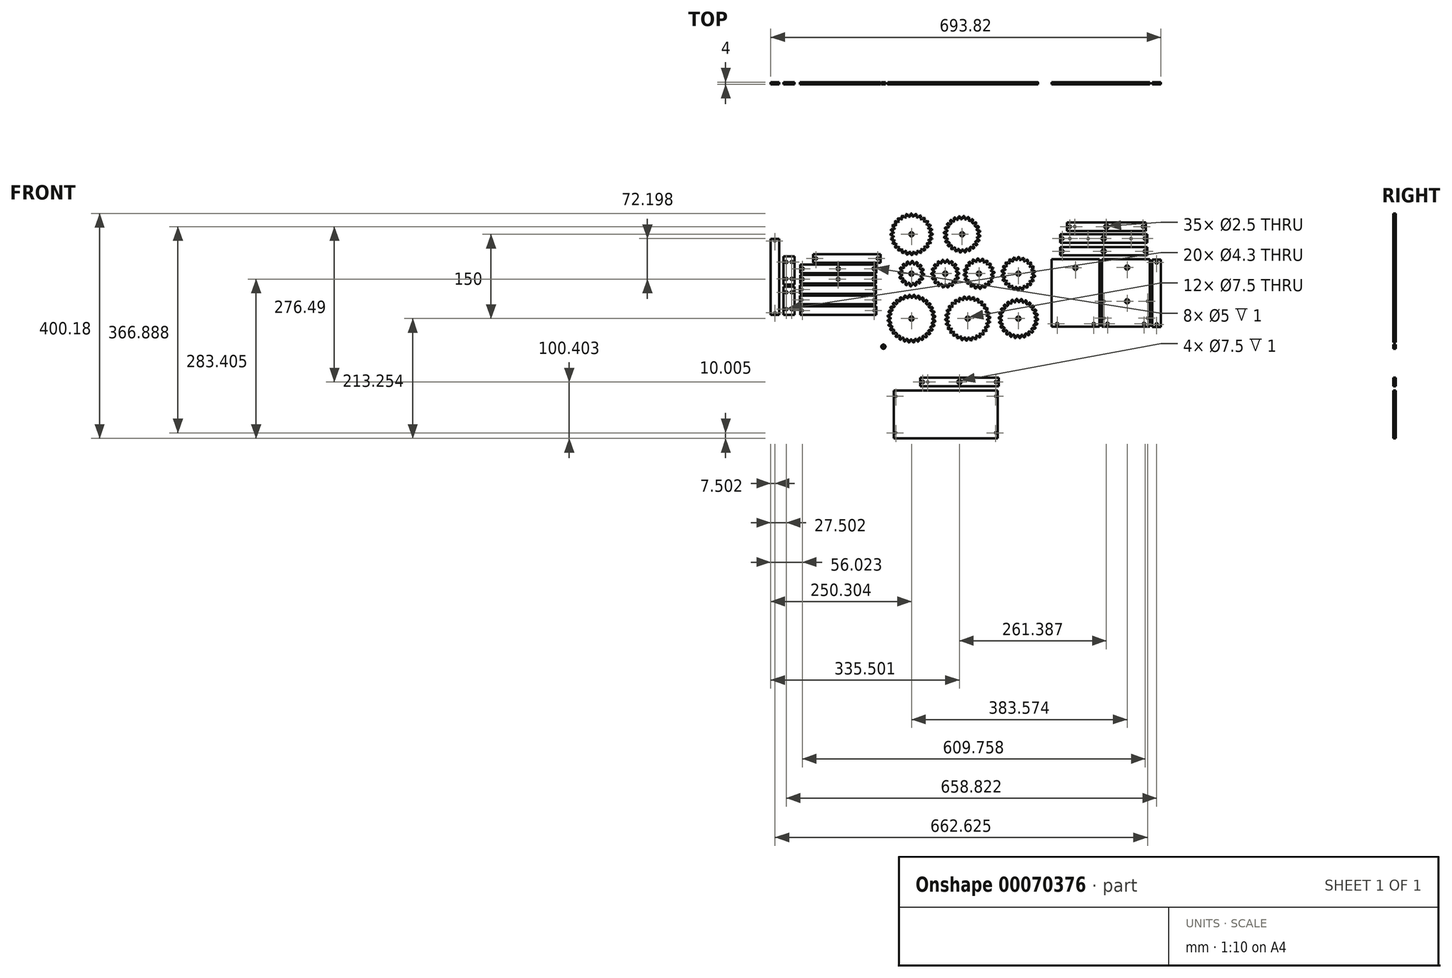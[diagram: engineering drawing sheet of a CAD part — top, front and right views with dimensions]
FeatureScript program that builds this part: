
annotation { "Feature Type Name" : "Feature", "Feature Type Description" : "" }
export const myFeature = defineFeature(function(context is Context, id is Id, definition is map)
    precondition{}
    {
        {
            var Q0;
            Q0=qCreatedBy(makeId("Front.planeOp"),FACE);
            var sketch = newSketch(context, id + "F0", { "sketchPlane" : qUnion([Q0])});
            skLineSegment(sketch, "E0", {"start": v(-125.86, -279.84) * mm, "end": v(59.14, -279.84) * mm});
            skLineSegment(sketch, "E1", {"start": v(59.14, -279.84) * mm, "end": v(59.14, -194.84) * mm});
            skLineSegment(sketch, "E2", {"start": v(59.14, -194.84) * mm, "end": v(-125.86, -194.84) * mm});
            skLineSegment(sketch, "E3", {"start": v(-125.86, -194.84) * mm, "end": v(-125.86, -279.84) * mm});
            skLineSegment(sketch, "E4", {"start": v(-79, -171.94) * mm, "end": v(-79, -186.94) * mm});
            skLineSegment(sketch, "E5", {"start": v(-79, -186.94) * mm, "end": v(61, -186.94) * mm});
            skLineSegment(sketch, "E6", {"start": v(61, -186.94) * mm, "end": v(61, -171.94) * mm});
            skLineSegment(sketch, "E7", {"start": v(61, -171.94) * mm, "end": v(-79, -171.94) * mm});
            skLineSegment(sketch, "E8", {"start": v(-122.1, -204.84) * mm, "end": v(-122.1, -269.84) * mm, "construction": true});
            skLineSegment(sketch, "E9", {"start": v(-122.1, -204.84) * mm, "end": v(55.4, -204.84) * mm, "construction": true});
            skLineSegment(sketch, "E10", {"start": v(55.4, -204.84) * mm, "end": v(55.4, -269.84) * mm, "construction": true});
            skLineSegment(sketch, "E11", {"start": v(55.4, -269.84) * mm, "end": v(-122.1, -269.84) * mm, "construction": true});
            skCircle(sketch, "E12", {"center": v(-122.1, -204.84) * mm, "radius": 1.25 * mm});
            skCircle(sketch, "E13", {"center": v(55.4, -204.84) * mm, "radius": 1.25 * mm});
            skCircle(sketch, "E14", {"center": v(-122.1, -269.84) * mm, "radius": 1.25 * mm});
            skCircle(sketch, "E15", {"center": v(55.4, -269.84) * mm, "radius": 1.25 * mm});
            skLineSegment(sketch, "E16", {"start": v(-74, -179.44) * mm, "end": v(-65.25, -179.44) * mm, "construction": true});
            skCircle(sketch, "E17", {"center": v(-74, -179.44) * mm, "radius": 2.15 * mm});
            skCircle(sketch, "E18", {"center": v(-65.25, -179.44) * mm, "radius": 1.25 * mm});
            skCircle(sketch, "E19", {"center": v(-9, -179.44) * mm, "radius": 1.25 * mm});
            skCircle(sketch, "E20", {"center": v(-9, -179.44) * mm, "radius": 3.75 * mm});
            skCircle(sketch, "E21", {"center": v(56, -179.44) * mm, "radius": 2.15 * mm});
            skLineSegment(sketch, "E22", {"start": v(-74, -179.44) * mm, "end": v(56, -179.44) * mm, "construction": true});
            skSolve(sketch);
        }
        {
            var Q0;
            Q0=makeQuery(id+"F0.imprint","IMPRINT",FACE,{"disambiguationData":[TD([[makeQuery(id+"F0.imprint","IMPRINT",EDGE,{"derivedFrom":sQuery(id+"F0.wireOp",EDGE,"E0")}),1.0]])]});
            var Q1;
            Q1=makeQuery(id+"F0.imprint","IMPRINT",FACE,{"disambiguationData":[TD([[makeQuery(id+"F0.imprint","IMPRINT",EDGE,{"derivedFrom":sQuery(id+"F0.wireOp",EDGE,"E4")}),1.0]])]});
            extrude(context, id + "F1", {"entities" : qUnion([Q0, Q1]), "depth" : 4 * mm});
        }
        {
            var Q0;
            Q0=makeQuery(id+"F0.imprint","IMPRINT",FACE,{"disambiguationData":[TD([[makeQuery(id+"F0.imprint","IMPRINT",EDGE,{"derivedFrom":sQuery(id+"F0.wireOp",EDGE,"E19")}),-1.0]])]});
            extrude(context, id + "F2", {"entities" : qUnion([Q0]), "operationType" : NewBodyOperationType.ADD, "depth" : 3 * mm});
        }
        {
            var Q0;
            Q0=qCreatedBy(makeId("Front.planeOp"),FACE);
            var sketch = newSketch(context, id + "F3", { "sketchPlane" : qUnion([Q0])});
            skLineSegment(sketch, "E23", {"start": v(-50.97, 12.48) * mm, "end": v(-50.97, 12.61) * mm});
            skLineSegment(sketch, "E24", {"start": v(-50.97, 12.61) * mm, "end": v(-50.98, 12.74) * mm});
            skLineSegment(sketch, "E25", {"start": v(-50.98, 12.74) * mm, "end": v(-50.99, 12.87) * mm});
            skLineSegment(sketch, "E26", {"start": v(-50.99, 12.87) * mm, "end": v(-51, 13) * mm});
            skLineSegment(sketch, "E27", {"start": v(-51, 13) * mm, "end": v(-51.02, 13.13) * mm});
            skLineSegment(sketch, "E28", {"start": v(-51.02, 13.13) * mm, "end": v(-51.05, 13.26) * mm});
            skLineSegment(sketch, "E29", {"start": v(-51.05, 13.26) * mm, "end": v(-51.08, 13.38) * mm});
            skLineSegment(sketch, "E30", {"start": v(-51.08, 13.38) * mm, "end": v(-51.1, 13.51) * mm});
            skLineSegment(sketch, "E31", {"start": v(-51.1, 13.51) * mm, "end": v(-51.15, 13.63) * mm});
            skLineSegment(sketch, "E32", {"start": v(-51.15, 13.63) * mm, "end": v(-51.19, 13.76) * mm});
            skLineSegment(sketch, "E33", {"start": v(-51.24, 13.88) * mm, "end": v(-51.29, 14) * mm});
            skLineSegment(sketch, "E34", {"start": v(-51.29, 14) * mm, "end": v(-51.34, 14.12) * mm});
            skLineSegment(sketch, "E35", {"start": v(-51.34, 14.12) * mm, "end": v(-51.4, 14.23) * mm});
            skLineSegment(sketch, "E36", {"start": v(-51.4, 14.23) * mm, "end": v(-51.46, 14.35) * mm});
            skLineSegment(sketch, "E37", {"start": v(-51.46, 14.35) * mm, "end": v(-51.53, 14.46) * mm});
            skLineSegment(sketch, "E38", {"start": v(-51.53, 14.46) * mm, "end": v(-51.6, 14.57) * mm});
            skLineSegment(sketch, "E39", {"start": v(-51.67, 14.68) * mm, "end": v(-51.75, 14.78) * mm});
            skLineSegment(sketch, "E40", {"start": v(-51.75, 14.78) * mm, "end": v(-51.83, 14.88) * mm});
            skLineSegment(sketch, "E41", {"start": v(-51.83, 14.88) * mm, "end": v(-51.92, 14.98) * mm});
            skLineSegment(sketch, "E42", {"start": v(-51.92, 14.98) * mm, "end": v(-52, 15.08) * mm});
            skLineSegment(sketch, "E43", {"start": v(-52, 15.08) * mm, "end": v(-52.1, 15.17) * mm});
            skLineSegment(sketch, "E44", {"start": v(-52.1, 15.17) * mm, "end": v(-52.2, 15.26) * mm});
            skLineSegment(sketch, "E45", {"start": v(-52.2, 15.26) * mm, "end": v(-52.3, 15.34) * mm});
            skLineSegment(sketch, "E46", {"start": v(-52.3, 15.34) * mm, "end": v(-52.4, 15.43) * mm});
            skLineSegment(sketch, "E47", {"start": v(-52.4, 15.43) * mm, "end": v(-52.5, 15.5) * mm});
            skLineSegment(sketch, "E48", {"start": v(-52.71, 15.65) * mm, "end": v(-52.82, 15.72) * mm});
            skLineSegment(sketch, "E49", {"start": v(-52.82, 15.72) * mm, "end": v(-52.94, 15.78) * mm});
            skLineSegment(sketch, "E50", {"start": v(-52.94, 15.78) * mm, "end": v(-53.05, 15.84) * mm});
            skLineSegment(sketch, "E51", {"start": v(-53.05, 15.84) * mm, "end": v(-53.17, 15.9) * mm});
            skLineSegment(sketch, "E52", {"start": v(-53.17, 15.9) * mm, "end": v(-53.29, 15.95) * mm});
            skLineSegment(sketch, "E53", {"start": v(-53.4, 16) * mm, "end": v(-53.53, 16.04) * mm});
            skLineSegment(sketch, "E54", {"start": v(-53.53, 16.04) * mm, "end": v(-53.66, 16.08) * mm});
            skLineSegment(sketch, "E55", {"start": v(-54.04, 16.17) * mm, "end": v(-54.16, 16.2) * mm});
            skLineSegment(sketch, "E56", {"start": v(-54.42, 16.22) * mm, "end": v(-54.55, 16.23) * mm});
            skLineSegment(sketch, "E57", {"start": v(-54.55, 16.23) * mm, "end": v(-54.68, 16.23) * mm});
            skLineSegment(sketch, "E58", {"start": v(-54.68, 16.23) * mm, "end": v(-54.81, 16.23) * mm});
            skLineSegment(sketch, "E59", {"start": v(-54.81, 16.23) * mm, "end": v(-54.94, 16.23) * mm});
            skLineSegment(sketch, "E60", {"start": v(-54.94, 16.23) * mm, "end": v(-55.07, 16.22) * mm});
            skLineSegment(sketch, "E61", {"start": v(-55.07, 16.22) * mm, "end": v(-55.2, 16.2) * mm});
            skLineSegment(sketch, "E62", {"start": v(-55.2, 16.2) * mm, "end": v(-55.33, 16.18) * mm});
            skLineSegment(sketch, "E63", {"start": v(-55.33, 16.18) * mm, "end": v(-55.46, 16.16) * mm});
            skLineSegment(sketch, "E64", {"start": v(-55.46, 16.16) * mm, "end": v(-55.59, 16.13) * mm});
            skLineSegment(sketch, "E65", {"start": v(-55.59, 16.13) * mm, "end": v(-55.71, 16.1) * mm});
            skLineSegment(sketch, "E66", {"start": v(-55.71, 16.1) * mm, "end": v(-55.84, 16.06) * mm});
            skLineSegment(sketch, "E67", {"start": v(-55.84, 16.06) * mm, "end": v(-55.96, 16.02) * mm});
            skLineSegment(sketch, "E68", {"start": v(-55.96, 16.02) * mm, "end": v(-56.08, 15.97) * mm});
            skLineSegment(sketch, "E69", {"start": v(-56.2, 15.92) * mm, "end": v(-56.32, 15.87) * mm});
            skLineSegment(sketch, "E70", {"start": v(-56.44, 15.81) * mm, "end": v(-56.55, 15.75) * mm});
            skLineSegment(sketch, "E71", {"start": v(-56.55, 15.75) * mm, "end": v(-56.67, 15.69) * mm});
            skLineSegment(sketch, "E72", {"start": v(-56.78, 15.62) * mm, "end": v(-56.88, 15.54) * mm});
            skLineSegment(sketch, "E73", {"start": v(-56.88, 15.54) * mm, "end": v(-56.99, 15.47) * mm});
            skLineSegment(sketch, "E74", {"start": v(-56.99, 15.47) * mm, "end": v(-57.1, 15.39) * mm});
            skLineSegment(sketch, "E75", {"start": v(-57.1, 15.39) * mm, "end": v(-57.19, 15.3) * mm});
            skLineSegment(sketch, "E76", {"start": v(-57.38, 15.12) * mm, "end": v(-57.47, 15.03) * mm});
            skLineSegment(sketch, "E77", {"start": v(-57.47, 15.03) * mm, "end": v(-57.56, 14.93) * mm});
            skLineSegment(sketch, "E78", {"start": v(-57.72, 14.73) * mm, "end": v(-57.8, 14.62) * mm});
            skLineSegment(sketch, "E79", {"start": v(-57.8, 14.62) * mm, "end": v(-57.87, 14.51) * mm});
            skLineSegment(sketch, "E80", {"start": v(-57.94, 14.4) * mm, "end": v(-58, 14.3) * mm});
            skLineSegment(sketch, "E81", {"start": v(-58, 14.3) * mm, "end": v(-58.06, 14.18) * mm});
            skLineSegment(sketch, "E82", {"start": v(-58.12, 14.06) * mm, "end": v(-58.17, 13.94) * mm});
            skLineSegment(sketch, "E83", {"start": v(-58.17, 13.94) * mm, "end": v(-58.22, 13.82) * mm});
            skLineSegment(sketch, "E84", {"start": v(-58.26, 13.7) * mm, "end": v(-58.3, 13.57) * mm});
            skLineSegment(sketch, "E85", {"start": v(-58.3, 13.57) * mm, "end": v(-58.34, 13.45) * mm});
            skLineSegment(sketch, "E86", {"start": v(-58.34, 13.45) * mm, "end": v(-58.37, 13.32) * mm});
            skLineSegment(sketch, "E87", {"start": v(-58.37, 13.32) * mm, "end": v(-58.4, 13.2) * mm});
            skLineSegment(sketch, "E88", {"start": v(-58.4, 13.2) * mm, "end": v(-58.42, 13.07) * mm});
            skLineSegment(sketch, "E89", {"start": v(-58.42, 13.07) * mm, "end": v(-58.44, 12.94) * mm});
            skLineSegment(sketch, "E90", {"start": v(-58.44, 12.94) * mm, "end": v(-58.45, 12.8) * mm});
            skLineSegment(sketch, "E91", {"start": v(-58.45, 12.8) * mm, "end": v(-58.46, 12.68) * mm});
            skLineSegment(sketch, "E92", {"start": v(-58.44, 12.03) * mm, "end": v(-58.42, 11.9) * mm});
            skLineSegment(sketch, "E93", {"start": v(-58.37, 11.64) * mm, "end": v(-58.34, 11.52) * mm});
            skLineSegment(sketch, "E94", {"start": v(-58.34, 11.52) * mm, "end": v(-58.3, 11.4) * mm});
            skLineSegment(sketch, "E95", {"start": v(-58.3, 11.4) * mm, "end": v(-58.26, 11.27) * mm});
            skLineSegment(sketch, "E96", {"start": v(-58.26, 11.27) * mm, "end": v(-58.22, 11.15) * mm});
            skLineSegment(sketch, "E97", {"start": v(-58.17, 11.02) * mm, "end": v(-58.12, 10.9) * mm});
            skLineSegment(sketch, "E98", {"start": v(-58.12, 10.9) * mm, "end": v(-58.06, 10.79) * mm});
            skLineSegment(sketch, "E99", {"start": v(-58.06, 10.79) * mm, "end": v(-58, 10.67) * mm});
            skLineSegment(sketch, "E100", {"start": v(-58, 10.67) * mm, "end": v(-57.94, 10.56) * mm});
            skLineSegment(sketch, "E101", {"start": v(-57.8, 10.34) * mm, "end": v(-57.72, 10.24) * mm});
            skLineSegment(sketch, "E102", {"start": v(-57.72, 10.24) * mm, "end": v(-57.64, 10.13) * mm});
            skLineSegment(sketch, "E103", {"start": v(-57.64, 10.13) * mm, "end": v(-57.56, 10.03) * mm});
            skLineSegment(sketch, "E104", {"start": v(-57.56, 10.03) * mm, "end": v(-57.47, 9.94) * mm});
            skLineSegment(sketch, "E105", {"start": v(-57.47, 9.94) * mm, "end": v(-57.38, 9.84) * mm});
            skLineSegment(sketch, "E106", {"start": v(-57.38, 9.84) * mm, "end": v(-57.29, 9.75) * mm});
            skLineSegment(sketch, "E107", {"start": v(-57.29, 9.75) * mm, "end": v(-57.19, 9.66) * mm});
            skLineSegment(sketch, "E108", {"start": v(-57.19, 9.66) * mm, "end": v(-57.1, 9.58) * mm});
            skLineSegment(sketch, "E109", {"start": v(-57.1, 9.58) * mm, "end": v(-56.99, 9.5) * mm});
            skLineSegment(sketch, "E110", {"start": v(-56.99, 9.5) * mm, "end": v(-56.88, 9.42) * mm});
            skLineSegment(sketch, "E111", {"start": v(-56.55, 9.21) * mm, "end": v(-56.44, 9.15) * mm});
            skLineSegment(sketch, "E112", {"start": v(-56.44, 9.15) * mm, "end": v(-56.32, 9.1) * mm});
            skLineSegment(sketch, "E113", {"start": v(-56.32, 9.1) * mm, "end": v(-56.2, 9.04) * mm});
            skLineSegment(sketch, "E114", {"start": v(-56.2, 9.04) * mm, "end": v(-56.08, 9) * mm});
            skLineSegment(sketch, "E115", {"start": v(-55.96, 8.95) * mm, "end": v(-55.84, 8.9) * mm});
            skLineSegment(sketch, "E116", {"start": v(-55.71, 8.87) * mm, "end": v(-55.59, 8.83) * mm});
            skLineSegment(sketch, "E117", {"start": v(-55.59, 8.83) * mm, "end": v(-55.46, 8.8) * mm});
            skLineSegment(sketch, "E118", {"start": v(-55.46, 8.8) * mm, "end": v(-55.33, 8.78) * mm});
            skLineSegment(sketch, "E119", {"start": v(-55.33, 8.78) * mm, "end": v(-55.2, 8.76) * mm});
            skLineSegment(sketch, "E120", {"start": v(-55.2, 8.76) * mm, "end": v(-55.07, 8.75) * mm});
            skLineSegment(sketch, "E121", {"start": v(-55.07, 8.75) * mm, "end": v(-54.94, 8.74) * mm});
            skLineSegment(sketch, "E122", {"start": v(-54.94, 8.74) * mm, "end": v(-54.81, 8.73) * mm});
            skLineSegment(sketch, "E123", {"start": v(-54.81, 8.73) * mm, "end": v(-54.68, 8.73) * mm});
            skLineSegment(sketch, "E124", {"start": v(-54.68, 8.73) * mm, "end": v(-54.55, 8.74) * mm});
            skLineSegment(sketch, "E125", {"start": v(-54.55, 8.74) * mm, "end": v(-54.42, 8.74) * mm});
            skLineSegment(sketch, "E126", {"start": v(-54.16, 8.77) * mm, "end": v(-54.04, 8.8) * mm});
            skLineSegment(sketch, "E127", {"start": v(-53.9, 8.82) * mm, "end": v(-53.78, 8.85) * mm});
            skLineSegment(sketch, "E128", {"start": v(-53.78, 8.85) * mm, "end": v(-53.66, 8.89) * mm});
            skLineSegment(sketch, "E129", {"start": v(-53.66, 8.89) * mm, "end": v(-53.53, 8.92) * mm});
            skLineSegment(sketch, "E130", {"start": v(-52.82, 9.25) * mm, "end": v(-52.71, 9.31) * mm});
            skLineSegment(sketch, "E131", {"start": v(-52.71, 9.31) * mm, "end": v(-52.6, 9.38) * mm});
            skLineSegment(sketch, "E132", {"start": v(-52.6, 9.38) * mm, "end": v(-52.5, 9.46) * mm});
            skLineSegment(sketch, "E133", {"start": v(-52.5, 9.46) * mm, "end": v(-52.4, 9.54) * mm});
            skLineSegment(sketch, "E134", {"start": v(-52.4, 9.54) * mm, "end": v(-52.3, 9.62) * mm});
            skLineSegment(sketch, "E135", {"start": v(-52.2, 9.7) * mm, "end": v(-52.1, 9.8) * mm});
            skLineSegment(sketch, "E136", {"start": v(-52.1, 9.8) * mm, "end": v(-52, 9.89) * mm});
            skLineSegment(sketch, "E137", {"start": v(-51.92, 9.98) * mm, "end": v(-51.83, 10.08) * mm});
            skLineSegment(sketch, "E138", {"start": v(-51.83, 10.08) * mm, "end": v(-51.75, 10.18) * mm});
            skLineSegment(sketch, "E139", {"start": v(-51.67, 10.29) * mm, "end": v(-51.6, 10.4) * mm});
            skLineSegment(sketch, "E140", {"start": v(-51.6, 10.4) * mm, "end": v(-51.53, 10.5) * mm});
            skLineSegment(sketch, "E141", {"start": v(-51.53, 10.5) * mm, "end": v(-51.46, 10.62) * mm});
            skLineSegment(sketch, "E142", {"start": v(-51.46, 10.62) * mm, "end": v(-51.4, 10.73) * mm});
            skLineSegment(sketch, "E143", {"start": v(-51.4, 10.73) * mm, "end": v(-51.34, 10.85) * mm});
            skLineSegment(sketch, "E144", {"start": v(-51.34, 10.85) * mm, "end": v(-51.29, 10.97) * mm});
            skLineSegment(sketch, "E145", {"start": v(-51.29, 10.97) * mm, "end": v(-51.24, 11.08) * mm});
            skLineSegment(sketch, "E146", {"start": v(-51.24, 11.08) * mm, "end": v(-51.19, 11.2) * mm});
            skLineSegment(sketch, "E147", {"start": v(-51.19, 11.2) * mm, "end": v(-51.15, 11.33) * mm});
            skLineSegment(sketch, "E148", {"start": v(-51.15, 11.33) * mm, "end": v(-51.1, 11.45) * mm});
            skLineSegment(sketch, "E149", {"start": v(-51.05, 11.7) * mm, "end": v(-51.02, 11.83) * mm});
            skLineSegment(sketch, "E150", {"start": v(-51.02, 11.83) * mm, "end": v(-51, 11.96) * mm});
            skLineSegment(sketch, "E151", {"start": v(-50.99, 12.1) * mm, "end": v(-50.98, 12.22) * mm});
            skLineSegment(sketch, "E152", {"start": v(-50.98, 12.22) * mm, "end": v(-50.97, 12.35) * mm});
            skLineSegment(sketch, "E153", {"start": v(-20.07, -87.52) * mm, "end": v(-20.07, -87.44) * mm});
            skLineSegment(sketch, "E154", {"start": v(-20.07, -87.44) * mm, "end": v(-20.07, -87.37) * mm});
            skLineSegment(sketch, "E155", {"start": v(-20.07, -87.37) * mm, "end": v(-20.08, -87.3) * mm});
            skLineSegment(sketch, "E156", {"start": v(-20.08, -87.3) * mm, "end": v(-20.09, -87.22) * mm});
            skLineSegment(sketch, "E157", {"start": v(-20.09, -87.22) * mm, "end": v(-20.1, -87.15) * mm});
            skLineSegment(sketch, "E158", {"start": v(-20.1, -87.15) * mm, "end": v(-20.11, -87.07) * mm});
            skLineSegment(sketch, "E159", {"start": v(-20.11, -87.07) * mm, "end": v(-20.13, -87) * mm});
            skLineSegment(sketch, "E160", {"start": v(-20.13, -87) * mm, "end": v(-20.15, -86.93) * mm});
            skLineSegment(sketch, "E161", {"start": v(-20.15, -86.93) * mm, "end": v(-20.17, -86.86) * mm});
            skLineSegment(sketch, "E162", {"start": v(-20.2, -86.79) * mm, "end": v(-20.22, -86.72) * mm});
            skLineSegment(sketch, "E163", {"start": v(-20.22, -86.72) * mm, "end": v(-20.25, -86.65) * mm});
            skLineSegment(sketch, "E164", {"start": v(-20.28, -86.58) * mm, "end": v(-20.32, -86.51) * mm});
            skLineSegment(sketch, "E165", {"start": v(-20.32, -86.51) * mm, "end": v(-20.35, -86.45) * mm});
            skLineSegment(sketch, "E166", {"start": v(-20.35, -86.45) * mm, "end": v(-20.39, -86.38) * mm});
            skLineSegment(sketch, "E167", {"start": v(-20.39, -86.38) * mm, "end": v(-20.43, -86.32) * mm});
            skLineSegment(sketch, "E168", {"start": v(-20.43, -86.32) * mm, "end": v(-20.47, -86.26) * mm});
            skLineSegment(sketch, "E169", {"start": v(-20.52, -86.2) * mm, "end": v(-20.56, -86.14) * mm});
            skLineSegment(sketch, "E170", {"start": v(-20.56, -86.14) * mm, "end": v(-20.61, -86.09) * mm});
            skLineSegment(sketch, "E171", {"start": v(-20.61, -86.09) * mm, "end": v(-20.66, -86.03) * mm});
            skLineSegment(sketch, "E172", {"start": v(-20.66, -86.03) * mm, "end": v(-20.72, -85.98) * mm});
            skLineSegment(sketch, "E173", {"start": v(-20.72, -85.98) * mm, "end": v(-20.77, -85.93) * mm});
            skLineSegment(sketch, "E174", {"start": v(-20.83, -85.88) * mm, "end": v(-20.88, -85.83) * mm});
            skLineSegment(sketch, "E175", {"start": v(-20.88, -85.83) * mm, "end": v(-20.94, -85.78) * mm});
            skLineSegment(sketch, "E176", {"start": v(-20.94, -85.78) * mm, "end": v(-21, -85.74) * mm});
            skLineSegment(sketch, "E177", {"start": v(-21, -85.74) * mm, "end": v(-21.07, -85.7) * mm});
            skLineSegment(sketch, "E178", {"start": v(-21.07, -85.7) * mm, "end": v(-21.13, -85.66) * mm});
            skLineSegment(sketch, "E179", {"start": v(-21.13, -85.66) * mm, "end": v(-21.2, -85.63) * mm});
            skLineSegment(sketch, "E180", {"start": v(-21.2, -85.63) * mm, "end": v(-21.26, -85.6) * mm});
            skLineSegment(sketch, "E181", {"start": v(-21.26, -85.6) * mm, "end": v(-21.33, -85.56) * mm});
            skLineSegment(sketch, "E182", {"start": v(-21.4, -85.53) * mm, "end": v(-21.47, -85.5) * mm});
            skLineSegment(sketch, "E183", {"start": v(-21.47, -85.5) * mm, "end": v(-21.54, -85.48) * mm});
            skLineSegment(sketch, "E184", {"start": v(-21.54, -85.48) * mm, "end": v(-21.6, -85.46) * mm});
            skLineSegment(sketch, "E185", {"start": v(-21.6, -85.46) * mm, "end": v(-21.68, -85.44) * mm});
            skLineSegment(sketch, "E186", {"start": v(-21.68, -85.44) * mm, "end": v(-21.75, -85.42) * mm});
            skLineSegment(sketch, "E187", {"start": v(-21.75, -85.42) * mm, "end": v(-21.83, -85.4) * mm});
            skLineSegment(sketch, "E188", {"start": v(-21.83, -85.4) * mm, "end": v(-21.9, -85.4) * mm});
            skLineSegment(sketch, "E189", {"start": v(-21.9, -85.4) * mm, "end": v(-21.97, -85.38) * mm});
            skLineSegment(sketch, "E190", {"start": v(-21.97, -85.38) * mm, "end": v(-22.05, -85.37) * mm});
            skLineSegment(sketch, "E191", {"start": v(-22.05, -85.37) * mm, "end": v(-22.12, -85.37) * mm});
            skLineSegment(sketch, "E192", {"start": v(-22.12, -85.37) * mm, "end": v(-22.2, -85.37) * mm});
            skLineSegment(sketch, "E193", {"start": v(-22.2, -85.37) * mm, "end": v(-22.27, -85.37) * mm});
            skLineSegment(sketch, "E194", {"start": v(-22.27, -85.37) * mm, "end": v(-22.35, -85.37) * mm});
            skLineSegment(sketch, "E195", {"start": v(-22.35, -85.37) * mm, "end": v(-22.42, -85.38) * mm});
            skLineSegment(sketch, "E196", {"start": v(-22.42, -85.38) * mm, "end": v(-22.5, -85.39) * mm});
            skLineSegment(sketch, "E197", {"start": v(-22.5, -85.39) * mm, "end": v(-22.57, -85.4) * mm});
            skLineSegment(sketch, "E198", {"start": v(-22.64, -85.41) * mm, "end": v(-22.72, -85.43) * mm});
            skLineSegment(sketch, "E199", {"start": v(-22.72, -85.43) * mm, "end": v(-22.79, -85.44) * mm});
            skLineSegment(sketch, "E200", {"start": v(-22.79, -85.44) * mm, "end": v(-22.86, -85.47) * mm});
            skLineSegment(sketch, "E201", {"start": v(-23, -85.52) * mm, "end": v(-23.07, -85.54) * mm});
            skLineSegment(sketch, "E202", {"start": v(-23.2, -85.6) * mm, "end": v(-23.27, -85.64) * mm});
            skLineSegment(sketch, "E203", {"start": v(-23.27, -85.64) * mm, "end": v(-23.33, -85.68) * mm});
            skLineSegment(sketch, "E204", {"start": v(-23.33, -85.68) * mm, "end": v(-23.4, -85.72) * mm});
            skLineSegment(sketch, "E205", {"start": v(-23.4, -85.72) * mm, "end": v(-23.46, -85.76) * mm});
            skLineSegment(sketch, "E206", {"start": v(-23.46, -85.76) * mm, "end": v(-23.52, -85.8) * mm});
            skLineSegment(sketch, "E207", {"start": v(-23.52, -85.8) * mm, "end": v(-23.58, -85.85) * mm});
            skLineSegment(sketch, "E208", {"start": v(-23.58, -85.85) * mm, "end": v(-23.63, -85.9) * mm});
            skLineSegment(sketch, "E209", {"start": v(-23.63, -85.9) * mm, "end": v(-23.69, -85.95) * mm});
            skLineSegment(sketch, "E210", {"start": v(-23.69, -85.95) * mm, "end": v(-23.74, -86) * mm});
            skLineSegment(sketch, "E211", {"start": v(-23.74, -86) * mm, "end": v(-23.8, -86.06) * mm});
            skLineSegment(sketch, "E212", {"start": v(-23.8, -86.06) * mm, "end": v(-23.84, -86.11) * mm});
            skLineSegment(sketch, "E213", {"start": v(-23.84, -86.11) * mm, "end": v(-23.9, -86.17) * mm});
            skLineSegment(sketch, "E214", {"start": v(-23.9, -86.17) * mm, "end": v(-23.94, -86.23) * mm});
            skLineSegment(sketch, "E215", {"start": v(-23.94, -86.23) * mm, "end": v(-23.98, -86.3) * mm});
            skLineSegment(sketch, "E216", {"start": v(-23.98, -86.3) * mm, "end": v(-24.02, -86.35) * mm});
            skLineSegment(sketch, "E217", {"start": v(-24.02, -86.35) * mm, "end": v(-24.06, -86.42) * mm});
            skLineSegment(sketch, "E218", {"start": v(-24.1, -86.48) * mm, "end": v(-24.13, -86.55) * mm});
            skLineSegment(sketch, "E219", {"start": v(-24.17, -86.61) * mm, "end": v(-24.2, -86.68) * mm});
            skLineSegment(sketch, "E220", {"start": v(-24.2, -86.68) * mm, "end": v(-24.22, -86.75) * mm});
            skLineSegment(sketch, "E221", {"start": v(-24.22, -86.75) * mm, "end": v(-24.25, -86.82) * mm});
            skLineSegment(sketch, "E222", {"start": v(-24.25, -86.82) * mm, "end": v(-24.27, -86.9) * mm});
            skLineSegment(sketch, "E223", {"start": v(-24.27, -86.9) * mm, "end": v(-24.3, -86.96) * mm});
            skLineSegment(sketch, "E224", {"start": v(-24.3, -86.96) * mm, "end": v(-24.31, -87.04) * mm});
            skLineSegment(sketch, "E225", {"start": v(-24.31, -87.04) * mm, "end": v(-24.33, -87.1) * mm});
            skLineSegment(sketch, "E226", {"start": v(-24.33, -87.1) * mm, "end": v(-24.34, -87.18) * mm});
            skLineSegment(sketch, "E227", {"start": v(-24.34, -87.18) * mm, "end": v(-24.35, -87.26) * mm});
            skLineSegment(sketch, "E228", {"start": v(-24.35, -87.26) * mm, "end": v(-24.36, -87.33) * mm});
            skLineSegment(sketch, "E229", {"start": v(-24.36, -87.33) * mm, "end": v(-24.36, -87.4) * mm});
            skLineSegment(sketch, "E230", {"start": v(-24.36, -87.4) * mm, "end": v(-24.37, -87.48) * mm});
            skLineSegment(sketch, "E231", {"start": v(-24.37, -87.48) * mm, "end": v(-24.37, -87.55) * mm});
            skLineSegment(sketch, "E232", {"start": v(-24.37, -87.55) * mm, "end": v(-24.36, -87.63) * mm});
            skLineSegment(sketch, "E233", {"start": v(-24.36, -87.63) * mm, "end": v(-24.36, -87.7) * mm});
            skLineSegment(sketch, "E234", {"start": v(-24.36, -87.7) * mm, "end": v(-24.35, -87.78) * mm});
            skLineSegment(sketch, "E235", {"start": v(-24.22, -88.28) * mm, "end": v(-24.2, -88.35) * mm});
            skLineSegment(sketch, "E236", {"start": v(-24.2, -88.35) * mm, "end": v(-24.17, -88.42) * mm});
            skLineSegment(sketch, "E237", {"start": v(-24.17, -88.42) * mm, "end": v(-24.13, -88.49) * mm});
            skLineSegment(sketch, "E238", {"start": v(-24.13, -88.49) * mm, "end": v(-24.1, -88.55) * mm});
            skLineSegment(sketch, "E239", {"start": v(-24.1, -88.55) * mm, "end": v(-24.06, -88.62) * mm});
            skLineSegment(sketch, "E240", {"start": v(-24.06, -88.62) * mm, "end": v(-24.02, -88.68) * mm});
            skLineSegment(sketch, "E241", {"start": v(-23.94, -88.8) * mm, "end": v(-23.9, -88.86) * mm});
            skLineSegment(sketch, "E242", {"start": v(-23.9, -88.86) * mm, "end": v(-23.84, -88.92) * mm});
            skLineSegment(sketch, "E243", {"start": v(-23.84, -88.92) * mm, "end": v(-23.8, -88.98) * mm});
            skLineSegment(sketch, "E244", {"start": v(-23.8, -88.98) * mm, "end": v(-23.74, -89.03) * mm});
            skLineSegment(sketch, "E245", {"start": v(-23.74, -89.03) * mm, "end": v(-23.69, -89.08) * mm});
            skLineSegment(sketch, "E246", {"start": v(-23.69, -89.08) * mm, "end": v(-23.63, -89.13) * mm});
            skLineSegment(sketch, "E247", {"start": v(-23.58, -89.18) * mm, "end": v(-23.52, -89.23) * mm});
            skLineSegment(sketch, "E248", {"start": v(-23.52, -89.23) * mm, "end": v(-23.46, -89.27) * mm});
            skLineSegment(sketch, "E249", {"start": v(-23.46, -89.27) * mm, "end": v(-23.4, -89.31) * mm});
            skLineSegment(sketch, "E250", {"start": v(-23.4, -89.31) * mm, "end": v(-23.33, -89.35) * mm});
            skLineSegment(sketch, "E251", {"start": v(-23.33, -89.35) * mm, "end": v(-23.27, -89.4) * mm});
            skLineSegment(sketch, "E252", {"start": v(-23.14, -89.46) * mm, "end": v(-23.07, -89.5) * mm});
            skLineSegment(sketch, "E253", {"start": v(-23.07, -89.5) * mm, "end": v(-23, -89.52) * mm});
            skLineSegment(sketch, "E254", {"start": v(-23, -89.52) * mm, "end": v(-22.93, -89.55) * mm});
            skLineSegment(sketch, "E255", {"start": v(-22.93, -89.55) * mm, "end": v(-22.86, -89.57) * mm});
            skLineSegment(sketch, "E256", {"start": v(-22.86, -89.57) * mm, "end": v(-22.79, -89.6) * mm});
            skLineSegment(sketch, "E257", {"start": v(-22.72, -89.6) * mm, "end": v(-22.64, -89.62) * mm});
            skLineSegment(sketch, "E258", {"start": v(-22.64, -89.62) * mm, "end": v(-22.57, -89.64) * mm});
            skLineSegment(sketch, "E259", {"start": v(-22.5, -89.65) * mm, "end": v(-22.42, -89.66) * mm});
            skLineSegment(sketch, "E260", {"start": v(-22.42, -89.66) * mm, "end": v(-22.35, -89.66) * mm});
            skLineSegment(sketch, "E261", {"start": v(-22.35, -89.66) * mm, "end": v(-22.27, -89.67) * mm});
            skLineSegment(sketch, "E262", {"start": v(-22.27, -89.67) * mm, "end": v(-22.2, -89.67) * mm});
            skLineSegment(sketch, "E263", {"start": v(-22.2, -89.67) * mm, "end": v(-22.12, -89.67) * mm});
            skLineSegment(sketch, "E264", {"start": v(-22.12, -89.67) * mm, "end": v(-22.05, -89.66) * mm});
            skLineSegment(sketch, "E265", {"start": v(-22.05, -89.66) * mm, "end": v(-21.97, -89.65) * mm});
            skLineSegment(sketch, "E266", {"start": v(-21.97, -89.65) * mm, "end": v(-21.9, -89.64) * mm});
            skLineSegment(sketch, "E267", {"start": v(-21.9, -89.64) * mm, "end": v(-21.83, -89.63) * mm});
            skLineSegment(sketch, "E268", {"start": v(-21.83, -89.63) * mm, "end": v(-21.75, -89.62) * mm});
            skLineSegment(sketch, "E269", {"start": v(-21.75, -89.62) * mm, "end": v(-21.68, -89.6) * mm});
            skLineSegment(sketch, "E270", {"start": v(-21.68, -89.6) * mm, "end": v(-21.6, -89.58) * mm});
            skLineSegment(sketch, "E271", {"start": v(-21.54, -89.56) * mm, "end": v(-21.47, -89.53) * mm});
            skLineSegment(sketch, "E272", {"start": v(-21.47, -89.53) * mm, "end": v(-21.4, -89.5) * mm});
            skLineSegment(sketch, "E273", {"start": v(-21.4, -89.5) * mm, "end": v(-21.33, -89.48) * mm});
            skLineSegment(sketch, "E274", {"start": v(-21.33, -89.48) * mm, "end": v(-21.26, -89.44) * mm});
            skLineSegment(sketch, "E275", {"start": v(-21.26, -89.44) * mm, "end": v(-21.2, -89.4) * mm});
            skLineSegment(sketch, "E276", {"start": v(-21.13, -89.37) * mm, "end": v(-21.07, -89.33) * mm});
            skLineSegment(sketch, "E277", {"start": v(-21.07, -89.33) * mm, "end": v(-21, -89.3) * mm});
            skLineSegment(sketch, "E278", {"start": v(-21, -89.3) * mm, "end": v(-20.94, -89.25) * mm});
            skLineSegment(sketch, "E279", {"start": v(-20.94, -89.25) * mm, "end": v(-20.88, -89.2) * mm});
            skLineSegment(sketch, "E280", {"start": v(-20.88, -89.2) * mm, "end": v(-20.83, -89.16) * mm});
            skLineSegment(sketch, "E281", {"start": v(-20.83, -89.16) * mm, "end": v(-20.77, -89.1) * mm});
            skLineSegment(sketch, "E282", {"start": v(-20.77, -89.1) * mm, "end": v(-20.72, -89.06) * mm});
            skLineSegment(sketch, "E283", {"start": v(-20.72, -89.06) * mm, "end": v(-20.66, -89) * mm});
            skLineSegment(sketch, "E284", {"start": v(-20.66, -89) * mm, "end": v(-20.61, -88.95) * mm});
            skLineSegment(sketch, "E285", {"start": v(-20.61, -88.95) * mm, "end": v(-20.56, -88.9) * mm});
            skLineSegment(sketch, "E286", {"start": v(-20.56, -88.9) * mm, "end": v(-20.52, -88.84) * mm});
            skLineSegment(sketch, "E287", {"start": v(-20.52, -88.84) * mm, "end": v(-20.47, -88.78) * mm});
            skLineSegment(sketch, "E288", {"start": v(-20.47, -88.78) * mm, "end": v(-20.43, -88.71) * mm});
            skLineSegment(sketch, "E289", {"start": v(-20.43, -88.71) * mm, "end": v(-20.39, -88.65) * mm});
            skLineSegment(sketch, "E290", {"start": v(-20.17, -88.18) * mm, "end": v(-20.15, -88.1) * mm});
            skLineSegment(sketch, "E291", {"start": v(-20.15, -88.1) * mm, "end": v(-20.13, -88.03) * mm});
            skLineSegment(sketch, "E292", {"start": v(-20.11, -87.96) * mm, "end": v(-20.1, -87.89) * mm});
            skLineSegment(sketch, "E293", {"start": v(-20.1, -87.89) * mm, "end": v(-20.09, -87.82) * mm});
            skLineSegment(sketch, "E294", {"start": v(-20.08, -87.74) * mm, "end": v(-20.07, -87.67) * mm});
            skLineSegment(sketch, "E295", {"start": v(-20.07, -87.67) * mm, "end": v(-20.07, -87.6) * mm});
            skLineSegment(sketch, "E296", {"start": v(-20.07, -87.6) * mm, "end": v(-20.07, -87.52) * mm});
            skLineSegment(sketch, "E297", {"start": v(-85.07, -87.52) * mm, "end": v(-85.07, -87.44) * mm});
            skLineSegment(sketch, "E298", {"start": v(-85.07, -87.44) * mm, "end": v(-85.07, -87.37) * mm});
            skLineSegment(sketch, "E299", {"start": v(-85.07, -87.37) * mm, "end": v(-85.08, -87.3) * mm});
            skLineSegment(sketch, "E300", {"start": v(-85.08, -87.3) * mm, "end": v(-85.09, -87.22) * mm});
            skLineSegment(sketch, "E301", {"start": v(-85.09, -87.22) * mm, "end": v(-85.1, -87.15) * mm});
            skLineSegment(sketch, "E302", {"start": v(-85.1, -87.15) * mm, "end": v(-85.11, -87.07) * mm});
            skLineSegment(sketch, "E303", {"start": v(-85.11, -87.07) * mm, "end": v(-85.13, -87) * mm});
            skLineSegment(sketch, "E304", {"start": v(-85.13, -87) * mm, "end": v(-85.15, -86.93) * mm});
            skLineSegment(sketch, "E305", {"start": v(-85.15, -86.93) * mm, "end": v(-85.17, -86.86) * mm});
            skLineSegment(sketch, "E306", {"start": v(-85.17, -86.86) * mm, "end": v(-85.2, -86.79) * mm});
            skLineSegment(sketch, "E307", {"start": v(-85.2, -86.79) * mm, "end": v(-85.22, -86.72) * mm});
            skLineSegment(sketch, "E308", {"start": v(-85.22, -86.72) * mm, "end": v(-85.25, -86.65) * mm});
            skLineSegment(sketch, "E309", {"start": v(-85.25, -86.65) * mm, "end": v(-85.28, -86.58) * mm});
            skLineSegment(sketch, "E310", {"start": v(-85.28, -86.58) * mm, "end": v(-85.32, -86.51) * mm});
            skLineSegment(sketch, "E311", {"start": v(-85.32, -86.51) * mm, "end": v(-85.35, -86.45) * mm});
            skLineSegment(sketch, "E312", {"start": v(-85.35, -86.45) * mm, "end": v(-85.39, -86.38) * mm});
            skLineSegment(sketch, "E313", {"start": v(-85.39, -86.38) * mm, "end": v(-85.43, -86.32) * mm});
            skLineSegment(sketch, "E314", {"start": v(-85.43, -86.32) * mm, "end": v(-85.47, -86.26) * mm});
            skLineSegment(sketch, "E315", {"start": v(-85.47, -86.26) * mm, "end": v(-85.52, -86.2) * mm});
            skLineSegment(sketch, "E316", {"start": v(-85.52, -86.2) * mm, "end": v(-85.56, -86.14) * mm});
            skLineSegment(sketch, "E317", {"start": v(-85.61, -86.09) * mm, "end": v(-85.66, -86.03) * mm});
            skLineSegment(sketch, "E318", {"start": v(-85.72, -85.98) * mm, "end": v(-85.77, -85.93) * mm});
            skLineSegment(sketch, "E319", {"start": v(-85.77, -85.93) * mm, "end": v(-85.83, -85.88) * mm});
            skLineSegment(sketch, "E320", {"start": v(-85.83, -85.88) * mm, "end": v(-85.88, -85.83) * mm});
            skLineSegment(sketch, "E321", {"start": v(-85.88, -85.83) * mm, "end": v(-85.94, -85.78) * mm});
            skLineSegment(sketch, "E322", {"start": v(-85.94, -85.78) * mm, "end": v(-86, -85.74) * mm});
            skLineSegment(sketch, "E323", {"start": v(-86, -85.74) * mm, "end": v(-86.07, -85.7) * mm});
            skLineSegment(sketch, "E324", {"start": v(-86.13, -85.66) * mm, "end": v(-86.2, -85.63) * mm});
            skLineSegment(sketch, "E325", {"start": v(-86.2, -85.63) * mm, "end": v(-86.26, -85.6) * mm});
            skLineSegment(sketch, "E326", {"start": v(-86.26, -85.6) * mm, "end": v(-86.33, -85.56) * mm});
            skLineSegment(sketch, "E327", {"start": v(-86.33, -85.56) * mm, "end": v(-86.4, -85.53) * mm});
            skLineSegment(sketch, "E328", {"start": v(-86.4, -85.53) * mm, "end": v(-86.47, -85.5) * mm});
            skLineSegment(sketch, "E329", {"start": v(-86.47, -85.5) * mm, "end": v(-86.54, -85.48) * mm});
            skLineSegment(sketch, "E330", {"start": v(-86.54, -85.48) * mm, "end": v(-86.6, -85.46) * mm});
            skLineSegment(sketch, "E331", {"start": v(-86.6, -85.46) * mm, "end": v(-86.68, -85.44) * mm});
            skLineSegment(sketch, "E332", {"start": v(-86.9, -85.4) * mm, "end": v(-86.97, -85.38) * mm});
            skLineSegment(sketch, "E333", {"start": v(-86.97, -85.38) * mm, "end": v(-87.05, -85.37) * mm});
            skLineSegment(sketch, "E334", {"start": v(-87.05, -85.37) * mm, "end": v(-87.12, -85.37) * mm});
            skLineSegment(sketch, "E335", {"start": v(-87.12, -85.37) * mm, "end": v(-87.2, -85.37) * mm});
            skLineSegment(sketch, "E336", {"start": v(-87.2, -85.37) * mm, "end": v(-87.27, -85.37) * mm});
            skLineSegment(sketch, "E337", {"start": v(-87.42, -85.38) * mm, "end": v(-87.5, -85.39) * mm});
            skLineSegment(sketch, "E338", {"start": v(-87.5, -85.39) * mm, "end": v(-87.57, -85.4) * mm});
            skLineSegment(sketch, "E339", {"start": v(-87.57, -85.4) * mm, "end": v(-87.64, -85.41) * mm});
            skLineSegment(sketch, "E340", {"start": v(-87.64, -85.41) * mm, "end": v(-87.72, -85.43) * mm});
            skLineSegment(sketch, "E341", {"start": v(-87.72, -85.43) * mm, "end": v(-87.79, -85.44) * mm});
            skLineSegment(sketch, "E342", {"start": v(-87.86, -85.47) * mm, "end": v(-87.93, -85.49) * mm});
            skLineSegment(sketch, "E343", {"start": v(-87.93, -85.49) * mm, "end": v(-88, -85.52) * mm});
            skLineSegment(sketch, "E344", {"start": v(-88, -85.52) * mm, "end": v(-88.07, -85.54) * mm});
            skLineSegment(sketch, "E345", {"start": v(-88.07, -85.54) * mm, "end": v(-88.14, -85.57) * mm});
            skLineSegment(sketch, "E346", {"start": v(-88.14, -85.57) * mm, "end": v(-88.2, -85.6) * mm});
            skLineSegment(sketch, "E347", {"start": v(-88.2, -85.6) * mm, "end": v(-88.27, -85.64) * mm});
            skLineSegment(sketch, "E348", {"start": v(-88.27, -85.64) * mm, "end": v(-88.33, -85.68) * mm});
            skLineSegment(sketch, "E349", {"start": v(-88.33, -85.68) * mm, "end": v(-88.4, -85.72) * mm});
            skLineSegment(sketch, "E350", {"start": v(-88.4, -85.72) * mm, "end": v(-88.46, -85.76) * mm});
            skLineSegment(sketch, "E351", {"start": v(-88.46, -85.76) * mm, "end": v(-88.52, -85.8) * mm});
            skLineSegment(sketch, "E352", {"start": v(-88.52, -85.8) * mm, "end": v(-88.58, -85.85) * mm});
            skLineSegment(sketch, "E353", {"start": v(-88.58, -85.85) * mm, "end": v(-88.63, -85.9) * mm});
            skLineSegment(sketch, "E354", {"start": v(-88.63, -85.9) * mm, "end": v(-88.69, -85.95) * mm});
            skLineSegment(sketch, "E355", {"start": v(-88.69, -85.95) * mm, "end": v(-88.74, -86) * mm});
            skLineSegment(sketch, "E356", {"start": v(-88.74, -86) * mm, "end": v(-88.8, -86.06) * mm});
            skLineSegment(sketch, "E357", {"start": v(-88.8, -86.06) * mm, "end": v(-88.84, -86.11) * mm});
            skLineSegment(sketch, "E358", {"start": v(-88.84, -86.11) * mm, "end": v(-88.9, -86.17) * mm});
            skLineSegment(sketch, "E359", {"start": v(-88.9, -86.17) * mm, "end": v(-88.94, -86.23) * mm});
            skLineSegment(sketch, "E360", {"start": v(-88.94, -86.23) * mm, "end": v(-88.98, -86.3) * mm});
            skLineSegment(sketch, "E361", {"start": v(-88.98, -86.3) * mm, "end": v(-89.02, -86.35) * mm});
            skLineSegment(sketch, "E362", {"start": v(-89.1, -86.48) * mm, "end": v(-89.13, -86.55) * mm});
            skLineSegment(sketch, "E363", {"start": v(-89.13, -86.55) * mm, "end": v(-89.17, -86.61) * mm});
            skLineSegment(sketch, "E364", {"start": v(-89.17, -86.61) * mm, "end": v(-89.2, -86.68) * mm});
            skLineSegment(sketch, "E365", {"start": v(-89.2, -86.68) * mm, "end": v(-89.22, -86.75) * mm});
            skLineSegment(sketch, "E366", {"start": v(-89.22, -86.75) * mm, "end": v(-89.25, -86.82) * mm});
            skLineSegment(sketch, "E367", {"start": v(-89.25, -86.82) * mm, "end": v(-89.27, -86.9) * mm});
            skLineSegment(sketch, "E368", {"start": v(-89.27, -86.9) * mm, "end": v(-89.3, -86.96) * mm});
            skLineSegment(sketch, "E369", {"start": v(-89.3, -86.96) * mm, "end": v(-89.31, -87.04) * mm});
            skLineSegment(sketch, "E370", {"start": v(-89.31, -87.04) * mm, "end": v(-89.33, -87.1) * mm});
            skLineSegment(sketch, "E371", {"start": v(-89.33, -87.1) * mm, "end": v(-89.34, -87.18) * mm});
            skLineSegment(sketch, "E372", {"start": v(-89.34, -87.18) * mm, "end": v(-89.35, -87.26) * mm});
            skLineSegment(sketch, "E373", {"start": v(-89.35, -87.26) * mm, "end": v(-89.36, -87.33) * mm});
            skLineSegment(sketch, "E374", {"start": v(-89.36, -87.33) * mm, "end": v(-89.36, -87.4) * mm});
            skLineSegment(sketch, "E375", {"start": v(-89.36, -87.4) * mm, "end": v(-89.37, -87.48) * mm});
            skLineSegment(sketch, "E376", {"start": v(-89.37, -87.48) * mm, "end": v(-89.37, -87.55) * mm});
            skLineSegment(sketch, "E377", {"start": v(-89.37, -87.55) * mm, "end": v(-89.36, -87.63) * mm});
            skLineSegment(sketch, "E378", {"start": v(-89.36, -87.63) * mm, "end": v(-89.36, -87.7) * mm});
            skLineSegment(sketch, "E379", {"start": v(-89.36, -87.7) * mm, "end": v(-89.35, -87.78) * mm});
            skLineSegment(sketch, "E380", {"start": v(-89.35, -87.78) * mm, "end": v(-89.34, -87.85) * mm});
            skLineSegment(sketch, "E381", {"start": v(-89.34, -87.85) * mm, "end": v(-89.33, -87.93) * mm});
            skLineSegment(sketch, "E382", {"start": v(-89.33, -87.93) * mm, "end": v(-89.31, -88) * mm});
            skLineSegment(sketch, "E383", {"start": v(-89.31, -88) * mm, "end": v(-89.3, -88.07) * mm});
            skLineSegment(sketch, "E384", {"start": v(-89.3, -88.07) * mm, "end": v(-89.27, -88.14) * mm});
            skLineSegment(sketch, "E385", {"start": v(-89.27, -88.14) * mm, "end": v(-89.25, -88.21) * mm});
            skLineSegment(sketch, "E386", {"start": v(-89.25, -88.21) * mm, "end": v(-89.22, -88.28) * mm});
            skLineSegment(sketch, "E387", {"start": v(-89.2, -88.35) * mm, "end": v(-89.17, -88.42) * mm});
            skLineSegment(sketch, "E388", {"start": v(-89.17, -88.42) * mm, "end": v(-89.13, -88.49) * mm});
            skLineSegment(sketch, "E389", {"start": v(-89.13, -88.49) * mm, "end": v(-89.1, -88.55) * mm});
            skLineSegment(sketch, "E390", {"start": v(-89.1, -88.55) * mm, "end": v(-89.06, -88.62) * mm});
            skLineSegment(sketch, "E391", {"start": v(-89.06, -88.62) * mm, "end": v(-89.02, -88.68) * mm});
            skLineSegment(sketch, "E392", {"start": v(-89.02, -88.68) * mm, "end": v(-88.98, -88.74) * mm});
            skLineSegment(sketch, "E393", {"start": v(-88.98, -88.74) * mm, "end": v(-88.94, -88.8) * mm});
            skLineSegment(sketch, "E394", {"start": v(-88.94, -88.8) * mm, "end": v(-88.9, -88.86) * mm});
            skLineSegment(sketch, "E395", {"start": v(-88.9, -88.86) * mm, "end": v(-88.84, -88.92) * mm});
            skLineSegment(sketch, "E396", {"start": v(-88.84, -88.92) * mm, "end": v(-88.8, -88.98) * mm});
            skLineSegment(sketch, "E397", {"start": v(-88.63, -89.13) * mm, "end": v(-88.58, -89.18) * mm});
            skLineSegment(sketch, "E398", {"start": v(-88.58, -89.18) * mm, "end": v(-88.52, -89.23) * mm});
            skLineSegment(sketch, "E399", {"start": v(-88.46, -89.27) * mm, "end": v(-88.4, -89.31) * mm});
            skLineSegment(sketch, "E400", {"start": v(-88.4, -89.31) * mm, "end": v(-88.33, -89.35) * mm});
            skLineSegment(sketch, "E401", {"start": v(-88.33, -89.35) * mm, "end": v(-88.27, -89.4) * mm});
            skLineSegment(sketch, "E402", {"start": v(-88.27, -89.4) * mm, "end": v(-88.2, -89.43) * mm});
            skLineSegment(sketch, "E403", {"start": v(-88.2, -89.43) * mm, "end": v(-88.14, -89.46) * mm});
            skLineSegment(sketch, "E404", {"start": v(-88.14, -89.46) * mm, "end": v(-88.07, -89.5) * mm});
            skLineSegment(sketch, "E405", {"start": v(-88.07, -89.5) * mm, "end": v(-88, -89.52) * mm});
            skLineSegment(sketch, "E406", {"start": v(-88, -89.52) * mm, "end": v(-87.93, -89.55) * mm});
            skLineSegment(sketch, "E407", {"start": v(-87.93, -89.55) * mm, "end": v(-87.86, -89.57) * mm});
            skLineSegment(sketch, "E408", {"start": v(-87.86, -89.57) * mm, "end": v(-87.79, -89.6) * mm});
            skLineSegment(sketch, "E409", {"start": v(-87.35, -89.66) * mm, "end": v(-87.27, -89.67) * mm});
            skLineSegment(sketch, "E410", {"start": v(-87.27, -89.67) * mm, "end": v(-87.2, -89.67) * mm});
            skLineSegment(sketch, "E411", {"start": v(-87.2, -89.67) * mm, "end": v(-87.12, -89.67) * mm});
            skLineSegment(sketch, "E412", {"start": v(-87.12, -89.67) * mm, "end": v(-87.05, -89.66) * mm});
            skLineSegment(sketch, "E413", {"start": v(-87.05, -89.66) * mm, "end": v(-86.97, -89.65) * mm});
            skLineSegment(sketch, "E414", {"start": v(-86.97, -89.65) * mm, "end": v(-86.9, -89.64) * mm});
            skLineSegment(sketch, "E415", {"start": v(-86.9, -89.64) * mm, "end": v(-86.83, -89.63) * mm});
            skLineSegment(sketch, "E416", {"start": v(-86.83, -89.63) * mm, "end": v(-86.75, -89.62) * mm});
            skLineSegment(sketch, "E417", {"start": v(-86.75, -89.62) * mm, "end": v(-86.68, -89.6) * mm});
            skLineSegment(sketch, "E418", {"start": v(-86.68, -89.6) * mm, "end": v(-86.6, -89.58) * mm});
            skLineSegment(sketch, "E419", {"start": v(-86.6, -89.58) * mm, "end": v(-86.54, -89.56) * mm});
            skLineSegment(sketch, "E420", {"start": v(-86.54, -89.56) * mm, "end": v(-86.47, -89.53) * mm});
            skLineSegment(sketch, "E421", {"start": v(-86.47, -89.53) * mm, "end": v(-86.4, -89.5) * mm});
            skLineSegment(sketch, "E422", {"start": v(-86.4, -89.5) * mm, "end": v(-86.33, -89.48) * mm});
            skLineSegment(sketch, "E423", {"start": v(-86.33, -89.48) * mm, "end": v(-86.26, -89.44) * mm});
            skLineSegment(sketch, "E424", {"start": v(-86.26, -89.44) * mm, "end": v(-86.2, -89.4) * mm});
            skLineSegment(sketch, "E425", {"start": v(-86.2, -89.4) * mm, "end": v(-86.13, -89.37) * mm});
            skLineSegment(sketch, "E426", {"start": v(-86.13, -89.37) * mm, "end": v(-86.07, -89.33) * mm});
            skLineSegment(sketch, "E427", {"start": v(-86.07, -89.33) * mm, "end": v(-86, -89.3) * mm});
            skLineSegment(sketch, "E428", {"start": v(-86, -89.3) * mm, "end": v(-85.94, -89.25) * mm});
            skLineSegment(sketch, "E429", {"start": v(-85.94, -89.25) * mm, "end": v(-85.88, -89.2) * mm});
            skLineSegment(sketch, "E430", {"start": v(-85.88, -89.2) * mm, "end": v(-85.83, -89.16) * mm});
            skLineSegment(sketch, "E431", {"start": v(-85.83, -89.16) * mm, "end": v(-85.77, -89.1) * mm});
            skLineSegment(sketch, "E432", {"start": v(-85.77, -89.1) * mm, "end": v(-85.72, -89.06) * mm});
            skLineSegment(sketch, "E433", {"start": v(-85.72, -89.06) * mm, "end": v(-85.66, -89) * mm});
            skLineSegment(sketch, "E434", {"start": v(-85.66, -89) * mm, "end": v(-85.61, -88.95) * mm});
            skLineSegment(sketch, "E435", {"start": v(-85.61, -88.95) * mm, "end": v(-85.56, -88.9) * mm});
            skLineSegment(sketch, "E436", {"start": v(-85.56, -88.9) * mm, "end": v(-85.52, -88.84) * mm});
            skLineSegment(sketch, "E437", {"start": v(-85.52, -88.84) * mm, "end": v(-85.47, -88.78) * mm});
            skLineSegment(sketch, "E438", {"start": v(-85.47, -88.78) * mm, "end": v(-85.43, -88.71) * mm});
            skLineSegment(sketch, "E439", {"start": v(-85.43, -88.71) * mm, "end": v(-85.39, -88.65) * mm});
            skLineSegment(sketch, "E440", {"start": v(-85.39, -88.65) * mm, "end": v(-85.35, -88.59) * mm});
            skLineSegment(sketch, "E441", {"start": v(-85.35, -88.59) * mm, "end": v(-85.32, -88.52) * mm});
            skLineSegment(sketch, "E442", {"start": v(-85.32, -88.52) * mm, "end": v(-85.28, -88.46) * mm});
            skLineSegment(sketch, "E443", {"start": v(-85.28, -88.46) * mm, "end": v(-85.25, -88.39) * mm});
            skLineSegment(sketch, "E444", {"start": v(-85.22, -88.32) * mm, "end": v(-85.2, -88.25) * mm});
            skLineSegment(sketch, "E445", {"start": v(-85.2, -88.25) * mm, "end": v(-85.17, -88.18) * mm});
            skLineSegment(sketch, "E446", {"start": v(-85.15, -88.1) * mm, "end": v(-85.13, -88.03) * mm});
            skLineSegment(sketch, "E447", {"start": v(-85.13, -88.03) * mm, "end": v(-85.11, -87.96) * mm});
            skLineSegment(sketch, "E448", {"start": v(-85.11, -87.96) * mm, "end": v(-85.1, -87.89) * mm});
            skLineSegment(sketch, "E449", {"start": v(-85.09, -87.82) * mm, "end": v(-85.08, -87.74) * mm});
            skLineSegment(sketch, "E450", {"start": v(-85.08, -87.74) * mm, "end": v(-85.07, -87.67) * mm});
            skLineSegment(sketch, "E451", {"start": v(-85.07, -87.67) * mm, "end": v(-85.07, -87.6) * mm});
            skLineSegment(sketch, "E452", {"start": v(-85.07, -87.6) * mm, "end": v(-85.07, -87.52) * mm});
            skLineSegment(sketch, "E453", {"start": v(154.9, -81.16) * mm, "end": v(239.9, -81.16) * mm});
            skLineSegment(sketch, "E454", {"start": v(239.9, -81.16) * mm, "end": v(239.9, 38.84) * mm});
            skLineSegment(sketch, "E455", {"start": v(239.9, 38.84) * mm, "end": v(154.9, 38.84) * mm});
            skLineSegment(sketch, "E456", {"start": v(154.9, 38.84) * mm, "end": v(154.9, -81.16) * mm});
            skLineSegment(sketch, "E457", {"start": v(74.77, -47.12) * mm, "end": v(74.77, -47.08) * mm});
            skLineSegment(sketch, "E458", {"start": v(74.77, -47.08) * mm, "end": v(74.77, -47.04) * mm});
            skLineSegment(sketch, "E459", {"start": v(74.77, -47.04) * mm, "end": v(74.76, -47) * mm});
            skLineSegment(sketch, "E460", {"start": v(74.76, -47) * mm, "end": v(74.76, -46.95) * mm});
            skLineSegment(sketch, "E461", {"start": v(74.76, -46.95) * mm, "end": v(74.75, -46.9) * mm});
            skLineSegment(sketch, "E462", {"start": v(74.75, -46.9) * mm, "end": v(74.74, -46.86) * mm});
            skLineSegment(sketch, "E463", {"start": v(74.74, -46.86) * mm, "end": v(74.73, -46.82) * mm});
            skLineSegment(sketch, "E464", {"start": v(74.73, -46.82) * mm, "end": v(74.72, -46.78) * mm});
            skLineSegment(sketch, "E465", {"start": v(74.72, -46.78) * mm, "end": v(74.7, -46.74) * mm});
            skLineSegment(sketch, "E466", {"start": v(74.7, -46.74) * mm, "end": v(74.7, -46.7) * mm});
            skLineSegment(sketch, "E467", {"start": v(74.7, -46.7) * mm, "end": v(74.68, -46.66) * mm});
            skLineSegment(sketch, "E468", {"start": v(74.68, -46.66) * mm, "end": v(74.66, -46.62) * mm});
            skLineSegment(sketch, "E469", {"start": v(74.66, -46.62) * mm, "end": v(74.64, -46.58) * mm});
            skLineSegment(sketch, "E470", {"start": v(74.64, -46.58) * mm, "end": v(74.62, -46.54) * mm});
            skLineSegment(sketch, "E471", {"start": v(74.62, -46.54) * mm, "end": v(74.6, -46.5) * mm});
            skLineSegment(sketch, "E472", {"start": v(74.6, -46.5) * mm, "end": v(74.58, -46.46) * mm});
            skLineSegment(sketch, "E473", {"start": v(74.53, -46.4) * mm, "end": v(74.5, -46.36) * mm});
            skLineSegment(sketch, "E474", {"start": v(74.5, -46.36) * mm, "end": v(74.48, -46.32) * mm});
            skLineSegment(sketch, "E475", {"start": v(74.42, -46.26) * mm, "end": v(74.4, -46.23) * mm});
            skLineSegment(sketch, "E476", {"start": v(74.4, -46.23) * mm, "end": v(74.36, -46.2) * mm});
            skLineSegment(sketch, "E477", {"start": v(74.36, -46.2) * mm, "end": v(74.33, -46.17) * mm});
            skLineSegment(sketch, "E478", {"start": v(74.33, -46.17) * mm, "end": v(74.3, -46.14) * mm});
            skLineSegment(sketch, "E479", {"start": v(74.3, -46.14) * mm, "end": v(74.26, -46.11) * mm});
            skLineSegment(sketch, "E480", {"start": v(74.26, -46.11) * mm, "end": v(74.22, -46.09) * mm});
            skLineSegment(sketch, "E481", {"start": v(74.22, -46.09) * mm, "end": v(74.19, -46.07) * mm});
            skLineSegment(sketch, "E482", {"start": v(74.19, -46.07) * mm, "end": v(74.15, -46.04) * mm});
            skLineSegment(sketch, "E483", {"start": v(74.15, -46.04) * mm, "end": v(74.11, -46.02) * mm});
            skLineSegment(sketch, "E484", {"start": v(74.11, -46.02) * mm, "end": v(74.07, -46) * mm});
            skLineSegment(sketch, "E485", {"start": v(74.07, -46) * mm, "end": v(74.03, -45.98) * mm});
            skLineSegment(sketch, "E486", {"start": v(74.03, -45.98) * mm, "end": v(74, -45.97) * mm});
            skLineSegment(sketch, "E487", {"start": v(74, -45.97) * mm, "end": v(73.95, -45.95) * mm});
            skLineSegment(sketch, "E488", {"start": v(73.95, -45.95) * mm, "end": v(73.91, -45.94) * mm});
            skLineSegment(sketch, "E489", {"start": v(73.91, -45.94) * mm, "end": v(73.87, -45.92) * mm});
            skLineSegment(sketch, "E490", {"start": v(73.87, -45.92) * mm, "end": v(73.83, -45.91) * mm});
            skLineSegment(sketch, "E491", {"start": v(73.83, -45.91) * mm, "end": v(73.79, -45.9) * mm});
            skLineSegment(sketch, "E492", {"start": v(73.79, -45.9) * mm, "end": v(73.75, -45.9) * mm});
            skLineSegment(sketch, "E493", {"start": v(73.75, -45.9) * mm, "end": v(73.7, -45.89) * mm});
            skLineSegment(sketch, "E494", {"start": v(73.7, -45.89) * mm, "end": v(73.66, -45.88) * mm});
            skLineSegment(sketch, "E495", {"start": v(73.66, -45.88) * mm, "end": v(73.62, -45.88) * mm});
            skLineSegment(sketch, "E496", {"start": v(73.62, -45.88) * mm, "end": v(73.57, -45.87) * mm});
            skLineSegment(sketch, "E497", {"start": v(73.57, -45.87) * mm, "end": v(73.53, -45.87) * mm});
            skLineSegment(sketch, "E498", {"start": v(73.53, -45.87) * mm, "end": v(73.49, -45.87) * mm});
            skLineSegment(sketch, "E499", {"start": v(73.49, -45.87) * mm, "end": v(73.44, -45.87) * mm});
            skLineSegment(sketch, "E500", {"start": v(73.44, -45.87) * mm, "end": v(73.4, -45.88) * mm});
            skLineSegment(sketch, "E501", {"start": v(73.4, -45.88) * mm, "end": v(73.36, -45.88) * mm});
            skLineSegment(sketch, "E502", {"start": v(73.36, -45.88) * mm, "end": v(73.31, -45.89) * mm});
            skLineSegment(sketch, "E503", {"start": v(73.31, -45.89) * mm, "end": v(73.27, -45.9) * mm});
            skLineSegment(sketch, "E504", {"start": v(73.27, -45.9) * mm, "end": v(73.23, -45.9) * mm});
            skLineSegment(sketch, "E505", {"start": v(73.23, -45.9) * mm, "end": v(73.19, -45.92) * mm});
            skLineSegment(sketch, "E506", {"start": v(73.15, -45.93) * mm, "end": v(73.1, -45.94) * mm});
            skLineSegment(sketch, "E507", {"start": v(73.1, -45.94) * mm, "end": v(73.06, -45.96) * mm});
            skLineSegment(sketch, "E508", {"start": v(73.06, -45.96) * mm, "end": v(73.02, -45.97) * mm});
            skLineSegment(sketch, "E509", {"start": v(73.02, -45.97) * mm, "end": v(72.98, -46) * mm});
            skLineSegment(sketch, "E510", {"start": v(72.98, -46) * mm, "end": v(72.94, -46.01) * mm});
            skLineSegment(sketch, "E511", {"start": v(72.94, -46.01) * mm, "end": v(72.9, -46.03) * mm});
            skLineSegment(sketch, "E512", {"start": v(72.9, -46.03) * mm, "end": v(72.87, -46.05) * mm});
            skLineSegment(sketch, "E513", {"start": v(72.87, -46.05) * mm, "end": v(72.83, -46.08) * mm});
            skLineSegment(sketch, "E514", {"start": v(72.83, -46.08) * mm, "end": v(72.8, -46.1) * mm});
            skLineSegment(sketch, "E515", {"start": v(72.8, -46.1) * mm, "end": v(72.76, -46.13) * mm});
            skLineSegment(sketch, "E516", {"start": v(72.76, -46.13) * mm, "end": v(72.73, -46.15) * mm});
            skLineSegment(sketch, "E517", {"start": v(72.73, -46.15) * mm, "end": v(72.7, -46.18) * mm});
            skLineSegment(sketch, "E518", {"start": v(72.7, -46.18) * mm, "end": v(72.66, -46.21) * mm});
            skLineSegment(sketch, "E519", {"start": v(72.66, -46.21) * mm, "end": v(72.63, -46.24) * mm});
            skLineSegment(sketch, "E520", {"start": v(72.63, -46.24) * mm, "end": v(72.6, -46.27) * mm});
            skLineSegment(sketch, "E521", {"start": v(72.6, -46.27) * mm, "end": v(72.57, -46.3) * mm});
            skLineSegment(sketch, "E522", {"start": v(72.57, -46.3) * mm, "end": v(72.54, -46.34) * mm});
            skLineSegment(sketch, "E523", {"start": v(72.54, -46.34) * mm, "end": v(72.52, -46.37) * mm});
            skLineSegment(sketch, "E524", {"start": v(72.52, -46.37) * mm, "end": v(72.5, -46.4) * mm});
            skLineSegment(sketch, "E525", {"start": v(72.5, -46.4) * mm, "end": v(72.47, -46.44) * mm});
            skLineSegment(sketch, "E526", {"start": v(72.47, -46.44) * mm, "end": v(72.45, -46.48) * mm});
            skLineSegment(sketch, "E527", {"start": v(72.45, -46.48) * mm, "end": v(72.42, -46.52) * mm});
            skLineSegment(sketch, "E528", {"start": v(72.42, -46.52) * mm, "end": v(72.4, -46.56) * mm});
            skLineSegment(sketch, "E529", {"start": v(72.4, -46.56) * mm, "end": v(72.38, -46.6) * mm});
            skLineSegment(sketch, "E530", {"start": v(72.38, -46.6) * mm, "end": v(72.37, -46.64) * mm});
            skLineSegment(sketch, "E531", {"start": v(72.37, -46.64) * mm, "end": v(72.35, -46.68) * mm});
            skLineSegment(sketch, "E532", {"start": v(72.35, -46.68) * mm, "end": v(72.34, -46.72) * mm});
            skLineSegment(sketch, "E533", {"start": v(72.34, -46.72) * mm, "end": v(72.32, -46.76) * mm});
            skLineSegment(sketch, "E534", {"start": v(72.32, -46.76) * mm, "end": v(72.31, -46.8) * mm});
            skLineSegment(sketch, "E535", {"start": v(72.31, -46.8) * mm, "end": v(72.3, -46.84) * mm});
            skLineSegment(sketch, "E536", {"start": v(72.3, -46.84) * mm, "end": v(72.3, -46.88) * mm});
            skLineSegment(sketch, "E537", {"start": v(72.3, -46.88) * mm, "end": v(72.28, -46.93) * mm});
            skLineSegment(sketch, "E538", {"start": v(72.28, -46.93) * mm, "end": v(72.28, -46.97) * mm});
            skLineSegment(sketch, "E539", {"start": v(72.28, -46.97) * mm, "end": v(72.27, -47.01) * mm});
            skLineSegment(sketch, "E540", {"start": v(72.27, -47.01) * mm, "end": v(72.27, -47.06) * mm});
            skLineSegment(sketch, "E541", {"start": v(72.27, -47.06) * mm, "end": v(72.27, -47.1) * mm});
            skLineSegment(sketch, "E542", {"start": v(72.27, -47.1) * mm, "end": v(72.27, -47.14) * mm});
            skLineSegment(sketch, "E543", {"start": v(72.27, -47.14) * mm, "end": v(72.27, -47.19) * mm});
            skLineSegment(sketch, "E544", {"start": v(72.27, -47.19) * mm, "end": v(72.27, -47.23) * mm});
            skLineSegment(sketch, "E545", {"start": v(72.27, -47.23) * mm, "end": v(72.28, -47.27) * mm});
            skLineSegment(sketch, "E546", {"start": v(72.3, -47.36) * mm, "end": v(72.3, -47.4) * mm});
            skLineSegment(sketch, "E547", {"start": v(72.3, -47.4) * mm, "end": v(72.31, -47.44) * mm});
            skLineSegment(sketch, "E548", {"start": v(72.31, -47.44) * mm, "end": v(72.32, -47.49) * mm});
            skLineSegment(sketch, "E549", {"start": v(72.32, -47.49) * mm, "end": v(72.34, -47.53) * mm});
            skLineSegment(sketch, "E550", {"start": v(72.34, -47.53) * mm, "end": v(72.35, -47.57) * mm});
            skLineSegment(sketch, "E551", {"start": v(72.35, -47.57) * mm, "end": v(72.37, -47.6) * mm});
            skLineSegment(sketch, "E552", {"start": v(72.37, -47.6) * mm, "end": v(72.38, -47.65) * mm});
            skLineSegment(sketch, "E553", {"start": v(72.38, -47.65) * mm, "end": v(72.4, -47.69) * mm});
            skLineSegment(sketch, "E554", {"start": v(72.4, -47.69) * mm, "end": v(72.42, -47.72) * mm});
            skLineSegment(sketch, "E555", {"start": v(72.42, -47.72) * mm, "end": v(72.45, -47.76) * mm});
            skLineSegment(sketch, "E556", {"start": v(72.45, -47.76) * mm, "end": v(72.47, -47.8) * mm});
            skLineSegment(sketch, "E557", {"start": v(72.5, -47.84) * mm, "end": v(72.52, -47.87) * mm});
            skLineSegment(sketch, "E558", {"start": v(72.52, -47.87) * mm, "end": v(72.54, -47.9) * mm});
            skLineSegment(sketch, "E559", {"start": v(72.54, -47.9) * mm, "end": v(72.57, -47.94) * mm});
            skLineSegment(sketch, "E560", {"start": v(72.63, -48) * mm, "end": v(72.66, -48.03) * mm});
            skLineSegment(sketch, "E561", {"start": v(72.66, -48.03) * mm, "end": v(72.7, -48.06) * mm});
            skLineSegment(sketch, "E562", {"start": v(72.7, -48.06) * mm, "end": v(72.73, -48.09) * mm});
            skLineSegment(sketch, "E563", {"start": v(72.73, -48.09) * mm, "end": v(72.76, -48.12) * mm});
            skLineSegment(sketch, "E564", {"start": v(72.76, -48.12) * mm, "end": v(72.8, -48.14) * mm});
            skLineSegment(sketch, "E565", {"start": v(72.8, -48.14) * mm, "end": v(72.83, -48.17) * mm});
            skLineSegment(sketch, "E566", {"start": v(72.83, -48.17) * mm, "end": v(72.87, -48.19) * mm});
            skLineSegment(sketch, "E567", {"start": v(72.87, -48.19) * mm, "end": v(72.9, -48.21) * mm});
            skLineSegment(sketch, "E568", {"start": v(72.9, -48.21) * mm, "end": v(72.94, -48.23) * mm});
            skLineSegment(sketch, "E569", {"start": v(72.94, -48.23) * mm, "end": v(72.98, -48.25) * mm});
            skLineSegment(sketch, "E570", {"start": v(72.98, -48.25) * mm, "end": v(73.02, -48.27) * mm});
            skLineSegment(sketch, "E571", {"start": v(73.02, -48.27) * mm, "end": v(73.06, -48.29) * mm});
            skLineSegment(sketch, "E572", {"start": v(73.06, -48.29) * mm, "end": v(73.1, -48.3) * mm});
            skLineSegment(sketch, "E573", {"start": v(73.1, -48.3) * mm, "end": v(73.15, -48.31) * mm});
            skLineSegment(sketch, "E574", {"start": v(73.15, -48.31) * mm, "end": v(73.19, -48.33) * mm});
            skLineSegment(sketch, "E575", {"start": v(73.19, -48.33) * mm, "end": v(73.23, -48.34) * mm});
            skLineSegment(sketch, "E576", {"start": v(73.27, -48.35) * mm, "end": v(73.31, -48.35) * mm});
            skLineSegment(sketch, "E577", {"start": v(73.31, -48.35) * mm, "end": v(73.36, -48.36) * mm});
            skLineSegment(sketch, "E578", {"start": v(73.36, -48.36) * mm, "end": v(73.4, -48.37) * mm});
            skLineSegment(sketch, "E579", {"start": v(73.4, -48.37) * mm, "end": v(73.44, -48.37) * mm});
            skLineSegment(sketch, "E580", {"start": v(73.44, -48.37) * mm, "end": v(73.49, -48.37) * mm});
            skLineSegment(sketch, "E581", {"start": v(73.49, -48.37) * mm, "end": v(73.53, -48.37) * mm});
            skLineSegment(sketch, "E582", {"start": v(73.53, -48.37) * mm, "end": v(73.57, -48.37) * mm});
            skLineSegment(sketch, "E583", {"start": v(73.57, -48.37) * mm, "end": v(73.62, -48.37) * mm});
            skLineSegment(sketch, "E584", {"start": v(73.62, -48.37) * mm, "end": v(73.66, -48.36) * mm});
            skLineSegment(sketch, "E585", {"start": v(73.66, -48.36) * mm, "end": v(73.7, -48.36) * mm});
            skLineSegment(sketch, "E586", {"start": v(73.7, -48.36) * mm, "end": v(73.75, -48.35) * mm});
            skLineSegment(sketch, "E587", {"start": v(73.75, -48.35) * mm, "end": v(73.79, -48.34) * mm});
            skLineSegment(sketch, "E588", {"start": v(73.79, -48.34) * mm, "end": v(73.83, -48.33) * mm});
            skLineSegment(sketch, "E589", {"start": v(73.83, -48.33) * mm, "end": v(73.87, -48.32) * mm});
            skLineSegment(sketch, "E590", {"start": v(73.87, -48.32) * mm, "end": v(73.91, -48.3) * mm});
            skLineSegment(sketch, "E591", {"start": v(73.91, -48.3) * mm, "end": v(73.95, -48.3) * mm});
            skLineSegment(sketch, "E592", {"start": v(73.95, -48.3) * mm, "end": v(74, -48.28) * mm});
            skLineSegment(sketch, "E593", {"start": v(74, -48.28) * mm, "end": v(74.03, -48.26) * mm});
            skLineSegment(sketch, "E594", {"start": v(74.03, -48.26) * mm, "end": v(74.07, -48.24) * mm});
            skLineSegment(sketch, "E595", {"start": v(74.07, -48.24) * mm, "end": v(74.11, -48.22) * mm});
            skLineSegment(sketch, "E596", {"start": v(74.11, -48.22) * mm, "end": v(74.15, -48.2) * mm});
            skLineSegment(sketch, "E597", {"start": v(74.15, -48.2) * mm, "end": v(74.19, -48.18) * mm});
            skLineSegment(sketch, "E598", {"start": v(74.19, -48.18) * mm, "end": v(74.22, -48.15) * mm});
            skLineSegment(sketch, "E599", {"start": v(74.22, -48.15) * mm, "end": v(74.26, -48.13) * mm});
            skLineSegment(sketch, "E600", {"start": v(74.26, -48.13) * mm, "end": v(74.3, -48.1) * mm});
            skLineSegment(sketch, "E601", {"start": v(74.3, -48.1) * mm, "end": v(74.33, -48.08) * mm});
            skLineSegment(sketch, "E602", {"start": v(74.33, -48.08) * mm, "end": v(74.36, -48.05) * mm});
            skLineSegment(sketch, "E603", {"start": v(74.36, -48.05) * mm, "end": v(74.4, -48.02) * mm});
            skLineSegment(sketch, "E604", {"start": v(74.4, -48.02) * mm, "end": v(74.42, -47.99) * mm});
            skLineSegment(sketch, "E605", {"start": v(74.42, -47.99) * mm, "end": v(74.45, -47.95) * mm});
            skLineSegment(sketch, "E606", {"start": v(74.45, -47.95) * mm, "end": v(74.48, -47.92) * mm});
            skLineSegment(sketch, "E607", {"start": v(74.48, -47.92) * mm, "end": v(74.5, -47.89) * mm});
            skLineSegment(sketch, "E608", {"start": v(74.53, -47.85) * mm, "end": v(74.56, -47.82) * mm});
            skLineSegment(sketch, "E609", {"start": v(74.56, -47.82) * mm, "end": v(74.58, -47.78) * mm});
            skLineSegment(sketch, "E610", {"start": v(74.58, -47.78) * mm, "end": v(74.6, -47.74) * mm});
            skLineSegment(sketch, "E611", {"start": v(74.6, -47.74) * mm, "end": v(74.62, -47.7) * mm});
            skLineSegment(sketch, "E612", {"start": v(74.62, -47.7) * mm, "end": v(74.64, -47.67) * mm});
            skLineSegment(sketch, "E613", {"start": v(74.64, -47.67) * mm, "end": v(74.66, -47.63) * mm});
            skLineSegment(sketch, "E614", {"start": v(74.66, -47.63) * mm, "end": v(74.68, -47.59) * mm});
            skLineSegment(sketch, "E615", {"start": v(74.68, -47.59) * mm, "end": v(74.7, -47.55) * mm});
            skLineSegment(sketch, "E616", {"start": v(74.7, -47.55) * mm, "end": v(74.7, -47.5) * mm});
            skLineSegment(sketch, "E617", {"start": v(74.7, -47.5) * mm, "end": v(74.72, -47.46) * mm});
            skLineSegment(sketch, "E618", {"start": v(74.72, -47.46) * mm, "end": v(74.73, -47.42) * mm});
            skLineSegment(sketch, "E619", {"start": v(74.74, -47.38) * mm, "end": v(74.75, -47.34) * mm});
            skLineSegment(sketch, "E620", {"start": v(74.75, -47.34) * mm, "end": v(74.76, -47.3) * mm});
            skLineSegment(sketch, "E621", {"start": v(74.76, -47.3) * mm, "end": v(74.76, -47.25) * mm});
            skLineSegment(sketch, "E622", {"start": v(74.76, -47.25) * mm, "end": v(74.77, -47.2) * mm});
            skLineSegment(sketch, "E623", {"start": v(74.77, -47.2) * mm, "end": v(74.77, -47.17) * mm});
            skLineSegment(sketch, "E624", {"start": v(74.77, -47.17) * mm, "end": v(74.77, -47.12) * mm});
            skLineSegment(sketch, "E625", {"start": v(74.77, -77.12) * mm, "end": v(74.77, -77.08) * mm});
            skLineSegment(sketch, "E626", {"start": v(74.77, -77.08) * mm, "end": v(74.77, -77.04) * mm});
            skLineSegment(sketch, "E627", {"start": v(74.77, -77.04) * mm, "end": v(74.76, -77) * mm});
            skLineSegment(sketch, "E628", {"start": v(74.76, -77) * mm, "end": v(74.76, -76.95) * mm});
            skLineSegment(sketch, "E629", {"start": v(74.76, -76.95) * mm, "end": v(74.75, -76.9) * mm});
            skLineSegment(sketch, "E630", {"start": v(74.75, -76.9) * mm, "end": v(74.74, -76.86) * mm});
            skLineSegment(sketch, "E631", {"start": v(74.74, -76.86) * mm, "end": v(74.73, -76.82) * mm});
            skLineSegment(sketch, "E632", {"start": v(74.73, -76.82) * mm, "end": v(74.72, -76.78) * mm});
            skLineSegment(sketch, "E633", {"start": v(74.72, -76.78) * mm, "end": v(74.7, -76.74) * mm});
            skLineSegment(sketch, "E634", {"start": v(74.7, -76.7) * mm, "end": v(74.68, -76.66) * mm});
            skLineSegment(sketch, "E635", {"start": v(74.68, -76.66) * mm, "end": v(74.66, -76.62) * mm});
            skLineSegment(sketch, "E636", {"start": v(74.66, -76.62) * mm, "end": v(74.64, -76.58) * mm});
            skLineSegment(sketch, "E637", {"start": v(74.64, -76.58) * mm, "end": v(74.62, -76.54) * mm});
            skLineSegment(sketch, "E638", {"start": v(74.6, -76.5) * mm, "end": v(74.58, -76.46) * mm});
            skLineSegment(sketch, "E639", {"start": v(74.58, -76.46) * mm, "end": v(74.56, -76.43) * mm});
            skLineSegment(sketch, "E640", {"start": v(74.56, -76.43) * mm, "end": v(74.53, -76.4) * mm});
            skLineSegment(sketch, "E641", {"start": v(74.53, -76.4) * mm, "end": v(74.5, -76.36) * mm});
            skLineSegment(sketch, "E642", {"start": v(74.5, -76.36) * mm, "end": v(74.48, -76.32) * mm});
            skLineSegment(sketch, "E643", {"start": v(74.48, -76.32) * mm, "end": v(74.45, -76.29) * mm});
            skLineSegment(sketch, "E644", {"start": v(74.45, -76.29) * mm, "end": v(74.42, -76.26) * mm});
            skLineSegment(sketch, "E645", {"start": v(74.42, -76.26) * mm, "end": v(74.4, -76.23) * mm});
            skLineSegment(sketch, "E646", {"start": v(74.4, -76.23) * mm, "end": v(74.36, -76.2) * mm});
            skLineSegment(sketch, "E647", {"start": v(74.36, -76.2) * mm, "end": v(74.33, -76.17) * mm});
            skLineSegment(sketch, "E648", {"start": v(74.33, -76.17) * mm, "end": v(74.3, -76.14) * mm});
            skLineSegment(sketch, "E649", {"start": v(74.3, -76.14) * mm, "end": v(74.26, -76.11) * mm});
            skLineSegment(sketch, "E650", {"start": v(74.26, -76.11) * mm, "end": v(74.22, -76.09) * mm});
            skLineSegment(sketch, "E651", {"start": v(74.22, -76.09) * mm, "end": v(74.19, -76.07) * mm});
            skLineSegment(sketch, "E652", {"start": v(74.15, -76.04) * mm, "end": v(74.11, -76.02) * mm});
            skLineSegment(sketch, "E653", {"start": v(74.11, -76.02) * mm, "end": v(74.07, -76) * mm});
            skLineSegment(sketch, "E654", {"start": v(74.07, -76) * mm, "end": v(74.03, -75.98) * mm});
            skLineSegment(sketch, "E655", {"start": v(74.03, -75.98) * mm, "end": v(74, -75.97) * mm});
            skLineSegment(sketch, "E656", {"start": v(74, -75.97) * mm, "end": v(73.95, -75.95) * mm});
            skLineSegment(sketch, "E657", {"start": v(73.95, -75.95) * mm, "end": v(73.91, -75.94) * mm});
            skLineSegment(sketch, "E658", {"start": v(73.91, -75.94) * mm, "end": v(73.87, -75.92) * mm});
            skLineSegment(sketch, "E659", {"start": v(73.87, -75.92) * mm, "end": v(73.83, -75.91) * mm});
            skLineSegment(sketch, "E660", {"start": v(73.83, -75.91) * mm, "end": v(73.79, -75.9) * mm});
            skLineSegment(sketch, "E661", {"start": v(73.79, -75.9) * mm, "end": v(73.75, -75.9) * mm});
            skLineSegment(sketch, "E662", {"start": v(73.75, -75.9) * mm, "end": v(73.7, -75.89) * mm});
            skLineSegment(sketch, "E663", {"start": v(73.7, -75.89) * mm, "end": v(73.66, -75.88) * mm});
            skLineSegment(sketch, "E664", {"start": v(73.66, -75.88) * mm, "end": v(73.62, -75.88) * mm});
            skLineSegment(sketch, "E665", {"start": v(73.62, -75.88) * mm, "end": v(73.57, -75.87) * mm});
            skLineSegment(sketch, "E666", {"start": v(73.57, -75.87) * mm, "end": v(73.53, -75.87) * mm});
            skLineSegment(sketch, "E667", {"start": v(73.53, -75.87) * mm, "end": v(73.49, -75.87) * mm});
            skLineSegment(sketch, "E668", {"start": v(73.49, -75.87) * mm, "end": v(73.44, -75.87) * mm});
            skLineSegment(sketch, "E669", {"start": v(73.44, -75.87) * mm, "end": v(73.4, -75.88) * mm});
            skLineSegment(sketch, "E670", {"start": v(73.4, -75.88) * mm, "end": v(73.36, -75.88) * mm});
            skLineSegment(sketch, "E671", {"start": v(73.36, -75.88) * mm, "end": v(73.31, -75.89) * mm});
            skLineSegment(sketch, "E672", {"start": v(73.27, -75.9) * mm, "end": v(73.23, -75.9) * mm});
            skLineSegment(sketch, "E673", {"start": v(73.23, -75.9) * mm, "end": v(73.19, -75.92) * mm});
            skLineSegment(sketch, "E674", {"start": v(73.19, -75.92) * mm, "end": v(73.15, -75.93) * mm});
            skLineSegment(sketch, "E675", {"start": v(73.15, -75.93) * mm, "end": v(73.1, -75.94) * mm});
            skLineSegment(sketch, "E676", {"start": v(73.1, -75.94) * mm, "end": v(73.06, -75.96) * mm});
            skLineSegment(sketch, "E677", {"start": v(73.06, -75.96) * mm, "end": v(73.02, -75.97) * mm});
            skLineSegment(sketch, "E678", {"start": v(73.02, -75.97) * mm, "end": v(72.98, -76) * mm});
            skLineSegment(sketch, "E679", {"start": v(72.66, -76.21) * mm, "end": v(72.63, -76.24) * mm});
            skLineSegment(sketch, "E680", {"start": v(72.63, -76.24) * mm, "end": v(72.6, -76.27) * mm});
            skLineSegment(sketch, "E681", {"start": v(72.6, -76.27) * mm, "end": v(72.57, -76.3) * mm});
            skLineSegment(sketch, "E682", {"start": v(72.57, -76.3) * mm, "end": v(72.54, -76.34) * mm});
            skLineSegment(sketch, "E683", {"start": v(72.54, -76.34) * mm, "end": v(72.52, -76.37) * mm});
            skLineSegment(sketch, "E684", {"start": v(72.52, -76.37) * mm, "end": v(72.5, -76.4) * mm});
            skLineSegment(sketch, "E685", {"start": v(72.5, -76.4) * mm, "end": v(72.47, -76.44) * mm});
            skLineSegment(sketch, "E686", {"start": v(72.45, -76.48) * mm, "end": v(72.42, -76.52) * mm});
            skLineSegment(sketch, "E687", {"start": v(72.42, -76.52) * mm, "end": v(72.4, -76.56) * mm});
            skLineSegment(sketch, "E688", {"start": v(72.4, -76.56) * mm, "end": v(72.38, -76.6) * mm});
            skLineSegment(sketch, "E689", {"start": v(72.38, -76.6) * mm, "end": v(72.37, -76.64) * mm});
            skLineSegment(sketch, "E690", {"start": v(72.37, -76.64) * mm, "end": v(72.35, -76.68) * mm});
            skLineSegment(sketch, "E691", {"start": v(72.35, -76.68) * mm, "end": v(72.34, -76.72) * mm});
            skLineSegment(sketch, "E692", {"start": v(72.32, -76.76) * mm, "end": v(72.31, -76.8) * mm});
            skLineSegment(sketch, "E693", {"start": v(72.31, -76.8) * mm, "end": v(72.3, -76.84) * mm});
            skLineSegment(sketch, "E694", {"start": v(72.3, -76.88) * mm, "end": v(72.28, -76.93) * mm});
            skLineSegment(sketch, "E695", {"start": v(72.28, -76.93) * mm, "end": v(72.28, -76.97) * mm});
            skLineSegment(sketch, "E696", {"start": v(72.28, -76.97) * mm, "end": v(72.27, -77.01) * mm});
            skLineSegment(sketch, "E697", {"start": v(72.27, -77.01) * mm, "end": v(72.27, -77.06) * mm});
            skLineSegment(sketch, "E698", {"start": v(72.27, -77.06) * mm, "end": v(72.27, -77.1) * mm});
            skLineSegment(sketch, "E699", {"start": v(72.27, -77.1) * mm, "end": v(72.27, -77.14) * mm});
            skLineSegment(sketch, "E700", {"start": v(72.27, -77.14) * mm, "end": v(72.27, -77.19) * mm});
            skLineSegment(sketch, "E701", {"start": v(72.27, -77.19) * mm, "end": v(72.27, -77.23) * mm});
            skLineSegment(sketch, "E702", {"start": v(72.27, -77.23) * mm, "end": v(72.28, -77.27) * mm});
            skLineSegment(sketch, "E703", {"start": v(72.28, -77.27) * mm, "end": v(72.28, -77.32) * mm});
            skLineSegment(sketch, "E704", {"start": v(72.28, -77.32) * mm, "end": v(72.3, -77.36) * mm});
            skLineSegment(sketch, "E705", {"start": v(72.3, -77.36) * mm, "end": v(72.3, -77.4) * mm});
            skLineSegment(sketch, "E706", {"start": v(72.3, -77.4) * mm, "end": v(72.31, -77.44) * mm});
            skLineSegment(sketch, "E707", {"start": v(72.31, -77.44) * mm, "end": v(72.32, -77.49) * mm});
            skLineSegment(sketch, "E708", {"start": v(72.32, -77.49) * mm, "end": v(72.34, -77.53) * mm});
            skLineSegment(sketch, "E709", {"start": v(72.34, -77.53) * mm, "end": v(72.35, -77.57) * mm});
            skLineSegment(sketch, "E710", {"start": v(72.35, -77.57) * mm, "end": v(72.37, -77.6) * mm});
            skLineSegment(sketch, "E711", {"start": v(72.37, -77.6) * mm, "end": v(72.38, -77.65) * mm});
            skLineSegment(sketch, "E712", {"start": v(72.38, -77.65) * mm, "end": v(72.4, -77.69) * mm});
            skLineSegment(sketch, "E713", {"start": v(72.4, -77.69) * mm, "end": v(72.42, -77.72) * mm});
            skLineSegment(sketch, "E714", {"start": v(72.45, -77.76) * mm, "end": v(72.47, -77.8) * mm});
            skLineSegment(sketch, "E715", {"start": v(72.47, -77.8) * mm, "end": v(72.5, -77.84) * mm});
            skLineSegment(sketch, "E716", {"start": v(72.5, -77.84) * mm, "end": v(72.52, -77.87) * mm});
            skLineSegment(sketch, "E717", {"start": v(72.52, -77.87) * mm, "end": v(72.54, -77.9) * mm});
            skLineSegment(sketch, "E718", {"start": v(72.54, -77.9) * mm, "end": v(72.57, -77.94) * mm});
            skLineSegment(sketch, "E719", {"start": v(72.57, -77.94) * mm, "end": v(72.6, -77.97) * mm});
            skLineSegment(sketch, "E720", {"start": v(72.6, -77.97) * mm, "end": v(72.63, -78) * mm});
            skLineSegment(sketch, "E721", {"start": v(72.63, -78) * mm, "end": v(72.66, -78.03) * mm});
            skLineSegment(sketch, "E722", {"start": v(72.66, -78.03) * mm, "end": v(72.7, -78.06) * mm});
            skLineSegment(sketch, "E723", {"start": v(72.7, -78.06) * mm, "end": v(72.73, -78.09) * mm});
            skLineSegment(sketch, "E724", {"start": v(72.73, -78.09) * mm, "end": v(72.76, -78.12) * mm});
            skLineSegment(sketch, "E725", {"start": v(72.76, -78.12) * mm, "end": v(72.8, -78.14) * mm});
            skLineSegment(sketch, "E726", {"start": v(72.8, -78.14) * mm, "end": v(72.83, -78.17) * mm});
            skLineSegment(sketch, "E727", {"start": v(72.83, -78.17) * mm, "end": v(72.87, -78.19) * mm});
            skLineSegment(sketch, "E728", {"start": v(72.87, -78.19) * mm, "end": v(72.9, -78.21) * mm});
            skLineSegment(sketch, "E729", {"start": v(72.9, -78.21) * mm, "end": v(72.94, -78.23) * mm});
            skLineSegment(sketch, "E730", {"start": v(72.94, -78.23) * mm, "end": v(72.98, -78.25) * mm});
            skLineSegment(sketch, "E731", {"start": v(73.02, -78.27) * mm, "end": v(73.06, -78.29) * mm});
            skLineSegment(sketch, "E732", {"start": v(73.06, -78.29) * mm, "end": v(73.1, -78.3) * mm});
            skLineSegment(sketch, "E733", {"start": v(73.15, -78.31) * mm, "end": v(73.19, -78.33) * mm});
            skLineSegment(sketch, "E734", {"start": v(73.19, -78.33) * mm, "end": v(73.23, -78.34) * mm});
            skLineSegment(sketch, "E735", {"start": v(73.23, -78.34) * mm, "end": v(73.27, -78.35) * mm});
            skLineSegment(sketch, "E736", {"start": v(73.27, -78.35) * mm, "end": v(73.31, -78.35) * mm});
            skLineSegment(sketch, "E737", {"start": v(73.31, -78.35) * mm, "end": v(73.36, -78.36) * mm});
            skLineSegment(sketch, "E738", {"start": v(73.36, -78.36) * mm, "end": v(73.4, -78.37) * mm});
            skLineSegment(sketch, "E739", {"start": v(73.4, -78.37) * mm, "end": v(73.44, -78.37) * mm});
            skLineSegment(sketch, "E740", {"start": v(73.44, -78.37) * mm, "end": v(73.49, -78.37) * mm});
            skLineSegment(sketch, "E741", {"start": v(73.49, -78.37) * mm, "end": v(73.53, -78.37) * mm});
            skLineSegment(sketch, "E742", {"start": v(73.53, -78.37) * mm, "end": v(73.57, -78.37) * mm});
            skLineSegment(sketch, "E743", {"start": v(73.57, -78.37) * mm, "end": v(73.62, -78.37) * mm});
            skLineSegment(sketch, "E744", {"start": v(73.62, -78.37) * mm, "end": v(73.66, -78.36) * mm});
            skLineSegment(sketch, "E745", {"start": v(73.66, -78.36) * mm, "end": v(73.7, -78.36) * mm});
            skLineSegment(sketch, "E746", {"start": v(73.7, -78.36) * mm, "end": v(73.75, -78.35) * mm});
            skLineSegment(sketch, "E747", {"start": v(73.75, -78.35) * mm, "end": v(73.79, -78.34) * mm});
            skLineSegment(sketch, "E748", {"start": v(73.79, -78.34) * mm, "end": v(73.83, -78.33) * mm});
            skLineSegment(sketch, "E749", {"start": v(73.83, -78.33) * mm, "end": v(73.87, -78.32) * mm});
            skLineSegment(sketch, "E750", {"start": v(73.87, -78.32) * mm, "end": v(73.91, -78.3) * mm});
            skLineSegment(sketch, "E751", {"start": v(73.91, -78.3) * mm, "end": v(73.95, -78.3) * mm});
            skLineSegment(sketch, "E752", {"start": v(73.95, -78.3) * mm, "end": v(74, -78.28) * mm});
            skLineSegment(sketch, "E753", {"start": v(74, -78.28) * mm, "end": v(74.03, -78.26) * mm});
            skLineSegment(sketch, "E754", {"start": v(74.03, -78.26) * mm, "end": v(74.07, -78.24) * mm});
            skLineSegment(sketch, "E755", {"start": v(74.07, -78.24) * mm, "end": v(74.11, -78.22) * mm});
            skLineSegment(sketch, "E756", {"start": v(74.11, -78.22) * mm, "end": v(74.15, -78.2) * mm});
            skLineSegment(sketch, "E757", {"start": v(74.15, -78.2) * mm, "end": v(74.19, -78.18) * mm});
            skLineSegment(sketch, "E758", {"start": v(74.19, -78.18) * mm, "end": v(74.22, -78.15) * mm});
            skLineSegment(sketch, "E759", {"start": v(74.22, -78.15) * mm, "end": v(74.26, -78.13) * mm});
            skLineSegment(sketch, "E760", {"start": v(74.26, -78.13) * mm, "end": v(74.3, -78.1) * mm});
            skLineSegment(sketch, "E761", {"start": v(74.3, -78.1) * mm, "end": v(74.33, -78.08) * mm});
            skLineSegment(sketch, "E762", {"start": v(74.36, -78.05) * mm, "end": v(74.4, -78.02) * mm});
            skLineSegment(sketch, "E763", {"start": v(74.4, -78.02) * mm, "end": v(74.42, -77.99) * mm});
            skLineSegment(sketch, "E764", {"start": v(74.42, -77.99) * mm, "end": v(74.45, -77.95) * mm});
            skLineSegment(sketch, "E765", {"start": v(74.45, -77.95) * mm, "end": v(74.48, -77.92) * mm});
            skLineSegment(sketch, "E766", {"start": v(74.5, -77.89) * mm, "end": v(74.53, -77.85) * mm});
            skLineSegment(sketch, "E767", {"start": v(74.53, -77.85) * mm, "end": v(74.56, -77.82) * mm});
            skLineSegment(sketch, "E768", {"start": v(74.58, -77.78) * mm, "end": v(74.6, -77.74) * mm});
            skLineSegment(sketch, "E769", {"start": v(74.6, -77.74) * mm, "end": v(74.62, -77.7) * mm});
            skLineSegment(sketch, "E770", {"start": v(74.62, -77.7) * mm, "end": v(74.64, -77.67) * mm});
            skLineSegment(sketch, "E771", {"start": v(74.64, -77.67) * mm, "end": v(74.66, -77.63) * mm});
            skLineSegment(sketch, "E772", {"start": v(74.66, -77.63) * mm, "end": v(74.68, -77.59) * mm});
            skLineSegment(sketch, "E773", {"start": v(74.68, -77.59) * mm, "end": v(74.7, -77.55) * mm});
            skLineSegment(sketch, "E774", {"start": v(74.7, -77.55) * mm, "end": v(74.7, -77.5) * mm});
            skLineSegment(sketch, "E775", {"start": v(74.7, -77.5) * mm, "end": v(74.72, -77.46) * mm});
            skLineSegment(sketch, "E776", {"start": v(74.72, -77.46) * mm, "end": v(74.73, -77.42) * mm});
            skLineSegment(sketch, "E777", {"start": v(74.73, -77.42) * mm, "end": v(74.74, -77.38) * mm});
            skLineSegment(sketch, "E778", {"start": v(74.74, -77.38) * mm, "end": v(74.75, -77.34) * mm});
            skLineSegment(sketch, "E779", {"start": v(74.75, -77.34) * mm, "end": v(74.76, -77.3) * mm});
            skLineSegment(sketch, "E780", {"start": v(74.76, -77.3) * mm, "end": v(74.76, -77.25) * mm});
            skLineSegment(sketch, "E781", {"start": v(74.76, -77.25) * mm, "end": v(74.77, -77.2) * mm});
            skLineSegment(sketch, "E782", {"start": v(74.77, -77.2) * mm, "end": v(74.77, -77.17) * mm});
            skLineSegment(sketch, "E783", {"start": v(74.77, -77.17) * mm, "end": v(74.77, -77.12) * mm});
            skLineSegment(sketch, "E784", {"start": v(-2.73, -77.12) * mm, "end": v(-2.73, -77.08) * mm});
            skLineSegment(sketch, "E785", {"start": v(-2.73, -77.08) * mm, "end": v(-2.73, -77.04) * mm});
            skLineSegment(sketch, "E786", {"start": v(-2.73, -77.04) * mm, "end": v(-2.74, -77) * mm});
            skLineSegment(sketch, "E787", {"start": v(-2.74, -77) * mm, "end": v(-2.74, -76.95) * mm});
            skLineSegment(sketch, "E788", {"start": v(-2.74, -76.95) * mm, "end": v(-2.75, -76.9) * mm});
            skLineSegment(sketch, "E789", {"start": v(-2.75, -76.9) * mm, "end": v(-2.76, -76.86) * mm});
            skLineSegment(sketch, "E790", {"start": v(-2.77, -76.82) * mm, "end": v(-2.78, -76.78) * mm});
            skLineSegment(sketch, "E791", {"start": v(-2.78, -76.78) * mm, "end": v(-2.8, -76.74) * mm});
            skLineSegment(sketch, "E792", {"start": v(-2.8, -76.74) * mm, "end": v(-2.8, -76.7) * mm});
            skLineSegment(sketch, "E793", {"start": v(-2.82, -76.66) * mm, "end": v(-2.84, -76.62) * mm});
            skLineSegment(sketch, "E794", {"start": v(-2.84, -76.62) * mm, "end": v(-2.86, -76.58) * mm});
            skLineSegment(sketch, "E795", {"start": v(-2.86, -76.58) * mm, "end": v(-2.88, -76.54) * mm});
            skLineSegment(sketch, "E796", {"start": v(-2.88, -76.54) * mm, "end": v(-2.9, -76.5) * mm});
            skLineSegment(sketch, "E797", {"start": v(-2.9, -76.5) * mm, "end": v(-2.92, -76.46) * mm});
            skLineSegment(sketch, "E798", {"start": v(-2.92, -76.46) * mm, "end": v(-2.94, -76.43) * mm});
            skLineSegment(sketch, "E799", {"start": v(-2.94, -76.43) * mm, "end": v(-2.97, -76.4) * mm});
            skLineSegment(sketch, "E800", {"start": v(-2.97, -76.4) * mm, "end": v(-3, -76.36) * mm});
            skLineSegment(sketch, "E801", {"start": v(-3, -76.36) * mm, "end": v(-3.02, -76.32) * mm});
            skLineSegment(sketch, "E802", {"start": v(-3.02, -76.32) * mm, "end": v(-3.05, -76.29) * mm});
            skLineSegment(sketch, "E803", {"start": v(-3.05, -76.29) * mm, "end": v(-3.08, -76.26) * mm});
            skLineSegment(sketch, "E804", {"start": v(-3.08, -76.26) * mm, "end": v(-3.1, -76.23) * mm});
            skLineSegment(sketch, "E805", {"start": v(-3.1, -76.23) * mm, "end": v(-3.14, -76.2) * mm});
            skLineSegment(sketch, "E806", {"start": v(-3.14, -76.2) * mm, "end": v(-3.17, -76.17) * mm});
            skLineSegment(sketch, "E807", {"start": v(-3.17, -76.17) * mm, "end": v(-3.2, -76.14) * mm});
            skLineSegment(sketch, "E808", {"start": v(-3.2, -76.14) * mm, "end": v(-3.24, -76.11) * mm});
            skLineSegment(sketch, "E809", {"start": v(-3.24, -76.11) * mm, "end": v(-3.28, -76.09) * mm});
            skLineSegment(sketch, "E810", {"start": v(-3.28, -76.09) * mm, "end": v(-3.31, -76.07) * mm});
            skLineSegment(sketch, "E811", {"start": v(-3.35, -76.04) * mm, "end": v(-3.39, -76.02) * mm});
            skLineSegment(sketch, "E812", {"start": v(-3.39, -76.02) * mm, "end": v(-3.43, -76) * mm});
            skLineSegment(sketch, "E813", {"start": v(-3.47, -75.98) * mm, "end": v(-3.5, -75.97) * mm});
            skLineSegment(sketch, "E814", {"start": v(-3.5, -75.97) * mm, "end": v(-3.55, -75.95) * mm});
            skLineSegment(sketch, "E815", {"start": v(-3.55, -75.95) * mm, "end": v(-3.59, -75.94) * mm});
            skLineSegment(sketch, "E816", {"start": v(-3.59, -75.94) * mm, "end": v(-3.63, -75.92) * mm});
            skLineSegment(sketch, "E817", {"start": v(-3.63, -75.92) * mm, "end": v(-3.67, -75.91) * mm});
            skLineSegment(sketch, "E818", {"start": v(-3.67, -75.91) * mm, "end": v(-3.71, -75.9) * mm});
            skLineSegment(sketch, "E819", {"start": v(-3.71, -75.9) * mm, "end": v(-3.75, -75.9) * mm});
            skLineSegment(sketch, "E820", {"start": v(-3.84, -75.88) * mm, "end": v(-3.88, -75.88) * mm});
            skLineSegment(sketch, "E821", {"start": v(-3.88, -75.88) * mm, "end": v(-3.93, -75.87) * mm});
            skLineSegment(sketch, "E822", {"start": v(-3.93, -75.87) * mm, "end": v(-3.97, -75.87) * mm});
            skLineSegment(sketch, "E823", {"start": v(-3.97, -75.87) * mm, "end": v(-4.01, -75.87) * mm});
            skLineSegment(sketch, "E824", {"start": v(-4.01, -75.87) * mm, "end": v(-4.06, -75.87) * mm});
            skLineSegment(sketch, "E825", {"start": v(-4.06, -75.87) * mm, "end": v(-4.1, -75.88) * mm});
            skLineSegment(sketch, "E826", {"start": v(-4.1, -75.88) * mm, "end": v(-4.14, -75.88) * mm});
            skLineSegment(sketch, "E827", {"start": v(-4.14, -75.88) * mm, "end": v(-4.19, -75.89) * mm});
            skLineSegment(sketch, "E828", {"start": v(-4.19, -75.89) * mm, "end": v(-4.23, -75.9) * mm});
            skLineSegment(sketch, "E829", {"start": v(-4.23, -75.9) * mm, "end": v(-4.27, -75.9) * mm});
            skLineSegment(sketch, "E830", {"start": v(-4.27, -75.9) * mm, "end": v(-4.31, -75.92) * mm});
            skLineSegment(sketch, "E831", {"start": v(-4.31, -75.92) * mm, "end": v(-4.35, -75.93) * mm});
            skLineSegment(sketch, "E832", {"start": v(-4.35, -75.93) * mm, "end": v(-4.4, -75.94) * mm});
            skLineSegment(sketch, "E833", {"start": v(-4.4, -75.94) * mm, "end": v(-4.44, -75.96) * mm});
            skLineSegment(sketch, "E834", {"start": v(-4.44, -75.96) * mm, "end": v(-4.48, -75.97) * mm});
            skLineSegment(sketch, "E835", {"start": v(-4.48, -75.97) * mm, "end": v(-4.52, -76) * mm});
            skLineSegment(sketch, "E836", {"start": v(-4.52, -76) * mm, "end": v(-4.56, -76.01) * mm});
            skLineSegment(sketch, "E837", {"start": v(-4.56, -76.01) * mm, "end": v(-4.6, -76.03) * mm});
            skLineSegment(sketch, "E838", {"start": v(-4.6, -76.03) * mm, "end": v(-4.63, -76.05) * mm});
            skLineSegment(sketch, "E839", {"start": v(-4.63, -76.05) * mm, "end": v(-4.67, -76.08) * mm});
            skLineSegment(sketch, "E840", {"start": v(-4.67, -76.08) * mm, "end": v(-4.7, -76.1) * mm});
            skLineSegment(sketch, "E841", {"start": v(-4.7, -76.1) * mm, "end": v(-4.74, -76.13) * mm});
            skLineSegment(sketch, "E842", {"start": v(-4.74, -76.13) * mm, "end": v(-4.77, -76.15) * mm});
            skLineSegment(sketch, "E843", {"start": v(-4.77, -76.15) * mm, "end": v(-4.8, -76.18) * mm});
            skLineSegment(sketch, "E844", {"start": v(-4.8, -76.18) * mm, "end": v(-4.84, -76.21) * mm});
            skLineSegment(sketch, "E845", {"start": v(-4.84, -76.21) * mm, "end": v(-4.87, -76.24) * mm});
            skLineSegment(sketch, "E846", {"start": v(-4.87, -76.24) * mm, "end": v(-4.9, -76.27) * mm});
            skLineSegment(sketch, "E847", {"start": v(-4.9, -76.27) * mm, "end": v(-4.93, -76.3) * mm});
            skLineSegment(sketch, "E848", {"start": v(-4.93, -76.3) * mm, "end": v(-4.96, -76.34) * mm});
            skLineSegment(sketch, "E849", {"start": v(-4.96, -76.34) * mm, "end": v(-4.98, -76.37) * mm});
            skLineSegment(sketch, "E850", {"start": v(-4.98, -76.37) * mm, "end": v(-5, -76.4) * mm});
            skLineSegment(sketch, "E851", {"start": v(-5, -76.4) * mm, "end": v(-5.03, -76.44) * mm});
            skLineSegment(sketch, "E852", {"start": v(-5.03, -76.44) * mm, "end": v(-5.05, -76.48) * mm});
            skLineSegment(sketch, "E853", {"start": v(-5.05, -76.48) * mm, "end": v(-5.08, -76.52) * mm});
            skLineSegment(sketch, "E854", {"start": v(-5.08, -76.52) * mm, "end": v(-5.1, -76.56) * mm});
            skLineSegment(sketch, "E855", {"start": v(-5.1, -76.56) * mm, "end": v(-5.12, -76.6) * mm});
            skLineSegment(sketch, "E856", {"start": v(-5.12, -76.6) * mm, "end": v(-5.13, -76.64) * mm});
            skLineSegment(sketch, "E857", {"start": v(-5.13, -76.64) * mm, "end": v(-5.15, -76.68) * mm});
            skLineSegment(sketch, "E858", {"start": v(-5.15, -76.68) * mm, "end": v(-5.16, -76.72) * mm});
            skLineSegment(sketch, "E859", {"start": v(-5.18, -76.76) * mm, "end": v(-5.19, -76.8) * mm});
            skLineSegment(sketch, "E860", {"start": v(-5.19, -76.8) * mm, "end": v(-5.2, -76.84) * mm});
            skLineSegment(sketch, "E861", {"start": v(-5.2, -76.84) * mm, "end": v(-5.2, -76.88) * mm});
            skLineSegment(sketch, "E862", {"start": v(-5.2, -76.88) * mm, "end": v(-5.22, -76.93) * mm});
            skLineSegment(sketch, "E863", {"start": v(-5.22, -76.93) * mm, "end": v(-5.22, -76.97) * mm});
            skLineSegment(sketch, "E864", {"start": v(-5.22, -76.97) * mm, "end": v(-5.23, -77.01) * mm});
            skLineSegment(sketch, "E865", {"start": v(-5.23, -77.01) * mm, "end": v(-5.23, -77.06) * mm});
            skLineSegment(sketch, "E866", {"start": v(-5.23, -77.06) * mm, "end": v(-5.23, -77.1) * mm});
            skLineSegment(sketch, "E867", {"start": v(-5.23, -77.1) * mm, "end": v(-5.23, -77.14) * mm});
            skLineSegment(sketch, "E868", {"start": v(-5.23, -77.14) * mm, "end": v(-5.23, -77.19) * mm});
            skLineSegment(sketch, "E869", {"start": v(-5.23, -77.19) * mm, "end": v(-5.23, -77.23) * mm});
            skLineSegment(sketch, "E870", {"start": v(-5.23, -77.23) * mm, "end": v(-5.22, -77.27) * mm});
            skLineSegment(sketch, "E871", {"start": v(-5.22, -77.27) * mm, "end": v(-5.22, -77.32) * mm});
            skLineSegment(sketch, "E872", {"start": v(-5.22, -77.32) * mm, "end": v(-5.2, -77.36) * mm});
            skLineSegment(sketch, "E873", {"start": v(-5.2, -77.36) * mm, "end": v(-5.2, -77.4) * mm});
            skLineSegment(sketch, "E874", {"start": v(-5.2, -77.4) * mm, "end": v(-5.19, -77.44) * mm});
            skLineSegment(sketch, "E875", {"start": v(-5.19, -77.44) * mm, "end": v(-5.18, -77.49) * mm});
            skLineSegment(sketch, "E876", {"start": v(-5.18, -77.49) * mm, "end": v(-5.16, -77.53) * mm});
            skLineSegment(sketch, "E877", {"start": v(-5.16, -77.53) * mm, "end": v(-5.15, -77.57) * mm});
            skLineSegment(sketch, "E878", {"start": v(-5.15, -77.57) * mm, "end": v(-5.13, -77.6) * mm});
            skLineSegment(sketch, "E879", {"start": v(-5.13, -77.6) * mm, "end": v(-5.12, -77.65) * mm});
            skLineSegment(sketch, "E880", {"start": v(-5.12, -77.65) * mm, "end": v(-5.1, -77.69) * mm});
            skLineSegment(sketch, "E881", {"start": v(-5.1, -77.69) * mm, "end": v(-5.08, -77.72) * mm});
            skLineSegment(sketch, "E882", {"start": v(-5.08, -77.72) * mm, "end": v(-5.05, -77.76) * mm});
            skLineSegment(sketch, "E883", {"start": v(-5.05, -77.76) * mm, "end": v(-5.03, -77.8) * mm});
            skLineSegment(sketch, "E884", {"start": v(-5.03, -77.8) * mm, "end": v(-5, -77.84) * mm});
            skLineSegment(sketch, "E885", {"start": v(-5, -77.84) * mm, "end": v(-4.98, -77.87) * mm});
            skLineSegment(sketch, "E886", {"start": v(-4.98, -77.87) * mm, "end": v(-4.96, -77.9) * mm});
            skLineSegment(sketch, "E887", {"start": v(-4.96, -77.9) * mm, "end": v(-4.93, -77.94) * mm});
            skLineSegment(sketch, "E888", {"start": v(-4.93, -77.94) * mm, "end": v(-4.9, -77.97) * mm});
            skLineSegment(sketch, "E889", {"start": v(-4.9, -77.97) * mm, "end": v(-4.87, -78) * mm});
            skLineSegment(sketch, "E890", {"start": v(-4.87, -78) * mm, "end": v(-4.84, -78.03) * mm});
            skLineSegment(sketch, "E891", {"start": v(-4.84, -78.03) * mm, "end": v(-4.8, -78.06) * mm});
            skLineSegment(sketch, "E892", {"start": v(-4.8, -78.06) * mm, "end": v(-4.77, -78.09) * mm});
            skLineSegment(sketch, "E893", {"start": v(-4.77, -78.09) * mm, "end": v(-4.74, -78.12) * mm});
            skLineSegment(sketch, "E894", {"start": v(-4.74, -78.12) * mm, "end": v(-4.7, -78.14) * mm});
            skLineSegment(sketch, "E895", {"start": v(-4.35, -78.31) * mm, "end": v(-4.31, -78.33) * mm});
            skLineSegment(sketch, "E896", {"start": v(-4.31, -78.33) * mm, "end": v(-4.27, -78.34) * mm});
            skLineSegment(sketch, "E897", {"start": v(-4.27, -78.34) * mm, "end": v(-4.23, -78.35) * mm});
            skLineSegment(sketch, "E898", {"start": v(-4.23, -78.35) * mm, "end": v(-4.19, -78.35) * mm});
            skLineSegment(sketch, "E899", {"start": v(-4.1, -78.37) * mm, "end": v(-4.06, -78.37) * mm});
            skLineSegment(sketch, "E900", {"start": v(-4.06, -78.37) * mm, "end": v(-4.01, -78.37) * mm});
            skLineSegment(sketch, "E901", {"start": v(-4.01, -78.37) * mm, "end": v(-3.97, -78.37) * mm});
            skLineSegment(sketch, "E902", {"start": v(-3.97, -78.37) * mm, "end": v(-3.93, -78.37) * mm});
            skLineSegment(sketch, "E903", {"start": v(-3.93, -78.37) * mm, "end": v(-3.88, -78.37) * mm});
            skLineSegment(sketch, "E904", {"start": v(-3.84, -78.36) * mm, "end": v(-3.8, -78.36) * mm});
            skLineSegment(sketch, "E905", {"start": v(-3.8, -78.36) * mm, "end": v(-3.75, -78.35) * mm});
            skLineSegment(sketch, "E906", {"start": v(-3.75, -78.35) * mm, "end": v(-3.71, -78.34) * mm});
            skLineSegment(sketch, "E907", {"start": v(-3.71, -78.34) * mm, "end": v(-3.67, -78.33) * mm});
            skLineSegment(sketch, "E908", {"start": v(-3.67, -78.33) * mm, "end": v(-3.63, -78.32) * mm});
            skLineSegment(sketch, "E909", {"start": v(-3.63, -78.32) * mm, "end": v(-3.59, -78.3) * mm});
            skLineSegment(sketch, "E910", {"start": v(-3.59, -78.3) * mm, "end": v(-3.55, -78.3) * mm});
            skLineSegment(sketch, "E911", {"start": v(-3.55, -78.3) * mm, "end": v(-3.5, -78.28) * mm});
            skLineSegment(sketch, "E912", {"start": v(-3.5, -78.28) * mm, "end": v(-3.47, -78.26) * mm});
            skLineSegment(sketch, "E913", {"start": v(-3.47, -78.26) * mm, "end": v(-3.43, -78.24) * mm});
            skLineSegment(sketch, "E914", {"start": v(-3.43, -78.24) * mm, "end": v(-3.39, -78.22) * mm});
            skLineSegment(sketch, "E915", {"start": v(-3.39, -78.22) * mm, "end": v(-3.35, -78.2) * mm});
            skLineSegment(sketch, "E916", {"start": v(-3.35, -78.2) * mm, "end": v(-3.31, -78.18) * mm});
            skLineSegment(sketch, "E917", {"start": v(-3.31, -78.18) * mm, "end": v(-3.28, -78.15) * mm});
            skLineSegment(sketch, "E918", {"start": v(-3.28, -78.15) * mm, "end": v(-3.24, -78.13) * mm});
            skLineSegment(sketch, "E919", {"start": v(-3.24, -78.13) * mm, "end": v(-3.2, -78.1) * mm});
            skLineSegment(sketch, "E920", {"start": v(-3.2, -78.1) * mm, "end": v(-3.17, -78.08) * mm});
            skLineSegment(sketch, "E921", {"start": v(-3.17, -78.08) * mm, "end": v(-3.14, -78.05) * mm});
            skLineSegment(sketch, "E922", {"start": v(-3.14, -78.05) * mm, "end": v(-3.1, -78.02) * mm});
            skLineSegment(sketch, "E923", {"start": v(-3.1, -78.02) * mm, "end": v(-3.08, -77.99) * mm});
            skLineSegment(sketch, "E924", {"start": v(-3.08, -77.99) * mm, "end": v(-3.05, -77.95) * mm});
            skLineSegment(sketch, "E925", {"start": v(-3.05, -77.95) * mm, "end": v(-3.02, -77.92) * mm});
            skLineSegment(sketch, "E926", {"start": v(-3.02, -77.92) * mm, "end": v(-3, -77.89) * mm});
            skLineSegment(sketch, "E927", {"start": v(-3, -77.89) * mm, "end": v(-2.97, -77.85) * mm});
            skLineSegment(sketch, "E928", {"start": v(-2.97, -77.85) * mm, "end": v(-2.94, -77.82) * mm});
            skLineSegment(sketch, "E929", {"start": v(-2.94, -77.82) * mm, "end": v(-2.92, -77.78) * mm});
            skLineSegment(sketch, "E930", {"start": v(-2.92, -77.78) * mm, "end": v(-2.9, -77.74) * mm});
            skLineSegment(sketch, "E931", {"start": v(-2.9, -77.74) * mm, "end": v(-2.88, -77.7) * mm});
            skLineSegment(sketch, "E932", {"start": v(-2.88, -77.7) * mm, "end": v(-2.86, -77.67) * mm});
            skLineSegment(sketch, "E933", {"start": v(-2.86, -77.67) * mm, "end": v(-2.84, -77.63) * mm});
            skLineSegment(sketch, "E934", {"start": v(-2.84, -77.63) * mm, "end": v(-2.82, -77.59) * mm});
            skLineSegment(sketch, "E935", {"start": v(-2.82, -77.59) * mm, "end": v(-2.8, -77.55) * mm});
            skLineSegment(sketch, "E936", {"start": v(-2.8, -77.5) * mm, "end": v(-2.78, -77.46) * mm});
            skLineSegment(sketch, "E937", {"start": v(-2.78, -77.46) * mm, "end": v(-2.77, -77.42) * mm});
            skLineSegment(sketch, "E938", {"start": v(-2.77, -77.42) * mm, "end": v(-2.76, -77.38) * mm});
            skLineSegment(sketch, "E939", {"start": v(-2.76, -77.38) * mm, "end": v(-2.75, -77.34) * mm});
            skLineSegment(sketch, "E940", {"start": v(-2.75, -77.34) * mm, "end": v(-2.74, -77.3) * mm});
            skLineSegment(sketch, "E941", {"start": v(-2.74, -77.3) * mm, "end": v(-2.74, -77.25) * mm});
            skLineSegment(sketch, "E942", {"start": v(-2.74, -77.25) * mm, "end": v(-2.73, -77.2) * mm});
            skLineSegment(sketch, "E943", {"start": v(-2.73, -77.2) * mm, "end": v(-2.73, -77.17) * mm});
            skLineSegment(sketch, "E944", {"start": v(-2.73, -77.17) * mm, "end": v(-2.73, -77.12) * mm});
            skLineSegment(sketch, "E945", {"start": v(-2.73, -47.12) * mm, "end": v(-2.73, -47.08) * mm});
            skLineSegment(sketch, "E946", {"start": v(-2.73, -47.08) * mm, "end": v(-2.73, -47.04) * mm});
            skLineSegment(sketch, "E947", {"start": v(-2.73, -47.04) * mm, "end": v(-2.74, -47) * mm});
            skLineSegment(sketch, "E948", {"start": v(-2.74, -47) * mm, "end": v(-2.74, -46.95) * mm});
            skLineSegment(sketch, "E949", {"start": v(-2.74, -46.95) * mm, "end": v(-2.75, -46.9) * mm});
            skLineSegment(sketch, "E950", {"start": v(-2.75, -46.9) * mm, "end": v(-2.76, -46.86) * mm});
            skLineSegment(sketch, "E951", {"start": v(-2.76, -46.86) * mm, "end": v(-2.77, -46.82) * mm});
            skLineSegment(sketch, "E952", {"start": v(-2.77, -46.82) * mm, "end": v(-2.78, -46.78) * mm});
            skLineSegment(sketch, "E953", {"start": v(-2.78, -46.78) * mm, "end": v(-2.8, -46.74) * mm});
            skLineSegment(sketch, "E954", {"start": v(-2.8, -46.74) * mm, "end": v(-2.8, -46.7) * mm});
            skLineSegment(sketch, "E955", {"start": v(-2.8, -46.7) * mm, "end": v(-2.82, -46.66) * mm});
            skLineSegment(sketch, "E956", {"start": v(-2.82, -46.66) * mm, "end": v(-2.84, -46.62) * mm});
            skLineSegment(sketch, "E957", {"start": v(-2.84, -46.62) * mm, "end": v(-2.86, -46.58) * mm});
            skLineSegment(sketch, "E958", {"start": v(-2.86, -46.58) * mm, "end": v(-2.88, -46.54) * mm});
            skLineSegment(sketch, "E959", {"start": v(-2.88, -46.54) * mm, "end": v(-2.9, -46.5) * mm});
            skLineSegment(sketch, "E960", {"start": v(-2.9, -46.5) * mm, "end": v(-2.92, -46.46) * mm});
            skLineSegment(sketch, "E961", {"start": v(-2.92, -46.46) * mm, "end": v(-2.94, -46.43) * mm});
            skLineSegment(sketch, "E962", {"start": v(-2.94, -46.43) * mm, "end": v(-2.97, -46.4) * mm});
            skLineSegment(sketch, "E963", {"start": v(-2.97, -46.4) * mm, "end": v(-3, -46.36) * mm});
            skLineSegment(sketch, "E964", {"start": v(-3, -46.36) * mm, "end": v(-3.02, -46.32) * mm});
            skLineSegment(sketch, "E965", {"start": v(-3.02, -46.32) * mm, "end": v(-3.05, -46.29) * mm});
            skLineSegment(sketch, "E966", {"start": v(-3.05, -46.29) * mm, "end": v(-3.08, -46.26) * mm});
            skLineSegment(sketch, "E967", {"start": v(-3.08, -46.26) * mm, "end": v(-3.1, -46.23) * mm});
            skLineSegment(sketch, "E968", {"start": v(-3.1, -46.23) * mm, "end": v(-3.14, -46.2) * mm});
            skLineSegment(sketch, "E969", {"start": v(-3.14, -46.2) * mm, "end": v(-3.17, -46.17) * mm});
            skLineSegment(sketch, "E970", {"start": v(-3.17, -46.17) * mm, "end": v(-3.2, -46.14) * mm});
            skLineSegment(sketch, "E971", {"start": v(-3.2, -46.14) * mm, "end": v(-3.24, -46.11) * mm});
            skLineSegment(sketch, "E972", {"start": v(-3.24, -46.11) * mm, "end": v(-3.28, -46.09) * mm});
            skLineSegment(sketch, "E973", {"start": v(-3.28, -46.09) * mm, "end": v(-3.31, -46.07) * mm});
            skLineSegment(sketch, "E974", {"start": v(-3.31, -46.07) * mm, "end": v(-3.35, -46.04) * mm});
            skLineSegment(sketch, "E975", {"start": v(-3.35, -46.04) * mm, "end": v(-3.39, -46.02) * mm});
            skLineSegment(sketch, "E976", {"start": v(-3.39, -46.02) * mm, "end": v(-3.43, -46) * mm});
            skLineSegment(sketch, "E977", {"start": v(-3.43, -46) * mm, "end": v(-3.47, -45.98) * mm});
            skLineSegment(sketch, "E978", {"start": v(-3.5, -45.97) * mm, "end": v(-3.55, -45.95) * mm});
            skLineSegment(sketch, "E979", {"start": v(-3.55, -45.95) * mm, "end": v(-3.59, -45.94) * mm});
            skLineSegment(sketch, "E980", {"start": v(-3.59, -45.94) * mm, "end": v(-3.63, -45.92) * mm});
            skLineSegment(sketch, "E981", {"start": v(-3.63, -45.92) * mm, "end": v(-3.67, -45.91) * mm});
            skLineSegment(sketch, "E982", {"start": v(-3.67, -45.91) * mm, "end": v(-3.71, -45.9) * mm});
            skLineSegment(sketch, "E983", {"start": v(-3.75, -45.9) * mm, "end": v(-3.8, -45.89) * mm});
            skLineSegment(sketch, "E984", {"start": v(-3.8, -45.89) * mm, "end": v(-3.84, -45.88) * mm});
            skLineSegment(sketch, "E985", {"start": v(-3.84, -45.88) * mm, "end": v(-3.88, -45.88) * mm});
            skLineSegment(sketch, "E986", {"start": v(-3.88, -45.88) * mm, "end": v(-3.93, -45.87) * mm});
            skLineSegment(sketch, "E987", {"start": v(-3.93, -45.87) * mm, "end": v(-3.97, -45.87) * mm});
            skLineSegment(sketch, "E988", {"start": v(-3.97, -45.87) * mm, "end": v(-4.01, -45.87) * mm});
            skLineSegment(sketch, "E989", {"start": v(-4.01, -45.87) * mm, "end": v(-4.06, -45.87) * mm});
            skLineSegment(sketch, "E990", {"start": v(-4.06, -45.87) * mm, "end": v(-4.1, -45.88) * mm});
            skLineSegment(sketch, "E991", {"start": v(-4.1, -45.88) * mm, "end": v(-4.14, -45.88) * mm});
            skLineSegment(sketch, "E992", {"start": v(-4.14, -45.88) * mm, "end": v(-4.19, -45.89) * mm});
            skLineSegment(sketch, "E993", {"start": v(-4.19, -45.89) * mm, "end": v(-4.23, -45.9) * mm});
            skLineSegment(sketch, "E994", {"start": v(-4.27, -45.9) * mm, "end": v(-4.31, -45.92) * mm});
            skLineSegment(sketch, "E995", {"start": v(-4.44, -45.96) * mm, "end": v(-4.48, -45.97) * mm});
            skLineSegment(sketch, "E996", {"start": v(-4.48, -45.97) * mm, "end": v(-4.52, -46) * mm});
            skLineSegment(sketch, "E997", {"start": v(-4.52, -46) * mm, "end": v(-4.56, -46.01) * mm});
            skLineSegment(sketch, "E998", {"start": v(-4.56, -46.01) * mm, "end": v(-4.6, -46.03) * mm});
            skLineSegment(sketch, "E999", {"start": v(-4.6, -46.03) * mm, "end": v(-4.63, -46.05) * mm});
            skLineSegment(sketch, "E1000", {"start": v(-4.63, -46.05) * mm, "end": v(-4.67, -46.08) * mm});
            skLineSegment(sketch, "E1001", {"start": v(-4.67, -46.08) * mm, "end": v(-4.7, -46.1) * mm});
            skLineSegment(sketch, "E1002", {"start": v(-4.7, -46.1) * mm, "end": v(-4.74, -46.13) * mm});
            skLineSegment(sketch, "E1003", {"start": v(-4.8, -46.18) * mm, "end": v(-4.84, -46.21) * mm});
            skLineSegment(sketch, "E1004", {"start": v(-4.84, -46.21) * mm, "end": v(-4.87, -46.24) * mm});
            skLineSegment(sketch, "E1005", {"start": v(-4.87, -46.24) * mm, "end": v(-4.9, -46.27) * mm});
            skLineSegment(sketch, "E1006", {"start": v(-4.9, -46.27) * mm, "end": v(-4.93, -46.3) * mm});
            skLineSegment(sketch, "E1007", {"start": v(-4.93, -46.3) * mm, "end": v(-4.96, -46.34) * mm});
            skLineSegment(sketch, "E1008", {"start": v(-4.96, -46.34) * mm, "end": v(-4.98, -46.37) * mm});
            skLineSegment(sketch, "E1009", {"start": v(-4.98, -46.37) * mm, "end": v(-5, -46.4) * mm});
            skLineSegment(sketch, "E1010", {"start": v(-5, -46.4) * mm, "end": v(-5.03, -46.44) * mm});
            skLineSegment(sketch, "E1011", {"start": v(-5.03, -46.44) * mm, "end": v(-5.05, -46.48) * mm});
            skLineSegment(sketch, "E1012", {"start": v(-5.08, -46.52) * mm, "end": v(-5.1, -46.56) * mm});
            skLineSegment(sketch, "E1013", {"start": v(-5.1, -46.56) * mm, "end": v(-5.12, -46.6) * mm});
            skLineSegment(sketch, "E1014", {"start": v(-5.12, -46.6) * mm, "end": v(-5.13, -46.64) * mm});
            skLineSegment(sketch, "E1015", {"start": v(-5.13, -46.64) * mm, "end": v(-5.15, -46.68) * mm});
            skLineSegment(sketch, "E1016", {"start": v(-5.15, -46.68) * mm, "end": v(-5.16, -46.72) * mm});
            skLineSegment(sketch, "E1017", {"start": v(-5.16, -46.72) * mm, "end": v(-5.18, -46.76) * mm});
            skLineSegment(sketch, "E1018", {"start": v(-5.18, -46.76) * mm, "end": v(-5.19, -46.8) * mm});
            skLineSegment(sketch, "E1019", {"start": v(-5.19, -46.8) * mm, "end": v(-5.2, -46.84) * mm});
            skLineSegment(sketch, "E1020", {"start": v(-5.2, -46.84) * mm, "end": v(-5.2, -46.88) * mm});
            skLineSegment(sketch, "E1021", {"start": v(-5.2, -46.88) * mm, "end": v(-5.22, -46.93) * mm});
            skLineSegment(sketch, "E1022", {"start": v(-5.22, -46.93) * mm, "end": v(-5.22, -46.97) * mm});
            skLineSegment(sketch, "E1023", {"start": v(-5.22, -46.97) * mm, "end": v(-5.23, -47.01) * mm});
            skLineSegment(sketch, "E1024", {"start": v(-5.23, -47.01) * mm, "end": v(-5.23, -47.06) * mm});
            skLineSegment(sketch, "E1025", {"start": v(-5.23, -47.06) * mm, "end": v(-5.23, -47.1) * mm});
            skLineSegment(sketch, "E1026", {"start": v(-5.23, -47.1) * mm, "end": v(-5.23, -47.14) * mm});
            skLineSegment(sketch, "E1027", {"start": v(-5.23, -47.14) * mm, "end": v(-5.23, -47.19) * mm});
            skLineSegment(sketch, "E1028", {"start": v(-5.23, -47.19) * mm, "end": v(-5.23, -47.23) * mm});
            skLineSegment(sketch, "E1029", {"start": v(-5.23, -47.23) * mm, "end": v(-5.22, -47.27) * mm});
            skLineSegment(sketch, "E1030", {"start": v(-5.22, -47.27) * mm, "end": v(-5.22, -47.32) * mm});
            skLineSegment(sketch, "E1031", {"start": v(-5.2, -47.36) * mm, "end": v(-5.2, -47.4) * mm});
            skLineSegment(sketch, "E1032", {"start": v(-5.19, -47.44) * mm, "end": v(-5.18, -47.49) * mm});
            skLineSegment(sketch, "E1033", {"start": v(-5.18, -47.49) * mm, "end": v(-5.16, -47.53) * mm});
            skLineSegment(sketch, "E1034", {"start": v(-5.16, -47.53) * mm, "end": v(-5.15, -47.57) * mm});
            skLineSegment(sketch, "E1035", {"start": v(-5.15, -47.57) * mm, "end": v(-5.13, -47.6) * mm});
            skLineSegment(sketch, "E1036", {"start": v(-5.13, -47.6) * mm, "end": v(-5.12, -47.65) * mm});
            skLineSegment(sketch, "E1037", {"start": v(-5.12, -47.65) * mm, "end": v(-5.1, -47.69) * mm});
            skLineSegment(sketch, "E1038", {"start": v(-5.1, -47.69) * mm, "end": v(-5.08, -47.72) * mm});
            skLineSegment(sketch, "E1039", {"start": v(-5.08, -47.72) * mm, "end": v(-5.05, -47.76) * mm});
            skLineSegment(sketch, "E1040", {"start": v(-5.05, -47.76) * mm, "end": v(-5.03, -47.8) * mm});
            skLineSegment(sketch, "E1041", {"start": v(-5.03, -47.8) * mm, "end": v(-5, -47.84) * mm});
            skLineSegment(sketch, "E1042", {"start": v(-5, -47.84) * mm, "end": v(-4.98, -47.87) * mm});
            skLineSegment(sketch, "E1043", {"start": v(-4.98, -47.87) * mm, "end": v(-4.96, -47.9) * mm});
            skLineSegment(sketch, "E1044", {"start": v(-4.96, -47.9) * mm, "end": v(-4.93, -47.94) * mm});
            skLineSegment(sketch, "E1045", {"start": v(-4.93, -47.94) * mm, "end": v(-4.9, -47.97) * mm});
            skLineSegment(sketch, "E1046", {"start": v(-4.9, -47.97) * mm, "end": v(-4.87, -48) * mm});
            skLineSegment(sketch, "E1047", {"start": v(-4.87, -48) * mm, "end": v(-4.84, -48.03) * mm});
            skLineSegment(sketch, "E1048", {"start": v(-4.84, -48.03) * mm, "end": v(-4.8, -48.06) * mm});
            skLineSegment(sketch, "E1049", {"start": v(-4.8, -48.06) * mm, "end": v(-4.77, -48.09) * mm});
            skLineSegment(sketch, "E1050", {"start": v(-4.77, -48.09) * mm, "end": v(-4.74, -48.12) * mm});
            skLineSegment(sketch, "E1051", {"start": v(-4.74, -48.12) * mm, "end": v(-4.7, -48.14) * mm});
            skLineSegment(sketch, "E1052", {"start": v(-4.23, -48.35) * mm, "end": v(-4.19, -48.35) * mm});
            skLineSegment(sketch, "E1053", {"start": v(-4.19, -48.35) * mm, "end": v(-4.14, -48.36) * mm});
            skLineSegment(sketch, "E1054", {"start": v(-4.14, -48.36) * mm, "end": v(-4.1, -48.37) * mm});
            skLineSegment(sketch, "E1055", {"start": v(-4.1, -48.37) * mm, "end": v(-4.06, -48.37) * mm});
            skLineSegment(sketch, "E1056", {"start": v(-4.06, -48.37) * mm, "end": v(-4.01, -48.37) * mm});
            skLineSegment(sketch, "E1057", {"start": v(-4.01, -48.37) * mm, "end": v(-3.97, -48.37) * mm});
            skLineSegment(sketch, "E1058", {"start": v(-3.97, -48.37) * mm, "end": v(-3.93, -48.37) * mm});
            skLineSegment(sketch, "E1059", {"start": v(-3.93, -48.37) * mm, "end": v(-3.88, -48.37) * mm});
            skLineSegment(sketch, "E1060", {"start": v(-3.88, -48.37) * mm, "end": v(-3.84, -48.36) * mm});
            skLineSegment(sketch, "E1061", {"start": v(-3.8, -48.36) * mm, "end": v(-3.75, -48.35) * mm});
            skLineSegment(sketch, "E1062", {"start": v(-3.75, -48.35) * mm, "end": v(-3.71, -48.34) * mm});
            skLineSegment(sketch, "E1063", {"start": v(-3.71, -48.34) * mm, "end": v(-3.67, -48.33) * mm});
            skLineSegment(sketch, "E1064", {"start": v(-3.67, -48.33) * mm, "end": v(-3.63, -48.32) * mm});
            skLineSegment(sketch, "E1065", {"start": v(-3.5, -48.28) * mm, "end": v(-3.47, -48.26) * mm});
            skLineSegment(sketch, "E1066", {"start": v(-3.47, -48.26) * mm, "end": v(-3.43, -48.24) * mm});
            skLineSegment(sketch, "E1067", {"start": v(-3.43, -48.24) * mm, "end": v(-3.39, -48.22) * mm});
            skLineSegment(sketch, "E1068", {"start": v(-3.39, -48.22) * mm, "end": v(-3.35, -48.2) * mm});
            skLineSegment(sketch, "E1069", {"start": v(-3.35, -48.2) * mm, "end": v(-3.31, -48.18) * mm});
            skLineSegment(sketch, "E1070", {"start": v(-3.31, -48.18) * mm, "end": v(-3.28, -48.15) * mm});
            skLineSegment(sketch, "E1071", {"start": v(-3.28, -48.15) * mm, "end": v(-3.24, -48.13) * mm});
            skLineSegment(sketch, "E1072", {"start": v(-3.2, -48.1) * mm, "end": v(-3.17, -48.08) * mm});
            skLineSegment(sketch, "E1073", {"start": v(-3.17, -48.08) * mm, "end": v(-3.14, -48.05) * mm});
            skLineSegment(sketch, "E1074", {"start": v(-3.14, -48.05) * mm, "end": v(-3.1, -48.02) * mm});
            skLineSegment(sketch, "E1075", {"start": v(-3.1, -48.02) * mm, "end": v(-3.08, -47.99) * mm});
            skLineSegment(sketch, "E1076", {"start": v(-3.08, -47.99) * mm, "end": v(-3.05, -47.95) * mm});
            skLineSegment(sketch, "E1077", {"start": v(-3.05, -47.95) * mm, "end": v(-3.02, -47.92) * mm});
            skLineSegment(sketch, "E1078", {"start": v(-3.02, -47.92) * mm, "end": v(-3, -47.89) * mm});
            skLineSegment(sketch, "E1079", {"start": v(-3, -47.89) * mm, "end": v(-2.97, -47.85) * mm});
            skLineSegment(sketch, "E1080", {"start": v(-2.97, -47.85) * mm, "end": v(-2.94, -47.82) * mm});
            skLineSegment(sketch, "E1081", {"start": v(-2.94, -47.82) * mm, "end": v(-2.92, -47.78) * mm});
            skLineSegment(sketch, "E1082", {"start": v(-2.92, -47.78) * mm, "end": v(-2.9, -47.74) * mm});
            skLineSegment(sketch, "E1083", {"start": v(-2.9, -47.74) * mm, "end": v(-2.88, -47.7) * mm});
            skLineSegment(sketch, "E1084", {"start": v(-2.88, -47.7) * mm, "end": v(-2.86, -47.67) * mm});
            skLineSegment(sketch, "E1085", {"start": v(-2.86, -47.67) * mm, "end": v(-2.84, -47.63) * mm});
            skLineSegment(sketch, "E1086", {"start": v(-2.84, -47.63) * mm, "end": v(-2.82, -47.59) * mm});
            skLineSegment(sketch, "E1087", {"start": v(-2.82, -47.59) * mm, "end": v(-2.8, -47.55) * mm});
            skLineSegment(sketch, "E1088", {"start": v(-2.8, -47.55) * mm, "end": v(-2.8, -47.5) * mm});
            skLineSegment(sketch, "E1089", {"start": v(-2.8, -47.5) * mm, "end": v(-2.78, -47.46) * mm});
            skLineSegment(sketch, "E1090", {"start": v(-2.78, -47.46) * mm, "end": v(-2.77, -47.42) * mm});
            skLineSegment(sketch, "E1091", {"start": v(-2.77, -47.42) * mm, "end": v(-2.76, -47.38) * mm});
            skLineSegment(sketch, "E1092", {"start": v(-2.76, -47.38) * mm, "end": v(-2.75, -47.34) * mm});
            skLineSegment(sketch, "E1093", {"start": v(-2.74, -47.3) * mm, "end": v(-2.74, -47.25) * mm});
            skLineSegment(sketch, "E1094", {"start": v(-2.74, -47.25) * mm, "end": v(-2.73, -47.2) * mm});
            skLineSegment(sketch, "E1095", {"start": v(-2.73, -47.2) * mm, "end": v(-2.73, -47.17) * mm});
            skLineSegment(sketch, "E1096", {"start": v(-2.73, -47.17) * mm, "end": v(-2.73, -47.12) * mm});
            skLineSegment(sketch, "E1097", {"start": v(41.02, -47.12) * mm, "end": v(41.02, -47) * mm});
            skLineSegment(sketch, "E1098", {"start": v(41.02, -47) * mm, "end": v(41.01, -46.86) * mm});
            skLineSegment(sketch, "E1099", {"start": v(41.01, -46.86) * mm, "end": v(41, -46.73) * mm});
            skLineSegment(sketch, "E1100", {"start": v(41, -46.73) * mm, "end": v(40.98, -46.6) * mm});
            skLineSegment(sketch, "E1101", {"start": v(40.98, -46.6) * mm, "end": v(40.96, -46.47) * mm});
            skLineSegment(sketch, "E1102", {"start": v(40.96, -46.47) * mm, "end": v(40.94, -46.35) * mm});
            skLineSegment(sketch, "E1103", {"start": v(40.94, -46.35) * mm, "end": v(40.9, -46.22) * mm});
            skLineSegment(sketch, "E1104", {"start": v(40.9, -46.22) * mm, "end": v(40.88, -46.1) * mm});
            skLineSegment(sketch, "E1105", {"start": v(40.88, -46.1) * mm, "end": v(40.84, -45.97) * mm});
            skLineSegment(sketch, "E1106", {"start": v(40.84, -45.97) * mm, "end": v(40.8, -45.85) * mm});
            skLineSegment(sketch, "E1107", {"start": v(40.8, -45.85) * mm, "end": v(40.75, -45.72) * mm});
            skLineSegment(sketch, "E1108", {"start": v(40.64, -45.49) * mm, "end": v(40.58, -45.37) * mm});
            skLineSegment(sketch, "E1109", {"start": v(40.58, -45.37) * mm, "end": v(40.52, -45.26) * mm});
            skLineSegment(sketch, "E1110", {"start": v(40.52, -45.26) * mm, "end": v(40.46, -45.14) * mm});
            skLineSegment(sketch, "E1111", {"start": v(40.46, -45.14) * mm, "end": v(40.38, -45.04) * mm});
            skLineSegment(sketch, "E1112", {"start": v(40.38, -45.04) * mm, "end": v(40.31, -44.93) * mm});
            skLineSegment(sketch, "E1113", {"start": v(40.31, -44.93) * mm, "end": v(40.23, -44.82) * mm});
            skLineSegment(sketch, "E1114", {"start": v(40.23, -44.82) * mm, "end": v(40.15, -44.72) * mm});
            skLineSegment(sketch, "E1115", {"start": v(39.89, -44.44) * mm, "end": v(39.8, -44.35) * mm});
            skLineSegment(sketch, "E1116", {"start": v(39.8, -44.35) * mm, "end": v(39.7, -44.26) * mm});
            skLineSegment(sketch, "E1117", {"start": v(39.7, -44.26) * mm, "end": v(39.6, -44.18) * mm});
            skLineSegment(sketch, "E1118", {"start": v(39.6, -44.18) * mm, "end": v(39.49, -44.1) * mm});
            skLineSegment(sketch, "E1119", {"start": v(39.49, -44.1) * mm, "end": v(39.38, -44.02) * mm});
            skLineSegment(sketch, "E1120", {"start": v(39.16, -43.89) * mm, "end": v(39.05, -43.82) * mm});
            skLineSegment(sketch, "E1121", {"start": v(38.82, -43.7) * mm, "end": v(38.7, -43.65) * mm});
            skLineSegment(sketch, "E1122", {"start": v(38.7, -43.65) * mm, "end": v(38.58, -43.6) * mm});
            skLineSegment(sketch, "E1123", {"start": v(38.58, -43.6) * mm, "end": v(38.45, -43.56) * mm});
            skLineSegment(sketch, "E1124", {"start": v(38.45, -43.56) * mm, "end": v(38.33, -43.52) * mm});
            skLineSegment(sketch, "E1125", {"start": v(38.33, -43.52) * mm, "end": v(38.2, -43.49) * mm});
            skLineSegment(sketch, "E1126", {"start": v(38.08, -43.46) * mm, "end": v(37.95, -43.43) * mm});
            skLineSegment(sketch, "E1127", {"start": v(37.95, -43.43) * mm, "end": v(37.82, -43.41) * mm});
            skLineSegment(sketch, "E1128", {"start": v(37.82, -43.41) * mm, "end": v(37.7, -43.4) * mm});
            skLineSegment(sketch, "E1129", {"start": v(37.7, -43.4) * mm, "end": v(37.56, -43.38) * mm});
            skLineSegment(sketch, "E1130", {"start": v(37.56, -43.38) * mm, "end": v(37.43, -43.38) * mm});
            skLineSegment(sketch, "E1131", {"start": v(37.43, -43.38) * mm, "end": v(37.3, -43.37) * mm});
            skLineSegment(sketch, "E1132", {"start": v(37.3, -43.37) * mm, "end": v(37.17, -43.37) * mm});
            skLineSegment(sketch, "E1133", {"start": v(36.53, -43.45) * mm, "end": v(36.4, -43.47) * mm});
            skLineSegment(sketch, "E1134", {"start": v(36.4, -43.47) * mm, "end": v(36.27, -43.5) * mm});
            skLineSegment(sketch, "E1135", {"start": v(36.27, -43.5) * mm, "end": v(36.15, -43.54) * mm});
            skLineSegment(sketch, "E1136", {"start": v(36.15, -43.54) * mm, "end": v(36.02, -43.58) * mm});
            skLineSegment(sketch, "E1137", {"start": v(36.02, -43.58) * mm, "end": v(35.9, -43.63) * mm});
            skLineSegment(sketch, "E1138", {"start": v(35.9, -43.63) * mm, "end": v(35.78, -43.68) * mm});
            skLineSegment(sketch, "E1139", {"start": v(35.78, -43.68) * mm, "end": v(35.66, -43.73) * mm});
            skLineSegment(sketch, "E1140", {"start": v(35.66, -43.73) * mm, "end": v(35.55, -43.8) * mm});
            skLineSegment(sketch, "E1141", {"start": v(35.55, -43.8) * mm, "end": v(35.43, -43.85) * mm});
            skLineSegment(sketch, "E1142", {"start": v(35.43, -43.85) * mm, "end": v(35.32, -43.92) * mm});
            skLineSegment(sketch, "E1143", {"start": v(35.2, -43.99) * mm, "end": v(35.1, -44.06) * mm});
            skLineSegment(sketch, "E1144", {"start": v(35.1, -44.06) * mm, "end": v(35, -44.14) * mm});
            skLineSegment(sketch, "E1145", {"start": v(35, -44.14) * mm, "end": v(34.9, -44.22) * mm});
            skLineSegment(sketch, "E1146", {"start": v(34.9, -44.22) * mm, "end": v(34.8, -44.3) * mm});
            skLineSegment(sketch, "E1147", {"start": v(34.7, -44.4) * mm, "end": v(34.6, -44.48) * mm});
            skLineSegment(sketch, "E1148", {"start": v(34.6, -44.48) * mm, "end": v(34.52, -44.58) * mm});
            skLineSegment(sketch, "E1149", {"start": v(34.52, -44.58) * mm, "end": v(34.43, -44.67) * mm});
            skLineSegment(sketch, "E1150", {"start": v(34.43, -44.67) * mm, "end": v(34.35, -44.77) * mm});
            skLineSegment(sketch, "E1151", {"start": v(34.35, -44.77) * mm, "end": v(34.27, -44.88) * mm});
            skLineSegment(sketch, "E1152", {"start": v(34.19, -44.98) * mm, "end": v(34.12, -45.09) * mm});
            skLineSegment(sketch, "E1153", {"start": v(34.12, -45.09) * mm, "end": v(34.05, -45.2) * mm});
            skLineSegment(sketch, "E1154", {"start": v(34.05, -45.2) * mm, "end": v(33.98, -45.31) * mm});
            skLineSegment(sketch, "E1155", {"start": v(33.98, -45.31) * mm, "end": v(33.92, -45.43) * mm});
            skLineSegment(sketch, "E1156", {"start": v(33.92, -45.43) * mm, "end": v(33.87, -45.55) * mm});
            skLineSegment(sketch, "E1157", {"start": v(33.87, -45.55) * mm, "end": v(33.81, -45.66) * mm});
            skLineSegment(sketch, "E1158", {"start": v(33.77, -45.79) * mm, "end": v(33.72, -45.9) * mm});
            skLineSegment(sketch, "E1159", {"start": v(33.72, -45.9) * mm, "end": v(33.68, -46.03) * mm});
            skLineSegment(sketch, "E1160", {"start": v(33.68, -46.03) * mm, "end": v(33.65, -46.16) * mm});
            skLineSegment(sketch, "E1161", {"start": v(33.65, -46.16) * mm, "end": v(33.61, -46.28) * mm});
            skLineSegment(sketch, "E1162", {"start": v(33.61, -46.28) * mm, "end": v(33.59, -46.41) * mm});
            skLineSegment(sketch, "E1163", {"start": v(33.59, -46.41) * mm, "end": v(33.56, -46.54) * mm});
            skLineSegment(sketch, "E1164", {"start": v(33.56, -46.54) * mm, "end": v(33.55, -46.67) * mm});
            skLineSegment(sketch, "E1165", {"start": v(33.55, -46.67) * mm, "end": v(33.53, -46.8) * mm});
            skLineSegment(sketch, "E1166", {"start": v(33.53, -46.8) * mm, "end": v(33.52, -46.93) * mm});
            skLineSegment(sketch, "E1167", {"start": v(33.52, -46.93) * mm, "end": v(33.52, -47.06) * mm});
            skLineSegment(sketch, "E1168", {"start": v(33.52, -47.06) * mm, "end": v(33.52, -47.19) * mm});
            skLineSegment(sketch, "E1169", {"start": v(33.52, -47.19) * mm, "end": v(33.52, -47.32) * mm});
            skLineSegment(sketch, "E1170", {"start": v(33.61, -47.96) * mm, "end": v(33.65, -48.09) * mm});
            skLineSegment(sketch, "E1171", {"start": v(33.65, -48.09) * mm, "end": v(33.68, -48.21) * mm});
            skLineSegment(sketch, "E1172", {"start": v(33.68, -48.21) * mm, "end": v(33.72, -48.34) * mm});
            skLineSegment(sketch, "E1173", {"start": v(33.72, -48.34) * mm, "end": v(33.77, -48.46) * mm});
            skLineSegment(sketch, "E1174", {"start": v(33.77, -48.46) * mm, "end": v(33.81, -48.58) * mm});
            skLineSegment(sketch, "E1175", {"start": v(33.81, -48.58) * mm, "end": v(33.87, -48.7) * mm});
            skLineSegment(sketch, "E1176", {"start": v(33.87, -48.7) * mm, "end": v(33.92, -48.82) * mm});
            skLineSegment(sketch, "E1177", {"start": v(33.92, -48.82) * mm, "end": v(33.98, -48.93) * mm});
            skLineSegment(sketch, "E1178", {"start": v(34.12, -49.15) * mm, "end": v(34.19, -49.26) * mm});
            skLineSegment(sketch, "E1179", {"start": v(34.19, -49.26) * mm, "end": v(34.27, -49.37) * mm});
            skLineSegment(sketch, "E1180", {"start": v(34.27, -49.37) * mm, "end": v(34.35, -49.47) * mm});
            skLineSegment(sketch, "E1181", {"start": v(34.35, -49.47) * mm, "end": v(34.43, -49.57) * mm});
            skLineSegment(sketch, "E1182", {"start": v(34.43, -49.57) * mm, "end": v(34.52, -49.67) * mm});
            skLineSegment(sketch, "E1183", {"start": v(34.52, -49.67) * mm, "end": v(34.6, -49.76) * mm});
            skLineSegment(sketch, "E1184", {"start": v(34.9, -50.02) * mm, "end": v(35, -50.1) * mm});
            skLineSegment(sketch, "E1185", {"start": v(35, -50.1) * mm, "end": v(35.1, -50.18) * mm});
            skLineSegment(sketch, "E1186", {"start": v(35.1, -50.18) * mm, "end": v(35.2, -50.26) * mm});
            skLineSegment(sketch, "E1187", {"start": v(35.2, -50.26) * mm, "end": v(35.32, -50.33) * mm});
            skLineSegment(sketch, "E1188", {"start": v(35.32, -50.33) * mm, "end": v(35.43, -50.4) * mm});
            skLineSegment(sketch, "E1189", {"start": v(35.78, -50.56) * mm, "end": v(35.9, -50.61) * mm});
            skLineSegment(sketch, "E1190", {"start": v(35.9, -50.61) * mm, "end": v(36.02, -50.66) * mm});
            skLineSegment(sketch, "E1191", {"start": v(36.02, -50.66) * mm, "end": v(36.15, -50.7) * mm});
            skLineSegment(sketch, "E1192", {"start": v(36.15, -50.7) * mm, "end": v(36.27, -50.74) * mm});
            skLineSegment(sketch, "E1193", {"start": v(36.27, -50.74) * mm, "end": v(36.4, -50.77) * mm});
            skLineSegment(sketch, "E1194", {"start": v(36.4, -50.77) * mm, "end": v(36.53, -50.8) * mm});
            skLineSegment(sketch, "E1195", {"start": v(36.53, -50.8) * mm, "end": v(36.65, -50.82) * mm});
            skLineSegment(sketch, "E1196", {"start": v(36.65, -50.82) * mm, "end": v(36.78, -50.84) * mm});
            skLineSegment(sketch, "E1197", {"start": v(37.17, -50.87) * mm, "end": v(37.3, -50.87) * mm});
            skLineSegment(sketch, "E1198", {"start": v(37.3, -50.87) * mm, "end": v(37.43, -50.87) * mm});
            skLineSegment(sketch, "E1199", {"start": v(37.43, -50.87) * mm, "end": v(37.56, -50.86) * mm});
            skLineSegment(sketch, "E1200", {"start": v(37.56, -50.86) * mm, "end": v(37.7, -50.85) * mm});
            skLineSegment(sketch, "E1201", {"start": v(37.7, -50.85) * mm, "end": v(37.82, -50.83) * mm});
            skLineSegment(sketch, "E1202", {"start": v(37.82, -50.83) * mm, "end": v(37.95, -50.8) * mm});
            skLineSegment(sketch, "E1203", {"start": v(37.95, -50.8) * mm, "end": v(38.08, -50.78) * mm});
            skLineSegment(sketch, "E1204", {"start": v(38.08, -50.78) * mm, "end": v(38.2, -50.75) * mm});
            skLineSegment(sketch, "E1205", {"start": v(38.2, -50.75) * mm, "end": v(38.33, -50.72) * mm});
            skLineSegment(sketch, "E1206", {"start": v(38.45, -50.68) * mm, "end": v(38.58, -50.64) * mm});
            skLineSegment(sketch, "E1207", {"start": v(38.7, -50.59) * mm, "end": v(38.82, -50.54) * mm});
            skLineSegment(sketch, "E1208", {"start": v(38.82, -50.54) * mm, "end": v(38.93, -50.48) * mm});
            skLineSegment(sketch, "E1209", {"start": v(38.93, -50.48) * mm, "end": v(39.05, -50.42) * mm});
            skLineSegment(sketch, "E1210", {"start": v(39.05, -50.42) * mm, "end": v(39.16, -50.36) * mm});
            skLineSegment(sketch, "E1211", {"start": v(39.16, -50.36) * mm, "end": v(39.27, -50.3) * mm});
            skLineSegment(sketch, "E1212", {"start": v(39.27, -50.3) * mm, "end": v(39.38, -50.22) * mm});
            skLineSegment(sketch, "E1213", {"start": v(39.7, -49.98) * mm, "end": v(39.8, -49.9) * mm});
            skLineSegment(sketch, "E1214", {"start": v(39.8, -49.9) * mm, "end": v(39.89, -49.8) * mm});
            skLineSegment(sketch, "E1215", {"start": v(39.89, -49.8) * mm, "end": v(39.98, -49.72) * mm});
            skLineSegment(sketch, "E1216", {"start": v(39.98, -49.72) * mm, "end": v(40.07, -49.62) * mm});
            skLineSegment(sketch, "E1217", {"start": v(40.23, -49.42) * mm, "end": v(40.31, -49.32) * mm});
            skLineSegment(sketch, "E1218", {"start": v(40.31, -49.32) * mm, "end": v(40.38, -49.2) * mm});
            skLineSegment(sketch, "E1219", {"start": v(40.46, -49.1) * mm, "end": v(40.52, -48.99) * mm});
            skLineSegment(sketch, "E1220", {"start": v(40.52, -48.99) * mm, "end": v(40.58, -48.87) * mm});
            skLineSegment(sketch, "E1221", {"start": v(40.58, -48.87) * mm, "end": v(40.64, -48.76) * mm});
            skLineSegment(sketch, "E1222", {"start": v(40.64, -48.76) * mm, "end": v(40.7, -48.64) * mm});
            skLineSegment(sketch, "E1223", {"start": v(40.7, -48.64) * mm, "end": v(40.75, -48.52) * mm});
            skLineSegment(sketch, "E1224", {"start": v(40.75, -48.52) * mm, "end": v(40.8, -48.4) * mm});
            skLineSegment(sketch, "E1225", {"start": v(40.8, -48.4) * mm, "end": v(40.84, -48.27) * mm});
            skLineSegment(sketch, "E1226", {"start": v(40.84, -48.27) * mm, "end": v(40.88, -48.15) * mm});
            skLineSegment(sketch, "E1227", {"start": v(40.96, -47.77) * mm, "end": v(40.98, -47.64) * mm});
            skLineSegment(sketch, "E1228", {"start": v(41.01, -47.38) * mm, "end": v(41.02, -47.25) * mm});
            skLineSegment(sketch, "E1229", {"start": v(41.02, -47.25) * mm, "end": v(41.02, -47.12) * mm});
            skLineSegment(sketch, "E1230", {"start": v(41.02, 12.88) * mm, "end": v(41.02, 13) * mm});
            skLineSegment(sketch, "E1231", {"start": v(41.02, 13) * mm, "end": v(41.01, 13.14) * mm});
            skLineSegment(sketch, "E1232", {"start": v(41.01, 13.14) * mm, "end": v(41, 13.27) * mm});
            skLineSegment(sketch, "E1233", {"start": v(41, 13.27) * mm, "end": v(40.98, 13.4) * mm});
            skLineSegment(sketch, "E1234", {"start": v(40.98, 13.4) * mm, "end": v(40.96, 13.53) * mm});
            skLineSegment(sketch, "E1235", {"start": v(40.96, 13.53) * mm, "end": v(40.94, 13.65) * mm});
            skLineSegment(sketch, "E1236", {"start": v(40.94, 13.65) * mm, "end": v(40.9, 13.78) * mm});
            skLineSegment(sketch, "E1237", {"start": v(40.9, 13.78) * mm, "end": v(40.88, 13.9) * mm});
            skLineSegment(sketch, "E1238", {"start": v(40.88, 13.9) * mm, "end": v(40.84, 14.03) * mm});
            skLineSegment(sketch, "E1239", {"start": v(40.84, 14.03) * mm, "end": v(40.8, 14.15) * mm});
            skLineSegment(sketch, "E1240", {"start": v(40.7, 14.4) * mm, "end": v(40.64, 14.51) * mm});
            skLineSegment(sketch, "E1241", {"start": v(40.64, 14.51) * mm, "end": v(40.58, 14.63) * mm});
            skLineSegment(sketch, "E1242", {"start": v(40.58, 14.63) * mm, "end": v(40.52, 14.74) * mm});
            skLineSegment(sketch, "E1243", {"start": v(40.52, 14.74) * mm, "end": v(40.46, 14.86) * mm});
            skLineSegment(sketch, "E1244", {"start": v(40.46, 14.86) * mm, "end": v(40.38, 14.96) * mm});
            skLineSegment(sketch, "E1245", {"start": v(40.38, 14.96) * mm, "end": v(40.31, 15.07) * mm});
            skLineSegment(sketch, "E1246", {"start": v(39.98, 15.47) * mm, "end": v(39.89, 15.56) * mm});
            skLineSegment(sketch, "E1247", {"start": v(39.89, 15.56) * mm, "end": v(39.8, 15.65) * mm});
            skLineSegment(sketch, "E1248", {"start": v(39.8, 15.65) * mm, "end": v(39.7, 15.74) * mm});
            skLineSegment(sketch, "E1249", {"start": v(39.7, 15.74) * mm, "end": v(39.6, 15.82) * mm});
            skLineSegment(sketch, "E1250", {"start": v(39.38, 15.98) * mm, "end": v(39.27, 16.05) * mm});
            skLineSegment(sketch, "E1251", {"start": v(39.27, 16.05) * mm, "end": v(39.16, 16.11) * mm});
            skLineSegment(sketch, "E1252", {"start": v(39.16, 16.11) * mm, "end": v(39.05, 16.18) * mm});
            skLineSegment(sketch, "E1253", {"start": v(38.93, 16.24) * mm, "end": v(38.82, 16.3) * mm});
            skLineSegment(sketch, "E1254", {"start": v(38.82, 16.3) * mm, "end": v(38.7, 16.35) * mm});
            skLineSegment(sketch, "E1255", {"start": v(38.7, 16.35) * mm, "end": v(38.58, 16.4) * mm});
            skLineSegment(sketch, "E1256", {"start": v(38.58, 16.4) * mm, "end": v(38.45, 16.44) * mm});
            skLineSegment(sketch, "E1257", {"start": v(38.45, 16.44) * mm, "end": v(38.33, 16.48) * mm});
            skLineSegment(sketch, "E1258", {"start": v(38.2, 16.51) * mm, "end": v(38.08, 16.54) * mm});
            skLineSegment(sketch, "E1259", {"start": v(38.08, 16.54) * mm, "end": v(37.95, 16.57) * mm});
            skLineSegment(sketch, "E1260", {"start": v(37.95, 16.57) * mm, "end": v(37.82, 16.59) * mm});
            skLineSegment(sketch, "E1261", {"start": v(37.82, 16.59) * mm, "end": v(37.7, 16.6) * mm});
            skLineSegment(sketch, "E1262", {"start": v(37.7, 16.6) * mm, "end": v(37.56, 16.62) * mm});
            skLineSegment(sketch, "E1263", {"start": v(37.56, 16.62) * mm, "end": v(37.43, 16.62) * mm});
            skLineSegment(sketch, "E1264", {"start": v(37.43, 16.62) * mm, "end": v(37.3, 16.63) * mm});
            skLineSegment(sketch, "E1265", {"start": v(37.3, 16.63) * mm, "end": v(37.17, 16.63) * mm});
            skLineSegment(sketch, "E1266", {"start": v(36.78, 16.6) * mm, "end": v(36.65, 16.58) * mm});
            skLineSegment(sketch, "E1267", {"start": v(36.27, 16.5) * mm, "end": v(36.15, 16.46) * mm});
            skLineSegment(sketch, "E1268", {"start": v(36.15, 16.46) * mm, "end": v(36.02, 16.42) * mm});
            skLineSegment(sketch, "E1269", {"start": v(35.9, 16.37) * mm, "end": v(35.78, 16.32) * mm});
            skLineSegment(sketch, "E1270", {"start": v(35.78, 16.32) * mm, "end": v(35.66, 16.27) * mm});
            skLineSegment(sketch, "E1271", {"start": v(35.66, 16.27) * mm, "end": v(35.55, 16.2) * mm});
            skLineSegment(sketch, "E1272", {"start": v(35.55, 16.2) * mm, "end": v(35.43, 16.15) * mm});
            skLineSegment(sketch, "E1273", {"start": v(35.32, 16.08) * mm, "end": v(35.2, 16.01) * mm});
            skLineSegment(sketch, "E1274", {"start": v(35.1, 15.94) * mm, "end": v(35, 15.86) * mm});
            skLineSegment(sketch, "E1275", {"start": v(35, 15.86) * mm, "end": v(34.9, 15.78) * mm});
            skLineSegment(sketch, "E1276", {"start": v(34.9, 15.78) * mm, "end": v(34.8, 15.7) * mm});
            skLineSegment(sketch, "E1277", {"start": v(34.8, 15.7) * mm, "end": v(34.7, 15.6) * mm});
            skLineSegment(sketch, "E1278", {"start": v(34.7, 15.6) * mm, "end": v(34.6, 15.52) * mm});
            skLineSegment(sketch, "E1279", {"start": v(34.43, 15.33) * mm, "end": v(34.35, 15.23) * mm});
            skLineSegment(sketch, "E1280", {"start": v(34.27, 15.12) * mm, "end": v(34.19, 15.02) * mm});
            skLineSegment(sketch, "E1281", {"start": v(34.19, 15.02) * mm, "end": v(34.12, 14.91) * mm});
            skLineSegment(sketch, "E1282", {"start": v(34.12, 14.91) * mm, "end": v(34.05, 14.8) * mm});
            skLineSegment(sketch, "E1283", {"start": v(33.98, 14.69) * mm, "end": v(33.92, 14.57) * mm});
            skLineSegment(sketch, "E1284", {"start": v(33.92, 14.57) * mm, "end": v(33.87, 14.45) * mm});
            skLineSegment(sketch, "E1285", {"start": v(33.87, 14.45) * mm, "end": v(33.81, 14.34) * mm});
            skLineSegment(sketch, "E1286", {"start": v(33.77, 14.21) * mm, "end": v(33.72, 14.1) * mm});
            skLineSegment(sketch, "E1287", {"start": v(33.68, 13.97) * mm, "end": v(33.65, 13.84) * mm});
            skLineSegment(sketch, "E1288", {"start": v(33.65, 13.84) * mm, "end": v(33.61, 13.72) * mm});
            skLineSegment(sketch, "E1289", {"start": v(33.61, 13.72) * mm, "end": v(33.59, 13.59) * mm});
            skLineSegment(sketch, "E1290", {"start": v(33.59, 13.59) * mm, "end": v(33.56, 13.46) * mm});
            skLineSegment(sketch, "E1291", {"start": v(33.56, 13.46) * mm, "end": v(33.55, 13.33) * mm});
            skLineSegment(sketch, "E1292", {"start": v(33.55, 13.33) * mm, "end": v(33.53, 13.2) * mm});
            skLineSegment(sketch, "E1293", {"start": v(33.53, 13.2) * mm, "end": v(33.52, 13.07) * mm});
            skLineSegment(sketch, "E1294", {"start": v(33.52, 13.07) * mm, "end": v(33.52, 12.94) * mm});
            skLineSegment(sketch, "E1295", {"start": v(33.52, 12.94) * mm, "end": v(33.52, 12.81) * mm});
            skLineSegment(sketch, "E1296", {"start": v(33.52, 12.81) * mm, "end": v(33.52, 12.68) * mm});
            skLineSegment(sketch, "E1297", {"start": v(33.52, 12.68) * mm, "end": v(33.53, 12.55) * mm});
            skLineSegment(sketch, "E1298", {"start": v(33.53, 12.55) * mm, "end": v(33.55, 12.42) * mm});
            skLineSegment(sketch, "E1299", {"start": v(33.55, 12.42) * mm, "end": v(33.56, 12.3) * mm});
            skLineSegment(sketch, "E1300", {"start": v(33.59, 12.17) * mm, "end": v(33.61, 12.04) * mm});
            skLineSegment(sketch, "E1301", {"start": v(33.61, 12.04) * mm, "end": v(33.65, 11.91) * mm});
            skLineSegment(sketch, "E1302", {"start": v(33.68, 11.79) * mm, "end": v(33.72, 11.66) * mm});
            skLineSegment(sketch, "E1303", {"start": v(33.72, 11.66) * mm, "end": v(33.77, 11.54) * mm});
            skLineSegment(sketch, "E1304", {"start": v(33.77, 11.54) * mm, "end": v(33.81, 11.42) * mm});
            skLineSegment(sketch, "E1305", {"start": v(33.81, 11.42) * mm, "end": v(33.87, 11.3) * mm});
            skLineSegment(sketch, "E1306", {"start": v(33.87, 11.3) * mm, "end": v(33.92, 11.18) * mm});
            skLineSegment(sketch, "E1307", {"start": v(33.92, 11.18) * mm, "end": v(33.98, 11.07) * mm});
            skLineSegment(sketch, "E1308", {"start": v(34.12, 10.85) * mm, "end": v(34.19, 10.74) * mm});
            skLineSegment(sketch, "E1309", {"start": v(34.19, 10.74) * mm, "end": v(34.27, 10.63) * mm});
            skLineSegment(sketch, "E1310", {"start": v(34.35, 10.53) * mm, "end": v(34.43, 10.43) * mm});
            skLineSegment(sketch, "E1311", {"start": v(34.43, 10.43) * mm, "end": v(34.52, 10.33) * mm});
            skLineSegment(sketch, "E1312", {"start": v(34.52, 10.33) * mm, "end": v(34.6, 10.24) * mm});
            skLineSegment(sketch, "E1313", {"start": v(34.9, 9.98) * mm, "end": v(35, 9.9) * mm});
            skLineSegment(sketch, "E1314", {"start": v(35, 9.9) * mm, "end": v(35.1, 9.82) * mm});
            skLineSegment(sketch, "E1315", {"start": v(35.1, 9.82) * mm, "end": v(35.2, 9.74) * mm});
            skLineSegment(sketch, "E1316", {"start": v(35.2, 9.74) * mm, "end": v(35.32, 9.67) * mm});
            skLineSegment(sketch, "E1317", {"start": v(35.32, 9.67) * mm, "end": v(35.43, 9.6) * mm});
            skLineSegment(sketch, "E1318", {"start": v(35.43, 9.6) * mm, "end": v(35.55, 9.55) * mm});
            skLineSegment(sketch, "E1319", {"start": v(35.66, 9.49) * mm, "end": v(35.78, 9.44) * mm});
            skLineSegment(sketch, "E1320", {"start": v(35.9, 9.39) * mm, "end": v(36.02, 9.34) * mm});
            skLineSegment(sketch, "E1321", {"start": v(36.02, 9.34) * mm, "end": v(36.15, 9.3) * mm});
            skLineSegment(sketch, "E1322", {"start": v(36.15, 9.3) * mm, "end": v(36.27, 9.26) * mm});
            skLineSegment(sketch, "E1323", {"start": v(36.27, 9.26) * mm, "end": v(36.4, 9.23) * mm});
            skLineSegment(sketch, "E1324", {"start": v(36.4, 9.23) * mm, "end": v(36.53, 9.2) * mm});
            skLineSegment(sketch, "E1325", {"start": v(36.53, 9.2) * mm, "end": v(36.65, 9.18) * mm});
            skLineSegment(sketch, "E1326", {"start": v(36.65, 9.18) * mm, "end": v(36.78, 9.16) * mm});
            skLineSegment(sketch, "E1327", {"start": v(37.17, 9.13) * mm, "end": v(37.3, 9.13) * mm});
            skLineSegment(sketch, "E1328", {"start": v(37.3, 9.13) * mm, "end": v(37.43, 9.13) * mm});
            skLineSegment(sketch, "E1329", {"start": v(37.43, 9.13) * mm, "end": v(37.56, 9.14) * mm});
            skLineSegment(sketch, "E1330", {"start": v(37.56, 9.14) * mm, "end": v(37.7, 9.15) * mm});
            skLineSegment(sketch, "E1331", {"start": v(37.7, 9.15) * mm, "end": v(37.82, 9.17) * mm});
            skLineSegment(sketch, "E1332", {"start": v(37.82, 9.17) * mm, "end": v(37.95, 9.2) * mm});
            skLineSegment(sketch, "E1333", {"start": v(37.95, 9.2) * mm, "end": v(38.08, 9.22) * mm});
            skLineSegment(sketch, "E1334", {"start": v(38.08, 9.22) * mm, "end": v(38.2, 9.25) * mm});
            skLineSegment(sketch, "E1335", {"start": v(38.33, 9.28) * mm, "end": v(38.45, 9.32) * mm});
            skLineSegment(sketch, "E1336", {"start": v(38.45, 9.32) * mm, "end": v(38.58, 9.36) * mm});
            skLineSegment(sketch, "E1337", {"start": v(38.58, 9.36) * mm, "end": v(38.7, 9.41) * mm});
            skLineSegment(sketch, "E1338", {"start": v(38.82, 9.46) * mm, "end": v(38.93, 9.52) * mm});
            skLineSegment(sketch, "E1339", {"start": v(38.93, 9.52) * mm, "end": v(39.05, 9.58) * mm});
            skLineSegment(sketch, "E1340", {"start": v(39.05, 9.58) * mm, "end": v(39.16, 9.64) * mm});
            skLineSegment(sketch, "E1341", {"start": v(39.89, 10.2) * mm, "end": v(39.98, 10.28) * mm});
            skLineSegment(sketch, "E1342", {"start": v(39.98, 10.28) * mm, "end": v(40.07, 10.38) * mm});
            skLineSegment(sketch, "E1343", {"start": v(40.07, 10.38) * mm, "end": v(40.15, 10.48) * mm});
            skLineSegment(sketch, "E1344", {"start": v(40.15, 10.48) * mm, "end": v(40.23, 10.58) * mm});
            skLineSegment(sketch, "E1345", {"start": v(40.23, 10.58) * mm, "end": v(40.31, 10.68) * mm});
            skLineSegment(sketch, "E1346", {"start": v(40.31, 10.68) * mm, "end": v(40.38, 10.8) * mm});
            skLineSegment(sketch, "E1347", {"start": v(40.38, 10.8) * mm, "end": v(40.46, 10.9) * mm});
            skLineSegment(sketch, "E1348", {"start": v(40.46, 10.9) * mm, "end": v(40.52, 11.01) * mm});
            skLineSegment(sketch, "E1349", {"start": v(40.52, 11.01) * mm, "end": v(40.58, 11.13) * mm});
            skLineSegment(sketch, "E1350", {"start": v(40.58, 11.13) * mm, "end": v(40.64, 11.24) * mm});
            skLineSegment(sketch, "E1351", {"start": v(40.64, 11.24) * mm, "end": v(40.7, 11.36) * mm});
            skLineSegment(sketch, "E1352", {"start": v(40.7, 11.36) * mm, "end": v(40.75, 11.48) * mm});
            skLineSegment(sketch, "E1353", {"start": v(40.8, 11.6) * mm, "end": v(40.84, 11.73) * mm});
            skLineSegment(sketch, "E1354", {"start": v(40.84, 11.73) * mm, "end": v(40.88, 11.85) * mm});
            skLineSegment(sketch, "E1355", {"start": v(40.88, 11.85) * mm, "end": v(40.9, 11.98) * mm});
            skLineSegment(sketch, "E1356", {"start": v(40.96, 12.23) * mm, "end": v(40.98, 12.36) * mm});
            skLineSegment(sketch, "E1357", {"start": v(40.98, 12.36) * mm, "end": v(41, 12.49) * mm});
            skLineSegment(sketch, "E1358", {"start": v(41.01, 12.62) * mm, "end": v(41.02, 12.75) * mm});
            skLineSegment(sketch, "E1359", {"start": v(41.02, 12.75) * mm, "end": v(41.02, 12.88) * mm});
            skLineSegment(sketch, "E1360", {"start": v(69.42, -87.12) * mm, "end": v(69.42, -87.05) * mm});
            skLineSegment(sketch, "E1361", {"start": v(69.42, -87.05) * mm, "end": v(69.41, -86.97) * mm});
            skLineSegment(sketch, "E1362", {"start": v(69.41, -86.97) * mm, "end": v(69.4, -86.9) * mm});
            skLineSegment(sketch, "E1363", {"start": v(69.4, -86.9) * mm, "end": v(69.4, -86.82) * mm});
            skLineSegment(sketch, "E1364", {"start": v(69.4, -86.82) * mm, "end": v(69.39, -86.75) * mm});
            skLineSegment(sketch, "E1365", {"start": v(69.39, -86.75) * mm, "end": v(69.37, -86.68) * mm});
            skLineSegment(sketch, "E1366", {"start": v(69.37, -86.68) * mm, "end": v(69.36, -86.6) * mm});
            skLineSegment(sketch, "E1367", {"start": v(69.36, -86.6) * mm, "end": v(69.34, -86.53) * mm});
            skLineSegment(sketch, "E1368", {"start": v(69.31, -86.46) * mm, "end": v(69.3, -86.4) * mm});
            skLineSegment(sketch, "E1369", {"start": v(69.3, -86.4) * mm, "end": v(69.26, -86.32) * mm});
            skLineSegment(sketch, "E1370", {"start": v(69.26, -86.32) * mm, "end": v(69.24, -86.25) * mm});
            skLineSegment(sketch, "E1371", {"start": v(69.24, -86.25) * mm, "end": v(69.2, -86.18) * mm});
            skLineSegment(sketch, "E1372", {"start": v(69.2, -86.18) * mm, "end": v(69.17, -86.12) * mm});
            skLineSegment(sketch, "E1373", {"start": v(69.17, -86.12) * mm, "end": v(69.13, -86.05) * mm});
            skLineSegment(sketch, "E1374", {"start": v(69.13, -86.05) * mm, "end": v(69.1, -85.99) * mm});
            skLineSegment(sketch, "E1375", {"start": v(69.1, -85.99) * mm, "end": v(69.06, -85.93) * mm});
            skLineSegment(sketch, "E1376", {"start": v(69.06, -85.93) * mm, "end": v(69.01, -85.86) * mm});
            skLineSegment(sketch, "E1377", {"start": v(69.01, -85.86) * mm, "end": v(68.97, -85.8) * mm});
            skLineSegment(sketch, "E1378", {"start": v(68.97, -85.8) * mm, "end": v(68.92, -85.75) * mm});
            skLineSegment(sketch, "E1379", {"start": v(68.92, -85.75) * mm, "end": v(68.87, -85.69) * mm});
            skLineSegment(sketch, "E1380", {"start": v(68.87, -85.69) * mm, "end": v(68.82, -85.63) * mm});
            skLineSegment(sketch, "E1381", {"start": v(68.82, -85.63) * mm, "end": v(68.77, -85.58) * mm});
            skLineSegment(sketch, "E1382", {"start": v(68.77, -85.58) * mm, "end": v(68.72, -85.53) * mm});
            skLineSegment(sketch, "E1383", {"start": v(68.6, -85.43) * mm, "end": v(68.54, -85.39) * mm});
            skLineSegment(sketch, "E1384", {"start": v(68.54, -85.39) * mm, "end": v(68.48, -85.35) * mm});
            skLineSegment(sketch, "E1385", {"start": v(68.48, -85.35) * mm, "end": v(68.42, -85.3) * mm});
            skLineSegment(sketch, "E1386", {"start": v(68.29, -85.23) * mm, "end": v(68.22, -85.2) * mm});
            skLineSegment(sketch, "E1387", {"start": v(68.22, -85.2) * mm, "end": v(68.16, -85.16) * mm});
            skLineSegment(sketch, "E1388", {"start": v(68.16, -85.16) * mm, "end": v(68.09, -85.13) * mm});
            skLineSegment(sketch, "E1389", {"start": v(68.09, -85.13) * mm, "end": v(68.02, -85.1) * mm});
            skLineSegment(sketch, "E1390", {"start": v(68.02, -85.1) * mm, "end": v(67.95, -85.08) * mm});
            skLineSegment(sketch, "E1391", {"start": v(67.95, -85.08) * mm, "end": v(67.88, -85.06) * mm});
            skLineSegment(sketch, "E1392", {"start": v(67.88, -85.06) * mm, "end": v(67.8, -85.04) * mm});
            skLineSegment(sketch, "E1393", {"start": v(67.8, -85.04) * mm, "end": v(67.73, -85.02) * mm});
            skLineSegment(sketch, "E1394", {"start": v(67.73, -85.02) * mm, "end": v(67.66, -85) * mm});
            skLineSegment(sketch, "E1395", {"start": v(67.66, -85) * mm, "end": v(67.59, -85) * mm});
            skLineSegment(sketch, "E1396", {"start": v(67.59, -85) * mm, "end": v(67.51, -84.99) * mm});
            skLineSegment(sketch, "E1397", {"start": v(67.51, -84.99) * mm, "end": v(67.44, -84.98) * mm});
            skLineSegment(sketch, "E1398", {"start": v(67.44, -84.98) * mm, "end": v(67.36, -84.97) * mm});
            skLineSegment(sketch, "E1399", {"start": v(67.36, -84.97) * mm, "end": v(67.29, -84.97) * mm});
            skLineSegment(sketch, "E1400", {"start": v(67.29, -84.97) * mm, "end": v(67.21, -84.97) * mm});
            skLineSegment(sketch, "E1401", {"start": v(67.21, -84.97) * mm, "end": v(67.14, -84.98) * mm});
            skLineSegment(sketch, "E1402", {"start": v(67.14, -84.98) * mm, "end": v(67.06, -84.98) * mm});
            skLineSegment(sketch, "E1403", {"start": v(67.06, -84.98) * mm, "end": v(66.99, -85) * mm});
            skLineSegment(sketch, "E1404", {"start": v(66.99, -85) * mm, "end": v(66.92, -85) * mm});
            skLineSegment(sketch, "E1405", {"start": v(66.92, -85) * mm, "end": v(66.84, -85.01) * mm});
            skLineSegment(sketch, "E1406", {"start": v(66.84, -85.01) * mm, "end": v(66.77, -85.03) * mm});
            skLineSegment(sketch, "E1407", {"start": v(66.77, -85.03) * mm, "end": v(66.7, -85.05) * mm});
            skLineSegment(sketch, "E1408", {"start": v(66.7, -85.05) * mm, "end": v(66.63, -85.07) * mm});
            skLineSegment(sketch, "E1409", {"start": v(66.63, -85.07) * mm, "end": v(66.56, -85.1) * mm});
            skLineSegment(sketch, "E1410", {"start": v(66.56, -85.1) * mm, "end": v(66.49, -85.12) * mm});
            skLineSegment(sketch, "E1411", {"start": v(66.42, -85.15) * mm, "end": v(66.35, -85.18) * mm});
            skLineSegment(sketch, "E1412", {"start": v(66.35, -85.18) * mm, "end": v(66.28, -85.21) * mm});
            skLineSegment(sketch, "E1413", {"start": v(66.28, -85.21) * mm, "end": v(66.22, -85.25) * mm});
            skLineSegment(sketch, "E1414", {"start": v(66.22, -85.25) * mm, "end": v(66.15, -85.29) * mm});
            skLineSegment(sketch, "E1415", {"start": v(66.15, -85.29) * mm, "end": v(66.09, -85.33) * mm});
            skLineSegment(sketch, "E1416", {"start": v(66.09, -85.33) * mm, "end": v(66.03, -85.37) * mm});
            skLineSegment(sketch, "E1417", {"start": v(66.03, -85.37) * mm, "end": v(65.97, -85.41) * mm});
            skLineSegment(sketch, "E1418", {"start": v(65.97, -85.41) * mm, "end": v(65.9, -85.46) * mm});
            skLineSegment(sketch, "E1419", {"start": v(65.9, -85.46) * mm, "end": v(65.85, -85.5) * mm});
            skLineSegment(sketch, "E1420", {"start": v(65.46, -85.96) * mm, "end": v(65.42, -86.02) * mm});
            skLineSegment(sketch, "E1421", {"start": v(65.42, -86.02) * mm, "end": v(65.39, -86.08) * mm});
            skLineSegment(sketch, "E1422", {"start": v(65.39, -86.08) * mm, "end": v(65.35, -86.15) * mm});
            skLineSegment(sketch, "E1423", {"start": v(65.35, -86.15) * mm, "end": v(65.32, -86.22) * mm});
            skLineSegment(sketch, "E1424", {"start": v(65.32, -86.22) * mm, "end": v(65.29, -86.29) * mm});
            skLineSegment(sketch, "E1425", {"start": v(65.29, -86.29) * mm, "end": v(65.26, -86.36) * mm});
            skLineSegment(sketch, "E1426", {"start": v(65.23, -86.43) * mm, "end": v(65.21, -86.5) * mm});
            skLineSegment(sketch, "E1427", {"start": v(65.21, -86.5) * mm, "end": v(65.2, -86.57) * mm});
            skLineSegment(sketch, "E1428", {"start": v(65.2, -86.57) * mm, "end": v(65.17, -86.64) * mm});
            skLineSegment(sketch, "E1429", {"start": v(65.17, -86.64) * mm, "end": v(65.16, -86.71) * mm});
            skLineSegment(sketch, "E1430", {"start": v(65.16, -86.71) * mm, "end": v(65.15, -86.79) * mm});
            skLineSegment(sketch, "E1431", {"start": v(65.15, -86.79) * mm, "end": v(65.13, -86.86) * mm});
            skLineSegment(sketch, "E1432", {"start": v(65.13, -86.86) * mm, "end": v(65.13, -86.94) * mm});
            skLineSegment(sketch, "E1433", {"start": v(65.13, -86.94) * mm, "end": v(65.12, -87) * mm});
            skLineSegment(sketch, "E1434", {"start": v(65.12, -87) * mm, "end": v(65.12, -87.08) * mm});
            skLineSegment(sketch, "E1435", {"start": v(65.12, -87.08) * mm, "end": v(65.12, -87.16) * mm});
            skLineSegment(sketch, "E1436", {"start": v(65.12, -87.16) * mm, "end": v(65.12, -87.23) * mm});
            skLineSegment(sketch, "E1437", {"start": v(65.12, -87.23) * mm, "end": v(65.13, -87.3) * mm});
            skLineSegment(sketch, "E1438", {"start": v(65.13, -87.3) * mm, "end": v(65.13, -87.38) * mm});
            skLineSegment(sketch, "E1439", {"start": v(65.13, -87.38) * mm, "end": v(65.15, -87.46) * mm});
            skLineSegment(sketch, "E1440", {"start": v(65.15, -87.46) * mm, "end": v(65.16, -87.53) * mm});
            skLineSegment(sketch, "E1441", {"start": v(65.16, -87.53) * mm, "end": v(65.17, -87.6) * mm});
            skLineSegment(sketch, "E1442", {"start": v(65.2, -87.68) * mm, "end": v(65.21, -87.75) * mm});
            skLineSegment(sketch, "E1443", {"start": v(65.21, -87.75) * mm, "end": v(65.23, -87.82) * mm});
            skLineSegment(sketch, "E1444", {"start": v(65.35, -88.1) * mm, "end": v(65.39, -88.16) * mm});
            skLineSegment(sketch, "E1445", {"start": v(65.39, -88.16) * mm, "end": v(65.42, -88.22) * mm});
            skLineSegment(sketch, "E1446", {"start": v(65.46, -88.29) * mm, "end": v(65.5, -88.35) * mm});
            skLineSegment(sketch, "E1447", {"start": v(65.5, -88.35) * mm, "end": v(65.55, -88.4) * mm});
            skLineSegment(sketch, "E1448", {"start": v(65.55, -88.4) * mm, "end": v(65.6, -88.47) * mm});
            skLineSegment(sketch, "E1449", {"start": v(65.74, -88.64) * mm, "end": v(65.8, -88.69) * mm});
            skLineSegment(sketch, "E1450", {"start": v(65.8, -88.69) * mm, "end": v(65.85, -88.74) * mm});
            skLineSegment(sketch, "E1451", {"start": v(65.85, -88.74) * mm, "end": v(65.9, -88.79) * mm});
            skLineSegment(sketch, "E1452", {"start": v(65.9, -88.79) * mm, "end": v(65.97, -88.83) * mm});
            skLineSegment(sketch, "E1453", {"start": v(65.97, -88.83) * mm, "end": v(66.03, -88.88) * mm});
            skLineSegment(sketch, "E1454", {"start": v(66.03, -88.88) * mm, "end": v(66.09, -88.92) * mm});
            skLineSegment(sketch, "E1455", {"start": v(66.09, -88.92) * mm, "end": v(66.15, -88.96) * mm});
            skLineSegment(sketch, "E1456", {"start": v(66.15, -88.96) * mm, "end": v(66.22, -89) * mm});
            skLineSegment(sketch, "E1457", {"start": v(66.22, -89) * mm, "end": v(66.28, -89.03) * mm});
            skLineSegment(sketch, "E1458", {"start": v(66.35, -89.06) * mm, "end": v(66.42, -89.1) * mm});
            skLineSegment(sketch, "E1459", {"start": v(66.42, -89.1) * mm, "end": v(66.49, -89.12) * mm});
            skLineSegment(sketch, "E1460", {"start": v(66.49, -89.12) * mm, "end": v(66.56, -89.15) * mm});
            skLineSegment(sketch, "E1461", {"start": v(66.56, -89.15) * mm, "end": v(66.63, -89.17) * mm});
            skLineSegment(sketch, "E1462", {"start": v(66.63, -89.17) * mm, "end": v(66.7, -89.2) * mm});
            skLineSegment(sketch, "E1463", {"start": v(66.7, -89.2) * mm, "end": v(66.77, -89.21) * mm});
            skLineSegment(sketch, "E1464", {"start": v(66.77, -89.21) * mm, "end": v(66.84, -89.23) * mm});
            skLineSegment(sketch, "E1465", {"start": v(66.84, -89.23) * mm, "end": v(66.92, -89.24) * mm});
            skLineSegment(sketch, "E1466", {"start": v(66.92, -89.24) * mm, "end": v(66.99, -89.25) * mm});
            skLineSegment(sketch, "E1467", {"start": v(66.99, -89.25) * mm, "end": v(67.06, -89.26) * mm});
            skLineSegment(sketch, "E1468", {"start": v(67.06, -89.26) * mm, "end": v(67.14, -89.27) * mm});
            skLineSegment(sketch, "E1469", {"start": v(67.14, -89.27) * mm, "end": v(67.21, -89.27) * mm});
            skLineSegment(sketch, "E1470", {"start": v(67.21, -89.27) * mm, "end": v(67.29, -89.27) * mm});
            skLineSegment(sketch, "E1471", {"start": v(67.29, -89.27) * mm, "end": v(67.36, -89.27) * mm});
            skLineSegment(sketch, "E1472", {"start": v(67.36, -89.27) * mm, "end": v(67.44, -89.27) * mm});
            skLineSegment(sketch, "E1473", {"start": v(67.44, -89.27) * mm, "end": v(67.51, -89.26) * mm});
            skLineSegment(sketch, "E1474", {"start": v(67.51, -89.26) * mm, "end": v(67.59, -89.25) * mm});
            skLineSegment(sketch, "E1475", {"start": v(67.59, -89.25) * mm, "end": v(67.66, -89.24) * mm});
            skLineSegment(sketch, "E1476", {"start": v(67.66, -89.24) * mm, "end": v(67.73, -89.22) * mm});
            skLineSegment(sketch, "E1477", {"start": v(67.88, -89.18) * mm, "end": v(67.95, -89.16) * mm});
            skLineSegment(sketch, "E1478", {"start": v(67.95, -89.16) * mm, "end": v(68.02, -89.14) * mm});
            skLineSegment(sketch, "E1479", {"start": v(68.02, -89.14) * mm, "end": v(68.09, -89.1) * mm});
            skLineSegment(sketch, "E1480", {"start": v(68.09, -89.1) * mm, "end": v(68.16, -89.08) * mm});
            skLineSegment(sketch, "E1481", {"start": v(68.16, -89.08) * mm, "end": v(68.22, -89.05) * mm});
            skLineSegment(sketch, "E1482", {"start": v(68.22, -89.05) * mm, "end": v(68.29, -89.01) * mm});
            skLineSegment(sketch, "E1483", {"start": v(68.29, -89.01) * mm, "end": v(68.35, -88.98) * mm});
            skLineSegment(sketch, "E1484", {"start": v(68.35, -88.98) * mm, "end": v(68.42, -88.94) * mm});
            skLineSegment(sketch, "E1485", {"start": v(68.48, -88.9) * mm, "end": v(68.54, -88.85) * mm});
            skLineSegment(sketch, "E1486", {"start": v(68.54, -88.85) * mm, "end": v(68.6, -88.8) * mm});
            skLineSegment(sketch, "E1487", {"start": v(68.72, -88.71) * mm, "end": v(68.77, -88.66) * mm});
            skLineSegment(sketch, "E1488", {"start": v(68.77, -88.66) * mm, "end": v(68.82, -88.6) * mm});
            skLineSegment(sketch, "E1489", {"start": v(68.82, -88.6) * mm, "end": v(68.87, -88.55) * mm});
            skLineSegment(sketch, "E1490", {"start": v(68.87, -88.55) * mm, "end": v(68.92, -88.5) * mm});
            skLineSegment(sketch, "E1491", {"start": v(68.97, -88.44) * mm, "end": v(69.01, -88.38) * mm});
            skLineSegment(sketch, "E1492", {"start": v(69.01, -88.38) * mm, "end": v(69.06, -88.32) * mm});
            skLineSegment(sketch, "E1493", {"start": v(69.06, -88.32) * mm, "end": v(69.1, -88.26) * mm});
            skLineSegment(sketch, "E1494", {"start": v(69.1, -88.26) * mm, "end": v(69.13, -88.2) * mm});
            skLineSegment(sketch, "E1495", {"start": v(69.13, -88.2) * mm, "end": v(69.17, -88.13) * mm});
            skLineSegment(sketch, "E1496", {"start": v(69.17, -88.13) * mm, "end": v(69.2, -88.06) * mm});
            skLineSegment(sketch, "E1497", {"start": v(69.2, -88.06) * mm, "end": v(69.24, -88) * mm});
            skLineSegment(sketch, "E1498", {"start": v(69.26, -87.92) * mm, "end": v(69.3, -87.85) * mm});
            skLineSegment(sketch, "E1499", {"start": v(69.3, -87.85) * mm, "end": v(69.31, -87.78) * mm});
            skLineSegment(sketch, "E1500", {"start": v(69.34, -87.71) * mm, "end": v(69.36, -87.64) * mm});
            skLineSegment(sketch, "E1501", {"start": v(69.36, -87.64) * mm, "end": v(69.37, -87.57) * mm});
            skLineSegment(sketch, "E1502", {"start": v(69.37, -87.57) * mm, "end": v(69.39, -87.5) * mm});
            skLineSegment(sketch, "E1503", {"start": v(69.39, -87.5) * mm, "end": v(69.4, -87.42) * mm});
            skLineSegment(sketch, "E1504", {"start": v(69.4, -87.42) * mm, "end": v(69.4, -87.35) * mm});
            skLineSegment(sketch, "E1505", {"start": v(69.4, -87.35) * mm, "end": v(69.41, -87.27) * mm});
            skLineSegment(sketch, "E1506", {"start": v(69.41, -87.27) * mm, "end": v(69.42, -87.2) * mm});
            skLineSegment(sketch, "E1507", {"start": v(69.42, -87.2) * mm, "end": v(69.42, -87.12) * mm});
            skLineSegment(sketch, "E1508", {"start": v(4.42, -87.12) * mm, "end": v(4.42, -87.05) * mm});
            skLineSegment(sketch, "E1509", {"start": v(4.42, -87.05) * mm, "end": v(4.41, -86.97) * mm});
            skLineSegment(sketch, "E1510", {"start": v(4.41, -86.97) * mm, "end": v(4.4, -86.9) * mm});
            skLineSegment(sketch, "E1511", {"start": v(4.4, -86.9) * mm, "end": v(4.4, -86.82) * mm});
            skLineSegment(sketch, "E1512", {"start": v(4.4, -86.82) * mm, "end": v(4.39, -86.75) * mm});
            skLineSegment(sketch, "E1513", {"start": v(4.39, -86.75) * mm, "end": v(4.37, -86.68) * mm});
            skLineSegment(sketch, "E1514", {"start": v(4.37, -86.68) * mm, "end": v(4.36, -86.6) * mm});
            skLineSegment(sketch, "E1515", {"start": v(4.36, -86.6) * mm, "end": v(4.34, -86.53) * mm});
            skLineSegment(sketch, "E1516", {"start": v(4.34, -86.53) * mm, "end": v(4.31, -86.46) * mm});
            skLineSegment(sketch, "E1517", {"start": v(4.31, -86.46) * mm, "end": v(4.3, -86.4) * mm});
            skLineSegment(sketch, "E1518", {"start": v(4.3, -86.4) * mm, "end": v(4.26, -86.32) * mm});
            skLineSegment(sketch, "E1519", {"start": v(4.26, -86.32) * mm, "end": v(4.24, -86.25) * mm});
            skLineSegment(sketch, "E1520", {"start": v(4.24, -86.25) * mm, "end": v(4.2, -86.18) * mm});
            skLineSegment(sketch, "E1521", {"start": v(4.2, -86.18) * mm, "end": v(4.17, -86.12) * mm});
            skLineSegment(sketch, "E1522", {"start": v(4.17, -86.12) * mm, "end": v(4.13, -86.05) * mm});
            skLineSegment(sketch, "E1523", {"start": v(4.13, -86.05) * mm, "end": v(4.1, -85.99) * mm});
            skLineSegment(sketch, "E1524", {"start": v(4.1, -85.99) * mm, "end": v(4.06, -85.93) * mm});
            skLineSegment(sketch, "E1525", {"start": v(4.06, -85.93) * mm, "end": v(4.01, -85.86) * mm});
            skLineSegment(sketch, "E1526", {"start": v(3.92, -85.75) * mm, "end": v(3.87, -85.69) * mm});
            skLineSegment(sketch, "E1527", {"start": v(3.87, -85.69) * mm, "end": v(3.82, -85.63) * mm});
            skLineSegment(sketch, "E1528", {"start": v(3.82, -85.63) * mm, "end": v(3.77, -85.58) * mm});
            skLineSegment(sketch, "E1529", {"start": v(3.77, -85.58) * mm, "end": v(3.72, -85.53) * mm});
            skLineSegment(sketch, "E1530", {"start": v(3.72, -85.53) * mm, "end": v(3.66, -85.48) * mm});
            skLineSegment(sketch, "E1531", {"start": v(3.66, -85.48) * mm, "end": v(3.6, -85.43) * mm});
            skLineSegment(sketch, "E1532", {"start": v(3.54, -85.39) * mm, "end": v(3.48, -85.35) * mm});
            skLineSegment(sketch, "E1533", {"start": v(3.48, -85.35) * mm, "end": v(3.42, -85.3) * mm});
            skLineSegment(sketch, "E1534", {"start": v(3.42, -85.3) * mm, "end": v(3.35, -85.27) * mm});
            skLineSegment(sketch, "E1535", {"start": v(3.35, -85.27) * mm, "end": v(3.29, -85.23) * mm});
            skLineSegment(sketch, "E1536", {"start": v(3.29, -85.23) * mm, "end": v(3.22, -85.2) * mm});
            skLineSegment(sketch, "E1537", {"start": v(3.22, -85.2) * mm, "end": v(3.16, -85.16) * mm});
            skLineSegment(sketch, "E1538", {"start": v(3.16, -85.16) * mm, "end": v(3.09, -85.13) * mm});
            skLineSegment(sketch, "E1539", {"start": v(3.02, -85.1) * mm, "end": v(2.95, -85.08) * mm});
            skLineSegment(sketch, "E1540", {"start": v(2.95, -85.08) * mm, "end": v(2.88, -85.06) * mm});
            skLineSegment(sketch, "E1541", {"start": v(2.8, -85.04) * mm, "end": v(2.73, -85.02) * mm});
            skLineSegment(sketch, "E1542", {"start": v(2.73, -85.02) * mm, "end": v(2.66, -85) * mm});
            skLineSegment(sketch, "E1543", {"start": v(2.66, -85) * mm, "end": v(2.59, -85) * mm});
            skLineSegment(sketch, "E1544", {"start": v(2.44, -84.98) * mm, "end": v(2.36, -84.97) * mm});
            skLineSegment(sketch, "E1545", {"start": v(2.36, -84.97) * mm, "end": v(2.29, -84.97) * mm});
            skLineSegment(sketch, "E1546", {"start": v(2.29, -84.97) * mm, "end": v(2.21, -84.97) * mm});
            skLineSegment(sketch, "E1547", {"start": v(2.14, -84.98) * mm, "end": v(2.06, -84.98) * mm});
            skLineSegment(sketch, "E1548", {"start": v(2.06, -84.98) * mm, "end": v(1.99, -85) * mm});
            skLineSegment(sketch, "E1549", {"start": v(1.99, -85) * mm, "end": v(1.92, -85) * mm});
            skLineSegment(sketch, "E1550", {"start": v(1.92, -85) * mm, "end": v(1.84, -85.01) * mm});
            skLineSegment(sketch, "E1551", {"start": v(1.84, -85.01) * mm, "end": v(1.77, -85.03) * mm});
            skLineSegment(sketch, "E1552", {"start": v(1.77, -85.03) * mm, "end": v(1.7, -85.05) * mm});
            skLineSegment(sketch, "E1553", {"start": v(1.7, -85.05) * mm, "end": v(1.63, -85.07) * mm});
            skLineSegment(sketch, "E1554", {"start": v(1.56, -85.1) * mm, "end": v(1.49, -85.12) * mm});
            skLineSegment(sketch, "E1555", {"start": v(1.49, -85.12) * mm, "end": v(1.42, -85.15) * mm});
            skLineSegment(sketch, "E1556", {"start": v(1.42, -85.15) * mm, "end": v(1.35, -85.18) * mm});
            skLineSegment(sketch, "E1557", {"start": v(1.35, -85.18) * mm, "end": v(1.28, -85.21) * mm});
            skLineSegment(sketch, "E1558", {"start": v(1.28, -85.21) * mm, "end": v(1.22, -85.25) * mm});
            skLineSegment(sketch, "E1559", {"start": v(1.22, -85.25) * mm, "end": v(1.15, -85.29) * mm});
            skLineSegment(sketch, "E1560", {"start": v(1.15, -85.29) * mm, "end": v(1.09, -85.33) * mm});
            skLineSegment(sketch, "E1561", {"start": v(1.09, -85.33) * mm, "end": v(1.03, -85.37) * mm});
            skLineSegment(sketch, "E1562", {"start": v(1.03, -85.37) * mm, "end": v(0.97, -85.41) * mm});
            skLineSegment(sketch, "E1563", {"start": v(0.97, -85.41) * mm, "end": v(0.9, -85.46) * mm});
            skLineSegment(sketch, "E1564", {"start": v(0.9, -85.46) * mm, "end": v(0.85, -85.5) * mm});
            skLineSegment(sketch, "E1565", {"start": v(0.8, -85.56) * mm, "end": v(0.74, -85.6) * mm});
            skLineSegment(sketch, "E1566", {"start": v(0.7, -85.66) * mm, "end": v(0.64, -85.72) * mm});
            skLineSegment(sketch, "E1567", {"start": v(0.64, -85.72) * mm, "end": v(0.6, -85.78) * mm});
            skLineSegment(sketch, "E1568", {"start": v(0.6, -85.78) * mm, "end": v(0.55, -85.83) * mm});
            skLineSegment(sketch, "E1569", {"start": v(0.55, -85.83) * mm, "end": v(0.5, -85.9) * mm});
            skLineSegment(sketch, "E1570", {"start": v(0.5, -85.9) * mm, "end": v(0.46, -85.96) * mm});
            skLineSegment(sketch, "E1571", {"start": v(0.46, -85.96) * mm, "end": v(0.42, -86.02) * mm});
            skLineSegment(sketch, "E1572", {"start": v(0.42, -86.02) * mm, "end": v(0.39, -86.08) * mm});
            skLineSegment(sketch, "E1573", {"start": v(0.39, -86.08) * mm, "end": v(0.35, -86.15) * mm});
            skLineSegment(sketch, "E1574", {"start": v(0.35, -86.15) * mm, "end": v(0.32, -86.22) * mm});
            skLineSegment(sketch, "E1575", {"start": v(0.32, -86.22) * mm, "end": v(0.29, -86.29) * mm});
            skLineSegment(sketch, "E1576", {"start": v(0.29, -86.29) * mm, "end": v(0.26, -86.36) * mm});
            skLineSegment(sketch, "E1577", {"start": v(0.26, -86.36) * mm, "end": v(0.23, -86.43) * mm});
            skLineSegment(sketch, "E1578", {"start": v(0.23, -86.43) * mm, "end": v(0.21, -86.5) * mm});
            skLineSegment(sketch, "E1579", {"start": v(0.21, -86.5) * mm, "end": v(0.2, -86.57) * mm});
            skLineSegment(sketch, "E1580", {"start": v(0.2, -86.57) * mm, "end": v(0.17, -86.64) * mm});
            skLineSegment(sketch, "E1581", {"start": v(0.17, -86.64) * mm, "end": v(0.16, -86.71) * mm});
            skLineSegment(sketch, "E1582", {"start": v(0.16, -86.71) * mm, "end": v(0.15, -86.79) * mm});
            skLineSegment(sketch, "E1583", {"start": v(0.15, -86.79) * mm, "end": v(0.13, -86.86) * mm});
            skLineSegment(sketch, "E1584", {"start": v(0.13, -86.86) * mm, "end": v(0.13, -86.94) * mm});
            skLineSegment(sketch, "E1585", {"start": v(0.13, -86.94) * mm, "end": v(0.12, -87) * mm});
            skLineSegment(sketch, "E1586", {"start": v(0.12, -87) * mm, "end": v(0.12, -87.08) * mm});
            skLineSegment(sketch, "E1587", {"start": v(0.12, -87.08) * mm, "end": v(0.12, -87.16) * mm});
            skLineSegment(sketch, "E1588", {"start": v(0.12, -87.16) * mm, "end": v(0.12, -87.23) * mm});
            skLineSegment(sketch, "E1589", {"start": v(0.12, -87.23) * mm, "end": v(0.13, -87.3) * mm});
            skLineSegment(sketch, "E1590", {"start": v(0.13, -87.3) * mm, "end": v(0.13, -87.38) * mm});
            skLineSegment(sketch, "E1591", {"start": v(0.13, -87.38) * mm, "end": v(0.15, -87.46) * mm});
            skLineSegment(sketch, "E1592", {"start": v(0.15, -87.46) * mm, "end": v(0.16, -87.53) * mm});
            skLineSegment(sketch, "E1593", {"start": v(0.16, -87.53) * mm, "end": v(0.17, -87.6) * mm});
            skLineSegment(sketch, "E1594", {"start": v(0.17, -87.6) * mm, "end": v(0.2, -87.68) * mm});
            skLineSegment(sketch, "E1595", {"start": v(0.2, -87.68) * mm, "end": v(0.21, -87.75) * mm});
            skLineSegment(sketch, "E1596", {"start": v(0.21, -87.75) * mm, "end": v(0.23, -87.82) * mm});
            skLineSegment(sketch, "E1597", {"start": v(0.23, -87.82) * mm, "end": v(0.26, -87.89) * mm});
            skLineSegment(sketch, "E1598", {"start": v(0.29, -87.96) * mm, "end": v(0.32, -88.03) * mm});
            skLineSegment(sketch, "E1599", {"start": v(0.32, -88.03) * mm, "end": v(0.35, -88.1) * mm});
            skLineSegment(sketch, "E1600", {"start": v(0.35, -88.1) * mm, "end": v(0.39, -88.16) * mm});
            skLineSegment(sketch, "E1601", {"start": v(0.39, -88.16) * mm, "end": v(0.42, -88.22) * mm});
            skLineSegment(sketch, "E1602", {"start": v(0.42, -88.22) * mm, "end": v(0.46, -88.29) * mm});
            skLineSegment(sketch, "E1603", {"start": v(0.46, -88.29) * mm, "end": v(0.5, -88.35) * mm});
            skLineSegment(sketch, "E1604", {"start": v(0.55, -88.4) * mm, "end": v(0.6, -88.47) * mm});
            skLineSegment(sketch, "E1605", {"start": v(0.6, -88.47) * mm, "end": v(0.64, -88.53) * mm});
            skLineSegment(sketch, "E1606", {"start": v(0.64, -88.53) * mm, "end": v(0.7, -88.58) * mm});
            skLineSegment(sketch, "E1607", {"start": v(0.7, -88.58) * mm, "end": v(0.74, -88.64) * mm});
            skLineSegment(sketch, "E1608", {"start": v(0.74, -88.64) * mm, "end": v(0.8, -88.69) * mm});
            skLineSegment(sketch, "E1609", {"start": v(0.8, -88.69) * mm, "end": v(0.85, -88.74) * mm});
            skLineSegment(sketch, "E1610", {"start": v(0.85, -88.74) * mm, "end": v(0.9, -88.79) * mm});
            skLineSegment(sketch, "E1611", {"start": v(0.97, -88.83) * mm, "end": v(1.03, -88.88) * mm});
            skLineSegment(sketch, "E1612", {"start": v(1.03, -88.88) * mm, "end": v(1.09, -88.92) * mm});
            skLineSegment(sketch, "E1613", {"start": v(1.09, -88.92) * mm, "end": v(1.15, -88.96) * mm});
            skLineSegment(sketch, "E1614", {"start": v(1.15, -88.96) * mm, "end": v(1.22, -89) * mm});
            skLineSegment(sketch, "E1615", {"start": v(1.22, -89) * mm, "end": v(1.28, -89.03) * mm});
            skLineSegment(sketch, "E1616", {"start": v(1.28, -89.03) * mm, "end": v(1.35, -89.06) * mm});
            skLineSegment(sketch, "E1617", {"start": v(1.35, -89.06) * mm, "end": v(1.42, -89.1) * mm});
            skLineSegment(sketch, "E1618", {"start": v(1.42, -89.1) * mm, "end": v(1.49, -89.12) * mm});
            skLineSegment(sketch, "E1619", {"start": v(1.49, -89.12) * mm, "end": v(1.56, -89.15) * mm});
            skLineSegment(sketch, "E1620", {"start": v(1.56, -89.15) * mm, "end": v(1.63, -89.17) * mm});
            skLineSegment(sketch, "E1621", {"start": v(1.7, -89.2) * mm, "end": v(1.77, -89.21) * mm});
            skLineSegment(sketch, "E1622", {"start": v(1.77, -89.21) * mm, "end": v(1.84, -89.23) * mm});
            skLineSegment(sketch, "E1623", {"start": v(1.84, -89.23) * mm, "end": v(1.92, -89.24) * mm});
            skLineSegment(sketch, "E1624", {"start": v(2.14, -89.27) * mm, "end": v(2.21, -89.27) * mm});
            skLineSegment(sketch, "E1625", {"start": v(2.21, -89.27) * mm, "end": v(2.29, -89.27) * mm});
            skLineSegment(sketch, "E1626", {"start": v(2.29, -89.27) * mm, "end": v(2.36, -89.27) * mm});
            skLineSegment(sketch, "E1627", {"start": v(2.36, -89.27) * mm, "end": v(2.44, -89.27) * mm});
            skLineSegment(sketch, "E1628", {"start": v(2.44, -89.27) * mm, "end": v(2.51, -89.26) * mm});
            skLineSegment(sketch, "E1629", {"start": v(2.51, -89.26) * mm, "end": v(2.59, -89.25) * mm});
            skLineSegment(sketch, "E1630", {"start": v(2.59, -89.25) * mm, "end": v(2.66, -89.24) * mm});
            skLineSegment(sketch, "E1631", {"start": v(2.66, -89.24) * mm, "end": v(2.73, -89.22) * mm});
            skLineSegment(sketch, "E1632", {"start": v(2.73, -89.22) * mm, "end": v(2.8, -89.2) * mm});
            skLineSegment(sketch, "E1633", {"start": v(2.8, -89.2) * mm, "end": v(2.88, -89.18) * mm});
            skLineSegment(sketch, "E1634", {"start": v(3.02, -89.14) * mm, "end": v(3.09, -89.1) * mm});
            skLineSegment(sketch, "E1635", {"start": v(3.09, -89.1) * mm, "end": v(3.16, -89.08) * mm});
            skLineSegment(sketch, "E1636", {"start": v(3.16, -89.08) * mm, "end": v(3.22, -89.05) * mm});
            skLineSegment(sketch, "E1637", {"start": v(3.22, -89.05) * mm, "end": v(3.29, -89.01) * mm});
            skLineSegment(sketch, "E1638", {"start": v(3.29, -89.01) * mm, "end": v(3.35, -88.98) * mm});
            skLineSegment(sketch, "E1639", {"start": v(3.35, -88.98) * mm, "end": v(3.42, -88.94) * mm});
            skLineSegment(sketch, "E1640", {"start": v(3.42, -88.94) * mm, "end": v(3.48, -88.9) * mm});
            skLineSegment(sketch, "E1641", {"start": v(3.48, -88.9) * mm, "end": v(3.54, -88.85) * mm});
            skLineSegment(sketch, "E1642", {"start": v(3.6, -88.8) * mm, "end": v(3.66, -88.76) * mm});
            skLineSegment(sketch, "E1643", {"start": v(3.66, -88.76) * mm, "end": v(3.72, -88.71) * mm});
            skLineSegment(sketch, "E1644", {"start": v(3.77, -88.66) * mm, "end": v(3.82, -88.6) * mm});
            skLineSegment(sketch, "E1645", {"start": v(3.92, -88.5) * mm, "end": v(3.97, -88.44) * mm});
            skLineSegment(sketch, "E1646", {"start": v(3.97, -88.44) * mm, "end": v(4.01, -88.38) * mm});
            skLineSegment(sketch, "E1647", {"start": v(4.01, -88.38) * mm, "end": v(4.06, -88.32) * mm});
            skLineSegment(sketch, "E1648", {"start": v(4.06, -88.32) * mm, "end": v(4.1, -88.26) * mm});
            skLineSegment(sketch, "E1649", {"start": v(4.1, -88.26) * mm, "end": v(4.13, -88.2) * mm});
            skLineSegment(sketch, "E1650", {"start": v(4.13, -88.2) * mm, "end": v(4.17, -88.13) * mm});
            skLineSegment(sketch, "E1651", {"start": v(4.17, -88.13) * mm, "end": v(4.2, -88.06) * mm});
            skLineSegment(sketch, "E1652", {"start": v(4.2, -88.06) * mm, "end": v(4.24, -88) * mm});
            skLineSegment(sketch, "E1653", {"start": v(4.24, -88) * mm, "end": v(4.26, -87.92) * mm});
            skLineSegment(sketch, "E1654", {"start": v(4.26, -87.92) * mm, "end": v(4.3, -87.85) * mm});
            skLineSegment(sketch, "E1655", {"start": v(4.3, -87.85) * mm, "end": v(4.31, -87.78) * mm});
            skLineSegment(sketch, "E1656", {"start": v(4.31, -87.78) * mm, "end": v(4.34, -87.71) * mm});
            skLineSegment(sketch, "E1657", {"start": v(4.34, -87.71) * mm, "end": v(4.36, -87.64) * mm});
            skLineSegment(sketch, "E1658", {"start": v(4.36, -87.64) * mm, "end": v(4.37, -87.57) * mm});
            skLineSegment(sketch, "E1659", {"start": v(4.37, -87.57) * mm, "end": v(4.39, -87.5) * mm});
            skLineSegment(sketch, "E1660", {"start": v(4.39, -87.5) * mm, "end": v(4.4, -87.42) * mm});
            skLineSegment(sketch, "E1661", {"start": v(4.4, -87.42) * mm, "end": v(4.4, -87.35) * mm});
            skLineSegment(sketch, "E1662", {"start": v(4.4, -87.35) * mm, "end": v(4.41, -87.27) * mm});
            skLineSegment(sketch, "E1663", {"start": v(4.41, -87.27) * mm, "end": v(4.42, -87.2) * mm});
            skLineSegment(sketch, "E1664", {"start": v(4.42, -87.2) * mm, "end": v(4.42, -87.12) * mm});
            skLineSegment(sketch, "E1665", {"start": v(244.38, -80.76) * mm, "end": v(329.38, -80.76) * mm});
            skLineSegment(sketch, "E1666", {"start": v(329.38, -80.76) * mm, "end": v(329.38, 39.24) * mm});
            skLineSegment(sketch, "E1667", {"start": v(329.38, 39.24) * mm, "end": v(244.38, 39.24) * mm});
            skLineSegment(sketch, "E1668", {"start": v(244.38, 39.24) * mm, "end": v(244.38, -80.76) * mm});
            skLineSegment(sketch, "E1669", {"start": v(91.87, -88.2) * mm, "end": v(91.86, -88.12) * mm});
            skLineSegment(sketch, "E1670", {"start": v(91.83, -87.82) * mm, "end": v(91.82, -87.75) * mm});
            skLineSegment(sketch, "E1671", {"start": v(91.82, -87.75) * mm, "end": v(91.8, -87.68) * mm});
            skLineSegment(sketch, "E1672", {"start": v(91.8, -87.68) * mm, "end": v(91.78, -87.6) * mm});
            skLineSegment(sketch, "E1673", {"start": v(91.78, -87.6) * mm, "end": v(91.76, -87.53) * mm});
            skLineSegment(sketch, "E1674", {"start": v(91.76, -87.53) * mm, "end": v(91.74, -87.46) * mm});
            skLineSegment(sketch, "E1675", {"start": v(91.74, -87.46) * mm, "end": v(91.71, -87.4) * mm});
            skLineSegment(sketch, "E1676", {"start": v(91.71, -87.4) * mm, "end": v(91.68, -87.32) * mm});
            skLineSegment(sketch, "E1677", {"start": v(91.68, -87.32) * mm, "end": v(91.65, -87.25) * mm});
            skLineSegment(sketch, "E1678", {"start": v(91.65, -87.25) * mm, "end": v(91.62, -87.19) * mm});
            skLineSegment(sketch, "E1679", {"start": v(91.62, -87.19) * mm, "end": v(91.58, -87.12) * mm});
            skLineSegment(sketch, "E1680", {"start": v(91.58, -87.12) * mm, "end": v(91.54, -87.06) * mm});
            skLineSegment(sketch, "E1681", {"start": v(91.54, -87.06) * mm, "end": v(91.5, -87) * mm});
            skLineSegment(sketch, "E1682", {"start": v(91.5, -87) * mm, "end": v(91.46, -86.93) * mm});
            skLineSegment(sketch, "E1683", {"start": v(91.46, -86.93) * mm, "end": v(91.42, -86.88) * mm});
            skLineSegment(sketch, "E1684", {"start": v(91.42, -86.88) * mm, "end": v(91.37, -86.82) * mm});
            skLineSegment(sketch, "E1685", {"start": v(91.37, -86.82) * mm, "end": v(91.32, -86.76) * mm});
            skLineSegment(sketch, "E1686", {"start": v(91.32, -86.76) * mm, "end": v(91.27, -86.7) * mm});
            skLineSegment(sketch, "E1687", {"start": v(91.27, -86.7) * mm, "end": v(91.22, -86.65) * mm});
            skLineSegment(sketch, "E1688", {"start": v(91.16, -86.6) * mm, "end": v(91.1, -86.55) * mm});
            skLineSegment(sketch, "E1689", {"start": v(91.1, -86.55) * mm, "end": v(91.05, -86.5) * mm});
            skLineSegment(sketch, "E1690", {"start": v(91.05, -86.5) * mm, "end": v(90.99, -86.46) * mm});
            skLineSegment(sketch, "E1691", {"start": v(90.99, -86.46) * mm, "end": v(90.93, -86.42) * mm});
            skLineSegment(sketch, "E1692", {"start": v(90.93, -86.42) * mm, "end": v(90.87, -86.38) * mm});
            skLineSegment(sketch, "E1693", {"start": v(90.87, -86.38) * mm, "end": v(90.8, -86.34) * mm});
            skLineSegment(sketch, "E1694", {"start": v(90.74, -86.3) * mm, "end": v(90.67, -86.27) * mm});
            skLineSegment(sketch, "E1695", {"start": v(90.67, -86.27) * mm, "end": v(90.6, -86.23) * mm});
            skLineSegment(sketch, "E1696", {"start": v(90.6, -86.23) * mm, "end": v(90.53, -86.2) * mm});
            skLineSegment(sketch, "E1697", {"start": v(90.53, -86.2) * mm, "end": v(90.47, -86.18) * mm});
            skLineSegment(sketch, "E1698", {"start": v(90.47, -86.18) * mm, "end": v(90.4, -86.15) * mm});
            skLineSegment(sketch, "E1699", {"start": v(90.4, -86.15) * mm, "end": v(90.32, -86.13) * mm});
            skLineSegment(sketch, "E1700", {"start": v(90.32, -86.13) * mm, "end": v(90.25, -86.11) * mm});
            skLineSegment(sketch, "E1701", {"start": v(90.25, -86.11) * mm, "end": v(90.18, -86.1) * mm});
            skLineSegment(sketch, "E1702", {"start": v(90.18, -86.1) * mm, "end": v(90.1, -86.08) * mm});
            skLineSegment(sketch, "E1703", {"start": v(90.1, -86.08) * mm, "end": v(90.03, -86.07) * mm});
            skLineSegment(sketch, "E1704", {"start": v(90.03, -86.07) * mm, "end": v(89.96, -86.06) * mm});
            skLineSegment(sketch, "E1705", {"start": v(89.96, -86.06) * mm, "end": v(89.88, -86.05) * mm});
            skLineSegment(sketch, "E1706", {"start": v(88.04, -86.85) * mm, "end": v(88, -86.9) * mm});
            skLineSegment(sketch, "E1707", {"start": v(88, -86.9) * mm, "end": v(87.95, -86.97) * mm});
            skLineSegment(sketch, "E1708", {"start": v(87.95, -86.97) * mm, "end": v(87.9, -87.03) * mm});
            skLineSegment(sketch, "E1709", {"start": v(87.9, -87.03) * mm, "end": v(87.87, -87.1) * mm});
            skLineSegment(sketch, "E1710", {"start": v(87.87, -87.1) * mm, "end": v(87.83, -87.16) * mm});
            skLineSegment(sketch, "E1711", {"start": v(87.83, -87.16) * mm, "end": v(87.8, -87.22) * mm});
            skLineSegment(sketch, "E1712", {"start": v(87.8, -87.22) * mm, "end": v(87.77, -87.29) * mm});
            skLineSegment(sketch, "E1713", {"start": v(87.77, -87.29) * mm, "end": v(87.74, -87.36) * mm});
            skLineSegment(sketch, "E1714", {"start": v(87.74, -87.36) * mm, "end": v(87.7, -87.43) * mm});
            skLineSegment(sketch, "E1715", {"start": v(87.7, -87.43) * mm, "end": v(87.68, -87.5) * mm});
            skLineSegment(sketch, "E1716", {"start": v(87.68, -87.5) * mm, "end": v(87.66, -87.57) * mm});
            skLineSegment(sketch, "E1717", {"start": v(87.66, -87.57) * mm, "end": v(87.64, -87.64) * mm});
            skLineSegment(sketch, "E1718", {"start": v(87.64, -87.64) * mm, "end": v(87.62, -87.71) * mm});
            skLineSegment(sketch, "E1719", {"start": v(87.62, -87.71) * mm, "end": v(87.6, -87.78) * mm});
            skLineSegment(sketch, "E1720", {"start": v(87.6, -87.78) * mm, "end": v(87.6, -87.86) * mm});
            skLineSegment(sketch, "E1721", {"start": v(87.6, -87.86) * mm, "end": v(87.58, -87.93) * mm});
            skLineSegment(sketch, "E1722", {"start": v(87.57, -88) * mm, "end": v(87.57, -88.08) * mm});
            skLineSegment(sketch, "E1723", {"start": v(87.57, -88.16) * mm, "end": v(87.57, -88.23) * mm});
            skLineSegment(sketch, "E1724", {"start": v(87.57, -88.23) * mm, "end": v(87.57, -88.3) * mm});
            skLineSegment(sketch, "E1725", {"start": v(87.57, -88.3) * mm, "end": v(87.57, -88.38) * mm});
            skLineSegment(sketch, "E1726", {"start": v(87.57, -88.38) * mm, "end": v(87.58, -88.45) * mm});
            skLineSegment(sketch, "E1727", {"start": v(87.58, -88.45) * mm, "end": v(87.6, -88.53) * mm});
            skLineSegment(sketch, "E1728", {"start": v(87.6, -88.53) * mm, "end": v(87.6, -88.6) * mm});
            skLineSegment(sketch, "E1729", {"start": v(87.6, -88.6) * mm, "end": v(87.62, -88.67) * mm});
            skLineSegment(sketch, "E1730", {"start": v(87.62, -88.67) * mm, "end": v(87.64, -88.75) * mm});
            skLineSegment(sketch, "E1731", {"start": v(87.64, -88.75) * mm, "end": v(87.66, -88.82) * mm});
            skLineSegment(sketch, "E1732", {"start": v(87.66, -88.82) * mm, "end": v(87.68, -88.89) * mm});
            skLineSegment(sketch, "E1733", {"start": v(87.68, -88.89) * mm, "end": v(87.7, -88.96) * mm});
            skLineSegment(sketch, "E1734", {"start": v(87.7, -88.96) * mm, "end": v(87.74, -89.03) * mm});
            skLineSegment(sketch, "E1735", {"start": v(87.74, -89.03) * mm, "end": v(87.77, -89.1) * mm});
            skLineSegment(sketch, "E1736", {"start": v(87.77, -89.1) * mm, "end": v(87.8, -89.16) * mm});
            skLineSegment(sketch, "E1737", {"start": v(87.8, -89.16) * mm, "end": v(87.83, -89.23) * mm});
            skLineSegment(sketch, "E1738", {"start": v(87.83, -89.23) * mm, "end": v(87.87, -89.3) * mm});
            skLineSegment(sketch, "E1739", {"start": v(87.87, -89.3) * mm, "end": v(87.9, -89.36) * mm});
            skLineSegment(sketch, "E1740", {"start": v(87.9, -89.36) * mm, "end": v(87.95, -89.42) * mm});
            skLineSegment(sketch, "E1741", {"start": v(87.95, -89.42) * mm, "end": v(88, -89.48) * mm});
            skLineSegment(sketch, "E1742", {"start": v(88, -89.48) * mm, "end": v(88.04, -89.54) * mm});
            skLineSegment(sketch, "E1743", {"start": v(88.04, -89.54) * mm, "end": v(88.09, -89.6) * mm});
            skLineSegment(sketch, "E1744", {"start": v(88.09, -89.6) * mm, "end": v(88.14, -89.65) * mm});
            skLineSegment(sketch, "E1745", {"start": v(88.19, -89.7) * mm, "end": v(88.24, -89.76) * mm});
            skLineSegment(sketch, "E1746", {"start": v(88.3, -89.8) * mm, "end": v(88.35, -89.86) * mm});
            skLineSegment(sketch, "E1747", {"start": v(88.35, -89.86) * mm, "end": v(88.41, -89.9) * mm});
            skLineSegment(sketch, "E1748", {"start": v(88.41, -89.9) * mm, "end": v(88.47, -89.95) * mm});
            skLineSegment(sketch, "E1749", {"start": v(88.47, -89.95) * mm, "end": v(88.54, -89.99) * mm});
            skLineSegment(sketch, "E1750", {"start": v(88.54, -89.99) * mm, "end": v(88.6, -90.03) * mm});
            skLineSegment(sketch, "E1751", {"start": v(88.6, -90.03) * mm, "end": v(88.66, -90.07) * mm});
            skLineSegment(sketch, "E1752", {"start": v(88.66, -90.07) * mm, "end": v(88.73, -90.1) * mm});
            skLineSegment(sketch, "E1753", {"start": v(88.73, -90.1) * mm, "end": v(88.8, -90.14) * mm});
            skLineSegment(sketch, "E1754", {"start": v(88.8, -90.14) * mm, "end": v(88.86, -90.17) * mm});
            skLineSegment(sketch, "E1755", {"start": v(88.86, -90.17) * mm, "end": v(88.93, -90.2) * mm});
            skLineSegment(sketch, "E1756", {"start": v(88.93, -90.2) * mm, "end": v(89, -90.22) * mm});
            skLineSegment(sketch, "E1757", {"start": v(89, -90.22) * mm, "end": v(89.07, -90.24) * mm});
            skLineSegment(sketch, "E1758", {"start": v(89.07, -90.24) * mm, "end": v(89.14, -90.27) * mm});
            skLineSegment(sketch, "E1759", {"start": v(89.14, -90.27) * mm, "end": v(89.22, -90.28) * mm});
            skLineSegment(sketch, "E1760", {"start": v(89.22, -90.28) * mm, "end": v(89.29, -90.3) * mm});
            skLineSegment(sketch, "E1761", {"start": v(90.99, -89.93) * mm, "end": v(91.05, -89.88) * mm});
            skLineSegment(sketch, "E1762", {"start": v(91.05, -89.88) * mm, "end": v(91.1, -89.83) * mm});
            skLineSegment(sketch, "E1763", {"start": v(91.16, -89.78) * mm, "end": v(91.22, -89.73) * mm});
            skLineSegment(sketch, "E1764", {"start": v(91.27, -89.68) * mm, "end": v(91.32, -89.62) * mm});
            skLineSegment(sketch, "E1765", {"start": v(91.32, -89.62) * mm, "end": v(91.37, -89.57) * mm});
            skLineSegment(sketch, "E1766", {"start": v(91.37, -89.57) * mm, "end": v(91.42, -89.5) * mm});
            skLineSegment(sketch, "E1767", {"start": v(91.42, -89.5) * mm, "end": v(91.46, -89.45) * mm});
            skLineSegment(sketch, "E1768", {"start": v(91.46, -89.45) * mm, "end": v(91.5, -89.39) * mm});
            skLineSegment(sketch, "E1769", {"start": v(91.5, -89.39) * mm, "end": v(91.54, -89.33) * mm});
            skLineSegment(sketch, "E1770", {"start": v(91.54, -89.33) * mm, "end": v(91.58, -89.26) * mm});
            skLineSegment(sketch, "E1771", {"start": v(91.58, -89.26) * mm, "end": v(91.62, -89.2) * mm});
            skLineSegment(sketch, "E1772", {"start": v(91.62, -89.2) * mm, "end": v(91.65, -89.13) * mm});
            skLineSegment(sketch, "E1773", {"start": v(91.65, -89.13) * mm, "end": v(91.68, -89.06) * mm});
            skLineSegment(sketch, "E1774", {"start": v(91.68, -89.06) * mm, "end": v(91.71, -89) * mm});
            skLineSegment(sketch, "E1775", {"start": v(91.71, -89) * mm, "end": v(91.74, -88.92) * mm});
            skLineSegment(sketch, "E1776", {"start": v(91.74, -88.92) * mm, "end": v(91.76, -88.85) * mm});
            skLineSegment(sketch, "E1777", {"start": v(91.76, -88.85) * mm, "end": v(91.78, -88.78) * mm});
            skLineSegment(sketch, "E1778", {"start": v(91.78, -88.78) * mm, "end": v(91.8, -88.7) * mm});
            skLineSegment(sketch, "E1779", {"start": v(91.8, -88.7) * mm, "end": v(91.82, -88.64) * mm});
            skLineSegment(sketch, "E1780", {"start": v(91.82, -88.64) * mm, "end": v(91.83, -88.56) * mm});
            skLineSegment(sketch, "E1781", {"start": v(91.83, -88.56) * mm, "end": v(91.85, -88.5) * mm});
            skLineSegment(sketch, "E1782", {"start": v(91.85, -88.42) * mm, "end": v(91.86, -88.34) * mm});
            skLineSegment(sketch, "E1783", {"start": v(91.86, -88.34) * mm, "end": v(91.86, -88.27) * mm});
            skLineSegment(sketch, "E1784", {"start": v(91.86, -88.27) * mm, "end": v(91.87, -88.2) * mm});
            skLineSegment(sketch, "E1785", {"start": v(91.87, 21.8) * mm, "end": v(91.86, 21.88) * mm});
            skLineSegment(sketch, "E1786", {"start": v(91.86, 21.88) * mm, "end": v(91.86, 21.96) * mm});
            skLineSegment(sketch, "E1787", {"start": v(91.85, 22.03) * mm, "end": v(91.85, 22.1) * mm});
            skLineSegment(sketch, "E1788", {"start": v(91.85, 22.1) * mm, "end": v(91.83, 22.18) * mm});
            skLineSegment(sketch, "E1789", {"start": v(91.83, 22.18) * mm, "end": v(91.82, 22.25) * mm});
            skLineSegment(sketch, "E1790", {"start": v(91.82, 22.25) * mm, "end": v(91.8, 22.32) * mm});
            skLineSegment(sketch, "E1791", {"start": v(91.8, 22.32) * mm, "end": v(91.78, 22.4) * mm});
            skLineSegment(sketch, "E1792", {"start": v(91.78, 22.4) * mm, "end": v(91.76, 22.47) * mm});
            skLineSegment(sketch, "E1793", {"start": v(91.76, 22.47) * mm, "end": v(91.74, 22.54) * mm});
            skLineSegment(sketch, "E1794", {"start": v(91.74, 22.54) * mm, "end": v(91.71, 22.6) * mm});
            skLineSegment(sketch, "E1795", {"start": v(91.71, 22.6) * mm, "end": v(91.68, 22.68) * mm});
            skLineSegment(sketch, "E1796", {"start": v(91.68, 22.68) * mm, "end": v(91.65, 22.75) * mm});
            skLineSegment(sketch, "E1797", {"start": v(91.65, 22.75) * mm, "end": v(91.62, 22.81) * mm});
            skLineSegment(sketch, "E1798", {"start": v(91.62, 22.81) * mm, "end": v(91.58, 22.88) * mm});
            skLineSegment(sketch, "E1799", {"start": v(91.58, 22.88) * mm, "end": v(91.54, 22.94) * mm});
            skLineSegment(sketch, "E1800", {"start": v(91.54, 22.94) * mm, "end": v(91.5, 23) * mm});
            skLineSegment(sketch, "E1801", {"start": v(91.5, 23) * mm, "end": v(91.46, 23.07) * mm});
            skLineSegment(sketch, "E1802", {"start": v(91.46, 23.07) * mm, "end": v(91.42, 23.12) * mm});
            skLineSegment(sketch, "E1803", {"start": v(91.42, 23.12) * mm, "end": v(91.37, 23.18) * mm});
            skLineSegment(sketch, "E1804", {"start": v(91.37, 23.18) * mm, "end": v(91.32, 23.24) * mm});
            skLineSegment(sketch, "E1805", {"start": v(91.27, 23.3) * mm, "end": v(91.22, 23.35) * mm});
            skLineSegment(sketch, "E1806", {"start": v(91.22, 23.35) * mm, "end": v(91.16, 23.4) * mm});
            skLineSegment(sketch, "E1807", {"start": v(91.16, 23.4) * mm, "end": v(91.1, 23.45) * mm});
            skLineSegment(sketch, "E1808", {"start": v(91.1, 23.45) * mm, "end": v(91.05, 23.5) * mm});
            skLineSegment(sketch, "E1809", {"start": v(91.05, 23.5) * mm, "end": v(90.99, 23.54) * mm});
            skLineSegment(sketch, "E1810", {"start": v(90.99, 23.54) * mm, "end": v(90.93, 23.58) * mm});
            skLineSegment(sketch, "E1811", {"start": v(90.93, 23.58) * mm, "end": v(90.87, 23.62) * mm});
            skLineSegment(sketch, "E1812", {"start": v(90.87, 23.62) * mm, "end": v(90.8, 23.66) * mm});
            skLineSegment(sketch, "E1813", {"start": v(90.8, 23.66) * mm, "end": v(90.74, 23.7) * mm});
            skLineSegment(sketch, "E1814", {"start": v(90.74, 23.7) * mm, "end": v(90.67, 23.73) * mm});
            skLineSegment(sketch, "E1815", {"start": v(90.67, 23.73) * mm, "end": v(90.6, 23.77) * mm});
            skLineSegment(sketch, "E1816", {"start": v(90.6, 23.77) * mm, "end": v(90.53, 23.8) * mm});
            skLineSegment(sketch, "E1817", {"start": v(89.22, 23.9) * mm, "end": v(89.14, 23.88) * mm});
            skLineSegment(sketch, "E1818", {"start": v(89.14, 23.88) * mm, "end": v(89.07, 23.86) * mm});
            skLineSegment(sketch, "E1819", {"start": v(89.07, 23.86) * mm, "end": v(89, 23.84) * mm});
            skLineSegment(sketch, "E1820", {"start": v(89, 23.84) * mm, "end": v(88.93, 23.8) * mm});
            skLineSegment(sketch, "E1821", {"start": v(88.93, 23.8) * mm, "end": v(88.86, 23.78) * mm});
            skLineSegment(sketch, "E1822", {"start": v(88.86, 23.78) * mm, "end": v(88.8, 23.75) * mm});
            skLineSegment(sketch, "E1823", {"start": v(88.73, 23.72) * mm, "end": v(88.66, 23.68) * mm});
            skLineSegment(sketch, "E1824", {"start": v(88.66, 23.68) * mm, "end": v(88.6, 23.64) * mm});
            skLineSegment(sketch, "E1825", {"start": v(88.6, 23.64) * mm, "end": v(88.54, 23.6) * mm});
            skLineSegment(sketch, "E1826", {"start": v(88.54, 23.6) * mm, "end": v(88.47, 23.56) * mm});
            skLineSegment(sketch, "E1827", {"start": v(88.47, 23.56) * mm, "end": v(88.41, 23.52) * mm});
            skLineSegment(sketch, "E1828", {"start": v(88.41, 23.52) * mm, "end": v(88.35, 23.47) * mm});
            skLineSegment(sketch, "E1829", {"start": v(88.35, 23.47) * mm, "end": v(88.3, 23.42) * mm});
            skLineSegment(sketch, "E1830", {"start": v(88.24, 23.37) * mm, "end": v(88.19, 23.32) * mm});
            skLineSegment(sketch, "E1831", {"start": v(88.19, 23.32) * mm, "end": v(88.14, 23.27) * mm});
            skLineSegment(sketch, "E1832", {"start": v(88.09, 23.21) * mm, "end": v(88.04, 23.15) * mm});
            skLineSegment(sketch, "E1833", {"start": v(88.04, 23.15) * mm, "end": v(88, 23.1) * mm});
            skLineSegment(sketch, "E1834", {"start": v(88, 23.1) * mm, "end": v(87.95, 23.03) * mm});
            skLineSegment(sketch, "E1835", {"start": v(87.95, 23.03) * mm, "end": v(87.9, 22.97) * mm});
            skLineSegment(sketch, "E1836", {"start": v(87.9, 22.97) * mm, "end": v(87.87, 22.9) * mm});
            skLineSegment(sketch, "E1837", {"start": v(87.87, 22.9) * mm, "end": v(87.83, 22.84) * mm});
            skLineSegment(sketch, "E1838", {"start": v(87.83, 22.84) * mm, "end": v(87.8, 22.78) * mm});
            skLineSegment(sketch, "E1839", {"start": v(87.8, 22.78) * mm, "end": v(87.77, 22.71) * mm});
            skLineSegment(sketch, "E1840", {"start": v(87.77, 22.71) * mm, "end": v(87.74, 22.64) * mm});
            skLineSegment(sketch, "E1841", {"start": v(87.74, 22.64) * mm, "end": v(87.7, 22.57) * mm});
            skLineSegment(sketch, "E1842", {"start": v(87.7, 22.57) * mm, "end": v(87.68, 22.5) * mm});
            skLineSegment(sketch, "E1843", {"start": v(87.68, 22.5) * mm, "end": v(87.66, 22.43) * mm});
            skLineSegment(sketch, "E1844", {"start": v(87.66, 22.43) * mm, "end": v(87.64, 22.36) * mm});
            skLineSegment(sketch, "E1845", {"start": v(87.64, 22.36) * mm, "end": v(87.62, 22.29) * mm});
            skLineSegment(sketch, "E1846", {"start": v(87.62, 22.29) * mm, "end": v(87.6, 22.22) * mm});
            skLineSegment(sketch, "E1847", {"start": v(87.6, 22.22) * mm, "end": v(87.6, 22.14) * mm});
            skLineSegment(sketch, "E1848", {"start": v(87.6, 22.14) * mm, "end": v(87.58, 22.07) * mm});
            skLineSegment(sketch, "E1849", {"start": v(87.57, 22) * mm, "end": v(87.57, 21.92) * mm});
            skLineSegment(sketch, "E1850", {"start": v(87.57, 21.92) * mm, "end": v(87.57, 21.84) * mm});
            skLineSegment(sketch, "E1851", {"start": v(87.57, 21.84) * mm, "end": v(87.57, 21.77) * mm});
            skLineSegment(sketch, "E1852", {"start": v(87.57, 21.77) * mm, "end": v(87.57, 21.7) * mm});
            skLineSegment(sketch, "E1853", {"start": v(87.58, 21.55) * mm, "end": v(87.6, 21.47) * mm});
            skLineSegment(sketch, "E1854", {"start": v(87.6, 21.47) * mm, "end": v(87.6, 21.4) * mm});
            skLineSegment(sketch, "E1855", {"start": v(87.6, 21.4) * mm, "end": v(87.62, 21.33) * mm});
            skLineSegment(sketch, "E1856", {"start": v(87.62, 21.33) * mm, "end": v(87.64, 21.25) * mm});
            skLineSegment(sketch, "E1857", {"start": v(87.64, 21.25) * mm, "end": v(87.66, 21.18) * mm});
            skLineSegment(sketch, "E1858", {"start": v(87.7, 21.04) * mm, "end": v(87.74, 20.97) * mm});
            skLineSegment(sketch, "E1859", {"start": v(87.74, 20.97) * mm, "end": v(87.77, 20.9) * mm});
            skLineSegment(sketch, "E1860", {"start": v(87.77, 20.9) * mm, "end": v(87.8, 20.84) * mm});
            skLineSegment(sketch, "E1861", {"start": v(87.8, 20.84) * mm, "end": v(87.83, 20.77) * mm});
            skLineSegment(sketch, "E1862", {"start": v(87.83, 20.77) * mm, "end": v(87.87, 20.7) * mm});
            skLineSegment(sketch, "E1863", {"start": v(87.87, 20.7) * mm, "end": v(87.9, 20.64) * mm});
            skLineSegment(sketch, "E1864", {"start": v(87.9, 20.64) * mm, "end": v(87.95, 20.58) * mm});
            skLineSegment(sketch, "E1865", {"start": v(87.95, 20.58) * mm, "end": v(88, 20.52) * mm});
            skLineSegment(sketch, "E1866", {"start": v(88, 20.52) * mm, "end": v(88.04, 20.46) * mm});
            skLineSegment(sketch, "E1867", {"start": v(88.04, 20.46) * mm, "end": v(88.09, 20.4) * mm});
            skLineSegment(sketch, "E1868", {"start": v(88.14, 20.35) * mm, "end": v(88.19, 20.3) * mm});
            skLineSegment(sketch, "E1869", {"start": v(88.19, 20.3) * mm, "end": v(88.24, 20.24) * mm});
            skLineSegment(sketch, "E1870", {"start": v(88.24, 20.24) * mm, "end": v(88.3, 20.2) * mm});
            skLineSegment(sketch, "E1871", {"start": v(88.3, 20.2) * mm, "end": v(88.35, 20.14) * mm});
            skLineSegment(sketch, "E1872", {"start": v(88.35, 20.14) * mm, "end": v(88.41, 20.1) * mm});
            skLineSegment(sketch, "E1873", {"start": v(88.41, 20.1) * mm, "end": v(88.47, 20.05) * mm});
            skLineSegment(sketch, "E1874", {"start": v(88.47, 20.05) * mm, "end": v(88.54, 20.01) * mm});
            skLineSegment(sketch, "E1875", {"start": v(88.54, 20.01) * mm, "end": v(88.6, 19.97) * mm});
            skLineSegment(sketch, "E1876", {"start": v(88.6, 19.97) * mm, "end": v(88.66, 19.93) * mm});
            skLineSegment(sketch, "E1877", {"start": v(90.32, 19.75) * mm, "end": v(90.4, 19.77) * mm});
            skLineSegment(sketch, "E1878", {"start": v(90.4, 19.77) * mm, "end": v(90.47, 19.8) * mm});
            skLineSegment(sketch, "E1879", {"start": v(90.47, 19.8) * mm, "end": v(90.53, 19.82) * mm});
            skLineSegment(sketch, "E1880", {"start": v(90.53, 19.82) * mm, "end": v(90.6, 19.85) * mm});
            skLineSegment(sketch, "E1881", {"start": v(90.6, 19.85) * mm, "end": v(90.67, 19.88) * mm});
            skLineSegment(sketch, "E1882", {"start": v(90.74, 19.92) * mm, "end": v(90.8, 19.95) * mm});
            skLineSegment(sketch, "E1883", {"start": v(90.8, 19.95) * mm, "end": v(90.87, 20) * mm});
            skLineSegment(sketch, "E1884", {"start": v(90.87, 20) * mm, "end": v(90.93, 20.03) * mm});
            skLineSegment(sketch, "E1885", {"start": v(90.93, 20.03) * mm, "end": v(90.99, 20.07) * mm});
            skLineSegment(sketch, "E1886", {"start": v(90.99, 20.07) * mm, "end": v(91.05, 20.12) * mm});
            skLineSegment(sketch, "E1887", {"start": v(91.05, 20.12) * mm, "end": v(91.1, 20.17) * mm});
            skLineSegment(sketch, "E1888", {"start": v(91.1, 20.17) * mm, "end": v(91.16, 20.22) * mm});
            skLineSegment(sketch, "E1889", {"start": v(91.16, 20.22) * mm, "end": v(91.22, 20.27) * mm});
            skLineSegment(sketch, "E1890", {"start": v(91.22, 20.27) * mm, "end": v(91.27, 20.32) * mm});
            skLineSegment(sketch, "E1891", {"start": v(91.32, 20.38) * mm, "end": v(91.37, 20.43) * mm});
            skLineSegment(sketch, "E1892", {"start": v(91.37, 20.43) * mm, "end": v(91.42, 20.5) * mm});
            skLineSegment(sketch, "E1893", {"start": v(91.42, 20.5) * mm, "end": v(91.46, 20.55) * mm});
            skLineSegment(sketch, "E1894", {"start": v(91.46, 20.55) * mm, "end": v(91.5, 20.61) * mm});
            skLineSegment(sketch, "E1895", {"start": v(91.5, 20.61) * mm, "end": v(91.54, 20.67) * mm});
            skLineSegment(sketch, "E1896", {"start": v(91.54, 20.67) * mm, "end": v(91.58, 20.74) * mm});
            skLineSegment(sketch, "E1897", {"start": v(91.58, 20.74) * mm, "end": v(91.62, 20.8) * mm});
            skLineSegment(sketch, "E1898", {"start": v(91.62, 20.8) * mm, "end": v(91.65, 20.87) * mm});
            skLineSegment(sketch, "E1899", {"start": v(91.65, 20.87) * mm, "end": v(91.68, 20.94) * mm});
            skLineSegment(sketch, "E1900", {"start": v(91.68, 20.94) * mm, "end": v(91.71, 21) * mm});
            skLineSegment(sketch, "E1901", {"start": v(91.71, 21) * mm, "end": v(91.74, 21.08) * mm});
            skLineSegment(sketch, "E1902", {"start": v(91.86, 21.66) * mm, "end": v(91.86, 21.73) * mm});
            skLineSegment(sketch, "E1903", {"start": v(91.86, 21.73) * mm, "end": v(91.87, 21.8) * mm});
            skLineSegment(sketch, "E1904", {"start": v(334.32, -81.83) * mm, "end": v(349.32, -81.83) * mm});
            skLineSegment(sketch, "E1905", {"start": v(349.32, -81.83) * mm, "end": v(349.32, 38.17) * mm});
            skLineSegment(sketch, "E1906", {"start": v(349.32, 38.17) * mm, "end": v(334.32, 38.17) * mm});
            skLineSegment(sketch, "E1907", {"start": v(334.32, 38.17) * mm, "end": v(334.32, -81.83) * mm});
            skLineSegment(sketch, "E1908", {"start": v(170.03, 60.76) * mm, "end": v(170.03, 45.76) * mm});
            skLineSegment(sketch, "E1909", {"start": v(170.03, 45.76) * mm, "end": v(325.03, 45.76) * mm});
            skLineSegment(sketch, "E1910", {"start": v(325.03, 45.76) * mm, "end": v(325.03, 60.76) * mm});
            skLineSegment(sketch, "E1911", {"start": v(325.03, 60.76) * mm, "end": v(170.03, 60.76) * mm});
            skLineSegment(sketch, "E1912", {"start": v(182.39, 104.55) * mm, "end": v(182.39, 89.55) * mm});
            skLineSegment(sketch, "E1913", {"start": v(182.39, 89.55) * mm, "end": v(322.39, 89.55) * mm});
            skLineSegment(sketch, "E1914", {"start": v(322.39, 89.55) * mm, "end": v(322.39, 104.55) * mm});
            skLineSegment(sketch, "E1915", {"start": v(322.39, 104.55) * mm, "end": v(182.39, 104.55) * mm});
            skLineSegment(sketch, "E1916", {"start": v(-64.72, 83.54) * mm, "end": v(-64.65, 83.54) * mm});
            skLineSegment(sketch, "E1917", {"start": v(-64.2, 83.6) * mm, "end": v(-64.13, 83.62) * mm});
            skLineSegment(sketch, "E1918", {"start": v(-63.4, 84) * mm, "end": v(-63.34, 84.04) * mm});
            skLineSegment(sketch, "E1919", {"start": v(-63.29, 84.09) * mm, "end": v(-63.23, 84.14) * mm});
            skLineSegment(sketch, "E1920", {"start": v(-62.62, 85.23) * mm, "end": v(-62.6, 85.3) * mm});
            skLineSegment(sketch, "E1921", {"start": v(-62.58, 85.45) * mm, "end": v(-62.58, 85.52) * mm});
            skLineSegment(sketch, "E1922", {"start": v(-62.57, 85.6) * mm, "end": v(-62.57, 85.67) * mm});
            skLineSegment(sketch, "E1923", {"start": v(-62.57, 85.75) * mm, "end": v(-62.57, 85.82) * mm});
            skLineSegment(sketch, "E1924", {"start": v(-62.65, 86.26) * mm, "end": v(-62.67, 86.34) * mm});
            skLineSegment(sketch, "E1925", {"start": v(-63.82, 87.64) * mm, "end": v(-63.88, 87.67) * mm});
            skLineSegment(sketch, "E1926", {"start": v(-64.46, 87.83) * mm, "end": v(-64.53, 87.83) * mm});
            skLineSegment(sketch, "E1927", {"start": v(-64.6, 87.84) * mm, "end": v(-64.68, 87.84) * mm});
            skLineSegment(sketch, "E1928", {"start": v(-64.68, 87.84) * mm, "end": v(-64.76, 87.84) * mm});
            skLineSegment(sketch, "E1929", {"start": v(-64.98, 87.83) * mm, "end": v(-65.05, 87.82) * mm});
            skLineSegment(sketch, "E1930", {"start": v(-65.35, 87.75) * mm, "end": v(-65.42, 87.73) * mm});
            skLineSegment(sketch, "E1931", {"start": v(-66, 87.41) * mm, "end": v(-66.07, 87.37) * mm});
            skLineSegment(sketch, "E1932", {"start": v(-66.18, 87.27) * mm, "end": v(-66.23, 87.22) * mm});
            skLineSegment(sketch, "E1933", {"start": v(-66.34, 87.11) * mm, "end": v(-66.38, 87.05) * mm});
            skLineSegment(sketch, "E1934", {"start": v(-66.85, 85.97) * mm, "end": v(-66.86, 85.9) * mm});
            skLineSegment(sketch, "E1935", {"start": v(-66.87, 85.82) * mm, "end": v(-66.87, 85.75) * mm});
            skLineSegment(sketch, "E1936", {"start": v(-66.87, 85.67) * mm, "end": v(-66.87, 85.6) * mm});
            skLineSegment(sketch, "E1937", {"start": v(-66.86, 85.52) * mm, "end": v(-66.86, 85.45) * mm});
            skLineSegment(sketch, "E1938", {"start": v(-66.4, 84.36) * mm, "end": v(-66.36, 84.3) * mm});
            skLineSegment(sketch, "E1939", {"start": v(-66.26, 84.2) * mm, "end": v(-66.2, 84.14) * mm});
            skLineSegment(sketch, "E1940", {"start": v(-65.52, 83.7) * mm, "end": v(-65.45, 83.67) * mm});
            skLineSegment(sketch, "E1941", {"start": v(-65.1, 83.57) * mm, "end": v(-65.02, 83.56) * mm});
            skLineSegment(sketch, "E1942", {"start": v(-64.87, 83.55) * mm, "end": v(-64.8, 83.54) * mm});
            skLineSegment(sketch, "E1943", {"start": v(65.28, 83.54) * mm, "end": v(65.35, 83.54) * mm});
            skLineSegment(sketch, "E1944", {"start": v(65.35, 83.54) * mm, "end": v(65.43, 83.55) * mm});
            skLineSegment(sketch, "E1945", {"start": v(65.94, 83.65) * mm, "end": v(66.01, 83.67) * mm});
            skLineSegment(sketch, "E1946", {"start": v(66.01, 83.67) * mm, "end": v(66.08, 83.7) * mm});
            skLineSegment(sketch, "E1947", {"start": v(66.15, 83.73) * mm, "end": v(66.22, 83.76) * mm});
            skLineSegment(sketch, "E1948", {"start": v(66.22, 83.76) * mm, "end": v(66.28, 83.8) * mm});
            skLineSegment(sketch, "E1949", {"start": v(66.28, 83.8) * mm, "end": v(66.35, 83.83) * mm});
            skLineSegment(sketch, "E1950", {"start": v(66.41, 83.87) * mm, "end": v(66.48, 83.9) * mm});
            skLineSegment(sketch, "E1951", {"start": v(66.48, 83.9) * mm, "end": v(66.54, 83.95) * mm});
            skLineSegment(sketch, "E1952", {"start": v(66.54, 83.95) * mm, "end": v(66.6, 84) * mm});
            skLineSegment(sketch, "E1953", {"start": v(66.6, 84) * mm, "end": v(66.66, 84.04) * mm});
            skLineSegment(sketch, "E1954", {"start": v(66.66, 84.04) * mm, "end": v(66.71, 84.09) * mm});
            skLineSegment(sketch, "E1955", {"start": v(66.71, 84.09) * mm, "end": v(66.77, 84.14) * mm});
            skLineSegment(sketch, "E1956", {"start": v(66.87, 84.25) * mm, "end": v(66.92, 84.3) * mm});
            skLineSegment(sketch, "E1957", {"start": v(66.92, 84.3) * mm, "end": v(66.97, 84.36) * mm});
            skLineSegment(sketch, "E1958", {"start": v(66.97, 84.36) * mm, "end": v(67.01, 84.42) * mm});
            skLineSegment(sketch, "E1959", {"start": v(67.01, 84.42) * mm, "end": v(67.06, 84.48) * mm});
            skLineSegment(sketch, "E1960", {"start": v(67.06, 84.48) * mm, "end": v(67.1, 84.54) * mm});
            skLineSegment(sketch, "E1961", {"start": v(67.1, 84.54) * mm, "end": v(67.14, 84.6) * mm});
            skLineSegment(sketch, "E1962", {"start": v(67.17, 84.67) * mm, "end": v(67.2, 84.74) * mm});
            skLineSegment(sketch, "E1963", {"start": v(67.2, 84.74) * mm, "end": v(67.24, 84.8) * mm});
            skLineSegment(sketch, "E1964", {"start": v(67.3, 84.94) * mm, "end": v(67.32, 85.01) * mm});
            skLineSegment(sketch, "E1965", {"start": v(67.32, 85.01) * mm, "end": v(67.34, 85.09) * mm});
            skLineSegment(sketch, "E1966", {"start": v(67.36, 85.16) * mm, "end": v(67.38, 85.23) * mm});
            skLineSegment(sketch, "E1967", {"start": v(67.38, 85.23) * mm, "end": v(67.4, 85.3) * mm});
            skLineSegment(sketch, "E1968", {"start": v(67.4, 85.38) * mm, "end": v(67.42, 85.45) * mm});
            skLineSegment(sketch, "E1969", {"start": v(67.42, 85.45) * mm, "end": v(67.42, 85.52) * mm});
            skLineSegment(sketch, "E1970", {"start": v(67.42, 85.52) * mm, "end": v(67.43, 85.6) * mm});
            skLineSegment(sketch, "E1971", {"start": v(67.43, 85.6) * mm, "end": v(67.43, 85.67) * mm});
            skLineSegment(sketch, "E1972", {"start": v(67.43, 85.67) * mm, "end": v(67.43, 85.75) * mm});
            skLineSegment(sketch, "E1973", {"start": v(67.43, 85.75) * mm, "end": v(67.43, 85.82) * mm});
            skLineSegment(sketch, "E1974", {"start": v(67.43, 85.82) * mm, "end": v(67.42, 85.9) * mm});
            skLineSegment(sketch, "E1975", {"start": v(67.41, 85.97) * mm, "end": v(67.4, 86.05) * mm});
            skLineSegment(sketch, "E1976", {"start": v(67.4, 86.05) * mm, "end": v(67.39, 86.12) * mm});
            skLineSegment(sketch, "E1977", {"start": v(67.39, 86.12) * mm, "end": v(67.37, 86.2) * mm});
            skLineSegment(sketch, "E1978", {"start": v(67.35, 86.26) * mm, "end": v(67.33, 86.34) * mm});
            skLineSegment(sketch, "E1979", {"start": v(67.33, 86.34) * mm, "end": v(67.3, 86.4) * mm});
            skLineSegment(sketch, "E1980", {"start": v(67.3, 86.4) * mm, "end": v(67.28, 86.48) * mm});
            skLineSegment(sketch, "E1981", {"start": v(67.25, 86.55) * mm, "end": v(67.22, 86.61) * mm});
            skLineSegment(sketch, "E1982", {"start": v(67.22, 86.61) * mm, "end": v(67.19, 86.68) * mm});
            skLineSegment(sketch, "E1983", {"start": v(67.19, 86.68) * mm, "end": v(67.15, 86.75) * mm});
            skLineSegment(sketch, "E1984", {"start": v(67.15, 86.75) * mm, "end": v(67.12, 86.81) * mm});
            skLineSegment(sketch, "E1985", {"start": v(67.12, 86.81) * mm, "end": v(67.08, 86.87) * mm});
            skLineSegment(sketch, "E1986", {"start": v(67.08, 86.87) * mm, "end": v(67.03, 86.93) * mm});
            skLineSegment(sketch, "E1987", {"start": v(66.8, 87.22) * mm, "end": v(66.74, 87.27) * mm});
            skLineSegment(sketch, "E1988", {"start": v(66.68, 87.32) * mm, "end": v(66.63, 87.37) * mm});
            skLineSegment(sketch, "E1989", {"start": v(66.63, 87.37) * mm, "end": v(66.57, 87.41) * mm});
            skLineSegment(sketch, "E1990", {"start": v(66.57, 87.41) * mm, "end": v(66.5, 87.46) * mm});
            skLineSegment(sketch, "E1991", {"start": v(66.5, 87.46) * mm, "end": v(66.45, 87.5) * mm});
            skLineSegment(sketch, "E1992", {"start": v(66.45, 87.5) * mm, "end": v(66.38, 87.54) * mm});
            skLineSegment(sketch, "E1993", {"start": v(66.38, 87.54) * mm, "end": v(66.32, 87.58) * mm});
            skLineSegment(sketch, "E1994", {"start": v(66.32, 87.58) * mm, "end": v(66.25, 87.61) * mm});
            skLineSegment(sketch, "E1995", {"start": v(66.25, 87.61) * mm, "end": v(66.18, 87.64) * mm});
            skLineSegment(sketch, "E1996", {"start": v(66.18, 87.64) * mm, "end": v(66.12, 87.67) * mm});
            skLineSegment(sketch, "E1997", {"start": v(66.05, 87.7) * mm, "end": v(65.98, 87.73) * mm});
            skLineSegment(sketch, "E1998", {"start": v(65.98, 87.73) * mm, "end": v(65.9, 87.75) * mm});
            skLineSegment(sketch, "E1999", {"start": v(65.76, 87.79) * mm, "end": v(65.69, 87.8) * mm});
            skLineSegment(sketch, "E2000", {"start": v(65.69, 87.8) * mm, "end": v(65.61, 87.82) * mm});
            skLineSegment(sketch, "E2001", {"start": v(65.54, 87.83) * mm, "end": v(65.47, 87.83) * mm});
            skLineSegment(sketch, "E2002", {"start": v(65.47, 87.83) * mm, "end": v(65.4, 87.84) * mm});
            skLineSegment(sketch, "E2003", {"start": v(65.4, 87.84) * mm, "end": v(65.32, 87.84) * mm});
            skLineSegment(sketch, "E2004", {"start": v(65.32, 87.84) * mm, "end": v(65.24, 87.84) * mm});
            skLineSegment(sketch, "E2005", {"start": v(65.24, 87.84) * mm, "end": v(65.17, 87.84) * mm});
            skLineSegment(sketch, "E2006", {"start": v(65.1, 87.83) * mm, "end": v(65.02, 87.83) * mm});
            skLineSegment(sketch, "E2007", {"start": v(64.87, 87.8) * mm, "end": v(64.8, 87.79) * mm});
            skLineSegment(sketch, "E2008", {"start": v(64.73, 87.77) * mm, "end": v(64.65, 87.75) * mm});
            skLineSegment(sketch, "E2009", {"start": v(64.65, 87.75) * mm, "end": v(64.58, 87.73) * mm});
            skLineSegment(sketch, "E2010", {"start": v(64.44, 87.67) * mm, "end": v(64.38, 87.64) * mm});
            skLineSegment(sketch, "E2011", {"start": v(64.38, 87.64) * mm, "end": v(64.3, 87.61) * mm});
            skLineSegment(sketch, "E2012", {"start": v(64.24, 87.58) * mm, "end": v(64.18, 87.54) * mm});
            skLineSegment(sketch, "E2013", {"start": v(64.11, 87.5) * mm, "end": v(64.05, 87.46) * mm});
            skLineSegment(sketch, "E2014", {"start": v(64, 87.41) * mm, "end": v(63.93, 87.37) * mm});
            skLineSegment(sketch, "E2015", {"start": v(63.93, 87.37) * mm, "end": v(63.88, 87.32) * mm});
            skLineSegment(sketch, "E2016", {"start": v(63.88, 87.32) * mm, "end": v(63.82, 87.27) * mm});
            skLineSegment(sketch, "E2017", {"start": v(63.71, 87.17) * mm, "end": v(63.66, 87.11) * mm});
            skLineSegment(sketch, "E2018", {"start": v(63.66, 87.11) * mm, "end": v(63.62, 87.05) * mm});
            skLineSegment(sketch, "E2019", {"start": v(63.62, 87.05) * mm, "end": v(63.57, 87) * mm});
            skLineSegment(sketch, "E2020", {"start": v(63.4, 86.75) * mm, "end": v(63.37, 86.68) * mm});
            skLineSegment(sketch, "E2021", {"start": v(63.37, 86.68) * mm, "end": v(63.34, 86.61) * mm});
            skLineSegment(sketch, "E2022", {"start": v(63.34, 86.61) * mm, "end": v(63.3, 86.55) * mm});
            skLineSegment(sketch, "E2023", {"start": v(63.3, 86.55) * mm, "end": v(63.28, 86.48) * mm});
            skLineSegment(sketch, "E2024", {"start": v(63.25, 86.4) * mm, "end": v(63.23, 86.34) * mm});
            skLineSegment(sketch, "E2025", {"start": v(63.13, 85.82) * mm, "end": v(63.13, 85.75) * mm});
            skLineSegment(sketch, "E2026", {"start": v(63.13, 85.75) * mm, "end": v(63.13, 85.67) * mm});
            skLineSegment(sketch, "E2027", {"start": v(63.13, 85.67) * mm, "end": v(63.13, 85.6) * mm});
            skLineSegment(sketch, "E2028", {"start": v(63.13, 85.6) * mm, "end": v(63.14, 85.52) * mm});
            skLineSegment(sketch, "E2029", {"start": v(63.14, 85.52) * mm, "end": v(63.14, 85.45) * mm});
            skLineSegment(sketch, "E2030", {"start": v(63.14, 85.45) * mm, "end": v(63.15, 85.38) * mm});
            skLineSegment(sketch, "E2031", {"start": v(63.17, 85.3) * mm, "end": v(63.18, 85.23) * mm});
            skLineSegment(sketch, "E2032", {"start": v(63.22, 85.09) * mm, "end": v(63.24, 85.01) * mm});
            skLineSegment(sketch, "E2033", {"start": v(63.24, 85.01) * mm, "end": v(63.26, 84.94) * mm});
            skLineSegment(sketch, "E2034", {"start": v(63.26, 84.94) * mm, "end": v(63.3, 84.87) * mm});
            skLineSegment(sketch, "E2035", {"start": v(63.3, 84.87) * mm, "end": v(63.32, 84.8) * mm});
            skLineSegment(sketch, "E2036", {"start": v(63.32, 84.8) * mm, "end": v(63.35, 84.74) * mm});
            skLineSegment(sketch, "E2037", {"start": v(63.55, 84.42) * mm, "end": v(63.6, 84.36) * mm});
            skLineSegment(sketch, "E2038", {"start": v(63.6, 84.36) * mm, "end": v(63.64, 84.3) * mm});
            skLineSegment(sketch, "E2039", {"start": v(63.69, 84.25) * mm, "end": v(63.74, 84.2) * mm});
            skLineSegment(sketch, "E2040", {"start": v(63.8, 84.14) * mm, "end": v(63.85, 84.09) * mm});
            skLineSegment(sketch, "E2041", {"start": v(63.85, 84.09) * mm, "end": v(63.9, 84.04) * mm});
            skLineSegment(sketch, "E2042", {"start": v(63.9, 84.04) * mm, "end": v(63.96, 84) * mm});
            skLineSegment(sketch, "E2043", {"start": v(63.96, 84) * mm, "end": v(64.02, 83.95) * mm});
            skLineSegment(sketch, "E2044", {"start": v(64.02, 83.95) * mm, "end": v(64.08, 83.9) * mm});
            skLineSegment(sketch, "E2045", {"start": v(64.08, 83.9) * mm, "end": v(64.15, 83.87) * mm});
            skLineSegment(sketch, "E2046", {"start": v(64.15, 83.87) * mm, "end": v(64.21, 83.83) * mm});
            skLineSegment(sketch, "E2047", {"start": v(64.21, 83.83) * mm, "end": v(64.28, 83.8) * mm});
            skLineSegment(sketch, "E2048", {"start": v(64.28, 83.8) * mm, "end": v(64.34, 83.76) * mm});
            skLineSegment(sketch, "E2049", {"start": v(64.48, 83.7) * mm, "end": v(64.55, 83.67) * mm});
            skLineSegment(sketch, "E2050", {"start": v(64.55, 83.67) * mm, "end": v(64.62, 83.65) * mm});
            skLineSegment(sketch, "E2051", {"start": v(64.62, 83.65) * mm, "end": v(64.7, 83.62) * mm});
            skLineSegment(sketch, "E2052", {"start": v(64.76, 83.6) * mm, "end": v(64.84, 83.59) * mm});
            skLineSegment(sketch, "E2053", {"start": v(64.84, 83.59) * mm, "end": v(64.9, 83.57) * mm});
            skLineSegment(sketch, "E2054", {"start": v(64.9, 83.57) * mm, "end": v(64.98, 83.56) * mm});
            skLineSegment(sketch, "E2055", {"start": v(65.13, 83.55) * mm, "end": v(65.2, 83.54) * mm});
            skLineSegment(sketch, "E2056", {"start": v(65.2, 83.54) * mm, "end": v(65.28, 83.54) * mm});
            skLineSegment(sketch, "E2057", {"start": v(0.28, 81.94) * mm, "end": v(0.4, 81.94) * mm});
            skLineSegment(sketch, "E2058", {"start": v(0.4, 81.94) * mm, "end": v(0.54, 81.95) * mm});
            skLineSegment(sketch, "E2059", {"start": v(0.54, 81.95) * mm, "end": v(0.67, 81.96) * mm});
            skLineSegment(sketch, "E2060", {"start": v(1.56, 82.17) * mm, "end": v(1.68, 82.21) * mm});
            skLineSegment(sketch, "E2061", {"start": v(1.68, 82.21) * mm, "end": v(1.8, 82.26) * mm});
            skLineSegment(sketch, "E2062", {"start": v(1.92, 82.32) * mm, "end": v(2.03, 82.38) * mm});
            skLineSegment(sketch, "E2063", {"start": v(2.03, 82.38) * mm, "end": v(2.15, 82.44) * mm});
            skLineSegment(sketch, "E2064", {"start": v(2.15, 82.44) * mm, "end": v(2.26, 82.5) * mm});
            skLineSegment(sketch, "E2065", {"start": v(2.26, 82.5) * mm, "end": v(2.37, 82.58) * mm});
            skLineSegment(sketch, "E2066", {"start": v(2.68, 82.81) * mm, "end": v(2.78, 82.9) * mm});
            skLineSegment(sketch, "E2067", {"start": v(2.87, 82.98) * mm, "end": v(2.97, 83.08) * mm});
            skLineSegment(sketch, "E2068", {"start": v(3.05, 83.17) * mm, "end": v(3.14, 83.27) * mm});
            skLineSegment(sketch, "E2069", {"start": v(3.14, 83.27) * mm, "end": v(3.22, 83.37) * mm});
            skLineSegment(sketch, "E2070", {"start": v(3.52, 83.8) * mm, "end": v(3.58, 83.91) * mm});
            skLineSegment(sketch, "E2071", {"start": v(3.58, 83.91) * mm, "end": v(3.64, 84.03) * mm});
            skLineSegment(sketch, "E2072", {"start": v(3.64, 84.03) * mm, "end": v(3.7, 84.15) * mm});
            skLineSegment(sketch, "E2073", {"start": v(3.7, 84.15) * mm, "end": v(3.75, 84.26) * mm});
            skLineSegment(sketch, "E2074", {"start": v(3.91, 84.76) * mm, "end": v(3.94, 84.89) * mm});
            skLineSegment(sketch, "E2075", {"start": v(3.97, 85.01) * mm, "end": v(3.99, 85.14) * mm});
            skLineSegment(sketch, "E2076", {"start": v(4.02, 85.4) * mm, "end": v(4.03, 85.53) * mm});
            skLineSegment(sketch, "E2077", {"start": v(4.03, 85.53) * mm, "end": v(4.03, 85.66) * mm});
            skLineSegment(sketch, "E2078", {"start": v(4.03, 85.66) * mm, "end": v(4.03, 85.8) * mm});
            skLineSegment(sketch, "E2079", {"start": v(4.03, 85.8) * mm, "end": v(4.02, 85.92) * mm});
            skLineSegment(sketch, "E2080", {"start": v(4.02, 85.92) * mm, "end": v(4.01, 86.05) * mm});
            skLineSegment(sketch, "E2081", {"start": v(3.93, 86.56) * mm, "end": v(3.9, 86.69) * mm});
            skLineSegment(sketch, "E2082", {"start": v(3.9, 86.69) * mm, "end": v(3.86, 86.81) * mm});
            skLineSegment(sketch, "E2083", {"start": v(3.86, 86.81) * mm, "end": v(3.82, 86.94) * mm});
            skLineSegment(sketch, "E2084", {"start": v(3.77, 87.06) * mm, "end": v(3.72, 87.18) * mm});
            skLineSegment(sketch, "E2085", {"start": v(3.61, 87.42) * mm, "end": v(3.55, 87.53) * mm});
            skLineSegment(sketch, "E2086", {"start": v(3.55, 87.53) * mm, "end": v(3.48, 87.64) * mm});
            skLineSegment(sketch, "E2087", {"start": v(3.48, 87.64) * mm, "end": v(3.41, 87.75) * mm});
            skLineSegment(sketch, "E2088", {"start": v(3.41, 87.75) * mm, "end": v(3.34, 87.86) * mm});
            skLineSegment(sketch, "E2089", {"start": v(3.26, 87.96) * mm, "end": v(3.18, 88.07) * mm});
            skLineSegment(sketch, "E2090", {"start": v(3.18, 88.07) * mm, "end": v(3.1, 88.17) * mm});
            skLineSegment(sketch, "E2091", {"start": v(2.73, 88.53) * mm, "end": v(2.63, 88.62) * mm});
            skLineSegment(sketch, "E2092", {"start": v(2.31, 88.84) * mm, "end": v(2.2, 88.91) * mm});
            skLineSegment(sketch, "E2093", {"start": v(2.2, 88.91) * mm, "end": v(2.09, 88.98) * mm});
            skLineSegment(sketch, "E2094", {"start": v(2.09, 88.98) * mm, "end": v(1.97, 89.04) * mm});
            skLineSegment(sketch, "E2095", {"start": v(1.97, 89.04) * mm, "end": v(1.86, 89.1) * mm});
            skLineSegment(sketch, "E2096", {"start": v(1, 89.37) * mm, "end": v(0.86, 89.4) * mm});
            skLineSegment(sketch, "E2097", {"start": v(0.6, 89.43) * mm, "end": v(0.47, 89.44) * mm});
            skLineSegment(sketch, "E2098", {"start": v(0.47, 89.44) * mm, "end": v(0.34, 89.44) * mm});
            skLineSegment(sketch, "E2099", {"start": v(0.34, 89.44) * mm, "end": v(0.21, 89.44) * mm});
            skLineSegment(sketch, "E2100", {"start": v(0.21, 89.44) * mm, "end": v(0.08, 89.44) * mm});
            skLineSegment(sketch, "E2101", {"start": v(0.08, 89.44) * mm, "end": v(-0.05, 89.43) * mm});
            skLineSegment(sketch, "E2102", {"start": v(-0.3, 89.4) * mm, "end": v(-0.43, 89.37) * mm});
            skLineSegment(sketch, "E2103", {"start": v(-0.43, 89.37) * mm, "end": v(-0.56, 89.35) * mm});
            skLineSegment(sketch, "E2104", {"start": v(-0.56, 89.35) * mm, "end": v(-0.69, 89.32) * mm});
            skLineSegment(sketch, "E2105", {"start": v(-1.3, 89.1) * mm, "end": v(-1.41, 89.04) * mm});
            skLineSegment(sketch, "E2106", {"start": v(-1.41, 89.04) * mm, "end": v(-1.53, 88.98) * mm});
            skLineSegment(sketch, "E2107", {"start": v(-1.53, 88.98) * mm, "end": v(-1.64, 88.91) * mm});
            skLineSegment(sketch, "E2108", {"start": v(-1.75, 88.84) * mm, "end": v(-1.86, 88.77) * mm});
            skLineSegment(sketch, "E2109", {"start": v(-2.07, 88.62) * mm, "end": v(-2.17, 88.53) * mm});
            skLineSegment(sketch, "E2110", {"start": v(-2.17, 88.53) * mm, "end": v(-2.27, 88.45) * mm});
            skLineSegment(sketch, "E2111", {"start": v(-2.45, 88.26) * mm, "end": v(-2.54, 88.17) * mm});
            skLineSegment(sketch, "E2112", {"start": v(-2.62, 88.07) * mm, "end": v(-2.7, 87.96) * mm});
            skLineSegment(sketch, "E2113", {"start": v(-2.85, 87.75) * mm, "end": v(-2.92, 87.64) * mm});
            skLineSegment(sketch, "E2114", {"start": v(-2.92, 87.64) * mm, "end": v(-2.99, 87.53) * mm});
            skLineSegment(sketch, "E2115", {"start": v(-2.99, 87.53) * mm, "end": v(-3.05, 87.42) * mm});
            skLineSegment(sketch, "E2116", {"start": v(-3.05, 87.42) * mm, "end": v(-3.1, 87.3) * mm});
            skLineSegment(sketch, "E2117", {"start": v(-3.21, 87.06) * mm, "end": v(-3.26, 86.94) * mm});
            skLineSegment(sketch, "E2118", {"start": v(-3.3, 86.81) * mm, "end": v(-3.34, 86.69) * mm});
            skLineSegment(sketch, "E2119", {"start": v(-3.34, 86.69) * mm, "end": v(-3.37, 86.56) * mm});
            skLineSegment(sketch, "E2120", {"start": v(-3.44, 86.18) * mm, "end": v(-3.45, 86.05) * mm});
            skLineSegment(sketch, "E2121", {"start": v(-3.46, 85.92) * mm, "end": v(-3.47, 85.8) * mm});
            skLineSegment(sketch, "E2122", {"start": v(-3.47, 85.8) * mm, "end": v(-3.47, 85.66) * mm});
            skLineSegment(sketch, "E2123", {"start": v(-3.47, 85.66) * mm, "end": v(-3.47, 85.53) * mm});
            skLineSegment(sketch, "E2124", {"start": v(-3.47, 85.53) * mm, "end": v(-3.46, 85.4) * mm});
            skLineSegment(sketch, "E2125", {"start": v(-3.43, 85.14) * mm, "end": v(-3.4, 85.01) * mm});
            skLineSegment(sketch, "E2126", {"start": v(-3.4, 85.01) * mm, "end": v(-3.38, 84.89) * mm});
            skLineSegment(sketch, "E2127", {"start": v(-3.38, 84.89) * mm, "end": v(-3.35, 84.76) * mm});
            skLineSegment(sketch, "E2128", {"start": v(-3.35, 84.76) * mm, "end": v(-3.32, 84.63) * mm});
            skLineSegment(sketch, "E2129", {"start": v(-3.28, 84.5) * mm, "end": v(-3.24, 84.39) * mm});
            skLineSegment(sketch, "E2130", {"start": v(-3.19, 84.26) * mm, "end": v(-3.14, 84.15) * mm});
            skLineSegment(sketch, "E2131", {"start": v(-3.14, 84.15) * mm, "end": v(-3.08, 84.03) * mm});
            skLineSegment(sketch, "E2132", {"start": v(-3.08, 84.03) * mm, "end": v(-3.02, 83.91) * mm});
            skLineSegment(sketch, "E2133", {"start": v(-3.02, 83.91) * mm, "end": v(-2.96, 83.8) * mm});
            skLineSegment(sketch, "E2134", {"start": v(-2.96, 83.8) * mm, "end": v(-2.89, 83.69) * mm});
            skLineSegment(sketch, "E2135", {"start": v(-2.82, 83.58) * mm, "end": v(-2.74, 83.47) * mm});
            skLineSegment(sketch, "E2136", {"start": v(-2.58, 83.27) * mm, "end": v(-2.5, 83.17) * mm});
            skLineSegment(sketch, "E2137", {"start": v(-2.12, 82.81) * mm, "end": v(-2.02, 82.73) * mm});
            skLineSegment(sketch, "E2138", {"start": v(-1.91, 82.65) * mm, "end": v(-1.8, 82.58) * mm});
            skLineSegment(sketch, "E2139", {"start": v(-1.8, 82.58) * mm, "end": v(-1.7, 82.5) * mm});
            skLineSegment(sketch, "E2140", {"start": v(-1.7, 82.5) * mm, "end": v(-1.59, 82.44) * mm});
            skLineSegment(sketch, "E2141", {"start": v(-1.59, 82.44) * mm, "end": v(-1.47, 82.38) * mm});
            skLineSegment(sketch, "E2142", {"start": v(-1.47, 82.38) * mm, "end": v(-1.36, 82.32) * mm});
            skLineSegment(sketch, "E2143", {"start": v(-0.75, 82.09) * mm, "end": v(-0.62, 82.05) * mm});
            skLineSegment(sketch, "E2144", {"start": v(-0.62, 82.05) * mm, "end": v(-0.5, 82.02) * mm});
            skLineSegment(sketch, "E2145", {"start": v(-0.5, 82.02) * mm, "end": v(-0.37, 82) * mm});
            skLineSegment(sketch, "E2146", {"start": v(-0.11, 81.96) * mm, "end": v(0.02, 81.95) * mm});
            skLineSegment(sketch, "E2147", {"start": v(0.02, 81.95) * mm, "end": v(0.15, 81.94) * mm});
            skLineSegment(sketch, "E2148", {"start": v(0.15, 81.94) * mm, "end": v(0.28, 81.94) * mm});
            skLineSegment(sketch, "E2149", {"start": v(0.28, 84.44) * mm, "end": v(0.32, 84.44) * mm});
            skLineSegment(sketch, "E2150", {"start": v(0.32, 84.44) * mm, "end": v(0.37, 84.45) * mm});
            skLineSegment(sketch, "E2151", {"start": v(0.37, 84.45) * mm, "end": v(0.4, 84.45) * mm});
            skLineSegment(sketch, "E2152", {"start": v(0.4, 84.45) * mm, "end": v(0.45, 84.45) * mm});
            skLineSegment(sketch, "E2153", {"start": v(0.45, 84.45) * mm, "end": v(0.5, 84.46) * mm});
            skLineSegment(sketch, "E2154", {"start": v(0.5, 84.46) * mm, "end": v(0.54, 84.47) * mm});
            skLineSegment(sketch, "E2155", {"start": v(0.54, 84.47) * mm, "end": v(0.58, 84.48) * mm});
            skLineSegment(sketch, "E2156", {"start": v(0.58, 84.48) * mm, "end": v(0.62, 84.5) * mm});
            skLineSegment(sketch, "E2157", {"start": v(0.62, 84.5) * mm, "end": v(0.66, 84.5) * mm});
            skLineSegment(sketch, "E2158", {"start": v(0.7, 84.52) * mm, "end": v(0.75, 84.53) * mm});
            skLineSegment(sketch, "E2159", {"start": v(0.75, 84.53) * mm, "end": v(0.79, 84.55) * mm});
            skLineSegment(sketch, "E2160", {"start": v(0.79, 84.55) * mm, "end": v(0.82, 84.57) * mm});
            skLineSegment(sketch, "E2161", {"start": v(0.82, 84.57) * mm, "end": v(0.86, 84.59) * mm});
            skLineSegment(sketch, "E2162", {"start": v(0.86, 84.59) * mm, "end": v(0.9, 84.6) * mm});
            skLineSegment(sketch, "E2163", {"start": v(0.9, 84.6) * mm, "end": v(0.94, 84.63) * mm});
            skLineSegment(sketch, "E2164", {"start": v(0.94, 84.63) * mm, "end": v(0.98, 84.65) * mm});
            skLineSegment(sketch, "E2165", {"start": v(0.98, 84.65) * mm, "end": v(1.01, 84.68) * mm});
            skLineSegment(sketch, "E2166", {"start": v(1.01, 84.68) * mm, "end": v(1.05, 84.7) * mm});
            skLineSegment(sketch, "E2167", {"start": v(1.08, 84.73) * mm, "end": v(1.11, 84.76) * mm});
            skLineSegment(sketch, "E2168", {"start": v(1.11, 84.76) * mm, "end": v(1.14, 84.79) * mm});
            skLineSegment(sketch, "E2169", {"start": v(1.14, 84.79) * mm, "end": v(1.18, 84.82) * mm});
            skLineSegment(sketch, "E2170", {"start": v(1.2, 84.85) * mm, "end": v(1.23, 84.88) * mm});
            skLineSegment(sketch, "E2171", {"start": v(1.29, 84.95) * mm, "end": v(1.31, 84.99) * mm});
            skLineSegment(sketch, "E2172", {"start": v(1.31, 84.99) * mm, "end": v(1.34, 85.02) * mm});
            skLineSegment(sketch, "E2173", {"start": v(1.34, 85.02) * mm, "end": v(1.36, 85.06) * mm});
            skLineSegment(sketch, "E2174", {"start": v(1.36, 85.06) * mm, "end": v(1.38, 85.1) * mm});
            skLineSegment(sketch, "E2175", {"start": v(1.38, 85.1) * mm, "end": v(1.4, 85.14) * mm});
            skLineSegment(sketch, "E2176", {"start": v(1.4, 85.14) * mm, "end": v(1.42, 85.18) * mm});
            skLineSegment(sketch, "E2177", {"start": v(1.42, 85.18) * mm, "end": v(1.44, 85.22) * mm});
            skLineSegment(sketch, "E2178", {"start": v(1.44, 85.22) * mm, "end": v(1.45, 85.26) * mm});
            skLineSegment(sketch, "E2179", {"start": v(1.47, 85.3) * mm, "end": v(1.48, 85.34) * mm});
            skLineSegment(sketch, "E2180", {"start": v(1.5, 85.38) * mm, "end": v(1.5, 85.42) * mm});
            skLineSegment(sketch, "E2181", {"start": v(1.5, 85.42) * mm, "end": v(1.5, 85.47) * mm});
            skLineSegment(sketch, "E2182", {"start": v(1.5, 85.47) * mm, "end": v(1.52, 85.5) * mm});
            skLineSegment(sketch, "E2183", {"start": v(1.52, 85.5) * mm, "end": v(1.52, 85.55) * mm});
            skLineSegment(sketch, "E2184", {"start": v(1.52, 85.55) * mm, "end": v(1.53, 85.6) * mm});
            skLineSegment(sketch, "E2185", {"start": v(1.53, 85.6) * mm, "end": v(1.53, 85.64) * mm});
            skLineSegment(sketch, "E2186", {"start": v(1.53, 85.64) * mm, "end": v(1.53, 85.68) * mm});
            skLineSegment(sketch, "E2187", {"start": v(1.53, 85.68) * mm, "end": v(1.53, 85.72) * mm});
            skLineSegment(sketch, "E2188", {"start": v(1.53, 85.72) * mm, "end": v(1.53, 85.77) * mm});
            skLineSegment(sketch, "E2189", {"start": v(1.53, 85.77) * mm, "end": v(1.52, 85.81) * mm});
            skLineSegment(sketch, "E2190", {"start": v(1.52, 85.85) * mm, "end": v(1.51, 85.9) * mm});
            skLineSegment(sketch, "E2191", {"start": v(1.51, 85.9) * mm, "end": v(1.5, 85.94) * mm});
            skLineSegment(sketch, "E2192", {"start": v(1.5, 85.94) * mm, "end": v(1.5, 85.98) * mm});
            skLineSegment(sketch, "E2193", {"start": v(1.5, 85.98) * mm, "end": v(1.48, 86.02) * mm});
            skLineSegment(sketch, "E2194", {"start": v(1.48, 86.02) * mm, "end": v(1.47, 86.07) * mm});
            skLineSegment(sketch, "E2195", {"start": v(1.47, 86.07) * mm, "end": v(1.46, 86.1) * mm});
            skLineSegment(sketch, "E2196", {"start": v(1.44, 86.15) * mm, "end": v(1.43, 86.19) * mm});
            skLineSegment(sketch, "E2197", {"start": v(1.43, 86.19) * mm, "end": v(1.4, 86.23) * mm});
            skLineSegment(sketch, "E2198", {"start": v(1.37, 86.3) * mm, "end": v(1.35, 86.34) * mm});
            skLineSegment(sketch, "E2199", {"start": v(1.35, 86.34) * mm, "end": v(1.32, 86.38) * mm});
            skLineSegment(sketch, "E2200", {"start": v(1.32, 86.38) * mm, "end": v(1.3, 86.41) * mm});
            skLineSegment(sketch, "E2201", {"start": v(1.3, 86.41) * mm, "end": v(1.27, 86.45) * mm});
            skLineSegment(sketch, "E2202", {"start": v(1.27, 86.45) * mm, "end": v(1.25, 86.48) * mm});
            skLineSegment(sketch, "E2203", {"start": v(1.25, 86.48) * mm, "end": v(1.22, 86.52) * mm});
            skLineSegment(sketch, "E2204", {"start": v(1.22, 86.52) * mm, "end": v(1.2, 86.55) * mm});
            skLineSegment(sketch, "E2205", {"start": v(1.06, 86.67) * mm, "end": v(1.03, 86.7) * mm});
            skLineSegment(sketch, "E2206", {"start": v(1, 86.72) * mm, "end": v(0.96, 86.74) * mm});
            skLineSegment(sketch, "E2207", {"start": v(0.96, 86.74) * mm, "end": v(0.92, 86.77) * mm});
            skLineSegment(sketch, "E2208", {"start": v(0.92, 86.77) * mm, "end": v(0.88, 86.79) * mm});
            skLineSegment(sketch, "E2209", {"start": v(0.88, 86.79) * mm, "end": v(0.84, 86.8) * mm});
            skLineSegment(sketch, "E2210", {"start": v(0.84, 86.8) * mm, "end": v(0.8, 86.83) * mm});
            skLineSegment(sketch, "E2211", {"start": v(0.8, 86.83) * mm, "end": v(0.77, 86.84) * mm});
            skLineSegment(sketch, "E2212", {"start": v(0.77, 86.84) * mm, "end": v(0.73, 86.86) * mm});
            skLineSegment(sketch, "E2213", {"start": v(0.73, 86.86) * mm, "end": v(0.68, 86.88) * mm});
            skLineSegment(sketch, "E2214", {"start": v(0.64, 86.89) * mm, "end": v(0.6, 86.9) * mm});
            skLineSegment(sketch, "E2215", {"start": v(0.56, 86.91) * mm, "end": v(0.52, 86.92) * mm});
            skLineSegment(sketch, "E2216", {"start": v(0.52, 86.92) * mm, "end": v(0.47, 86.93) * mm});
            skLineSegment(sketch, "E2217", {"start": v(0.47, 86.93) * mm, "end": v(0.43, 86.93) * mm});
            skLineSegment(sketch, "E2218", {"start": v(0.43, 86.93) * mm, "end": v(0.39, 86.94) * mm});
            skLineSegment(sketch, "E2219", {"start": v(0.39, 86.94) * mm, "end": v(0.34, 86.94) * mm});
            skLineSegment(sketch, "E2220", {"start": v(0.34, 86.94) * mm, "end": v(0.3, 86.94) * mm});
            skLineSegment(sketch, "E2221", {"start": v(0.3, 86.94) * mm, "end": v(0.26, 86.94) * mm});
            skLineSegment(sketch, "E2222", {"start": v(0.26, 86.94) * mm, "end": v(0.21, 86.94) * mm});
            skLineSegment(sketch, "E2223", {"start": v(0.21, 86.94) * mm, "end": v(0.17, 86.94) * mm});
            skLineSegment(sketch, "E2224", {"start": v(0.17, 86.94) * mm, "end": v(0.13, 86.93) * mm});
            skLineSegment(sketch, "E2225", {"start": v(0.13, 86.93) * mm, "end": v(0.09, 86.93) * mm});
            skLineSegment(sketch, "E2226", {"start": v(0.09, 86.93) * mm, "end": v(0.04, 86.92) * mm});
            skLineSegment(sketch, "E2227", {"start": v(0.04, 86.92) * mm, "end": v(0, 86.91) * mm});
            skLineSegment(sketch, "E2228", {"start": v(0, 86.91) * mm, "end": v(-0.04, 86.9) * mm});
            skLineSegment(sketch, "E2229", {"start": v(-0.04, 86.9) * mm, "end": v(-0.08, 86.89) * mm});
            skLineSegment(sketch, "E2230", {"start": v(-0.12, 86.88) * mm, "end": v(-0.17, 86.86) * mm});
            skLineSegment(sketch, "E2231", {"start": v(-0.17, 86.86) * mm, "end": v(-0.2, 86.84) * mm});
            skLineSegment(sketch, "E2232", {"start": v(-0.2, 86.84) * mm, "end": v(-0.25, 86.83) * mm});
            skLineSegment(sketch, "E2233", {"start": v(-0.25, 86.83) * mm, "end": v(-0.28, 86.8) * mm});
            skLineSegment(sketch, "E2234", {"start": v(-0.28, 86.8) * mm, "end": v(-0.32, 86.79) * mm});
            skLineSegment(sketch, "E2235", {"start": v(-0.32, 86.79) * mm, "end": v(-0.36, 86.77) * mm});
            skLineSegment(sketch, "E2236", {"start": v(-0.4, 86.74) * mm, "end": v(-0.43, 86.72) * mm});
            skLineSegment(sketch, "E2237", {"start": v(-0.43, 86.72) * mm, "end": v(-0.47, 86.7) * mm});
            skLineSegment(sketch, "E2238", {"start": v(-0.47, 86.7) * mm, "end": v(-0.5, 86.67) * mm});
            skLineSegment(sketch, "E2239", {"start": v(-0.5, 86.67) * mm, "end": v(-0.54, 86.64) * mm});
            skLineSegment(sketch, "E2240", {"start": v(-0.6, 86.58) * mm, "end": v(-0.63, 86.55) * mm});
            skLineSegment(sketch, "E2241", {"start": v(-0.63, 86.55) * mm, "end": v(-0.66, 86.52) * mm});
            skLineSegment(sketch, "E2242", {"start": v(-0.69, 86.48) * mm, "end": v(-0.71, 86.45) * mm});
            skLineSegment(sketch, "E2243", {"start": v(-0.71, 86.45) * mm, "end": v(-0.74, 86.41) * mm});
            skLineSegment(sketch, "E2244", {"start": v(-0.74, 86.41) * mm, "end": v(-0.76, 86.38) * mm});
            skLineSegment(sketch, "E2245", {"start": v(-0.76, 86.38) * mm, "end": v(-0.79, 86.34) * mm});
            skLineSegment(sketch, "E2246", {"start": v(-0.79, 86.34) * mm, "end": v(-0.8, 86.3) * mm});
            skLineSegment(sketch, "E2247", {"start": v(-0.8, 86.3) * mm, "end": v(-0.83, 86.27) * mm});
            skLineSegment(sketch, "E2248", {"start": v(-0.83, 86.27) * mm, "end": v(-0.85, 86.23) * mm});
            skLineSegment(sketch, "E2249", {"start": v(-0.85, 86.23) * mm, "end": v(-0.87, 86.19) * mm});
            skLineSegment(sketch, "E2250", {"start": v(-0.87, 86.19) * mm, "end": v(-0.88, 86.15) * mm});
            skLineSegment(sketch, "E2251", {"start": v(-0.9, 86.1) * mm, "end": v(-0.91, 86.07) * mm});
            skLineSegment(sketch, "E2252", {"start": v(-0.91, 86.07) * mm, "end": v(-0.93, 86.02) * mm});
            skLineSegment(sketch, "E2253", {"start": v(-0.93, 86.02) * mm, "end": v(-0.94, 85.98) * mm});
            skLineSegment(sketch, "E2254", {"start": v(-0.94, 85.98) * mm, "end": v(-0.95, 85.94) * mm});
            skLineSegment(sketch, "E2255", {"start": v(-0.95, 85.94) * mm, "end": v(-0.95, 85.9) * mm});
            skLineSegment(sketch, "E2256", {"start": v(-0.95, 85.9) * mm, "end": v(-0.96, 85.85) * mm});
            skLineSegment(sketch, "E2257", {"start": v(-0.96, 85.85) * mm, "end": v(-0.96, 85.81) * mm});
            skLineSegment(sketch, "E2258", {"start": v(-0.96, 85.81) * mm, "end": v(-0.97, 85.77) * mm});
            skLineSegment(sketch, "E2259", {"start": v(-0.97, 85.77) * mm, "end": v(-0.97, 85.72) * mm});
            skLineSegment(sketch, "E2260", {"start": v(-0.97, 85.72) * mm, "end": v(-0.97, 85.68) * mm});
            skLineSegment(sketch, "E2261", {"start": v(-0.97, 85.68) * mm, "end": v(-0.97, 85.64) * mm});
            skLineSegment(sketch, "E2262", {"start": v(-0.97, 85.64) * mm, "end": v(-0.97, 85.6) * mm});
            skLineSegment(sketch, "E2263", {"start": v(-0.97, 85.6) * mm, "end": v(-0.96, 85.55) * mm});
            skLineSegment(sketch, "E2264", {"start": v(-0.96, 85.55) * mm, "end": v(-0.96, 85.5) * mm});
            skLineSegment(sketch, "E2265", {"start": v(-0.96, 85.5) * mm, "end": v(-0.95, 85.47) * mm});
            skLineSegment(sketch, "E2266", {"start": v(-0.95, 85.47) * mm, "end": v(-0.94, 85.42) * mm});
            skLineSegment(sketch, "E2267", {"start": v(-0.94, 85.42) * mm, "end": v(-0.93, 85.38) * mm});
            skLineSegment(sketch, "E2268", {"start": v(-0.92, 85.34) * mm, "end": v(-0.9, 85.3) * mm});
            skLineSegment(sketch, "E2269", {"start": v(-0.9, 85.3) * mm, "end": v(-0.9, 85.26) * mm});
            skLineSegment(sketch, "E2270", {"start": v(-0.9, 85.26) * mm, "end": v(-0.88, 85.22) * mm});
            skLineSegment(sketch, "E2271", {"start": v(-0.88, 85.22) * mm, "end": v(-0.86, 85.18) * mm});
            skLineSegment(sketch, "E2272", {"start": v(-0.86, 85.18) * mm, "end": v(-0.84, 85.14) * mm});
            skLineSegment(sketch, "E2273", {"start": v(-0.8, 85.06) * mm, "end": v(-0.78, 85.02) * mm});
            skLineSegment(sketch, "E2274", {"start": v(-0.78, 85.02) * mm, "end": v(-0.75, 84.99) * mm});
            skLineSegment(sketch, "E2275", {"start": v(-0.7, 84.92) * mm, "end": v(-0.67, 84.88) * mm});
            skLineSegment(sketch, "E2276", {"start": v(-0.67, 84.88) * mm, "end": v(-0.65, 84.85) * mm});
            skLineSegment(sketch, "E2277", {"start": v(-0.62, 84.82) * mm, "end": v(-0.58, 84.79) * mm});
            skLineSegment(sketch, "E2278", {"start": v(-0.58, 84.79) * mm, "end": v(-0.55, 84.76) * mm});
            skLineSegment(sketch, "E2279", {"start": v(-0.55, 84.76) * mm, "end": v(-0.52, 84.73) * mm});
            skLineSegment(sketch, "E2280", {"start": v(-0.52, 84.73) * mm, "end": v(-0.49, 84.7) * mm});
            skLineSegment(sketch, "E2281", {"start": v(-0.49, 84.7) * mm, "end": v(-0.45, 84.68) * mm});
            skLineSegment(sketch, "E2282", {"start": v(-0.45, 84.68) * mm, "end": v(-0.42, 84.65) * mm});
            skLineSegment(sketch, "E2283", {"start": v(-0.42, 84.65) * mm, "end": v(-0.38, 84.63) * mm});
            skLineSegment(sketch, "E2284", {"start": v(-0.38, 84.63) * mm, "end": v(-0.34, 84.6) * mm});
            skLineSegment(sketch, "E2285", {"start": v(-0.34, 84.6) * mm, "end": v(-0.3, 84.59) * mm});
            skLineSegment(sketch, "E2286", {"start": v(-0.3, 84.59) * mm, "end": v(-0.27, 84.57) * mm});
            skLineSegment(sketch, "E2287", {"start": v(-0.27, 84.57) * mm, "end": v(-0.23, 84.55) * mm});
            skLineSegment(sketch, "E2288", {"start": v(-0.23, 84.55) * mm, "end": v(-0.19, 84.53) * mm});
            skLineSegment(sketch, "E2289", {"start": v(-0.15, 84.52) * mm, "end": v(-0.1, 84.5) * mm});
            skLineSegment(sketch, "E2290", {"start": v(-0.1, 84.5) * mm, "end": v(-0.06, 84.5) * mm});
            skLineSegment(sketch, "E2291", {"start": v(-0.06, 84.5) * mm, "end": v(-0.02, 84.48) * mm});
            skLineSegment(sketch, "E2292", {"start": v(-0.02, 84.48) * mm, "end": v(0.02, 84.47) * mm});
            skLineSegment(sketch, "E2293", {"start": v(0.02, 84.47) * mm, "end": v(0.06, 84.46) * mm});
            skLineSegment(sketch, "E2294", {"start": v(0.06, 84.46) * mm, "end": v(0.1, 84.45) * mm});
            skLineSegment(sketch, "E2295", {"start": v(0.1, 84.45) * mm, "end": v(0.15, 84.45) * mm});
            skLineSegment(sketch, "E2296", {"start": v(0.15, 84.45) * mm, "end": v(0.2, 84.45) * mm});
            skLineSegment(sketch, "E2297", {"start": v(0.2, 84.45) * mm, "end": v(0.24, 84.44) * mm});
            skLineSegment(sketch, "E2298", {"start": v(0.24, 84.44) * mm, "end": v(0.28, 84.44) * mm});
            skLineSegment(sketch, "E2299", {"start": v(-55.97, 84.44) * mm, "end": v(-55.93, 84.44) * mm});
            skLineSegment(sketch, "E2300", {"start": v(-55.93, 84.44) * mm, "end": v(-55.88, 84.45) * mm});
            skLineSegment(sketch, "E2301", {"start": v(-55.8, 84.45) * mm, "end": v(-55.75, 84.46) * mm});
            skLineSegment(sketch, "E2302", {"start": v(-55.71, 84.47) * mm, "end": v(-55.67, 84.48) * mm});
            skLineSegment(sketch, "E2303", {"start": v(-55.67, 84.48) * mm, "end": v(-55.63, 84.5) * mm});
            skLineSegment(sketch, "E2304", {"start": v(-55.63, 84.5) * mm, "end": v(-55.59, 84.5) * mm});
            skLineSegment(sketch, "E2305", {"start": v(-55.54, 84.52) * mm, "end": v(-55.5, 84.53) * mm});
            skLineSegment(sketch, "E2306", {"start": v(-55.5, 84.53) * mm, "end": v(-55.46, 84.55) * mm});
            skLineSegment(sketch, "E2307", {"start": v(-55.43, 84.57) * mm, "end": v(-55.39, 84.59) * mm});
            skLineSegment(sketch, "E2308", {"start": v(-55.39, 84.59) * mm, "end": v(-55.35, 84.6) * mm});
            skLineSegment(sketch, "E2309", {"start": v(-55.1, 84.79) * mm, "end": v(-55.07, 84.82) * mm});
            skLineSegment(sketch, "E2310", {"start": v(-55.07, 84.82) * mm, "end": v(-55.05, 84.85) * mm});
            skLineSegment(sketch, "E2311", {"start": v(-54.99, 84.92) * mm, "end": v(-54.96, 84.95) * mm});
            skLineSegment(sketch, "E2312", {"start": v(-54.96, 84.95) * mm, "end": v(-54.94, 84.99) * mm});
            skLineSegment(sketch, "E2313", {"start": v(-54.94, 84.99) * mm, "end": v(-54.91, 85.02) * mm});
            skLineSegment(sketch, "E2314", {"start": v(-54.87, 85.1) * mm, "end": v(-54.85, 85.14) * mm});
            skLineSegment(sketch, "E2315", {"start": v(-54.85, 85.14) * mm, "end": v(-54.83, 85.18) * mm});
            skLineSegment(sketch, "E2316", {"start": v(-54.83, 85.18) * mm, "end": v(-54.81, 85.22) * mm});
            skLineSegment(sketch, "E2317", {"start": v(-54.81, 85.22) * mm, "end": v(-54.8, 85.26) * mm});
            skLineSegment(sketch, "E2318", {"start": v(-54.75, 85.42) * mm, "end": v(-54.74, 85.47) * mm});
            skLineSegment(sketch, "E2319", {"start": v(-54.74, 85.47) * mm, "end": v(-54.73, 85.5) * mm});
            skLineSegment(sketch, "E2320", {"start": v(-54.73, 85.5) * mm, "end": v(-54.73, 85.55) * mm});
            skLineSegment(sketch, "E2321", {"start": v(-54.73, 85.55) * mm, "end": v(-54.72, 85.6) * mm});
            skLineSegment(sketch, "E2322", {"start": v(-54.72, 85.6) * mm, "end": v(-54.72, 85.64) * mm});
            skLineSegment(sketch, "E2323", {"start": v(-54.72, 85.64) * mm, "end": v(-54.72, 85.68) * mm});
            skLineSegment(sketch, "E2324", {"start": v(-54.72, 85.72) * mm, "end": v(-54.72, 85.77) * mm});
            skLineSegment(sketch, "E2325", {"start": v(-54.72, 85.77) * mm, "end": v(-54.73, 85.81) * mm});
            skLineSegment(sketch, "E2326", {"start": v(-54.73, 85.81) * mm, "end": v(-54.73, 85.85) * mm});
            skLineSegment(sketch, "E2327", {"start": v(-54.73, 85.85) * mm, "end": v(-54.74, 85.9) * mm});
            skLineSegment(sketch, "E2328", {"start": v(-54.74, 85.9) * mm, "end": v(-54.75, 85.94) * mm});
            skLineSegment(sketch, "E2329", {"start": v(-54.75, 85.98) * mm, "end": v(-54.77, 86.02) * mm});
            skLineSegment(sketch, "E2330", {"start": v(-54.78, 86.07) * mm, "end": v(-54.8, 86.1) * mm});
            skLineSegment(sketch, "E2331", {"start": v(-54.8, 86.1) * mm, "end": v(-54.8, 86.15) * mm});
            skLineSegment(sketch, "E2332", {"start": v(-54.84, 86.23) * mm, "end": v(-54.86, 86.27) * mm});
            skLineSegment(sketch, "E2333", {"start": v(-54.86, 86.27) * mm, "end": v(-54.88, 86.3) * mm});
            skLineSegment(sketch, "E2334", {"start": v(-54.9, 86.34) * mm, "end": v(-54.93, 86.38) * mm});
            skLineSegment(sketch, "E2335", {"start": v(-54.93, 86.38) * mm, "end": v(-54.95, 86.41) * mm});
            skLineSegment(sketch, "E2336", {"start": v(-54.95, 86.41) * mm, "end": v(-54.98, 86.45) * mm});
            skLineSegment(sketch, "E2337", {"start": v(-54.98, 86.45) * mm, "end": v(-55, 86.48) * mm});
            skLineSegment(sketch, "E2338", {"start": v(-55.06, 86.55) * mm, "end": v(-55.1, 86.58) * mm});
            skLineSegment(sketch, "E2339", {"start": v(-55.1, 86.58) * mm, "end": v(-55.12, 86.61) * mm});
            skLineSegment(sketch, "E2340", {"start": v(-55.12, 86.61) * mm, "end": v(-55.15, 86.64) * mm});
            skLineSegment(sketch, "E2341", {"start": v(-55.26, 86.72) * mm, "end": v(-55.3, 86.74) * mm});
            skLineSegment(sketch, "E2342", {"start": v(-55.3, 86.74) * mm, "end": v(-55.33, 86.77) * mm});
            skLineSegment(sketch, "E2343", {"start": v(-55.37, 86.79) * mm, "end": v(-55.4, 86.8) * mm});
            skLineSegment(sketch, "E2344", {"start": v(-55.48, 86.84) * mm, "end": v(-55.52, 86.86) * mm});
            skLineSegment(sketch, "E2345", {"start": v(-55.52, 86.86) * mm, "end": v(-55.57, 86.88) * mm});
            skLineSegment(sketch, "E2346", {"start": v(-55.57, 86.88) * mm, "end": v(-55.6, 86.89) * mm});
            skLineSegment(sketch, "E2347", {"start": v(-55.6, 86.89) * mm, "end": v(-55.65, 86.9) * mm});
            skLineSegment(sketch, "E2348", {"start": v(-55.65, 86.9) * mm, "end": v(-55.7, 86.91) * mm});
            skLineSegment(sketch, "E2349", {"start": v(-55.7, 86.91) * mm, "end": v(-55.73, 86.92) * mm});
            skLineSegment(sketch, "E2350", {"start": v(-55.86, 86.94) * mm, "end": v(-55.9, 86.94) * mm});
            skLineSegment(sketch, "E2351", {"start": v(-55.9, 86.94) * mm, "end": v(-55.95, 86.94) * mm});
            skLineSegment(sketch, "E2352", {"start": v(-55.95, 86.94) * mm, "end": v(-56, 86.94) * mm});
            skLineSegment(sketch, "E2353", {"start": v(-56, 86.94) * mm, "end": v(-56.04, 86.94) * mm});
            skLineSegment(sketch, "E2354", {"start": v(-56.37, 86.88) * mm, "end": v(-56.42, 86.86) * mm});
            skLineSegment(sketch, "E2355", {"start": v(-56.46, 86.84) * mm, "end": v(-56.5, 86.83) * mm});
            skLineSegment(sketch, "E2356", {"start": v(-56.5, 86.83) * mm, "end": v(-56.53, 86.8) * mm});
            skLineSegment(sketch, "E2357", {"start": v(-56.57, 86.79) * mm, "end": v(-56.61, 86.77) * mm});
            skLineSegment(sketch, "E2358", {"start": v(-56.61, 86.77) * mm, "end": v(-56.65, 86.74) * mm});
            skLineSegment(sketch, "E2359", {"start": v(-56.65, 86.74) * mm, "end": v(-56.68, 86.72) * mm});
            skLineSegment(sketch, "E2360", {"start": v(-56.68, 86.72) * mm, "end": v(-56.72, 86.7) * mm});
            skLineSegment(sketch, "E2361", {"start": v(-56.72, 86.7) * mm, "end": v(-56.75, 86.67) * mm});
            skLineSegment(sketch, "E2362", {"start": v(-56.75, 86.67) * mm, "end": v(-56.79, 86.64) * mm});
            skLineSegment(sketch, "E2363", {"start": v(-56.79, 86.64) * mm, "end": v(-56.82, 86.61) * mm});
            skLineSegment(sketch, "E2364", {"start": v(-56.82, 86.61) * mm, "end": v(-56.85, 86.58) * mm});
            skLineSegment(sketch, "E2365", {"start": v(-56.85, 86.58) * mm, "end": v(-56.88, 86.55) * mm});
            skLineSegment(sketch, "E2366", {"start": v(-56.88, 86.55) * mm, "end": v(-56.9, 86.52) * mm});
            skLineSegment(sketch, "E2367", {"start": v(-56.96, 86.45) * mm, "end": v(-57, 86.41) * mm});
            skLineSegment(sketch, "E2368", {"start": v(-57, 86.41) * mm, "end": v(-57.01, 86.38) * mm});
            skLineSegment(sketch, "E2369", {"start": v(-57.01, 86.38) * mm, "end": v(-57.04, 86.34) * mm});
            skLineSegment(sketch, "E2370", {"start": v(-57.08, 86.27) * mm, "end": v(-57.1, 86.23) * mm});
            skLineSegment(sketch, "E2371", {"start": v(-57.1, 86.23) * mm, "end": v(-57.12, 86.19) * mm});
            skLineSegment(sketch, "E2372", {"start": v(-57.12, 86.19) * mm, "end": v(-57.13, 86.15) * mm});
            skLineSegment(sketch, "E2373", {"start": v(-57.13, 86.15) * mm, "end": v(-57.15, 86.1) * mm});
            skLineSegment(sketch, "E2374", {"start": v(-57.18, 86.02) * mm, "end": v(-57.19, 85.98) * mm});
            skLineSegment(sketch, "E2375", {"start": v(-57.2, 85.94) * mm, "end": v(-57.2, 85.9) * mm});
            skLineSegment(sketch, "E2376", {"start": v(-57.2, 85.9) * mm, "end": v(-57.2, 85.85) * mm});
            skLineSegment(sketch, "E2377", {"start": v(-57.21, 85.81) * mm, "end": v(-57.22, 85.77) * mm});
            skLineSegment(sketch, "E2378", {"start": v(-57.22, 85.77) * mm, "end": v(-57.22, 85.72) * mm});
            skLineSegment(sketch, "E2379", {"start": v(-57.22, 85.68) * mm, "end": v(-57.22, 85.64) * mm});
            skLineSegment(sketch, "E2380", {"start": v(-57.22, 85.64) * mm, "end": v(-57.22, 85.6) * mm});
            skLineSegment(sketch, "E2381", {"start": v(-57.22, 85.6) * mm, "end": v(-57.21, 85.55) * mm});
            skLineSegment(sketch, "E2382", {"start": v(-57.21, 85.55) * mm, "end": v(-57.2, 85.5) * mm});
            skLineSegment(sketch, "E2383", {"start": v(-57.2, 85.5) * mm, "end": v(-57.2, 85.47) * mm});
            skLineSegment(sketch, "E2384", {"start": v(-57.17, 85.34) * mm, "end": v(-57.16, 85.3) * mm});
            skLineSegment(sketch, "E2385", {"start": v(-57.16, 85.3) * mm, "end": v(-57.14, 85.26) * mm});
            skLineSegment(sketch, "E2386", {"start": v(-57.14, 85.26) * mm, "end": v(-57.13, 85.22) * mm});
            skLineSegment(sketch, "E2387", {"start": v(-57.1, 85.18) * mm, "end": v(-57.1, 85.14) * mm});
            skLineSegment(sketch, "E2388", {"start": v(-57.05, 85.06) * mm, "end": v(-57.03, 85.02) * mm});
            skLineSegment(sketch, "E2389", {"start": v(-57.03, 85.02) * mm, "end": v(-57, 84.99) * mm});
            skLineSegment(sketch, "E2390", {"start": v(-57, 84.99) * mm, "end": v(-56.98, 84.95) * mm});
            skLineSegment(sketch, "E2391", {"start": v(-56.92, 84.88) * mm, "end": v(-56.9, 84.85) * mm});
            skLineSegment(sketch, "E2392", {"start": v(-56.9, 84.85) * mm, "end": v(-56.87, 84.82) * mm});
            skLineSegment(sketch, "E2393", {"start": v(-56.87, 84.82) * mm, "end": v(-56.83, 84.79) * mm});
            skLineSegment(sketch, "E2394", {"start": v(-56.83, 84.79) * mm, "end": v(-56.8, 84.76) * mm});
            skLineSegment(sketch, "E2395", {"start": v(-56.77, 84.73) * mm, "end": v(-56.74, 84.7) * mm});
            skLineSegment(sketch, "E2396", {"start": v(-56.74, 84.7) * mm, "end": v(-56.7, 84.68) * mm});
            skLineSegment(sketch, "E2397", {"start": v(-56.7, 84.68) * mm, "end": v(-56.67, 84.65) * mm});
            skLineSegment(sketch, "E2398", {"start": v(-56.63, 84.63) * mm, "end": v(-56.6, 84.6) * mm});
            skLineSegment(sketch, "E2399", {"start": v(-56.55, 84.59) * mm, "end": v(-56.52, 84.57) * mm});
            skLineSegment(sketch, "E2400", {"start": v(-56.52, 84.57) * mm, "end": v(-56.48, 84.55) * mm});
            skLineSegment(sketch, "E2401", {"start": v(-56.44, 84.53) * mm, "end": v(-56.4, 84.52) * mm});
            skLineSegment(sketch, "E2402", {"start": v(-56.06, 84.45) * mm, "end": v(-56.01, 84.44) * mm});
            skLineSegment(sketch, "E2403", {"start": v(-56.01, 84.44) * mm, "end": v(-55.97, 84.44) * mm});
            skLineSegment(sketch, "E2404", {"start": v(69.17, 63.15) * mm, "end": v(69.22, 63.15) * mm});
            skLineSegment(sketch, "E2405", {"start": v(69.22, 63.15) * mm, "end": v(69.26, 63.16) * mm});
            skLineSegment(sketch, "E2406", {"start": v(69.26, 63.16) * mm, "end": v(69.3, 63.16) * mm});
            skLineSegment(sketch, "E2407", {"start": v(69.3, 63.16) * mm, "end": v(69.35, 63.16) * mm});
            skLineSegment(sketch, "E2408", {"start": v(69.35, 63.16) * mm, "end": v(69.39, 63.17) * mm});
            skLineSegment(sketch, "E2409", {"start": v(69.39, 63.17) * mm, "end": v(69.43, 63.18) * mm});
            skLineSegment(sketch, "E2410", {"start": v(69.43, 63.18) * mm, "end": v(69.47, 63.19) * mm});
            skLineSegment(sketch, "E2411", {"start": v(69.47, 63.19) * mm, "end": v(69.52, 63.2) * mm});
            skLineSegment(sketch, "E2412", {"start": v(69.52, 63.2) * mm, "end": v(69.56, 63.21) * mm});
            skLineSegment(sketch, "E2413", {"start": v(69.56, 63.21) * mm, "end": v(69.6, 63.23) * mm});
            skLineSegment(sketch, "E2414", {"start": v(69.6, 63.23) * mm, "end": v(69.64, 63.24) * mm});
            skLineSegment(sketch, "E2415", {"start": v(69.64, 63.24) * mm, "end": v(69.68, 63.26) * mm});
            skLineSegment(sketch, "E2416", {"start": v(69.68, 63.26) * mm, "end": v(69.72, 63.28) * mm});
            skLineSegment(sketch, "E2417", {"start": v(69.72, 63.28) * mm, "end": v(69.76, 63.3) * mm});
            skLineSegment(sketch, "E2418", {"start": v(69.76, 63.3) * mm, "end": v(69.8, 63.32) * mm});
            skLineSegment(sketch, "E2419", {"start": v(69.83, 63.34) * mm, "end": v(69.87, 63.36) * mm});
            skLineSegment(sketch, "E2420", {"start": v(69.87, 63.36) * mm, "end": v(69.9, 63.39) * mm});
            skLineSegment(sketch, "E2421", {"start": v(69.9, 63.39) * mm, "end": v(69.94, 63.41) * mm});
            skLineSegment(sketch, "E2422", {"start": v(69.94, 63.41) * mm, "end": v(69.97, 63.44) * mm});
            skLineSegment(sketch, "E2423", {"start": v(69.97, 63.44) * mm, "end": v(70, 63.47) * mm});
            skLineSegment(sketch, "E2424", {"start": v(70.04, 63.5) * mm, "end": v(70.07, 63.53) * mm});
            skLineSegment(sketch, "E2425", {"start": v(70.07, 63.53) * mm, "end": v(70.1, 63.56) * mm});
            skLineSegment(sketch, "E2426", {"start": v(70.1, 63.56) * mm, "end": v(70.13, 63.6) * mm});
            skLineSegment(sketch, "E2427", {"start": v(70.13, 63.6) * mm, "end": v(70.15, 63.63) * mm});
            skLineSegment(sketch, "E2428", {"start": v(70.15, 63.63) * mm, "end": v(70.18, 63.66) * mm});
            skLineSegment(sketch, "E2429", {"start": v(70.18, 63.66) * mm, "end": v(70.2, 63.7) * mm});
            skLineSegment(sketch, "E2430", {"start": v(70.2, 63.7) * mm, "end": v(70.23, 63.73) * mm});
            skLineSegment(sketch, "E2431", {"start": v(70.23, 63.73) * mm, "end": v(70.25, 63.77) * mm});
            skLineSegment(sketch, "E2432", {"start": v(70.25, 63.77) * mm, "end": v(70.27, 63.8) * mm});
            skLineSegment(sketch, "E2433", {"start": v(70.27, 63.8) * mm, "end": v(70.3, 63.85) * mm});
            skLineSegment(sketch, "E2434", {"start": v(70.3, 63.85) * mm, "end": v(70.31, 63.89) * mm});
            skLineSegment(sketch, "E2435", {"start": v(70.31, 63.89) * mm, "end": v(70.33, 63.93) * mm});
            skLineSegment(sketch, "E2436", {"start": v(70.33, 63.93) * mm, "end": v(70.34, 63.97) * mm});
            skLineSegment(sketch, "E2437", {"start": v(70.34, 63.97) * mm, "end": v(70.36, 64) * mm});
            skLineSegment(sketch, "E2438", {"start": v(70.36, 64) * mm, "end": v(70.37, 64.05) * mm});
            skLineSegment(sketch, "E2439", {"start": v(70.37, 64.05) * mm, "end": v(70.38, 64.1) * mm});
            skLineSegment(sketch, "E2440", {"start": v(70.38, 64.1) * mm, "end": v(70.4, 64.13) * mm});
            skLineSegment(sketch, "E2441", {"start": v(70.4, 64.13) * mm, "end": v(70.4, 64.18) * mm});
            skLineSegment(sketch, "E2442", {"start": v(70.4, 64.22) * mm, "end": v(70.41, 64.26) * mm});
            skLineSegment(sketch, "E2443", {"start": v(70.41, 64.26) * mm, "end": v(70.42, 64.3) * mm});
            skLineSegment(sketch, "E2444", {"start": v(70.42, 64.3) * mm, "end": v(70.42, 64.35) * mm});
            skLineSegment(sketch, "E2445", {"start": v(70.38, 64.73) * mm, "end": v(70.37, 64.78) * mm});
            skLineSegment(sketch, "E2446", {"start": v(70.37, 64.78) * mm, "end": v(70.35, 64.82) * mm});
            skLineSegment(sketch, "E2447", {"start": v(70.35, 64.82) * mm, "end": v(70.34, 64.86) * mm});
            skLineSegment(sketch, "E2448", {"start": v(70.34, 64.86) * mm, "end": v(70.32, 64.9) * mm});
            skLineSegment(sketch, "E2449", {"start": v(70.32, 64.9) * mm, "end": v(70.3, 64.94) * mm});
            skLineSegment(sketch, "E2450", {"start": v(70.3, 64.94) * mm, "end": v(70.28, 64.98) * mm});
            skLineSegment(sketch, "E2451", {"start": v(70.28, 64.98) * mm, "end": v(70.26, 65.02) * mm});
            skLineSegment(sketch, "E2452", {"start": v(70.26, 65.02) * mm, "end": v(70.24, 65.05) * mm});
            skLineSegment(sketch, "E2453", {"start": v(70.22, 65.09) * mm, "end": v(70.2, 65.13) * mm});
            skLineSegment(sketch, "E2454", {"start": v(70.2, 65.13) * mm, "end": v(70.17, 65.16) * mm});
            skLineSegment(sketch, "E2455", {"start": v(70.17, 65.16) * mm, "end": v(70.14, 65.2) * mm});
            skLineSegment(sketch, "E2456", {"start": v(70.14, 65.2) * mm, "end": v(70.11, 65.23) * mm});
            skLineSegment(sketch, "E2457", {"start": v(70.11, 65.23) * mm, "end": v(70.08, 65.26) * mm});
            skLineSegment(sketch, "E2458", {"start": v(70.08, 65.26) * mm, "end": v(70.05, 65.3) * mm});
            skLineSegment(sketch, "E2459", {"start": v(70.05, 65.3) * mm, "end": v(70.02, 65.32) * mm});
            skLineSegment(sketch, "E2460", {"start": v(70.02, 65.32) * mm, "end": v(69.99, 65.35) * mm});
            skLineSegment(sketch, "E2461", {"start": v(69.99, 65.35) * mm, "end": v(69.96, 65.38) * mm});
            skLineSegment(sketch, "E2462", {"start": v(69.92, 65.4) * mm, "end": v(69.89, 65.43) * mm});
            skLineSegment(sketch, "E2463", {"start": v(69.89, 65.43) * mm, "end": v(69.85, 65.45) * mm});
            skLineSegment(sketch, "E2464", {"start": v(69.85, 65.45) * mm, "end": v(69.81, 65.48) * mm});
            skLineSegment(sketch, "E2465", {"start": v(69.81, 65.48) * mm, "end": v(69.78, 65.5) * mm});
            skLineSegment(sketch, "E2466", {"start": v(69.78, 65.5) * mm, "end": v(69.74, 65.52) * mm});
            skLineSegment(sketch, "E2467", {"start": v(69.74, 65.52) * mm, "end": v(69.7, 65.54) * mm});
            skLineSegment(sketch, "E2468", {"start": v(69.7, 65.54) * mm, "end": v(69.66, 65.55) * mm});
            skLineSegment(sketch, "E2469", {"start": v(69.66, 65.55) * mm, "end": v(69.62, 65.57) * mm});
            skLineSegment(sketch, "E2470", {"start": v(69.62, 65.57) * mm, "end": v(69.58, 65.59) * mm});
            skLineSegment(sketch, "E2471", {"start": v(69.58, 65.59) * mm, "end": v(69.54, 65.6) * mm});
            skLineSegment(sketch, "E2472", {"start": v(69.54, 65.6) * mm, "end": v(69.5, 65.61) * mm});
            skLineSegment(sketch, "E2473", {"start": v(69.5, 65.61) * mm, "end": v(69.45, 65.62) * mm});
            skLineSegment(sketch, "E2474", {"start": v(69.45, 65.62) * mm, "end": v(69.4, 65.63) * mm});
            skLineSegment(sketch, "E2475", {"start": v(69.4, 65.63) * mm, "end": v(69.37, 65.64) * mm});
            skLineSegment(sketch, "E2476", {"start": v(69.37, 65.64) * mm, "end": v(69.32, 65.64) * mm});
            skLineSegment(sketch, "E2477", {"start": v(69.32, 65.64) * mm, "end": v(69.28, 65.65) * mm});
            skLineSegment(sketch, "E2478", {"start": v(69.28, 65.65) * mm, "end": v(69.24, 65.65) * mm});
            skLineSegment(sketch, "E2479", {"start": v(69.24, 65.65) * mm, "end": v(69.2, 65.65) * mm});
            skLineSegment(sketch, "E2480", {"start": v(69.2, 65.65) * mm, "end": v(69.15, 65.65) * mm});
            skLineSegment(sketch, "E2481", {"start": v(69.15, 65.65) * mm, "end": v(69.1, 65.65) * mm});
            skLineSegment(sketch, "E2482", {"start": v(69.1, 65.65) * mm, "end": v(69.06, 65.65) * mm});
            skLineSegment(sketch, "E2483", {"start": v(69.06, 65.65) * mm, "end": v(69.02, 65.64) * mm});
            skLineSegment(sketch, "E2484", {"start": v(69.02, 65.64) * mm, "end": v(68.98, 65.64) * mm});
            skLineSegment(sketch, "E2485", {"start": v(68.98, 65.64) * mm, "end": v(68.94, 65.63) * mm});
            skLineSegment(sketch, "E2486", {"start": v(68.9, 65.62) * mm, "end": v(68.85, 65.61) * mm});
            skLineSegment(sketch, "E2487", {"start": v(68.85, 65.61) * mm, "end": v(68.8, 65.6) * mm});
            skLineSegment(sketch, "E2488", {"start": v(68.8, 65.6) * mm, "end": v(68.77, 65.59) * mm});
            skLineSegment(sketch, "E2489", {"start": v(68.77, 65.59) * mm, "end": v(68.73, 65.57) * mm});
            skLineSegment(sketch, "E2490", {"start": v(68.73, 65.57) * mm, "end": v(68.69, 65.55) * mm});
            skLineSegment(sketch, "E2491", {"start": v(68.69, 65.55) * mm, "end": v(68.65, 65.54) * mm});
            skLineSegment(sketch, "E2492", {"start": v(68.65, 65.54) * mm, "end": v(68.6, 65.52) * mm});
            skLineSegment(sketch, "E2493", {"start": v(68.6, 65.52) * mm, "end": v(68.57, 65.5) * mm});
            skLineSegment(sketch, "E2494", {"start": v(68.57, 65.5) * mm, "end": v(68.53, 65.48) * mm});
            skLineSegment(sketch, "E2495", {"start": v(68.53, 65.48) * mm, "end": v(68.5, 65.45) * mm});
            skLineSegment(sketch, "E2496", {"start": v(68.5, 65.45) * mm, "end": v(68.46, 65.43) * mm});
            skLineSegment(sketch, "E2497", {"start": v(68.46, 65.43) * mm, "end": v(68.42, 65.4) * mm});
            skLineSegment(sketch, "E2498", {"start": v(68.42, 65.4) * mm, "end": v(68.39, 65.38) * mm});
            skLineSegment(sketch, "E2499", {"start": v(68.39, 65.38) * mm, "end": v(68.36, 65.35) * mm});
            skLineSegment(sketch, "E2500", {"start": v(68.36, 65.35) * mm, "end": v(68.32, 65.32) * mm});
            skLineSegment(sketch, "E2501", {"start": v(68.18, 65.16) * mm, "end": v(68.15, 65.13) * mm});
            skLineSegment(sketch, "E2502", {"start": v(68.15, 65.13) * mm, "end": v(68.13, 65.09) * mm});
            skLineSegment(sketch, "E2503", {"start": v(68.13, 65.09) * mm, "end": v(68.1, 65.05) * mm});
            skLineSegment(sketch, "E2504", {"start": v(68.1, 65.05) * mm, "end": v(68.08, 65.02) * mm});
            skLineSegment(sketch, "E2505", {"start": v(68.08, 65.02) * mm, "end": v(68.06, 64.98) * mm});
            skLineSegment(sketch, "E2506", {"start": v(68.06, 64.98) * mm, "end": v(68.04, 64.94) * mm});
            skLineSegment(sketch, "E2507", {"start": v(68.04, 64.94) * mm, "end": v(68.03, 64.9) * mm});
            skLineSegment(sketch, "E2508", {"start": v(68.03, 64.9) * mm, "end": v(68, 64.86) * mm});
            skLineSegment(sketch, "E2509", {"start": v(68, 64.86) * mm, "end": v(68, 64.82) * mm});
            skLineSegment(sketch, "E2510", {"start": v(68, 64.82) * mm, "end": v(67.98, 64.78) * mm});
            skLineSegment(sketch, "E2511", {"start": v(67.98, 64.78) * mm, "end": v(67.97, 64.73) * mm});
            skLineSegment(sketch, "E2512", {"start": v(67.93, 64.56) * mm, "end": v(67.93, 64.52) * mm});
            skLineSegment(sketch, "E2513", {"start": v(67.93, 64.52) * mm, "end": v(67.92, 64.48) * mm});
            skLineSegment(sketch, "E2514", {"start": v(67.92, 64.4) * mm, "end": v(67.92, 64.35) * mm});
            skLineSegment(sketch, "E2515", {"start": v(67.92, 64.35) * mm, "end": v(67.93, 64.3) * mm});
            skLineSegment(sketch, "E2516", {"start": v(67.93, 64.3) * mm, "end": v(67.93, 64.26) * mm});
            skLineSegment(sketch, "E2517", {"start": v(67.93, 64.26) * mm, "end": v(67.94, 64.22) * mm});
            skLineSegment(sketch, "E2518", {"start": v(67.94, 64.22) * mm, "end": v(67.94, 64.18) * mm});
            skLineSegment(sketch, "E2519", {"start": v(67.94, 64.18) * mm, "end": v(67.95, 64.13) * mm});
            skLineSegment(sketch, "E2520", {"start": v(67.95, 64.13) * mm, "end": v(67.96, 64.1) * mm});
            skLineSegment(sketch, "E2521", {"start": v(67.96, 64.1) * mm, "end": v(67.97, 64.05) * mm});
            skLineSegment(sketch, "E2522", {"start": v(67.97, 64.05) * mm, "end": v(67.99, 64) * mm});
            skLineSegment(sketch, "E2523", {"start": v(67.99, 64) * mm, "end": v(68, 63.97) * mm});
            skLineSegment(sketch, "E2524", {"start": v(68, 63.97) * mm, "end": v(68.02, 63.93) * mm});
            skLineSegment(sketch, "E2525", {"start": v(68.02, 63.93) * mm, "end": v(68.03, 63.89) * mm});
            skLineSegment(sketch, "E2526", {"start": v(68.03, 63.89) * mm, "end": v(68.05, 63.85) * mm});
            skLineSegment(sketch, "E2527", {"start": v(68.05, 63.85) * mm, "end": v(68.07, 63.8) * mm});
            skLineSegment(sketch, "E2528", {"start": v(68.07, 63.8) * mm, "end": v(68.1, 63.77) * mm});
            skLineSegment(sketch, "E2529", {"start": v(68.1, 63.77) * mm, "end": v(68.12, 63.73) * mm});
            skLineSegment(sketch, "E2530", {"start": v(68.12, 63.73) * mm, "end": v(68.14, 63.7) * mm});
            skLineSegment(sketch, "E2531", {"start": v(68.14, 63.7) * mm, "end": v(68.17, 63.66) * mm});
            skLineSegment(sketch, "E2532", {"start": v(68.17, 63.66) * mm, "end": v(68.2, 63.63) * mm});
            skLineSegment(sketch, "E2533", {"start": v(68.2, 63.63) * mm, "end": v(68.22, 63.6) * mm});
            skLineSegment(sketch, "E2534", {"start": v(68.22, 63.6) * mm, "end": v(68.25, 63.56) * mm});
            skLineSegment(sketch, "E2535", {"start": v(68.25, 63.56) * mm, "end": v(68.28, 63.53) * mm});
            skLineSegment(sketch, "E2536", {"start": v(68.28, 63.53) * mm, "end": v(68.3, 63.5) * mm});
            skLineSegment(sketch, "E2537", {"start": v(68.3, 63.5) * mm, "end": v(68.34, 63.47) * mm});
            skLineSegment(sketch, "E2538", {"start": v(68.34, 63.47) * mm, "end": v(68.37, 63.44) * mm});
            skLineSegment(sketch, "E2539", {"start": v(68.37, 63.44) * mm, "end": v(68.4, 63.41) * mm});
            skLineSegment(sketch, "E2540", {"start": v(68.4, 63.41) * mm, "end": v(68.44, 63.39) * mm});
            skLineSegment(sketch, "E2541", {"start": v(68.44, 63.39) * mm, "end": v(68.48, 63.36) * mm});
            skLineSegment(sketch, "E2542", {"start": v(68.48, 63.36) * mm, "end": v(68.51, 63.34) * mm});
            skLineSegment(sketch, "E2543", {"start": v(68.51, 63.34) * mm, "end": v(68.55, 63.32) * mm});
            skLineSegment(sketch, "E2544", {"start": v(68.55, 63.32) * mm, "end": v(68.59, 63.3) * mm});
            skLineSegment(sketch, "E2545", {"start": v(68.59, 63.3) * mm, "end": v(68.63, 63.28) * mm});
            skLineSegment(sketch, "E2546", {"start": v(68.63, 63.28) * mm, "end": v(68.67, 63.26) * mm});
            skLineSegment(sketch, "E2547", {"start": v(68.67, 63.26) * mm, "end": v(68.7, 63.24) * mm});
            skLineSegment(sketch, "E2548", {"start": v(68.7, 63.24) * mm, "end": v(68.75, 63.23) * mm});
            skLineSegment(sketch, "E2549", {"start": v(68.75, 63.23) * mm, "end": v(68.79, 63.21) * mm});
            skLineSegment(sketch, "E2550", {"start": v(68.79, 63.21) * mm, "end": v(68.83, 63.2) * mm});
            skLineSegment(sketch, "E2551", {"start": v(68.83, 63.2) * mm, "end": v(68.87, 63.19) * mm});
            skLineSegment(sketch, "E2552", {"start": v(68.87, 63.19) * mm, "end": v(68.91, 63.18) * mm});
            skLineSegment(sketch, "E2553", {"start": v(68.91, 63.18) * mm, "end": v(68.96, 63.17) * mm});
            skLineSegment(sketch, "E2554", {"start": v(68.96, 63.17) * mm, "end": v(69, 63.16) * mm});
            skLineSegment(sketch, "E2555", {"start": v(69, 63.16) * mm, "end": v(69.04, 63.16) * mm});
            skLineSegment(sketch, "E2556", {"start": v(69.04, 63.16) * mm, "end": v(69.09, 63.16) * mm});
            skLineSegment(sketch, "E2557", {"start": v(69.09, 63.16) * mm, "end": v(69.13, 63.15) * mm});
            skLineSegment(sketch, "E2558", {"start": v(69.13, 63.15) * mm, "end": v(69.17, 63.15) * mm});
            skLineSegment(sketch, "E2559", {"start": v(69.17, 40.65) * mm, "end": v(69.22, 40.65) * mm});
            skLineSegment(sketch, "E2560", {"start": v(69.22, 40.65) * mm, "end": v(69.26, 40.66) * mm});
            skLineSegment(sketch, "E2561", {"start": v(69.26, 40.66) * mm, "end": v(69.3, 40.66) * mm});
            skLineSegment(sketch, "E2562", {"start": v(69.3, 40.66) * mm, "end": v(69.35, 40.66) * mm});
            skLineSegment(sketch, "E2563", {"start": v(69.35, 40.66) * mm, "end": v(69.39, 40.67) * mm});
            skLineSegment(sketch, "E2564", {"start": v(69.39, 40.67) * mm, "end": v(69.43, 40.68) * mm});
            skLineSegment(sketch, "E2565", {"start": v(69.43, 40.68) * mm, "end": v(69.47, 40.69) * mm});
            skLineSegment(sketch, "E2566", {"start": v(69.47, 40.69) * mm, "end": v(69.52, 40.7) * mm});
            skLineSegment(sketch, "E2567", {"start": v(69.52, 40.7) * mm, "end": v(69.56, 40.71) * mm});
            skLineSegment(sketch, "E2568", {"start": v(69.56, 40.71) * mm, "end": v(69.6, 40.73) * mm});
            skLineSegment(sketch, "E2569", {"start": v(69.6, 40.73) * mm, "end": v(69.64, 40.74) * mm});
            skLineSegment(sketch, "E2570", {"start": v(69.64, 40.74) * mm, "end": v(69.68, 40.76) * mm});
            skLineSegment(sketch, "E2571", {"start": v(69.72, 40.78) * mm, "end": v(69.76, 40.8) * mm});
            skLineSegment(sketch, "E2572", {"start": v(69.76, 40.8) * mm, "end": v(69.8, 40.82) * mm});
            skLineSegment(sketch, "E2573", {"start": v(69.8, 40.82) * mm, "end": v(69.83, 40.84) * mm});
            skLineSegment(sketch, "E2574", {"start": v(69.83, 40.84) * mm, "end": v(69.87, 40.86) * mm});
            skLineSegment(sketch, "E2575", {"start": v(69.87, 40.86) * mm, "end": v(69.9, 40.89) * mm});
            skLineSegment(sketch, "E2576", {"start": v(69.9, 40.89) * mm, "end": v(69.94, 40.91) * mm});
            skLineSegment(sketch, "E2577", {"start": v(69.94, 40.91) * mm, "end": v(69.97, 40.94) * mm});
            skLineSegment(sketch, "E2578", {"start": v(69.97, 40.94) * mm, "end": v(70, 40.97) * mm});
            skLineSegment(sketch, "E2579", {"start": v(70, 40.97) * mm, "end": v(70.04, 41) * mm});
            skLineSegment(sketch, "E2580", {"start": v(70.04, 41) * mm, "end": v(70.07, 41.03) * mm});
            skLineSegment(sketch, "E2581", {"start": v(70.07, 41.03) * mm, "end": v(70.1, 41.06) * mm});
            skLineSegment(sketch, "E2582", {"start": v(70.13, 41.1) * mm, "end": v(70.15, 41.13) * mm});
            skLineSegment(sketch, "E2583", {"start": v(70.15, 41.13) * mm, "end": v(70.18, 41.16) * mm});
            skLineSegment(sketch, "E2584", {"start": v(70.18, 41.16) * mm, "end": v(70.2, 41.2) * mm});
            skLineSegment(sketch, "E2585", {"start": v(70.2, 41.2) * mm, "end": v(70.23, 41.23) * mm});
            skLineSegment(sketch, "E2586", {"start": v(70.23, 41.23) * mm, "end": v(70.25, 41.27) * mm});
            skLineSegment(sketch, "E2587", {"start": v(70.25, 41.27) * mm, "end": v(70.27, 41.3) * mm});
            skLineSegment(sketch, "E2588", {"start": v(70.27, 41.3) * mm, "end": v(70.3, 41.35) * mm});
            skLineSegment(sketch, "E2589", {"start": v(70.3, 41.35) * mm, "end": v(70.31, 41.39) * mm});
            skLineSegment(sketch, "E2590", {"start": v(70.31, 41.39) * mm, "end": v(70.33, 41.43) * mm});
            skLineSegment(sketch, "E2591", {"start": v(70.33, 41.43) * mm, "end": v(70.34, 41.47) * mm});
            skLineSegment(sketch, "E2592", {"start": v(70.34, 41.47) * mm, "end": v(70.36, 41.5) * mm});
            skLineSegment(sketch, "E2593", {"start": v(70.36, 41.5) * mm, "end": v(70.37, 41.55) * mm});
            skLineSegment(sketch, "E2594", {"start": v(70.38, 41.6) * mm, "end": v(70.4, 41.63) * mm});
            skLineSegment(sketch, "E2595", {"start": v(70.4, 41.63) * mm, "end": v(70.4, 41.68) * mm});
            skLineSegment(sketch, "E2596", {"start": v(70.4, 41.68) * mm, "end": v(70.4, 41.72) * mm});
            skLineSegment(sketch, "E2597", {"start": v(70.4, 41.72) * mm, "end": v(70.41, 41.76) * mm});
            skLineSegment(sketch, "E2598", {"start": v(70.41, 41.76) * mm, "end": v(70.42, 41.8) * mm});
            skLineSegment(sketch, "E2599", {"start": v(70.42, 41.8) * mm, "end": v(70.42, 41.85) * mm});
            skLineSegment(sketch, "E2600", {"start": v(70.42, 41.85) * mm, "end": v(70.42, 41.9) * mm});
            skLineSegment(sketch, "E2601", {"start": v(70.42, 41.9) * mm, "end": v(70.42, 41.94) * mm});
            skLineSegment(sketch, "E2602", {"start": v(70.42, 41.94) * mm, "end": v(70.42, 41.98) * mm});
            skLineSegment(sketch, "E2603", {"start": v(70.42, 41.98) * mm, "end": v(70.42, 42.02) * mm});
            skLineSegment(sketch, "E2604", {"start": v(70.42, 42.02) * mm, "end": v(70.41, 42.06) * mm});
            skLineSegment(sketch, "E2605", {"start": v(70.41, 42.06) * mm, "end": v(70.4, 42.1) * mm});
            skLineSegment(sketch, "E2606", {"start": v(70.4, 42.1) * mm, "end": v(70.4, 42.15) * mm});
            skLineSegment(sketch, "E2607", {"start": v(70.4, 42.15) * mm, "end": v(70.39, 42.2) * mm});
            skLineSegment(sketch, "E2608", {"start": v(70.39, 42.2) * mm, "end": v(70.38, 42.23) * mm});
            skLineSegment(sketch, "E2609", {"start": v(70.38, 42.23) * mm, "end": v(70.37, 42.28) * mm});
            skLineSegment(sketch, "E2610", {"start": v(70.37, 42.28) * mm, "end": v(70.35, 42.32) * mm});
            skLineSegment(sketch, "E2611", {"start": v(70.35, 42.32) * mm, "end": v(70.34, 42.36) * mm});
            skLineSegment(sketch, "E2612", {"start": v(70.34, 42.36) * mm, "end": v(70.32, 42.4) * mm});
            skLineSegment(sketch, "E2613", {"start": v(70.32, 42.4) * mm, "end": v(70.3, 42.44) * mm});
            skLineSegment(sketch, "E2614", {"start": v(70.3, 42.44) * mm, "end": v(70.28, 42.48) * mm});
            skLineSegment(sketch, "E2615", {"start": v(70.28, 42.48) * mm, "end": v(70.26, 42.52) * mm});
            skLineSegment(sketch, "E2616", {"start": v(70.26, 42.52) * mm, "end": v(70.24, 42.55) * mm});
            skLineSegment(sketch, "E2617", {"start": v(70.24, 42.55) * mm, "end": v(70.22, 42.59) * mm});
            skLineSegment(sketch, "E2618", {"start": v(70.22, 42.59) * mm, "end": v(70.2, 42.63) * mm});
            skLineSegment(sketch, "E2619", {"start": v(70.2, 42.63) * mm, "end": v(70.17, 42.66) * mm});
            skLineSegment(sketch, "E2620", {"start": v(70.17, 42.66) * mm, "end": v(70.14, 42.7) * mm});
            skLineSegment(sketch, "E2621", {"start": v(70.14, 42.7) * mm, "end": v(70.11, 42.73) * mm});
            skLineSegment(sketch, "E2622", {"start": v(70.05, 42.8) * mm, "end": v(70.02, 42.82) * mm});
            skLineSegment(sketch, "E2623", {"start": v(70.02, 42.82) * mm, "end": v(69.99, 42.85) * mm});
            skLineSegment(sketch, "E2624", {"start": v(69.99, 42.85) * mm, "end": v(69.96, 42.88) * mm});
            skLineSegment(sketch, "E2625", {"start": v(69.92, 42.9) * mm, "end": v(69.89, 42.93) * mm});
            skLineSegment(sketch, "E2626", {"start": v(69.89, 42.93) * mm, "end": v(69.85, 42.95) * mm});
            skLineSegment(sketch, "E2627", {"start": v(69.85, 42.95) * mm, "end": v(69.81, 42.98) * mm});
            skLineSegment(sketch, "E2628", {"start": v(69.81, 42.98) * mm, "end": v(69.78, 43) * mm});
            skLineSegment(sketch, "E2629", {"start": v(69.78, 43) * mm, "end": v(69.74, 43.02) * mm});
            skLineSegment(sketch, "E2630", {"start": v(69.74, 43.02) * mm, "end": v(69.7, 43.04) * mm});
            skLineSegment(sketch, "E2631", {"start": v(69.7, 43.04) * mm, "end": v(69.66, 43.05) * mm});
            skLineSegment(sketch, "E2632", {"start": v(69.66, 43.05) * mm, "end": v(69.62, 43.07) * mm});
            skLineSegment(sketch, "E2633", {"start": v(69.62, 43.07) * mm, "end": v(69.58, 43.09) * mm});
            skLineSegment(sketch, "E2634", {"start": v(69.58, 43.09) * mm, "end": v(69.54, 43.1) * mm});
            skLineSegment(sketch, "E2635", {"start": v(69.54, 43.1) * mm, "end": v(69.5, 43.11) * mm});
            skLineSegment(sketch, "E2636", {"start": v(69.5, 43.11) * mm, "end": v(69.45, 43.12) * mm});
            skLineSegment(sketch, "E2637", {"start": v(69.45, 43.12) * mm, "end": v(69.4, 43.13) * mm});
            skLineSegment(sketch, "E2638", {"start": v(69.4, 43.13) * mm, "end": v(69.37, 43.14) * mm});
            skLineSegment(sketch, "E2639", {"start": v(69.37, 43.14) * mm, "end": v(69.32, 43.14) * mm});
            skLineSegment(sketch, "E2640", {"start": v(69.32, 43.14) * mm, "end": v(69.28, 43.15) * mm});
            skLineSegment(sketch, "E2641", {"start": v(69.28, 43.15) * mm, "end": v(69.24, 43.15) * mm});
            skLineSegment(sketch, "E2642", {"start": v(69.24, 43.15) * mm, "end": v(69.2, 43.15) * mm});
            skLineSegment(sketch, "E2643", {"start": v(69.2, 43.15) * mm, "end": v(69.15, 43.15) * mm});
            skLineSegment(sketch, "E2644", {"start": v(69.15, 43.15) * mm, "end": v(69.1, 43.15) * mm});
            skLineSegment(sketch, "E2645", {"start": v(69.1, 43.15) * mm, "end": v(69.06, 43.15) * mm});
            skLineSegment(sketch, "E2646", {"start": v(69.06, 43.15) * mm, "end": v(69.02, 43.14) * mm});
            skLineSegment(sketch, "E2647", {"start": v(69.02, 43.14) * mm, "end": v(68.98, 43.14) * mm});
            skLineSegment(sketch, "E2648", {"start": v(68.98, 43.14) * mm, "end": v(68.94, 43.13) * mm});
            skLineSegment(sketch, "E2649", {"start": v(68.94, 43.13) * mm, "end": v(68.9, 43.12) * mm});
            skLineSegment(sketch, "E2650", {"start": v(68.9, 43.12) * mm, "end": v(68.85, 43.11) * mm});
            skLineSegment(sketch, "E2651", {"start": v(68.85, 43.11) * mm, "end": v(68.8, 43.1) * mm});
            skLineSegment(sketch, "E2652", {"start": v(68.8, 43.1) * mm, "end": v(68.77, 43.09) * mm});
            skLineSegment(sketch, "E2653", {"start": v(68.77, 43.09) * mm, "end": v(68.73, 43.07) * mm});
            skLineSegment(sketch, "E2654", {"start": v(68.73, 43.07) * mm, "end": v(68.69, 43.05) * mm});
            skLineSegment(sketch, "E2655", {"start": v(68.69, 43.05) * mm, "end": v(68.65, 43.04) * mm});
            skLineSegment(sketch, "E2656", {"start": v(68.65, 43.04) * mm, "end": v(68.6, 43.02) * mm});
            skLineSegment(sketch, "E2657", {"start": v(68.6, 43.02) * mm, "end": v(68.57, 43) * mm});
            skLineSegment(sketch, "E2658", {"start": v(68.53, 42.98) * mm, "end": v(68.5, 42.95) * mm});
            skLineSegment(sketch, "E2659", {"start": v(68.5, 42.95) * mm, "end": v(68.46, 42.93) * mm});
            skLineSegment(sketch, "E2660", {"start": v(68.46, 42.93) * mm, "end": v(68.42, 42.9) * mm});
            skLineSegment(sketch, "E2661", {"start": v(68.42, 42.9) * mm, "end": v(68.39, 42.88) * mm});
            skLineSegment(sketch, "E2662", {"start": v(68.39, 42.88) * mm, "end": v(68.36, 42.85) * mm});
            skLineSegment(sketch, "E2663", {"start": v(68.32, 42.82) * mm, "end": v(68.3, 42.8) * mm});
            skLineSegment(sketch, "E2664", {"start": v(68.3, 42.8) * mm, "end": v(68.26, 42.76) * mm});
            skLineSegment(sketch, "E2665", {"start": v(68.26, 42.76) * mm, "end": v(68.23, 42.73) * mm});
            skLineSegment(sketch, "E2666", {"start": v(68.23, 42.73) * mm, "end": v(68.2, 42.7) * mm});
            skLineSegment(sketch, "E2667", {"start": v(68.2, 42.7) * mm, "end": v(68.18, 42.66) * mm});
            skLineSegment(sketch, "E2668", {"start": v(68.18, 42.66) * mm, "end": v(68.15, 42.63) * mm});
            skLineSegment(sketch, "E2669", {"start": v(68.15, 42.63) * mm, "end": v(68.13, 42.59) * mm});
            skLineSegment(sketch, "E2670", {"start": v(68.13, 42.59) * mm, "end": v(68.1, 42.55) * mm});
            skLineSegment(sketch, "E2671", {"start": v(68.1, 42.55) * mm, "end": v(68.08, 42.52) * mm});
            skLineSegment(sketch, "E2672", {"start": v(68.08, 42.52) * mm, "end": v(68.06, 42.48) * mm});
            skLineSegment(sketch, "E2673", {"start": v(68.06, 42.48) * mm, "end": v(68.04, 42.44) * mm});
            skLineSegment(sketch, "E2674", {"start": v(68.04, 42.44) * mm, "end": v(68.03, 42.4) * mm});
            skLineSegment(sketch, "E2675", {"start": v(68.03, 42.4) * mm, "end": v(68, 42.36) * mm});
            skLineSegment(sketch, "E2676", {"start": v(68, 42.36) * mm, "end": v(68, 42.32) * mm});
            skLineSegment(sketch, "E2677", {"start": v(68, 42.32) * mm, "end": v(67.98, 42.28) * mm});
            skLineSegment(sketch, "E2678", {"start": v(67.98, 42.28) * mm, "end": v(67.97, 42.23) * mm});
            skLineSegment(sketch, "E2679", {"start": v(67.97, 42.23) * mm, "end": v(67.96, 42.2) * mm});
            skLineSegment(sketch, "E2680", {"start": v(67.96, 42.2) * mm, "end": v(67.95, 42.15) * mm});
            skLineSegment(sketch, "E2681", {"start": v(67.95, 42.15) * mm, "end": v(67.94, 42.1) * mm});
            skLineSegment(sketch, "E2682", {"start": v(67.94, 42.1) * mm, "end": v(67.93, 42.06) * mm});
            skLineSegment(sketch, "E2683", {"start": v(67.93, 42.06) * mm, "end": v(67.93, 42.02) * mm});
            skLineSegment(sketch, "E2684", {"start": v(67.93, 42.02) * mm, "end": v(67.92, 41.98) * mm});
            skLineSegment(sketch, "E2685", {"start": v(67.92, 41.98) * mm, "end": v(67.92, 41.94) * mm});
            skLineSegment(sketch, "E2686", {"start": v(67.92, 41.94) * mm, "end": v(67.92, 41.9) * mm});
            skLineSegment(sketch, "E2687", {"start": v(67.92, 41.9) * mm, "end": v(67.92, 41.85) * mm});
            skLineSegment(sketch, "E2688", {"start": v(67.92, 41.85) * mm, "end": v(67.93, 41.8) * mm});
            skLineSegment(sketch, "E2689", {"start": v(67.93, 41.8) * mm, "end": v(67.93, 41.76) * mm});
            skLineSegment(sketch, "E2690", {"start": v(67.93, 41.76) * mm, "end": v(67.94, 41.72) * mm});
            skLineSegment(sketch, "E2691", {"start": v(67.94, 41.68) * mm, "end": v(67.95, 41.63) * mm});
            skLineSegment(sketch, "E2692", {"start": v(67.95, 41.63) * mm, "end": v(67.96, 41.6) * mm});
            skLineSegment(sketch, "E2693", {"start": v(67.96, 41.6) * mm, "end": v(67.97, 41.55) * mm});
            skLineSegment(sketch, "E2694", {"start": v(67.97, 41.55) * mm, "end": v(67.99, 41.5) * mm});
            skLineSegment(sketch, "E2695", {"start": v(67.99, 41.5) * mm, "end": v(68, 41.47) * mm});
            skLineSegment(sketch, "E2696", {"start": v(68.2, 41.13) * mm, "end": v(68.22, 41.1) * mm});
            skLineSegment(sketch, "E2697", {"start": v(68.34, 40.97) * mm, "end": v(68.37, 40.94) * mm});
            skLineSegment(sketch, "E2698", {"start": v(68.37, 40.94) * mm, "end": v(68.4, 40.91) * mm});
            skLineSegment(sketch, "E2699", {"start": v(68.4, 40.91) * mm, "end": v(68.44, 40.89) * mm});
            skLineSegment(sketch, "E2700", {"start": v(68.44, 40.89) * mm, "end": v(68.48, 40.86) * mm});
            skLineSegment(sketch, "E2701", {"start": v(68.48, 40.86) * mm, "end": v(68.51, 40.84) * mm});
            skLineSegment(sketch, "E2702", {"start": v(68.51, 40.84) * mm, "end": v(68.55, 40.82) * mm});
            skLineSegment(sketch, "E2703", {"start": v(68.55, 40.82) * mm, "end": v(68.59, 40.8) * mm});
            skLineSegment(sketch, "E2704", {"start": v(68.59, 40.8) * mm, "end": v(68.63, 40.78) * mm});
            skLineSegment(sketch, "E2705", {"start": v(68.63, 40.78) * mm, "end": v(68.67, 40.76) * mm});
            skLineSegment(sketch, "E2706", {"start": v(68.67, 40.76) * mm, "end": v(68.7, 40.74) * mm});
            skLineSegment(sketch, "E2707", {"start": v(68.7, 40.74) * mm, "end": v(68.75, 40.73) * mm});
            skLineSegment(sketch, "E2708", {"start": v(68.75, 40.73) * mm, "end": v(68.79, 40.71) * mm});
            skLineSegment(sketch, "E2709", {"start": v(68.79, 40.71) * mm, "end": v(68.83, 40.7) * mm});
            skLineSegment(sketch, "E2710", {"start": v(68.83, 40.7) * mm, "end": v(68.87, 40.69) * mm});
            skLineSegment(sketch, "E2711", {"start": v(68.87, 40.69) * mm, "end": v(68.91, 40.68) * mm});
            skLineSegment(sketch, "E2712", {"start": v(68.91, 40.68) * mm, "end": v(68.96, 40.67) * mm});
            skLineSegment(sketch, "E2713", {"start": v(68.96, 40.67) * mm, "end": v(69, 40.66) * mm});
            skLineSegment(sketch, "E2714", {"start": v(69, 40.66) * mm, "end": v(69.04, 40.66) * mm});
            skLineSegment(sketch, "E2715", {"start": v(69.04, 40.66) * mm, "end": v(69.09, 40.66) * mm});
            skLineSegment(sketch, "E2716", {"start": v(69.09, 40.66) * mm, "end": v(69.13, 40.65) * mm});
            skLineSegment(sketch, "E2717", {"start": v(69.13, 40.65) * mm, "end": v(69.17, 40.65) * mm});
            skLineSegment(sketch, "E2718", {"start": v(-77.98, 40.7) * mm, "end": v(-77.94, 40.71) * mm});
            skLineSegment(sketch, "E2719", {"start": v(-77.94, 40.71) * mm, "end": v(-77.9, 40.73) * mm});
            skLineSegment(sketch, "E2720", {"start": v(-77.9, 40.73) * mm, "end": v(-77.86, 40.74) * mm});
            skLineSegment(sketch, "E2721", {"start": v(-77.86, 40.74) * mm, "end": v(-77.82, 40.76) * mm});
            skLineSegment(sketch, "E2722", {"start": v(-77.82, 40.76) * mm, "end": v(-77.78, 40.78) * mm});
            skLineSegment(sketch, "E2723", {"start": v(-77.78, 40.78) * mm, "end": v(-77.74, 40.8) * mm});
            skLineSegment(sketch, "E2724", {"start": v(-77.74, 40.8) * mm, "end": v(-77.7, 40.82) * mm});
            skLineSegment(sketch, "E2725", {"start": v(-77.7, 40.82) * mm, "end": v(-77.67, 40.84) * mm});
            skLineSegment(sketch, "E2726", {"start": v(-77.67, 40.84) * mm, "end": v(-77.63, 40.86) * mm});
            skLineSegment(sketch, "E2727", {"start": v(-77.63, 40.86) * mm, "end": v(-77.6, 40.89) * mm});
            skLineSegment(sketch, "E2728", {"start": v(-77.6, 40.89) * mm, "end": v(-77.56, 40.91) * mm});
            skLineSegment(sketch, "E2729", {"start": v(-77.56, 40.91) * mm, "end": v(-77.53, 40.94) * mm});
            skLineSegment(sketch, "E2730", {"start": v(-77.53, 40.94) * mm, "end": v(-77.5, 40.97) * mm});
            skLineSegment(sketch, "E2731", {"start": v(-77.17, 41.43) * mm, "end": v(-77.16, 41.47) * mm});
            skLineSegment(sketch, "E2732", {"start": v(-77.16, 41.47) * mm, "end": v(-77.14, 41.5) * mm});
            skLineSegment(sketch, "E2733", {"start": v(-77.14, 41.5) * mm, "end": v(-77.13, 41.55) * mm});
            skLineSegment(sketch, "E2734", {"start": v(-77.13, 41.55) * mm, "end": v(-77.12, 41.6) * mm});
            skLineSegment(sketch, "E2735", {"start": v(-77.12, 41.6) * mm, "end": v(-77.1, 41.63) * mm});
            skLineSegment(sketch, "E2736", {"start": v(-77.1, 41.72) * mm, "end": v(-77.09, 41.76) * mm});
            skLineSegment(sketch, "E2737", {"start": v(-77.09, 41.76) * mm, "end": v(-77.08, 41.8) * mm});
            skLineSegment(sketch, "E2738", {"start": v(-77.08, 41.8) * mm, "end": v(-77.08, 41.85) * mm});
            skLineSegment(sketch, "E2739", {"start": v(-77.08, 41.85) * mm, "end": v(-77.08, 41.9) * mm});
            skLineSegment(sketch, "E2740", {"start": v(-77.08, 41.9) * mm, "end": v(-77.08, 41.94) * mm});
            skLineSegment(sketch, "E2741", {"start": v(-77.08, 41.94) * mm, "end": v(-77.08, 41.98) * mm});
            skLineSegment(sketch, "E2742", {"start": v(-77.08, 41.98) * mm, "end": v(-77.08, 42.02) * mm});
            skLineSegment(sketch, "E2743", {"start": v(-77.08, 42.02) * mm, "end": v(-77.09, 42.06) * mm});
            skLineSegment(sketch, "E2744", {"start": v(-77.09, 42.06) * mm, "end": v(-77.1, 42.1) * mm});
            skLineSegment(sketch, "E2745", {"start": v(-77.1, 42.1) * mm, "end": v(-77.1, 42.15) * mm});
            skLineSegment(sketch, "E2746", {"start": v(-77.1, 42.15) * mm, "end": v(-77.11, 42.2) * mm});
            skLineSegment(sketch, "E2747", {"start": v(-77.11, 42.2) * mm, "end": v(-77.12, 42.23) * mm});
            skLineSegment(sketch, "E2748", {"start": v(-77.12, 42.23) * mm, "end": v(-77.13, 42.28) * mm});
            skLineSegment(sketch, "E2749", {"start": v(-77.13, 42.28) * mm, "end": v(-77.15, 42.32) * mm});
            skLineSegment(sketch, "E2750", {"start": v(-77.15, 42.32) * mm, "end": v(-77.16, 42.36) * mm});
            skLineSegment(sketch, "E2751", {"start": v(-77.16, 42.36) * mm, "end": v(-77.18, 42.4) * mm});
            skLineSegment(sketch, "E2752", {"start": v(-77.18, 42.4) * mm, "end": v(-77.2, 42.44) * mm});
            skLineSegment(sketch, "E2753", {"start": v(-77.2, 42.44) * mm, "end": v(-77.22, 42.48) * mm});
            skLineSegment(sketch, "E2754", {"start": v(-77.22, 42.48) * mm, "end": v(-77.24, 42.52) * mm});
            skLineSegment(sketch, "E2755", {"start": v(-77.26, 42.55) * mm, "end": v(-77.28, 42.59) * mm});
            skLineSegment(sketch, "E2756", {"start": v(-77.28, 42.59) * mm, "end": v(-77.3, 42.63) * mm});
            skLineSegment(sketch, "E2757", {"start": v(-77.3, 42.63) * mm, "end": v(-77.33, 42.66) * mm});
            skLineSegment(sketch, "E2758", {"start": v(-77.33, 42.66) * mm, "end": v(-77.36, 42.7) * mm});
            skLineSegment(sketch, "E2759", {"start": v(-77.36, 42.7) * mm, "end": v(-77.39, 42.73) * mm});
            skLineSegment(sketch, "E2760", {"start": v(-77.39, 42.73) * mm, "end": v(-77.42, 42.76) * mm});
            skLineSegment(sketch, "E2761", {"start": v(-77.42, 42.76) * mm, "end": v(-77.45, 42.8) * mm});
            skLineSegment(sketch, "E2762", {"start": v(-77.45, 42.8) * mm, "end": v(-77.48, 42.82) * mm});
            skLineSegment(sketch, "E2763", {"start": v(-77.48, 42.82) * mm, "end": v(-77.51, 42.85) * mm});
            skLineSegment(sketch, "E2764", {"start": v(-77.51, 42.85) * mm, "end": v(-77.54, 42.88) * mm});
            skLineSegment(sketch, "E2765", {"start": v(-77.54, 42.88) * mm, "end": v(-77.58, 42.9) * mm});
            skLineSegment(sketch, "E2766", {"start": v(-77.58, 42.9) * mm, "end": v(-77.61, 42.93) * mm});
            skLineSegment(sketch, "E2767", {"start": v(-77.61, 42.93) * mm, "end": v(-77.65, 42.95) * mm});
            skLineSegment(sketch, "E2768", {"start": v(-77.65, 42.95) * mm, "end": v(-77.69, 42.98) * mm});
            skLineSegment(sketch, "E2769", {"start": v(-77.69, 42.98) * mm, "end": v(-77.72, 43) * mm});
            skLineSegment(sketch, "E2770", {"start": v(-77.72, 43) * mm, "end": v(-77.76, 43.02) * mm});
            skLineSegment(sketch, "E2771", {"start": v(-77.76, 43.02) * mm, "end": v(-77.8, 43.04) * mm});
            skLineSegment(sketch, "E2772", {"start": v(-77.8, 43.04) * mm, "end": v(-77.84, 43.05) * mm});
            skLineSegment(sketch, "E2773", {"start": v(-77.84, 43.05) * mm, "end": v(-77.88, 43.07) * mm});
            skLineSegment(sketch, "E2774", {"start": v(-77.92, 43.09) * mm, "end": v(-77.96, 43.1) * mm});
            skLineSegment(sketch, "E2775", {"start": v(-77.96, 43.1) * mm, "end": v(-78, 43.11) * mm});
            skLineSegment(sketch, "E2776", {"start": v(-78.35, 43.15) * mm, "end": v(-78.4, 43.15) * mm});
            skLineSegment(sketch, "E2777", {"start": v(-78.4, 43.15) * mm, "end": v(-78.44, 43.15) * mm});
            skLineSegment(sketch, "E2778", {"start": v(-78.44, 43.15) * mm, "end": v(-78.48, 43.14) * mm});
            skLineSegment(sketch, "E2779", {"start": v(-78.48, 43.14) * mm, "end": v(-78.52, 43.14) * mm});
            skLineSegment(sketch, "E2780", {"start": v(-78.52, 43.14) * mm, "end": v(-78.56, 43.13) * mm});
            skLineSegment(sketch, "E2781", {"start": v(-78.56, 43.13) * mm, "end": v(-78.6, 43.12) * mm});
            skLineSegment(sketch, "E2782", {"start": v(-78.6, 43.12) * mm, "end": v(-78.65, 43.11) * mm});
            skLineSegment(sketch, "E2783", {"start": v(-78.65, 43.11) * mm, "end": v(-78.7, 43.1) * mm});
            skLineSegment(sketch, "E2784", {"start": v(-78.7, 43.1) * mm, "end": v(-78.73, 43.09) * mm});
            skLineSegment(sketch, "E2785", {"start": v(-78.73, 43.09) * mm, "end": v(-78.77, 43.07) * mm});
            skLineSegment(sketch, "E2786", {"start": v(-78.77, 43.07) * mm, "end": v(-78.81, 43.05) * mm});
            skLineSegment(sketch, "E2787", {"start": v(-78.81, 43.05) * mm, "end": v(-78.85, 43.04) * mm});
            skLineSegment(sketch, "E2788", {"start": v(-78.85, 43.04) * mm, "end": v(-78.9, 43.02) * mm});
            skLineSegment(sketch, "E2789", {"start": v(-78.9, 43.02) * mm, "end": v(-78.93, 43) * mm});
            skLineSegment(sketch, "E2790", {"start": v(-78.93, 43) * mm, "end": v(-78.97, 42.98) * mm});
            skLineSegment(sketch, "E2791", {"start": v(-78.97, 42.98) * mm, "end": v(-79, 42.95) * mm});
            skLineSegment(sketch, "E2792", {"start": v(-79, 42.95) * mm, "end": v(-79.04, 42.93) * mm});
            skLineSegment(sketch, "E2793", {"start": v(-79.04, 42.93) * mm, "end": v(-79.08, 42.9) * mm});
            skLineSegment(sketch, "E2794", {"start": v(-79.08, 42.9) * mm, "end": v(-79.11, 42.88) * mm});
            skLineSegment(sketch, "E2795", {"start": v(-79.11, 42.88) * mm, "end": v(-79.14, 42.85) * mm});
            skLineSegment(sketch, "E2796", {"start": v(-79.24, 42.76) * mm, "end": v(-79.27, 42.73) * mm});
            skLineSegment(sketch, "E2797", {"start": v(-79.27, 42.73) * mm, "end": v(-79.3, 42.7) * mm});
            skLineSegment(sketch, "E2798", {"start": v(-79.3, 42.7) * mm, "end": v(-79.32, 42.66) * mm});
            skLineSegment(sketch, "E2799", {"start": v(-79.35, 42.63) * mm, "end": v(-79.37, 42.59) * mm});
            skLineSegment(sketch, "E2800", {"start": v(-79.37, 42.59) * mm, "end": v(-79.4, 42.55) * mm});
            skLineSegment(sketch, "E2801", {"start": v(-79.4, 42.55) * mm, "end": v(-79.42, 42.52) * mm});
            skLineSegment(sketch, "E2802", {"start": v(-79.44, 42.48) * mm, "end": v(-79.46, 42.44) * mm});
            skLineSegment(sketch, "E2803", {"start": v(-79.46, 42.44) * mm, "end": v(-79.47, 42.4) * mm});
            skLineSegment(sketch, "E2804", {"start": v(-79.47, 42.4) * mm, "end": v(-79.5, 42.36) * mm});
            skLineSegment(sketch, "E2805", {"start": v(-79.5, 42.36) * mm, "end": v(-79.5, 42.32) * mm});
            skLineSegment(sketch, "E2806", {"start": v(-79.5, 42.32) * mm, "end": v(-79.52, 42.28) * mm});
            skLineSegment(sketch, "E2807", {"start": v(-79.52, 42.28) * mm, "end": v(-79.53, 42.23) * mm});
            skLineSegment(sketch, "E2808", {"start": v(-79.53, 42.23) * mm, "end": v(-79.54, 42.2) * mm});
            skLineSegment(sketch, "E2809", {"start": v(-79.54, 42.2) * mm, "end": v(-79.55, 42.15) * mm});
            skLineSegment(sketch, "E2810", {"start": v(-79.55, 42.15) * mm, "end": v(-79.56, 42.1) * mm});
            skLineSegment(sketch, "E2811", {"start": v(-79.56, 42.1) * mm, "end": v(-79.57, 42.06) * mm});
            skLineSegment(sketch, "E2812", {"start": v(-79.57, 42.06) * mm, "end": v(-79.57, 42.02) * mm});
            skLineSegment(sketch, "E2813", {"start": v(-79.57, 42.02) * mm, "end": v(-79.58, 41.98) * mm});
            skLineSegment(sketch, "E2814", {"start": v(-79.58, 41.98) * mm, "end": v(-79.58, 41.94) * mm});
            skLineSegment(sketch, "E2815", {"start": v(-79.58, 41.94) * mm, "end": v(-79.58, 41.9) * mm});
            skLineSegment(sketch, "E2816", {"start": v(-79.58, 41.9) * mm, "end": v(-79.58, 41.85) * mm});
            skLineSegment(sketch, "E2817", {"start": v(-79.58, 41.85) * mm, "end": v(-79.57, 41.8) * mm});
            skLineSegment(sketch, "E2818", {"start": v(-79.57, 41.8) * mm, "end": v(-79.57, 41.76) * mm});
            skLineSegment(sketch, "E2819", {"start": v(-79.57, 41.76) * mm, "end": v(-79.56, 41.72) * mm});
            skLineSegment(sketch, "E2820", {"start": v(-79.56, 41.72) * mm, "end": v(-79.56, 41.68) * mm});
            skLineSegment(sketch, "E2821", {"start": v(-79.56, 41.68) * mm, "end": v(-79.55, 41.63) * mm});
            skLineSegment(sketch, "E2822", {"start": v(-79.55, 41.63) * mm, "end": v(-79.54, 41.6) * mm});
            skLineSegment(sketch, "E2823", {"start": v(-79.54, 41.6) * mm, "end": v(-79.53, 41.55) * mm});
            skLineSegment(sketch, "E2824", {"start": v(-79.53, 41.55) * mm, "end": v(-79.51, 41.5) * mm});
            skLineSegment(sketch, "E2825", {"start": v(-79.5, 41.47) * mm, "end": v(-79.48, 41.43) * mm});
            skLineSegment(sketch, "E2826", {"start": v(-79.48, 41.43) * mm, "end": v(-79.47, 41.39) * mm});
            skLineSegment(sketch, "E2827", {"start": v(-79.47, 41.39) * mm, "end": v(-79.45, 41.35) * mm});
            skLineSegment(sketch, "E2828", {"start": v(-79.45, 41.35) * mm, "end": v(-79.43, 41.3) * mm});
            skLineSegment(sketch, "E2829", {"start": v(-79.43, 41.3) * mm, "end": v(-79.4, 41.27) * mm});
            skLineSegment(sketch, "E2830", {"start": v(-79.4, 41.27) * mm, "end": v(-79.38, 41.23) * mm});
            skLineSegment(sketch, "E2831", {"start": v(-79.38, 41.23) * mm, "end": v(-79.36, 41.2) * mm});
            skLineSegment(sketch, "E2832", {"start": v(-79.36, 41.2) * mm, "end": v(-79.33, 41.16) * mm});
            skLineSegment(sketch, "E2833", {"start": v(-79.33, 41.16) * mm, "end": v(-79.3, 41.13) * mm});
            skLineSegment(sketch, "E2834", {"start": v(-79.3, 41.13) * mm, "end": v(-79.28, 41.1) * mm});
            skLineSegment(sketch, "E2835", {"start": v(-79.28, 41.1) * mm, "end": v(-79.25, 41.06) * mm});
            skLineSegment(sketch, "E2836", {"start": v(-79.25, 41.06) * mm, "end": v(-79.22, 41.03) * mm});
            skLineSegment(sketch, "E2837", {"start": v(-79.22, 41.03) * mm, "end": v(-79.2, 41) * mm});
            skLineSegment(sketch, "E2838", {"start": v(-79.2, 41) * mm, "end": v(-79.16, 40.97) * mm});
            skLineSegment(sketch, "E2839", {"start": v(-79.16, 40.97) * mm, "end": v(-79.13, 40.94) * mm});
            skLineSegment(sketch, "E2840", {"start": v(-79.13, 40.94) * mm, "end": v(-79.1, 40.91) * mm});
            skLineSegment(sketch, "E2841", {"start": v(-79.1, 40.91) * mm, "end": v(-79.06, 40.89) * mm});
            skLineSegment(sketch, "E2842", {"start": v(-79.06, 40.89) * mm, "end": v(-79.02, 40.86) * mm});
            skLineSegment(sketch, "E2843", {"start": v(-79.02, 40.86) * mm, "end": v(-78.99, 40.84) * mm});
            skLineSegment(sketch, "E2844", {"start": v(-78.95, 40.82) * mm, "end": v(-78.91, 40.8) * mm});
            skLineSegment(sketch, "E2845", {"start": v(-78.91, 40.8) * mm, "end": v(-78.87, 40.78) * mm});
            skLineSegment(sketch, "E2846", {"start": v(-78.87, 40.78) * mm, "end": v(-78.83, 40.76) * mm});
            skLineSegment(sketch, "E2847", {"start": v(-78.83, 40.76) * mm, "end": v(-78.8, 40.74) * mm});
            skLineSegment(sketch, "E2848", {"start": v(-78.8, 40.74) * mm, "end": v(-78.75, 40.73) * mm});
            skLineSegment(sketch, "E2849", {"start": v(-78.75, 40.73) * mm, "end": v(-78.71, 40.71) * mm});
            skLineSegment(sketch, "E2850", {"start": v(-78.71, 40.71) * mm, "end": v(-78.67, 40.7) * mm});
            skLineSegment(sketch, "E2851", {"start": v(-78.67, 40.7) * mm, "end": v(-78.63, 40.69) * mm});
            skLineSegment(sketch, "E2852", {"start": v(-78.63, 40.69) * mm, "end": v(-78.59, 40.68) * mm});
            skLineSegment(sketch, "E2853", {"start": v(-78.59, 40.68) * mm, "end": v(-78.54, 40.67) * mm});
            skLineSegment(sketch, "E2854", {"start": v(-78.54, 40.67) * mm, "end": v(-78.5, 40.66) * mm});
            skLineSegment(sketch, "E2855", {"start": v(-78.5, 40.66) * mm, "end": v(-78.46, 40.66) * mm});
            skLineSegment(sketch, "E2856", {"start": v(-78.46, 40.66) * mm, "end": v(-78.41, 40.66) * mm});
            skLineSegment(sketch, "E2857", {"start": v(-78.41, 40.66) * mm, "end": v(-78.37, 40.65) * mm});
            skLineSegment(sketch, "E2858", {"start": v(-78.37, 40.65) * mm, "end": v(-78.33, 40.65) * mm});
            skLineSegment(sketch, "E2859", {"start": v(-78.33, 63.15) * mm, "end": v(-78.28, 63.15) * mm});
            skLineSegment(sketch, "E2860", {"start": v(-78.28, 63.15) * mm, "end": v(-78.24, 63.16) * mm});
            skLineSegment(sketch, "E2861", {"start": v(-78.24, 63.16) * mm, "end": v(-78.2, 63.16) * mm});
            skLineSegment(sketch, "E2862", {"start": v(-78.2, 63.16) * mm, "end": v(-78.15, 63.16) * mm});
            skLineSegment(sketch, "E2863", {"start": v(-78.15, 63.16) * mm, "end": v(-78.11, 63.17) * mm});
            skLineSegment(sketch, "E2864", {"start": v(-78.11, 63.17) * mm, "end": v(-78.07, 63.18) * mm});
            skLineSegment(sketch, "E2865", {"start": v(-78.07, 63.18) * mm, "end": v(-78.03, 63.19) * mm});
            skLineSegment(sketch, "E2866", {"start": v(-78.03, 63.19) * mm, "end": v(-77.98, 63.2) * mm});
            skLineSegment(sketch, "E2867", {"start": v(-77.98, 63.2) * mm, "end": v(-77.94, 63.21) * mm});
            skLineSegment(sketch, "E2868", {"start": v(-77.94, 63.21) * mm, "end": v(-77.9, 63.23) * mm});
            skLineSegment(sketch, "E2869", {"start": v(-77.9, 63.23) * mm, "end": v(-77.86, 63.24) * mm});
            skLineSegment(sketch, "E2870", {"start": v(-77.86, 63.24) * mm, "end": v(-77.82, 63.26) * mm});
            skLineSegment(sketch, "E2871", {"start": v(-77.82, 63.26) * mm, "end": v(-77.78, 63.28) * mm});
            skLineSegment(sketch, "E2872", {"start": v(-77.78, 63.28) * mm, "end": v(-77.74, 63.3) * mm});
            skLineSegment(sketch, "E2873", {"start": v(-77.74, 63.3) * mm, "end": v(-77.7, 63.32) * mm});
            skLineSegment(sketch, "E2874", {"start": v(-77.7, 63.32) * mm, "end": v(-77.67, 63.34) * mm});
            skLineSegment(sketch, "E2875", {"start": v(-77.67, 63.34) * mm, "end": v(-77.63, 63.36) * mm});
            skLineSegment(sketch, "E2876", {"start": v(-77.63, 63.36) * mm, "end": v(-77.6, 63.39) * mm});
            skLineSegment(sketch, "E2877", {"start": v(-77.6, 63.39) * mm, "end": v(-77.56, 63.41) * mm});
            skLineSegment(sketch, "E2878", {"start": v(-77.56, 63.41) * mm, "end": v(-77.53, 63.44) * mm});
            skLineSegment(sketch, "E2879", {"start": v(-77.53, 63.44) * mm, "end": v(-77.5, 63.47) * mm});
            skLineSegment(sketch, "E2880", {"start": v(-77.5, 63.47) * mm, "end": v(-77.46, 63.5) * mm});
            skLineSegment(sketch, "E2881", {"start": v(-77.46, 63.5) * mm, "end": v(-77.43, 63.53) * mm});
            skLineSegment(sketch, "E2882", {"start": v(-77.43, 63.53) * mm, "end": v(-77.4, 63.56) * mm});
            skLineSegment(sketch, "E2883", {"start": v(-77.37, 63.6) * mm, "end": v(-77.35, 63.63) * mm});
            skLineSegment(sketch, "E2884", {"start": v(-77.35, 63.63) * mm, "end": v(-77.32, 63.66) * mm});
            skLineSegment(sketch, "E2885", {"start": v(-77.32, 63.66) * mm, "end": v(-77.3, 63.7) * mm});
            skLineSegment(sketch, "E2886", {"start": v(-77.3, 63.7) * mm, "end": v(-77.27, 63.73) * mm});
            skLineSegment(sketch, "E2887", {"start": v(-77.27, 63.73) * mm, "end": v(-77.25, 63.77) * mm});
            skLineSegment(sketch, "E2888", {"start": v(-77.25, 63.77) * mm, "end": v(-77.23, 63.8) * mm});
            skLineSegment(sketch, "E2889", {"start": v(-77.23, 63.8) * mm, "end": v(-77.2, 63.85) * mm});
            skLineSegment(sketch, "E2890", {"start": v(-77.2, 63.85) * mm, "end": v(-77.19, 63.89) * mm});
            skLineSegment(sketch, "E2891", {"start": v(-77.19, 63.89) * mm, "end": v(-77.17, 63.93) * mm});
            skLineSegment(sketch, "E2892", {"start": v(-77.17, 63.93) * mm, "end": v(-77.16, 63.97) * mm});
            skLineSegment(sketch, "E2893", {"start": v(-77.16, 63.97) * mm, "end": v(-77.14, 64) * mm});
            skLineSegment(sketch, "E2894", {"start": v(-77.14, 64) * mm, "end": v(-77.13, 64.05) * mm});
            skLineSegment(sketch, "E2895", {"start": v(-77.13, 64.05) * mm, "end": v(-77.12, 64.1) * mm});
            skLineSegment(sketch, "E2896", {"start": v(-77.12, 64.1) * mm, "end": v(-77.1, 64.13) * mm});
            skLineSegment(sketch, "E2897", {"start": v(-77.1, 64.13) * mm, "end": v(-77.1, 64.18) * mm});
            skLineSegment(sketch, "E2898", {"start": v(-77.1, 64.18) * mm, "end": v(-77.1, 64.22) * mm});
            skLineSegment(sketch, "E2899", {"start": v(-77.1, 64.22) * mm, "end": v(-77.09, 64.26) * mm});
            skLineSegment(sketch, "E2900", {"start": v(-77.09, 64.26) * mm, "end": v(-77.08, 64.3) * mm});
            skLineSegment(sketch, "E2901", {"start": v(-77.08, 64.3) * mm, "end": v(-77.08, 64.35) * mm});
            skLineSegment(sketch, "E2902", {"start": v(-77.08, 64.35) * mm, "end": v(-77.08, 64.4) * mm});
            skLineSegment(sketch, "E2903", {"start": v(-77.08, 64.44) * mm, "end": v(-77.08, 64.48) * mm});
            skLineSegment(sketch, "E2904", {"start": v(-77.08, 64.48) * mm, "end": v(-77.08, 64.52) * mm});
            skLineSegment(sketch, "E2905", {"start": v(-77.08, 64.52) * mm, "end": v(-77.09, 64.56) * mm});
            skLineSegment(sketch, "E2906", {"start": v(-77.09, 64.56) * mm, "end": v(-77.1, 64.6) * mm});
            skLineSegment(sketch, "E2907", {"start": v(-77.1, 64.6) * mm, "end": v(-77.1, 64.65) * mm});
            skLineSegment(sketch, "E2908", {"start": v(-77.1, 64.65) * mm, "end": v(-77.11, 64.7) * mm});
            skLineSegment(sketch, "E2909", {"start": v(-77.11, 64.7) * mm, "end": v(-77.12, 64.73) * mm});
            skLineSegment(sketch, "E2910", {"start": v(-77.13, 64.78) * mm, "end": v(-77.15, 64.82) * mm});
            skLineSegment(sketch, "E2911", {"start": v(-77.15, 64.82) * mm, "end": v(-77.16, 64.86) * mm});
            skLineSegment(sketch, "E2912", {"start": v(-77.16, 64.86) * mm, "end": v(-77.18, 64.9) * mm});
            skLineSegment(sketch, "E2913", {"start": v(-77.18, 64.9) * mm, "end": v(-77.2, 64.94) * mm});
            skLineSegment(sketch, "E2914", {"start": v(-77.2, 64.94) * mm, "end": v(-77.22, 64.98) * mm});
            skLineSegment(sketch, "E2915", {"start": v(-77.22, 64.98) * mm, "end": v(-77.24, 65.02) * mm});
            skLineSegment(sketch, "E2916", {"start": v(-77.24, 65.02) * mm, "end": v(-77.26, 65.05) * mm});
            skLineSegment(sketch, "E2917", {"start": v(-77.26, 65.05) * mm, "end": v(-77.28, 65.09) * mm});
            skLineSegment(sketch, "E2918", {"start": v(-77.28, 65.09) * mm, "end": v(-77.3, 65.13) * mm});
            skLineSegment(sketch, "E2919", {"start": v(-77.3, 65.13) * mm, "end": v(-77.33, 65.16) * mm});
            skLineSegment(sketch, "E2920", {"start": v(-77.33, 65.16) * mm, "end": v(-77.36, 65.2) * mm});
            skLineSegment(sketch, "E2921", {"start": v(-77.51, 65.35) * mm, "end": v(-77.54, 65.38) * mm});
            skLineSegment(sketch, "E2922", {"start": v(-77.54, 65.38) * mm, "end": v(-77.58, 65.4) * mm});
            skLineSegment(sketch, "E2923", {"start": v(-77.69, 65.48) * mm, "end": v(-77.72, 65.5) * mm});
            skLineSegment(sketch, "E2924", {"start": v(-77.72, 65.5) * mm, "end": v(-77.76, 65.52) * mm});
            skLineSegment(sketch, "E2925", {"start": v(-77.76, 65.52) * mm, "end": v(-77.8, 65.54) * mm});
            skLineSegment(sketch, "E2926", {"start": v(-77.8, 65.54) * mm, "end": v(-77.84, 65.55) * mm});
            skLineSegment(sketch, "E2927", {"start": v(-77.84, 65.55) * mm, "end": v(-77.88, 65.57) * mm});
            skLineSegment(sketch, "E2928", {"start": v(-77.88, 65.57) * mm, "end": v(-77.92, 65.59) * mm});
            skLineSegment(sketch, "E2929", {"start": v(-77.92, 65.59) * mm, "end": v(-77.96, 65.6) * mm});
            skLineSegment(sketch, "E2930", {"start": v(-78, 65.61) * mm, "end": v(-78.05, 65.62) * mm});
            skLineSegment(sketch, "E2931", {"start": v(-78.05, 65.62) * mm, "end": v(-78.1, 65.63) * mm});
            skLineSegment(sketch, "E2932", {"start": v(-78.1, 65.63) * mm, "end": v(-78.13, 65.64) * mm});
            skLineSegment(sketch, "E2933", {"start": v(-78.13, 65.64) * mm, "end": v(-78.18, 65.64) * mm});
            skLineSegment(sketch, "E2934", {"start": v(-78.18, 65.64) * mm, "end": v(-78.22, 65.65) * mm});
            skLineSegment(sketch, "E2935", {"start": v(-78.26, 65.65) * mm, "end": v(-78.3, 65.65) * mm});
            skLineSegment(sketch, "E2936", {"start": v(-78.3, 65.65) * mm, "end": v(-78.35, 65.65) * mm});
            skLineSegment(sketch, "E2937", {"start": v(-78.35, 65.65) * mm, "end": v(-78.4, 65.65) * mm});
            skLineSegment(sketch, "E2938", {"start": v(-78.4, 65.65) * mm, "end": v(-78.44, 65.65) * mm});
            skLineSegment(sketch, "E2939", {"start": v(-78.44, 65.65) * mm, "end": v(-78.48, 65.64) * mm});
            skLineSegment(sketch, "E2940", {"start": v(-78.48, 65.64) * mm, "end": v(-78.52, 65.64) * mm});
            skLineSegment(sketch, "E2941", {"start": v(-78.52, 65.64) * mm, "end": v(-78.56, 65.63) * mm});
            skLineSegment(sketch, "E2942", {"start": v(-78.56, 65.63) * mm, "end": v(-78.6, 65.62) * mm});
            skLineSegment(sketch, "E2943", {"start": v(-78.6, 65.62) * mm, "end": v(-78.65, 65.61) * mm});
            skLineSegment(sketch, "E2944", {"start": v(-78.65, 65.61) * mm, "end": v(-78.7, 65.6) * mm});
            skLineSegment(sketch, "E2945", {"start": v(-78.7, 65.6) * mm, "end": v(-78.73, 65.59) * mm});
            skLineSegment(sketch, "E2946", {"start": v(-78.73, 65.59) * mm, "end": v(-78.77, 65.57) * mm});
            skLineSegment(sketch, "E2947", {"start": v(-78.77, 65.57) * mm, "end": v(-78.81, 65.55) * mm});
            skLineSegment(sketch, "E2948", {"start": v(-78.81, 65.55) * mm, "end": v(-78.85, 65.54) * mm});
            skLineSegment(sketch, "E2949", {"start": v(-78.85, 65.54) * mm, "end": v(-78.9, 65.52) * mm});
            skLineSegment(sketch, "E2950", {"start": v(-78.9, 65.52) * mm, "end": v(-78.93, 65.5) * mm});
            skLineSegment(sketch, "E2951", {"start": v(-78.93, 65.5) * mm, "end": v(-78.97, 65.48) * mm});
            skLineSegment(sketch, "E2952", {"start": v(-78.97, 65.48) * mm, "end": v(-79, 65.45) * mm});
            skLineSegment(sketch, "E2953", {"start": v(-79, 65.45) * mm, "end": v(-79.04, 65.43) * mm});
            skLineSegment(sketch, "E2954", {"start": v(-79.04, 65.43) * mm, "end": v(-79.08, 65.4) * mm});
            skLineSegment(sketch, "E2955", {"start": v(-79.08, 65.4) * mm, "end": v(-79.11, 65.38) * mm});
            skLineSegment(sketch, "E2956", {"start": v(-79.11, 65.38) * mm, "end": v(-79.14, 65.35) * mm});
            skLineSegment(sketch, "E2957", {"start": v(-79.14, 65.35) * mm, "end": v(-79.18, 65.32) * mm});
            skLineSegment(sketch, "E2958", {"start": v(-79.18, 65.32) * mm, "end": v(-79.2, 65.3) * mm});
            skLineSegment(sketch, "E2959", {"start": v(-79.2, 65.3) * mm, "end": v(-79.24, 65.26) * mm});
            skLineSegment(sketch, "E2960", {"start": v(-79.24, 65.26) * mm, "end": v(-79.27, 65.23) * mm});
            skLineSegment(sketch, "E2961", {"start": v(-79.27, 65.23) * mm, "end": v(-79.3, 65.2) * mm});
            skLineSegment(sketch, "E2962", {"start": v(-79.3, 65.2) * mm, "end": v(-79.32, 65.16) * mm});
            skLineSegment(sketch, "E2963", {"start": v(-79.32, 65.16) * mm, "end": v(-79.35, 65.13) * mm});
            skLineSegment(sketch, "E2964", {"start": v(-79.35, 65.13) * mm, "end": v(-79.37, 65.09) * mm});
            skLineSegment(sketch, "E2965", {"start": v(-79.37, 65.09) * mm, "end": v(-79.4, 65.05) * mm});
            skLineSegment(sketch, "E2966", {"start": v(-79.4, 65.05) * mm, "end": v(-79.42, 65.02) * mm});
            skLineSegment(sketch, "E2967", {"start": v(-79.42, 65.02) * mm, "end": v(-79.44, 64.98) * mm});
            skLineSegment(sketch, "E2968", {"start": v(-79.46, 64.94) * mm, "end": v(-79.47, 64.9) * mm});
            skLineSegment(sketch, "E2969", {"start": v(-79.47, 64.9) * mm, "end": v(-79.5, 64.86) * mm});
            skLineSegment(sketch, "E2970", {"start": v(-79.5, 64.86) * mm, "end": v(-79.5, 64.82) * mm});
            skLineSegment(sketch, "E2971", {"start": v(-79.5, 64.82) * mm, "end": v(-79.52, 64.78) * mm});
            skLineSegment(sketch, "E2972", {"start": v(-79.52, 64.78) * mm, "end": v(-79.53, 64.73) * mm});
            skLineSegment(sketch, "E2973", {"start": v(-79.53, 64.73) * mm, "end": v(-79.54, 64.7) * mm});
            skLineSegment(sketch, "E2974", {"start": v(-79.54, 64.7) * mm, "end": v(-79.55, 64.65) * mm});
            skLineSegment(sketch, "E2975", {"start": v(-79.55, 64.65) * mm, "end": v(-79.56, 64.6) * mm});
            skLineSegment(sketch, "E2976", {"start": v(-79.56, 64.6) * mm, "end": v(-79.57, 64.56) * mm});
            skLineSegment(sketch, "E2977", {"start": v(-79.57, 64.56) * mm, "end": v(-79.57, 64.52) * mm});
            skLineSegment(sketch, "E2978", {"start": v(-79.58, 64.48) * mm, "end": v(-79.58, 64.44) * mm});
            skLineSegment(sketch, "E2979", {"start": v(-79.58, 64.35) * mm, "end": v(-79.57, 64.3) * mm});
            skLineSegment(sketch, "E2980", {"start": v(-79.57, 64.3) * mm, "end": v(-79.57, 64.26) * mm});
            skLineSegment(sketch, "E2981", {"start": v(-79.57, 64.26) * mm, "end": v(-79.56, 64.22) * mm});
            skLineSegment(sketch, "E2982", {"start": v(-79.56, 64.22) * mm, "end": v(-79.56, 64.18) * mm});
            skLineSegment(sketch, "E2983", {"start": v(-79.56, 64.18) * mm, "end": v(-79.55, 64.13) * mm});
            skLineSegment(sketch, "E2984", {"start": v(-79.55, 64.13) * mm, "end": v(-79.54, 64.1) * mm});
            skLineSegment(sketch, "E2985", {"start": v(-79.54, 64.1) * mm, "end": v(-79.53, 64.05) * mm});
            skLineSegment(sketch, "E2986", {"start": v(-79.53, 64.05) * mm, "end": v(-79.51, 64) * mm});
            skLineSegment(sketch, "E2987", {"start": v(-79.51, 64) * mm, "end": v(-79.5, 63.97) * mm});
            skLineSegment(sketch, "E2988", {"start": v(-79.5, 63.97) * mm, "end": v(-79.48, 63.93) * mm});
            skLineSegment(sketch, "E2989", {"start": v(-79.48, 63.93) * mm, "end": v(-79.47, 63.89) * mm});
            skLineSegment(sketch, "E2990", {"start": v(-79.47, 63.89) * mm, "end": v(-79.45, 63.85) * mm});
            skLineSegment(sketch, "E2991", {"start": v(-79.45, 63.85) * mm, "end": v(-79.43, 63.8) * mm});
            skLineSegment(sketch, "E2992", {"start": v(-79.43, 63.8) * mm, "end": v(-79.4, 63.77) * mm});
            skLineSegment(sketch, "E2993", {"start": v(-79.4, 63.77) * mm, "end": v(-79.38, 63.73) * mm});
            skLineSegment(sketch, "E2994", {"start": v(-79.38, 63.73) * mm, "end": v(-79.36, 63.7) * mm});
            skLineSegment(sketch, "E2995", {"start": v(-79.36, 63.7) * mm, "end": v(-79.33, 63.66) * mm});
            skLineSegment(sketch, "E2996", {"start": v(-79.33, 63.66) * mm, "end": v(-79.3, 63.63) * mm});
            skLineSegment(sketch, "E2997", {"start": v(-79.28, 63.6) * mm, "end": v(-79.25, 63.56) * mm});
            skLineSegment(sketch, "E2998", {"start": v(-78.99, 63.34) * mm, "end": v(-78.95, 63.32) * mm});
            skLineSegment(sketch, "E2999", {"start": v(-78.95, 63.32) * mm, "end": v(-78.91, 63.3) * mm});
            skLineSegment(sketch, "E3000", {"start": v(-78.91, 63.3) * mm, "end": v(-78.87, 63.28) * mm});
            skLineSegment(sketch, "E3001", {"start": v(-78.87, 63.28) * mm, "end": v(-78.83, 63.26) * mm});
            skLineSegment(sketch, "E3002", {"start": v(-78.83, 63.26) * mm, "end": v(-78.8, 63.24) * mm});
            skLineSegment(sketch, "E3003", {"start": v(-78.8, 63.24) * mm, "end": v(-78.75, 63.23) * mm});
            skLineSegment(sketch, "E3004", {"start": v(-78.75, 63.23) * mm, "end": v(-78.71, 63.21) * mm});
            skLineSegment(sketch, "E3005", {"start": v(-78.71, 63.21) * mm, "end": v(-78.67, 63.2) * mm});
            skLineSegment(sketch, "E3006", {"start": v(-78.67, 63.2) * mm, "end": v(-78.63, 63.19) * mm});
            skLineSegment(sketch, "E3007", {"start": v(-78.63, 63.19) * mm, "end": v(-78.59, 63.18) * mm});
            skLineSegment(sketch, "E3008", {"start": v(-78.59, 63.18) * mm, "end": v(-78.54, 63.17) * mm});
            skLineSegment(sketch, "E3009", {"start": v(-78.54, 63.17) * mm, "end": v(-78.5, 63.16) * mm});
            skLineSegment(sketch, "E3010", {"start": v(-78.5, 63.16) * mm, "end": v(-78.46, 63.16) * mm});
            skLineSegment(sketch, "E3011", {"start": v(-78.46, 63.16) * mm, "end": v(-78.41, 63.16) * mm});
            skLineSegment(sketch, "E3012", {"start": v(-78.41, 63.16) * mm, "end": v(-78.37, 63.15) * mm});
            skLineSegment(sketch, "E3013", {"start": v(-78.37, 63.15) * mm, "end": v(-78.33, 63.15) * mm});
            skLineSegment(sketch, "E3014", {"start": v(44.17, 63.15) * mm, "end": v(44.22, 63.15) * mm});
            skLineSegment(sketch, "E3015", {"start": v(44.26, 63.16) * mm, "end": v(44.3, 63.16) * mm});
            skLineSegment(sketch, "E3016", {"start": v(44.3, 63.16) * mm, "end": v(44.35, 63.16) * mm});
            skLineSegment(sketch, "E3017", {"start": v(44.35, 63.16) * mm, "end": v(44.39, 63.17) * mm});
            skLineSegment(sketch, "E3018", {"start": v(44.68, 63.26) * mm, "end": v(44.72, 63.28) * mm});
            skLineSegment(sketch, "E3019", {"start": v(44.72, 63.28) * mm, "end": v(44.76, 63.3) * mm});
            skLineSegment(sketch, "E3020", {"start": v(44.76, 63.3) * mm, "end": v(44.8, 63.32) * mm});
            skLineSegment(sketch, "E3021", {"start": v(44.8, 63.32) * mm, "end": v(44.83, 63.34) * mm});
            skLineSegment(sketch, "E3022", {"start": v(44.83, 63.34) * mm, "end": v(44.87, 63.36) * mm});
            skLineSegment(sketch, "E3023", {"start": v(44.87, 63.36) * mm, "end": v(44.9, 63.39) * mm});
            skLineSegment(sketch, "E3024", {"start": v(44.9, 63.39) * mm, "end": v(44.94, 63.41) * mm});
            skLineSegment(sketch, "E3025", {"start": v(44.94, 63.41) * mm, "end": v(44.97, 63.44) * mm});
            skLineSegment(sketch, "E3026", {"start": v(44.97, 63.44) * mm, "end": v(45, 63.47) * mm});
            skLineSegment(sketch, "E3027", {"start": v(45, 63.47) * mm, "end": v(45.04, 63.5) * mm});
            skLineSegment(sketch, "E3028", {"start": v(45.04, 63.5) * mm, "end": v(45.07, 63.53) * mm});
            skLineSegment(sketch, "E3029", {"start": v(45.1, 63.56) * mm, "end": v(45.13, 63.6) * mm});
            skLineSegment(sketch, "E3030", {"start": v(45.13, 63.6) * mm, "end": v(45.15, 63.63) * mm});
            skLineSegment(sketch, "E3031", {"start": v(45.15, 63.63) * mm, "end": v(45.18, 63.66) * mm});
            skLineSegment(sketch, "E3032", {"start": v(45.18, 63.66) * mm, "end": v(45.2, 63.7) * mm});
            skLineSegment(sketch, "E3033", {"start": v(45.2, 63.7) * mm, "end": v(45.23, 63.73) * mm});
            skLineSegment(sketch, "E3034", {"start": v(45.25, 63.77) * mm, "end": v(45.27, 63.8) * mm});
            skLineSegment(sketch, "E3035", {"start": v(45.27, 63.8) * mm, "end": v(45.3, 63.85) * mm});
            skLineSegment(sketch, "E3036", {"start": v(45.3, 63.85) * mm, "end": v(45.31, 63.89) * mm});
            skLineSegment(sketch, "E3037", {"start": v(45.31, 63.89) * mm, "end": v(45.33, 63.93) * mm});
            skLineSegment(sketch, "E3038", {"start": v(45.33, 63.93) * mm, "end": v(45.34, 63.97) * mm});
            skLineSegment(sketch, "E3039", {"start": v(45.34, 63.97) * mm, "end": v(45.36, 64) * mm});
            skLineSegment(sketch, "E3040", {"start": v(45.36, 64) * mm, "end": v(45.37, 64.05) * mm});
            skLineSegment(sketch, "E3041", {"start": v(45.37, 64.05) * mm, "end": v(45.38, 64.1) * mm});
            skLineSegment(sketch, "E3042", {"start": v(45.38, 64.1) * mm, "end": v(45.4, 64.13) * mm});
            skLineSegment(sketch, "E3043", {"start": v(45.4, 64.13) * mm, "end": v(45.4, 64.18) * mm});
            skLineSegment(sketch, "E3044", {"start": v(45.4, 64.65) * mm, "end": v(45.39, 64.7) * mm});
            skLineSegment(sketch, "E3045", {"start": v(45.39, 64.7) * mm, "end": v(45.38, 64.73) * mm});
            skLineSegment(sketch, "E3046", {"start": v(45.38, 64.73) * mm, "end": v(45.37, 64.78) * mm});
            skLineSegment(sketch, "E3047", {"start": v(45.37, 64.78) * mm, "end": v(45.35, 64.82) * mm});
            skLineSegment(sketch, "E3048", {"start": v(45.34, 64.86) * mm, "end": v(45.32, 64.9) * mm});
            skLineSegment(sketch, "E3049", {"start": v(45.32, 64.9) * mm, "end": v(45.3, 64.94) * mm});
            skLineSegment(sketch, "E3050", {"start": v(45.3, 64.94) * mm, "end": v(45.28, 64.98) * mm});
            skLineSegment(sketch, "E3051", {"start": v(45.28, 64.98) * mm, "end": v(45.26, 65.02) * mm});
            skLineSegment(sketch, "E3052", {"start": v(45.26, 65.02) * mm, "end": v(45.24, 65.05) * mm});
            skLineSegment(sketch, "E3053", {"start": v(45.24, 65.05) * mm, "end": v(45.22, 65.09) * mm});
            skLineSegment(sketch, "E3054", {"start": v(45.22, 65.09) * mm, "end": v(45.2, 65.13) * mm});
            skLineSegment(sketch, "E3055", {"start": v(45.2, 65.13) * mm, "end": v(45.17, 65.16) * mm});
            skLineSegment(sketch, "E3056", {"start": v(45.17, 65.16) * mm, "end": v(45.14, 65.2) * mm});
            skLineSegment(sketch, "E3057", {"start": v(45.14, 65.2) * mm, "end": v(45.11, 65.23) * mm});
            skLineSegment(sketch, "E3058", {"start": v(45.11, 65.23) * mm, "end": v(45.08, 65.26) * mm});
            skLineSegment(sketch, "E3059", {"start": v(45.08, 65.26) * mm, "end": v(45.05, 65.3) * mm});
            skLineSegment(sketch, "E3060", {"start": v(45.05, 65.3) * mm, "end": v(45.02, 65.32) * mm});
            skLineSegment(sketch, "E3061", {"start": v(45.02, 65.32) * mm, "end": v(44.99, 65.35) * mm});
            skLineSegment(sketch, "E3062", {"start": v(44.99, 65.35) * mm, "end": v(44.96, 65.38) * mm});
            skLineSegment(sketch, "E3063", {"start": v(44.96, 65.38) * mm, "end": v(44.92, 65.4) * mm});
            skLineSegment(sketch, "E3064", {"start": v(44.92, 65.4) * mm, "end": v(44.89, 65.43) * mm});
            skLineSegment(sketch, "E3065", {"start": v(44.89, 65.43) * mm, "end": v(44.85, 65.45) * mm});
            skLineSegment(sketch, "E3066", {"start": v(44.85, 65.45) * mm, "end": v(44.81, 65.48) * mm});
            skLineSegment(sketch, "E3067", {"start": v(44.81, 65.48) * mm, "end": v(44.78, 65.5) * mm});
            skLineSegment(sketch, "E3068", {"start": v(44.78, 65.5) * mm, "end": v(44.74, 65.52) * mm});
            skLineSegment(sketch, "E3069", {"start": v(44.74, 65.52) * mm, "end": v(44.7, 65.54) * mm});
            skLineSegment(sketch, "E3070", {"start": v(44.7, 65.54) * mm, "end": v(44.66, 65.55) * mm});
            skLineSegment(sketch, "E3071", {"start": v(44.66, 65.55) * mm, "end": v(44.62, 65.57) * mm});
            skLineSegment(sketch, "E3072", {"start": v(44.62, 65.57) * mm, "end": v(44.58, 65.59) * mm});
            skLineSegment(sketch, "E3073", {"start": v(44.54, 65.6) * mm, "end": v(44.5, 65.61) * mm});
            skLineSegment(sketch, "E3074", {"start": v(44.5, 65.61) * mm, "end": v(44.45, 65.62) * mm});
            skLineSegment(sketch, "E3075", {"start": v(44.45, 65.62) * mm, "end": v(44.4, 65.63) * mm});
            skLineSegment(sketch, "E3076", {"start": v(44.4, 65.63) * mm, "end": v(44.37, 65.64) * mm});
            skLineSegment(sketch, "E3077", {"start": v(44.37, 65.64) * mm, "end": v(44.32, 65.64) * mm});
            skLineSegment(sketch, "E3078", {"start": v(44.24, 65.65) * mm, "end": v(44.2, 65.65) * mm});
            skLineSegment(sketch, "E3079", {"start": v(44.2, 65.65) * mm, "end": v(44.15, 65.65) * mm});
            skLineSegment(sketch, "E3080", {"start": v(44.15, 65.65) * mm, "end": v(44.1, 65.65) * mm});
            skLineSegment(sketch, "E3081", {"start": v(44.1, 65.65) * mm, "end": v(44.06, 65.65) * mm});
            skLineSegment(sketch, "E3082", {"start": v(44.06, 65.65) * mm, "end": v(44.02, 65.64) * mm});
            skLineSegment(sketch, "E3083", {"start": v(44.02, 65.64) * mm, "end": v(43.98, 65.64) * mm});
            skLineSegment(sketch, "E3084", {"start": v(43.98, 65.64) * mm, "end": v(43.94, 65.63) * mm});
            skLineSegment(sketch, "E3085", {"start": v(43.6, 65.52) * mm, "end": v(43.57, 65.5) * mm});
            skLineSegment(sketch, "E3086", {"start": v(43.57, 65.5) * mm, "end": v(43.53, 65.48) * mm});
            skLineSegment(sketch, "E3087", {"start": v(43.53, 65.48) * mm, "end": v(43.5, 65.45) * mm});
            skLineSegment(sketch, "E3088", {"start": v(43.46, 65.43) * mm, "end": v(43.42, 65.4) * mm});
            skLineSegment(sketch, "E3089", {"start": v(43.42, 65.4) * mm, "end": v(43.39, 65.38) * mm});
            skLineSegment(sketch, "E3090", {"start": v(43.39, 65.38) * mm, "end": v(43.36, 65.35) * mm});
            skLineSegment(sketch, "E3091", {"start": v(43.36, 65.35) * mm, "end": v(43.32, 65.32) * mm});
            skLineSegment(sketch, "E3092", {"start": v(43.3, 65.3) * mm, "end": v(43.26, 65.26) * mm});
            skLineSegment(sketch, "E3093", {"start": v(43.26, 65.26) * mm, "end": v(43.23, 65.23) * mm});
            skLineSegment(sketch, "E3094", {"start": v(43.23, 65.23) * mm, "end": v(43.2, 65.2) * mm});
            skLineSegment(sketch, "E3095", {"start": v(43.2, 65.2) * mm, "end": v(43.18, 65.16) * mm});
            skLineSegment(sketch, "E3096", {"start": v(43.18, 65.16) * mm, "end": v(43.15, 65.13) * mm});
            skLineSegment(sketch, "E3097", {"start": v(43.15, 65.13) * mm, "end": v(43.13, 65.09) * mm});
            skLineSegment(sketch, "E3098", {"start": v(43.13, 65.09) * mm, "end": v(43.1, 65.05) * mm});
            skLineSegment(sketch, "E3099", {"start": v(43.1, 65.05) * mm, "end": v(43.08, 65.02) * mm});
            skLineSegment(sketch, "E3100", {"start": v(43.08, 65.02) * mm, "end": v(43.06, 64.98) * mm});
            skLineSegment(sketch, "E3101", {"start": v(43.06, 64.98) * mm, "end": v(43.04, 64.94) * mm});
            skLineSegment(sketch, "E3102", {"start": v(43.04, 64.94) * mm, "end": v(43.03, 64.9) * mm});
            skLineSegment(sketch, "E3103", {"start": v(43.03, 64.9) * mm, "end": v(43, 64.86) * mm});
            skLineSegment(sketch, "E3104", {"start": v(43, 64.86) * mm, "end": v(43, 64.82) * mm});
            skLineSegment(sketch, "E3105", {"start": v(43, 64.82) * mm, "end": v(42.98, 64.78) * mm});
            skLineSegment(sketch, "E3106", {"start": v(42.98, 64.78) * mm, "end": v(42.97, 64.73) * mm});
            skLineSegment(sketch, "E3107", {"start": v(42.97, 64.73) * mm, "end": v(42.96, 64.7) * mm});
            skLineSegment(sketch, "E3108", {"start": v(42.96, 64.7) * mm, "end": v(42.95, 64.65) * mm});
            skLineSegment(sketch, "E3109", {"start": v(42.95, 64.65) * mm, "end": v(42.94, 64.6) * mm});
            skLineSegment(sketch, "E3110", {"start": v(42.94, 64.6) * mm, "end": v(42.93, 64.56) * mm});
            skLineSegment(sketch, "E3111", {"start": v(42.93, 64.56) * mm, "end": v(42.93, 64.52) * mm});
            skLineSegment(sketch, "E3112", {"start": v(42.93, 64.52) * mm, "end": v(42.92, 64.48) * mm});
            skLineSegment(sketch, "E3113", {"start": v(42.92, 64.48) * mm, "end": v(42.92, 64.44) * mm});
            skLineSegment(sketch, "E3114", {"start": v(42.92, 64.4) * mm, "end": v(42.92, 64.35) * mm});
            skLineSegment(sketch, "E3115", {"start": v(42.92, 64.35) * mm, "end": v(42.93, 64.3) * mm});
            skLineSegment(sketch, "E3116", {"start": v(42.93, 64.3) * mm, "end": v(42.93, 64.26) * mm});
            skLineSegment(sketch, "E3117", {"start": v(42.93, 64.26) * mm, "end": v(42.94, 64.22) * mm});
            skLineSegment(sketch, "E3118", {"start": v(42.94, 64.22) * mm, "end": v(42.94, 64.18) * mm});
            skLineSegment(sketch, "E3119", {"start": v(42.94, 64.18) * mm, "end": v(42.95, 64.13) * mm});
            skLineSegment(sketch, "E3120", {"start": v(42.95, 64.13) * mm, "end": v(42.96, 64.1) * mm});
            skLineSegment(sketch, "E3121", {"start": v(42.96, 64.1) * mm, "end": v(42.97, 64.05) * mm});
            skLineSegment(sketch, "E3122", {"start": v(42.97, 64.05) * mm, "end": v(42.99, 64) * mm});
            skLineSegment(sketch, "E3123", {"start": v(42.99, 64) * mm, "end": v(43, 63.97) * mm});
            skLineSegment(sketch, "E3124", {"start": v(43, 63.97) * mm, "end": v(43.02, 63.93) * mm});
            skLineSegment(sketch, "E3125", {"start": v(43.02, 63.93) * mm, "end": v(43.03, 63.89) * mm});
            skLineSegment(sketch, "E3126", {"start": v(43.03, 63.89) * mm, "end": v(43.05, 63.85) * mm});
            skLineSegment(sketch, "E3127", {"start": v(43.05, 63.85) * mm, "end": v(43.07, 63.8) * mm});
            skLineSegment(sketch, "E3128", {"start": v(43.07, 63.8) * mm, "end": v(43.1, 63.77) * mm});
            skLineSegment(sketch, "E3129", {"start": v(43.1, 63.77) * mm, "end": v(43.12, 63.73) * mm});
            skLineSegment(sketch, "E3130", {"start": v(43.12, 63.73) * mm, "end": v(43.14, 63.7) * mm});
            skLineSegment(sketch, "E3131", {"start": v(43.14, 63.7) * mm, "end": v(43.17, 63.66) * mm});
            skLineSegment(sketch, "E3132", {"start": v(43.17, 63.66) * mm, "end": v(43.2, 63.63) * mm});
            skLineSegment(sketch, "E3133", {"start": v(43.2, 63.63) * mm, "end": v(43.22, 63.6) * mm});
            skLineSegment(sketch, "E3134", {"start": v(43.22, 63.6) * mm, "end": v(43.25, 63.56) * mm});
            skLineSegment(sketch, "E3135", {"start": v(43.25, 63.56) * mm, "end": v(43.28, 63.53) * mm});
            skLineSegment(sketch, "E3136", {"start": v(43.28, 63.53) * mm, "end": v(43.3, 63.5) * mm});
            skLineSegment(sketch, "E3137", {"start": v(43.3, 63.5) * mm, "end": v(43.34, 63.47) * mm});
            skLineSegment(sketch, "E3138", {"start": v(43.34, 63.47) * mm, "end": v(43.37, 63.44) * mm});
            skLineSegment(sketch, "E3139", {"start": v(43.37, 63.44) * mm, "end": v(43.4, 63.41) * mm});
            skLineSegment(sketch, "E3140", {"start": v(43.4, 63.41) * mm, "end": v(43.44, 63.39) * mm});
            skLineSegment(sketch, "E3141", {"start": v(43.44, 63.39) * mm, "end": v(43.48, 63.36) * mm});
            skLineSegment(sketch, "E3142", {"start": v(43.48, 63.36) * mm, "end": v(43.51, 63.34) * mm});
            skLineSegment(sketch, "E3143", {"start": v(43.51, 63.34) * mm, "end": v(43.55, 63.32) * mm});
            skLineSegment(sketch, "E3144", {"start": v(43.55, 63.32) * mm, "end": v(43.59, 63.3) * mm});
            skLineSegment(sketch, "E3145", {"start": v(43.59, 63.3) * mm, "end": v(43.63, 63.28) * mm});
            skLineSegment(sketch, "E3146", {"start": v(43.63, 63.28) * mm, "end": v(43.67, 63.26) * mm});
            skLineSegment(sketch, "E3147", {"start": v(43.67, 63.26) * mm, "end": v(43.7, 63.24) * mm});
            skLineSegment(sketch, "E3148", {"start": v(43.7, 63.24) * mm, "end": v(43.75, 63.23) * mm});
            skLineSegment(sketch, "E3149", {"start": v(43.75, 63.23) * mm, "end": v(43.79, 63.21) * mm});
            skLineSegment(sketch, "E3150", {"start": v(43.79, 63.21) * mm, "end": v(43.83, 63.2) * mm});
            skLineSegment(sketch, "E3151", {"start": v(43.83, 63.2) * mm, "end": v(43.87, 63.19) * mm});
            skLineSegment(sketch, "E3152", {"start": v(43.87, 63.19) * mm, "end": v(43.91, 63.18) * mm});
            skLineSegment(sketch, "E3153", {"start": v(43.91, 63.18) * mm, "end": v(43.96, 63.17) * mm});
            skLineSegment(sketch, "E3154", {"start": v(43.96, 63.17) * mm, "end": v(44, 63.16) * mm});
            skLineSegment(sketch, "E3155", {"start": v(44, 63.16) * mm, "end": v(44.04, 63.16) * mm});
            skLineSegment(sketch, "E3156", {"start": v(44.09, 63.16) * mm, "end": v(44.13, 63.15) * mm});
            skLineSegment(sketch, "E3157", {"start": v(-4.58, 40.65) * mm, "end": v(-4.53, 40.65) * mm});
            skLineSegment(sketch, "E3158", {"start": v(-4.53, 40.65) * mm, "end": v(-4.5, 40.66) * mm});
            skLineSegment(sketch, "E3159", {"start": v(-4.5, 40.66) * mm, "end": v(-4.45, 40.66) * mm});
            skLineSegment(sketch, "E3160", {"start": v(-4.45, 40.66) * mm, "end": v(-4.4, 40.66) * mm});
            skLineSegment(sketch, "E3161", {"start": v(-4.32, 40.68) * mm, "end": v(-4.28, 40.69) * mm});
            skLineSegment(sketch, "E3162", {"start": v(-4.28, 40.69) * mm, "end": v(-4.23, 40.7) * mm});
            skLineSegment(sketch, "E3163", {"start": v(-4.23, 40.7) * mm, "end": v(-4.2, 40.71) * mm});
            skLineSegment(sketch, "E3164", {"start": v(-4.2, 40.71) * mm, "end": v(-4.15, 40.73) * mm});
            skLineSegment(sketch, "E3165", {"start": v(-4.15, 40.73) * mm, "end": v(-4.11, 40.74) * mm});
            skLineSegment(sketch, "E3166", {"start": v(-4.11, 40.74) * mm, "end": v(-4.07, 40.76) * mm});
            skLineSegment(sketch, "E3167", {"start": v(-4.07, 40.76) * mm, "end": v(-4.03, 40.78) * mm});
            skLineSegment(sketch, "E3168", {"start": v(-4.03, 40.78) * mm, "end": v(-4, 40.8) * mm});
            skLineSegment(sketch, "E3169", {"start": v(-3.85, 40.89) * mm, "end": v(-3.81, 40.91) * mm});
            skLineSegment(sketch, "E3170", {"start": v(-3.81, 40.91) * mm, "end": v(-3.78, 40.94) * mm});
            skLineSegment(sketch, "E3171", {"start": v(-3.78, 40.94) * mm, "end": v(-3.74, 40.97) * mm});
            skLineSegment(sketch, "E3172", {"start": v(-3.74, 40.97) * mm, "end": v(-3.71, 41) * mm});
            skLineSegment(sketch, "E3173", {"start": v(-3.71, 41) * mm, "end": v(-3.68, 41.03) * mm});
            skLineSegment(sketch, "E3174", {"start": v(-3.68, 41.03) * mm, "end": v(-3.65, 41.06) * mm});
            skLineSegment(sketch, "E3175", {"start": v(-3.65, 41.06) * mm, "end": v(-3.62, 41.1) * mm});
            skLineSegment(sketch, "E3176", {"start": v(-3.62, 41.1) * mm, "end": v(-3.6, 41.13) * mm});
            skLineSegment(sketch, "E3177", {"start": v(-3.44, 41.39) * mm, "end": v(-3.42, 41.43) * mm});
            skLineSegment(sketch, "E3178", {"start": v(-3.42, 41.43) * mm, "end": v(-3.4, 41.47) * mm});
            skLineSegment(sketch, "E3179", {"start": v(-3.4, 41.47) * mm, "end": v(-3.4, 41.5) * mm});
            skLineSegment(sketch, "E3180", {"start": v(-3.4, 41.5) * mm, "end": v(-3.38, 41.55) * mm});
            skLineSegment(sketch, "E3181", {"start": v(-3.38, 41.55) * mm, "end": v(-3.37, 41.6) * mm});
            skLineSegment(sketch, "E3182", {"start": v(-3.37, 41.6) * mm, "end": v(-3.36, 41.63) * mm});
            skLineSegment(sketch, "E3183", {"start": v(-3.35, 41.68) * mm, "end": v(-3.34, 41.72) * mm});
            skLineSegment(sketch, "E3184", {"start": v(-3.34, 41.72) * mm, "end": v(-3.34, 41.76) * mm});
            skLineSegment(sketch, "E3185", {"start": v(-3.34, 41.76) * mm, "end": v(-3.33, 41.8) * mm});
            skLineSegment(sketch, "E3186", {"start": v(-3.33, 41.8) * mm, "end": v(-3.33, 41.85) * mm});
            skLineSegment(sketch, "E3187", {"start": v(-3.33, 41.85) * mm, "end": v(-3.33, 41.9) * mm});
            skLineSegment(sketch, "E3188", {"start": v(-3.33, 41.9) * mm, "end": v(-3.33, 41.94) * mm});
            skLineSegment(sketch, "E3189", {"start": v(-3.33, 41.94) * mm, "end": v(-3.33, 41.98) * mm});
            skLineSegment(sketch, "E3190", {"start": v(-3.33, 41.98) * mm, "end": v(-3.33, 42.02) * mm});
            skLineSegment(sketch, "E3191", {"start": v(-3.33, 42.02) * mm, "end": v(-3.34, 42.06) * mm});
            skLineSegment(sketch, "E3192", {"start": v(-3.34, 42.06) * mm, "end": v(-3.34, 42.1) * mm});
            skLineSegment(sketch, "E3193", {"start": v(-3.34, 42.1) * mm, "end": v(-3.35, 42.15) * mm});
            skLineSegment(sketch, "E3194", {"start": v(-3.35, 42.15) * mm, "end": v(-3.36, 42.2) * mm});
            skLineSegment(sketch, "E3195", {"start": v(-3.36, 42.2) * mm, "end": v(-3.37, 42.23) * mm});
            skLineSegment(sketch, "E3196", {"start": v(-3.37, 42.23) * mm, "end": v(-3.38, 42.28) * mm});
            skLineSegment(sketch, "E3197", {"start": v(-3.38, 42.28) * mm, "end": v(-3.4, 42.32) * mm});
            skLineSegment(sketch, "E3198", {"start": v(-3.4, 42.32) * mm, "end": v(-3.41, 42.36) * mm});
            skLineSegment(sketch, "E3199", {"start": v(-3.41, 42.36) * mm, "end": v(-3.43, 42.4) * mm});
            skLineSegment(sketch, "E3200", {"start": v(-3.43, 42.4) * mm, "end": v(-3.45, 42.44) * mm});
            skLineSegment(sketch, "E3201", {"start": v(-3.45, 42.44) * mm, "end": v(-3.47, 42.48) * mm});
            skLineSegment(sketch, "E3202", {"start": v(-3.47, 42.48) * mm, "end": v(-3.49, 42.52) * mm});
            skLineSegment(sketch, "E3203", {"start": v(-3.49, 42.52) * mm, "end": v(-3.5, 42.55) * mm});
            skLineSegment(sketch, "E3204", {"start": v(-3.5, 42.55) * mm, "end": v(-3.53, 42.59) * mm});
            skLineSegment(sketch, "E3205", {"start": v(-3.53, 42.59) * mm, "end": v(-3.56, 42.63) * mm});
            skLineSegment(sketch, "E3206", {"start": v(-3.56, 42.63) * mm, "end": v(-3.58, 42.66) * mm});
            skLineSegment(sketch, "E3207", {"start": v(-3.58, 42.66) * mm, "end": v(-3.6, 42.7) * mm});
            skLineSegment(sketch, "E3208", {"start": v(-3.6, 42.7) * mm, "end": v(-3.64, 42.73) * mm});
            skLineSegment(sketch, "E3209", {"start": v(-3.64, 42.73) * mm, "end": v(-3.67, 42.76) * mm});
            skLineSegment(sketch, "E3210", {"start": v(-3.67, 42.76) * mm, "end": v(-3.7, 42.8) * mm});
            skLineSegment(sketch, "E3211", {"start": v(-3.7, 42.8) * mm, "end": v(-3.73, 42.82) * mm});
            skLineSegment(sketch, "E3212", {"start": v(-3.73, 42.82) * mm, "end": v(-3.76, 42.85) * mm});
            skLineSegment(sketch, "E3213", {"start": v(-3.76, 42.85) * mm, "end": v(-3.8, 42.88) * mm});
            skLineSegment(sketch, "E3214", {"start": v(-3.8, 42.88) * mm, "end": v(-3.83, 42.9) * mm});
            skLineSegment(sketch, "E3215", {"start": v(-3.83, 42.9) * mm, "end": v(-3.86, 42.93) * mm});
            skLineSegment(sketch, "E3216", {"start": v(-3.86, 42.93) * mm, "end": v(-3.9, 42.95) * mm});
            skLineSegment(sketch, "E3217", {"start": v(-4.01, 43.02) * mm, "end": v(-4.05, 43.04) * mm});
            skLineSegment(sketch, "E3218", {"start": v(-4.05, 43.04) * mm, "end": v(-4.1, 43.05) * mm});
            skLineSegment(sketch, "E3219", {"start": v(-4.1, 43.05) * mm, "end": v(-4.13, 43.07) * mm});
            skLineSegment(sketch, "E3220", {"start": v(-4.13, 43.07) * mm, "end": v(-4.17, 43.09) * mm});
            skLineSegment(sketch, "E3221", {"start": v(-4.17, 43.09) * mm, "end": v(-4.21, 43.1) * mm});
            skLineSegment(sketch, "E3222", {"start": v(-4.21, 43.1) * mm, "end": v(-4.26, 43.11) * mm});
            skLineSegment(sketch, "E3223", {"start": v(-4.26, 43.11) * mm, "end": v(-4.3, 43.12) * mm});
            skLineSegment(sketch, "E3224", {"start": v(-4.3, 43.12) * mm, "end": v(-4.34, 43.13) * mm});
            skLineSegment(sketch, "E3225", {"start": v(-4.34, 43.13) * mm, "end": v(-4.38, 43.14) * mm});
            skLineSegment(sketch, "E3226", {"start": v(-4.38, 43.14) * mm, "end": v(-4.43, 43.14) * mm});
            skLineSegment(sketch, "E3227", {"start": v(-4.43, 43.14) * mm, "end": v(-4.47, 43.15) * mm});
            skLineSegment(sketch, "E3228", {"start": v(-4.47, 43.15) * mm, "end": v(-4.51, 43.15) * mm});
            skLineSegment(sketch, "E3229", {"start": v(-4.51, 43.15) * mm, "end": v(-4.56, 43.15) * mm});
            skLineSegment(sketch, "E3230", {"start": v(-4.56, 43.15) * mm, "end": v(-4.6, 43.15) * mm});
            skLineSegment(sketch, "E3231", {"start": v(-4.6, 43.15) * mm, "end": v(-4.64, 43.15) * mm});
            skLineSegment(sketch, "E3232", {"start": v(-4.64, 43.15) * mm, "end": v(-4.69, 43.15) * mm});
            skLineSegment(sketch, "E3233", {"start": v(-4.69, 43.15) * mm, "end": v(-4.73, 43.14) * mm});
            skLineSegment(sketch, "E3234", {"start": v(-4.81, 43.13) * mm, "end": v(-4.86, 43.12) * mm});
            skLineSegment(sketch, "E3235", {"start": v(-4.86, 43.12) * mm, "end": v(-4.9, 43.11) * mm});
            skLineSegment(sketch, "E3236", {"start": v(-4.9, 43.11) * mm, "end": v(-4.94, 43.1) * mm});
            skLineSegment(sketch, "E3237", {"start": v(-4.94, 43.1) * mm, "end": v(-4.98, 43.09) * mm});
            skLineSegment(sketch, "E3238", {"start": v(-4.98, 43.09) * mm, "end": v(-5.02, 43.07) * mm});
            skLineSegment(sketch, "E3239", {"start": v(-5.02, 43.07) * mm, "end": v(-5.06, 43.05) * mm});
            skLineSegment(sketch, "E3240", {"start": v(-5.06, 43.05) * mm, "end": v(-5.1, 43.04) * mm});
            skLineSegment(sketch, "E3241", {"start": v(-5.1, 43.04) * mm, "end": v(-5.14, 43.02) * mm});
            skLineSegment(sketch, "E3242", {"start": v(-5.14, 43.02) * mm, "end": v(-5.18, 43) * mm});
            skLineSegment(sketch, "E3243", {"start": v(-5.18, 43) * mm, "end": v(-5.22, 42.98) * mm});
            skLineSegment(sketch, "E3244", {"start": v(-5.22, 42.98) * mm, "end": v(-5.25, 42.95) * mm});
            skLineSegment(sketch, "E3245", {"start": v(-5.25, 42.95) * mm, "end": v(-5.3, 42.93) * mm});
            skLineSegment(sketch, "E3246", {"start": v(-5.3, 42.93) * mm, "end": v(-5.33, 42.9) * mm});
            skLineSegment(sketch, "E3247", {"start": v(-5.33, 42.9) * mm, "end": v(-5.36, 42.88) * mm});
            skLineSegment(sketch, "E3248", {"start": v(-5.36, 42.88) * mm, "end": v(-5.4, 42.85) * mm});
            skLineSegment(sketch, "E3249", {"start": v(-5.4, 42.85) * mm, "end": v(-5.43, 42.82) * mm});
            skLineSegment(sketch, "E3250", {"start": v(-5.43, 42.82) * mm, "end": v(-5.46, 42.8) * mm});
            skLineSegment(sketch, "E3251", {"start": v(-5.46, 42.8) * mm, "end": v(-5.49, 42.76) * mm});
            skLineSegment(sketch, "E3252", {"start": v(-5.49, 42.76) * mm, "end": v(-5.52, 42.73) * mm});
            skLineSegment(sketch, "E3253", {"start": v(-5.52, 42.73) * mm, "end": v(-5.54, 42.7) * mm});
            skLineSegment(sketch, "E3254", {"start": v(-5.54, 42.7) * mm, "end": v(-5.57, 42.66) * mm});
            skLineSegment(sketch, "E3255", {"start": v(-5.6, 42.63) * mm, "end": v(-5.62, 42.59) * mm});
            skLineSegment(sketch, "E3256", {"start": v(-5.62, 42.59) * mm, "end": v(-5.65, 42.55) * mm});
            skLineSegment(sketch, "E3257", {"start": v(-5.65, 42.55) * mm, "end": v(-5.67, 42.52) * mm});
            skLineSegment(sketch, "E3258", {"start": v(-5.67, 42.52) * mm, "end": v(-5.69, 42.48) * mm});
            skLineSegment(sketch, "E3259", {"start": v(-5.69, 42.48) * mm, "end": v(-5.7, 42.44) * mm});
            skLineSegment(sketch, "E3260", {"start": v(-5.7, 42.44) * mm, "end": v(-5.72, 42.4) * mm});
            skLineSegment(sketch, "E3261", {"start": v(-5.72, 42.4) * mm, "end": v(-5.74, 42.36) * mm});
            skLineSegment(sketch, "E3262", {"start": v(-5.74, 42.36) * mm, "end": v(-5.76, 42.32) * mm});
            skLineSegment(sketch, "E3263", {"start": v(-5.76, 42.32) * mm, "end": v(-5.77, 42.28) * mm});
            skLineSegment(sketch, "E3264", {"start": v(-5.77, 42.28) * mm, "end": v(-5.78, 42.23) * mm});
            skLineSegment(sketch, "E3265", {"start": v(-5.78, 42.23) * mm, "end": v(-5.8, 42.2) * mm});
            skLineSegment(sketch, "E3266", {"start": v(-5.8, 42.2) * mm, "end": v(-5.8, 42.15) * mm});
            skLineSegment(sketch, "E3267", {"start": v(-5.8, 42.15) * mm, "end": v(-5.81, 42.1) * mm});
            skLineSegment(sketch, "E3268", {"start": v(-5.81, 42.1) * mm, "end": v(-5.82, 42.06) * mm});
            skLineSegment(sketch, "E3269", {"start": v(-5.82, 42.06) * mm, "end": v(-5.82, 42.02) * mm});
            skLineSegment(sketch, "E3270", {"start": v(-5.82, 42.02) * mm, "end": v(-5.83, 41.98) * mm});
            skLineSegment(sketch, "E3271", {"start": v(-5.83, 41.98) * mm, "end": v(-5.83, 41.94) * mm});
            skLineSegment(sketch, "E3272", {"start": v(-5.83, 41.94) * mm, "end": v(-5.83, 41.9) * mm});
            skLineSegment(sketch, "E3273", {"start": v(-5.83, 41.9) * mm, "end": v(-5.83, 41.85) * mm});
            skLineSegment(sketch, "E3274", {"start": v(-5.83, 41.85) * mm, "end": v(-5.82, 41.8) * mm});
            skLineSegment(sketch, "E3275", {"start": v(-5.82, 41.8) * mm, "end": v(-5.82, 41.76) * mm});
            skLineSegment(sketch, "E3276", {"start": v(-5.82, 41.76) * mm, "end": v(-5.81, 41.72) * mm});
            skLineSegment(sketch, "E3277", {"start": v(-5.81, 41.72) * mm, "end": v(-5.8, 41.68) * mm});
            skLineSegment(sketch, "E3278", {"start": v(-5.8, 41.68) * mm, "end": v(-5.8, 41.63) * mm});
            skLineSegment(sketch, "E3279", {"start": v(-5.8, 41.63) * mm, "end": v(-5.79, 41.6) * mm});
            skLineSegment(sketch, "E3280", {"start": v(-5.79, 41.6) * mm, "end": v(-5.78, 41.55) * mm});
            skLineSegment(sketch, "E3281", {"start": v(-5.78, 41.55) * mm, "end": v(-5.76, 41.5) * mm});
            skLineSegment(sketch, "E3282", {"start": v(-5.76, 41.5) * mm, "end": v(-5.75, 41.47) * mm});
            skLineSegment(sketch, "E3283", {"start": v(-5.75, 41.47) * mm, "end": v(-5.73, 41.43) * mm});
            skLineSegment(sketch, "E3284", {"start": v(-5.72, 41.39) * mm, "end": v(-5.7, 41.35) * mm});
            skLineSegment(sketch, "E3285", {"start": v(-5.7, 41.35) * mm, "end": v(-5.68, 41.3) * mm});
            skLineSegment(sketch, "E3286", {"start": v(-5.68, 41.3) * mm, "end": v(-5.66, 41.27) * mm});
            skLineSegment(sketch, "E3287", {"start": v(-5.66, 41.27) * mm, "end": v(-5.63, 41.23) * mm});
            skLineSegment(sketch, "E3288", {"start": v(-5.63, 41.23) * mm, "end": v(-5.6, 41.2) * mm});
            skLineSegment(sketch, "E3289", {"start": v(-5.58, 41.16) * mm, "end": v(-5.56, 41.13) * mm});
            skLineSegment(sketch, "E3290", {"start": v(-5.56, 41.13) * mm, "end": v(-5.53, 41.1) * mm});
            skLineSegment(sketch, "E3291", {"start": v(-5.53, 41.1) * mm, "end": v(-5.5, 41.06) * mm});
            skLineSegment(sketch, "E3292", {"start": v(-5.5, 41.06) * mm, "end": v(-5.47, 41.03) * mm});
            skLineSegment(sketch, "E3293", {"start": v(-5.47, 41.03) * mm, "end": v(-5.44, 41) * mm});
            skLineSegment(sketch, "E3294", {"start": v(-5.44, 41) * mm, "end": v(-5.41, 40.97) * mm});
            skLineSegment(sketch, "E3295", {"start": v(-5.41, 40.97) * mm, "end": v(-5.38, 40.94) * mm});
            skLineSegment(sketch, "E3296", {"start": v(-5.38, 40.94) * mm, "end": v(-5.34, 40.91) * mm});
            skLineSegment(sketch, "E3297", {"start": v(-5.34, 40.91) * mm, "end": v(-5.3, 40.89) * mm});
            skLineSegment(sketch, "E3298", {"start": v(-5.3, 40.89) * mm, "end": v(-5.27, 40.86) * mm});
            skLineSegment(sketch, "E3299", {"start": v(-5.27, 40.86) * mm, "end": v(-5.24, 40.84) * mm});
            skLineSegment(sketch, "E3300", {"start": v(-5.24, 40.84) * mm, "end": v(-5.2, 40.82) * mm});
            skLineSegment(sketch, "E3301", {"start": v(-5.2, 40.82) * mm, "end": v(-5.16, 40.8) * mm});
            skLineSegment(sketch, "E3302", {"start": v(-5.16, 40.8) * mm, "end": v(-5.12, 40.78) * mm});
            skLineSegment(sketch, "E3303", {"start": v(-5.08, 40.76) * mm, "end": v(-5.04, 40.74) * mm});
            skLineSegment(sketch, "E3304", {"start": v(-5.04, 40.74) * mm, "end": v(-5, 40.73) * mm});
            skLineSegment(sketch, "E3305", {"start": v(-5, 40.73) * mm, "end": v(-4.96, 40.71) * mm});
            skLineSegment(sketch, "E3306", {"start": v(-4.96, 40.71) * mm, "end": v(-4.92, 40.7) * mm});
            skLineSegment(sketch, "E3307", {"start": v(-4.92, 40.7) * mm, "end": v(-4.88, 40.69) * mm});
            skLineSegment(sketch, "E3308", {"start": v(-4.88, 40.69) * mm, "end": v(-4.84, 40.68) * mm});
            skLineSegment(sketch, "E3309", {"start": v(-4.84, 40.68) * mm, "end": v(-4.8, 40.67) * mm});
            skLineSegment(sketch, "E3310", {"start": v(-4.8, 40.67) * mm, "end": v(-4.75, 40.66) * mm});
            skLineSegment(sketch, "E3311", {"start": v(-4.75, 40.66) * mm, "end": v(-4.7, 40.66) * mm});
            skLineSegment(sketch, "E3312", {"start": v(-4.7, 40.66) * mm, "end": v(-4.66, 40.66) * mm});
            skLineSegment(sketch, "E3313", {"start": v(-4.66, 40.66) * mm, "end": v(-4.62, 40.65) * mm});
            skLineSegment(sketch, "E3314", {"start": v(-4.62, 40.65) * mm, "end": v(-4.58, 40.65) * mm});
            skLineSegment(sketch, "E3315", {"start": v(-4.58, 63.15) * mm, "end": v(-4.53, 63.15) * mm});
            skLineSegment(sketch, "E3316", {"start": v(-4.53, 63.15) * mm, "end": v(-4.5, 63.16) * mm});
            skLineSegment(sketch, "E3317", {"start": v(-4.5, 63.16) * mm, "end": v(-4.45, 63.16) * mm});
            skLineSegment(sketch, "E3318", {"start": v(-4.45, 63.16) * mm, "end": v(-4.4, 63.16) * mm});
            skLineSegment(sketch, "E3319", {"start": v(-4.4, 63.16) * mm, "end": v(-4.36, 63.17) * mm});
            skLineSegment(sketch, "E3320", {"start": v(-4.36, 63.17) * mm, "end": v(-4.32, 63.18) * mm});
            skLineSegment(sketch, "E3321", {"start": v(-4.32, 63.18) * mm, "end": v(-4.28, 63.19) * mm});
            skLineSegment(sketch, "E3322", {"start": v(-4.28, 63.19) * mm, "end": v(-4.23, 63.2) * mm});
            skLineSegment(sketch, "E3323", {"start": v(-4.23, 63.2) * mm, "end": v(-4.2, 63.21) * mm});
            skLineSegment(sketch, "E3324", {"start": v(-4.15, 63.23) * mm, "end": v(-4.11, 63.24) * mm});
            skLineSegment(sketch, "E3325", {"start": v(-4.11, 63.24) * mm, "end": v(-4.07, 63.26) * mm});
            skLineSegment(sketch, "E3326", {"start": v(-4.07, 63.26) * mm, "end": v(-4.03, 63.28) * mm});
            skLineSegment(sketch, "E3327", {"start": v(-4.03, 63.28) * mm, "end": v(-4, 63.3) * mm});
            skLineSegment(sketch, "E3328", {"start": v(-4, 63.3) * mm, "end": v(-3.96, 63.32) * mm});
            skLineSegment(sketch, "E3329", {"start": v(-3.96, 63.32) * mm, "end": v(-3.92, 63.34) * mm});
            skLineSegment(sketch, "E3330", {"start": v(-3.92, 63.34) * mm, "end": v(-3.88, 63.36) * mm});
            skLineSegment(sketch, "E3331", {"start": v(-3.88, 63.36) * mm, "end": v(-3.85, 63.39) * mm});
            skLineSegment(sketch, "E3332", {"start": v(-3.85, 63.39) * mm, "end": v(-3.81, 63.41) * mm});
            skLineSegment(sketch, "E3333", {"start": v(-3.81, 63.41) * mm, "end": v(-3.78, 63.44) * mm});
            skLineSegment(sketch, "E3334", {"start": v(-3.78, 63.44) * mm, "end": v(-3.74, 63.47) * mm});
            skLineSegment(sketch, "E3335", {"start": v(-3.74, 63.47) * mm, "end": v(-3.71, 63.5) * mm});
            skLineSegment(sketch, "E3336", {"start": v(-3.71, 63.5) * mm, "end": v(-3.68, 63.53) * mm});
            skLineSegment(sketch, "E3337", {"start": v(-3.68, 63.53) * mm, "end": v(-3.65, 63.56) * mm});
            skLineSegment(sketch, "E3338", {"start": v(-3.65, 63.56) * mm, "end": v(-3.62, 63.6) * mm});
            skLineSegment(sketch, "E3339", {"start": v(-3.62, 63.6) * mm, "end": v(-3.6, 63.63) * mm});
            skLineSegment(sketch, "E3340", {"start": v(-3.6, 63.63) * mm, "end": v(-3.57, 63.66) * mm});
            skLineSegment(sketch, "E3341", {"start": v(-3.57, 63.66) * mm, "end": v(-3.54, 63.7) * mm});
            skLineSegment(sketch, "E3342", {"start": v(-3.54, 63.7) * mm, "end": v(-3.52, 63.73) * mm});
            skLineSegment(sketch, "E3343", {"start": v(-3.52, 63.73) * mm, "end": v(-3.5, 63.77) * mm});
            skLineSegment(sketch, "E3344", {"start": v(-3.5, 63.77) * mm, "end": v(-3.48, 63.8) * mm});
            skLineSegment(sketch, "E3345", {"start": v(-3.48, 63.8) * mm, "end": v(-3.46, 63.85) * mm});
            skLineSegment(sketch, "E3346", {"start": v(-3.46, 63.85) * mm, "end": v(-3.44, 63.89) * mm});
            skLineSegment(sketch, "E3347", {"start": v(-3.44, 63.89) * mm, "end": v(-3.42, 63.93) * mm});
            skLineSegment(sketch, "E3348", {"start": v(-3.42, 63.93) * mm, "end": v(-3.4, 63.97) * mm});
            skLineSegment(sketch, "E3349", {"start": v(-3.4, 63.97) * mm, "end": v(-3.4, 64) * mm});
            skLineSegment(sketch, "E3350", {"start": v(-3.4, 64) * mm, "end": v(-3.38, 64.05) * mm});
            skLineSegment(sketch, "E3351", {"start": v(-3.38, 64.05) * mm, "end": v(-3.37, 64.1) * mm});
            skLineSegment(sketch, "E3352", {"start": v(-3.37, 64.1) * mm, "end": v(-3.36, 64.13) * mm});
            skLineSegment(sketch, "E3353", {"start": v(-3.36, 64.13) * mm, "end": v(-3.35, 64.18) * mm});
            skLineSegment(sketch, "E3354", {"start": v(-3.35, 64.18) * mm, "end": v(-3.34, 64.22) * mm});
            skLineSegment(sketch, "E3355", {"start": v(-3.34, 64.22) * mm, "end": v(-3.34, 64.26) * mm});
            skLineSegment(sketch, "E3356", {"start": v(-3.37, 64.73) * mm, "end": v(-3.38, 64.78) * mm});
            skLineSegment(sketch, "E3357", {"start": v(-3.38, 64.78) * mm, "end": v(-3.4, 64.82) * mm});
            skLineSegment(sketch, "E3358", {"start": v(-3.4, 64.82) * mm, "end": v(-3.41, 64.86) * mm});
            skLineSegment(sketch, "E3359", {"start": v(-3.41, 64.86) * mm, "end": v(-3.43, 64.9) * mm});
            skLineSegment(sketch, "E3360", {"start": v(-3.43, 64.9) * mm, "end": v(-3.45, 64.94) * mm});
            skLineSegment(sketch, "E3361", {"start": v(-3.45, 64.94) * mm, "end": v(-3.47, 64.98) * mm});
            skLineSegment(sketch, "E3362", {"start": v(-3.47, 64.98) * mm, "end": v(-3.49, 65.02) * mm});
            skLineSegment(sketch, "E3363", {"start": v(-3.49, 65.02) * mm, "end": v(-3.5, 65.05) * mm});
            skLineSegment(sketch, "E3364", {"start": v(-3.5, 65.05) * mm, "end": v(-3.53, 65.09) * mm});
            skLineSegment(sketch, "E3365", {"start": v(-3.53, 65.09) * mm, "end": v(-3.56, 65.13) * mm});
            skLineSegment(sketch, "E3366", {"start": v(-3.56, 65.13) * mm, "end": v(-3.58, 65.16) * mm});
            skLineSegment(sketch, "E3367", {"start": v(-3.76, 65.35) * mm, "end": v(-3.8, 65.38) * mm});
            skLineSegment(sketch, "E3368", {"start": v(-3.8, 65.38) * mm, "end": v(-3.83, 65.4) * mm});
            skLineSegment(sketch, "E3369", {"start": v(-3.83, 65.4) * mm, "end": v(-3.86, 65.43) * mm});
            skLineSegment(sketch, "E3370", {"start": v(-3.86, 65.43) * mm, "end": v(-3.9, 65.45) * mm});
            skLineSegment(sketch, "E3371", {"start": v(-3.9, 65.45) * mm, "end": v(-3.94, 65.48) * mm});
            skLineSegment(sketch, "E3372", {"start": v(-3.94, 65.48) * mm, "end": v(-3.97, 65.5) * mm});
            skLineSegment(sketch, "E3373", {"start": v(-3.97, 65.5) * mm, "end": v(-4.01, 65.52) * mm});
            skLineSegment(sketch, "E3374", {"start": v(-4.01, 65.52) * mm, "end": v(-4.05, 65.54) * mm});
            skLineSegment(sketch, "E3375", {"start": v(-4.05, 65.54) * mm, "end": v(-4.1, 65.55) * mm});
            skLineSegment(sketch, "E3376", {"start": v(-4.1, 65.55) * mm, "end": v(-4.13, 65.57) * mm});
            skLineSegment(sketch, "E3377", {"start": v(-4.13, 65.57) * mm, "end": v(-4.17, 65.59) * mm});
            skLineSegment(sketch, "E3378", {"start": v(-4.17, 65.59) * mm, "end": v(-4.21, 65.6) * mm});
            skLineSegment(sketch, "E3379", {"start": v(-4.26, 65.61) * mm, "end": v(-4.3, 65.62) * mm});
            skLineSegment(sketch, "E3380", {"start": v(-4.3, 65.62) * mm, "end": v(-4.34, 65.63) * mm});
            skLineSegment(sketch, "E3381", {"start": v(-4.34, 65.63) * mm, "end": v(-4.38, 65.64) * mm});
            skLineSegment(sketch, "E3382", {"start": v(-4.38, 65.64) * mm, "end": v(-4.43, 65.64) * mm});
            skLineSegment(sketch, "E3383", {"start": v(-4.43, 65.64) * mm, "end": v(-4.47, 65.65) * mm});
            skLineSegment(sketch, "E3384", {"start": v(-4.47, 65.65) * mm, "end": v(-4.51, 65.65) * mm});
            skLineSegment(sketch, "E3385", {"start": v(-4.56, 65.65) * mm, "end": v(-4.6, 65.65) * mm});
            skLineSegment(sketch, "E3386", {"start": v(-4.6, 65.65) * mm, "end": v(-4.64, 65.65) * mm});
            skLineSegment(sketch, "E3387", {"start": v(-4.64, 65.65) * mm, "end": v(-4.69, 65.65) * mm});
            skLineSegment(sketch, "E3388", {"start": v(-4.69, 65.65) * mm, "end": v(-4.73, 65.64) * mm});
            skLineSegment(sketch, "E3389", {"start": v(-4.73, 65.64) * mm, "end": v(-4.77, 65.64) * mm});
            skLineSegment(sketch, "E3390", {"start": v(-4.77, 65.64) * mm, "end": v(-4.81, 65.63) * mm});
            skLineSegment(sketch, "E3391", {"start": v(-4.81, 65.63) * mm, "end": v(-4.86, 65.62) * mm});
            skLineSegment(sketch, "E3392", {"start": v(-4.86, 65.62) * mm, "end": v(-4.9, 65.61) * mm});
            skLineSegment(sketch, "E3393", {"start": v(-4.9, 65.61) * mm, "end": v(-4.94, 65.6) * mm});
            skLineSegment(sketch, "E3394", {"start": v(-4.94, 65.6) * mm, "end": v(-4.98, 65.59) * mm});
            skLineSegment(sketch, "E3395", {"start": v(-4.98, 65.59) * mm, "end": v(-5.02, 65.57) * mm});
            skLineSegment(sketch, "E3396", {"start": v(-5.02, 65.57) * mm, "end": v(-5.06, 65.55) * mm});
            skLineSegment(sketch, "E3397", {"start": v(-5.06, 65.55) * mm, "end": v(-5.1, 65.54) * mm});
            skLineSegment(sketch, "E3398", {"start": v(-5.1, 65.54) * mm, "end": v(-5.14, 65.52) * mm});
            skLineSegment(sketch, "E3399", {"start": v(-5.14, 65.52) * mm, "end": v(-5.18, 65.5) * mm});
            skLineSegment(sketch, "E3400", {"start": v(-5.18, 65.5) * mm, "end": v(-5.22, 65.48) * mm});
            skLineSegment(sketch, "E3401", {"start": v(-5.22, 65.48) * mm, "end": v(-5.25, 65.45) * mm});
            skLineSegment(sketch, "E3402", {"start": v(-5.25, 65.45) * mm, "end": v(-5.3, 65.43) * mm});
            skLineSegment(sketch, "E3403", {"start": v(-5.3, 65.43) * mm, "end": v(-5.33, 65.4) * mm});
            skLineSegment(sketch, "E3404", {"start": v(-5.33, 65.4) * mm, "end": v(-5.36, 65.38) * mm});
            skLineSegment(sketch, "E3405", {"start": v(-5.36, 65.38) * mm, "end": v(-5.4, 65.35) * mm});
            skLineSegment(sketch, "E3406", {"start": v(-5.4, 65.35) * mm, "end": v(-5.43, 65.32) * mm});
            skLineSegment(sketch, "E3407", {"start": v(-5.43, 65.32) * mm, "end": v(-5.46, 65.3) * mm});
            skLineSegment(sketch, "E3408", {"start": v(-5.46, 65.3) * mm, "end": v(-5.49, 65.26) * mm});
            skLineSegment(sketch, "E3409", {"start": v(-5.49, 65.26) * mm, "end": v(-5.52, 65.23) * mm});
            skLineSegment(sketch, "E3410", {"start": v(-5.52, 65.23) * mm, "end": v(-5.54, 65.2) * mm});
            skLineSegment(sketch, "E3411", {"start": v(-5.54, 65.2) * mm, "end": v(-5.57, 65.16) * mm});
            skLineSegment(sketch, "E3412", {"start": v(-5.57, 65.16) * mm, "end": v(-5.6, 65.13) * mm});
            skLineSegment(sketch, "E3413", {"start": v(-5.6, 65.13) * mm, "end": v(-5.62, 65.09) * mm});
            skLineSegment(sketch, "E3414", {"start": v(-5.65, 65.05) * mm, "end": v(-5.67, 65.02) * mm});
            skLineSegment(sketch, "E3415", {"start": v(-5.67, 65.02) * mm, "end": v(-5.69, 64.98) * mm});
            skLineSegment(sketch, "E3416", {"start": v(-5.69, 64.98) * mm, "end": v(-5.7, 64.94) * mm});
            skLineSegment(sketch, "E3417", {"start": v(-5.7, 64.94) * mm, "end": v(-5.72, 64.9) * mm});
            skLineSegment(sketch, "E3418", {"start": v(-5.72, 64.9) * mm, "end": v(-5.74, 64.86) * mm});
            skLineSegment(sketch, "E3419", {"start": v(-5.74, 64.86) * mm, "end": v(-5.76, 64.82) * mm});
            skLineSegment(sketch, "E3420", {"start": v(-5.76, 64.82) * mm, "end": v(-5.77, 64.78) * mm});
            skLineSegment(sketch, "E3421", {"start": v(-5.77, 64.78) * mm, "end": v(-5.78, 64.73) * mm});
            skLineSegment(sketch, "E3422", {"start": v(-5.78, 64.73) * mm, "end": v(-5.8, 64.7) * mm});
            skLineSegment(sketch, "E3423", {"start": v(-5.8, 64.7) * mm, "end": v(-5.8, 64.65) * mm});
            skLineSegment(sketch, "E3424", {"start": v(-5.8, 64.65) * mm, "end": v(-5.81, 64.6) * mm});
            skLineSegment(sketch, "E3425", {"start": v(-5.79, 64.1) * mm, "end": v(-5.78, 64.05) * mm});
            skLineSegment(sketch, "E3426", {"start": v(-5.78, 64.05) * mm, "end": v(-5.76, 64) * mm});
            skLineSegment(sketch, "E3427", {"start": v(-5.76, 64) * mm, "end": v(-5.75, 63.97) * mm});
            skLineSegment(sketch, "E3428", {"start": v(-5.75, 63.97) * mm, "end": v(-5.73, 63.93) * mm});
            skLineSegment(sketch, "E3429", {"start": v(-5.73, 63.93) * mm, "end": v(-5.72, 63.89) * mm});
            skLineSegment(sketch, "E3430", {"start": v(-5.72, 63.89) * mm, "end": v(-5.7, 63.85) * mm});
            skLineSegment(sketch, "E3431", {"start": v(-5.7, 63.85) * mm, "end": v(-5.68, 63.8) * mm});
            skLineSegment(sketch, "E3432", {"start": v(-5.68, 63.8) * mm, "end": v(-5.66, 63.77) * mm});
            skLineSegment(sketch, "E3433", {"start": v(-5.66, 63.77) * mm, "end": v(-5.63, 63.73) * mm});
            skLineSegment(sketch, "E3434", {"start": v(-5.63, 63.73) * mm, "end": v(-5.6, 63.7) * mm});
            skLineSegment(sketch, "E3435", {"start": v(-5.6, 63.7) * mm, "end": v(-5.58, 63.66) * mm});
            skLineSegment(sketch, "E3436", {"start": v(-5.58, 63.66) * mm, "end": v(-5.56, 63.63) * mm});
            skLineSegment(sketch, "E3437", {"start": v(-5.56, 63.63) * mm, "end": v(-5.53, 63.6) * mm});
            skLineSegment(sketch, "E3438", {"start": v(-5.53, 63.6) * mm, "end": v(-5.5, 63.56) * mm});
            skLineSegment(sketch, "E3439", {"start": v(-5.5, 63.56) * mm, "end": v(-5.47, 63.53) * mm});
            skLineSegment(sketch, "E3440", {"start": v(-5.47, 63.53) * mm, "end": v(-5.44, 63.5) * mm});
            skLineSegment(sketch, "E3441", {"start": v(-5.41, 63.47) * mm, "end": v(-5.38, 63.44) * mm});
            skLineSegment(sketch, "E3442", {"start": v(-5.38, 63.44) * mm, "end": v(-5.34, 63.41) * mm});
            skLineSegment(sketch, "E3443", {"start": v(-5.3, 63.39) * mm, "end": v(-5.27, 63.36) * mm});
            skLineSegment(sketch, "E3444", {"start": v(-5.27, 63.36) * mm, "end": v(-5.24, 63.34) * mm});
            skLineSegment(sketch, "E3445", {"start": v(-5.24, 63.34) * mm, "end": v(-5.2, 63.32) * mm});
            skLineSegment(sketch, "E3446", {"start": v(-5.2, 63.32) * mm, "end": v(-5.16, 63.3) * mm});
            skLineSegment(sketch, "E3447", {"start": v(-5.16, 63.3) * mm, "end": v(-5.12, 63.28) * mm});
            skLineSegment(sketch, "E3448", {"start": v(-5.12, 63.28) * mm, "end": v(-5.08, 63.26) * mm});
            skLineSegment(sketch, "E3449", {"start": v(-5.08, 63.26) * mm, "end": v(-5.04, 63.24) * mm});
            skLineSegment(sketch, "E3450", {"start": v(-5.04, 63.24) * mm, "end": v(-5, 63.23) * mm});
            skLineSegment(sketch, "E3451", {"start": v(-5, 63.23) * mm, "end": v(-4.96, 63.21) * mm});
            skLineSegment(sketch, "E3452", {"start": v(-4.96, 63.21) * mm, "end": v(-4.92, 63.2) * mm});
            skLineSegment(sketch, "E3453", {"start": v(-4.92, 63.2) * mm, "end": v(-4.88, 63.19) * mm});
            skLineSegment(sketch, "E3454", {"start": v(-4.88, 63.19) * mm, "end": v(-4.84, 63.18) * mm});
            skLineSegment(sketch, "E3455", {"start": v(-4.84, 63.18) * mm, "end": v(-4.8, 63.17) * mm});
            skLineSegment(sketch, "E3456", {"start": v(-4.8, 63.17) * mm, "end": v(-4.75, 63.16) * mm});
            skLineSegment(sketch, "E3457", {"start": v(-4.75, 63.16) * mm, "end": v(-4.7, 63.16) * mm});
            skLineSegment(sketch, "E3458", {"start": v(-4.7, 63.16) * mm, "end": v(-4.66, 63.16) * mm});
            skLineSegment(sketch, "E3459", {"start": v(-4.66, 63.16) * mm, "end": v(-4.62, 63.15) * mm});
            skLineSegment(sketch, "E3460", {"start": v(-4.62, 63.15) * mm, "end": v(-4.58, 63.15) * mm});
            skLineSegment(sketch, "E3461", {"start": v(-78.33, 61.9) * mm, "end": v(-78.24, 61.9) * mm});
            skLineSegment(sketch, "E3462", {"start": v(-78.24, 61.9) * mm, "end": v(-78.15, 61.9) * mm});
            skLineSegment(sketch, "E3463", {"start": v(-78.07, 61.92) * mm, "end": v(-77.98, 61.93) * mm});
            skLineSegment(sketch, "E3464", {"start": v(-77.9, 61.94) * mm, "end": v(-77.81, 61.96) * mm});
            skLineSegment(sketch, "E3465", {"start": v(-77.81, 61.96) * mm, "end": v(-77.73, 61.98) * mm});
            skLineSegment(sketch, "E3466", {"start": v(-77.73, 61.98) * mm, "end": v(-77.64, 62) * mm});
            skLineSegment(sketch, "E3467", {"start": v(-77.64, 62) * mm, "end": v(-77.56, 62.02) * mm});
            skLineSegment(sketch, "E3468", {"start": v(-77.56, 62.02) * mm, "end": v(-77.48, 62.05) * mm});
            skLineSegment(sketch, "E3469", {"start": v(-77.32, 62.12) * mm, "end": v(-77.24, 62.15) * mm});
            skLineSegment(sketch, "E3470", {"start": v(-77.24, 62.15) * mm, "end": v(-77.16, 62.2) * mm});
            skLineSegment(sketch, "E3471", {"start": v(-77.16, 62.2) * mm, "end": v(-77.08, 62.23) * mm});
            skLineSegment(sketch, "E3472", {"start": v(-77.08, 62.23) * mm, "end": v(-77, 62.28) * mm});
            skLineSegment(sketch, "E3473", {"start": v(-77, 62.28) * mm, "end": v(-76.94, 62.33) * mm});
            skLineSegment(sketch, "E3474", {"start": v(-76.94, 62.33) * mm, "end": v(-76.86, 62.37) * mm});
            skLineSegment(sketch, "E3475", {"start": v(-76.86, 62.37) * mm, "end": v(-76.8, 62.43) * mm});
            skLineSegment(sketch, "E3476", {"start": v(-76.8, 62.43) * mm, "end": v(-76.73, 62.48) * mm});
            skLineSegment(sketch, "E3477", {"start": v(-76.73, 62.48) * mm, "end": v(-76.66, 62.54) * mm});
            skLineSegment(sketch, "E3478", {"start": v(-76.66, 62.54) * mm, "end": v(-76.6, 62.6) * mm});
            skLineSegment(sketch, "E3479", {"start": v(-76.6, 62.6) * mm, "end": v(-76.54, 62.66) * mm});
            skLineSegment(sketch, "E3480", {"start": v(-76.54, 62.66) * mm, "end": v(-76.48, 62.72) * mm});
            skLineSegment(sketch, "E3481", {"start": v(-76.42, 62.79) * mm, "end": v(-76.37, 62.85) * mm});
            skLineSegment(sketch, "E3482", {"start": v(-76.37, 62.85) * mm, "end": v(-76.31, 62.92) * mm});
            skLineSegment(sketch, "E3483", {"start": v(-76.31, 62.92) * mm, "end": v(-76.26, 63) * mm});
            skLineSegment(sketch, "E3484", {"start": v(-76.26, 63) * mm, "end": v(-76.21, 63.07) * mm});
            skLineSegment(sketch, "E3485", {"start": v(-76.21, 63.07) * mm, "end": v(-76.17, 63.14) * mm});
            skLineSegment(sketch, "E3486", {"start": v(-76.17, 63.14) * mm, "end": v(-76.13, 63.22) * mm});
            skLineSegment(sketch, "E3487", {"start": v(-76.13, 63.22) * mm, "end": v(-76.09, 63.3) * mm});
            skLineSegment(sketch, "E3488", {"start": v(-76.09, 63.3) * mm, "end": v(-76.05, 63.37) * mm});
            skLineSegment(sketch, "E3489", {"start": v(-76.05, 63.37) * mm, "end": v(-76.02, 63.45) * mm});
            skLineSegment(sketch, "E3490", {"start": v(-76.02, 63.45) * mm, "end": v(-75.98, 63.53) * mm});
            skLineSegment(sketch, "E3491", {"start": v(-75.98, 63.53) * mm, "end": v(-75.96, 63.61) * mm});
            skLineSegment(sketch, "E3492", {"start": v(-75.96, 63.61) * mm, "end": v(-75.93, 63.7) * mm});
            skLineSegment(sketch, "E3493", {"start": v(-75.93, 63.7) * mm, "end": v(-75.9, 63.78) * mm});
            skLineSegment(sketch, "E3494", {"start": v(-75.9, 63.78) * mm, "end": v(-75.89, 63.86) * mm});
            skLineSegment(sketch, "E3495", {"start": v(-75.89, 63.86) * mm, "end": v(-75.87, 63.95) * mm});
            skLineSegment(sketch, "E3496", {"start": v(-75.87, 63.95) * mm, "end": v(-75.85, 64.04) * mm});
            skLineSegment(sketch, "E3497", {"start": v(-75.85, 64.04) * mm, "end": v(-75.84, 64.12) * mm});
            skLineSegment(sketch, "E3498", {"start": v(-75.84, 64.12) * mm, "end": v(-75.84, 64.2) * mm});
            skLineSegment(sketch, "E3499", {"start": v(-75.84, 64.2) * mm, "end": v(-75.83, 64.3) * mm});
            skLineSegment(sketch, "E3500", {"start": v(-75.85, 64.73) * mm, "end": v(-75.86, 64.81) * mm});
            skLineSegment(sketch, "E3501", {"start": v(-75.86, 64.81) * mm, "end": v(-75.88, 64.9) * mm});
            skLineSegment(sketch, "E3502", {"start": v(-75.88, 64.9) * mm, "end": v(-75.9, 64.98) * mm});
            skLineSegment(sketch, "E3503", {"start": v(-75.9, 64.98) * mm, "end": v(-75.92, 65.07) * mm});
            skLineSegment(sketch, "E3504", {"start": v(-75.94, 65.15) * mm, "end": v(-75.97, 65.23) * mm});
            skLineSegment(sketch, "E3505", {"start": v(-75.97, 65.23) * mm, "end": v(-76, 65.31) * mm});
            skLineSegment(sketch, "E3506", {"start": v(-76, 65.31) * mm, "end": v(-76.03, 65.4) * mm});
            skLineSegment(sketch, "E3507", {"start": v(-76.03, 65.4) * mm, "end": v(-76.07, 65.47) * mm});
            skLineSegment(sketch, "E3508", {"start": v(-76.07, 65.47) * mm, "end": v(-76.1, 65.55) * mm});
            skLineSegment(sketch, "E3509", {"start": v(-76.1, 65.55) * mm, "end": v(-76.15, 65.63) * mm});
            skLineSegment(sketch, "E3510", {"start": v(-76.15, 65.63) * mm, "end": v(-76.2, 65.7) * mm});
            skLineSegment(sketch, "E3511", {"start": v(-76.2, 65.7) * mm, "end": v(-76.24, 65.78) * mm});
            skLineSegment(sketch, "E3512", {"start": v(-76.83, 66.4) * mm, "end": v(-76.9, 66.46) * mm});
            skLineSegment(sketch, "E3513", {"start": v(-77.05, 66.55) * mm, "end": v(-77.12, 66.6) * mm});
            skLineSegment(sketch, "E3514", {"start": v(-77.12, 66.6) * mm, "end": v(-77.2, 66.63) * mm});
            skLineSegment(sketch, "E3515", {"start": v(-77.2, 66.63) * mm, "end": v(-77.28, 66.67) * mm});
            skLineSegment(sketch, "E3516", {"start": v(-77.28, 66.67) * mm, "end": v(-77.36, 66.7) * mm});
            skLineSegment(sketch, "E3517", {"start": v(-77.36, 66.7) * mm, "end": v(-77.44, 66.74) * mm});
            skLineSegment(sketch, "E3518", {"start": v(-77.44, 66.74) * mm, "end": v(-77.52, 66.77) * mm});
            skLineSegment(sketch, "E3519", {"start": v(-77.52, 66.77) * mm, "end": v(-77.6, 66.8) * mm});
            skLineSegment(sketch, "E3520", {"start": v(-77.68, 66.82) * mm, "end": v(-77.77, 66.84) * mm});
            skLineSegment(sketch, "E3521", {"start": v(-77.77, 66.84) * mm, "end": v(-77.85, 66.86) * mm});
            skLineSegment(sketch, "E3522", {"start": v(-78.37, 66.9) * mm, "end": v(-78.46, 66.9) * mm});
            skLineSegment(sketch, "E3523", {"start": v(-78.46, 66.9) * mm, "end": v(-78.54, 66.9) * mm});
            skLineSegment(sketch, "E3524", {"start": v(-78.54, 66.9) * mm, "end": v(-78.63, 66.88) * mm});
            skLineSegment(sketch, "E3525", {"start": v(-78.63, 66.88) * mm, "end": v(-78.72, 66.87) * mm});
            skLineSegment(sketch, "E3526", {"start": v(-78.72, 66.87) * mm, "end": v(-78.8, 66.86) * mm});
            skLineSegment(sketch, "E3527", {"start": v(-78.8, 66.86) * mm, "end": v(-78.89, 66.84) * mm});
            skLineSegment(sketch, "E3528", {"start": v(-78.89, 66.84) * mm, "end": v(-78.97, 66.82) * mm});
            skLineSegment(sketch, "E3529", {"start": v(-78.97, 66.82) * mm, "end": v(-79.05, 66.8) * mm});
            skLineSegment(sketch, "E3530", {"start": v(-79.05, 66.8) * mm, "end": v(-79.14, 66.77) * mm});
            skLineSegment(sketch, "E3531", {"start": v(-79.14, 66.77) * mm, "end": v(-79.22, 66.74) * mm});
            skLineSegment(sketch, "E3532", {"start": v(-79.22, 66.74) * mm, "end": v(-79.3, 66.7) * mm});
            skLineSegment(sketch, "E3533", {"start": v(-79.3, 66.7) * mm, "end": v(-79.38, 66.67) * mm});
            skLineSegment(sketch, "E3534", {"start": v(-79.38, 66.67) * mm, "end": v(-79.46, 66.63) * mm});
            skLineSegment(sketch, "E3535", {"start": v(-79.46, 66.63) * mm, "end": v(-79.53, 66.6) * mm});
            skLineSegment(sketch, "E3536", {"start": v(-79.53, 66.6) * mm, "end": v(-79.6, 66.55) * mm});
            skLineSegment(sketch, "E3537", {"start": v(-79.6, 66.55) * mm, "end": v(-79.68, 66.5) * mm});
            skLineSegment(sketch, "E3538", {"start": v(-79.68, 66.5) * mm, "end": v(-79.75, 66.46) * mm});
            skLineSegment(sketch, "E3539", {"start": v(-79.82, 66.4) * mm, "end": v(-79.9, 66.35) * mm});
            skLineSegment(sketch, "E3540", {"start": v(-79.9, 66.35) * mm, "end": v(-79.96, 66.3) * mm});
            skLineSegment(sketch, "E3541", {"start": v(-79.96, 66.3) * mm, "end": v(-80.02, 66.24) * mm});
            skLineSegment(sketch, "E3542", {"start": v(-80.02, 66.24) * mm, "end": v(-80.09, 66.18) * mm});
            skLineSegment(sketch, "E3543", {"start": v(-80.09, 66.18) * mm, "end": v(-80.15, 66.12) * mm});
            skLineSegment(sketch, "E3544", {"start": v(-80.15, 66.12) * mm, "end": v(-80.2, 66.05) * mm});
            skLineSegment(sketch, "E3545", {"start": v(-80.2, 66.05) * mm, "end": v(-80.26, 65.99) * mm});
            skLineSegment(sketch, "E3546", {"start": v(-80.26, 65.99) * mm, "end": v(-80.32, 65.92) * mm});
            skLineSegment(sketch, "E3547", {"start": v(-80.32, 65.92) * mm, "end": v(-80.37, 65.85) * mm});
            skLineSegment(sketch, "E3548", {"start": v(-80.37, 65.85) * mm, "end": v(-80.42, 65.78) * mm});
            skLineSegment(sketch, "E3549", {"start": v(-80.42, 65.78) * mm, "end": v(-80.46, 65.7) * mm});
            skLineSegment(sketch, "E3550", {"start": v(-80.46, 65.7) * mm, "end": v(-80.5, 65.63) * mm});
            skLineSegment(sketch, "E3551", {"start": v(-80.5, 65.63) * mm, "end": v(-80.55, 65.55) * mm});
            skLineSegment(sketch, "E3552", {"start": v(-80.59, 65.47) * mm, "end": v(-80.62, 65.4) * mm});
            skLineSegment(sketch, "E3553", {"start": v(-80.62, 65.4) * mm, "end": v(-80.66, 65.31) * mm});
            skLineSegment(sketch, "E3554", {"start": v(-80.66, 65.31) * mm, "end": v(-80.69, 65.23) * mm});
            skLineSegment(sketch, "E3555", {"start": v(-80.69, 65.23) * mm, "end": v(-80.71, 65.15) * mm});
            skLineSegment(sketch, "E3556", {"start": v(-80.71, 65.15) * mm, "end": v(-80.74, 65.07) * mm});
            skLineSegment(sketch, "E3557", {"start": v(-80.74, 65.07) * mm, "end": v(-80.76, 64.98) * mm});
            skLineSegment(sketch, "E3558", {"start": v(-80.78, 64.9) * mm, "end": v(-80.8, 64.81) * mm});
            skLineSegment(sketch, "E3559", {"start": v(-80.8, 64.81) * mm, "end": v(-80.8, 64.73) * mm});
            skLineSegment(sketch, "E3560", {"start": v(-80.8, 64.73) * mm, "end": v(-80.82, 64.64) * mm});
            skLineSegment(sketch, "E3561", {"start": v(-80.82, 64.2) * mm, "end": v(-80.81, 64.12) * mm});
            skLineSegment(sketch, "E3562", {"start": v(-80.81, 64.12) * mm, "end": v(-80.8, 64.04) * mm});
            skLineSegment(sketch, "E3563", {"start": v(-80.8, 64.04) * mm, "end": v(-80.79, 63.95) * mm});
            skLineSegment(sketch, "E3564", {"start": v(-80.79, 63.95) * mm, "end": v(-80.77, 63.86) * mm});
            skLineSegment(sketch, "E3565", {"start": v(-80.77, 63.86) * mm, "end": v(-80.75, 63.78) * mm});
            skLineSegment(sketch, "E3566", {"start": v(-80.75, 63.78) * mm, "end": v(-80.73, 63.7) * mm});
            skLineSegment(sketch, "E3567", {"start": v(-80.73, 63.7) * mm, "end": v(-80.7, 63.61) * mm});
            skLineSegment(sketch, "E3568", {"start": v(-80.67, 63.53) * mm, "end": v(-80.64, 63.45) * mm});
            skLineSegment(sketch, "E3569", {"start": v(-80.64, 63.45) * mm, "end": v(-80.6, 63.37) * mm});
            skLineSegment(sketch, "E3570", {"start": v(-80.6, 63.37) * mm, "end": v(-80.57, 63.3) * mm});
            skLineSegment(sketch, "E3571", {"start": v(-80.57, 63.3) * mm, "end": v(-80.53, 63.22) * mm});
            skLineSegment(sketch, "E3572", {"start": v(-80.53, 63.22) * mm, "end": v(-80.49, 63.14) * mm});
            skLineSegment(sketch, "E3573", {"start": v(-80.49, 63.14) * mm, "end": v(-80.44, 63.07) * mm});
            skLineSegment(sketch, "E3574", {"start": v(-80.44, 63.07) * mm, "end": v(-80.4, 63) * mm});
            skLineSegment(sketch, "E3575", {"start": v(-80.4, 63) * mm, "end": v(-80.34, 62.92) * mm});
            skLineSegment(sketch, "E3576", {"start": v(-80.34, 62.92) * mm, "end": v(-80.29, 62.85) * mm});
            skLineSegment(sketch, "E3577", {"start": v(-80.18, 62.72) * mm, "end": v(-80.12, 62.66) * mm});
            skLineSegment(sketch, "E3578", {"start": v(-80.06, 62.6) * mm, "end": v(-80, 62.54) * mm});
            skLineSegment(sketch, "E3579", {"start": v(-80, 62.54) * mm, "end": v(-79.93, 62.48) * mm});
            skLineSegment(sketch, "E3580", {"start": v(-79.93, 62.48) * mm, "end": v(-79.86, 62.43) * mm});
            skLineSegment(sketch, "E3581", {"start": v(-79.86, 62.43) * mm, "end": v(-79.79, 62.37) * mm});
            skLineSegment(sketch, "E3582", {"start": v(-79.79, 62.37) * mm, "end": v(-79.72, 62.33) * mm});
            skLineSegment(sketch, "E3583", {"start": v(-79.72, 62.33) * mm, "end": v(-79.65, 62.28) * mm});
            skLineSegment(sketch, "E3584", {"start": v(-79.65, 62.28) * mm, "end": v(-79.57, 62.23) * mm});
            skLineSegment(sketch, "E3585", {"start": v(-79.57, 62.23) * mm, "end": v(-79.5, 62.2) * mm});
            skLineSegment(sketch, "E3586", {"start": v(-79.5, 62.2) * mm, "end": v(-79.42, 62.15) * mm});
            skLineSegment(sketch, "E3587", {"start": v(-79.34, 62.12) * mm, "end": v(-79.26, 62.08) * mm});
            skLineSegment(sketch, "E3588", {"start": v(-79.26, 62.08) * mm, "end": v(-79.18, 62.05) * mm});
            skLineSegment(sketch, "E3589", {"start": v(-79.18, 62.05) * mm, "end": v(-79.1, 62.02) * mm});
            skLineSegment(sketch, "E3590", {"start": v(-79.1, 62.02) * mm, "end": v(-79.01, 62) * mm});
            skLineSegment(sketch, "E3591", {"start": v(-79.01, 62) * mm, "end": v(-78.93, 61.98) * mm});
            skLineSegment(sketch, "E3592", {"start": v(-78.93, 61.98) * mm, "end": v(-78.84, 61.96) * mm});
            skLineSegment(sketch, "E3593", {"start": v(-78.84, 61.96) * mm, "end": v(-78.76, 61.94) * mm});
            skLineSegment(sketch, "E3594", {"start": v(-78.76, 61.94) * mm, "end": v(-78.67, 61.93) * mm});
            skLineSegment(sketch, "E3595", {"start": v(-78.67, 61.93) * mm, "end": v(-78.59, 61.92) * mm});
            skLineSegment(sketch, "E3596", {"start": v(-78.59, 61.92) * mm, "end": v(-78.5, 61.9) * mm});
            skLineSegment(sketch, "E3597", {"start": v(-78.5, 61.9) * mm, "end": v(-78.41, 61.9) * mm});
            skLineSegment(sketch, "E3598", {"start": v(-78.41, 61.9) * mm, "end": v(-78.33, 61.9) * mm});
            skLineSegment(sketch, "E3599", {"start": v(69.17, 61.9) * mm, "end": v(69.26, 61.9) * mm});
            skLineSegment(sketch, "E3600", {"start": v(69.26, 61.9) * mm, "end": v(69.35, 61.9) * mm});
            skLineSegment(sketch, "E3601", {"start": v(69.35, 61.9) * mm, "end": v(69.43, 61.92) * mm});
            skLineSegment(sketch, "E3602", {"start": v(69.43, 61.92) * mm, "end": v(69.52, 61.93) * mm});
            skLineSegment(sketch, "E3603", {"start": v(69.52, 61.93) * mm, "end": v(69.6, 61.94) * mm});
            skLineSegment(sketch, "E3604", {"start": v(69.6, 61.94) * mm, "end": v(69.69, 61.96) * mm});
            skLineSegment(sketch, "E3605", {"start": v(69.69, 61.96) * mm, "end": v(69.77, 61.98) * mm});
            skLineSegment(sketch, "E3606", {"start": v(69.77, 61.98) * mm, "end": v(69.86, 62) * mm});
            skLineSegment(sketch, "E3607", {"start": v(69.86, 62) * mm, "end": v(69.94, 62.02) * mm});
            skLineSegment(sketch, "E3608", {"start": v(69.94, 62.02) * mm, "end": v(70.02, 62.05) * mm});
            skLineSegment(sketch, "E3609", {"start": v(70.02, 62.05) * mm, "end": v(70.1, 62.08) * mm});
            skLineSegment(sketch, "E3610", {"start": v(70.1, 62.08) * mm, "end": v(70.18, 62.12) * mm});
            skLineSegment(sketch, "E3611", {"start": v(70.18, 62.12) * mm, "end": v(70.26, 62.15) * mm});
            skLineSegment(sketch, "E3612", {"start": v(70.64, 62.37) * mm, "end": v(70.7, 62.43) * mm});
            skLineSegment(sketch, "E3613", {"start": v(70.77, 62.48) * mm, "end": v(70.84, 62.54) * mm});
            skLineSegment(sketch, "E3614", {"start": v(70.9, 62.6) * mm, "end": v(70.96, 62.66) * mm});
            skLineSegment(sketch, "E3615", {"start": v(70.96, 62.66) * mm, "end": v(71.02, 62.72) * mm});
            skLineSegment(sketch, "E3616", {"start": v(71.02, 62.72) * mm, "end": v(71.08, 62.79) * mm});
            skLineSegment(sketch, "E3617", {"start": v(71.08, 62.79) * mm, "end": v(71.13, 62.85) * mm});
            skLineSegment(sketch, "E3618", {"start": v(71.13, 62.85) * mm, "end": v(71.19, 62.92) * mm});
            skLineSegment(sketch, "E3619", {"start": v(71.19, 62.92) * mm, "end": v(71.24, 63) * mm});
            skLineSegment(sketch, "E3620", {"start": v(71.24, 63) * mm, "end": v(71.29, 63.07) * mm});
            skLineSegment(sketch, "E3621", {"start": v(71.33, 63.14) * mm, "end": v(71.37, 63.22) * mm});
            skLineSegment(sketch, "E3622", {"start": v(71.37, 63.22) * mm, "end": v(71.41, 63.3) * mm});
            skLineSegment(sketch, "E3623", {"start": v(71.41, 63.3) * mm, "end": v(71.45, 63.37) * mm});
            skLineSegment(sketch, "E3624", {"start": v(71.45, 63.37) * mm, "end": v(71.48, 63.45) * mm});
            skLineSegment(sketch, "E3625", {"start": v(71.52, 63.53) * mm, "end": v(71.54, 63.61) * mm});
            skLineSegment(sketch, "E3626", {"start": v(71.54, 63.61) * mm, "end": v(71.57, 63.7) * mm});
            skLineSegment(sketch, "E3627", {"start": v(71.57, 63.7) * mm, "end": v(71.6, 63.78) * mm});
            skLineSegment(sketch, "E3628", {"start": v(71.6, 63.78) * mm, "end": v(71.61, 63.86) * mm});
            skLineSegment(sketch, "E3629", {"start": v(71.61, 63.86) * mm, "end": v(71.63, 63.95) * mm});
            skLineSegment(sketch, "E3630", {"start": v(71.63, 63.95) * mm, "end": v(71.65, 64.04) * mm});
            skLineSegment(sketch, "E3631", {"start": v(71.65, 64.04) * mm, "end": v(71.66, 64.12) * mm});
            skLineSegment(sketch, "E3632", {"start": v(71.66, 64.12) * mm, "end": v(71.66, 64.2) * mm});
            skLineSegment(sketch, "E3633", {"start": v(71.64, 64.81) * mm, "end": v(71.62, 64.9) * mm});
            skLineSegment(sketch, "E3634", {"start": v(71.62, 64.9) * mm, "end": v(71.6, 64.98) * mm});
            skLineSegment(sketch, "E3635", {"start": v(71.6, 64.98) * mm, "end": v(71.58, 65.07) * mm});
            skLineSegment(sketch, "E3636", {"start": v(71.58, 65.07) * mm, "end": v(71.56, 65.15) * mm});
            skLineSegment(sketch, "E3637", {"start": v(71.56, 65.15) * mm, "end": v(71.53, 65.23) * mm});
            skLineSegment(sketch, "E3638", {"start": v(71.53, 65.23) * mm, "end": v(71.5, 65.31) * mm});
            skLineSegment(sketch, "E3639", {"start": v(71.5, 65.31) * mm, "end": v(71.47, 65.4) * mm});
            skLineSegment(sketch, "E3640", {"start": v(71.47, 65.4) * mm, "end": v(71.43, 65.47) * mm});
            skLineSegment(sketch, "E3641", {"start": v(71.43, 65.47) * mm, "end": v(71.4, 65.55) * mm});
            skLineSegment(sketch, "E3642", {"start": v(71.4, 65.55) * mm, "end": v(71.35, 65.63) * mm});
            skLineSegment(sketch, "E3643", {"start": v(71.35, 65.63) * mm, "end": v(71.3, 65.7) * mm});
            skLineSegment(sketch, "E3644", {"start": v(71.21, 65.85) * mm, "end": v(71.16, 65.92) * mm});
            skLineSegment(sketch, "E3645", {"start": v(71.16, 65.92) * mm, "end": v(71.1, 65.99) * mm});
            skLineSegment(sketch, "E3646", {"start": v(71.1, 65.99) * mm, "end": v(71.05, 66.05) * mm});
            skLineSegment(sketch, "E3647", {"start": v(71.05, 66.05) * mm, "end": v(71, 66.12) * mm});
            skLineSegment(sketch, "E3648", {"start": v(71, 66.12) * mm, "end": v(70.93, 66.18) * mm});
            skLineSegment(sketch, "E3649", {"start": v(70.93, 66.18) * mm, "end": v(70.87, 66.24) * mm});
            skLineSegment(sketch, "E3650", {"start": v(70.87, 66.24) * mm, "end": v(70.8, 66.3) * mm});
            skLineSegment(sketch, "E3651", {"start": v(70.8, 66.3) * mm, "end": v(70.74, 66.35) * mm});
            skLineSegment(sketch, "E3652", {"start": v(70.67, 66.4) * mm, "end": v(70.6, 66.46) * mm});
            skLineSegment(sketch, "E3653", {"start": v(70.6, 66.46) * mm, "end": v(70.53, 66.5) * mm});
            skLineSegment(sketch, "E3654", {"start": v(70.53, 66.5) * mm, "end": v(70.45, 66.55) * mm});
            skLineSegment(sketch, "E3655", {"start": v(70.45, 66.55) * mm, "end": v(70.38, 66.6) * mm});
            skLineSegment(sketch, "E3656", {"start": v(70.3, 66.63) * mm, "end": v(70.22, 66.67) * mm});
            skLineSegment(sketch, "E3657", {"start": v(70.22, 66.67) * mm, "end": v(70.14, 66.7) * mm});
            skLineSegment(sketch, "E3658", {"start": v(70.14, 66.7) * mm, "end": v(70.06, 66.74) * mm});
            skLineSegment(sketch, "E3659", {"start": v(70.06, 66.74) * mm, "end": v(69.98, 66.77) * mm});
            skLineSegment(sketch, "E3660", {"start": v(69.98, 66.77) * mm, "end": v(69.9, 66.8) * mm});
            skLineSegment(sketch, "E3661", {"start": v(69.9, 66.8) * mm, "end": v(69.82, 66.82) * mm});
            skLineSegment(sketch, "E3662", {"start": v(69.82, 66.82) * mm, "end": v(69.73, 66.84) * mm});
            skLineSegment(sketch, "E3663", {"start": v(69.73, 66.84) * mm, "end": v(69.65, 66.86) * mm});
            skLineSegment(sketch, "E3664", {"start": v(69.65, 66.86) * mm, "end": v(69.56, 66.87) * mm});
            skLineSegment(sketch, "E3665", {"start": v(69.56, 66.87) * mm, "end": v(69.48, 66.88) * mm});
            skLineSegment(sketch, "E3666", {"start": v(69.48, 66.88) * mm, "end": v(69.39, 66.9) * mm});
            skLineSegment(sketch, "E3667", {"start": v(69.39, 66.9) * mm, "end": v(69.3, 66.9) * mm});
            skLineSegment(sketch, "E3668", {"start": v(69.3, 66.9) * mm, "end": v(69.22, 66.9) * mm});
            skLineSegment(sketch, "E3669", {"start": v(69.22, 66.9) * mm, "end": v(69.13, 66.9) * mm});
            skLineSegment(sketch, "E3670", {"start": v(69.13, 66.9) * mm, "end": v(69.04, 66.9) * mm});
            skLineSegment(sketch, "E3671", {"start": v(69.04, 66.9) * mm, "end": v(68.96, 66.9) * mm});
            skLineSegment(sketch, "E3672", {"start": v(68.96, 66.9) * mm, "end": v(68.87, 66.88) * mm});
            skLineSegment(sketch, "E3673", {"start": v(68.87, 66.88) * mm, "end": v(68.78, 66.87) * mm});
            skLineSegment(sketch, "E3674", {"start": v(68.78, 66.87) * mm, "end": v(68.7, 66.86) * mm});
            skLineSegment(sketch, "E3675", {"start": v(68.61, 66.84) * mm, "end": v(68.53, 66.82) * mm});
            skLineSegment(sketch, "E3676", {"start": v(68.53, 66.82) * mm, "end": v(68.45, 66.8) * mm});
            skLineSegment(sketch, "E3677", {"start": v(68.45, 66.8) * mm, "end": v(68.36, 66.77) * mm});
            skLineSegment(sketch, "E3678", {"start": v(68.36, 66.77) * mm, "end": v(68.28, 66.74) * mm});
            skLineSegment(sketch, "E3679", {"start": v(68.2, 66.7) * mm, "end": v(68.12, 66.67) * mm});
            skLineSegment(sketch, "E3680", {"start": v(68.12, 66.67) * mm, "end": v(68.04, 66.63) * mm});
            skLineSegment(sketch, "E3681", {"start": v(68.04, 66.63) * mm, "end": v(67.97, 66.6) * mm});
            skLineSegment(sketch, "E3682", {"start": v(67.97, 66.6) * mm, "end": v(67.9, 66.55) * mm});
            skLineSegment(sketch, "E3683", {"start": v(67.9, 66.55) * mm, "end": v(67.82, 66.5) * mm});
            skLineSegment(sketch, "E3684", {"start": v(67.82, 66.5) * mm, "end": v(67.75, 66.46) * mm});
            skLineSegment(sketch, "E3685", {"start": v(67.75, 66.46) * mm, "end": v(67.68, 66.4) * mm});
            skLineSegment(sketch, "E3686", {"start": v(67.68, 66.4) * mm, "end": v(67.6, 66.35) * mm});
            skLineSegment(sketch, "E3687", {"start": v(67.6, 66.35) * mm, "end": v(67.54, 66.3) * mm});
            skLineSegment(sketch, "E3688", {"start": v(67.54, 66.3) * mm, "end": v(67.48, 66.24) * mm});
            skLineSegment(sketch, "E3689", {"start": v(67.48, 66.24) * mm, "end": v(67.41, 66.18) * mm});
            skLineSegment(sketch, "E3690", {"start": v(67.3, 66.05) * mm, "end": v(67.24, 65.99) * mm});
            skLineSegment(sketch, "E3691", {"start": v(67.24, 65.99) * mm, "end": v(67.18, 65.92) * mm});
            skLineSegment(sketch, "E3692", {"start": v(67.13, 65.85) * mm, "end": v(67.08, 65.78) * mm});
            skLineSegment(sketch, "E3693", {"start": v(67.08, 65.78) * mm, "end": v(67.04, 65.7) * mm});
            skLineSegment(sketch, "E3694", {"start": v(67.04, 65.7) * mm, "end": v(67, 65.63) * mm});
            skLineSegment(sketch, "E3695", {"start": v(67, 65.63) * mm, "end": v(66.95, 65.55) * mm});
            skLineSegment(sketch, "E3696", {"start": v(66.95, 65.55) * mm, "end": v(66.91, 65.47) * mm});
            skLineSegment(sketch, "E3697", {"start": v(66.91, 65.47) * mm, "end": v(66.88, 65.4) * mm});
            skLineSegment(sketch, "E3698", {"start": v(66.88, 65.4) * mm, "end": v(66.84, 65.31) * mm});
            skLineSegment(sketch, "E3699", {"start": v(66.84, 65.31) * mm, "end": v(66.81, 65.23) * mm});
            skLineSegment(sketch, "E3700", {"start": v(66.81, 65.23) * mm, "end": v(66.79, 65.15) * mm});
            skLineSegment(sketch, "E3701", {"start": v(66.79, 65.15) * mm, "end": v(66.76, 65.07) * mm});
            skLineSegment(sketch, "E3702", {"start": v(66.74, 64.98) * mm, "end": v(66.72, 64.9) * mm});
            skLineSegment(sketch, "E3703", {"start": v(66.7, 64.73) * mm, "end": v(66.68, 64.64) * mm});
            skLineSegment(sketch, "E3704", {"start": v(66.68, 64.64) * mm, "end": v(66.68, 64.55) * mm});
            skLineSegment(sketch, "E3705", {"start": v(66.67, 64.3) * mm, "end": v(66.68, 64.2) * mm});
            skLineSegment(sketch, "E3706", {"start": v(66.68, 64.2) * mm, "end": v(66.69, 64.12) * mm});
            skLineSegment(sketch, "E3707", {"start": v(66.69, 64.12) * mm, "end": v(66.7, 64.04) * mm});
            skLineSegment(sketch, "E3708", {"start": v(66.7, 64.04) * mm, "end": v(66.71, 63.95) * mm});
            skLineSegment(sketch, "E3709", {"start": v(66.71, 63.95) * mm, "end": v(66.73, 63.86) * mm});
            skLineSegment(sketch, "E3710", {"start": v(66.73, 63.86) * mm, "end": v(66.75, 63.78) * mm});
            skLineSegment(sketch, "E3711", {"start": v(66.75, 63.78) * mm, "end": v(66.77, 63.7) * mm});
            skLineSegment(sketch, "E3712", {"start": v(66.77, 63.7) * mm, "end": v(66.8, 63.61) * mm});
            skLineSegment(sketch, "E3713", {"start": v(66.8, 63.61) * mm, "end": v(66.83, 63.53) * mm});
            skLineSegment(sketch, "E3714", {"start": v(66.83, 63.53) * mm, "end": v(66.86, 63.45) * mm});
            skLineSegment(sketch, "E3715", {"start": v(66.9, 63.37) * mm, "end": v(66.93, 63.3) * mm});
            skLineSegment(sketch, "E3716", {"start": v(66.93, 63.3) * mm, "end": v(66.97, 63.22) * mm});
            skLineSegment(sketch, "E3717", {"start": v(66.97, 63.22) * mm, "end": v(67.01, 63.14) * mm});
            skLineSegment(sketch, "E3718", {"start": v(67.01, 63.14) * mm, "end": v(67.06, 63.07) * mm});
            skLineSegment(sketch, "E3719", {"start": v(67.06, 63.07) * mm, "end": v(67.1, 63) * mm});
            skLineSegment(sketch, "E3720", {"start": v(67.1, 63) * mm, "end": v(67.16, 62.92) * mm});
            skLineSegment(sketch, "E3721", {"start": v(67.16, 62.92) * mm, "end": v(67.21, 62.85) * mm});
            skLineSegment(sketch, "E3722", {"start": v(67.27, 62.79) * mm, "end": v(67.32, 62.72) * mm});
            skLineSegment(sketch, "E3723", {"start": v(67.32, 62.72) * mm, "end": v(67.38, 62.66) * mm});
            skLineSegment(sketch, "E3724", {"start": v(67.38, 62.66) * mm, "end": v(67.44, 62.6) * mm});
            skLineSegment(sketch, "E3725", {"start": v(67.44, 62.6) * mm, "end": v(67.5, 62.54) * mm});
            skLineSegment(sketch, "E3726", {"start": v(67.5, 62.54) * mm, "end": v(67.57, 62.48) * mm});
            skLineSegment(sketch, "E3727", {"start": v(67.57, 62.48) * mm, "end": v(67.64, 62.43) * mm});
            skLineSegment(sketch, "E3728", {"start": v(67.64, 62.43) * mm, "end": v(67.71, 62.37) * mm});
            skLineSegment(sketch, "E3729", {"start": v(67.85, 62.28) * mm, "end": v(67.93, 62.23) * mm});
            skLineSegment(sketch, "E3730", {"start": v(68.24, 62.08) * mm, "end": v(68.32, 62.05) * mm});
            skLineSegment(sketch, "E3731", {"start": v(68.32, 62.05) * mm, "end": v(68.4, 62.02) * mm});
            skLineSegment(sketch, "E3732", {"start": v(68.4, 62.02) * mm, "end": v(68.49, 62) * mm});
            skLineSegment(sketch, "E3733", {"start": v(68.66, 61.96) * mm, "end": v(68.74, 61.94) * mm});
            skLineSegment(sketch, "E3734", {"start": v(68.74, 61.94) * mm, "end": v(68.83, 61.93) * mm});
            skLineSegment(sketch, "E3735", {"start": v(68.83, 61.93) * mm, "end": v(68.91, 61.92) * mm});
            skLineSegment(sketch, "E3736", {"start": v(68.91, 61.92) * mm, "end": v(69, 61.9) * mm});
            skLineSegment(sketch, "E3737", {"start": v(69, 61.9) * mm, "end": v(69.09, 61.9) * mm});
            skLineSegment(sketch, "E3738", {"start": v(69.09, 61.9) * mm, "end": v(69.17, 61.9) * mm});
            skLineSegment(sketch, "E3739", {"start": v(-4.32, 60.66) * mm, "end": v(-4.19, 60.67) * mm});
            skLineSegment(sketch, "E3740", {"start": v(-4.19, 60.67) * mm, "end": v(-4.06, 60.69) * mm});
            skLineSegment(sketch, "E3741", {"start": v(-3.93, 60.7) * mm, "end": v(-3.8, 60.73) * mm});
            skLineSegment(sketch, "E3742", {"start": v(-3.8, 60.73) * mm, "end": v(-3.68, 60.76) * mm});
            skLineSegment(sketch, "E3743", {"start": v(-3.55, 60.8) * mm, "end": v(-3.42, 60.83) * mm});
            skLineSegment(sketch, "E3744", {"start": v(-3.3, 60.88) * mm, "end": v(-3.18, 60.92) * mm});
            skLineSegment(sketch, "E3745", {"start": v(-3.18, 60.92) * mm, "end": v(-3.06, 60.97) * mm});
            skLineSegment(sketch, "E3746", {"start": v(-3.06, 60.97) * mm, "end": v(-2.94, 61.03) * mm});
            skLineSegment(sketch, "E3747", {"start": v(-2.94, 61.03) * mm, "end": v(-2.83, 61.09) * mm});
            skLineSegment(sketch, "E3748", {"start": v(-2.83, 61.09) * mm, "end": v(-2.71, 61.15) * mm});
            skLineSegment(sketch, "E3749", {"start": v(-2.71, 61.15) * mm, "end": v(-2.6, 61.22) * mm});
            skLineSegment(sketch, "E3750", {"start": v(-2.38, 61.36) * mm, "end": v(-2.28, 61.44) * mm});
            skLineSegment(sketch, "E3751", {"start": v(-2.28, 61.44) * mm, "end": v(-2.18, 61.52) * mm});
            skLineSegment(sketch, "E3752", {"start": v(-2.08, 61.6) * mm, "end": v(-1.98, 61.7) * mm});
            skLineSegment(sketch, "E3753", {"start": v(-1.98, 61.7) * mm, "end": v(-1.9, 61.79) * mm});
            skLineSegment(sketch, "E3754", {"start": v(-1.8, 61.88) * mm, "end": v(-1.72, 61.98) * mm});
            skLineSegment(sketch, "E3755", {"start": v(-1.72, 61.98) * mm, "end": v(-1.63, 62.08) * mm});
            skLineSegment(sketch, "E3756", {"start": v(-1.4, 62.4) * mm, "end": v(-1.34, 62.5) * mm});
            skLineSegment(sketch, "E3757", {"start": v(-1.34, 62.5) * mm, "end": v(-1.28, 62.62) * mm});
            skLineSegment(sketch, "E3758", {"start": v(-1.28, 62.62) * mm, "end": v(-1.22, 62.74) * mm});
            skLineSegment(sketch, "E3759", {"start": v(-1.06, 63.1) * mm, "end": v(-1.02, 63.22) * mm});
            skLineSegment(sketch, "E3760", {"start": v(-1.02, 63.22) * mm, "end": v(-0.98, 63.34) * mm});
            skLineSegment(sketch, "E3761", {"start": v(-0.98, 63.34) * mm, "end": v(-0.95, 63.47) * mm});
            skLineSegment(sketch, "E3762", {"start": v(-0.95, 63.47) * mm, "end": v(-0.92, 63.6) * mm});
            skLineSegment(sketch, "E3763", {"start": v(-0.92, 63.6) * mm, "end": v(-0.89, 63.72) * mm});
            skLineSegment(sketch, "E3764", {"start": v(-0.89, 63.72) * mm, "end": v(-0.87, 63.85) * mm});
            skLineSegment(sketch, "E3765", {"start": v(-0.87, 63.85) * mm, "end": v(-0.85, 63.98) * mm});
            skLineSegment(sketch, "E3766", {"start": v(-0.85, 63.98) * mm, "end": v(-0.84, 64.11) * mm});
            skLineSegment(sketch, "E3767", {"start": v(-0.84, 64.11) * mm, "end": v(-0.83, 64.24) * mm});
            skLineSegment(sketch, "E3768", {"start": v(-0.83, 64.24) * mm, "end": v(-0.83, 64.37) * mm});
            skLineSegment(sketch, "E3769", {"start": v(-0.83, 64.63) * mm, "end": v(-0.84, 64.76) * mm});
            skLineSegment(sketch, "E3770", {"start": v(-0.84, 64.76) * mm, "end": v(-0.86, 64.89) * mm});
            skLineSegment(sketch, "E3771", {"start": v(-0.88, 65.02) * mm, "end": v(-0.9, 65.15) * mm});
            skLineSegment(sketch, "E3772", {"start": v(-0.9, 65.15) * mm, "end": v(-0.93, 65.27) * mm});
            skLineSegment(sketch, "E3773", {"start": v(-0.96, 65.4) * mm, "end": v(-1, 65.52) * mm});
            skLineSegment(sketch, "E3774", {"start": v(-1, 65.52) * mm, "end": v(-1.04, 65.65) * mm});
            skLineSegment(sketch, "E3775", {"start": v(-1.04, 65.65) * mm, "end": v(-1.09, 65.77) * mm});
            skLineSegment(sketch, "E3776", {"start": v(-1.09, 65.77) * mm, "end": v(-1.14, 65.9) * mm});
            skLineSegment(sketch, "E3777", {"start": v(-1.19, 66) * mm, "end": v(-1.25, 66.13) * mm});
            skLineSegment(sketch, "E3778", {"start": v(-1.25, 66.13) * mm, "end": v(-1.3, 66.24) * mm});
            skLineSegment(sketch, "E3779", {"start": v(-1.3, 66.24) * mm, "end": v(-1.37, 66.35) * mm});
            skLineSegment(sketch, "E3780", {"start": v(-1.37, 66.35) * mm, "end": v(-1.44, 66.46) * mm});
            skLineSegment(sketch, "E3781", {"start": v(-1.44, 66.46) * mm, "end": v(-1.52, 66.57) * mm});
            skLineSegment(sketch, "E3782", {"start": v(-1.52, 66.57) * mm, "end": v(-1.6, 66.67) * mm});
            skLineSegment(sketch, "E3783", {"start": v(-1.67, 66.78) * mm, "end": v(-1.76, 66.88) * mm});
            skLineSegment(sketch, "E3784", {"start": v(-1.76, 66.88) * mm, "end": v(-1.85, 66.97) * mm});
            skLineSegment(sketch, "E3785", {"start": v(-1.94, 67.07) * mm, "end": v(-2.03, 67.16) * mm});
            skLineSegment(sketch, "E3786", {"start": v(-2.03, 67.16) * mm, "end": v(-2.13, 67.24) * mm});
            skLineSegment(sketch, "E3787", {"start": v(-2.13, 67.24) * mm, "end": v(-2.23, 67.33) * mm});
            skLineSegment(sketch, "E3788", {"start": v(-2.23, 67.33) * mm, "end": v(-2.33, 67.4) * mm});
            skLineSegment(sketch, "E3789", {"start": v(-2.33, 67.4) * mm, "end": v(-2.44, 67.48) * mm});
            skLineSegment(sketch, "E3790", {"start": v(-2.44, 67.48) * mm, "end": v(-2.55, 67.55) * mm});
            skLineSegment(sketch, "E3791", {"start": v(-2.66, 67.62) * mm, "end": v(-2.77, 67.69) * mm});
            skLineSegment(sketch, "E3792", {"start": v(-2.77, 67.69) * mm, "end": v(-2.88, 67.75) * mm});
            skLineSegment(sketch, "E3793", {"start": v(-2.88, 67.75) * mm, "end": v(-3, 67.8) * mm});
            skLineSegment(sketch, "E3794", {"start": v(-3, 67.8) * mm, "end": v(-3.12, 67.86) * mm});
            skLineSegment(sketch, "E3795", {"start": v(-3.12, 67.86) * mm, "end": v(-3.24, 67.9) * mm});
            skLineSegment(sketch, "E3796", {"start": v(-3.24, 67.9) * mm, "end": v(-3.36, 67.95) * mm});
            skLineSegment(sketch, "E3797", {"start": v(-3.36, 67.95) * mm, "end": v(-3.49, 68) * mm});
            skLineSegment(sketch, "E3798", {"start": v(-3.61, 68.03) * mm, "end": v(-3.74, 68.06) * mm});
            skLineSegment(sketch, "E3799", {"start": v(-3.74, 68.06) * mm, "end": v(-3.87, 68.08) * mm});
            skLineSegment(sketch, "E3800", {"start": v(-4.12, 68.12) * mm, "end": v(-4.25, 68.14) * mm});
            skLineSegment(sketch, "E3801", {"start": v(-4.25, 68.14) * mm, "end": v(-4.38, 68.15) * mm});
            skLineSegment(sketch, "E3802", {"start": v(-4.51, 68.15) * mm, "end": v(-4.64, 68.15) * mm});
            skLineSegment(sketch, "E3803", {"start": v(-4.64, 68.15) * mm, "end": v(-4.77, 68.15) * mm});
            skLineSegment(sketch, "E3804", {"start": v(-4.77, 68.15) * mm, "end": v(-4.9, 68.14) * mm});
            skLineSegment(sketch, "E3805", {"start": v(-4.9, 68.14) * mm, "end": v(-5.03, 68.12) * mm});
            skLineSegment(sketch, "E3806", {"start": v(-5.03, 68.12) * mm, "end": v(-5.16, 68.1) * mm});
            skLineSegment(sketch, "E3807", {"start": v(-5.16, 68.1) * mm, "end": v(-5.29, 68.08) * mm});
            skLineSegment(sketch, "E3808", {"start": v(-5.29, 68.08) * mm, "end": v(-5.42, 68.06) * mm});
            skLineSegment(sketch, "E3809", {"start": v(-5.54, 68.03) * mm, "end": v(-5.67, 68) * mm});
            skLineSegment(sketch, "E3810", {"start": v(-5.8, 67.95) * mm, "end": v(-5.91, 67.9) * mm});
            skLineSegment(sketch, "E3811", {"start": v(-6.15, 67.8) * mm, "end": v(-6.27, 67.75) * mm});
            skLineSegment(sketch, "E3812", {"start": v(-6.27, 67.75) * mm, "end": v(-6.39, 67.69) * mm});
            skLineSegment(sketch, "E3813", {"start": v(-6.39, 67.69) * mm, "end": v(-6.5, 67.62) * mm});
            skLineSegment(sketch, "E3814", {"start": v(-6.72, 67.48) * mm, "end": v(-6.82, 67.4) * mm});
            skLineSegment(sketch, "E3815", {"start": v(-6.82, 67.4) * mm, "end": v(-6.93, 67.33) * mm});
            skLineSegment(sketch, "E3816", {"start": v(-6.93, 67.33) * mm, "end": v(-7.03, 67.24) * mm});
            skLineSegment(sketch, "E3817", {"start": v(-7.03, 67.24) * mm, "end": v(-7.12, 67.16) * mm});
            skLineSegment(sketch, "E3818", {"start": v(-7.22, 67.07) * mm, "end": v(-7.3, 66.97) * mm});
            skLineSegment(sketch, "E3819", {"start": v(-7.3, 66.97) * mm, "end": v(-7.4, 66.88) * mm});
            skLineSegment(sketch, "E3820", {"start": v(-7.4, 66.88) * mm, "end": v(-7.48, 66.78) * mm});
            skLineSegment(sketch, "E3821", {"start": v(-7.48, 66.78) * mm, "end": v(-7.56, 66.67) * mm});
            skLineSegment(sketch, "E3822", {"start": v(-7.56, 66.67) * mm, "end": v(-7.64, 66.57) * mm});
            skLineSegment(sketch, "E3823", {"start": v(-7.78, 66.35) * mm, "end": v(-7.85, 66.24) * mm});
            skLineSegment(sketch, "E3824", {"start": v(-7.85, 66.24) * mm, "end": v(-7.9, 66.13) * mm});
            skLineSegment(sketch, "E3825", {"start": v(-7.9, 66.13) * mm, "end": v(-7.97, 66) * mm});
            skLineSegment(sketch, "E3826", {"start": v(-7.97, 66) * mm, "end": v(-8.02, 65.9) * mm});
            skLineSegment(sketch, "E3827", {"start": v(-8.02, 65.9) * mm, "end": v(-8.07, 65.77) * mm});
            skLineSegment(sketch, "E3828", {"start": v(-8.07, 65.77) * mm, "end": v(-8.11, 65.65) * mm});
            skLineSegment(sketch, "E3829", {"start": v(-8.11, 65.65) * mm, "end": v(-8.16, 65.52) * mm});
            skLineSegment(sketch, "E3830", {"start": v(-8.16, 65.52) * mm, "end": v(-8.2, 65.4) * mm});
            skLineSegment(sketch, "E3831", {"start": v(-8.25, 65.15) * mm, "end": v(-8.28, 65.02) * mm});
            skLineSegment(sketch, "E3832", {"start": v(-8.28, 65.02) * mm, "end": v(-8.3, 64.89) * mm});
            skLineSegment(sketch, "E3833", {"start": v(-8.33, 64.37) * mm, "end": v(-8.32, 64.24) * mm});
            skLineSegment(sketch, "E3834", {"start": v(-8.32, 64.24) * mm, "end": v(-8.32, 64.11) * mm});
            skLineSegment(sketch, "E3835", {"start": v(-8.32, 64.11) * mm, "end": v(-8.3, 63.98) * mm});
            skLineSegment(sketch, "E3836", {"start": v(-8.3, 63.98) * mm, "end": v(-8.29, 63.85) * mm});
            skLineSegment(sketch, "E3837", {"start": v(-8.29, 63.85) * mm, "end": v(-8.27, 63.72) * mm});
            skLineSegment(sketch, "E3838", {"start": v(-8.27, 63.72) * mm, "end": v(-8.24, 63.6) * mm});
            skLineSegment(sketch, "E3839", {"start": v(-8.24, 63.6) * mm, "end": v(-8.2, 63.47) * mm});
            skLineSegment(sketch, "E3840", {"start": v(-8.2, 63.47) * mm, "end": v(-8.17, 63.34) * mm});
            skLineSegment(sketch, "E3841", {"start": v(-8.17, 63.34) * mm, "end": v(-8.14, 63.22) * mm});
            skLineSegment(sketch, "E3842", {"start": v(-8.14, 63.22) * mm, "end": v(-8.1, 63.1) * mm});
            skLineSegment(sketch, "E3843", {"start": v(-8.05, 62.98) * mm, "end": v(-8, 62.86) * mm});
            skLineSegment(sketch, "E3844", {"start": v(-8, 62.86) * mm, "end": v(-7.94, 62.74) * mm});
            skLineSegment(sketch, "E3845", {"start": v(-7.94, 62.74) * mm, "end": v(-7.88, 62.62) * mm});
            skLineSegment(sketch, "E3846", {"start": v(-7.81, 62.5) * mm, "end": v(-7.75, 62.4) * mm});
            skLineSegment(sketch, "E3847", {"start": v(-7.75, 62.4) * mm, "end": v(-7.67, 62.29) * mm});
            skLineSegment(sketch, "E3848", {"start": v(-7.67, 62.29) * mm, "end": v(-7.6, 62.18) * mm});
            skLineSegment(sketch, "E3849", {"start": v(-7.6, 62.18) * mm, "end": v(-7.52, 62.08) * mm});
            skLineSegment(sketch, "E3850", {"start": v(-7.52, 62.08) * mm, "end": v(-7.44, 61.98) * mm});
            skLineSegment(sketch, "E3851", {"start": v(-7.44, 61.98) * mm, "end": v(-7.35, 61.88) * mm});
            skLineSegment(sketch, "E3852", {"start": v(-7.35, 61.88) * mm, "end": v(-7.26, 61.79) * mm});
            skLineSegment(sketch, "E3853", {"start": v(-6.98, 61.52) * mm, "end": v(-6.88, 61.44) * mm});
            skLineSegment(sketch, "E3854", {"start": v(-6.77, 61.36) * mm, "end": v(-6.66, 61.29) * mm});
            skLineSegment(sketch, "E3855", {"start": v(-6.66, 61.29) * mm, "end": v(-6.55, 61.22) * mm});
            skLineSegment(sketch, "E3856", {"start": v(-6.55, 61.22) * mm, "end": v(-6.44, 61.15) * mm});
            skLineSegment(sketch, "E3857", {"start": v(-6.44, 61.15) * mm, "end": v(-6.33, 61.09) * mm});
            skLineSegment(sketch, "E3858", {"start": v(-6.33, 61.09) * mm, "end": v(-6.21, 61.03) * mm});
            skLineSegment(sketch, "E3859", {"start": v(-6.21, 61.03) * mm, "end": v(-6.1, 60.97) * mm});
            skLineSegment(sketch, "E3860", {"start": v(-6.1, 60.97) * mm, "end": v(-5.97, 60.92) * mm});
            skLineSegment(sketch, "E3861", {"start": v(-5.97, 60.92) * mm, "end": v(-5.85, 60.88) * mm});
            skLineSegment(sketch, "E3862", {"start": v(-5.73, 60.83) * mm, "end": v(-5.6, 60.8) * mm});
            skLineSegment(sketch, "E3863", {"start": v(-5.6, 60.8) * mm, "end": v(-5.48, 60.76) * mm});
            skLineSegment(sketch, "E3864", {"start": v(-5.48, 60.76) * mm, "end": v(-5.35, 60.73) * mm});
            skLineSegment(sketch, "E3865", {"start": v(-5.35, 60.73) * mm, "end": v(-5.23, 60.7) * mm});
            skLineSegment(sketch, "E3866", {"start": v(-5.23, 60.7) * mm, "end": v(-5.1, 60.69) * mm});
            skLineSegment(sketch, "E3867", {"start": v(-5.1, 60.69) * mm, "end": v(-4.97, 60.67) * mm});
            skLineSegment(sketch, "E3868", {"start": v(-4.97, 60.67) * mm, "end": v(-4.84, 60.66) * mm});
            skLineSegment(sketch, "E3869", {"start": v(-4.84, 60.66) * mm, "end": v(-4.7, 60.65) * mm});
            skLineSegment(sketch, "E3870", {"start": v(-4.7, 60.65) * mm, "end": v(-4.58, 60.65) * mm});
            skLineSegment(sketch, "E3871", {"start": v(-64.58, 63.15) * mm, "end": v(-64.53, 63.15) * mm});
            skLineSegment(sketch, "E3872", {"start": v(-64.53, 63.15) * mm, "end": v(-64.5, 63.16) * mm});
            skLineSegment(sketch, "E3873", {"start": v(-64.5, 63.16) * mm, "end": v(-64.45, 63.16) * mm});
            skLineSegment(sketch, "E3874", {"start": v(-64.45, 63.16) * mm, "end": v(-64.4, 63.16) * mm});
            skLineSegment(sketch, "E3875", {"start": v(-64.4, 63.16) * mm, "end": v(-64.36, 63.17) * mm});
            skLineSegment(sketch, "E3876", {"start": v(-64.36, 63.17) * mm, "end": v(-64.32, 63.18) * mm});
            skLineSegment(sketch, "E3877", {"start": v(-64.32, 63.18) * mm, "end": v(-64.28, 63.19) * mm});
            skLineSegment(sketch, "E3878", {"start": v(-64.28, 63.19) * mm, "end": v(-64.23, 63.2) * mm});
            skLineSegment(sketch, "E3879", {"start": v(-64.23, 63.2) * mm, "end": v(-64.2, 63.21) * mm});
            skLineSegment(sketch, "E3880", {"start": v(-64.2, 63.21) * mm, "end": v(-64.15, 63.23) * mm});
            skLineSegment(sketch, "E3881", {"start": v(-64.15, 63.23) * mm, "end": v(-64.11, 63.24) * mm});
            skLineSegment(sketch, "E3882", {"start": v(-64.11, 63.24) * mm, "end": v(-64.07, 63.26) * mm});
            skLineSegment(sketch, "E3883", {"start": v(-64.07, 63.26) * mm, "end": v(-64.03, 63.28) * mm});
            skLineSegment(sketch, "E3884", {"start": v(-64.03, 63.28) * mm, "end": v(-64, 63.3) * mm});
            skLineSegment(sketch, "E3885", {"start": v(-64, 63.3) * mm, "end": v(-63.96, 63.32) * mm});
            skLineSegment(sketch, "E3886", {"start": v(-63.96, 63.32) * mm, "end": v(-63.92, 63.34) * mm});
            skLineSegment(sketch, "E3887", {"start": v(-63.92, 63.34) * mm, "end": v(-63.88, 63.36) * mm});
            skLineSegment(sketch, "E3888", {"start": v(-63.88, 63.36) * mm, "end": v(-63.85, 63.39) * mm});
            skLineSegment(sketch, "E3889", {"start": v(-63.85, 63.39) * mm, "end": v(-63.81, 63.41) * mm});
            skLineSegment(sketch, "E3890", {"start": v(-63.78, 63.44) * mm, "end": v(-63.74, 63.47) * mm});
            skLineSegment(sketch, "E3891", {"start": v(-63.74, 63.47) * mm, "end": v(-63.71, 63.5) * mm});
            skLineSegment(sketch, "E3892", {"start": v(-63.71, 63.5) * mm, "end": v(-63.68, 63.53) * mm});
            skLineSegment(sketch, "E3893", {"start": v(-63.68, 63.53) * mm, "end": v(-63.65, 63.56) * mm});
            skLineSegment(sketch, "E3894", {"start": v(-63.65, 63.56) * mm, "end": v(-63.62, 63.6) * mm});
            skLineSegment(sketch, "E3895", {"start": v(-63.62, 63.6) * mm, "end": v(-63.6, 63.63) * mm});
            skLineSegment(sketch, "E3896", {"start": v(-63.6, 63.63) * mm, "end": v(-63.57, 63.66) * mm});
            skLineSegment(sketch, "E3897", {"start": v(-63.57, 63.66) * mm, "end": v(-63.54, 63.7) * mm});
            skLineSegment(sketch, "E3898", {"start": v(-63.54, 63.7) * mm, "end": v(-63.52, 63.73) * mm});
            skLineSegment(sketch, "E3899", {"start": v(-63.52, 63.73) * mm, "end": v(-63.5, 63.77) * mm});
            skLineSegment(sketch, "E3900", {"start": v(-63.5, 63.77) * mm, "end": v(-63.48, 63.8) * mm});
            skLineSegment(sketch, "E3901", {"start": v(-63.48, 63.8) * mm, "end": v(-63.46, 63.85) * mm});
            skLineSegment(sketch, "E3902", {"start": v(-63.46, 63.85) * mm, "end": v(-63.44, 63.89) * mm});
            skLineSegment(sketch, "E3903", {"start": v(-63.44, 63.89) * mm, "end": v(-63.42, 63.93) * mm});
            skLineSegment(sketch, "E3904", {"start": v(-63.42, 63.93) * mm, "end": v(-63.4, 63.97) * mm});
            skLineSegment(sketch, "E3905", {"start": v(-63.4, 63.97) * mm, "end": v(-63.4, 64) * mm});
            skLineSegment(sketch, "E3906", {"start": v(-63.4, 64) * mm, "end": v(-63.38, 64.05) * mm});
            skLineSegment(sketch, "E3907", {"start": v(-63.38, 64.05) * mm, "end": v(-63.37, 64.1) * mm});
            skLineSegment(sketch, "E3908", {"start": v(-63.37, 64.1) * mm, "end": v(-63.36, 64.13) * mm});
            skLineSegment(sketch, "E3909", {"start": v(-63.36, 64.13) * mm, "end": v(-63.35, 64.18) * mm});
            skLineSegment(sketch, "E3910", {"start": v(-63.35, 64.18) * mm, "end": v(-63.34, 64.22) * mm});
            skLineSegment(sketch, "E3911", {"start": v(-63.34, 64.22) * mm, "end": v(-63.34, 64.26) * mm});
            skLineSegment(sketch, "E3912", {"start": v(-63.34, 64.26) * mm, "end": v(-63.33, 64.3) * mm});
            skLineSegment(sketch, "E3913", {"start": v(-63.33, 64.3) * mm, "end": v(-63.33, 64.35) * mm});
            skLineSegment(sketch, "E3914", {"start": v(-63.33, 64.48) * mm, "end": v(-63.33, 64.52) * mm});
            skLineSegment(sketch, "E3915", {"start": v(-63.33, 64.52) * mm, "end": v(-63.34, 64.56) * mm});
            skLineSegment(sketch, "E3916", {"start": v(-63.34, 64.56) * mm, "end": v(-63.34, 64.6) * mm});
            skLineSegment(sketch, "E3917", {"start": v(-63.34, 64.6) * mm, "end": v(-63.35, 64.65) * mm});
            skLineSegment(sketch, "E3918", {"start": v(-63.36, 64.7) * mm, "end": v(-63.37, 64.73) * mm});
            skLineSegment(sketch, "E3919", {"start": v(-63.37, 64.73) * mm, "end": v(-63.38, 64.78) * mm});
            skLineSegment(sketch, "E3920", {"start": v(-63.38, 64.78) * mm, "end": v(-63.4, 64.82) * mm});
            skLineSegment(sketch, "E3921", {"start": v(-63.4, 64.82) * mm, "end": v(-63.41, 64.86) * mm});
            skLineSegment(sketch, "E3922", {"start": v(-63.41, 64.86) * mm, "end": v(-63.43, 64.9) * mm});
            skLineSegment(sketch, "E3923", {"start": v(-63.43, 64.9) * mm, "end": v(-63.45, 64.94) * mm});
            skLineSegment(sketch, "E3924", {"start": v(-63.45, 64.94) * mm, "end": v(-63.47, 64.98) * mm});
            skLineSegment(sketch, "E3925", {"start": v(-63.47, 64.98) * mm, "end": v(-63.49, 65.02) * mm});
            skLineSegment(sketch, "E3926", {"start": v(-63.49, 65.02) * mm, "end": v(-63.5, 65.05) * mm});
            skLineSegment(sketch, "E3927", {"start": v(-63.5, 65.05) * mm, "end": v(-63.53, 65.09) * mm});
            skLineSegment(sketch, "E3928", {"start": v(-63.53, 65.09) * mm, "end": v(-63.56, 65.13) * mm});
            skLineSegment(sketch, "E3929", {"start": v(-63.58, 65.16) * mm, "end": v(-63.6, 65.2) * mm});
            skLineSegment(sketch, "E3930", {"start": v(-63.6, 65.2) * mm, "end": v(-63.64, 65.23) * mm});
            skLineSegment(sketch, "E3931", {"start": v(-63.64, 65.23) * mm, "end": v(-63.67, 65.26) * mm});
            skLineSegment(sketch, "E3932", {"start": v(-63.67, 65.26) * mm, "end": v(-63.7, 65.3) * mm});
            skLineSegment(sketch, "E3933", {"start": v(-63.7, 65.3) * mm, "end": v(-63.73, 65.32) * mm});
            skLineSegment(sketch, "E3934", {"start": v(-63.73, 65.32) * mm, "end": v(-63.76, 65.35) * mm});
            skLineSegment(sketch, "E3935", {"start": v(-63.76, 65.35) * mm, "end": v(-63.8, 65.38) * mm});
            skLineSegment(sketch, "E3936", {"start": v(-63.8, 65.38) * mm, "end": v(-63.83, 65.4) * mm});
            skLineSegment(sketch, "E3937", {"start": v(-63.83, 65.4) * mm, "end": v(-63.86, 65.43) * mm});
            skLineSegment(sketch, "E3938", {"start": v(-63.86, 65.43) * mm, "end": v(-63.9, 65.45) * mm});
            skLineSegment(sketch, "E3939", {"start": v(-63.9, 65.45) * mm, "end": v(-63.94, 65.48) * mm});
            skLineSegment(sketch, "E3940", {"start": v(-63.94, 65.48) * mm, "end": v(-63.97, 65.5) * mm});
            skLineSegment(sketch, "E3941", {"start": v(-63.97, 65.5) * mm, "end": v(-64.01, 65.52) * mm});
            skLineSegment(sketch, "E3942", {"start": v(-64.01, 65.52) * mm, "end": v(-64.05, 65.54) * mm});
            skLineSegment(sketch, "E3943", {"start": v(-64.05, 65.54) * mm, "end": v(-64.1, 65.55) * mm});
            skLineSegment(sketch, "E3944", {"start": v(-64.1, 65.55) * mm, "end": v(-64.13, 65.57) * mm});
            skLineSegment(sketch, "E3945", {"start": v(-64.17, 65.59) * mm, "end": v(-64.21, 65.6) * mm});
            skLineSegment(sketch, "E3946", {"start": v(-64.21, 65.6) * mm, "end": v(-64.26, 65.61) * mm});
            skLineSegment(sketch, "E3947", {"start": v(-64.26, 65.61) * mm, "end": v(-64.3, 65.62) * mm});
            skLineSegment(sketch, "E3948", {"start": v(-64.3, 65.62) * mm, "end": v(-64.34, 65.63) * mm});
            skLineSegment(sketch, "E3949", {"start": v(-64.34, 65.63) * mm, "end": v(-64.38, 65.64) * mm});
            skLineSegment(sketch, "E3950", {"start": v(-64.43, 65.64) * mm, "end": v(-64.47, 65.65) * mm});
            skLineSegment(sketch, "E3951", {"start": v(-64.47, 65.65) * mm, "end": v(-64.51, 65.65) * mm});
            skLineSegment(sketch, "E3952", {"start": v(-64.51, 65.65) * mm, "end": v(-64.56, 65.65) * mm});
            skLineSegment(sketch, "E3953", {"start": v(-64.56, 65.65) * mm, "end": v(-64.6, 65.65) * mm});
            skLineSegment(sketch, "E3954", {"start": v(-64.6, 65.65) * mm, "end": v(-64.64, 65.65) * mm});
            skLineSegment(sketch, "E3955", {"start": v(-64.64, 65.65) * mm, "end": v(-64.69, 65.65) * mm});
            skLineSegment(sketch, "E3956", {"start": v(-64.69, 65.65) * mm, "end": v(-64.73, 65.64) * mm});
            skLineSegment(sketch, "E3957", {"start": v(-64.73, 65.64) * mm, "end": v(-64.77, 65.64) * mm});
            skLineSegment(sketch, "E3958", {"start": v(-64.77, 65.64) * mm, "end": v(-64.81, 65.63) * mm});
            skLineSegment(sketch, "E3959", {"start": v(-64.81, 65.63) * mm, "end": v(-64.86, 65.62) * mm});
            skLineSegment(sketch, "E3960", {"start": v(-64.86, 65.62) * mm, "end": v(-64.9, 65.61) * mm});
            skLineSegment(sketch, "E3961", {"start": v(-64.9, 65.61) * mm, "end": v(-64.94, 65.6) * mm});
            skLineSegment(sketch, "E3962", {"start": v(-64.94, 65.6) * mm, "end": v(-64.98, 65.59) * mm});
            skLineSegment(sketch, "E3963", {"start": v(-65.02, 65.57) * mm, "end": v(-65.06, 65.55) * mm});
            skLineSegment(sketch, "E3964", {"start": v(-65.06, 65.55) * mm, "end": v(-65.1, 65.54) * mm});
            skLineSegment(sketch, "E3965", {"start": v(-65.1, 65.54) * mm, "end": v(-65.14, 65.52) * mm});
            skLineSegment(sketch, "E3966", {"start": v(-65.14, 65.52) * mm, "end": v(-65.18, 65.5) * mm});
            skLineSegment(sketch, "E3967", {"start": v(-65.18, 65.5) * mm, "end": v(-65.22, 65.48) * mm});
            skLineSegment(sketch, "E3968", {"start": v(-65.25, 65.45) * mm, "end": v(-65.3, 65.43) * mm});
            skLineSegment(sketch, "E3969", {"start": v(-65.3, 65.43) * mm, "end": v(-65.33, 65.4) * mm});
            skLineSegment(sketch, "E3970", {"start": v(-65.33, 65.4) * mm, "end": v(-65.36, 65.38) * mm});
            skLineSegment(sketch, "E3971", {"start": v(-65.36, 65.38) * mm, "end": v(-65.4, 65.35) * mm});
            skLineSegment(sketch, "E3972", {"start": v(-65.4, 65.35) * mm, "end": v(-65.43, 65.32) * mm});
            skLineSegment(sketch, "E3973", {"start": v(-65.43, 65.32) * mm, "end": v(-65.46, 65.3) * mm});
            skLineSegment(sketch, "E3974", {"start": v(-65.46, 65.3) * mm, "end": v(-65.49, 65.26) * mm});
            skLineSegment(sketch, "E3975", {"start": v(-65.49, 65.26) * mm, "end": v(-65.52, 65.23) * mm});
            skLineSegment(sketch, "E3976", {"start": v(-65.52, 65.23) * mm, "end": v(-65.54, 65.2) * mm});
            skLineSegment(sketch, "E3977", {"start": v(-65.54, 65.2) * mm, "end": v(-65.57, 65.16) * mm});
            skLineSegment(sketch, "E3978", {"start": v(-65.57, 65.16) * mm, "end": v(-65.6, 65.13) * mm});
            skLineSegment(sketch, "E3979", {"start": v(-65.6, 65.13) * mm, "end": v(-65.62, 65.09) * mm});
            skLineSegment(sketch, "E3980", {"start": v(-65.62, 65.09) * mm, "end": v(-65.65, 65.05) * mm});
            skLineSegment(sketch, "E3981", {"start": v(-65.65, 65.05) * mm, "end": v(-65.67, 65.02) * mm});
            skLineSegment(sketch, "E3982", {"start": v(-65.67, 65.02) * mm, "end": v(-65.69, 64.98) * mm});
            skLineSegment(sketch, "E3983", {"start": v(-65.69, 64.98) * mm, "end": v(-65.7, 64.94) * mm});
            skLineSegment(sketch, "E3984", {"start": v(-65.7, 64.94) * mm, "end": v(-65.72, 64.9) * mm});
            skLineSegment(sketch, "E3985", {"start": v(-65.72, 64.9) * mm, "end": v(-65.74, 64.86) * mm});
            skLineSegment(sketch, "E3986", {"start": v(-65.74, 64.86) * mm, "end": v(-65.76, 64.82) * mm});
            skLineSegment(sketch, "E3987", {"start": v(-65.76, 64.82) * mm, "end": v(-65.77, 64.78) * mm});
            skLineSegment(sketch, "E3988", {"start": v(-65.77, 64.78) * mm, "end": v(-65.78, 64.73) * mm});
            skLineSegment(sketch, "E3989", {"start": v(-65.78, 64.73) * mm, "end": v(-65.8, 64.7) * mm});
            skLineSegment(sketch, "E3990", {"start": v(-65.8, 64.7) * mm, "end": v(-65.8, 64.65) * mm});
            skLineSegment(sketch, "E3991", {"start": v(-65.8, 64.65) * mm, "end": v(-65.81, 64.6) * mm});
            skLineSegment(sketch, "E3992", {"start": v(-65.81, 64.6) * mm, "end": v(-65.82, 64.56) * mm});
            skLineSegment(sketch, "E3993", {"start": v(-65.82, 64.52) * mm, "end": v(-65.83, 64.48) * mm});
            skLineSegment(sketch, "E3994", {"start": v(-65.83, 64.48) * mm, "end": v(-65.83, 64.44) * mm});
            skLineSegment(sketch, "E3995", {"start": v(-65.83, 64.35) * mm, "end": v(-65.82, 64.3) * mm});
            skLineSegment(sketch, "E3996", {"start": v(-65.82, 64.3) * mm, "end": v(-65.82, 64.26) * mm});
            skLineSegment(sketch, "E3997", {"start": v(-65.82, 64.26) * mm, "end": v(-65.81, 64.22) * mm});
            skLineSegment(sketch, "E3998", {"start": v(-65.81, 64.22) * mm, "end": v(-65.8, 64.18) * mm});
            skLineSegment(sketch, "E3999", {"start": v(-65.79, 64.1) * mm, "end": v(-65.78, 64.05) * mm});
            skLineSegment(sketch, "E4000", {"start": v(-65.78, 64.05) * mm, "end": v(-65.76, 64) * mm});
            skLineSegment(sketch, "E4001", {"start": v(-65.76, 64) * mm, "end": v(-65.75, 63.97) * mm});
            skLineSegment(sketch, "E4002", {"start": v(-65.75, 63.97) * mm, "end": v(-65.73, 63.93) * mm});
            skLineSegment(sketch, "E4003", {"start": v(-65.73, 63.93) * mm, "end": v(-65.72, 63.89) * mm});
            skLineSegment(sketch, "E4004", {"start": v(-65.72, 63.89) * mm, "end": v(-65.7, 63.85) * mm});
            skLineSegment(sketch, "E4005", {"start": v(-65.7, 63.85) * mm, "end": v(-65.68, 63.8) * mm});
            skLineSegment(sketch, "E4006", {"start": v(-65.68, 63.8) * mm, "end": v(-65.66, 63.77) * mm});
            skLineSegment(sketch, "E4007", {"start": v(-65.66, 63.77) * mm, "end": v(-65.63, 63.73) * mm});
            skLineSegment(sketch, "E4008", {"start": v(-65.63, 63.73) * mm, "end": v(-65.6, 63.7) * mm});
            skLineSegment(sketch, "E4009", {"start": v(-65.6, 63.7) * mm, "end": v(-65.58, 63.66) * mm});
            skLineSegment(sketch, "E4010", {"start": v(-65.58, 63.66) * mm, "end": v(-65.56, 63.63) * mm});
            skLineSegment(sketch, "E4011", {"start": v(-65.56, 63.63) * mm, "end": v(-65.53, 63.6) * mm});
            skLineSegment(sketch, "E4012", {"start": v(-65.53, 63.6) * mm, "end": v(-65.5, 63.56) * mm});
            skLineSegment(sketch, "E4013", {"start": v(-65.5, 63.56) * mm, "end": v(-65.47, 63.53) * mm});
            skLineSegment(sketch, "E4014", {"start": v(-65.47, 63.53) * mm, "end": v(-65.44, 63.5) * mm});
            skLineSegment(sketch, "E4015", {"start": v(-65.44, 63.5) * mm, "end": v(-65.41, 63.47) * mm});
            skLineSegment(sketch, "E4016", {"start": v(-65.34, 63.41) * mm, "end": v(-65.3, 63.39) * mm});
            skLineSegment(sketch, "E4017", {"start": v(-65.3, 63.39) * mm, "end": v(-65.27, 63.36) * mm});
            skLineSegment(sketch, "E4018", {"start": v(-65.27, 63.36) * mm, "end": v(-65.24, 63.34) * mm});
            skLineSegment(sketch, "E4019", {"start": v(-65.24, 63.34) * mm, "end": v(-65.2, 63.32) * mm});
            skLineSegment(sketch, "E4020", {"start": v(-65.2, 63.32) * mm, "end": v(-65.16, 63.3) * mm});
            skLineSegment(sketch, "E4021", {"start": v(-65.16, 63.3) * mm, "end": v(-65.12, 63.28) * mm});
            skLineSegment(sketch, "E4022", {"start": v(-65.12, 63.28) * mm, "end": v(-65.08, 63.26) * mm});
            skLineSegment(sketch, "E4023", {"start": v(-65.08, 63.26) * mm, "end": v(-65.04, 63.24) * mm});
            skLineSegment(sketch, "E4024", {"start": v(-65.04, 63.24) * mm, "end": v(-65, 63.23) * mm});
            skLineSegment(sketch, "E4025", {"start": v(-65, 63.23) * mm, "end": v(-64.96, 63.21) * mm});
            skLineSegment(sketch, "E4026", {"start": v(-64.96, 63.21) * mm, "end": v(-64.92, 63.2) * mm});
            skLineSegment(sketch, "E4027", {"start": v(-64.92, 63.2) * mm, "end": v(-64.88, 63.19) * mm});
            skLineSegment(sketch, "E4028", {"start": v(-64.88, 63.19) * mm, "end": v(-64.84, 63.18) * mm});
            skLineSegment(sketch, "E4029", {"start": v(-64.84, 63.18) * mm, "end": v(-64.8, 63.17) * mm});
            skLineSegment(sketch, "E4030", {"start": v(-64.8, 63.17) * mm, "end": v(-64.75, 63.16) * mm});
            skLineSegment(sketch, "E4031", {"start": v(-64.75, 63.16) * mm, "end": v(-64.7, 63.16) * mm});
            skLineSegment(sketch, "E4032", {"start": v(-64.7, 63.16) * mm, "end": v(-64.66, 63.16) * mm});
            skLineSegment(sketch, "E4033", {"start": v(-64.66, 63.16) * mm, "end": v(-64.62, 63.15) * mm});
            skLineSegment(sketch, "E4034", {"start": v(-64.62, 63.15) * mm, "end": v(-64.58, 63.15) * mm});
            skLineSegment(sketch, "E4035", {"start": v(-32.08, 63.15) * mm, "end": v(-32.03, 63.15) * mm});
            skLineSegment(sketch, "E4036", {"start": v(-32.03, 63.15) * mm, "end": v(-32, 63.16) * mm});
            skLineSegment(sketch, "E4037", {"start": v(-32, 63.16) * mm, "end": v(-31.95, 63.16) * mm});
            skLineSegment(sketch, "E4038", {"start": v(-31.95, 63.16) * mm, "end": v(-31.9, 63.16) * mm});
            skLineSegment(sketch, "E4039", {"start": v(-31.9, 63.16) * mm, "end": v(-31.86, 63.17) * mm});
            skLineSegment(sketch, "E4040", {"start": v(-31.86, 63.17) * mm, "end": v(-31.82, 63.18) * mm});
            skLineSegment(sketch, "E4041", {"start": v(-31.78, 63.19) * mm, "end": v(-31.73, 63.2) * mm});
            skLineSegment(sketch, "E4042", {"start": v(-31.73, 63.2) * mm, "end": v(-31.7, 63.21) * mm});
            skLineSegment(sketch, "E4043", {"start": v(-31.7, 63.21) * mm, "end": v(-31.65, 63.23) * mm});
            skLineSegment(sketch, "E4044", {"start": v(-31.65, 63.23) * mm, "end": v(-31.61, 63.24) * mm});
            skLineSegment(sketch, "E4045", {"start": v(-31.61, 63.24) * mm, "end": v(-31.57, 63.26) * mm});
            skLineSegment(sketch, "E4046", {"start": v(-31.57, 63.26) * mm, "end": v(-31.53, 63.28) * mm});
            skLineSegment(sketch, "E4047", {"start": v(-31.53, 63.28) * mm, "end": v(-31.5, 63.3) * mm});
            skLineSegment(sketch, "E4048", {"start": v(-31.5, 63.3) * mm, "end": v(-31.46, 63.32) * mm});
            skLineSegment(sketch, "E4049", {"start": v(-31.46, 63.32) * mm, "end": v(-31.42, 63.34) * mm});
            skLineSegment(sketch, "E4050", {"start": v(-31.42, 63.34) * mm, "end": v(-31.38, 63.36) * mm});
            skLineSegment(sketch, "E4051", {"start": v(-31.38, 63.36) * mm, "end": v(-31.35, 63.39) * mm});
            skLineSegment(sketch, "E4052", {"start": v(-31.35, 63.39) * mm, "end": v(-31.31, 63.41) * mm});
            skLineSegment(sketch, "E4053", {"start": v(-31.31, 63.41) * mm, "end": v(-31.28, 63.44) * mm});
            skLineSegment(sketch, "E4054", {"start": v(-31.28, 63.44) * mm, "end": v(-31.24, 63.47) * mm});
            skLineSegment(sketch, "E4055", {"start": v(-31.24, 63.47) * mm, "end": v(-31.21, 63.5) * mm});
            skLineSegment(sketch, "E4056", {"start": v(-31.21, 63.5) * mm, "end": v(-31.18, 63.53) * mm});
            skLineSegment(sketch, "E4057", {"start": v(-31.18, 63.53) * mm, "end": v(-31.15, 63.56) * mm});
            skLineSegment(sketch, "E4058", {"start": v(-31.15, 63.56) * mm, "end": v(-31.12, 63.6) * mm});
            skLineSegment(sketch, "E4059", {"start": v(-31.12, 63.6) * mm, "end": v(-31.1, 63.63) * mm});
            skLineSegment(sketch, "E4060", {"start": v(-31.1, 63.63) * mm, "end": v(-31.07, 63.66) * mm});
            skLineSegment(sketch, "E4061", {"start": v(-31.07, 63.66) * mm, "end": v(-31.04, 63.7) * mm});
            skLineSegment(sketch, "E4062", {"start": v(-31.04, 63.7) * mm, "end": v(-31.02, 63.73) * mm});
            skLineSegment(sketch, "E4063", {"start": v(-31.02, 63.73) * mm, "end": v(-31, 63.77) * mm});
            skLineSegment(sketch, "E4064", {"start": v(-31, 63.77) * mm, "end": v(-30.98, 63.8) * mm});
            skLineSegment(sketch, "E4065", {"start": v(-30.98, 63.8) * mm, "end": v(-30.96, 63.85) * mm});
            skLineSegment(sketch, "E4066", {"start": v(-30.96, 63.85) * mm, "end": v(-30.94, 63.89) * mm});
            skLineSegment(sketch, "E4067", {"start": v(-30.94, 63.89) * mm, "end": v(-30.92, 63.93) * mm});
            skLineSegment(sketch, "E4068", {"start": v(-30.92, 63.93) * mm, "end": v(-30.9, 63.97) * mm});
            skLineSegment(sketch, "E4069", {"start": v(-30.88, 64.05) * mm, "end": v(-30.87, 64.1) * mm});
            skLineSegment(sketch, "E4070", {"start": v(-30.87, 64.1) * mm, "end": v(-30.86, 64.13) * mm});
            skLineSegment(sketch, "E4071", {"start": v(-30.86, 64.13) * mm, "end": v(-30.85, 64.18) * mm});
            skLineSegment(sketch, "E4072", {"start": v(-30.85, 64.65) * mm, "end": v(-30.86, 64.7) * mm});
            skLineSegment(sketch, "E4073", {"start": v(-30.86, 64.7) * mm, "end": v(-30.87, 64.73) * mm});
            skLineSegment(sketch, "E4074", {"start": v(-30.87, 64.73) * mm, "end": v(-30.88, 64.78) * mm});
            skLineSegment(sketch, "E4075", {"start": v(-30.88, 64.78) * mm, "end": v(-30.9, 64.82) * mm});
            skLineSegment(sketch, "E4076", {"start": v(-30.9, 64.82) * mm, "end": v(-30.91, 64.86) * mm});
            skLineSegment(sketch, "E4077", {"start": v(-30.93, 64.9) * mm, "end": v(-30.95, 64.94) * mm});
            skLineSegment(sketch, "E4078", {"start": v(-30.95, 64.94) * mm, "end": v(-30.97, 64.98) * mm});
            skLineSegment(sketch, "E4079", {"start": v(-30.97, 64.98) * mm, "end": v(-30.99, 65.02) * mm});
            skLineSegment(sketch, "E4080", {"start": v(-30.99, 65.02) * mm, "end": v(-31, 65.05) * mm});
            skLineSegment(sketch, "E4081", {"start": v(-31, 65.05) * mm, "end": v(-31.03, 65.09) * mm});
            skLineSegment(sketch, "E4082", {"start": v(-31.03, 65.09) * mm, "end": v(-31.06, 65.13) * mm});
            skLineSegment(sketch, "E4083", {"start": v(-31.06, 65.13) * mm, "end": v(-31.08, 65.16) * mm});
            skLineSegment(sketch, "E4084", {"start": v(-31.08, 65.16) * mm, "end": v(-31.1, 65.2) * mm});
            skLineSegment(sketch, "E4085", {"start": v(-31.1, 65.2) * mm, "end": v(-31.14, 65.23) * mm});
            skLineSegment(sketch, "E4086", {"start": v(-31.14, 65.23) * mm, "end": v(-31.17, 65.26) * mm});
            skLineSegment(sketch, "E4087", {"start": v(-31.17, 65.26) * mm, "end": v(-31.2, 65.3) * mm});
            skLineSegment(sketch, "E4088", {"start": v(-31.2, 65.3) * mm, "end": v(-31.23, 65.32) * mm});
            skLineSegment(sketch, "E4089", {"start": v(-31.23, 65.32) * mm, "end": v(-31.26, 65.35) * mm});
            skLineSegment(sketch, "E4090", {"start": v(-31.26, 65.35) * mm, "end": v(-31.3, 65.38) * mm});
            skLineSegment(sketch, "E4091", {"start": v(-31.3, 65.38) * mm, "end": v(-31.33, 65.4) * mm});
            skLineSegment(sketch, "E4092", {"start": v(-31.36, 65.43) * mm, "end": v(-31.4, 65.45) * mm});
            skLineSegment(sketch, "E4093", {"start": v(-31.4, 65.45) * mm, "end": v(-31.44, 65.48) * mm});
            skLineSegment(sketch, "E4094", {"start": v(-31.44, 65.48) * mm, "end": v(-31.47, 65.5) * mm});
            skLineSegment(sketch, "E4095", {"start": v(-31.47, 65.5) * mm, "end": v(-31.51, 65.52) * mm});
            skLineSegment(sketch, "E4096", {"start": v(-31.51, 65.52) * mm, "end": v(-31.55, 65.54) * mm});
            skLineSegment(sketch, "E4097", {"start": v(-31.55, 65.54) * mm, "end": v(-31.6, 65.55) * mm});
            skLineSegment(sketch, "E4098", {"start": v(-31.6, 65.55) * mm, "end": v(-31.63, 65.57) * mm});
            skLineSegment(sketch, "E4099", {"start": v(-31.63, 65.57) * mm, "end": v(-31.67, 65.59) * mm});
            skLineSegment(sketch, "E4100", {"start": v(-31.67, 65.59) * mm, "end": v(-31.71, 65.6) * mm});
            skLineSegment(sketch, "E4101", {"start": v(-31.71, 65.6) * mm, "end": v(-31.76, 65.61) * mm});
            skLineSegment(sketch, "E4102", {"start": v(-31.76, 65.61) * mm, "end": v(-31.8, 65.62) * mm});
            skLineSegment(sketch, "E4103", {"start": v(-31.8, 65.62) * mm, "end": v(-31.84, 65.63) * mm});
            skLineSegment(sketch, "E4104", {"start": v(-31.84, 65.63) * mm, "end": v(-31.88, 65.64) * mm});
            skLineSegment(sketch, "E4105", {"start": v(-31.88, 65.64) * mm, "end": v(-31.93, 65.64) * mm});
            skLineSegment(sketch, "E4106", {"start": v(-31.93, 65.64) * mm, "end": v(-31.97, 65.65) * mm});
            skLineSegment(sketch, "E4107", {"start": v(-31.97, 65.65) * mm, "end": v(-32.01, 65.65) * mm});
            skLineSegment(sketch, "E4108", {"start": v(-32.01, 65.65) * mm, "end": v(-32.06, 65.65) * mm});
            skLineSegment(sketch, "E4109", {"start": v(-32.06, 65.65) * mm, "end": v(-32.1, 65.65) * mm});
            skLineSegment(sketch, "E4110", {"start": v(-32.1, 65.65) * mm, "end": v(-32.14, 65.65) * mm});
            skLineSegment(sketch, "E4111", {"start": v(-32.19, 65.65) * mm, "end": v(-32.23, 65.64) * mm});
            skLineSegment(sketch, "E4112", {"start": v(-32.23, 65.64) * mm, "end": v(-32.27, 65.64) * mm});
            skLineSegment(sketch, "E4113", {"start": v(-32.27, 65.64) * mm, "end": v(-32.31, 65.63) * mm});
            skLineSegment(sketch, "E4114", {"start": v(-32.4, 65.61) * mm, "end": v(-32.44, 65.6) * mm});
            skLineSegment(sketch, "E4115", {"start": v(-32.44, 65.6) * mm, "end": v(-32.48, 65.59) * mm});
            skLineSegment(sketch, "E4116", {"start": v(-32.48, 65.59) * mm, "end": v(-32.52, 65.57) * mm});
            skLineSegment(sketch, "E4117", {"start": v(-32.52, 65.57) * mm, "end": v(-32.56, 65.55) * mm});
            skLineSegment(sketch, "E4118", {"start": v(-32.56, 65.55) * mm, "end": v(-32.6, 65.54) * mm});
            skLineSegment(sketch, "E4119", {"start": v(-32.6, 65.54) * mm, "end": v(-32.64, 65.52) * mm});
            skLineSegment(sketch, "E4120", {"start": v(-32.64, 65.52) * mm, "end": v(-32.68, 65.5) * mm});
            skLineSegment(sketch, "E4121", {"start": v(-32.68, 65.5) * mm, "end": v(-32.72, 65.48) * mm});
            skLineSegment(sketch, "E4122", {"start": v(-32.72, 65.48) * mm, "end": v(-32.75, 65.45) * mm});
            skLineSegment(sketch, "E4123", {"start": v(-32.8, 65.43) * mm, "end": v(-32.83, 65.4) * mm});
            skLineSegment(sketch, "E4124", {"start": v(-32.83, 65.4) * mm, "end": v(-32.86, 65.38) * mm});
            skLineSegment(sketch, "E4125", {"start": v(-32.86, 65.38) * mm, "end": v(-32.9, 65.35) * mm});
            skLineSegment(sketch, "E4126", {"start": v(-32.9, 65.35) * mm, "end": v(-32.93, 65.32) * mm});
            skLineSegment(sketch, "E4127", {"start": v(-32.93, 65.32) * mm, "end": v(-32.96, 65.3) * mm});
            skLineSegment(sketch, "E4128", {"start": v(-32.96, 65.3) * mm, "end": v(-32.99, 65.26) * mm});
            skLineSegment(sketch, "E4129", {"start": v(-32.99, 65.26) * mm, "end": v(-33.02, 65.23) * mm});
            skLineSegment(sketch, "E4130", {"start": v(-33.02, 65.23) * mm, "end": v(-33.04, 65.2) * mm});
            skLineSegment(sketch, "E4131", {"start": v(-33.04, 65.2) * mm, "end": v(-33.07, 65.16) * mm});
            skLineSegment(sketch, "E4132", {"start": v(-33.07, 65.16) * mm, "end": v(-33.1, 65.13) * mm});
            skLineSegment(sketch, "E4133", {"start": v(-33.1, 65.13) * mm, "end": v(-33.12, 65.09) * mm});
            skLineSegment(sketch, "E4134", {"start": v(-33.12, 65.09) * mm, "end": v(-33.15, 65.05) * mm});
            skLineSegment(sketch, "E4135", {"start": v(-33.15, 65.05) * mm, "end": v(-33.17, 65.02) * mm});
            skLineSegment(sketch, "E4136", {"start": v(-33.17, 65.02) * mm, "end": v(-33.19, 64.98) * mm});
            skLineSegment(sketch, "E4137", {"start": v(-33.19, 64.98) * mm, "end": v(-33.2, 64.94) * mm});
            skLineSegment(sketch, "E4138", {"start": v(-33.2, 64.94) * mm, "end": v(-33.22, 64.9) * mm});
            skLineSegment(sketch, "E4139", {"start": v(-33.22, 64.9) * mm, "end": v(-33.24, 64.86) * mm});
            skLineSegment(sketch, "E4140", {"start": v(-33.24, 64.86) * mm, "end": v(-33.26, 64.82) * mm});
            skLineSegment(sketch, "E4141", {"start": v(-33.28, 64.73) * mm, "end": v(-33.3, 64.7) * mm});
            skLineSegment(sketch, "E4142", {"start": v(-33.3, 64.7) * mm, "end": v(-33.3, 64.65) * mm});
            skLineSegment(sketch, "E4143", {"start": v(-33.3, 64.65) * mm, "end": v(-33.31, 64.6) * mm});
            skLineSegment(sketch, "E4144", {"start": v(-33.31, 64.6) * mm, "end": v(-33.32, 64.56) * mm});
            skLineSegment(sketch, "E4145", {"start": v(-33.32, 64.56) * mm, "end": v(-33.32, 64.52) * mm});
            skLineSegment(sketch, "E4146", {"start": v(-33.32, 64.52) * mm, "end": v(-33.33, 64.48) * mm});
            skLineSegment(sketch, "E4147", {"start": v(-33.33, 64.48) * mm, "end": v(-33.33, 64.44) * mm});
            skLineSegment(sketch, "E4148", {"start": v(-33.33, 64.4) * mm, "end": v(-33.33, 64.35) * mm});
            skLineSegment(sketch, "E4149", {"start": v(-33.33, 64.35) * mm, "end": v(-33.32, 64.3) * mm});
            skLineSegment(sketch, "E4150", {"start": v(-33.32, 64.3) * mm, "end": v(-33.32, 64.26) * mm});
            skLineSegment(sketch, "E4151", {"start": v(-33.32, 64.26) * mm, "end": v(-33.31, 64.22) * mm});
            skLineSegment(sketch, "E4152", {"start": v(-33.31, 64.22) * mm, "end": v(-33.3, 64.18) * mm});
            skLineSegment(sketch, "E4153", {"start": v(-33.3, 64.18) * mm, "end": v(-33.3, 64.13) * mm});
            skLineSegment(sketch, "E4154", {"start": v(-33.3, 64.13) * mm, "end": v(-33.29, 64.1) * mm});
            skLineSegment(sketch, "E4155", {"start": v(-33.29, 64.1) * mm, "end": v(-33.28, 64.05) * mm});
            skLineSegment(sketch, "E4156", {"start": v(-33.28, 64.05) * mm, "end": v(-33.26, 64) * mm});
            skLineSegment(sketch, "E4157", {"start": v(-33.26, 64) * mm, "end": v(-33.25, 63.97) * mm});
            skLineSegment(sketch, "E4158", {"start": v(-33.25, 63.97) * mm, "end": v(-33.23, 63.93) * mm});
            skLineSegment(sketch, "E4159", {"start": v(-33.23, 63.93) * mm, "end": v(-33.22, 63.89) * mm});
            skLineSegment(sketch, "E4160", {"start": v(-33.22, 63.89) * mm, "end": v(-33.2, 63.85) * mm});
            skLineSegment(sketch, "E4161", {"start": v(-33.2, 63.85) * mm, "end": v(-33.18, 63.8) * mm});
            skLineSegment(sketch, "E4162", {"start": v(-33.18, 63.8) * mm, "end": v(-33.16, 63.77) * mm});
            skLineSegment(sketch, "E4163", {"start": v(-33.16, 63.77) * mm, "end": v(-33.13, 63.73) * mm});
            skLineSegment(sketch, "E4164", {"start": v(-33.13, 63.73) * mm, "end": v(-33.1, 63.7) * mm});
            skLineSegment(sketch, "E4165", {"start": v(-33.1, 63.7) * mm, "end": v(-33.08, 63.66) * mm});
            skLineSegment(sketch, "E4166", {"start": v(-33.08, 63.66) * mm, "end": v(-33.06, 63.63) * mm});
            skLineSegment(sketch, "E4167", {"start": v(-33.06, 63.63) * mm, "end": v(-33.03, 63.6) * mm});
            skLineSegment(sketch, "E4168", {"start": v(-33.03, 63.6) * mm, "end": v(-33, 63.56) * mm});
            skLineSegment(sketch, "E4169", {"start": v(-33, 63.56) * mm, "end": v(-32.97, 63.53) * mm});
            skLineSegment(sketch, "E4170", {"start": v(-32.97, 63.53) * mm, "end": v(-32.94, 63.5) * mm});
            skLineSegment(sketch, "E4171", {"start": v(-32.94, 63.5) * mm, "end": v(-32.91, 63.47) * mm});
            skLineSegment(sketch, "E4172", {"start": v(-32.91, 63.47) * mm, "end": v(-32.88, 63.44) * mm});
            skLineSegment(sketch, "E4173", {"start": v(-32.88, 63.44) * mm, "end": v(-32.84, 63.41) * mm});
            skLineSegment(sketch, "E4174", {"start": v(-32.84, 63.41) * mm, "end": v(-32.8, 63.39) * mm});
            skLineSegment(sketch, "E4175", {"start": v(-32.8, 63.39) * mm, "end": v(-32.77, 63.36) * mm});
            skLineSegment(sketch, "E4176", {"start": v(-32.77, 63.36) * mm, "end": v(-32.74, 63.34) * mm});
            skLineSegment(sketch, "E4177", {"start": v(-32.74, 63.34) * mm, "end": v(-32.7, 63.32) * mm});
            skLineSegment(sketch, "E4178", {"start": v(-32.7, 63.32) * mm, "end": v(-32.66, 63.3) * mm});
            skLineSegment(sketch, "E4179", {"start": v(-32.66, 63.3) * mm, "end": v(-32.62, 63.28) * mm});
            skLineSegment(sketch, "E4180", {"start": v(-32.62, 63.28) * mm, "end": v(-32.58, 63.26) * mm});
            skLineSegment(sketch, "E4181", {"start": v(-32.58, 63.26) * mm, "end": v(-32.54, 63.24) * mm});
            skLineSegment(sketch, "E4182", {"start": v(-32.54, 63.24) * mm, "end": v(-32.5, 63.23) * mm});
            skLineSegment(sketch, "E4183", {"start": v(-32.5, 63.23) * mm, "end": v(-32.46, 63.21) * mm});
            skLineSegment(sketch, "E4184", {"start": v(-32.46, 63.21) * mm, "end": v(-32.42, 63.2) * mm});
            skLineSegment(sketch, "E4185", {"start": v(-32.42, 63.2) * mm, "end": v(-32.38, 63.19) * mm});
            skLineSegment(sketch, "E4186", {"start": v(-32.34, 63.18) * mm, "end": v(-32.3, 63.17) * mm});
            skLineSegment(sketch, "E4187", {"start": v(-32.3, 63.17) * mm, "end": v(-32.25, 63.16) * mm});
            skLineSegment(sketch, "E4188", {"start": v(-32.25, 63.16) * mm, "end": v(-32.2, 63.16) * mm});
            skLineSegment(sketch, "E4189", {"start": v(-32.2, 63.16) * mm, "end": v(-32.16, 63.16) * mm});
            skLineSegment(sketch, "E4190", {"start": v(-32.16, 63.16) * mm, "end": v(-32.12, 63.15) * mm});
            skLineSegment(sketch, "E4191", {"start": v(-32.12, 63.15) * mm, "end": v(-32.08, 63.15) * mm});
            skLineSegment(sketch, "E4192", {"start": v(-4.45, 38.15) * mm, "end": v(-4.32, 38.16) * mm});
            skLineSegment(sketch, "E4193", {"start": v(-3.68, 38.26) * mm, "end": v(-3.55, 38.3) * mm});
            skLineSegment(sketch, "E4194", {"start": v(-3.55, 38.3) * mm, "end": v(-3.42, 38.33) * mm});
            skLineSegment(sketch, "E4195", {"start": v(-3.3, 38.38) * mm, "end": v(-3.18, 38.42) * mm});
            skLineSegment(sketch, "E4196", {"start": v(-3.18, 38.42) * mm, "end": v(-3.06, 38.47) * mm});
            skLineSegment(sketch, "E4197", {"start": v(-3.06, 38.47) * mm, "end": v(-2.94, 38.53) * mm});
            skLineSegment(sketch, "E4198", {"start": v(-2.94, 38.53) * mm, "end": v(-2.83, 38.59) * mm});
            skLineSegment(sketch, "E4199", {"start": v(-2.83, 38.59) * mm, "end": v(-2.71, 38.65) * mm});
            skLineSegment(sketch, "E4200", {"start": v(-2.38, 38.86) * mm, "end": v(-2.28, 38.94) * mm});
            skLineSegment(sketch, "E4201", {"start": v(-2.28, 38.94) * mm, "end": v(-2.18, 39.02) * mm});
            skLineSegment(sketch, "E4202", {"start": v(-2.08, 39.1) * mm, "end": v(-1.98, 39.2) * mm});
            skLineSegment(sketch, "E4203", {"start": v(-1.98, 39.2) * mm, "end": v(-1.9, 39.29) * mm});
            skLineSegment(sketch, "E4204", {"start": v(-1.9, 39.29) * mm, "end": v(-1.8, 39.38) * mm});
            skLineSegment(sketch, "E4205", {"start": v(-1.72, 39.48) * mm, "end": v(-1.63, 39.58) * mm});
            skLineSegment(sketch, "E4206", {"start": v(-1.63, 39.58) * mm, "end": v(-1.56, 39.68) * mm});
            skLineSegment(sketch, "E4207", {"start": v(-1.56, 39.68) * mm, "end": v(-1.48, 39.79) * mm});
            skLineSegment(sketch, "E4208", {"start": v(-1.48, 39.79) * mm, "end": v(-1.4, 39.9) * mm});
            skLineSegment(sketch, "E4209", {"start": v(-1.4, 39.9) * mm, "end": v(-1.34, 40) * mm});
            skLineSegment(sketch, "E4210", {"start": v(-1.34, 40) * mm, "end": v(-1.28, 40.12) * mm});
            skLineSegment(sketch, "E4211", {"start": v(-1.28, 40.12) * mm, "end": v(-1.22, 40.24) * mm});
            skLineSegment(sketch, "E4212", {"start": v(-1.22, 40.24) * mm, "end": v(-1.16, 40.36) * mm});
            skLineSegment(sketch, "E4213", {"start": v(-1.16, 40.36) * mm, "end": v(-1.1, 40.48) * mm});
            skLineSegment(sketch, "E4214", {"start": v(-1.06, 40.6) * mm, "end": v(-1.02, 40.72) * mm});
            skLineSegment(sketch, "E4215", {"start": v(-1.02, 40.72) * mm, "end": v(-0.98, 40.84) * mm});
            skLineSegment(sketch, "E4216", {"start": v(-0.98, 40.84) * mm, "end": v(-0.95, 40.97) * mm});
            skLineSegment(sketch, "E4217", {"start": v(-0.95, 40.97) * mm, "end": v(-0.92, 41.1) * mm});
            skLineSegment(sketch, "E4218", {"start": v(-0.87, 41.35) * mm, "end": v(-0.85, 41.48) * mm});
            skLineSegment(sketch, "E4219", {"start": v(-0.84, 41.61) * mm, "end": v(-0.83, 41.74) * mm});
            skLineSegment(sketch, "E4220", {"start": v(-0.83, 41.74) * mm, "end": v(-0.83, 41.87) * mm});
            skLineSegment(sketch, "E4221", {"start": v(-0.83, 41.87) * mm, "end": v(-0.83, 42) * mm});
            skLineSegment(sketch, "E4222", {"start": v(-0.83, 42) * mm, "end": v(-0.83, 42.13) * mm});
            skLineSegment(sketch, "E4223", {"start": v(-0.83, 42.13) * mm, "end": v(-0.84, 42.26) * mm});
            skLineSegment(sketch, "E4224", {"start": v(-0.84, 42.26) * mm, "end": v(-0.86, 42.39) * mm});
            skLineSegment(sketch, "E4225", {"start": v(-0.86, 42.39) * mm, "end": v(-0.88, 42.52) * mm});
            skLineSegment(sketch, "E4226", {"start": v(-0.88, 42.52) * mm, "end": v(-0.9, 42.65) * mm});
            skLineSegment(sketch, "E4227", {"start": v(-0.93, 42.77) * mm, "end": v(-0.96, 42.9) * mm});
            skLineSegment(sketch, "E4228", {"start": v(-1, 43.02) * mm, "end": v(-1.04, 43.15) * mm});
            skLineSegment(sketch, "E4229", {"start": v(-1.09, 43.27) * mm, "end": v(-1.14, 43.4) * mm});
            skLineSegment(sketch, "E4230", {"start": v(-1.14, 43.4) * mm, "end": v(-1.19, 43.5) * mm});
            skLineSegment(sketch, "E4231", {"start": v(-1.37, 43.85) * mm, "end": v(-1.44, 43.96) * mm});
            skLineSegment(sketch, "E4232", {"start": v(-1.44, 43.96) * mm, "end": v(-1.52, 44.07) * mm});
            skLineSegment(sketch, "E4233", {"start": v(-1.52, 44.07) * mm, "end": v(-1.6, 44.17) * mm});
            skLineSegment(sketch, "E4234", {"start": v(-1.6, 44.17) * mm, "end": v(-1.67, 44.28) * mm});
            skLineSegment(sketch, "E4235", {"start": v(-1.67, 44.28) * mm, "end": v(-1.76, 44.38) * mm});
            skLineSegment(sketch, "E4236", {"start": v(-1.76, 44.38) * mm, "end": v(-1.85, 44.47) * mm});
            skLineSegment(sketch, "E4237", {"start": v(-1.85, 44.47) * mm, "end": v(-1.94, 44.57) * mm});
            skLineSegment(sketch, "E4238", {"start": v(-1.94, 44.57) * mm, "end": v(-2.03, 44.66) * mm});
            skLineSegment(sketch, "E4239", {"start": v(-2.13, 44.74) * mm, "end": v(-2.23, 44.83) * mm});
            skLineSegment(sketch, "E4240", {"start": v(-2.23, 44.83) * mm, "end": v(-2.33, 44.9) * mm});
            skLineSegment(sketch, "E4241", {"start": v(-2.33, 44.9) * mm, "end": v(-2.44, 44.98) * mm});
            skLineSegment(sketch, "E4242", {"start": v(-2.88, 45.25) * mm, "end": v(-3, 45.3) * mm});
            skLineSegment(sketch, "E4243", {"start": v(-3, 45.3) * mm, "end": v(-3.12, 45.36) * mm});
            skLineSegment(sketch, "E4244", {"start": v(-3.12, 45.36) * mm, "end": v(-3.24, 45.4) * mm});
            skLineSegment(sketch, "E4245", {"start": v(-3.24, 45.4) * mm, "end": v(-3.36, 45.45) * mm});
            skLineSegment(sketch, "E4246", {"start": v(-3.36, 45.45) * mm, "end": v(-3.49, 45.5) * mm});
            skLineSegment(sketch, "E4247", {"start": v(-3.49, 45.5) * mm, "end": v(-3.61, 45.53) * mm});
            skLineSegment(sketch, "E4248", {"start": v(-4, 45.6) * mm, "end": v(-4.12, 45.62) * mm});
            skLineSegment(sketch, "E4249", {"start": v(-4.12, 45.62) * mm, "end": v(-4.25, 45.64) * mm});
            skLineSegment(sketch, "E4250", {"start": v(-4.51, 45.65) * mm, "end": v(-4.64, 45.65) * mm});
            skLineSegment(sketch, "E4251", {"start": v(-4.64, 45.65) * mm, "end": v(-4.77, 45.65) * mm});
            skLineSegment(sketch, "E4252", {"start": v(-4.77, 45.65) * mm, "end": v(-4.9, 45.64) * mm});
            skLineSegment(sketch, "E4253", {"start": v(-4.9, 45.64) * mm, "end": v(-5.03, 45.62) * mm});
            skLineSegment(sketch, "E4254", {"start": v(-5.03, 45.62) * mm, "end": v(-5.16, 45.6) * mm});
            skLineSegment(sketch, "E4255", {"start": v(-5.16, 45.6) * mm, "end": v(-5.29, 45.58) * mm});
            skLineSegment(sketch, "E4256", {"start": v(-5.29, 45.58) * mm, "end": v(-5.42, 45.56) * mm});
            skLineSegment(sketch, "E4257", {"start": v(-5.42, 45.56) * mm, "end": v(-5.54, 45.53) * mm});
            skLineSegment(sketch, "E4258", {"start": v(-5.54, 45.53) * mm, "end": v(-5.67, 45.5) * mm});
            skLineSegment(sketch, "E4259", {"start": v(-5.8, 45.45) * mm, "end": v(-5.91, 45.4) * mm});
            skLineSegment(sketch, "E4260", {"start": v(-5.91, 45.4) * mm, "end": v(-6.04, 45.36) * mm});
            skLineSegment(sketch, "E4261", {"start": v(-6.15, 45.3) * mm, "end": v(-6.27, 45.25) * mm});
            skLineSegment(sketch, "E4262", {"start": v(-6.39, 45.19) * mm, "end": v(-6.5, 45.12) * mm});
            skLineSegment(sketch, "E4263", {"start": v(-6.5, 45.12) * mm, "end": v(-6.6, 45.05) * mm});
            skLineSegment(sketch, "E4264", {"start": v(-6.6, 45.05) * mm, "end": v(-6.72, 44.98) * mm});
            skLineSegment(sketch, "E4265", {"start": v(-6.72, 44.98) * mm, "end": v(-6.82, 44.9) * mm});
            skLineSegment(sketch, "E4266", {"start": v(-6.93, 44.83) * mm, "end": v(-7.03, 44.74) * mm});
            skLineSegment(sketch, "E4267", {"start": v(-7.12, 44.66) * mm, "end": v(-7.22, 44.57) * mm});
            skLineSegment(sketch, "E4268", {"start": v(-7.22, 44.57) * mm, "end": v(-7.3, 44.47) * mm});
            skLineSegment(sketch, "E4269", {"start": v(-7.4, 44.38) * mm, "end": v(-7.48, 44.28) * mm});
            skLineSegment(sketch, "E4270", {"start": v(-7.48, 44.28) * mm, "end": v(-7.56, 44.17) * mm});
            skLineSegment(sketch, "E4271", {"start": v(-7.71, 43.96) * mm, "end": v(-7.78, 43.85) * mm});
            skLineSegment(sketch, "E4272", {"start": v(-7.78, 43.85) * mm, "end": v(-7.85, 43.74) * mm});
            skLineSegment(sketch, "E4273", {"start": v(-7.85, 43.74) * mm, "end": v(-7.9, 43.63) * mm});
            skLineSegment(sketch, "E4274", {"start": v(-7.9, 43.63) * mm, "end": v(-7.97, 43.5) * mm});
            skLineSegment(sketch, "E4275", {"start": v(-8.07, 43.27) * mm, "end": v(-8.11, 43.15) * mm});
            skLineSegment(sketch, "E4276", {"start": v(-8.11, 43.15) * mm, "end": v(-8.16, 43.02) * mm});
            skLineSegment(sketch, "E4277", {"start": v(-8.2, 42.9) * mm, "end": v(-8.22, 42.77) * mm});
            skLineSegment(sketch, "E4278", {"start": v(-8.22, 42.77) * mm, "end": v(-8.25, 42.65) * mm});
            skLineSegment(sketch, "E4279", {"start": v(-8.25, 42.65) * mm, "end": v(-8.28, 42.52) * mm});
            skLineSegment(sketch, "E4280", {"start": v(-8.28, 42.52) * mm, "end": v(-8.3, 42.39) * mm});
            skLineSegment(sketch, "E4281", {"start": v(-8.3, 42.39) * mm, "end": v(-8.31, 42.26) * mm});
            skLineSegment(sketch, "E4282", {"start": v(-8.31, 42.26) * mm, "end": v(-8.32, 42.13) * mm});
            skLineSegment(sketch, "E4283", {"start": v(-8.32, 42.13) * mm, "end": v(-8.33, 42) * mm});
            skLineSegment(sketch, "E4284", {"start": v(-8.33, 42) * mm, "end": v(-8.33, 41.87) * mm});
            skLineSegment(sketch, "E4285", {"start": v(-8.33, 41.87) * mm, "end": v(-8.32, 41.74) * mm});
            skLineSegment(sketch, "E4286", {"start": v(-8.32, 41.74) * mm, "end": v(-8.32, 41.61) * mm});
            skLineSegment(sketch, "E4287", {"start": v(-8.32, 41.61) * mm, "end": v(-8.3, 41.48) * mm});
            skLineSegment(sketch, "E4288", {"start": v(-8.2, 40.97) * mm, "end": v(-8.17, 40.84) * mm});
            skLineSegment(sketch, "E4289", {"start": v(-8.17, 40.84) * mm, "end": v(-8.14, 40.72) * mm});
            skLineSegment(sketch, "E4290", {"start": v(-8.14, 40.72) * mm, "end": v(-8.1, 40.6) * mm});
            skLineSegment(sketch, "E4291", {"start": v(-8.1, 40.6) * mm, "end": v(-8.05, 40.48) * mm});
            skLineSegment(sketch, "E4292", {"start": v(-7.94, 40.24) * mm, "end": v(-7.88, 40.12) * mm});
            skLineSegment(sketch, "E4293", {"start": v(-7.88, 40.12) * mm, "end": v(-7.81, 40) * mm});
            skLineSegment(sketch, "E4294", {"start": v(-7.81, 40) * mm, "end": v(-7.75, 39.9) * mm});
            skLineSegment(sketch, "E4295", {"start": v(-7.75, 39.9) * mm, "end": v(-7.67, 39.79) * mm});
            skLineSegment(sketch, "E4296", {"start": v(-7.6, 39.68) * mm, "end": v(-7.52, 39.58) * mm});
            skLineSegment(sketch, "E4297", {"start": v(-7.35, 39.38) * mm, "end": v(-7.26, 39.29) * mm});
            skLineSegment(sketch, "E4298", {"start": v(-7.26, 39.29) * mm, "end": v(-7.17, 39.2) * mm});
            skLineSegment(sketch, "E4299", {"start": v(-7.17, 39.2) * mm, "end": v(-7.08, 39.1) * mm});
            skLineSegment(sketch, "E4300", {"start": v(-7.08, 39.1) * mm, "end": v(-6.98, 39.02) * mm});
            skLineSegment(sketch, "E4301", {"start": v(-6.88, 38.94) * mm, "end": v(-6.77, 38.86) * mm});
            skLineSegment(sketch, "E4302", {"start": v(-6.77, 38.86) * mm, "end": v(-6.66, 38.79) * mm});
            skLineSegment(sketch, "E4303", {"start": v(-6.66, 38.79) * mm, "end": v(-6.55, 38.72) * mm});
            skLineSegment(sketch, "E4304", {"start": v(-6.55, 38.72) * mm, "end": v(-6.44, 38.65) * mm});
            skLineSegment(sketch, "E4305", {"start": v(-6.44, 38.65) * mm, "end": v(-6.33, 38.59) * mm});
            skLineSegment(sketch, "E4306", {"start": v(-6.33, 38.59) * mm, "end": v(-6.21, 38.53) * mm});
            skLineSegment(sketch, "E4307", {"start": v(-5.97, 38.42) * mm, "end": v(-5.85, 38.38) * mm});
            skLineSegment(sketch, "E4308", {"start": v(-5.85, 38.38) * mm, "end": v(-5.73, 38.33) * mm});
            skLineSegment(sketch, "E4309", {"start": v(-5.73, 38.33) * mm, "end": v(-5.6, 38.3) * mm});
            skLineSegment(sketch, "E4310", {"start": v(-5.48, 38.26) * mm, "end": v(-5.35, 38.23) * mm});
            skLineSegment(sketch, "E4311", {"start": v(-5.35, 38.23) * mm, "end": v(-5.23, 38.2) * mm});
            skLineSegment(sketch, "E4312", {"start": v(-5.23, 38.2) * mm, "end": v(-5.1, 38.19) * mm});
            skLineSegment(sketch, "E4313", {"start": v(-5.1, 38.19) * mm, "end": v(-4.97, 38.17) * mm});
            skLineSegment(sketch, "E4314", {"start": v(-4.97, 38.17) * mm, "end": v(-4.84, 38.16) * mm});
            skLineSegment(sketch, "E4315", {"start": v(-4.84, 38.16) * mm, "end": v(-4.7, 38.15) * mm});
            skLineSegment(sketch, "E4316", {"start": v(-4.7, 38.15) * mm, "end": v(-4.58, 38.15) * mm});
            skLineSegment(sketch, "E4317", {"start": v(69.17, 39.4) * mm, "end": v(69.26, 39.4) * mm});
            skLineSegment(sketch, "E4318", {"start": v(69.26, 39.4) * mm, "end": v(69.35, 39.4) * mm});
            skLineSegment(sketch, "E4319", {"start": v(69.35, 39.4) * mm, "end": v(69.43, 39.42) * mm});
            skLineSegment(sketch, "E4320", {"start": v(69.43, 39.42) * mm, "end": v(69.52, 39.43) * mm});
            skLineSegment(sketch, "E4321", {"start": v(69.52, 39.43) * mm, "end": v(69.6, 39.44) * mm});
            skLineSegment(sketch, "E4322", {"start": v(69.6, 39.44) * mm, "end": v(69.69, 39.46) * mm});
            skLineSegment(sketch, "E4323", {"start": v(69.69, 39.46) * mm, "end": v(69.77, 39.48) * mm});
            skLineSegment(sketch, "E4324", {"start": v(69.77, 39.48) * mm, "end": v(69.86, 39.5) * mm});
            skLineSegment(sketch, "E4325", {"start": v(69.86, 39.5) * mm, "end": v(69.94, 39.52) * mm});
            skLineSegment(sketch, "E4326", {"start": v(69.94, 39.52) * mm, "end": v(70.02, 39.55) * mm});
            skLineSegment(sketch, "E4327", {"start": v(70.02, 39.55) * mm, "end": v(70.1, 39.58) * mm});
            skLineSegment(sketch, "E4328", {"start": v(70.1, 39.58) * mm, "end": v(70.18, 39.62) * mm});
            skLineSegment(sketch, "E4329", {"start": v(70.26, 39.65) * mm, "end": v(70.34, 39.7) * mm});
            skLineSegment(sketch, "E4330", {"start": v(70.34, 39.7) * mm, "end": v(70.42, 39.73) * mm});
            skLineSegment(sketch, "E4331", {"start": v(70.42, 39.73) * mm, "end": v(70.5, 39.78) * mm});
            skLineSegment(sketch, "E4332", {"start": v(70.56, 39.83) * mm, "end": v(70.64, 39.87) * mm});
            skLineSegment(sketch, "E4333", {"start": v(70.64, 39.87) * mm, "end": v(70.7, 39.93) * mm});
            skLineSegment(sketch, "E4334", {"start": v(70.7, 39.93) * mm, "end": v(70.77, 39.98) * mm});
            skLineSegment(sketch, "E4335", {"start": v(70.77, 39.98) * mm, "end": v(70.84, 40.04) * mm});
            skLineSegment(sketch, "E4336", {"start": v(70.84, 40.04) * mm, "end": v(70.9, 40.1) * mm});
            skLineSegment(sketch, "E4337", {"start": v(70.9, 40.1) * mm, "end": v(70.96, 40.16) * mm});
            skLineSegment(sketch, "E4338", {"start": v(70.96, 40.16) * mm, "end": v(71.02, 40.22) * mm});
            skLineSegment(sketch, "E4339", {"start": v(71.08, 40.29) * mm, "end": v(71.13, 40.35) * mm});
            skLineSegment(sketch, "E4340", {"start": v(71.13, 40.35) * mm, "end": v(71.19, 40.42) * mm});
            skLineSegment(sketch, "E4341", {"start": v(71.19, 40.42) * mm, "end": v(71.24, 40.5) * mm});
            skLineSegment(sketch, "E4342", {"start": v(71.24, 40.5) * mm, "end": v(71.29, 40.57) * mm});
            skLineSegment(sketch, "E4343", {"start": v(71.29, 40.57) * mm, "end": v(71.33, 40.64) * mm});
            skLineSegment(sketch, "E4344", {"start": v(71.33, 40.64) * mm, "end": v(71.37, 40.72) * mm});
            skLineSegment(sketch, "E4345", {"start": v(71.37, 40.72) * mm, "end": v(71.41, 40.8) * mm});
            skLineSegment(sketch, "E4346", {"start": v(71.48, 40.95) * mm, "end": v(71.52, 41.03) * mm});
            skLineSegment(sketch, "E4347", {"start": v(71.52, 41.03) * mm, "end": v(71.54, 41.11) * mm});
            skLineSegment(sketch, "E4348", {"start": v(71.65, 41.54) * mm, "end": v(71.66, 41.62) * mm});
            skLineSegment(sketch, "E4349", {"start": v(71.66, 41.62) * mm, "end": v(71.66, 41.7) * mm});
            skLineSegment(sketch, "E4350", {"start": v(71.66, 41.7) * mm, "end": v(71.67, 41.8) * mm});
            skLineSegment(sketch, "E4351", {"start": v(71.67, 41.8) * mm, "end": v(71.67, 41.88) * mm});
            skLineSegment(sketch, "E4352", {"start": v(71.67, 41.88) * mm, "end": v(71.67, 41.97) * mm});
            skLineSegment(sketch, "E4353", {"start": v(71.67, 41.97) * mm, "end": v(71.67, 42.05) * mm});
            skLineSegment(sketch, "E4354", {"start": v(71.67, 42.05) * mm, "end": v(71.66, 42.14) * mm});
            skLineSegment(sketch, "E4355", {"start": v(71.66, 42.14) * mm, "end": v(71.65, 42.23) * mm});
            skLineSegment(sketch, "E4356", {"start": v(71.65, 42.23) * mm, "end": v(71.64, 42.31) * mm});
            skLineSegment(sketch, "E4357", {"start": v(71.64, 42.31) * mm, "end": v(71.62, 42.4) * mm});
            skLineSegment(sketch, "E4358", {"start": v(71.62, 42.4) * mm, "end": v(71.6, 42.48) * mm});
            skLineSegment(sketch, "E4359", {"start": v(71.6, 42.48) * mm, "end": v(71.58, 42.57) * mm});
            skLineSegment(sketch, "E4360", {"start": v(71.58, 42.57) * mm, "end": v(71.56, 42.65) * mm});
            skLineSegment(sketch, "E4361", {"start": v(71.53, 42.73) * mm, "end": v(71.5, 42.81) * mm});
            skLineSegment(sketch, "E4362", {"start": v(71.5, 42.81) * mm, "end": v(71.47, 42.9) * mm});
            skLineSegment(sketch, "E4363", {"start": v(71.47, 42.9) * mm, "end": v(71.43, 42.97) * mm});
            skLineSegment(sketch, "E4364", {"start": v(71.43, 42.97) * mm, "end": v(71.4, 43.05) * mm});
            skLineSegment(sketch, "E4365", {"start": v(71.4, 43.05) * mm, "end": v(71.35, 43.13) * mm});
            skLineSegment(sketch, "E4366", {"start": v(71.35, 43.13) * mm, "end": v(71.3, 43.2) * mm});
            skLineSegment(sketch, "E4367", {"start": v(71.3, 43.2) * mm, "end": v(71.26, 43.28) * mm});
            skLineSegment(sketch, "E4368", {"start": v(71.26, 43.28) * mm, "end": v(71.21, 43.35) * mm});
            skLineSegment(sketch, "E4369", {"start": v(71.21, 43.35) * mm, "end": v(71.16, 43.42) * mm});
            skLineSegment(sketch, "E4370", {"start": v(71.16, 43.42) * mm, "end": v(71.1, 43.49) * mm});
            skLineSegment(sketch, "E4371", {"start": v(71.1, 43.49) * mm, "end": v(71.05, 43.55) * mm});
            skLineSegment(sketch, "E4372", {"start": v(71, 43.62) * mm, "end": v(70.93, 43.68) * mm});
            skLineSegment(sketch, "E4373", {"start": v(70.93, 43.68) * mm, "end": v(70.87, 43.74) * mm});
            skLineSegment(sketch, "E4374", {"start": v(70.87, 43.74) * mm, "end": v(70.8, 43.8) * mm});
            skLineSegment(sketch, "E4375", {"start": v(70.8, 43.8) * mm, "end": v(70.74, 43.85) * mm});
            skLineSegment(sketch, "E4376", {"start": v(70.67, 43.9) * mm, "end": v(70.6, 43.96) * mm});
            skLineSegment(sketch, "E4377", {"start": v(70.6, 43.96) * mm, "end": v(70.53, 44) * mm});
            skLineSegment(sketch, "E4378", {"start": v(70.53, 44) * mm, "end": v(70.45, 44.05) * mm});
            skLineSegment(sketch, "E4379", {"start": v(70.45, 44.05) * mm, "end": v(70.38, 44.1) * mm});
            skLineSegment(sketch, "E4380", {"start": v(70.38, 44.1) * mm, "end": v(70.3, 44.13) * mm});
            skLineSegment(sketch, "E4381", {"start": v(70.3, 44.13) * mm, "end": v(70.22, 44.17) * mm});
            skLineSegment(sketch, "E4382", {"start": v(70.22, 44.17) * mm, "end": v(70.14, 44.2) * mm});
            skLineSegment(sketch, "E4383", {"start": v(70.14, 44.2) * mm, "end": v(70.06, 44.24) * mm});
            skLineSegment(sketch, "E4384", {"start": v(69.9, 44.3) * mm, "end": v(69.82, 44.32) * mm});
            skLineSegment(sketch, "E4385", {"start": v(69.82, 44.32) * mm, "end": v(69.73, 44.34) * mm});
            skLineSegment(sketch, "E4386", {"start": v(69.73, 44.34) * mm, "end": v(69.65, 44.36) * mm});
            skLineSegment(sketch, "E4387", {"start": v(69.65, 44.36) * mm, "end": v(69.56, 44.37) * mm});
            skLineSegment(sketch, "E4388", {"start": v(69.56, 44.37) * mm, "end": v(69.48, 44.38) * mm});
            skLineSegment(sketch, "E4389", {"start": v(69.48, 44.38) * mm, "end": v(69.39, 44.4) * mm});
            skLineSegment(sketch, "E4390", {"start": v(69.39, 44.4) * mm, "end": v(69.3, 44.4) * mm});
            skLineSegment(sketch, "E4391", {"start": v(69.3, 44.4) * mm, "end": v(69.22, 44.4) * mm});
            skLineSegment(sketch, "E4392", {"start": v(69.22, 44.4) * mm, "end": v(69.13, 44.4) * mm});
            skLineSegment(sketch, "E4393", {"start": v(69.13, 44.4) * mm, "end": v(69.04, 44.4) * mm});
            skLineSegment(sketch, "E4394", {"start": v(69.04, 44.4) * mm, "end": v(68.96, 44.4) * mm});
            skLineSegment(sketch, "E4395", {"start": v(68.96, 44.4) * mm, "end": v(68.87, 44.38) * mm});
            skLineSegment(sketch, "E4396", {"start": v(68.87, 44.38) * mm, "end": v(68.78, 44.37) * mm});
            skLineSegment(sketch, "E4397", {"start": v(68.78, 44.37) * mm, "end": v(68.7, 44.36) * mm});
            skLineSegment(sketch, "E4398", {"start": v(68.45, 44.3) * mm, "end": v(68.36, 44.27) * mm});
            skLineSegment(sketch, "E4399", {"start": v(68.36, 44.27) * mm, "end": v(68.28, 44.24) * mm});
            skLineSegment(sketch, "E4400", {"start": v(68.28, 44.24) * mm, "end": v(68.2, 44.2) * mm});
            skLineSegment(sketch, "E4401", {"start": v(68.2, 44.2) * mm, "end": v(68.12, 44.17) * mm});
            skLineSegment(sketch, "E4402", {"start": v(68.12, 44.17) * mm, "end": v(68.04, 44.13) * mm});
            skLineSegment(sketch, "E4403", {"start": v(68.04, 44.13) * mm, "end": v(67.97, 44.1) * mm});
            skLineSegment(sketch, "E4404", {"start": v(67.9, 44.05) * mm, "end": v(67.82, 44) * mm});
            skLineSegment(sketch, "E4405", {"start": v(67.82, 44) * mm, "end": v(67.75, 43.96) * mm});
            skLineSegment(sketch, "E4406", {"start": v(67.75, 43.96) * mm, "end": v(67.68, 43.9) * mm});
            skLineSegment(sketch, "E4407", {"start": v(67.68, 43.9) * mm, "end": v(67.6, 43.85) * mm});
            skLineSegment(sketch, "E4408", {"start": v(67.6, 43.85) * mm, "end": v(67.54, 43.8) * mm});
            skLineSegment(sketch, "E4409", {"start": v(67.48, 43.74) * mm, "end": v(67.41, 43.68) * mm});
            skLineSegment(sketch, "E4410", {"start": v(67.41, 43.68) * mm, "end": v(67.35, 43.62) * mm});
            skLineSegment(sketch, "E4411", {"start": v(67.35, 43.62) * mm, "end": v(67.3, 43.55) * mm});
            skLineSegment(sketch, "E4412", {"start": v(67.3, 43.55) * mm, "end": v(67.24, 43.49) * mm});
            skLineSegment(sketch, "E4413", {"start": v(67.24, 43.49) * mm, "end": v(67.18, 43.42) * mm});
            skLineSegment(sketch, "E4414", {"start": v(67.18, 43.42) * mm, "end": v(67.13, 43.35) * mm});
            skLineSegment(sketch, "E4415", {"start": v(67.13, 43.35) * mm, "end": v(67.08, 43.28) * mm});
            skLineSegment(sketch, "E4416", {"start": v(67.08, 43.28) * mm, "end": v(67.04, 43.2) * mm});
            skLineSegment(sketch, "E4417", {"start": v(67.04, 43.2) * mm, "end": v(67, 43.13) * mm});
            skLineSegment(sketch, "E4418", {"start": v(67, 43.13) * mm, "end": v(66.95, 43.05) * mm});
            skLineSegment(sketch, "E4419", {"start": v(66.95, 43.05) * mm, "end": v(66.91, 42.97) * mm});
            skLineSegment(sketch, "E4420", {"start": v(66.91, 42.97) * mm, "end": v(66.88, 42.9) * mm});
            skLineSegment(sketch, "E4421", {"start": v(66.88, 42.9) * mm, "end": v(66.84, 42.81) * mm});
            skLineSegment(sketch, "E4422", {"start": v(66.84, 42.81) * mm, "end": v(66.81, 42.73) * mm});
            skLineSegment(sketch, "E4423", {"start": v(66.81, 42.73) * mm, "end": v(66.79, 42.65) * mm});
            skLineSegment(sketch, "E4424", {"start": v(66.79, 42.65) * mm, "end": v(66.76, 42.57) * mm});
            skLineSegment(sketch, "E4425", {"start": v(66.76, 42.57) * mm, "end": v(66.74, 42.48) * mm});
            skLineSegment(sketch, "E4426", {"start": v(66.74, 42.48) * mm, "end": v(66.72, 42.4) * mm});
            skLineSegment(sketch, "E4427", {"start": v(66.72, 42.4) * mm, "end": v(66.7, 42.31) * mm});
            skLineSegment(sketch, "E4428", {"start": v(66.7, 42.31) * mm, "end": v(66.7, 42.23) * mm});
            skLineSegment(sketch, "E4429", {"start": v(66.7, 42.23) * mm, "end": v(66.68, 42.14) * mm});
            skLineSegment(sketch, "E4430", {"start": v(66.68, 42.14) * mm, "end": v(66.68, 42.05) * mm});
            skLineSegment(sketch, "E4431", {"start": v(66.68, 42.05) * mm, "end": v(66.67, 41.97) * mm});
            skLineSegment(sketch, "E4432", {"start": v(66.67, 41.97) * mm, "end": v(66.67, 41.88) * mm});
            skLineSegment(sketch, "E4433", {"start": v(66.67, 41.88) * mm, "end": v(66.67, 41.8) * mm});
            skLineSegment(sketch, "E4434", {"start": v(66.67, 41.8) * mm, "end": v(66.68, 41.7) * mm});
            skLineSegment(sketch, "E4435", {"start": v(66.68, 41.7) * mm, "end": v(66.69, 41.62) * mm});
            skLineSegment(sketch, "E4436", {"start": v(66.69, 41.62) * mm, "end": v(66.7, 41.54) * mm});
            skLineSegment(sketch, "E4437", {"start": v(66.71, 41.45) * mm, "end": v(66.73, 41.36) * mm});
            skLineSegment(sketch, "E4438", {"start": v(66.73, 41.36) * mm, "end": v(66.75, 41.28) * mm});
            skLineSegment(sketch, "E4439", {"start": v(66.75, 41.28) * mm, "end": v(66.77, 41.2) * mm});
            skLineSegment(sketch, "E4440", {"start": v(66.77, 41.2) * mm, "end": v(66.8, 41.11) * mm});
            skLineSegment(sketch, "E4441", {"start": v(66.83, 41.03) * mm, "end": v(66.86, 40.95) * mm});
            skLineSegment(sketch, "E4442", {"start": v(66.86, 40.95) * mm, "end": v(66.9, 40.87) * mm});
            skLineSegment(sketch, "E4443", {"start": v(66.9, 40.87) * mm, "end": v(66.93, 40.8) * mm});
            skLineSegment(sketch, "E4444", {"start": v(66.93, 40.8) * mm, "end": v(66.97, 40.72) * mm});
            skLineSegment(sketch, "E4445", {"start": v(66.97, 40.72) * mm, "end": v(67.01, 40.64) * mm});
            skLineSegment(sketch, "E4446", {"start": v(67.1, 40.5) * mm, "end": v(67.16, 40.42) * mm});
            skLineSegment(sketch, "E4447", {"start": v(67.16, 40.42) * mm, "end": v(67.21, 40.35) * mm});
            skLineSegment(sketch, "E4448", {"start": v(67.21, 40.35) * mm, "end": v(67.27, 40.29) * mm});
            skLineSegment(sketch, "E4449", {"start": v(67.5, 40.04) * mm, "end": v(67.57, 39.98) * mm});
            skLineSegment(sketch, "E4450", {"start": v(67.57, 39.98) * mm, "end": v(67.64, 39.93) * mm});
            skLineSegment(sketch, "E4451", {"start": v(67.64, 39.93) * mm, "end": v(67.71, 39.87) * mm});
            skLineSegment(sketch, "E4452", {"start": v(67.71, 39.87) * mm, "end": v(67.78, 39.83) * mm});
            skLineSegment(sketch, "E4453", {"start": v(67.78, 39.83) * mm, "end": v(67.85, 39.78) * mm});
            skLineSegment(sketch, "E4454", {"start": v(67.85, 39.78) * mm, "end": v(67.93, 39.73) * mm});
            skLineSegment(sketch, "E4455", {"start": v(67.93, 39.73) * mm, "end": v(68, 39.7) * mm});
            skLineSegment(sketch, "E4456", {"start": v(68, 39.7) * mm, "end": v(68.08, 39.65) * mm});
            skLineSegment(sketch, "E4457", {"start": v(68.08, 39.65) * mm, "end": v(68.16, 39.62) * mm});
            skLineSegment(sketch, "E4458", {"start": v(68.16, 39.62) * mm, "end": v(68.24, 39.58) * mm});
            skLineSegment(sketch, "E4459", {"start": v(68.24, 39.58) * mm, "end": v(68.32, 39.55) * mm});
            skLineSegment(sketch, "E4460", {"start": v(68.49, 39.5) * mm, "end": v(68.57, 39.48) * mm});
            skLineSegment(sketch, "E4461", {"start": v(68.57, 39.48) * mm, "end": v(68.66, 39.46) * mm});
            skLineSegment(sketch, "E4462", {"start": v(68.66, 39.46) * mm, "end": v(68.74, 39.44) * mm});
            skLineSegment(sketch, "E4463", {"start": v(68.74, 39.44) * mm, "end": v(68.83, 39.43) * mm});
            skLineSegment(sketch, "E4464", {"start": v(68.83, 39.43) * mm, "end": v(68.91, 39.42) * mm});
            skLineSegment(sketch, "E4465", {"start": v(68.91, 39.42) * mm, "end": v(69, 39.4) * mm});
            skLineSegment(sketch, "E4466", {"start": v(69, 39.4) * mm, "end": v(69.09, 39.4) * mm});
            skLineSegment(sketch, "E4467", {"start": v(69.09, 39.4) * mm, "end": v(69.17, 39.4) * mm});
            skLineSegment(sketch, "E4468", {"start": v(-78.33, 39.4) * mm, "end": v(-78.24, 39.4) * mm});
            skLineSegment(sketch, "E4469", {"start": v(-78.15, 39.4) * mm, "end": v(-78.07, 39.42) * mm});
            skLineSegment(sketch, "E4470", {"start": v(-77.73, 39.48) * mm, "end": v(-77.64, 39.5) * mm});
            skLineSegment(sketch, "E4471", {"start": v(-77.64, 39.5) * mm, "end": v(-77.56, 39.52) * mm});
            skLineSegment(sketch, "E4472", {"start": v(-77.56, 39.52) * mm, "end": v(-77.48, 39.55) * mm});
            skLineSegment(sketch, "E4473", {"start": v(-77.48, 39.55) * mm, "end": v(-77.4, 39.58) * mm});
            skLineSegment(sketch, "E4474", {"start": v(-77.4, 39.58) * mm, "end": v(-77.32, 39.62) * mm});
            skLineSegment(sketch, "E4475", {"start": v(-77.32, 39.62) * mm, "end": v(-77.24, 39.65) * mm});
            skLineSegment(sketch, "E4476", {"start": v(-77.24, 39.65) * mm, "end": v(-77.16, 39.7) * mm});
            skLineSegment(sketch, "E4477", {"start": v(-77.16, 39.7) * mm, "end": v(-77.08, 39.73) * mm});
            skLineSegment(sketch, "E4478", {"start": v(-77.08, 39.73) * mm, "end": v(-77, 39.78) * mm});
            skLineSegment(sketch, "E4479", {"start": v(-77, 39.78) * mm, "end": v(-76.94, 39.83) * mm});
            skLineSegment(sketch, "E4480", {"start": v(-76.94, 39.83) * mm, "end": v(-76.86, 39.87) * mm});
            skLineSegment(sketch, "E4481", {"start": v(-76.86, 39.87) * mm, "end": v(-76.8, 39.93) * mm});
            skLineSegment(sketch, "E4482", {"start": v(-76.8, 39.93) * mm, "end": v(-76.73, 39.98) * mm});
            skLineSegment(sketch, "E4483", {"start": v(-76.54, 40.16) * mm, "end": v(-76.48, 40.22) * mm});
            skLineSegment(sketch, "E4484", {"start": v(-76.48, 40.22) * mm, "end": v(-76.42, 40.29) * mm});
            skLineSegment(sketch, "E4485", {"start": v(-76.42, 40.29) * mm, "end": v(-76.37, 40.35) * mm});
            skLineSegment(sketch, "E4486", {"start": v(-76.26, 40.5) * mm, "end": v(-76.21, 40.57) * mm});
            skLineSegment(sketch, "E4487", {"start": v(-76.21, 40.57) * mm, "end": v(-76.17, 40.64) * mm});
            skLineSegment(sketch, "E4488", {"start": v(-76.17, 40.64) * mm, "end": v(-76.13, 40.72) * mm});
            skLineSegment(sketch, "E4489", {"start": v(-76.13, 40.72) * mm, "end": v(-76.09, 40.8) * mm});
            skLineSegment(sketch, "E4490", {"start": v(-76.05, 40.87) * mm, "end": v(-76.02, 40.95) * mm});
            skLineSegment(sketch, "E4491", {"start": v(-76.02, 40.95) * mm, "end": v(-75.98, 41.03) * mm});
            skLineSegment(sketch, "E4492", {"start": v(-75.98, 41.03) * mm, "end": v(-75.96, 41.11) * mm});
            skLineSegment(sketch, "E4493", {"start": v(-75.96, 41.11) * mm, "end": v(-75.93, 41.2) * mm});
            skLineSegment(sketch, "E4494", {"start": v(-75.93, 41.2) * mm, "end": v(-75.9, 41.28) * mm});
            skLineSegment(sketch, "E4495", {"start": v(-75.9, 41.28) * mm, "end": v(-75.89, 41.36) * mm});
            skLineSegment(sketch, "E4496", {"start": v(-75.85, 41.54) * mm, "end": v(-75.84, 41.62) * mm});
            skLineSegment(sketch, "E4497", {"start": v(-75.84, 41.62) * mm, "end": v(-75.84, 41.7) * mm});
            skLineSegment(sketch, "E4498", {"start": v(-75.84, 41.7) * mm, "end": v(-75.83, 41.8) * mm});
            skLineSegment(sketch, "E4499", {"start": v(-75.83, 41.8) * mm, "end": v(-75.83, 41.88) * mm});
            skLineSegment(sketch, "E4500", {"start": v(-75.83, 41.88) * mm, "end": v(-75.83, 41.97) * mm});
            skLineSegment(sketch, "E4501", {"start": v(-75.83, 41.97) * mm, "end": v(-75.83, 42.05) * mm});
            skLineSegment(sketch, "E4502", {"start": v(-75.83, 42.05) * mm, "end": v(-75.84, 42.14) * mm});
            skLineSegment(sketch, "E4503", {"start": v(-75.84, 42.14) * mm, "end": v(-75.85, 42.23) * mm});
            skLineSegment(sketch, "E4504", {"start": v(-75.85, 42.23) * mm, "end": v(-75.86, 42.31) * mm});
            skLineSegment(sketch, "E4505", {"start": v(-75.86, 42.31) * mm, "end": v(-75.88, 42.4) * mm});
            skLineSegment(sketch, "E4506", {"start": v(-75.88, 42.4) * mm, "end": v(-75.9, 42.48) * mm});
            skLineSegment(sketch, "E4507", {"start": v(-75.9, 42.48) * mm, "end": v(-75.92, 42.57) * mm});
            skLineSegment(sketch, "E4508", {"start": v(-75.92, 42.57) * mm, "end": v(-75.94, 42.65) * mm});
            skLineSegment(sketch, "E4509", {"start": v(-75.94, 42.65) * mm, "end": v(-75.97, 42.73) * mm});
            skLineSegment(sketch, "E4510", {"start": v(-75.97, 42.73) * mm, "end": v(-76, 42.81) * mm});
            skLineSegment(sketch, "E4511", {"start": v(-76, 42.81) * mm, "end": v(-76.03, 42.9) * mm});
            skLineSegment(sketch, "E4512", {"start": v(-76.07, 42.97) * mm, "end": v(-76.1, 43.05) * mm});
            skLineSegment(sketch, "E4513", {"start": v(-76.1, 43.05) * mm, "end": v(-76.15, 43.13) * mm});
            skLineSegment(sketch, "E4514", {"start": v(-76.2, 43.2) * mm, "end": v(-76.24, 43.28) * mm});
            skLineSegment(sketch, "E4515", {"start": v(-76.24, 43.28) * mm, "end": v(-76.29, 43.35) * mm});
            skLineSegment(sketch, "E4516", {"start": v(-76.29, 43.35) * mm, "end": v(-76.34, 43.42) * mm});
            skLineSegment(sketch, "E4517", {"start": v(-76.34, 43.42) * mm, "end": v(-76.4, 43.49) * mm});
            skLineSegment(sketch, "E4518", {"start": v(-76.4, 43.49) * mm, "end": v(-76.45, 43.55) * mm});
            skLineSegment(sketch, "E4519", {"start": v(-76.45, 43.55) * mm, "end": v(-76.5, 43.62) * mm});
            skLineSegment(sketch, "E4520", {"start": v(-76.5, 43.62) * mm, "end": v(-76.57, 43.68) * mm});
            skLineSegment(sketch, "E4521", {"start": v(-76.57, 43.68) * mm, "end": v(-76.63, 43.74) * mm});
            skLineSegment(sketch, "E4522", {"start": v(-76.63, 43.74) * mm, "end": v(-76.7, 43.8) * mm});
            skLineSegment(sketch, "E4523", {"start": v(-76.7, 43.8) * mm, "end": v(-76.76, 43.85) * mm});
            skLineSegment(sketch, "E4524", {"start": v(-76.76, 43.85) * mm, "end": v(-76.83, 43.9) * mm});
            skLineSegment(sketch, "E4525", {"start": v(-76.9, 43.96) * mm, "end": v(-76.97, 44) * mm});
            skLineSegment(sketch, "E4526", {"start": v(-76.97, 44) * mm, "end": v(-77.05, 44.05) * mm});
            skLineSegment(sketch, "E4527", {"start": v(-77.05, 44.05) * mm, "end": v(-77.12, 44.1) * mm});
            skLineSegment(sketch, "E4528", {"start": v(-77.12, 44.1) * mm, "end": v(-77.2, 44.13) * mm});
            skLineSegment(sketch, "E4529", {"start": v(-77.2, 44.13) * mm, "end": v(-77.28, 44.17) * mm});
            skLineSegment(sketch, "E4530", {"start": v(-77.28, 44.17) * mm, "end": v(-77.36, 44.2) * mm});
            skLineSegment(sketch, "E4531", {"start": v(-77.36, 44.2) * mm, "end": v(-77.44, 44.24) * mm});
            skLineSegment(sketch, "E4532", {"start": v(-77.6, 44.3) * mm, "end": v(-77.68, 44.32) * mm});
            skLineSegment(sketch, "E4533", {"start": v(-77.68, 44.32) * mm, "end": v(-77.77, 44.34) * mm});
            skLineSegment(sketch, "E4534", {"start": v(-77.77, 44.34) * mm, "end": v(-77.85, 44.36) * mm});
            skLineSegment(sketch, "E4535", {"start": v(-78.11, 44.4) * mm, "end": v(-78.2, 44.4) * mm});
            skLineSegment(sketch, "E4536", {"start": v(-78.28, 44.4) * mm, "end": v(-78.37, 44.4) * mm});
            skLineSegment(sketch, "E4537", {"start": v(-78.37, 44.4) * mm, "end": v(-78.46, 44.4) * mm});
            skLineSegment(sketch, "E4538", {"start": v(-78.46, 44.4) * mm, "end": v(-78.54, 44.4) * mm});
            skLineSegment(sketch, "E4539", {"start": v(-78.54, 44.4) * mm, "end": v(-78.63, 44.38) * mm});
            skLineSegment(sketch, "E4540", {"start": v(-78.63, 44.38) * mm, "end": v(-78.72, 44.37) * mm});
            skLineSegment(sketch, "E4541", {"start": v(-78.72, 44.37) * mm, "end": v(-78.8, 44.36) * mm});
            skLineSegment(sketch, "E4542", {"start": v(-78.8, 44.36) * mm, "end": v(-78.89, 44.34) * mm});
            skLineSegment(sketch, "E4543", {"start": v(-78.89, 44.34) * mm, "end": v(-78.97, 44.32) * mm});
            skLineSegment(sketch, "E4544", {"start": v(-78.97, 44.32) * mm, "end": v(-79.05, 44.3) * mm});
            skLineSegment(sketch, "E4545", {"start": v(-79.05, 44.3) * mm, "end": v(-79.14, 44.27) * mm});
            skLineSegment(sketch, "E4546", {"start": v(-79.14, 44.27) * mm, "end": v(-79.22, 44.24) * mm});
            skLineSegment(sketch, "E4547", {"start": v(-79.22, 44.24) * mm, "end": v(-79.3, 44.2) * mm});
            skLineSegment(sketch, "E4548", {"start": v(-79.3, 44.2) * mm, "end": v(-79.38, 44.17) * mm});
            skLineSegment(sketch, "E4549", {"start": v(-79.38, 44.17) * mm, "end": v(-79.46, 44.13) * mm});
            skLineSegment(sketch, "E4550", {"start": v(-79.46, 44.13) * mm, "end": v(-79.53, 44.1) * mm});
            skLineSegment(sketch, "E4551", {"start": v(-79.53, 44.1) * mm, "end": v(-79.6, 44.05) * mm});
            skLineSegment(sketch, "E4552", {"start": v(-79.68, 44) * mm, "end": v(-79.75, 43.96) * mm});
            skLineSegment(sketch, "E4553", {"start": v(-79.75, 43.96) * mm, "end": v(-79.82, 43.9) * mm});
            skLineSegment(sketch, "E4554", {"start": v(-79.82, 43.9) * mm, "end": v(-79.9, 43.85) * mm});
            skLineSegment(sketch, "E4555", {"start": v(-79.9, 43.85) * mm, "end": v(-79.96, 43.8) * mm});
            skLineSegment(sketch, "E4556", {"start": v(-80.26, 43.49) * mm, "end": v(-80.32, 43.42) * mm});
            skLineSegment(sketch, "E4557", {"start": v(-80.32, 43.42) * mm, "end": v(-80.37, 43.35) * mm});
            skLineSegment(sketch, "E4558", {"start": v(-80.37, 43.35) * mm, "end": v(-80.42, 43.28) * mm});
            skLineSegment(sketch, "E4559", {"start": v(-80.62, 42.9) * mm, "end": v(-80.66, 42.81) * mm});
            skLineSegment(sketch, "E4560", {"start": v(-80.66, 42.81) * mm, "end": v(-80.69, 42.73) * mm});
            skLineSegment(sketch, "E4561", {"start": v(-80.69, 42.73) * mm, "end": v(-80.71, 42.65) * mm});
            skLineSegment(sketch, "E4562", {"start": v(-80.71, 42.65) * mm, "end": v(-80.74, 42.57) * mm});
            skLineSegment(sketch, "E4563", {"start": v(-80.76, 42.48) * mm, "end": v(-80.78, 42.4) * mm});
            skLineSegment(sketch, "E4564", {"start": v(-80.78, 42.4) * mm, "end": v(-80.8, 42.31) * mm});
            skLineSegment(sketch, "E4565", {"start": v(-80.8, 42.31) * mm, "end": v(-80.8, 42.23) * mm});
            skLineSegment(sketch, "E4566", {"start": v(-80.8, 42.23) * mm, "end": v(-80.82, 42.14) * mm});
            skLineSegment(sketch, "E4567", {"start": v(-80.82, 42.14) * mm, "end": v(-80.82, 42.05) * mm});
            skLineSegment(sketch, "E4568", {"start": v(-80.82, 42.05) * mm, "end": v(-80.83, 41.97) * mm});
            skLineSegment(sketch, "E4569", {"start": v(-80.83, 41.97) * mm, "end": v(-80.83, 41.88) * mm});
            skLineSegment(sketch, "E4570", {"start": v(-80.83, 41.88) * mm, "end": v(-80.83, 41.8) * mm});
            skLineSegment(sketch, "E4571", {"start": v(-80.83, 41.8) * mm, "end": v(-80.82, 41.7) * mm});
            skLineSegment(sketch, "E4572", {"start": v(-80.82, 41.7) * mm, "end": v(-80.81, 41.62) * mm});
            skLineSegment(sketch, "E4573", {"start": v(-80.81, 41.62) * mm, "end": v(-80.8, 41.54) * mm});
            skLineSegment(sketch, "E4574", {"start": v(-80.8, 41.54) * mm, "end": v(-80.79, 41.45) * mm});
            skLineSegment(sketch, "E4575", {"start": v(-80.44, 40.57) * mm, "end": v(-80.4, 40.5) * mm});
            skLineSegment(sketch, "E4576", {"start": v(-80.4, 40.5) * mm, "end": v(-80.34, 40.42) * mm});
            skLineSegment(sketch, "E4577", {"start": v(-80.34, 40.42) * mm, "end": v(-80.29, 40.35) * mm});
            skLineSegment(sketch, "E4578", {"start": v(-80.29, 40.35) * mm, "end": v(-80.23, 40.29) * mm});
            skLineSegment(sketch, "E4579", {"start": v(-80.23, 40.29) * mm, "end": v(-80.18, 40.22) * mm});
            skLineSegment(sketch, "E4580", {"start": v(-80.18, 40.22) * mm, "end": v(-80.12, 40.16) * mm});
            skLineSegment(sketch, "E4581", {"start": v(-80.12, 40.16) * mm, "end": v(-80.06, 40.1) * mm});
            skLineSegment(sketch, "E4582", {"start": v(-80.06, 40.1) * mm, "end": v(-80, 40.04) * mm});
            skLineSegment(sketch, "E4583", {"start": v(-80, 40.04) * mm, "end": v(-79.93, 39.98) * mm});
            skLineSegment(sketch, "E4584", {"start": v(-79.93, 39.98) * mm, "end": v(-79.86, 39.93) * mm});
            skLineSegment(sketch, "E4585", {"start": v(-79.86, 39.93) * mm, "end": v(-79.79, 39.87) * mm});
            skLineSegment(sketch, "E4586", {"start": v(-79.79, 39.87) * mm, "end": v(-79.72, 39.83) * mm});
            skLineSegment(sketch, "E4587", {"start": v(-79.72, 39.83) * mm, "end": v(-79.65, 39.78) * mm});
            skLineSegment(sketch, "E4588", {"start": v(-79.57, 39.73) * mm, "end": v(-79.5, 39.7) * mm});
            skLineSegment(sketch, "E4589", {"start": v(-79.5, 39.7) * mm, "end": v(-79.42, 39.65) * mm});
            skLineSegment(sketch, "E4590", {"start": v(-79.42, 39.65) * mm, "end": v(-79.34, 39.62) * mm});
            skLineSegment(sketch, "E4591", {"start": v(-79.34, 39.62) * mm, "end": v(-79.26, 39.58) * mm});
            skLineSegment(sketch, "E4592", {"start": v(-79.26, 39.58) * mm, "end": v(-79.18, 39.55) * mm});
            skLineSegment(sketch, "E4593", {"start": v(-79.18, 39.55) * mm, "end": v(-79.1, 39.52) * mm});
            skLineSegment(sketch, "E4594", {"start": v(-79.1, 39.52) * mm, "end": v(-79.01, 39.5) * mm});
            skLineSegment(sketch, "E4595", {"start": v(-79.01, 39.5) * mm, "end": v(-78.93, 39.48) * mm});
            skLineSegment(sketch, "E4596", {"start": v(-78.93, 39.48) * mm, "end": v(-78.84, 39.46) * mm});
            skLineSegment(sketch, "E4597", {"start": v(-78.84, 39.46) * mm, "end": v(-78.76, 39.44) * mm});
            skLineSegment(sketch, "E4598", {"start": v(-78.76, 39.44) * mm, "end": v(-78.67, 39.43) * mm});
            skLineSegment(sketch, "E4599", {"start": v(-78.67, 39.43) * mm, "end": v(-78.59, 39.42) * mm});
            skLineSegment(sketch, "E4600", {"start": v(-78.59, 39.42) * mm, "end": v(-78.5, 39.4) * mm});
            skLineSegment(sketch, "E4601", {"start": v(-78.5, 39.4) * mm, "end": v(-78.41, 39.4) * mm});
            skLineSegment(sketch, "E4602", {"start": v(-78.41, 39.4) * mm, "end": v(-78.33, 39.4) * mm});
            skLineSegment(sketch, "E4603", {"start": v(170.03, 83.26) * mm, "end": v(170.03, 68.26) * mm});
            skLineSegment(sketch, "E4604", {"start": v(170.03, 68.26) * mm, "end": v(325.03, 68.26) * mm});
            skLineSegment(sketch, "E4605", {"start": v(325.03, 68.26) * mm, "end": v(325.03, 83.26) * mm});
            skLineSegment(sketch, "E4606", {"start": v(325.03, 83.26) * mm, "end": v(170.03, 83.26) * mm});
            skCircle(sketch, "E4607", {"center": v(187.39, 97.05) * mm, "radius": 2.15 * mm});
            skCircle(sketch, "E4608", {"center": v(196.14, 97.05) * mm, "radius": 1.25 * mm});
            skCircle(sketch, "E4609", {"center": v(252.39, 97.05) * mm, "radius": 3.75 * mm});
            skCircle(sketch, "E4610", {"center": v(252.39, 97.05) * mm, "radius": 1.25 * mm});
            skCircle(sketch, "E4611", {"center": v(317.39, 97.05) * mm, "radius": 2.15 * mm});
            skCircle(sketch, "E4612", {"center": v(173.78, 75.76) * mm, "radius": 2.5 * mm});
            skCircle(sketch, "E4613", {"center": v(173.78, 75.76) * mm, "radius": 1.25 * mm});
            skCircle(sketch, "E4614", {"center": v(187.53, 75.76) * mm, "radius": 1.25 * mm});
            skCircle(sketch, "E4615", {"center": v(220.03, 75.76) * mm, "radius": 1.25 * mm});
            skCircle(sketch, "E4616", {"center": v(247.53, 75.76) * mm, "radius": 1.25 * mm});
            skCircle(sketch, "E4617", {"center": v(247.53, 75.76) * mm, "radius": 3.75 * mm});
            skCircle(sketch, "E4618", {"center": v(296.28, 75.76) * mm, "radius": 1.25 * mm});
            skCircle(sketch, "E4619", {"center": v(321.28, 75.76) * mm, "radius": 1.25 * mm});
            skCircle(sketch, "E4620", {"center": v(321.28, 75.76) * mm, "radius": 2.5 * mm});
            skCircle(sketch, "E4621", {"center": v(173.78, 53.26) * mm, "radius": 2.5 * mm});
            skCircle(sketch, "E4622", {"center": v(173.78, 53.26) * mm, "radius": 1.25 * mm});
            skCircle(sketch, "E4623", {"center": v(247.53, 53.26) * mm, "radius": 3.75 * mm});
            skCircle(sketch, "E4624", {"center": v(247.53, 53.26) * mm, "radius": 1.25 * mm});
            skCircle(sketch, "E4625", {"center": v(321.28, 53.26) * mm, "radius": 2.5 * mm});
            skCircle(sketch, "E4626", {"center": v(321.28, 53.26) * mm, "radius": 1.25 * mm});
            skCircle(sketch, "E4627", {"center": v(197.4, 23.84) * mm, "radius": 3.75 * mm});
            skCircle(sketch, "E4628", {"center": v(164.9, -76.16) * mm, "radius": 2.15 * mm});
            skCircle(sketch, "E4629", {"center": v(229.9, -76.16) * mm, "radius": 2.15 * mm});
            skCircle(sketch, "E4630", {"center": v(248.13, -65.76) * mm, "radius": 1.25 * mm});
            skCircle(sketch, "E4631", {"center": v(254.38, -75.76) * mm, "radius": 2.15 * mm});
            skCircle(sketch, "E4632", {"center": v(319.38, -75.76) * mm, "radius": 2.15 * mm});
            skCircle(sketch, "E4633", {"center": v(325.63, -65.76) * mm, "radius": 1.25 * mm});
            skCircle(sketch, "E4634", {"center": v(248.13, -35.76) * mm, "radius": 1.25 * mm});
            skCircle(sketch, "E4635", {"center": v(289.38, -35.76) * mm, "radius": 3.75 * mm});
            skCircle(sketch, "E4636", {"center": v(325.63, -35.76) * mm, "radius": 1.25 * mm});
            skCircle(sketch, "E4637", {"center": v(289.38, 24.24) * mm, "radius": 3.75 * mm});
            skCircle(sketch, "E4638", {"center": v(341.82, 33.17) * mm, "radius": 2.15 * mm});
            skCircle(sketch, "E4639", {"center": v(341.82, -76.83) * mm, "radius": 2.15 * mm});
            skSolve(sketch);
        }
        {
            var Q0;
            Q0=makeQuery(id+"F3.imprint","IMPRINT",FACE,{"disambiguationData":[TD([[makeQuery(id+"F3.imprint","IMPRINT",EDGE,{"derivedFrom":sQuery(id+"F3.wireOp",EDGE,"E453")}),1.0]])]});
            var Q1;
            Q1=makeQuery(id+"F3.imprint","IMPRINT",FACE,{"disambiguationData":[TD([[makeQuery(id+"F3.imprint","IMPRINT",EDGE,{"derivedFrom":sQuery(id+"F3.wireOp",EDGE,"E1665")}),1.0]])]});
            var Q2;
            Q2=makeQuery(id+"F3.imprint","IMPRINT",FACE,{"disambiguationData":[TD([[makeQuery(id+"F3.imprint","IMPRINT",EDGE,{"derivedFrom":sQuery(id+"F3.wireOp",EDGE,"E1904")}),1.0]])]});
            var Q3;
            Q3=makeQuery(id+"F3.imprint","IMPRINT",FACE,{"disambiguationData":[TD([[makeQuery(id+"F3.imprint","IMPRINT",EDGE,{"derivedFrom":sQuery(id+"F3.wireOp",EDGE,"E1908")}),1.0]])]});
            var Q4;
            Q4=makeQuery(id+"F3.imprint","IMPRINT",FACE,{"disambiguationData":[TD([[makeQuery(id+"F3.imprint","IMPRINT",EDGE,{"derivedFrom":sQuery(id+"F3.wireOp",EDGE,"E4603")}),1.0]])]});
            var Q5;
            Q5=makeQuery(id+"F3.imprint","IMPRINT",FACE,{"disambiguationData":[TD([[makeQuery(id+"F3.imprint","IMPRINT",EDGE,{"derivedFrom":sQuery(id+"F3.wireOp",EDGE,"E1912")}),1.0]])]});
            extrude(context, id + "F4", {"entities" : qUnion([Q0, Q1, Q2, Q3, Q4, Q5]), "depth" : 4 * mm});
        }
        {
            var Q0;
            Q0=makeQuery(id+"F3.imprint","IMPRINT",FACE,{"disambiguationData":[TD([[makeQuery(id+"F3.imprint","IMPRINT",EDGE,{"derivedFrom":sQuery(id+"F3.wireOp",EDGE,"E4616")}),-1.0]])]});
            var Q1;
            Q1=makeQuery(id+"F3.imprint","IMPRINT",FACE,{"disambiguationData":[TD([[makeQuery(id+"F3.imprint","IMPRINT",EDGE,{"derivedFrom":sQuery(id+"F3.wireOp",EDGE,"E4609")}),1.0]])]});
            var Q2;
            Q2=makeQuery(id+"F3.imprint","IMPRINT",FACE,{"disambiguationData":[TD([[makeQuery(id+"F3.imprint","IMPRINT",EDGE,{"derivedFrom":sQuery(id+"F3.wireOp",EDGE,"E4623")}),1.0]])]});
            var Q3;
            Q3=makeQuery(id+"F3.imprint","IMPRINT",FACE,{"disambiguationData":[TD([[makeQuery(id+"F3.imprint","IMPRINT",EDGE,{"derivedFrom":sQuery(id+"F3.wireOp",EDGE,"E4612")}),1.0]])]});
            var Q4;
            Q4=makeQuery(id+"F3.imprint","IMPRINT",FACE,{"disambiguationData":[TD([[makeQuery(id+"F3.imprint","IMPRINT",EDGE,{"derivedFrom":sQuery(id+"F3.wireOp",EDGE,"E4621")}),1.0]])]});
            var Q5;
            Q5=makeQuery(id+"F3.imprint","IMPRINT",FACE,{"disambiguationData":[TD([[makeQuery(id+"F3.imprint","IMPRINT",EDGE,{"derivedFrom":sQuery(id+"F3.wireOp",EDGE,"E4619")}),-1.0]])]});
            var Q6;
            Q6=makeQuery(id+"F3.imprint","IMPRINT",FACE,{"disambiguationData":[TD([[makeQuery(id+"F3.imprint","IMPRINT",EDGE,{"derivedFrom":sQuery(id+"F3.wireOp",EDGE,"E4625")}),1.0]])]});
            extrude(context, id + "F5", {"entities" : qUnion([Q0, Q1, Q2, Q3, Q4, Q5, Q6]), "operationType" : NewBodyOperationType.ADD, "depth" : 3 * mm});
        }
        {
            var Q0;
            Q0=qCreatedBy(makeId("Front.planeOp"),FACE);
            var sketch = newSketch(context, id + "F6", { "sketchPlane" : qUnion([Q0])});
            skLineSegment(sketch, "E4640", {"start": v(-344.5, -59.75) * mm, "end": v(-329.5, -59.75) * mm});
            skLineSegment(sketch, "E4641", {"start": v(-329.5, -59.75) * mm, "end": v(-329.5, 75.25) * mm});
            skLineSegment(sketch, "E4642", {"start": v(-329.5, 75.25) * mm, "end": v(-344.5, 75.25) * mm});
            skLineSegment(sketch, "E4643", {"start": v(-344.5, 75.25) * mm, "end": v(-344.5, -59.75) * mm});
            skLineSegment(sketch, "E4644", {"start": v(-88.9, 63.8) * mm, "end": v(-88.9, 63.85) * mm});
            skLineSegment(sketch, "E4645", {"start": v(-88.9, 63.85) * mm, "end": v(-88.9, 63.9) * mm});
            skLineSegment(sketch, "E4646", {"start": v(-88.9, 63.9) * mm, "end": v(-88.91, 63.93) * mm});
            skLineSegment(sketch, "E4647", {"start": v(-88.91, 63.93) * mm, "end": v(-88.92, 63.98) * mm});
            skLineSegment(sketch, "E4648", {"start": v(-88.92, 63.98) * mm, "end": v(-88.92, 64.02) * mm});
            skLineSegment(sketch, "E4649", {"start": v(-88.92, 64.02) * mm, "end": v(-88.93, 64.06) * mm});
            skLineSegment(sketch, "E4650", {"start": v(-88.93, 64.06) * mm, "end": v(-88.94, 64.1) * mm});
            skLineSegment(sketch, "E4651", {"start": v(-88.94, 64.1) * mm, "end": v(-88.95, 64.15) * mm});
            skLineSegment(sketch, "E4652", {"start": v(-88.97, 64.19) * mm, "end": v(-88.98, 64.23) * mm});
            skLineSegment(sketch, "E4653", {"start": v(-88.98, 64.23) * mm, "end": v(-89, 64.27) * mm});
            skLineSegment(sketch, "E4654", {"start": v(-89, 64.27) * mm, "end": v(-89.01, 64.3) * mm});
            skLineSegment(sketch, "E4655", {"start": v(-89.01, 64.3) * mm, "end": v(-89.03, 64.35) * mm});
            skLineSegment(sketch, "E4656", {"start": v(-89.03, 64.35) * mm, "end": v(-89.05, 64.39) * mm});
            skLineSegment(sketch, "E4657", {"start": v(-89.05, 64.39) * mm, "end": v(-89.07, 64.43) * mm});
            skLineSegment(sketch, "E4658", {"start": v(-89.07, 64.43) * mm, "end": v(-89.1, 64.46) * mm});
            skLineSegment(sketch, "E4659", {"start": v(-89.1, 64.46) * mm, "end": v(-89.12, 64.5) * mm});
            skLineSegment(sketch, "E4660", {"start": v(-89.12, 64.5) * mm, "end": v(-89.14, 64.53) * mm});
            skLineSegment(sketch, "E4661", {"start": v(-89.14, 64.53) * mm, "end": v(-89.17, 64.57) * mm});
            skLineSegment(sketch, "E4662", {"start": v(-89.17, 64.57) * mm, "end": v(-89.2, 64.6) * mm});
            skLineSegment(sketch, "E4663", {"start": v(-89.2, 64.6) * mm, "end": v(-89.22, 64.64) * mm});
            skLineSegment(sketch, "E4664", {"start": v(-89.22, 64.64) * mm, "end": v(-89.25, 64.67) * mm});
            skLineSegment(sketch, "E4665", {"start": v(-89.25, 64.67) * mm, "end": v(-89.28, 64.7) * mm});
            skLineSegment(sketch, "E4666", {"start": v(-89.28, 64.7) * mm, "end": v(-89.31, 64.73) * mm});
            skLineSegment(sketch, "E4667", {"start": v(-89.31, 64.73) * mm, "end": v(-89.35, 64.76) * mm});
            skLineSegment(sketch, "E4668", {"start": v(-89.35, 64.76) * mm, "end": v(-89.38, 64.78) * mm});
            skLineSegment(sketch, "E4669", {"start": v(-89.38, 64.78) * mm, "end": v(-89.42, 64.81) * mm});
            skLineSegment(sketch, "E4670", {"start": v(-89.42, 64.81) * mm, "end": v(-89.45, 64.84) * mm});
            skLineSegment(sketch, "E4671", {"start": v(-89.45, 64.84) * mm, "end": v(-89.49, 64.86) * mm});
            skLineSegment(sketch, "E4672", {"start": v(-89.49, 64.86) * mm, "end": v(-89.52, 64.88) * mm});
            skLineSegment(sketch, "E4673", {"start": v(-89.56, 64.9) * mm, "end": v(-89.6, 64.92) * mm});
            skLineSegment(sketch, "E4674", {"start": v(-89.6, 64.92) * mm, "end": v(-89.64, 64.94) * mm});
            skLineSegment(sketch, "E4675", {"start": v(-89.64, 64.94) * mm, "end": v(-89.68, 64.96) * mm});
            skLineSegment(sketch, "E4676", {"start": v(-89.68, 64.96) * mm, "end": v(-89.72, 64.98) * mm});
            skLineSegment(sketch, "E4677", {"start": v(-89.72, 64.98) * mm, "end": v(-89.76, 64.99) * mm});
            skLineSegment(sketch, "E4678", {"start": v(-89.76, 64.99) * mm, "end": v(-89.8, 65) * mm});
            skLineSegment(sketch, "E4679", {"start": v(-89.8, 65) * mm, "end": v(-89.84, 65.01) * mm});
            skLineSegment(sketch, "E4680", {"start": v(-89.84, 65.01) * mm, "end": v(-89.89, 65.02) * mm});
            skLineSegment(sketch, "E4681", {"start": v(-89.89, 65.02) * mm, "end": v(-89.93, 65.03) * mm});
            skLineSegment(sketch, "E4682", {"start": v(-89.93, 65.03) * mm, "end": v(-89.97, 65.04) * mm});
            skLineSegment(sketch, "E4683", {"start": v(-89.97, 65.04) * mm, "end": v(-90.01, 65.05) * mm});
            skLineSegment(sketch, "E4684", {"start": v(-90.01, 65.05) * mm, "end": v(-90.06, 65.05) * mm});
            skLineSegment(sketch, "E4685", {"start": v(-90.06, 65.05) * mm, "end": v(-90.1, 65.05) * mm});
            skLineSegment(sketch, "E4686", {"start": v(-90.1, 65.05) * mm, "end": v(-90.14, 65.05) * mm});
            skLineSegment(sketch, "E4687", {"start": v(-90.14, 65.05) * mm, "end": v(-90.19, 65.05) * mm});
            skLineSegment(sketch, "E4688", {"start": v(-90.19, 65.05) * mm, "end": v(-90.23, 65.05) * mm});
            skLineSegment(sketch, "E4689", {"start": v(-90.23, 65.05) * mm, "end": v(-90.27, 65.05) * mm});
            skLineSegment(sketch, "E4690", {"start": v(-90.27, 65.05) * mm, "end": v(-90.32, 65.04) * mm});
            skLineSegment(sketch, "E4691", {"start": v(-90.32, 65.04) * mm, "end": v(-90.36, 65.04) * mm});
            skLineSegment(sketch, "E4692", {"start": v(-90.36, 65.04) * mm, "end": v(-90.4, 65.03) * mm});
            skLineSegment(sketch, "E4693", {"start": v(-90.4, 65.03) * mm, "end": v(-90.45, 65.02) * mm});
            skLineSegment(sketch, "E4694", {"start": v(-90.45, 65.02) * mm, "end": v(-90.49, 65) * mm});
            skLineSegment(sketch, "E4695", {"start": v(-90.49, 65) * mm, "end": v(-90.53, 65) * mm});
            skLineSegment(sketch, "E4696", {"start": v(-90.53, 65) * mm, "end": v(-90.57, 64.98) * mm});
            skLineSegment(sketch, "E4697", {"start": v(-90.57, 64.98) * mm, "end": v(-90.61, 64.97) * mm});
            skLineSegment(sketch, "E4698", {"start": v(-90.61, 64.97) * mm, "end": v(-90.65, 64.95) * mm});
            skLineSegment(sketch, "E4699", {"start": v(-90.65, 64.95) * mm, "end": v(-90.7, 64.93) * mm});
            skLineSegment(sketch, "E4700", {"start": v(-90.7, 64.93) * mm, "end": v(-90.73, 64.91) * mm});
            skLineSegment(sketch, "E4701", {"start": v(-90.73, 64.91) * mm, "end": v(-90.77, 64.9) * mm});
            skLineSegment(sketch, "E4702", {"start": v(-90.77, 64.9) * mm, "end": v(-90.8, 64.87) * mm});
            skLineSegment(sketch, "E4703", {"start": v(-90.8, 64.87) * mm, "end": v(-90.84, 64.85) * mm});
            skLineSegment(sketch, "E4704", {"start": v(-90.84, 64.85) * mm, "end": v(-90.88, 64.82) * mm});
            skLineSegment(sketch, "E4705", {"start": v(-90.88, 64.82) * mm, "end": v(-90.91, 64.8) * mm});
            skLineSegment(sketch, "E4706", {"start": v(-90.91, 64.8) * mm, "end": v(-90.95, 64.77) * mm});
            skLineSegment(sketch, "E4707", {"start": v(-90.95, 64.77) * mm, "end": v(-90.98, 64.74) * mm});
            skLineSegment(sketch, "E4708", {"start": v(-90.98, 64.74) * mm, "end": v(-91.01, 64.71) * mm});
            skLineSegment(sketch, "E4709", {"start": v(-91.01, 64.71) * mm, "end": v(-91.04, 64.68) * mm});
            skLineSegment(sketch, "E4710", {"start": v(-91.04, 64.68) * mm, "end": v(-91.07, 64.65) * mm});
            skLineSegment(sketch, "E4711", {"start": v(-91.07, 64.65) * mm, "end": v(-91.1, 64.62) * mm});
            skLineSegment(sketch, "E4712", {"start": v(-91.1, 64.62) * mm, "end": v(-91.13, 64.59) * mm});
            skLineSegment(sketch, "E4713", {"start": v(-91.13, 64.59) * mm, "end": v(-91.16, 64.55) * mm});
            skLineSegment(sketch, "E4714", {"start": v(-91.16, 64.55) * mm, "end": v(-91.18, 64.52) * mm});
            skLineSegment(sketch, "E4715", {"start": v(-91.18, 64.52) * mm, "end": v(-91.2, 64.48) * mm});
            skLineSegment(sketch, "E4716", {"start": v(-91.2, 64.48) * mm, "end": v(-91.23, 64.44) * mm});
            skLineSegment(sketch, "E4717", {"start": v(-91.23, 64.44) * mm, "end": v(-91.25, 64.4) * mm});
            skLineSegment(sketch, "E4718", {"start": v(-91.25, 64.4) * mm, "end": v(-91.27, 64.37) * mm});
            skLineSegment(sketch, "E4719", {"start": v(-91.29, 64.33) * mm, "end": v(-91.3, 64.29) * mm});
            skLineSegment(sketch, "E4720", {"start": v(-91.3, 64.29) * mm, "end": v(-91.32, 64.25) * mm});
            skLineSegment(sketch, "E4721", {"start": v(-91.32, 64.25) * mm, "end": v(-91.34, 64.2) * mm});
            skLineSegment(sketch, "E4722", {"start": v(-91.34, 64.2) * mm, "end": v(-91.35, 64.17) * mm});
            skLineSegment(sketch, "E4723", {"start": v(-91.35, 64.17) * mm, "end": v(-91.36, 64.13) * mm});
            skLineSegment(sketch, "E4724", {"start": v(-91.36, 64.13) * mm, "end": v(-91.37, 64.08) * mm});
            skLineSegment(sketch, "E4725", {"start": v(-91.37, 64.08) * mm, "end": v(-91.38, 64.04) * mm});
            skLineSegment(sketch, "E4726", {"start": v(-91.38, 64.04) * mm, "end": v(-91.4, 64) * mm});
            skLineSegment(sketch, "E4727", {"start": v(-91.4, 64) * mm, "end": v(-91.4, 63.96) * mm});
            skLineSegment(sketch, "E4728", {"start": v(-91.4, 63.96) * mm, "end": v(-91.4, 63.91) * mm});
            skLineSegment(sketch, "E4729", {"start": v(-91.4, 63.91) * mm, "end": v(-91.4, 63.87) * mm});
            skLineSegment(sketch, "E4730", {"start": v(-91.4, 63.87) * mm, "end": v(-91.4, 63.83) * mm});
            skLineSegment(sketch, "E4731", {"start": v(-91.4, 63.83) * mm, "end": v(-91.4, 63.78) * mm});
            skLineSegment(sketch, "E4732", {"start": v(-91.4, 63.78) * mm, "end": v(-91.4, 63.74) * mm});
            skLineSegment(sketch, "E4733", {"start": v(-91.4, 63.74) * mm, "end": v(-91.4, 63.7) * mm});
            skLineSegment(sketch, "E4734", {"start": v(-91.4, 63.7) * mm, "end": v(-91.4, 63.65) * mm});
            skLineSegment(sketch, "E4735", {"start": v(-91.4, 63.65) * mm, "end": v(-91.4, 63.6) * mm});
            skLineSegment(sketch, "E4736", {"start": v(-91.4, 63.6) * mm, "end": v(-91.38, 63.57) * mm});
            skLineSegment(sketch, "E4737", {"start": v(-91.38, 63.57) * mm, "end": v(-91.37, 63.52) * mm});
            skLineSegment(sketch, "E4738", {"start": v(-91.37, 63.52) * mm, "end": v(-91.36, 63.48) * mm});
            skLineSegment(sketch, "E4739", {"start": v(-91.36, 63.48) * mm, "end": v(-91.35, 63.44) * mm});
            skLineSegment(sketch, "E4740", {"start": v(-91.35, 63.44) * mm, "end": v(-91.34, 63.4) * mm});
            skLineSegment(sketch, "E4741", {"start": v(-91.34, 63.4) * mm, "end": v(-91.32, 63.36) * mm});
            skLineSegment(sketch, "E4742", {"start": v(-91.32, 63.36) * mm, "end": v(-91.3, 63.32) * mm});
            skLineSegment(sketch, "E4743", {"start": v(-91.3, 63.32) * mm, "end": v(-91.29, 63.28) * mm});
            skLineSegment(sketch, "E4744", {"start": v(-91.29, 63.28) * mm, "end": v(-91.27, 63.24) * mm});
            skLineSegment(sketch, "E4745", {"start": v(-91.27, 63.24) * mm, "end": v(-91.25, 63.2) * mm});
            skLineSegment(sketch, "E4746", {"start": v(-91.25, 63.2) * mm, "end": v(-91.23, 63.16) * mm});
            skLineSegment(sketch, "E4747", {"start": v(-91.23, 63.16) * mm, "end": v(-91.2, 63.13) * mm});
            skLineSegment(sketch, "E4748", {"start": v(-91.2, 63.13) * mm, "end": v(-91.18, 63.1) * mm});
            skLineSegment(sketch, "E4749", {"start": v(-91.18, 63.1) * mm, "end": v(-91.16, 63.06) * mm});
            skLineSegment(sketch, "E4750", {"start": v(-91.16, 63.06) * mm, "end": v(-91.13, 63.02) * mm});
            skLineSegment(sketch, "E4751", {"start": v(-91.13, 63.02) * mm, "end": v(-91.1, 62.99) * mm});
            skLineSegment(sketch, "E4752", {"start": v(-91.1, 62.99) * mm, "end": v(-91.07, 62.96) * mm});
            skLineSegment(sketch, "E4753", {"start": v(-91.07, 62.96) * mm, "end": v(-91.04, 62.92) * mm});
            skLineSegment(sketch, "E4754", {"start": v(-91.04, 62.92) * mm, "end": v(-91.01, 62.9) * mm});
            skLineSegment(sketch, "E4755", {"start": v(-91.01, 62.9) * mm, "end": v(-90.98, 62.86) * mm});
            skLineSegment(sketch, "E4756", {"start": v(-90.98, 62.86) * mm, "end": v(-90.95, 62.84) * mm});
            skLineSegment(sketch, "E4757", {"start": v(-90.95, 62.84) * mm, "end": v(-90.91, 62.8) * mm});
            skLineSegment(sketch, "E4758", {"start": v(-90.91, 62.8) * mm, "end": v(-90.88, 62.78) * mm});
            skLineSegment(sketch, "E4759", {"start": v(-90.88, 62.78) * mm, "end": v(-90.84, 62.76) * mm});
            skLineSegment(sketch, "E4760", {"start": v(-90.84, 62.76) * mm, "end": v(-90.8, 62.74) * mm});
            skLineSegment(sketch, "E4761", {"start": v(-90.8, 62.74) * mm, "end": v(-90.77, 62.71) * mm});
            skLineSegment(sketch, "E4762", {"start": v(-90.77, 62.71) * mm, "end": v(-90.73, 62.7) * mm});
            skLineSegment(sketch, "E4763", {"start": v(-90.73, 62.7) * mm, "end": v(-90.7, 62.67) * mm});
            skLineSegment(sketch, "E4764", {"start": v(-90.7, 62.67) * mm, "end": v(-90.65, 62.66) * mm});
            skLineSegment(sketch, "E4765", {"start": v(-90.65, 62.66) * mm, "end": v(-90.61, 62.64) * mm});
            skLineSegment(sketch, "E4766", {"start": v(-90.61, 62.64) * mm, "end": v(-90.57, 62.62) * mm});
            skLineSegment(sketch, "E4767", {"start": v(-90.57, 62.62) * mm, "end": v(-90.53, 62.61) * mm});
            skLineSegment(sketch, "E4768", {"start": v(-90.53, 62.61) * mm, "end": v(-90.49, 62.6) * mm});
            skLineSegment(sketch, "E4769", {"start": v(-90.49, 62.6) * mm, "end": v(-90.45, 62.59) * mm});
            skLineSegment(sketch, "E4770", {"start": v(-90.45, 62.59) * mm, "end": v(-90.4, 62.58) * mm});
            skLineSegment(sketch, "E4771", {"start": v(-90.4, 62.58) * mm, "end": v(-90.36, 62.57) * mm});
            skLineSegment(sketch, "E4772", {"start": v(-90.36, 62.57) * mm, "end": v(-90.32, 62.56) * mm});
            skLineSegment(sketch, "E4773", {"start": v(-90.32, 62.56) * mm, "end": v(-90.27, 62.56) * mm});
            skLineSegment(sketch, "E4774", {"start": v(-90.27, 62.56) * mm, "end": v(-90.23, 62.56) * mm});
            skLineSegment(sketch, "E4775", {"start": v(-90.23, 62.56) * mm, "end": v(-90.19, 62.55) * mm});
            skLineSegment(sketch, "E4776", {"start": v(-90.19, 62.55) * mm, "end": v(-90.14, 62.55) * mm});
            skLineSegment(sketch, "E4777", {"start": v(-90.14, 62.55) * mm, "end": v(-90.1, 62.55) * mm});
            skLineSegment(sketch, "E4778", {"start": v(-90.1, 62.55) * mm, "end": v(-90.06, 62.56) * mm});
            skLineSegment(sketch, "E4779", {"start": v(-90.06, 62.56) * mm, "end": v(-90.01, 62.56) * mm});
            skLineSegment(sketch, "E4780", {"start": v(-90.01, 62.56) * mm, "end": v(-89.97, 62.57) * mm});
            skLineSegment(sketch, "E4781", {"start": v(-89.97, 62.57) * mm, "end": v(-89.93, 62.57) * mm});
            skLineSegment(sketch, "E4782", {"start": v(-89.93, 62.57) * mm, "end": v(-89.89, 62.58) * mm});
            skLineSegment(sketch, "E4783", {"start": v(-89.64, 62.67) * mm, "end": v(-89.6, 62.68) * mm});
            skLineSegment(sketch, "E4784", {"start": v(-89.6, 62.68) * mm, "end": v(-89.56, 62.7) * mm});
            skLineSegment(sketch, "E4785", {"start": v(-89.56, 62.7) * mm, "end": v(-89.52, 62.72) * mm});
            skLineSegment(sketch, "E4786", {"start": v(-89.52, 62.72) * mm, "end": v(-89.49, 62.75) * mm});
            skLineSegment(sketch, "E4787", {"start": v(-89.49, 62.75) * mm, "end": v(-89.45, 62.77) * mm});
            skLineSegment(sketch, "E4788", {"start": v(-89.45, 62.77) * mm, "end": v(-89.42, 62.8) * mm});
            skLineSegment(sketch, "E4789", {"start": v(-89.42, 62.8) * mm, "end": v(-89.38, 62.82) * mm});
            skLineSegment(sketch, "E4790", {"start": v(-89.38, 62.82) * mm, "end": v(-89.35, 62.85) * mm});
            skLineSegment(sketch, "E4791", {"start": v(-89.35, 62.85) * mm, "end": v(-89.31, 62.88) * mm});
            skLineSegment(sketch, "E4792", {"start": v(-89.31, 62.88) * mm, "end": v(-89.28, 62.9) * mm});
            skLineSegment(sketch, "E4793", {"start": v(-89.28, 62.9) * mm, "end": v(-89.25, 62.94) * mm});
            skLineSegment(sketch, "E4794", {"start": v(-89.25, 62.94) * mm, "end": v(-89.22, 62.97) * mm});
            skLineSegment(sketch, "E4795", {"start": v(-89.22, 62.97) * mm, "end": v(-89.2, 63) * mm});
            skLineSegment(sketch, "E4796", {"start": v(-89.2, 63) * mm, "end": v(-89.17, 63.04) * mm});
            skLineSegment(sketch, "E4797", {"start": v(-89.17, 63.04) * mm, "end": v(-89.14, 63.07) * mm});
            skLineSegment(sketch, "E4798", {"start": v(-89.14, 63.07) * mm, "end": v(-89.12, 63.1) * mm});
            skLineSegment(sketch, "E4799", {"start": v(-89.12, 63.1) * mm, "end": v(-89.1, 63.14) * mm});
            skLineSegment(sketch, "E4800", {"start": v(-89.1, 63.14) * mm, "end": v(-89.07, 63.18) * mm});
            skLineSegment(sketch, "E4801", {"start": v(-89.07, 63.18) * mm, "end": v(-89.05, 63.22) * mm});
            skLineSegment(sketch, "E4802", {"start": v(-89.05, 63.22) * mm, "end": v(-89.03, 63.26) * mm});
            skLineSegment(sketch, "E4803", {"start": v(-89.03, 63.26) * mm, "end": v(-89.01, 63.3) * mm});
            skLineSegment(sketch, "E4804", {"start": v(-89.01, 63.3) * mm, "end": v(-89, 63.34) * mm});
            skLineSegment(sketch, "E4805", {"start": v(-89, 63.34) * mm, "end": v(-88.98, 63.38) * mm});
            skLineSegment(sketch, "E4806", {"start": v(-88.98, 63.38) * mm, "end": v(-88.97, 63.42) * mm});
            skLineSegment(sketch, "E4807", {"start": v(-88.97, 63.42) * mm, "end": v(-88.95, 63.46) * mm});
            skLineSegment(sketch, "E4808", {"start": v(-88.95, 63.46) * mm, "end": v(-88.94, 63.5) * mm});
            skLineSegment(sketch, "E4809", {"start": v(-88.94, 63.5) * mm, "end": v(-88.93, 63.55) * mm});
            skLineSegment(sketch, "E4810", {"start": v(-88.93, 63.55) * mm, "end": v(-88.92, 63.59) * mm});
            skLineSegment(sketch, "E4811", {"start": v(-88.92, 63.59) * mm, "end": v(-88.92, 63.63) * mm});
            skLineSegment(sketch, "E4812", {"start": v(-88.92, 63.63) * mm, "end": v(-88.91, 63.67) * mm});
            skLineSegment(sketch, "E4813", {"start": v(-88.91, 63.67) * mm, "end": v(-88.9, 63.72) * mm});
            skLineSegment(sketch, "E4814", {"start": v(-88.9, 63.72) * mm, "end": v(-88.9, 63.76) * mm});
            skLineSegment(sketch, "E4815", {"start": v(-88.9, 63.76) * mm, "end": v(-88.9, 63.8) * mm});
            skLineSegment(sketch, "E4816", {"start": v(-88.9, -63.7) * mm, "end": v(-88.9, -63.65) * mm});
            skLineSegment(sketch, "E4817", {"start": v(-88.9, -63.65) * mm, "end": v(-88.9, -63.6) * mm});
            skLineSegment(sketch, "E4818", {"start": v(-88.9, -63.6) * mm, "end": v(-88.91, -63.57) * mm});
            skLineSegment(sketch, "E4819", {"start": v(-88.91, -63.57) * mm, "end": v(-88.92, -63.52) * mm});
            skLineSegment(sketch, "E4820", {"start": v(-88.92, -63.52) * mm, "end": v(-88.92, -63.48) * mm});
            skLineSegment(sketch, "E4821", {"start": v(-88.92, -63.48) * mm, "end": v(-88.93, -63.44) * mm});
            skLineSegment(sketch, "E4822", {"start": v(-88.93, -63.44) * mm, "end": v(-88.94, -63.4) * mm});
            skLineSegment(sketch, "E4823", {"start": v(-88.94, -63.4) * mm, "end": v(-88.95, -63.35) * mm});
            skLineSegment(sketch, "E4824", {"start": v(-88.95, -63.35) * mm, "end": v(-88.97, -63.31) * mm});
            skLineSegment(sketch, "E4825", {"start": v(-88.97, -63.31) * mm, "end": v(-88.98, -63.27) * mm});
            skLineSegment(sketch, "E4826", {"start": v(-88.98, -63.27) * mm, "end": v(-89, -63.23) * mm});
            skLineSegment(sketch, "E4827", {"start": v(-89, -63.23) * mm, "end": v(-89.01, -63.2) * mm});
            skLineSegment(sketch, "E4828", {"start": v(-89.01, -63.2) * mm, "end": v(-89.03, -63.15) * mm});
            skLineSegment(sketch, "E4829", {"start": v(-89.03, -63.15) * mm, "end": v(-89.05, -63.11) * mm});
            skLineSegment(sketch, "E4830", {"start": v(-89.05, -63.11) * mm, "end": v(-89.07, -63.07) * mm});
            skLineSegment(sketch, "E4831", {"start": v(-89.07, -63.07) * mm, "end": v(-89.1, -63.04) * mm});
            skLineSegment(sketch, "E4832", {"start": v(-89.1, -63.04) * mm, "end": v(-89.12, -63) * mm});
            skLineSegment(sketch, "E4833", {"start": v(-89.12, -63) * mm, "end": v(-89.14, -62.97) * mm});
            skLineSegment(sketch, "E4834", {"start": v(-89.14, -62.97) * mm, "end": v(-89.17, -62.93) * mm});
            skLineSegment(sketch, "E4835", {"start": v(-89.17, -62.93) * mm, "end": v(-89.2, -62.9) * mm});
            skLineSegment(sketch, "E4836", {"start": v(-89.2, -62.9) * mm, "end": v(-89.22, -62.86) * mm});
            skLineSegment(sketch, "E4837", {"start": v(-89.22, -62.86) * mm, "end": v(-89.25, -62.83) * mm});
            skLineSegment(sketch, "E4838", {"start": v(-89.25, -62.83) * mm, "end": v(-89.28, -62.8) * mm});
            skLineSegment(sketch, "E4839", {"start": v(-89.28, -62.8) * mm, "end": v(-89.31, -62.77) * mm});
            skLineSegment(sketch, "E4840", {"start": v(-89.31, -62.77) * mm, "end": v(-89.35, -62.74) * mm});
            skLineSegment(sketch, "E4841", {"start": v(-89.35, -62.74) * mm, "end": v(-89.38, -62.72) * mm});
            skLineSegment(sketch, "E4842", {"start": v(-89.38, -62.72) * mm, "end": v(-89.42, -62.69) * mm});
            skLineSegment(sketch, "E4843", {"start": v(-89.42, -62.69) * mm, "end": v(-89.45, -62.66) * mm});
            skLineSegment(sketch, "E4844", {"start": v(-89.45, -62.66) * mm, "end": v(-89.49, -62.64) * mm});
            skLineSegment(sketch, "E4845", {"start": v(-89.49, -62.64) * mm, "end": v(-89.52, -62.62) * mm});
            skLineSegment(sketch, "E4846", {"start": v(-89.52, -62.62) * mm, "end": v(-89.56, -62.6) * mm});
            skLineSegment(sketch, "E4847", {"start": v(-89.56, -62.6) * mm, "end": v(-89.6, -62.58) * mm});
            skLineSegment(sketch, "E4848", {"start": v(-89.6, -62.58) * mm, "end": v(-89.64, -62.56) * mm});
            skLineSegment(sketch, "E4849", {"start": v(-89.64, -62.56) * mm, "end": v(-89.68, -62.54) * mm});
            skLineSegment(sketch, "E4850", {"start": v(-89.68, -62.54) * mm, "end": v(-89.72, -62.52) * mm});
            skLineSegment(sketch, "E4851", {"start": v(-89.72, -62.52) * mm, "end": v(-89.76, -62.51) * mm});
            skLineSegment(sketch, "E4852", {"start": v(-89.8, -62.5) * mm, "end": v(-89.84, -62.49) * mm});
            skLineSegment(sketch, "E4853", {"start": v(-89.84, -62.49) * mm, "end": v(-89.89, -62.48) * mm});
            skLineSegment(sketch, "E4854", {"start": v(-89.89, -62.48) * mm, "end": v(-89.93, -62.47) * mm});
            skLineSegment(sketch, "E4855", {"start": v(-89.93, -62.47) * mm, "end": v(-89.97, -62.46) * mm});
            skLineSegment(sketch, "E4856", {"start": v(-89.97, -62.46) * mm, "end": v(-90.01, -62.45) * mm});
            skLineSegment(sketch, "E4857", {"start": v(-90.01, -62.45) * mm, "end": v(-90.06, -62.45) * mm});
            skLineSegment(sketch, "E4858", {"start": v(-90.06, -62.45) * mm, "end": v(-90.1, -62.45) * mm});
            skLineSegment(sketch, "E4859", {"start": v(-90.1, -62.45) * mm, "end": v(-90.14, -62.45) * mm});
            skLineSegment(sketch, "E4860", {"start": v(-90.14, -62.45) * mm, "end": v(-90.19, -62.45) * mm});
            skLineSegment(sketch, "E4861", {"start": v(-90.19, -62.45) * mm, "end": v(-90.23, -62.45) * mm});
            skLineSegment(sketch, "E4862", {"start": v(-90.23, -62.45) * mm, "end": v(-90.27, -62.45) * mm});
            skLineSegment(sketch, "E4863", {"start": v(-90.27, -62.45) * mm, "end": v(-90.32, -62.46) * mm});
            skLineSegment(sketch, "E4864", {"start": v(-90.32, -62.46) * mm, "end": v(-90.36, -62.46) * mm});
            skLineSegment(sketch, "E4865", {"start": v(-90.36, -62.46) * mm, "end": v(-90.4, -62.47) * mm});
            skLineSegment(sketch, "E4866", {"start": v(-90.4, -62.47) * mm, "end": v(-90.45, -62.48) * mm});
            skLineSegment(sketch, "E4867", {"start": v(-90.45, -62.48) * mm, "end": v(-90.49, -62.5) * mm});
            skLineSegment(sketch, "E4868", {"start": v(-90.49, -62.5) * mm, "end": v(-90.53, -62.5) * mm});
            skLineSegment(sketch, "E4869", {"start": v(-90.53, -62.5) * mm, "end": v(-90.57, -62.52) * mm});
            skLineSegment(sketch, "E4870", {"start": v(-90.57, -62.52) * mm, "end": v(-90.61, -62.53) * mm});
            skLineSegment(sketch, "E4871", {"start": v(-90.61, -62.53) * mm, "end": v(-90.65, -62.55) * mm});
            skLineSegment(sketch, "E4872", {"start": v(-90.65, -62.55) * mm, "end": v(-90.7, -62.57) * mm});
            skLineSegment(sketch, "E4873", {"start": v(-90.7, -62.57) * mm, "end": v(-90.73, -62.59) * mm});
            skLineSegment(sketch, "E4874", {"start": v(-90.73, -62.59) * mm, "end": v(-90.77, -62.6) * mm});
            skLineSegment(sketch, "E4875", {"start": v(-90.77, -62.6) * mm, "end": v(-90.8, -62.63) * mm});
            skLineSegment(sketch, "E4876", {"start": v(-90.8, -62.63) * mm, "end": v(-90.84, -62.65) * mm});
            skLineSegment(sketch, "E4877", {"start": v(-90.84, -62.65) * mm, "end": v(-90.88, -62.68) * mm});
            skLineSegment(sketch, "E4878", {"start": v(-90.88, -62.68) * mm, "end": v(-90.91, -62.7) * mm});
            skLineSegment(sketch, "E4879", {"start": v(-90.91, -62.7) * mm, "end": v(-90.95, -62.73) * mm});
            skLineSegment(sketch, "E4880", {"start": v(-90.95, -62.73) * mm, "end": v(-90.98, -62.76) * mm});
            skLineSegment(sketch, "E4881", {"start": v(-90.98, -62.76) * mm, "end": v(-91.01, -62.79) * mm});
            skLineSegment(sketch, "E4882", {"start": v(-91.01, -62.79) * mm, "end": v(-91.04, -62.82) * mm});
            skLineSegment(sketch, "E4883", {"start": v(-91.04, -62.82) * mm, "end": v(-91.07, -62.85) * mm});
            skLineSegment(sketch, "E4884", {"start": v(-91.07, -62.85) * mm, "end": v(-91.1, -62.88) * mm});
            skLineSegment(sketch, "E4885", {"start": v(-91.13, -62.91) * mm, "end": v(-91.16, -62.95) * mm});
            skLineSegment(sketch, "E4886", {"start": v(-91.16, -62.95) * mm, "end": v(-91.18, -62.98) * mm});
            skLineSegment(sketch, "E4887", {"start": v(-91.18, -62.98) * mm, "end": v(-91.2, -63.02) * mm});
            skLineSegment(sketch, "E4888", {"start": v(-91.2, -63.02) * mm, "end": v(-91.23, -63.06) * mm});
            skLineSegment(sketch, "E4889", {"start": v(-91.23, -63.06) * mm, "end": v(-91.25, -63.1) * mm});
            skLineSegment(sketch, "E4890", {"start": v(-91.25, -63.1) * mm, "end": v(-91.27, -63.13) * mm});
            skLineSegment(sketch, "E4891", {"start": v(-91.27, -63.13) * mm, "end": v(-91.29, -63.17) * mm});
            skLineSegment(sketch, "E4892", {"start": v(-91.29, -63.17) * mm, "end": v(-91.3, -63.21) * mm});
            skLineSegment(sketch, "E4893", {"start": v(-91.3, -63.21) * mm, "end": v(-91.32, -63.25) * mm});
            skLineSegment(sketch, "E4894", {"start": v(-91.32, -63.25) * mm, "end": v(-91.34, -63.3) * mm});
            skLineSegment(sketch, "E4895", {"start": v(-91.34, -63.3) * mm, "end": v(-91.35, -63.33) * mm});
            skLineSegment(sketch, "E4896", {"start": v(-91.35, -63.33) * mm, "end": v(-91.36, -63.37) * mm});
            skLineSegment(sketch, "E4897", {"start": v(-91.36, -63.37) * mm, "end": v(-91.37, -63.42) * mm});
            skLineSegment(sketch, "E4898", {"start": v(-91.37, -63.42) * mm, "end": v(-91.38, -63.46) * mm});
            skLineSegment(sketch, "E4899", {"start": v(-91.38, -63.46) * mm, "end": v(-91.4, -63.5) * mm});
            skLineSegment(sketch, "E4900", {"start": v(-91.4, -63.5) * mm, "end": v(-91.4, -63.54) * mm});
            skLineSegment(sketch, "E4901", {"start": v(-91.4, -63.54) * mm, "end": v(-91.4, -63.59) * mm});
            skLineSegment(sketch, "E4902", {"start": v(-91.4, -63.59) * mm, "end": v(-91.4, -63.63) * mm});
            skLineSegment(sketch, "E4903", {"start": v(-91.4, -63.63) * mm, "end": v(-91.4, -63.67) * mm});
            skLineSegment(sketch, "E4904", {"start": v(-91.4, -63.67) * mm, "end": v(-91.4, -63.72) * mm});
            skLineSegment(sketch, "E4905", {"start": v(-91.4, -63.72) * mm, "end": v(-91.4, -63.76) * mm});
            skLineSegment(sketch, "E4906", {"start": v(-91.4, -63.76) * mm, "end": v(-91.4, -63.8) * mm});
            skLineSegment(sketch, "E4907", {"start": v(-91.4, -63.8) * mm, "end": v(-91.4, -63.85) * mm});
            skLineSegment(sketch, "E4908", {"start": v(-91.4, -63.85) * mm, "end": v(-91.4, -63.9) * mm});
            skLineSegment(sketch, "E4909", {"start": v(-91.4, -63.9) * mm, "end": v(-91.38, -63.93) * mm});
            skLineSegment(sketch, "E4910", {"start": v(-91.38, -63.93) * mm, "end": v(-91.37, -63.98) * mm});
            skLineSegment(sketch, "E4911", {"start": v(-91.37, -63.98) * mm, "end": v(-91.36, -64.02) * mm});
            skLineSegment(sketch, "E4912", {"start": v(-91.36, -64.02) * mm, "end": v(-91.35, -64.06) * mm});
            skLineSegment(sketch, "E4913", {"start": v(-91.35, -64.06) * mm, "end": v(-91.34, -64.1) * mm});
            skLineSegment(sketch, "E4914", {"start": v(-91.34, -64.1) * mm, "end": v(-91.32, -64.14) * mm});
            skLineSegment(sketch, "E4915", {"start": v(-91.32, -64.14) * mm, "end": v(-91.3, -64.18) * mm});
            skLineSegment(sketch, "E4916", {"start": v(-91.29, -64.22) * mm, "end": v(-91.27, -64.26) * mm});
            skLineSegment(sketch, "E4917", {"start": v(-91.27, -64.26) * mm, "end": v(-91.25, -64.3) * mm});
            skLineSegment(sketch, "E4918", {"start": v(-91.25, -64.3) * mm, "end": v(-91.23, -64.34) * mm});
            skLineSegment(sketch, "E4919", {"start": v(-91.23, -64.34) * mm, "end": v(-91.2, -64.37) * mm});
            skLineSegment(sketch, "E4920", {"start": v(-91.2, -64.37) * mm, "end": v(-91.18, -64.4) * mm});
            skLineSegment(sketch, "E4921", {"start": v(-91.18, -64.4) * mm, "end": v(-91.16, -64.44) * mm});
            skLineSegment(sketch, "E4922", {"start": v(-91.16, -64.44) * mm, "end": v(-91.13, -64.48) * mm});
            skLineSegment(sketch, "E4923", {"start": v(-91.13, -64.48) * mm, "end": v(-91.1, -64.51) * mm});
            skLineSegment(sketch, "E4924", {"start": v(-91.1, -64.51) * mm, "end": v(-91.07, -64.54) * mm});
            skLineSegment(sketch, "E4925", {"start": v(-91.07, -64.54) * mm, "end": v(-91.04, -64.58) * mm});
            skLineSegment(sketch, "E4926", {"start": v(-91.04, -64.58) * mm, "end": v(-91.01, -64.6) * mm});
            skLineSegment(sketch, "E4927", {"start": v(-91.01, -64.6) * mm, "end": v(-90.98, -64.64) * mm});
            skLineSegment(sketch, "E4928", {"start": v(-90.98, -64.64) * mm, "end": v(-90.95, -64.66) * mm});
            skLineSegment(sketch, "E4929", {"start": v(-90.95, -64.66) * mm, "end": v(-90.91, -64.7) * mm});
            skLineSegment(sketch, "E4930", {"start": v(-90.91, -64.7) * mm, "end": v(-90.88, -64.72) * mm});
            skLineSegment(sketch, "E4931", {"start": v(-90.88, -64.72) * mm, "end": v(-90.84, -64.74) * mm});
            skLineSegment(sketch, "E4932", {"start": v(-90.84, -64.74) * mm, "end": v(-90.8, -64.76) * mm});
            skLineSegment(sketch, "E4933", {"start": v(-90.77, -64.79) * mm, "end": v(-90.73, -64.8) * mm});
            skLineSegment(sketch, "E4934", {"start": v(-90.73, -64.8) * mm, "end": v(-90.7, -64.83) * mm});
            skLineSegment(sketch, "E4935", {"start": v(-90.7, -64.83) * mm, "end": v(-90.65, -64.84) * mm});
            skLineSegment(sketch, "E4936", {"start": v(-90.65, -64.84) * mm, "end": v(-90.61, -64.86) * mm});
            skLineSegment(sketch, "E4937", {"start": v(-90.61, -64.86) * mm, "end": v(-90.57, -64.88) * mm});
            skLineSegment(sketch, "E4938", {"start": v(-90.57, -64.88) * mm, "end": v(-90.53, -64.89) * mm});
            skLineSegment(sketch, "E4939", {"start": v(-90.53, -64.89) * mm, "end": v(-90.49, -64.9) * mm});
            skLineSegment(sketch, "E4940", {"start": v(-90.49, -64.9) * mm, "end": v(-90.45, -64.91) * mm});
            skLineSegment(sketch, "E4941", {"start": v(-90.45, -64.91) * mm, "end": v(-90.4, -64.92) * mm});
            skLineSegment(sketch, "E4942", {"start": v(-90.4, -64.92) * mm, "end": v(-90.36, -64.93) * mm});
            skLineSegment(sketch, "E4943", {"start": v(-90.36, -64.93) * mm, "end": v(-90.32, -64.94) * mm});
            skLineSegment(sketch, "E4944", {"start": v(-90.32, -64.94) * mm, "end": v(-90.27, -64.94) * mm});
            skLineSegment(sketch, "E4945", {"start": v(-90.27, -64.94) * mm, "end": v(-90.23, -64.94) * mm});
            skLineSegment(sketch, "E4946", {"start": v(-90.23, -64.94) * mm, "end": v(-90.19, -64.95) * mm});
            skLineSegment(sketch, "E4947", {"start": v(-90.19, -64.95) * mm, "end": v(-90.14, -64.95) * mm});
            skLineSegment(sketch, "E4948", {"start": v(-90.14, -64.95) * mm, "end": v(-90.1, -64.95) * mm});
            skLineSegment(sketch, "E4949", {"start": v(-90.1, -64.95) * mm, "end": v(-90.06, -64.94) * mm});
            skLineSegment(sketch, "E4950", {"start": v(-90.06, -64.94) * mm, "end": v(-90.01, -64.94) * mm});
            skLineSegment(sketch, "E4951", {"start": v(-90.01, -64.94) * mm, "end": v(-89.97, -64.93) * mm});
            skLineSegment(sketch, "E4952", {"start": v(-89.93, -64.93) * mm, "end": v(-89.89, -64.92) * mm});
            skLineSegment(sketch, "E4953", {"start": v(-89.89, -64.92) * mm, "end": v(-89.84, -64.9) * mm});
            skLineSegment(sketch, "E4954", {"start": v(-89.84, -64.9) * mm, "end": v(-89.8, -64.9) * mm});
            skLineSegment(sketch, "E4955", {"start": v(-89.8, -64.9) * mm, "end": v(-89.76, -64.88) * mm});
            skLineSegment(sketch, "E4956", {"start": v(-89.76, -64.88) * mm, "end": v(-89.72, -64.87) * mm});
            skLineSegment(sketch, "E4957", {"start": v(-89.72, -64.87) * mm, "end": v(-89.68, -64.85) * mm});
            skLineSegment(sketch, "E4958", {"start": v(-89.68, -64.85) * mm, "end": v(-89.64, -64.83) * mm});
            skLineSegment(sketch, "E4959", {"start": v(-89.64, -64.83) * mm, "end": v(-89.6, -64.82) * mm});
            skLineSegment(sketch, "E4960", {"start": v(-89.6, -64.82) * mm, "end": v(-89.56, -64.8) * mm});
            skLineSegment(sketch, "E4961", {"start": v(-89.56, -64.8) * mm, "end": v(-89.52, -64.78) * mm});
            skLineSegment(sketch, "E4962", {"start": v(-89.49, -64.75) * mm, "end": v(-89.45, -64.73) * mm});
            skLineSegment(sketch, "E4963", {"start": v(-89.45, -64.73) * mm, "end": v(-89.42, -64.7) * mm});
            skLineSegment(sketch, "E4964", {"start": v(-89.42, -64.7) * mm, "end": v(-89.38, -64.68) * mm});
            skLineSegment(sketch, "E4965", {"start": v(-89.38, -64.68) * mm, "end": v(-89.35, -64.65) * mm});
            skLineSegment(sketch, "E4966", {"start": v(-89.35, -64.65) * mm, "end": v(-89.31, -64.62) * mm});
            skLineSegment(sketch, "E4967", {"start": v(-89.31, -64.62) * mm, "end": v(-89.28, -64.6) * mm});
            skLineSegment(sketch, "E4968", {"start": v(-89.28, -64.6) * mm, "end": v(-89.25, -64.56) * mm});
            skLineSegment(sketch, "E4969", {"start": v(-89.25, -64.56) * mm, "end": v(-89.22, -64.53) * mm});
            skLineSegment(sketch, "E4970", {"start": v(-89.22, -64.53) * mm, "end": v(-89.2, -64.5) * mm});
            skLineSegment(sketch, "E4971", {"start": v(-89.2, -64.5) * mm, "end": v(-89.17, -64.46) * mm});
            skLineSegment(sketch, "E4972", {"start": v(-89.17, -64.46) * mm, "end": v(-89.14, -64.43) * mm});
            skLineSegment(sketch, "E4973", {"start": v(-89.14, -64.43) * mm, "end": v(-89.12, -64.4) * mm});
            skLineSegment(sketch, "E4974", {"start": v(-89.12, -64.4) * mm, "end": v(-89.1, -64.36) * mm});
            skLineSegment(sketch, "E4975", {"start": v(-89.1, -64.36) * mm, "end": v(-89.07, -64.32) * mm});
            skLineSegment(sketch, "E4976", {"start": v(-89.07, -64.32) * mm, "end": v(-89.05, -64.28) * mm});
            skLineSegment(sketch, "E4977", {"start": v(-89.05, -64.28) * mm, "end": v(-89.03, -64.24) * mm});
            skLineSegment(sketch, "E4978", {"start": v(-89.03, -64.24) * mm, "end": v(-89.01, -64.2) * mm});
            skLineSegment(sketch, "E4979", {"start": v(-89.01, -64.2) * mm, "end": v(-89, -64.16) * mm});
            skLineSegment(sketch, "E4980", {"start": v(-89, -64.16) * mm, "end": v(-88.98, -64.12) * mm});
            skLineSegment(sketch, "E4981", {"start": v(-88.98, -64.12) * mm, "end": v(-88.97, -64.08) * mm});
            skLineSegment(sketch, "E4982", {"start": v(-88.97, -64.08) * mm, "end": v(-88.95, -64.04) * mm});
            skLineSegment(sketch, "E4983", {"start": v(-88.95, -64.04) * mm, "end": v(-88.94, -64) * mm});
            skLineSegment(sketch, "E4984", {"start": v(-88.94, -64) * mm, "end": v(-88.93, -63.95) * mm});
            skLineSegment(sketch, "E4985", {"start": v(-88.93, -63.95) * mm, "end": v(-88.92, -63.91) * mm});
            skLineSegment(sketch, "E4986", {"start": v(-88.92, -63.91) * mm, "end": v(-88.92, -63.87) * mm});
            skLineSegment(sketch, "E4987", {"start": v(-88.92, -63.87) * mm, "end": v(-88.91, -63.83) * mm});
            skLineSegment(sketch, "E4988", {"start": v(-88.91, -63.83) * mm, "end": v(-88.9, -63.78) * mm});
            skLineSegment(sketch, "E4989", {"start": v(-88.9, -63.78) * mm, "end": v(-88.9, -63.74) * mm});
            skLineSegment(sketch, "E4990", {"start": v(-88.9, -63.74) * mm, "end": v(-88.9, -63.7) * mm});
            skLineSegment(sketch, "E4991", {"start": v(-322, -59.75) * mm, "end": v(-302, -59.75) * mm});
            skLineSegment(sketch, "E4992", {"start": v(-302, -59.75) * mm, "end": v(-302, -9.75) * mm});
            skLineSegment(sketch, "E4993", {"start": v(-302, -9.75) * mm, "end": v(-322, -9.75) * mm});
            skLineSegment(sketch, "E4994", {"start": v(-322, -9.75) * mm, "end": v(-322, -59.75) * mm});
            skLineSegment(sketch, "E4995", {"start": v(-68, -57.45) * mm, "end": v(-68, -57.37) * mm});
            skLineSegment(sketch, "E4996", {"start": v(-68, -57.37) * mm, "end": v(-68.01, -57.3) * mm});
            skLineSegment(sketch, "E4997", {"start": v(-68.01, -57.3) * mm, "end": v(-68.02, -57.22) * mm});
            skLineSegment(sketch, "E4998", {"start": v(-68.02, -57.22) * mm, "end": v(-68.03, -57.15) * mm});
            skLineSegment(sketch, "E4999", {"start": v(-68.03, -57.15) * mm, "end": v(-68.04, -57.07) * mm});
            skLineSegment(sketch, "E5000", {"start": v(-68.04, -57.07) * mm, "end": v(-68.05, -57) * mm});
            skLineSegment(sketch, "E5001", {"start": v(-68.05, -57) * mm, "end": v(-68.07, -56.93) * mm});
            skLineSegment(sketch, "E5002", {"start": v(-68.07, -56.93) * mm, "end": v(-68.09, -56.86) * mm});
            skLineSegment(sketch, "E5003", {"start": v(-68.09, -56.86) * mm, "end": v(-68.1, -56.79) * mm});
            skLineSegment(sketch, "E5004", {"start": v(-68.1, -56.79) * mm, "end": v(-68.13, -56.71) * mm});
            skLineSegment(sketch, "E5005", {"start": v(-68.13, -56.71) * mm, "end": v(-68.16, -56.65) * mm});
            skLineSegment(sketch, "E5006", {"start": v(-68.16, -56.65) * mm, "end": v(-68.19, -56.58) * mm});
            skLineSegment(sketch, "E5007", {"start": v(-68.19, -56.58) * mm, "end": v(-68.22, -56.5) * mm});
            skLineSegment(sketch, "E5008", {"start": v(-68.22, -56.5) * mm, "end": v(-68.25, -56.44) * mm});
            skLineSegment(sketch, "E5009", {"start": v(-68.25, -56.44) * mm, "end": v(-68.3, -56.38) * mm});
            skLineSegment(sketch, "E5010", {"start": v(-68.3, -56.38) * mm, "end": v(-68.33, -56.31) * mm});
            skLineSegment(sketch, "E5011", {"start": v(-68.33, -56.31) * mm, "end": v(-68.37, -56.25) * mm});
            skLineSegment(sketch, "E5012", {"start": v(-68.37, -56.25) * mm, "end": v(-68.41, -56.19) * mm});
            skLineSegment(sketch, "E5013", {"start": v(-68.41, -56.19) * mm, "end": v(-68.46, -56.13) * mm});
            skLineSegment(sketch, "E5014", {"start": v(-68.46, -56.13) * mm, "end": v(-68.5, -56.07) * mm});
            skLineSegment(sketch, "E5015", {"start": v(-68.5, -56.07) * mm, "end": v(-68.55, -56.01) * mm});
            skLineSegment(sketch, "E5016", {"start": v(-68.55, -56.01) * mm, "end": v(-68.6, -55.96) * mm});
            skLineSegment(sketch, "E5017", {"start": v(-68.6, -55.96) * mm, "end": v(-68.66, -55.9) * mm});
            skLineSegment(sketch, "E5018", {"start": v(-68.66, -55.9) * mm, "end": v(-68.7, -55.86) * mm});
            skLineSegment(sketch, "E5019", {"start": v(-68.7, -55.86) * mm, "end": v(-68.77, -55.8) * mm});
            skLineSegment(sketch, "E5020", {"start": v(-68.88, -55.71) * mm, "end": v(-68.94, -55.67) * mm});
            skLineSegment(sketch, "E5021", {"start": v(-68.94, -55.67) * mm, "end": v(-69, -55.63) * mm});
            skLineSegment(sketch, "E5022", {"start": v(-69, -55.63) * mm, "end": v(-69.07, -55.6) * mm});
            skLineSegment(sketch, "E5023", {"start": v(-69.07, -55.6) * mm, "end": v(-69.13, -55.55) * mm});
            skLineSegment(sketch, "E5024", {"start": v(-69.13, -55.55) * mm, "end": v(-69.2, -55.52) * mm});
            skLineSegment(sketch, "E5025", {"start": v(-69.2, -55.52) * mm, "end": v(-69.27, -55.49) * mm});
            skLineSegment(sketch, "E5026", {"start": v(-69.27, -55.49) * mm, "end": v(-69.34, -55.46) * mm});
            skLineSegment(sketch, "E5027", {"start": v(-69.34, -55.46) * mm, "end": v(-69.4, -55.43) * mm});
            skLineSegment(sketch, "E5028", {"start": v(-69.4, -55.43) * mm, "end": v(-69.48, -55.4) * mm});
            skLineSegment(sketch, "E5029", {"start": v(-69.48, -55.4) * mm, "end": v(-69.55, -55.38) * mm});
            skLineSegment(sketch, "E5030", {"start": v(-69.55, -55.38) * mm, "end": v(-69.62, -55.36) * mm});
            skLineSegment(sketch, "E5031", {"start": v(-69.62, -55.36) * mm, "end": v(-69.7, -55.35) * mm});
            skLineSegment(sketch, "E5032", {"start": v(-69.7, -55.35) * mm, "end": v(-69.77, -55.33) * mm});
            skLineSegment(sketch, "E5033", {"start": v(-69.77, -55.33) * mm, "end": v(-69.84, -55.32) * mm});
            skLineSegment(sketch, "E5034", {"start": v(-69.84, -55.32) * mm, "end": v(-69.91, -55.3) * mm});
            skLineSegment(sketch, "E5035", {"start": v(-69.91, -55.3) * mm, "end": v(-69.99, -55.3) * mm});
            skLineSegment(sketch, "E5036", {"start": v(-69.99, -55.3) * mm, "end": v(-70.06, -55.3) * mm});
            skLineSegment(sketch, "E5037", {"start": v(-70.06, -55.3) * mm, "end": v(-70.14, -55.3) * mm});
            skLineSegment(sketch, "E5038", {"start": v(-70.14, -55.3) * mm, "end": v(-70.21, -55.3) * mm});
            skLineSegment(sketch, "E5039", {"start": v(-70.21, -55.3) * mm, "end": v(-70.29, -55.3) * mm});
            skLineSegment(sketch, "E5040", {"start": v(-70.29, -55.3) * mm, "end": v(-70.36, -55.3) * mm});
            skLineSegment(sketch, "E5041", {"start": v(-70.36, -55.3) * mm, "end": v(-70.43, -55.31) * mm});
            skLineSegment(sketch, "E5042", {"start": v(-70.43, -55.31) * mm, "end": v(-70.5, -55.33) * mm});
            skLineSegment(sketch, "E5043", {"start": v(-70.5, -55.33) * mm, "end": v(-70.58, -55.34) * mm});
            skLineSegment(sketch, "E5044", {"start": v(-70.58, -55.34) * mm, "end": v(-70.65, -55.36) * mm});
            skLineSegment(sketch, "E5045", {"start": v(-70.65, -55.36) * mm, "end": v(-70.73, -55.37) * mm});
            skLineSegment(sketch, "E5046", {"start": v(-70.73, -55.37) * mm, "end": v(-70.8, -55.4) * mm});
            skLineSegment(sketch, "E5047", {"start": v(-70.87, -55.42) * mm, "end": v(-70.94, -55.44) * mm});
            skLineSegment(sketch, "E5048", {"start": v(-70.94, -55.44) * mm, "end": v(-71, -55.47) * mm});
            skLineSegment(sketch, "E5049", {"start": v(-71, -55.47) * mm, "end": v(-71.08, -55.5) * mm});
            skLineSegment(sketch, "E5050", {"start": v(-71.08, -55.5) * mm, "end": v(-71.14, -55.54) * mm});
            skLineSegment(sketch, "E5051", {"start": v(-71.14, -55.54) * mm, "end": v(-71.2, -55.57) * mm});
            skLineSegment(sketch, "E5052", {"start": v(-71.2, -55.57) * mm, "end": v(-71.27, -55.6) * mm});
            skLineSegment(sketch, "E5053", {"start": v(-71.27, -55.6) * mm, "end": v(-71.34, -55.65) * mm});
            skLineSegment(sketch, "E5054", {"start": v(-71.34, -55.65) * mm, "end": v(-71.4, -55.7) * mm});
            skLineSegment(sketch, "E5055", {"start": v(-71.4, -55.7) * mm, "end": v(-71.46, -55.74) * mm});
            skLineSegment(sketch, "E5056", {"start": v(-71.46, -55.74) * mm, "end": v(-71.52, -55.78) * mm});
            skLineSegment(sketch, "E5057", {"start": v(-71.52, -55.78) * mm, "end": v(-71.57, -55.83) * mm});
            skLineSegment(sketch, "E5058", {"start": v(-71.63, -55.88) * mm, "end": v(-71.68, -55.93) * mm});
            skLineSegment(sketch, "E5059", {"start": v(-71.68, -55.93) * mm, "end": v(-71.73, -55.99) * mm});
            skLineSegment(sketch, "E5060", {"start": v(-71.73, -55.99) * mm, "end": v(-71.78, -56.04) * mm});
            skLineSegment(sketch, "E5061", {"start": v(-71.78, -56.04) * mm, "end": v(-71.83, -56.1) * mm});
            skLineSegment(sketch, "E5062", {"start": v(-71.83, -56.1) * mm, "end": v(-71.88, -56.16) * mm});
            skLineSegment(sketch, "E5063", {"start": v(-71.88, -56.16) * mm, "end": v(-71.92, -56.22) * mm});
            skLineSegment(sketch, "E5064", {"start": v(-71.92, -56.22) * mm, "end": v(-71.96, -56.28) * mm});
            skLineSegment(sketch, "E5065", {"start": v(-71.96, -56.28) * mm, "end": v(-72, -56.34) * mm});
            skLineSegment(sketch, "E5066", {"start": v(-72, -56.34) * mm, "end": v(-72.04, -56.4) * mm});
            skLineSegment(sketch, "E5067", {"start": v(-72.04, -56.4) * mm, "end": v(-72.07, -56.48) * mm});
            skLineSegment(sketch, "E5068", {"start": v(-72.07, -56.48) * mm, "end": v(-72.1, -56.54) * mm});
            skLineSegment(sketch, "E5069", {"start": v(-72.1, -56.54) * mm, "end": v(-72.14, -56.61) * mm});
            skLineSegment(sketch, "E5070", {"start": v(-72.16, -56.68) * mm, "end": v(-72.19, -56.75) * mm});
            skLineSegment(sketch, "E5071", {"start": v(-72.19, -56.75) * mm, "end": v(-72.21, -56.82) * mm});
            skLineSegment(sketch, "E5072", {"start": v(-72.21, -56.82) * mm, "end": v(-72.23, -56.9) * mm});
            skLineSegment(sketch, "E5073", {"start": v(-72.23, -56.9) * mm, "end": v(-72.25, -56.97) * mm});
            skLineSegment(sketch, "E5074", {"start": v(-72.25, -56.97) * mm, "end": v(-72.27, -57.04) * mm});
            skLineSegment(sketch, "E5075", {"start": v(-72.27, -57.04) * mm, "end": v(-72.28, -57.11) * mm});
            skLineSegment(sketch, "E5076", {"start": v(-72.28, -57.11) * mm, "end": v(-72.29, -57.19) * mm});
            skLineSegment(sketch, "E5077", {"start": v(-72.29, -57.19) * mm, "end": v(-72.3, -57.26) * mm});
            skLineSegment(sketch, "E5078", {"start": v(-72.3, -57.26) * mm, "end": v(-72.3, -57.33) * mm});
            skLineSegment(sketch, "E5079", {"start": v(-72.3, -57.33) * mm, "end": v(-72.3, -57.4) * mm});
            skLineSegment(sketch, "E5080", {"start": v(-72.3, -57.4) * mm, "end": v(-72.3, -57.48) * mm});
            skLineSegment(sketch, "E5081", {"start": v(-72.3, -57.48) * mm, "end": v(-72.3, -57.56) * mm});
            skLineSegment(sketch, "E5082", {"start": v(-72.3, -57.56) * mm, "end": v(-72.3, -57.63) * mm});
            skLineSegment(sketch, "E5083", {"start": v(-72.3, -57.63) * mm, "end": v(-72.29, -57.7) * mm});
            skLineSegment(sketch, "E5084", {"start": v(-72.29, -57.7) * mm, "end": v(-72.28, -57.78) * mm});
            skLineSegment(sketch, "E5085", {"start": v(-72.28, -57.78) * mm, "end": v(-72.27, -57.85) * mm});
            skLineSegment(sketch, "E5086", {"start": v(-72.27, -57.85) * mm, "end": v(-72.25, -57.93) * mm});
            skLineSegment(sketch, "E5087", {"start": v(-72.25, -57.93) * mm, "end": v(-72.23, -58) * mm});
            skLineSegment(sketch, "E5088", {"start": v(-72.23, -58) * mm, "end": v(-72.21, -58.07) * mm});
            skLineSegment(sketch, "E5089", {"start": v(-72.21, -58.07) * mm, "end": v(-72.19, -58.14) * mm});
            skLineSegment(sketch, "E5090", {"start": v(-72.19, -58.14) * mm, "end": v(-72.16, -58.21) * mm});
            skLineSegment(sketch, "E5091", {"start": v(-72.16, -58.21) * mm, "end": v(-72.14, -58.28) * mm});
            skLineSegment(sketch, "E5092", {"start": v(-72.14, -58.28) * mm, "end": v(-72.1, -58.35) * mm});
            skLineSegment(sketch, "E5093", {"start": v(-72.1, -58.35) * mm, "end": v(-72.07, -58.42) * mm});
            skLineSegment(sketch, "E5094", {"start": v(-72.07, -58.42) * mm, "end": v(-72.04, -58.48) * mm});
            skLineSegment(sketch, "E5095", {"start": v(-72.04, -58.48) * mm, "end": v(-72, -58.55) * mm});
            skLineSegment(sketch, "E5096", {"start": v(-72, -58.55) * mm, "end": v(-71.96, -58.61) * mm});
            skLineSegment(sketch, "E5097", {"start": v(-71.96, -58.61) * mm, "end": v(-71.92, -58.67) * mm});
            skLineSegment(sketch, "E5098", {"start": v(-71.83, -58.8) * mm, "end": v(-71.78, -58.85) * mm});
            skLineSegment(sketch, "E5099", {"start": v(-71.78, -58.85) * mm, "end": v(-71.73, -58.9) * mm});
            skLineSegment(sketch, "E5100", {"start": v(-71.73, -58.9) * mm, "end": v(-71.68, -58.96) * mm});
            skLineSegment(sketch, "E5101", {"start": v(-71.68, -58.96) * mm, "end": v(-71.63, -59.01) * mm});
            skLineSegment(sketch, "E5102", {"start": v(-71.63, -59.01) * mm, "end": v(-71.57, -59.06) * mm});
            skLineSegment(sketch, "E5103", {"start": v(-71.57, -59.06) * mm, "end": v(-71.52, -59.11) * mm});
            skLineSegment(sketch, "E5104", {"start": v(-71.52, -59.11) * mm, "end": v(-71.46, -59.16) * mm});
            skLineSegment(sketch, "E5105", {"start": v(-71.46, -59.16) * mm, "end": v(-71.4, -59.2) * mm});
            skLineSegment(sketch, "E5106", {"start": v(-71.4, -59.2) * mm, "end": v(-71.34, -59.24) * mm});
            skLineSegment(sketch, "E5107", {"start": v(-71.34, -59.24) * mm, "end": v(-71.27, -59.28) * mm});
            skLineSegment(sketch, "E5108", {"start": v(-71.27, -59.28) * mm, "end": v(-71.2, -59.32) * mm});
            skLineSegment(sketch, "E5109", {"start": v(-71.2, -59.32) * mm, "end": v(-71.14, -59.36) * mm});
            skLineSegment(sketch, "E5110", {"start": v(-71.14, -59.36) * mm, "end": v(-71.08, -59.39) * mm});
            skLineSegment(sketch, "E5111", {"start": v(-71.08, -59.39) * mm, "end": v(-71, -59.42) * mm});
            skLineSegment(sketch, "E5112", {"start": v(-71, -59.42) * mm, "end": v(-70.94, -59.45) * mm});
            skLineSegment(sketch, "E5113", {"start": v(-70.87, -59.47) * mm, "end": v(-70.8, -59.5) * mm});
            skLineSegment(sketch, "E5114", {"start": v(-70.8, -59.5) * mm, "end": v(-70.73, -59.52) * mm});
            skLineSegment(sketch, "E5115", {"start": v(-70.73, -59.52) * mm, "end": v(-70.65, -59.54) * mm});
            skLineSegment(sketch, "E5116", {"start": v(-70.65, -59.54) * mm, "end": v(-70.58, -59.55) * mm});
            skLineSegment(sketch, "E5117", {"start": v(-70.58, -59.55) * mm, "end": v(-70.5, -59.57) * mm});
            skLineSegment(sketch, "E5118", {"start": v(-70.5, -59.57) * mm, "end": v(-70.43, -59.58) * mm});
            skLineSegment(sketch, "E5119", {"start": v(-70.43, -59.58) * mm, "end": v(-70.36, -59.59) * mm});
            skLineSegment(sketch, "E5120", {"start": v(-70.36, -59.59) * mm, "end": v(-70.29, -59.6) * mm});
            skLineSegment(sketch, "E5121", {"start": v(-70.29, -59.6) * mm, "end": v(-70.21, -59.6) * mm});
            skLineSegment(sketch, "E5122", {"start": v(-70.21, -59.6) * mm, "end": v(-70.14, -59.6) * mm});
            skLineSegment(sketch, "E5123", {"start": v(-70.14, -59.6) * mm, "end": v(-70.06, -59.6) * mm});
            skLineSegment(sketch, "E5124", {"start": v(-70.06, -59.6) * mm, "end": v(-69.99, -59.59) * mm});
            skLineSegment(sketch, "E5125", {"start": v(-69.99, -59.59) * mm, "end": v(-69.91, -59.58) * mm});
            skLineSegment(sketch, "E5126", {"start": v(-69.91, -59.58) * mm, "end": v(-69.84, -59.57) * mm});
            skLineSegment(sketch, "E5127", {"start": v(-69.84, -59.57) * mm, "end": v(-69.77, -59.56) * mm});
            skLineSegment(sketch, "E5128", {"start": v(-69.77, -59.56) * mm, "end": v(-69.7, -59.55) * mm});
            skLineSegment(sketch, "E5129", {"start": v(-69.7, -59.55) * mm, "end": v(-69.62, -59.53) * mm});
            skLineSegment(sketch, "E5130", {"start": v(-69.62, -59.53) * mm, "end": v(-69.55, -59.5) * mm});
            skLineSegment(sketch, "E5131", {"start": v(-69.55, -59.5) * mm, "end": v(-69.48, -59.49) * mm});
            skLineSegment(sketch, "E5132", {"start": v(-69.48, -59.49) * mm, "end": v(-69.4, -59.46) * mm});
            skLineSegment(sketch, "E5133", {"start": v(-69.4, -59.46) * mm, "end": v(-69.34, -59.43) * mm});
            skLineSegment(sketch, "E5134", {"start": v(-69.34, -59.43) * mm, "end": v(-69.27, -59.4) * mm});
            skLineSegment(sketch, "E5135", {"start": v(-69.27, -59.4) * mm, "end": v(-69.2, -59.37) * mm});
            skLineSegment(sketch, "E5136", {"start": v(-69.2, -59.37) * mm, "end": v(-69.13, -59.34) * mm});
            skLineSegment(sketch, "E5137", {"start": v(-69.13, -59.34) * mm, "end": v(-69.07, -59.3) * mm});
            skLineSegment(sketch, "E5138", {"start": v(-69.07, -59.3) * mm, "end": v(-69, -59.26) * mm});
            skLineSegment(sketch, "E5139", {"start": v(-69, -59.26) * mm, "end": v(-68.94, -59.22) * mm});
            skLineSegment(sketch, "E5140", {"start": v(-68.94, -59.22) * mm, "end": v(-68.88, -59.18) * mm});
            skLineSegment(sketch, "E5141", {"start": v(-68.88, -59.18) * mm, "end": v(-68.82, -59.13) * mm});
            skLineSegment(sketch, "E5142", {"start": v(-68.82, -59.13) * mm, "end": v(-68.77, -59.09) * mm});
            skLineSegment(sketch, "E5143", {"start": v(-68.77, -59.09) * mm, "end": v(-68.7, -59.04) * mm});
            skLineSegment(sketch, "E5144", {"start": v(-68.7, -59.04) * mm, "end": v(-68.66, -58.99) * mm});
            skLineSegment(sketch, "E5145", {"start": v(-68.66, -58.99) * mm, "end": v(-68.6, -58.93) * mm});
            skLineSegment(sketch, "E5146", {"start": v(-68.6, -58.93) * mm, "end": v(-68.55, -58.88) * mm});
            skLineSegment(sketch, "E5147", {"start": v(-68.5, -58.82) * mm, "end": v(-68.46, -58.76) * mm});
            skLineSegment(sketch, "E5148", {"start": v(-68.46, -58.76) * mm, "end": v(-68.41, -58.7) * mm});
            skLineSegment(sketch, "E5149", {"start": v(-68.41, -58.7) * mm, "end": v(-68.37, -58.64) * mm});
            skLineSegment(sketch, "E5150", {"start": v(-68.37, -58.64) * mm, "end": v(-68.33, -58.58) * mm});
            skLineSegment(sketch, "E5151", {"start": v(-68.33, -58.58) * mm, "end": v(-68.3, -58.52) * mm});
            skLineSegment(sketch, "E5152", {"start": v(-68.3, -58.52) * mm, "end": v(-68.25, -58.45) * mm});
            skLineSegment(sketch, "E5153", {"start": v(-68.25, -58.45) * mm, "end": v(-68.22, -58.38) * mm});
            skLineSegment(sketch, "E5154", {"start": v(-68.22, -58.38) * mm, "end": v(-68.19, -58.32) * mm});
            skLineSegment(sketch, "E5155", {"start": v(-68.19, -58.32) * mm, "end": v(-68.16, -58.25) * mm});
            skLineSegment(sketch, "E5156", {"start": v(-68.16, -58.25) * mm, "end": v(-68.13, -58.18) * mm});
            skLineSegment(sketch, "E5157", {"start": v(-68.13, -58.18) * mm, "end": v(-68.1, -58.1) * mm});
            skLineSegment(sketch, "E5158", {"start": v(-68.1, -58.1) * mm, "end": v(-68.09, -58.04) * mm});
            skLineSegment(sketch, "E5159", {"start": v(-68.07, -57.96) * mm, "end": v(-68.05, -57.9) * mm});
            skLineSegment(sketch, "E5160", {"start": v(-68.05, -57.9) * mm, "end": v(-68.04, -57.82) * mm});
            skLineSegment(sketch, "E5161", {"start": v(-68.04, -57.82) * mm, "end": v(-68.03, -57.74) * mm});
            skLineSegment(sketch, "E5162", {"start": v(-68.03, -57.74) * mm, "end": v(-68.02, -57.67) * mm});
            skLineSegment(sketch, "E5163", {"start": v(-68.02, -57.67) * mm, "end": v(-68.01, -57.6) * mm});
            skLineSegment(sketch, "E5164", {"start": v(-68.01, -57.6) * mm, "end": v(-68, -57.52) * mm});
            skLineSegment(sketch, "E5165", {"start": v(-68, -57.52) * mm, "end": v(-68, -57.45) * mm});
            skLineSegment(sketch, "E5166", {"start": v(-58, -57.45) * mm, "end": v(-58, -57.37) * mm});
            skLineSegment(sketch, "E5167", {"start": v(-58, -57.37) * mm, "end": v(-58.01, -57.3) * mm});
            skLineSegment(sketch, "E5168", {"start": v(-58.01, -57.3) * mm, "end": v(-58.02, -57.22) * mm});
            skLineSegment(sketch, "E5169", {"start": v(-58.02, -57.22) * mm, "end": v(-58.03, -57.15) * mm});
            skLineSegment(sketch, "E5170", {"start": v(-58.03, -57.15) * mm, "end": v(-58.04, -57.07) * mm});
            skLineSegment(sketch, "E5171", {"start": v(-58.04, -57.07) * mm, "end": v(-58.05, -57) * mm});
            skLineSegment(sketch, "E5172", {"start": v(-58.05, -57) * mm, "end": v(-58.07, -56.93) * mm});
            skLineSegment(sketch, "E5173", {"start": v(-58.07, -56.93) * mm, "end": v(-58.09, -56.86) * mm});
            skLineSegment(sketch, "E5174", {"start": v(-58.09, -56.86) * mm, "end": v(-58.1, -56.79) * mm});
            skLineSegment(sketch, "E5175", {"start": v(-58.1, -56.79) * mm, "end": v(-58.13, -56.71) * mm});
            skLineSegment(sketch, "E5176", {"start": v(-58.16, -56.65) * mm, "end": v(-58.19, -56.58) * mm});
            skLineSegment(sketch, "E5177", {"start": v(-58.19, -56.58) * mm, "end": v(-58.22, -56.5) * mm});
            skLineSegment(sketch, "E5178", {"start": v(-58.22, -56.5) * mm, "end": v(-58.25, -56.44) * mm});
            skLineSegment(sketch, "E5179", {"start": v(-58.25, -56.44) * mm, "end": v(-58.3, -56.38) * mm});
            skLineSegment(sketch, "E5180", {"start": v(-58.3, -56.38) * mm, "end": v(-58.33, -56.31) * mm});
            skLineSegment(sketch, "E5181", {"start": v(-58.33, -56.31) * mm, "end": v(-58.37, -56.25) * mm});
            skLineSegment(sketch, "E5182", {"start": v(-58.37, -56.25) * mm, "end": v(-58.41, -56.19) * mm});
            skLineSegment(sketch, "E5183", {"start": v(-58.41, -56.19) * mm, "end": v(-58.46, -56.13) * mm});
            skLineSegment(sketch, "E5184", {"start": v(-58.46, -56.13) * mm, "end": v(-58.5, -56.07) * mm});
            skLineSegment(sketch, "E5185", {"start": v(-58.5, -56.07) * mm, "end": v(-58.55, -56.01) * mm});
            skLineSegment(sketch, "E5186", {"start": v(-58.55, -56.01) * mm, "end": v(-58.6, -55.96) * mm});
            skLineSegment(sketch, "E5187", {"start": v(-58.66, -55.9) * mm, "end": v(-58.7, -55.86) * mm});
            skLineSegment(sketch, "E5188", {"start": v(-58.7, -55.86) * mm, "end": v(-58.77, -55.8) * mm});
            skLineSegment(sketch, "E5189", {"start": v(-58.77, -55.8) * mm, "end": v(-58.82, -55.76) * mm});
            skLineSegment(sketch, "E5190", {"start": v(-58.82, -55.76) * mm, "end": v(-58.88, -55.71) * mm});
            skLineSegment(sketch, "E5191", {"start": v(-58.88, -55.71) * mm, "end": v(-58.94, -55.67) * mm});
            skLineSegment(sketch, "E5192", {"start": v(-58.94, -55.67) * mm, "end": v(-59, -55.63) * mm});
            skLineSegment(sketch, "E5193", {"start": v(-59, -55.63) * mm, "end": v(-59.07, -55.6) * mm});
            skLineSegment(sketch, "E5194", {"start": v(-59.07, -55.6) * mm, "end": v(-59.13, -55.55) * mm});
            skLineSegment(sketch, "E5195", {"start": v(-59.13, -55.55) * mm, "end": v(-59.2, -55.52) * mm});
            skLineSegment(sketch, "E5196", {"start": v(-59.2, -55.52) * mm, "end": v(-59.27, -55.49) * mm});
            skLineSegment(sketch, "E5197", {"start": v(-59.27, -55.49) * mm, "end": v(-59.34, -55.46) * mm});
            skLineSegment(sketch, "E5198", {"start": v(-59.34, -55.46) * mm, "end": v(-59.4, -55.43) * mm});
            skLineSegment(sketch, "E5199", {"start": v(-59.4, -55.43) * mm, "end": v(-59.48, -55.4) * mm});
            skLineSegment(sketch, "E5200", {"start": v(-59.48, -55.4) * mm, "end": v(-59.55, -55.38) * mm});
            skLineSegment(sketch, "E5201", {"start": v(-59.55, -55.38) * mm, "end": v(-59.62, -55.36) * mm});
            skLineSegment(sketch, "E5202", {"start": v(-59.62, -55.36) * mm, "end": v(-59.7, -55.35) * mm});
            skLineSegment(sketch, "E5203", {"start": v(-59.7, -55.35) * mm, "end": v(-59.77, -55.33) * mm});
            skLineSegment(sketch, "E5204", {"start": v(-59.77, -55.33) * mm, "end": v(-59.84, -55.32) * mm});
            skLineSegment(sketch, "E5205", {"start": v(-59.84, -55.32) * mm, "end": v(-59.91, -55.3) * mm});
            skLineSegment(sketch, "E5206", {"start": v(-59.91, -55.3) * mm, "end": v(-59.99, -55.3) * mm});
            skLineSegment(sketch, "E5207", {"start": v(-59.99, -55.3) * mm, "end": v(-60.06, -55.3) * mm});
            skLineSegment(sketch, "E5208", {"start": v(-60.06, -55.3) * mm, "end": v(-60.14, -55.3) * mm});
            skLineSegment(sketch, "E5209", {"start": v(-60.14, -55.3) * mm, "end": v(-60.21, -55.3) * mm});
            skLineSegment(sketch, "E5210", {"start": v(-60.21, -55.3) * mm, "end": v(-60.29, -55.3) * mm});
            skLineSegment(sketch, "E5211", {"start": v(-60.29, -55.3) * mm, "end": v(-60.36, -55.3) * mm});
            skLineSegment(sketch, "E5212", {"start": v(-60.36, -55.3) * mm, "end": v(-60.43, -55.31) * mm});
            skLineSegment(sketch, "E5213", {"start": v(-60.43, -55.31) * mm, "end": v(-60.5, -55.33) * mm});
            skLineSegment(sketch, "E5214", {"start": v(-60.5, -55.33) * mm, "end": v(-60.58, -55.34) * mm});
            skLineSegment(sketch, "E5215", {"start": v(-60.58, -55.34) * mm, "end": v(-60.65, -55.36) * mm});
            skLineSegment(sketch, "E5216", {"start": v(-60.73, -55.37) * mm, "end": v(-60.8, -55.4) * mm});
            skLineSegment(sketch, "E5217", {"start": v(-60.8, -55.4) * mm, "end": v(-60.87, -55.42) * mm});
            skLineSegment(sketch, "E5218", {"start": v(-60.87, -55.42) * mm, "end": v(-60.94, -55.44) * mm});
            skLineSegment(sketch, "E5219", {"start": v(-60.94, -55.44) * mm, "end": v(-61, -55.47) * mm});
            skLineSegment(sketch, "E5220", {"start": v(-61, -55.47) * mm, "end": v(-61.08, -55.5) * mm});
            skLineSegment(sketch, "E5221", {"start": v(-61.08, -55.5) * mm, "end": v(-61.14, -55.54) * mm});
            skLineSegment(sketch, "E5222", {"start": v(-61.14, -55.54) * mm, "end": v(-61.2, -55.57) * mm});
            skLineSegment(sketch, "E5223", {"start": v(-61.2, -55.57) * mm, "end": v(-61.27, -55.6) * mm});
            skLineSegment(sketch, "E5224", {"start": v(-61.27, -55.6) * mm, "end": v(-61.34, -55.65) * mm});
            skLineSegment(sketch, "E5225", {"start": v(-61.4, -55.7) * mm, "end": v(-61.46, -55.74) * mm});
            skLineSegment(sketch, "E5226", {"start": v(-61.46, -55.74) * mm, "end": v(-61.52, -55.78) * mm});
            skLineSegment(sketch, "E5227", {"start": v(-61.52, -55.78) * mm, "end": v(-61.57, -55.83) * mm});
            skLineSegment(sketch, "E5228", {"start": v(-61.57, -55.83) * mm, "end": v(-61.63, -55.88) * mm});
            skLineSegment(sketch, "E5229", {"start": v(-61.63, -55.88) * mm, "end": v(-61.68, -55.93) * mm});
            skLineSegment(sketch, "E5230", {"start": v(-61.68, -55.93) * mm, "end": v(-61.73, -55.99) * mm});
            skLineSegment(sketch, "E5231", {"start": v(-61.73, -55.99) * mm, "end": v(-61.78, -56.04) * mm});
            skLineSegment(sketch, "E5232", {"start": v(-61.78, -56.04) * mm, "end": v(-61.83, -56.1) * mm});
            skLineSegment(sketch, "E5233", {"start": v(-61.83, -56.1) * mm, "end": v(-61.88, -56.16) * mm});
            skLineSegment(sketch, "E5234", {"start": v(-61.88, -56.16) * mm, "end": v(-61.92, -56.22) * mm});
            skLineSegment(sketch, "E5235", {"start": v(-61.92, -56.22) * mm, "end": v(-61.96, -56.28) * mm});
            skLineSegment(sketch, "E5236", {"start": v(-61.96, -56.28) * mm, "end": v(-62, -56.34) * mm});
            skLineSegment(sketch, "E5237", {"start": v(-62, -56.34) * mm, "end": v(-62.04, -56.4) * mm});
            skLineSegment(sketch, "E5238", {"start": v(-62.04, -56.4) * mm, "end": v(-62.07, -56.48) * mm});
            skLineSegment(sketch, "E5239", {"start": v(-62.07, -56.48) * mm, "end": v(-62.1, -56.54) * mm});
            skLineSegment(sketch, "E5240", {"start": v(-62.1, -56.54) * mm, "end": v(-62.14, -56.61) * mm});
            skLineSegment(sketch, "E5241", {"start": v(-62.14, -56.61) * mm, "end": v(-62.16, -56.68) * mm});
            skLineSegment(sketch, "E5242", {"start": v(-62.16, -56.68) * mm, "end": v(-62.19, -56.75) * mm});
            skLineSegment(sketch, "E5243", {"start": v(-62.19, -56.75) * mm, "end": v(-62.21, -56.82) * mm});
            skLineSegment(sketch, "E5244", {"start": v(-62.21, -56.82) * mm, "end": v(-62.23, -56.9) * mm});
            skLineSegment(sketch, "E5245", {"start": v(-62.23, -56.9) * mm, "end": v(-62.25, -56.97) * mm});
            skLineSegment(sketch, "E5246", {"start": v(-62.25, -56.97) * mm, "end": v(-62.27, -57.04) * mm});
            skLineSegment(sketch, "E5247", {"start": v(-62.27, -57.04) * mm, "end": v(-62.28, -57.11) * mm});
            skLineSegment(sketch, "E5248", {"start": v(-62.28, -57.11) * mm, "end": v(-62.29, -57.19) * mm});
            skLineSegment(sketch, "E5249", {"start": v(-62.29, -57.19) * mm, "end": v(-62.3, -57.26) * mm});
            skLineSegment(sketch, "E5250", {"start": v(-62.3, -57.26) * mm, "end": v(-62.3, -57.33) * mm});
            skLineSegment(sketch, "E5251", {"start": v(-62.3, -57.33) * mm, "end": v(-62.3, -57.4) * mm});
            skLineSegment(sketch, "E5252", {"start": v(-62.3, -57.4) * mm, "end": v(-62.3, -57.48) * mm});
            skLineSegment(sketch, "E5253", {"start": v(-62.3, -57.48) * mm, "end": v(-62.3, -57.56) * mm});
            skLineSegment(sketch, "E5254", {"start": v(-62.3, -57.56) * mm, "end": v(-62.3, -57.63) * mm});
            skLineSegment(sketch, "E5255", {"start": v(-62.3, -57.63) * mm, "end": v(-62.29, -57.7) * mm});
            skLineSegment(sketch, "E5256", {"start": v(-62.29, -57.7) * mm, "end": v(-62.28, -57.78) * mm});
            skLineSegment(sketch, "E5257", {"start": v(-62.28, -57.78) * mm, "end": v(-62.27, -57.85) * mm});
            skLineSegment(sketch, "E5258", {"start": v(-62.27, -57.85) * mm, "end": v(-62.25, -57.93) * mm});
            skLineSegment(sketch, "E5259", {"start": v(-62.25, -57.93) * mm, "end": v(-62.23, -58) * mm});
            skLineSegment(sketch, "E5260", {"start": v(-62.21, -58.07) * mm, "end": v(-62.19, -58.14) * mm});
            skLineSegment(sketch, "E5261", {"start": v(-62.19, -58.14) * mm, "end": v(-62.16, -58.21) * mm});
            skLineSegment(sketch, "E5262", {"start": v(-62.16, -58.21) * mm, "end": v(-62.14, -58.28) * mm});
            skLineSegment(sketch, "E5263", {"start": v(-62.14, -58.28) * mm, "end": v(-62.1, -58.35) * mm});
            skLineSegment(sketch, "E5264", {"start": v(-62.1, -58.35) * mm, "end": v(-62.07, -58.42) * mm});
            skLineSegment(sketch, "E5265", {"start": v(-62.07, -58.42) * mm, "end": v(-62.04, -58.48) * mm});
            skLineSegment(sketch, "E5266", {"start": v(-62.04, -58.48) * mm, "end": v(-62, -58.55) * mm});
            skLineSegment(sketch, "E5267", {"start": v(-62, -58.55) * mm, "end": v(-61.96, -58.61) * mm});
            skLineSegment(sketch, "E5268", {"start": v(-61.96, -58.61) * mm, "end": v(-61.92, -58.67) * mm});
            skLineSegment(sketch, "E5269", {"start": v(-61.92, -58.67) * mm, "end": v(-61.88, -58.73) * mm});
            skLineSegment(sketch, "E5270", {"start": v(-61.88, -58.73) * mm, "end": v(-61.83, -58.8) * mm});
            skLineSegment(sketch, "E5271", {"start": v(-61.83, -58.8) * mm, "end": v(-61.78, -58.85) * mm});
            skLineSegment(sketch, "E5272", {"start": v(-61.78, -58.85) * mm, "end": v(-61.73, -58.9) * mm});
            skLineSegment(sketch, "E5273", {"start": v(-61.63, -59.01) * mm, "end": v(-61.57, -59.06) * mm});
            skLineSegment(sketch, "E5274", {"start": v(-61.57, -59.06) * mm, "end": v(-61.52, -59.11) * mm});
            skLineSegment(sketch, "E5275", {"start": v(-61.52, -59.11) * mm, "end": v(-61.46, -59.16) * mm});
            skLineSegment(sketch, "E5276", {"start": v(-61.46, -59.16) * mm, "end": v(-61.4, -59.2) * mm});
            skLineSegment(sketch, "E5277", {"start": v(-61.4, -59.2) * mm, "end": v(-61.34, -59.24) * mm});
            skLineSegment(sketch, "E5278", {"start": v(-61.34, -59.24) * mm, "end": v(-61.27, -59.28) * mm});
            skLineSegment(sketch, "E5279", {"start": v(-61.27, -59.28) * mm, "end": v(-61.2, -59.32) * mm});
            skLineSegment(sketch, "E5280", {"start": v(-61.2, -59.32) * mm, "end": v(-61.14, -59.36) * mm});
            skLineSegment(sketch, "E5281", {"start": v(-61.14, -59.36) * mm, "end": v(-61.08, -59.39) * mm});
            skLineSegment(sketch, "E5282", {"start": v(-61.08, -59.39) * mm, "end": v(-61, -59.42) * mm});
            skLineSegment(sketch, "E5283", {"start": v(-61, -59.42) * mm, "end": v(-60.94, -59.45) * mm});
            skLineSegment(sketch, "E5284", {"start": v(-60.94, -59.45) * mm, "end": v(-60.87, -59.47) * mm});
            skLineSegment(sketch, "E5285", {"start": v(-60.87, -59.47) * mm, "end": v(-60.8, -59.5) * mm});
            skLineSegment(sketch, "E5286", {"start": v(-60.73, -59.52) * mm, "end": v(-60.65, -59.54) * mm});
            skLineSegment(sketch, "E5287", {"start": v(-60.65, -59.54) * mm, "end": v(-60.58, -59.55) * mm});
            skLineSegment(sketch, "E5288", {"start": v(-60.58, -59.55) * mm, "end": v(-60.5, -59.57) * mm});
            skLineSegment(sketch, "E5289", {"start": v(-60.5, -59.57) * mm, "end": v(-60.43, -59.58) * mm});
            skLineSegment(sketch, "E5290", {"start": v(-60.43, -59.58) * mm, "end": v(-60.36, -59.59) * mm});
            skLineSegment(sketch, "E5291", {"start": v(-60.36, -59.59) * mm, "end": v(-60.29, -59.6) * mm});
            skLineSegment(sketch, "E5292", {"start": v(-60.29, -59.6) * mm, "end": v(-60.21, -59.6) * mm});
            skLineSegment(sketch, "E5293", {"start": v(-60.21, -59.6) * mm, "end": v(-60.14, -59.6) * mm});
            skLineSegment(sketch, "E5294", {"start": v(-60.14, -59.6) * mm, "end": v(-60.06, -59.6) * mm});
            skLineSegment(sketch, "E5295", {"start": v(-60.06, -59.6) * mm, "end": v(-59.99, -59.59) * mm});
            skLineSegment(sketch, "E5296", {"start": v(-59.99, -59.59) * mm, "end": v(-59.91, -59.58) * mm});
            skLineSegment(sketch, "E5297", {"start": v(-59.91, -59.58) * mm, "end": v(-59.84, -59.57) * mm});
            skLineSegment(sketch, "E5298", {"start": v(-59.84, -59.57) * mm, "end": v(-59.77, -59.56) * mm});
            skLineSegment(sketch, "E5299", {"start": v(-59.77, -59.56) * mm, "end": v(-59.7, -59.55) * mm});
            skLineSegment(sketch, "E5300", {"start": v(-59.7, -59.55) * mm, "end": v(-59.62, -59.53) * mm});
            skLineSegment(sketch, "E5301", {"start": v(-59.62, -59.53) * mm, "end": v(-59.55, -59.5) * mm});
            skLineSegment(sketch, "E5302", {"start": v(-59.55, -59.5) * mm, "end": v(-59.48, -59.49) * mm});
            skLineSegment(sketch, "E5303", {"start": v(-59.48, -59.49) * mm, "end": v(-59.4, -59.46) * mm});
            skLineSegment(sketch, "E5304", {"start": v(-59.4, -59.46) * mm, "end": v(-59.34, -59.43) * mm});
            skLineSegment(sketch, "E5305", {"start": v(-59.27, -59.4) * mm, "end": v(-59.2, -59.37) * mm});
            skLineSegment(sketch, "E5306", {"start": v(-59.2, -59.37) * mm, "end": v(-59.13, -59.34) * mm});
            skLineSegment(sketch, "E5307", {"start": v(-59.13, -59.34) * mm, "end": v(-59.07, -59.3) * mm});
            skLineSegment(sketch, "E5308", {"start": v(-59.07, -59.3) * mm, "end": v(-59, -59.26) * mm});
            skLineSegment(sketch, "E5309", {"start": v(-59, -59.26) * mm, "end": v(-58.94, -59.22) * mm});
            skLineSegment(sketch, "E5310", {"start": v(-58.94, -59.22) * mm, "end": v(-58.88, -59.18) * mm});
            skLineSegment(sketch, "E5311", {"start": v(-58.88, -59.18) * mm, "end": v(-58.82, -59.13) * mm});
            skLineSegment(sketch, "E5312", {"start": v(-58.82, -59.13) * mm, "end": v(-58.77, -59.09) * mm});
            skLineSegment(sketch, "E5313", {"start": v(-58.77, -59.09) * mm, "end": v(-58.7, -59.04) * mm});
            skLineSegment(sketch, "E5314", {"start": v(-58.7, -59.04) * mm, "end": v(-58.66, -58.99) * mm});
            skLineSegment(sketch, "E5315", {"start": v(-58.66, -58.99) * mm, "end": v(-58.6, -58.93) * mm});
            skLineSegment(sketch, "E5316", {"start": v(-58.6, -58.93) * mm, "end": v(-58.55, -58.88) * mm});
            skLineSegment(sketch, "E5317", {"start": v(-58.55, -58.88) * mm, "end": v(-58.5, -58.82) * mm});
            skLineSegment(sketch, "E5318", {"start": v(-58.5, -58.82) * mm, "end": v(-58.46, -58.76) * mm});
            skLineSegment(sketch, "E5319", {"start": v(-58.46, -58.76) * mm, "end": v(-58.41, -58.7) * mm});
            skLineSegment(sketch, "E5320", {"start": v(-58.33, -58.58) * mm, "end": v(-58.3, -58.52) * mm});
            skLineSegment(sketch, "E5321", {"start": v(-58.3, -58.52) * mm, "end": v(-58.25, -58.45) * mm});
            skLineSegment(sketch, "E5322", {"start": v(-58.25, -58.45) * mm, "end": v(-58.22, -58.38) * mm});
            skLineSegment(sketch, "E5323", {"start": v(-58.22, -58.38) * mm, "end": v(-58.19, -58.32) * mm});
            skLineSegment(sketch, "E5324", {"start": v(-58.19, -58.32) * mm, "end": v(-58.16, -58.25) * mm});
            skLineSegment(sketch, "E5325", {"start": v(-58.16, -58.25) * mm, "end": v(-58.13, -58.18) * mm});
            skLineSegment(sketch, "E5326", {"start": v(-58.13, -58.18) * mm, "end": v(-58.1, -58.1) * mm});
            skLineSegment(sketch, "E5327", {"start": v(-58.1, -58.1) * mm, "end": v(-58.09, -58.04) * mm});
            skLineSegment(sketch, "E5328", {"start": v(-58.09, -58.04) * mm, "end": v(-58.07, -57.96) * mm});
            skLineSegment(sketch, "E5329", {"start": v(-58.07, -57.96) * mm, "end": v(-58.05, -57.9) * mm});
            skLineSegment(sketch, "E5330", {"start": v(-58.05, -57.9) * mm, "end": v(-58.04, -57.82) * mm});
            skLineSegment(sketch, "E5331", {"start": v(-58.04, -57.82) * mm, "end": v(-58.03, -57.74) * mm});
            skLineSegment(sketch, "E5332", {"start": v(-58.03, -57.74) * mm, "end": v(-58.02, -57.67) * mm});
            skLineSegment(sketch, "E5333", {"start": v(-58.02, -57.67) * mm, "end": v(-58.01, -57.6) * mm});
            skLineSegment(sketch, "E5334", {"start": v(-58.01, -57.6) * mm, "end": v(-58, -57.52) * mm});
            skLineSegment(sketch, "E5335", {"start": v(-58, -57.52) * mm, "end": v(-58, -57.45) * mm});
            skLineSegment(sketch, "E5336", {"start": v(-58, -27.45) * mm, "end": v(-58, -27.37) * mm});
            skLineSegment(sketch, "E5337", {"start": v(-58, -27.37) * mm, "end": v(-58.01, -27.3) * mm});
            skLineSegment(sketch, "E5338", {"start": v(-58.01, -27.3) * mm, "end": v(-58.02, -27.22) * mm});
            skLineSegment(sketch, "E5339", {"start": v(-58.02, -27.22) * mm, "end": v(-58.03, -27.15) * mm});
            skLineSegment(sketch, "E5340", {"start": v(-58.03, -27.15) * mm, "end": v(-58.04, -27.07) * mm});
            skLineSegment(sketch, "E5341", {"start": v(-58.04, -27.07) * mm, "end": v(-58.05, -27) * mm});
            skLineSegment(sketch, "E5342", {"start": v(-58.05, -27) * mm, "end": v(-58.07, -26.93) * mm});
            skLineSegment(sketch, "E5343", {"start": v(-58.07, -26.93) * mm, "end": v(-58.09, -26.86) * mm});
            skLineSegment(sketch, "E5344", {"start": v(-58.09, -26.86) * mm, "end": v(-58.1, -26.79) * mm});
            skLineSegment(sketch, "E5345", {"start": v(-58.1, -26.79) * mm, "end": v(-58.13, -26.71) * mm});
            skLineSegment(sketch, "E5346", {"start": v(-58.13, -26.71) * mm, "end": v(-58.16, -26.65) * mm});
            skLineSegment(sketch, "E5347", {"start": v(-58.16, -26.65) * mm, "end": v(-58.19, -26.58) * mm});
            skLineSegment(sketch, "E5348", {"start": v(-58.19, -26.58) * mm, "end": v(-58.22, -26.5) * mm});
            skLineSegment(sketch, "E5349", {"start": v(-58.22, -26.5) * mm, "end": v(-58.25, -26.44) * mm});
            skLineSegment(sketch, "E5350", {"start": v(-58.25, -26.44) * mm, "end": v(-58.3, -26.38) * mm});
            skLineSegment(sketch, "E5351", {"start": v(-58.33, -26.31) * mm, "end": v(-58.37, -26.25) * mm});
            skLineSegment(sketch, "E5352", {"start": v(-58.37, -26.25) * mm, "end": v(-58.41, -26.19) * mm});
            skLineSegment(sketch, "E5353", {"start": v(-58.41, -26.19) * mm, "end": v(-58.46, -26.13) * mm});
            skLineSegment(sketch, "E5354", {"start": v(-58.46, -26.13) * mm, "end": v(-58.5, -26.07) * mm});
            skLineSegment(sketch, "E5355", {"start": v(-58.5, -26.07) * mm, "end": v(-58.55, -26.01) * mm});
            skLineSegment(sketch, "E5356", {"start": v(-58.55, -26.01) * mm, "end": v(-58.6, -25.96) * mm});
            skLineSegment(sketch, "E5357", {"start": v(-58.6, -25.96) * mm, "end": v(-58.66, -25.9) * mm});
            skLineSegment(sketch, "E5358", {"start": v(-58.66, -25.9) * mm, "end": v(-58.7, -25.86) * mm});
            skLineSegment(sketch, "E5359", {"start": v(-58.7, -25.86) * mm, "end": v(-58.77, -25.8) * mm});
            skLineSegment(sketch, "E5360", {"start": v(-58.77, -25.8) * mm, "end": v(-58.82, -25.76) * mm});
            skLineSegment(sketch, "E5361", {"start": v(-58.82, -25.76) * mm, "end": v(-58.88, -25.71) * mm});
            skLineSegment(sketch, "E5362", {"start": v(-58.88, -25.71) * mm, "end": v(-58.94, -25.67) * mm});
            skLineSegment(sketch, "E5363", {"start": v(-59.07, -25.6) * mm, "end": v(-59.13, -25.55) * mm});
            skLineSegment(sketch, "E5364", {"start": v(-59.13, -25.55) * mm, "end": v(-59.2, -25.52) * mm});
            skLineSegment(sketch, "E5365", {"start": v(-59.2, -25.52) * mm, "end": v(-59.27, -25.49) * mm});
            skLineSegment(sketch, "E5366", {"start": v(-59.27, -25.49) * mm, "end": v(-59.34, -25.46) * mm});
            skLineSegment(sketch, "E5367", {"start": v(-59.34, -25.46) * mm, "end": v(-59.4, -25.43) * mm});
            skLineSegment(sketch, "E5368", {"start": v(-59.4, -25.43) * mm, "end": v(-59.48, -25.4) * mm});
            skLineSegment(sketch, "E5369", {"start": v(-59.55, -25.38) * mm, "end": v(-59.62, -25.36) * mm});
            skLineSegment(sketch, "E5370", {"start": v(-59.62, -25.36) * mm, "end": v(-59.7, -25.35) * mm});
            skLineSegment(sketch, "E5371", {"start": v(-59.7, -25.35) * mm, "end": v(-59.77, -25.33) * mm});
            skLineSegment(sketch, "E5372", {"start": v(-59.77, -25.33) * mm, "end": v(-59.84, -25.32) * mm});
            skLineSegment(sketch, "E5373", {"start": v(-59.84, -25.32) * mm, "end": v(-59.91, -25.3) * mm});
            skLineSegment(sketch, "E5374", {"start": v(-59.91, -25.3) * mm, "end": v(-59.99, -25.3) * mm});
            skLineSegment(sketch, "E5375", {"start": v(-59.99, -25.3) * mm, "end": v(-60.06, -25.3) * mm});
            skLineSegment(sketch, "E5376", {"start": v(-60.06, -25.3) * mm, "end": v(-60.14, -25.3) * mm});
            skLineSegment(sketch, "E5377", {"start": v(-60.14, -25.3) * mm, "end": v(-60.21, -25.3) * mm});
            skLineSegment(sketch, "E5378", {"start": v(-60.21, -25.3) * mm, "end": v(-60.29, -25.3) * mm});
            skLineSegment(sketch, "E5379", {"start": v(-60.29, -25.3) * mm, "end": v(-60.36, -25.3) * mm});
            skLineSegment(sketch, "E5380", {"start": v(-60.36, -25.3) * mm, "end": v(-60.43, -25.31) * mm});
            skLineSegment(sketch, "E5381", {"start": v(-60.43, -25.31) * mm, "end": v(-60.5, -25.33) * mm});
            skLineSegment(sketch, "E5382", {"start": v(-60.5, -25.33) * mm, "end": v(-60.58, -25.34) * mm});
            skLineSegment(sketch, "E5383", {"start": v(-60.58, -25.34) * mm, "end": v(-60.65, -25.36) * mm});
            skLineSegment(sketch, "E5384", {"start": v(-60.65, -25.36) * mm, "end": v(-60.73, -25.37) * mm});
            skLineSegment(sketch, "E5385", {"start": v(-60.73, -25.37) * mm, "end": v(-60.8, -25.4) * mm});
            skLineSegment(sketch, "E5386", {"start": v(-61.14, -25.54) * mm, "end": v(-61.2, -25.57) * mm});
            skLineSegment(sketch, "E5387", {"start": v(-61.2, -25.57) * mm, "end": v(-61.27, -25.6) * mm});
            skLineSegment(sketch, "E5388", {"start": v(-61.27, -25.6) * mm, "end": v(-61.34, -25.65) * mm});
            skLineSegment(sketch, "E5389", {"start": v(-61.34, -25.65) * mm, "end": v(-61.4, -25.7) * mm});
            skLineSegment(sketch, "E5390", {"start": v(-61.4, -25.7) * mm, "end": v(-61.46, -25.74) * mm});
            skLineSegment(sketch, "E5391", {"start": v(-61.46, -25.74) * mm, "end": v(-61.52, -25.78) * mm});
            skLineSegment(sketch, "E5392", {"start": v(-61.52, -25.78) * mm, "end": v(-61.57, -25.83) * mm});
            skLineSegment(sketch, "E5393", {"start": v(-61.57, -25.83) * mm, "end": v(-61.63, -25.88) * mm});
            skLineSegment(sketch, "E5394", {"start": v(-61.63, -25.88) * mm, "end": v(-61.68, -25.93) * mm});
            skLineSegment(sketch, "E5395", {"start": v(-61.68, -25.93) * mm, "end": v(-61.73, -25.99) * mm});
            skLineSegment(sketch, "E5396", {"start": v(-61.73, -25.99) * mm, "end": v(-61.78, -26.04) * mm});
            skLineSegment(sketch, "E5397", {"start": v(-61.78, -26.04) * mm, "end": v(-61.83, -26.1) * mm});
            skLineSegment(sketch, "E5398", {"start": v(-61.83, -26.1) * mm, "end": v(-61.88, -26.16) * mm});
            skLineSegment(sketch, "E5399", {"start": v(-61.88, -26.16) * mm, "end": v(-61.92, -26.22) * mm});
            skLineSegment(sketch, "E5400", {"start": v(-61.96, -26.28) * mm, "end": v(-62, -26.34) * mm});
            skLineSegment(sketch, "E5401", {"start": v(-62, -26.34) * mm, "end": v(-62.04, -26.4) * mm});
            skLineSegment(sketch, "E5402", {"start": v(-62.04, -26.4) * mm, "end": v(-62.07, -26.48) * mm});
            skLineSegment(sketch, "E5403", {"start": v(-62.07, -26.48) * mm, "end": v(-62.1, -26.54) * mm});
            skLineSegment(sketch, "E5404", {"start": v(-62.1, -26.54) * mm, "end": v(-62.14, -26.61) * mm});
            skLineSegment(sketch, "E5405", {"start": v(-62.14, -26.61) * mm, "end": v(-62.16, -26.68) * mm});
            skLineSegment(sketch, "E5406", {"start": v(-62.16, -26.68) * mm, "end": v(-62.19, -26.75) * mm});
            skLineSegment(sketch, "E5407", {"start": v(-62.19, -26.75) * mm, "end": v(-62.21, -26.82) * mm});
            skLineSegment(sketch, "E5408", {"start": v(-62.21, -26.82) * mm, "end": v(-62.23, -26.9) * mm});
            skLineSegment(sketch, "E5409", {"start": v(-62.23, -26.9) * mm, "end": v(-62.25, -26.97) * mm});
            skLineSegment(sketch, "E5410", {"start": v(-62.25, -26.97) * mm, "end": v(-62.27, -27.04) * mm});
            skLineSegment(sketch, "E5411", {"start": v(-62.27, -27.04) * mm, "end": v(-62.28, -27.11) * mm});
            skLineSegment(sketch, "E5412", {"start": v(-62.28, -27.11) * mm, "end": v(-62.29, -27.19) * mm});
            skLineSegment(sketch, "E5413", {"start": v(-62.29, -27.19) * mm, "end": v(-62.3, -27.26) * mm});
            skLineSegment(sketch, "E5414", {"start": v(-62.3, -27.26) * mm, "end": v(-62.3, -27.33) * mm});
            skLineSegment(sketch, "E5415", {"start": v(-62.3, -27.33) * mm, "end": v(-62.3, -27.4) * mm});
            skLineSegment(sketch, "E5416", {"start": v(-62.3, -27.4) * mm, "end": v(-62.3, -27.48) * mm});
            skLineSegment(sketch, "E5417", {"start": v(-62.3, -27.56) * mm, "end": v(-62.3, -27.63) * mm});
            skLineSegment(sketch, "E5418", {"start": v(-62.27, -27.85) * mm, "end": v(-62.25, -27.93) * mm});
            skLineSegment(sketch, "E5419", {"start": v(-62.25, -27.93) * mm, "end": v(-62.23, -28) * mm});
            skLineSegment(sketch, "E5420", {"start": v(-62.23, -28) * mm, "end": v(-62.21, -28.07) * mm});
            skLineSegment(sketch, "E5421", {"start": v(-62.21, -28.07) * mm, "end": v(-62.19, -28.14) * mm});
            skLineSegment(sketch, "E5422", {"start": v(-62.19, -28.14) * mm, "end": v(-62.16, -28.21) * mm});
            skLineSegment(sketch, "E5423", {"start": v(-62.16, -28.21) * mm, "end": v(-62.14, -28.28) * mm});
            skLineSegment(sketch, "E5424", {"start": v(-62.14, -28.28) * mm, "end": v(-62.1, -28.35) * mm});
            skLineSegment(sketch, "E5425", {"start": v(-62.1, -28.35) * mm, "end": v(-62.07, -28.42) * mm});
            skLineSegment(sketch, "E5426", {"start": v(-62.07, -28.42) * mm, "end": v(-62.04, -28.48) * mm});
            skLineSegment(sketch, "E5427", {"start": v(-62.04, -28.48) * mm, "end": v(-62, -28.55) * mm});
            skLineSegment(sketch, "E5428", {"start": v(-62, -28.55) * mm, "end": v(-61.96, -28.61) * mm});
            skLineSegment(sketch, "E5429", {"start": v(-61.96, -28.61) * mm, "end": v(-61.92, -28.67) * mm});
            skLineSegment(sketch, "E5430", {"start": v(-61.92, -28.67) * mm, "end": v(-61.88, -28.73) * mm});
            skLineSegment(sketch, "E5431", {"start": v(-61.88, -28.73) * mm, "end": v(-61.83, -28.8) * mm});
            skLineSegment(sketch, "E5432", {"start": v(-61.83, -28.8) * mm, "end": v(-61.78, -28.85) * mm});
            skLineSegment(sketch, "E5433", {"start": v(-61.78, -28.85) * mm, "end": v(-61.73, -28.9) * mm});
            skLineSegment(sketch, "E5434", {"start": v(-61.73, -28.9) * mm, "end": v(-61.68, -28.96) * mm});
            skLineSegment(sketch, "E5435", {"start": v(-61.68, -28.96) * mm, "end": v(-61.63, -29.01) * mm});
            skLineSegment(sketch, "E5436", {"start": v(-61.63, -29.01) * mm, "end": v(-61.57, -29.06) * mm});
            skLineSegment(sketch, "E5437", {"start": v(-61.57, -29.06) * mm, "end": v(-61.52, -29.11) * mm});
            skLineSegment(sketch, "E5438", {"start": v(-61.52, -29.11) * mm, "end": v(-61.46, -29.16) * mm});
            skLineSegment(sketch, "E5439", {"start": v(-61.46, -29.16) * mm, "end": v(-61.4, -29.2) * mm});
            skLineSegment(sketch, "E5440", {"start": v(-61.4, -29.2) * mm, "end": v(-61.34, -29.24) * mm});
            skLineSegment(sketch, "E5441", {"start": v(-61.34, -29.24) * mm, "end": v(-61.27, -29.28) * mm});
            skLineSegment(sketch, "E5442", {"start": v(-61.27, -29.28) * mm, "end": v(-61.2, -29.32) * mm});
            skLineSegment(sketch, "E5443", {"start": v(-61.2, -29.32) * mm, "end": v(-61.14, -29.36) * mm});
            skLineSegment(sketch, "E5444", {"start": v(-61.14, -29.36) * mm, "end": v(-61.08, -29.39) * mm});
            skLineSegment(sketch, "E5445", {"start": v(-61.08, -29.39) * mm, "end": v(-61, -29.42) * mm});
            skLineSegment(sketch, "E5446", {"start": v(-61, -29.42) * mm, "end": v(-60.94, -29.45) * mm});
            skLineSegment(sketch, "E5447", {"start": v(-60.8, -29.5) * mm, "end": v(-60.73, -29.52) * mm});
            skLineSegment(sketch, "E5448", {"start": v(-60.73, -29.52) * mm, "end": v(-60.65, -29.54) * mm});
            skLineSegment(sketch, "E5449", {"start": v(-60.65, -29.54) * mm, "end": v(-60.58, -29.55) * mm});
            skLineSegment(sketch, "E5450", {"start": v(-60.58, -29.55) * mm, "end": v(-60.5, -29.57) * mm});
            skLineSegment(sketch, "E5451", {"start": v(-60.5, -29.57) * mm, "end": v(-60.43, -29.58) * mm});
            skLineSegment(sketch, "E5452", {"start": v(-60.43, -29.58) * mm, "end": v(-60.36, -29.59) * mm});
            skLineSegment(sketch, "E5453", {"start": v(-60.36, -29.59) * mm, "end": v(-60.29, -29.6) * mm});
            skLineSegment(sketch, "E5454", {"start": v(-60.29, -29.6) * mm, "end": v(-60.21, -29.6) * mm});
            skLineSegment(sketch, "E5455", {"start": v(-60.21, -29.6) * mm, "end": v(-60.14, -29.6) * mm});
            skLineSegment(sketch, "E5456", {"start": v(-60.14, -29.6) * mm, "end": v(-60.06, -29.6) * mm});
            skLineSegment(sketch, "E5457", {"start": v(-60.06, -29.6) * mm, "end": v(-59.99, -29.59) * mm});
            skLineSegment(sketch, "E5458", {"start": v(-59.99, -29.59) * mm, "end": v(-59.91, -29.58) * mm});
            skLineSegment(sketch, "E5459", {"start": v(-59.91, -29.58) * mm, "end": v(-59.84, -29.57) * mm});
            skLineSegment(sketch, "E5460", {"start": v(-59.84, -29.57) * mm, "end": v(-59.77, -29.56) * mm});
            skLineSegment(sketch, "E5461", {"start": v(-59.77, -29.56) * mm, "end": v(-59.7, -29.55) * mm});
            skLineSegment(sketch, "E5462", {"start": v(-59.7, -29.55) * mm, "end": v(-59.62, -29.53) * mm});
            skLineSegment(sketch, "E5463", {"start": v(-59.62, -29.53) * mm, "end": v(-59.55, -29.5) * mm});
            skLineSegment(sketch, "E5464", {"start": v(-59.55, -29.5) * mm, "end": v(-59.48, -29.49) * mm});
            skLineSegment(sketch, "E5465", {"start": v(-59.48, -29.49) * mm, "end": v(-59.4, -29.46) * mm});
            skLineSegment(sketch, "E5466", {"start": v(-59.4, -29.46) * mm, "end": v(-59.34, -29.43) * mm});
            skLineSegment(sketch, "E5467", {"start": v(-59.34, -29.43) * mm, "end": v(-59.27, -29.4) * mm});
            skLineSegment(sketch, "E5468", {"start": v(-59.27, -29.4) * mm, "end": v(-59.2, -29.37) * mm});
            skLineSegment(sketch, "E5469", {"start": v(-59.2, -29.37) * mm, "end": v(-59.13, -29.34) * mm});
            skLineSegment(sketch, "E5470", {"start": v(-59.07, -29.3) * mm, "end": v(-59, -29.26) * mm});
            skLineSegment(sketch, "E5471", {"start": v(-59, -29.26) * mm, "end": v(-58.94, -29.22) * mm});
            skLineSegment(sketch, "E5472", {"start": v(-58.94, -29.22) * mm, "end": v(-58.88, -29.18) * mm});
            skLineSegment(sketch, "E5473", {"start": v(-58.88, -29.18) * mm, "end": v(-58.82, -29.13) * mm});
            skLineSegment(sketch, "E5474", {"start": v(-58.82, -29.13) * mm, "end": v(-58.77, -29.09) * mm});
            skLineSegment(sketch, "E5475", {"start": v(-58.77, -29.09) * mm, "end": v(-58.7, -29.04) * mm});
            skLineSegment(sketch, "E5476", {"start": v(-58.7, -29.04) * mm, "end": v(-58.66, -28.99) * mm});
            skLineSegment(sketch, "E5477", {"start": v(-58.66, -28.99) * mm, "end": v(-58.6, -28.93) * mm});
            skLineSegment(sketch, "E5478", {"start": v(-58.6, -28.93) * mm, "end": v(-58.55, -28.88) * mm});
            skLineSegment(sketch, "E5479", {"start": v(-58.55, -28.88) * mm, "end": v(-58.5, -28.82) * mm});
            skLineSegment(sketch, "E5480", {"start": v(-58.5, -28.82) * mm, "end": v(-58.46, -28.76) * mm});
            skLineSegment(sketch, "E5481", {"start": v(-58.46, -28.76) * mm, "end": v(-58.41, -28.7) * mm});
            skLineSegment(sketch, "E5482", {"start": v(-58.41, -28.7) * mm, "end": v(-58.37, -28.64) * mm});
            skLineSegment(sketch, "E5483", {"start": v(-58.37, -28.64) * mm, "end": v(-58.33, -28.58) * mm});
            skLineSegment(sketch, "E5484", {"start": v(-58.33, -28.58) * mm, "end": v(-58.3, -28.52) * mm});
            skLineSegment(sketch, "E5485", {"start": v(-58.3, -28.52) * mm, "end": v(-58.25, -28.45) * mm});
            skLineSegment(sketch, "E5486", {"start": v(-58.25, -28.45) * mm, "end": v(-58.22, -28.38) * mm});
            skLineSegment(sketch, "E5487", {"start": v(-58.22, -28.38) * mm, "end": v(-58.19, -28.32) * mm});
            skLineSegment(sketch, "E5488", {"start": v(-58.19, -28.32) * mm, "end": v(-58.16, -28.25) * mm});
            skLineSegment(sketch, "E5489", {"start": v(-58.16, -28.25) * mm, "end": v(-58.13, -28.18) * mm});
            skLineSegment(sketch, "E5490", {"start": v(-58.13, -28.18) * mm, "end": v(-58.1, -28.1) * mm});
            skLineSegment(sketch, "E5491", {"start": v(-58.1, -28.1) * mm, "end": v(-58.09, -28.04) * mm});
            skLineSegment(sketch, "E5492", {"start": v(-58.09, -28.04) * mm, "end": v(-58.07, -27.96) * mm});
            skLineSegment(sketch, "E5493", {"start": v(-58.07, -27.96) * mm, "end": v(-58.05, -27.9) * mm});
            skLineSegment(sketch, "E5494", {"start": v(-58.05, -27.9) * mm, "end": v(-58.04, -27.82) * mm});
            skLineSegment(sketch, "E5495", {"start": v(-58.04, -27.82) * mm, "end": v(-58.03, -27.74) * mm});
            skLineSegment(sketch, "E5496", {"start": v(-58.01, -27.6) * mm, "end": v(-58, -27.52) * mm});
            skLineSegment(sketch, "E5497", {"start": v(-58, -27.52) * mm, "end": v(-58, -27.45) * mm});
            skLineSegment(sketch, "E5498", {"start": v(-68, -27.45) * mm, "end": v(-68, -27.37) * mm});
            skLineSegment(sketch, "E5499", {"start": v(-68, -27.37) * mm, "end": v(-68.01, -27.3) * mm});
            skLineSegment(sketch, "E5500", {"start": v(-68.01, -27.3) * mm, "end": v(-68.02, -27.22) * mm});
            skLineSegment(sketch, "E5501", {"start": v(-68.02, -27.22) * mm, "end": v(-68.03, -27.15) * mm});
            skLineSegment(sketch, "E5502", {"start": v(-68.03, -27.15) * mm, "end": v(-68.04, -27.07) * mm});
            skLineSegment(sketch, "E5503", {"start": v(-68.04, -27.07) * mm, "end": v(-68.05, -27) * mm});
            skLineSegment(sketch, "E5504", {"start": v(-68.05, -27) * mm, "end": v(-68.07, -26.93) * mm});
            skLineSegment(sketch, "E5505", {"start": v(-68.07, -26.93) * mm, "end": v(-68.09, -26.86) * mm});
            skLineSegment(sketch, "E5506", {"start": v(-68.09, -26.86) * mm, "end": v(-68.1, -26.79) * mm});
            skLineSegment(sketch, "E5507", {"start": v(-68.1, -26.79) * mm, "end": v(-68.13, -26.71) * mm});
            skLineSegment(sketch, "E5508", {"start": v(-68.13, -26.71) * mm, "end": v(-68.16, -26.65) * mm});
            skLineSegment(sketch, "E5509", {"start": v(-68.16, -26.65) * mm, "end": v(-68.19, -26.58) * mm});
            skLineSegment(sketch, "E5510", {"start": v(-68.19, -26.58) * mm, "end": v(-68.22, -26.5) * mm});
            skLineSegment(sketch, "E5511", {"start": v(-68.22, -26.5) * mm, "end": v(-68.25, -26.44) * mm});
            skLineSegment(sketch, "E5512", {"start": v(-68.25, -26.44) * mm, "end": v(-68.3, -26.38) * mm});
            skLineSegment(sketch, "E5513", {"start": v(-68.3, -26.38) * mm, "end": v(-68.33, -26.31) * mm});
            skLineSegment(sketch, "E5514", {"start": v(-68.37, -26.25) * mm, "end": v(-68.41, -26.19) * mm});
            skLineSegment(sketch, "E5515", {"start": v(-68.41, -26.19) * mm, "end": v(-68.46, -26.13) * mm});
            skLineSegment(sketch, "E5516", {"start": v(-68.46, -26.13) * mm, "end": v(-68.5, -26.07) * mm});
            skLineSegment(sketch, "E5517", {"start": v(-68.5, -26.07) * mm, "end": v(-68.55, -26.01) * mm});
            skLineSegment(sketch, "E5518", {"start": v(-68.55, -26.01) * mm, "end": v(-68.6, -25.96) * mm});
            skLineSegment(sketch, "E5519", {"start": v(-68.6, -25.96) * mm, "end": v(-68.66, -25.9) * mm});
            skLineSegment(sketch, "E5520", {"start": v(-68.66, -25.9) * mm, "end": v(-68.7, -25.86) * mm});
            skLineSegment(sketch, "E5521", {"start": v(-68.7, -25.86) * mm, "end": v(-68.77, -25.8) * mm});
            skLineSegment(sketch, "E5522", {"start": v(-68.77, -25.8) * mm, "end": v(-68.82, -25.76) * mm});
            skLineSegment(sketch, "E5523", {"start": v(-68.82, -25.76) * mm, "end": v(-68.88, -25.71) * mm});
            skLineSegment(sketch, "E5524", {"start": v(-68.88, -25.71) * mm, "end": v(-68.94, -25.67) * mm});
            skLineSegment(sketch, "E5525", {"start": v(-68.94, -25.67) * mm, "end": v(-69, -25.63) * mm});
            skLineSegment(sketch, "E5526", {"start": v(-69, -25.63) * mm, "end": v(-69.07, -25.6) * mm});
            skLineSegment(sketch, "E5527", {"start": v(-69.34, -25.46) * mm, "end": v(-69.4, -25.43) * mm});
            skLineSegment(sketch, "E5528", {"start": v(-69.4, -25.43) * mm, "end": v(-69.48, -25.4) * mm});
            skLineSegment(sketch, "E5529", {"start": v(-69.48, -25.4) * mm, "end": v(-69.55, -25.38) * mm});
            skLineSegment(sketch, "E5530", {"start": v(-69.55, -25.38) * mm, "end": v(-69.62, -25.36) * mm});
            skLineSegment(sketch, "E5531", {"start": v(-69.7, -25.35) * mm, "end": v(-69.77, -25.33) * mm});
            skLineSegment(sketch, "E5532", {"start": v(-69.77, -25.33) * mm, "end": v(-69.84, -25.32) * mm});
            skLineSegment(sketch, "E5533", {"start": v(-69.84, -25.32) * mm, "end": v(-69.91, -25.3) * mm});
            skLineSegment(sketch, "E5534", {"start": v(-69.91, -25.3) * mm, "end": v(-69.99, -25.3) * mm});
            skLineSegment(sketch, "E5535", {"start": v(-69.99, -25.3) * mm, "end": v(-70.06, -25.3) * mm});
            skLineSegment(sketch, "E5536", {"start": v(-70.06, -25.3) * mm, "end": v(-70.14, -25.3) * mm});
            skLineSegment(sketch, "E5537", {"start": v(-70.14, -25.3) * mm, "end": v(-70.21, -25.3) * mm});
            skLineSegment(sketch, "E5538", {"start": v(-70.21, -25.3) * mm, "end": v(-70.29, -25.3) * mm});
            skLineSegment(sketch, "E5539", {"start": v(-70.29, -25.3) * mm, "end": v(-70.36, -25.3) * mm});
            skLineSegment(sketch, "E5540", {"start": v(-70.36, -25.3) * mm, "end": v(-70.43, -25.31) * mm});
            skLineSegment(sketch, "E5541", {"start": v(-70.43, -25.31) * mm, "end": v(-70.5, -25.33) * mm});
            skLineSegment(sketch, "E5542", {"start": v(-70.5, -25.33) * mm, "end": v(-70.58, -25.34) * mm});
            skLineSegment(sketch, "E5543", {"start": v(-70.58, -25.34) * mm, "end": v(-70.65, -25.36) * mm});
            skLineSegment(sketch, "E5544", {"start": v(-70.65, -25.36) * mm, "end": v(-70.73, -25.37) * mm});
            skLineSegment(sketch, "E5545", {"start": v(-70.73, -25.37) * mm, "end": v(-70.8, -25.4) * mm});
            skLineSegment(sketch, "E5546", {"start": v(-70.8, -25.4) * mm, "end": v(-70.87, -25.42) * mm});
            skLineSegment(sketch, "E5547", {"start": v(-70.87, -25.42) * mm, "end": v(-70.94, -25.44) * mm});
            skLineSegment(sketch, "E5548", {"start": v(-70.94, -25.44) * mm, "end": v(-71, -25.47) * mm});
            skLineSegment(sketch, "E5549", {"start": v(-71, -25.47) * mm, "end": v(-71.08, -25.5) * mm});
            skLineSegment(sketch, "E5550", {"start": v(-71.34, -25.65) * mm, "end": v(-71.4, -25.7) * mm});
            skLineSegment(sketch, "E5551", {"start": v(-71.4, -25.7) * mm, "end": v(-71.46, -25.74) * mm});
            skLineSegment(sketch, "E5552", {"start": v(-71.46, -25.74) * mm, "end": v(-71.52, -25.78) * mm});
            skLineSegment(sketch, "E5553", {"start": v(-71.52, -25.78) * mm, "end": v(-71.57, -25.83) * mm});
            skLineSegment(sketch, "E5554", {"start": v(-71.57, -25.83) * mm, "end": v(-71.63, -25.88) * mm});
            skLineSegment(sketch, "E5555", {"start": v(-71.63, -25.88) * mm, "end": v(-71.68, -25.93) * mm});
            skLineSegment(sketch, "E5556", {"start": v(-71.68, -25.93) * mm, "end": v(-71.73, -25.99) * mm});
            skLineSegment(sketch, "E5557", {"start": v(-71.73, -25.99) * mm, "end": v(-71.78, -26.04) * mm});
            skLineSegment(sketch, "E5558", {"start": v(-71.78, -26.04) * mm, "end": v(-71.83, -26.1) * mm});
            skLineSegment(sketch, "E5559", {"start": v(-71.83, -26.1) * mm, "end": v(-71.88, -26.16) * mm});
            skLineSegment(sketch, "E5560", {"start": v(-71.88, -26.16) * mm, "end": v(-71.92, -26.22) * mm});
            skLineSegment(sketch, "E5561", {"start": v(-71.92, -26.22) * mm, "end": v(-71.96, -26.28) * mm});
            skLineSegment(sketch, "E5562", {"start": v(-72, -26.34) * mm, "end": v(-72.04, -26.4) * mm});
            skLineSegment(sketch, "E5563", {"start": v(-72.04, -26.4) * mm, "end": v(-72.07, -26.48) * mm});
            skLineSegment(sketch, "E5564", {"start": v(-72.07, -26.48) * mm, "end": v(-72.1, -26.54) * mm});
            skLineSegment(sketch, "E5565", {"start": v(-72.1, -26.54) * mm, "end": v(-72.14, -26.61) * mm});
            skLineSegment(sketch, "E5566", {"start": v(-72.14, -26.61) * mm, "end": v(-72.16, -26.68) * mm});
            skLineSegment(sketch, "E5567", {"start": v(-72.16, -26.68) * mm, "end": v(-72.19, -26.75) * mm});
            skLineSegment(sketch, "E5568", {"start": v(-72.19, -26.75) * mm, "end": v(-72.21, -26.82) * mm});
            skLineSegment(sketch, "E5569", {"start": v(-72.21, -26.82) * mm, "end": v(-72.23, -26.9) * mm});
            skLineSegment(sketch, "E5570", {"start": v(-72.23, -26.9) * mm, "end": v(-72.25, -26.97) * mm});
            skLineSegment(sketch, "E5571", {"start": v(-72.25, -26.97) * mm, "end": v(-72.27, -27.04) * mm});
            skLineSegment(sketch, "E5572", {"start": v(-72.27, -27.04) * mm, "end": v(-72.28, -27.11) * mm});
            skLineSegment(sketch, "E5573", {"start": v(-72.28, -27.11) * mm, "end": v(-72.29, -27.19) * mm});
            skLineSegment(sketch, "E5574", {"start": v(-72.29, -27.19) * mm, "end": v(-72.3, -27.26) * mm});
            skLineSegment(sketch, "E5575", {"start": v(-72.3, -27.26) * mm, "end": v(-72.3, -27.33) * mm});
            skLineSegment(sketch, "E5576", {"start": v(-72.3, -27.33) * mm, "end": v(-72.3, -27.4) * mm});
            skLineSegment(sketch, "E5577", {"start": v(-72.3, -27.4) * mm, "end": v(-72.3, -27.48) * mm});
            skLineSegment(sketch, "E5578", {"start": v(-72.29, -27.7) * mm, "end": v(-72.28, -27.78) * mm});
            skLineSegment(sketch, "E5579", {"start": v(-72.28, -27.78) * mm, "end": v(-72.27, -27.85) * mm});
            skLineSegment(sketch, "E5580", {"start": v(-72.27, -27.85) * mm, "end": v(-72.25, -27.93) * mm});
            skLineSegment(sketch, "E5581", {"start": v(-72.25, -27.93) * mm, "end": v(-72.23, -28) * mm});
            skLineSegment(sketch, "E5582", {"start": v(-72.23, -28) * mm, "end": v(-72.21, -28.07) * mm});
            skLineSegment(sketch, "E5583", {"start": v(-72.21, -28.07) * mm, "end": v(-72.19, -28.14) * mm});
            skLineSegment(sketch, "E5584", {"start": v(-72.19, -28.14) * mm, "end": v(-72.16, -28.21) * mm});
            skLineSegment(sketch, "E5585", {"start": v(-72.16, -28.21) * mm, "end": v(-72.14, -28.28) * mm});
            skLineSegment(sketch, "E5586", {"start": v(-72.14, -28.28) * mm, "end": v(-72.1, -28.35) * mm});
            skLineSegment(sketch, "E5587", {"start": v(-72.1, -28.35) * mm, "end": v(-72.07, -28.42) * mm});
            skLineSegment(sketch, "E5588", {"start": v(-72.07, -28.42) * mm, "end": v(-72.04, -28.48) * mm});
            skLineSegment(sketch, "E5589", {"start": v(-72.04, -28.48) * mm, "end": v(-72, -28.55) * mm});
            skLineSegment(sketch, "E5590", {"start": v(-72, -28.55) * mm, "end": v(-71.96, -28.61) * mm});
            skLineSegment(sketch, "E5591", {"start": v(-71.96, -28.61) * mm, "end": v(-71.92, -28.67) * mm});
            skLineSegment(sketch, "E5592", {"start": v(-71.92, -28.67) * mm, "end": v(-71.88, -28.73) * mm});
            skLineSegment(sketch, "E5593", {"start": v(-71.88, -28.73) * mm, "end": v(-71.83, -28.8) * mm});
            skLineSegment(sketch, "E5594", {"start": v(-71.83, -28.8) * mm, "end": v(-71.78, -28.85) * mm});
            skLineSegment(sketch, "E5595", {"start": v(-71.78, -28.85) * mm, "end": v(-71.73, -28.9) * mm});
            skLineSegment(sketch, "E5596", {"start": v(-71.73, -28.9) * mm, "end": v(-71.68, -28.96) * mm});
            skLineSegment(sketch, "E5597", {"start": v(-71.68, -28.96) * mm, "end": v(-71.63, -29.01) * mm});
            skLineSegment(sketch, "E5598", {"start": v(-71.63, -29.01) * mm, "end": v(-71.57, -29.06) * mm});
            skLineSegment(sketch, "E5599", {"start": v(-71.57, -29.06) * mm, "end": v(-71.52, -29.11) * mm});
            skLineSegment(sketch, "E5600", {"start": v(-71.52, -29.11) * mm, "end": v(-71.46, -29.16) * mm});
            skLineSegment(sketch, "E5601", {"start": v(-71.46, -29.16) * mm, "end": v(-71.4, -29.2) * mm});
            skLineSegment(sketch, "E5602", {"start": v(-71.4, -29.2) * mm, "end": v(-71.34, -29.24) * mm});
            skLineSegment(sketch, "E5603", {"start": v(-71.34, -29.24) * mm, "end": v(-71.27, -29.28) * mm});
            skLineSegment(sketch, "E5604", {"start": v(-71.27, -29.28) * mm, "end": v(-71.2, -29.32) * mm});
            skLineSegment(sketch, "E5605", {"start": v(-71.2, -29.32) * mm, "end": v(-71.14, -29.36) * mm});
            skLineSegment(sketch, "E5606", {"start": v(-71.08, -29.39) * mm, "end": v(-71, -29.42) * mm});
            skLineSegment(sketch, "E5607", {"start": v(-71, -29.42) * mm, "end": v(-70.94, -29.45) * mm});
            skLineSegment(sketch, "E5608", {"start": v(-70.94, -29.45) * mm, "end": v(-70.87, -29.47) * mm});
            skLineSegment(sketch, "E5609", {"start": v(-70.87, -29.47) * mm, "end": v(-70.8, -29.5) * mm});
            skLineSegment(sketch, "E5610", {"start": v(-70.8, -29.5) * mm, "end": v(-70.73, -29.52) * mm});
            skLineSegment(sketch, "E5611", {"start": v(-70.73, -29.52) * mm, "end": v(-70.65, -29.54) * mm});
            skLineSegment(sketch, "E5612", {"start": v(-70.65, -29.54) * mm, "end": v(-70.58, -29.55) * mm});
            skLineSegment(sketch, "E5613", {"start": v(-70.58, -29.55) * mm, "end": v(-70.5, -29.57) * mm});
            skLineSegment(sketch, "E5614", {"start": v(-70.5, -29.57) * mm, "end": v(-70.43, -29.58) * mm});
            skLineSegment(sketch, "E5615", {"start": v(-70.43, -29.58) * mm, "end": v(-70.36, -29.59) * mm});
            skLineSegment(sketch, "E5616", {"start": v(-70.36, -29.59) * mm, "end": v(-70.29, -29.6) * mm});
            skLineSegment(sketch, "E5617", {"start": v(-70.29, -29.6) * mm, "end": v(-70.21, -29.6) * mm});
            skLineSegment(sketch, "E5618", {"start": v(-70.21, -29.6) * mm, "end": v(-70.14, -29.6) * mm});
            skLineSegment(sketch, "E5619", {"start": v(-70.14, -29.6) * mm, "end": v(-70.06, -29.6) * mm});
            skLineSegment(sketch, "E5620", {"start": v(-70.06, -29.6) * mm, "end": v(-69.99, -29.59) * mm});
            skLineSegment(sketch, "E5621", {"start": v(-69.99, -29.59) * mm, "end": v(-69.91, -29.58) * mm});
            skLineSegment(sketch, "E5622", {"start": v(-69.91, -29.58) * mm, "end": v(-69.84, -29.57) * mm});
            skLineSegment(sketch, "E5623", {"start": v(-69.84, -29.57) * mm, "end": v(-69.77, -29.56) * mm});
            skLineSegment(sketch, "E5624", {"start": v(-69.77, -29.56) * mm, "end": v(-69.7, -29.55) * mm});
            skLineSegment(sketch, "E5625", {"start": v(-69.7, -29.55) * mm, "end": v(-69.62, -29.53) * mm});
            skLineSegment(sketch, "E5626", {"start": v(-69.62, -29.53) * mm, "end": v(-69.55, -29.5) * mm});
            skLineSegment(sketch, "E5627", {"start": v(-69.55, -29.5) * mm, "end": v(-69.48, -29.49) * mm});
            skLineSegment(sketch, "E5628", {"start": v(-69.48, -29.49) * mm, "end": v(-69.4, -29.46) * mm});
            skLineSegment(sketch, "E5629", {"start": v(-69.4, -29.46) * mm, "end": v(-69.34, -29.43) * mm});
            skLineSegment(sketch, "E5630", {"start": v(-69.27, -29.4) * mm, "end": v(-69.2, -29.37) * mm});
            skLineSegment(sketch, "E5631", {"start": v(-69.2, -29.37) * mm, "end": v(-69.13, -29.34) * mm});
            skLineSegment(sketch, "E5632", {"start": v(-69.13, -29.34) * mm, "end": v(-69.07, -29.3) * mm});
            skLineSegment(sketch, "E5633", {"start": v(-69.07, -29.3) * mm, "end": v(-69, -29.26) * mm});
            skLineSegment(sketch, "E5634", {"start": v(-69, -29.26) * mm, "end": v(-68.94, -29.22) * mm});
            skLineSegment(sketch, "E5635", {"start": v(-68.94, -29.22) * mm, "end": v(-68.88, -29.18) * mm});
            skLineSegment(sketch, "E5636", {"start": v(-68.88, -29.18) * mm, "end": v(-68.82, -29.13) * mm});
            skLineSegment(sketch, "E5637", {"start": v(-68.82, -29.13) * mm, "end": v(-68.77, -29.09) * mm});
            skLineSegment(sketch, "E5638", {"start": v(-68.77, -29.09) * mm, "end": v(-68.7, -29.04) * mm});
            skLineSegment(sketch, "E5639", {"start": v(-68.7, -29.04) * mm, "end": v(-68.66, -28.99) * mm});
            skLineSegment(sketch, "E5640", {"start": v(-68.66, -28.99) * mm, "end": v(-68.6, -28.93) * mm});
            skLineSegment(sketch, "E5641", {"start": v(-68.6, -28.93) * mm, "end": v(-68.55, -28.88) * mm});
            skLineSegment(sketch, "E5642", {"start": v(-68.55, -28.88) * mm, "end": v(-68.5, -28.82) * mm});
            skLineSegment(sketch, "E5643", {"start": v(-68.5, -28.82) * mm, "end": v(-68.46, -28.76) * mm});
            skLineSegment(sketch, "E5644", {"start": v(-68.46, -28.76) * mm, "end": v(-68.41, -28.7) * mm});
            skLineSegment(sketch, "E5645", {"start": v(-68.41, -28.7) * mm, "end": v(-68.37, -28.64) * mm});
            skLineSegment(sketch, "E5646", {"start": v(-68.37, -28.64) * mm, "end": v(-68.33, -28.58) * mm});
            skLineSegment(sketch, "E5647", {"start": v(-68.33, -28.58) * mm, "end": v(-68.3, -28.52) * mm});
            skLineSegment(sketch, "E5648", {"start": v(-68.3, -28.52) * mm, "end": v(-68.25, -28.45) * mm});
            skLineSegment(sketch, "E5649", {"start": v(-68.25, -28.45) * mm, "end": v(-68.22, -28.38) * mm});
            skLineSegment(sketch, "E5650", {"start": v(-68.22, -28.38) * mm, "end": v(-68.19, -28.32) * mm});
            skLineSegment(sketch, "E5651", {"start": v(-68.19, -28.32) * mm, "end": v(-68.16, -28.25) * mm});
            skLineSegment(sketch, "E5652", {"start": v(-68.16, -28.25) * mm, "end": v(-68.13, -28.18) * mm});
            skLineSegment(sketch, "E5653", {"start": v(-68.13, -28.18) * mm, "end": v(-68.1, -28.1) * mm});
            skLineSegment(sketch, "E5654", {"start": v(-68.1, -28.1) * mm, "end": v(-68.09, -28.04) * mm});
            skLineSegment(sketch, "E5655", {"start": v(-68.09, -28.04) * mm, "end": v(-68.07, -27.96) * mm});
            skLineSegment(sketch, "E5656", {"start": v(-68.07, -27.96) * mm, "end": v(-68.05, -27.9) * mm});
            skLineSegment(sketch, "E5657", {"start": v(-68.05, -27.9) * mm, "end": v(-68.04, -27.82) * mm});
            skLineSegment(sketch, "E5658", {"start": v(-68.04, -27.82) * mm, "end": v(-68.03, -27.74) * mm});
            skLineSegment(sketch, "E5659", {"start": v(-68.01, -27.6) * mm, "end": v(-68, -27.52) * mm});
            skLineSegment(sketch, "E5660", {"start": v(-68, -27.52) * mm, "end": v(-68, -27.45) * mm});
            skLineSegment(sketch, "E5661", {"start": v(87.24, -60.05) * mm, "end": v(87.24, -60.01) * mm});
            skLineSegment(sketch, "E5662", {"start": v(87.24, -60.01) * mm, "end": v(87.24, -59.97) * mm});
            skLineSegment(sketch, "E5663", {"start": v(87.24, -59.97) * mm, "end": v(87.23, -59.92) * mm});
            skLineSegment(sketch, "E5664", {"start": v(87.23, -59.92) * mm, "end": v(87.23, -59.88) * mm});
            skLineSegment(sketch, "E5665", {"start": v(87.23, -59.88) * mm, "end": v(87.22, -59.84) * mm});
            skLineSegment(sketch, "E5666", {"start": v(87.22, -59.84) * mm, "end": v(87.21, -59.8) * mm});
            skLineSegment(sketch, "E5667", {"start": v(87.21, -59.8) * mm, "end": v(87.2, -59.75) * mm});
            skLineSegment(sketch, "E5668", {"start": v(87.2, -59.75) * mm, "end": v(87.2, -59.71) * mm});
            skLineSegment(sketch, "E5669", {"start": v(87.2, -59.71) * mm, "end": v(87.18, -59.67) * mm});
            skLineSegment(sketch, "E5670", {"start": v(87.18, -59.67) * mm, "end": v(87.17, -59.63) * mm});
            skLineSegment(sketch, "E5671", {"start": v(87.17, -59.63) * mm, "end": v(87.15, -59.59) * mm});
            skLineSegment(sketch, "E5672", {"start": v(87.15, -59.59) * mm, "end": v(87.13, -59.55) * mm});
            skLineSegment(sketch, "E5673", {"start": v(87.13, -59.55) * mm, "end": v(87.12, -59.5) * mm});
            skLineSegment(sketch, "E5674", {"start": v(87.12, -59.5) * mm, "end": v(87.1, -59.47) * mm});
            skLineSegment(sketch, "E5675", {"start": v(87.1, -59.47) * mm, "end": v(87.08, -59.43) * mm});
            skLineSegment(sketch, "E5676", {"start": v(87.08, -59.43) * mm, "end": v(87.05, -59.4) * mm});
            skLineSegment(sketch, "E5677", {"start": v(87.05, -59.4) * mm, "end": v(87.03, -59.36) * mm});
            skLineSegment(sketch, "E5678", {"start": v(87.03, -59.36) * mm, "end": v(87, -59.32) * mm});
            skLineSegment(sketch, "E5679", {"start": v(87, -59.32) * mm, "end": v(86.98, -59.29) * mm});
            skLineSegment(sketch, "E5680", {"start": v(86.98, -59.29) * mm, "end": v(86.95, -59.25) * mm});
            skLineSegment(sketch, "E5681", {"start": v(86.95, -59.25) * mm, "end": v(86.92, -59.22) * mm});
            skLineSegment(sketch, "E5682", {"start": v(86.92, -59.22) * mm, "end": v(86.9, -59.19) * mm});
            skLineSegment(sketch, "E5683", {"start": v(86.9, -59.19) * mm, "end": v(86.86, -59.16) * mm});
            skLineSegment(sketch, "E5684", {"start": v(86.86, -59.16) * mm, "end": v(86.83, -59.13) * mm});
            skLineSegment(sketch, "E5685", {"start": v(86.83, -59.13) * mm, "end": v(86.8, -59.1) * mm});
            skLineSegment(sketch, "E5686", {"start": v(86.8, -59.1) * mm, "end": v(86.77, -59.07) * mm});
            skLineSegment(sketch, "E5687", {"start": v(86.77, -59.07) * mm, "end": v(86.73, -59.05) * mm});
            skLineSegment(sketch, "E5688", {"start": v(86.73, -59.05) * mm, "end": v(86.7, -59.02) * mm});
            skLineSegment(sketch, "E5689", {"start": v(86.7, -59.02) * mm, "end": v(86.66, -59) * mm});
            skLineSegment(sketch, "E5690", {"start": v(86.66, -59) * mm, "end": v(86.62, -58.97) * mm});
            skLineSegment(sketch, "E5691", {"start": v(86.62, -58.97) * mm, "end": v(86.58, -58.95) * mm});
            skLineSegment(sketch, "E5692", {"start": v(86.58, -58.95) * mm, "end": v(86.55, -58.93) * mm});
            skLineSegment(sketch, "E5693", {"start": v(86.55, -58.93) * mm, "end": v(86.5, -58.92) * mm});
            skLineSegment(sketch, "E5694", {"start": v(86.47, -58.9) * mm, "end": v(86.43, -58.88) * mm});
            skLineSegment(sketch, "E5695", {"start": v(86.43, -58.88) * mm, "end": v(86.39, -58.87) * mm});
            skLineSegment(sketch, "E5696", {"start": v(86.39, -58.87) * mm, "end": v(86.34, -58.85) * mm});
            skLineSegment(sketch, "E5697", {"start": v(86.34, -58.85) * mm, "end": v(86.3, -58.84) * mm});
            skLineSegment(sketch, "E5698", {"start": v(86.3, -58.84) * mm, "end": v(86.26, -58.83) * mm});
            skLineSegment(sketch, "E5699", {"start": v(86.26, -58.83) * mm, "end": v(86.22, -58.82) * mm});
            skLineSegment(sketch, "E5700", {"start": v(86.22, -58.82) * mm, "end": v(86.17, -58.82) * mm});
            skLineSegment(sketch, "E5701", {"start": v(86.17, -58.82) * mm, "end": v(86.13, -58.81) * mm});
            skLineSegment(sketch, "E5702", {"start": v(86.13, -58.81) * mm, "end": v(86.09, -58.8) * mm});
            skLineSegment(sketch, "E5703", {"start": v(86.09, -58.8) * mm, "end": v(86.05, -58.8) * mm});
            skLineSegment(sketch, "E5704", {"start": v(86.05, -58.8) * mm, "end": v(86, -58.8) * mm});
            skLineSegment(sketch, "E5705", {"start": v(86, -58.8) * mm, "end": v(85.96, -58.8) * mm});
            skLineSegment(sketch, "E5706", {"start": v(85.96, -58.8) * mm, "end": v(85.92, -58.8) * mm});
            skLineSegment(sketch, "E5707", {"start": v(85.92, -58.8) * mm, "end": v(85.87, -58.8) * mm});
            skLineSegment(sketch, "E5708", {"start": v(85.87, -58.8) * mm, "end": v(85.83, -58.81) * mm});
            skLineSegment(sketch, "E5709", {"start": v(85.83, -58.81) * mm, "end": v(85.79, -58.82) * mm});
            skLineSegment(sketch, "E5710", {"start": v(85.79, -58.82) * mm, "end": v(85.74, -58.83) * mm});
            skLineSegment(sketch, "E5711", {"start": v(85.74, -58.83) * mm, "end": v(85.7, -58.84) * mm});
            skLineSegment(sketch, "E5712", {"start": v(85.7, -58.84) * mm, "end": v(85.66, -58.85) * mm});
            skLineSegment(sketch, "E5713", {"start": v(85.66, -58.85) * mm, "end": v(85.62, -58.86) * mm});
            skLineSegment(sketch, "E5714", {"start": v(85.62, -58.86) * mm, "end": v(85.58, -58.87) * mm});
            skLineSegment(sketch, "E5715", {"start": v(85.58, -58.87) * mm, "end": v(85.54, -58.89) * mm});
            skLineSegment(sketch, "E5716", {"start": v(85.54, -58.89) * mm, "end": v(85.5, -58.9) * mm});
            skLineSegment(sketch, "E5717", {"start": v(85.5, -58.9) * mm, "end": v(85.46, -58.92) * mm});
            skLineSegment(sketch, "E5718", {"start": v(85.46, -58.92) * mm, "end": v(85.42, -58.94) * mm});
            skLineSegment(sketch, "E5719", {"start": v(85.42, -58.94) * mm, "end": v(85.38, -58.96) * mm});
            skLineSegment(sketch, "E5720", {"start": v(85.38, -58.96) * mm, "end": v(85.34, -58.99) * mm});
            skLineSegment(sketch, "E5721", {"start": v(85.34, -58.99) * mm, "end": v(85.3, -59) * mm});
            skLineSegment(sketch, "E5722", {"start": v(85.3, -59) * mm, "end": v(85.27, -59.03) * mm});
            skLineSegment(sketch, "E5723", {"start": v(85.27, -59.03) * mm, "end": v(85.23, -59.06) * mm});
            skLineSegment(sketch, "E5724", {"start": v(85.23, -59.06) * mm, "end": v(85.2, -59.09) * mm});
            skLineSegment(sketch, "E5725", {"start": v(85.2, -59.09) * mm, "end": v(85.17, -59.11) * mm});
            skLineSegment(sketch, "E5726", {"start": v(85.17, -59.11) * mm, "end": v(85.13, -59.14) * mm});
            skLineSegment(sketch, "E5727", {"start": v(85.13, -59.14) * mm, "end": v(85.1, -59.17) * mm});
            skLineSegment(sketch, "E5728", {"start": v(85.1, -59.17) * mm, "end": v(85.07, -59.2) * mm});
            skLineSegment(sketch, "E5729", {"start": v(85.07, -59.2) * mm, "end": v(85.04, -59.24) * mm});
            skLineSegment(sketch, "E5730", {"start": v(85.04, -59.24) * mm, "end": v(85.02, -59.27) * mm});
            skLineSegment(sketch, "E5731", {"start": v(85.02, -59.27) * mm, "end": v(84.99, -59.3) * mm});
            skLineSegment(sketch, "E5732", {"start": v(84.99, -59.3) * mm, "end": v(84.96, -59.34) * mm});
            skLineSegment(sketch, "E5733", {"start": v(84.96, -59.34) * mm, "end": v(84.94, -59.38) * mm});
            skLineSegment(sketch, "E5734", {"start": v(84.94, -59.38) * mm, "end": v(84.92, -59.41) * mm});
            skLineSegment(sketch, "E5735", {"start": v(84.92, -59.41) * mm, "end": v(84.9, -59.45) * mm});
            skLineSegment(sketch, "E5736", {"start": v(84.9, -59.45) * mm, "end": v(84.88, -59.49) * mm});
            skLineSegment(sketch, "E5737", {"start": v(84.88, -59.49) * mm, "end": v(84.86, -59.53) * mm});
            skLineSegment(sketch, "E5738", {"start": v(84.86, -59.53) * mm, "end": v(84.84, -59.57) * mm});
            skLineSegment(sketch, "E5739", {"start": v(84.84, -59.57) * mm, "end": v(84.82, -59.6) * mm});
            skLineSegment(sketch, "E5740", {"start": v(84.82, -59.6) * mm, "end": v(84.8, -59.65) * mm});
            skLineSegment(sketch, "E5741", {"start": v(84.8, -59.65) * mm, "end": v(84.8, -59.7) * mm});
            skLineSegment(sketch, "E5742", {"start": v(84.8, -59.7) * mm, "end": v(84.78, -59.73) * mm});
            skLineSegment(sketch, "E5743", {"start": v(84.78, -59.73) * mm, "end": v(84.77, -59.77) * mm});
            skLineSegment(sketch, "E5744", {"start": v(84.77, -59.77) * mm, "end": v(84.76, -59.82) * mm});
            skLineSegment(sketch, "E5745", {"start": v(84.76, -59.82) * mm, "end": v(84.76, -59.86) * mm});
            skLineSegment(sketch, "E5746", {"start": v(84.76, -59.86) * mm, "end": v(84.75, -59.9) * mm});
            skLineSegment(sketch, "E5747", {"start": v(84.75, -59.9) * mm, "end": v(84.75, -59.95) * mm});
            skLineSegment(sketch, "E5748", {"start": v(84.75, -59.95) * mm, "end": v(84.74, -59.99) * mm});
            skLineSegment(sketch, "E5749", {"start": v(84.74, -59.99) * mm, "end": v(84.74, -60.03) * mm});
            skLineSegment(sketch, "E5750", {"start": v(84.74, -60.03) * mm, "end": v(84.74, -60.08) * mm});
            skLineSegment(sketch, "E5751", {"start": v(84.74, -60.08) * mm, "end": v(84.74, -60.12) * mm});
            skLineSegment(sketch, "E5752", {"start": v(84.74, -60.12) * mm, "end": v(84.75, -60.16) * mm});
            skLineSegment(sketch, "E5753", {"start": v(84.8, -60.46) * mm, "end": v(84.82, -60.5) * mm});
            skLineSegment(sketch, "E5754", {"start": v(84.82, -60.5) * mm, "end": v(84.84, -60.54) * mm});
            skLineSegment(sketch, "E5755", {"start": v(84.84, -60.54) * mm, "end": v(84.86, -60.58) * mm});
            skLineSegment(sketch, "E5756", {"start": v(84.86, -60.58) * mm, "end": v(84.88, -60.62) * mm});
            skLineSegment(sketch, "E5757", {"start": v(84.88, -60.62) * mm, "end": v(84.9, -60.66) * mm});
            skLineSegment(sketch, "E5758", {"start": v(84.9, -60.66) * mm, "end": v(84.92, -60.7) * mm});
            skLineSegment(sketch, "E5759", {"start": v(84.92, -60.7) * mm, "end": v(84.94, -60.73) * mm});
            skLineSegment(sketch, "E5760", {"start": v(84.94, -60.73) * mm, "end": v(84.96, -60.77) * mm});
            skLineSegment(sketch, "E5761", {"start": v(84.96, -60.77) * mm, "end": v(84.99, -60.8) * mm});
            skLineSegment(sketch, "E5762", {"start": v(84.99, -60.8) * mm, "end": v(85.02, -60.84) * mm});
            skLineSegment(sketch, "E5763", {"start": v(85.02, -60.84) * mm, "end": v(85.04, -60.87) * mm});
            skLineSegment(sketch, "E5764", {"start": v(85.04, -60.87) * mm, "end": v(85.07, -60.9) * mm});
            skLineSegment(sketch, "E5765", {"start": v(85.07, -60.9) * mm, "end": v(85.1, -60.93) * mm});
            skLineSegment(sketch, "E5766", {"start": v(85.1, -60.93) * mm, "end": v(85.13, -60.96) * mm});
            skLineSegment(sketch, "E5767", {"start": v(85.13, -60.96) * mm, "end": v(85.17, -61) * mm});
            skLineSegment(sketch, "E5768", {"start": v(85.17, -61) * mm, "end": v(85.2, -61.02) * mm});
            skLineSegment(sketch, "E5769", {"start": v(85.2, -61.02) * mm, "end": v(85.23, -61.05) * mm});
            skLineSegment(sketch, "E5770", {"start": v(85.23, -61.05) * mm, "end": v(85.27, -61.07) * mm});
            skLineSegment(sketch, "E5771", {"start": v(85.27, -61.07) * mm, "end": v(85.3, -61.1) * mm});
            skLineSegment(sketch, "E5772", {"start": v(85.3, -61.1) * mm, "end": v(85.34, -61.12) * mm});
            skLineSegment(sketch, "E5773", {"start": v(85.34, -61.12) * mm, "end": v(85.38, -61.14) * mm});
            skLineSegment(sketch, "E5774", {"start": v(85.38, -61.14) * mm, "end": v(85.42, -61.16) * mm});
            skLineSegment(sketch, "E5775", {"start": v(85.42, -61.16) * mm, "end": v(85.46, -61.18) * mm});
            skLineSegment(sketch, "E5776", {"start": v(85.46, -61.18) * mm, "end": v(85.5, -61.2) * mm});
            skLineSegment(sketch, "E5777", {"start": v(85.5, -61.2) * mm, "end": v(85.54, -61.22) * mm});
            skLineSegment(sketch, "E5778", {"start": v(85.54, -61.22) * mm, "end": v(85.58, -61.23) * mm});
            skLineSegment(sketch, "E5779", {"start": v(85.58, -61.23) * mm, "end": v(85.62, -61.25) * mm});
            skLineSegment(sketch, "E5780", {"start": v(85.62, -61.25) * mm, "end": v(85.66, -61.26) * mm});
            skLineSegment(sketch, "E5781", {"start": v(85.66, -61.26) * mm, "end": v(85.7, -61.27) * mm});
            skLineSegment(sketch, "E5782", {"start": v(85.7, -61.27) * mm, "end": v(85.74, -61.28) * mm});
            skLineSegment(sketch, "E5783", {"start": v(85.74, -61.28) * mm, "end": v(85.79, -61.29) * mm});
            skLineSegment(sketch, "E5784", {"start": v(85.79, -61.29) * mm, "end": v(85.83, -61.3) * mm});
            skLineSegment(sketch, "E5785", {"start": v(85.83, -61.3) * mm, "end": v(85.87, -61.3) * mm});
            skLineSegment(sketch, "E5786", {"start": v(85.87, -61.3) * mm, "end": v(85.92, -61.3) * mm});
            skLineSegment(sketch, "E5787", {"start": v(85.92, -61.3) * mm, "end": v(85.96, -61.3) * mm});
            skLineSegment(sketch, "E5788", {"start": v(85.96, -61.3) * mm, "end": v(86, -61.3) * mm});
            skLineSegment(sketch, "E5789", {"start": v(86, -61.3) * mm, "end": v(86.05, -61.3) * mm});
            skLineSegment(sketch, "E5790", {"start": v(86.05, -61.3) * mm, "end": v(86.09, -61.3) * mm});
            skLineSegment(sketch, "E5791", {"start": v(86.09, -61.3) * mm, "end": v(86.13, -61.3) * mm});
            skLineSegment(sketch, "E5792", {"start": v(86.13, -61.3) * mm, "end": v(86.17, -61.3) * mm});
            skLineSegment(sketch, "E5793", {"start": v(86.17, -61.3) * mm, "end": v(86.22, -61.28) * mm});
            skLineSegment(sketch, "E5794", {"start": v(86.22, -61.28) * mm, "end": v(86.26, -61.27) * mm});
            skLineSegment(sketch, "E5795", {"start": v(86.26, -61.27) * mm, "end": v(86.3, -61.26) * mm});
            skLineSegment(sketch, "E5796", {"start": v(86.3, -61.26) * mm, "end": v(86.34, -61.25) * mm});
            skLineSegment(sketch, "E5797", {"start": v(86.34, -61.25) * mm, "end": v(86.39, -61.24) * mm});
            skLineSegment(sketch, "E5798", {"start": v(86.39, -61.24) * mm, "end": v(86.43, -61.23) * mm});
            skLineSegment(sketch, "E5799", {"start": v(86.43, -61.23) * mm, "end": v(86.47, -61.2) * mm});
            skLineSegment(sketch, "E5800", {"start": v(86.47, -61.2) * mm, "end": v(86.5, -61.2) * mm});
            skLineSegment(sketch, "E5801", {"start": v(86.5, -61.2) * mm, "end": v(86.55, -61.17) * mm});
            skLineSegment(sketch, "E5802", {"start": v(86.55, -61.17) * mm, "end": v(86.58, -61.15) * mm});
            skLineSegment(sketch, "E5803", {"start": v(86.58, -61.15) * mm, "end": v(86.62, -61.13) * mm});
            skLineSegment(sketch, "E5804", {"start": v(86.62, -61.13) * mm, "end": v(86.66, -61.11) * mm});
            skLineSegment(sketch, "E5805", {"start": v(86.66, -61.11) * mm, "end": v(86.7, -61.09) * mm});
            skLineSegment(sketch, "E5806", {"start": v(86.7, -61.09) * mm, "end": v(86.73, -61.06) * mm});
            skLineSegment(sketch, "E5807", {"start": v(86.73, -61.06) * mm, "end": v(86.77, -61.03) * mm});
            skLineSegment(sketch, "E5808", {"start": v(86.77, -61.03) * mm, "end": v(86.8, -61) * mm});
            skLineSegment(sketch, "E5809", {"start": v(86.8, -61) * mm, "end": v(86.83, -60.98) * mm});
            skLineSegment(sketch, "E5810", {"start": v(86.83, -60.98) * mm, "end": v(86.86, -60.95) * mm});
            skLineSegment(sketch, "E5811", {"start": v(86.86, -60.95) * mm, "end": v(86.9, -60.92) * mm});
            skLineSegment(sketch, "E5812", {"start": v(86.9, -60.92) * mm, "end": v(86.92, -60.89) * mm});
            skLineSegment(sketch, "E5813", {"start": v(86.92, -60.89) * mm, "end": v(86.95, -60.85) * mm});
            skLineSegment(sketch, "E5814", {"start": v(86.95, -60.85) * mm, "end": v(86.98, -60.82) * mm});
            skLineSegment(sketch, "E5815", {"start": v(86.98, -60.82) * mm, "end": v(87, -60.78) * mm});
            skLineSegment(sketch, "E5816", {"start": v(87, -60.78) * mm, "end": v(87.03, -60.75) * mm});
            skLineSegment(sketch, "E5817", {"start": v(87.03, -60.75) * mm, "end": v(87.05, -60.71) * mm});
            skLineSegment(sketch, "E5818", {"start": v(87.05, -60.71) * mm, "end": v(87.08, -60.68) * mm});
            skLineSegment(sketch, "E5819", {"start": v(87.08, -60.68) * mm, "end": v(87.1, -60.64) * mm});
            skLineSegment(sketch, "E5820", {"start": v(87.1, -60.64) * mm, "end": v(87.12, -60.6) * mm});
            skLineSegment(sketch, "E5821", {"start": v(87.12, -60.6) * mm, "end": v(87.13, -60.56) * mm});
            skLineSegment(sketch, "E5822", {"start": v(87.13, -60.56) * mm, "end": v(87.15, -60.52) * mm});
            skLineSegment(sketch, "E5823", {"start": v(87.15, -60.52) * mm, "end": v(87.17, -60.48) * mm});
            skLineSegment(sketch, "E5824", {"start": v(87.18, -60.44) * mm, "end": v(87.2, -60.4) * mm});
            skLineSegment(sketch, "E5825", {"start": v(87.2, -60.4) * mm, "end": v(87.2, -60.35) * mm});
            skLineSegment(sketch, "E5826", {"start": v(87.2, -60.35) * mm, "end": v(87.21, -60.31) * mm});
            skLineSegment(sketch, "E5827", {"start": v(87.21, -60.31) * mm, "end": v(87.22, -60.27) * mm});
            skLineSegment(sketch, "E5828", {"start": v(87.22, -60.27) * mm, "end": v(87.23, -60.23) * mm});
            skLineSegment(sketch, "E5829", {"start": v(87.23, -60.23) * mm, "end": v(87.23, -60.18) * mm});
            skLineSegment(sketch, "E5830", {"start": v(87.24, -60.14) * mm, "end": v(87.24, -60.1) * mm});
            skLineSegment(sketch, "E5831", {"start": v(87.24, -60.1) * mm, "end": v(87.24, -60.05) * mm});
            skLineSegment(sketch, "E5832", {"start": v(-40.26, -60.05) * mm, "end": v(-40.26, -60.01) * mm});
            skLineSegment(sketch, "E5833", {"start": v(-40.26, -60.01) * mm, "end": v(-40.26, -59.97) * mm});
            skLineSegment(sketch, "E5834", {"start": v(-40.26, -59.97) * mm, "end": v(-40.27, -59.92) * mm});
            skLineSegment(sketch, "E5835", {"start": v(-40.27, -59.92) * mm, "end": v(-40.27, -59.88) * mm});
            skLineSegment(sketch, "E5836", {"start": v(-40.27, -59.88) * mm, "end": v(-40.28, -59.84) * mm});
            skLineSegment(sketch, "E5837", {"start": v(-40.28, -59.84) * mm, "end": v(-40.29, -59.8) * mm});
            skLineSegment(sketch, "E5838", {"start": v(-40.29, -59.8) * mm, "end": v(-40.3, -59.75) * mm});
            skLineSegment(sketch, "E5839", {"start": v(-40.3, -59.75) * mm, "end": v(-40.3, -59.71) * mm});
            skLineSegment(sketch, "E5840", {"start": v(-40.3, -59.71) * mm, "end": v(-40.32, -59.67) * mm});
            skLineSegment(sketch, "E5841", {"start": v(-40.32, -59.67) * mm, "end": v(-40.33, -59.63) * mm});
            skLineSegment(sketch, "E5842", {"start": v(-40.33, -59.63) * mm, "end": v(-40.35, -59.59) * mm});
            skLineSegment(sketch, "E5843", {"start": v(-40.35, -59.59) * mm, "end": v(-40.37, -59.55) * mm});
            skLineSegment(sketch, "E5844", {"start": v(-40.37, -59.55) * mm, "end": v(-40.38, -59.5) * mm});
            skLineSegment(sketch, "E5845", {"start": v(-40.38, -59.5) * mm, "end": v(-40.4, -59.47) * mm});
            skLineSegment(sketch, "E5846", {"start": v(-40.4, -59.47) * mm, "end": v(-40.42, -59.43) * mm});
            skLineSegment(sketch, "E5847", {"start": v(-40.42, -59.43) * mm, "end": v(-40.45, -59.4) * mm});
            skLineSegment(sketch, "E5848", {"start": v(-40.45, -59.4) * mm, "end": v(-40.47, -59.36) * mm});
            skLineSegment(sketch, "E5849", {"start": v(-40.47, -59.36) * mm, "end": v(-40.5, -59.32) * mm});
            skLineSegment(sketch, "E5850", {"start": v(-40.5, -59.32) * mm, "end": v(-40.52, -59.29) * mm});
            skLineSegment(sketch, "E5851", {"start": v(-40.52, -59.29) * mm, "end": v(-40.55, -59.25) * mm});
            skLineSegment(sketch, "E5852", {"start": v(-40.55, -59.25) * mm, "end": v(-40.58, -59.22) * mm});
            skLineSegment(sketch, "E5853", {"start": v(-40.58, -59.22) * mm, "end": v(-40.6, -59.19) * mm});
            skLineSegment(sketch, "E5854", {"start": v(-40.6, -59.19) * mm, "end": v(-40.64, -59.16) * mm});
            skLineSegment(sketch, "E5855", {"start": v(-40.64, -59.16) * mm, "end": v(-40.67, -59.13) * mm});
            skLineSegment(sketch, "E5856", {"start": v(-40.67, -59.13) * mm, "end": v(-40.7, -59.1) * mm});
            skLineSegment(sketch, "E5857", {"start": v(-40.7, -59.1) * mm, "end": v(-40.73, -59.07) * mm});
            skLineSegment(sketch, "E5858", {"start": v(-40.73, -59.07) * mm, "end": v(-40.77, -59.05) * mm});
            skLineSegment(sketch, "E5859", {"start": v(-40.77, -59.05) * mm, "end": v(-40.8, -59.02) * mm});
            skLineSegment(sketch, "E5860", {"start": v(-40.8, -59.02) * mm, "end": v(-40.84, -59) * mm});
            skLineSegment(sketch, "E5861", {"start": v(-40.84, -59) * mm, "end": v(-40.88, -58.97) * mm});
            skLineSegment(sketch, "E5862", {"start": v(-40.88, -58.97) * mm, "end": v(-40.92, -58.95) * mm});
            skLineSegment(sketch, "E5863", {"start": v(-40.92, -58.95) * mm, "end": v(-40.95, -58.93) * mm});
            skLineSegment(sketch, "E5864", {"start": v(-40.95, -58.93) * mm, "end": v(-41, -58.92) * mm});
            skLineSegment(sketch, "E5865", {"start": v(-41, -58.92) * mm, "end": v(-41.03, -58.9) * mm});
            skLineSegment(sketch, "E5866", {"start": v(-41.03, -58.9) * mm, "end": v(-41.07, -58.88) * mm});
            skLineSegment(sketch, "E5867", {"start": v(-41.07, -58.88) * mm, "end": v(-41.11, -58.87) * mm});
            skLineSegment(sketch, "E5868", {"start": v(-41.11, -58.87) * mm, "end": v(-41.16, -58.85) * mm});
            skLineSegment(sketch, "E5869", {"start": v(-41.16, -58.85) * mm, "end": v(-41.2, -58.84) * mm});
            skLineSegment(sketch, "E5870", {"start": v(-41.2, -58.84) * mm, "end": v(-41.24, -58.83) * mm});
            skLineSegment(sketch, "E5871", {"start": v(-41.24, -58.83) * mm, "end": v(-41.28, -58.82) * mm});
            skLineSegment(sketch, "E5872", {"start": v(-41.28, -58.82) * mm, "end": v(-41.33, -58.82) * mm});
            skLineSegment(sketch, "E5873", {"start": v(-41.33, -58.82) * mm, "end": v(-41.37, -58.81) * mm});
            skLineSegment(sketch, "E5874", {"start": v(-41.37, -58.81) * mm, "end": v(-41.41, -58.8) * mm});
            skLineSegment(sketch, "E5875", {"start": v(-41.41, -58.8) * mm, "end": v(-41.45, -58.8) * mm});
            skLineSegment(sketch, "E5876", {"start": v(-41.45, -58.8) * mm, "end": v(-41.5, -58.8) * mm});
            skLineSegment(sketch, "E5877", {"start": v(-41.5, -58.8) * mm, "end": v(-41.54, -58.8) * mm});
            skLineSegment(sketch, "E5878", {"start": v(-41.54, -58.8) * mm, "end": v(-41.58, -58.8) * mm});
            skLineSegment(sketch, "E5879", {"start": v(-41.58, -58.8) * mm, "end": v(-41.63, -58.8) * mm});
            skLineSegment(sketch, "E5880", {"start": v(-41.63, -58.8) * mm, "end": v(-41.67, -58.81) * mm});
            skLineSegment(sketch, "E5881", {"start": v(-41.67, -58.81) * mm, "end": v(-41.71, -58.82) * mm});
            skLineSegment(sketch, "E5882", {"start": v(-41.71, -58.82) * mm, "end": v(-41.76, -58.83) * mm});
            skLineSegment(sketch, "E5883", {"start": v(-41.76, -58.83) * mm, "end": v(-41.8, -58.84) * mm});
            skLineSegment(sketch, "E5884", {"start": v(-41.8, -58.84) * mm, "end": v(-41.84, -58.85) * mm});
            skLineSegment(sketch, "E5885", {"start": v(-41.84, -58.85) * mm, "end": v(-41.88, -58.86) * mm});
            skLineSegment(sketch, "E5886", {"start": v(-41.88, -58.86) * mm, "end": v(-41.92, -58.87) * mm});
            skLineSegment(sketch, "E5887", {"start": v(-41.92, -58.87) * mm, "end": v(-41.96, -58.89) * mm});
            skLineSegment(sketch, "E5888", {"start": v(-41.96, -58.89) * mm, "end": v(-42, -58.9) * mm});
            skLineSegment(sketch, "E5889", {"start": v(-42, -58.9) * mm, "end": v(-42.04, -58.92) * mm});
            skLineSegment(sketch, "E5890", {"start": v(-42.04, -58.92) * mm, "end": v(-42.08, -58.94) * mm});
            skLineSegment(sketch, "E5891", {"start": v(-42.08, -58.94) * mm, "end": v(-42.12, -58.96) * mm});
            skLineSegment(sketch, "E5892", {"start": v(-42.12, -58.96) * mm, "end": v(-42.16, -58.99) * mm});
            skLineSegment(sketch, "E5893", {"start": v(-42.16, -58.99) * mm, "end": v(-42.2, -59) * mm});
            skLineSegment(sketch, "E5894", {"start": v(-42.2, -59) * mm, "end": v(-42.23, -59.03) * mm});
            skLineSegment(sketch, "E5895", {"start": v(-42.23, -59.03) * mm, "end": v(-42.27, -59.06) * mm});
            skLineSegment(sketch, "E5896", {"start": v(-42.27, -59.06) * mm, "end": v(-42.3, -59.09) * mm});
            skLineSegment(sketch, "E5897", {"start": v(-42.3, -59.09) * mm, "end": v(-42.33, -59.11) * mm});
            skLineSegment(sketch, "E5898", {"start": v(-42.33, -59.11) * mm, "end": v(-42.37, -59.14) * mm});
            skLineSegment(sketch, "E5899", {"start": v(-42.37, -59.14) * mm, "end": v(-42.4, -59.17) * mm});
            skLineSegment(sketch, "E5900", {"start": v(-42.4, -59.17) * mm, "end": v(-42.43, -59.2) * mm});
            skLineSegment(sketch, "E5901", {"start": v(-42.43, -59.2) * mm, "end": v(-42.46, -59.24) * mm});
            skLineSegment(sketch, "E5902", {"start": v(-42.46, -59.24) * mm, "end": v(-42.48, -59.27) * mm});
            skLineSegment(sketch, "E5903", {"start": v(-42.48, -59.27) * mm, "end": v(-42.51, -59.3) * mm});
            skLineSegment(sketch, "E5904", {"start": v(-42.51, -59.3) * mm, "end": v(-42.54, -59.34) * mm});
            skLineSegment(sketch, "E5905", {"start": v(-42.54, -59.34) * mm, "end": v(-42.56, -59.38) * mm});
            skLineSegment(sketch, "E5906", {"start": v(-42.56, -59.38) * mm, "end": v(-42.58, -59.41) * mm});
            skLineSegment(sketch, "E5907", {"start": v(-42.58, -59.41) * mm, "end": v(-42.6, -59.45) * mm});
            skLineSegment(sketch, "E5908", {"start": v(-42.6, -59.45) * mm, "end": v(-42.62, -59.49) * mm});
            skLineSegment(sketch, "E5909", {"start": v(-42.62, -59.49) * mm, "end": v(-42.64, -59.53) * mm});
            skLineSegment(sketch, "E5910", {"start": v(-42.64, -59.53) * mm, "end": v(-42.66, -59.57) * mm});
            skLineSegment(sketch, "E5911", {"start": v(-42.66, -59.57) * mm, "end": v(-42.68, -59.6) * mm});
            skLineSegment(sketch, "E5912", {"start": v(-42.68, -59.6) * mm, "end": v(-42.7, -59.65) * mm});
            skLineSegment(sketch, "E5913", {"start": v(-42.7, -59.65) * mm, "end": v(-42.7, -59.7) * mm});
            skLineSegment(sketch, "E5914", {"start": v(-42.7, -59.7) * mm, "end": v(-42.72, -59.73) * mm});
            skLineSegment(sketch, "E5915", {"start": v(-42.72, -59.73) * mm, "end": v(-42.73, -59.77) * mm});
            skLineSegment(sketch, "E5916", {"start": v(-42.73, -59.77) * mm, "end": v(-42.74, -59.82) * mm});
            skLineSegment(sketch, "E5917", {"start": v(-42.74, -59.82) * mm, "end": v(-42.74, -59.86) * mm});
            skLineSegment(sketch, "E5918", {"start": v(-42.74, -59.86) * mm, "end": v(-42.75, -59.9) * mm});
            skLineSegment(sketch, "E5919", {"start": v(-42.75, -59.9) * mm, "end": v(-42.75, -59.95) * mm});
            skLineSegment(sketch, "E5920", {"start": v(-42.75, -59.95) * mm, "end": v(-42.76, -59.99) * mm});
            skLineSegment(sketch, "E5921", {"start": v(-42.76, -59.99) * mm, "end": v(-42.76, -60.03) * mm});
            skLineSegment(sketch, "E5922", {"start": v(-42.76, -60.03) * mm, "end": v(-42.76, -60.08) * mm});
            skLineSegment(sketch, "E5923", {"start": v(-42.76, -60.08) * mm, "end": v(-42.76, -60.12) * mm});
            skLineSegment(sketch, "E5924", {"start": v(-42.76, -60.12) * mm, "end": v(-42.75, -60.16) * mm});
            skLineSegment(sketch, "E5925", {"start": v(-42.75, -60.16) * mm, "end": v(-42.75, -60.2) * mm});
            skLineSegment(sketch, "E5926", {"start": v(-42.75, -60.2) * mm, "end": v(-42.74, -60.25) * mm});
            skLineSegment(sketch, "E5927", {"start": v(-42.74, -60.25) * mm, "end": v(-42.74, -60.3) * mm});
            skLineSegment(sketch, "E5928", {"start": v(-42.74, -60.3) * mm, "end": v(-42.73, -60.33) * mm});
            skLineSegment(sketch, "E5929", {"start": v(-42.72, -60.38) * mm, "end": v(-42.7, -60.42) * mm});
            skLineSegment(sketch, "E5930", {"start": v(-42.7, -60.42) * mm, "end": v(-42.7, -60.46) * mm});
            skLineSegment(sketch, "E5931", {"start": v(-42.7, -60.46) * mm, "end": v(-42.68, -60.5) * mm});
            skLineSegment(sketch, "E5932", {"start": v(-42.68, -60.5) * mm, "end": v(-42.66, -60.54) * mm});
            skLineSegment(sketch, "E5933", {"start": v(-42.66, -60.54) * mm, "end": v(-42.64, -60.58) * mm});
            skLineSegment(sketch, "E5934", {"start": v(-42.64, -60.58) * mm, "end": v(-42.62, -60.62) * mm});
            skLineSegment(sketch, "E5935", {"start": v(-42.62, -60.62) * mm, "end": v(-42.6, -60.66) * mm});
            skLineSegment(sketch, "E5936", {"start": v(-42.6, -60.66) * mm, "end": v(-42.58, -60.7) * mm});
            skLineSegment(sketch, "E5937", {"start": v(-42.58, -60.7) * mm, "end": v(-42.56, -60.73) * mm});
            skLineSegment(sketch, "E5938", {"start": v(-42.56, -60.73) * mm, "end": v(-42.54, -60.77) * mm});
            skLineSegment(sketch, "E5939", {"start": v(-42.54, -60.77) * mm, "end": v(-42.51, -60.8) * mm});
            skLineSegment(sketch, "E5940", {"start": v(-42.51, -60.8) * mm, "end": v(-42.48, -60.84) * mm});
            skLineSegment(sketch, "E5941", {"start": v(-42.48, -60.84) * mm, "end": v(-42.46, -60.87) * mm});
            skLineSegment(sketch, "E5942", {"start": v(-42.46, -60.87) * mm, "end": v(-42.43, -60.9) * mm});
            skLineSegment(sketch, "E5943", {"start": v(-42.43, -60.9) * mm, "end": v(-42.4, -60.93) * mm});
            skLineSegment(sketch, "E5944", {"start": v(-42.4, -60.93) * mm, "end": v(-42.37, -60.96) * mm});
            skLineSegment(sketch, "E5945", {"start": v(-42.37, -60.96) * mm, "end": v(-42.33, -61) * mm});
            skLineSegment(sketch, "E5946", {"start": v(-42.33, -61) * mm, "end": v(-42.3, -61.02) * mm});
            skLineSegment(sketch, "E5947", {"start": v(-42.3, -61.02) * mm, "end": v(-42.27, -61.05) * mm});
            skLineSegment(sketch, "E5948", {"start": v(-42.27, -61.05) * mm, "end": v(-42.23, -61.07) * mm});
            skLineSegment(sketch, "E5949", {"start": v(-42.23, -61.07) * mm, "end": v(-42.2, -61.1) * mm});
            skLineSegment(sketch, "E5950", {"start": v(-42.2, -61.1) * mm, "end": v(-42.16, -61.12) * mm});
            skLineSegment(sketch, "E5951", {"start": v(-42.16, -61.12) * mm, "end": v(-42.12, -61.14) * mm});
            skLineSegment(sketch, "E5952", {"start": v(-42.12, -61.14) * mm, "end": v(-42.08, -61.16) * mm});
            skLineSegment(sketch, "E5953", {"start": v(-42.08, -61.16) * mm, "end": v(-42.04, -61.18) * mm});
            skLineSegment(sketch, "E5954", {"start": v(-42.04, -61.18) * mm, "end": v(-42, -61.2) * mm});
            skLineSegment(sketch, "E5955", {"start": v(-42, -61.2) * mm, "end": v(-41.96, -61.22) * mm});
            skLineSegment(sketch, "E5956", {"start": v(-41.96, -61.22) * mm, "end": v(-41.92, -61.23) * mm});
            skLineSegment(sketch, "E5957", {"start": v(-41.92, -61.23) * mm, "end": v(-41.88, -61.25) * mm});
            skLineSegment(sketch, "E5958", {"start": v(-41.88, -61.25) * mm, "end": v(-41.84, -61.26) * mm});
            skLineSegment(sketch, "E5959", {"start": v(-41.84, -61.26) * mm, "end": v(-41.8, -61.27) * mm});
            skLineSegment(sketch, "E5960", {"start": v(-41.8, -61.27) * mm, "end": v(-41.76, -61.28) * mm});
            skLineSegment(sketch, "E5961", {"start": v(-41.76, -61.28) * mm, "end": v(-41.71, -61.29) * mm});
            skLineSegment(sketch, "E5962", {"start": v(-41.71, -61.29) * mm, "end": v(-41.67, -61.3) * mm});
            skLineSegment(sketch, "E5963", {"start": v(-41.67, -61.3) * mm, "end": v(-41.63, -61.3) * mm});
            skLineSegment(sketch, "E5964", {"start": v(-41.63, -61.3) * mm, "end": v(-41.58, -61.3) * mm});
            skLineSegment(sketch, "E5965", {"start": v(-41.58, -61.3) * mm, "end": v(-41.54, -61.3) * mm});
            skLineSegment(sketch, "E5966", {"start": v(-41.54, -61.3) * mm, "end": v(-41.5, -61.3) * mm});
            skLineSegment(sketch, "E5967", {"start": v(-41.5, -61.3) * mm, "end": v(-41.45, -61.3) * mm});
            skLineSegment(sketch, "E5968", {"start": v(-41.45, -61.3) * mm, "end": v(-41.41, -61.3) * mm});
            skLineSegment(sketch, "E5969", {"start": v(-41.41, -61.3) * mm, "end": v(-41.37, -61.3) * mm});
            skLineSegment(sketch, "E5970", {"start": v(-41.37, -61.3) * mm, "end": v(-41.33, -61.3) * mm});
            skLineSegment(sketch, "E5971", {"start": v(-41.33, -61.3) * mm, "end": v(-41.28, -61.28) * mm});
            skLineSegment(sketch, "E5972", {"start": v(-41.28, -61.28) * mm, "end": v(-41.24, -61.27) * mm});
            skLineSegment(sketch, "E5973", {"start": v(-41.24, -61.27) * mm, "end": v(-41.2, -61.26) * mm});
            skLineSegment(sketch, "E5974", {"start": v(-41.2, -61.26) * mm, "end": v(-41.16, -61.25) * mm});
            skLineSegment(sketch, "E5975", {"start": v(-41.16, -61.25) * mm, "end": v(-41.11, -61.24) * mm});
            skLineSegment(sketch, "E5976", {"start": v(-41.11, -61.24) * mm, "end": v(-41.07, -61.23) * mm});
            skLineSegment(sketch, "E5977", {"start": v(-41.07, -61.23) * mm, "end": v(-41.03, -61.2) * mm});
            skLineSegment(sketch, "E5978", {"start": v(-41.03, -61.2) * mm, "end": v(-41, -61.2) * mm});
            skLineSegment(sketch, "E5979", {"start": v(-41, -61.2) * mm, "end": v(-40.95, -61.17) * mm});
            skLineSegment(sketch, "E5980", {"start": v(-40.95, -61.17) * mm, "end": v(-40.92, -61.15) * mm});
            skLineSegment(sketch, "E5981", {"start": v(-40.92, -61.15) * mm, "end": v(-40.88, -61.13) * mm});
            skLineSegment(sketch, "E5982", {"start": v(-40.88, -61.13) * mm, "end": v(-40.84, -61.11) * mm});
            skLineSegment(sketch, "E5983", {"start": v(-40.84, -61.11) * mm, "end": v(-40.8, -61.09) * mm});
            skLineSegment(sketch, "E5984", {"start": v(-40.8, -61.09) * mm, "end": v(-40.77, -61.06) * mm});
            skLineSegment(sketch, "E5985", {"start": v(-40.77, -61.06) * mm, "end": v(-40.73, -61.03) * mm});
            skLineSegment(sketch, "E5986", {"start": v(-40.73, -61.03) * mm, "end": v(-40.7, -61) * mm});
            skLineSegment(sketch, "E5987", {"start": v(-40.7, -61) * mm, "end": v(-40.67, -60.98) * mm});
            skLineSegment(sketch, "E5988", {"start": v(-40.67, -60.98) * mm, "end": v(-40.64, -60.95) * mm});
            skLineSegment(sketch, "E5989", {"start": v(-40.64, -60.95) * mm, "end": v(-40.6, -60.92) * mm});
            skLineSegment(sketch, "E5990", {"start": v(-40.6, -60.92) * mm, "end": v(-40.58, -60.89) * mm});
            skLineSegment(sketch, "E5991", {"start": v(-40.58, -60.89) * mm, "end": v(-40.55, -60.85) * mm});
            skLineSegment(sketch, "E5992", {"start": v(-40.55, -60.85) * mm, "end": v(-40.52, -60.82) * mm});
            skLineSegment(sketch, "E5993", {"start": v(-40.52, -60.82) * mm, "end": v(-40.5, -60.78) * mm});
            skLineSegment(sketch, "E5994", {"start": v(-40.5, -60.78) * mm, "end": v(-40.47, -60.75) * mm});
            skLineSegment(sketch, "E5995", {"start": v(-40.47, -60.75) * mm, "end": v(-40.45, -60.71) * mm});
            skLineSegment(sketch, "E5996", {"start": v(-40.45, -60.71) * mm, "end": v(-40.42, -60.68) * mm});
            skLineSegment(sketch, "E5997", {"start": v(-40.42, -60.68) * mm, "end": v(-40.4, -60.64) * mm});
            skLineSegment(sketch, "E5998", {"start": v(-40.4, -60.64) * mm, "end": v(-40.38, -60.6) * mm});
            skLineSegment(sketch, "E5999", {"start": v(-40.38, -60.6) * mm, "end": v(-40.37, -60.56) * mm});
            skLineSegment(sketch, "E6000", {"start": v(-40.37, -60.56) * mm, "end": v(-40.35, -60.52) * mm});
            skLineSegment(sketch, "E6001", {"start": v(-40.35, -60.52) * mm, "end": v(-40.33, -60.48) * mm});
            skLineSegment(sketch, "E6002", {"start": v(-40.33, -60.48) * mm, "end": v(-40.32, -60.44) * mm});
            skLineSegment(sketch, "E6003", {"start": v(-40.32, -60.44) * mm, "end": v(-40.3, -60.4) * mm});
            skLineSegment(sketch, "E6004", {"start": v(-40.29, -60.31) * mm, "end": v(-40.28, -60.27) * mm});
            skLineSegment(sketch, "E6005", {"start": v(-40.28, -60.27) * mm, "end": v(-40.27, -60.23) * mm});
            skLineSegment(sketch, "E6006", {"start": v(-40.27, -60.23) * mm, "end": v(-40.27, -60.18) * mm});
            skLineSegment(sketch, "E6007", {"start": v(-40.26, -60.14) * mm, "end": v(-40.26, -60.1) * mm});
            skLineSegment(sketch, "E6008", {"start": v(-40.26, -60.1) * mm, "end": v(-40.26, -60.05) * mm});
            skLineSegment(sketch, "E6009", {"start": v(-292.1, -59.86) * mm, "end": v(-157.1, -59.86) * mm});
            skLineSegment(sketch, "E6010", {"start": v(-157.1, -59.86) * mm, "end": v(-157.1, -44.86) * mm});
            skLineSegment(sketch, "E6011", {"start": v(-157.1, -44.86) * mm, "end": v(-292.1, -44.86) * mm});
            skLineSegment(sketch, "E6012", {"start": v(-292.1, -44.86) * mm, "end": v(-292.1, -59.86) * mm});
            skLineSegment(sketch, "E6013", {"start": v(-292.7, -40.98) * mm, "end": v(-157.7, -40.98) * mm});
            skLineSegment(sketch, "E6014", {"start": v(-157.7, -40.98) * mm, "end": v(-157.7, -25.98) * mm});
            skLineSegment(sketch, "E6015", {"start": v(-157.7, -25.98) * mm, "end": v(-292.7, -25.98) * mm});
            skLineSegment(sketch, "E6016", {"start": v(-292.7, -25.98) * mm, "end": v(-292.7, -40.98) * mm});
            skLineSegment(sketch, "E6017", {"start": v(-40.86, -41.18) * mm, "end": v(-40.86, -41.13) * mm});
            skLineSegment(sketch, "E6018", {"start": v(-40.86, -41.13) * mm, "end": v(-40.87, -41.09) * mm});
            skLineSegment(sketch, "E6019", {"start": v(-40.87, -41.09) * mm, "end": v(-40.87, -41.05) * mm});
            skLineSegment(sketch, "E6020", {"start": v(-40.87, -41.05) * mm, "end": v(-40.87, -41) * mm});
            skLineSegment(sketch, "E6021", {"start": v(-40.87, -41) * mm, "end": v(-40.88, -40.96) * mm});
            skLineSegment(sketch, "E6022", {"start": v(-40.88, -40.96) * mm, "end": v(-40.89, -40.92) * mm});
            skLineSegment(sketch, "E6023", {"start": v(-40.89, -40.92) * mm, "end": v(-40.9, -40.88) * mm});
            skLineSegment(sketch, "E6024", {"start": v(-40.9, -40.88) * mm, "end": v(-40.91, -40.83) * mm});
            skLineSegment(sketch, "E6025", {"start": v(-40.91, -40.83) * mm, "end": v(-40.92, -40.8) * mm});
            skLineSegment(sketch, "E6026", {"start": v(-40.92, -40.8) * mm, "end": v(-40.94, -40.75) * mm});
            skLineSegment(sketch, "E6027", {"start": v(-40.94, -40.75) * mm, "end": v(-40.95, -40.71) * mm});
            skLineSegment(sketch, "E6028", {"start": v(-40.95, -40.71) * mm, "end": v(-40.97, -40.67) * mm});
            skLineSegment(sketch, "E6029", {"start": v(-40.97, -40.67) * mm, "end": v(-40.99, -40.63) * mm});
            skLineSegment(sketch, "E6030", {"start": v(-40.99, -40.63) * mm, "end": v(-41, -40.6) * mm});
            skLineSegment(sketch, "E6031", {"start": v(-41, -40.6) * mm, "end": v(-41.03, -40.55) * mm});
            skLineSegment(sketch, "E6032", {"start": v(-41.03, -40.55) * mm, "end": v(-41.05, -40.52) * mm});
            skLineSegment(sketch, "E6033", {"start": v(-41.05, -40.52) * mm, "end": v(-41.07, -40.48) * mm});
            skLineSegment(sketch, "E6034", {"start": v(-41.07, -40.48) * mm, "end": v(-41.1, -40.45) * mm});
            skLineSegment(sketch, "E6035", {"start": v(-41.1, -40.45) * mm, "end": v(-41.13, -40.41) * mm});
            skLineSegment(sketch, "E6036", {"start": v(-41.15, -40.38) * mm, "end": v(-41.18, -40.34) * mm});
            skLineSegment(sketch, "E6037", {"start": v(-41.18, -40.34) * mm, "end": v(-41.21, -40.31) * mm});
            skLineSegment(sketch, "E6038", {"start": v(-41.21, -40.31) * mm, "end": v(-41.24, -40.28) * mm});
            skLineSegment(sketch, "E6039", {"start": v(-41.24, -40.28) * mm, "end": v(-41.27, -40.25) * mm});
            skLineSegment(sketch, "E6040", {"start": v(-41.27, -40.25) * mm, "end": v(-41.3, -40.22) * mm});
            skLineSegment(sketch, "E6041", {"start": v(-41.3, -40.22) * mm, "end": v(-41.34, -40.2) * mm});
            skLineSegment(sketch, "E6042", {"start": v(-41.34, -40.2) * mm, "end": v(-41.37, -40.17) * mm});
            skLineSegment(sketch, "E6043", {"start": v(-41.37, -40.17) * mm, "end": v(-41.4, -40.14) * mm});
            skLineSegment(sketch, "E6044", {"start": v(-41.4, -40.14) * mm, "end": v(-41.44, -40.12) * mm});
            skLineSegment(sketch, "E6045", {"start": v(-41.44, -40.12) * mm, "end": v(-41.48, -40.1) * mm});
            skLineSegment(sketch, "E6046", {"start": v(-41.48, -40.1) * mm, "end": v(-41.52, -40.08) * mm});
            skLineSegment(sketch, "E6047", {"start": v(-41.52, -40.08) * mm, "end": v(-41.56, -40.06) * mm});
            skLineSegment(sketch, "E6048", {"start": v(-41.56, -40.06) * mm, "end": v(-41.6, -40.04) * mm});
            skLineSegment(sketch, "E6049", {"start": v(-41.6, -40.04) * mm, "end": v(-41.64, -40.02) * mm});
            skLineSegment(sketch, "E6050", {"start": v(-41.64, -40.02) * mm, "end": v(-41.68, -40) * mm});
            skLineSegment(sketch, "E6051", {"start": v(-41.68, -40) * mm, "end": v(-41.72, -40) * mm});
            skLineSegment(sketch, "E6052", {"start": v(-41.72, -40) * mm, "end": v(-41.76, -39.98) * mm});
            skLineSegment(sketch, "E6053", {"start": v(-41.76, -39.98) * mm, "end": v(-41.8, -39.97) * mm});
            skLineSegment(sketch, "E6054", {"start": v(-41.8, -39.97) * mm, "end": v(-41.84, -39.96) * mm});
            skLineSegment(sketch, "E6055", {"start": v(-41.84, -39.96) * mm, "end": v(-41.89, -39.95) * mm});
            skLineSegment(sketch, "E6056", {"start": v(-41.89, -39.95) * mm, "end": v(-41.93, -39.94) * mm});
            skLineSegment(sketch, "E6057", {"start": v(-41.93, -39.94) * mm, "end": v(-41.97, -39.93) * mm});
            skLineSegment(sketch, "E6058", {"start": v(-41.97, -39.93) * mm, "end": v(-42.02, -39.93) * mm});
            skLineSegment(sketch, "E6059", {"start": v(-42.02, -39.93) * mm, "end": v(-42.06, -39.93) * mm});
            skLineSegment(sketch, "E6060", {"start": v(-42.06, -39.93) * mm, "end": v(-42.1, -39.93) * mm});
            skLineSegment(sketch, "E6061", {"start": v(-42.1, -39.93) * mm, "end": v(-42.15, -39.93) * mm});
            skLineSegment(sketch, "E6062", {"start": v(-42.15, -39.93) * mm, "end": v(-42.19, -39.93) * mm});
            skLineSegment(sketch, "E6063", {"start": v(-42.19, -39.93) * mm, "end": v(-42.23, -39.93) * mm});
            skLineSegment(sketch, "E6064", {"start": v(-42.23, -39.93) * mm, "end": v(-42.28, -39.94) * mm});
            skLineSegment(sketch, "E6065", {"start": v(-42.28, -39.94) * mm, "end": v(-42.32, -39.94) * mm});
            skLineSegment(sketch, "E6066", {"start": v(-42.32, -39.94) * mm, "end": v(-42.36, -39.95) * mm});
            skLineSegment(sketch, "E6067", {"start": v(-42.49, -39.98) * mm, "end": v(-42.53, -40) * mm});
            skLineSegment(sketch, "E6068", {"start": v(-42.53, -40) * mm, "end": v(-42.57, -40.01) * mm});
            skLineSegment(sketch, "E6069", {"start": v(-42.57, -40.01) * mm, "end": v(-42.6, -40.03) * mm});
            skLineSegment(sketch, "E6070", {"start": v(-42.6, -40.03) * mm, "end": v(-42.65, -40.05) * mm});
            skLineSegment(sketch, "E6071", {"start": v(-42.65, -40.05) * mm, "end": v(-42.69, -40.07) * mm});
            skLineSegment(sketch, "E6072", {"start": v(-42.69, -40.07) * mm, "end": v(-42.73, -40.09) * mm});
            skLineSegment(sketch, "E6073", {"start": v(-42.73, -40.09) * mm, "end": v(-42.76, -40.1) * mm});
            skLineSegment(sketch, "E6074", {"start": v(-42.76, -40.1) * mm, "end": v(-42.8, -40.13) * mm});
            skLineSegment(sketch, "E6075", {"start": v(-42.8, -40.13) * mm, "end": v(-42.84, -40.16) * mm});
            skLineSegment(sketch, "E6076", {"start": v(-42.84, -40.16) * mm, "end": v(-42.87, -40.18) * mm});
            skLineSegment(sketch, "E6077", {"start": v(-42.87, -40.18) * mm, "end": v(-42.9, -40.2) * mm});
            skLineSegment(sketch, "E6078", {"start": v(-42.9, -40.2) * mm, "end": v(-42.94, -40.24) * mm});
            skLineSegment(sketch, "E6079", {"start": v(-42.94, -40.24) * mm, "end": v(-42.97, -40.27) * mm});
            skLineSegment(sketch, "E6080", {"start": v(-42.97, -40.27) * mm, "end": v(-43, -40.3) * mm});
            skLineSegment(sketch, "E6081", {"start": v(-43, -40.3) * mm, "end": v(-43.03, -40.33) * mm});
            skLineSegment(sketch, "E6082", {"start": v(-43.03, -40.33) * mm, "end": v(-43.06, -40.36) * mm});
            skLineSegment(sketch, "E6083", {"start": v(-43.06, -40.36) * mm, "end": v(-43.09, -40.4) * mm});
            skLineSegment(sketch, "E6084", {"start": v(-43.09, -40.4) * mm, "end": v(-43.11, -40.43) * mm});
            skLineSegment(sketch, "E6085", {"start": v(-43.11, -40.43) * mm, "end": v(-43.14, -40.46) * mm});
            skLineSegment(sketch, "E6086", {"start": v(-43.14, -40.46) * mm, "end": v(-43.16, -40.5) * mm});
            skLineSegment(sketch, "E6087", {"start": v(-43.16, -40.5) * mm, "end": v(-43.19, -40.54) * mm});
            skLineSegment(sketch, "E6088", {"start": v(-43.19, -40.54) * mm, "end": v(-43.2, -40.57) * mm});
            skLineSegment(sketch, "E6089", {"start": v(-43.2, -40.57) * mm, "end": v(-43.23, -40.61) * mm});
            skLineSegment(sketch, "E6090", {"start": v(-43.23, -40.61) * mm, "end": v(-43.25, -40.65) * mm});
            skLineSegment(sketch, "E6091", {"start": v(-43.25, -40.65) * mm, "end": v(-43.26, -40.7) * mm});
            skLineSegment(sketch, "E6092", {"start": v(-43.26, -40.7) * mm, "end": v(-43.28, -40.73) * mm});
            skLineSegment(sketch, "E6093", {"start": v(-43.28, -40.73) * mm, "end": v(-43.3, -40.77) * mm});
            skLineSegment(sketch, "E6094", {"start": v(-43.3, -40.77) * mm, "end": v(-43.3, -40.81) * mm});
            skLineSegment(sketch, "E6095", {"start": v(-43.3, -40.81) * mm, "end": v(-43.32, -40.85) * mm});
            skLineSegment(sketch, "E6096", {"start": v(-43.32, -40.85) * mm, "end": v(-43.33, -40.9) * mm});
            skLineSegment(sketch, "E6097", {"start": v(-43.33, -40.9) * mm, "end": v(-43.34, -40.94) * mm});
            skLineSegment(sketch, "E6098", {"start": v(-43.34, -40.94) * mm, "end": v(-43.35, -40.98) * mm});
            skLineSegment(sketch, "E6099", {"start": v(-43.35, -40.98) * mm, "end": v(-43.35, -41.03) * mm});
            skLineSegment(sketch, "E6100", {"start": v(-43.35, -41.03) * mm, "end": v(-43.36, -41.07) * mm});
            skLineSegment(sketch, "E6101", {"start": v(-43.36, -41.07) * mm, "end": v(-43.36, -41.11) * mm});
            skLineSegment(sketch, "E6102", {"start": v(-43.36, -41.11) * mm, "end": v(-43.36, -41.15) * mm});
            skLineSegment(sketch, "E6103", {"start": v(-43.36, -41.15) * mm, "end": v(-43.36, -41.2) * mm});
            skLineSegment(sketch, "E6104", {"start": v(-43.36, -41.2) * mm, "end": v(-43.36, -41.24) * mm});
            skLineSegment(sketch, "E6105", {"start": v(-43.36, -41.24) * mm, "end": v(-43.36, -41.29) * mm});
            skLineSegment(sketch, "E6106", {"start": v(-43.36, -41.29) * mm, "end": v(-43.35, -41.33) * mm});
            skLineSegment(sketch, "E6107", {"start": v(-43.35, -41.33) * mm, "end": v(-43.35, -41.37) * mm});
            skLineSegment(sketch, "E6108", {"start": v(-43.35, -41.37) * mm, "end": v(-43.34, -41.41) * mm});
            skLineSegment(sketch, "E6109", {"start": v(-43.34, -41.41) * mm, "end": v(-43.33, -41.46) * mm});
            skLineSegment(sketch, "E6110", {"start": v(-43.33, -41.46) * mm, "end": v(-43.32, -41.5) * mm});
            skLineSegment(sketch, "E6111", {"start": v(-43.3, -41.54) * mm, "end": v(-43.3, -41.58) * mm});
            skLineSegment(sketch, "E6112", {"start": v(-43.3, -41.58) * mm, "end": v(-43.28, -41.62) * mm});
            skLineSegment(sketch, "E6113", {"start": v(-43.28, -41.62) * mm, "end": v(-43.26, -41.66) * mm});
            skLineSegment(sketch, "E6114", {"start": v(-43.26, -41.66) * mm, "end": v(-43.25, -41.7) * mm});
            skLineSegment(sketch, "E6115", {"start": v(-43.25, -41.7) * mm, "end": v(-43.23, -41.74) * mm});
            skLineSegment(sketch, "E6116", {"start": v(-43.23, -41.74) * mm, "end": v(-43.2, -41.78) * mm});
            skLineSegment(sketch, "E6117", {"start": v(-43.2, -41.78) * mm, "end": v(-43.19, -41.82) * mm});
            skLineSegment(sketch, "E6118", {"start": v(-43.19, -41.82) * mm, "end": v(-43.16, -41.85) * mm});
            skLineSegment(sketch, "E6119", {"start": v(-43.16, -41.85) * mm, "end": v(-43.14, -41.9) * mm});
            skLineSegment(sketch, "E6120", {"start": v(-43.14, -41.9) * mm, "end": v(-43.11, -41.93) * mm});
            skLineSegment(sketch, "E6121", {"start": v(-43.11, -41.93) * mm, "end": v(-43.09, -41.96) * mm});
            skLineSegment(sketch, "E6122", {"start": v(-43.09, -41.96) * mm, "end": v(-43.06, -42) * mm});
            skLineSegment(sketch, "E6123", {"start": v(-43.06, -42) * mm, "end": v(-43.03, -42.03) * mm});
            skLineSegment(sketch, "E6124", {"start": v(-43.03, -42.03) * mm, "end": v(-43, -42.06) * mm});
            skLineSegment(sketch, "E6125", {"start": v(-43, -42.06) * mm, "end": v(-42.97, -42.09) * mm});
            skLineSegment(sketch, "E6126", {"start": v(-42.97, -42.09) * mm, "end": v(-42.94, -42.12) * mm});
            skLineSegment(sketch, "E6127", {"start": v(-42.94, -42.12) * mm, "end": v(-42.9, -42.14) * mm});
            skLineSegment(sketch, "E6128", {"start": v(-42.9, -42.14) * mm, "end": v(-42.87, -42.17) * mm});
            skLineSegment(sketch, "E6129", {"start": v(-42.87, -42.17) * mm, "end": v(-42.84, -42.2) * mm});
            skLineSegment(sketch, "E6130", {"start": v(-42.84, -42.2) * mm, "end": v(-42.8, -42.22) * mm});
            skLineSegment(sketch, "E6131", {"start": v(-42.8, -42.22) * mm, "end": v(-42.76, -42.24) * mm});
            skLineSegment(sketch, "E6132", {"start": v(-42.69, -42.29) * mm, "end": v(-42.65, -42.3) * mm});
            skLineSegment(sketch, "E6133", {"start": v(-42.65, -42.3) * mm, "end": v(-42.6, -42.32) * mm});
            skLineSegment(sketch, "E6134", {"start": v(-42.6, -42.32) * mm, "end": v(-42.57, -42.34) * mm});
            skLineSegment(sketch, "E6135", {"start": v(-42.57, -42.34) * mm, "end": v(-42.53, -42.36) * mm});
            skLineSegment(sketch, "E6136", {"start": v(-42.53, -42.36) * mm, "end": v(-42.49, -42.37) * mm});
            skLineSegment(sketch, "E6137", {"start": v(-42.49, -42.37) * mm, "end": v(-42.45, -42.38) * mm});
            skLineSegment(sketch, "E6138", {"start": v(-42.45, -42.38) * mm, "end": v(-42.4, -42.4) * mm});
            skLineSegment(sketch, "E6139", {"start": v(-42.4, -42.4) * mm, "end": v(-42.36, -42.4) * mm});
            skLineSegment(sketch, "E6140", {"start": v(-42.36, -42.4) * mm, "end": v(-42.32, -42.4) * mm});
            skLineSegment(sketch, "E6141", {"start": v(-42.28, -42.42) * mm, "end": v(-42.23, -42.42) * mm});
            skLineSegment(sketch, "E6142", {"start": v(-42.23, -42.42) * mm, "end": v(-42.19, -42.42) * mm});
            skLineSegment(sketch, "E6143", {"start": v(-42.19, -42.42) * mm, "end": v(-42.15, -42.43) * mm});
            skLineSegment(sketch, "E6144", {"start": v(-42.15, -42.43) * mm, "end": v(-42.1, -42.43) * mm});
            skLineSegment(sketch, "E6145", {"start": v(-42.1, -42.43) * mm, "end": v(-42.06, -42.43) * mm});
            skLineSegment(sketch, "E6146", {"start": v(-42.06, -42.43) * mm, "end": v(-42.02, -42.42) * mm});
            skLineSegment(sketch, "E6147", {"start": v(-42.02, -42.42) * mm, "end": v(-41.97, -42.42) * mm});
            skLineSegment(sketch, "E6148", {"start": v(-41.97, -42.42) * mm, "end": v(-41.93, -42.41) * mm});
            skLineSegment(sketch, "E6149", {"start": v(-41.93, -42.41) * mm, "end": v(-41.89, -42.4) * mm});
            skLineSegment(sketch, "E6150", {"start": v(-41.89, -42.4) * mm, "end": v(-41.84, -42.4) * mm});
            skLineSegment(sketch, "E6151", {"start": v(-41.84, -42.4) * mm, "end": v(-41.8, -42.39) * mm});
            skLineSegment(sketch, "E6152", {"start": v(-41.8, -42.39) * mm, "end": v(-41.76, -42.38) * mm});
            skLineSegment(sketch, "E6153", {"start": v(-41.76, -42.38) * mm, "end": v(-41.72, -42.36) * mm});
            skLineSegment(sketch, "E6154", {"start": v(-41.72, -42.36) * mm, "end": v(-41.68, -42.35) * mm});
            skLineSegment(sketch, "E6155", {"start": v(-41.68, -42.35) * mm, "end": v(-41.64, -42.33) * mm});
            skLineSegment(sketch, "E6156", {"start": v(-41.64, -42.33) * mm, "end": v(-41.6, -42.32) * mm});
            skLineSegment(sketch, "E6157", {"start": v(-41.6, -42.32) * mm, "end": v(-41.56, -42.3) * mm});
            skLineSegment(sketch, "E6158", {"start": v(-41.56, -42.3) * mm, "end": v(-41.52, -42.28) * mm});
            skLineSegment(sketch, "E6159", {"start": v(-41.52, -42.28) * mm, "end": v(-41.48, -42.26) * mm});
            skLineSegment(sketch, "E6160", {"start": v(-41.48, -42.26) * mm, "end": v(-41.44, -42.23) * mm});
            skLineSegment(sketch, "E6161", {"start": v(-41.44, -42.23) * mm, "end": v(-41.4, -42.2) * mm});
            skLineSegment(sketch, "E6162", {"start": v(-41.4, -42.2) * mm, "end": v(-41.37, -42.18) * mm});
            skLineSegment(sketch, "E6163", {"start": v(-41.37, -42.18) * mm, "end": v(-41.34, -42.16) * mm});
            skLineSegment(sketch, "E6164", {"start": v(-41.34, -42.16) * mm, "end": v(-41.3, -42.13) * mm});
            skLineSegment(sketch, "E6165", {"start": v(-41.3, -42.13) * mm, "end": v(-41.27, -42.1) * mm});
            skLineSegment(sketch, "E6166", {"start": v(-41.27, -42.1) * mm, "end": v(-41.24, -42.07) * mm});
            skLineSegment(sketch, "E6167", {"start": v(-41.24, -42.07) * mm, "end": v(-41.21, -42.04) * mm});
            skLineSegment(sketch, "E6168", {"start": v(-41.21, -42.04) * mm, "end": v(-41.18, -42) * mm});
            skLineSegment(sketch, "E6169", {"start": v(-41.18, -42) * mm, "end": v(-41.15, -41.98) * mm});
            skLineSegment(sketch, "E6170", {"start": v(-41.15, -41.98) * mm, "end": v(-41.13, -41.94) * mm});
            skLineSegment(sketch, "E6171", {"start": v(-41.13, -41.94) * mm, "end": v(-41.1, -41.9) * mm});
            skLineSegment(sketch, "E6172", {"start": v(-41.1, -41.9) * mm, "end": v(-41.07, -41.87) * mm});
            skLineSegment(sketch, "E6173", {"start": v(-41.07, -41.87) * mm, "end": v(-41.05, -41.84) * mm});
            skLineSegment(sketch, "E6174", {"start": v(-41.05, -41.84) * mm, "end": v(-41.03, -41.8) * mm});
            skLineSegment(sketch, "E6175", {"start": v(-41.03, -41.8) * mm, "end": v(-41, -41.76) * mm});
            skLineSegment(sketch, "E6176", {"start": v(-41, -41.76) * mm, "end": v(-40.99, -41.72) * mm});
            skLineSegment(sketch, "E6177", {"start": v(-40.99, -41.72) * mm, "end": v(-40.97, -41.68) * mm});
            skLineSegment(sketch, "E6178", {"start": v(-40.95, -41.64) * mm, "end": v(-40.94, -41.6) * mm});
            skLineSegment(sketch, "E6179", {"start": v(-40.94, -41.6) * mm, "end": v(-40.92, -41.56) * mm});
            skLineSegment(sketch, "E6180", {"start": v(-40.92, -41.56) * mm, "end": v(-40.91, -41.52) * mm});
            skLineSegment(sketch, "E6181", {"start": v(-40.91, -41.52) * mm, "end": v(-40.9, -41.48) * mm});
            skLineSegment(sketch, "E6182", {"start": v(-40.9, -41.48) * mm, "end": v(-40.89, -41.44) * mm});
            skLineSegment(sketch, "E6183", {"start": v(-40.89, -41.44) * mm, "end": v(-40.88, -41.4) * mm});
            skLineSegment(sketch, "E6184", {"start": v(-40.88, -41.4) * mm, "end": v(-40.87, -41.35) * mm});
            skLineSegment(sketch, "E6185", {"start": v(-40.87, -41.35) * mm, "end": v(-40.87, -41.3) * mm});
            skLineSegment(sketch, "E6186", {"start": v(-40.87, -41.3) * mm, "end": v(-40.87, -41.26) * mm});
            skLineSegment(sketch, "E6187", {"start": v(-40.87, -41.26) * mm, "end": v(-40.86, -41.22) * mm});
            skLineSegment(sketch, "E6188", {"start": v(-40.86, -41.22) * mm, "end": v(-40.86, -41.18) * mm});
            skLineSegment(sketch, "E6189", {"start": v(86.64, -41.18) * mm, "end": v(86.64, -41.13) * mm});
            skLineSegment(sketch, "E6190", {"start": v(86.64, -41.13) * mm, "end": v(86.63, -41.09) * mm});
            skLineSegment(sketch, "E6191", {"start": v(86.63, -41.09) * mm, "end": v(86.63, -41.05) * mm});
            skLineSegment(sketch, "E6192", {"start": v(86.63, -41.05) * mm, "end": v(86.63, -41) * mm});
            skLineSegment(sketch, "E6193", {"start": v(86.63, -41) * mm, "end": v(86.62, -40.96) * mm});
            skLineSegment(sketch, "E6194", {"start": v(86.62, -40.96) * mm, "end": v(86.61, -40.92) * mm});
            skLineSegment(sketch, "E6195", {"start": v(86.61, -40.92) * mm, "end": v(86.6, -40.88) * mm});
            skLineSegment(sketch, "E6196", {"start": v(86.6, -40.88) * mm, "end": v(86.59, -40.83) * mm});
            skLineSegment(sketch, "E6197", {"start": v(86.59, -40.83) * mm, "end": v(86.58, -40.8) * mm});
            skLineSegment(sketch, "E6198", {"start": v(86.58, -40.8) * mm, "end": v(86.56, -40.75) * mm});
            skLineSegment(sketch, "E6199", {"start": v(86.56, -40.75) * mm, "end": v(86.55, -40.71) * mm});
            skLineSegment(sketch, "E6200", {"start": v(86.55, -40.71) * mm, "end": v(86.53, -40.67) * mm});
            skLineSegment(sketch, "E6201", {"start": v(86.53, -40.67) * mm, "end": v(86.51, -40.63) * mm});
            skLineSegment(sketch, "E6202", {"start": v(86.51, -40.63) * mm, "end": v(86.5, -40.6) * mm});
            skLineSegment(sketch, "E6203", {"start": v(86.5, -40.6) * mm, "end": v(86.47, -40.55) * mm});
            skLineSegment(sketch, "E6204", {"start": v(86.47, -40.55) * mm, "end": v(86.45, -40.52) * mm});
            skLineSegment(sketch, "E6205", {"start": v(86.45, -40.52) * mm, "end": v(86.43, -40.48) * mm});
            skLineSegment(sketch, "E6206", {"start": v(86.43, -40.48) * mm, "end": v(86.4, -40.45) * mm});
            skLineSegment(sketch, "E6207", {"start": v(86.4, -40.45) * mm, "end": v(86.37, -40.41) * mm});
            skLineSegment(sketch, "E6208", {"start": v(86.37, -40.41) * mm, "end": v(86.35, -40.38) * mm});
            skLineSegment(sketch, "E6209", {"start": v(86.35, -40.38) * mm, "end": v(86.32, -40.34) * mm});
            skLineSegment(sketch, "E6210", {"start": v(86.32, -40.34) * mm, "end": v(86.29, -40.31) * mm});
            skLineSegment(sketch, "E6211", {"start": v(86.26, -40.28) * mm, "end": v(86.23, -40.25) * mm});
            skLineSegment(sketch, "E6212", {"start": v(86.23, -40.25) * mm, "end": v(86.2, -40.22) * mm});
            skLineSegment(sketch, "E6213", {"start": v(86.2, -40.22) * mm, "end": v(86.16, -40.2) * mm});
            skLineSegment(sketch, "E6214", {"start": v(86.16, -40.2) * mm, "end": v(86.13, -40.17) * mm});
            skLineSegment(sketch, "E6215", {"start": v(86.13, -40.17) * mm, "end": v(86.1, -40.14) * mm});
            skLineSegment(sketch, "E6216", {"start": v(86.1, -40.14) * mm, "end": v(86.06, -40.12) * mm});
            skLineSegment(sketch, "E6217", {"start": v(86.06, -40.12) * mm, "end": v(86.02, -40.1) * mm});
            skLineSegment(sketch, "E6218", {"start": v(86.02, -40.1) * mm, "end": v(85.98, -40.08) * mm});
            skLineSegment(sketch, "E6219", {"start": v(85.98, -40.08) * mm, "end": v(85.94, -40.06) * mm});
            skLineSegment(sketch, "E6220", {"start": v(85.94, -40.06) * mm, "end": v(85.9, -40.04) * mm});
            skLineSegment(sketch, "E6221", {"start": v(85.9, -40.04) * mm, "end": v(85.86, -40.02) * mm});
            skLineSegment(sketch, "E6222", {"start": v(85.86, -40.02) * mm, "end": v(85.82, -40) * mm});
            skLineSegment(sketch, "E6223", {"start": v(85.82, -40) * mm, "end": v(85.78, -40) * mm});
            skLineSegment(sketch, "E6224", {"start": v(85.78, -40) * mm, "end": v(85.74, -39.98) * mm});
            skLineSegment(sketch, "E6225", {"start": v(85.74, -39.98) * mm, "end": v(85.7, -39.97) * mm});
            skLineSegment(sketch, "E6226", {"start": v(85.7, -39.97) * mm, "end": v(85.66, -39.96) * mm});
            skLineSegment(sketch, "E6227", {"start": v(85.66, -39.96) * mm, "end": v(85.61, -39.95) * mm});
            skLineSegment(sketch, "E6228", {"start": v(85.61, -39.95) * mm, "end": v(85.57, -39.94) * mm});
            skLineSegment(sketch, "E6229", {"start": v(85.57, -39.94) * mm, "end": v(85.53, -39.93) * mm});
            skLineSegment(sketch, "E6230", {"start": v(85.53, -39.93) * mm, "end": v(85.48, -39.93) * mm});
            skLineSegment(sketch, "E6231", {"start": v(85.48, -39.93) * mm, "end": v(85.44, -39.93) * mm});
            skLineSegment(sketch, "E6232", {"start": v(85.44, -39.93) * mm, "end": v(85.4, -39.93) * mm});
            skLineSegment(sketch, "E6233", {"start": v(85.4, -39.93) * mm, "end": v(85.35, -39.93) * mm});
            skLineSegment(sketch, "E6234", {"start": v(85.35, -39.93) * mm, "end": v(85.31, -39.93) * mm});
            skLineSegment(sketch, "E6235", {"start": v(85.31, -39.93) * mm, "end": v(85.27, -39.93) * mm});
            skLineSegment(sketch, "E6236", {"start": v(85.27, -39.93) * mm, "end": v(85.22, -39.94) * mm});
            skLineSegment(sketch, "E6237", {"start": v(85.22, -39.94) * mm, "end": v(85.18, -39.94) * mm});
            skLineSegment(sketch, "E6238", {"start": v(85.18, -39.94) * mm, "end": v(85.14, -39.95) * mm});
            skLineSegment(sketch, "E6239", {"start": v(85.14, -39.95) * mm, "end": v(85.1, -39.96) * mm});
            skLineSegment(sketch, "E6240", {"start": v(85.1, -39.96) * mm, "end": v(85.05, -39.97) * mm});
            skLineSegment(sketch, "E6241", {"start": v(85.05, -39.97) * mm, "end": v(85.01, -39.98) * mm});
            skLineSegment(sketch, "E6242", {"start": v(85.01, -39.98) * mm, "end": v(84.97, -40) * mm});
            skLineSegment(sketch, "E6243", {"start": v(84.97, -40) * mm, "end": v(84.93, -40.01) * mm});
            skLineSegment(sketch, "E6244", {"start": v(84.93, -40.01) * mm, "end": v(84.9, -40.03) * mm});
            skLineSegment(sketch, "E6245", {"start": v(84.9, -40.03) * mm, "end": v(84.85, -40.05) * mm});
            skLineSegment(sketch, "E6246", {"start": v(84.81, -40.07) * mm, "end": v(84.77, -40.09) * mm});
            skLineSegment(sketch, "E6247", {"start": v(84.77, -40.09) * mm, "end": v(84.74, -40.1) * mm});
            skLineSegment(sketch, "E6248", {"start": v(84.74, -40.1) * mm, "end": v(84.7, -40.13) * mm});
            skLineSegment(sketch, "E6249", {"start": v(84.7, -40.13) * mm, "end": v(84.66, -40.16) * mm});
            skLineSegment(sketch, "E6250", {"start": v(84.66, -40.16) * mm, "end": v(84.63, -40.18) * mm});
            skLineSegment(sketch, "E6251", {"start": v(84.63, -40.18) * mm, "end": v(84.6, -40.2) * mm});
            skLineSegment(sketch, "E6252", {"start": v(84.6, -40.2) * mm, "end": v(84.56, -40.24) * mm});
            skLineSegment(sketch, "E6253", {"start": v(84.56, -40.24) * mm, "end": v(84.53, -40.27) * mm});
            skLineSegment(sketch, "E6254", {"start": v(84.53, -40.27) * mm, "end": v(84.5, -40.3) * mm});
            skLineSegment(sketch, "E6255", {"start": v(84.5, -40.3) * mm, "end": v(84.47, -40.33) * mm});
            skLineSegment(sketch, "E6256", {"start": v(84.47, -40.33) * mm, "end": v(84.44, -40.36) * mm});
            skLineSegment(sketch, "E6257", {"start": v(84.44, -40.36) * mm, "end": v(84.41, -40.4) * mm});
            skLineSegment(sketch, "E6258", {"start": v(84.41, -40.4) * mm, "end": v(84.39, -40.43) * mm});
            skLineSegment(sketch, "E6259", {"start": v(84.39, -40.43) * mm, "end": v(84.36, -40.46) * mm});
            skLineSegment(sketch, "E6260", {"start": v(84.36, -40.46) * mm, "end": v(84.34, -40.5) * mm});
            skLineSegment(sketch, "E6261", {"start": v(84.34, -40.5) * mm, "end": v(84.31, -40.54) * mm});
            skLineSegment(sketch, "E6262", {"start": v(84.31, -40.54) * mm, "end": v(84.3, -40.57) * mm});
            skLineSegment(sketch, "E6263", {"start": v(84.3, -40.57) * mm, "end": v(84.27, -40.61) * mm});
            skLineSegment(sketch, "E6264", {"start": v(84.25, -40.65) * mm, "end": v(84.24, -40.7) * mm});
            skLineSegment(sketch, "E6265", {"start": v(84.24, -40.7) * mm, "end": v(84.22, -40.73) * mm});
            skLineSegment(sketch, "E6266", {"start": v(84.22, -40.73) * mm, "end": v(84.2, -40.77) * mm});
            skLineSegment(sketch, "E6267", {"start": v(84.2, -40.77) * mm, "end": v(84.2, -40.81) * mm});
            skLineSegment(sketch, "E6268", {"start": v(84.2, -40.81) * mm, "end": v(84.18, -40.85) * mm});
            skLineSegment(sketch, "E6269", {"start": v(84.18, -40.85) * mm, "end": v(84.17, -40.9) * mm});
            skLineSegment(sketch, "E6270", {"start": v(84.17, -40.9) * mm, "end": v(84.16, -40.94) * mm});
            skLineSegment(sketch, "E6271", {"start": v(84.16, -40.94) * mm, "end": v(84.15, -40.98) * mm});
            skLineSegment(sketch, "E6272", {"start": v(84.15, -40.98) * mm, "end": v(84.15, -41.03) * mm});
            skLineSegment(sketch, "E6273", {"start": v(84.15, -41.03) * mm, "end": v(84.14, -41.07) * mm});
            skLineSegment(sketch, "E6274", {"start": v(84.14, -41.07) * mm, "end": v(84.14, -41.11) * mm});
            skLineSegment(sketch, "E6275", {"start": v(84.14, -41.11) * mm, "end": v(84.14, -41.15) * mm});
            skLineSegment(sketch, "E6276", {"start": v(84.14, -41.15) * mm, "end": v(84.14, -41.2) * mm});
            skLineSegment(sketch, "E6277", {"start": v(84.14, -41.2) * mm, "end": v(84.14, -41.24) * mm});
            skLineSegment(sketch, "E6278", {"start": v(84.14, -41.24) * mm, "end": v(84.14, -41.29) * mm});
            skLineSegment(sketch, "E6279", {"start": v(84.14, -41.29) * mm, "end": v(84.15, -41.33) * mm});
            skLineSegment(sketch, "E6280", {"start": v(84.15, -41.33) * mm, "end": v(84.15, -41.37) * mm});
            skLineSegment(sketch, "E6281", {"start": v(84.15, -41.37) * mm, "end": v(84.16, -41.41) * mm});
            skLineSegment(sketch, "E6282", {"start": v(84.16, -41.41) * mm, "end": v(84.17, -41.46) * mm});
            skLineSegment(sketch, "E6283", {"start": v(84.17, -41.46) * mm, "end": v(84.18, -41.5) * mm});
            skLineSegment(sketch, "E6284", {"start": v(84.18, -41.5) * mm, "end": v(84.2, -41.54) * mm});
            skLineSegment(sketch, "E6285", {"start": v(84.2, -41.54) * mm, "end": v(84.2, -41.58) * mm});
            skLineSegment(sketch, "E6286", {"start": v(84.2, -41.58) * mm, "end": v(84.22, -41.62) * mm});
            skLineSegment(sketch, "E6287", {"start": v(84.22, -41.62) * mm, "end": v(84.24, -41.66) * mm});
            skLineSegment(sketch, "E6288", {"start": v(84.24, -41.66) * mm, "end": v(84.25, -41.7) * mm});
            skLineSegment(sketch, "E6289", {"start": v(84.25, -41.7) * mm, "end": v(84.27, -41.74) * mm});
            skLineSegment(sketch, "E6290", {"start": v(84.27, -41.74) * mm, "end": v(84.3, -41.78) * mm});
            skLineSegment(sketch, "E6291", {"start": v(84.3, -41.78) * mm, "end": v(84.31, -41.82) * mm});
            skLineSegment(sketch, "E6292", {"start": v(84.31, -41.82) * mm, "end": v(84.34, -41.85) * mm});
            skLineSegment(sketch, "E6293", {"start": v(84.34, -41.85) * mm, "end": v(84.36, -41.9) * mm});
            skLineSegment(sketch, "E6294", {"start": v(84.36, -41.9) * mm, "end": v(84.39, -41.93) * mm});
            skLineSegment(sketch, "E6295", {"start": v(84.39, -41.93) * mm, "end": v(84.41, -41.96) * mm});
            skLineSegment(sketch, "E6296", {"start": v(84.41, -41.96) * mm, "end": v(84.44, -42) * mm});
            skLineSegment(sketch, "E6297", {"start": v(84.44, -42) * mm, "end": v(84.47, -42.03) * mm});
            skLineSegment(sketch, "E6298", {"start": v(84.47, -42.03) * mm, "end": v(84.5, -42.06) * mm});
            skLineSegment(sketch, "E6299", {"start": v(84.53, -42.09) * mm, "end": v(84.56, -42.12) * mm});
            skLineSegment(sketch, "E6300", {"start": v(84.56, -42.12) * mm, "end": v(84.6, -42.14) * mm});
            skLineSegment(sketch, "E6301", {"start": v(84.6, -42.14) * mm, "end": v(84.63, -42.17) * mm});
            skLineSegment(sketch, "E6302", {"start": v(84.63, -42.17) * mm, "end": v(84.66, -42.2) * mm});
            skLineSegment(sketch, "E6303", {"start": v(84.66, -42.2) * mm, "end": v(84.7, -42.22) * mm});
            skLineSegment(sketch, "E6304", {"start": v(84.7, -42.22) * mm, "end": v(84.74, -42.24) * mm});
            skLineSegment(sketch, "E6305", {"start": v(84.74, -42.24) * mm, "end": v(84.77, -42.27) * mm});
            skLineSegment(sketch, "E6306", {"start": v(84.77, -42.27) * mm, "end": v(84.81, -42.29) * mm});
            skLineSegment(sketch, "E6307", {"start": v(84.81, -42.29) * mm, "end": v(84.85, -42.3) * mm});
            skLineSegment(sketch, "E6308", {"start": v(84.85, -42.3) * mm, "end": v(84.9, -42.32) * mm});
            skLineSegment(sketch, "E6309", {"start": v(84.9, -42.32) * mm, "end": v(84.93, -42.34) * mm});
            skLineSegment(sketch, "E6310", {"start": v(84.93, -42.34) * mm, "end": v(84.97, -42.36) * mm});
            skLineSegment(sketch, "E6311", {"start": v(84.97, -42.36) * mm, "end": v(85.01, -42.37) * mm});
            skLineSegment(sketch, "E6312", {"start": v(85.01, -42.37) * mm, "end": v(85.05, -42.38) * mm});
            skLineSegment(sketch, "E6313", {"start": v(85.05, -42.38) * mm, "end": v(85.1, -42.4) * mm});
            skLineSegment(sketch, "E6314", {"start": v(85.1, -42.4) * mm, "end": v(85.14, -42.4) * mm});
            skLineSegment(sketch, "E6315", {"start": v(85.14, -42.4) * mm, "end": v(85.18, -42.4) * mm});
            skLineSegment(sketch, "E6316", {"start": v(85.18, -42.4) * mm, "end": v(85.22, -42.42) * mm});
            skLineSegment(sketch, "E6317", {"start": v(85.22, -42.42) * mm, "end": v(85.27, -42.42) * mm});
            skLineSegment(sketch, "E6318", {"start": v(85.27, -42.42) * mm, "end": v(85.31, -42.42) * mm});
            skLineSegment(sketch, "E6319", {"start": v(85.31, -42.42) * mm, "end": v(85.35, -42.43) * mm});
            skLineSegment(sketch, "E6320", {"start": v(85.35, -42.43) * mm, "end": v(85.4, -42.43) * mm});
            skLineSegment(sketch, "E6321", {"start": v(85.4, -42.43) * mm, "end": v(85.44, -42.43) * mm});
            skLineSegment(sketch, "E6322", {"start": v(85.44, -42.43) * mm, "end": v(85.48, -42.42) * mm});
            skLineSegment(sketch, "E6323", {"start": v(85.48, -42.42) * mm, "end": v(85.53, -42.42) * mm});
            skLineSegment(sketch, "E6324", {"start": v(85.53, -42.42) * mm, "end": v(85.57, -42.41) * mm});
            skLineSegment(sketch, "E6325", {"start": v(85.57, -42.41) * mm, "end": v(85.61, -42.4) * mm});
            skLineSegment(sketch, "E6326", {"start": v(85.61, -42.4) * mm, "end": v(85.66, -42.4) * mm});
            skLineSegment(sketch, "E6327", {"start": v(85.66, -42.4) * mm, "end": v(85.7, -42.39) * mm});
            skLineSegment(sketch, "E6328", {"start": v(85.7, -42.39) * mm, "end": v(85.74, -42.38) * mm});
            skLineSegment(sketch, "E6329", {"start": v(85.74, -42.38) * mm, "end": v(85.78, -42.36) * mm});
            skLineSegment(sketch, "E6330", {"start": v(85.78, -42.36) * mm, "end": v(85.82, -42.35) * mm});
            skLineSegment(sketch, "E6331", {"start": v(85.82, -42.35) * mm, "end": v(85.86, -42.33) * mm});
            skLineSegment(sketch, "E6332", {"start": v(85.86, -42.33) * mm, "end": v(85.9, -42.32) * mm});
            skLineSegment(sketch, "E6333", {"start": v(85.9, -42.32) * mm, "end": v(85.94, -42.3) * mm});
            skLineSegment(sketch, "E6334", {"start": v(85.94, -42.3) * mm, "end": v(85.98, -42.28) * mm});
            skLineSegment(sketch, "E6335", {"start": v(85.98, -42.28) * mm, "end": v(86.02, -42.26) * mm});
            skLineSegment(sketch, "E6336", {"start": v(86.02, -42.26) * mm, "end": v(86.06, -42.23) * mm});
            skLineSegment(sketch, "E6337", {"start": v(86.06, -42.23) * mm, "end": v(86.1, -42.2) * mm});
            skLineSegment(sketch, "E6338", {"start": v(86.1, -42.2) * mm, "end": v(86.13, -42.18) * mm});
            skLineSegment(sketch, "E6339", {"start": v(86.13, -42.18) * mm, "end": v(86.16, -42.16) * mm});
            skLineSegment(sketch, "E6340", {"start": v(86.16, -42.16) * mm, "end": v(86.2, -42.13) * mm});
            skLineSegment(sketch, "E6341", {"start": v(86.2, -42.13) * mm, "end": v(86.23, -42.1) * mm});
            skLineSegment(sketch, "E6342", {"start": v(86.23, -42.1) * mm, "end": v(86.26, -42.07) * mm});
            skLineSegment(sketch, "E6343", {"start": v(86.26, -42.07) * mm, "end": v(86.29, -42.04) * mm});
            skLineSegment(sketch, "E6344", {"start": v(86.29, -42.04) * mm, "end": v(86.32, -42) * mm});
            skLineSegment(sketch, "E6345", {"start": v(86.32, -42) * mm, "end": v(86.35, -41.98) * mm});
            skLineSegment(sketch, "E6346", {"start": v(86.35, -41.98) * mm, "end": v(86.37, -41.94) * mm});
            skLineSegment(sketch, "E6347", {"start": v(86.37, -41.94) * mm, "end": v(86.4, -41.9) * mm});
            skLineSegment(sketch, "E6348", {"start": v(86.4, -41.9) * mm, "end": v(86.43, -41.87) * mm});
            skLineSegment(sketch, "E6349", {"start": v(86.43, -41.87) * mm, "end": v(86.45, -41.84) * mm});
            skLineSegment(sketch, "E6350", {"start": v(86.45, -41.84) * mm, "end": v(86.47, -41.8) * mm});
            skLineSegment(sketch, "E6351", {"start": v(86.47, -41.8) * mm, "end": v(86.5, -41.76) * mm});
            skLineSegment(sketch, "E6352", {"start": v(86.51, -41.72) * mm, "end": v(86.53, -41.68) * mm});
            skLineSegment(sketch, "E6353", {"start": v(86.53, -41.68) * mm, "end": v(86.55, -41.64) * mm});
            skLineSegment(sketch, "E6354", {"start": v(86.55, -41.64) * mm, "end": v(86.56, -41.6) * mm});
            skLineSegment(sketch, "E6355", {"start": v(86.56, -41.6) * mm, "end": v(86.58, -41.56) * mm});
            skLineSegment(sketch, "E6356", {"start": v(86.58, -41.56) * mm, "end": v(86.59, -41.52) * mm});
            skLineSegment(sketch, "E6357", {"start": v(86.59, -41.52) * mm, "end": v(86.6, -41.48) * mm});
            skLineSegment(sketch, "E6358", {"start": v(86.6, -41.48) * mm, "end": v(86.61, -41.44) * mm});
            skLineSegment(sketch, "E6359", {"start": v(86.61, -41.44) * mm, "end": v(86.62, -41.4) * mm});
            skLineSegment(sketch, "E6360", {"start": v(86.62, -41.4) * mm, "end": v(86.63, -41.35) * mm});
            skLineSegment(sketch, "E6361", {"start": v(86.63, -41.35) * mm, "end": v(86.63, -41.3) * mm});
            skLineSegment(sketch, "E6362", {"start": v(86.63, -41.3) * mm, "end": v(86.63, -41.26) * mm});
            skLineSegment(sketch, "E6363", {"start": v(86.63, -41.26) * mm, "end": v(86.64, -41.22) * mm});
            skLineSegment(sketch, "E6364", {"start": v(86.64, -41.22) * mm, "end": v(86.64, -41.18) * mm});
            skLineSegment(sketch, "E6365", {"start": v(-68, 26.42) * mm, "end": v(-68, 26.5) * mm});
            skLineSegment(sketch, "E6366", {"start": v(-68, 26.5) * mm, "end": v(-68.01, 26.57) * mm});
            skLineSegment(sketch, "E6367", {"start": v(-68.01, 26.57) * mm, "end": v(-68.02, 26.64) * mm});
            skLineSegment(sketch, "E6368", {"start": v(-68.02, 26.64) * mm, "end": v(-68.03, 26.72) * mm});
            skLineSegment(sketch, "E6369", {"start": v(-68.03, 26.72) * mm, "end": v(-68.04, 26.8) * mm});
            skLineSegment(sketch, "E6370", {"start": v(-68.04, 26.8) * mm, "end": v(-68.05, 26.86) * mm});
            skLineSegment(sketch, "E6371", {"start": v(-68.05, 26.86) * mm, "end": v(-68.07, 26.94) * mm});
            skLineSegment(sketch, "E6372", {"start": v(-68.07, 26.94) * mm, "end": v(-68.09, 27) * mm});
            skLineSegment(sketch, "E6373", {"start": v(-68.09, 27) * mm, "end": v(-68.1, 27.08) * mm});
            skLineSegment(sketch, "E6374", {"start": v(-68.1, 27.08) * mm, "end": v(-68.13, 27.15) * mm});
            skLineSegment(sketch, "E6375", {"start": v(-68.13, 27.15) * mm, "end": v(-68.16, 27.22) * mm});
            skLineSegment(sketch, "E6376", {"start": v(-68.19, 27.29) * mm, "end": v(-68.22, 27.36) * mm});
            skLineSegment(sketch, "E6377", {"start": v(-68.22, 27.36) * mm, "end": v(-68.25, 27.42) * mm});
            skLineSegment(sketch, "E6378", {"start": v(-68.25, 27.42) * mm, "end": v(-68.3, 27.49) * mm});
            skLineSegment(sketch, "E6379", {"start": v(-68.3, 27.49) * mm, "end": v(-68.33, 27.55) * mm});
            skLineSegment(sketch, "E6380", {"start": v(-68.33, 27.55) * mm, "end": v(-68.37, 27.62) * mm});
            skLineSegment(sketch, "E6381", {"start": v(-68.37, 27.62) * mm, "end": v(-68.41, 27.68) * mm});
            skLineSegment(sketch, "E6382", {"start": v(-68.41, 27.68) * mm, "end": v(-68.46, 27.74) * mm});
            skLineSegment(sketch, "E6383", {"start": v(-68.46, 27.74) * mm, "end": v(-68.5, 27.8) * mm});
            skLineSegment(sketch, "E6384", {"start": v(-68.5, 27.8) * mm, "end": v(-68.55, 27.85) * mm});
            skLineSegment(sketch, "E6385", {"start": v(-68.55, 27.85) * mm, "end": v(-68.6, 27.9) * mm});
            skLineSegment(sketch, "E6386", {"start": v(-68.6, 27.9) * mm, "end": v(-68.66, 27.96) * mm});
            skLineSegment(sketch, "E6387", {"start": v(-68.66, 27.96) * mm, "end": v(-68.7, 28.01) * mm});
            skLineSegment(sketch, "E6388", {"start": v(-68.7, 28.01) * mm, "end": v(-68.77, 28.06) * mm});
            skLineSegment(sketch, "E6389", {"start": v(-68.77, 28.06) * mm, "end": v(-68.82, 28.1) * mm});
            skLineSegment(sketch, "E6390", {"start": v(-68.94, 28.2) * mm, "end": v(-69, 28.24) * mm});
            skLineSegment(sketch, "E6391", {"start": v(-69, 28.24) * mm, "end": v(-69.07, 28.28) * mm});
            skLineSegment(sketch, "E6392", {"start": v(-69.07, 28.28) * mm, "end": v(-69.13, 28.31) * mm});
            skLineSegment(sketch, "E6393", {"start": v(-69.13, 28.31) * mm, "end": v(-69.2, 28.35) * mm});
            skLineSegment(sketch, "E6394", {"start": v(-69.2, 28.35) * mm, "end": v(-69.27, 28.38) * mm});
            skLineSegment(sketch, "E6395", {"start": v(-69.27, 28.38) * mm, "end": v(-69.34, 28.4) * mm});
            skLineSegment(sketch, "E6396", {"start": v(-69.34, 28.4) * mm, "end": v(-69.4, 28.44) * mm});
            skLineSegment(sketch, "E6397", {"start": v(-69.4, 28.44) * mm, "end": v(-69.48, 28.46) * mm});
            skLineSegment(sketch, "E6398", {"start": v(-69.48, 28.46) * mm, "end": v(-69.55, 28.48) * mm});
            skLineSegment(sketch, "E6399", {"start": v(-69.62, 28.5) * mm, "end": v(-69.7, 28.52) * mm});
            skLineSegment(sketch, "E6400", {"start": v(-69.7, 28.52) * mm, "end": v(-69.77, 28.53) * mm});
            skLineSegment(sketch, "E6401", {"start": v(-69.77, 28.53) * mm, "end": v(-69.84, 28.55) * mm});
            skLineSegment(sketch, "E6402", {"start": v(-69.84, 28.55) * mm, "end": v(-69.91, 28.56) * mm});
            skLineSegment(sketch, "E6403", {"start": v(-69.91, 28.56) * mm, "end": v(-69.99, 28.56) * mm});
            skLineSegment(sketch, "E6404", {"start": v(-69.99, 28.56) * mm, "end": v(-70.06, 28.57) * mm});
            skLineSegment(sketch, "E6405", {"start": v(-70.06, 28.57) * mm, "end": v(-70.14, 28.57) * mm});
            skLineSegment(sketch, "E6406", {"start": v(-70.14, 28.57) * mm, "end": v(-70.21, 28.57) * mm});
            skLineSegment(sketch, "E6407", {"start": v(-70.21, 28.57) * mm, "end": v(-70.29, 28.57) * mm});
            skLineSegment(sketch, "E6408", {"start": v(-70.29, 28.57) * mm, "end": v(-70.36, 28.56) * mm});
            skLineSegment(sketch, "E6409", {"start": v(-70.36, 28.56) * mm, "end": v(-70.43, 28.55) * mm});
            skLineSegment(sketch, "E6410", {"start": v(-70.43, 28.55) * mm, "end": v(-70.5, 28.54) * mm});
            skLineSegment(sketch, "E6411", {"start": v(-70.5, 28.54) * mm, "end": v(-70.58, 28.53) * mm});
            skLineSegment(sketch, "E6412", {"start": v(-70.58, 28.53) * mm, "end": v(-70.65, 28.51) * mm});
            skLineSegment(sketch, "E6413", {"start": v(-70.65, 28.51) * mm, "end": v(-70.73, 28.5) * mm});
            skLineSegment(sketch, "E6414", {"start": v(-70.73, 28.5) * mm, "end": v(-70.8, 28.47) * mm});
            skLineSegment(sketch, "E6415", {"start": v(-70.87, 28.45) * mm, "end": v(-70.94, 28.42) * mm});
            skLineSegment(sketch, "E6416", {"start": v(-70.94, 28.42) * mm, "end": v(-71, 28.4) * mm});
            skLineSegment(sketch, "E6417", {"start": v(-71, 28.4) * mm, "end": v(-71.08, 28.36) * mm});
            skLineSegment(sketch, "E6418", {"start": v(-71.08, 28.36) * mm, "end": v(-71.14, 28.33) * mm});
            skLineSegment(sketch, "E6419", {"start": v(-71.14, 28.33) * mm, "end": v(-71.2, 28.3) * mm});
            skLineSegment(sketch, "E6420", {"start": v(-71.2, 28.3) * mm, "end": v(-71.27, 28.26) * mm});
            skLineSegment(sketch, "E6421", {"start": v(-71.27, 28.26) * mm, "end": v(-71.34, 28.22) * mm});
            skLineSegment(sketch, "E6422", {"start": v(-71.34, 28.22) * mm, "end": v(-71.4, 28.17) * mm});
            skLineSegment(sketch, "E6423", {"start": v(-71.4, 28.17) * mm, "end": v(-71.46, 28.13) * mm});
            skLineSegment(sketch, "E6424", {"start": v(-71.46, 28.13) * mm, "end": v(-71.52, 28.08) * mm});
            skLineSegment(sketch, "E6425", {"start": v(-71.57, 28.04) * mm, "end": v(-71.63, 27.99) * mm});
            skLineSegment(sketch, "E6426", {"start": v(-71.63, 27.99) * mm, "end": v(-71.68, 27.93) * mm});
            skLineSegment(sketch, "E6427", {"start": v(-71.68, 27.93) * mm, "end": v(-71.73, 27.88) * mm});
            skLineSegment(sketch, "E6428", {"start": v(-71.73, 27.88) * mm, "end": v(-71.78, 27.82) * mm});
            skLineSegment(sketch, "E6429", {"start": v(-71.78, 27.82) * mm, "end": v(-71.83, 27.77) * mm});
            skLineSegment(sketch, "E6430", {"start": v(-71.83, 27.77) * mm, "end": v(-71.88, 27.7) * mm});
            skLineSegment(sketch, "E6431", {"start": v(-71.88, 27.7) * mm, "end": v(-71.92, 27.65) * mm});
            skLineSegment(sketch, "E6432", {"start": v(-71.92, 27.65) * mm, "end": v(-71.96, 27.59) * mm});
            skLineSegment(sketch, "E6433", {"start": v(-71.96, 27.59) * mm, "end": v(-72, 27.52) * mm});
            skLineSegment(sketch, "E6434", {"start": v(-72, 27.52) * mm, "end": v(-72.04, 27.46) * mm});
            skLineSegment(sketch, "E6435", {"start": v(-72.04, 27.46) * mm, "end": v(-72.07, 27.4) * mm});
            skLineSegment(sketch, "E6436", {"start": v(-72.07, 27.4) * mm, "end": v(-72.1, 27.32) * mm});
            skLineSegment(sketch, "E6437", {"start": v(-72.1, 27.32) * mm, "end": v(-72.14, 27.26) * mm});
            skLineSegment(sketch, "E6438", {"start": v(-72.16, 27.19) * mm, "end": v(-72.19, 27.12) * mm});
            skLineSegment(sketch, "E6439", {"start": v(-72.19, 27.12) * mm, "end": v(-72.21, 27.05) * mm});
            skLineSegment(sketch, "E6440", {"start": v(-72.21, 27.05) * mm, "end": v(-72.23, 26.97) * mm});
            skLineSegment(sketch, "E6441", {"start": v(-72.23, 26.97) * mm, "end": v(-72.25, 26.9) * mm});
            skLineSegment(sketch, "E6442", {"start": v(-72.25, 26.9) * mm, "end": v(-72.27, 26.83) * mm});
            skLineSegment(sketch, "E6443", {"start": v(-72.27, 26.83) * mm, "end": v(-72.28, 26.75) * mm});
            skLineSegment(sketch, "E6444", {"start": v(-72.28, 26.75) * mm, "end": v(-72.29, 26.68) * mm});
            skLineSegment(sketch, "E6445", {"start": v(-72.29, 26.68) * mm, "end": v(-72.3, 26.6) * mm});
            skLineSegment(sketch, "E6446", {"start": v(-72.3, 26.6) * mm, "end": v(-72.3, 26.53) * mm});
            skLineSegment(sketch, "E6447", {"start": v(-72.3, 26.53) * mm, "end": v(-72.3, 26.46) * mm});
            skLineSegment(sketch, "E6448", {"start": v(-72.3, 26.46) * mm, "end": v(-72.3, 26.38) * mm});
            skLineSegment(sketch, "E6449", {"start": v(-72.3, 26.38) * mm, "end": v(-72.3, 26.3) * mm});
            skLineSegment(sketch, "E6450", {"start": v(-72.3, 26.3) * mm, "end": v(-72.3, 26.23) * mm});
            skLineSegment(sketch, "E6451", {"start": v(-72.3, 26.23) * mm, "end": v(-72.29, 26.16) * mm});
            skLineSegment(sketch, "E6452", {"start": v(-72.29, 26.16) * mm, "end": v(-72.28, 26.09) * mm});
            skLineSegment(sketch, "E6453", {"start": v(-72.28, 26.09) * mm, "end": v(-72.27, 26.01) * mm});
            skLineSegment(sketch, "E6454", {"start": v(-72.27, 26.01) * mm, "end": v(-72.25, 25.94) * mm});
            skLineSegment(sketch, "E6455", {"start": v(-72.23, 25.87) * mm, "end": v(-72.21, 25.8) * mm});
            skLineSegment(sketch, "E6456", {"start": v(-72.21, 25.8) * mm, "end": v(-72.19, 25.72) * mm});
            skLineSegment(sketch, "E6457", {"start": v(-72.19, 25.72) * mm, "end": v(-72.16, 25.65) * mm});
            skLineSegment(sketch, "E6458", {"start": v(-72.16, 25.65) * mm, "end": v(-72.14, 25.58) * mm});
            skLineSegment(sketch, "E6459", {"start": v(-72.14, 25.58) * mm, "end": v(-72.1, 25.52) * mm});
            skLineSegment(sketch, "E6460", {"start": v(-72.1, 25.52) * mm, "end": v(-72.07, 25.45) * mm});
            skLineSegment(sketch, "E6461", {"start": v(-72.07, 25.45) * mm, "end": v(-72.04, 25.38) * mm});
            skLineSegment(sketch, "E6462", {"start": v(-72.04, 25.38) * mm, "end": v(-72, 25.32) * mm});
            skLineSegment(sketch, "E6463", {"start": v(-72, 25.32) * mm, "end": v(-71.96, 25.25) * mm});
            skLineSegment(sketch, "E6464", {"start": v(-71.88, 25.13) * mm, "end": v(-71.83, 25.07) * mm});
            skLineSegment(sketch, "E6465", {"start": v(-71.83, 25.07) * mm, "end": v(-71.78, 25.02) * mm});
            skLineSegment(sketch, "E6466", {"start": v(-71.78, 25.02) * mm, "end": v(-71.73, 24.96) * mm});
            skLineSegment(sketch, "E6467", {"start": v(-71.73, 24.96) * mm, "end": v(-71.68, 24.9) * mm});
            skLineSegment(sketch, "E6468", {"start": v(-71.68, 24.9) * mm, "end": v(-71.63, 24.85) * mm});
            skLineSegment(sketch, "E6469", {"start": v(-71.63, 24.85) * mm, "end": v(-71.57, 24.8) * mm});
            skLineSegment(sketch, "E6470", {"start": v(-71.57, 24.8) * mm, "end": v(-71.52, 24.76) * mm});
            skLineSegment(sketch, "E6471", {"start": v(-71.52, 24.76) * mm, "end": v(-71.46, 24.7) * mm});
            skLineSegment(sketch, "E6472", {"start": v(-71.46, 24.7) * mm, "end": v(-71.4, 24.67) * mm});
            skLineSegment(sketch, "E6473", {"start": v(-71.4, 24.67) * mm, "end": v(-71.34, 24.62) * mm});
            skLineSegment(sketch, "E6474", {"start": v(-71.34, 24.62) * mm, "end": v(-71.27, 24.58) * mm});
            skLineSegment(sketch, "E6475", {"start": v(-71.27, 24.58) * mm, "end": v(-71.2, 24.55) * mm});
            skLineSegment(sketch, "E6476", {"start": v(-71.2, 24.55) * mm, "end": v(-71.14, 24.51) * mm});
            skLineSegment(sketch, "E6477", {"start": v(-71.14, 24.51) * mm, "end": v(-71.08, 24.48) * mm});
            skLineSegment(sketch, "E6478", {"start": v(-71.08, 24.48) * mm, "end": v(-71, 24.45) * mm});
            skLineSegment(sketch, "E6479", {"start": v(-71, 24.45) * mm, "end": v(-70.94, 24.42) * mm});
            skLineSegment(sketch, "E6480", {"start": v(-70.94, 24.42) * mm, "end": v(-70.87, 24.4) * mm});
            skLineSegment(sketch, "E6481", {"start": v(-70.87, 24.4) * mm, "end": v(-70.8, 24.37) * mm});
            skLineSegment(sketch, "E6482", {"start": v(-70.8, 24.37) * mm, "end": v(-70.73, 24.35) * mm});
            skLineSegment(sketch, "E6483", {"start": v(-70.73, 24.35) * mm, "end": v(-70.65, 24.33) * mm});
            skLineSegment(sketch, "E6484", {"start": v(-70.65, 24.33) * mm, "end": v(-70.58, 24.31) * mm});
            skLineSegment(sketch, "E6485", {"start": v(-70.58, 24.31) * mm, "end": v(-70.5, 24.3) * mm});
            skLineSegment(sketch, "E6486", {"start": v(-70.5, 24.3) * mm, "end": v(-70.43, 24.29) * mm});
            skLineSegment(sketch, "E6487", {"start": v(-70.43, 24.29) * mm, "end": v(-70.36, 24.28) * mm});
            skLineSegment(sketch, "E6488", {"start": v(-70.36, 24.28) * mm, "end": v(-70.29, 24.27) * mm});
            skLineSegment(sketch, "E6489", {"start": v(-70.29, 24.27) * mm, "end": v(-70.21, 24.27) * mm});
            skLineSegment(sketch, "E6490", {"start": v(-70.21, 24.27) * mm, "end": v(-70.14, 24.27) * mm});
            skLineSegment(sketch, "E6491", {"start": v(-70.14, 24.27) * mm, "end": v(-70.06, 24.27) * mm});
            skLineSegment(sketch, "E6492", {"start": v(-70.06, 24.27) * mm, "end": v(-69.99, 24.28) * mm});
            skLineSegment(sketch, "E6493", {"start": v(-69.99, 24.28) * mm, "end": v(-69.91, 24.28) * mm});
            skLineSegment(sketch, "E6494", {"start": v(-69.91, 24.28) * mm, "end": v(-69.84, 24.3) * mm});
            skLineSegment(sketch, "E6495", {"start": v(-69.84, 24.3) * mm, "end": v(-69.77, 24.3) * mm});
            skLineSegment(sketch, "E6496", {"start": v(-69.77, 24.3) * mm, "end": v(-69.7, 24.32) * mm});
            skLineSegment(sketch, "E6497", {"start": v(-69.7, 24.32) * mm, "end": v(-69.62, 24.34) * mm});
            skLineSegment(sketch, "E6498", {"start": v(-69.62, 24.34) * mm, "end": v(-69.55, 24.36) * mm});
            skLineSegment(sketch, "E6499", {"start": v(-69.55, 24.36) * mm, "end": v(-69.48, 24.38) * mm});
            skLineSegment(sketch, "E6500", {"start": v(-69.4, 24.4) * mm, "end": v(-69.34, 24.43) * mm});
            skLineSegment(sketch, "E6501", {"start": v(-69.34, 24.43) * mm, "end": v(-69.27, 24.46) * mm});
            skLineSegment(sketch, "E6502", {"start": v(-69.27, 24.46) * mm, "end": v(-69.2, 24.5) * mm});
            skLineSegment(sketch, "E6503", {"start": v(-69.2, 24.5) * mm, "end": v(-69.13, 24.53) * mm});
            skLineSegment(sketch, "E6504", {"start": v(-69.13, 24.53) * mm, "end": v(-69.07, 24.56) * mm});
            skLineSegment(sketch, "E6505", {"start": v(-69.07, 24.56) * mm, "end": v(-69, 24.6) * mm});
            skLineSegment(sketch, "E6506", {"start": v(-69, 24.6) * mm, "end": v(-68.94, 24.64) * mm});
            skLineSegment(sketch, "E6507", {"start": v(-68.94, 24.64) * mm, "end": v(-68.88, 24.69) * mm});
            skLineSegment(sketch, "E6508", {"start": v(-68.88, 24.69) * mm, "end": v(-68.82, 24.73) * mm});
            skLineSegment(sketch, "E6509", {"start": v(-68.82, 24.73) * mm, "end": v(-68.77, 24.78) * mm});
            skLineSegment(sketch, "E6510", {"start": v(-68.77, 24.78) * mm, "end": v(-68.7, 24.83) * mm});
            skLineSegment(sketch, "E6511", {"start": v(-68.7, 24.83) * mm, "end": v(-68.66, 24.88) * mm});
            skLineSegment(sketch, "E6512", {"start": v(-68.66, 24.88) * mm, "end": v(-68.6, 24.93) * mm});
            skLineSegment(sketch, "E6513", {"start": v(-68.55, 24.99) * mm, "end": v(-68.5, 25.04) * mm});
            skLineSegment(sketch, "E6514", {"start": v(-68.41, 25.16) * mm, "end": v(-68.37, 25.22) * mm});
            skLineSegment(sketch, "E6515", {"start": v(-68.37, 25.22) * mm, "end": v(-68.33, 25.29) * mm});
            skLineSegment(sketch, "E6516", {"start": v(-68.33, 25.29) * mm, "end": v(-68.3, 25.35) * mm});
            skLineSegment(sketch, "E6517", {"start": v(-68.3, 25.35) * mm, "end": v(-68.25, 25.42) * mm});
            skLineSegment(sketch, "E6518", {"start": v(-68.25, 25.42) * mm, "end": v(-68.22, 25.48) * mm});
            skLineSegment(sketch, "E6519", {"start": v(-68.22, 25.48) * mm, "end": v(-68.19, 25.55) * mm});
            skLineSegment(sketch, "E6520", {"start": v(-68.19, 25.55) * mm, "end": v(-68.16, 25.62) * mm});
            skLineSegment(sketch, "E6521", {"start": v(-68.16, 25.62) * mm, "end": v(-68.13, 25.69) * mm});
            skLineSegment(sketch, "E6522", {"start": v(-68.13, 25.69) * mm, "end": v(-68.1, 25.76) * mm});
            skLineSegment(sketch, "E6523", {"start": v(-68.1, 25.76) * mm, "end": v(-68.09, 25.83) * mm});
            skLineSegment(sketch, "E6524", {"start": v(-68.09, 25.83) * mm, "end": v(-68.07, 25.9) * mm});
            skLineSegment(sketch, "E6525", {"start": v(-68.07, 25.9) * mm, "end": v(-68.05, 25.98) * mm});
            skLineSegment(sketch, "E6526", {"start": v(-68.05, 25.98) * mm, "end": v(-68.04, 26.05) * mm});
            skLineSegment(sketch, "E6527", {"start": v(-68.04, 26.05) * mm, "end": v(-68.03, 26.12) * mm});
            skLineSegment(sketch, "E6528", {"start": v(-68.03, 26.12) * mm, "end": v(-68.02, 26.2) * mm});
            skLineSegment(sketch, "E6529", {"start": v(-68.02, 26.2) * mm, "end": v(-68.01, 26.27) * mm});
            skLineSegment(sketch, "E6530", {"start": v(-68.01, 26.27) * mm, "end": v(-68, 26.35) * mm});
            skLineSegment(sketch, "E6531", {"start": v(-68, 26.35) * mm, "end": v(-68, 26.42) * mm});
            skLineSegment(sketch, "E6532", {"start": v(-58, 26.42) * mm, "end": v(-58, 26.5) * mm});
            skLineSegment(sketch, "E6533", {"start": v(-58, 26.5) * mm, "end": v(-58.01, 26.57) * mm});
            skLineSegment(sketch, "E6534", {"start": v(-58.01, 26.57) * mm, "end": v(-58.02, 26.64) * mm});
            skLineSegment(sketch, "E6535", {"start": v(-58.02, 26.64) * mm, "end": v(-58.03, 26.72) * mm});
            skLineSegment(sketch, "E6536", {"start": v(-58.03, 26.72) * mm, "end": v(-58.04, 26.8) * mm});
            skLineSegment(sketch, "E6537", {"start": v(-58.04, 26.8) * mm, "end": v(-58.05, 26.86) * mm});
            skLineSegment(sketch, "E6538", {"start": v(-58.05, 26.86) * mm, "end": v(-58.07, 26.94) * mm});
            skLineSegment(sketch, "E6539", {"start": v(-58.07, 26.94) * mm, "end": v(-58.09, 27) * mm});
            skLineSegment(sketch, "E6540", {"start": v(-58.09, 27) * mm, "end": v(-58.1, 27.08) * mm});
            skLineSegment(sketch, "E6541", {"start": v(-58.1, 27.08) * mm, "end": v(-58.13, 27.15) * mm});
            skLineSegment(sketch, "E6542", {"start": v(-58.13, 27.15) * mm, "end": v(-58.16, 27.22) * mm});
            skLineSegment(sketch, "E6543", {"start": v(-58.16, 27.22) * mm, "end": v(-58.19, 27.29) * mm});
            skLineSegment(sketch, "E6544", {"start": v(-58.19, 27.29) * mm, "end": v(-58.22, 27.36) * mm});
            skLineSegment(sketch, "E6545", {"start": v(-58.22, 27.36) * mm, "end": v(-58.25, 27.42) * mm});
            skLineSegment(sketch, "E6546", {"start": v(-58.25, 27.42) * mm, "end": v(-58.3, 27.49) * mm});
            skLineSegment(sketch, "E6547", {"start": v(-58.3, 27.49) * mm, "end": v(-58.33, 27.55) * mm});
            skLineSegment(sketch, "E6548", {"start": v(-58.33, 27.55) * mm, "end": v(-58.37, 27.62) * mm});
            skLineSegment(sketch, "E6549", {"start": v(-58.37, 27.62) * mm, "end": v(-58.41, 27.68) * mm});
            skLineSegment(sketch, "E6550", {"start": v(-58.41, 27.68) * mm, "end": v(-58.46, 27.74) * mm});
            skLineSegment(sketch, "E6551", {"start": v(-58.46, 27.74) * mm, "end": v(-58.5, 27.8) * mm});
            skLineSegment(sketch, "E6552", {"start": v(-58.5, 27.8) * mm, "end": v(-58.55, 27.85) * mm});
            skLineSegment(sketch, "E6553", {"start": v(-58.55, 27.85) * mm, "end": v(-58.6, 27.9) * mm});
            skLineSegment(sketch, "E6554", {"start": v(-58.6, 27.9) * mm, "end": v(-58.66, 27.96) * mm});
            skLineSegment(sketch, "E6555", {"start": v(-58.7, 28.01) * mm, "end": v(-58.77, 28.06) * mm});
            skLineSegment(sketch, "E6556", {"start": v(-58.77, 28.06) * mm, "end": v(-58.82, 28.1) * mm});
            skLineSegment(sketch, "E6557", {"start": v(-58.82, 28.1) * mm, "end": v(-58.88, 28.15) * mm});
            skLineSegment(sketch, "E6558", {"start": v(-58.88, 28.15) * mm, "end": v(-58.94, 28.2) * mm});
            skLineSegment(sketch, "E6559", {"start": v(-58.94, 28.2) * mm, "end": v(-59, 28.24) * mm});
            skLineSegment(sketch, "E6560", {"start": v(-59, 28.24) * mm, "end": v(-59.07, 28.28) * mm});
            skLineSegment(sketch, "E6561", {"start": v(-59.07, 28.28) * mm, "end": v(-59.13, 28.31) * mm});
            skLineSegment(sketch, "E6562", {"start": v(-59.13, 28.31) * mm, "end": v(-59.2, 28.35) * mm});
            skLineSegment(sketch, "E6563", {"start": v(-59.2, 28.35) * mm, "end": v(-59.27, 28.38) * mm});
            skLineSegment(sketch, "E6564", {"start": v(-59.27, 28.38) * mm, "end": v(-59.34, 28.4) * mm});
            skLineSegment(sketch, "E6565", {"start": v(-59.34, 28.4) * mm, "end": v(-59.4, 28.44) * mm});
            skLineSegment(sketch, "E6566", {"start": v(-59.48, 28.46) * mm, "end": v(-59.55, 28.48) * mm});
            skLineSegment(sketch, "E6567", {"start": v(-59.55, 28.48) * mm, "end": v(-59.62, 28.5) * mm});
            skLineSegment(sketch, "E6568", {"start": v(-59.62, 28.5) * mm, "end": v(-59.7, 28.52) * mm});
            skLineSegment(sketch, "E6569", {"start": v(-59.7, 28.52) * mm, "end": v(-59.77, 28.53) * mm});
            skLineSegment(sketch, "E6570", {"start": v(-59.77, 28.53) * mm, "end": v(-59.84, 28.55) * mm});
            skLineSegment(sketch, "E6571", {"start": v(-59.84, 28.55) * mm, "end": v(-59.91, 28.56) * mm});
            skLineSegment(sketch, "E6572", {"start": v(-59.91, 28.56) * mm, "end": v(-59.99, 28.56) * mm});
            skLineSegment(sketch, "E6573", {"start": v(-59.99, 28.56) * mm, "end": v(-60.06, 28.57) * mm});
            skLineSegment(sketch, "E6574", {"start": v(-60.06, 28.57) * mm, "end": v(-60.14, 28.57) * mm});
            skLineSegment(sketch, "E6575", {"start": v(-60.14, 28.57) * mm, "end": v(-60.21, 28.57) * mm});
            skLineSegment(sketch, "E6576", {"start": v(-60.21, 28.57) * mm, "end": v(-60.29, 28.57) * mm});
            skLineSegment(sketch, "E6577", {"start": v(-60.29, 28.57) * mm, "end": v(-60.36, 28.56) * mm});
            skLineSegment(sketch, "E6578", {"start": v(-60.36, 28.56) * mm, "end": v(-60.43, 28.55) * mm});
            skLineSegment(sketch, "E6579", {"start": v(-60.43, 28.55) * mm, "end": v(-60.5, 28.54) * mm});
            skLineSegment(sketch, "E6580", {"start": v(-60.5, 28.54) * mm, "end": v(-60.58, 28.53) * mm});
            skLineSegment(sketch, "E6581", {"start": v(-60.58, 28.53) * mm, "end": v(-60.65, 28.51) * mm});
            skLineSegment(sketch, "E6582", {"start": v(-60.73, 28.5) * mm, "end": v(-60.8, 28.47) * mm});
            skLineSegment(sketch, "E6583", {"start": v(-60.8, 28.47) * mm, "end": v(-60.87, 28.45) * mm});
            skLineSegment(sketch, "E6584", {"start": v(-60.87, 28.45) * mm, "end": v(-60.94, 28.42) * mm});
            skLineSegment(sketch, "E6585", {"start": v(-60.94, 28.42) * mm, "end": v(-61, 28.4) * mm});
            skLineSegment(sketch, "E6586", {"start": v(-61, 28.4) * mm, "end": v(-61.08, 28.36) * mm});
            skLineSegment(sketch, "E6587", {"start": v(-61.08, 28.36) * mm, "end": v(-61.14, 28.33) * mm});
            skLineSegment(sketch, "E6588", {"start": v(-61.14, 28.33) * mm, "end": v(-61.2, 28.3) * mm});
            skLineSegment(sketch, "E6589", {"start": v(-61.2, 28.3) * mm, "end": v(-61.27, 28.26) * mm});
            skLineSegment(sketch, "E6590", {"start": v(-61.34, 28.22) * mm, "end": v(-61.4, 28.17) * mm});
            skLineSegment(sketch, "E6591", {"start": v(-61.4, 28.17) * mm, "end": v(-61.46, 28.13) * mm});
            skLineSegment(sketch, "E6592", {"start": v(-61.46, 28.13) * mm, "end": v(-61.52, 28.08) * mm});
            skLineSegment(sketch, "E6593", {"start": v(-61.52, 28.08) * mm, "end": v(-61.57, 28.04) * mm});
            skLineSegment(sketch, "E6594", {"start": v(-61.57, 28.04) * mm, "end": v(-61.63, 27.99) * mm});
            skLineSegment(sketch, "E6595", {"start": v(-61.63, 27.99) * mm, "end": v(-61.68, 27.93) * mm});
            skLineSegment(sketch, "E6596", {"start": v(-61.68, 27.93) * mm, "end": v(-61.73, 27.88) * mm});
            skLineSegment(sketch, "E6597", {"start": v(-61.73, 27.88) * mm, "end": v(-61.78, 27.82) * mm});
            skLineSegment(sketch, "E6598", {"start": v(-61.78, 27.82) * mm, "end": v(-61.83, 27.77) * mm});
            skLineSegment(sketch, "E6599", {"start": v(-61.83, 27.77) * mm, "end": v(-61.88, 27.7) * mm});
            skLineSegment(sketch, "E6600", {"start": v(-61.88, 27.7) * mm, "end": v(-61.92, 27.65) * mm});
            skLineSegment(sketch, "E6601", {"start": v(-61.92, 27.65) * mm, "end": v(-61.96, 27.59) * mm});
            skLineSegment(sketch, "E6602", {"start": v(-61.96, 27.59) * mm, "end": v(-62, 27.52) * mm});
            skLineSegment(sketch, "E6603", {"start": v(-62, 27.52) * mm, "end": v(-62.04, 27.46) * mm});
            skLineSegment(sketch, "E6604", {"start": v(-62.04, 27.46) * mm, "end": v(-62.07, 27.4) * mm});
            skLineSegment(sketch, "E6605", {"start": v(-62.07, 27.4) * mm, "end": v(-62.1, 27.32) * mm});
            skLineSegment(sketch, "E6606", {"start": v(-62.14, 27.26) * mm, "end": v(-62.16, 27.19) * mm});
            skLineSegment(sketch, "E6607", {"start": v(-62.16, 27.19) * mm, "end": v(-62.19, 27.12) * mm});
            skLineSegment(sketch, "E6608", {"start": v(-62.19, 27.12) * mm, "end": v(-62.21, 27.05) * mm});
            skLineSegment(sketch, "E6609", {"start": v(-62.21, 27.05) * mm, "end": v(-62.23, 26.97) * mm});
            skLineSegment(sketch, "E6610", {"start": v(-62.23, 26.97) * mm, "end": v(-62.25, 26.9) * mm});
            skLineSegment(sketch, "E6611", {"start": v(-62.25, 26.9) * mm, "end": v(-62.27, 26.83) * mm});
            skLineSegment(sketch, "E6612", {"start": v(-62.27, 26.83) * mm, "end": v(-62.28, 26.75) * mm});
            skLineSegment(sketch, "E6613", {"start": v(-62.28, 26.75) * mm, "end": v(-62.29, 26.68) * mm});
            skLineSegment(sketch, "E6614", {"start": v(-62.29, 26.68) * mm, "end": v(-62.3, 26.6) * mm});
            skLineSegment(sketch, "E6615", {"start": v(-62.3, 26.6) * mm, "end": v(-62.3, 26.53) * mm});
            skLineSegment(sketch, "E6616", {"start": v(-62.3, 26.53) * mm, "end": v(-62.3, 26.46) * mm});
            skLineSegment(sketch, "E6617", {"start": v(-62.3, 26.46) * mm, "end": v(-62.3, 26.38) * mm});
            skLineSegment(sketch, "E6618", {"start": v(-62.3, 26.38) * mm, "end": v(-62.3, 26.3) * mm});
            skLineSegment(sketch, "E6619", {"start": v(-62.3, 26.3) * mm, "end": v(-62.3, 26.23) * mm});
            skLineSegment(sketch, "E6620", {"start": v(-62.3, 26.23) * mm, "end": v(-62.29, 26.16) * mm});
            skLineSegment(sketch, "E6621", {"start": v(-62.29, 26.16) * mm, "end": v(-62.28, 26.09) * mm});
            skLineSegment(sketch, "E6622", {"start": v(-62.28, 26.09) * mm, "end": v(-62.27, 26.01) * mm});
            skLineSegment(sketch, "E6623", {"start": v(-62.27, 26.01) * mm, "end": v(-62.25, 25.94) * mm});
            skLineSegment(sketch, "E6624", {"start": v(-62.23, 25.87) * mm, "end": v(-62.21, 25.8) * mm});
            skLineSegment(sketch, "E6625", {"start": v(-62.21, 25.8) * mm, "end": v(-62.19, 25.72) * mm});
            skLineSegment(sketch, "E6626", {"start": v(-62.19, 25.72) * mm, "end": v(-62.16, 25.65) * mm});
            skLineSegment(sketch, "E6627", {"start": v(-62.16, 25.65) * mm, "end": v(-62.14, 25.58) * mm});
            skLineSegment(sketch, "E6628", {"start": v(-62.14, 25.58) * mm, "end": v(-62.1, 25.52) * mm});
            skLineSegment(sketch, "E6629", {"start": v(-62.1, 25.52) * mm, "end": v(-62.07, 25.45) * mm});
            skLineSegment(sketch, "E6630", {"start": v(-62.07, 25.45) * mm, "end": v(-62.04, 25.38) * mm});
            skLineSegment(sketch, "E6631", {"start": v(-62.04, 25.38) * mm, "end": v(-62, 25.32) * mm});
            skLineSegment(sketch, "E6632", {"start": v(-62, 25.32) * mm, "end": v(-61.96, 25.25) * mm});
            skLineSegment(sketch, "E6633", {"start": v(-61.96, 25.25) * mm, "end": v(-61.92, 25.2) * mm});
            skLineSegment(sketch, "E6634", {"start": v(-61.92, 25.2) * mm, "end": v(-61.88, 25.13) * mm});
            skLineSegment(sketch, "E6635", {"start": v(-61.88, 25.13) * mm, "end": v(-61.83, 25.07) * mm});
            skLineSegment(sketch, "E6636", {"start": v(-61.83, 25.07) * mm, "end": v(-61.78, 25.02) * mm});
            skLineSegment(sketch, "E6637", {"start": v(-61.68, 24.9) * mm, "end": v(-61.63, 24.85) * mm});
            skLineSegment(sketch, "E6638", {"start": v(-61.63, 24.85) * mm, "end": v(-61.57, 24.8) * mm});
            skLineSegment(sketch, "E6639", {"start": v(-61.57, 24.8) * mm, "end": v(-61.52, 24.76) * mm});
            skLineSegment(sketch, "E6640", {"start": v(-61.52, 24.76) * mm, "end": v(-61.46, 24.7) * mm});
            skLineSegment(sketch, "E6641", {"start": v(-61.46, 24.7) * mm, "end": v(-61.4, 24.67) * mm});
            skLineSegment(sketch, "E6642", {"start": v(-61.4, 24.67) * mm, "end": v(-61.34, 24.62) * mm});
            skLineSegment(sketch, "E6643", {"start": v(-61.34, 24.62) * mm, "end": v(-61.27, 24.58) * mm});
            skLineSegment(sketch, "E6644", {"start": v(-61.27, 24.58) * mm, "end": v(-61.2, 24.55) * mm});
            skLineSegment(sketch, "E6645", {"start": v(-61.2, 24.55) * mm, "end": v(-61.14, 24.51) * mm});
            skLineSegment(sketch, "E6646", {"start": v(-61.14, 24.51) * mm, "end": v(-61.08, 24.48) * mm});
            skLineSegment(sketch, "E6647", {"start": v(-61.08, 24.48) * mm, "end": v(-61, 24.45) * mm});
            skLineSegment(sketch, "E6648", {"start": v(-61, 24.45) * mm, "end": v(-60.94, 24.42) * mm});
            skLineSegment(sketch, "E6649", {"start": v(-60.94, 24.42) * mm, "end": v(-60.87, 24.4) * mm});
            skLineSegment(sketch, "E6650", {"start": v(-60.87, 24.4) * mm, "end": v(-60.8, 24.37) * mm});
            skLineSegment(sketch, "E6651", {"start": v(-60.73, 24.35) * mm, "end": v(-60.65, 24.33) * mm});
            skLineSegment(sketch, "E6652", {"start": v(-60.65, 24.33) * mm, "end": v(-60.58, 24.31) * mm});
            skLineSegment(sketch, "E6653", {"start": v(-60.58, 24.31) * mm, "end": v(-60.5, 24.3) * mm});
            skLineSegment(sketch, "E6654", {"start": v(-60.5, 24.3) * mm, "end": v(-60.43, 24.29) * mm});
            skLineSegment(sketch, "E6655", {"start": v(-60.43, 24.29) * mm, "end": v(-60.36, 24.28) * mm});
            skLineSegment(sketch, "E6656", {"start": v(-60.36, 24.28) * mm, "end": v(-60.29, 24.27) * mm});
            skLineSegment(sketch, "E6657", {"start": v(-60.29, 24.27) * mm, "end": v(-60.21, 24.27) * mm});
            skLineSegment(sketch, "E6658", {"start": v(-60.21, 24.27) * mm, "end": v(-60.14, 24.27) * mm});
            skLineSegment(sketch, "E6659", {"start": v(-60.14, 24.27) * mm, "end": v(-60.06, 24.27) * mm});
            skLineSegment(sketch, "E6660", {"start": v(-60.06, 24.27) * mm, "end": v(-59.99, 24.28) * mm});
            skLineSegment(sketch, "E6661", {"start": v(-59.99, 24.28) * mm, "end": v(-59.91, 24.28) * mm});
            skLineSegment(sketch, "E6662", {"start": v(-59.91, 24.28) * mm, "end": v(-59.84, 24.3) * mm});
            skLineSegment(sketch, "E6663", {"start": v(-59.84, 24.3) * mm, "end": v(-59.77, 24.3) * mm});
            skLineSegment(sketch, "E6664", {"start": v(-59.77, 24.3) * mm, "end": v(-59.7, 24.32) * mm});
            skLineSegment(sketch, "E6665", {"start": v(-59.7, 24.32) * mm, "end": v(-59.62, 24.34) * mm});
            skLineSegment(sketch, "E6666", {"start": v(-59.62, 24.34) * mm, "end": v(-59.55, 24.36) * mm});
            skLineSegment(sketch, "E6667", {"start": v(-59.55, 24.36) * mm, "end": v(-59.48, 24.38) * mm});
            skLineSegment(sketch, "E6668", {"start": v(-59.48, 24.38) * mm, "end": v(-59.4, 24.4) * mm});
            skLineSegment(sketch, "E6669", {"start": v(-59.4, 24.4) * mm, "end": v(-59.34, 24.43) * mm});
            skLineSegment(sketch, "E6670", {"start": v(-59.27, 24.46) * mm, "end": v(-59.2, 24.5) * mm});
            skLineSegment(sketch, "E6671", {"start": v(-59.2, 24.5) * mm, "end": v(-59.13, 24.53) * mm});
            skLineSegment(sketch, "E6672", {"start": v(-59.13, 24.53) * mm, "end": v(-59.07, 24.56) * mm});
            skLineSegment(sketch, "E6673", {"start": v(-59.07, 24.56) * mm, "end": v(-59, 24.6) * mm});
            skLineSegment(sketch, "E6674", {"start": v(-59, 24.6) * mm, "end": v(-58.94, 24.64) * mm});
            skLineSegment(sketch, "E6675", {"start": v(-58.94, 24.64) * mm, "end": v(-58.88, 24.69) * mm});
            skLineSegment(sketch, "E6676", {"start": v(-58.88, 24.69) * mm, "end": v(-58.82, 24.73) * mm});
            skLineSegment(sketch, "E6677", {"start": v(-58.82, 24.73) * mm, "end": v(-58.77, 24.78) * mm});
            skLineSegment(sketch, "E6678", {"start": v(-58.77, 24.78) * mm, "end": v(-58.7, 24.83) * mm});
            skLineSegment(sketch, "E6679", {"start": v(-58.7, 24.83) * mm, "end": v(-58.66, 24.88) * mm});
            skLineSegment(sketch, "E6680", {"start": v(-58.66, 24.88) * mm, "end": v(-58.6, 24.93) * mm});
            skLineSegment(sketch, "E6681", {"start": v(-58.6, 24.93) * mm, "end": v(-58.55, 24.99) * mm});
            skLineSegment(sketch, "E6682", {"start": v(-58.55, 24.99) * mm, "end": v(-58.5, 25.04) * mm});
            skLineSegment(sketch, "E6683", {"start": v(-58.5, 25.04) * mm, "end": v(-58.46, 25.1) * mm});
            skLineSegment(sketch, "E6684", {"start": v(-58.46, 25.1) * mm, "end": v(-58.41, 25.16) * mm});
            skLineSegment(sketch, "E6685", {"start": v(-58.41, 25.16) * mm, "end": v(-58.37, 25.22) * mm});
            skLineSegment(sketch, "E6686", {"start": v(-58.3, 25.35) * mm, "end": v(-58.25, 25.42) * mm});
            skLineSegment(sketch, "E6687", {"start": v(-58.25, 25.42) * mm, "end": v(-58.22, 25.48) * mm});
            skLineSegment(sketch, "E6688", {"start": v(-58.22, 25.48) * mm, "end": v(-58.19, 25.55) * mm});
            skLineSegment(sketch, "E6689", {"start": v(-58.19, 25.55) * mm, "end": v(-58.16, 25.62) * mm});
            skLineSegment(sketch, "E6690", {"start": v(-58.16, 25.62) * mm, "end": v(-58.13, 25.69) * mm});
            skLineSegment(sketch, "E6691", {"start": v(-58.13, 25.69) * mm, "end": v(-58.1, 25.76) * mm});
            skLineSegment(sketch, "E6692", {"start": v(-58.1, 25.76) * mm, "end": v(-58.09, 25.83) * mm});
            skLineSegment(sketch, "E6693", {"start": v(-58.09, 25.83) * mm, "end": v(-58.07, 25.9) * mm});
            skLineSegment(sketch, "E6694", {"start": v(-58.05, 25.98) * mm, "end": v(-58.04, 26.05) * mm});
            skLineSegment(sketch, "E6695", {"start": v(-58.04, 26.05) * mm, "end": v(-58.03, 26.12) * mm});
            skLineSegment(sketch, "E6696", {"start": v(-58.03, 26.12) * mm, "end": v(-58.02, 26.2) * mm});
            skLineSegment(sketch, "E6697", {"start": v(-58.02, 26.2) * mm, "end": v(-58.01, 26.27) * mm});
            skLineSegment(sketch, "E6698", {"start": v(-58.01, 26.27) * mm, "end": v(-58, 26.35) * mm});
            skLineSegment(sketch, "E6699", {"start": v(-58, 26.35) * mm, "end": v(-58, 26.42) * mm});
            skLineSegment(sketch, "E6700", {"start": v(-58, -3.58) * mm, "end": v(-58, -3.5) * mm});
            skLineSegment(sketch, "E6701", {"start": v(-58, -3.5) * mm, "end": v(-58.01, -3.43) * mm});
            skLineSegment(sketch, "E6702", {"start": v(-58.01, -3.43) * mm, "end": v(-58.02, -3.36) * mm});
            skLineSegment(sketch, "E6703", {"start": v(-58.02, -3.36) * mm, "end": v(-58.03, -3.28) * mm});
            skLineSegment(sketch, "E6704", {"start": v(-58.03, -3.28) * mm, "end": v(-58.04, -3.2) * mm});
            skLineSegment(sketch, "E6705", {"start": v(-58.04, -3.2) * mm, "end": v(-58.05, -3.14) * mm});
            skLineSegment(sketch, "E6706", {"start": v(-58.05, -3.14) * mm, "end": v(-58.07, -3.06) * mm});
            skLineSegment(sketch, "E6707", {"start": v(-58.07, -3.06) * mm, "end": v(-58.09, -3) * mm});
            skLineSegment(sketch, "E6708", {"start": v(-58.09, -3) * mm, "end": v(-58.1, -2.92) * mm});
            skLineSegment(sketch, "E6709", {"start": v(-58.1, -2.92) * mm, "end": v(-58.13, -2.85) * mm});
            skLineSegment(sketch, "E6710", {"start": v(-58.13, -2.85) * mm, "end": v(-58.16, -2.78) * mm});
            skLineSegment(sketch, "E6711", {"start": v(-58.16, -2.78) * mm, "end": v(-58.19, -2.71) * mm});
            skLineSegment(sketch, "E6712", {"start": v(-58.25, -2.58) * mm, "end": v(-58.3, -2.51) * mm});
            skLineSegment(sketch, "E6713", {"start": v(-58.3, -2.51) * mm, "end": v(-58.33, -2.45) * mm});
            skLineSegment(sketch, "E6714", {"start": v(-58.33, -2.45) * mm, "end": v(-58.37, -2.38) * mm});
            skLineSegment(sketch, "E6715", {"start": v(-58.37, -2.38) * mm, "end": v(-58.41, -2.32) * mm});
            skLineSegment(sketch, "E6716", {"start": v(-58.41, -2.32) * mm, "end": v(-58.46, -2.26) * mm});
            skLineSegment(sketch, "E6717", {"start": v(-58.46, -2.26) * mm, "end": v(-58.5, -2.2) * mm});
            skLineSegment(sketch, "E6718", {"start": v(-58.5, -2.2) * mm, "end": v(-58.55, -2.15) * mm});
            skLineSegment(sketch, "E6719", {"start": v(-58.55, -2.15) * mm, "end": v(-58.6, -2.1) * mm});
            skLineSegment(sketch, "E6720", {"start": v(-58.6, -2.1) * mm, "end": v(-58.66, -2.04) * mm});
            skLineSegment(sketch, "E6721", {"start": v(-58.66, -2.04) * mm, "end": v(-58.7, -1.99) * mm});
            skLineSegment(sketch, "E6722", {"start": v(-58.7, -1.99) * mm, "end": v(-58.77, -1.94) * mm});
            skLineSegment(sketch, "E6723", {"start": v(-58.77, -1.94) * mm, "end": v(-58.82, -1.9) * mm});
            skLineSegment(sketch, "E6724", {"start": v(-58.82, -1.9) * mm, "end": v(-58.88, -1.85) * mm});
            skLineSegment(sketch, "E6725", {"start": v(-58.88, -1.85) * mm, "end": v(-58.94, -1.8) * mm});
            skLineSegment(sketch, "E6726", {"start": v(-58.94, -1.8) * mm, "end": v(-59, -1.76) * mm});
            skLineSegment(sketch, "E6727", {"start": v(-59, -1.76) * mm, "end": v(-59.07, -1.72) * mm});
            skLineSegment(sketch, "E6728", {"start": v(-59.07, -1.72) * mm, "end": v(-59.13, -1.69) * mm});
            skLineSegment(sketch, "E6729", {"start": v(-59.13, -1.69) * mm, "end": v(-59.2, -1.65) * mm});
            skLineSegment(sketch, "E6730", {"start": v(-59.27, -1.62) * mm, "end": v(-59.34, -1.6) * mm});
            skLineSegment(sketch, "E6731", {"start": v(-59.34, -1.6) * mm, "end": v(-59.4, -1.56) * mm});
            skLineSegment(sketch, "E6732", {"start": v(-59.4, -1.56) * mm, "end": v(-59.48, -1.54) * mm});
            skLineSegment(sketch, "E6733", {"start": v(-59.48, -1.54) * mm, "end": v(-59.55, -1.52) * mm});
            skLineSegment(sketch, "E6734", {"start": v(-59.55, -1.52) * mm, "end": v(-59.62, -1.5) * mm});
            skLineSegment(sketch, "E6735", {"start": v(-59.62, -1.5) * mm, "end": v(-59.7, -1.48) * mm});
            skLineSegment(sketch, "E6736", {"start": v(-59.7, -1.48) * mm, "end": v(-59.77, -1.47) * mm});
            skLineSegment(sketch, "E6737", {"start": v(-59.77, -1.47) * mm, "end": v(-59.84, -1.45) * mm});
            skLineSegment(sketch, "E6738", {"start": v(-59.84, -1.45) * mm, "end": v(-59.91, -1.44) * mm});
            skLineSegment(sketch, "E6739", {"start": v(-59.91, -1.44) * mm, "end": v(-59.99, -1.44) * mm});
            skLineSegment(sketch, "E6740", {"start": v(-59.99, -1.44) * mm, "end": v(-60.06, -1.43) * mm});
            skLineSegment(sketch, "E6741", {"start": v(-60.06, -1.43) * mm, "end": v(-60.14, -1.43) * mm});
            skLineSegment(sketch, "E6742", {"start": v(-60.14, -1.43) * mm, "end": v(-60.21, -1.43) * mm});
            skLineSegment(sketch, "E6743", {"start": v(-60.21, -1.43) * mm, "end": v(-60.29, -1.43) * mm});
            skLineSegment(sketch, "E6744", {"start": v(-60.29, -1.43) * mm, "end": v(-60.36, -1.44) * mm});
            skLineSegment(sketch, "E6745", {"start": v(-60.36, -1.44) * mm, "end": v(-60.43, -1.45) * mm});
            skLineSegment(sketch, "E6746", {"start": v(-60.43, -1.45) * mm, "end": v(-60.5, -1.46) * mm});
            skLineSegment(sketch, "E6747", {"start": v(-60.5, -1.46) * mm, "end": v(-60.58, -1.47) * mm});
            skLineSegment(sketch, "E6748", {"start": v(-60.58, -1.47) * mm, "end": v(-60.65, -1.49) * mm});
            skLineSegment(sketch, "E6749", {"start": v(-60.65, -1.49) * mm, "end": v(-60.73, -1.5) * mm});
            skLineSegment(sketch, "E6750", {"start": v(-60.73, -1.5) * mm, "end": v(-60.8, -1.53) * mm});
            skLineSegment(sketch, "E6751", {"start": v(-60.8, -1.53) * mm, "end": v(-60.87, -1.55) * mm});
            skLineSegment(sketch, "E6752", {"start": v(-60.87, -1.55) * mm, "end": v(-60.94, -1.58) * mm});
            skLineSegment(sketch, "E6753", {"start": v(-60.94, -1.58) * mm, "end": v(-61, -1.6) * mm});
            skLineSegment(sketch, "E6754", {"start": v(-61, -1.6) * mm, "end": v(-61.08, -1.64) * mm});
            skLineSegment(sketch, "E6755", {"start": v(-61.08, -1.64) * mm, "end": v(-61.14, -1.67) * mm});
            skLineSegment(sketch, "E6756", {"start": v(-61.14, -1.67) * mm, "end": v(-61.2, -1.7) * mm});
            skLineSegment(sketch, "E6757", {"start": v(-61.2, -1.7) * mm, "end": v(-61.27, -1.74) * mm});
            skLineSegment(sketch, "E6758", {"start": v(-61.27, -1.74) * mm, "end": v(-61.34, -1.78) * mm});
            skLineSegment(sketch, "E6759", {"start": v(-61.34, -1.78) * mm, "end": v(-61.4, -1.83) * mm});
            skLineSegment(sketch, "E6760", {"start": v(-61.4, -1.83) * mm, "end": v(-61.46, -1.87) * mm});
            skLineSegment(sketch, "E6761", {"start": v(-61.46, -1.87) * mm, "end": v(-61.52, -1.92) * mm});
            skLineSegment(sketch, "E6762", {"start": v(-61.52, -1.92) * mm, "end": v(-61.57, -1.96) * mm});
            skLineSegment(sketch, "E6763", {"start": v(-61.57, -1.96) * mm, "end": v(-61.63, -2.01) * mm});
            skLineSegment(sketch, "E6764", {"start": v(-61.63, -2.01) * mm, "end": v(-61.68, -2.07) * mm});
            skLineSegment(sketch, "E6765", {"start": v(-61.68, -2.07) * mm, "end": v(-61.73, -2.12) * mm});
            skLineSegment(sketch, "E6766", {"start": v(-61.73, -2.12) * mm, "end": v(-61.78, -2.18) * mm});
            skLineSegment(sketch, "E6767", {"start": v(-61.78, -2.18) * mm, "end": v(-61.83, -2.23) * mm});
            skLineSegment(sketch, "E6768", {"start": v(-61.83, -2.23) * mm, "end": v(-61.88, -2.3) * mm});
            skLineSegment(sketch, "E6769", {"start": v(-61.96, -2.41) * mm, "end": v(-62, -2.48) * mm});
            skLineSegment(sketch, "E6770", {"start": v(-62, -2.48) * mm, "end": v(-62.04, -2.54) * mm});
            skLineSegment(sketch, "E6771", {"start": v(-62.04, -2.54) * mm, "end": v(-62.07, -2.6) * mm});
            skLineSegment(sketch, "E6772", {"start": v(-62.07, -2.6) * mm, "end": v(-62.1, -2.68) * mm});
            skLineSegment(sketch, "E6773", {"start": v(-62.1, -2.68) * mm, "end": v(-62.14, -2.74) * mm});
            skLineSegment(sketch, "E6774", {"start": v(-62.14, -2.74) * mm, "end": v(-62.16, -2.81) * mm});
            skLineSegment(sketch, "E6775", {"start": v(-62.16, -2.81) * mm, "end": v(-62.19, -2.88) * mm});
            skLineSegment(sketch, "E6776", {"start": v(-62.19, -2.88) * mm, "end": v(-62.21, -2.95) * mm});
            skLineSegment(sketch, "E6777", {"start": v(-62.21, -2.95) * mm, "end": v(-62.23, -3.03) * mm});
            skLineSegment(sketch, "E6778", {"start": v(-62.23, -3.03) * mm, "end": v(-62.25, -3.1) * mm});
            skLineSegment(sketch, "E6779", {"start": v(-62.27, -3.17) * mm, "end": v(-62.28, -3.25) * mm});
            skLineSegment(sketch, "E6780", {"start": v(-62.28, -3.25) * mm, "end": v(-62.29, -3.32) * mm});
            skLineSegment(sketch, "E6781", {"start": v(-62.29, -3.32) * mm, "end": v(-62.3, -3.4) * mm});
            skLineSegment(sketch, "E6782", {"start": v(-62.3, -3.4) * mm, "end": v(-62.3, -3.47) * mm});
            skLineSegment(sketch, "E6783", {"start": v(-62.3, -3.47) * mm, "end": v(-62.3, -3.54) * mm});
            skLineSegment(sketch, "E6784", {"start": v(-62.3, -3.54) * mm, "end": v(-62.3, -3.62) * mm});
            skLineSegment(sketch, "E6785", {"start": v(-62.3, -3.62) * mm, "end": v(-62.3, -3.7) * mm});
            skLineSegment(sketch, "E6786", {"start": v(-62.3, -3.7) * mm, "end": v(-62.3, -3.77) * mm});
            skLineSegment(sketch, "E6787", {"start": v(-62.3, -3.77) * mm, "end": v(-62.29, -3.84) * mm});
            skLineSegment(sketch, "E6788", {"start": v(-62.29, -3.84) * mm, "end": v(-62.28, -3.91) * mm});
            skLineSegment(sketch, "E6789", {"start": v(-62.28, -3.91) * mm, "end": v(-62.27, -3.99) * mm});
            skLineSegment(sketch, "E6790", {"start": v(-62.27, -3.99) * mm, "end": v(-62.25, -4.06) * mm});
            skLineSegment(sketch, "E6791", {"start": v(-62.25, -4.06) * mm, "end": v(-62.23, -4.13) * mm});
            skLineSegment(sketch, "E6792", {"start": v(-62.23, -4.13) * mm, "end": v(-62.21, -4.2) * mm});
            skLineSegment(sketch, "E6793", {"start": v(-62.21, -4.2) * mm, "end": v(-62.19, -4.28) * mm});
            skLineSegment(sketch, "E6794", {"start": v(-62.19, -4.28) * mm, "end": v(-62.16, -4.35) * mm});
            skLineSegment(sketch, "E6795", {"start": v(-62.16, -4.35) * mm, "end": v(-62.14, -4.42) * mm});
            skLineSegment(sketch, "E6796", {"start": v(-62.14, -4.42) * mm, "end": v(-62.1, -4.48) * mm});
            skLineSegment(sketch, "E6797", {"start": v(-62.1, -4.48) * mm, "end": v(-62.07, -4.55) * mm});
            skLineSegment(sketch, "E6798", {"start": v(-62.07, -4.55) * mm, "end": v(-62.04, -4.62) * mm});
            skLineSegment(sketch, "E6799", {"start": v(-62.04, -4.62) * mm, "end": v(-62, -4.68) * mm});
            skLineSegment(sketch, "E6800", {"start": v(-62, -4.68) * mm, "end": v(-61.96, -4.75) * mm});
            skLineSegment(sketch, "E6801", {"start": v(-61.96, -4.75) * mm, "end": v(-61.92, -4.8) * mm});
            skLineSegment(sketch, "E6802", {"start": v(-61.92, -4.8) * mm, "end": v(-61.88, -4.87) * mm});
            skLineSegment(sketch, "E6803", {"start": v(-61.88, -4.87) * mm, "end": v(-61.83, -4.93) * mm});
            skLineSegment(sketch, "E6804", {"start": v(-61.83, -4.93) * mm, "end": v(-61.78, -4.98) * mm});
            skLineSegment(sketch, "E6805", {"start": v(-61.78, -4.98) * mm, "end": v(-61.73, -5.04) * mm});
            skLineSegment(sketch, "E6806", {"start": v(-61.73, -5.04) * mm, "end": v(-61.68, -5.1) * mm});
            skLineSegment(sketch, "E6807", {"start": v(-61.68, -5.1) * mm, "end": v(-61.63, -5.15) * mm});
            skLineSegment(sketch, "E6808", {"start": v(-61.63, -5.15) * mm, "end": v(-61.57, -5.2) * mm});
            skLineSegment(sketch, "E6809", {"start": v(-61.57, -5.2) * mm, "end": v(-61.52, -5.24) * mm});
            skLineSegment(sketch, "E6810", {"start": v(-61.52, -5.24) * mm, "end": v(-61.46, -5.3) * mm});
            skLineSegment(sketch, "E6811", {"start": v(-61.46, -5.3) * mm, "end": v(-61.4, -5.33) * mm});
            skLineSegment(sketch, "E6812", {"start": v(-61.4, -5.33) * mm, "end": v(-61.34, -5.38) * mm});
            skLineSegment(sketch, "E6813", {"start": v(-61.34, -5.38) * mm, "end": v(-61.27, -5.42) * mm});
            skLineSegment(sketch, "E6814", {"start": v(-61.2, -5.45) * mm, "end": v(-61.14, -5.49) * mm});
            skLineSegment(sketch, "E6815", {"start": v(-61.14, -5.49) * mm, "end": v(-61.08, -5.52) * mm});
            skLineSegment(sketch, "E6816", {"start": v(-61.08, -5.52) * mm, "end": v(-61, -5.55) * mm});
            skLineSegment(sketch, "E6817", {"start": v(-61, -5.55) * mm, "end": v(-60.94, -5.58) * mm});
            skLineSegment(sketch, "E6818", {"start": v(-60.94, -5.58) * mm, "end": v(-60.87, -5.6) * mm});
            skLineSegment(sketch, "E6819", {"start": v(-60.87, -5.6) * mm, "end": v(-60.8, -5.63) * mm});
            skLineSegment(sketch, "E6820", {"start": v(-60.8, -5.63) * mm, "end": v(-60.73, -5.65) * mm});
            skLineSegment(sketch, "E6821", {"start": v(-60.73, -5.65) * mm, "end": v(-60.65, -5.67) * mm});
            skLineSegment(sketch, "E6822", {"start": v(-60.65, -5.67) * mm, "end": v(-60.58, -5.69) * mm});
            skLineSegment(sketch, "E6823", {"start": v(-60.58, -5.69) * mm, "end": v(-60.5, -5.7) * mm});
            skLineSegment(sketch, "E6824", {"start": v(-60.5, -5.7) * mm, "end": v(-60.43, -5.71) * mm});
            skLineSegment(sketch, "E6825", {"start": v(-60.43, -5.71) * mm, "end": v(-60.36, -5.72) * mm});
            skLineSegment(sketch, "E6826", {"start": v(-60.36, -5.72) * mm, "end": v(-60.29, -5.73) * mm});
            skLineSegment(sketch, "E6827", {"start": v(-60.29, -5.73) * mm, "end": v(-60.21, -5.73) * mm});
            skLineSegment(sketch, "E6828", {"start": v(-60.21, -5.73) * mm, "end": v(-60.14, -5.73) * mm});
            skLineSegment(sketch, "E6829", {"start": v(-60.14, -5.73) * mm, "end": v(-60.06, -5.73) * mm});
            skLineSegment(sketch, "E6830", {"start": v(-60.06, -5.73) * mm, "end": v(-59.99, -5.72) * mm});
            skLineSegment(sketch, "E6831", {"start": v(-59.99, -5.72) * mm, "end": v(-59.91, -5.72) * mm});
            skLineSegment(sketch, "E6832", {"start": v(-59.91, -5.72) * mm, "end": v(-59.84, -5.7) * mm});
            skLineSegment(sketch, "E6833", {"start": v(-59.84, -5.7) * mm, "end": v(-59.77, -5.7) * mm});
            skLineSegment(sketch, "E6834", {"start": v(-59.77, -5.7) * mm, "end": v(-59.7, -5.68) * mm});
            skLineSegment(sketch, "E6835", {"start": v(-59.7, -5.68) * mm, "end": v(-59.62, -5.66) * mm});
            skLineSegment(sketch, "E6836", {"start": v(-59.62, -5.66) * mm, "end": v(-59.55, -5.64) * mm});
            skLineSegment(sketch, "E6837", {"start": v(-59.55, -5.64) * mm, "end": v(-59.48, -5.62) * mm});
            skLineSegment(sketch, "E6838", {"start": v(-59.4, -5.6) * mm, "end": v(-59.34, -5.57) * mm});
            skLineSegment(sketch, "E6839", {"start": v(-59.34, -5.57) * mm, "end": v(-59.27, -5.54) * mm});
            skLineSegment(sketch, "E6840", {"start": v(-59.27, -5.54) * mm, "end": v(-59.2, -5.5) * mm});
            skLineSegment(sketch, "E6841", {"start": v(-59.2, -5.5) * mm, "end": v(-59.13, -5.47) * mm});
            skLineSegment(sketch, "E6842", {"start": v(-59.13, -5.47) * mm, "end": v(-59.07, -5.44) * mm});
            skLineSegment(sketch, "E6843", {"start": v(-59.07, -5.44) * mm, "end": v(-59, -5.4) * mm});
            skLineSegment(sketch, "E6844", {"start": v(-59, -5.4) * mm, "end": v(-58.94, -5.36) * mm});
            skLineSegment(sketch, "E6845", {"start": v(-58.94, -5.36) * mm, "end": v(-58.88, -5.31) * mm});
            skLineSegment(sketch, "E6846", {"start": v(-58.88, -5.31) * mm, "end": v(-58.82, -5.27) * mm});
            skLineSegment(sketch, "E6847", {"start": v(-58.77, -5.22) * mm, "end": v(-58.7, -5.17) * mm});
            skLineSegment(sketch, "E6848", {"start": v(-58.7, -5.17) * mm, "end": v(-58.66, -5.12) * mm});
            skLineSegment(sketch, "E6849", {"start": v(-58.66, -5.12) * mm, "end": v(-58.6, -5.07) * mm});
            skLineSegment(sketch, "E6850", {"start": v(-58.6, -5.07) * mm, "end": v(-58.55, -5.01) * mm});
            skLineSegment(sketch, "E6851", {"start": v(-58.55, -5.01) * mm, "end": v(-58.5, -4.96) * mm});
            skLineSegment(sketch, "E6852", {"start": v(-58.5, -4.96) * mm, "end": v(-58.46, -4.9) * mm});
            skLineSegment(sketch, "E6853", {"start": v(-58.46, -4.9) * mm, "end": v(-58.41, -4.84) * mm});
            skLineSegment(sketch, "E6854", {"start": v(-58.41, -4.84) * mm, "end": v(-58.37, -4.78) * mm});
            skLineSegment(sketch, "E6855", {"start": v(-58.37, -4.78) * mm, "end": v(-58.33, -4.71) * mm});
            skLineSegment(sketch, "E6856", {"start": v(-58.33, -4.71) * mm, "end": v(-58.3, -4.65) * mm});
            skLineSegment(sketch, "E6857", {"start": v(-58.3, -4.65) * mm, "end": v(-58.25, -4.58) * mm});
            skLineSegment(sketch, "E6858", {"start": v(-58.25, -4.58) * mm, "end": v(-58.22, -4.52) * mm});
            skLineSegment(sketch, "E6859", {"start": v(-58.22, -4.52) * mm, "end": v(-58.19, -4.45) * mm});
            skLineSegment(sketch, "E6860", {"start": v(-58.19, -4.45) * mm, "end": v(-58.16, -4.38) * mm});
            skLineSegment(sketch, "E6861", {"start": v(-58.16, -4.38) * mm, "end": v(-58.13, -4.31) * mm});
            skLineSegment(sketch, "E6862", {"start": v(-58.13, -4.31) * mm, "end": v(-58.1, -4.24) * mm});
            skLineSegment(sketch, "E6863", {"start": v(-58.1, -4.24) * mm, "end": v(-58.09, -4.17) * mm});
            skLineSegment(sketch, "E6864", {"start": v(-58.09, -4.17) * mm, "end": v(-58.07, -4.1) * mm});
            skLineSegment(sketch, "E6865", {"start": v(-58.07, -4.1) * mm, "end": v(-58.05, -4.02) * mm});
            skLineSegment(sketch, "E6866", {"start": v(-58.05, -4.02) * mm, "end": v(-58.04, -3.95) * mm});
            skLineSegment(sketch, "E6867", {"start": v(-58.04, -3.95) * mm, "end": v(-58.03, -3.88) * mm});
            skLineSegment(sketch, "E6868", {"start": v(-58.03, -3.88) * mm, "end": v(-58.02, -3.8) * mm});
            skLineSegment(sketch, "E6869", {"start": v(-58.02, -3.8) * mm, "end": v(-58.01, -3.73) * mm});
            skLineSegment(sketch, "E6870", {"start": v(-58.01, -3.73) * mm, "end": v(-58, -3.65) * mm});
            skLineSegment(sketch, "E6871", {"start": v(-58, -3.65) * mm, "end": v(-58, -3.58) * mm});
            skLineSegment(sketch, "E6872", {"start": v(-68, -3.58) * mm, "end": v(-68, -3.5) * mm});
            skLineSegment(sketch, "E6873", {"start": v(-68, -3.5) * mm, "end": v(-68.01, -3.43) * mm});
            skLineSegment(sketch, "E6874", {"start": v(-68.01, -3.43) * mm, "end": v(-68.02, -3.36) * mm});
            skLineSegment(sketch, "E6875", {"start": v(-68.02, -3.36) * mm, "end": v(-68.03, -3.28) * mm});
            skLineSegment(sketch, "E6876", {"start": v(-68.03, -3.28) * mm, "end": v(-68.04, -3.2) * mm});
            skLineSegment(sketch, "E6877", {"start": v(-68.05, -3.14) * mm, "end": v(-68.07, -3.06) * mm});
            skLineSegment(sketch, "E6878", {"start": v(-68.07, -3.06) * mm, "end": v(-68.09, -3) * mm});
            skLineSegment(sketch, "E6879", {"start": v(-68.09, -3) * mm, "end": v(-68.1, -2.92) * mm});
            skLineSegment(sketch, "E6880", {"start": v(-68.1, -2.92) * mm, "end": v(-68.13, -2.85) * mm});
            skLineSegment(sketch, "E6881", {"start": v(-68.13, -2.85) * mm, "end": v(-68.16, -2.78) * mm});
            skLineSegment(sketch, "E6882", {"start": v(-68.16, -2.78) * mm, "end": v(-68.19, -2.71) * mm});
            skLineSegment(sketch, "E6883", {"start": v(-68.19, -2.71) * mm, "end": v(-68.22, -2.64) * mm});
            skLineSegment(sketch, "E6884", {"start": v(-68.22, -2.64) * mm, "end": v(-68.25, -2.58) * mm});
            skLineSegment(sketch, "E6885", {"start": v(-68.25, -2.58) * mm, "end": v(-68.3, -2.51) * mm});
            skLineSegment(sketch, "E6886", {"start": v(-68.37, -2.38) * mm, "end": v(-68.41, -2.32) * mm});
            skLineSegment(sketch, "E6887", {"start": v(-68.41, -2.32) * mm, "end": v(-68.46, -2.26) * mm});
            skLineSegment(sketch, "E6888", {"start": v(-68.46, -2.26) * mm, "end": v(-68.5, -2.2) * mm});
            skLineSegment(sketch, "E6889", {"start": v(-68.5, -2.2) * mm, "end": v(-68.55, -2.15) * mm});
            skLineSegment(sketch, "E6890", {"start": v(-68.55, -2.15) * mm, "end": v(-68.6, -2.1) * mm});
            skLineSegment(sketch, "E6891", {"start": v(-68.6, -2.1) * mm, "end": v(-68.66, -2.04) * mm});
            skLineSegment(sketch, "E6892", {"start": v(-68.66, -2.04) * mm, "end": v(-68.7, -1.99) * mm});
            skLineSegment(sketch, "E6893", {"start": v(-68.7, -1.99) * mm, "end": v(-68.77, -1.94) * mm});
            skLineSegment(sketch, "E6894", {"start": v(-68.77, -1.94) * mm, "end": v(-68.82, -1.9) * mm});
            skLineSegment(sketch, "E6895", {"start": v(-68.82, -1.9) * mm, "end": v(-68.88, -1.85) * mm});
            skLineSegment(sketch, "E6896", {"start": v(-68.88, -1.85) * mm, "end": v(-68.94, -1.8) * mm});
            skLineSegment(sketch, "E6897", {"start": v(-68.94, -1.8) * mm, "end": v(-69, -1.76) * mm});
            skLineSegment(sketch, "E6898", {"start": v(-69, -1.76) * mm, "end": v(-69.07, -1.72) * mm});
            skLineSegment(sketch, "E6899", {"start": v(-69.07, -1.72) * mm, "end": v(-69.13, -1.69) * mm});
            skLineSegment(sketch, "E6900", {"start": v(-69.13, -1.69) * mm, "end": v(-69.2, -1.65) * mm});
            skLineSegment(sketch, "E6901", {"start": v(-69.2, -1.65) * mm, "end": v(-69.27, -1.62) * mm});
            skLineSegment(sketch, "E6902", {"start": v(-69.27, -1.62) * mm, "end": v(-69.34, -1.6) * mm});
            skLineSegment(sketch, "E6903", {"start": v(-69.34, -1.6) * mm, "end": v(-69.4, -1.56) * mm});
            skLineSegment(sketch, "E6904", {"start": v(-69.48, -1.54) * mm, "end": v(-69.55, -1.52) * mm});
            skLineSegment(sketch, "E6905", {"start": v(-69.55, -1.52) * mm, "end": v(-69.62, -1.5) * mm});
            skLineSegment(sketch, "E6906", {"start": v(-69.62, -1.5) * mm, "end": v(-69.7, -1.48) * mm});
            skLineSegment(sketch, "E6907", {"start": v(-69.7, -1.48) * mm, "end": v(-69.77, -1.47) * mm});
            skLineSegment(sketch, "E6908", {"start": v(-69.77, -1.47) * mm, "end": v(-69.84, -1.45) * mm});
            skLineSegment(sketch, "E6909", {"start": v(-69.84, -1.45) * mm, "end": v(-69.91, -1.44) * mm});
            skLineSegment(sketch, "E6910", {"start": v(-69.91, -1.44) * mm, "end": v(-69.99, -1.44) * mm});
            skLineSegment(sketch, "E6911", {"start": v(-69.99, -1.44) * mm, "end": v(-70.06, -1.43) * mm});
            skLineSegment(sketch, "E6912", {"start": v(-70.06, -1.43) * mm, "end": v(-70.14, -1.43) * mm});
            skLineSegment(sketch, "E6913", {"start": v(-70.14, -1.43) * mm, "end": v(-70.21, -1.43) * mm});
            skLineSegment(sketch, "E6914", {"start": v(-70.21, -1.43) * mm, "end": v(-70.29, -1.43) * mm});
            skLineSegment(sketch, "E6915", {"start": v(-70.29, -1.43) * mm, "end": v(-70.36, -1.44) * mm});
            skLineSegment(sketch, "E6916", {"start": v(-70.36, -1.44) * mm, "end": v(-70.43, -1.45) * mm});
            skLineSegment(sketch, "E6917", {"start": v(-70.43, -1.45) * mm, "end": v(-70.5, -1.46) * mm});
            skLineSegment(sketch, "E6918", {"start": v(-70.5, -1.46) * mm, "end": v(-70.58, -1.47) * mm});
            skLineSegment(sketch, "E6919", {"start": v(-70.58, -1.47) * mm, "end": v(-70.65, -1.49) * mm});
            skLineSegment(sketch, "E6920", {"start": v(-70.65, -1.49) * mm, "end": v(-70.73, -1.5) * mm});
            skLineSegment(sketch, "E6921", {"start": v(-70.73, -1.5) * mm, "end": v(-70.8, -1.53) * mm});
            skLineSegment(sketch, "E6922", {"start": v(-70.8, -1.53) * mm, "end": v(-70.87, -1.55) * mm});
            skLineSegment(sketch, "E6923", {"start": v(-70.87, -1.55) * mm, "end": v(-70.94, -1.58) * mm});
            skLineSegment(sketch, "E6924", {"start": v(-71, -1.6) * mm, "end": v(-71.08, -1.64) * mm});
            skLineSegment(sketch, "E6925", {"start": v(-71.08, -1.64) * mm, "end": v(-71.14, -1.67) * mm});
            skLineSegment(sketch, "E6926", {"start": v(-71.14, -1.67) * mm, "end": v(-71.2, -1.7) * mm});
            skLineSegment(sketch, "E6927", {"start": v(-71.2, -1.7) * mm, "end": v(-71.27, -1.74) * mm});
            skLineSegment(sketch, "E6928", {"start": v(-71.27, -1.74) * mm, "end": v(-71.34, -1.78) * mm});
            skLineSegment(sketch, "E6929", {"start": v(-71.34, -1.78) * mm, "end": v(-71.4, -1.83) * mm});
            skLineSegment(sketch, "E6930", {"start": v(-71.4, -1.83) * mm, "end": v(-71.46, -1.87) * mm});
            skLineSegment(sketch, "E6931", {"start": v(-71.46, -1.87) * mm, "end": v(-71.52, -1.92) * mm});
            skLineSegment(sketch, "E6932", {"start": v(-71.52, -1.92) * mm, "end": v(-71.57, -1.96) * mm});
            skLineSegment(sketch, "E6933", {"start": v(-71.57, -1.96) * mm, "end": v(-71.63, -2.01) * mm});
            skLineSegment(sketch, "E6934", {"start": v(-71.63, -2.01) * mm, "end": v(-71.68, -2.07) * mm});
            skLineSegment(sketch, "E6935", {"start": v(-71.68, -2.07) * mm, "end": v(-71.73, -2.12) * mm});
            skLineSegment(sketch, "E6936", {"start": v(-71.73, -2.12) * mm, "end": v(-71.78, -2.18) * mm});
            skLineSegment(sketch, "E6937", {"start": v(-71.83, -2.23) * mm, "end": v(-71.88, -2.3) * mm});
            skLineSegment(sketch, "E6938", {"start": v(-71.88, -2.3) * mm, "end": v(-71.92, -2.35) * mm});
            skLineSegment(sketch, "E6939", {"start": v(-71.92, -2.35) * mm, "end": v(-71.96, -2.41) * mm});
            skLineSegment(sketch, "E6940", {"start": v(-71.96, -2.41) * mm, "end": v(-72, -2.48) * mm});
            skLineSegment(sketch, "E6941", {"start": v(-72.07, -2.6) * mm, "end": v(-72.1, -2.68) * mm});
            skLineSegment(sketch, "E6942", {"start": v(-72.1, -2.68) * mm, "end": v(-72.14, -2.74) * mm});
            skLineSegment(sketch, "E6943", {"start": v(-72.14, -2.74) * mm, "end": v(-72.16, -2.81) * mm});
            skLineSegment(sketch, "E6944", {"start": v(-72.16, -2.81) * mm, "end": v(-72.19, -2.88) * mm});
            skLineSegment(sketch, "E6945", {"start": v(-72.19, -2.88) * mm, "end": v(-72.21, -2.95) * mm});
            skLineSegment(sketch, "E6946", {"start": v(-72.21, -2.95) * mm, "end": v(-72.23, -3.03) * mm});
            skLineSegment(sketch, "E6947", {"start": v(-72.23, -3.03) * mm, "end": v(-72.25, -3.1) * mm});
            skLineSegment(sketch, "E6948", {"start": v(-72.25, -3.1) * mm, "end": v(-72.27, -3.17) * mm});
            skLineSegment(sketch, "E6949", {"start": v(-72.27, -3.17) * mm, "end": v(-72.28, -3.25) * mm});
            skLineSegment(sketch, "E6950", {"start": v(-72.28, -3.25) * mm, "end": v(-72.29, -3.32) * mm});
            skLineSegment(sketch, "E6951", {"start": v(-72.29, -3.32) * mm, "end": v(-72.3, -3.4) * mm});
            skLineSegment(sketch, "E6952", {"start": v(-72.3, -3.4) * mm, "end": v(-72.3, -3.47) * mm});
            skLineSegment(sketch, "E6953", {"start": v(-72.3, -3.47) * mm, "end": v(-72.3, -3.54) * mm});
            skLineSegment(sketch, "E6954", {"start": v(-72.3, -3.54) * mm, "end": v(-72.3, -3.62) * mm});
            skLineSegment(sketch, "E6955", {"start": v(-72.3, -3.62) * mm, "end": v(-72.3, -3.7) * mm});
            skLineSegment(sketch, "E6956", {"start": v(-72.3, -3.7) * mm, "end": v(-72.3, -3.77) * mm});
            skLineSegment(sketch, "E6957", {"start": v(-72.3, -3.77) * mm, "end": v(-72.29, -3.84) * mm});
            skLineSegment(sketch, "E6958", {"start": v(-72.29, -3.84) * mm, "end": v(-72.28, -3.91) * mm});
            skLineSegment(sketch, "E6959", {"start": v(-72.28, -3.91) * mm, "end": v(-72.27, -3.99) * mm});
            skLineSegment(sketch, "E6960", {"start": v(-72.27, -3.99) * mm, "end": v(-72.25, -4.06) * mm});
            skLineSegment(sketch, "E6961", {"start": v(-72.25, -4.06) * mm, "end": v(-72.23, -4.13) * mm});
            skLineSegment(sketch, "E6962", {"start": v(-72.23, -4.13) * mm, "end": v(-72.21, -4.2) * mm});
            skLineSegment(sketch, "E6963", {"start": v(-72.21, -4.2) * mm, "end": v(-72.19, -4.28) * mm});
            skLineSegment(sketch, "E6964", {"start": v(-72.19, -4.28) * mm, "end": v(-72.16, -4.35) * mm});
            skLineSegment(sketch, "E6965", {"start": v(-72.16, -4.35) * mm, "end": v(-72.14, -4.42) * mm});
            skLineSegment(sketch, "E6966", {"start": v(-72.14, -4.42) * mm, "end": v(-72.1, -4.48) * mm});
            skLineSegment(sketch, "E6967", {"start": v(-72.1, -4.48) * mm, "end": v(-72.07, -4.55) * mm});
            skLineSegment(sketch, "E6968", {"start": v(-72.07, -4.55) * mm, "end": v(-72.04, -4.62) * mm});
            skLineSegment(sketch, "E6969", {"start": v(-72.04, -4.62) * mm, "end": v(-72, -4.68) * mm});
            skLineSegment(sketch, "E6970", {"start": v(-72, -4.68) * mm, "end": v(-71.96, -4.75) * mm});
            skLineSegment(sketch, "E6971", {"start": v(-71.96, -4.75) * mm, "end": v(-71.92, -4.8) * mm});
            skLineSegment(sketch, "E6972", {"start": v(-71.92, -4.8) * mm, "end": v(-71.88, -4.87) * mm});
            skLineSegment(sketch, "E6973", {"start": v(-71.88, -4.87) * mm, "end": v(-71.83, -4.93) * mm});
            skLineSegment(sketch, "E6974", {"start": v(-71.83, -4.93) * mm, "end": v(-71.78, -4.98) * mm});
            skLineSegment(sketch, "E6975", {"start": v(-71.78, -4.98) * mm, "end": v(-71.73, -5.04) * mm});
            skLineSegment(sketch, "E6976", {"start": v(-71.73, -5.04) * mm, "end": v(-71.68, -5.1) * mm});
            skLineSegment(sketch, "E6977", {"start": v(-71.68, -5.1) * mm, "end": v(-71.63, -5.15) * mm});
            skLineSegment(sketch, "E6978", {"start": v(-71.63, -5.15) * mm, "end": v(-71.57, -5.2) * mm});
            skLineSegment(sketch, "E6979", {"start": v(-71.57, -5.2) * mm, "end": v(-71.52, -5.24) * mm});
            skLineSegment(sketch, "E6980", {"start": v(-71.52, -5.24) * mm, "end": v(-71.46, -5.3) * mm});
            skLineSegment(sketch, "E6981", {"start": v(-71.4, -5.33) * mm, "end": v(-71.34, -5.38) * mm});
            skLineSegment(sketch, "E6982", {"start": v(-71.34, -5.38) * mm, "end": v(-71.27, -5.42) * mm});
            skLineSegment(sketch, "E6983", {"start": v(-71.27, -5.42) * mm, "end": v(-71.2, -5.45) * mm});
            skLineSegment(sketch, "E6984", {"start": v(-71.2, -5.45) * mm, "end": v(-71.14, -5.49) * mm});
            skLineSegment(sketch, "E6985", {"start": v(-71.14, -5.49) * mm, "end": v(-71.08, -5.52) * mm});
            skLineSegment(sketch, "E6986", {"start": v(-71.08, -5.52) * mm, "end": v(-71, -5.55) * mm});
            skLineSegment(sketch, "E6987", {"start": v(-71, -5.55) * mm, "end": v(-70.94, -5.58) * mm});
            skLineSegment(sketch, "E6988", {"start": v(-70.94, -5.58) * mm, "end": v(-70.87, -5.6) * mm});
            skLineSegment(sketch, "E6989", {"start": v(-70.87, -5.6) * mm, "end": v(-70.8, -5.63) * mm});
            skLineSegment(sketch, "E6990", {"start": v(-70.8, -5.63) * mm, "end": v(-70.73, -5.65) * mm});
            skLineSegment(sketch, "E6991", {"start": v(-70.73, -5.65) * mm, "end": v(-70.65, -5.67) * mm});
            skLineSegment(sketch, "E6992", {"start": v(-70.65, -5.67) * mm, "end": v(-70.58, -5.69) * mm});
            skLineSegment(sketch, "E6993", {"start": v(-70.58, -5.69) * mm, "end": v(-70.5, -5.7) * mm});
            skLineSegment(sketch, "E6994", {"start": v(-70.5, -5.7) * mm, "end": v(-70.43, -5.71) * mm});
            skLineSegment(sketch, "E6995", {"start": v(-70.43, -5.71) * mm, "end": v(-70.36, -5.72) * mm});
            skLineSegment(sketch, "E6996", {"start": v(-70.36, -5.72) * mm, "end": v(-70.29, -5.73) * mm});
            skLineSegment(sketch, "E6997", {"start": v(-70.29, -5.73) * mm, "end": v(-70.21, -5.73) * mm});
            skLineSegment(sketch, "E6998", {"start": v(-70.21, -5.73) * mm, "end": v(-70.14, -5.73) * mm});
            skLineSegment(sketch, "E6999", {"start": v(-70.14, -5.73) * mm, "end": v(-70.06, -5.73) * mm});
            skLineSegment(sketch, "E7000", {"start": v(-70.06, -5.73) * mm, "end": v(-69.99, -5.72) * mm});
            skLineSegment(sketch, "E7001", {"start": v(-69.99, -5.72) * mm, "end": v(-69.91, -5.72) * mm});
            skLineSegment(sketch, "E7002", {"start": v(-69.91, -5.72) * mm, "end": v(-69.84, -5.7) * mm});
            skLineSegment(sketch, "E7003", {"start": v(-69.84, -5.7) * mm, "end": v(-69.77, -5.7) * mm});
            skLineSegment(sketch, "E7004", {"start": v(-69.77, -5.7) * mm, "end": v(-69.7, -5.68) * mm});
            skLineSegment(sketch, "E7005", {"start": v(-69.7, -5.68) * mm, "end": v(-69.62, -5.66) * mm});
            skLineSegment(sketch, "E7006", {"start": v(-69.55, -5.64) * mm, "end": v(-69.48, -5.62) * mm});
            skLineSegment(sketch, "E7007", {"start": v(-69.48, -5.62) * mm, "end": v(-69.4, -5.6) * mm});
            skLineSegment(sketch, "E7008", {"start": v(-69.4, -5.6) * mm, "end": v(-69.34, -5.57) * mm});
            skLineSegment(sketch, "E7009", {"start": v(-69.34, -5.57) * mm, "end": v(-69.27, -5.54) * mm});
            skLineSegment(sketch, "E7010", {"start": v(-69.27, -5.54) * mm, "end": v(-69.2, -5.5) * mm});
            skLineSegment(sketch, "E7011", {"start": v(-69.2, -5.5) * mm, "end": v(-69.13, -5.47) * mm});
            skLineSegment(sketch, "E7012", {"start": v(-69.13, -5.47) * mm, "end": v(-69.07, -5.44) * mm});
            skLineSegment(sketch, "E7013", {"start": v(-69.07, -5.44) * mm, "end": v(-69, -5.4) * mm});
            skLineSegment(sketch, "E7014", {"start": v(-68.94, -5.36) * mm, "end": v(-68.88, -5.31) * mm});
            skLineSegment(sketch, "E7015", {"start": v(-68.88, -5.31) * mm, "end": v(-68.82, -5.27) * mm});
            skLineSegment(sketch, "E7016", {"start": v(-68.82, -5.27) * mm, "end": v(-68.77, -5.22) * mm});
            skLineSegment(sketch, "E7017", {"start": v(-68.77, -5.22) * mm, "end": v(-68.7, -5.17) * mm});
            skLineSegment(sketch, "E7018", {"start": v(-68.7, -5.17) * mm, "end": v(-68.66, -5.12) * mm});
            skLineSegment(sketch, "E7019", {"start": v(-68.66, -5.12) * mm, "end": v(-68.6, -5.07) * mm});
            skLineSegment(sketch, "E7020", {"start": v(-68.6, -5.07) * mm, "end": v(-68.55, -5.01) * mm});
            skLineSegment(sketch, "E7021", {"start": v(-68.55, -5.01) * mm, "end": v(-68.5, -4.96) * mm});
            skLineSegment(sketch, "E7022", {"start": v(-68.5, -4.96) * mm, "end": v(-68.46, -4.9) * mm});
            skLineSegment(sketch, "E7023", {"start": v(-68.46, -4.9) * mm, "end": v(-68.41, -4.84) * mm});
            skLineSegment(sketch, "E7024", {"start": v(-68.41, -4.84) * mm, "end": v(-68.37, -4.78) * mm});
            skLineSegment(sketch, "E7025", {"start": v(-68.37, -4.78) * mm, "end": v(-68.33, -4.71) * mm});
            skLineSegment(sketch, "E7026", {"start": v(-68.33, -4.71) * mm, "end": v(-68.3, -4.65) * mm});
            skLineSegment(sketch, "E7027", {"start": v(-68.3, -4.65) * mm, "end": v(-68.25, -4.58) * mm});
            skLineSegment(sketch, "E7028", {"start": v(-68.25, -4.58) * mm, "end": v(-68.22, -4.52) * mm});
            skLineSegment(sketch, "E7029", {"start": v(-68.22, -4.52) * mm, "end": v(-68.19, -4.45) * mm});
            skLineSegment(sketch, "E7030", {"start": v(-68.19, -4.45) * mm, "end": v(-68.16, -4.38) * mm});
            skLineSegment(sketch, "E7031", {"start": v(-68.16, -4.38) * mm, "end": v(-68.13, -4.31) * mm});
            skLineSegment(sketch, "E7032", {"start": v(-68.13, -4.31) * mm, "end": v(-68.1, -4.24) * mm});
            skLineSegment(sketch, "E7033", {"start": v(-68.1, -4.24) * mm, "end": v(-68.09, -4.17) * mm});
            skLineSegment(sketch, "E7034", {"start": v(-68.09, -4.17) * mm, "end": v(-68.07, -4.1) * mm});
            skLineSegment(sketch, "E7035", {"start": v(-68.07, -4.1) * mm, "end": v(-68.05, -4.02) * mm});
            skLineSegment(sketch, "E7036", {"start": v(-68.05, -4.02) * mm, "end": v(-68.04, -3.95) * mm});
            skLineSegment(sketch, "E7037", {"start": v(-68.04, -3.95) * mm, "end": v(-68.03, -3.88) * mm});
            skLineSegment(sketch, "E7038", {"start": v(-68.03, -3.88) * mm, "end": v(-68.02, -3.8) * mm});
            skLineSegment(sketch, "E7039", {"start": v(-68.02, -3.8) * mm, "end": v(-68.01, -3.73) * mm});
            skLineSegment(sketch, "E7040", {"start": v(-68.01, -3.73) * mm, "end": v(-68, -3.65) * mm});
            skLineSegment(sketch, "E7041", {"start": v(-68, -3.65) * mm, "end": v(-68, -3.58) * mm});
            skLineSegment(sketch, "E7042", {"start": v(-322, -5.88) * mm, "end": v(-302, -5.88) * mm});
            skLineSegment(sketch, "E7043", {"start": v(-302, -5.88) * mm, "end": v(-302, 44.12) * mm});
            skLineSegment(sketch, "E7044", {"start": v(-302, 44.12) * mm, "end": v(-322, 44.12) * mm});
            skLineSegment(sketch, "E7045", {"start": v(-322, 44.12) * mm, "end": v(-322, -5.88) * mm});
            skLineSegment(sketch, "E7046", {"start": v(-292.44, -22.37) * mm, "end": v(-157.44, -22.37) * mm});
            skLineSegment(sketch, "E7047", {"start": v(-157.44, -22.37) * mm, "end": v(-157.44, -7.37) * mm});
            skLineSegment(sketch, "E7048", {"start": v(-157.44, -7.37) * mm, "end": v(-292.44, -7.37) * mm});
            skLineSegment(sketch, "E7049", {"start": v(-292.44, -7.37) * mm, "end": v(-292.44, -22.37) * mm});
            skLineSegment(sketch, "E7050", {"start": v(-40.6, -22.57) * mm, "end": v(-40.6, -22.52) * mm});
            skLineSegment(sketch, "E7051", {"start": v(-40.6, -22.52) * mm, "end": v(-40.6, -22.48) * mm});
            skLineSegment(sketch, "E7052", {"start": v(-40.6, -22.48) * mm, "end": v(-40.6, -22.44) * mm});
            skLineSegment(sketch, "E7053", {"start": v(-40.6, -22.44) * mm, "end": v(-40.61, -22.4) * mm});
            skLineSegment(sketch, "E7054", {"start": v(-40.61, -22.4) * mm, "end": v(-40.62, -22.35) * mm});
            skLineSegment(sketch, "E7055", {"start": v(-40.62, -22.35) * mm, "end": v(-40.63, -22.3) * mm});
            skLineSegment(sketch, "E7056", {"start": v(-40.63, -22.3) * mm, "end": v(-40.64, -22.27) * mm});
            skLineSegment(sketch, "E7057", {"start": v(-40.64, -22.27) * mm, "end": v(-40.65, -22.23) * mm});
            skLineSegment(sketch, "E7058", {"start": v(-40.65, -22.23) * mm, "end": v(-40.66, -22.18) * mm});
            skLineSegment(sketch, "E7059", {"start": v(-40.66, -22.18) * mm, "end": v(-40.68, -22.14) * mm});
            skLineSegment(sketch, "E7060", {"start": v(-40.68, -22.14) * mm, "end": v(-40.7, -22.1) * mm});
            skLineSegment(sketch, "E7061", {"start": v(-40.7, -22.1) * mm, "end": v(-40.7, -22.06) * mm});
            skLineSegment(sketch, "E7062", {"start": v(-40.7, -22.06) * mm, "end": v(-40.73, -22.02) * mm});
            skLineSegment(sketch, "E7063", {"start": v(-40.73, -22.02) * mm, "end": v(-40.75, -21.98) * mm});
            skLineSegment(sketch, "E7064", {"start": v(-40.75, -21.98) * mm, "end": v(-40.77, -21.95) * mm});
            skLineSegment(sketch, "E7065", {"start": v(-40.77, -21.95) * mm, "end": v(-40.79, -21.9) * mm});
            skLineSegment(sketch, "E7066", {"start": v(-40.79, -21.9) * mm, "end": v(-40.81, -21.87) * mm});
            skLineSegment(sketch, "E7067", {"start": v(-40.81, -21.87) * mm, "end": v(-40.84, -21.84) * mm});
            skLineSegment(sketch, "E7068", {"start": v(-40.84, -21.84) * mm, "end": v(-40.86, -21.8) * mm});
            skLineSegment(sketch, "E7069", {"start": v(-40.86, -21.8) * mm, "end": v(-40.89, -21.77) * mm});
            skLineSegment(sketch, "E7070", {"start": v(-40.89, -21.77) * mm, "end": v(-40.92, -21.74) * mm});
            skLineSegment(sketch, "E7071", {"start": v(-40.92, -21.74) * mm, "end": v(-40.95, -21.7) * mm});
            skLineSegment(sketch, "E7072", {"start": v(-40.95, -21.7) * mm, "end": v(-40.98, -21.67) * mm});
            skLineSegment(sketch, "E7073", {"start": v(-40.98, -21.67) * mm, "end": v(-41, -21.64) * mm});
            skLineSegment(sketch, "E7074", {"start": v(-41, -21.64) * mm, "end": v(-41.04, -21.61) * mm});
            skLineSegment(sketch, "E7075", {"start": v(-41.04, -21.61) * mm, "end": v(-41.08, -21.59) * mm});
            skLineSegment(sketch, "E7076", {"start": v(-41.08, -21.59) * mm, "end": v(-41.11, -21.56) * mm});
            skLineSegment(sketch, "E7077", {"start": v(-41.11, -21.56) * mm, "end": v(-41.15, -21.54) * mm});
            skLineSegment(sketch, "E7078", {"start": v(-41.15, -21.54) * mm, "end": v(-41.18, -21.51) * mm});
            skLineSegment(sketch, "E7079", {"start": v(-41.18, -21.51) * mm, "end": v(-41.22, -21.49) * mm});
            skLineSegment(sketch, "E7080", {"start": v(-41.22, -21.49) * mm, "end": v(-41.26, -21.47) * mm});
            skLineSegment(sketch, "E7081", {"start": v(-41.26, -21.47) * mm, "end": v(-41.3, -21.45) * mm});
            skLineSegment(sketch, "E7082", {"start": v(-41.3, -21.45) * mm, "end": v(-41.33, -21.43) * mm});
            skLineSegment(sketch, "E7083", {"start": v(-41.33, -21.43) * mm, "end": v(-41.37, -21.41) * mm});
            skLineSegment(sketch, "E7084", {"start": v(-41.37, -21.41) * mm, "end": v(-41.42, -21.4) * mm});
            skLineSegment(sketch, "E7085", {"start": v(-41.42, -21.4) * mm, "end": v(-41.46, -21.38) * mm});
            skLineSegment(sketch, "E7086", {"start": v(-41.46, -21.38) * mm, "end": v(-41.5, -21.37) * mm});
            skLineSegment(sketch, "E7087", {"start": v(-41.5, -21.37) * mm, "end": v(-41.54, -21.36) * mm});
            skLineSegment(sketch, "E7088", {"start": v(-41.54, -21.36) * mm, "end": v(-41.58, -21.35) * mm});
            skLineSegment(sketch, "E7089", {"start": v(-41.58, -21.35) * mm, "end": v(-41.62, -21.34) * mm});
            skLineSegment(sketch, "E7090", {"start": v(-41.62, -21.34) * mm, "end": v(-41.67, -21.33) * mm});
            skLineSegment(sketch, "E7091", {"start": v(-41.67, -21.33) * mm, "end": v(-41.7, -21.33) * mm});
            skLineSegment(sketch, "E7092", {"start": v(-41.7, -21.33) * mm, "end": v(-41.75, -21.32) * mm});
            skLineSegment(sketch, "E7093", {"start": v(-41.75, -21.32) * mm, "end": v(-41.8, -21.32) * mm});
            skLineSegment(sketch, "E7094", {"start": v(-41.8, -21.32) * mm, "end": v(-41.84, -21.32) * mm});
            skLineSegment(sketch, "E7095", {"start": v(-41.84, -21.32) * mm, "end": v(-41.88, -21.32) * mm});
            skLineSegment(sketch, "E7096", {"start": v(-41.88, -21.32) * mm, "end": v(-41.93, -21.32) * mm});
            skLineSegment(sketch, "E7097", {"start": v(-41.93, -21.32) * mm, "end": v(-41.97, -21.32) * mm});
            skLineSegment(sketch, "E7098", {"start": v(-41.97, -21.32) * mm, "end": v(-42.01, -21.33) * mm});
            skLineSegment(sketch, "E7099", {"start": v(-42.01, -21.33) * mm, "end": v(-42.06, -21.34) * mm});
            skLineSegment(sketch, "E7100", {"start": v(-42.06, -21.34) * mm, "end": v(-42.1, -21.34) * mm});
            skLineSegment(sketch, "E7101", {"start": v(-42.1, -21.34) * mm, "end": v(-42.14, -21.35) * mm});
            skLineSegment(sketch, "E7102", {"start": v(-42.14, -21.35) * mm, "end": v(-42.18, -21.36) * mm});
            skLineSegment(sketch, "E7103", {"start": v(-42.18, -21.36) * mm, "end": v(-42.22, -21.38) * mm});
            skLineSegment(sketch, "E7104", {"start": v(-42.22, -21.38) * mm, "end": v(-42.27, -21.39) * mm});
            skLineSegment(sketch, "E7105", {"start": v(-42.27, -21.39) * mm, "end": v(-42.3, -21.4) * mm});
            skLineSegment(sketch, "E7106", {"start": v(-42.3, -21.4) * mm, "end": v(-42.35, -21.42) * mm});
            skLineSegment(sketch, "E7107", {"start": v(-42.35, -21.42) * mm, "end": v(-42.39, -21.44) * mm});
            skLineSegment(sketch, "E7108", {"start": v(-42.57, -21.55) * mm, "end": v(-42.6, -21.57) * mm});
            skLineSegment(sketch, "E7109", {"start": v(-42.6, -21.57) * mm, "end": v(-42.64, -21.6) * mm});
            skLineSegment(sketch, "E7110", {"start": v(-42.64, -21.6) * mm, "end": v(-42.68, -21.63) * mm});
            skLineSegment(sketch, "E7111", {"start": v(-42.68, -21.63) * mm, "end": v(-42.7, -21.66) * mm});
            skLineSegment(sketch, "E7112", {"start": v(-42.7, -21.66) * mm, "end": v(-42.74, -21.69) * mm});
            skLineSegment(sketch, "E7113", {"start": v(-42.74, -21.69) * mm, "end": v(-42.77, -21.72) * mm});
            skLineSegment(sketch, "E7114", {"start": v(-42.77, -21.72) * mm, "end": v(-42.8, -21.75) * mm});
            skLineSegment(sketch, "E7115", {"start": v(-42.8, -21.75) * mm, "end": v(-42.83, -21.79) * mm});
            skLineSegment(sketch, "E7116", {"start": v(-42.83, -21.79) * mm, "end": v(-42.85, -21.82) * mm});
            skLineSegment(sketch, "E7117", {"start": v(-42.85, -21.82) * mm, "end": v(-42.88, -21.85) * mm});
            skLineSegment(sketch, "E7118", {"start": v(-42.88, -21.85) * mm, "end": v(-42.9, -21.9) * mm});
            skLineSegment(sketch, "E7119", {"start": v(-42.9, -21.9) * mm, "end": v(-42.92, -21.93) * mm});
            skLineSegment(sketch, "E7120", {"start": v(-42.92, -21.93) * mm, "end": v(-42.95, -21.97) * mm});
            skLineSegment(sketch, "E7121", {"start": v(-42.95, -21.97) * mm, "end": v(-42.97, -22) * mm});
            skLineSegment(sketch, "E7122", {"start": v(-42.97, -22) * mm, "end": v(-42.98, -22.04) * mm});
            skLineSegment(sketch, "E7123", {"start": v(-42.98, -22.04) * mm, "end": v(-43, -22.08) * mm});
            skLineSegment(sketch, "E7124", {"start": v(-43, -22.08) * mm, "end": v(-43.02, -22.12) * mm});
            skLineSegment(sketch, "E7125", {"start": v(-43.02, -22.12) * mm, "end": v(-43.03, -22.16) * mm});
            skLineSegment(sketch, "E7126", {"start": v(-43.03, -22.16) * mm, "end": v(-43.05, -22.2) * mm});
            skLineSegment(sketch, "E7127", {"start": v(-43.05, -22.2) * mm, "end": v(-43.06, -22.25) * mm});
            skLineSegment(sketch, "E7128", {"start": v(-43.06, -22.25) * mm, "end": v(-43.07, -22.29) * mm});
            skLineSegment(sketch, "E7129", {"start": v(-43.07, -22.29) * mm, "end": v(-43.08, -22.33) * mm});
            skLineSegment(sketch, "E7130", {"start": v(-43.08, -22.33) * mm, "end": v(-43.09, -22.37) * mm});
            skLineSegment(sketch, "E7131", {"start": v(-43.09, -22.37) * mm, "end": v(-43.1, -22.42) * mm});
            skLineSegment(sketch, "E7132", {"start": v(-43.1, -22.42) * mm, "end": v(-43.1, -22.46) * mm});
            skLineSegment(sketch, "E7133", {"start": v(-43.1, -22.46) * mm, "end": v(-43.1, -22.5) * mm});
            skLineSegment(sketch, "E7134", {"start": v(-43.1, -22.5) * mm, "end": v(-43.1, -22.55) * mm});
            skLineSegment(sketch, "E7135", {"start": v(-43.1, -22.55) * mm, "end": v(-43.1, -22.6) * mm});
            skLineSegment(sketch, "E7136", {"start": v(-43.1, -22.6) * mm, "end": v(-43.1, -22.63) * mm});
            skLineSegment(sketch, "E7137", {"start": v(-43.1, -22.63) * mm, "end": v(-43.1, -22.68) * mm});
            skLineSegment(sketch, "E7138", {"start": v(-43.1, -22.68) * mm, "end": v(-43.1, -22.72) * mm});
            skLineSegment(sketch, "E7139", {"start": v(-43.1, -22.72) * mm, "end": v(-43.09, -22.76) * mm});
            skLineSegment(sketch, "E7140", {"start": v(-43.09, -22.76) * mm, "end": v(-43.08, -22.8) * mm});
            skLineSegment(sketch, "E7141", {"start": v(-43.08, -22.8) * mm, "end": v(-43.07, -22.85) * mm});
            skLineSegment(sketch, "E7142", {"start": v(-43.07, -22.85) * mm, "end": v(-43.06, -22.9) * mm});
            skLineSegment(sketch, "E7143", {"start": v(-43.06, -22.9) * mm, "end": v(-43.05, -22.93) * mm});
            skLineSegment(sketch, "E7144", {"start": v(-43.03, -22.97) * mm, "end": v(-43.02, -23.01) * mm});
            skLineSegment(sketch, "E7145", {"start": v(-43.02, -23.01) * mm, "end": v(-43, -23.05) * mm});
            skLineSegment(sketch, "E7146", {"start": v(-43, -23.05) * mm, "end": v(-42.98, -23.1) * mm});
            skLineSegment(sketch, "E7147", {"start": v(-42.98, -23.1) * mm, "end": v(-42.97, -23.13) * mm});
            skLineSegment(sketch, "E7148", {"start": v(-42.97, -23.13) * mm, "end": v(-42.95, -23.17) * mm});
            skLineSegment(sketch, "E7149", {"start": v(-42.95, -23.17) * mm, "end": v(-42.92, -23.2) * mm});
            skLineSegment(sketch, "E7150", {"start": v(-42.92, -23.2) * mm, "end": v(-42.9, -23.25) * mm});
            skLineSegment(sketch, "E7151", {"start": v(-42.9, -23.25) * mm, "end": v(-42.88, -23.28) * mm});
            skLineSegment(sketch, "E7152", {"start": v(-42.88, -23.28) * mm, "end": v(-42.85, -23.32) * mm});
            skLineSegment(sketch, "E7153", {"start": v(-42.85, -23.32) * mm, "end": v(-42.83, -23.35) * mm});
            skLineSegment(sketch, "E7154", {"start": v(-42.83, -23.35) * mm, "end": v(-42.8, -23.38) * mm});
            skLineSegment(sketch, "E7155", {"start": v(-42.8, -23.38) * mm, "end": v(-42.77, -23.42) * mm});
            skLineSegment(sketch, "E7156", {"start": v(-42.77, -23.42) * mm, "end": v(-42.74, -23.45) * mm});
            skLineSegment(sketch, "E7157", {"start": v(-42.74, -23.45) * mm, "end": v(-42.7, -23.48) * mm});
            skLineSegment(sketch, "E7158", {"start": v(-42.7, -23.48) * mm, "end": v(-42.68, -23.5) * mm});
            skLineSegment(sketch, "E7159", {"start": v(-42.57, -23.59) * mm, "end": v(-42.54, -23.61) * mm});
            skLineSegment(sketch, "E7160", {"start": v(-42.54, -23.61) * mm, "end": v(-42.5, -23.64) * mm});
            skLineSegment(sketch, "E7161", {"start": v(-42.5, -23.64) * mm, "end": v(-42.46, -23.66) * mm});
            skLineSegment(sketch, "E7162", {"start": v(-42.46, -23.66) * mm, "end": v(-42.42, -23.68) * mm});
            skLineSegment(sketch, "E7163", {"start": v(-42.42, -23.68) * mm, "end": v(-42.39, -23.7) * mm});
            skLineSegment(sketch, "E7164", {"start": v(-42.39, -23.7) * mm, "end": v(-42.35, -23.72) * mm});
            skLineSegment(sketch, "E7165", {"start": v(-42.35, -23.72) * mm, "end": v(-42.3, -23.73) * mm});
            skLineSegment(sketch, "E7166", {"start": v(-42.3, -23.73) * mm, "end": v(-42.27, -23.75) * mm});
            skLineSegment(sketch, "E7167", {"start": v(-42.27, -23.75) * mm, "end": v(-42.22, -23.76) * mm});
            skLineSegment(sketch, "E7168", {"start": v(-42.22, -23.76) * mm, "end": v(-42.18, -23.77) * mm});
            skLineSegment(sketch, "E7169", {"start": v(-42.18, -23.77) * mm, "end": v(-42.14, -23.78) * mm});
            skLineSegment(sketch, "E7170", {"start": v(-42.1, -23.8) * mm, "end": v(-42.06, -23.8) * mm});
            skLineSegment(sketch, "E7171", {"start": v(-42.06, -23.8) * mm, "end": v(-42.01, -23.8) * mm});
            skLineSegment(sketch, "E7172", {"start": v(-42.01, -23.8) * mm, "end": v(-41.97, -23.81) * mm});
            skLineSegment(sketch, "E7173", {"start": v(-41.97, -23.81) * mm, "end": v(-41.93, -23.82) * mm});
            skLineSegment(sketch, "E7174", {"start": v(-41.93, -23.82) * mm, "end": v(-41.88, -23.82) * mm});
            skLineSegment(sketch, "E7175", {"start": v(-41.88, -23.82) * mm, "end": v(-41.84, -23.82) * mm});
            skLineSegment(sketch, "E7176", {"start": v(-41.84, -23.82) * mm, "end": v(-41.8, -23.82) * mm});
            skLineSegment(sketch, "E7177", {"start": v(-41.8, -23.82) * mm, "end": v(-41.75, -23.81) * mm});
            skLineSegment(sketch, "E7178", {"start": v(-41.75, -23.81) * mm, "end": v(-41.7, -23.81) * mm});
            skLineSegment(sketch, "E7179", {"start": v(-41.7, -23.81) * mm, "end": v(-41.67, -23.8) * mm});
            skLineSegment(sketch, "E7180", {"start": v(-41.67, -23.8) * mm, "end": v(-41.62, -23.8) * mm});
            skLineSegment(sketch, "E7181", {"start": v(-41.62, -23.8) * mm, "end": v(-41.58, -23.79) * mm});
            skLineSegment(sketch, "E7182", {"start": v(-41.58, -23.79) * mm, "end": v(-41.54, -23.78) * mm});
            skLineSegment(sketch, "E7183", {"start": v(-41.54, -23.78) * mm, "end": v(-41.5, -23.77) * mm});
            skLineSegment(sketch, "E7184", {"start": v(-41.5, -23.77) * mm, "end": v(-41.46, -23.75) * mm});
            skLineSegment(sketch, "E7185", {"start": v(-41.46, -23.75) * mm, "end": v(-41.42, -23.74) * mm});
            skLineSegment(sketch, "E7186", {"start": v(-41.42, -23.74) * mm, "end": v(-41.37, -23.72) * mm});
            skLineSegment(sketch, "E7187", {"start": v(-41.37, -23.72) * mm, "end": v(-41.33, -23.7) * mm});
            skLineSegment(sketch, "E7188", {"start": v(-41.3, -23.69) * mm, "end": v(-41.26, -23.67) * mm});
            skLineSegment(sketch, "E7189", {"start": v(-41.26, -23.67) * mm, "end": v(-41.22, -23.65) * mm});
            skLineSegment(sketch, "E7190", {"start": v(-41.22, -23.65) * mm, "end": v(-41.18, -23.62) * mm});
            skLineSegment(sketch, "E7191", {"start": v(-41.18, -23.62) * mm, "end": v(-41.15, -23.6) * mm});
            skLineSegment(sketch, "E7192", {"start": v(-41.15, -23.6) * mm, "end": v(-41.11, -23.58) * mm});
            skLineSegment(sketch, "E7193", {"start": v(-41.11, -23.58) * mm, "end": v(-41.08, -23.55) * mm});
            skLineSegment(sketch, "E7194", {"start": v(-41.08, -23.55) * mm, "end": v(-41.04, -23.52) * mm});
            skLineSegment(sketch, "E7195", {"start": v(-41.04, -23.52) * mm, "end": v(-41, -23.5) * mm});
            skLineSegment(sketch, "E7196", {"start": v(-41, -23.5) * mm, "end": v(-40.98, -23.46) * mm});
            skLineSegment(sketch, "E7197", {"start": v(-40.98, -23.46) * mm, "end": v(-40.95, -23.43) * mm});
            skLineSegment(sketch, "E7198", {"start": v(-40.95, -23.43) * mm, "end": v(-40.92, -23.4) * mm});
            skLineSegment(sketch, "E7199", {"start": v(-40.92, -23.4) * mm, "end": v(-40.89, -23.37) * mm});
            skLineSegment(sketch, "E7200", {"start": v(-40.89, -23.37) * mm, "end": v(-40.86, -23.33) * mm});
            skLineSegment(sketch, "E7201", {"start": v(-40.86, -23.33) * mm, "end": v(-40.84, -23.3) * mm});
            skLineSegment(sketch, "E7202", {"start": v(-40.84, -23.3) * mm, "end": v(-40.81, -23.26) * mm});
            skLineSegment(sketch, "E7203", {"start": v(-40.79, -23.23) * mm, "end": v(-40.77, -23.2) * mm});
            skLineSegment(sketch, "E7204", {"start": v(-40.77, -23.2) * mm, "end": v(-40.75, -23.15) * mm});
            skLineSegment(sketch, "E7205", {"start": v(-40.75, -23.15) * mm, "end": v(-40.73, -23.11) * mm});
            skLineSegment(sketch, "E7206", {"start": v(-40.73, -23.11) * mm, "end": v(-40.7, -23.07) * mm});
            skLineSegment(sketch, "E7207", {"start": v(-40.7, -23.07) * mm, "end": v(-40.7, -23.03) * mm});
            skLineSegment(sketch, "E7208", {"start": v(-40.7, -23.03) * mm, "end": v(-40.68, -23) * mm});
            skLineSegment(sketch, "E7209", {"start": v(-40.68, -23) * mm, "end": v(-40.66, -22.95) * mm});
            skLineSegment(sketch, "E7210", {"start": v(-40.66, -22.95) * mm, "end": v(-40.65, -22.91) * mm});
            skLineSegment(sketch, "E7211", {"start": v(-40.65, -22.91) * mm, "end": v(-40.64, -22.87) * mm});
            skLineSegment(sketch, "E7212", {"start": v(-40.64, -22.87) * mm, "end": v(-40.63, -22.83) * mm});
            skLineSegment(sketch, "E7213", {"start": v(-40.63, -22.83) * mm, "end": v(-40.62, -22.78) * mm});
            skLineSegment(sketch, "E7214", {"start": v(-40.62, -22.78) * mm, "end": v(-40.61, -22.74) * mm});
            skLineSegment(sketch, "E7215", {"start": v(-40.61, -22.74) * mm, "end": v(-40.6, -22.7) * mm});
            skLineSegment(sketch, "E7216", {"start": v(-40.6, -22.7) * mm, "end": v(-40.6, -22.66) * mm});
            skLineSegment(sketch, "E7217", {"start": v(-40.6, -22.66) * mm, "end": v(-40.6, -22.61) * mm});
            skLineSegment(sketch, "E7218", {"start": v(-40.6, -22.61) * mm, "end": v(-40.6, -22.57) * mm});
            skLineSegment(sketch, "E7219", {"start": v(86.9, -22.57) * mm, "end": v(86.9, -22.52) * mm});
            skLineSegment(sketch, "E7220", {"start": v(86.9, -22.52) * mm, "end": v(86.9, -22.48) * mm});
            skLineSegment(sketch, "E7221", {"start": v(86.9, -22.48) * mm, "end": v(86.9, -22.44) * mm});
            skLineSegment(sketch, "E7222", {"start": v(86.9, -22.44) * mm, "end": v(86.89, -22.4) * mm});
            skLineSegment(sketch, "E7223", {"start": v(86.89, -22.4) * mm, "end": v(86.88, -22.35) * mm});
            skLineSegment(sketch, "E7224", {"start": v(86.88, -22.35) * mm, "end": v(86.87, -22.3) * mm});
            skLineSegment(sketch, "E7225", {"start": v(86.87, -22.3) * mm, "end": v(86.86, -22.27) * mm});
            skLineSegment(sketch, "E7226", {"start": v(86.86, -22.27) * mm, "end": v(86.85, -22.23) * mm});
            skLineSegment(sketch, "E7227", {"start": v(86.85, -22.23) * mm, "end": v(86.84, -22.18) * mm});
            skLineSegment(sketch, "E7228", {"start": v(86.84, -22.18) * mm, "end": v(86.82, -22.14) * mm});
            skLineSegment(sketch, "E7229", {"start": v(86.82, -22.14) * mm, "end": v(86.8, -22.1) * mm});
            skLineSegment(sketch, "E7230", {"start": v(86.8, -22.1) * mm, "end": v(86.8, -22.06) * mm});
            skLineSegment(sketch, "E7231", {"start": v(86.8, -22.06) * mm, "end": v(86.77, -22.02) * mm});
            skLineSegment(sketch, "E7232", {"start": v(86.77, -22.02) * mm, "end": v(86.75, -21.98) * mm});
            skLineSegment(sketch, "E7233", {"start": v(86.75, -21.98) * mm, "end": v(86.73, -21.95) * mm});
            skLineSegment(sketch, "E7234", {"start": v(86.73, -21.95) * mm, "end": v(86.71, -21.9) * mm});
            skLineSegment(sketch, "E7235", {"start": v(86.71, -21.9) * mm, "end": v(86.69, -21.87) * mm});
            skLineSegment(sketch, "E7236", {"start": v(86.69, -21.87) * mm, "end": v(86.66, -21.84) * mm});
            skLineSegment(sketch, "E7237", {"start": v(86.66, -21.84) * mm, "end": v(86.64, -21.8) * mm});
            skLineSegment(sketch, "E7238", {"start": v(86.64, -21.8) * mm, "end": v(86.61, -21.77) * mm});
            skLineSegment(sketch, "E7239", {"start": v(86.61, -21.77) * mm, "end": v(86.58, -21.74) * mm});
            skLineSegment(sketch, "E7240", {"start": v(86.58, -21.74) * mm, "end": v(86.55, -21.7) * mm});
            skLineSegment(sketch, "E7241", {"start": v(86.55, -21.7) * mm, "end": v(86.52, -21.67) * mm});
            skLineSegment(sketch, "E7242", {"start": v(86.5, -21.64) * mm, "end": v(86.46, -21.61) * mm});
            skLineSegment(sketch, "E7243", {"start": v(86.46, -21.61) * mm, "end": v(86.42, -21.59) * mm});
            skLineSegment(sketch, "E7244", {"start": v(86.42, -21.59) * mm, "end": v(86.39, -21.56) * mm});
            skLineSegment(sketch, "E7245", {"start": v(86.39, -21.56) * mm, "end": v(86.35, -21.54) * mm});
            skLineSegment(sketch, "E7246", {"start": v(86.35, -21.54) * mm, "end": v(86.32, -21.51) * mm});
            skLineSegment(sketch, "E7247", {"start": v(86.32, -21.51) * mm, "end": v(86.28, -21.49) * mm});
            skLineSegment(sketch, "E7248", {"start": v(86.28, -21.49) * mm, "end": v(86.24, -21.47) * mm});
            skLineSegment(sketch, "E7249", {"start": v(86.24, -21.47) * mm, "end": v(86.2, -21.45) * mm});
            skLineSegment(sketch, "E7250", {"start": v(86.2, -21.45) * mm, "end": v(86.17, -21.43) * mm});
            skLineSegment(sketch, "E7251", {"start": v(86.17, -21.43) * mm, "end": v(86.13, -21.41) * mm});
            skLineSegment(sketch, "E7252", {"start": v(86.13, -21.41) * mm, "end": v(86.08, -21.4) * mm});
            skLineSegment(sketch, "E7253", {"start": v(86.08, -21.4) * mm, "end": v(86.04, -21.38) * mm});
            skLineSegment(sketch, "E7254", {"start": v(86.04, -21.38) * mm, "end": v(86, -21.37) * mm});
            skLineSegment(sketch, "E7255", {"start": v(86, -21.37) * mm, "end": v(85.96, -21.36) * mm});
            skLineSegment(sketch, "E7256", {"start": v(85.96, -21.36) * mm, "end": v(85.92, -21.35) * mm});
            skLineSegment(sketch, "E7257", {"start": v(85.92, -21.35) * mm, "end": v(85.88, -21.34) * mm});
            skLineSegment(sketch, "E7258", {"start": v(85.88, -21.34) * mm, "end": v(85.83, -21.33) * mm});
            skLineSegment(sketch, "E7259", {"start": v(85.83, -21.33) * mm, "end": v(85.8, -21.33) * mm});
            skLineSegment(sketch, "E7260", {"start": v(85.8, -21.33) * mm, "end": v(85.75, -21.32) * mm});
            skLineSegment(sketch, "E7261", {"start": v(85.75, -21.32) * mm, "end": v(85.7, -21.32) * mm});
            skLineSegment(sketch, "E7262", {"start": v(85.7, -21.32) * mm, "end": v(85.66, -21.32) * mm});
            skLineSegment(sketch, "E7263", {"start": v(85.66, -21.32) * mm, "end": v(85.62, -21.32) * mm});
            skLineSegment(sketch, "E7264", {"start": v(85.62, -21.32) * mm, "end": v(85.57, -21.32) * mm});
            skLineSegment(sketch, "E7265", {"start": v(85.57, -21.32) * mm, "end": v(85.53, -21.32) * mm});
            skLineSegment(sketch, "E7266", {"start": v(85.53, -21.32) * mm, "end": v(85.49, -21.33) * mm});
            skLineSegment(sketch, "E7267", {"start": v(85.49, -21.33) * mm, "end": v(85.44, -21.34) * mm});
            skLineSegment(sketch, "E7268", {"start": v(85.44, -21.34) * mm, "end": v(85.4, -21.34) * mm});
            skLineSegment(sketch, "E7269", {"start": v(85.4, -21.34) * mm, "end": v(85.36, -21.35) * mm});
            skLineSegment(sketch, "E7270", {"start": v(85.36, -21.35) * mm, "end": v(85.32, -21.36) * mm});
            skLineSegment(sketch, "E7271", {"start": v(85.32, -21.36) * mm, "end": v(85.28, -21.38) * mm});
            skLineSegment(sketch, "E7272", {"start": v(85.28, -21.38) * mm, "end": v(85.23, -21.39) * mm});
            skLineSegment(sketch, "E7273", {"start": v(85.23, -21.39) * mm, "end": v(85.2, -21.4) * mm});
            skLineSegment(sketch, "E7274", {"start": v(85.2, -21.4) * mm, "end": v(85.15, -21.42) * mm});
            skLineSegment(sketch, "E7275", {"start": v(85.15, -21.42) * mm, "end": v(85.11, -21.44) * mm});
            skLineSegment(sketch, "E7276", {"start": v(85.11, -21.44) * mm, "end": v(85.08, -21.46) * mm});
            skLineSegment(sketch, "E7277", {"start": v(85.08, -21.46) * mm, "end": v(85.04, -21.48) * mm});
            skLineSegment(sketch, "E7278", {"start": v(85.04, -21.48) * mm, "end": v(85, -21.5) * mm});
            skLineSegment(sketch, "E7279", {"start": v(85, -21.5) * mm, "end": v(84.96, -21.52) * mm});
            skLineSegment(sketch, "E7280", {"start": v(84.96, -21.52) * mm, "end": v(84.93, -21.55) * mm});
            skLineSegment(sketch, "E7281", {"start": v(84.93, -21.55) * mm, "end": v(84.9, -21.57) * mm});
            skLineSegment(sketch, "E7282", {"start": v(84.9, -21.57) * mm, "end": v(84.86, -21.6) * mm});
            skLineSegment(sketch, "E7283", {"start": v(84.86, -21.6) * mm, "end": v(84.82, -21.63) * mm});
            skLineSegment(sketch, "E7284", {"start": v(84.82, -21.63) * mm, "end": v(84.8, -21.66) * mm});
            skLineSegment(sketch, "E7285", {"start": v(84.8, -21.66) * mm, "end": v(84.76, -21.69) * mm});
            skLineSegment(sketch, "E7286", {"start": v(84.76, -21.69) * mm, "end": v(84.73, -21.72) * mm});
            skLineSegment(sketch, "E7287", {"start": v(84.73, -21.72) * mm, "end": v(84.7, -21.75) * mm});
            skLineSegment(sketch, "E7288", {"start": v(84.7, -21.75) * mm, "end": v(84.67, -21.79) * mm});
            skLineSegment(sketch, "E7289", {"start": v(84.67, -21.79) * mm, "end": v(84.65, -21.82) * mm});
            skLineSegment(sketch, "E7290", {"start": v(84.65, -21.82) * mm, "end": v(84.62, -21.85) * mm});
            skLineSegment(sketch, "E7291", {"start": v(84.62, -21.85) * mm, "end": v(84.6, -21.9) * mm});
            skLineSegment(sketch, "E7292", {"start": v(84.6, -21.9) * mm, "end": v(84.58, -21.93) * mm});
            skLineSegment(sketch, "E7293", {"start": v(84.58, -21.93) * mm, "end": v(84.55, -21.97) * mm});
            skLineSegment(sketch, "E7294", {"start": v(84.55, -21.97) * mm, "end": v(84.53, -22) * mm});
            skLineSegment(sketch, "E7295", {"start": v(84.53, -22) * mm, "end": v(84.52, -22.04) * mm});
            skLineSegment(sketch, "E7296", {"start": v(84.52, -22.04) * mm, "end": v(84.5, -22.08) * mm});
            skLineSegment(sketch, "E7297", {"start": v(84.5, -22.08) * mm, "end": v(84.48, -22.12) * mm});
            skLineSegment(sketch, "E7298", {"start": v(84.48, -22.12) * mm, "end": v(84.47, -22.16) * mm});
            skLineSegment(sketch, "E7299", {"start": v(84.47, -22.16) * mm, "end": v(84.45, -22.2) * mm});
            skLineSegment(sketch, "E7300", {"start": v(84.45, -22.2) * mm, "end": v(84.44, -22.25) * mm});
            skLineSegment(sketch, "E7301", {"start": v(84.44, -22.25) * mm, "end": v(84.43, -22.29) * mm});
            skLineSegment(sketch, "E7302", {"start": v(84.43, -22.29) * mm, "end": v(84.42, -22.33) * mm});
            skLineSegment(sketch, "E7303", {"start": v(84.42, -22.33) * mm, "end": v(84.41, -22.37) * mm});
            skLineSegment(sketch, "E7304", {"start": v(84.41, -22.37) * mm, "end": v(84.4, -22.42) * mm});
            skLineSegment(sketch, "E7305", {"start": v(84.4, -22.42) * mm, "end": v(84.4, -22.46) * mm});
            skLineSegment(sketch, "E7306", {"start": v(84.4, -22.46) * mm, "end": v(84.4, -22.5) * mm});
            skLineSegment(sketch, "E7307", {"start": v(84.4, -22.5) * mm, "end": v(84.4, -22.55) * mm});
            skLineSegment(sketch, "E7308", {"start": v(84.4, -22.55) * mm, "end": v(84.4, -22.6) * mm});
            skLineSegment(sketch, "E7309", {"start": v(84.4, -22.6) * mm, "end": v(84.4, -22.63) * mm});
            skLineSegment(sketch, "E7310", {"start": v(84.4, -22.63) * mm, "end": v(84.4, -22.68) * mm});
            skLineSegment(sketch, "E7311", {"start": v(84.4, -22.68) * mm, "end": v(84.4, -22.72) * mm});
            skLineSegment(sketch, "E7312", {"start": v(84.4, -22.72) * mm, "end": v(84.41, -22.76) * mm});
            skLineSegment(sketch, "E7313", {"start": v(84.41, -22.76) * mm, "end": v(84.42, -22.8) * mm});
            skLineSegment(sketch, "E7314", {"start": v(84.42, -22.8) * mm, "end": v(84.43, -22.85) * mm});
            skLineSegment(sketch, "E7315", {"start": v(84.43, -22.85) * mm, "end": v(84.44, -22.9) * mm});
            skLineSegment(sketch, "E7316", {"start": v(84.44, -22.9) * mm, "end": v(84.45, -22.93) * mm});
            skLineSegment(sketch, "E7317", {"start": v(84.45, -22.93) * mm, "end": v(84.47, -22.97) * mm});
            skLineSegment(sketch, "E7318", {"start": v(84.47, -22.97) * mm, "end": v(84.48, -23.01) * mm});
            skLineSegment(sketch, "E7319", {"start": v(84.48, -23.01) * mm, "end": v(84.5, -23.05) * mm});
            skLineSegment(sketch, "E7320", {"start": v(84.5, -23.05) * mm, "end": v(84.52, -23.1) * mm});
            skLineSegment(sketch, "E7321", {"start": v(84.52, -23.1) * mm, "end": v(84.53, -23.13) * mm});
            skLineSegment(sketch, "E7322", {"start": v(84.53, -23.13) * mm, "end": v(84.55, -23.17) * mm});
            skLineSegment(sketch, "E7323", {"start": v(84.55, -23.17) * mm, "end": v(84.58, -23.2) * mm});
            skLineSegment(sketch, "E7324", {"start": v(84.58, -23.2) * mm, "end": v(84.6, -23.25) * mm});
            skLineSegment(sketch, "E7325", {"start": v(84.6, -23.25) * mm, "end": v(84.62, -23.28) * mm});
            skLineSegment(sketch, "E7326", {"start": v(84.62, -23.28) * mm, "end": v(84.65, -23.32) * mm});
            skLineSegment(sketch, "E7327", {"start": v(84.86, -23.54) * mm, "end": v(84.9, -23.56) * mm});
            skLineSegment(sketch, "E7328", {"start": v(84.9, -23.56) * mm, "end": v(84.93, -23.59) * mm});
            skLineSegment(sketch, "E7329", {"start": v(84.93, -23.59) * mm, "end": v(84.96, -23.61) * mm});
            skLineSegment(sketch, "E7330", {"start": v(84.96, -23.61) * mm, "end": v(85, -23.64) * mm});
            skLineSegment(sketch, "E7331", {"start": v(85, -23.64) * mm, "end": v(85.04, -23.66) * mm});
            skLineSegment(sketch, "E7332", {"start": v(85.04, -23.66) * mm, "end": v(85.08, -23.68) * mm});
            skLineSegment(sketch, "E7333", {"start": v(85.08, -23.68) * mm, "end": v(85.11, -23.7) * mm});
            skLineSegment(sketch, "E7334", {"start": v(85.11, -23.7) * mm, "end": v(85.15, -23.72) * mm});
            skLineSegment(sketch, "E7335", {"start": v(85.15, -23.72) * mm, "end": v(85.2, -23.73) * mm});
            skLineSegment(sketch, "E7336", {"start": v(85.2, -23.73) * mm, "end": v(85.23, -23.75) * mm});
            skLineSegment(sketch, "E7337", {"start": v(85.23, -23.75) * mm, "end": v(85.28, -23.76) * mm});
            skLineSegment(sketch, "E7338", {"start": v(85.28, -23.76) * mm, "end": v(85.32, -23.77) * mm});
            skLineSegment(sketch, "E7339", {"start": v(85.32, -23.77) * mm, "end": v(85.36, -23.78) * mm});
            skLineSegment(sketch, "E7340", {"start": v(85.36, -23.78) * mm, "end": v(85.4, -23.8) * mm});
            skLineSegment(sketch, "E7341", {"start": v(85.4, -23.8) * mm, "end": v(85.44, -23.8) * mm});
            skLineSegment(sketch, "E7342", {"start": v(85.44, -23.8) * mm, "end": v(85.49, -23.8) * mm});
            skLineSegment(sketch, "E7343", {"start": v(85.49, -23.8) * mm, "end": v(85.53, -23.81) * mm});
            skLineSegment(sketch, "E7344", {"start": v(85.53, -23.81) * mm, "end": v(85.57, -23.82) * mm});
            skLineSegment(sketch, "E7345", {"start": v(85.57, -23.82) * mm, "end": v(85.62, -23.82) * mm});
            skLineSegment(sketch, "E7346", {"start": v(85.62, -23.82) * mm, "end": v(85.66, -23.82) * mm});
            skLineSegment(sketch, "E7347", {"start": v(85.66, -23.82) * mm, "end": v(85.7, -23.82) * mm});
            skLineSegment(sketch, "E7348", {"start": v(85.7, -23.82) * mm, "end": v(85.75, -23.81) * mm});
            skLineSegment(sketch, "E7349", {"start": v(85.75, -23.81) * mm, "end": v(85.8, -23.81) * mm});
            skLineSegment(sketch, "E7350", {"start": v(85.8, -23.81) * mm, "end": v(85.83, -23.8) * mm});
            skLineSegment(sketch, "E7351", {"start": v(85.83, -23.8) * mm, "end": v(85.88, -23.8) * mm});
            skLineSegment(sketch, "E7352", {"start": v(85.88, -23.8) * mm, "end": v(85.92, -23.79) * mm});
            skLineSegment(sketch, "E7353", {"start": v(85.92, -23.79) * mm, "end": v(85.96, -23.78) * mm});
            skLineSegment(sketch, "E7354", {"start": v(85.96, -23.78) * mm, "end": v(86, -23.77) * mm});
            skLineSegment(sketch, "E7355", {"start": v(86, -23.77) * mm, "end": v(86.04, -23.75) * mm});
            skLineSegment(sketch, "E7356", {"start": v(86.04, -23.75) * mm, "end": v(86.08, -23.74) * mm});
            skLineSegment(sketch, "E7357", {"start": v(86.08, -23.74) * mm, "end": v(86.13, -23.72) * mm});
            skLineSegment(sketch, "E7358", {"start": v(86.13, -23.72) * mm, "end": v(86.17, -23.7) * mm});
            skLineSegment(sketch, "E7359", {"start": v(86.17, -23.7) * mm, "end": v(86.2, -23.69) * mm});
            skLineSegment(sketch, "E7360", {"start": v(86.2, -23.69) * mm, "end": v(86.24, -23.67) * mm});
            skLineSegment(sketch, "E7361", {"start": v(86.24, -23.67) * mm, "end": v(86.28, -23.65) * mm});
            skLineSegment(sketch, "E7362", {"start": v(86.28, -23.65) * mm, "end": v(86.32, -23.62) * mm});
            skLineSegment(sketch, "E7363", {"start": v(86.32, -23.62) * mm, "end": v(86.35, -23.6) * mm});
            skLineSegment(sketch, "E7364", {"start": v(86.35, -23.6) * mm, "end": v(86.39, -23.58) * mm});
            skLineSegment(sketch, "E7365", {"start": v(86.39, -23.58) * mm, "end": v(86.42, -23.55) * mm});
            skLineSegment(sketch, "E7366", {"start": v(86.42, -23.55) * mm, "end": v(86.46, -23.52) * mm});
            skLineSegment(sketch, "E7367", {"start": v(86.46, -23.52) * mm, "end": v(86.5, -23.5) * mm});
            skLineSegment(sketch, "E7368", {"start": v(86.5, -23.5) * mm, "end": v(86.52, -23.46) * mm});
            skLineSegment(sketch, "E7369", {"start": v(86.52, -23.46) * mm, "end": v(86.55, -23.43) * mm});
            skLineSegment(sketch, "E7370", {"start": v(86.55, -23.43) * mm, "end": v(86.58, -23.4) * mm});
            skLineSegment(sketch, "E7371", {"start": v(86.58, -23.4) * mm, "end": v(86.61, -23.37) * mm});
            skLineSegment(sketch, "E7372", {"start": v(86.66, -23.3) * mm, "end": v(86.69, -23.26) * mm});
            skLineSegment(sketch, "E7373", {"start": v(86.69, -23.26) * mm, "end": v(86.71, -23.23) * mm});
            skLineSegment(sketch, "E7374", {"start": v(86.71, -23.23) * mm, "end": v(86.73, -23.2) * mm});
            skLineSegment(sketch, "E7375", {"start": v(86.73, -23.2) * mm, "end": v(86.75, -23.15) * mm});
            skLineSegment(sketch, "E7376", {"start": v(86.75, -23.15) * mm, "end": v(86.77, -23.11) * mm});
            skLineSegment(sketch, "E7377", {"start": v(86.77, -23.11) * mm, "end": v(86.8, -23.07) * mm});
            skLineSegment(sketch, "E7378", {"start": v(86.8, -23.07) * mm, "end": v(86.8, -23.03) * mm});
            skLineSegment(sketch, "E7379", {"start": v(86.8, -23.03) * mm, "end": v(86.82, -23) * mm});
            skLineSegment(sketch, "E7380", {"start": v(86.82, -23) * mm, "end": v(86.84, -22.95) * mm});
            skLineSegment(sketch, "E7381", {"start": v(86.84, -22.95) * mm, "end": v(86.85, -22.91) * mm});
            skLineSegment(sketch, "E7382", {"start": v(86.85, -22.91) * mm, "end": v(86.86, -22.87) * mm});
            skLineSegment(sketch, "E7383", {"start": v(86.86, -22.87) * mm, "end": v(86.87, -22.83) * mm});
            skLineSegment(sketch, "E7384", {"start": v(86.87, -22.83) * mm, "end": v(86.88, -22.78) * mm});
            skLineSegment(sketch, "E7385", {"start": v(86.88, -22.78) * mm, "end": v(86.89, -22.74) * mm});
            skLineSegment(sketch, "E7386", {"start": v(86.89, -22.74) * mm, "end": v(86.9, -22.7) * mm});
            skLineSegment(sketch, "E7387", {"start": v(86.9, -22.7) * mm, "end": v(86.9, -22.66) * mm});
            skLineSegment(sketch, "E7388", {"start": v(86.9, -22.66) * mm, "end": v(86.9, -22.61) * mm});
            skLineSegment(sketch, "E7389", {"start": v(86.9, -22.61) * mm, "end": v(86.9, -22.57) * mm});
            skLineSegment(sketch, "E7390", {"start": v(85.87, -1.63) * mm, "end": v(85.78, -1.63) * mm});
            skLineSegment(sketch, "E7391", {"start": v(85.78, -1.63) * mm, "end": v(85.7, -1.64) * mm});
            skLineSegment(sketch, "E7392", {"start": v(85.7, -1.64) * mm, "end": v(85.6, -1.64) * mm});
            skLineSegment(sketch, "E7393", {"start": v(85.6, -1.64) * mm, "end": v(85.52, -1.65) * mm});
            skLineSegment(sketch, "E7394", {"start": v(85.52, -1.65) * mm, "end": v(85.43, -1.67) * mm});
            skLineSegment(sketch, "E7395", {"start": v(85.43, -1.67) * mm, "end": v(85.35, -1.68) * mm});
            skLineSegment(sketch, "E7396", {"start": v(85.35, -1.68) * mm, "end": v(85.26, -1.7) * mm});
            skLineSegment(sketch, "E7397", {"start": v(85.26, -1.7) * mm, "end": v(85.18, -1.73) * mm});
            skLineSegment(sketch, "E7398", {"start": v(85.18, -1.73) * mm, "end": v(85.1, -1.75) * mm});
            skLineSegment(sketch, "E7399", {"start": v(85.1, -1.75) * mm, "end": v(85.02, -1.78) * mm});
            skLineSegment(sketch, "E7400", {"start": v(85.02, -1.78) * mm, "end": v(84.93, -1.81) * mm});
            skLineSegment(sketch, "E7401", {"start": v(84.93, -1.81) * mm, "end": v(84.85, -1.84) * mm});
            skLineSegment(sketch, "E7402", {"start": v(84.85, -1.84) * mm, "end": v(84.78, -1.88) * mm});
            skLineSegment(sketch, "E7403", {"start": v(84.78, -1.88) * mm, "end": v(84.7, -1.92) * mm});
            skLineSegment(sketch, "E7404", {"start": v(84.7, -1.92) * mm, "end": v(84.62, -1.96) * mm});
            skLineSegment(sketch, "E7405", {"start": v(84.62, -1.96) * mm, "end": v(84.55, -2) * mm});
            skLineSegment(sketch, "E7406", {"start": v(84.55, -2) * mm, "end": v(84.47, -2.05) * mm});
            skLineSegment(sketch, "E7407", {"start": v(84.47, -2.05) * mm, "end": v(84.4, -2.1) * mm});
            skLineSegment(sketch, "E7408", {"start": v(84.4, -2.1) * mm, "end": v(84.33, -2.15) * mm});
            skLineSegment(sketch, "E7409", {"start": v(84.33, -2.15) * mm, "end": v(84.27, -2.2) * mm});
            skLineSegment(sketch, "E7410", {"start": v(84.27, -2.2) * mm, "end": v(84.2, -2.27) * mm});
            skLineSegment(sketch, "E7411", {"start": v(84.2, -2.27) * mm, "end": v(84.14, -2.32) * mm});
            skLineSegment(sketch, "E7412", {"start": v(84.02, -2.45) * mm, "end": v(83.96, -2.51) * mm});
            skLineSegment(sketch, "E7413", {"start": v(83.96, -2.51) * mm, "end": v(83.9, -2.58) * mm});
            skLineSegment(sketch, "E7414", {"start": v(83.9, -2.58) * mm, "end": v(83.85, -2.65) * mm});
            skLineSegment(sketch, "E7415", {"start": v(83.85, -2.65) * mm, "end": v(83.8, -2.72) * mm});
            skLineSegment(sketch, "E7416", {"start": v(83.8, -2.72) * mm, "end": v(83.75, -2.8) * mm});
            skLineSegment(sketch, "E7417", {"start": v(83.75, -2.8) * mm, "end": v(83.7, -2.87) * mm});
            skLineSegment(sketch, "E7418", {"start": v(83.7, -2.87) * mm, "end": v(83.67, -2.94) * mm});
            skLineSegment(sketch, "E7419", {"start": v(83.67, -2.94) * mm, "end": v(83.63, -3.02) * mm});
            skLineSegment(sketch, "E7420", {"start": v(83.63, -3.02) * mm, "end": v(83.59, -3.1) * mm});
            skLineSegment(sketch, "E7421", {"start": v(83.59, -3.1) * mm, "end": v(83.55, -3.18) * mm});
            skLineSegment(sketch, "E7422", {"start": v(83.55, -3.18) * mm, "end": v(83.52, -3.26) * mm});
            skLineSegment(sketch, "E7423", {"start": v(83.5, -3.34) * mm, "end": v(83.47, -3.42) * mm});
            skLineSegment(sketch, "E7424", {"start": v(83.47, -3.42) * mm, "end": v(83.44, -3.5) * mm});
            skLineSegment(sketch, "E7425", {"start": v(83.44, -3.5) * mm, "end": v(83.42, -3.6) * mm});
            skLineSegment(sketch, "E7426", {"start": v(83.42, -3.6) * mm, "end": v(83.4, -3.68) * mm});
            skLineSegment(sketch, "E7427", {"start": v(83.4, -3.68) * mm, "end": v(83.4, -3.76) * mm});
            skLineSegment(sketch, "E7428", {"start": v(83.4, -3.76) * mm, "end": v(83.38, -3.85) * mm});
            skLineSegment(sketch, "E7429", {"start": v(83.38, -3.85) * mm, "end": v(83.37, -3.94) * mm});
            skLineSegment(sketch, "E7430", {"start": v(83.37, -3.94) * mm, "end": v(83.37, -4.02) * mm});
            skLineSegment(sketch, "E7431", {"start": v(83.37, -4.02) * mm, "end": v(83.37, -4.1) * mm});
            skLineSegment(sketch, "E7432", {"start": v(83.37, -4.1) * mm, "end": v(83.37, -4.2) * mm});
            skLineSegment(sketch, "E7433", {"start": v(83.37, -4.2) * mm, "end": v(83.37, -4.28) * mm});
            skLineSegment(sketch, "E7434", {"start": v(83.37, -4.28) * mm, "end": v(83.38, -4.37) * mm});
            skLineSegment(sketch, "E7435", {"start": v(83.38, -4.37) * mm, "end": v(83.39, -4.45) * mm});
            skLineSegment(sketch, "E7436", {"start": v(83.39, -4.45) * mm, "end": v(83.4, -4.54) * mm});
            skLineSegment(sketch, "E7437", {"start": v(83.4, -4.54) * mm, "end": v(83.42, -4.63) * mm});
            skLineSegment(sketch, "E7438", {"start": v(83.42, -4.63) * mm, "end": v(83.43, -4.71) * mm});
            skLineSegment(sketch, "E7439", {"start": v(83.43, -4.71) * mm, "end": v(83.46, -4.8) * mm});
            skLineSegment(sketch, "E7440", {"start": v(83.48, -4.88) * mm, "end": v(83.5, -4.96) * mm});
            skLineSegment(sketch, "E7441", {"start": v(83.5, -4.96) * mm, "end": v(83.54, -5.04) * mm});
            skLineSegment(sketch, "E7442", {"start": v(83.54, -5.04) * mm, "end": v(83.57, -5.12) * mm});
            skLineSegment(sketch, "E7443", {"start": v(83.57, -5.12) * mm, "end": v(83.6, -5.2) * mm});
            skLineSegment(sketch, "E7444", {"start": v(83.6, -5.2) * mm, "end": v(83.65, -5.28) * mm});
            skLineSegment(sketch, "E7445", {"start": v(83.65, -5.28) * mm, "end": v(83.69, -5.36) * mm});
            skLineSegment(sketch, "E7446", {"start": v(83.69, -5.36) * mm, "end": v(83.73, -5.43) * mm});
            skLineSegment(sketch, "E7447", {"start": v(83.73, -5.43) * mm, "end": v(83.78, -5.5) * mm});
            skLineSegment(sketch, "E7448", {"start": v(83.78, -5.5) * mm, "end": v(83.83, -5.58) * mm});
            skLineSegment(sketch, "E7449", {"start": v(83.93, -5.71) * mm, "end": v(83.99, -5.78) * mm});
            skLineSegment(sketch, "E7450", {"start": v(84.04, -5.84) * mm, "end": v(84.1, -5.9) * mm});
            skLineSegment(sketch, "E7451", {"start": v(84.1, -5.9) * mm, "end": v(84.17, -5.97) * mm});
            skLineSegment(sketch, "E7452", {"start": v(84.17, -5.97) * mm, "end": v(84.23, -6.02) * mm});
            skLineSegment(sketch, "E7453", {"start": v(84.23, -6.02) * mm, "end": v(84.3, -6.08) * mm});
            skLineSegment(sketch, "E7454", {"start": v(84.3, -6.08) * mm, "end": v(84.37, -6.13) * mm});
            skLineSegment(sketch, "E7455", {"start": v(84.37, -6.13) * mm, "end": v(84.44, -6.18) * mm});
            skLineSegment(sketch, "E7456", {"start": v(84.44, -6.18) * mm, "end": v(84.51, -6.23) * mm});
            skLineSegment(sketch, "E7457", {"start": v(84.51, -6.23) * mm, "end": v(84.58, -6.28) * mm});
            skLineSegment(sketch, "E7458", {"start": v(84.58, -6.28) * mm, "end": v(84.66, -6.32) * mm});
            skLineSegment(sketch, "E7459", {"start": v(84.66, -6.32) * mm, "end": v(84.74, -6.36) * mm});
            skLineSegment(sketch, "E7460", {"start": v(84.74, -6.36) * mm, "end": v(84.81, -6.4) * mm});
            skLineSegment(sketch, "E7461", {"start": v(84.81, -6.4) * mm, "end": v(84.9, -6.43) * mm});
            skLineSegment(sketch, "E7462", {"start": v(84.97, -6.47) * mm, "end": v(85.06, -6.5) * mm});
            skLineSegment(sketch, "E7463", {"start": v(85.06, -6.5) * mm, "end": v(85.14, -6.52) * mm});
            skLineSegment(sketch, "E7464", {"start": v(85.14, -6.52) * mm, "end": v(85.22, -6.55) * mm});
            skLineSegment(sketch, "E7465", {"start": v(85.22, -6.55) * mm, "end": v(85.3, -6.57) * mm});
            skLineSegment(sketch, "E7466", {"start": v(85.3, -6.57) * mm, "end": v(85.4, -6.58) * mm});
            skLineSegment(sketch, "E7467", {"start": v(85.4, -6.58) * mm, "end": v(85.48, -6.6) * mm});
            skLineSegment(sketch, "E7468", {"start": v(85.48, -6.6) * mm, "end": v(85.56, -6.61) * mm});
            skLineSegment(sketch, "E7469", {"start": v(85.56, -6.61) * mm, "end": v(85.65, -6.62) * mm});
            skLineSegment(sketch, "E7470", {"start": v(85.65, -6.62) * mm, "end": v(85.74, -6.63) * mm});
            skLineSegment(sketch, "E7471", {"start": v(85.74, -6.63) * mm, "end": v(85.82, -6.63) * mm});
            skLineSegment(sketch, "E7472", {"start": v(85.82, -6.63) * mm, "end": v(85.9, -6.63) * mm});
            skLineSegment(sketch, "E7473", {"start": v(85.9, -6.63) * mm, "end": v(86, -6.63) * mm});
            skLineSegment(sketch, "E7474", {"start": v(86, -6.63) * mm, "end": v(86.08, -6.62) * mm});
            skLineSegment(sketch, "E7475", {"start": v(86.08, -6.62) * mm, "end": v(86.17, -6.61) * mm});
            skLineSegment(sketch, "E7476", {"start": v(86.17, -6.61) * mm, "end": v(86.25, -6.6) * mm});
            skLineSegment(sketch, "E7477", {"start": v(86.25, -6.6) * mm, "end": v(86.34, -6.58) * mm});
            skLineSegment(sketch, "E7478", {"start": v(86.34, -6.58) * mm, "end": v(86.42, -6.57) * mm});
            skLineSegment(sketch, "E7479", {"start": v(86.42, -6.57) * mm, "end": v(86.5, -6.55) * mm});
            skLineSegment(sketch, "E7480", {"start": v(86.5, -6.55) * mm, "end": v(86.6, -6.52) * mm});
            skLineSegment(sketch, "E7481", {"start": v(86.6, -6.52) * mm, "end": v(86.68, -6.5) * mm});
            skLineSegment(sketch, "E7482", {"start": v(86.68, -6.5) * mm, "end": v(86.76, -6.47) * mm});
            skLineSegment(sketch, "E7483", {"start": v(86.76, -6.47) * mm, "end": v(86.84, -6.43) * mm});
            skLineSegment(sketch, "E7484", {"start": v(86.84, -6.43) * mm, "end": v(86.92, -6.4) * mm});
            skLineSegment(sketch, "E7485", {"start": v(86.92, -6.4) * mm, "end": v(87, -6.36) * mm});
            skLineSegment(sketch, "E7486", {"start": v(87, -6.36) * mm, "end": v(87.07, -6.32) * mm});
            skLineSegment(sketch, "E7487", {"start": v(87.07, -6.32) * mm, "end": v(87.15, -6.28) * mm});
            skLineSegment(sketch, "E7488", {"start": v(87.15, -6.28) * mm, "end": v(87.22, -6.23) * mm});
            skLineSegment(sketch, "E7489", {"start": v(87.22, -6.23) * mm, "end": v(87.3, -6.18) * mm});
            skLineSegment(sketch, "E7490", {"start": v(87.3, -6.18) * mm, "end": v(87.36, -6.13) * mm});
            skLineSegment(sketch, "E7491", {"start": v(87.36, -6.13) * mm, "end": v(87.43, -6.08) * mm});
            skLineSegment(sketch, "E7492", {"start": v(87.43, -6.08) * mm, "end": v(87.5, -6.02) * mm});
            skLineSegment(sketch, "E7493", {"start": v(87.5, -6.02) * mm, "end": v(87.56, -5.97) * mm});
            skLineSegment(sketch, "E7494", {"start": v(87.69, -5.84) * mm, "end": v(87.74, -5.78) * mm});
            skLineSegment(sketch, "E7495", {"start": v(87.74, -5.78) * mm, "end": v(87.8, -5.71) * mm});
            skLineSegment(sketch, "E7496", {"start": v(87.8, -5.71) * mm, "end": v(87.85, -5.65) * mm});
            skLineSegment(sketch, "E7497", {"start": v(87.85, -5.65) * mm, "end": v(87.9, -5.58) * mm});
            skLineSegment(sketch, "E7498", {"start": v(87.9, -5.58) * mm, "end": v(87.95, -5.5) * mm});
            skLineSegment(sketch, "E7499", {"start": v(87.95, -5.5) * mm, "end": v(88, -5.43) * mm});
            skLineSegment(sketch, "E7500", {"start": v(88, -5.43) * mm, "end": v(88.05, -5.36) * mm});
            skLineSegment(sketch, "E7501", {"start": v(88.05, -5.36) * mm, "end": v(88.09, -5.28) * mm});
            skLineSegment(sketch, "E7502", {"start": v(88.09, -5.28) * mm, "end": v(88.12, -5.2) * mm});
            skLineSegment(sketch, "E7503", {"start": v(88.12, -5.2) * mm, "end": v(88.16, -5.12) * mm});
            skLineSegment(sketch, "E7504", {"start": v(88.16, -5.12) * mm, "end": v(88.2, -5.04) * mm});
            skLineSegment(sketch, "E7505", {"start": v(88.2, -5.04) * mm, "end": v(88.22, -4.96) * mm});
            skLineSegment(sketch, "E7506", {"start": v(88.22, -4.96) * mm, "end": v(88.25, -4.88) * mm});
            skLineSegment(sketch, "E7507", {"start": v(88.28, -4.8) * mm, "end": v(88.3, -4.71) * mm});
            skLineSegment(sketch, "E7508", {"start": v(88.3, -4.71) * mm, "end": v(88.32, -4.63) * mm});
            skLineSegment(sketch, "E7509", {"start": v(88.32, -4.63) * mm, "end": v(88.33, -4.54) * mm});
            skLineSegment(sketch, "E7510", {"start": v(88.33, -4.54) * mm, "end": v(88.34, -4.45) * mm});
            skLineSegment(sketch, "E7511", {"start": v(88.34, -4.45) * mm, "end": v(88.35, -4.37) * mm});
            skLineSegment(sketch, "E7512", {"start": v(88.35, -4.37) * mm, "end": v(88.36, -4.28) * mm});
            skLineSegment(sketch, "E7513", {"start": v(88.36, -4.28) * mm, "end": v(88.36, -4.2) * mm});
            skLineSegment(sketch, "E7514", {"start": v(88.36, -4.2) * mm, "end": v(88.37, -4.1) * mm});
            skLineSegment(sketch, "E7515", {"start": v(88.37, -4.1) * mm, "end": v(88.36, -4.02) * mm});
            skLineSegment(sketch, "E7516", {"start": v(88.36, -4.02) * mm, "end": v(88.36, -3.94) * mm});
            skLineSegment(sketch, "E7517", {"start": v(88.36, -3.94) * mm, "end": v(88.35, -3.85) * mm});
            skLineSegment(sketch, "E7518", {"start": v(88.35, -3.85) * mm, "end": v(88.34, -3.76) * mm});
            skLineSegment(sketch, "E7519", {"start": v(88.34, -3.76) * mm, "end": v(88.32, -3.68) * mm});
            skLineSegment(sketch, "E7520", {"start": v(88.32, -3.68) * mm, "end": v(88.3, -3.6) * mm});
            skLineSegment(sketch, "E7521", {"start": v(88.3, -3.6) * mm, "end": v(88.29, -3.5) * mm});
            skLineSegment(sketch, "E7522", {"start": v(88.29, -3.5) * mm, "end": v(88.26, -3.42) * mm});
            skLineSegment(sketch, "E7523", {"start": v(88.26, -3.42) * mm, "end": v(88.24, -3.34) * mm});
            skLineSegment(sketch, "E7524", {"start": v(88.24, -3.34) * mm, "end": v(88.2, -3.26) * mm});
            skLineSegment(sketch, "E7525", {"start": v(88.18, -3.18) * mm, "end": v(88.14, -3.1) * mm});
            skLineSegment(sketch, "E7526", {"start": v(88.14, -3.1) * mm, "end": v(88.1, -3.02) * mm});
            skLineSegment(sketch, "E7527", {"start": v(88.1, -3.02) * mm, "end": v(88.07, -2.94) * mm});
            skLineSegment(sketch, "E7528", {"start": v(88.07, -2.94) * mm, "end": v(88.02, -2.87) * mm});
            skLineSegment(sketch, "E7529", {"start": v(88.02, -2.87) * mm, "end": v(87.98, -2.8) * mm});
            skLineSegment(sketch, "E7530", {"start": v(87.98, -2.8) * mm, "end": v(87.93, -2.72) * mm});
            skLineSegment(sketch, "E7531", {"start": v(87.93, -2.72) * mm, "end": v(87.88, -2.65) * mm});
            skLineSegment(sketch, "E7532", {"start": v(87.88, -2.65) * mm, "end": v(87.83, -2.58) * mm});
            skLineSegment(sketch, "E7533", {"start": v(87.83, -2.58) * mm, "end": v(87.77, -2.51) * mm});
            skLineSegment(sketch, "E7534", {"start": v(87.77, -2.51) * mm, "end": v(87.72, -2.45) * mm});
            skLineSegment(sketch, "E7535", {"start": v(87.72, -2.45) * mm, "end": v(87.66, -2.39) * mm});
            skLineSegment(sketch, "E7536", {"start": v(87.66, -2.39) * mm, "end": v(87.6, -2.32) * mm});
            skLineSegment(sketch, "E7537", {"start": v(87.53, -2.27) * mm, "end": v(87.47, -2.2) * mm});
            skLineSegment(sketch, "E7538", {"start": v(87.33, -2.1) * mm, "end": v(87.26, -2.05) * mm});
            skLineSegment(sketch, "E7539", {"start": v(87.26, -2.05) * mm, "end": v(87.18, -2) * mm});
            skLineSegment(sketch, "E7540", {"start": v(87.18, -2) * mm, "end": v(87.1, -1.96) * mm});
            skLineSegment(sketch, "E7541", {"start": v(87.1, -1.96) * mm, "end": v(87.03, -1.92) * mm});
            skLineSegment(sketch, "E7542", {"start": v(87.03, -1.92) * mm, "end": v(86.96, -1.88) * mm});
            skLineSegment(sketch, "E7543", {"start": v(86.96, -1.88) * mm, "end": v(86.88, -1.84) * mm});
            skLineSegment(sketch, "E7544", {"start": v(86.88, -1.84) * mm, "end": v(86.8, -1.81) * mm});
            skLineSegment(sketch, "E7545", {"start": v(86.8, -1.81) * mm, "end": v(86.72, -1.78) * mm});
            skLineSegment(sketch, "E7546", {"start": v(86.72, -1.78) * mm, "end": v(86.63, -1.75) * mm});
            skLineSegment(sketch, "E7547", {"start": v(86.63, -1.75) * mm, "end": v(86.55, -1.73) * mm});
            skLineSegment(sketch, "E7548", {"start": v(86.47, -1.7) * mm, "end": v(86.38, -1.68) * mm});
            skLineSegment(sketch, "E7549", {"start": v(86.38, -1.68) * mm, "end": v(86.3, -1.67) * mm});
            skLineSegment(sketch, "E7550", {"start": v(86.3, -1.67) * mm, "end": v(86.21, -1.65) * mm});
            skLineSegment(sketch, "E7551", {"start": v(86.21, -1.65) * mm, "end": v(86.13, -1.64) * mm});
            skLineSegment(sketch, "E7552", {"start": v(86.13, -1.64) * mm, "end": v(86.04, -1.64) * mm});
            skLineSegment(sketch, "E7553", {"start": v(86.04, -1.64) * mm, "end": v(85.95, -1.63) * mm});
            skLineSegment(sketch, "E7554", {"start": v(85.95, -1.63) * mm, "end": v(85.87, -1.63) * mm});
            skLineSegment(sketch, "E7555", {"start": v(-41.63, -1.63) * mm, "end": v(-41.72, -1.63) * mm});
            skLineSegment(sketch, "E7556", {"start": v(-41.72, -1.63) * mm, "end": v(-41.8, -1.64) * mm});
            skLineSegment(sketch, "E7557", {"start": v(-41.8, -1.64) * mm, "end": v(-41.9, -1.64) * mm});
            skLineSegment(sketch, "E7558", {"start": v(-41.9, -1.64) * mm, "end": v(-41.98, -1.65) * mm});
            skLineSegment(sketch, "E7559", {"start": v(-41.98, -1.65) * mm, "end": v(-42.07, -1.67) * mm});
            skLineSegment(sketch, "E7560", {"start": v(-42.07, -1.67) * mm, "end": v(-42.15, -1.68) * mm});
            skLineSegment(sketch, "E7561", {"start": v(-42.15, -1.68) * mm, "end": v(-42.24, -1.7) * mm});
            skLineSegment(sketch, "E7562", {"start": v(-42.32, -1.73) * mm, "end": v(-42.4, -1.75) * mm});
            skLineSegment(sketch, "E7563", {"start": v(-42.4, -1.75) * mm, "end": v(-42.48, -1.78) * mm});
            skLineSegment(sketch, "E7564", {"start": v(-42.48, -1.78) * mm, "end": v(-42.57, -1.81) * mm});
            skLineSegment(sketch, "E7565", {"start": v(-42.57, -1.81) * mm, "end": v(-42.65, -1.84) * mm});
            skLineSegment(sketch, "E7566", {"start": v(-42.65, -1.84) * mm, "end": v(-42.72, -1.88) * mm});
            skLineSegment(sketch, "E7567", {"start": v(-42.72, -1.88) * mm, "end": v(-42.8, -1.92) * mm});
            skLineSegment(sketch, "E7568", {"start": v(-42.8, -1.92) * mm, "end": v(-42.88, -1.96) * mm});
            skLineSegment(sketch, "E7569", {"start": v(-42.88, -1.96) * mm, "end": v(-42.95, -2) * mm});
            skLineSegment(sketch, "E7570", {"start": v(-42.95, -2) * mm, "end": v(-43.03, -2.05) * mm});
            skLineSegment(sketch, "E7571", {"start": v(-43.03, -2.05) * mm, "end": v(-43.1, -2.1) * mm});
            skLineSegment(sketch, "E7572", {"start": v(-43.23, -2.2) * mm, "end": v(-43.3, -2.27) * mm});
            skLineSegment(sketch, "E7573", {"start": v(-43.36, -2.32) * mm, "end": v(-43.42, -2.39) * mm});
            skLineSegment(sketch, "E7574", {"start": v(-43.42, -2.39) * mm, "end": v(-43.48, -2.45) * mm});
            skLineSegment(sketch, "E7575", {"start": v(-43.48, -2.45) * mm, "end": v(-43.54, -2.51) * mm});
            skLineSegment(sketch, "E7576", {"start": v(-43.54, -2.51) * mm, "end": v(-43.6, -2.58) * mm});
            skLineSegment(sketch, "E7577", {"start": v(-43.6, -2.58) * mm, "end": v(-43.65, -2.65) * mm});
            skLineSegment(sketch, "E7578", {"start": v(-43.65, -2.65) * mm, "end": v(-43.7, -2.72) * mm});
            skLineSegment(sketch, "E7579", {"start": v(-43.7, -2.72) * mm, "end": v(-43.75, -2.8) * mm});
            skLineSegment(sketch, "E7580", {"start": v(-43.75, -2.8) * mm, "end": v(-43.8, -2.87) * mm});
            skLineSegment(sketch, "E7581", {"start": v(-43.8, -2.87) * mm, "end": v(-43.83, -2.94) * mm});
            skLineSegment(sketch, "E7582", {"start": v(-43.83, -2.94) * mm, "end": v(-43.87, -3.02) * mm});
            skLineSegment(sketch, "E7583", {"start": v(-43.87, -3.02) * mm, "end": v(-43.91, -3.1) * mm});
            skLineSegment(sketch, "E7584", {"start": v(-43.91, -3.1) * mm, "end": v(-43.95, -3.18) * mm});
            skLineSegment(sketch, "E7585", {"start": v(-43.98, -3.26) * mm, "end": v(-44, -3.34) * mm});
            skLineSegment(sketch, "E7586", {"start": v(-44, -3.34) * mm, "end": v(-44.03, -3.42) * mm});
            skLineSegment(sketch, "E7587", {"start": v(-44.03, -3.42) * mm, "end": v(-44.06, -3.5) * mm});
            skLineSegment(sketch, "E7588", {"start": v(-44.06, -3.5) * mm, "end": v(-44.08, -3.6) * mm});
            skLineSegment(sketch, "E7589", {"start": v(-44.08, -3.6) * mm, "end": v(-44.1, -3.68) * mm});
            skLineSegment(sketch, "E7590", {"start": v(-44.1, -3.68) * mm, "end": v(-44.1, -3.76) * mm});
            skLineSegment(sketch, "E7591", {"start": v(-44.1, -3.76) * mm, "end": v(-44.12, -3.85) * mm});
            skLineSegment(sketch, "E7592", {"start": v(-44.12, -3.85) * mm, "end": v(-44.13, -3.94) * mm});
            skLineSegment(sketch, "E7593", {"start": v(-44.13, -3.94) * mm, "end": v(-44.13, -4.02) * mm});
            skLineSegment(sketch, "E7594", {"start": v(-44.13, -4.02) * mm, "end": v(-44.13, -4.1) * mm});
            skLineSegment(sketch, "E7595", {"start": v(-44.13, -4.1) * mm, "end": v(-44.13, -4.2) * mm});
            skLineSegment(sketch, "E7596", {"start": v(-44.13, -4.2) * mm, "end": v(-44.13, -4.28) * mm});
            skLineSegment(sketch, "E7597", {"start": v(-44.13, -4.28) * mm, "end": v(-44.12, -4.37) * mm});
            skLineSegment(sketch, "E7598", {"start": v(-44.12, -4.37) * mm, "end": v(-44.11, -4.45) * mm});
            skLineSegment(sketch, "E7599", {"start": v(-44.11, -4.45) * mm, "end": v(-44.1, -4.54) * mm});
            skLineSegment(sketch, "E7600", {"start": v(-44.1, -4.54) * mm, "end": v(-44.08, -4.63) * mm});
            skLineSegment(sketch, "E7601", {"start": v(-44.08, -4.63) * mm, "end": v(-44.07, -4.71) * mm});
            skLineSegment(sketch, "E7602", {"start": v(-44.07, -4.71) * mm, "end": v(-44.04, -4.8) * mm});
            skLineSegment(sketch, "E7603", {"start": v(-44.02, -4.88) * mm, "end": v(-44, -4.96) * mm});
            skLineSegment(sketch, "E7604", {"start": v(-44, -4.96) * mm, "end": v(-43.96, -5.04) * mm});
            skLineSegment(sketch, "E7605", {"start": v(-43.96, -5.04) * mm, "end": v(-43.93, -5.12) * mm});
            skLineSegment(sketch, "E7606", {"start": v(-43.93, -5.12) * mm, "end": v(-43.9, -5.2) * mm});
            skLineSegment(sketch, "E7607", {"start": v(-43.9, -5.2) * mm, "end": v(-43.85, -5.28) * mm});
            skLineSegment(sketch, "E7608", {"start": v(-43.85, -5.28) * mm, "end": v(-43.81, -5.36) * mm});
            skLineSegment(sketch, "E7609", {"start": v(-43.81, -5.36) * mm, "end": v(-43.77, -5.43) * mm});
            skLineSegment(sketch, "E7610", {"start": v(-43.77, -5.43) * mm, "end": v(-43.72, -5.5) * mm});
            skLineSegment(sketch, "E7611", {"start": v(-43.72, -5.5) * mm, "end": v(-43.67, -5.58) * mm});
            skLineSegment(sketch, "E7612", {"start": v(-43.67, -5.58) * mm, "end": v(-43.62, -5.65) * mm});
            skLineSegment(sketch, "E7613", {"start": v(-43.62, -5.65) * mm, "end": v(-43.57, -5.71) * mm});
            skLineSegment(sketch, "E7614", {"start": v(-43.57, -5.71) * mm, "end": v(-43.51, -5.78) * mm});
            skLineSegment(sketch, "E7615", {"start": v(-43.51, -5.78) * mm, "end": v(-43.46, -5.84) * mm});
            skLineSegment(sketch, "E7616", {"start": v(-43.33, -5.97) * mm, "end": v(-43.27, -6.02) * mm});
            skLineSegment(sketch, "E7617", {"start": v(-43.27, -6.02) * mm, "end": v(-43.2, -6.08) * mm});
            skLineSegment(sketch, "E7618", {"start": v(-43.2, -6.08) * mm, "end": v(-43.13, -6.13) * mm});
            skLineSegment(sketch, "E7619", {"start": v(-43.13, -6.13) * mm, "end": v(-43.06, -6.18) * mm});
            skLineSegment(sketch, "E7620", {"start": v(-43.06, -6.18) * mm, "end": v(-42.99, -6.23) * mm});
            skLineSegment(sketch, "E7621", {"start": v(-42.99, -6.23) * mm, "end": v(-42.92, -6.28) * mm});
            skLineSegment(sketch, "E7622", {"start": v(-42.92, -6.28) * mm, "end": v(-42.84, -6.32) * mm});
            skLineSegment(sketch, "E7623", {"start": v(-42.84, -6.32) * mm, "end": v(-42.76, -6.36) * mm});
            skLineSegment(sketch, "E7624", {"start": v(-42.76, -6.36) * mm, "end": v(-42.69, -6.4) * mm});
            skLineSegment(sketch, "E7625", {"start": v(-42.69, -6.4) * mm, "end": v(-42.6, -6.43) * mm});
            skLineSegment(sketch, "E7626", {"start": v(-42.6, -6.43) * mm, "end": v(-42.53, -6.47) * mm});
            skLineSegment(sketch, "E7627", {"start": v(-42.53, -6.47) * mm, "end": v(-42.44, -6.5) * mm});
            skLineSegment(sketch, "E7628", {"start": v(-42.44, -6.5) * mm, "end": v(-42.36, -6.52) * mm});
            skLineSegment(sketch, "E7629", {"start": v(-42.28, -6.55) * mm, "end": v(-42.2, -6.57) * mm});
            skLineSegment(sketch, "E7630", {"start": v(-42.2, -6.57) * mm, "end": v(-42.1, -6.58) * mm});
            skLineSegment(sketch, "E7631", {"start": v(-42.1, -6.58) * mm, "end": v(-42.02, -6.6) * mm});
            skLineSegment(sketch, "E7632", {"start": v(-42.02, -6.6) * mm, "end": v(-41.94, -6.61) * mm});
            skLineSegment(sketch, "E7633", {"start": v(-41.94, -6.61) * mm, "end": v(-41.85, -6.62) * mm});
            skLineSegment(sketch, "E7634", {"start": v(-41.85, -6.62) * mm, "end": v(-41.76, -6.63) * mm});
            skLineSegment(sketch, "E7635", {"start": v(-41.76, -6.63) * mm, "end": v(-41.68, -6.63) * mm});
            skLineSegment(sketch, "E7636", {"start": v(-41.68, -6.63) * mm, "end": v(-41.6, -6.63) * mm});
            skLineSegment(sketch, "E7637", {"start": v(-41.6, -6.63) * mm, "end": v(-41.5, -6.63) * mm});
            skLineSegment(sketch, "E7638", {"start": v(-41.5, -6.63) * mm, "end": v(-41.42, -6.62) * mm});
            skLineSegment(sketch, "E7639", {"start": v(-41.42, -6.62) * mm, "end": v(-41.33, -6.61) * mm});
            skLineSegment(sketch, "E7640", {"start": v(-41.33, -6.61) * mm, "end": v(-41.25, -6.6) * mm});
            skLineSegment(sketch, "E7641", {"start": v(-41.25, -6.6) * mm, "end": v(-41.16, -6.58) * mm});
            skLineSegment(sketch, "E7642", {"start": v(-41.16, -6.58) * mm, "end": v(-41.08, -6.57) * mm});
            skLineSegment(sketch, "E7643", {"start": v(-41.08, -6.57) * mm, "end": v(-41, -6.55) * mm});
            skLineSegment(sketch, "E7644", {"start": v(-41, -6.55) * mm, "end": v(-40.9, -6.52) * mm});
            skLineSegment(sketch, "E7645", {"start": v(-40.9, -6.52) * mm, "end": v(-40.82, -6.5) * mm});
            skLineSegment(sketch, "E7646", {"start": v(-40.82, -6.5) * mm, "end": v(-40.74, -6.47) * mm});
            skLineSegment(sketch, "E7647", {"start": v(-40.66, -6.43) * mm, "end": v(-40.58, -6.4) * mm});
            skLineSegment(sketch, "E7648", {"start": v(-40.58, -6.4) * mm, "end": v(-40.5, -6.36) * mm});
            skLineSegment(sketch, "E7649", {"start": v(-40.5, -6.36) * mm, "end": v(-40.43, -6.32) * mm});
            skLineSegment(sketch, "E7650", {"start": v(-40.43, -6.32) * mm, "end": v(-40.35, -6.28) * mm});
            skLineSegment(sketch, "E7651", {"start": v(-40.35, -6.28) * mm, "end": v(-40.28, -6.23) * mm});
            skLineSegment(sketch, "E7652", {"start": v(-40.28, -6.23) * mm, "end": v(-40.2, -6.18) * mm});
            skLineSegment(sketch, "E7653", {"start": v(-40.2, -6.18) * mm, "end": v(-40.14, -6.13) * mm});
            skLineSegment(sketch, "E7654", {"start": v(-40.14, -6.13) * mm, "end": v(-40.07, -6.08) * mm});
            skLineSegment(sketch, "E7655", {"start": v(-40.07, -6.08) * mm, "end": v(-40, -6.02) * mm});
            skLineSegment(sketch, "E7656", {"start": v(-40, -6.02) * mm, "end": v(-39.94, -5.97) * mm});
            skLineSegment(sketch, "E7657", {"start": v(-39.94, -5.97) * mm, "end": v(-39.87, -5.9) * mm});
            skLineSegment(sketch, "E7658", {"start": v(-39.87, -5.9) * mm, "end": v(-39.81, -5.84) * mm});
            skLineSegment(sketch, "E7659", {"start": v(-39.76, -5.78) * mm, "end": v(-39.7, -5.71) * mm});
            skLineSegment(sketch, "E7660", {"start": v(-39.6, -5.58) * mm, "end": v(-39.55, -5.5) * mm});
            skLineSegment(sketch, "E7661", {"start": v(-39.55, -5.5) * mm, "end": v(-39.5, -5.43) * mm});
            skLineSegment(sketch, "E7662", {"start": v(-39.5, -5.43) * mm, "end": v(-39.45, -5.36) * mm});
            skLineSegment(sketch, "E7663", {"start": v(-39.45, -5.36) * mm, "end": v(-39.41, -5.28) * mm});
            skLineSegment(sketch, "E7664", {"start": v(-39.41, -5.28) * mm, "end": v(-39.38, -5.2) * mm});
            skLineSegment(sketch, "E7665", {"start": v(-39.38, -5.2) * mm, "end": v(-39.34, -5.12) * mm});
            skLineSegment(sketch, "E7666", {"start": v(-39.34, -5.12) * mm, "end": v(-39.3, -5.04) * mm});
            skLineSegment(sketch, "E7667", {"start": v(-39.3, -5.04) * mm, "end": v(-39.28, -4.96) * mm});
            skLineSegment(sketch, "E7668", {"start": v(-39.28, -4.96) * mm, "end": v(-39.25, -4.88) * mm});
            skLineSegment(sketch, "E7669", {"start": v(-39.22, -4.8) * mm, "end": v(-39.2, -4.71) * mm});
            skLineSegment(sketch, "E7670", {"start": v(-39.2, -4.71) * mm, "end": v(-39.18, -4.63) * mm});
            skLineSegment(sketch, "E7671", {"start": v(-39.18, -4.63) * mm, "end": v(-39.17, -4.54) * mm});
            skLineSegment(sketch, "E7672", {"start": v(-39.17, -4.54) * mm, "end": v(-39.16, -4.45) * mm});
            skLineSegment(sketch, "E7673", {"start": v(-39.16, -4.45) * mm, "end": v(-39.15, -4.37) * mm});
            skLineSegment(sketch, "E7674", {"start": v(-39.15, -4.37) * mm, "end": v(-39.14, -4.28) * mm});
            skLineSegment(sketch, "E7675", {"start": v(-39.14, -4.28) * mm, "end": v(-39.14, -4.2) * mm});
            skLineSegment(sketch, "E7676", {"start": v(-39.14, -4.2) * mm, "end": v(-39.13, -4.1) * mm});
            skLineSegment(sketch, "E7677", {"start": v(-39.13, -4.1) * mm, "end": v(-39.14, -4.02) * mm});
            skLineSegment(sketch, "E7678", {"start": v(-39.14, -4.02) * mm, "end": v(-39.14, -3.94) * mm});
            skLineSegment(sketch, "E7679", {"start": v(-39.14, -3.94) * mm, "end": v(-39.15, -3.85) * mm});
            skLineSegment(sketch, "E7680", {"start": v(-39.15, -3.85) * mm, "end": v(-39.16, -3.76) * mm});
            skLineSegment(sketch, "E7681", {"start": v(-39.16, -3.76) * mm, "end": v(-39.18, -3.68) * mm});
            skLineSegment(sketch, "E7682", {"start": v(-39.18, -3.68) * mm, "end": v(-39.2, -3.6) * mm});
            skLineSegment(sketch, "E7683", {"start": v(-39.2, -3.6) * mm, "end": v(-39.21, -3.5) * mm});
            skLineSegment(sketch, "E7684", {"start": v(-39.21, -3.5) * mm, "end": v(-39.24, -3.42) * mm});
            skLineSegment(sketch, "E7685", {"start": v(-39.24, -3.42) * mm, "end": v(-39.26, -3.34) * mm});
            skLineSegment(sketch, "E7686", {"start": v(-39.3, -3.26) * mm, "end": v(-39.32, -3.18) * mm});
            skLineSegment(sketch, "E7687", {"start": v(-39.32, -3.18) * mm, "end": v(-39.36, -3.1) * mm});
            skLineSegment(sketch, "E7688", {"start": v(-39.36, -3.1) * mm, "end": v(-39.4, -3.02) * mm});
            skLineSegment(sketch, "E7689", {"start": v(-39.4, -3.02) * mm, "end": v(-39.43, -2.94) * mm});
            skLineSegment(sketch, "E7690", {"start": v(-39.43, -2.94) * mm, "end": v(-39.48, -2.87) * mm});
            skLineSegment(sketch, "E7691", {"start": v(-39.48, -2.87) * mm, "end": v(-39.52, -2.8) * mm});
            skLineSegment(sketch, "E7692", {"start": v(-39.52, -2.8) * mm, "end": v(-39.57, -2.72) * mm});
            skLineSegment(sketch, "E7693", {"start": v(-39.57, -2.72) * mm, "end": v(-39.62, -2.65) * mm});
            skLineSegment(sketch, "E7694", {"start": v(-39.62, -2.65) * mm, "end": v(-39.67, -2.58) * mm});
            skLineSegment(sketch, "E7695", {"start": v(-39.67, -2.58) * mm, "end": v(-39.73, -2.51) * mm});
            skLineSegment(sketch, "E7696", {"start": v(-39.73, -2.51) * mm, "end": v(-39.78, -2.45) * mm});
            skLineSegment(sketch, "E7697", {"start": v(-39.9, -2.32) * mm, "end": v(-39.97, -2.27) * mm});
            skLineSegment(sketch, "E7698", {"start": v(-39.97, -2.27) * mm, "end": v(-40.03, -2.2) * mm});
            skLineSegment(sketch, "E7699", {"start": v(-40.03, -2.2) * mm, "end": v(-40.1, -2.15) * mm});
            skLineSegment(sketch, "E7700", {"start": v(-40.1, -2.15) * mm, "end": v(-40.17, -2.1) * mm});
            skLineSegment(sketch, "E7701", {"start": v(-40.17, -2.1) * mm, "end": v(-40.24, -2.05) * mm});
            skLineSegment(sketch, "E7702", {"start": v(-40.24, -2.05) * mm, "end": v(-40.32, -2) * mm});
            skLineSegment(sketch, "E7703", {"start": v(-40.32, -2) * mm, "end": v(-40.4, -1.96) * mm});
            skLineSegment(sketch, "E7704", {"start": v(-40.4, -1.96) * mm, "end": v(-40.47, -1.92) * mm});
            skLineSegment(sketch, "E7705", {"start": v(-40.47, -1.92) * mm, "end": v(-40.54, -1.88) * mm});
            skLineSegment(sketch, "E7706", {"start": v(-40.54, -1.88) * mm, "end": v(-40.62, -1.84) * mm});
            skLineSegment(sketch, "E7707", {"start": v(-40.62, -1.84) * mm, "end": v(-40.7, -1.81) * mm});
            skLineSegment(sketch, "E7708", {"start": v(-40.7, -1.81) * mm, "end": v(-40.78, -1.78) * mm});
            skLineSegment(sketch, "E7709", {"start": v(-40.78, -1.78) * mm, "end": v(-40.87, -1.75) * mm});
            skLineSegment(sketch, "E7710", {"start": v(-40.87, -1.75) * mm, "end": v(-40.95, -1.73) * mm});
            skLineSegment(sketch, "E7711", {"start": v(-40.95, -1.73) * mm, "end": v(-41.03, -1.7) * mm});
            skLineSegment(sketch, "E7712", {"start": v(-41.03, -1.7) * mm, "end": v(-41.12, -1.68) * mm});
            skLineSegment(sketch, "E7713", {"start": v(-41.12, -1.68) * mm, "end": v(-41.2, -1.67) * mm});
            skLineSegment(sketch, "E7714", {"start": v(-41.2, -1.67) * mm, "end": v(-41.29, -1.65) * mm});
            skLineSegment(sketch, "E7715", {"start": v(-41.29, -1.65) * mm, "end": v(-41.37, -1.64) * mm});
            skLineSegment(sketch, "E7716", {"start": v(-41.37, -1.64) * mm, "end": v(-41.46, -1.64) * mm});
            skLineSegment(sketch, "E7717", {"start": v(-41.46, -1.64) * mm, "end": v(-41.55, -1.63) * mm});
            skLineSegment(sketch, "E7718", {"start": v(-41.55, -1.63) * mm, "end": v(-41.63, -1.63) * mm});
            skLineSegment(sketch, "E7719", {"start": v(-222.63, 0.82) * mm, "end": v(-222.63, 6.32) * mm});
            skLineSegment(sketch, "E7720", {"start": v(-222.63, 6.32) * mm, "end": v(-226.83, 6.32) * mm});
            skLineSegment(sketch, "E7721", {"start": v(-226.83, 6.32) * mm, "end": v(-226.83, 0.82) * mm});
            skLineSegment(sketch, "E7722", {"start": v(-226.83, 0.82) * mm, "end": v(-222.63, 0.82) * mm});
            skLineSegment(sketch, "E7723", {"start": v(22.12, -2.88) * mm, "end": v(22.07, -2.88) * mm});
            skLineSegment(sketch, "E7724", {"start": v(22.07, -2.88) * mm, "end": v(22.03, -2.88) * mm});
            skLineSegment(sketch, "E7725", {"start": v(22.03, -2.88) * mm, "end": v(21.99, -2.89) * mm});
            skLineSegment(sketch, "E7726", {"start": v(21.99, -2.89) * mm, "end": v(21.94, -2.9) * mm});
            skLineSegment(sketch, "E7727", {"start": v(21.94, -2.9) * mm, "end": v(21.9, -2.9) * mm});
            skLineSegment(sketch, "E7728", {"start": v(21.9, -2.9) * mm, "end": v(21.86, -2.9) * mm});
            skLineSegment(sketch, "E7729", {"start": v(21.86, -2.9) * mm, "end": v(21.81, -2.92) * mm});
            skLineSegment(sketch, "E7730", {"start": v(21.81, -2.92) * mm, "end": v(21.77, -2.93) * mm});
            skLineSegment(sketch, "E7731", {"start": v(21.77, -2.93) * mm, "end": v(21.73, -2.94) * mm});
            skLineSegment(sketch, "E7732", {"start": v(21.73, -2.94) * mm, "end": v(21.7, -2.95) * mm});
            skLineSegment(sketch, "E7733", {"start": v(21.7, -2.95) * mm, "end": v(21.65, -2.97) * mm});
            skLineSegment(sketch, "E7734", {"start": v(21.65, -2.97) * mm, "end": v(21.6, -2.99) * mm});
            skLineSegment(sketch, "E7735", {"start": v(21.6, -2.99) * mm, "end": v(21.57, -3) * mm});
            skLineSegment(sketch, "E7736", {"start": v(21.57, -3) * mm, "end": v(21.53, -3.03) * mm});
            skLineSegment(sketch, "E7737", {"start": v(21.53, -3.03) * mm, "end": v(21.5, -3.05) * mm});
            skLineSegment(sketch, "E7738", {"start": v(21.5, -3.05) * mm, "end": v(21.46, -3.07) * mm});
            skLineSegment(sketch, "E7739", {"start": v(21.46, -3.07) * mm, "end": v(21.42, -3.1) * mm});
            skLineSegment(sketch, "E7740", {"start": v(21.42, -3.1) * mm, "end": v(21.38, -3.12) * mm});
            skLineSegment(sketch, "E7741", {"start": v(21.38, -3.12) * mm, "end": v(21.35, -3.14) * mm});
            skLineSegment(sketch, "E7742", {"start": v(21.35, -3.14) * mm, "end": v(21.32, -3.17) * mm});
            skLineSegment(sketch, "E7743", {"start": v(21.32, -3.17) * mm, "end": v(21.28, -3.2) * mm});
            skLineSegment(sketch, "E7744", {"start": v(21.28, -3.2) * mm, "end": v(21.25, -3.23) * mm});
            skLineSegment(sketch, "E7745", {"start": v(21.25, -3.23) * mm, "end": v(21.22, -3.26) * mm});
            skLineSegment(sketch, "E7746", {"start": v(21.22, -3.26) * mm, "end": v(21.2, -3.29) * mm});
            skLineSegment(sketch, "E7747", {"start": v(21.2, -3.29) * mm, "end": v(21.16, -3.32) * mm});
            skLineSegment(sketch, "E7748", {"start": v(21.16, -3.32) * mm, "end": v(21.13, -3.36) * mm});
            skLineSegment(sketch, "E7749", {"start": v(21.13, -3.36) * mm, "end": v(21.1, -3.4) * mm});
            skLineSegment(sketch, "E7750", {"start": v(21.1, -3.4) * mm, "end": v(21.08, -3.43) * mm});
            skLineSegment(sketch, "E7751", {"start": v(21.08, -3.43) * mm, "end": v(21.06, -3.46) * mm});
            skLineSegment(sketch, "E7752", {"start": v(21.06, -3.46) * mm, "end": v(21.04, -3.5) * mm});
            skLineSegment(sketch, "E7753", {"start": v(21.04, -3.5) * mm, "end": v(21.02, -3.54) * mm});
            skLineSegment(sketch, "E7754", {"start": v(21.02, -3.54) * mm, "end": v(21, -3.58) * mm});
            skLineSegment(sketch, "E7755", {"start": v(21, -3.58) * mm, "end": v(20.98, -3.61) * mm});
            skLineSegment(sketch, "E7756", {"start": v(20.98, -3.61) * mm, "end": v(20.96, -3.65) * mm});
            skLineSegment(sketch, "E7757", {"start": v(20.96, -3.65) * mm, "end": v(20.94, -3.7) * mm});
            skLineSegment(sketch, "E7758", {"start": v(20.94, -3.7) * mm, "end": v(20.93, -3.74) * mm});
            skLineSegment(sketch, "E7759", {"start": v(20.93, -3.74) * mm, "end": v(20.92, -3.78) * mm});
            skLineSegment(sketch, "E7760", {"start": v(20.92, -3.78) * mm, "end": v(20.9, -3.82) * mm});
            skLineSegment(sketch, "E7761", {"start": v(20.9, -3.82) * mm, "end": v(20.9, -3.86) * mm});
            skLineSegment(sketch, "E7762", {"start": v(20.9, -3.86) * mm, "end": v(20.89, -3.9) * mm});
            skLineSegment(sketch, "E7763", {"start": v(20.89, -3.9) * mm, "end": v(20.88, -3.95) * mm});
            skLineSegment(sketch, "E7764", {"start": v(20.88, -3.95) * mm, "end": v(20.87, -3.99) * mm});
            skLineSegment(sketch, "E7765", {"start": v(20.87, -3.99) * mm, "end": v(20.87, -4.03) * mm});
            skLineSegment(sketch, "E7766", {"start": v(20.87, -4.03) * mm, "end": v(20.87, -4.08) * mm});
            skLineSegment(sketch, "E7767", {"start": v(20.87, -4.08) * mm, "end": v(20.87, -4.12) * mm});
            skLineSegment(sketch, "E7768", {"start": v(20.87, -4.12) * mm, "end": v(20.87, -4.16) * mm});
            skLineSegment(sketch, "E7769", {"start": v(20.87, -4.16) * mm, "end": v(20.87, -4.2) * mm});
            skLineSegment(sketch, "E7770", {"start": v(20.87, -4.2) * mm, "end": v(20.87, -4.25) * mm});
            skLineSegment(sketch, "E7771", {"start": v(20.87, -4.25) * mm, "end": v(20.88, -4.3) * mm});
            skLineSegment(sketch, "E7772", {"start": v(20.88, -4.3) * mm, "end": v(20.88, -4.34) * mm});
            skLineSegment(sketch, "E7773", {"start": v(20.88, -4.34) * mm, "end": v(20.9, -4.38) * mm});
            skLineSegment(sketch, "E7774", {"start": v(20.9, -4.38) * mm, "end": v(20.9, -4.42) * mm});
            skLineSegment(sketch, "E7775", {"start": v(20.9, -4.42) * mm, "end": v(20.91, -4.46) * mm});
            skLineSegment(sketch, "E7776", {"start": v(20.92, -4.5) * mm, "end": v(20.94, -4.55) * mm});
            skLineSegment(sketch, "E7777", {"start": v(20.94, -4.55) * mm, "end": v(20.95, -4.59) * mm});
            skLineSegment(sketch, "E7778", {"start": v(20.95, -4.59) * mm, "end": v(20.97, -4.63) * mm});
            skLineSegment(sketch, "E7779", {"start": v(20.97, -4.63) * mm, "end": v(20.99, -4.67) * mm});
            skLineSegment(sketch, "E7780", {"start": v(20.99, -4.67) * mm, "end": v(21, -4.7) * mm});
            skLineSegment(sketch, "E7781", {"start": v(21, -4.7) * mm, "end": v(21.03, -4.74) * mm});
            skLineSegment(sketch, "E7782", {"start": v(21.03, -4.74) * mm, "end": v(21.05, -4.78) * mm});
            skLineSegment(sketch, "E7783", {"start": v(21.05, -4.78) * mm, "end": v(21.07, -4.82) * mm});
            skLineSegment(sketch, "E7784", {"start": v(21.07, -4.82) * mm, "end": v(21.1, -4.85) * mm});
            skLineSegment(sketch, "E7785", {"start": v(21.1, -4.85) * mm, "end": v(21.12, -4.89) * mm});
            skLineSegment(sketch, "E7786", {"start": v(21.24, -5.02) * mm, "end": v(21.27, -5.05) * mm});
            skLineSegment(sketch, "E7787", {"start": v(21.27, -5.05) * mm, "end": v(21.3, -5.08) * mm});
            skLineSegment(sketch, "E7788", {"start": v(21.3, -5.08) * mm, "end": v(21.33, -5.1) * mm});
            skLineSegment(sketch, "E7789", {"start": v(21.33, -5.1) * mm, "end": v(21.37, -5.13) * mm});
            skLineSegment(sketch, "E7790", {"start": v(21.37, -5.13) * mm, "end": v(21.4, -5.16) * mm});
            skLineSegment(sketch, "E7791", {"start": v(21.4, -5.16) * mm, "end": v(21.44, -5.18) * mm});
            skLineSegment(sketch, "E7792", {"start": v(21.44, -5.18) * mm, "end": v(21.48, -5.2) * mm});
            skLineSegment(sketch, "E7793", {"start": v(21.48, -5.2) * mm, "end": v(21.51, -5.23) * mm});
            skLineSegment(sketch, "E7794", {"start": v(21.51, -5.23) * mm, "end": v(21.55, -5.25) * mm});
            skLineSegment(sketch, "E7795", {"start": v(21.55, -5.25) * mm, "end": v(21.6, -5.26) * mm});
            skLineSegment(sketch, "E7796", {"start": v(21.6, -5.26) * mm, "end": v(21.63, -5.28) * mm});
            skLineSegment(sketch, "E7797", {"start": v(21.63, -5.28) * mm, "end": v(21.67, -5.3) * mm});
            skLineSegment(sketch, "E7798", {"start": v(21.67, -5.3) * mm, "end": v(21.71, -5.31) * mm});
            skLineSegment(sketch, "E7799", {"start": v(21.71, -5.31) * mm, "end": v(21.75, -5.33) * mm});
            skLineSegment(sketch, "E7800", {"start": v(21.75, -5.33) * mm, "end": v(21.8, -5.34) * mm});
            skLineSegment(sketch, "E7801", {"start": v(21.8, -5.34) * mm, "end": v(21.84, -5.35) * mm});
            skLineSegment(sketch, "E7802", {"start": v(21.84, -5.35) * mm, "end": v(21.88, -5.36) * mm});
            skLineSegment(sketch, "E7803", {"start": v(21.88, -5.36) * mm, "end": v(21.92, -5.37) * mm});
            skLineSegment(sketch, "E7804", {"start": v(21.92, -5.37) * mm, "end": v(21.96, -5.37) * mm});
            skLineSegment(sketch, "E7805", {"start": v(21.96, -5.37) * mm, "end": v(22, -5.38) * mm});
            skLineSegment(sketch, "E7806", {"start": v(22, -5.38) * mm, "end": v(22.05, -5.38) * mm});
            skLineSegment(sketch, "E7807", {"start": v(22.05, -5.38) * mm, "end": v(22.1, -5.38) * mm});
            skLineSegment(sketch, "E7808", {"start": v(22.1, -5.38) * mm, "end": v(22.14, -5.38) * mm});
            skLineSegment(sketch, "E7809", {"start": v(22.14, -5.38) * mm, "end": v(22.18, -5.38) * mm});
            skLineSegment(sketch, "E7810", {"start": v(22.18, -5.38) * mm, "end": v(22.22, -5.38) * mm});
            skLineSegment(sketch, "E7811", {"start": v(22.22, -5.38) * mm, "end": v(22.27, -5.37) * mm});
            skLineSegment(sketch, "E7812", {"start": v(22.27, -5.37) * mm, "end": v(22.31, -5.37) * mm});
            skLineSegment(sketch, "E7813", {"start": v(22.31, -5.37) * mm, "end": v(22.35, -5.36) * mm});
            skLineSegment(sketch, "E7814", {"start": v(22.35, -5.36) * mm, "end": v(22.4, -5.35) * mm});
            skLineSegment(sketch, "E7815", {"start": v(22.4, -5.35) * mm, "end": v(22.44, -5.34) * mm});
            skLineSegment(sketch, "E7816", {"start": v(22.44, -5.34) * mm, "end": v(22.48, -5.33) * mm});
            skLineSegment(sketch, "E7817", {"start": v(22.48, -5.33) * mm, "end": v(22.52, -5.31) * mm});
            skLineSegment(sketch, "E7818", {"start": v(22.52, -5.31) * mm, "end": v(22.56, -5.3) * mm});
            skLineSegment(sketch, "E7819", {"start": v(22.56, -5.3) * mm, "end": v(22.6, -5.28) * mm});
            skLineSegment(sketch, "E7820", {"start": v(22.6, -5.28) * mm, "end": v(22.64, -5.26) * mm});
            skLineSegment(sketch, "E7821", {"start": v(22.64, -5.26) * mm, "end": v(22.68, -5.25) * mm});
            skLineSegment(sketch, "E7822", {"start": v(22.68, -5.25) * mm, "end": v(22.72, -5.23) * mm});
            skLineSegment(sketch, "E7823", {"start": v(22.72, -5.23) * mm, "end": v(22.76, -5.2) * mm});
            skLineSegment(sketch, "E7824", {"start": v(22.76, -5.2) * mm, "end": v(22.8, -5.18) * mm});
            skLineSegment(sketch, "E7825", {"start": v(22.8, -5.18) * mm, "end": v(22.83, -5.16) * mm});
            skLineSegment(sketch, "E7826", {"start": v(22.83, -5.16) * mm, "end": v(22.86, -5.13) * mm});
            skLineSegment(sketch, "E7827", {"start": v(22.86, -5.13) * mm, "end": v(22.9, -5.1) * mm});
            skLineSegment(sketch, "E7828", {"start": v(22.9, -5.1) * mm, "end": v(22.93, -5.08) * mm});
            skLineSegment(sketch, "E7829", {"start": v(22.93, -5.08) * mm, "end": v(22.96, -5.05) * mm});
            skLineSegment(sketch, "E7830", {"start": v(22.96, -5.05) * mm, "end": v(23, -5.02) * mm});
            skLineSegment(sketch, "E7831", {"start": v(23.11, -4.89) * mm, "end": v(23.14, -4.85) * mm});
            skLineSegment(sketch, "E7832", {"start": v(23.14, -4.85) * mm, "end": v(23.16, -4.82) * mm});
            skLineSegment(sketch, "E7833", {"start": v(23.16, -4.82) * mm, "end": v(23.18, -4.78) * mm});
            skLineSegment(sketch, "E7834", {"start": v(23.18, -4.78) * mm, "end": v(23.2, -4.74) * mm});
            skLineSegment(sketch, "E7835", {"start": v(23.2, -4.74) * mm, "end": v(23.23, -4.7) * mm});
            skLineSegment(sketch, "E7836", {"start": v(23.23, -4.7) * mm, "end": v(23.25, -4.67) * mm});
            skLineSegment(sketch, "E7837", {"start": v(23.25, -4.67) * mm, "end": v(23.26, -4.63) * mm});
            skLineSegment(sketch, "E7838", {"start": v(23.26, -4.63) * mm, "end": v(23.28, -4.59) * mm});
            skLineSegment(sketch, "E7839", {"start": v(23.28, -4.59) * mm, "end": v(23.3, -4.55) * mm});
            skLineSegment(sketch, "E7840", {"start": v(23.3, -4.55) * mm, "end": v(23.3, -4.5) * mm});
            skLineSegment(sketch, "E7841", {"start": v(23.32, -4.46) * mm, "end": v(23.33, -4.42) * mm});
            skLineSegment(sketch, "E7842", {"start": v(23.33, -4.42) * mm, "end": v(23.34, -4.38) * mm});
            skLineSegment(sketch, "E7843", {"start": v(23.34, -4.38) * mm, "end": v(23.35, -4.34) * mm});
            skLineSegment(sketch, "E7844", {"start": v(23.35, -4.34) * mm, "end": v(23.36, -4.3) * mm});
            skLineSegment(sketch, "E7845", {"start": v(23.36, -4.3) * mm, "end": v(23.36, -4.25) * mm});
            skLineSegment(sketch, "E7846", {"start": v(23.36, -4.25) * mm, "end": v(23.36, -4.2) * mm});
            skLineSegment(sketch, "E7847", {"start": v(23.36, -4.2) * mm, "end": v(23.37, -4.16) * mm});
            skLineSegment(sketch, "E7848", {"start": v(23.37, -4.16) * mm, "end": v(23.37, -4.12) * mm});
            skLineSegment(sketch, "E7849", {"start": v(23.37, -4.12) * mm, "end": v(23.36, -4.08) * mm});
            skLineSegment(sketch, "E7850", {"start": v(23.36, -4.08) * mm, "end": v(23.36, -4.03) * mm});
            skLineSegment(sketch, "E7851", {"start": v(23.36, -4.03) * mm, "end": v(23.36, -3.99) * mm});
            skLineSegment(sketch, "E7852", {"start": v(23.36, -3.99) * mm, "end": v(23.35, -3.95) * mm});
            skLineSegment(sketch, "E7853", {"start": v(23.35, -3.95) * mm, "end": v(23.34, -3.9) * mm});
            skLineSegment(sketch, "E7854", {"start": v(23.34, -3.9) * mm, "end": v(23.34, -3.86) * mm});
            skLineSegment(sketch, "E7855", {"start": v(23.34, -3.86) * mm, "end": v(23.33, -3.82) * mm});
            skLineSegment(sketch, "E7856", {"start": v(23.33, -3.82) * mm, "end": v(23.31, -3.78) * mm});
            skLineSegment(sketch, "E7857", {"start": v(23.31, -3.78) * mm, "end": v(23.3, -3.74) * mm});
            skLineSegment(sketch, "E7858", {"start": v(23.3, -3.74) * mm, "end": v(23.29, -3.7) * mm});
            skLineSegment(sketch, "E7859", {"start": v(23.29, -3.7) * mm, "end": v(23.27, -3.65) * mm});
            skLineSegment(sketch, "E7860", {"start": v(23.27, -3.65) * mm, "end": v(23.25, -3.61) * mm});
            skLineSegment(sketch, "E7861", {"start": v(23.25, -3.61) * mm, "end": v(23.24, -3.58) * mm});
            skLineSegment(sketch, "E7862", {"start": v(23.24, -3.58) * mm, "end": v(23.22, -3.54) * mm});
            skLineSegment(sketch, "E7863", {"start": v(23.22, -3.54) * mm, "end": v(23.2, -3.5) * mm});
            skLineSegment(sketch, "E7864", {"start": v(23.2, -3.5) * mm, "end": v(23.17, -3.46) * mm});
            skLineSegment(sketch, "E7865", {"start": v(23.17, -3.46) * mm, "end": v(23.15, -3.43) * mm});
            skLineSegment(sketch, "E7866", {"start": v(23.15, -3.43) * mm, "end": v(23.12, -3.4) * mm});
            skLineSegment(sketch, "E7867", {"start": v(23.12, -3.4) * mm, "end": v(23.1, -3.36) * mm});
            skLineSegment(sketch, "E7868", {"start": v(23.1, -3.36) * mm, "end": v(23.07, -3.32) * mm});
            skLineSegment(sketch, "E7869", {"start": v(23.07, -3.32) * mm, "end": v(23.04, -3.29) * mm});
            skLineSegment(sketch, "E7870", {"start": v(23.04, -3.29) * mm, "end": v(23.01, -3.26) * mm});
            skLineSegment(sketch, "E7871", {"start": v(23.01, -3.26) * mm, "end": v(22.98, -3.23) * mm});
            skLineSegment(sketch, "E7872", {"start": v(22.95, -3.2) * mm, "end": v(22.92, -3.17) * mm});
            skLineSegment(sketch, "E7873", {"start": v(22.92, -3.17) * mm, "end": v(22.88, -3.14) * mm});
            skLineSegment(sketch, "E7874", {"start": v(22.88, -3.14) * mm, "end": v(22.85, -3.12) * mm});
            skLineSegment(sketch, "E7875", {"start": v(22.85, -3.12) * mm, "end": v(22.81, -3.1) * mm});
            skLineSegment(sketch, "E7876", {"start": v(22.81, -3.1) * mm, "end": v(22.77, -3.07) * mm});
            skLineSegment(sketch, "E7877", {"start": v(22.77, -3.07) * mm, "end": v(22.74, -3.05) * mm});
            skLineSegment(sketch, "E7878", {"start": v(22.74, -3.05) * mm, "end": v(22.7, -3.03) * mm});
            skLineSegment(sketch, "E7879", {"start": v(22.7, -3.03) * mm, "end": v(22.66, -3) * mm});
            skLineSegment(sketch, "E7880", {"start": v(22.66, -3) * mm, "end": v(22.62, -2.99) * mm});
            skLineSegment(sketch, "E7881", {"start": v(22.62, -2.99) * mm, "end": v(22.58, -2.97) * mm});
            skLineSegment(sketch, "E7882", {"start": v(22.58, -2.97) * mm, "end": v(22.54, -2.95) * mm});
            skLineSegment(sketch, "E7883", {"start": v(22.54, -2.95) * mm, "end": v(22.5, -2.94) * mm});
            skLineSegment(sketch, "E7884", {"start": v(22.5, -2.94) * mm, "end": v(22.46, -2.93) * mm});
            skLineSegment(sketch, "E7885", {"start": v(22.46, -2.93) * mm, "end": v(22.42, -2.92) * mm});
            skLineSegment(sketch, "E7886", {"start": v(22.42, -2.92) * mm, "end": v(22.37, -2.9) * mm});
            skLineSegment(sketch, "E7887", {"start": v(22.37, -2.9) * mm, "end": v(22.33, -2.9) * mm});
            skLineSegment(sketch, "E7888", {"start": v(22.33, -2.9) * mm, "end": v(22.29, -2.9) * mm});
            skLineSegment(sketch, "E7889", {"start": v(22.29, -2.9) * mm, "end": v(22.25, -2.89) * mm});
            skLineSegment(sketch, "E7890", {"start": v(22.25, -2.89) * mm, "end": v(22.2, -2.88) * mm});
            skLineSegment(sketch, "E7891", {"start": v(22.2, -2.88) * mm, "end": v(22.16, -2.88) * mm});
            skLineSegment(sketch, "E7892", {"start": v(22.16, -2.88) * mm, "end": v(22.12, -2.88) * mm});
            skLineSegment(sketch, "E7893", {"start": v(85.87, -2.88) * mm, "end": v(85.82, -2.88) * mm});
            skLineSegment(sketch, "E7894", {"start": v(85.82, -2.88) * mm, "end": v(85.78, -2.88) * mm});
            skLineSegment(sketch, "E7895", {"start": v(85.78, -2.88) * mm, "end": v(85.74, -2.89) * mm});
            skLineSegment(sketch, "E7896", {"start": v(85.74, -2.89) * mm, "end": v(85.7, -2.9) * mm});
            skLineSegment(sketch, "E7897", {"start": v(85.7, -2.9) * mm, "end": v(85.65, -2.9) * mm});
            skLineSegment(sketch, "E7898", {"start": v(85.65, -2.9) * mm, "end": v(85.6, -2.9) * mm});
            skLineSegment(sketch, "E7899", {"start": v(85.6, -2.9) * mm, "end": v(85.56, -2.92) * mm});
            skLineSegment(sketch, "E7900", {"start": v(85.56, -2.92) * mm, "end": v(85.52, -2.93) * mm});
            skLineSegment(sketch, "E7901", {"start": v(85.52, -2.93) * mm, "end": v(85.48, -2.94) * mm});
            skLineSegment(sketch, "E7902", {"start": v(85.48, -2.94) * mm, "end": v(85.44, -2.95) * mm});
            skLineSegment(sketch, "E7903", {"start": v(85.44, -2.95) * mm, "end": v(85.4, -2.97) * mm});
            skLineSegment(sketch, "E7904", {"start": v(85.4, -2.97) * mm, "end": v(85.36, -2.99) * mm});
            skLineSegment(sketch, "E7905", {"start": v(85.36, -2.99) * mm, "end": v(85.32, -3) * mm});
            skLineSegment(sketch, "E7906", {"start": v(85.32, -3) * mm, "end": v(85.28, -3.03) * mm});
            skLineSegment(sketch, "E7907", {"start": v(85.28, -3.03) * mm, "end": v(85.24, -3.05) * mm});
            skLineSegment(sketch, "E7908", {"start": v(85.24, -3.05) * mm, "end": v(85.2, -3.07) * mm});
            skLineSegment(sketch, "E7909", {"start": v(85.2, -3.07) * mm, "end": v(85.17, -3.1) * mm});
            skLineSegment(sketch, "E7910", {"start": v(85.17, -3.1) * mm, "end": v(85.13, -3.12) * mm});
            skLineSegment(sketch, "E7911", {"start": v(85.13, -3.12) * mm, "end": v(85.1, -3.14) * mm});
            skLineSegment(sketch, "E7912", {"start": v(85.1, -3.14) * mm, "end": v(85.07, -3.17) * mm});
            skLineSegment(sketch, "E7913", {"start": v(85.07, -3.17) * mm, "end": v(85.03, -3.2) * mm});
            skLineSegment(sketch, "E7914", {"start": v(85.03, -3.2) * mm, "end": v(85, -3.23) * mm});
            skLineSegment(sketch, "E7915", {"start": v(84.97, -3.26) * mm, "end": v(84.94, -3.29) * mm});
            skLineSegment(sketch, "E7916", {"start": v(84.94, -3.29) * mm, "end": v(84.91, -3.32) * mm});
            skLineSegment(sketch, "E7917", {"start": v(84.91, -3.32) * mm, "end": v(84.88, -3.36) * mm});
            skLineSegment(sketch, "E7918", {"start": v(84.88, -3.36) * mm, "end": v(84.86, -3.4) * mm});
            skLineSegment(sketch, "E7919", {"start": v(84.86, -3.4) * mm, "end": v(84.83, -3.43) * mm});
            skLineSegment(sketch, "E7920", {"start": v(84.83, -3.43) * mm, "end": v(84.8, -3.46) * mm});
            skLineSegment(sketch, "E7921", {"start": v(84.8, -3.46) * mm, "end": v(84.79, -3.5) * mm});
            skLineSegment(sketch, "E7922", {"start": v(84.79, -3.5) * mm, "end": v(84.77, -3.54) * mm});
            skLineSegment(sketch, "E7923", {"start": v(84.77, -3.54) * mm, "end": v(84.75, -3.58) * mm});
            skLineSegment(sketch, "E7924", {"start": v(84.75, -3.58) * mm, "end": v(84.73, -3.61) * mm});
            skLineSegment(sketch, "E7925", {"start": v(84.73, -3.61) * mm, "end": v(84.7, -3.65) * mm});
            skLineSegment(sketch, "E7926", {"start": v(84.7, -3.65) * mm, "end": v(84.7, -3.7) * mm});
            skLineSegment(sketch, "E7927", {"start": v(84.7, -3.7) * mm, "end": v(84.68, -3.74) * mm});
            skLineSegment(sketch, "E7928", {"start": v(84.68, -3.74) * mm, "end": v(84.67, -3.78) * mm});
            skLineSegment(sketch, "E7929", {"start": v(84.67, -3.78) * mm, "end": v(84.66, -3.82) * mm});
            skLineSegment(sketch, "E7930", {"start": v(84.66, -3.82) * mm, "end": v(84.64, -3.86) * mm});
            skLineSegment(sketch, "E7931", {"start": v(84.64, -3.86) * mm, "end": v(84.64, -3.9) * mm});
            skLineSegment(sketch, "E7932", {"start": v(84.64, -3.9) * mm, "end": v(84.63, -3.95) * mm});
            skLineSegment(sketch, "E7933", {"start": v(84.63, -3.95) * mm, "end": v(84.62, -3.99) * mm});
            skLineSegment(sketch, "E7934", {"start": v(84.62, -3.99) * mm, "end": v(84.62, -4.03) * mm});
            skLineSegment(sketch, "E7935", {"start": v(84.62, -4.03) * mm, "end": v(84.62, -4.08) * mm});
            skLineSegment(sketch, "E7936", {"start": v(84.62, -4.08) * mm, "end": v(84.62, -4.12) * mm});
            skLineSegment(sketch, "E7937", {"start": v(84.62, -4.12) * mm, "end": v(84.62, -4.16) * mm});
            skLineSegment(sketch, "E7938", {"start": v(84.62, -4.16) * mm, "end": v(84.62, -4.2) * mm});
            skLineSegment(sketch, "E7939", {"start": v(84.62, -4.2) * mm, "end": v(84.62, -4.25) * mm});
            skLineSegment(sketch, "E7940", {"start": v(84.62, -4.25) * mm, "end": v(84.63, -4.3) * mm});
            skLineSegment(sketch, "E7941", {"start": v(84.63, -4.3) * mm, "end": v(84.63, -4.34) * mm});
            skLineSegment(sketch, "E7942", {"start": v(84.63, -4.34) * mm, "end": v(84.64, -4.38) * mm});
            skLineSegment(sketch, "E7943", {"start": v(84.64, -4.38) * mm, "end": v(84.65, -4.42) * mm});
            skLineSegment(sketch, "E7944", {"start": v(84.65, -4.42) * mm, "end": v(84.66, -4.46) * mm});
            skLineSegment(sketch, "E7945", {"start": v(84.66, -4.46) * mm, "end": v(84.67, -4.5) * mm});
            skLineSegment(sketch, "E7946", {"start": v(84.67, -4.5) * mm, "end": v(84.69, -4.55) * mm});
            skLineSegment(sketch, "E7947", {"start": v(84.69, -4.55) * mm, "end": v(84.7, -4.59) * mm});
            skLineSegment(sketch, "E7948", {"start": v(84.7, -4.59) * mm, "end": v(84.72, -4.63) * mm});
            skLineSegment(sketch, "E7949", {"start": v(84.72, -4.63) * mm, "end": v(84.74, -4.67) * mm});
            skLineSegment(sketch, "E7950", {"start": v(84.74, -4.67) * mm, "end": v(84.76, -4.7) * mm});
            skLineSegment(sketch, "E7951", {"start": v(84.76, -4.7) * mm, "end": v(84.78, -4.74) * mm});
            skLineSegment(sketch, "E7952", {"start": v(84.78, -4.74) * mm, "end": v(84.8, -4.78) * mm});
            skLineSegment(sketch, "E7953", {"start": v(84.8, -4.78) * mm, "end": v(84.82, -4.82) * mm});
            skLineSegment(sketch, "E7954", {"start": v(84.82, -4.82) * mm, "end": v(84.85, -4.85) * mm});
            skLineSegment(sketch, "E7955", {"start": v(84.85, -4.85) * mm, "end": v(84.87, -4.89) * mm});
            skLineSegment(sketch, "E7956", {"start": v(84.9, -4.92) * mm, "end": v(84.93, -4.95) * mm});
            skLineSegment(sketch, "E7957", {"start": v(84.93, -4.95) * mm, "end": v(84.96, -4.99) * mm});
            skLineSegment(sketch, "E7958", {"start": v(84.96, -4.99) * mm, "end": v(84.99, -5.02) * mm});
            skLineSegment(sketch, "E7959", {"start": v(84.99, -5.02) * mm, "end": v(85.02, -5.05) * mm});
            skLineSegment(sketch, "E7960", {"start": v(85.02, -5.05) * mm, "end": v(85.05, -5.08) * mm});
            skLineSegment(sketch, "E7961", {"start": v(85.05, -5.08) * mm, "end": v(85.08, -5.1) * mm});
            skLineSegment(sketch, "E7962", {"start": v(85.08, -5.1) * mm, "end": v(85.12, -5.13) * mm});
            skLineSegment(sketch, "E7963", {"start": v(85.12, -5.13) * mm, "end": v(85.15, -5.16) * mm});
            skLineSegment(sketch, "E7964", {"start": v(85.15, -5.16) * mm, "end": v(85.19, -5.18) * mm});
            skLineSegment(sketch, "E7965", {"start": v(85.19, -5.18) * mm, "end": v(85.23, -5.2) * mm});
            skLineSegment(sketch, "E7966", {"start": v(85.23, -5.2) * mm, "end": v(85.26, -5.23) * mm});
            skLineSegment(sketch, "E7967", {"start": v(85.26, -5.23) * mm, "end": v(85.3, -5.25) * mm});
            skLineSegment(sketch, "E7968", {"start": v(85.3, -5.25) * mm, "end": v(85.34, -5.26) * mm});
            skLineSegment(sketch, "E7969", {"start": v(85.34, -5.26) * mm, "end": v(85.38, -5.28) * mm});
            skLineSegment(sketch, "E7970", {"start": v(85.38, -5.28) * mm, "end": v(85.42, -5.3) * mm});
            skLineSegment(sketch, "E7971", {"start": v(85.42, -5.3) * mm, "end": v(85.46, -5.31) * mm});
            skLineSegment(sketch, "E7972", {"start": v(85.46, -5.31) * mm, "end": v(85.5, -5.33) * mm});
            skLineSegment(sketch, "E7973", {"start": v(85.5, -5.33) * mm, "end": v(85.54, -5.34) * mm});
            skLineSegment(sketch, "E7974", {"start": v(85.54, -5.34) * mm, "end": v(85.59, -5.35) * mm});
            skLineSegment(sketch, "E7975", {"start": v(85.59, -5.35) * mm, "end": v(85.63, -5.36) * mm});
            skLineSegment(sketch, "E7976", {"start": v(85.63, -5.36) * mm, "end": v(85.67, -5.37) * mm});
            skLineSegment(sketch, "E7977", {"start": v(85.67, -5.37) * mm, "end": v(85.71, -5.37) * mm});
            skLineSegment(sketch, "E7978", {"start": v(85.71, -5.37) * mm, "end": v(85.76, -5.38) * mm});
            skLineSegment(sketch, "E7979", {"start": v(85.76, -5.38) * mm, "end": v(85.8, -5.38) * mm});
            skLineSegment(sketch, "E7980", {"start": v(85.8, -5.38) * mm, "end": v(85.84, -5.38) * mm});
            skLineSegment(sketch, "E7981", {"start": v(85.84, -5.38) * mm, "end": v(85.89, -5.38) * mm});
            skLineSegment(sketch, "E7982", {"start": v(85.89, -5.38) * mm, "end": v(85.93, -5.38) * mm});
            skLineSegment(sketch, "E7983", {"start": v(85.93, -5.38) * mm, "end": v(85.97, -5.38) * mm});
            skLineSegment(sketch, "E7984", {"start": v(85.97, -5.38) * mm, "end": v(86.02, -5.37) * mm});
            skLineSegment(sketch, "E7985", {"start": v(86.02, -5.37) * mm, "end": v(86.06, -5.37) * mm});
            skLineSegment(sketch, "E7986", {"start": v(86.06, -5.37) * mm, "end": v(86.1, -5.36) * mm});
            skLineSegment(sketch, "E7987", {"start": v(86.1, -5.36) * mm, "end": v(86.15, -5.35) * mm});
            skLineSegment(sketch, "E7988", {"start": v(86.15, -5.35) * mm, "end": v(86.19, -5.34) * mm});
            skLineSegment(sketch, "E7989", {"start": v(86.19, -5.34) * mm, "end": v(86.23, -5.33) * mm});
            skLineSegment(sketch, "E7990", {"start": v(86.23, -5.33) * mm, "end": v(86.27, -5.31) * mm});
            skLineSegment(sketch, "E7991", {"start": v(86.27, -5.31) * mm, "end": v(86.31, -5.3) * mm});
            skLineSegment(sketch, "E7992", {"start": v(86.31, -5.3) * mm, "end": v(86.35, -5.28) * mm});
            skLineSegment(sketch, "E7993", {"start": v(86.35, -5.28) * mm, "end": v(86.4, -5.26) * mm});
            skLineSegment(sketch, "E7994", {"start": v(86.4, -5.26) * mm, "end": v(86.43, -5.25) * mm});
            skLineSegment(sketch, "E7995", {"start": v(86.43, -5.25) * mm, "end": v(86.47, -5.23) * mm});
            skLineSegment(sketch, "E7996", {"start": v(86.47, -5.23) * mm, "end": v(86.5, -5.2) * mm});
            skLineSegment(sketch, "E7997", {"start": v(86.5, -5.2) * mm, "end": v(86.54, -5.18) * mm});
            skLineSegment(sketch, "E7998", {"start": v(86.54, -5.18) * mm, "end": v(86.58, -5.16) * mm});
            skLineSegment(sketch, "E7999", {"start": v(86.58, -5.16) * mm, "end": v(86.61, -5.13) * mm});
            skLineSegment(sketch, "E8000", {"start": v(86.86, -4.89) * mm, "end": v(86.89, -4.85) * mm});
            skLineSegment(sketch, "E8001", {"start": v(86.89, -4.85) * mm, "end": v(86.91, -4.82) * mm});
            skLineSegment(sketch, "E8002", {"start": v(86.91, -4.82) * mm, "end": v(86.93, -4.78) * mm});
            skLineSegment(sketch, "E8003", {"start": v(86.93, -4.78) * mm, "end": v(86.96, -4.74) * mm});
            skLineSegment(sketch, "E8004", {"start": v(86.96, -4.74) * mm, "end": v(86.98, -4.7) * mm});
            skLineSegment(sketch, "E8005", {"start": v(86.98, -4.7) * mm, "end": v(87, -4.67) * mm});
            skLineSegment(sketch, "E8006", {"start": v(87, -4.67) * mm, "end": v(87.01, -4.63) * mm});
            skLineSegment(sketch, "E8007", {"start": v(87.01, -4.63) * mm, "end": v(87.03, -4.59) * mm});
            skLineSegment(sketch, "E8008", {"start": v(87.03, -4.59) * mm, "end": v(87.04, -4.55) * mm});
            skLineSegment(sketch, "E8009", {"start": v(87.04, -4.55) * mm, "end": v(87.06, -4.5) * mm});
            skLineSegment(sketch, "E8010", {"start": v(87.06, -4.5) * mm, "end": v(87.07, -4.46) * mm});
            skLineSegment(sketch, "E8011", {"start": v(87.07, -4.46) * mm, "end": v(87.08, -4.42) * mm});
            skLineSegment(sketch, "E8012", {"start": v(87.08, -4.42) * mm, "end": v(87.1, -4.38) * mm});
            skLineSegment(sketch, "E8013", {"start": v(87.1, -4.38) * mm, "end": v(87.1, -4.34) * mm});
            skLineSegment(sketch, "E8014", {"start": v(87.1, -4.34) * mm, "end": v(87.1, -4.3) * mm});
            skLineSegment(sketch, "E8015", {"start": v(87.1, -4.3) * mm, "end": v(87.1, -4.25) * mm});
            skLineSegment(sketch, "E8016", {"start": v(87.1, -4.25) * mm, "end": v(87.11, -4.2) * mm});
            skLineSegment(sketch, "E8017", {"start": v(87.11, -4.2) * mm, "end": v(87.12, -4.16) * mm});
            skLineSegment(sketch, "E8018", {"start": v(87.12, -4.16) * mm, "end": v(87.12, -4.12) * mm});
            skLineSegment(sketch, "E8019", {"start": v(87.12, -4.12) * mm, "end": v(87.11, -4.08) * mm});
            skLineSegment(sketch, "E8020", {"start": v(87.11, -4.08) * mm, "end": v(87.11, -4.03) * mm});
            skLineSegment(sketch, "E8021", {"start": v(87.11, -4.03) * mm, "end": v(87.1, -3.99) * mm});
            skLineSegment(sketch, "E8022", {"start": v(87.1, -3.99) * mm, "end": v(87.1, -3.95) * mm});
            skLineSegment(sketch, "E8023", {"start": v(87.1, -3.95) * mm, "end": v(87.1, -3.9) * mm});
            skLineSegment(sketch, "E8024", {"start": v(87.1, -3.9) * mm, "end": v(87.09, -3.86) * mm});
            skLineSegment(sketch, "E8025", {"start": v(87.09, -3.86) * mm, "end": v(87.08, -3.82) * mm});
            skLineSegment(sketch, "E8026", {"start": v(87.08, -3.82) * mm, "end": v(87.06, -3.78) * mm});
            skLineSegment(sketch, "E8027", {"start": v(87.06, -3.78) * mm, "end": v(87.05, -3.74) * mm});
            skLineSegment(sketch, "E8028", {"start": v(87.05, -3.74) * mm, "end": v(87.04, -3.7) * mm});
            skLineSegment(sketch, "E8029", {"start": v(87.02, -3.65) * mm, "end": v(87, -3.61) * mm});
            skLineSegment(sketch, "E8030", {"start": v(87, -3.61) * mm, "end": v(86.99, -3.58) * mm});
            skLineSegment(sketch, "E8031", {"start": v(86.99, -3.58) * mm, "end": v(86.97, -3.54) * mm});
            skLineSegment(sketch, "E8032", {"start": v(86.97, -3.54) * mm, "end": v(86.94, -3.5) * mm});
            skLineSegment(sketch, "E8033", {"start": v(86.94, -3.5) * mm, "end": v(86.92, -3.46) * mm});
            skLineSegment(sketch, "E8034", {"start": v(86.92, -3.46) * mm, "end": v(86.9, -3.43) * mm});
            skLineSegment(sketch, "E8035", {"start": v(86.9, -3.43) * mm, "end": v(86.87, -3.4) * mm});
            skLineSegment(sketch, "E8036", {"start": v(86.87, -3.4) * mm, "end": v(86.85, -3.36) * mm});
            skLineSegment(sketch, "E8037", {"start": v(86.85, -3.36) * mm, "end": v(86.82, -3.32) * mm});
            skLineSegment(sketch, "E8038", {"start": v(86.82, -3.32) * mm, "end": v(86.8, -3.29) * mm});
            skLineSegment(sketch, "E8039", {"start": v(86.8, -3.29) * mm, "end": v(86.76, -3.26) * mm});
            skLineSegment(sketch, "E8040", {"start": v(86.76, -3.26) * mm, "end": v(86.73, -3.23) * mm});
            skLineSegment(sketch, "E8041", {"start": v(86.73, -3.23) * mm, "end": v(86.7, -3.2) * mm});
            skLineSegment(sketch, "E8042", {"start": v(86.7, -3.2) * mm, "end": v(86.67, -3.17) * mm});
            skLineSegment(sketch, "E8043", {"start": v(86.63, -3.14) * mm, "end": v(86.6, -3.12) * mm});
            skLineSegment(sketch, "E8044", {"start": v(86.6, -3.12) * mm, "end": v(86.56, -3.1) * mm});
            skLineSegment(sketch, "E8045", {"start": v(86.56, -3.1) * mm, "end": v(86.52, -3.07) * mm});
            skLineSegment(sketch, "E8046", {"start": v(86.52, -3.07) * mm, "end": v(86.49, -3.05) * mm});
            skLineSegment(sketch, "E8047", {"start": v(86.49, -3.05) * mm, "end": v(86.45, -3.03) * mm});
            skLineSegment(sketch, "E8048", {"start": v(86.45, -3.03) * mm, "end": v(86.41, -3) * mm});
            skLineSegment(sketch, "E8049", {"start": v(86.41, -3) * mm, "end": v(86.37, -2.99) * mm});
            skLineSegment(sketch, "E8050", {"start": v(86.37, -2.99) * mm, "end": v(86.33, -2.97) * mm});
            skLineSegment(sketch, "E8051", {"start": v(86.33, -2.97) * mm, "end": v(86.3, -2.95) * mm});
            skLineSegment(sketch, "E8052", {"start": v(86.3, -2.95) * mm, "end": v(86.25, -2.94) * mm});
            skLineSegment(sketch, "E8053", {"start": v(86.25, -2.94) * mm, "end": v(86.2, -2.93) * mm});
            skLineSegment(sketch, "E8054", {"start": v(86.2, -2.93) * mm, "end": v(86.17, -2.92) * mm});
            skLineSegment(sketch, "E8055", {"start": v(86.17, -2.92) * mm, "end": v(86.12, -2.9) * mm});
            skLineSegment(sketch, "E8056", {"start": v(86.12, -2.9) * mm, "end": v(86.08, -2.9) * mm});
            skLineSegment(sketch, "E8057", {"start": v(86.08, -2.9) * mm, "end": v(86.04, -2.9) * mm});
            skLineSegment(sketch, "E8058", {"start": v(86.04, -2.9) * mm, "end": v(86, -2.89) * mm});
            skLineSegment(sketch, "E8059", {"start": v(86, -2.89) * mm, "end": v(85.95, -2.88) * mm});
            skLineSegment(sketch, "E8060", {"start": v(85.95, -2.88) * mm, "end": v(85.9, -2.88) * mm});
            skLineSegment(sketch, "E8061", {"start": v(85.9, -2.88) * mm, "end": v(85.87, -2.88) * mm});
            skLineSegment(sketch, "E8062", {"start": v(-41.63, -2.88) * mm, "end": v(-41.68, -2.88) * mm});
            skLineSegment(sketch, "E8063", {"start": v(-41.68, -2.88) * mm, "end": v(-41.72, -2.88) * mm});
            skLineSegment(sketch, "E8064", {"start": v(-41.72, -2.88) * mm, "end": v(-41.76, -2.89) * mm});
            skLineSegment(sketch, "E8065", {"start": v(-41.76, -2.89) * mm, "end": v(-41.8, -2.9) * mm});
            skLineSegment(sketch, "E8066", {"start": v(-41.8, -2.9) * mm, "end": v(-41.85, -2.9) * mm});
            skLineSegment(sketch, "E8067", {"start": v(-41.85, -2.9) * mm, "end": v(-41.9, -2.9) * mm});
            skLineSegment(sketch, "E8068", {"start": v(-41.9, -2.9) * mm, "end": v(-41.94, -2.92) * mm});
            skLineSegment(sketch, "E8069", {"start": v(-41.94, -2.92) * mm, "end": v(-41.98, -2.93) * mm});
            skLineSegment(sketch, "E8070", {"start": v(-41.98, -2.93) * mm, "end": v(-42.02, -2.94) * mm});
            skLineSegment(sketch, "E8071", {"start": v(-42.02, -2.94) * mm, "end": v(-42.06, -2.95) * mm});
            skLineSegment(sketch, "E8072", {"start": v(-42.06, -2.95) * mm, "end": v(-42.1, -2.97) * mm});
            skLineSegment(sketch, "E8073", {"start": v(-42.1, -2.97) * mm, "end": v(-42.14, -2.99) * mm});
            skLineSegment(sketch, "E8074", {"start": v(-42.14, -2.99) * mm, "end": v(-42.18, -3) * mm});
            skLineSegment(sketch, "E8075", {"start": v(-42.18, -3) * mm, "end": v(-42.22, -3.03) * mm});
            skLineSegment(sketch, "E8076", {"start": v(-42.22, -3.03) * mm, "end": v(-42.26, -3.05) * mm});
            skLineSegment(sketch, "E8077", {"start": v(-42.26, -3.05) * mm, "end": v(-42.3, -3.07) * mm});
            skLineSegment(sketch, "E8078", {"start": v(-42.3, -3.07) * mm, "end": v(-42.33, -3.1) * mm});
            skLineSegment(sketch, "E8079", {"start": v(-42.33, -3.1) * mm, "end": v(-42.37, -3.12) * mm});
            skLineSegment(sketch, "E8080", {"start": v(-42.37, -3.12) * mm, "end": v(-42.4, -3.14) * mm});
            skLineSegment(sketch, "E8081", {"start": v(-42.4, -3.14) * mm, "end": v(-42.43, -3.17) * mm});
            skLineSegment(sketch, "E8082", {"start": v(-42.43, -3.17) * mm, "end": v(-42.47, -3.2) * mm});
            skLineSegment(sketch, "E8083", {"start": v(-42.47, -3.2) * mm, "end": v(-42.5, -3.23) * mm});
            skLineSegment(sketch, "E8084", {"start": v(-42.5, -3.23) * mm, "end": v(-42.53, -3.26) * mm});
            skLineSegment(sketch, "E8085", {"start": v(-42.53, -3.26) * mm, "end": v(-42.56, -3.29) * mm});
            skLineSegment(sketch, "E8086", {"start": v(-42.56, -3.29) * mm, "end": v(-42.59, -3.32) * mm});
            skLineSegment(sketch, "E8087", {"start": v(-42.59, -3.32) * mm, "end": v(-42.62, -3.36) * mm});
            skLineSegment(sketch, "E8088", {"start": v(-42.62, -3.36) * mm, "end": v(-42.64, -3.4) * mm});
            skLineSegment(sketch, "E8089", {"start": v(-42.64, -3.4) * mm, "end": v(-42.67, -3.43) * mm});
            skLineSegment(sketch, "E8090", {"start": v(-42.67, -3.43) * mm, "end": v(-42.7, -3.46) * mm});
            skLineSegment(sketch, "E8091", {"start": v(-42.7, -3.46) * mm, "end": v(-42.71, -3.5) * mm});
            skLineSegment(sketch, "E8092", {"start": v(-42.71, -3.5) * mm, "end": v(-42.73, -3.54) * mm});
            skLineSegment(sketch, "E8093", {"start": v(-42.73, -3.54) * mm, "end": v(-42.75, -3.58) * mm});
            skLineSegment(sketch, "E8094", {"start": v(-42.75, -3.58) * mm, "end": v(-42.77, -3.61) * mm});
            skLineSegment(sketch, "E8095", {"start": v(-42.77, -3.61) * mm, "end": v(-42.8, -3.65) * mm});
            skLineSegment(sketch, "E8096", {"start": v(-42.8, -3.7) * mm, "end": v(-42.82, -3.74) * mm});
            skLineSegment(sketch, "E8097", {"start": v(-42.82, -3.74) * mm, "end": v(-42.83, -3.78) * mm});
            skLineSegment(sketch, "E8098", {"start": v(-42.83, -3.78) * mm, "end": v(-42.84, -3.82) * mm});
            skLineSegment(sketch, "E8099", {"start": v(-42.84, -3.82) * mm, "end": v(-42.86, -3.86) * mm});
            skLineSegment(sketch, "E8100", {"start": v(-42.86, -3.86) * mm, "end": v(-42.86, -3.9) * mm});
            skLineSegment(sketch, "E8101", {"start": v(-42.86, -3.9) * mm, "end": v(-42.87, -3.95) * mm});
            skLineSegment(sketch, "E8102", {"start": v(-42.87, -3.95) * mm, "end": v(-42.88, -3.99) * mm});
            skLineSegment(sketch, "E8103", {"start": v(-42.88, -3.99) * mm, "end": v(-42.88, -4.03) * mm});
            skLineSegment(sketch, "E8104", {"start": v(-42.88, -4.03) * mm, "end": v(-42.88, -4.08) * mm});
            skLineSegment(sketch, "E8105", {"start": v(-42.88, -4.08) * mm, "end": v(-42.88, -4.12) * mm});
            skLineSegment(sketch, "E8106", {"start": v(-42.88, -4.12) * mm, "end": v(-42.88, -4.16) * mm});
            skLineSegment(sketch, "E8107", {"start": v(-42.88, -4.16) * mm, "end": v(-42.88, -4.2) * mm});
            skLineSegment(sketch, "E8108", {"start": v(-42.88, -4.2) * mm, "end": v(-42.88, -4.25) * mm});
            skLineSegment(sketch, "E8109", {"start": v(-42.88, -4.25) * mm, "end": v(-42.87, -4.3) * mm});
            skLineSegment(sketch, "E8110", {"start": v(-42.87, -4.3) * mm, "end": v(-42.87, -4.34) * mm});
            skLineSegment(sketch, "E8111", {"start": v(-42.87, -4.34) * mm, "end": v(-42.86, -4.38) * mm});
            skLineSegment(sketch, "E8112", {"start": v(-42.86, -4.38) * mm, "end": v(-42.85, -4.42) * mm});
            skLineSegment(sketch, "E8113", {"start": v(-42.85, -4.42) * mm, "end": v(-42.84, -4.46) * mm});
            skLineSegment(sketch, "E8114", {"start": v(-42.84, -4.46) * mm, "end": v(-42.83, -4.5) * mm});
            skLineSegment(sketch, "E8115", {"start": v(-42.83, -4.5) * mm, "end": v(-42.81, -4.55) * mm});
            skLineSegment(sketch, "E8116", {"start": v(-42.81, -4.55) * mm, "end": v(-42.8, -4.59) * mm});
            skLineSegment(sketch, "E8117", {"start": v(-42.8, -4.59) * mm, "end": v(-42.78, -4.63) * mm});
            skLineSegment(sketch, "E8118", {"start": v(-42.78, -4.63) * mm, "end": v(-42.76, -4.67) * mm});
            skLineSegment(sketch, "E8119", {"start": v(-42.76, -4.67) * mm, "end": v(-42.74, -4.7) * mm});
            skLineSegment(sketch, "E8120", {"start": v(-42.74, -4.7) * mm, "end": v(-42.72, -4.74) * mm});
            skLineSegment(sketch, "E8121", {"start": v(-42.72, -4.74) * mm, "end": v(-42.7, -4.78) * mm});
            skLineSegment(sketch, "E8122", {"start": v(-42.7, -4.78) * mm, "end": v(-42.68, -4.82) * mm});
            skLineSegment(sketch, "E8123", {"start": v(-42.68, -4.82) * mm, "end": v(-42.65, -4.85) * mm});
            skLineSegment(sketch, "E8124", {"start": v(-42.65, -4.85) * mm, "end": v(-42.63, -4.89) * mm});
            skLineSegment(sketch, "E8125", {"start": v(-42.38, -5.13) * mm, "end": v(-42.35, -5.16) * mm});
            skLineSegment(sketch, "E8126", {"start": v(-42.35, -5.16) * mm, "end": v(-42.31, -5.18) * mm});
            skLineSegment(sketch, "E8127", {"start": v(-42.31, -5.18) * mm, "end": v(-42.27, -5.2) * mm});
            skLineSegment(sketch, "E8128", {"start": v(-42.27, -5.2) * mm, "end": v(-42.24, -5.23) * mm});
            skLineSegment(sketch, "E8129", {"start": v(-42.24, -5.23) * mm, "end": v(-42.2, -5.25) * mm});
            skLineSegment(sketch, "E8130", {"start": v(-42.2, -5.25) * mm, "end": v(-42.16, -5.26) * mm});
            skLineSegment(sketch, "E8131", {"start": v(-42.16, -5.26) * mm, "end": v(-42.12, -5.28) * mm});
            skLineSegment(sketch, "E8132", {"start": v(-42.12, -5.28) * mm, "end": v(-42.08, -5.3) * mm});
            skLineSegment(sketch, "E8133", {"start": v(-42.08, -5.3) * mm, "end": v(-42.04, -5.31) * mm});
            skLineSegment(sketch, "E8134", {"start": v(-42.04, -5.31) * mm, "end": v(-42, -5.33) * mm});
            skLineSegment(sketch, "E8135", {"start": v(-42, -5.33) * mm, "end": v(-41.96, -5.34) * mm});
            skLineSegment(sketch, "E8136", {"start": v(-41.96, -5.34) * mm, "end": v(-41.91, -5.35) * mm});
            skLineSegment(sketch, "E8137", {"start": v(-41.91, -5.35) * mm, "end": v(-41.87, -5.36) * mm});
            skLineSegment(sketch, "E8138", {"start": v(-41.87, -5.36) * mm, "end": v(-41.83, -5.37) * mm});
            skLineSegment(sketch, "E8139", {"start": v(-41.83, -5.37) * mm, "end": v(-41.79, -5.37) * mm});
            skLineSegment(sketch, "E8140", {"start": v(-41.79, -5.37) * mm, "end": v(-41.74, -5.38) * mm});
            skLineSegment(sketch, "E8141", {"start": v(-41.74, -5.38) * mm, "end": v(-41.7, -5.38) * mm});
            skLineSegment(sketch, "E8142", {"start": v(-41.7, -5.38) * mm, "end": v(-41.66, -5.38) * mm});
            skLineSegment(sketch, "E8143", {"start": v(-41.66, -5.38) * mm, "end": v(-41.61, -5.38) * mm});
            skLineSegment(sketch, "E8144", {"start": v(-41.61, -5.38) * mm, "end": v(-41.57, -5.38) * mm});
            skLineSegment(sketch, "E8145", {"start": v(-41.57, -5.38) * mm, "end": v(-41.53, -5.38) * mm});
            skLineSegment(sketch, "E8146", {"start": v(-41.53, -5.38) * mm, "end": v(-41.48, -5.37) * mm});
            skLineSegment(sketch, "E8147", {"start": v(-41.48, -5.37) * mm, "end": v(-41.44, -5.37) * mm});
            skLineSegment(sketch, "E8148", {"start": v(-41.44, -5.37) * mm, "end": v(-41.4, -5.36) * mm});
            skLineSegment(sketch, "E8149", {"start": v(-41.4, -5.36) * mm, "end": v(-41.35, -5.35) * mm});
            skLineSegment(sketch, "E8150", {"start": v(-41.35, -5.35) * mm, "end": v(-41.31, -5.34) * mm});
            skLineSegment(sketch, "E8151", {"start": v(-41.31, -5.34) * mm, "end": v(-41.27, -5.33) * mm});
            skLineSegment(sketch, "E8152", {"start": v(-41.27, -5.33) * mm, "end": v(-41.23, -5.31) * mm});
            skLineSegment(sketch, "E8153", {"start": v(-41.23, -5.31) * mm, "end": v(-41.19, -5.3) * mm});
            skLineSegment(sketch, "E8154", {"start": v(-41.19, -5.3) * mm, "end": v(-41.15, -5.28) * mm});
            skLineSegment(sketch, "E8155", {"start": v(-41.15, -5.28) * mm, "end": v(-41.1, -5.26) * mm});
            skLineSegment(sketch, "E8156", {"start": v(-41.1, -5.26) * mm, "end": v(-41.07, -5.25) * mm});
            skLineSegment(sketch, "E8157", {"start": v(-41.07, -5.25) * mm, "end": v(-41.03, -5.23) * mm});
            skLineSegment(sketch, "E8158", {"start": v(-41.03, -5.23) * mm, "end": v(-41, -5.2) * mm});
            skLineSegment(sketch, "E8159", {"start": v(-41, -5.2) * mm, "end": v(-40.96, -5.18) * mm});
            skLineSegment(sketch, "E8160", {"start": v(-40.96, -5.18) * mm, "end": v(-40.92, -5.16) * mm});
            skLineSegment(sketch, "E8161", {"start": v(-40.92, -5.16) * mm, "end": v(-40.89, -5.13) * mm});
            skLineSegment(sketch, "E8162", {"start": v(-40.89, -5.13) * mm, "end": v(-40.85, -5.1) * mm});
            skLineSegment(sketch, "E8163", {"start": v(-40.85, -5.1) * mm, "end": v(-40.82, -5.08) * mm});
            skLineSegment(sketch, "E8164", {"start": v(-40.82, -5.08) * mm, "end": v(-40.79, -5.05) * mm});
            skLineSegment(sketch, "E8165", {"start": v(-40.79, -5.05) * mm, "end": v(-40.75, -5.02) * mm});
            skLineSegment(sketch, "E8166", {"start": v(-40.75, -5.02) * mm, "end": v(-40.72, -4.99) * mm});
            skLineSegment(sketch, "E8167", {"start": v(-40.72, -4.99) * mm, "end": v(-40.7, -4.95) * mm});
            skLineSegment(sketch, "E8168", {"start": v(-40.7, -4.95) * mm, "end": v(-40.67, -4.92) * mm});
            skLineSegment(sketch, "E8169", {"start": v(-40.64, -4.89) * mm, "end": v(-40.61, -4.85) * mm});
            skLineSegment(sketch, "E8170", {"start": v(-40.61, -4.85) * mm, "end": v(-40.59, -4.82) * mm});
            skLineSegment(sketch, "E8171", {"start": v(-40.59, -4.82) * mm, "end": v(-40.57, -4.78) * mm});
            skLineSegment(sketch, "E8172", {"start": v(-40.57, -4.78) * mm, "end": v(-40.54, -4.74) * mm});
            skLineSegment(sketch, "E8173", {"start": v(-40.54, -4.74) * mm, "end": v(-40.52, -4.7) * mm});
            skLineSegment(sketch, "E8174", {"start": v(-40.52, -4.7) * mm, "end": v(-40.5, -4.67) * mm});
            skLineSegment(sketch, "E8175", {"start": v(-40.5, -4.67) * mm, "end": v(-40.49, -4.63) * mm});
            skLineSegment(sketch, "E8176", {"start": v(-40.49, -4.63) * mm, "end": v(-40.47, -4.59) * mm});
            skLineSegment(sketch, "E8177", {"start": v(-40.47, -4.59) * mm, "end": v(-40.46, -4.55) * mm});
            skLineSegment(sketch, "E8178", {"start": v(-40.46, -4.55) * mm, "end": v(-40.44, -4.5) * mm});
            skLineSegment(sketch, "E8179", {"start": v(-40.44, -4.5) * mm, "end": v(-40.43, -4.46) * mm});
            skLineSegment(sketch, "E8180", {"start": v(-40.43, -4.46) * mm, "end": v(-40.42, -4.42) * mm});
            skLineSegment(sketch, "E8181", {"start": v(-40.42, -4.42) * mm, "end": v(-40.4, -4.38) * mm});
            skLineSegment(sketch, "E8182", {"start": v(-40.4, -4.38) * mm, "end": v(-40.4, -4.34) * mm});
            skLineSegment(sketch, "E8183", {"start": v(-40.4, -4.34) * mm, "end": v(-40.4, -4.3) * mm});
            skLineSegment(sketch, "E8184", {"start": v(-40.4, -4.3) * mm, "end": v(-40.4, -4.25) * mm});
            skLineSegment(sketch, "E8185", {"start": v(-40.4, -4.25) * mm, "end": v(-40.39, -4.2) * mm});
            skLineSegment(sketch, "E8186", {"start": v(-40.39, -4.2) * mm, "end": v(-40.38, -4.16) * mm});
            skLineSegment(sketch, "E8187", {"start": v(-40.38, -4.16) * mm, "end": v(-40.38, -4.12) * mm});
            skLineSegment(sketch, "E8188", {"start": v(-40.38, -4.12) * mm, "end": v(-40.39, -4.08) * mm});
            skLineSegment(sketch, "E8189", {"start": v(-40.39, -4.08) * mm, "end": v(-40.39, -4.03) * mm});
            skLineSegment(sketch, "E8190", {"start": v(-40.39, -4.03) * mm, "end": v(-40.4, -3.99) * mm});
            skLineSegment(sketch, "E8191", {"start": v(-40.4, -3.99) * mm, "end": v(-40.4, -3.95) * mm});
            skLineSegment(sketch, "E8192", {"start": v(-40.4, -3.95) * mm, "end": v(-40.4, -3.9) * mm});
            skLineSegment(sketch, "E8193", {"start": v(-40.4, -3.9) * mm, "end": v(-40.41, -3.86) * mm});
            skLineSegment(sketch, "E8194", {"start": v(-40.41, -3.86) * mm, "end": v(-40.42, -3.82) * mm});
            skLineSegment(sketch, "E8195", {"start": v(-40.42, -3.82) * mm, "end": v(-40.44, -3.78) * mm});
            skLineSegment(sketch, "E8196", {"start": v(-40.44, -3.78) * mm, "end": v(-40.45, -3.74) * mm});
            skLineSegment(sketch, "E8197", {"start": v(-40.45, -3.74) * mm, "end": v(-40.46, -3.7) * mm});
            skLineSegment(sketch, "E8198", {"start": v(-40.46, -3.7) * mm, "end": v(-40.48, -3.65) * mm});
            skLineSegment(sketch, "E8199", {"start": v(-40.48, -3.65) * mm, "end": v(-40.5, -3.61) * mm});
            skLineSegment(sketch, "E8200", {"start": v(-40.5, -3.61) * mm, "end": v(-40.51, -3.58) * mm});
            skLineSegment(sketch, "E8201", {"start": v(-40.51, -3.58) * mm, "end": v(-40.53, -3.54) * mm});
            skLineSegment(sketch, "E8202", {"start": v(-40.53, -3.54) * mm, "end": v(-40.56, -3.5) * mm});
            skLineSegment(sketch, "E8203", {"start": v(-40.56, -3.5) * mm, "end": v(-40.58, -3.46) * mm});
            skLineSegment(sketch, "E8204", {"start": v(-40.58, -3.46) * mm, "end": v(-40.6, -3.43) * mm});
            skLineSegment(sketch, "E8205", {"start": v(-40.6, -3.43) * mm, "end": v(-40.63, -3.4) * mm});
            skLineSegment(sketch, "E8206", {"start": v(-40.63, -3.4) * mm, "end": v(-40.65, -3.36) * mm});
            skLineSegment(sketch, "E8207", {"start": v(-40.65, -3.36) * mm, "end": v(-40.68, -3.32) * mm});
            skLineSegment(sketch, "E8208", {"start": v(-40.68, -3.32) * mm, "end": v(-40.7, -3.29) * mm});
            skLineSegment(sketch, "E8209", {"start": v(-40.7, -3.29) * mm, "end": v(-40.74, -3.26) * mm});
            skLineSegment(sketch, "E8210", {"start": v(-40.74, -3.26) * mm, "end": v(-40.77, -3.23) * mm});
            skLineSegment(sketch, "E8211", {"start": v(-40.77, -3.23) * mm, "end": v(-40.8, -3.2) * mm});
            skLineSegment(sketch, "E8212", {"start": v(-40.8, -3.2) * mm, "end": v(-40.83, -3.17) * mm});
            skLineSegment(sketch, "E8213", {"start": v(-40.83, -3.17) * mm, "end": v(-40.87, -3.14) * mm});
            skLineSegment(sketch, "E8214", {"start": v(-40.87, -3.14) * mm, "end": v(-40.9, -3.12) * mm});
            skLineSegment(sketch, "E8215", {"start": v(-40.9, -3.12) * mm, "end": v(-40.94, -3.1) * mm});
            skLineSegment(sketch, "E8216", {"start": v(-40.94, -3.1) * mm, "end": v(-40.98, -3.07) * mm});
            skLineSegment(sketch, "E8217", {"start": v(-40.98, -3.07) * mm, "end": v(-41.01, -3.05) * mm});
            skLineSegment(sketch, "E8218", {"start": v(-41.01, -3.05) * mm, "end": v(-41.05, -3.03) * mm});
            skLineSegment(sketch, "E8219", {"start": v(-41.05, -3.03) * mm, "end": v(-41.09, -3) * mm});
            skLineSegment(sketch, "E8220", {"start": v(-41.09, -3) * mm, "end": v(-41.13, -2.99) * mm});
            skLineSegment(sketch, "E8221", {"start": v(-41.13, -2.99) * mm, "end": v(-41.17, -2.97) * mm});
            skLineSegment(sketch, "E8222", {"start": v(-41.17, -2.97) * mm, "end": v(-41.2, -2.95) * mm});
            skLineSegment(sketch, "E8223", {"start": v(-41.2, -2.95) * mm, "end": v(-41.25, -2.94) * mm});
            skLineSegment(sketch, "E8224", {"start": v(-41.25, -2.94) * mm, "end": v(-41.3, -2.93) * mm});
            skLineSegment(sketch, "E8225", {"start": v(-41.3, -2.93) * mm, "end": v(-41.33, -2.92) * mm});
            skLineSegment(sketch, "E8226", {"start": v(-41.33, -2.92) * mm, "end": v(-41.38, -2.9) * mm});
            skLineSegment(sketch, "E8227", {"start": v(-41.38, -2.9) * mm, "end": v(-41.42, -2.9) * mm});
            skLineSegment(sketch, "E8228", {"start": v(-41.42, -2.9) * mm, "end": v(-41.46, -2.9) * mm});
            skLineSegment(sketch, "E8229", {"start": v(-41.46, -2.9) * mm, "end": v(-41.5, -2.89) * mm});
            skLineSegment(sketch, "E8230", {"start": v(-41.5, -2.89) * mm, "end": v(-41.55, -2.88) * mm});
            skLineSegment(sketch, "E8231", {"start": v(-41.55, -2.88) * mm, "end": v(-41.6, -2.88) * mm});
            skLineSegment(sketch, "E8232", {"start": v(-41.6, -2.88) * mm, "end": v(-41.63, -2.88) * mm});
            skLineSegment(sketch, "E8233", {"start": v(-157.23, -3.93) * mm, "end": v(-157.23, 11.07) * mm});
            skLineSegment(sketch, "E8234", {"start": v(-157.23, 11.07) * mm, "end": v(-292.23, 11.07) * mm});
            skLineSegment(sketch, "E8235", {"start": v(-292.23, 11.07) * mm, "end": v(-292.23, -3.93) * mm});
            skLineSegment(sketch, "E8236", {"start": v(-292.23, -3.93) * mm, "end": v(-157.23, -3.93) * mm});
            skLineSegment(sketch, "E8237", {"start": v(86.04, 16.94) * mm, "end": v(85.95, 16.94) * mm});
            skLineSegment(sketch, "E8238", {"start": v(85.95, 16.94) * mm, "end": v(85.86, 16.94) * mm});
            skLineSegment(sketch, "E8239", {"start": v(85.86, 16.94) * mm, "end": v(85.78, 16.93) * mm});
            skLineSegment(sketch, "E8240", {"start": v(85.78, 16.93) * mm, "end": v(85.7, 16.92) * mm});
            skLineSegment(sketch, "E8241", {"start": v(85.7, 16.92) * mm, "end": v(85.6, 16.9) * mm});
            skLineSegment(sketch, "E8242", {"start": v(85.6, 16.9) * mm, "end": v(85.52, 16.89) * mm});
            skLineSegment(sketch, "E8243", {"start": v(85.52, 16.89) * mm, "end": v(85.43, 16.87) * mm});
            skLineSegment(sketch, "E8244", {"start": v(85.43, 16.87) * mm, "end": v(85.35, 16.85) * mm});
            skLineSegment(sketch, "E8245", {"start": v(85.35, 16.85) * mm, "end": v(85.27, 16.82) * mm});
            skLineSegment(sketch, "E8246", {"start": v(85.27, 16.82) * mm, "end": v(85.19, 16.8) * mm});
            skLineSegment(sketch, "E8247", {"start": v(85.19, 16.8) * mm, "end": v(85.1, 16.76) * mm});
            skLineSegment(sketch, "E8248", {"start": v(85.02, 16.73) * mm, "end": v(84.95, 16.7) * mm});
            skLineSegment(sketch, "E8249", {"start": v(84.95, 16.7) * mm, "end": v(84.87, 16.65) * mm});
            skLineSegment(sketch, "E8250", {"start": v(84.87, 16.65) * mm, "end": v(84.8, 16.61) * mm});
            skLineSegment(sketch, "E8251", {"start": v(84.8, 16.61) * mm, "end": v(84.72, 16.57) * mm});
            skLineSegment(sketch, "E8252", {"start": v(84.72, 16.57) * mm, "end": v(84.65, 16.52) * mm});
            skLineSegment(sketch, "E8253", {"start": v(84.65, 16.52) * mm, "end": v(84.57, 16.47) * mm});
            skLineSegment(sketch, "E8254", {"start": v(84.57, 16.47) * mm, "end": v(84.5, 16.42) * mm});
            skLineSegment(sketch, "E8255", {"start": v(84.5, 16.42) * mm, "end": v(84.44, 16.36) * mm});
            skLineSegment(sketch, "E8256", {"start": v(84.44, 16.36) * mm, "end": v(84.37, 16.3) * mm});
            skLineSegment(sketch, "E8257", {"start": v(84.37, 16.3) * mm, "end": v(84.3, 16.25) * mm});
            skLineSegment(sketch, "E8258", {"start": v(84.3, 16.25) * mm, "end": v(84.25, 16.19) * mm});
            skLineSegment(sketch, "E8259", {"start": v(84.25, 16.19) * mm, "end": v(84.19, 16.12) * mm});
            skLineSegment(sketch, "E8260", {"start": v(84.19, 16.12) * mm, "end": v(84.13, 16.06) * mm});
            skLineSegment(sketch, "E8261", {"start": v(84.13, 16.06) * mm, "end": v(84.07, 16) * mm});
            skLineSegment(sketch, "E8262", {"start": v(84.02, 15.92) * mm, "end": v(83.97, 15.85) * mm});
            skLineSegment(sketch, "E8263", {"start": v(83.97, 15.85) * mm, "end": v(83.92, 15.78) * mm});
            skLineSegment(sketch, "E8264", {"start": v(83.92, 15.78) * mm, "end": v(83.88, 15.7) * mm});
            skLineSegment(sketch, "E8265", {"start": v(83.88, 15.7) * mm, "end": v(83.84, 15.63) * mm});
            skLineSegment(sketch, "E8266", {"start": v(83.84, 15.63) * mm, "end": v(83.8, 15.55) * mm});
            skLineSegment(sketch, "E8267", {"start": v(83.8, 15.55) * mm, "end": v(83.76, 15.47) * mm});
            skLineSegment(sketch, "E8268", {"start": v(83.76, 15.47) * mm, "end": v(83.72, 15.4) * mm});
            skLineSegment(sketch, "E8269", {"start": v(83.72, 15.4) * mm, "end": v(83.7, 15.31) * mm});
            skLineSegment(sketch, "E8270", {"start": v(83.7, 15.31) * mm, "end": v(83.66, 15.23) * mm});
            skLineSegment(sketch, "E8271", {"start": v(83.66, 15.23) * mm, "end": v(83.64, 15.15) * mm});
            skLineSegment(sketch, "E8272", {"start": v(83.64, 15.15) * mm, "end": v(83.62, 15.06) * mm});
            skLineSegment(sketch, "E8273", {"start": v(83.62, 15.06) * mm, "end": v(83.6, 14.98) * mm});
            skLineSegment(sketch, "E8274", {"start": v(83.6, 14.98) * mm, "end": v(83.58, 14.9) * mm});
            skLineSegment(sketch, "E8275", {"start": v(83.58, 14.9) * mm, "end": v(83.56, 14.8) * mm});
            skLineSegment(sketch, "E8276", {"start": v(83.56, 14.8) * mm, "end": v(83.55, 14.72) * mm});
            skLineSegment(sketch, "E8277", {"start": v(83.55, 14.72) * mm, "end": v(83.54, 14.64) * mm});
            skLineSegment(sketch, "E8278", {"start": v(83.54, 14.64) * mm, "end": v(83.54, 14.55) * mm});
            skLineSegment(sketch, "E8279", {"start": v(83.54, 14.55) * mm, "end": v(83.54, 14.46) * mm});
            skLineSegment(sketch, "E8280", {"start": v(83.54, 14.46) * mm, "end": v(83.54, 14.38) * mm});
            skLineSegment(sketch, "E8281", {"start": v(83.54, 14.38) * mm, "end": v(83.54, 14.29) * mm});
            skLineSegment(sketch, "E8282", {"start": v(83.54, 14.29) * mm, "end": v(83.55, 14.2) * mm});
            skLineSegment(sketch, "E8283", {"start": v(83.55, 14.2) * mm, "end": v(83.56, 14.12) * mm});
            skLineSegment(sketch, "E8284", {"start": v(83.56, 14.12) * mm, "end": v(83.57, 14.03) * mm});
            skLineSegment(sketch, "E8285", {"start": v(83.57, 14.03) * mm, "end": v(83.59, 13.95) * mm});
            skLineSegment(sketch, "E8286", {"start": v(83.59, 13.95) * mm, "end": v(83.6, 13.86) * mm});
            skLineSegment(sketch, "E8287", {"start": v(83.6, 13.86) * mm, "end": v(83.63, 13.78) * mm});
            skLineSegment(sketch, "E8288", {"start": v(83.63, 13.78) * mm, "end": v(83.65, 13.7) * mm});
            skLineSegment(sketch, "E8289", {"start": v(83.65, 13.7) * mm, "end": v(83.68, 13.61) * mm});
            skLineSegment(sketch, "E8290", {"start": v(83.68, 13.61) * mm, "end": v(83.7, 13.53) * mm});
            skLineSegment(sketch, "E8291", {"start": v(83.7, 13.53) * mm, "end": v(83.74, 13.45) * mm});
            skLineSegment(sketch, "E8292", {"start": v(83.74, 13.45) * mm, "end": v(83.78, 13.37) * mm});
            skLineSegment(sketch, "E8293", {"start": v(83.78, 13.37) * mm, "end": v(83.82, 13.3) * mm});
            skLineSegment(sketch, "E8294", {"start": v(83.82, 13.3) * mm, "end": v(83.86, 13.22) * mm});
            skLineSegment(sketch, "E8295", {"start": v(83.86, 13.22) * mm, "end": v(83.9, 13.14) * mm});
            skLineSegment(sketch, "E8296", {"start": v(83.9, 13.14) * mm, "end": v(83.95, 13.07) * mm});
            skLineSegment(sketch, "E8297", {"start": v(83.95, 13.07) * mm, "end": v(84, 13) * mm});
            skLineSegment(sketch, "E8298", {"start": v(84, 13) * mm, "end": v(84.05, 12.93) * mm});
            skLineSegment(sketch, "E8299", {"start": v(84.1, 12.86) * mm, "end": v(84.16, 12.8) * mm});
            skLineSegment(sketch, "E8300", {"start": v(84.16, 12.8) * mm, "end": v(84.22, 12.73) * mm});
            skLineSegment(sketch, "E8301", {"start": v(84.22, 12.73) * mm, "end": v(84.28, 12.67) * mm});
            skLineSegment(sketch, "E8302", {"start": v(84.28, 12.67) * mm, "end": v(84.34, 12.6) * mm});
            skLineSegment(sketch, "E8303", {"start": v(84.34, 12.6) * mm, "end": v(84.4, 12.55) * mm});
            skLineSegment(sketch, "E8304", {"start": v(84.4, 12.55) * mm, "end": v(84.47, 12.5) * mm});
            skLineSegment(sketch, "E8305", {"start": v(84.47, 12.5) * mm, "end": v(84.54, 12.44) * mm});
            skLineSegment(sketch, "E8306", {"start": v(84.54, 12.44) * mm, "end": v(84.6, 12.39) * mm});
            skLineSegment(sketch, "E8307", {"start": v(84.6, 12.39) * mm, "end": v(84.68, 12.34) * mm});
            skLineSegment(sketch, "E8308", {"start": v(84.68, 12.34) * mm, "end": v(84.76, 12.3) * mm});
            skLineSegment(sketch, "E8309", {"start": v(84.76, 12.3) * mm, "end": v(84.83, 12.25) * mm});
            skLineSegment(sketch, "E8310", {"start": v(84.83, 12.25) * mm, "end": v(84.9, 12.21) * mm});
            skLineSegment(sketch, "E8311", {"start": v(84.9, 12.21) * mm, "end": v(84.99, 12.17) * mm});
            skLineSegment(sketch, "E8312", {"start": v(84.99, 12.17) * mm, "end": v(85.06, 12.14) * mm});
            skLineSegment(sketch, "E8313", {"start": v(85.06, 12.14) * mm, "end": v(85.15, 12.1) * mm});
            skLineSegment(sketch, "E8314", {"start": v(85.15, 12.1) * mm, "end": v(85.23, 12.08) * mm});
            skLineSegment(sketch, "E8315", {"start": v(85.23, 12.08) * mm, "end": v(85.3, 12.05) * mm});
            skLineSegment(sketch, "E8316", {"start": v(85.3, 12.05) * mm, "end": v(85.4, 12.03) * mm});
            skLineSegment(sketch, "E8317", {"start": v(85.4, 12.03) * mm, "end": v(85.48, 12) * mm});
            skLineSegment(sketch, "E8318", {"start": v(85.48, 12) * mm, "end": v(85.56, 11.99) * mm});
            skLineSegment(sketch, "E8319", {"start": v(85.56, 11.99) * mm, "end": v(85.65, 11.97) * mm});
            skLineSegment(sketch, "E8320", {"start": v(85.65, 11.97) * mm, "end": v(85.73, 11.96) * mm});
            skLineSegment(sketch, "E8321", {"start": v(85.73, 11.96) * mm, "end": v(85.82, 11.95) * mm});
            skLineSegment(sketch, "E8322", {"start": v(85.82, 11.95) * mm, "end": v(85.9, 11.95) * mm});
            skLineSegment(sketch, "E8323", {"start": v(85.9, 11.95) * mm, "end": v(86, 11.94) * mm});
            skLineSegment(sketch, "E8324", {"start": v(86, 11.94) * mm, "end": v(86.08, 11.94) * mm});
            skLineSegment(sketch, "E8325", {"start": v(86.08, 11.94) * mm, "end": v(86.17, 11.95) * mm});
            skLineSegment(sketch, "E8326", {"start": v(86.17, 11.95) * mm, "end": v(86.25, 11.95) * mm});
            skLineSegment(sketch, "E8327", {"start": v(86.25, 11.95) * mm, "end": v(86.34, 11.96) * mm});
            skLineSegment(sketch, "E8328", {"start": v(86.34, 11.96) * mm, "end": v(86.43, 11.97) * mm});
            skLineSegment(sketch, "E8329", {"start": v(86.43, 11.97) * mm, "end": v(86.51, 11.99) * mm});
            skLineSegment(sketch, "E8330", {"start": v(86.51, 11.99) * mm, "end": v(86.6, 12) * mm});
            skLineSegment(sketch, "E8331", {"start": v(86.6, 12) * mm, "end": v(86.68, 12.03) * mm});
            skLineSegment(sketch, "E8332", {"start": v(86.68, 12.03) * mm, "end": v(86.76, 12.05) * mm});
            skLineSegment(sketch, "E8333", {"start": v(86.76, 12.05) * mm, "end": v(86.85, 12.08) * mm});
            skLineSegment(sketch, "E8334", {"start": v(86.85, 12.08) * mm, "end": v(86.93, 12.1) * mm});
            skLineSegment(sketch, "E8335", {"start": v(86.93, 12.1) * mm, "end": v(87, 12.14) * mm});
            skLineSegment(sketch, "E8336", {"start": v(87, 12.14) * mm, "end": v(87.09, 12.17) * mm});
            skLineSegment(sketch, "E8337", {"start": v(87.09, 12.17) * mm, "end": v(87.17, 12.21) * mm});
            skLineSegment(sketch, "E8338", {"start": v(87.17, 12.21) * mm, "end": v(87.24, 12.25) * mm});
            skLineSegment(sketch, "E8339", {"start": v(87.24, 12.25) * mm, "end": v(87.32, 12.3) * mm});
            skLineSegment(sketch, "E8340", {"start": v(87.32, 12.3) * mm, "end": v(87.4, 12.34) * mm});
            skLineSegment(sketch, "E8341", {"start": v(87.53, 12.44) * mm, "end": v(87.6, 12.5) * mm});
            skLineSegment(sketch, "E8342", {"start": v(87.6, 12.5) * mm, "end": v(87.67, 12.55) * mm});
            skLineSegment(sketch, "E8343", {"start": v(87.73, 12.6) * mm, "end": v(87.8, 12.67) * mm});
            skLineSegment(sketch, "E8344", {"start": v(87.8, 12.67) * mm, "end": v(87.86, 12.73) * mm});
            skLineSegment(sketch, "E8345", {"start": v(87.86, 12.73) * mm, "end": v(87.92, 12.8) * mm});
            skLineSegment(sketch, "E8346", {"start": v(87.92, 12.8) * mm, "end": v(87.97, 12.86) * mm});
            skLineSegment(sketch, "E8347", {"start": v(87.97, 12.86) * mm, "end": v(88.03, 12.93) * mm});
            skLineSegment(sketch, "E8348", {"start": v(88.03, 12.93) * mm, "end": v(88.08, 13) * mm});
            skLineSegment(sketch, "E8349", {"start": v(88.08, 13) * mm, "end": v(88.13, 13.07) * mm});
            skLineSegment(sketch, "E8350", {"start": v(88.13, 13.07) * mm, "end": v(88.17, 13.14) * mm});
            skLineSegment(sketch, "E8351", {"start": v(88.17, 13.14) * mm, "end": v(88.22, 13.22) * mm});
            skLineSegment(sketch, "E8352", {"start": v(88.22, 13.22) * mm, "end": v(88.26, 13.3) * mm});
            skLineSegment(sketch, "E8353", {"start": v(88.26, 13.3) * mm, "end": v(88.3, 13.37) * mm});
            skLineSegment(sketch, "E8354", {"start": v(88.3, 13.37) * mm, "end": v(88.33, 13.45) * mm});
            skLineSegment(sketch, "E8355", {"start": v(88.33, 13.45) * mm, "end": v(88.36, 13.53) * mm});
            skLineSegment(sketch, "E8356", {"start": v(88.4, 13.61) * mm, "end": v(88.42, 13.7) * mm});
            skLineSegment(sketch, "E8357", {"start": v(88.42, 13.7) * mm, "end": v(88.45, 13.78) * mm});
            skLineSegment(sketch, "E8358", {"start": v(88.45, 13.78) * mm, "end": v(88.47, 13.86) * mm});
            skLineSegment(sketch, "E8359", {"start": v(88.47, 13.86) * mm, "end": v(88.49, 13.95) * mm});
            skLineSegment(sketch, "E8360", {"start": v(88.49, 13.95) * mm, "end": v(88.5, 14.03) * mm});
            skLineSegment(sketch, "E8361", {"start": v(88.5, 14.03) * mm, "end": v(88.52, 14.12) * mm});
            skLineSegment(sketch, "E8362", {"start": v(88.52, 14.12) * mm, "end": v(88.53, 14.2) * mm});
            skLineSegment(sketch, "E8363", {"start": v(88.53, 14.2) * mm, "end": v(88.53, 14.29) * mm});
            skLineSegment(sketch, "E8364", {"start": v(88.53, 14.29) * mm, "end": v(88.54, 14.38) * mm});
            skLineSegment(sketch, "E8365", {"start": v(88.54, 14.38) * mm, "end": v(88.54, 14.46) * mm});
            skLineSegment(sketch, "E8366", {"start": v(88.54, 14.46) * mm, "end": v(88.53, 14.55) * mm});
            skLineSegment(sketch, "E8367", {"start": v(88.53, 14.55) * mm, "end": v(88.53, 14.64) * mm});
            skLineSegment(sketch, "E8368", {"start": v(88.53, 14.64) * mm, "end": v(88.52, 14.72) * mm});
            skLineSegment(sketch, "E8369", {"start": v(88.52, 14.72) * mm, "end": v(88.5, 14.8) * mm});
            skLineSegment(sketch, "E8370", {"start": v(88.5, 14.8) * mm, "end": v(88.5, 14.9) * mm});
            skLineSegment(sketch, "E8371", {"start": v(88.5, 14.9) * mm, "end": v(88.48, 14.98) * mm});
            skLineSegment(sketch, "E8372", {"start": v(88.48, 14.98) * mm, "end": v(88.46, 15.06) * mm});
            skLineSegment(sketch, "E8373", {"start": v(88.46, 15.06) * mm, "end": v(88.43, 15.15) * mm});
            skLineSegment(sketch, "E8374", {"start": v(88.43, 15.15) * mm, "end": v(88.4, 15.23) * mm});
            skLineSegment(sketch, "E8375", {"start": v(88.38, 15.31) * mm, "end": v(88.35, 15.4) * mm});
            skLineSegment(sketch, "E8376", {"start": v(88.35, 15.4) * mm, "end": v(88.31, 15.47) * mm});
            skLineSegment(sketch, "E8377", {"start": v(88.31, 15.47) * mm, "end": v(88.28, 15.55) * mm});
            skLineSegment(sketch, "E8378", {"start": v(88.28, 15.55) * mm, "end": v(88.24, 15.63) * mm});
            skLineSegment(sketch, "E8379", {"start": v(88.24, 15.63) * mm, "end": v(88.2, 15.7) * mm});
            skLineSegment(sketch, "E8380", {"start": v(88.2, 15.7) * mm, "end": v(88.15, 15.78) * mm});
            skLineSegment(sketch, "E8381", {"start": v(88.15, 15.78) * mm, "end": v(88.1, 15.85) * mm});
            skLineSegment(sketch, "E8382", {"start": v(88.1, 15.85) * mm, "end": v(88.05, 15.92) * mm});
            skLineSegment(sketch, "E8383", {"start": v(88.05, 15.92) * mm, "end": v(88, 16) * mm});
            skLineSegment(sketch, "E8384", {"start": v(88, 16) * mm, "end": v(87.94, 16.06) * mm});
            skLineSegment(sketch, "E8385", {"start": v(87.94, 16.06) * mm, "end": v(87.89, 16.12) * mm});
            skLineSegment(sketch, "E8386", {"start": v(87.89, 16.12) * mm, "end": v(87.83, 16.19) * mm});
            skLineSegment(sketch, "E8387", {"start": v(87.83, 16.19) * mm, "end": v(87.77, 16.25) * mm});
            skLineSegment(sketch, "E8388", {"start": v(87.7, 16.3) * mm, "end": v(87.64, 16.36) * mm});
            skLineSegment(sketch, "E8389", {"start": v(87.64, 16.36) * mm, "end": v(87.57, 16.42) * mm});
            skLineSegment(sketch, "E8390", {"start": v(87.43, 16.52) * mm, "end": v(87.35, 16.57) * mm});
            skLineSegment(sketch, "E8391", {"start": v(87.35, 16.57) * mm, "end": v(87.28, 16.61) * mm});
            skLineSegment(sketch, "E8392", {"start": v(87.28, 16.61) * mm, "end": v(87.2, 16.65) * mm});
            skLineSegment(sketch, "E8393", {"start": v(87.2, 16.65) * mm, "end": v(87.13, 16.7) * mm});
            skLineSegment(sketch, "E8394", {"start": v(87.13, 16.7) * mm, "end": v(87.05, 16.73) * mm});
            skLineSegment(sketch, "E8395", {"start": v(87.05, 16.73) * mm, "end": v(86.97, 16.76) * mm});
            skLineSegment(sketch, "E8396", {"start": v(86.97, 16.76) * mm, "end": v(86.89, 16.8) * mm});
            skLineSegment(sketch, "E8397", {"start": v(86.89, 16.8) * mm, "end": v(86.8, 16.82) * mm});
            skLineSegment(sketch, "E8398", {"start": v(86.8, 16.82) * mm, "end": v(86.72, 16.85) * mm});
            skLineSegment(sketch, "E8399", {"start": v(86.72, 16.85) * mm, "end": v(86.64, 16.87) * mm});
            skLineSegment(sketch, "E8400", {"start": v(86.55, 16.89) * mm, "end": v(86.47, 16.9) * mm});
            skLineSegment(sketch, "E8401", {"start": v(86.47, 16.9) * mm, "end": v(86.38, 16.92) * mm});
            skLineSegment(sketch, "E8402", {"start": v(86.38, 16.92) * mm, "end": v(86.3, 16.93) * mm});
            skLineSegment(sketch, "E8403", {"start": v(86.3, 16.93) * mm, "end": v(86.2, 16.94) * mm});
            skLineSegment(sketch, "E8404", {"start": v(86.2, 16.94) * mm, "end": v(86.12, 16.94) * mm});
            skLineSegment(sketch, "E8405", {"start": v(86.12, 16.94) * mm, "end": v(86.04, 16.94) * mm});
            skLineSegment(sketch, "E8406", {"start": v(-41.46, 16.94) * mm, "end": v(-41.55, 16.94) * mm});
            skLineSegment(sketch, "E8407", {"start": v(-41.55, 16.94) * mm, "end": v(-41.64, 16.94) * mm});
            skLineSegment(sketch, "E8408", {"start": v(-41.64, 16.94) * mm, "end": v(-41.72, 16.93) * mm});
            skLineSegment(sketch, "E8409", {"start": v(-41.72, 16.93) * mm, "end": v(-41.8, 16.92) * mm});
            skLineSegment(sketch, "E8410", {"start": v(-41.8, 16.92) * mm, "end": v(-41.9, 16.9) * mm});
            skLineSegment(sketch, "E8411", {"start": v(-41.9, 16.9) * mm, "end": v(-41.98, 16.89) * mm});
            skLineSegment(sketch, "E8412", {"start": v(-41.98, 16.89) * mm, "end": v(-42.07, 16.87) * mm});
            skLineSegment(sketch, "E8413", {"start": v(-42.07, 16.87) * mm, "end": v(-42.15, 16.85) * mm});
            skLineSegment(sketch, "E8414", {"start": v(-42.15, 16.85) * mm, "end": v(-42.23, 16.82) * mm});
            skLineSegment(sketch, "E8415", {"start": v(-42.31, 16.8) * mm, "end": v(-42.4, 16.76) * mm});
            skLineSegment(sketch, "E8416", {"start": v(-42.4, 16.76) * mm, "end": v(-42.48, 16.73) * mm});
            skLineSegment(sketch, "E8417", {"start": v(-42.48, 16.73) * mm, "end": v(-42.55, 16.7) * mm});
            skLineSegment(sketch, "E8418", {"start": v(-42.55, 16.7) * mm, "end": v(-42.63, 16.65) * mm});
            skLineSegment(sketch, "E8419", {"start": v(-42.63, 16.65) * mm, "end": v(-42.7, 16.61) * mm});
            skLineSegment(sketch, "E8420", {"start": v(-42.7, 16.61) * mm, "end": v(-42.78, 16.57) * mm});
            skLineSegment(sketch, "E8421", {"start": v(-42.78, 16.57) * mm, "end": v(-42.85, 16.52) * mm});
            skLineSegment(sketch, "E8422", {"start": v(-42.85, 16.52) * mm, "end": v(-42.93, 16.47) * mm});
            skLineSegment(sketch, "E8423", {"start": v(-42.93, 16.47) * mm, "end": v(-43, 16.42) * mm});
            skLineSegment(sketch, "E8424", {"start": v(-43, 16.42) * mm, "end": v(-43.06, 16.36) * mm});
            skLineSegment(sketch, "E8425", {"start": v(-43.06, 16.36) * mm, "end": v(-43.13, 16.3) * mm});
            skLineSegment(sketch, "E8426", {"start": v(-43.13, 16.3) * mm, "end": v(-43.2, 16.25) * mm});
            skLineSegment(sketch, "E8427", {"start": v(-43.2, 16.25) * mm, "end": v(-43.25, 16.19) * mm});
            skLineSegment(sketch, "E8428", {"start": v(-43.31, 16.12) * mm, "end": v(-43.37, 16.06) * mm});
            skLineSegment(sketch, "E8429", {"start": v(-43.37, 16.06) * mm, "end": v(-43.43, 16) * mm});
            skLineSegment(sketch, "E8430", {"start": v(-43.43, 16) * mm, "end": v(-43.48, 15.92) * mm});
            skLineSegment(sketch, "E8431", {"start": v(-43.48, 15.92) * mm, "end": v(-43.53, 15.85) * mm});
            skLineSegment(sketch, "E8432", {"start": v(-43.53, 15.85) * mm, "end": v(-43.58, 15.78) * mm});
            skLineSegment(sketch, "E8433", {"start": v(-43.58, 15.78) * mm, "end": v(-43.62, 15.7) * mm});
            skLineSegment(sketch, "E8434", {"start": v(-43.62, 15.7) * mm, "end": v(-43.66, 15.63) * mm});
            skLineSegment(sketch, "E8435", {"start": v(-43.66, 15.63) * mm, "end": v(-43.7, 15.55) * mm});
            skLineSegment(sketch, "E8436", {"start": v(-43.7, 15.55) * mm, "end": v(-43.74, 15.47) * mm});
            skLineSegment(sketch, "E8437", {"start": v(-43.74, 15.47) * mm, "end": v(-43.78, 15.4) * mm});
            skLineSegment(sketch, "E8438", {"start": v(-43.78, 15.4) * mm, "end": v(-43.8, 15.31) * mm});
            skLineSegment(sketch, "E8439", {"start": v(-43.8, 15.31) * mm, "end": v(-43.84, 15.23) * mm});
            skLineSegment(sketch, "E8440", {"start": v(-43.86, 15.15) * mm, "end": v(-43.88, 15.06) * mm});
            skLineSegment(sketch, "E8441", {"start": v(-43.88, 15.06) * mm, "end": v(-43.9, 14.98) * mm});
            skLineSegment(sketch, "E8442", {"start": v(-43.9, 14.98) * mm, "end": v(-43.92, 14.9) * mm});
            skLineSegment(sketch, "E8443", {"start": v(-43.92, 14.9) * mm, "end": v(-43.94, 14.8) * mm});
            skLineSegment(sketch, "E8444", {"start": v(-43.94, 14.8) * mm, "end": v(-43.95, 14.72) * mm});
            skLineSegment(sketch, "E8445", {"start": v(-43.95, 14.72) * mm, "end": v(-43.96, 14.64) * mm});
            skLineSegment(sketch, "E8446", {"start": v(-43.96, 14.64) * mm, "end": v(-43.96, 14.55) * mm});
            skLineSegment(sketch, "E8447", {"start": v(-43.96, 14.55) * mm, "end": v(-43.96, 14.46) * mm});
            skLineSegment(sketch, "E8448", {"start": v(-43.96, 14.46) * mm, "end": v(-43.96, 14.38) * mm});
            skLineSegment(sketch, "E8449", {"start": v(-43.96, 14.38) * mm, "end": v(-43.96, 14.29) * mm});
            skLineSegment(sketch, "E8450", {"start": v(-43.96, 14.29) * mm, "end": v(-43.95, 14.2) * mm});
            skLineSegment(sketch, "E8451", {"start": v(-43.95, 14.2) * mm, "end": v(-43.94, 14.12) * mm});
            skLineSegment(sketch, "E8452", {"start": v(-43.94, 14.12) * mm, "end": v(-43.93, 14.03) * mm});
            skLineSegment(sketch, "E8453", {"start": v(-43.93, 14.03) * mm, "end": v(-43.91, 13.95) * mm});
            skLineSegment(sketch, "E8454", {"start": v(-43.91, 13.95) * mm, "end": v(-43.9, 13.86) * mm});
            skLineSegment(sketch, "E8455", {"start": v(-43.9, 13.86) * mm, "end": v(-43.87, 13.78) * mm});
            skLineSegment(sketch, "E8456", {"start": v(-43.87, 13.78) * mm, "end": v(-43.85, 13.7) * mm});
            skLineSegment(sketch, "E8457", {"start": v(-43.82, 13.61) * mm, "end": v(-43.8, 13.53) * mm});
            skLineSegment(sketch, "E8458", {"start": v(-43.8, 13.53) * mm, "end": v(-43.76, 13.45) * mm});
            skLineSegment(sketch, "E8459", {"start": v(-43.76, 13.45) * mm, "end": v(-43.72, 13.37) * mm});
            skLineSegment(sketch, "E8460", {"start": v(-43.72, 13.37) * mm, "end": v(-43.68, 13.3) * mm});
            skLineSegment(sketch, "E8461", {"start": v(-43.68, 13.3) * mm, "end": v(-43.64, 13.22) * mm});
            skLineSegment(sketch, "E8462", {"start": v(-43.64, 13.22) * mm, "end": v(-43.6, 13.14) * mm});
            skLineSegment(sketch, "E8463", {"start": v(-43.6, 13.14) * mm, "end": v(-43.55, 13.07) * mm});
            skLineSegment(sketch, "E8464", {"start": v(-43.55, 13.07) * mm, "end": v(-43.5, 13) * mm});
            skLineSegment(sketch, "E8465", {"start": v(-43.5, 13) * mm, "end": v(-43.45, 12.93) * mm});
            skLineSegment(sketch, "E8466", {"start": v(-43.45, 12.93) * mm, "end": v(-43.4, 12.86) * mm});
            skLineSegment(sketch, "E8467", {"start": v(-43.4, 12.86) * mm, "end": v(-43.34, 12.8) * mm});
            skLineSegment(sketch, "E8468", {"start": v(-43.34, 12.8) * mm, "end": v(-43.28, 12.73) * mm});
            skLineSegment(sketch, "E8469", {"start": v(-43.16, 12.6) * mm, "end": v(-43.1, 12.55) * mm});
            skLineSegment(sketch, "E8470", {"start": v(-43.1, 12.55) * mm, "end": v(-43.03, 12.5) * mm});
            skLineSegment(sketch, "E8471", {"start": v(-43.03, 12.5) * mm, "end": v(-42.96, 12.44) * mm});
            skLineSegment(sketch, "E8472", {"start": v(-42.96, 12.44) * mm, "end": v(-42.9, 12.39) * mm});
            skLineSegment(sketch, "E8473", {"start": v(-42.9, 12.39) * mm, "end": v(-42.82, 12.34) * mm});
            skLineSegment(sketch, "E8474", {"start": v(-42.82, 12.34) * mm, "end": v(-42.74, 12.3) * mm});
            skLineSegment(sketch, "E8475", {"start": v(-42.74, 12.3) * mm, "end": v(-42.67, 12.25) * mm});
            skLineSegment(sketch, "E8476", {"start": v(-42.67, 12.25) * mm, "end": v(-42.6, 12.21) * mm});
            skLineSegment(sketch, "E8477", {"start": v(-42.6, 12.21) * mm, "end": v(-42.51, 12.17) * mm});
            skLineSegment(sketch, "E8478", {"start": v(-42.51, 12.17) * mm, "end": v(-42.44, 12.14) * mm});
            skLineSegment(sketch, "E8479", {"start": v(-42.44, 12.14) * mm, "end": v(-42.35, 12.1) * mm});
            skLineSegment(sketch, "E8480", {"start": v(-42.35, 12.1) * mm, "end": v(-42.27, 12.08) * mm});
            skLineSegment(sketch, "E8481", {"start": v(-42.27, 12.08) * mm, "end": v(-42.2, 12.05) * mm});
            skLineSegment(sketch, "E8482", {"start": v(-42.2, 12.05) * mm, "end": v(-42.1, 12.03) * mm});
            skLineSegment(sketch, "E8483", {"start": v(-42.1, 12.03) * mm, "end": v(-42.02, 12) * mm});
            skLineSegment(sketch, "E8484", {"start": v(-42.02, 12) * mm, "end": v(-41.94, 11.99) * mm});
            skLineSegment(sketch, "E8485", {"start": v(-41.94, 11.99) * mm, "end": v(-41.85, 11.97) * mm});
            skLineSegment(sketch, "E8486", {"start": v(-41.85, 11.97) * mm, "end": v(-41.77, 11.96) * mm});
            skLineSegment(sketch, "E8487", {"start": v(-41.77, 11.96) * mm, "end": v(-41.68, 11.95) * mm});
            skLineSegment(sketch, "E8488", {"start": v(-41.68, 11.95) * mm, "end": v(-41.6, 11.95) * mm});
            skLineSegment(sketch, "E8489", {"start": v(-41.6, 11.95) * mm, "end": v(-41.5, 11.94) * mm});
            skLineSegment(sketch, "E8490", {"start": v(-41.5, 11.94) * mm, "end": v(-41.42, 11.94) * mm});
            skLineSegment(sketch, "E8491", {"start": v(-41.42, 11.94) * mm, "end": v(-41.33, 11.95) * mm});
            skLineSegment(sketch, "E8492", {"start": v(-41.33, 11.95) * mm, "end": v(-41.25, 11.95) * mm});
            skLineSegment(sketch, "E8493", {"start": v(-41.25, 11.95) * mm, "end": v(-41.16, 11.96) * mm});
            skLineSegment(sketch, "E8494", {"start": v(-41.16, 11.96) * mm, "end": v(-41.07, 11.97) * mm});
            skLineSegment(sketch, "E8495", {"start": v(-41.07, 11.97) * mm, "end": v(-40.99, 11.99) * mm});
            skLineSegment(sketch, "E8496", {"start": v(-40.99, 11.99) * mm, "end": v(-40.9, 12) * mm});
            skLineSegment(sketch, "E8497", {"start": v(-40.9, 12) * mm, "end": v(-40.82, 12.03) * mm});
            skLineSegment(sketch, "E8498", {"start": v(-40.82, 12.03) * mm, "end": v(-40.74, 12.05) * mm});
            skLineSegment(sketch, "E8499", {"start": v(-40.65, 12.08) * mm, "end": v(-40.57, 12.1) * mm});
            skLineSegment(sketch, "E8500", {"start": v(-40.57, 12.1) * mm, "end": v(-40.5, 12.14) * mm});
            skLineSegment(sketch, "E8501", {"start": v(-40.5, 12.14) * mm, "end": v(-40.41, 12.17) * mm});
            skLineSegment(sketch, "E8502", {"start": v(-40.41, 12.17) * mm, "end": v(-40.33, 12.21) * mm});
            skLineSegment(sketch, "E8503", {"start": v(-40.33, 12.21) * mm, "end": v(-40.26, 12.25) * mm});
            skLineSegment(sketch, "E8504", {"start": v(-40.26, 12.25) * mm, "end": v(-40.18, 12.3) * mm});
            skLineSegment(sketch, "E8505", {"start": v(-40.18, 12.3) * mm, "end": v(-40.1, 12.34) * mm});
            skLineSegment(sketch, "E8506", {"start": v(-40.1, 12.34) * mm, "end": v(-40.04, 12.39) * mm});
            skLineSegment(sketch, "E8507", {"start": v(-40.04, 12.39) * mm, "end": v(-39.97, 12.44) * mm});
            skLineSegment(sketch, "E8508", {"start": v(-39.97, 12.44) * mm, "end": v(-39.9, 12.5) * mm});
            skLineSegment(sketch, "E8509", {"start": v(-39.9, 12.5) * mm, "end": v(-39.83, 12.55) * mm});
            skLineSegment(sketch, "E8510", {"start": v(-39.7, 12.67) * mm, "end": v(-39.64, 12.73) * mm});
            skLineSegment(sketch, "E8511", {"start": v(-39.64, 12.73) * mm, "end": v(-39.58, 12.8) * mm});
            skLineSegment(sketch, "E8512", {"start": v(-39.58, 12.8) * mm, "end": v(-39.53, 12.86) * mm});
            skLineSegment(sketch, "E8513", {"start": v(-39.53, 12.86) * mm, "end": v(-39.47, 12.93) * mm});
            skLineSegment(sketch, "E8514", {"start": v(-39.47, 12.93) * mm, "end": v(-39.42, 13) * mm});
            skLineSegment(sketch, "E8515", {"start": v(-39.42, 13) * mm, "end": v(-39.37, 13.07) * mm});
            skLineSegment(sketch, "E8516", {"start": v(-39.37, 13.07) * mm, "end": v(-39.33, 13.14) * mm});
            skLineSegment(sketch, "E8517", {"start": v(-39.33, 13.14) * mm, "end": v(-39.28, 13.22) * mm});
            skLineSegment(sketch, "E8518", {"start": v(-39.28, 13.22) * mm, "end": v(-39.24, 13.3) * mm});
            skLineSegment(sketch, "E8519", {"start": v(-39.24, 13.3) * mm, "end": v(-39.2, 13.37) * mm});
            skLineSegment(sketch, "E8520", {"start": v(-39.2, 13.37) * mm, "end": v(-39.17, 13.45) * mm});
            skLineSegment(sketch, "E8521", {"start": v(-39.17, 13.45) * mm, "end": v(-39.14, 13.53) * mm});
            skLineSegment(sketch, "E8522", {"start": v(-39.14, 13.53) * mm, "end": v(-39.1, 13.61) * mm});
            skLineSegment(sketch, "E8523", {"start": v(-39.08, 13.7) * mm, "end": v(-39.05, 13.78) * mm});
            skLineSegment(sketch, "E8524", {"start": v(-39.05, 13.78) * mm, "end": v(-39.03, 13.86) * mm});
            skLineSegment(sketch, "E8525", {"start": v(-39.03, 13.86) * mm, "end": v(-39.01, 13.95) * mm});
            skLineSegment(sketch, "E8526", {"start": v(-39.01, 13.95) * mm, "end": v(-39, 14.03) * mm});
            skLineSegment(sketch, "E8527", {"start": v(-39, 14.03) * mm, "end": v(-38.98, 14.12) * mm});
            skLineSegment(sketch, "E8528", {"start": v(-38.98, 14.12) * mm, "end": v(-38.97, 14.2) * mm});
            skLineSegment(sketch, "E8529", {"start": v(-38.97, 14.2) * mm, "end": v(-38.97, 14.29) * mm});
            skLineSegment(sketch, "E8530", {"start": v(-38.97, 14.29) * mm, "end": v(-38.96, 14.38) * mm});
            skLineSegment(sketch, "E8531", {"start": v(-38.96, 14.38) * mm, "end": v(-38.96, 14.46) * mm});
            skLineSegment(sketch, "E8532", {"start": v(-38.96, 14.46) * mm, "end": v(-38.97, 14.55) * mm});
            skLineSegment(sketch, "E8533", {"start": v(-38.97, 14.55) * mm, "end": v(-38.97, 14.64) * mm});
            skLineSegment(sketch, "E8534", {"start": v(-38.97, 14.64) * mm, "end": v(-38.98, 14.72) * mm});
            skLineSegment(sketch, "E8535", {"start": v(-38.98, 14.72) * mm, "end": v(-39, 14.8) * mm});
            skLineSegment(sketch, "E8536", {"start": v(-39, 14.8) * mm, "end": v(-39, 14.9) * mm});
            skLineSegment(sketch, "E8537", {"start": v(-39, 14.9) * mm, "end": v(-39.02, 14.98) * mm});
            skLineSegment(sketch, "E8538", {"start": v(-39.02, 14.98) * mm, "end": v(-39.04, 15.06) * mm});
            skLineSegment(sketch, "E8539", {"start": v(-39.04, 15.06) * mm, "end": v(-39.07, 15.15) * mm});
            skLineSegment(sketch, "E8540", {"start": v(-39.1, 15.23) * mm, "end": v(-39.12, 15.31) * mm});
            skLineSegment(sketch, "E8541", {"start": v(-39.12, 15.31) * mm, "end": v(-39.15, 15.4) * mm});
            skLineSegment(sketch, "E8542", {"start": v(-39.15, 15.4) * mm, "end": v(-39.19, 15.47) * mm});
            skLineSegment(sketch, "E8543", {"start": v(-39.19, 15.47) * mm, "end": v(-39.22, 15.55) * mm});
            skLineSegment(sketch, "E8544", {"start": v(-39.22, 15.55) * mm, "end": v(-39.26, 15.63) * mm});
            skLineSegment(sketch, "E8545", {"start": v(-39.26, 15.63) * mm, "end": v(-39.3, 15.7) * mm});
            skLineSegment(sketch, "E8546", {"start": v(-39.3, 15.7) * mm, "end": v(-39.35, 15.78) * mm});
            skLineSegment(sketch, "E8547", {"start": v(-39.35, 15.78) * mm, "end": v(-39.4, 15.85) * mm});
            skLineSegment(sketch, "E8548", {"start": v(-39.4, 15.85) * mm, "end": v(-39.45, 15.92) * mm});
            skLineSegment(sketch, "E8549", {"start": v(-39.45, 15.92) * mm, "end": v(-39.5, 16) * mm});
            skLineSegment(sketch, "E8550", {"start": v(-39.5, 16) * mm, "end": v(-39.56, 16.06) * mm});
            skLineSegment(sketch, "E8551", {"start": v(-39.56, 16.06) * mm, "end": v(-39.61, 16.12) * mm});
            skLineSegment(sketch, "E8552", {"start": v(-39.73, 16.25) * mm, "end": v(-39.8, 16.3) * mm});
            skLineSegment(sketch, "E8553", {"start": v(-39.8, 16.3) * mm, "end": v(-39.86, 16.36) * mm});
            skLineSegment(sketch, "E8554", {"start": v(-39.86, 16.36) * mm, "end": v(-39.93, 16.42) * mm});
            skLineSegment(sketch, "E8555", {"start": v(-39.93, 16.42) * mm, "end": v(-40, 16.47) * mm});
            skLineSegment(sketch, "E8556", {"start": v(-40, 16.47) * mm, "end": v(-40.07, 16.52) * mm});
            skLineSegment(sketch, "E8557", {"start": v(-40.07, 16.52) * mm, "end": v(-40.15, 16.57) * mm});
            skLineSegment(sketch, "E8558", {"start": v(-40.15, 16.57) * mm, "end": v(-40.22, 16.61) * mm});
            skLineSegment(sketch, "E8559", {"start": v(-40.22, 16.61) * mm, "end": v(-40.3, 16.65) * mm});
            skLineSegment(sketch, "E8560", {"start": v(-40.3, 16.65) * mm, "end": v(-40.37, 16.7) * mm});
            skLineSegment(sketch, "E8561", {"start": v(-40.37, 16.7) * mm, "end": v(-40.45, 16.73) * mm});
            skLineSegment(sketch, "E8562", {"start": v(-40.45, 16.73) * mm, "end": v(-40.53, 16.76) * mm});
            skLineSegment(sketch, "E8563", {"start": v(-40.53, 16.76) * mm, "end": v(-40.61, 16.8) * mm});
            skLineSegment(sketch, "E8564", {"start": v(-40.61, 16.8) * mm, "end": v(-40.7, 16.82) * mm});
            skLineSegment(sketch, "E8565", {"start": v(-40.7, 16.82) * mm, "end": v(-40.78, 16.85) * mm});
            skLineSegment(sketch, "E8566", {"start": v(-40.78, 16.85) * mm, "end": v(-40.86, 16.87) * mm});
            skLineSegment(sketch, "E8567", {"start": v(-40.86, 16.87) * mm, "end": v(-40.95, 16.89) * mm});
            skLineSegment(sketch, "E8568", {"start": v(-40.95, 16.89) * mm, "end": v(-41.03, 16.9) * mm});
            skLineSegment(sketch, "E8569", {"start": v(-41.03, 16.9) * mm, "end": v(-41.12, 16.92) * mm});
            skLineSegment(sketch, "E8570", {"start": v(-41.12, 16.92) * mm, "end": v(-41.2, 16.93) * mm});
            skLineSegment(sketch, "E8571", {"start": v(-41.2, 16.93) * mm, "end": v(-41.3, 16.94) * mm});
            skLineSegment(sketch, "E8572", {"start": v(-41.3, 16.94) * mm, "end": v(-41.38, 16.94) * mm});
            skLineSegment(sketch, "E8573", {"start": v(-41.38, 16.94) * mm, "end": v(-41.46, 16.94) * mm});
            skLineSegment(sketch, "E8574", {"start": v(-222.46, 19.39) * mm, "end": v(-222.46, 24.89) * mm});
            skLineSegment(sketch, "E8575", {"start": v(-222.46, 24.89) * mm, "end": v(-226.66, 24.89) * mm});
            skLineSegment(sketch, "E8576", {"start": v(-226.66, 24.89) * mm, "end": v(-226.66, 19.39) * mm});
            skLineSegment(sketch, "E8577", {"start": v(-226.66, 19.39) * mm, "end": v(-222.46, 19.39) * mm});
            skLineSegment(sketch, "E8578", {"start": v(22.29, 15.7) * mm, "end": v(22.24, 15.7) * mm});
            skLineSegment(sketch, "E8579", {"start": v(22.24, 15.7) * mm, "end": v(22.2, 15.69) * mm});
            skLineSegment(sketch, "E8580", {"start": v(22.2, 15.69) * mm, "end": v(22.16, 15.68) * mm});
            skLineSegment(sketch, "E8581", {"start": v(22.16, 15.68) * mm, "end": v(22.11, 15.68) * mm});
            skLineSegment(sketch, "E8582", {"start": v(22.11, 15.68) * mm, "end": v(22.07, 15.67) * mm});
            skLineSegment(sketch, "E8583", {"start": v(22.07, 15.67) * mm, "end": v(22.03, 15.66) * mm});
            skLineSegment(sketch, "E8584", {"start": v(22.03, 15.66) * mm, "end": v(21.99, 15.65) * mm});
            skLineSegment(sketch, "E8585", {"start": v(21.99, 15.65) * mm, "end": v(21.94, 15.64) * mm});
            skLineSegment(sketch, "E8586", {"start": v(21.94, 15.64) * mm, "end": v(21.9, 15.63) * mm});
            skLineSegment(sketch, "E8587", {"start": v(21.9, 15.63) * mm, "end": v(21.86, 15.62) * mm});
            skLineSegment(sketch, "E8588", {"start": v(21.86, 15.62) * mm, "end": v(21.82, 15.6) * mm});
            skLineSegment(sketch, "E8589", {"start": v(21.82, 15.6) * mm, "end": v(21.78, 15.58) * mm});
            skLineSegment(sketch, "E8590", {"start": v(21.78, 15.58) * mm, "end": v(21.74, 15.57) * mm});
            skLineSegment(sketch, "E8591", {"start": v(21.74, 15.57) * mm, "end": v(21.7, 15.55) * mm});
            skLineSegment(sketch, "E8592", {"start": v(21.7, 15.55) * mm, "end": v(21.66, 15.53) * mm});
            skLineSegment(sketch, "E8593", {"start": v(21.66, 15.53) * mm, "end": v(21.63, 15.5) * mm});
            skLineSegment(sketch, "E8594", {"start": v(21.63, 15.5) * mm, "end": v(21.6, 15.48) * mm});
            skLineSegment(sketch, "E8595", {"start": v(21.6, 15.48) * mm, "end": v(21.56, 15.46) * mm});
            skLineSegment(sketch, "E8596", {"start": v(21.56, 15.46) * mm, "end": v(21.52, 15.43) * mm});
            skLineSegment(sketch, "E8597", {"start": v(21.52, 15.43) * mm, "end": v(21.49, 15.4) * mm});
            skLineSegment(sketch, "E8598", {"start": v(21.49, 15.4) * mm, "end": v(21.45, 15.37) * mm});
            skLineSegment(sketch, "E8599", {"start": v(21.45, 15.37) * mm, "end": v(21.42, 15.34) * mm});
            skLineSegment(sketch, "E8600", {"start": v(21.42, 15.34) * mm, "end": v(21.4, 15.31) * mm});
            skLineSegment(sketch, "E8601", {"start": v(21.4, 15.31) * mm, "end": v(21.36, 15.28) * mm});
            skLineSegment(sketch, "E8602", {"start": v(21.36, 15.28) * mm, "end": v(21.33, 15.25) * mm});
            skLineSegment(sketch, "E8603", {"start": v(21.3, 15.22) * mm, "end": v(21.28, 15.18) * mm});
            skLineSegment(sketch, "E8604", {"start": v(21.28, 15.18) * mm, "end": v(21.25, 15.15) * mm});
            skLineSegment(sketch, "E8605", {"start": v(21.25, 15.15) * mm, "end": v(21.23, 15.1) * mm});
            skLineSegment(sketch, "E8606", {"start": v(21.23, 15.1) * mm, "end": v(21.2, 15.07) * mm});
            skLineSegment(sketch, "E8607", {"start": v(21.2, 15.07) * mm, "end": v(21.19, 15.04) * mm});
            skLineSegment(sketch, "E8608", {"start": v(21.19, 15.04) * mm, "end": v(21.17, 15) * mm});
            skLineSegment(sketch, "E8609", {"start": v(21.17, 15) * mm, "end": v(21.15, 14.96) * mm});
            skLineSegment(sketch, "E8610", {"start": v(21.15, 14.96) * mm, "end": v(21.13, 14.92) * mm});
            skLineSegment(sketch, "E8611", {"start": v(21.13, 14.92) * mm, "end": v(21.11, 14.88) * mm});
            skLineSegment(sketch, "E8612", {"start": v(21.11, 14.88) * mm, "end": v(21.1, 14.84) * mm});
            skLineSegment(sketch, "E8613", {"start": v(21.1, 14.84) * mm, "end": v(21.09, 14.8) * mm});
            skLineSegment(sketch, "E8614", {"start": v(21.09, 14.8) * mm, "end": v(21.08, 14.75) * mm});
            skLineSegment(sketch, "E8615", {"start": v(21.08, 14.75) * mm, "end": v(21.07, 14.71) * mm});
            skLineSegment(sketch, "E8616", {"start": v(21.07, 14.71) * mm, "end": v(21.06, 14.67) * mm});
            skLineSegment(sketch, "E8617", {"start": v(21.06, 14.67) * mm, "end": v(21.05, 14.63) * mm});
            skLineSegment(sketch, "E8618", {"start": v(21.05, 14.63) * mm, "end": v(21.04, 14.58) * mm});
            skLineSegment(sketch, "E8619", {"start": v(21.04, 14.58) * mm, "end": v(21.04, 14.54) * mm});
            skLineSegment(sketch, "E8620", {"start": v(21.04, 14.54) * mm, "end": v(21.04, 14.5) * mm});
            skLineSegment(sketch, "E8621", {"start": v(21.04, 14.5) * mm, "end": v(21.04, 14.45) * mm});
            skLineSegment(sketch, "E8622", {"start": v(21.04, 14.45) * mm, "end": v(21.04, 14.4) * mm});
            skLineSegment(sketch, "E8623", {"start": v(21.04, 14.4) * mm, "end": v(21.04, 14.37) * mm});
            skLineSegment(sketch, "E8624", {"start": v(21.04, 14.37) * mm, "end": v(21.04, 14.32) * mm});
            skLineSegment(sketch, "E8625", {"start": v(21.04, 14.32) * mm, "end": v(21.05, 14.28) * mm});
            skLineSegment(sketch, "E8626", {"start": v(21.05, 14.28) * mm, "end": v(21.05, 14.24) * mm});
            skLineSegment(sketch, "E8627", {"start": v(21.05, 14.24) * mm, "end": v(21.06, 14.2) * mm});
            skLineSegment(sketch, "E8628", {"start": v(21.06, 14.2) * mm, "end": v(21.07, 14.15) * mm});
            skLineSegment(sketch, "E8629", {"start": v(21.07, 14.15) * mm, "end": v(21.08, 14.1) * mm});
            skLineSegment(sketch, "E8630", {"start": v(21.08, 14.1) * mm, "end": v(21.1, 14.07) * mm});
            skLineSegment(sketch, "E8631", {"start": v(21.1, 14.07) * mm, "end": v(21.1, 14.03) * mm});
            skLineSegment(sketch, "E8632", {"start": v(21.1, 14.03) * mm, "end": v(21.12, 13.99) * mm});
            skLineSegment(sketch, "E8633", {"start": v(21.12, 13.99) * mm, "end": v(21.14, 13.95) * mm});
            skLineSegment(sketch, "E8634", {"start": v(21.14, 13.95) * mm, "end": v(21.16, 13.9) * mm});
            skLineSegment(sketch, "E8635", {"start": v(21.16, 13.9) * mm, "end": v(21.18, 13.87) * mm});
            skLineSegment(sketch, "E8636", {"start": v(21.18, 13.87) * mm, "end": v(21.2, 13.83) * mm});
            skLineSegment(sketch, "E8637", {"start": v(21.2, 13.83) * mm, "end": v(21.22, 13.8) * mm});
            skLineSegment(sketch, "E8638", {"start": v(21.22, 13.8) * mm, "end": v(21.24, 13.76) * mm});
            skLineSegment(sketch, "E8639", {"start": v(21.24, 13.76) * mm, "end": v(21.27, 13.72) * mm});
            skLineSegment(sketch, "E8640", {"start": v(21.27, 13.72) * mm, "end": v(21.3, 13.68) * mm});
            skLineSegment(sketch, "E8641", {"start": v(21.3, 13.68) * mm, "end": v(21.32, 13.65) * mm});
            skLineSegment(sketch, "E8642", {"start": v(21.32, 13.65) * mm, "end": v(21.35, 13.62) * mm});
            skLineSegment(sketch, "E8643", {"start": v(21.38, 13.58) * mm, "end": v(21.4, 13.55) * mm});
            skLineSegment(sketch, "E8644", {"start": v(21.4, 13.55) * mm, "end": v(21.44, 13.52) * mm});
            skLineSegment(sketch, "E8645", {"start": v(21.44, 13.52) * mm, "end": v(21.47, 13.5) * mm});
            skLineSegment(sketch, "E8646", {"start": v(21.47, 13.5) * mm, "end": v(21.5, 13.47) * mm});
            skLineSegment(sketch, "E8647", {"start": v(21.5, 13.47) * mm, "end": v(21.54, 13.44) * mm});
            skLineSegment(sketch, "E8648", {"start": v(21.54, 13.44) * mm, "end": v(21.57, 13.42) * mm});
            skLineSegment(sketch, "E8649", {"start": v(21.57, 13.42) * mm, "end": v(21.6, 13.4) * mm});
            skLineSegment(sketch, "E8650", {"start": v(21.6, 13.4) * mm, "end": v(21.65, 13.37) * mm});
            skLineSegment(sketch, "E8651", {"start": v(21.65, 13.37) * mm, "end": v(21.68, 13.35) * mm});
            skLineSegment(sketch, "E8652", {"start": v(21.68, 13.35) * mm, "end": v(21.72, 13.33) * mm});
            skLineSegment(sketch, "E8653", {"start": v(21.72, 13.33) * mm, "end": v(21.76, 13.3) * mm});
            skLineSegment(sketch, "E8654", {"start": v(21.76, 13.3) * mm, "end": v(21.8, 13.29) * mm});
            skLineSegment(sketch, "E8655", {"start": v(21.8, 13.29) * mm, "end": v(21.84, 13.27) * mm});
            skLineSegment(sketch, "E8656", {"start": v(21.84, 13.27) * mm, "end": v(21.88, 13.26) * mm});
            skLineSegment(sketch, "E8657", {"start": v(21.88, 13.26) * mm, "end": v(21.92, 13.25) * mm});
            skLineSegment(sketch, "E8658", {"start": v(21.92, 13.25) * mm, "end": v(21.96, 13.23) * mm});
            skLineSegment(sketch, "E8659", {"start": v(21.96, 13.23) * mm, "end": v(22, 13.22) * mm});
            skLineSegment(sketch, "E8660", {"start": v(22, 13.22) * mm, "end": v(22.05, 13.21) * mm});
            skLineSegment(sketch, "E8661", {"start": v(22.05, 13.21) * mm, "end": v(22.1, 13.2) * mm});
            skLineSegment(sketch, "E8662", {"start": v(22.1, 13.2) * mm, "end": v(22.13, 13.2) * mm});
            skLineSegment(sketch, "E8663", {"start": v(22.13, 13.2) * mm, "end": v(22.18, 13.2) * mm});
            skLineSegment(sketch, "E8664", {"start": v(22.18, 13.2) * mm, "end": v(22.22, 13.2) * mm});
            skLineSegment(sketch, "E8665", {"start": v(22.22, 13.2) * mm, "end": v(22.26, 13.2) * mm});
            skLineSegment(sketch, "E8666", {"start": v(22.26, 13.2) * mm, "end": v(22.3, 13.2) * mm});
            skLineSegment(sketch, "E8667", {"start": v(22.3, 13.2) * mm, "end": v(22.35, 13.2) * mm});
            skLineSegment(sketch, "E8668", {"start": v(22.35, 13.2) * mm, "end": v(22.4, 13.2) * mm});
            skLineSegment(sketch, "E8669", {"start": v(22.4, 13.2) * mm, "end": v(22.44, 13.2) * mm});
            skLineSegment(sketch, "E8670", {"start": v(22.44, 13.2) * mm, "end": v(22.48, 13.2) * mm});
            skLineSegment(sketch, "E8671", {"start": v(22.48, 13.2) * mm, "end": v(22.52, 13.21) * mm});
            skLineSegment(sketch, "E8672", {"start": v(22.52, 13.21) * mm, "end": v(22.57, 13.22) * mm});
            skLineSegment(sketch, "E8673", {"start": v(22.57, 13.22) * mm, "end": v(22.6, 13.23) * mm});
            skLineSegment(sketch, "E8674", {"start": v(22.6, 13.23) * mm, "end": v(22.65, 13.25) * mm});
            skLineSegment(sketch, "E8675", {"start": v(22.65, 13.25) * mm, "end": v(22.7, 13.26) * mm});
            skLineSegment(sketch, "E8676", {"start": v(22.7, 13.26) * mm, "end": v(22.73, 13.27) * mm});
            skLineSegment(sketch, "E8677", {"start": v(22.73, 13.27) * mm, "end": v(22.77, 13.29) * mm});
            skLineSegment(sketch, "E8678", {"start": v(22.77, 13.29) * mm, "end": v(22.81, 13.3) * mm});
            skLineSegment(sketch, "E8679", {"start": v(22.81, 13.3) * mm, "end": v(22.85, 13.33) * mm});
            skLineSegment(sketch, "E8680", {"start": v(22.85, 13.33) * mm, "end": v(22.89, 13.35) * mm});
            skLineSegment(sketch, "E8681", {"start": v(22.89, 13.35) * mm, "end": v(22.93, 13.37) * mm});
            skLineSegment(sketch, "E8682", {"start": v(22.93, 13.37) * mm, "end": v(22.96, 13.4) * mm});
            skLineSegment(sketch, "E8683", {"start": v(22.96, 13.4) * mm, "end": v(23, 13.42) * mm});
            skLineSegment(sketch, "E8684", {"start": v(23.14, 13.52) * mm, "end": v(23.17, 13.55) * mm});
            skLineSegment(sketch, "E8685", {"start": v(23.17, 13.55) * mm, "end": v(23.2, 13.58) * mm});
            skLineSegment(sketch, "E8686", {"start": v(23.2, 13.58) * mm, "end": v(23.23, 13.62) * mm});
            skLineSegment(sketch, "E8687", {"start": v(23.23, 13.62) * mm, "end": v(23.25, 13.65) * mm});
            skLineSegment(sketch, "E8688", {"start": v(23.25, 13.65) * mm, "end": v(23.28, 13.68) * mm});
            skLineSegment(sketch, "E8689", {"start": v(23.28, 13.68) * mm, "end": v(23.3, 13.72) * mm});
            skLineSegment(sketch, "E8690", {"start": v(23.3, 13.72) * mm, "end": v(23.33, 13.76) * mm});
            skLineSegment(sketch, "E8691", {"start": v(23.33, 13.76) * mm, "end": v(23.35, 13.8) * mm});
            skLineSegment(sketch, "E8692", {"start": v(23.35, 13.8) * mm, "end": v(23.38, 13.83) * mm});
            skLineSegment(sketch, "E8693", {"start": v(23.38, 13.83) * mm, "end": v(23.4, 13.87) * mm});
            skLineSegment(sketch, "E8694", {"start": v(23.4, 13.87) * mm, "end": v(23.42, 13.9) * mm});
            skLineSegment(sketch, "E8695", {"start": v(23.42, 13.9) * mm, "end": v(23.43, 13.95) * mm});
            skLineSegment(sketch, "E8696", {"start": v(23.43, 13.95) * mm, "end": v(23.45, 13.99) * mm});
            skLineSegment(sketch, "E8697", {"start": v(23.45, 13.99) * mm, "end": v(23.47, 14.03) * mm});
            skLineSegment(sketch, "E8698", {"start": v(23.47, 14.03) * mm, "end": v(23.48, 14.07) * mm});
            skLineSegment(sketch, "E8699", {"start": v(23.48, 14.07) * mm, "end": v(23.5, 14.1) * mm});
            skLineSegment(sketch, "E8700", {"start": v(23.5, 14.1) * mm, "end": v(23.5, 14.15) * mm});
            skLineSegment(sketch, "E8701", {"start": v(23.5, 14.15) * mm, "end": v(23.51, 14.2) * mm});
            skLineSegment(sketch, "E8702", {"start": v(23.51, 14.2) * mm, "end": v(23.52, 14.24) * mm});
            skLineSegment(sketch, "E8703", {"start": v(23.52, 14.24) * mm, "end": v(23.53, 14.28) * mm});
            skLineSegment(sketch, "E8704", {"start": v(23.53, 14.28) * mm, "end": v(23.53, 14.32) * mm});
            skLineSegment(sketch, "E8705", {"start": v(23.53, 14.32) * mm, "end": v(23.53, 14.37) * mm});
            skLineSegment(sketch, "E8706", {"start": v(23.53, 14.37) * mm, "end": v(23.54, 14.4) * mm});
            skLineSegment(sketch, "E8707", {"start": v(23.54, 14.4) * mm, "end": v(23.54, 14.45) * mm});
            skLineSegment(sketch, "E8708", {"start": v(23.54, 14.45) * mm, "end": v(23.54, 14.5) * mm});
            skLineSegment(sketch, "E8709", {"start": v(23.54, 14.5) * mm, "end": v(23.53, 14.54) * mm});
            skLineSegment(sketch, "E8710", {"start": v(23.53, 14.54) * mm, "end": v(23.53, 14.58) * mm});
            skLineSegment(sketch, "E8711", {"start": v(23.53, 14.58) * mm, "end": v(23.52, 14.63) * mm});
            skLineSegment(sketch, "E8712", {"start": v(23.52, 14.63) * mm, "end": v(23.52, 14.67) * mm});
            skLineSegment(sketch, "E8713", {"start": v(23.52, 14.67) * mm, "end": v(23.5, 14.71) * mm});
            skLineSegment(sketch, "E8714", {"start": v(23.5, 14.71) * mm, "end": v(23.5, 14.75) * mm});
            skLineSegment(sketch, "E8715", {"start": v(23.5, 14.75) * mm, "end": v(23.49, 14.8) * mm});
            skLineSegment(sketch, "E8716", {"start": v(23.49, 14.8) * mm, "end": v(23.47, 14.84) * mm});
            skLineSegment(sketch, "E8717", {"start": v(23.47, 14.84) * mm, "end": v(23.46, 14.88) * mm});
            skLineSegment(sketch, "E8718", {"start": v(23.46, 14.88) * mm, "end": v(23.44, 14.92) * mm});
            skLineSegment(sketch, "E8719", {"start": v(23.44, 14.92) * mm, "end": v(23.43, 14.96) * mm});
            skLineSegment(sketch, "E8720", {"start": v(23.43, 14.96) * mm, "end": v(23.4, 15) * mm});
            skLineSegment(sketch, "E8721", {"start": v(23.4, 15) * mm, "end": v(23.39, 15.04) * mm});
            skLineSegment(sketch, "E8722", {"start": v(23.39, 15.04) * mm, "end": v(23.37, 15.07) * mm});
            skLineSegment(sketch, "E8723", {"start": v(23.37, 15.07) * mm, "end": v(23.34, 15.1) * mm});
            skLineSegment(sketch, "E8724", {"start": v(23.34, 15.1) * mm, "end": v(23.32, 15.15) * mm});
            skLineSegment(sketch, "E8725", {"start": v(23.32, 15.15) * mm, "end": v(23.3, 15.18) * mm});
            skLineSegment(sketch, "E8726", {"start": v(23.3, 15.18) * mm, "end": v(23.27, 15.22) * mm});
            skLineSegment(sketch, "E8727", {"start": v(23.27, 15.22) * mm, "end": v(23.24, 15.25) * mm});
            skLineSegment(sketch, "E8728", {"start": v(23.24, 15.25) * mm, "end": v(23.21, 15.28) * mm});
            skLineSegment(sketch, "E8729", {"start": v(22.98, 15.48) * mm, "end": v(22.95, 15.5) * mm});
            skLineSegment(sketch, "E8730", {"start": v(22.95, 15.5) * mm, "end": v(22.9, 15.53) * mm});
            skLineSegment(sketch, "E8731", {"start": v(22.9, 15.53) * mm, "end": v(22.87, 15.55) * mm});
            skLineSegment(sketch, "E8732", {"start": v(22.87, 15.55) * mm, "end": v(22.83, 15.57) * mm});
            skLineSegment(sketch, "E8733", {"start": v(22.83, 15.57) * mm, "end": v(22.8, 15.58) * mm});
            skLineSegment(sketch, "E8734", {"start": v(22.8, 15.58) * mm, "end": v(22.75, 15.6) * mm});
            skLineSegment(sketch, "E8735", {"start": v(22.75, 15.6) * mm, "end": v(22.71, 15.62) * mm});
            skLineSegment(sketch, "E8736", {"start": v(22.71, 15.62) * mm, "end": v(22.67, 15.63) * mm});
            skLineSegment(sketch, "E8737", {"start": v(22.67, 15.63) * mm, "end": v(22.63, 15.64) * mm});
            skLineSegment(sketch, "E8738", {"start": v(22.63, 15.64) * mm, "end": v(22.59, 15.65) * mm});
            skLineSegment(sketch, "E8739", {"start": v(22.59, 15.65) * mm, "end": v(22.54, 15.66) * mm});
            skLineSegment(sketch, "E8740", {"start": v(22.54, 15.66) * mm, "end": v(22.5, 15.67) * mm});
            skLineSegment(sketch, "E8741", {"start": v(22.5, 15.67) * mm, "end": v(22.46, 15.68) * mm});
            skLineSegment(sketch, "E8742", {"start": v(22.46, 15.68) * mm, "end": v(22.42, 15.68) * mm});
            skLineSegment(sketch, "E8743", {"start": v(22.42, 15.68) * mm, "end": v(22.37, 15.69) * mm});
            skLineSegment(sketch, "E8744", {"start": v(22.37, 15.69) * mm, "end": v(22.33, 15.7) * mm});
            skLineSegment(sketch, "E8745", {"start": v(22.33, 15.7) * mm, "end": v(22.29, 15.7) * mm});
            skLineSegment(sketch, "E8746", {"start": v(86.04, 15.7) * mm, "end": v(86, 15.7) * mm});
            skLineSegment(sketch, "E8747", {"start": v(86, 15.7) * mm, "end": v(85.95, 15.69) * mm});
            skLineSegment(sketch, "E8748", {"start": v(85.95, 15.69) * mm, "end": v(85.9, 15.68) * mm});
            skLineSegment(sketch, "E8749", {"start": v(85.9, 15.68) * mm, "end": v(85.86, 15.68) * mm});
            skLineSegment(sketch, "E8750", {"start": v(85.86, 15.68) * mm, "end": v(85.82, 15.67) * mm});
            skLineSegment(sketch, "E8751", {"start": v(85.82, 15.67) * mm, "end": v(85.78, 15.66) * mm});
            skLineSegment(sketch, "E8752", {"start": v(85.78, 15.66) * mm, "end": v(85.74, 15.65) * mm});
            skLineSegment(sketch, "E8753", {"start": v(85.74, 15.65) * mm, "end": v(85.7, 15.64) * mm});
            skLineSegment(sketch, "E8754", {"start": v(85.7, 15.64) * mm, "end": v(85.65, 15.63) * mm});
            skLineSegment(sketch, "E8755", {"start": v(85.65, 15.63) * mm, "end": v(85.61, 15.62) * mm});
            skLineSegment(sketch, "E8756", {"start": v(85.61, 15.62) * mm, "end": v(85.57, 15.6) * mm});
            skLineSegment(sketch, "E8757", {"start": v(85.57, 15.6) * mm, "end": v(85.53, 15.58) * mm});
            skLineSegment(sketch, "E8758", {"start": v(85.53, 15.58) * mm, "end": v(85.5, 15.57) * mm});
            skLineSegment(sketch, "E8759", {"start": v(85.5, 15.57) * mm, "end": v(85.45, 15.55) * mm});
            skLineSegment(sketch, "E8760", {"start": v(85.45, 15.55) * mm, "end": v(85.41, 15.53) * mm});
            skLineSegment(sketch, "E8761", {"start": v(85.41, 15.53) * mm, "end": v(85.38, 15.5) * mm});
            skLineSegment(sketch, "E8762", {"start": v(85.38, 15.5) * mm, "end": v(85.34, 15.48) * mm});
            skLineSegment(sketch, "E8763", {"start": v(85.34, 15.48) * mm, "end": v(85.3, 15.46) * mm});
            skLineSegment(sketch, "E8764", {"start": v(85.3, 15.46) * mm, "end": v(85.27, 15.43) * mm});
            skLineSegment(sketch, "E8765", {"start": v(85.27, 15.43) * mm, "end": v(85.24, 15.4) * mm});
            skLineSegment(sketch, "E8766", {"start": v(85.24, 15.4) * mm, "end": v(85.2, 15.37) * mm});
            skLineSegment(sketch, "E8767", {"start": v(85.2, 15.37) * mm, "end": v(85.17, 15.34) * mm});
            skLineSegment(sketch, "E8768", {"start": v(85.17, 15.34) * mm, "end": v(85.14, 15.31) * mm});
            skLineSegment(sketch, "E8769", {"start": v(85.14, 15.31) * mm, "end": v(85.11, 15.28) * mm});
            skLineSegment(sketch, "E8770", {"start": v(85.11, 15.28) * mm, "end": v(85.08, 15.25) * mm});
            skLineSegment(sketch, "E8771", {"start": v(85.08, 15.25) * mm, "end": v(85.06, 15.22) * mm});
            skLineSegment(sketch, "E8772", {"start": v(85.03, 15.18) * mm, "end": v(85, 15.15) * mm});
            skLineSegment(sketch, "E8773", {"start": v(85, 15.15) * mm, "end": v(84.98, 15.1) * mm});
            skLineSegment(sketch, "E8774", {"start": v(84.98, 15.1) * mm, "end": v(84.96, 15.07) * mm});
            skLineSegment(sketch, "E8775", {"start": v(84.96, 15.07) * mm, "end": v(84.94, 15.04) * mm});
            skLineSegment(sketch, "E8776", {"start": v(84.94, 15.04) * mm, "end": v(84.92, 15) * mm});
            skLineSegment(sketch, "E8777", {"start": v(84.92, 15) * mm, "end": v(84.9, 14.96) * mm});
            skLineSegment(sketch, "E8778", {"start": v(84.9, 14.96) * mm, "end": v(84.88, 14.92) * mm});
            skLineSegment(sketch, "E8779", {"start": v(84.88, 14.92) * mm, "end": v(84.86, 14.88) * mm});
            skLineSegment(sketch, "E8780", {"start": v(84.86, 14.88) * mm, "end": v(84.85, 14.84) * mm});
            skLineSegment(sketch, "E8781", {"start": v(84.85, 14.84) * mm, "end": v(84.84, 14.8) * mm});
            skLineSegment(sketch, "E8782", {"start": v(84.84, 14.8) * mm, "end": v(84.83, 14.75) * mm});
            skLineSegment(sketch, "E8783", {"start": v(84.83, 14.75) * mm, "end": v(84.82, 14.71) * mm});
            skLineSegment(sketch, "E8784", {"start": v(84.82, 14.71) * mm, "end": v(84.8, 14.67) * mm});
            skLineSegment(sketch, "E8785", {"start": v(84.8, 14.67) * mm, "end": v(84.8, 14.63) * mm});
            skLineSegment(sketch, "E8786", {"start": v(84.8, 14.63) * mm, "end": v(84.8, 14.58) * mm});
            skLineSegment(sketch, "E8787", {"start": v(84.8, 14.58) * mm, "end": v(84.8, 14.54) * mm});
            skLineSegment(sketch, "E8788", {"start": v(84.8, 14.54) * mm, "end": v(84.79, 14.5) * mm});
            skLineSegment(sketch, "E8789", {"start": v(84.79, 14.5) * mm, "end": v(84.79, 14.45) * mm});
            skLineSegment(sketch, "E8790", {"start": v(84.79, 14.45) * mm, "end": v(84.79, 14.4) * mm});
            skLineSegment(sketch, "E8791", {"start": v(84.79, 14.4) * mm, "end": v(84.79, 14.37) * mm});
            skLineSegment(sketch, "E8792", {"start": v(84.79, 14.37) * mm, "end": v(84.8, 14.32) * mm});
            skLineSegment(sketch, "E8793", {"start": v(84.8, 14.32) * mm, "end": v(84.8, 14.28) * mm});
            skLineSegment(sketch, "E8794", {"start": v(84.8, 14.28) * mm, "end": v(84.8, 14.24) * mm});
            skLineSegment(sketch, "E8795", {"start": v(84.8, 14.24) * mm, "end": v(84.81, 14.2) * mm});
            skLineSegment(sketch, "E8796", {"start": v(84.81, 14.2) * mm, "end": v(84.82, 14.15) * mm});
            skLineSegment(sketch, "E8797", {"start": v(84.82, 14.15) * mm, "end": v(84.83, 14.1) * mm});
            skLineSegment(sketch, "E8798", {"start": v(84.83, 14.1) * mm, "end": v(84.84, 14.07) * mm});
            skLineSegment(sketch, "E8799", {"start": v(84.84, 14.07) * mm, "end": v(84.86, 14.03) * mm});
            skLineSegment(sketch, "E8800", {"start": v(84.86, 14.03) * mm, "end": v(84.87, 13.99) * mm});
            skLineSegment(sketch, "E8801", {"start": v(84.87, 13.99) * mm, "end": v(84.89, 13.95) * mm});
            skLineSegment(sketch, "E8802", {"start": v(84.89, 13.95) * mm, "end": v(84.9, 13.9) * mm});
            skLineSegment(sketch, "E8803", {"start": v(84.9, 13.9) * mm, "end": v(84.93, 13.87) * mm});
            skLineSegment(sketch, "E8804", {"start": v(84.93, 13.87) * mm, "end": v(84.95, 13.83) * mm});
            skLineSegment(sketch, "E8805", {"start": v(84.95, 13.83) * mm, "end": v(84.97, 13.8) * mm});
            skLineSegment(sketch, "E8806", {"start": v(84.97, 13.8) * mm, "end": v(85, 13.76) * mm});
            skLineSegment(sketch, "E8807", {"start": v(85, 13.76) * mm, "end": v(85.02, 13.72) * mm});
            skLineSegment(sketch, "E8808", {"start": v(85.02, 13.72) * mm, "end": v(85.04, 13.68) * mm});
            skLineSegment(sketch, "E8809", {"start": v(85.07, 13.65) * mm, "end": v(85.1, 13.62) * mm});
            skLineSegment(sketch, "E8810", {"start": v(85.1, 13.62) * mm, "end": v(85.13, 13.58) * mm});
            skLineSegment(sketch, "E8811", {"start": v(85.13, 13.58) * mm, "end": v(85.16, 13.55) * mm});
            skLineSegment(sketch, "E8812", {"start": v(85.16, 13.55) * mm, "end": v(85.19, 13.52) * mm});
            skLineSegment(sketch, "E8813", {"start": v(85.19, 13.52) * mm, "end": v(85.22, 13.5) * mm});
            skLineSegment(sketch, "E8814", {"start": v(85.22, 13.5) * mm, "end": v(85.25, 13.47) * mm});
            skLineSegment(sketch, "E8815", {"start": v(85.25, 13.47) * mm, "end": v(85.29, 13.44) * mm});
            skLineSegment(sketch, "E8816", {"start": v(85.29, 13.44) * mm, "end": v(85.32, 13.42) * mm});
            skLineSegment(sketch, "E8817", {"start": v(85.32, 13.42) * mm, "end": v(85.36, 13.4) * mm});
            skLineSegment(sketch, "E8818", {"start": v(85.36, 13.4) * mm, "end": v(85.4, 13.37) * mm});
            skLineSegment(sketch, "E8819", {"start": v(85.4, 13.37) * mm, "end": v(85.43, 13.35) * mm});
            skLineSegment(sketch, "E8820", {"start": v(85.43, 13.35) * mm, "end": v(85.47, 13.33) * mm});
            skLineSegment(sketch, "E8821", {"start": v(85.47, 13.33) * mm, "end": v(85.51, 13.3) * mm});
            skLineSegment(sketch, "E8822", {"start": v(85.51, 13.3) * mm, "end": v(85.55, 13.29) * mm});
            skLineSegment(sketch, "E8823", {"start": v(85.55, 13.29) * mm, "end": v(85.6, 13.27) * mm});
            skLineSegment(sketch, "E8824", {"start": v(85.6, 13.27) * mm, "end": v(85.63, 13.26) * mm});
            skLineSegment(sketch, "E8825", {"start": v(85.63, 13.26) * mm, "end": v(85.67, 13.25) * mm});
            skLineSegment(sketch, "E8826", {"start": v(85.67, 13.25) * mm, "end": v(85.71, 13.23) * mm});
            skLineSegment(sketch, "E8827", {"start": v(85.71, 13.23) * mm, "end": v(85.76, 13.22) * mm});
            skLineSegment(sketch, "E8828", {"start": v(85.76, 13.22) * mm, "end": v(85.8, 13.21) * mm});
            skLineSegment(sketch, "E8829", {"start": v(85.8, 13.21) * mm, "end": v(85.84, 13.2) * mm});
            skLineSegment(sketch, "E8830", {"start": v(85.84, 13.2) * mm, "end": v(85.88, 13.2) * mm});
            skLineSegment(sketch, "E8831", {"start": v(85.88, 13.2) * mm, "end": v(85.93, 13.2) * mm});
            skLineSegment(sketch, "E8832", {"start": v(85.93, 13.2) * mm, "end": v(85.97, 13.2) * mm});
            skLineSegment(sketch, "E8833", {"start": v(85.97, 13.2) * mm, "end": v(86.01, 13.2) * mm});
            skLineSegment(sketch, "E8834", {"start": v(86.01, 13.2) * mm, "end": v(86.06, 13.2) * mm});
            skLineSegment(sketch, "E8835", {"start": v(86.06, 13.2) * mm, "end": v(86.1, 13.2) * mm});
            skLineSegment(sketch, "E8836", {"start": v(86.1, 13.2) * mm, "end": v(86.14, 13.2) * mm});
            skLineSegment(sketch, "E8837", {"start": v(86.14, 13.2) * mm, "end": v(86.19, 13.2) * mm});
            skLineSegment(sketch, "E8838", {"start": v(86.19, 13.2) * mm, "end": v(86.23, 13.2) * mm});
            skLineSegment(sketch, "E8839", {"start": v(86.23, 13.2) * mm, "end": v(86.27, 13.21) * mm});
            skLineSegment(sketch, "E8840", {"start": v(86.27, 13.21) * mm, "end": v(86.32, 13.22) * mm});
            skLineSegment(sketch, "E8841", {"start": v(86.32, 13.22) * mm, "end": v(86.36, 13.23) * mm});
            skLineSegment(sketch, "E8842", {"start": v(86.36, 13.23) * mm, "end": v(86.4, 13.25) * mm});
            skLineSegment(sketch, "E8843", {"start": v(86.4, 13.25) * mm, "end": v(86.44, 13.26) * mm});
            skLineSegment(sketch, "E8844", {"start": v(86.44, 13.26) * mm, "end": v(86.48, 13.27) * mm});
            skLineSegment(sketch, "E8845", {"start": v(86.48, 13.27) * mm, "end": v(86.52, 13.29) * mm});
            skLineSegment(sketch, "E8846", {"start": v(86.52, 13.29) * mm, "end": v(86.56, 13.3) * mm});
            skLineSegment(sketch, "E8847", {"start": v(86.56, 13.3) * mm, "end": v(86.6, 13.33) * mm});
            skLineSegment(sketch, "E8848", {"start": v(86.89, 13.52) * mm, "end": v(86.92, 13.55) * mm});
            skLineSegment(sketch, "E8849", {"start": v(86.92, 13.55) * mm, "end": v(86.95, 13.58) * mm});
            skLineSegment(sketch, "E8850", {"start": v(86.95, 13.58) * mm, "end": v(86.98, 13.62) * mm});
            skLineSegment(sketch, "E8851", {"start": v(86.98, 13.62) * mm, "end": v(87, 13.65) * mm});
            skLineSegment(sketch, "E8852", {"start": v(87, 13.65) * mm, "end": v(87.03, 13.68) * mm});
            skLineSegment(sketch, "E8853", {"start": v(87.03, 13.68) * mm, "end": v(87.06, 13.72) * mm});
            skLineSegment(sketch, "E8854", {"start": v(87.06, 13.72) * mm, "end": v(87.08, 13.76) * mm});
            skLineSegment(sketch, "E8855", {"start": v(87.08, 13.76) * mm, "end": v(87.1, 13.8) * mm});
            skLineSegment(sketch, "E8856", {"start": v(87.1, 13.8) * mm, "end": v(87.13, 13.83) * mm});
            skLineSegment(sketch, "E8857", {"start": v(87.13, 13.83) * mm, "end": v(87.15, 13.87) * mm});
            skLineSegment(sketch, "E8858", {"start": v(87.15, 13.87) * mm, "end": v(87.17, 13.9) * mm});
            skLineSegment(sketch, "E8859", {"start": v(87.17, 13.9) * mm, "end": v(87.18, 13.95) * mm});
            skLineSegment(sketch, "E8860", {"start": v(87.18, 13.95) * mm, "end": v(87.2, 13.99) * mm});
            skLineSegment(sketch, "E8861", {"start": v(87.2, 13.99) * mm, "end": v(87.22, 14.03) * mm});
            skLineSegment(sketch, "E8862", {"start": v(87.22, 14.03) * mm, "end": v(87.23, 14.07) * mm});
            skLineSegment(sketch, "E8863", {"start": v(87.23, 14.07) * mm, "end": v(87.24, 14.1) * mm});
            skLineSegment(sketch, "E8864", {"start": v(87.24, 14.1) * mm, "end": v(87.25, 14.15) * mm});
            skLineSegment(sketch, "E8865", {"start": v(87.25, 14.15) * mm, "end": v(87.26, 14.2) * mm});
            skLineSegment(sketch, "E8866", {"start": v(87.26, 14.2) * mm, "end": v(87.27, 14.24) * mm});
            skLineSegment(sketch, "E8867", {"start": v(87.27, 14.24) * mm, "end": v(87.28, 14.28) * mm});
            skLineSegment(sketch, "E8868", {"start": v(87.28, 14.28) * mm, "end": v(87.28, 14.32) * mm});
            skLineSegment(sketch, "E8869", {"start": v(87.28, 14.32) * mm, "end": v(87.28, 14.37) * mm});
            skLineSegment(sketch, "E8870", {"start": v(87.28, 14.37) * mm, "end": v(87.29, 14.4) * mm});
            skLineSegment(sketch, "E8871", {"start": v(87.29, 14.4) * mm, "end": v(87.29, 14.45) * mm});
            skLineSegment(sketch, "E8872", {"start": v(87.29, 14.45) * mm, "end": v(87.29, 14.5) * mm});
            skLineSegment(sketch, "E8873", {"start": v(87.29, 14.5) * mm, "end": v(87.28, 14.54) * mm});
            skLineSegment(sketch, "E8874", {"start": v(87.28, 14.54) * mm, "end": v(87.28, 14.58) * mm});
            skLineSegment(sketch, "E8875", {"start": v(87.28, 14.58) * mm, "end": v(87.27, 14.63) * mm});
            skLineSegment(sketch, "E8876", {"start": v(87.27, 14.63) * mm, "end": v(87.27, 14.67) * mm});
            skLineSegment(sketch, "E8877", {"start": v(87.27, 14.67) * mm, "end": v(87.26, 14.71) * mm});
            skLineSegment(sketch, "E8878", {"start": v(87.26, 14.71) * mm, "end": v(87.25, 14.75) * mm});
            skLineSegment(sketch, "E8879", {"start": v(87.25, 14.75) * mm, "end": v(87.24, 14.8) * mm});
            skLineSegment(sketch, "E8880", {"start": v(87.24, 14.8) * mm, "end": v(87.22, 14.84) * mm});
            skLineSegment(sketch, "E8881", {"start": v(87.2, 14.88) * mm, "end": v(87.2, 14.92) * mm});
            skLineSegment(sketch, "E8882", {"start": v(87.2, 14.92) * mm, "end": v(87.18, 14.96) * mm});
            skLineSegment(sketch, "E8883", {"start": v(87.18, 14.96) * mm, "end": v(87.16, 15) * mm});
            skLineSegment(sketch, "E8884", {"start": v(87.16, 15) * mm, "end": v(87.14, 15.04) * mm});
            skLineSegment(sketch, "E8885", {"start": v(87.14, 15.04) * mm, "end": v(87.12, 15.07) * mm});
            skLineSegment(sketch, "E8886", {"start": v(87.12, 15.07) * mm, "end": v(87.1, 15.1) * mm});
            skLineSegment(sketch, "E8887", {"start": v(87.1, 15.1) * mm, "end": v(87.07, 15.15) * mm});
            skLineSegment(sketch, "E8888", {"start": v(87.07, 15.15) * mm, "end": v(87.04, 15.18) * mm});
            skLineSegment(sketch, "E8889", {"start": v(87.04, 15.18) * mm, "end": v(87.02, 15.22) * mm});
            skLineSegment(sketch, "E8890", {"start": v(87.02, 15.22) * mm, "end": v(87, 15.25) * mm});
            skLineSegment(sketch, "E8891", {"start": v(87, 15.25) * mm, "end": v(86.96, 15.28) * mm});
            skLineSegment(sketch, "E8892", {"start": v(86.96, 15.28) * mm, "end": v(86.93, 15.31) * mm});
            skLineSegment(sketch, "E8893", {"start": v(86.93, 15.31) * mm, "end": v(86.9, 15.34) * mm});
            skLineSegment(sketch, "E8894", {"start": v(86.62, 15.55) * mm, "end": v(86.58, 15.57) * mm});
            skLineSegment(sketch, "E8895", {"start": v(86.58, 15.57) * mm, "end": v(86.54, 15.58) * mm});
            skLineSegment(sketch, "E8896", {"start": v(86.54, 15.58) * mm, "end": v(86.5, 15.6) * mm});
            skLineSegment(sketch, "E8897", {"start": v(86.5, 15.6) * mm, "end": v(86.46, 15.62) * mm});
            skLineSegment(sketch, "E8898", {"start": v(86.46, 15.62) * mm, "end": v(86.42, 15.63) * mm});
            skLineSegment(sketch, "E8899", {"start": v(86.42, 15.63) * mm, "end": v(86.38, 15.64) * mm});
            skLineSegment(sketch, "E8900", {"start": v(86.38, 15.64) * mm, "end": v(86.34, 15.65) * mm});
            skLineSegment(sketch, "E8901", {"start": v(86.34, 15.65) * mm, "end": v(86.3, 15.66) * mm});
            skLineSegment(sketch, "E8902", {"start": v(86.3, 15.66) * mm, "end": v(86.25, 15.67) * mm});
            skLineSegment(sketch, "E8903", {"start": v(86.25, 15.67) * mm, "end": v(86.2, 15.68) * mm});
            skLineSegment(sketch, "E8904", {"start": v(86.2, 15.68) * mm, "end": v(86.17, 15.68) * mm});
            skLineSegment(sketch, "E8905", {"start": v(86.17, 15.68) * mm, "end": v(86.12, 15.69) * mm});
            skLineSegment(sketch, "E8906", {"start": v(86.12, 15.69) * mm, "end": v(86.08, 15.7) * mm});
            skLineSegment(sketch, "E8907", {"start": v(86.08, 15.7) * mm, "end": v(86.04, 15.7) * mm});
            skLineSegment(sketch, "E8908", {"start": v(-41.46, 15.7) * mm, "end": v(-41.5, 15.7) * mm});
            skLineSegment(sketch, "E8909", {"start": v(-41.5, 15.7) * mm, "end": v(-41.55, 15.69) * mm});
            skLineSegment(sketch, "E8910", {"start": v(-41.55, 15.69) * mm, "end": v(-41.6, 15.68) * mm});
            skLineSegment(sketch, "E8911", {"start": v(-41.6, 15.68) * mm, "end": v(-41.64, 15.68) * mm});
            skLineSegment(sketch, "E8912", {"start": v(-41.64, 15.68) * mm, "end": v(-41.68, 15.67) * mm});
            skLineSegment(sketch, "E8913", {"start": v(-41.68, 15.67) * mm, "end": v(-41.72, 15.66) * mm});
            skLineSegment(sketch, "E8914", {"start": v(-41.72, 15.66) * mm, "end": v(-41.76, 15.65) * mm});
            skLineSegment(sketch, "E8915", {"start": v(-41.76, 15.65) * mm, "end": v(-41.8, 15.64) * mm});
            skLineSegment(sketch, "E8916", {"start": v(-41.8, 15.64) * mm, "end": v(-41.85, 15.63) * mm});
            skLineSegment(sketch, "E8917", {"start": v(-41.89, 15.62) * mm, "end": v(-41.93, 15.6) * mm});
            skLineSegment(sketch, "E8918", {"start": v(-41.93, 15.6) * mm, "end": v(-41.97, 15.58) * mm});
            skLineSegment(sketch, "E8919", {"start": v(-41.97, 15.58) * mm, "end": v(-42, 15.57) * mm});
            skLineSegment(sketch, "E8920", {"start": v(-42, 15.57) * mm, "end": v(-42.05, 15.55) * mm});
            skLineSegment(sketch, "E8921", {"start": v(-42.05, 15.55) * mm, "end": v(-42.09, 15.53) * mm});
            skLineSegment(sketch, "E8922", {"start": v(-42.09, 15.53) * mm, "end": v(-42.12, 15.5) * mm});
            skLineSegment(sketch, "E8923", {"start": v(-42.12, 15.5) * mm, "end": v(-42.16, 15.48) * mm});
            skLineSegment(sketch, "E8924", {"start": v(-42.16, 15.48) * mm, "end": v(-42.2, 15.46) * mm});
            skLineSegment(sketch, "E8925", {"start": v(-42.2, 15.46) * mm, "end": v(-42.23, 15.43) * mm});
            skLineSegment(sketch, "E8926", {"start": v(-42.23, 15.43) * mm, "end": v(-42.26, 15.4) * mm});
            skLineSegment(sketch, "E8927", {"start": v(-42.26, 15.4) * mm, "end": v(-42.3, 15.37) * mm});
            skLineSegment(sketch, "E8928", {"start": v(-42.3, 15.37) * mm, "end": v(-42.33, 15.34) * mm});
            skLineSegment(sketch, "E8929", {"start": v(-42.33, 15.34) * mm, "end": v(-42.36, 15.31) * mm});
            skLineSegment(sketch, "E8930", {"start": v(-42.39, 15.28) * mm, "end": v(-42.42, 15.25) * mm});
            skLineSegment(sketch, "E8931", {"start": v(-42.42, 15.25) * mm, "end": v(-42.44, 15.22) * mm});
            skLineSegment(sketch, "E8932", {"start": v(-42.44, 15.22) * mm, "end": v(-42.47, 15.18) * mm});
            skLineSegment(sketch, "E8933", {"start": v(-42.47, 15.18) * mm, "end": v(-42.5, 15.15) * mm});
            skLineSegment(sketch, "E8934", {"start": v(-42.5, 15.15) * mm, "end": v(-42.52, 15.1) * mm});
            skLineSegment(sketch, "E8935", {"start": v(-42.52, 15.1) * mm, "end": v(-42.54, 15.07) * mm});
            skLineSegment(sketch, "E8936", {"start": v(-42.54, 15.07) * mm, "end": v(-42.56, 15.04) * mm});
            skLineSegment(sketch, "E8937", {"start": v(-42.56, 15.04) * mm, "end": v(-42.58, 15) * mm});
            skLineSegment(sketch, "E8938", {"start": v(-42.58, 15) * mm, "end": v(-42.6, 14.96) * mm});
            skLineSegment(sketch, "E8939", {"start": v(-42.6, 14.96) * mm, "end": v(-42.62, 14.92) * mm});
            skLineSegment(sketch, "E8940", {"start": v(-42.62, 14.92) * mm, "end": v(-42.64, 14.88) * mm});
            skLineSegment(sketch, "E8941", {"start": v(-42.64, 14.88) * mm, "end": v(-42.65, 14.84) * mm});
            skLineSegment(sketch, "E8942", {"start": v(-42.65, 14.84) * mm, "end": v(-42.66, 14.8) * mm});
            skLineSegment(sketch, "E8943", {"start": v(-42.66, 14.8) * mm, "end": v(-42.67, 14.75) * mm});
            skLineSegment(sketch, "E8944", {"start": v(-42.67, 14.75) * mm, "end": v(-42.68, 14.71) * mm});
            skLineSegment(sketch, "E8945", {"start": v(-42.68, 14.71) * mm, "end": v(-42.7, 14.67) * mm});
            skLineSegment(sketch, "E8946", {"start": v(-42.7, 14.67) * mm, "end": v(-42.7, 14.63) * mm});
            skLineSegment(sketch, "E8947", {"start": v(-42.7, 14.63) * mm, "end": v(-42.7, 14.58) * mm});
            skLineSegment(sketch, "E8948", {"start": v(-42.7, 14.58) * mm, "end": v(-42.7, 14.54) * mm});
            skLineSegment(sketch, "E8949", {"start": v(-42.7, 14.54) * mm, "end": v(-42.71, 14.5) * mm});
            skLineSegment(sketch, "E8950", {"start": v(-42.71, 14.5) * mm, "end": v(-42.71, 14.45) * mm});
            skLineSegment(sketch, "E8951", {"start": v(-42.71, 14.45) * mm, "end": v(-42.71, 14.4) * mm});
            skLineSegment(sketch, "E8952", {"start": v(-42.71, 14.4) * mm, "end": v(-42.71, 14.37) * mm});
            skLineSegment(sketch, "E8953", {"start": v(-42.71, 14.37) * mm, "end": v(-42.7, 14.32) * mm});
            skLineSegment(sketch, "E8954", {"start": v(-42.7, 14.32) * mm, "end": v(-42.7, 14.28) * mm});
            skLineSegment(sketch, "E8955", {"start": v(-42.7, 14.28) * mm, "end": v(-42.7, 14.24) * mm});
            skLineSegment(sketch, "E8956", {"start": v(-42.7, 14.24) * mm, "end": v(-42.69, 14.2) * mm});
            skLineSegment(sketch, "E8957", {"start": v(-42.69, 14.2) * mm, "end": v(-42.68, 14.15) * mm});
            skLineSegment(sketch, "E8958", {"start": v(-42.68, 14.15) * mm, "end": v(-42.67, 14.1) * mm});
            skLineSegment(sketch, "E8959", {"start": v(-42.67, 14.1) * mm, "end": v(-42.66, 14.07) * mm});
            skLineSegment(sketch, "E8960", {"start": v(-42.64, 14.03) * mm, "end": v(-42.63, 13.99) * mm});
            skLineSegment(sketch, "E8961", {"start": v(-42.63, 13.99) * mm, "end": v(-42.61, 13.95) * mm});
            skLineSegment(sketch, "E8962", {"start": v(-42.61, 13.95) * mm, "end": v(-42.6, 13.9) * mm});
            skLineSegment(sketch, "E8963", {"start": v(-42.6, 13.9) * mm, "end": v(-42.57, 13.87) * mm});
            skLineSegment(sketch, "E8964", {"start": v(-42.57, 13.87) * mm, "end": v(-42.55, 13.83) * mm});
            skLineSegment(sketch, "E8965", {"start": v(-42.55, 13.83) * mm, "end": v(-42.53, 13.8) * mm});
            skLineSegment(sketch, "E8966", {"start": v(-42.53, 13.8) * mm, "end": v(-42.5, 13.76) * mm});
            skLineSegment(sketch, "E8967", {"start": v(-42.5, 13.76) * mm, "end": v(-42.48, 13.72) * mm});
            skLineSegment(sketch, "E8968", {"start": v(-42.48, 13.72) * mm, "end": v(-42.46, 13.68) * mm});
            skLineSegment(sketch, "E8969", {"start": v(-42.46, 13.68) * mm, "end": v(-42.43, 13.65) * mm});
            skLineSegment(sketch, "E8970", {"start": v(-42.43, 13.65) * mm, "end": v(-42.4, 13.62) * mm});
            skLineSegment(sketch, "E8971", {"start": v(-42.4, 13.62) * mm, "end": v(-42.37, 13.58) * mm});
            skLineSegment(sketch, "E8972", {"start": v(-42.34, 13.55) * mm, "end": v(-42.31, 13.52) * mm});
            skLineSegment(sketch, "E8973", {"start": v(-42.31, 13.52) * mm, "end": v(-42.28, 13.5) * mm});
            skLineSegment(sketch, "E8974", {"start": v(-42.28, 13.5) * mm, "end": v(-42.25, 13.47) * mm});
            skLineSegment(sketch, "E8975", {"start": v(-42.25, 13.47) * mm, "end": v(-42.21, 13.44) * mm});
            skLineSegment(sketch, "E8976", {"start": v(-42.21, 13.44) * mm, "end": v(-42.18, 13.42) * mm});
            skLineSegment(sketch, "E8977", {"start": v(-42.18, 13.42) * mm, "end": v(-42.14, 13.4) * mm});
            skLineSegment(sketch, "E8978", {"start": v(-42.14, 13.4) * mm, "end": v(-42.1, 13.37) * mm});
            skLineSegment(sketch, "E8979", {"start": v(-42.1, 13.37) * mm, "end": v(-42.07, 13.35) * mm});
            skLineSegment(sketch, "E8980", {"start": v(-42.07, 13.35) * mm, "end": v(-42.03, 13.33) * mm});
            skLineSegment(sketch, "E8981", {"start": v(-42.03, 13.33) * mm, "end": v(-41.99, 13.3) * mm});
            skLineSegment(sketch, "E8982", {"start": v(-41.99, 13.3) * mm, "end": v(-41.95, 13.29) * mm});
            skLineSegment(sketch, "E8983", {"start": v(-41.95, 13.29) * mm, "end": v(-41.9, 13.27) * mm});
            skLineSegment(sketch, "E8984", {"start": v(-41.9, 13.27) * mm, "end": v(-41.87, 13.26) * mm});
            skLineSegment(sketch, "E8985", {"start": v(-41.87, 13.26) * mm, "end": v(-41.83, 13.25) * mm});
            skLineSegment(sketch, "E8986", {"start": v(-41.83, 13.25) * mm, "end": v(-41.79, 13.23) * mm});
            skLineSegment(sketch, "E8987", {"start": v(-41.79, 13.23) * mm, "end": v(-41.74, 13.22) * mm});
            skLineSegment(sketch, "E8988", {"start": v(-41.74, 13.22) * mm, "end": v(-41.7, 13.21) * mm});
            skLineSegment(sketch, "E8989", {"start": v(-41.7, 13.21) * mm, "end": v(-41.66, 13.2) * mm});
            skLineSegment(sketch, "E8990", {"start": v(-41.66, 13.2) * mm, "end": v(-41.62, 13.2) * mm});
            skLineSegment(sketch, "E8991", {"start": v(-41.62, 13.2) * mm, "end": v(-41.57, 13.2) * mm});
            skLineSegment(sketch, "E8992", {"start": v(-41.57, 13.2) * mm, "end": v(-41.53, 13.2) * mm});
            skLineSegment(sketch, "E8993", {"start": v(-41.53, 13.2) * mm, "end": v(-41.49, 13.2) * mm});
            skLineSegment(sketch, "E8994", {"start": v(-41.49, 13.2) * mm, "end": v(-41.44, 13.2) * mm});
            skLineSegment(sketch, "E8995", {"start": v(-41.44, 13.2) * mm, "end": v(-41.4, 13.2) * mm});
            skLineSegment(sketch, "E8996", {"start": v(-41.4, 13.2) * mm, "end": v(-41.36, 13.2) * mm});
            skLineSegment(sketch, "E8997", {"start": v(-41.36, 13.2) * mm, "end": v(-41.31, 13.2) * mm});
            skLineSegment(sketch, "E8998", {"start": v(-41.31, 13.2) * mm, "end": v(-41.27, 13.2) * mm});
            skLineSegment(sketch, "E8999", {"start": v(-41.27, 13.2) * mm, "end": v(-41.23, 13.21) * mm});
            skLineSegment(sketch, "E9000", {"start": v(-41.23, 13.21) * mm, "end": v(-41.18, 13.22) * mm});
            skLineSegment(sketch, "E9001", {"start": v(-41.18, 13.22) * mm, "end": v(-41.14, 13.23) * mm});
            skLineSegment(sketch, "E9002", {"start": v(-41.14, 13.23) * mm, "end": v(-41.1, 13.25) * mm});
            skLineSegment(sketch, "E9003", {"start": v(-41.06, 13.26) * mm, "end": v(-41.02, 13.27) * mm});
            skLineSegment(sketch, "E9004", {"start": v(-41.02, 13.27) * mm, "end": v(-40.98, 13.29) * mm});
            skLineSegment(sketch, "E9005", {"start": v(-40.98, 13.29) * mm, "end": v(-40.94, 13.3) * mm});
            skLineSegment(sketch, "E9006", {"start": v(-40.94, 13.3) * mm, "end": v(-40.9, 13.33) * mm});
            skLineSegment(sketch, "E9007", {"start": v(-40.9, 13.33) * mm, "end": v(-40.86, 13.35) * mm});
            skLineSegment(sketch, "E9008", {"start": v(-40.86, 13.35) * mm, "end": v(-40.82, 13.37) * mm});
            skLineSegment(sketch, "E9009", {"start": v(-40.82, 13.37) * mm, "end": v(-40.79, 13.4) * mm});
            skLineSegment(sketch, "E9010", {"start": v(-40.79, 13.4) * mm, "end": v(-40.75, 13.42) * mm});
            skLineSegment(sketch, "E9011", {"start": v(-40.75, 13.42) * mm, "end": v(-40.71, 13.44) * mm});
            skLineSegment(sketch, "E9012", {"start": v(-40.71, 13.44) * mm, "end": v(-40.68, 13.47) * mm});
            skLineSegment(sketch, "E9013", {"start": v(-40.68, 13.47) * mm, "end": v(-40.65, 13.5) * mm});
            skLineSegment(sketch, "E9014", {"start": v(-40.65, 13.5) * mm, "end": v(-40.61, 13.52) * mm});
            skLineSegment(sketch, "E9015", {"start": v(-40.58, 13.55) * mm, "end": v(-40.55, 13.58) * mm});
            skLineSegment(sketch, "E9016", {"start": v(-40.55, 13.58) * mm, "end": v(-40.52, 13.62) * mm});
            skLineSegment(sketch, "E9017", {"start": v(-40.52, 13.62) * mm, "end": v(-40.5, 13.65) * mm});
            skLineSegment(sketch, "E9018", {"start": v(-40.5, 13.65) * mm, "end": v(-40.47, 13.68) * mm});
            skLineSegment(sketch, "E9019", {"start": v(-40.47, 13.68) * mm, "end": v(-40.44, 13.72) * mm});
            skLineSegment(sketch, "E9020", {"start": v(-40.44, 13.72) * mm, "end": v(-40.42, 13.76) * mm});
            skLineSegment(sketch, "E9021", {"start": v(-40.42, 13.76) * mm, "end": v(-40.4, 13.8) * mm});
            skLineSegment(sketch, "E9022", {"start": v(-40.4, 13.8) * mm, "end": v(-40.37, 13.83) * mm});
            skLineSegment(sketch, "E9023", {"start": v(-40.37, 13.83) * mm, "end": v(-40.35, 13.87) * mm});
            skLineSegment(sketch, "E9024", {"start": v(-40.35, 13.87) * mm, "end": v(-40.33, 13.9) * mm});
            skLineSegment(sketch, "E9025", {"start": v(-40.33, 13.9) * mm, "end": v(-40.32, 13.95) * mm});
            skLineSegment(sketch, "E9026", {"start": v(-40.32, 13.95) * mm, "end": v(-40.3, 13.99) * mm});
            skLineSegment(sketch, "E9027", {"start": v(-40.3, 13.99) * mm, "end": v(-40.28, 14.03) * mm});
            skLineSegment(sketch, "E9028", {"start": v(-40.28, 14.03) * mm, "end": v(-40.27, 14.07) * mm});
            skLineSegment(sketch, "E9029", {"start": v(-40.27, 14.07) * mm, "end": v(-40.26, 14.1) * mm});
            skLineSegment(sketch, "E9030", {"start": v(-40.26, 14.1) * mm, "end": v(-40.25, 14.15) * mm});
            skLineSegment(sketch, "E9031", {"start": v(-40.25, 14.15) * mm, "end": v(-40.24, 14.2) * mm});
            skLineSegment(sketch, "E9032", {"start": v(-40.24, 14.2) * mm, "end": v(-40.23, 14.24) * mm});
            skLineSegment(sketch, "E9033", {"start": v(-40.23, 14.24) * mm, "end": v(-40.22, 14.28) * mm});
            skLineSegment(sketch, "E9034", {"start": v(-40.22, 14.28) * mm, "end": v(-40.22, 14.32) * mm});
            skLineSegment(sketch, "E9035", {"start": v(-40.22, 14.32) * mm, "end": v(-40.22, 14.37) * mm});
            skLineSegment(sketch, "E9036", {"start": v(-40.22, 14.37) * mm, "end": v(-40.21, 14.4) * mm});
            skLineSegment(sketch, "E9037", {"start": v(-40.21, 14.4) * mm, "end": v(-40.21, 14.45) * mm});
            skLineSegment(sketch, "E9038", {"start": v(-40.21, 14.45) * mm, "end": v(-40.21, 14.5) * mm});
            skLineSegment(sketch, "E9039", {"start": v(-40.21, 14.5) * mm, "end": v(-40.22, 14.54) * mm});
            skLineSegment(sketch, "E9040", {"start": v(-40.22, 14.54) * mm, "end": v(-40.22, 14.58) * mm});
            skLineSegment(sketch, "E9041", {"start": v(-40.22, 14.58) * mm, "end": v(-40.23, 14.63) * mm});
            skLineSegment(sketch, "E9042", {"start": v(-40.23, 14.63) * mm, "end": v(-40.23, 14.67) * mm});
            skLineSegment(sketch, "E9043", {"start": v(-40.23, 14.67) * mm, "end": v(-40.24, 14.71) * mm});
            skLineSegment(sketch, "E9044", {"start": v(-40.24, 14.71) * mm, "end": v(-40.25, 14.75) * mm});
            skLineSegment(sketch, "E9045", {"start": v(-40.25, 14.75) * mm, "end": v(-40.26, 14.8) * mm});
            skLineSegment(sketch, "E9046", {"start": v(-40.26, 14.8) * mm, "end": v(-40.28, 14.84) * mm});
            skLineSegment(sketch, "E9047", {"start": v(-40.28, 14.84) * mm, "end": v(-40.3, 14.88) * mm});
            skLineSegment(sketch, "E9048", {"start": v(-40.3, 14.88) * mm, "end": v(-40.3, 14.92) * mm});
            skLineSegment(sketch, "E9049", {"start": v(-40.3, 14.92) * mm, "end": v(-40.32, 14.96) * mm});
            skLineSegment(sketch, "E9050", {"start": v(-40.32, 14.96) * mm, "end": v(-40.34, 15) * mm});
            skLineSegment(sketch, "E9051", {"start": v(-40.34, 15) * mm, "end": v(-40.36, 15.04) * mm});
            skLineSegment(sketch, "E9052", {"start": v(-40.36, 15.04) * mm, "end": v(-40.38, 15.07) * mm});
            skLineSegment(sketch, "E9053", {"start": v(-40.38, 15.07) * mm, "end": v(-40.4, 15.1) * mm});
            skLineSegment(sketch, "E9054", {"start": v(-40.4, 15.1) * mm, "end": v(-40.43, 15.15) * mm});
            skLineSegment(sketch, "E9055", {"start": v(-40.43, 15.15) * mm, "end": v(-40.46, 15.18) * mm});
            skLineSegment(sketch, "E9056", {"start": v(-40.46, 15.18) * mm, "end": v(-40.48, 15.22) * mm});
            skLineSegment(sketch, "E9057", {"start": v(-40.48, 15.22) * mm, "end": v(-40.5, 15.25) * mm});
            skLineSegment(sketch, "E9058", {"start": v(-40.5, 15.25) * mm, "end": v(-40.54, 15.28) * mm});
            skLineSegment(sketch, "E9059", {"start": v(-40.63, 15.37) * mm, "end": v(-40.66, 15.4) * mm});
            skLineSegment(sketch, "E9060", {"start": v(-40.66, 15.4) * mm, "end": v(-40.7, 15.43) * mm});
            skLineSegment(sketch, "E9061", {"start": v(-40.7, 15.43) * mm, "end": v(-40.73, 15.46) * mm});
            skLineSegment(sketch, "E9062", {"start": v(-40.73, 15.46) * mm, "end": v(-40.77, 15.48) * mm});
            skLineSegment(sketch, "E9063", {"start": v(-40.77, 15.48) * mm, "end": v(-40.8, 15.5) * mm});
            skLineSegment(sketch, "E9064", {"start": v(-40.8, 15.5) * mm, "end": v(-40.84, 15.53) * mm});
            skLineSegment(sketch, "E9065", {"start": v(-40.84, 15.53) * mm, "end": v(-40.88, 15.55) * mm});
            skLineSegment(sketch, "E9066", {"start": v(-40.88, 15.55) * mm, "end": v(-40.92, 15.57) * mm});
            skLineSegment(sketch, "E9067", {"start": v(-40.92, 15.57) * mm, "end": v(-40.96, 15.58) * mm});
            skLineSegment(sketch, "E9068", {"start": v(-40.96, 15.58) * mm, "end": v(-41, 15.6) * mm});
            skLineSegment(sketch, "E9069", {"start": v(-41, 15.6) * mm, "end": v(-41.04, 15.62) * mm});
            skLineSegment(sketch, "E9070", {"start": v(-41.04, 15.62) * mm, "end": v(-41.08, 15.63) * mm});
            skLineSegment(sketch, "E9071", {"start": v(-41.08, 15.63) * mm, "end": v(-41.12, 15.64) * mm});
            skLineSegment(sketch, "E9072", {"start": v(-41.12, 15.64) * mm, "end": v(-41.16, 15.65) * mm});
            skLineSegment(sketch, "E9073", {"start": v(-41.16, 15.65) * mm, "end": v(-41.2, 15.66) * mm});
            skLineSegment(sketch, "E9074", {"start": v(-41.2, 15.66) * mm, "end": v(-41.25, 15.67) * mm});
            skLineSegment(sketch, "E9075", {"start": v(-41.25, 15.67) * mm, "end": v(-41.3, 15.68) * mm});
            skLineSegment(sketch, "E9076", {"start": v(-41.3, 15.68) * mm, "end": v(-41.33, 15.68) * mm});
            skLineSegment(sketch, "E9077", {"start": v(-41.33, 15.68) * mm, "end": v(-41.38, 15.69) * mm});
            skLineSegment(sketch, "E9078", {"start": v(-41.38, 15.69) * mm, "end": v(-41.42, 15.7) * mm});
            skLineSegment(sketch, "E9079", {"start": v(-41.42, 15.7) * mm, "end": v(-41.46, 15.7) * mm});
            skLineSegment(sketch, "E9080", {"start": v(-157.06, 14.64) * mm, "end": v(-157.06, 29.64) * mm});
            skLineSegment(sketch, "E9081", {"start": v(-157.06, 29.64) * mm, "end": v(-292.06, 29.64) * mm});
            skLineSegment(sketch, "E9082", {"start": v(-292.06, 29.64) * mm, "end": v(-292.06, 14.64) * mm});
            skLineSegment(sketch, "E9083", {"start": v(-292.06, 14.64) * mm, "end": v(-157.06, 14.64) * mm});
            skLineSegment(sketch, "E9084", {"start": v(92.66, 34.97) * mm, "end": v(92.58, 34.97) * mm});
            skLineSegment(sketch, "E9085", {"start": v(92.58, 34.97) * mm, "end": v(92.5, 34.97) * mm});
            skLineSegment(sketch, "E9086", {"start": v(92.5, 34.97) * mm, "end": v(92.43, 34.96) * mm});
            skLineSegment(sketch, "E9087", {"start": v(92.43, 34.96) * mm, "end": v(92.36, 34.95) * mm});
            skLineSegment(sketch, "E9088", {"start": v(92.36, 34.95) * mm, "end": v(92.28, 34.94) * mm});
            skLineSegment(sketch, "E9089", {"start": v(92.28, 34.94) * mm, "end": v(92.21, 34.93) * mm});
            skLineSegment(sketch, "E9090", {"start": v(92.21, 34.93) * mm, "end": v(92.14, 34.91) * mm});
            skLineSegment(sketch, "E9091", {"start": v(92.14, 34.91) * mm, "end": v(92.07, 34.9) * mm});
            skLineSegment(sketch, "E9092", {"start": v(92.07, 34.9) * mm, "end": v(92, 34.87) * mm});
            skLineSegment(sketch, "E9093", {"start": v(92, 34.87) * mm, "end": v(91.92, 34.85) * mm});
            skLineSegment(sketch, "E9094", {"start": v(91.92, 34.85) * mm, "end": v(91.85, 34.82) * mm});
            skLineSegment(sketch, "E9095", {"start": v(91.85, 34.82) * mm, "end": v(91.79, 34.8) * mm});
            skLineSegment(sketch, "E9096", {"start": v(91.79, 34.8) * mm, "end": v(91.72, 34.76) * mm});
            skLineSegment(sketch, "E9097", {"start": v(91.72, 34.76) * mm, "end": v(91.65, 34.73) * mm});
            skLineSegment(sketch, "E9098", {"start": v(91.65, 34.73) * mm, "end": v(91.59, 34.69) * mm});
            skLineSegment(sketch, "E9099", {"start": v(91.59, 34.69) * mm, "end": v(91.52, 34.65) * mm});
            skLineSegment(sketch, "E9100", {"start": v(91.52, 34.65) * mm, "end": v(91.46, 34.61) * mm});
            skLineSegment(sketch, "E9101", {"start": v(91.46, 34.61) * mm, "end": v(91.4, 34.57) * mm});
            skLineSegment(sketch, "E9102", {"start": v(91.4, 34.57) * mm, "end": v(91.34, 34.52) * mm});
            skLineSegment(sketch, "E9103", {"start": v(91.34, 34.52) * mm, "end": v(91.28, 34.48) * mm});
            skLineSegment(sketch, "E9104", {"start": v(91.28, 34.48) * mm, "end": v(91.22, 34.43) * mm});
            skLineSegment(sketch, "E9105", {"start": v(91.22, 34.43) * mm, "end": v(91.17, 34.38) * mm});
            skLineSegment(sketch, "E9106", {"start": v(91.17, 34.38) * mm, "end": v(91.12, 34.32) * mm});
            skLineSegment(sketch, "E9107", {"start": v(91.12, 34.32) * mm, "end": v(91.06, 34.27) * mm});
            skLineSegment(sketch, "E9108", {"start": v(91.06, 34.27) * mm, "end": v(91.02, 34.21) * mm});
            skLineSegment(sketch, "E9109", {"start": v(91.02, 34.21) * mm, "end": v(90.97, 34.16) * mm});
            skLineSegment(sketch, "E9110", {"start": v(90.97, 34.16) * mm, "end": v(90.92, 34.1) * mm});
            skLineSegment(sketch, "E9111", {"start": v(90.92, 34.1) * mm, "end": v(90.88, 34.04) * mm});
            skLineSegment(sketch, "E9112", {"start": v(90.73, 33.78) * mm, "end": v(90.7, 33.71) * mm});
            skLineSegment(sketch, "E9113", {"start": v(90.7, 33.71) * mm, "end": v(90.67, 33.64) * mm});
            skLineSegment(sketch, "E9114", {"start": v(90.67, 33.64) * mm, "end": v(90.64, 33.57) * mm});
            skLineSegment(sketch, "E9115", {"start": v(90.64, 33.57) * mm, "end": v(90.62, 33.5) * mm});
            skLineSegment(sketch, "E9116", {"start": v(90.62, 33.5) * mm, "end": v(90.6, 33.43) * mm});
            skLineSegment(sketch, "E9117", {"start": v(90.57, 33.36) * mm, "end": v(90.56, 33.29) * mm});
            skLineSegment(sketch, "E9118", {"start": v(90.56, 33.29) * mm, "end": v(90.54, 33.21) * mm});
            skLineSegment(sketch, "E9119", {"start": v(90.54, 33.21) * mm, "end": v(90.53, 33.14) * mm});
            skLineSegment(sketch, "E9120", {"start": v(90.53, 33.14) * mm, "end": v(90.52, 33.07) * mm});
            skLineSegment(sketch, "E9121", {"start": v(90.52, 33.07) * mm, "end": v(90.51, 33) * mm});
            skLineSegment(sketch, "E9122", {"start": v(90.51, 33) * mm, "end": v(90.5, 32.92) * mm});
            skLineSegment(sketch, "E9123", {"start": v(90.5, 32.92) * mm, "end": v(90.5, 32.84) * mm});
            skLineSegment(sketch, "E9124", {"start": v(90.5, 32.84) * mm, "end": v(90.5, 32.77) * mm});
            skLineSegment(sketch, "E9125", {"start": v(90.5, 32.77) * mm, "end": v(90.5, 32.7) * mm});
            skLineSegment(sketch, "E9126", {"start": v(90.5, 32.7) * mm, "end": v(90.52, 32.62) * mm});
            skLineSegment(sketch, "E9127", {"start": v(90.52, 32.62) * mm, "end": v(90.52, 32.55) * mm});
            skLineSegment(sketch, "E9128", {"start": v(90.52, 32.55) * mm, "end": v(90.53, 32.47) * mm});
            skLineSegment(sketch, "E9129", {"start": v(90.53, 32.47) * mm, "end": v(90.55, 32.4) * mm});
            skLineSegment(sketch, "E9130", {"start": v(90.55, 32.4) * mm, "end": v(90.56, 32.32) * mm});
            skLineSegment(sketch, "E9131", {"start": v(90.58, 32.25) * mm, "end": v(90.6, 32.18) * mm});
            skLineSegment(sketch, "E9132", {"start": v(90.6, 32.18) * mm, "end": v(90.63, 32.11) * mm});
            skLineSegment(sketch, "E9133", {"start": v(90.63, 32.11) * mm, "end": v(90.65, 32.04) * mm});
            skLineSegment(sketch, "E9134", {"start": v(90.65, 32.04) * mm, "end": v(90.68, 31.97) * mm});
            skLineSegment(sketch, "E9135", {"start": v(90.68, 31.97) * mm, "end": v(90.71, 31.9) * mm});
            skLineSegment(sketch, "E9136", {"start": v(90.86, 31.64) * mm, "end": v(90.9, 31.58) * mm});
            skLineSegment(sketch, "E9137", {"start": v(90.9, 31.58) * mm, "end": v(90.94, 31.52) * mm});
            skLineSegment(sketch, "E9138", {"start": v(90.94, 31.52) * mm, "end": v(91, 31.46) * mm});
            skLineSegment(sketch, "E9139", {"start": v(91, 31.46) * mm, "end": v(91.04, 31.4) * mm});
            skLineSegment(sketch, "E9140", {"start": v(91.04, 31.4) * mm, "end": v(91.09, 31.35) * mm});
            skLineSegment(sketch, "E9141", {"start": v(91.09, 31.35) * mm, "end": v(91.14, 31.3) * mm});
            skLineSegment(sketch, "E9142", {"start": v(91.14, 31.3) * mm, "end": v(91.2, 31.25) * mm});
            skLineSegment(sketch, "E9143", {"start": v(91.2, 31.25) * mm, "end": v(91.25, 31.2) * mm});
            skLineSegment(sketch, "E9144", {"start": v(91.25, 31.2) * mm, "end": v(91.3, 31.15) * mm});
            skLineSegment(sketch, "E9145", {"start": v(91.3, 31.15) * mm, "end": v(91.37, 31.1) * mm});
            skLineSegment(sketch, "E9146", {"start": v(91.37, 31.1) * mm, "end": v(91.43, 31.06) * mm});
            skLineSegment(sketch, "E9147", {"start": v(91.43, 31.06) * mm, "end": v(91.5, 31.02) * mm});
            skLineSegment(sketch, "E9148", {"start": v(91.5, 31.02) * mm, "end": v(91.55, 30.98) * mm});
            skLineSegment(sketch, "E9149", {"start": v(91.62, 30.94) * mm, "end": v(91.68, 30.9) * mm});
            skLineSegment(sketch, "E9150", {"start": v(91.68, 30.9) * mm, "end": v(91.75, 30.87) * mm});
            skLineSegment(sketch, "E9151", {"start": v(91.75, 30.87) * mm, "end": v(91.82, 30.84) * mm});
            skLineSegment(sketch, "E9152", {"start": v(91.82, 30.84) * mm, "end": v(91.89, 30.82) * mm});
            skLineSegment(sketch, "E9153", {"start": v(91.89, 30.82) * mm, "end": v(91.96, 30.79) * mm});
            skLineSegment(sketch, "E9154", {"start": v(91.96, 30.79) * mm, "end": v(92.03, 30.77) * mm});
            skLineSegment(sketch, "E9155", {"start": v(92.03, 30.77) * mm, "end": v(92.1, 30.75) * mm});
            skLineSegment(sketch, "E9156", {"start": v(92.1, 30.75) * mm, "end": v(92.17, 30.73) * mm});
            skLineSegment(sketch, "E9157", {"start": v(92.17, 30.73) * mm, "end": v(92.25, 30.71) * mm});
            skLineSegment(sketch, "E9158", {"start": v(92.25, 30.71) * mm, "end": v(92.32, 30.7) * mm});
            skLineSegment(sketch, "E9159", {"start": v(92.32, 30.7) * mm, "end": v(92.4, 30.69) * mm});
            skLineSegment(sketch, "E9160", {"start": v(92.4, 30.69) * mm, "end": v(92.47, 30.68) * mm});
            skLineSegment(sketch, "E9161", {"start": v(92.47, 30.68) * mm, "end": v(92.54, 30.68) * mm});
            skLineSegment(sketch, "E9162", {"start": v(92.54, 30.68) * mm, "end": v(92.62, 30.67) * mm});
            skLineSegment(sketch, "E9163", {"start": v(92.62, 30.67) * mm, "end": v(92.7, 30.67) * mm});
            skLineSegment(sketch, "E9164", {"start": v(92.7, 30.67) * mm, "end": v(92.77, 30.68) * mm});
            skLineSegment(sketch, "E9165", {"start": v(92.77, 30.68) * mm, "end": v(92.84, 30.68) * mm});
            skLineSegment(sketch, "E9166", {"start": v(92.84, 30.68) * mm, "end": v(92.92, 30.69) * mm});
            skLineSegment(sketch, "E9167", {"start": v(92.92, 30.69) * mm, "end": v(92.99, 30.7) * mm});
            skLineSegment(sketch, "E9168", {"start": v(92.99, 30.7) * mm, "end": v(93.06, 30.71) * mm});
            skLineSegment(sketch, "E9169", {"start": v(93.06, 30.71) * mm, "end": v(93.14, 30.73) * mm});
            skLineSegment(sketch, "E9170", {"start": v(93.28, 30.77) * mm, "end": v(93.35, 30.79) * mm});
            skLineSegment(sketch, "E9171", {"start": v(93.35, 30.79) * mm, "end": v(93.42, 30.82) * mm});
            skLineSegment(sketch, "E9172", {"start": v(93.42, 30.82) * mm, "end": v(93.5, 30.84) * mm});
            skLineSegment(sketch, "E9173", {"start": v(93.5, 30.84) * mm, "end": v(93.56, 30.87) * mm});
            skLineSegment(sketch, "E9174", {"start": v(93.56, 30.87) * mm, "end": v(93.63, 30.9) * mm});
            skLineSegment(sketch, "E9175", {"start": v(93.63, 30.9) * mm, "end": v(93.7, 30.94) * mm});
            skLineSegment(sketch, "E9176", {"start": v(93.7, 30.94) * mm, "end": v(93.76, 30.98) * mm});
            skLineSegment(sketch, "E9177", {"start": v(93.76, 30.98) * mm, "end": v(93.82, 31.02) * mm});
            skLineSegment(sketch, "E9178", {"start": v(93.82, 31.02) * mm, "end": v(93.88, 31.06) * mm});
            skLineSegment(sketch, "E9179", {"start": v(93.88, 31.06) * mm, "end": v(93.94, 31.1) * mm});
            skLineSegment(sketch, "E9180", {"start": v(93.94, 31.1) * mm, "end": v(94, 31.15) * mm});
            skLineSegment(sketch, "E9181", {"start": v(94, 31.15) * mm, "end": v(94.06, 31.2) * mm});
            skLineSegment(sketch, "E9182", {"start": v(94.06, 31.2) * mm, "end": v(94.12, 31.25) * mm});
            skLineSegment(sketch, "E9183", {"start": v(94.12, 31.25) * mm, "end": v(94.17, 31.3) * mm});
            skLineSegment(sketch, "E9184", {"start": v(94.17, 31.3) * mm, "end": v(94.22, 31.35) * mm});
            skLineSegment(sketch, "E9185", {"start": v(94.22, 31.35) * mm, "end": v(94.27, 31.4) * mm});
            skLineSegment(sketch, "E9186", {"start": v(94.27, 31.4) * mm, "end": v(94.32, 31.46) * mm});
            skLineSegment(sketch, "E9187", {"start": v(94.32, 31.46) * mm, "end": v(94.37, 31.52) * mm});
            skLineSegment(sketch, "E9188", {"start": v(94.37, 31.52) * mm, "end": v(94.41, 31.58) * mm});
            skLineSegment(sketch, "E9189", {"start": v(94.41, 31.58) * mm, "end": v(94.45, 31.64) * mm});
            skLineSegment(sketch, "E9190", {"start": v(94.45, 31.64) * mm, "end": v(94.5, 31.7) * mm});
            skLineSegment(sketch, "E9191", {"start": v(94.5, 31.7) * mm, "end": v(94.53, 31.77) * mm});
            skLineSegment(sketch, "E9192", {"start": v(94.53, 31.77) * mm, "end": v(94.57, 31.84) * mm});
            skLineSegment(sketch, "E9193", {"start": v(94.57, 31.84) * mm, "end": v(94.6, 31.9) * mm});
            skLineSegment(sketch, "E9194", {"start": v(94.63, 31.97) * mm, "end": v(94.66, 32.04) * mm});
            skLineSegment(sketch, "E9195", {"start": v(94.66, 32.04) * mm, "end": v(94.68, 32.11) * mm});
            skLineSegment(sketch, "E9196", {"start": v(94.68, 32.11) * mm, "end": v(94.7, 32.18) * mm});
            skLineSegment(sketch, "E9197", {"start": v(94.7, 32.18) * mm, "end": v(94.73, 32.25) * mm});
            skLineSegment(sketch, "E9198", {"start": v(94.73, 32.25) * mm, "end": v(94.75, 32.32) * mm});
            skLineSegment(sketch, "E9199", {"start": v(94.75, 32.32) * mm, "end": v(94.76, 32.4) * mm});
            skLineSegment(sketch, "E9200", {"start": v(94.76, 32.4) * mm, "end": v(94.78, 32.47) * mm});
            skLineSegment(sketch, "E9201", {"start": v(94.78, 32.47) * mm, "end": v(94.79, 32.55) * mm});
            skLineSegment(sketch, "E9202", {"start": v(94.79, 32.55) * mm, "end": v(94.8, 32.62) * mm});
            skLineSegment(sketch, "E9203", {"start": v(94.8, 32.62) * mm, "end": v(94.8, 32.7) * mm});
            skLineSegment(sketch, "E9204", {"start": v(94.8, 32.7) * mm, "end": v(94.8, 32.77) * mm});
            skLineSegment(sketch, "E9205", {"start": v(94.8, 32.77) * mm, "end": v(94.8, 32.84) * mm});
            skLineSegment(sketch, "E9206", {"start": v(94.8, 32.84) * mm, "end": v(94.8, 32.92) * mm});
            skLineSegment(sketch, "E9207", {"start": v(94.8, 32.92) * mm, "end": v(94.8, 33) * mm});
            skLineSegment(sketch, "E9208", {"start": v(94.8, 33) * mm, "end": v(94.8, 33.07) * mm});
            skLineSegment(sketch, "E9209", {"start": v(94.8, 33.07) * mm, "end": v(94.78, 33.14) * mm});
            skLineSegment(sketch, "E9210", {"start": v(94.78, 33.14) * mm, "end": v(94.77, 33.21) * mm});
            skLineSegment(sketch, "E9211", {"start": v(94.77, 33.21) * mm, "end": v(94.76, 33.29) * mm});
            skLineSegment(sketch, "E9212", {"start": v(94.76, 33.29) * mm, "end": v(94.74, 33.36) * mm});
            skLineSegment(sketch, "E9213", {"start": v(94.74, 33.36) * mm, "end": v(94.72, 33.43) * mm});
            skLineSegment(sketch, "E9214", {"start": v(94.72, 33.43) * mm, "end": v(94.7, 33.5) * mm});
            skLineSegment(sketch, "E9215", {"start": v(94.7, 33.5) * mm, "end": v(94.67, 33.57) * mm});
            skLineSegment(sketch, "E9216", {"start": v(94.67, 33.57) * mm, "end": v(94.64, 33.64) * mm});
            skLineSegment(sketch, "E9217", {"start": v(94.61, 33.71) * mm, "end": v(94.58, 33.78) * mm});
            skLineSegment(sketch, "E9218", {"start": v(94.58, 33.78) * mm, "end": v(94.55, 33.84) * mm});
            skLineSegment(sketch, "E9219", {"start": v(94.55, 33.84) * mm, "end": v(94.51, 33.9) * mm});
            skLineSegment(sketch, "E9220", {"start": v(94.51, 33.9) * mm, "end": v(94.47, 33.97) * mm});
            skLineSegment(sketch, "E9221", {"start": v(94.47, 33.97) * mm, "end": v(94.43, 34.04) * mm});
            skLineSegment(sketch, "E9222", {"start": v(94.43, 34.04) * mm, "end": v(94.39, 34.1) * mm});
            skLineSegment(sketch, "E9223", {"start": v(94.39, 34.1) * mm, "end": v(94.34, 34.16) * mm});
            skLineSegment(sketch, "E9224", {"start": v(94.34, 34.16) * mm, "end": v(94.3, 34.21) * mm});
            skLineSegment(sketch, "E9225", {"start": v(94.3, 34.21) * mm, "end": v(94.25, 34.27) * mm});
            skLineSegment(sketch, "E9226", {"start": v(94.25, 34.27) * mm, "end": v(94.2, 34.32) * mm});
            skLineSegment(sketch, "E9227", {"start": v(94.2, 34.32) * mm, "end": v(94.14, 34.38) * mm});
            skLineSegment(sketch, "E9228", {"start": v(94.14, 34.38) * mm, "end": v(94.09, 34.43) * mm});
            skLineSegment(sketch, "E9229", {"start": v(94.09, 34.43) * mm, "end": v(94.03, 34.48) * mm});
            skLineSegment(sketch, "E9230", {"start": v(94.03, 34.48) * mm, "end": v(93.97, 34.52) * mm});
            skLineSegment(sketch, "E9231", {"start": v(93.91, 34.57) * mm, "end": v(93.85, 34.61) * mm});
            skLineSegment(sketch, "E9232", {"start": v(93.85, 34.61) * mm, "end": v(93.79, 34.65) * mm});
            skLineSegment(sketch, "E9233", {"start": v(93.79, 34.65) * mm, "end": v(93.73, 34.69) * mm});
            skLineSegment(sketch, "E9234", {"start": v(93.73, 34.69) * mm, "end": v(93.66, 34.73) * mm});
            skLineSegment(sketch, "E9235", {"start": v(93.66, 34.73) * mm, "end": v(93.6, 34.76) * mm});
            skLineSegment(sketch, "E9236", {"start": v(93.6, 34.76) * mm, "end": v(93.53, 34.8) * mm});
            skLineSegment(sketch, "E9237", {"start": v(93.53, 34.8) * mm, "end": v(93.46, 34.82) * mm});
            skLineSegment(sketch, "E9238", {"start": v(93.46, 34.82) * mm, "end": v(93.39, 34.85) * mm});
            skLineSegment(sketch, "E9239", {"start": v(93.39, 34.85) * mm, "end": v(93.32, 34.87) * mm});
            skLineSegment(sketch, "E9240", {"start": v(93.32, 34.87) * mm, "end": v(93.24, 34.9) * mm});
            skLineSegment(sketch, "E9241", {"start": v(93.1, 34.93) * mm, "end": v(93.03, 34.94) * mm});
            skLineSegment(sketch, "E9242", {"start": v(93.03, 34.94) * mm, "end": v(92.95, 34.95) * mm});
            skLineSegment(sketch, "E9243", {"start": v(92.95, 34.95) * mm, "end": v(92.88, 34.96) * mm});
            skLineSegment(sketch, "E9244", {"start": v(92.8, 34.97) * mm, "end": v(92.73, 34.97) * mm});
            skLineSegment(sketch, "E9245", {"start": v(92.73, 34.97) * mm, "end": v(92.66, 34.97) * mm});
            skLineSegment(sketch, "E9246", {"start": v(-17.34, 34.97) * mm, "end": v(-17.42, 34.97) * mm});
            skLineSegment(sketch, "E9247", {"start": v(-17.42, 34.97) * mm, "end": v(-17.5, 34.97) * mm});
            skLineSegment(sketch, "E9248", {"start": v(-17.5, 34.97) * mm, "end": v(-17.57, 34.96) * mm});
            skLineSegment(sketch, "E9249", {"start": v(-17.57, 34.96) * mm, "end": v(-17.64, 34.95) * mm});
            skLineSegment(sketch, "E9250", {"start": v(-17.64, 34.95) * mm, "end": v(-17.72, 34.94) * mm});
            skLineSegment(sketch, "E9251", {"start": v(-17.72, 34.94) * mm, "end": v(-17.79, 34.93) * mm});
            skLineSegment(sketch, "E9252", {"start": v(-17.79, 34.93) * mm, "end": v(-17.86, 34.91) * mm});
            skLineSegment(sketch, "E9253", {"start": v(-17.86, 34.91) * mm, "end": v(-17.93, 34.9) * mm});
            skLineSegment(sketch, "E9254", {"start": v(-17.93, 34.9) * mm, "end": v(-18, 34.87) * mm});
            skLineSegment(sketch, "E9255", {"start": v(-18, 34.87) * mm, "end": v(-18.08, 34.85) * mm});
            skLineSegment(sketch, "E9256", {"start": v(-18.08, 34.85) * mm, "end": v(-18.15, 34.82) * mm});
            skLineSegment(sketch, "E9257", {"start": v(-18.15, 34.82) * mm, "end": v(-18.21, 34.8) * mm});
            skLineSegment(sketch, "E9258", {"start": v(-18.21, 34.8) * mm, "end": v(-18.28, 34.76) * mm});
            skLineSegment(sketch, "E9259", {"start": v(-18.41, 34.69) * mm, "end": v(-18.48, 34.65) * mm});
            skLineSegment(sketch, "E9260", {"start": v(-18.48, 34.65) * mm, "end": v(-18.54, 34.61) * mm});
            skLineSegment(sketch, "E9261", {"start": v(-18.54, 34.61) * mm, "end": v(-18.6, 34.57) * mm});
            skLineSegment(sketch, "E9262", {"start": v(-18.6, 34.57) * mm, "end": v(-18.66, 34.52) * mm});
            skLineSegment(sketch, "E9263", {"start": v(-18.66, 34.52) * mm, "end": v(-18.72, 34.48) * mm});
            skLineSegment(sketch, "E9264", {"start": v(-18.72, 34.48) * mm, "end": v(-18.78, 34.43) * mm});
            skLineSegment(sketch, "E9265", {"start": v(-18.78, 34.43) * mm, "end": v(-18.83, 34.38) * mm});
            skLineSegment(sketch, "E9266", {"start": v(-18.83, 34.38) * mm, "end": v(-18.88, 34.32) * mm});
            skLineSegment(sketch, "E9267", {"start": v(-18.88, 34.32) * mm, "end": v(-18.94, 34.27) * mm});
            skLineSegment(sketch, "E9268", {"start": v(-18.94, 34.27) * mm, "end": v(-18.98, 34.21) * mm});
            skLineSegment(sketch, "E9269", {"start": v(-18.98, 34.21) * mm, "end": v(-19.03, 34.16) * mm});
            skLineSegment(sketch, "E9270", {"start": v(-19.03, 34.16) * mm, "end": v(-19.08, 34.1) * mm});
            skLineSegment(sketch, "E9271", {"start": v(-19.08, 34.1) * mm, "end": v(-19.12, 34.04) * mm});
            skLineSegment(sketch, "E9272", {"start": v(-19.12, 34.04) * mm, "end": v(-19.16, 33.97) * mm});
            skLineSegment(sketch, "E9273", {"start": v(-19.16, 33.97) * mm, "end": v(-19.2, 33.9) * mm});
            skLineSegment(sketch, "E9274", {"start": v(-19.2, 33.9) * mm, "end": v(-19.24, 33.84) * mm});
            skLineSegment(sketch, "E9275", {"start": v(-19.24, 33.84) * mm, "end": v(-19.27, 33.78) * mm});
            skLineSegment(sketch, "E9276", {"start": v(-19.27, 33.78) * mm, "end": v(-19.3, 33.71) * mm});
            skLineSegment(sketch, "E9277", {"start": v(-19.3, 33.71) * mm, "end": v(-19.33, 33.64) * mm});
            skLineSegment(sketch, "E9278", {"start": v(-19.36, 33.57) * mm, "end": v(-19.38, 33.5) * mm});
            skLineSegment(sketch, "E9279", {"start": v(-19.38, 33.5) * mm, "end": v(-19.4, 33.43) * mm});
            skLineSegment(sketch, "E9280", {"start": v(-19.4, 33.43) * mm, "end": v(-19.43, 33.36) * mm});
            skLineSegment(sketch, "E9281", {"start": v(-19.43, 33.36) * mm, "end": v(-19.44, 33.29) * mm});
            skLineSegment(sketch, "E9282", {"start": v(-19.44, 33.29) * mm, "end": v(-19.46, 33.21) * mm});
            skLineSegment(sketch, "E9283", {"start": v(-19.46, 33.21) * mm, "end": v(-19.47, 33.14) * mm});
            skLineSegment(sketch, "E9284", {"start": v(-19.47, 33.14) * mm, "end": v(-19.48, 33.07) * mm});
            skLineSegment(sketch, "E9285", {"start": v(-19.48, 33.07) * mm, "end": v(-19.49, 33) * mm});
            skLineSegment(sketch, "E9286", {"start": v(-19.49, 33) * mm, "end": v(-19.5, 32.92) * mm});
            skLineSegment(sketch, "E9287", {"start": v(-19.5, 32.92) * mm, "end": v(-19.5, 32.84) * mm});
            skLineSegment(sketch, "E9288", {"start": v(-19.5, 32.84) * mm, "end": v(-19.5, 32.77) * mm});
            skLineSegment(sketch, "E9289", {"start": v(-19.5, 32.77) * mm, "end": v(-19.5, 32.7) * mm});
            skLineSegment(sketch, "E9290", {"start": v(-19.5, 32.7) * mm, "end": v(-19.48, 32.62) * mm});
            skLineSegment(sketch, "E9291", {"start": v(-19.48, 32.62) * mm, "end": v(-19.48, 32.55) * mm});
            skLineSegment(sketch, "E9292", {"start": v(-19.48, 32.55) * mm, "end": v(-19.47, 32.47) * mm});
            skLineSegment(sketch, "E9293", {"start": v(-19.47, 32.47) * mm, "end": v(-19.45, 32.4) * mm});
            skLineSegment(sketch, "E9294", {"start": v(-19.45, 32.4) * mm, "end": v(-19.44, 32.32) * mm});
            skLineSegment(sketch, "E9295", {"start": v(-19.44, 32.32) * mm, "end": v(-19.42, 32.25) * mm});
            skLineSegment(sketch, "E9296", {"start": v(-19.42, 32.25) * mm, "end": v(-19.4, 32.18) * mm});
            skLineSegment(sketch, "E9297", {"start": v(-19.4, 32.18) * mm, "end": v(-19.37, 32.11) * mm});
            skLineSegment(sketch, "E9298", {"start": v(-19.37, 32.11) * mm, "end": v(-19.35, 32.04) * mm});
            skLineSegment(sketch, "E9299", {"start": v(-19.35, 32.04) * mm, "end": v(-19.32, 31.97) * mm});
            skLineSegment(sketch, "E9300", {"start": v(-19.32, 31.97) * mm, "end": v(-19.29, 31.9) * mm});
            skLineSegment(sketch, "E9301", {"start": v(-19.29, 31.9) * mm, "end": v(-19.25, 31.84) * mm});
            skLineSegment(sketch, "E9302", {"start": v(-19.25, 31.84) * mm, "end": v(-19.22, 31.77) * mm});
            skLineSegment(sketch, "E9303", {"start": v(-19.22, 31.77) * mm, "end": v(-19.18, 31.7) * mm});
            skLineSegment(sketch, "E9304", {"start": v(-19.18, 31.7) * mm, "end": v(-19.14, 31.64) * mm});
            skLineSegment(sketch, "E9305", {"start": v(-19.14, 31.64) * mm, "end": v(-19.1, 31.58) * mm});
            skLineSegment(sketch, "E9306", {"start": v(-19.1, 31.58) * mm, "end": v(-19.06, 31.52) * mm});
            skLineSegment(sketch, "E9307", {"start": v(-19.06, 31.52) * mm, "end": v(-19, 31.46) * mm});
            skLineSegment(sketch, "E9308", {"start": v(-19, 31.46) * mm, "end": v(-18.96, 31.4) * mm});
            skLineSegment(sketch, "E9309", {"start": v(-18.96, 31.4) * mm, "end": v(-18.91, 31.35) * mm});
            skLineSegment(sketch, "E9310", {"start": v(-18.91, 31.35) * mm, "end": v(-18.86, 31.3) * mm});
            skLineSegment(sketch, "E9311", {"start": v(-18.86, 31.3) * mm, "end": v(-18.8, 31.25) * mm});
            skLineSegment(sketch, "E9312", {"start": v(-18.8, 31.25) * mm, "end": v(-18.75, 31.2) * mm});
            skLineSegment(sketch, "E9313", {"start": v(-18.75, 31.2) * mm, "end": v(-18.7, 31.15) * mm});
            skLineSegment(sketch, "E9314", {"start": v(-18.7, 31.15) * mm, "end": v(-18.63, 31.1) * mm});
            skLineSegment(sketch, "E9315", {"start": v(-18.63, 31.1) * mm, "end": v(-18.57, 31.06) * mm});
            skLineSegment(sketch, "E9316", {"start": v(-18.57, 31.06) * mm, "end": v(-18.5, 31.02) * mm});
            skLineSegment(sketch, "E9317", {"start": v(-18.5, 31.02) * mm, "end": v(-18.45, 30.98) * mm});
            skLineSegment(sketch, "E9318", {"start": v(-18.32, 30.9) * mm, "end": v(-18.25, 30.87) * mm});
            skLineSegment(sketch, "E9319", {"start": v(-18.25, 30.87) * mm, "end": v(-18.18, 30.84) * mm});
            skLineSegment(sketch, "E9320", {"start": v(-18.18, 30.84) * mm, "end": v(-18.11, 30.82) * mm});
            skLineSegment(sketch, "E9321", {"start": v(-18.11, 30.82) * mm, "end": v(-18.04, 30.79) * mm});
            skLineSegment(sketch, "E9322", {"start": v(-18.04, 30.79) * mm, "end": v(-17.97, 30.77) * mm});
            skLineSegment(sketch, "E9323", {"start": v(-17.97, 30.77) * mm, "end": v(-17.9, 30.75) * mm});
            skLineSegment(sketch, "E9324", {"start": v(-17.9, 30.75) * mm, "end": v(-17.83, 30.73) * mm});
            skLineSegment(sketch, "E9325", {"start": v(-17.83, 30.73) * mm, "end": v(-17.75, 30.71) * mm});
            skLineSegment(sketch, "E9326", {"start": v(-17.68, 30.7) * mm, "end": v(-17.6, 30.69) * mm});
            skLineSegment(sketch, "E9327", {"start": v(-17.6, 30.69) * mm, "end": v(-17.53, 30.68) * mm});
            skLineSegment(sketch, "E9328", {"start": v(-17.53, 30.68) * mm, "end": v(-17.46, 30.68) * mm});
            skLineSegment(sketch, "E9329", {"start": v(-17.46, 30.68) * mm, "end": v(-17.38, 30.67) * mm});
            skLineSegment(sketch, "E9330", {"start": v(-17.38, 30.67) * mm, "end": v(-17.3, 30.67) * mm});
            skLineSegment(sketch, "E9331", {"start": v(-17.3, 30.67) * mm, "end": v(-17.23, 30.68) * mm});
            skLineSegment(sketch, "E9332", {"start": v(-17.23, 30.68) * mm, "end": v(-17.16, 30.68) * mm});
            skLineSegment(sketch, "E9333", {"start": v(-17.16, 30.68) * mm, "end": v(-17.08, 30.69) * mm});
            skLineSegment(sketch, "E9334", {"start": v(-17.08, 30.69) * mm, "end": v(-17.01, 30.7) * mm});
            skLineSegment(sketch, "E9335", {"start": v(-17.01, 30.7) * mm, "end": v(-16.94, 30.71) * mm});
            skLineSegment(sketch, "E9336", {"start": v(-16.94, 30.71) * mm, "end": v(-16.86, 30.73) * mm});
            skLineSegment(sketch, "E9337", {"start": v(-16.86, 30.73) * mm, "end": v(-16.8, 30.75) * mm});
            skLineSegment(sketch, "E9338", {"start": v(-16.8, 30.75) * mm, "end": v(-16.72, 30.77) * mm});
            skLineSegment(sketch, "E9339", {"start": v(-16.72, 30.77) * mm, "end": v(-16.65, 30.79) * mm});
            skLineSegment(sketch, "E9340", {"start": v(-16.65, 30.79) * mm, "end": v(-16.58, 30.82) * mm});
            skLineSegment(sketch, "E9341", {"start": v(-16.58, 30.82) * mm, "end": v(-16.5, 30.84) * mm});
            skLineSegment(sketch, "E9342", {"start": v(-16.5, 30.84) * mm, "end": v(-16.44, 30.87) * mm});
            skLineSegment(sketch, "E9343", {"start": v(-16.37, 30.9) * mm, "end": v(-16.3, 30.94) * mm});
            skLineSegment(sketch, "E9344", {"start": v(-16.3, 30.94) * mm, "end": v(-16.24, 30.98) * mm});
            skLineSegment(sketch, "E9345", {"start": v(-16.24, 30.98) * mm, "end": v(-16.18, 31.02) * mm});
            skLineSegment(sketch, "E9346", {"start": v(-16.18, 31.02) * mm, "end": v(-16.12, 31.06) * mm});
            skLineSegment(sketch, "E9347", {"start": v(-16.12, 31.06) * mm, "end": v(-16.06, 31.1) * mm});
            skLineSegment(sketch, "E9348", {"start": v(-16.06, 31.1) * mm, "end": v(-16, 31.15) * mm});
            skLineSegment(sketch, "E9349", {"start": v(-16, 31.15) * mm, "end": v(-15.94, 31.2) * mm});
            skLineSegment(sketch, "E9350", {"start": v(-15.94, 31.2) * mm, "end": v(-15.88, 31.25) * mm});
            skLineSegment(sketch, "E9351", {"start": v(-15.88, 31.25) * mm, "end": v(-15.83, 31.3) * mm});
            skLineSegment(sketch, "E9352", {"start": v(-15.83, 31.3) * mm, "end": v(-15.78, 31.35) * mm});
            skLineSegment(sketch, "E9353", {"start": v(-15.78, 31.35) * mm, "end": v(-15.73, 31.4) * mm});
            skLineSegment(sketch, "E9354", {"start": v(-15.73, 31.4) * mm, "end": v(-15.68, 31.46) * mm});
            skLineSegment(sketch, "E9355", {"start": v(-15.68, 31.46) * mm, "end": v(-15.63, 31.52) * mm});
            skLineSegment(sketch, "E9356", {"start": v(-15.63, 31.52) * mm, "end": v(-15.59, 31.58) * mm});
            skLineSegment(sketch, "E9357", {"start": v(-15.55, 31.64) * mm, "end": v(-15.5, 31.7) * mm});
            skLineSegment(sketch, "E9358", {"start": v(-15.5, 31.7) * mm, "end": v(-15.47, 31.77) * mm});
            skLineSegment(sketch, "E9359", {"start": v(-15.47, 31.77) * mm, "end": v(-15.43, 31.84) * mm});
            skLineSegment(sketch, "E9360", {"start": v(-15.43, 31.84) * mm, "end": v(-15.4, 31.9) * mm});
            skLineSegment(sketch, "E9361", {"start": v(-15.4, 31.9) * mm, "end": v(-15.37, 31.97) * mm});
            skLineSegment(sketch, "E9362", {"start": v(-15.37, 31.97) * mm, "end": v(-15.34, 32.04) * mm});
            skLineSegment(sketch, "E9363", {"start": v(-15.34, 32.04) * mm, "end": v(-15.32, 32.11) * mm});
            skLineSegment(sketch, "E9364", {"start": v(-15.32, 32.11) * mm, "end": v(-15.3, 32.18) * mm});
            skLineSegment(sketch, "E9365", {"start": v(-15.27, 32.25) * mm, "end": v(-15.25, 32.32) * mm});
            skLineSegment(sketch, "E9366", {"start": v(-15.25, 32.32) * mm, "end": v(-15.24, 32.4) * mm});
            skLineSegment(sketch, "E9367", {"start": v(-15.24, 32.4) * mm, "end": v(-15.22, 32.47) * mm});
            skLineSegment(sketch, "E9368", {"start": v(-15.22, 32.47) * mm, "end": v(-15.21, 32.55) * mm});
            skLineSegment(sketch, "E9369", {"start": v(-15.21, 32.55) * mm, "end": v(-15.2, 32.62) * mm});
            skLineSegment(sketch, "E9370", {"start": v(-15.2, 32.62) * mm, "end": v(-15.2, 32.7) * mm});
            skLineSegment(sketch, "E9371", {"start": v(-15.2, 32.7) * mm, "end": v(-15.2, 32.77) * mm});
            skLineSegment(sketch, "E9372", {"start": v(-15.2, 32.77) * mm, "end": v(-15.2, 32.84) * mm});
            skLineSegment(sketch, "E9373", {"start": v(-15.2, 32.84) * mm, "end": v(-15.2, 32.92) * mm});
            skLineSegment(sketch, "E9374", {"start": v(-15.2, 32.92) * mm, "end": v(-15.2, 33) * mm});
            skLineSegment(sketch, "E9375", {"start": v(-15.2, 33) * mm, "end": v(-15.2, 33.07) * mm});
            skLineSegment(sketch, "E9376", {"start": v(-15.2, 33.07) * mm, "end": v(-15.22, 33.14) * mm});
            skLineSegment(sketch, "E9377", {"start": v(-15.22, 33.14) * mm, "end": v(-15.23, 33.21) * mm});
            skLineSegment(sketch, "E9378", {"start": v(-15.23, 33.21) * mm, "end": v(-15.24, 33.29) * mm});
            skLineSegment(sketch, "E9379", {"start": v(-15.24, 33.29) * mm, "end": v(-15.26, 33.36) * mm});
            skLineSegment(sketch, "E9380", {"start": v(-15.26, 33.36) * mm, "end": v(-15.28, 33.43) * mm});
            skLineSegment(sketch, "E9381", {"start": v(-15.28, 33.43) * mm, "end": v(-15.3, 33.5) * mm});
            skLineSegment(sketch, "E9382", {"start": v(-15.3, 33.5) * mm, "end": v(-15.33, 33.57) * mm});
            skLineSegment(sketch, "E9383", {"start": v(-15.33, 33.57) * mm, "end": v(-15.36, 33.64) * mm});
            skLineSegment(sketch, "E9384", {"start": v(-15.36, 33.64) * mm, "end": v(-15.39, 33.71) * mm});
            skLineSegment(sketch, "E9385", {"start": v(-15.39, 33.71) * mm, "end": v(-15.42, 33.78) * mm});
            skLineSegment(sketch, "E9386", {"start": v(-15.42, 33.78) * mm, "end": v(-15.45, 33.84) * mm});
            skLineSegment(sketch, "E9387", {"start": v(-15.45, 33.84) * mm, "end": v(-15.49, 33.9) * mm});
            skLineSegment(sketch, "E9388", {"start": v(-15.49, 33.9) * mm, "end": v(-15.53, 33.97) * mm});
            skLineSegment(sketch, "E9389", {"start": v(-15.53, 33.97) * mm, "end": v(-15.57, 34.04) * mm});
            skLineSegment(sketch, "E9390", {"start": v(-15.61, 34.1) * mm, "end": v(-15.66, 34.16) * mm});
            skLineSegment(sketch, "E9391", {"start": v(-15.66, 34.16) * mm, "end": v(-15.7, 34.21) * mm});
            skLineSegment(sketch, "E9392", {"start": v(-15.7, 34.21) * mm, "end": v(-15.75, 34.27) * mm});
            skLineSegment(sketch, "E9393", {"start": v(-15.75, 34.27) * mm, "end": v(-15.8, 34.32) * mm});
            skLineSegment(sketch, "E9394", {"start": v(-15.8, 34.32) * mm, "end": v(-15.86, 34.38) * mm});
            skLineSegment(sketch, "E9395", {"start": v(-15.86, 34.38) * mm, "end": v(-15.91, 34.43) * mm});
            skLineSegment(sketch, "E9396", {"start": v(-15.91, 34.43) * mm, "end": v(-15.97, 34.48) * mm});
            skLineSegment(sketch, "E9397", {"start": v(-15.97, 34.48) * mm, "end": v(-16.03, 34.52) * mm});
            skLineSegment(sketch, "E9398", {"start": v(-16.03, 34.52) * mm, "end": v(-16.09, 34.57) * mm});
            skLineSegment(sketch, "E9399", {"start": v(-16.09, 34.57) * mm, "end": v(-16.15, 34.61) * mm});
            skLineSegment(sketch, "E9400", {"start": v(-16.15, 34.61) * mm, "end": v(-16.21, 34.65) * mm});
            skLineSegment(sketch, "E9401", {"start": v(-16.21, 34.65) * mm, "end": v(-16.27, 34.69) * mm});
            skLineSegment(sketch, "E9402", {"start": v(-16.27, 34.69) * mm, "end": v(-16.34, 34.73) * mm});
            skLineSegment(sketch, "E9403", {"start": v(-16.34, 34.73) * mm, "end": v(-16.4, 34.76) * mm});
            skLineSegment(sketch, "E9404", {"start": v(-16.4, 34.76) * mm, "end": v(-16.47, 34.8) * mm});
            skLineSegment(sketch, "E9405", {"start": v(-16.47, 34.8) * mm, "end": v(-16.54, 34.82) * mm});
            skLineSegment(sketch, "E9406", {"start": v(-16.54, 34.82) * mm, "end": v(-16.61, 34.85) * mm});
            skLineSegment(sketch, "E9407", {"start": v(-16.61, 34.85) * mm, "end": v(-16.68, 34.87) * mm});
            skLineSegment(sketch, "E9408", {"start": v(-16.68, 34.87) * mm, "end": v(-16.76, 34.9) * mm});
            skLineSegment(sketch, "E9409", {"start": v(-16.76, 34.9) * mm, "end": v(-16.83, 34.91) * mm});
            skLineSegment(sketch, "E9410", {"start": v(-16.83, 34.91) * mm, "end": v(-16.9, 34.93) * mm});
            skLineSegment(sketch, "E9411", {"start": v(-16.9, 34.93) * mm, "end": v(-16.97, 34.94) * mm});
            skLineSegment(sketch, "E9412", {"start": v(-16.97, 34.94) * mm, "end": v(-17.05, 34.95) * mm});
            skLineSegment(sketch, "E9413", {"start": v(-17.05, 34.95) * mm, "end": v(-17.12, 34.96) * mm});
            skLineSegment(sketch, "E9414", {"start": v(-17.12, 34.96) * mm, "end": v(-17.2, 34.97) * mm});
            skLineSegment(sketch, "E9415", {"start": v(-17.2, 34.97) * mm, "end": v(-17.27, 34.97) * mm});
            skLineSegment(sketch, "E9416", {"start": v(-17.27, 34.97) * mm, "end": v(-17.34, 34.97) * mm});
            skLineSegment(sketch, "E9417", {"start": v(-149.19, 33.02) * mm, "end": v(-149.19, 48.02) * mm});
            skLineSegment(sketch, "E9418", {"start": v(-149.19, 48.02) * mm, "end": v(-269.19, 48.02) * mm});
            skLineSegment(sketch, "E9419", {"start": v(-269.19, 48.02) * mm, "end": v(-269.19, 33.02) * mm});
            skLineSegment(sketch, "E9420", {"start": v(-269.19, 33.02) * mm, "end": v(-149.19, 33.02) * mm});
            skCircle(sketch, "E9421", {"center": v(-264.19, 40.52) * mm, "radius": 2.15 * mm});
            skCircle(sketch, "E9422", {"center": v(-154.19, 40.52) * mm, "radius": 2.15 * mm});
            skCircle(sketch, "E9423", {"center": v(-288.3, 22.14) * mm, "radius": 2.5 * mm});
            skCircle(sketch, "E9424", {"center": v(-288.3, 22.14) * mm, "radius": 1.25 * mm});
            skCircle(sketch, "E9425", {"center": v(-224.56, 22.14) * mm, "radius": 1.25 * mm});
            skCircle(sketch, "E9426", {"center": v(-160.8, 22.14) * mm, "radius": 1.25 * mm});
            skCircle(sketch, "E9427", {"center": v(-160.8, 22.14) * mm, "radius": 2.5 * mm});
            skCircle(sketch, "E9428", {"center": v(-288.48, 3.57) * mm, "radius": 2.5 * mm});
            skCircle(sketch, "E9429", {"center": v(-288.48, 3.57) * mm, "radius": 1.25 * mm});
            skCircle(sketch, "E9430", {"center": v(-224.73, 3.57) * mm, "radius": 1.25 * mm});
            skCircle(sketch, "E9431", {"center": v(-160.98, 3.57) * mm, "radius": 2.5 * mm});
            skCircle(sketch, "E9432", {"center": v(-160.98, 3.57) * mm, "radius": 1.25 * mm});
            skCircle(sketch, "E9433", {"center": v(-288.7, -14.87) * mm, "radius": 1.25 * mm});
            skCircle(sketch, "E9434", {"center": v(-161.2, -14.87) * mm, "radius": 1.25 * mm});
            skCircle(sketch, "E9435", {"center": v(-161.46, -33.48) * mm, "radius": 1.25 * mm});
            skCircle(sketch, "E9436", {"center": v(-288.96, -33.48) * mm, "radius": 1.25 * mm});
            skCircle(sketch, "E9437", {"center": v(-288.35, -52.36) * mm, "radius": 1.25 * mm});
            skCircle(sketch, "E9438", {"center": v(-160.85, -52.36) * mm, "radius": 1.25 * mm});
            skCircle(sketch, "E9439", {"center": v(-317, 34.12) * mm, "radius": 2.15 * mm});
            skCircle(sketch, "E9440", {"center": v(-307, 34.12) * mm, "radius": 2.15 * mm});
            skCircle(sketch, "E9441", {"center": v(-317, 4.12) * mm, "radius": 2.15 * mm});
            skCircle(sketch, "E9442", {"center": v(-307, 4.12) * mm, "radius": 2.15 * mm});
            skCircle(sketch, "E9443", {"center": v(-317, -19.75) * mm, "radius": 2.15 * mm});
            skCircle(sketch, "E9444", {"center": v(-307, -19.75) * mm, "radius": 2.15 * mm});
            skCircle(sketch, "E9445", {"center": v(-317, -49.75) * mm, "radius": 2.15 * mm});
            skCircle(sketch, "E9446", {"center": v(-307, -49.75) * mm, "radius": 2.15 * mm});
            skCircle(sketch, "E9447", {"center": v(-337, -56) * mm, "radius": 1.25 * mm});
            skCircle(sketch, "E9448", {"center": v(-337, 71.5) * mm, "radius": 1.25 * mm});
            skSolve(sketch);
        }
        {
            var Q0;
            Q0=makeQuery(id+"F6.imprint","IMPRINT",FACE,{"disambiguationData":[TD([[makeQuery(id+"F6.imprint","IMPRINT",EDGE,{"derivedFrom":sQuery(id+"F6.wireOp",EDGE,"E9417")}),1.0]])]});
            var Q1;
            Q1=makeQuery(id+"F6.imprint","IMPRINT",FACE,{"disambiguationData":[TD([[makeQuery(id+"F6.imprint","IMPRINT",EDGE,{"derivedFrom":sQuery(id+"F6.wireOp",EDGE,"E8574")}),-1.0]])]});
            var Q2;
            Q2=makeQuery(id+"F6.imprint","IMPRINT",FACE,{"disambiguationData":[TD([[makeQuery(id+"F6.imprint","IMPRINT",EDGE,{"derivedFrom":sQuery(id+"F6.wireOp",EDGE,"E7719")}),-1.0]])]});
            var Q3;
            Q3=makeQuery(id+"F6.imprint","IMPRINT",FACE,{"disambiguationData":[TD([[makeQuery(id+"F6.imprint","IMPRINT",EDGE,{"derivedFrom":sQuery(id+"F6.wireOp",EDGE,"E7046")}),1.0]])]});
            var Q4;
            Q4=makeQuery(id+"F6.imprint","IMPRINT",FACE,{"disambiguationData":[TD([[makeQuery(id+"F6.imprint","IMPRINT",EDGE,{"derivedFrom":sQuery(id+"F6.wireOp",EDGE,"E6013")}),1.0]])]});
            var Q5;
            Q5=makeQuery(id+"F6.imprint","IMPRINT",FACE,{"disambiguationData":[TD([[makeQuery(id+"F6.imprint","IMPRINT",EDGE,{"derivedFrom":sQuery(id+"F6.wireOp",EDGE,"E6009")}),1.0]])]});
            var Q6;
            Q6=makeQuery(id+"F6.imprint","IMPRINT",FACE,{"disambiguationData":[TD([[makeQuery(id+"F6.imprint","IMPRINT",EDGE,{"derivedFrom":sQuery(id+"F6.wireOp",EDGE,"E4991")}),1.0]])]});
            var Q7;
            Q7=makeQuery(id+"F6.imprint","IMPRINT",FACE,{"disambiguationData":[TD([[makeQuery(id+"F6.imprint","IMPRINT",EDGE,{"derivedFrom":sQuery(id+"F6.wireOp",EDGE,"E4640")}),1.0]])]});
            var Q8;
            Q8=makeQuery(id+"F6.imprint","IMPRINT",FACE,{"disambiguationData":[TD([[makeQuery(id+"F6.imprint","IMPRINT",EDGE,{"derivedFrom":sQuery(id+"F6.wireOp",EDGE,"E7042")}),1.0]])]});
            extrude(context, id + "F7", {"entities" : qUnion([Q0, Q1, Q2, Q3, Q4, Q5, Q6, Q7, Q8]), "depth" : 4 * mm});
        }
        {
            var Q0;
            Q0=makeQuery(id+"F6.imprint","IMPRINT",FACE,{"disambiguationData":[TD([[makeQuery(id+"F6.imprint","IMPRINT",EDGE,{"derivedFrom":sQuery(id+"F6.wireOp",EDGE,"E9423")}),1.0]])]});
            var Q1;
            Q1=makeQuery(id+"F6.imprint","IMPRINT",FACE,{"disambiguationData":[TD([[makeQuery(id+"F6.imprint","IMPRINT",EDGE,{"derivedFrom":sQuery(id+"F6.wireOp",EDGE,"E9428")}),1.0]])]});
            var Q2;
            Q2=makeQuery(id+"F6.imprint","IMPRINT",FACE,{"disambiguationData":[TD([[makeQuery(id+"F6.imprint","IMPRINT",EDGE,{"derivedFrom":sQuery(id+"F6.wireOp",EDGE,"E8574")}),1.0]])]});
            var Q3;
            Q3=makeQuery(id+"F6.imprint","IMPRINT",FACE,{"disambiguationData":[TD([[makeQuery(id+"F6.imprint","IMPRINT",EDGE,{"derivedFrom":sQuery(id+"F6.wireOp",EDGE,"E7719")}),1.0]])]});
            var Q4;
            Q4=makeQuery(id+"F6.imprint","IMPRINT",FACE,{"disambiguationData":[TD([[makeQuery(id+"F6.imprint","IMPRINT",EDGE,{"derivedFrom":sQuery(id+"F6.wireOp",EDGE,"E9426")}),-1.0]])]});
            var Q5;
            Q5=makeQuery(id+"F6.imprint","IMPRINT",FACE,{"disambiguationData":[TD([[makeQuery(id+"F6.imprint","IMPRINT",EDGE,{"derivedFrom":sQuery(id+"F6.wireOp",EDGE,"E9431")}),1.0]])]});
            extrude(context, id + "F8", {"entities" : qUnion([Q0, Q1, Q2, Q3, Q4, Q5]), "operationType" : NewBodyOperationType.ADD, "depth" : 3 * mm});
        }
        {
            var Q0;
            Q0=qCreatedBy(makeId("Front.planeOp"),FACE);
            var sketch = newSketch(context, id + "F9", { "sketchPlane" : qUnion([Q0])});
            skCircle(sketch, "E9449", {"center": v(-144.2, -116.59) * mm, "radius": 1.25 * mm});
            skLineSegment(sketch, "E9450", {"start": v(-147.2, -118.65) * mm, "end": v(-141.2, -118.65) * mm});
            skLineSegment(sketch, "E9451", {"start": v(-141.2, -118.65) * mm, "end": v(-141.2, -114.52) * mm});
            skLineSegment(sketch, "E9452", {"start": v(-141.2, -114.52) * mm, "end": v(-147.2, -114.52) * mm});
            skLineSegment(sketch, "E9453", {"start": v(-147.2, -114.52) * mm, "end": v(-147.2, -118.65) * mm});
            skCircle(sketch, "E9454", {"center": v(-144.2, -116.59) * mm, "radius": 3.75 * mm});
            skLineSegment(sketch, "E9455", {"start": v(-66.55, -41.84) * mm, "end": v(-65.34, -40.76) * mm});
            skLineSegment(sketch, "E9456", {"start": v(-65.34, -40.76) * mm, "end": v(-65.3, -40.73) * mm});
            skLineSegment(sketch, "E9457", {"start": v(-65.3, -40.73) * mm, "end": v(-65.2, -40.64) * mm});
            skLineSegment(sketch, "E9458", {"start": v(-65.2, -40.64) * mm, "end": v(-65, -40.5) * mm});
            skLineSegment(sketch, "E9459", {"start": v(-65, -40.5) * mm, "end": v(-64.7, -40.32) * mm});
            skLineSegment(sketch, "E9460", {"start": v(-64.7, -40.32) * mm, "end": v(-64.32, -40.11) * mm});
            skLineSegment(sketch, "E9461", {"start": v(-64.32, -40.11) * mm, "end": v(-63.84, -39.88) * mm});
            skLineSegment(sketch, "E9462", {"start": v(-63.84, -39.88) * mm, "end": v(-63.26, -39.63) * mm});
            skLineSegment(sketch, "E9463", {"start": v(-63.26, -39.63) * mm, "end": v(-62.58, -39.38) * mm});
            skLineSegment(sketch, "E9464", {"start": v(-62.58, -39.38) * mm, "end": v(-61.8, -39.13) * mm});
            skLineSegment(sketch, "E9465", {"start": v(-61.8, -39.13) * mm, "end": v(-61.76, -39.12) * mm});
            skArc(sketch, "E9466", {"start": v(-61.76, -39.12) * mm, "mid": v(-61.03, -40.01) * mm, "end": v(-60.32, -40.92) * mm});
            skLineSegment(sketch, "E9467", {"start": v(-60.32, -40.92) * mm, "end": v(-60.34, -40.96) * mm});
            skLineSegment(sketch, "E9468", {"start": v(-60.34, -40.96) * mm, "end": v(-60.75, -41.67) * mm});
            skLineSegment(sketch, "E9469", {"start": v(-60.75, -41.67) * mm, "end": v(-61.14, -42.28) * mm});
            skLineSegment(sketch, "E9470", {"start": v(-61.14, -42.28) * mm, "end": v(-61.51, -42.79) * mm});
            skLineSegment(sketch, "E9471", {"start": v(-61.51, -42.79) * mm, "end": v(-61.84, -43.2) * mm});
            skLineSegment(sketch, "E9472", {"start": v(-61.84, -43.2) * mm, "end": v(-62.13, -43.53) * mm});
            skLineSegment(sketch, "E9473", {"start": v(-62.13, -43.53) * mm, "end": v(-62.37, -43.77) * mm});
            skLineSegment(sketch, "E9474", {"start": v(-62.37, -43.77) * mm, "end": v(-62.55, -43.94) * mm});
            skLineSegment(sketch, "E9475", {"start": v(-62.55, -43.94) * mm, "end": v(-62.66, -44.03) * mm});
            skLineSegment(sketch, "E9476", {"start": v(-62.66, -44.03) * mm, "end": v(-62.7, -44.06) * mm});
            skLineSegment(sketch, "E9477", {"start": v(-62.7, -44.06) * mm, "end": v(-64.01, -45) * mm});
            skArc(sketch, "E9478", {"start": v(-64.01, -45) * mm, "mid": v(-63.1, -46.33) * mm, "end": v(-62.25, -47.7) * mm});
            skLineSegment(sketch, "E9479", {"start": v(-62.25, -47.7) * mm, "end": v(-60.86, -46.88) * mm});
            skLineSegment(sketch, "E9480", {"start": v(-60.86, -46.88) * mm, "end": v(-60.82, -46.86) * mm});
            skLineSegment(sketch, "E9481", {"start": v(-60.82, -46.86) * mm, "end": v(-60.69, -46.8) * mm});
            skLineSegment(sketch, "E9482", {"start": v(-60.69, -46.8) * mm, "end": v(-60.46, -46.7) * mm});
            skLineSegment(sketch, "E9483", {"start": v(-60.46, -46.7) * mm, "end": v(-60.15, -46.58) * mm});
            skLineSegment(sketch, "E9484", {"start": v(-60.15, -46.58) * mm, "end": v(-59.73, -46.45) * mm});
            skLineSegment(sketch, "E9485", {"start": v(-59.73, -46.45) * mm, "end": v(-59.22, -46.31) * mm});
            skLineSegment(sketch, "E9486", {"start": v(-59.22, -46.31) * mm, "end": v(-58.6, -46.18) * mm});
            skLineSegment(sketch, "E9487", {"start": v(-58.6, -46.18) * mm, "end": v(-57.88, -46.07) * mm});
            skLineSegment(sketch, "E9488", {"start": v(-57.88, -46.07) * mm, "end": v(-57.07, -45.98) * mm});
            skLineSegment(sketch, "E9489", {"start": v(-57.07, -45.98) * mm, "end": v(-57.03, -45.98) * mm});
            skArc(sketch, "E9490", {"start": v(-57.03, -45.98) * mm, "mid": v(-56.48, -47) * mm, "end": v(-55.96, -48.02) * mm});
            skLineSegment(sketch, "E9491", {"start": v(-55.96, -48.02) * mm, "end": v(-55.99, -48.05) * mm});
            skLineSegment(sketch, "E9492", {"start": v(-55.99, -48.05) * mm, "end": v(-56.53, -48.67) * mm});
            skLineSegment(sketch, "E9493", {"start": v(-56.53, -48.67) * mm, "end": v(-57.04, -49.2) * mm});
            skLineSegment(sketch, "E9494", {"start": v(-57.04, -49.2) * mm, "end": v(-57.5, -49.62) * mm});
            skLineSegment(sketch, "E9495", {"start": v(-57.5, -49.62) * mm, "end": v(-57.9, -49.96) * mm});
            skLineSegment(sketch, "E9496", {"start": v(-57.9, -49.96) * mm, "end": v(-58.25, -50.23) * mm});
            skLineSegment(sketch, "E9497", {"start": v(-58.25, -50.23) * mm, "end": v(-58.53, -50.42) * mm});
            skLineSegment(sketch, "E9498", {"start": v(-58.53, -50.42) * mm, "end": v(-58.74, -50.55) * mm});
            skLineSegment(sketch, "E9499", {"start": v(-58.74, -50.55) * mm, "end": v(-58.86, -50.62) * mm});
            skLineSegment(sketch, "E9500", {"start": v(-58.86, -50.62) * mm, "end": v(-58.9, -50.64) * mm});
            skLineSegment(sketch, "E9501", {"start": v(-58.9, -50.64) * mm, "end": v(-60.38, -51.3) * mm});
            skArc(sketch, "E9502", {"start": v(-60.38, -51.3) * mm, "mid": v(-59.75, -52.79) * mm, "end": v(-59.18, -54.3) * mm});
            skLineSegment(sketch, "E9503", {"start": v(-59.18, -54.3) * mm, "end": v(-57.65, -53.76) * mm});
            skLineSegment(sketch, "E9504", {"start": v(-57.65, -53.76) * mm, "end": v(-57.6, -53.75) * mm});
            skLineSegment(sketch, "E9505", {"start": v(-57.6, -53.75) * mm, "end": v(-57.47, -53.71) * mm});
            skLineSegment(sketch, "E9506", {"start": v(-57.47, -53.71) * mm, "end": v(-57.23, -53.66) * mm});
            skLineSegment(sketch, "E9507", {"start": v(-57.23, -53.66) * mm, "end": v(-56.9, -53.6) * mm});
            skLineSegment(sketch, "E9508", {"start": v(-56.9, -53.6) * mm, "end": v(-56.46, -53.56) * mm});
            skLineSegment(sketch, "E9509", {"start": v(-56.46, -53.56) * mm, "end": v(-55.93, -53.53) * mm});
            skLineSegment(sketch, "E9510", {"start": v(-55.93, -53.53) * mm, "end": v(-55.3, -53.52) * mm});
            skLineSegment(sketch, "E9511", {"start": v(-55.3, -53.52) * mm, "end": v(-54.58, -53.55) * mm});
            skLineSegment(sketch, "E9512", {"start": v(-54.58, -53.55) * mm, "end": v(-53.76, -53.62) * mm});
            skLineSegment(sketch, "E9513", {"start": v(-53.76, -53.62) * mm, "end": v(-53.72, -53.62) * mm});
            skArc(sketch, "E9514", {"start": v(-53.72, -53.62) * mm, "mid": v(-53.38, -54.73) * mm, "end": v(-53.08, -55.84) * mm});
            skLineSegment(sketch, "E9515", {"start": v(-53.08, -55.84) * mm, "end": v(-53.1, -55.86) * mm});
            skLineSegment(sketch, "E9516", {"start": v(-53.1, -55.86) * mm, "end": v(-53.76, -56.36) * mm});
            skLineSegment(sketch, "E9517", {"start": v(-53.76, -56.36) * mm, "end": v(-54.36, -56.78) * mm});
            skLineSegment(sketch, "E9518", {"start": v(-54.36, -56.78) * mm, "end": v(-54.9, -57.1) * mm});
            skLineSegment(sketch, "E9519", {"start": v(-54.9, -57.1) * mm, "end": v(-55.36, -57.36) * mm});
            skLineSegment(sketch, "E9520", {"start": v(-55.36, -57.36) * mm, "end": v(-55.75, -57.56) * mm});
            skLineSegment(sketch, "E9521", {"start": v(-55.75, -57.56) * mm, "end": v(-56.06, -57.69) * mm});
            skLineSegment(sketch, "E9522", {"start": v(-56.06, -57.69) * mm, "end": v(-56.29, -57.77) * mm});
            skLineSegment(sketch, "E9523", {"start": v(-56.29, -57.77) * mm, "end": v(-56.43, -57.82) * mm});
            skLineSegment(sketch, "E9524", {"start": v(-56.43, -57.82) * mm, "end": v(-56.47, -57.83) * mm});
            skLineSegment(sketch, "E9525", {"start": v(-56.47, -57.83) * mm, "end": v(-58.05, -58.2) * mm});
            skArc(sketch, "E9526", {"start": v(-58.05, -58.2) * mm, "mid": v(-57.72, -59.77) * mm, "end": v(-57.46, -61.37) * mm});
            skLineSegment(sketch, "E9527", {"start": v(-57.46, -61.37) * mm, "end": v(-55.86, -61.14) * mm});
            skLineSegment(sketch, "E9528", {"start": v(-55.86, -61.14) * mm, "end": v(-55.8, -61.13) * mm});
            skLineSegment(sketch, "E9529", {"start": v(-55.8, -61.13) * mm, "end": v(-55.66, -61.13) * mm});
            skLineSegment(sketch, "E9530", {"start": v(-55.66, -61.13) * mm, "end": v(-55.42, -61.12) * mm});
            skLineSegment(sketch, "E9531", {"start": v(-55.42, -61.12) * mm, "end": v(-55.08, -61.13) * mm});
            skLineSegment(sketch, "E9532", {"start": v(-55.08, -61.13) * mm, "end": v(-54.65, -61.17) * mm});
            skLineSegment(sketch, "E9533", {"start": v(-54.65, -61.17) * mm, "end": v(-54.12, -61.24) * mm});
            skLineSegment(sketch, "E9534", {"start": v(-54.12, -61.24) * mm, "end": v(-53.5, -61.36) * mm});
            skLineSegment(sketch, "E9535", {"start": v(-53.5, -61.36) * mm, "end": v(-52.8, -61.53) * mm});
            skLineSegment(sketch, "E9536", {"start": v(-52.8, -61.53) * mm, "end": v(-52, -61.76) * mm});
            skLineSegment(sketch, "E9537", {"start": v(-52, -61.76) * mm, "end": v(-51.97, -61.77) * mm});
            skArc(sketch, "E9538", {"start": v(-51.97, -61.77) * mm, "mid": v(-51.86, -62.92) * mm, "end": v(-51.77, -64.07) * mm});
            skLineSegment(sketch, "E9539", {"start": v(-51.77, -64.07) * mm, "end": v(-51.8, -64.09) * mm});
            skLineSegment(sketch, "E9540", {"start": v(-51.8, -64.09) * mm, "end": v(-52.54, -64.45) * mm});
            skLineSegment(sketch, "E9541", {"start": v(-52.54, -64.45) * mm, "end": v(-53.2, -64.74) * mm});
            skLineSegment(sketch, "E9542", {"start": v(-53.2, -64.74) * mm, "end": v(-53.8, -64.96) * mm});
            skLineSegment(sketch, "E9543", {"start": v(-53.8, -64.96) * mm, "end": v(-54.3, -65.12) * mm});
            skLineSegment(sketch, "E9544", {"start": v(-54.3, -65.12) * mm, "end": v(-54.73, -65.23) * mm});
            skLineSegment(sketch, "E9545", {"start": v(-54.73, -65.23) * mm, "end": v(-55.06, -65.3) * mm});
            skLineSegment(sketch, "E9546", {"start": v(-55.06, -65.3) * mm, "end": v(-55.3, -65.34) * mm});
            skLineSegment(sketch, "E9547", {"start": v(-55.3, -65.34) * mm, "end": v(-55.44, -65.35) * mm});
            skLineSegment(sketch, "E9548", {"start": v(-55.44, -65.35) * mm, "end": v(-55.5, -65.36) * mm});
            skLineSegment(sketch, "E9549", {"start": v(-55.5, -65.36) * mm, "end": v(-57.1, -65.4) * mm});
            skArc(sketch, "E9550", {"start": v(-57.1, -65.4) * mm, "mid": v(-57.1, -67.02) * mm, "end": v(-57.15, -68.64) * mm});
            skLineSegment(sketch, "E9551", {"start": v(-57.15, -68.64) * mm, "end": v(-55.53, -68.72) * mm});
            skLineSegment(sketch, "E9552", {"start": v(-55.53, -68.72) * mm, "end": v(-55.48, -68.73) * mm});
            skLineSegment(sketch, "E9553", {"start": v(-55.48, -68.73) * mm, "end": v(-55.34, -68.75) * mm});
            skLineSegment(sketch, "E9554", {"start": v(-55.34, -68.75) * mm, "end": v(-55.1, -68.8) * mm});
            skLineSegment(sketch, "E9555", {"start": v(-55.1, -68.8) * mm, "end": v(-54.77, -68.87) * mm});
            skLineSegment(sketch, "E9556", {"start": v(-54.77, -68.87) * mm, "end": v(-54.35, -69) * mm});
            skLineSegment(sketch, "E9557", {"start": v(-54.35, -69) * mm, "end": v(-53.85, -69.16) * mm});
            skLineSegment(sketch, "E9558", {"start": v(-53.85, -69.16) * mm, "end": v(-53.26, -69.4) * mm});
            skLineSegment(sketch, "E9559", {"start": v(-53.26, -69.4) * mm, "end": v(-52.6, -69.7) * mm});
            skLineSegment(sketch, "E9560", {"start": v(-52.6, -69.7) * mm, "end": v(-51.87, -70.08) * mm});
            skLineSegment(sketch, "E9561", {"start": v(-51.87, -70.08) * mm, "end": v(-51.84, -70.1) * mm});
            skArc(sketch, "E9562", {"start": v(-51.84, -70.1) * mm, "mid": v(-51.95, -71.25) * mm, "end": v(-52.1, -72.4) * mm});
            skLineSegment(sketch, "E9563", {"start": v(-52.1, -72.4) * mm, "end": v(-52.13, -72.4) * mm});
            skLineSegment(sketch, "E9564", {"start": v(-52.13, -72.4) * mm, "end": v(-52.93, -72.62) * mm});
            skLineSegment(sketch, "E9565", {"start": v(-52.93, -72.62) * mm, "end": v(-53.64, -72.77) * mm});
            skLineSegment(sketch, "E9566", {"start": v(-53.64, -72.77) * mm, "end": v(-54.26, -72.87) * mm});
            skLineSegment(sketch, "E9567", {"start": v(-54.26, -72.87) * mm, "end": v(-54.79, -72.93) * mm});
            skLineSegment(sketch, "E9568", {"start": v(-54.79, -72.93) * mm, "end": v(-55.22, -72.96) * mm});
            skLineSegment(sketch, "E9569", {"start": v(-55.22, -72.96) * mm, "end": v(-55.56, -72.96) * mm});
            skLineSegment(sketch, "E9570", {"start": v(-55.56, -72.96) * mm, "end": v(-55.8, -72.95) * mm});
            skLineSegment(sketch, "E9571", {"start": v(-55.8, -72.95) * mm, "end": v(-55.95, -72.94) * mm});
            skLineSegment(sketch, "E9572", {"start": v(-55.95, -72.94) * mm, "end": v(-56, -72.93) * mm});
            skLineSegment(sketch, "E9573", {"start": v(-56, -72.93) * mm, "end": v(-57.6, -72.67) * mm});
            skArc(sketch, "E9574", {"start": v(-57.6, -72.67) * mm, "mid": v(-57.89, -74.25) * mm, "end": v(-58.26, -75.82) * mm});
            skLineSegment(sketch, "E9575", {"start": v(-58.26, -75.82) * mm, "end": v(-56.69, -76.23) * mm});
            skLineSegment(sketch, "E9576", {"start": v(-56.69, -76.23) * mm, "end": v(-56.64, -76.24) * mm});
            skLineSegment(sketch, "E9577", {"start": v(-56.64, -76.24) * mm, "end": v(-56.5, -76.29) * mm});
            skLineSegment(sketch, "E9578", {"start": v(-56.5, -76.29) * mm, "end": v(-56.28, -76.38) * mm});
            skLineSegment(sketch, "E9579", {"start": v(-56.28, -76.38) * mm, "end": v(-55.97, -76.52) * mm});
            skLineSegment(sketch, "E9580", {"start": v(-55.97, -76.52) * mm, "end": v(-55.59, -76.72) * mm});
            skLineSegment(sketch, "E9581", {"start": v(-55.59, -76.72) * mm, "end": v(-55.13, -76.99) * mm});
            skLineSegment(sketch, "E9582", {"start": v(-55.13, -76.99) * mm, "end": v(-54.6, -77.33) * mm});
            skLineSegment(sketch, "E9583", {"start": v(-54.6, -77.33) * mm, "end": v(-54.01, -77.75) * mm});
            skLineSegment(sketch, "E9584", {"start": v(-54.01, -77.75) * mm, "end": v(-53.37, -78.27) * mm});
            skLineSegment(sketch, "E9585", {"start": v(-53.37, -78.27) * mm, "end": v(-53.34, -78.3) * mm});
            skArc(sketch, "E9586", {"start": v(-53.34, -78.3) * mm, "mid": v(-53.67, -79.4) * mm, "end": v(-54.04, -80.5) * mm});
            skLineSegment(sketch, "E9587", {"start": v(-54.04, -80.5) * mm, "end": v(-54.07, -80.5) * mm});
            skLineSegment(sketch, "E9588", {"start": v(-54.07, -80.5) * mm, "end": v(-54.9, -80.55) * mm});
            skLineSegment(sketch, "E9589", {"start": v(-54.9, -80.55) * mm, "end": v(-55.62, -80.56) * mm});
            skLineSegment(sketch, "E9590", {"start": v(-55.62, -80.56) * mm, "end": v(-56.25, -80.54) * mm});
            skLineSegment(sketch, "E9591", {"start": v(-56.25, -80.54) * mm, "end": v(-56.78, -80.5) * mm});
            skLineSegment(sketch, "E9592", {"start": v(-56.78, -80.5) * mm, "end": v(-57.21, -80.44) * mm});
            skLineSegment(sketch, "E9593", {"start": v(-57.21, -80.44) * mm, "end": v(-57.55, -80.38) * mm});
            skLineSegment(sketch, "E9594", {"start": v(-57.55, -80.38) * mm, "end": v(-57.78, -80.32) * mm});
            skLineSegment(sketch, "E9595", {"start": v(-57.78, -80.32) * mm, "end": v(-57.92, -80.28) * mm});
            skLineSegment(sketch, "E9596", {"start": v(-57.92, -80.28) * mm, "end": v(-57.97, -80.26) * mm});
            skLineSegment(sketch, "E9597", {"start": v(-57.97, -80.26) * mm, "end": v(-59.48, -79.7) * mm});
            skArc(sketch, "E9598", {"start": v(-59.48, -79.7) * mm, "mid": v(-60.08, -81.19) * mm, "end": v(-60.75, -82.66) * mm});
            skLineSegment(sketch, "E9599", {"start": v(-60.75, -82.66) * mm, "end": v(-59.3, -83.36) * mm});
            skLineSegment(sketch, "E9600", {"start": v(-59.3, -83.36) * mm, "end": v(-59.25, -83.38) * mm});
            skLineSegment(sketch, "E9601", {"start": v(-59.25, -83.38) * mm, "end": v(-59.12, -83.45) * mm});
            skLineSegment(sketch, "E9602", {"start": v(-59.12, -83.45) * mm, "end": v(-58.92, -83.59) * mm});
            skLineSegment(sketch, "E9603", {"start": v(-58.92, -83.59) * mm, "end": v(-58.64, -83.78) * mm});
            skLineSegment(sketch, "E9604", {"start": v(-58.64, -83.78) * mm, "end": v(-58.3, -84.06) * mm});
            skLineSegment(sketch, "E9605", {"start": v(-58.3, -84.06) * mm, "end": v(-57.9, -84.4) * mm});
            skLineSegment(sketch, "E9606", {"start": v(-57.9, -84.4) * mm, "end": v(-57.46, -84.85) * mm});
            skLineSegment(sketch, "E9607", {"start": v(-57.46, -84.85) * mm, "end": v(-56.96, -85.38) * mm});
            skLineSegment(sketch, "E9608", {"start": v(-56.96, -85.38) * mm, "end": v(-56.43, -86.01) * mm});
            skLineSegment(sketch, "E9609", {"start": v(-56.43, -86.01) * mm, "end": v(-56.41, -86.04) * mm});
            skArc(sketch, "E9610", {"start": v(-56.41, -86.04) * mm, "mid": v(-56.95, -87.06) * mm, "end": v(-57.52, -88.06) * mm});
            skLineSegment(sketch, "E9611", {"start": v(-57.52, -88.06) * mm, "end": v(-57.56, -88.06) * mm});
            skLineSegment(sketch, "E9612", {"start": v(-57.56, -88.06) * mm, "end": v(-58.38, -87.95) * mm});
            skLineSegment(sketch, "E9613", {"start": v(-58.38, -87.95) * mm, "end": v(-59.09, -87.82) * mm});
            skLineSegment(sketch, "E9614", {"start": v(-59.09, -87.82) * mm, "end": v(-59.7, -87.68) * mm});
            skLineSegment(sketch, "E9615", {"start": v(-59.7, -87.68) * mm, "end": v(-60.21, -87.53) * mm});
            skLineSegment(sketch, "E9616", {"start": v(-60.21, -87.53) * mm, "end": v(-60.63, -87.39) * mm});
            skLineSegment(sketch, "E9617", {"start": v(-60.63, -87.39) * mm, "end": v(-60.94, -87.26) * mm});
            skLineSegment(sketch, "E9618", {"start": v(-60.94, -87.26) * mm, "end": v(-61.16, -87.16) * mm});
            skLineSegment(sketch, "E9619", {"start": v(-61.16, -87.16) * mm, "end": v(-61.29, -87.1) * mm});
            skLineSegment(sketch, "E9620", {"start": v(-61.29, -87.1) * mm, "end": v(-61.33, -87.07) * mm});
            skLineSegment(sketch, "E9621", {"start": v(-61.33, -87.07) * mm, "end": v(-62.7, -86.21) * mm});
            skArc(sketch, "E9622", {"start": v(-62.7, -86.21) * mm, "mid": v(-63.59, -87.56) * mm, "end": v(-64.53, -88.87) * mm});
            skLineSegment(sketch, "E9623", {"start": v(-64.53, -88.87) * mm, "end": v(-63.23, -89.85) * mm});
            skLineSegment(sketch, "E9624", {"start": v(-63.23, -89.85) * mm, "end": v(-63.2, -89.88) * mm});
            skLineSegment(sketch, "E9625", {"start": v(-63.2, -89.88) * mm, "end": v(-63.09, -89.97) * mm});
            skLineSegment(sketch, "E9626", {"start": v(-63.09, -89.97) * mm, "end": v(-62.91, -90.14) * mm});
            skLineSegment(sketch, "E9627", {"start": v(-62.91, -90.14) * mm, "end": v(-62.68, -90.39) * mm});
            skLineSegment(sketch, "E9628", {"start": v(-62.68, -90.39) * mm, "end": v(-62.4, -90.72) * mm});
            skLineSegment(sketch, "E9629", {"start": v(-62.4, -90.72) * mm, "end": v(-62.08, -91.15) * mm});
            skLineSegment(sketch, "E9630", {"start": v(-62.08, -91.15) * mm, "end": v(-61.72, -91.66) * mm});
            skLineSegment(sketch, "E9631", {"start": v(-61.72, -91.66) * mm, "end": v(-61.34, -92.28) * mm});
            skLineSegment(sketch, "E9632", {"start": v(-61.34, -92.28) * mm, "end": v(-60.95, -93) * mm});
            skLineSegment(sketch, "E9633", {"start": v(-60.95, -93) * mm, "end": v(-60.93, -93.04) * mm});
            skArc(sketch, "E9634", {"start": v(-60.93, -93.04) * mm, "mid": v(-61.66, -93.93) * mm, "end": v(-62.42, -94.8) * mm});
            skLineSegment(sketch, "E9635", {"start": v(-62.42, -94.8) * mm, "end": v(-62.45, -94.8) * mm});
            skLineSegment(sketch, "E9636", {"start": v(-62.45, -94.8) * mm, "end": v(-63.23, -94.53) * mm});
            skLineSegment(sketch, "E9637", {"start": v(-63.23, -94.53) * mm, "end": v(-63.9, -94.26) * mm});
            skLineSegment(sketch, "E9638", {"start": v(-63.9, -94.26) * mm, "end": v(-64.48, -94) * mm});
            skLineSegment(sketch, "E9639", {"start": v(-64.48, -94) * mm, "end": v(-64.95, -93.76) * mm});
            skLineSegment(sketch, "E9640", {"start": v(-64.95, -93.76) * mm, "end": v(-65.33, -93.54) * mm});
            skLineSegment(sketch, "E9641", {"start": v(-65.33, -93.54) * mm, "end": v(-65.61, -93.35) * mm});
            skLineSegment(sketch, "E9642", {"start": v(-65.61, -93.35) * mm, "end": v(-65.8, -93.2) * mm});
            skLineSegment(sketch, "E9643", {"start": v(-65.8, -93.2) * mm, "end": v(-65.92, -93.12) * mm});
            skLineSegment(sketch, "E9644", {"start": v(-65.92, -93.12) * mm, "end": v(-65.96, -93.09) * mm});
            skLineSegment(sketch, "E9645", {"start": v(-65.96, -93.09) * mm, "end": v(-67.14, -91.98) * mm});
            skArc(sketch, "E9646", {"start": v(-67.14, -91.98) * mm, "mid": v(-68.27, -93.13) * mm, "end": v(-69.45, -94.23) * mm});
            skLineSegment(sketch, "E9647", {"start": v(-69.45, -94.23) * mm, "end": v(-68.37, -95.44) * mm});
            skLineSegment(sketch, "E9648", {"start": v(-68.37, -95.44) * mm, "end": v(-68.34, -95.48) * mm});
            skLineSegment(sketch, "E9649", {"start": v(-68.34, -95.48) * mm, "end": v(-68.25, -95.6) * mm});
            skLineSegment(sketch, "E9650", {"start": v(-68.25, -95.6) * mm, "end": v(-68.11, -95.8) * mm});
            skLineSegment(sketch, "E9651", {"start": v(-68.11, -95.8) * mm, "end": v(-67.93, -96.08) * mm});
            skLineSegment(sketch, "E9652", {"start": v(-67.93, -96.08) * mm, "end": v(-67.72, -96.46) * mm});
            skLineSegment(sketch, "E9653", {"start": v(-67.72, -96.46) * mm, "end": v(-67.49, -96.94) * mm});
            skLineSegment(sketch, "E9654", {"start": v(-67.49, -96.94) * mm, "end": v(-67.24, -97.52) * mm});
            skLineSegment(sketch, "E9655", {"start": v(-67.24, -97.52) * mm, "end": v(-66.99, -98.2) * mm});
            skLineSegment(sketch, "E9656", {"start": v(-66.99, -98.2) * mm, "end": v(-66.74, -98.98) * mm});
            skLineSegment(sketch, "E9657", {"start": v(-66.74, -98.98) * mm, "end": v(-66.73, -99.02) * mm});
            skArc(sketch, "E9658", {"start": v(-66.73, -99.02) * mm, "mid": v(-67.62, -99.75) * mm, "end": v(-68.53, -100.46) * mm});
            skLineSegment(sketch, "E9659", {"start": v(-68.53, -100.46) * mm, "end": v(-68.57, -100.45) * mm});
            skLineSegment(sketch, "E9660", {"start": v(-68.57, -100.45) * mm, "end": v(-69.28, -100.03) * mm});
            skLineSegment(sketch, "E9661", {"start": v(-69.28, -100.03) * mm, "end": v(-69.89, -99.64) * mm});
            skLineSegment(sketch, "E9662", {"start": v(-69.89, -99.64) * mm, "end": v(-70.4, -99.27) * mm});
            skLineSegment(sketch, "E9663", {"start": v(-70.4, -99.27) * mm, "end": v(-70.81, -98.94) * mm});
            skLineSegment(sketch, "E9664", {"start": v(-70.81, -98.94) * mm, "end": v(-71.14, -98.65) * mm});
            skLineSegment(sketch, "E9665", {"start": v(-71.14, -98.65) * mm, "end": v(-71.38, -98.41) * mm});
            skLineSegment(sketch, "E9666", {"start": v(-71.38, -98.41) * mm, "end": v(-71.55, -98.24) * mm});
            skLineSegment(sketch, "E9667", {"start": v(-71.55, -98.24) * mm, "end": v(-71.64, -98.12) * mm});
            skLineSegment(sketch, "E9668", {"start": v(-71.64, -98.12) * mm, "end": v(-71.67, -98.09) * mm});
            skLineSegment(sketch, "E9669", {"start": v(-71.67, -98.09) * mm, "end": v(-72.61, -96.77) * mm});
            skArc(sketch, "E9670", {"start": v(-72.61, -96.77) * mm, "mid": v(-73.94, -97.68) * mm, "end": v(-75.32, -98.53) * mm});
            skLineSegment(sketch, "E9671", {"start": v(-75.32, -98.53) * mm, "end": v(-74.5, -99.92) * mm});
            skLineSegment(sketch, "E9672", {"start": v(-74.5, -99.92) * mm, "end": v(-74.47, -99.97) * mm});
            skLineSegment(sketch, "E9673", {"start": v(-74.47, -99.97) * mm, "end": v(-74.4, -100.1) * mm});
            skLineSegment(sketch, "E9674", {"start": v(-74.4, -100.1) * mm, "end": v(-74.3, -100.32) * mm});
            skLineSegment(sketch, "E9675", {"start": v(-74.3, -100.32) * mm, "end": v(-74.2, -100.64) * mm});
            skLineSegment(sketch, "E9676", {"start": v(-74.2, -100.64) * mm, "end": v(-74.06, -101.05) * mm});
            skLineSegment(sketch, "E9677", {"start": v(-74.06, -101.05) * mm, "end": v(-73.92, -101.57) * mm});
            skLineSegment(sketch, "E9678", {"start": v(-73.92, -101.57) * mm, "end": v(-73.8, -102.18) * mm});
            skLineSegment(sketch, "E9679", {"start": v(-73.8, -102.18) * mm, "end": v(-73.68, -102.9) * mm});
            skLineSegment(sketch, "E9680", {"start": v(-73.68, -102.9) * mm, "end": v(-73.59, -103.72) * mm});
            skLineSegment(sketch, "E9681", {"start": v(-73.59, -103.72) * mm, "end": v(-73.59, -103.75) * mm});
            skArc(sketch, "E9682", {"start": v(-73.59, -103.75) * mm, "mid": v(-74.6, -104.3) * mm, "end": v(-75.63, -104.82) * mm});
            skLineSegment(sketch, "E9683", {"start": v(-75.63, -104.82) * mm, "end": v(-75.66, -104.8) * mm});
            skLineSegment(sketch, "E9684", {"start": v(-75.66, -104.8) * mm, "end": v(-76.28, -104.25) * mm});
            skLineSegment(sketch, "E9685", {"start": v(-76.28, -104.25) * mm, "end": v(-76.8, -103.75) * mm});
            skLineSegment(sketch, "E9686", {"start": v(-76.8, -103.75) * mm, "end": v(-77.23, -103.29) * mm});
            skLineSegment(sketch, "E9687", {"start": v(-77.23, -103.29) * mm, "end": v(-77.58, -102.88) * mm});
            skLineSegment(sketch, "E9688", {"start": v(-77.58, -102.88) * mm, "end": v(-77.84, -102.53) * mm});
            skLineSegment(sketch, "E9689", {"start": v(-77.84, -102.53) * mm, "end": v(-78.03, -102.25) * mm});
            skLineSegment(sketch, "E9690", {"start": v(-78.03, -102.25) * mm, "end": v(-78.16, -102.05) * mm});
            skLineSegment(sketch, "E9691", {"start": v(-78.16, -102.05) * mm, "end": v(-78.23, -101.92) * mm});
            skLineSegment(sketch, "E9692", {"start": v(-78.23, -101.92) * mm, "end": v(-78.25, -101.88) * mm});
            skLineSegment(sketch, "E9693", {"start": v(-78.25, -101.88) * mm, "end": v(-78.91, -100.4) * mm});
            skArc(sketch, "E9694", {"start": v(-78.91, -100.4) * mm, "mid": v(-80.4, -101.03) * mm, "end": v(-81.91, -101.6) * mm});
            skLineSegment(sketch, "E9695", {"start": v(-81.91, -101.6) * mm, "end": v(-81.37, -103.13) * mm});
            skLineSegment(sketch, "E9696", {"start": v(-81.37, -103.13) * mm, "end": v(-81.36, -103.17) * mm});
            skLineSegment(sketch, "E9697", {"start": v(-81.36, -103.17) * mm, "end": v(-81.32, -103.31) * mm});
            skLineSegment(sketch, "E9698", {"start": v(-81.32, -103.31) * mm, "end": v(-81.27, -103.55) * mm});
            skLineSegment(sketch, "E9699", {"start": v(-81.27, -103.55) * mm, "end": v(-81.22, -103.89) * mm});
            skLineSegment(sketch, "E9700", {"start": v(-81.22, -103.89) * mm, "end": v(-81.17, -104.32) * mm});
            skLineSegment(sketch, "E9701", {"start": v(-81.17, -104.32) * mm, "end": v(-81.14, -104.85) * mm});
            skLineSegment(sketch, "E9702", {"start": v(-81.14, -104.85) * mm, "end": v(-81.13, -105.48) * mm});
            skLineSegment(sketch, "E9703", {"start": v(-81.13, -105.48) * mm, "end": v(-81.16, -106.2) * mm});
            skLineSegment(sketch, "E9704", {"start": v(-81.16, -106.2) * mm, "end": v(-81.23, -107.02) * mm});
            skLineSegment(sketch, "E9705", {"start": v(-81.23, -107.02) * mm, "end": v(-81.23, -107.06) * mm});
            skArc(sketch, "E9706", {"start": v(-81.23, -107.06) * mm, "mid": v(-82.34, -107.4) * mm, "end": v(-83.45, -107.7) * mm});
            skLineSegment(sketch, "E9707", {"start": v(-83.45, -107.7) * mm, "end": v(-83.47, -107.68) * mm});
            skLineSegment(sketch, "E9708", {"start": v(-83.47, -107.68) * mm, "end": v(-83.97, -107.02) * mm});
            skLineSegment(sketch, "E9709", {"start": v(-83.97, -107.02) * mm, "end": v(-84.39, -106.43) * mm});
            skLineSegment(sketch, "E9710", {"start": v(-84.39, -106.43) * mm, "end": v(-84.72, -105.9) * mm});
            skLineSegment(sketch, "E9711", {"start": v(-84.72, -105.9) * mm, "end": v(-84.97, -105.42) * mm});
            skLineSegment(sketch, "E9712", {"start": v(-84.97, -105.42) * mm, "end": v(-85.17, -105.03) * mm});
            skLineSegment(sketch, "E9713", {"start": v(-85.17, -105.03) * mm, "end": v(-85.3, -104.72) * mm});
            skLineSegment(sketch, "E9714", {"start": v(-85.3, -104.72) * mm, "end": v(-85.38, -104.5) * mm});
            skLineSegment(sketch, "E9715", {"start": v(-85.38, -104.5) * mm, "end": v(-85.43, -104.36) * mm});
            skLineSegment(sketch, "E9716", {"start": v(-85.43, -104.36) * mm, "end": v(-85.44, -104.3) * mm});
            skLineSegment(sketch, "E9717", {"start": v(-85.44, -104.3) * mm, "end": v(-85.8, -102.73) * mm});
            skArc(sketch, "E9718", {"start": v(-85.8, -102.73) * mm, "mid": v(-87.39, -103.06) * mm, "end": v(-88.98, -103.32) * mm});
            skLineSegment(sketch, "E9719", {"start": v(-88.98, -103.32) * mm, "end": v(-88.75, -104.93) * mm});
            skLineSegment(sketch, "E9720", {"start": v(-88.75, -104.93) * mm, "end": v(-88.74, -104.98) * mm});
            skLineSegment(sketch, "E9721", {"start": v(-88.74, -104.98) * mm, "end": v(-88.74, -105.12) * mm});
            skLineSegment(sketch, "E9722", {"start": v(-88.74, -105.12) * mm, "end": v(-88.73, -105.36) * mm});
            skLineSegment(sketch, "E9723", {"start": v(-88.73, -105.36) * mm, "end": v(-88.74, -105.7) * mm});
            skLineSegment(sketch, "E9724", {"start": v(-88.74, -105.7) * mm, "end": v(-88.78, -106.13) * mm});
            skLineSegment(sketch, "E9725", {"start": v(-88.78, -106.13) * mm, "end": v(-88.85, -106.66) * mm});
            skLineSegment(sketch, "E9726", {"start": v(-88.85, -106.66) * mm, "end": v(-88.97, -107.28) * mm});
            skLineSegment(sketch, "E9727", {"start": v(-88.97, -107.28) * mm, "end": v(-89.14, -107.99) * mm});
            skLineSegment(sketch, "E9728", {"start": v(-89.14, -107.99) * mm, "end": v(-89.37, -108.78) * mm});
            skLineSegment(sketch, "E9729", {"start": v(-89.37, -108.78) * mm, "end": v(-89.38, -108.81) * mm});
            skArc(sketch, "E9730", {"start": v(-89.38, -108.81) * mm, "mid": v(-90.53, -108.93) * mm, "end": v(-91.68, -109.01) * mm});
            skLineSegment(sketch, "E9731", {"start": v(-91.68, -109.01) * mm, "end": v(-91.7, -108.98) * mm});
            skLineSegment(sketch, "E9732", {"start": v(-91.7, -108.98) * mm, "end": v(-92.06, -108.24) * mm});
            skLineSegment(sketch, "E9733", {"start": v(-92.06, -108.24) * mm, "end": v(-92.35, -107.57) * mm});
            skLineSegment(sketch, "E9734", {"start": v(-92.35, -107.57) * mm, "end": v(-92.57, -106.98) * mm});
            skLineSegment(sketch, "E9735", {"start": v(-92.57, -106.98) * mm, "end": v(-92.73, -106.48) * mm});
            skLineSegment(sketch, "E9736", {"start": v(-92.73, -106.48) * mm, "end": v(-92.84, -106.06) * mm});
            skLineSegment(sketch, "E9737", {"start": v(-92.84, -106.06) * mm, "end": v(-92.9, -105.72) * mm});
            skLineSegment(sketch, "E9738", {"start": v(-92.9, -105.72) * mm, "end": v(-92.95, -105.49) * mm});
            skLineSegment(sketch, "E9739", {"start": v(-92.95, -105.49) * mm, "end": v(-92.96, -105.34) * mm});
            skLineSegment(sketch, "E9740", {"start": v(-92.96, -105.34) * mm, "end": v(-92.97, -105.3) * mm});
            skLineSegment(sketch, "E9741", {"start": v(-92.97, -105.3) * mm, "end": v(-93.02, -103.67) * mm});
            skArc(sketch, "E9742", {"start": v(-93.02, -103.67) * mm, "mid": v(-94.63, -103.7) * mm, "end": v(-96.25, -103.64) * mm});
            skLineSegment(sketch, "E9743", {"start": v(-96.25, -103.64) * mm, "end": v(-96.33, -105.25) * mm});
            skLineSegment(sketch, "E9744", {"start": v(-96.33, -105.25) * mm, "end": v(-96.34, -105.3) * mm});
            skLineSegment(sketch, "E9745", {"start": v(-96.34, -105.3) * mm, "end": v(-96.36, -105.45) * mm});
            skLineSegment(sketch, "E9746", {"start": v(-96.36, -105.45) * mm, "end": v(-96.4, -105.68) * mm});
            skLineSegment(sketch, "E9747", {"start": v(-96.4, -105.68) * mm, "end": v(-96.48, -106.01) * mm});
            skLineSegment(sketch, "E9748", {"start": v(-96.48, -106.01) * mm, "end": v(-96.6, -106.43) * mm});
            skLineSegment(sketch, "E9749", {"start": v(-96.6, -106.43) * mm, "end": v(-96.77, -106.93) * mm});
            skLineSegment(sketch, "E9750", {"start": v(-96.77, -106.93) * mm, "end": v(-97, -107.52) * mm});
            skLineSegment(sketch, "E9751", {"start": v(-97, -107.52) * mm, "end": v(-97.31, -108.18) * mm});
            skLineSegment(sketch, "E9752", {"start": v(-97.31, -108.18) * mm, "end": v(-97.7, -108.9) * mm});
            skLineSegment(sketch, "E9753", {"start": v(-97.7, -108.9) * mm, "end": v(-97.71, -108.94) * mm});
            skArc(sketch, "E9754", {"start": v(-97.71, -108.94) * mm, "mid": v(-98.86, -108.83) * mm, "end": v(-100, -108.69) * mm});
            skLineSegment(sketch, "E9755", {"start": v(-100, -108.69) * mm, "end": v(-100.02, -108.65) * mm});
            skLineSegment(sketch, "E9756", {"start": v(-100.02, -108.65) * mm, "end": v(-100.23, -107.86) * mm});
            skLineSegment(sketch, "E9757", {"start": v(-100.23, -107.86) * mm, "end": v(-100.38, -107.15) * mm});
            skLineSegment(sketch, "E9758", {"start": v(-100.38, -107.15) * mm, "end": v(-100.48, -106.53) * mm});
            skLineSegment(sketch, "E9759", {"start": v(-100.48, -106.53) * mm, "end": v(-100.54, -106) * mm});
            skLineSegment(sketch, "E9760", {"start": v(-100.54, -106) * mm, "end": v(-100.57, -105.56) * mm});
            skLineSegment(sketch, "E9761", {"start": v(-100.57, -105.56) * mm, "end": v(-100.57, -105.22) * mm});
            skLineSegment(sketch, "E9762", {"start": v(-100.57, -105.22) * mm, "end": v(-100.56, -104.98) * mm});
            skLineSegment(sketch, "E9763", {"start": v(-100.56, -104.98) * mm, "end": v(-100.55, -104.84) * mm});
            skLineSegment(sketch, "E9764", {"start": v(-100.55, -104.84) * mm, "end": v(-100.54, -104.79) * mm});
            skLineSegment(sketch, "E9765", {"start": v(-100.54, -104.79) * mm, "end": v(-100.28, -103.2) * mm});
            skArc(sketch, "E9766", {"start": v(-100.28, -103.2) * mm, "mid": v(-101.86, -102.9) * mm, "end": v(-103.43, -102.53) * mm});
            skLineSegment(sketch, "E9767", {"start": v(-103.43, -102.53) * mm, "end": v(-103.84, -104.1) * mm});
            skLineSegment(sketch, "E9768", {"start": v(-103.84, -104.1) * mm, "end": v(-103.85, -104.14) * mm});
            skLineSegment(sketch, "E9769", {"start": v(-103.85, -104.14) * mm, "end": v(-103.9, -104.28) * mm});
            skLineSegment(sketch, "E9770", {"start": v(-103.9, -104.28) * mm, "end": v(-103.99, -104.5) * mm});
            skLineSegment(sketch, "E9771", {"start": v(-103.99, -104.5) * mm, "end": v(-104.13, -104.8) * mm});
            skLineSegment(sketch, "E9772", {"start": v(-104.13, -104.8) * mm, "end": v(-104.33, -105.2) * mm});
            skLineSegment(sketch, "E9773", {"start": v(-104.33, -105.2) * mm, "end": v(-104.6, -105.66) * mm});
            skLineSegment(sketch, "E9774", {"start": v(-104.6, -105.66) * mm, "end": v(-104.94, -106.18) * mm});
            skLineSegment(sketch, "E9775", {"start": v(-104.94, -106.18) * mm, "end": v(-105.37, -106.77) * mm});
            skLineSegment(sketch, "E9776", {"start": v(-105.37, -106.77) * mm, "end": v(-105.88, -107.41) * mm});
            skLineSegment(sketch, "E9777", {"start": v(-105.88, -107.41) * mm, "end": v(-105.9, -107.44) * mm});
            skArc(sketch, "E9778", {"start": v(-105.9, -107.44) * mm, "mid": v(-107.01, -107.1) * mm, "end": v(-108.1, -106.75) * mm});
            skLineSegment(sketch, "E9779", {"start": v(-108.1, -106.75) * mm, "end": v(-108.11, -106.7) * mm});
            skLineSegment(sketch, "E9780", {"start": v(-108.11, -106.7) * mm, "end": v(-108.16, -105.89) * mm});
            skLineSegment(sketch, "E9781", {"start": v(-108.16, -105.89) * mm, "end": v(-108.17, -105.16) * mm});
            skLineSegment(sketch, "E9782", {"start": v(-108.17, -105.16) * mm, "end": v(-108.15, -104.53) * mm});
            skLineSegment(sketch, "E9783", {"start": v(-108.15, -104.53) * mm, "end": v(-108.1, -104) * mm});
            skLineSegment(sketch, "E9784", {"start": v(-108.1, -104) * mm, "end": v(-108.05, -103.57) * mm});
            skLineSegment(sketch, "E9785", {"start": v(-108.05, -103.57) * mm, "end": v(-107.99, -103.24) * mm});
            skLineSegment(sketch, "E9786", {"start": v(-107.99, -103.24) * mm, "end": v(-107.93, -103) * mm});
            skLineSegment(sketch, "E9787", {"start": v(-107.93, -103) * mm, "end": v(-107.89, -102.86) * mm});
            skLineSegment(sketch, "E9788", {"start": v(-107.89, -102.86) * mm, "end": v(-107.87, -102.82) * mm});
            skLineSegment(sketch, "E9789", {"start": v(-107.87, -102.82) * mm, "end": v(-107.3, -101.3) * mm});
            skArc(sketch, "E9790", {"start": v(-107.3, -101.3) * mm, "mid": v(-108.8, -100.7) * mm, "end": v(-110.27, -100.03) * mm});
            skLineSegment(sketch, "E9791", {"start": v(-110.27, -100.03) * mm, "end": v(-110.97, -101.5) * mm});
            skLineSegment(sketch, "E9792", {"start": v(-110.97, -101.5) * mm, "end": v(-111, -101.53) * mm});
            skLineSegment(sketch, "E9793", {"start": v(-111, -101.53) * mm, "end": v(-111.06, -101.66) * mm});
            skLineSegment(sketch, "E9794", {"start": v(-111.06, -101.66) * mm, "end": v(-111.2, -101.86) * mm});
            skLineSegment(sketch, "E9795", {"start": v(-111.2, -101.86) * mm, "end": v(-111.4, -102.14) * mm});
            skLineSegment(sketch, "E9796", {"start": v(-111.4, -102.14) * mm, "end": v(-111.67, -102.48) * mm});
            skLineSegment(sketch, "E9797", {"start": v(-111.67, -102.48) * mm, "end": v(-112.02, -102.88) * mm});
            skLineSegment(sketch, "E9798", {"start": v(-112.02, -102.88) * mm, "end": v(-112.46, -103.33) * mm});
            skLineSegment(sketch, "E9799", {"start": v(-112.46, -103.33) * mm, "end": v(-113, -103.82) * mm});
            skLineSegment(sketch, "E9800", {"start": v(-113, -103.82) * mm, "end": v(-113.62, -104.35) * mm});
            skLineSegment(sketch, "E9801", {"start": v(-113.62, -104.35) * mm, "end": v(-113.65, -104.37) * mm});
            skArc(sketch, "E9802", {"start": v(-113.65, -104.37) * mm, "mid": v(-114.67, -103.83) * mm, "end": v(-115.67, -103.26) * mm});
            skLineSegment(sketch, "E9803", {"start": v(-115.67, -103.26) * mm, "end": v(-115.67, -103.22) * mm});
            skLineSegment(sketch, "E9804", {"start": v(-115.67, -103.22) * mm, "end": v(-115.56, -102.4) * mm});
            skLineSegment(sketch, "E9805", {"start": v(-115.56, -102.4) * mm, "end": v(-115.43, -101.7) * mm});
            skLineSegment(sketch, "E9806", {"start": v(-115.43, -101.7) * mm, "end": v(-115.29, -101.08) * mm});
            skLineSegment(sketch, "E9807", {"start": v(-115.29, -101.08) * mm, "end": v(-115.14, -100.57) * mm});
            skLineSegment(sketch, "E9808", {"start": v(-115.14, -100.57) * mm, "end": v(-115, -100.16) * mm});
            skLineSegment(sketch, "E9809", {"start": v(-115, -100.16) * mm, "end": v(-114.87, -99.84) * mm});
            skLineSegment(sketch, "E9810", {"start": v(-114.87, -99.84) * mm, "end": v(-114.77, -99.62) * mm});
            skLineSegment(sketch, "E9811", {"start": v(-114.77, -99.62) * mm, "end": v(-114.7, -99.5) * mm});
            skLineSegment(sketch, "E9812", {"start": v(-114.7, -99.5) * mm, "end": v(-114.68, -99.45) * mm});
            skLineSegment(sketch, "E9813", {"start": v(-114.68, -99.45) * mm, "end": v(-113.82, -98.08) * mm});
            skArc(sketch, "E9814", {"start": v(-113.82, -98.08) * mm, "mid": v(-115.17, -97.2) * mm, "end": v(-116.48, -96.25) * mm});
            skLineSegment(sketch, "E9815", {"start": v(-116.48, -96.25) * mm, "end": v(-117.46, -97.55) * mm});
            skLineSegment(sketch, "E9816", {"start": v(-117.46, -97.55) * mm, "end": v(-117.49, -97.59) * mm});
            skLineSegment(sketch, "E9817", {"start": v(-117.49, -97.59) * mm, "end": v(-117.58, -97.7) * mm});
            skLineSegment(sketch, "E9818", {"start": v(-117.58, -97.7) * mm, "end": v(-117.75, -97.87) * mm});
            skLineSegment(sketch, "E9819", {"start": v(-117.75, -97.87) * mm, "end": v(-118, -98.1) * mm});
            skLineSegment(sketch, "E9820", {"start": v(-118, -98.1) * mm, "end": v(-118.33, -98.38) * mm});
            skLineSegment(sketch, "E9821", {"start": v(-118.33, -98.38) * mm, "end": v(-118.76, -98.7) * mm});
            skLineSegment(sketch, "E9822", {"start": v(-118.76, -98.7) * mm, "end": v(-119.27, -99.06) * mm});
            skLineSegment(sketch, "E9823", {"start": v(-119.27, -99.06) * mm, "end": v(-119.9, -99.44) * mm});
            skLineSegment(sketch, "E9824", {"start": v(-119.9, -99.44) * mm, "end": v(-120.62, -99.83) * mm});
            skLineSegment(sketch, "E9825", {"start": v(-120.62, -99.83) * mm, "end": v(-120.65, -99.85) * mm});
            skArc(sketch, "E9826", {"start": v(-120.65, -99.85) * mm, "mid": v(-121.54, -99.12) * mm, "end": v(-122.42, -98.37) * mm});
            skLineSegment(sketch, "E9827", {"start": v(-122.42, -98.37) * mm, "end": v(-122.4, -98.33) * mm});
            skLineSegment(sketch, "E9828", {"start": v(-122.4, -98.33) * mm, "end": v(-122.14, -97.55) * mm});
            skLineSegment(sketch, "E9829", {"start": v(-122.14, -97.55) * mm, "end": v(-121.87, -96.88) * mm});
            skLineSegment(sketch, "E9830", {"start": v(-121.87, -96.88) * mm, "end": v(-121.61, -96.3) * mm});
            skLineSegment(sketch, "E9831", {"start": v(-121.61, -96.3) * mm, "end": v(-121.37, -95.83) * mm});
            skLineSegment(sketch, "E9832", {"start": v(-121.37, -95.83) * mm, "end": v(-121.15, -95.45) * mm});
            skLineSegment(sketch, "E9833", {"start": v(-121.15, -95.45) * mm, "end": v(-120.96, -95.17) * mm});
            skLineSegment(sketch, "E9834", {"start": v(-120.96, -95.17) * mm, "end": v(-120.82, -94.97) * mm});
            skLineSegment(sketch, "E9835", {"start": v(-120.82, -94.97) * mm, "end": v(-120.73, -94.86) * mm});
            skLineSegment(sketch, "E9836", {"start": v(-120.73, -94.86) * mm, "end": v(-120.7, -94.82) * mm});
            skLineSegment(sketch, "E9837", {"start": v(-120.7, -94.82) * mm, "end": v(-119.59, -93.64) * mm});
            skArc(sketch, "E9838", {"start": v(-119.59, -93.64) * mm, "mid": v(-120.74, -92.52) * mm, "end": v(-121.84, -91.34) * mm});
            skLineSegment(sketch, "E9839", {"start": v(-121.84, -91.34) * mm, "end": v(-123.05, -92.42) * mm});
            skLineSegment(sketch, "E9840", {"start": v(-123.05, -92.42) * mm, "end": v(-123.09, -92.45) * mm});
            skLineSegment(sketch, "E9841", {"start": v(-123.09, -92.45) * mm, "end": v(-123.2, -92.53) * mm});
            skLineSegment(sketch, "E9842", {"start": v(-123.2, -92.53) * mm, "end": v(-123.4, -92.67) * mm});
            skLineSegment(sketch, "E9843", {"start": v(-123.4, -92.67) * mm, "end": v(-123.69, -92.85) * mm});
            skLineSegment(sketch, "E9844", {"start": v(-123.69, -92.85) * mm, "end": v(-124.07, -93.06) * mm});
            skLineSegment(sketch, "E9845", {"start": v(-124.07, -93.06) * mm, "end": v(-124.55, -93.3) * mm});
            skLineSegment(sketch, "E9846", {"start": v(-124.55, -93.3) * mm, "end": v(-125.13, -93.54) * mm});
            skLineSegment(sketch, "E9847", {"start": v(-125.13, -93.54) * mm, "end": v(-125.8, -93.8) * mm});
            skLineSegment(sketch, "E9848", {"start": v(-125.8, -93.8) * mm, "end": v(-126.6, -94.04) * mm});
            skLineSegment(sketch, "E9849", {"start": v(-126.6, -94.04) * mm, "end": v(-126.63, -94.05) * mm});
            skArc(sketch, "E9850", {"start": v(-126.63, -94.05) * mm, "mid": v(-127.36, -93.16) * mm, "end": v(-128.07, -92.25) * mm});
            skLineSegment(sketch, "E9851", {"start": v(-128.07, -92.25) * mm, "end": v(-128.06, -92.22) * mm});
            skLineSegment(sketch, "E9852", {"start": v(-128.06, -92.22) * mm, "end": v(-127.64, -91.5) * mm});
            skLineSegment(sketch, "E9853", {"start": v(-127.64, -91.5) * mm, "end": v(-127.25, -90.9) * mm});
            skLineSegment(sketch, "E9854", {"start": v(-127.25, -90.9) * mm, "end": v(-126.88, -90.38) * mm});
            skLineSegment(sketch, "E9855", {"start": v(-126.88, -90.38) * mm, "end": v(-126.55, -89.97) * mm});
            skLineSegment(sketch, "E9856", {"start": v(-126.55, -89.97) * mm, "end": v(-126.26, -89.64) * mm});
            skLineSegment(sketch, "E9857", {"start": v(-126.26, -89.64) * mm, "end": v(-126.02, -89.4) * mm});
            skLineSegment(sketch, "E9858", {"start": v(-126.02, -89.4) * mm, "end": v(-125.85, -89.24) * mm});
            skLineSegment(sketch, "E9859", {"start": v(-125.85, -89.24) * mm, "end": v(-125.74, -89.14) * mm});
            skLineSegment(sketch, "E9860", {"start": v(-125.74, -89.14) * mm, "end": v(-125.7, -89.11) * mm});
            skLineSegment(sketch, "E9861", {"start": v(-125.7, -89.11) * mm, "end": v(-124.38, -88.17) * mm});
            skArc(sketch, "E9862", {"start": v(-124.38, -88.17) * mm, "mid": v(-125.3, -86.84) * mm, "end": v(-126.14, -85.47) * mm});
            skLineSegment(sketch, "E9863", {"start": v(-126.14, -85.47) * mm, "end": v(-127.53, -86.3) * mm});
            skLineSegment(sketch, "E9864", {"start": v(-127.53, -86.3) * mm, "end": v(-127.58, -86.31) * mm});
            skLineSegment(sketch, "E9865", {"start": v(-127.58, -86.31) * mm, "end": v(-127.7, -86.38) * mm});
            skLineSegment(sketch, "E9866", {"start": v(-127.7, -86.38) * mm, "end": v(-127.93, -86.47) * mm});
            skLineSegment(sketch, "E9867", {"start": v(-127.93, -86.47) * mm, "end": v(-128.25, -86.6) * mm});
            skLineSegment(sketch, "E9868", {"start": v(-128.25, -86.6) * mm, "end": v(-128.66, -86.72) * mm});
            skLineSegment(sketch, "E9869", {"start": v(-128.66, -86.72) * mm, "end": v(-129.18, -86.86) * mm});
            skLineSegment(sketch, "E9870", {"start": v(-129.18, -86.86) * mm, "end": v(-129.8, -86.99) * mm});
            skLineSegment(sketch, "E9871", {"start": v(-129.8, -86.99) * mm, "end": v(-130.5, -87.1) * mm});
            skLineSegment(sketch, "E9872", {"start": v(-130.5, -87.1) * mm, "end": v(-131.33, -87.2) * mm});
            skLineSegment(sketch, "E9873", {"start": v(-131.33, -87.2) * mm, "end": v(-131.37, -87.2) * mm});
            skArc(sketch, "E9874", {"start": v(-131.37, -87.2) * mm, "mid": v(-131.91, -86.18) * mm, "end": v(-132.43, -85.15) * mm});
            skLineSegment(sketch, "E9875", {"start": v(-132.43, -85.15) * mm, "end": v(-132.4, -85.12) * mm});
            skLineSegment(sketch, "E9876", {"start": v(-132.4, -85.12) * mm, "end": v(-131.86, -84.5) * mm});
            skLineSegment(sketch, "E9877", {"start": v(-131.86, -84.5) * mm, "end": v(-131.36, -83.98) * mm});
            skLineSegment(sketch, "E9878", {"start": v(-131.36, -83.98) * mm, "end": v(-130.9, -83.55) * mm});
            skLineSegment(sketch, "E9879", {"start": v(-130.9, -83.55) * mm, "end": v(-130.49, -83.2) * mm});
            skLineSegment(sketch, "E9880", {"start": v(-130.49, -83.2) * mm, "end": v(-130.14, -82.94) * mm});
            skLineSegment(sketch, "E9881", {"start": v(-130.14, -82.94) * mm, "end": v(-129.86, -82.75) * mm});
            skLineSegment(sketch, "E9882", {"start": v(-129.86, -82.75) * mm, "end": v(-129.66, -82.63) * mm});
            skLineSegment(sketch, "E9883", {"start": v(-129.66, -82.63) * mm, "end": v(-129.53, -82.56) * mm});
            skLineSegment(sketch, "E9884", {"start": v(-129.53, -82.56) * mm, "end": v(-129.49, -82.53) * mm});
            skLineSegment(sketch, "E9885", {"start": v(-129.49, -82.53) * mm, "end": v(-128.01, -81.87) * mm});
            skArc(sketch, "E9886", {"start": v(-128.01, -81.87) * mm, "mid": v(-128.64, -80.38) * mm, "end": v(-129.21, -78.87) * mm});
            skLineSegment(sketch, "E9887", {"start": v(-129.21, -78.87) * mm, "end": v(-130.74, -79.4) * mm});
            skLineSegment(sketch, "E9888", {"start": v(-130.74, -79.4) * mm, "end": v(-130.78, -79.42) * mm});
            skLineSegment(sketch, "E9889", {"start": v(-130.78, -79.42) * mm, "end": v(-130.92, -79.46) * mm});
            skLineSegment(sketch, "E9890", {"start": v(-130.92, -79.46) * mm, "end": v(-131.16, -79.51) * mm});
            skLineSegment(sketch, "E9891", {"start": v(-131.16, -79.51) * mm, "end": v(-131.5, -79.56) * mm});
            skLineSegment(sketch, "E9892", {"start": v(-131.5, -79.56) * mm, "end": v(-131.93, -79.61) * mm});
            skLineSegment(sketch, "E9893", {"start": v(-131.93, -79.61) * mm, "end": v(-132.46, -79.65) * mm});
            skLineSegment(sketch, "E9894", {"start": v(-132.46, -79.65) * mm, "end": v(-133.09, -79.65) * mm});
            skLineSegment(sketch, "E9895", {"start": v(-133.09, -79.65) * mm, "end": v(-133.81, -79.63) * mm});
            skLineSegment(sketch, "E9896", {"start": v(-133.81, -79.63) * mm, "end": v(-134.63, -79.55) * mm});
            skLineSegment(sketch, "E9897", {"start": v(-134.63, -79.55) * mm, "end": v(-134.67, -79.55) * mm});
            skArc(sketch, "E9898", {"start": v(-134.67, -79.55) * mm, "mid": v(-135, -78.44) * mm, "end": v(-135.32, -77.33) * mm});
            skLineSegment(sketch, "E9899", {"start": v(-135.32, -77.33) * mm, "end": v(-135.29, -77.3) * mm});
            skLineSegment(sketch, "E9900", {"start": v(-135.29, -77.3) * mm, "end": v(-134.63, -76.8) * mm});
            skLineSegment(sketch, "E9901", {"start": v(-134.63, -76.8) * mm, "end": v(-134.04, -76.4) * mm});
            skLineSegment(sketch, "E9902", {"start": v(-134.04, -76.4) * mm, "end": v(-133.5, -76.06) * mm});
            skLineSegment(sketch, "E9903", {"start": v(-133.5, -76.06) * mm, "end": v(-133.03, -75.8) * mm});
            skLineSegment(sketch, "E9904", {"start": v(-133.03, -75.8) * mm, "end": v(-132.64, -75.62) * mm});
            skLineSegment(sketch, "E9905", {"start": v(-132.64, -75.62) * mm, "end": v(-132.33, -75.48) * mm});
            skLineSegment(sketch, "E9906", {"start": v(-132.33, -75.48) * mm, "end": v(-132.1, -75.4) * mm});
            skLineSegment(sketch, "E9907", {"start": v(-132.1, -75.4) * mm, "end": v(-131.97, -75.36) * mm});
            skLineSegment(sketch, "E9908", {"start": v(-131.97, -75.36) * mm, "end": v(-131.92, -75.34) * mm});
            skLineSegment(sketch, "E9909", {"start": v(-131.92, -75.34) * mm, "end": v(-130.34, -74.98) * mm});
            skArc(sketch, "E9910", {"start": v(-130.34, -74.98) * mm, "mid": v(-130.67, -73.4) * mm, "end": v(-130.94, -71.8) * mm});
            skLineSegment(sketch, "E9911", {"start": v(-130.94, -71.8) * mm, "end": v(-132.54, -72.03) * mm});
            skLineSegment(sketch, "E9912", {"start": v(-132.54, -72.03) * mm, "end": v(-132.59, -72.04) * mm});
            skLineSegment(sketch, "E9913", {"start": v(-132.59, -72.04) * mm, "end": v(-132.73, -72.05) * mm});
            skLineSegment(sketch, "E9914", {"start": v(-132.73, -72.05) * mm, "end": v(-132.97, -72.05) * mm});
            skLineSegment(sketch, "E9915", {"start": v(-132.97, -72.05) * mm, "end": v(-133.31, -72.04) * mm});
            skLineSegment(sketch, "E9916", {"start": v(-133.31, -72.04) * mm, "end": v(-133.75, -72) * mm});
            skLineSegment(sketch, "E9917", {"start": v(-133.75, -72) * mm, "end": v(-134.27, -71.93) * mm});
            skLineSegment(sketch, "E9918", {"start": v(-134.27, -71.93) * mm, "end": v(-134.9, -71.81) * mm});
            skLineSegment(sketch, "E9919", {"start": v(-134.9, -71.81) * mm, "end": v(-135.6, -71.65) * mm});
            skLineSegment(sketch, "E9920", {"start": v(-135.6, -71.65) * mm, "end": v(-136.39, -71.42) * mm});
            skLineSegment(sketch, "E9921", {"start": v(-136.39, -71.42) * mm, "end": v(-136.42, -71.4) * mm});
            skArc(sketch, "E9922", {"start": v(-136.42, -71.4) * mm, "mid": v(-136.54, -70.25) * mm, "end": v(-136.62, -69.1) * mm});
            skLineSegment(sketch, "E9923", {"start": v(-136.62, -69.1) * mm, "end": v(-136.59, -69.09) * mm});
            skLineSegment(sketch, "E9924", {"start": v(-136.59, -69.09) * mm, "end": v(-135.85, -68.72) * mm});
            skLineSegment(sketch, "E9925", {"start": v(-135.85, -68.72) * mm, "end": v(-135.18, -68.43) * mm});
            skLineSegment(sketch, "E9926", {"start": v(-135.18, -68.43) * mm, "end": v(-134.6, -68.21) * mm});
            skLineSegment(sketch, "E9927", {"start": v(-134.6, -68.21) * mm, "end": v(-134.09, -68.05) * mm});
            skLineSegment(sketch, "E9928", {"start": v(-134.09, -68.05) * mm, "end": v(-133.67, -67.94) * mm});
            skLineSegment(sketch, "E9929", {"start": v(-133.67, -67.94) * mm, "end": v(-133.33, -67.87) * mm});
            skLineSegment(sketch, "E9930", {"start": v(-133.33, -67.87) * mm, "end": v(-133.1, -67.83) * mm});
            skLineSegment(sketch, "E9931", {"start": v(-133.1, -67.83) * mm, "end": v(-132.95, -67.82) * mm});
            skLineSegment(sketch, "E9932", {"start": v(-132.95, -67.82) * mm, "end": v(-132.9, -67.82) * mm});
            skLineSegment(sketch, "E9933", {"start": v(-132.9, -67.82) * mm, "end": v(-131.29, -67.76) * mm});
            skArc(sketch, "E9934", {"start": v(-131.29, -67.76) * mm, "mid": v(-131.3, -66.15) * mm, "end": v(-131.25, -64.54) * mm});
            skLineSegment(sketch, "E9935", {"start": v(-131.25, -64.54) * mm, "end": v(-132.86, -64.45) * mm});
            skLineSegment(sketch, "E9936", {"start": v(-132.86, -64.45) * mm, "end": v(-132.91, -64.44) * mm});
            skLineSegment(sketch, "E9937", {"start": v(-132.91, -64.44) * mm, "end": v(-133.06, -64.42) * mm});
            skLineSegment(sketch, "E9938", {"start": v(-133.06, -64.42) * mm, "end": v(-133.3, -64.38) * mm});
            skLineSegment(sketch, "E9939", {"start": v(-133.3, -64.38) * mm, "end": v(-133.62, -64.3) * mm});
            skLineSegment(sketch, "E9940", {"start": v(-133.62, -64.3) * mm, "end": v(-134.04, -64.18) * mm});
            skLineSegment(sketch, "E9941", {"start": v(-134.04, -64.18) * mm, "end": v(-134.55, -64) * mm});
            skLineSegment(sketch, "E9942", {"start": v(-134.55, -64) * mm, "end": v(-135.13, -63.78) * mm});
            skLineSegment(sketch, "E9943", {"start": v(-135.13, -63.78) * mm, "end": v(-135.79, -63.47) * mm});
            skLineSegment(sketch, "E9944", {"start": v(-135.79, -63.47) * mm, "end": v(-136.52, -63.1) * mm});
            skLineSegment(sketch, "E9945", {"start": v(-136.52, -63.1) * mm, "end": v(-136.55, -63.07) * mm});
            skArc(sketch, "E9946", {"start": v(-136.55, -63.07) * mm, "mid": v(-136.44, -61.92) * mm, "end": v(-136.3, -60.78) * mm});
            skLineSegment(sketch, "E9947", {"start": v(-136.3, -60.78) * mm, "end": v(-136.26, -60.77) * mm});
            skLineSegment(sketch, "E9948", {"start": v(-136.26, -60.77) * mm, "end": v(-135.47, -60.56) * mm});
            skLineSegment(sketch, "E9949", {"start": v(-135.47, -60.56) * mm, "end": v(-134.76, -60.4) * mm});
            skLineSegment(sketch, "E9950", {"start": v(-134.76, -60.4) * mm, "end": v(-134.14, -60.3) * mm});
            skLineSegment(sketch, "E9951", {"start": v(-134.14, -60.3) * mm, "end": v(-133.6, -60.24) * mm});
            skLineSegment(sketch, "E9952", {"start": v(-133.6, -60.24) * mm, "end": v(-133.17, -60.22) * mm});
            skLineSegment(sketch, "E9953", {"start": v(-133.17, -60.22) * mm, "end": v(-132.83, -60.21) * mm});
            skLineSegment(sketch, "E9954", {"start": v(-132.83, -60.21) * mm, "end": v(-132.6, -60.22) * mm});
            skLineSegment(sketch, "E9955", {"start": v(-132.6, -60.22) * mm, "end": v(-132.45, -60.23) * mm});
            skLineSegment(sketch, "E9956", {"start": v(-132.45, -60.23) * mm, "end": v(-132.4, -60.24) * mm});
            skLineSegment(sketch, "E9957", {"start": v(-132.4, -60.24) * mm, "end": v(-130.8, -60.5) * mm});
            skArc(sketch, "E9958", {"start": v(-130.8, -60.5) * mm, "mid": v(-130.5, -58.92) * mm, "end": v(-130.14, -57.35) * mm});
            skLineSegment(sketch, "E9959", {"start": v(-130.14, -57.35) * mm, "end": v(-131.7, -56.95) * mm});
            skLineSegment(sketch, "E9960", {"start": v(-131.7, -56.95) * mm, "end": v(-131.75, -56.93) * mm});
            skLineSegment(sketch, "E9961", {"start": v(-131.75, -56.93) * mm, "end": v(-131.89, -56.88) * mm});
            skLineSegment(sketch, "E9962", {"start": v(-131.89, -56.88) * mm, "end": v(-132.11, -56.8) * mm});
            skLineSegment(sketch, "E9963", {"start": v(-132.11, -56.8) * mm, "end": v(-132.42, -56.65) * mm});
            skLineSegment(sketch, "E9964", {"start": v(-132.42, -56.65) * mm, "end": v(-132.8, -56.45) * mm});
            skLineSegment(sketch, "E9965", {"start": v(-132.8, -56.45) * mm, "end": v(-133.27, -56.19) * mm});
            skLineSegment(sketch, "E9966", {"start": v(-133.27, -56.19) * mm, "end": v(-133.8, -55.84) * mm});
            skLineSegment(sketch, "E9967", {"start": v(-133.8, -55.84) * mm, "end": v(-134.38, -55.42) * mm});
            skLineSegment(sketch, "E9968", {"start": v(-134.38, -55.42) * mm, "end": v(-135.02, -54.9) * mm});
            skLineSegment(sketch, "E9969", {"start": v(-135.02, -54.9) * mm, "end": v(-135.05, -54.88) * mm});
            skArc(sketch, "E9970", {"start": v(-135.05, -54.88) * mm, "mid": v(-134.72, -53.77) * mm, "end": v(-134.36, -52.68) * mm});
            skLineSegment(sketch, "E9971", {"start": v(-134.36, -52.68) * mm, "end": v(-134.32, -52.67) * mm});
            skLineSegment(sketch, "E9972", {"start": v(-134.32, -52.67) * mm, "end": v(-133.5, -52.62) * mm});
            skLineSegment(sketch, "E9973", {"start": v(-133.5, -52.62) * mm, "end": v(-132.77, -52.6) * mm});
            skLineSegment(sketch, "E9974", {"start": v(-132.77, -52.6) * mm, "end": v(-132.14, -52.63) * mm});
            skLineSegment(sketch, "E9975", {"start": v(-132.14, -52.63) * mm, "end": v(-131.61, -52.68) * mm});
            skLineSegment(sketch, "E9976", {"start": v(-131.61, -52.68) * mm, "end": v(-131.18, -52.73) * mm});
            skLineSegment(sketch, "E9977", {"start": v(-131.18, -52.73) * mm, "end": v(-130.85, -52.8) * mm});
            skLineSegment(sketch, "E9978", {"start": v(-130.85, -52.8) * mm, "end": v(-130.61, -52.85) * mm});
            skLineSegment(sketch, "E9979", {"start": v(-130.61, -52.85) * mm, "end": v(-130.47, -52.9) * mm});
            skLineSegment(sketch, "E9980", {"start": v(-130.47, -52.9) * mm, "end": v(-130.43, -52.9) * mm});
            skLineSegment(sketch, "E9981", {"start": v(-130.43, -52.9) * mm, "end": v(-128.91, -53.48) * mm});
            skArc(sketch, "E9982", {"start": v(-128.91, -53.48) * mm, "mid": v(-128.31, -51.98) * mm, "end": v(-127.64, -50.51) * mm});
            skLineSegment(sketch, "E9983", {"start": v(-127.64, -50.51) * mm, "end": v(-129.1, -49.81) * mm});
            skLineSegment(sketch, "E9984", {"start": v(-129.1, -49.81) * mm, "end": v(-129.14, -49.8) * mm});
            skLineSegment(sketch, "E9985", {"start": v(-129.14, -49.8) * mm, "end": v(-129.27, -49.72) * mm});
            skLineSegment(sketch, "E9986", {"start": v(-129.27, -49.72) * mm, "end": v(-129.47, -49.59) * mm});
            skLineSegment(sketch, "E9987", {"start": v(-129.47, -49.59) * mm, "end": v(-129.75, -49.39) * mm});
            skLineSegment(sketch, "E9988", {"start": v(-129.75, -49.39) * mm, "end": v(-130.09, -49.12) * mm});
            skLineSegment(sketch, "E9989", {"start": v(-130.09, -49.12) * mm, "end": v(-130.49, -48.76) * mm});
            skLineSegment(sketch, "E9990", {"start": v(-130.49, -48.76) * mm, "end": v(-130.94, -48.32) * mm});
            skLineSegment(sketch, "E9991", {"start": v(-130.94, -48.32) * mm, "end": v(-131.43, -47.8) * mm});
            skLineSegment(sketch, "E9992", {"start": v(-131.43, -47.8) * mm, "end": v(-131.96, -47.16) * mm});
            skLineSegment(sketch, "E9993", {"start": v(-131.96, -47.16) * mm, "end": v(-131.98, -47.13) * mm});
            skArc(sketch, "E9994", {"start": v(-131.98, -47.13) * mm, "mid": v(-131.44, -46.11) * mm, "end": v(-130.87, -45.1) * mm});
            skLineSegment(sketch, "E9995", {"start": v(-130.87, -45.1) * mm, "end": v(-130.83, -45.11) * mm});
            skLineSegment(sketch, "E9996", {"start": v(-130.83, -45.11) * mm, "end": v(-130.02, -45.22) * mm});
            skLineSegment(sketch, "E9997", {"start": v(-130.02, -45.22) * mm, "end": v(-129.3, -45.35) * mm});
            skLineSegment(sketch, "E9998", {"start": v(-129.3, -45.35) * mm, "end": v(-128.7, -45.5) * mm});
            skLineSegment(sketch, "E9999", {"start": v(-128.7, -45.5) * mm, "end": v(-128.18, -45.64) * mm});
            skLineSegment(sketch, "E10000", {"start": v(-128.18, -45.64) * mm, "end": v(-127.77, -45.79) * mm});
            skLineSegment(sketch, "E10001", {"start": v(-127.77, -45.79) * mm, "end": v(-127.45, -45.91) * mm});
            skLineSegment(sketch, "E10002", {"start": v(-127.45, -45.91) * mm, "end": v(-127.23, -46.01) * mm});
            skLineSegment(sketch, "E10003", {"start": v(-127.23, -46.01) * mm, "end": v(-127.1, -46.08) * mm});
            skLineSegment(sketch, "E10004", {"start": v(-127.1, -46.08) * mm, "end": v(-127.06, -46.1) * mm});
            skLineSegment(sketch, "E10005", {"start": v(-127.06, -46.1) * mm, "end": v(-125.69, -46.96) * mm});
            skArc(sketch, "E10006", {"start": v(-125.69, -46.96) * mm, "mid": v(-124.8, -45.6) * mm, "end": v(-123.86, -44.3) * mm});
            skLineSegment(sketch, "E10007", {"start": v(-123.86, -44.3) * mm, "end": v(-125.16, -43.33) * mm});
            skLineSegment(sketch, "E10008", {"start": v(-125.16, -43.33) * mm, "end": v(-125.2, -43.3) * mm});
            skLineSegment(sketch, "E10009", {"start": v(-125.2, -43.3) * mm, "end": v(-125.3, -43.2) * mm});
            skLineSegment(sketch, "E10010", {"start": v(-125.3, -43.2) * mm, "end": v(-125.48, -43.03) * mm});
            skLineSegment(sketch, "E10011", {"start": v(-125.48, -43.03) * mm, "end": v(-125.71, -42.78) * mm});
            skLineSegment(sketch, "E10012", {"start": v(-125.71, -42.78) * mm, "end": v(-126, -42.45) * mm});
            skLineSegment(sketch, "E10013", {"start": v(-126, -42.45) * mm, "end": v(-126.31, -42.03) * mm});
            skLineSegment(sketch, "E10014", {"start": v(-126.31, -42.03) * mm, "end": v(-126.67, -41.5) * mm});
            skLineSegment(sketch, "E10015", {"start": v(-126.67, -41.5) * mm, "end": v(-127.05, -40.89) * mm});
            skLineSegment(sketch, "E10016", {"start": v(-127.05, -40.89) * mm, "end": v(-127.44, -40.17) * mm});
            skLineSegment(sketch, "E10017", {"start": v(-127.44, -40.17) * mm, "end": v(-127.46, -40.13) * mm});
            skArc(sketch, "E10018", {"start": v(-127.46, -40.13) * mm, "mid": v(-126.73, -39.24) * mm, "end": v(-125.98, -38.37) * mm});
            skLineSegment(sketch, "E10019", {"start": v(-125.98, -38.37) * mm, "end": v(-125.94, -38.38) * mm});
            skLineSegment(sketch, "E10020", {"start": v(-125.94, -38.38) * mm, "end": v(-125.16, -38.64) * mm});
            skLineSegment(sketch, "E10021", {"start": v(-125.16, -38.64) * mm, "end": v(-124.49, -38.91) * mm});
            skLineSegment(sketch, "E10022", {"start": v(-124.49, -38.91) * mm, "end": v(-123.91, -39.17) * mm});
            skLineSegment(sketch, "E10023", {"start": v(-123.91, -39.17) * mm, "end": v(-123.44, -39.42) * mm});
            skLineSegment(sketch, "E10024", {"start": v(-123.44, -39.42) * mm, "end": v(-123.06, -39.64) * mm});
            skLineSegment(sketch, "E10025", {"start": v(-123.06, -39.64) * mm, "end": v(-122.78, -39.82) * mm});
            skLineSegment(sketch, "E10026", {"start": v(-122.78, -39.82) * mm, "end": v(-122.58, -39.96) * mm});
            skLineSegment(sketch, "E10027", {"start": v(-122.58, -39.96) * mm, "end": v(-122.47, -40.05) * mm});
            skLineSegment(sketch, "E10028", {"start": v(-122.47, -40.05) * mm, "end": v(-122.44, -40.09) * mm});
            skLineSegment(sketch, "E10029", {"start": v(-122.44, -40.09) * mm, "end": v(-121.26, -41.2) * mm});
            skArc(sketch, "E10030", {"start": v(-121.26, -41.2) * mm, "mid": v(-120.13, -40.04) * mm, "end": v(-118.95, -38.94) * mm});
            skLineSegment(sketch, "E10031", {"start": v(-118.95, -38.94) * mm, "end": v(-120.03, -37.73) * mm});
            skLineSegment(sketch, "E10032", {"start": v(-120.03, -37.73) * mm, "end": v(-120.06, -37.7) * mm});
            skLineSegment(sketch, "E10033", {"start": v(-120.06, -37.7) * mm, "end": v(-120.15, -37.58) * mm});
            skLineSegment(sketch, "E10034", {"start": v(-120.15, -37.58) * mm, "end": v(-120.28, -37.38) * mm});
            skLineSegment(sketch, "E10035", {"start": v(-120.28, -37.38) * mm, "end": v(-120.46, -37.1) * mm});
            skLineSegment(sketch, "E10036", {"start": v(-120.46, -37.1) * mm, "end": v(-120.67, -36.71) * mm});
            skLineSegment(sketch, "E10037", {"start": v(-120.67, -36.71) * mm, "end": v(-120.9, -36.23) * mm});
            skLineSegment(sketch, "E10038", {"start": v(-120.9, -36.23) * mm, "end": v(-121.15, -35.65) * mm});
            skLineSegment(sketch, "E10039", {"start": v(-121.15, -35.65) * mm, "end": v(-121.4, -34.97) * mm});
            skLineSegment(sketch, "E10040", {"start": v(-121.4, -34.97) * mm, "end": v(-121.65, -34.19) * mm});
            skLineSegment(sketch, "E10041", {"start": v(-121.65, -34.19) * mm, "end": v(-121.66, -34.15) * mm});
            skArc(sketch, "E10042", {"start": v(-121.66, -34.15) * mm, "mid": v(-120.77, -33.42) * mm, "end": v(-119.86, -32.7) * mm});
            skLineSegment(sketch, "E10043", {"start": v(-119.86, -32.7) * mm, "end": v(-119.83, -32.73) * mm});
            skLineSegment(sketch, "E10044", {"start": v(-119.83, -32.73) * mm, "end": v(-119.11, -33.14) * mm});
            skLineSegment(sketch, "E10045", {"start": v(-119.11, -33.14) * mm, "end": v(-118.5, -33.53) * mm});
            skLineSegment(sketch, "E10046", {"start": v(-118.5, -33.53) * mm, "end": v(-118, -33.9) * mm});
            skLineSegment(sketch, "E10047", {"start": v(-118, -33.9) * mm, "end": v(-117.58, -34.23) * mm});
            skLineSegment(sketch, "E10048", {"start": v(-117.58, -34.23) * mm, "end": v(-117.25, -34.52) * mm});
            skLineSegment(sketch, "E10049", {"start": v(-117.25, -34.52) * mm, "end": v(-117, -34.76) * mm});
            skLineSegment(sketch, "E10050", {"start": v(-117, -34.76) * mm, "end": v(-116.85, -34.94) * mm});
            skLineSegment(sketch, "E10051", {"start": v(-116.85, -34.94) * mm, "end": v(-116.75, -35.05) * mm});
            skLineSegment(sketch, "E10052", {"start": v(-116.75, -35.05) * mm, "end": v(-116.72, -35.09) * mm});
            skLineSegment(sketch, "E10053", {"start": v(-116.72, -35.09) * mm, "end": v(-115.78, -36.4) * mm});
            skArc(sketch, "E10054", {"start": v(-115.78, -36.4) * mm, "mid": v(-114.45, -35.5) * mm, "end": v(-113.08, -34.64) * mm});
            skLineSegment(sketch, "E10055", {"start": v(-113.08, -34.64) * mm, "end": v(-113.9, -33.25) * mm});
            skLineSegment(sketch, "E10056", {"start": v(-113.9, -33.25) * mm, "end": v(-113.92, -33.2) * mm});
            skLineSegment(sketch, "E10057", {"start": v(-113.92, -33.2) * mm, "end": v(-113.99, -33.08) * mm});
            skLineSegment(sketch, "E10058", {"start": v(-113.99, -33.08) * mm, "end": v(-114.08, -32.85) * mm});
            skLineSegment(sketch, "E10059", {"start": v(-114.08, -32.85) * mm, "end": v(-114.2, -32.54) * mm});
            skLineSegment(sketch, "E10060", {"start": v(-114.2, -32.54) * mm, "end": v(-114.33, -32.12) * mm});
            skLineSegment(sketch, "E10061", {"start": v(-114.33, -32.12) * mm, "end": v(-114.47, -31.6) * mm});
            skLineSegment(sketch, "E10062", {"start": v(-114.47, -31.6) * mm, "end": v(-114.6, -30.99) * mm});
            skLineSegment(sketch, "E10063", {"start": v(-114.6, -30.99) * mm, "end": v(-114.71, -30.27) * mm});
            skLineSegment(sketch, "E10064", {"start": v(-114.71, -30.27) * mm, "end": v(-114.8, -29.45) * mm});
            skLineSegment(sketch, "E10065", {"start": v(-114.8, -29.45) * mm, "end": v(-114.8, -29.42) * mm});
            skArc(sketch, "E10066", {"start": v(-114.8, -29.42) * mm, "mid": v(-113.79, -28.87) * mm, "end": v(-112.76, -28.35) * mm});
            skLineSegment(sketch, "E10067", {"start": v(-112.76, -28.35) * mm, "end": v(-112.73, -28.38) * mm});
            skLineSegment(sketch, "E10068", {"start": v(-112.73, -28.38) * mm, "end": v(-112.11, -28.92) * mm});
            skLineSegment(sketch, "E10069", {"start": v(-112.11, -28.92) * mm, "end": v(-111.59, -29.43) * mm});
            skLineSegment(sketch, "E10070", {"start": v(-111.59, -29.43) * mm, "end": v(-111.16, -29.89) * mm});
            skLineSegment(sketch, "E10071", {"start": v(-111.16, -29.89) * mm, "end": v(-110.82, -30.3) * mm});
            skLineSegment(sketch, "E10072", {"start": v(-110.82, -30.3) * mm, "end": v(-110.55, -30.64) * mm});
            skLineSegment(sketch, "E10073", {"start": v(-110.55, -30.64) * mm, "end": v(-110.36, -30.92) * mm});
            skLineSegment(sketch, "E10074", {"start": v(-110.36, -30.92) * mm, "end": v(-110.24, -31.13) * mm});
            skLineSegment(sketch, "E10075", {"start": v(-110.24, -31.13) * mm, "end": v(-110.17, -31.25) * mm});
            skLineSegment(sketch, "E10076", {"start": v(-110.17, -31.25) * mm, "end": v(-110.14, -31.3) * mm});
            skLineSegment(sketch, "E10077", {"start": v(-110.14, -31.3) * mm, "end": v(-109.48, -32.77) * mm});
            skArc(sketch, "E10078", {"start": v(-109.48, -32.77) * mm, "mid": v(-108, -32.14) * mm, "end": v(-106.48, -31.57) * mm});
            skLineSegment(sketch, "E10079", {"start": v(-106.48, -31.57) * mm, "end": v(-107.02, -30.04) * mm});
            skLineSegment(sketch, "E10080", {"start": v(-107.02, -30.04) * mm, "end": v(-107.03, -30) * mm});
            skLineSegment(sketch, "E10081", {"start": v(-107.03, -30) * mm, "end": v(-107.07, -29.86) * mm});
            skLineSegment(sketch, "E10082", {"start": v(-107.07, -29.86) * mm, "end": v(-107.12, -29.62) * mm});
            skLineSegment(sketch, "E10083", {"start": v(-107.12, -29.62) * mm, "end": v(-107.17, -29.29) * mm});
            skLineSegment(sketch, "E10084", {"start": v(-107.17, -29.29) * mm, "end": v(-107.22, -28.85) * mm});
            skLineSegment(sketch, "E10085", {"start": v(-107.22, -28.85) * mm, "end": v(-107.26, -28.32) * mm});
            skLineSegment(sketch, "E10086", {"start": v(-107.26, -28.32) * mm, "end": v(-107.26, -27.7) * mm});
            skLineSegment(sketch, "E10087", {"start": v(-107.26, -27.7) * mm, "end": v(-107.24, -26.97) * mm});
            skLineSegment(sketch, "E10088", {"start": v(-107.24, -26.97) * mm, "end": v(-107.16, -26.15) * mm});
            skLineSegment(sketch, "E10089", {"start": v(-107.16, -26.15) * mm, "end": v(-107.16, -26.11) * mm});
            skArc(sketch, "E10090", {"start": v(-107.16, -26.11) * mm, "mid": v(-106.05, -25.77) * mm, "end": v(-104.94, -25.47) * mm});
            skLineSegment(sketch, "E10091", {"start": v(-104.94, -25.47) * mm, "end": v(-104.92, -25.5) * mm});
            skLineSegment(sketch, "E10092", {"start": v(-104.92, -25.5) * mm, "end": v(-104.42, -26.15) * mm});
            skLineSegment(sketch, "E10093", {"start": v(-104.42, -26.15) * mm, "end": v(-104, -26.75) * mm});
            skLineSegment(sketch, "E10094", {"start": v(-104, -26.75) * mm, "end": v(-103.67, -27.28) * mm});
            skLineSegment(sketch, "E10095", {"start": v(-103.67, -27.28) * mm, "end": v(-103.42, -27.75) * mm});
            skLineSegment(sketch, "E10096", {"start": v(-103.42, -27.75) * mm, "end": v(-103.23, -28.14) * mm});
            skLineSegment(sketch, "E10097", {"start": v(-103.23, -28.14) * mm, "end": v(-103.1, -28.45) * mm});
            skLineSegment(sketch, "E10098", {"start": v(-103.1, -28.45) * mm, "end": v(-103, -28.68) * mm});
            skLineSegment(sketch, "E10099", {"start": v(-103, -28.68) * mm, "end": v(-102.97, -28.82) * mm});
            skLineSegment(sketch, "E10100", {"start": v(-102.97, -28.82) * mm, "end": v(-102.95, -28.86) * mm});
            skLineSegment(sketch, "E10101", {"start": v(-102.95, -28.86) * mm, "end": v(-102.59, -30.44) * mm});
            skArc(sketch, "E10102", {"start": v(-102.59, -30.44) * mm, "mid": v(-101, -30.1) * mm, "end": v(-99.42, -29.85) * mm});
            skLineSegment(sketch, "E10103", {"start": v(-99.42, -29.85) * mm, "end": v(-99.64, -28.25) * mm});
            skLineSegment(sketch, "E10104", {"start": v(-99.64, -28.25) * mm, "end": v(-99.65, -28.2) * mm});
            skLineSegment(sketch, "E10105", {"start": v(-99.65, -28.2) * mm, "end": v(-99.66, -28.05) * mm});
            skLineSegment(sketch, "E10106", {"start": v(-99.66, -28.05) * mm, "end": v(-99.66, -27.81) * mm});
            skLineSegment(sketch, "E10107", {"start": v(-99.66, -27.81) * mm, "end": v(-99.65, -27.47) * mm});
            skLineSegment(sketch, "E10108", {"start": v(-99.65, -27.47) * mm, "end": v(-99.61, -27.04) * mm});
            skLineSegment(sketch, "E10109", {"start": v(-99.61, -27.04) * mm, "end": v(-99.54, -26.5) * mm});
            skLineSegment(sketch, "E10110", {"start": v(-99.54, -26.5) * mm, "end": v(-99.42, -25.9) * mm});
            skLineSegment(sketch, "E10111", {"start": v(-99.42, -25.9) * mm, "end": v(-99.26, -25.19) * mm});
            skLineSegment(sketch, "E10112", {"start": v(-99.26, -25.19) * mm, "end": v(-99.03, -24.4) * mm});
            skLineSegment(sketch, "E10113", {"start": v(-99.03, -24.4) * mm, "end": v(-99.01, -24.36) * mm});
            skArc(sketch, "E10114", {"start": v(-99.01, -24.36) * mm, "mid": v(-97.87, -24.24) * mm, "end": v(-96.71, -24.16) * mm});
            skLineSegment(sketch, "E10115", {"start": v(-96.71, -24.16) * mm, "end": v(-96.7, -24.2) * mm});
            skLineSegment(sketch, "E10116", {"start": v(-96.7, -24.2) * mm, "end": v(-96.33, -24.93) * mm});
            skLineSegment(sketch, "E10117", {"start": v(-96.33, -24.93) * mm, "end": v(-96.05, -25.6) * mm});
            skLineSegment(sketch, "E10118", {"start": v(-96.05, -25.6) * mm, "end": v(-95.82, -26.19) * mm});
            skLineSegment(sketch, "E10119", {"start": v(-95.82, -26.19) * mm, "end": v(-95.66, -26.7) * mm});
            skLineSegment(sketch, "E10120", {"start": v(-95.66, -26.7) * mm, "end": v(-95.55, -27.12) * mm});
            skLineSegment(sketch, "E10121", {"start": v(-95.55, -27.12) * mm, "end": v(-95.48, -27.45) * mm});
            skLineSegment(sketch, "E10122", {"start": v(-95.48, -27.45) * mm, "end": v(-95.44, -27.69) * mm});
            skLineSegment(sketch, "E10123", {"start": v(-95.44, -27.69) * mm, "end": v(-95.43, -27.83) * mm});
            skLineSegment(sketch, "E10124", {"start": v(-95.43, -27.83) * mm, "end": v(-95.43, -27.88) * mm});
            skLineSegment(sketch, "E10125", {"start": v(-95.43, -27.88) * mm, "end": v(-95.37, -29.5) * mm});
            skArc(sketch, "E10126", {"start": v(-95.37, -29.5) * mm, "mid": v(-93.76, -29.48) * mm, "end": v(-92.15, -29.54) * mm});
            skLineSegment(sketch, "E10127", {"start": v(-92.15, -29.54) * mm, "end": v(-92.06, -27.92) * mm});
            skLineSegment(sketch, "E10128", {"start": v(-92.06, -27.92) * mm, "end": v(-92.05, -27.87) * mm});
            skLineSegment(sketch, "E10129", {"start": v(-92.05, -27.87) * mm, "end": v(-92.03, -27.73) * mm});
            skLineSegment(sketch, "E10130", {"start": v(-92.03, -27.73) * mm, "end": v(-92, -27.49) * mm});
            skLineSegment(sketch, "E10131", {"start": v(-92, -27.49) * mm, "end": v(-91.91, -27.16) * mm});
            skLineSegment(sketch, "E10132", {"start": v(-91.91, -27.16) * mm, "end": v(-91.8, -26.74) * mm});
            skLineSegment(sketch, "E10133", {"start": v(-91.8, -26.74) * mm, "end": v(-91.62, -26.24) * mm});
            skLineSegment(sketch, "E10134", {"start": v(-91.62, -26.24) * mm, "end": v(-91.39, -25.65) * mm});
            skLineSegment(sketch, "E10135", {"start": v(-91.39, -25.65) * mm, "end": v(-91.08, -25) * mm});
            skLineSegment(sketch, "E10136", {"start": v(-91.08, -25) * mm, "end": v(-90.7, -24.26) * mm});
            skLineSegment(sketch, "E10137", {"start": v(-90.7, -24.26) * mm, "end": v(-90.68, -24.23) * mm});
            skArc(sketch, "E10138", {"start": v(-90.68, -24.23) * mm, "mid": v(-89.53, -24.34) * mm, "end": v(-88.39, -24.48) * mm});
            skLineSegment(sketch, "E10139", {"start": v(-88.39, -24.48) * mm, "end": v(-88.38, -24.52) * mm});
            skLineSegment(sketch, "E10140", {"start": v(-88.38, -24.52) * mm, "end": v(-88.17, -25.32) * mm});
            skLineSegment(sketch, "E10141", {"start": v(-88.17, -25.32) * mm, "end": v(-88.01, -26.03) * mm});
            skLineSegment(sketch, "E10142", {"start": v(-88.01, -26.03) * mm, "end": v(-87.91, -26.65) * mm});
            skLineSegment(sketch, "E10143", {"start": v(-87.91, -26.65) * mm, "end": v(-87.85, -27.18) * mm});
            skLineSegment(sketch, "E10144", {"start": v(-87.85, -27.18) * mm, "end": v(-87.83, -27.61) * mm});
            skLineSegment(sketch, "E10145", {"start": v(-87.83, -27.61) * mm, "end": v(-87.82, -27.95) * mm});
            skLineSegment(sketch, "E10146", {"start": v(-87.82, -27.95) * mm, "end": v(-87.83, -28.2) * mm});
            skLineSegment(sketch, "E10147", {"start": v(-87.83, -28.2) * mm, "end": v(-87.84, -28.34) * mm});
            skLineSegment(sketch, "E10148", {"start": v(-87.84, -28.34) * mm, "end": v(-87.85, -28.38) * mm});
            skLineSegment(sketch, "E10149", {"start": v(-87.85, -28.38) * mm, "end": v(-88.12, -29.98) * mm});
            skArc(sketch, "E10150", {"start": v(-88.12, -29.98) * mm, "mid": v(-86.53, -30.28) * mm, "end": v(-84.96, -30.65) * mm});
            skLineSegment(sketch, "E10151", {"start": v(-84.96, -30.65) * mm, "end": v(-84.56, -29.08) * mm});
            skLineSegment(sketch, "E10152", {"start": v(-84.56, -29.08) * mm, "end": v(-84.54, -29.03) * mm});
            skLineSegment(sketch, "E10153", {"start": v(-84.54, -29.03) * mm, "end": v(-84.5, -28.9) * mm});
            skLineSegment(sketch, "E10154", {"start": v(-84.5, -28.9) * mm, "end": v(-84.4, -28.67) * mm});
            skLineSegment(sketch, "E10155", {"start": v(-84.4, -28.67) * mm, "end": v(-84.27, -28.36) * mm});
            skLineSegment(sketch, "E10156", {"start": v(-84.27, -28.36) * mm, "end": v(-84.07, -27.98) * mm});
            skLineSegment(sketch, "E10157", {"start": v(-84.07, -27.98) * mm, "end": v(-83.8, -27.52) * mm});
            skLineSegment(sketch, "E10158", {"start": v(-83.8, -27.52) * mm, "end": v(-83.45, -26.99) * mm});
            skLineSegment(sketch, "E10159", {"start": v(-83.45, -26.99) * mm, "end": v(-83.03, -26.4) * mm});
            skLineSegment(sketch, "E10160", {"start": v(-83.03, -26.4) * mm, "end": v(-82.51, -25.76) * mm});
            skLineSegment(sketch, "E10161", {"start": v(-82.51, -25.76) * mm, "end": v(-82.49, -25.73) * mm});
            skArc(sketch, "E10162", {"start": v(-82.49, -25.73) * mm, "mid": v(-81.38, -26.06) * mm, "end": v(-80.29, -26.43) * mm});
            skLineSegment(sketch, "E10163", {"start": v(-80.29, -26.43) * mm, "end": v(-80.28, -26.46) * mm});
            skLineSegment(sketch, "E10164", {"start": v(-80.28, -26.46) * mm, "end": v(-80.23, -27.29) * mm});
            skLineSegment(sketch, "E10165", {"start": v(-80.23, -27.29) * mm, "end": v(-80.22, -28.01) * mm});
            skLineSegment(sketch, "E10166", {"start": v(-80.22, -28.01) * mm, "end": v(-80.24, -28.64) * mm});
            skLineSegment(sketch, "E10167", {"start": v(-80.24, -28.64) * mm, "end": v(-80.29, -29.17) * mm});
            skLineSegment(sketch, "E10168", {"start": v(-80.29, -29.17) * mm, "end": v(-80.35, -29.6) * mm});
            skLineSegment(sketch, "E10169", {"start": v(-80.35, -29.6) * mm, "end": v(-80.4, -29.94) * mm});
            skLineSegment(sketch, "E10170", {"start": v(-80.4, -29.94) * mm, "end": v(-80.46, -30.17) * mm});
            skLineSegment(sketch, "E10171", {"start": v(-80.46, -30.17) * mm, "end": v(-80.5, -30.3) * mm});
            skLineSegment(sketch, "E10172", {"start": v(-80.5, -30.3) * mm, "end": v(-80.52, -30.36) * mm});
            skLineSegment(sketch, "E10173", {"start": v(-80.52, -30.36) * mm, "end": v(-81.1, -31.87) * mm});
            skArc(sketch, "E10174", {"start": v(-81.1, -31.87) * mm, "mid": v(-79.6, -32.47) * mm, "end": v(-78.12, -33.14) * mm});
            skLineSegment(sketch, "E10175", {"start": v(-78.12, -33.14) * mm, "end": v(-77.42, -31.68) * mm});
            skLineSegment(sketch, "E10176", {"start": v(-77.42, -31.68) * mm, "end": v(-77.4, -31.64) * mm});
            skLineSegment(sketch, "E10177", {"start": v(-77.4, -31.64) * mm, "end": v(-77.33, -31.51) * mm});
            skLineSegment(sketch, "E10178", {"start": v(-77.33, -31.51) * mm, "end": v(-77.2, -31.3) * mm});
            skLineSegment(sketch, "E10179", {"start": v(-77.2, -31.3) * mm, "end": v(-77, -31.03) * mm});
            skLineSegment(sketch, "E10180", {"start": v(-77, -31.03) * mm, "end": v(-76.73, -30.7) * mm});
            skLineSegment(sketch, "E10181", {"start": v(-76.73, -30.7) * mm, "end": v(-76.37, -30.3) * mm});
            skLineSegment(sketch, "E10182", {"start": v(-76.37, -30.3) * mm, "end": v(-75.93, -29.84) * mm});
            skLineSegment(sketch, "E10183", {"start": v(-75.93, -29.84) * mm, "end": v(-75.4, -29.35) * mm});
            skLineSegment(sketch, "E10184", {"start": v(-75.4, -29.35) * mm, "end": v(-74.77, -28.82) * mm});
            skLineSegment(sketch, "E10185", {"start": v(-74.77, -28.82) * mm, "end": v(-74.74, -28.8) * mm});
            skArc(sketch, "E10186", {"start": v(-74.74, -28.8) * mm, "mid": v(-73.72, -29.34) * mm, "end": v(-72.72, -29.91) * mm});
            skLineSegment(sketch, "E10187", {"start": v(-72.72, -29.91) * mm, "end": v(-72.72, -29.95) * mm});
            skLineSegment(sketch, "E10188", {"start": v(-72.72, -29.95) * mm, "end": v(-72.83, -30.76) * mm});
            skLineSegment(sketch, "E10189", {"start": v(-72.83, -30.76) * mm, "end": v(-72.96, -31.48) * mm});
            skLineSegment(sketch, "E10190", {"start": v(-72.96, -31.48) * mm, "end": v(-73.1, -32.1) * mm});
            skLineSegment(sketch, "E10191", {"start": v(-73.1, -32.1) * mm, "end": v(-73.25, -32.6) * mm});
            skLineSegment(sketch, "E10192", {"start": v(-73.25, -32.6) * mm, "end": v(-73.4, -33.01) * mm});
            skLineSegment(sketch, "E10193", {"start": v(-73.4, -33.01) * mm, "end": v(-73.52, -33.33) * mm});
            skLineSegment(sketch, "E10194", {"start": v(-73.52, -33.33) * mm, "end": v(-73.62, -33.55) * mm});
            skLineSegment(sketch, "E10195", {"start": v(-73.62, -33.55) * mm, "end": v(-73.7, -33.68) * mm});
            skLineSegment(sketch, "E10196", {"start": v(-73.7, -33.68) * mm, "end": v(-73.71, -33.72) * mm});
            skLineSegment(sketch, "E10197", {"start": v(-73.71, -33.72) * mm, "end": v(-74.57, -35.1) * mm});
            skArc(sketch, "E10198", {"start": v(-74.57, -35.1) * mm, "mid": v(-73.22, -35.98) * mm, "end": v(-71.9, -36.92) * mm});
            skLineSegment(sketch, "E10199", {"start": v(-71.9, -36.92) * mm, "end": v(-70.94, -35.62) * mm});
            skLineSegment(sketch, "E10200", {"start": v(-70.94, -35.62) * mm, "end": v(-70.9, -35.59) * mm});
            skLineSegment(sketch, "E10201", {"start": v(-70.9, -35.59) * mm, "end": v(-70.81, -35.48) * mm});
            skLineSegment(sketch, "E10202", {"start": v(-70.81, -35.48) * mm, "end": v(-70.64, -35.3) * mm});
            skLineSegment(sketch, "E10203", {"start": v(-70.64, -35.3) * mm, "end": v(-70.4, -35.07) * mm});
            skLineSegment(sketch, "E10204", {"start": v(-70.4, -35.07) * mm, "end": v(-70.06, -34.8) * mm});
            skLineSegment(sketch, "E10205", {"start": v(-70.06, -34.8) * mm, "end": v(-69.64, -34.47) * mm});
            skLineSegment(sketch, "E10206", {"start": v(-69.64, -34.47) * mm, "end": v(-69.12, -34.11) * mm});
            skLineSegment(sketch, "E10207", {"start": v(-69.12, -34.11) * mm, "end": v(-68.5, -33.73) * mm});
            skLineSegment(sketch, "E10208", {"start": v(-68.5, -33.73) * mm, "end": v(-67.78, -33.34) * mm});
            skLineSegment(sketch, "E10209", {"start": v(-67.78, -33.34) * mm, "end": v(-67.74, -33.32) * mm});
            skArc(sketch, "E10210", {"start": v(-67.74, -33.32) * mm, "mid": v(-66.85, -34.05) * mm, "end": v(-65.98, -34.8) * mm});
            skLineSegment(sketch, "E10211", {"start": v(-65.98, -34.8) * mm, "end": v(-65.99, -34.84) * mm});
            skLineSegment(sketch, "E10212", {"start": v(-65.99, -34.84) * mm, "end": v(-66.25, -35.62) * mm});
            skLineSegment(sketch, "E10213", {"start": v(-66.25, -35.62) * mm, "end": v(-66.52, -36.3) * mm});
            skLineSegment(sketch, "E10214", {"start": v(-66.52, -36.3) * mm, "end": v(-66.78, -36.87) * mm});
            skLineSegment(sketch, "E10215", {"start": v(-66.78, -36.87) * mm, "end": v(-67.03, -37.34) * mm});
            skLineSegment(sketch, "E10216", {"start": v(-67.03, -37.34) * mm, "end": v(-67.25, -37.72) * mm});
            skLineSegment(sketch, "E10217", {"start": v(-67.25, -37.72) * mm, "end": v(-67.43, -38) * mm});
            skLineSegment(sketch, "E10218", {"start": v(-67.43, -38) * mm, "end": v(-67.57, -38.2) * mm});
            skLineSegment(sketch, "E10219", {"start": v(-67.57, -38.2) * mm, "end": v(-67.66, -38.31) * mm});
            skLineSegment(sketch, "E10220", {"start": v(-67.66, -38.31) * mm, "end": v(-67.7, -38.35) * mm});
            skLineSegment(sketch, "E10221", {"start": v(-67.7, -38.35) * mm, "end": v(-68.8, -39.53) * mm});
            skArc(sketch, "E10222", {"start": v(-68.8, -39.53) * mm, "mid": v(-67.65, -40.66) * mm, "end": v(-66.55, -41.84) * mm});
            skCircle(sketch, "E10223", {"center": v(-94.2, -66.59) * mm, "radius": 1.25 * mm});
            skLineSegment(sketch, "E10224", {"start": v(-97.2, -68.69) * mm, "end": v(-91.2, -68.69) * mm});
            skLineSegment(sketch, "E10225", {"start": v(-91.2, -68.69) * mm, "end": v(-91.2, -64.49) * mm});
            skLineSegment(sketch, "E10226", {"start": v(-91.2, -64.49) * mm, "end": v(-97.2, -64.49) * mm});
            skLineSegment(sketch, "E10227", {"start": v(-97.2, -64.49) * mm, "end": v(-97.2, -68.69) * mm});
            skCircle(sketch, "E10228", {"center": v(-94.2, -66.59) * mm, "radius": 3.75 * mm});
            skCircle(sketch, "E10229", {"center": v(5.8, -66.59) * mm, "radius": 1.25 * mm});
            skLineSegment(sketch, "E10230", {"start": v(2.8, -68.65) * mm, "end": v(8.8, -68.65) * mm});
            skLineSegment(sketch, "E10231", {"start": v(8.8, -68.65) * mm, "end": v(8.8, -64.52) * mm});
            skLineSegment(sketch, "E10232", {"start": v(8.8, -64.52) * mm, "end": v(2.8, -64.52) * mm});
            skLineSegment(sketch, "E10233", {"start": v(2.8, -64.52) * mm, "end": v(2.8, -68.65) * mm});
            skCircle(sketch, "E10234", {"center": v(5.8, -66.59) * mm, "radius": 3.75 * mm});
            skLineSegment(sketch, "E10235", {"start": v(31.44, -43.69) * mm, "end": v(32.7, -42.56) * mm});
            skLineSegment(sketch, "E10236", {"start": v(32.7, -42.56) * mm, "end": v(32.73, -42.54) * mm});
            skLineSegment(sketch, "E10237", {"start": v(32.73, -42.54) * mm, "end": v(32.84, -42.45) * mm});
            skLineSegment(sketch, "E10238", {"start": v(32.84, -42.45) * mm, "end": v(33.02, -42.33) * mm});
            skLineSegment(sketch, "E10239", {"start": v(33.02, -42.33) * mm, "end": v(33.3, -42.16) * mm});
            skLineSegment(sketch, "E10240", {"start": v(33.3, -42.16) * mm, "end": v(33.65, -41.96) * mm});
            skLineSegment(sketch, "E10241", {"start": v(33.65, -41.96) * mm, "end": v(34.1, -41.74) * mm});
            skLineSegment(sketch, "E10242", {"start": v(34.1, -41.74) * mm, "end": v(34.64, -41.51) * mm});
            skLineSegment(sketch, "E10243", {"start": v(34.64, -41.51) * mm, "end": v(35.27, -41.28) * mm});
            skLineSegment(sketch, "E10244", {"start": v(35.27, -41.28) * mm, "end": v(36, -41.04) * mm});
            skLineSegment(sketch, "E10245", {"start": v(36, -41.04) * mm, "end": v(36.2, -40.99) * mm});
            skLineSegment(sketch, "E10246", {"start": v(36.2, -40.99) * mm, "end": v(37.64, -42.74) * mm});
            skLineSegment(sketch, "E10247", {"start": v(37.64, -42.74) * mm, "end": v(37.55, -42.92) * mm});
            skLineSegment(sketch, "E10248", {"start": v(37.55, -42.92) * mm, "end": v(37.16, -43.58) * mm});
            skLineSegment(sketch, "E10249", {"start": v(37.16, -43.58) * mm, "end": v(36.8, -44.14) * mm});
            skLineSegment(sketch, "E10250", {"start": v(36.8, -44.14) * mm, "end": v(36.45, -44.61) * mm});
            skLineSegment(sketch, "E10251", {"start": v(36.45, -44.61) * mm, "end": v(36.13, -45) * mm});
            skLineSegment(sketch, "E10252", {"start": v(36.13, -45) * mm, "end": v(35.86, -45.3) * mm});
            skLineSegment(sketch, "E10253", {"start": v(35.86, -45.3) * mm, "end": v(35.64, -45.52) * mm});
            skLineSegment(sketch, "E10254", {"start": v(35.64, -45.52) * mm, "end": v(35.48, -45.68) * mm});
            skLineSegment(sketch, "E10255", {"start": v(35.48, -45.68) * mm, "end": v(35.37, -45.76) * mm});
            skLineSegment(sketch, "E10256", {"start": v(35.37, -45.76) * mm, "end": v(35.34, -45.79) * mm});
            skLineSegment(sketch, "E10257", {"start": v(35.34, -45.79) * mm, "end": v(33.95, -46.76) * mm});
            skLineSegment(sketch, "E10258", {"start": v(33.95, -46.76) * mm, "end": v(35.71, -49.44) * mm});
            skLineSegment(sketch, "E10259", {"start": v(35.71, -49.44) * mm, "end": v(37.18, -48.6) * mm});
            skLineSegment(sketch, "E10260", {"start": v(37.18, -48.6) * mm, "end": v(37.22, -48.57) * mm});
            skLineSegment(sketch, "E10261", {"start": v(37.22, -48.57) * mm, "end": v(37.34, -48.52) * mm});
            skLineSegment(sketch, "E10262", {"start": v(37.34, -48.52) * mm, "end": v(37.55, -48.43) * mm});
            skLineSegment(sketch, "E10263", {"start": v(37.55, -48.43) * mm, "end": v(37.85, -48.32) * mm});
            skLineSegment(sketch, "E10264", {"start": v(37.85, -48.32) * mm, "end": v(38.24, -48.2) * mm});
            skLineSegment(sketch, "E10265", {"start": v(38.24, -48.2) * mm, "end": v(38.72, -48.08) * mm});
            skLineSegment(sketch, "E10266", {"start": v(38.72, -48.08) * mm, "end": v(39.3, -47.96) * mm});
            skLineSegment(sketch, "E10267", {"start": v(39.3, -47.96) * mm, "end": v(39.97, -47.86) * mm});
            skLineSegment(sketch, "E10268", {"start": v(39.97, -47.86) * mm, "end": v(40.74, -47.79) * mm});
            skLineSegment(sketch, "E10269", {"start": v(40.74, -47.79) * mm, "end": v(40.95, -47.77) * mm});
            skLineSegment(sketch, "E10270", {"start": v(40.95, -47.77) * mm, "end": v(41.98, -49.78) * mm});
            skLineSegment(sketch, "E10271", {"start": v(41.98, -49.78) * mm, "end": v(41.85, -49.94) * mm});
            skLineSegment(sketch, "E10272", {"start": v(41.85, -49.94) * mm, "end": v(41.33, -50.5) * mm});
            skLineSegment(sketch, "E10273", {"start": v(41.33, -50.5) * mm, "end": v(40.85, -50.98) * mm});
            skLineSegment(sketch, "E10274", {"start": v(40.85, -50.98) * mm, "end": v(40.41, -51.37) * mm});
            skLineSegment(sketch, "E10275", {"start": v(40.41, -51.37) * mm, "end": v(40.03, -51.68) * mm});
            skLineSegment(sketch, "E10276", {"start": v(40.03, -51.68) * mm, "end": v(39.7, -51.92) * mm});
            skLineSegment(sketch, "E10277", {"start": v(39.7, -51.92) * mm, "end": v(39.44, -52.1) * mm});
            skLineSegment(sketch, "E10278", {"start": v(39.44, -52.1) * mm, "end": v(39.24, -52.2) * mm});
            skLineSegment(sketch, "E10279", {"start": v(39.24, -52.2) * mm, "end": v(39.12, -52.27) * mm});
            skLineSegment(sketch, "E10280", {"start": v(39.12, -52.27) * mm, "end": v(39.08, -52.29) * mm});
            skLineSegment(sketch, "E10281", {"start": v(39.08, -52.29) * mm, "end": v(37.52, -52.96) * mm});
            skLineSegment(sketch, "E10282", {"start": v(37.52, -52.96) * mm, "end": v(38.68, -55.94) * mm});
            skLineSegment(sketch, "E10283", {"start": v(38.68, -55.94) * mm, "end": v(40.3, -55.41) * mm});
            skLineSegment(sketch, "E10284", {"start": v(40.3, -55.41) * mm, "end": v(40.33, -55.4) * mm});
            skLineSegment(sketch, "E10285", {"start": v(40.33, -55.4) * mm, "end": v(40.47, -55.37) * mm});
            skLineSegment(sketch, "E10286", {"start": v(40.47, -55.37) * mm, "end": v(40.69, -55.33) * mm});
            skLineSegment(sketch, "E10287", {"start": v(40.69, -55.33) * mm, "end": v(41, -55.28) * mm});
            skLineSegment(sketch, "E10288", {"start": v(41, -55.28) * mm, "end": v(41.41, -55.25) * mm});
            skLineSegment(sketch, "E10289", {"start": v(41.41, -55.25) * mm, "end": v(41.9, -55.22) * mm});
            skLineSegment(sketch, "E10290", {"start": v(41.9, -55.22) * mm, "end": v(42.5, -55.23) * mm});
            skLineSegment(sketch, "E10291", {"start": v(42.5, -55.23) * mm, "end": v(43.18, -55.27) * mm});
            skLineSegment(sketch, "E10292", {"start": v(43.18, -55.27) * mm, "end": v(43.95, -55.35) * mm});
            skLineSegment(sketch, "E10293", {"start": v(43.95, -55.35) * mm, "end": v(44.15, -55.38) * mm});
            skLineSegment(sketch, "E10294", {"start": v(44.15, -55.38) * mm, "end": v(44.74, -57.55) * mm});
            skLineSegment(sketch, "E10295", {"start": v(44.74, -57.55) * mm, "end": v(44.58, -57.68) * mm});
            skLineSegment(sketch, "E10296", {"start": v(44.58, -57.68) * mm, "end": v(43.95, -58.13) * mm});
            skLineSegment(sketch, "E10297", {"start": v(43.95, -58.13) * mm, "end": v(43.38, -58.5) * mm});
            skLineSegment(sketch, "E10298", {"start": v(43.38, -58.5) * mm, "end": v(42.87, -58.79) * mm});
            skLineSegment(sketch, "E10299", {"start": v(42.87, -58.79) * mm, "end": v(42.43, -59.01) * mm});
            skLineSegment(sketch, "E10300", {"start": v(42.43, -59.01) * mm, "end": v(42.06, -59.18) * mm});
            skLineSegment(sketch, "E10301", {"start": v(42.06, -59.18) * mm, "end": v(41.76, -59.3) * mm});
            skLineSegment(sketch, "E10302", {"start": v(41.76, -59.3) * mm, "end": v(41.55, -59.37) * mm});
            skLineSegment(sketch, "E10303", {"start": v(41.55, -59.37) * mm, "end": v(41.42, -59.4) * mm});
            skLineSegment(sketch, "E10304", {"start": v(41.42, -59.4) * mm, "end": v(41.37, -59.42) * mm});
            skLineSegment(sketch, "E10305", {"start": v(41.37, -59.42) * mm, "end": v(39.7, -59.75) * mm});
            skLineSegment(sketch, "E10306", {"start": v(39.7, -59.75) * mm, "end": v(40.2, -62.9) * mm});
            skLineSegment(sketch, "E10307", {"start": v(40.2, -62.9) * mm, "end": v(41.9, -62.72) * mm});
            skLineSegment(sketch, "E10308", {"start": v(41.9, -62.72) * mm, "end": v(41.94, -62.72) * mm});
            skLineSegment(sketch, "E10309", {"start": v(41.94, -62.72) * mm, "end": v(42.08, -62.71) * mm});
            skLineSegment(sketch, "E10310", {"start": v(42.08, -62.71) * mm, "end": v(42.3, -62.72) * mm});
            skLineSegment(sketch, "E10311", {"start": v(42.3, -62.72) * mm, "end": v(42.62, -62.74) * mm});
            skLineSegment(sketch, "E10312", {"start": v(42.62, -62.74) * mm, "end": v(43.03, -62.78) * mm});
            skLineSegment(sketch, "E10313", {"start": v(43.03, -62.78) * mm, "end": v(43.52, -62.87) * mm});
            skLineSegment(sketch, "E10314", {"start": v(43.52, -62.87) * mm, "end": v(44.1, -63) * mm});
            skLineSegment(sketch, "E10315", {"start": v(44.1, -63) * mm, "end": v(44.75, -63.17) * mm});
            skLineSegment(sketch, "E10316", {"start": v(44.75, -63.17) * mm, "end": v(45.48, -63.4) * mm});
            skLineSegment(sketch, "E10317", {"start": v(45.48, -63.4) * mm, "end": v(45.68, -63.48) * mm});
            skLineSegment(sketch, "E10318", {"start": v(45.68, -63.48) * mm, "end": v(45.8, -65.72) * mm});
            skLineSegment(sketch, "E10319", {"start": v(45.8, -65.72) * mm, "end": v(45.6, -65.82) * mm});
            skLineSegment(sketch, "E10320", {"start": v(45.6, -65.82) * mm, "end": v(44.9, -66.13) * mm});
            skLineSegment(sketch, "E10321", {"start": v(44.9, -66.13) * mm, "end": v(44.27, -66.37) * mm});
            skLineSegment(sketch, "E10322", {"start": v(44.27, -66.37) * mm, "end": v(43.7, -66.55) * mm});
            skLineSegment(sketch, "E10323", {"start": v(43.7, -66.55) * mm, "end": v(43.23, -66.68) * mm});
            skLineSegment(sketch, "E10324", {"start": v(43.23, -66.68) * mm, "end": v(42.83, -66.77) * mm});
            skLineSegment(sketch, "E10325", {"start": v(42.83, -66.77) * mm, "end": v(42.51, -66.82) * mm});
            skLineSegment(sketch, "E10326", {"start": v(42.51, -66.82) * mm, "end": v(42.29, -66.84) * mm});
            skLineSegment(sketch, "E10327", {"start": v(42.29, -66.84) * mm, "end": v(42.15, -66.85) * mm});
            skLineSegment(sketch, "E10328", {"start": v(42.15, -66.85) * mm, "end": v(42.1, -66.86) * mm});
            skLineSegment(sketch, "E10329", {"start": v(42.1, -66.86) * mm, "end": v(40.41, -66.84) * mm});
            skLineSegment(sketch, "E10330", {"start": v(40.41, -66.84) * mm, "end": v(40.23, -70.02) * mm});
            skLineSegment(sketch, "E10331", {"start": v(40.23, -70.02) * mm, "end": v(41.92, -70.2) * mm});
            skLineSegment(sketch, "E10332", {"start": v(41.92, -70.2) * mm, "end": v(41.97, -70.2) * mm});
            skLineSegment(sketch, "E10333", {"start": v(41.97, -70.2) * mm, "end": v(42.1, -70.22) * mm});
            skLineSegment(sketch, "E10334", {"start": v(42.1, -70.22) * mm, "end": v(42.32, -70.27) * mm});
            skLineSegment(sketch, "E10335", {"start": v(42.32, -70.27) * mm, "end": v(42.63, -70.36) * mm});
            skLineSegment(sketch, "E10336", {"start": v(42.63, -70.36) * mm, "end": v(43.02, -70.49) * mm});
            skLineSegment(sketch, "E10337", {"start": v(43.02, -70.49) * mm, "end": v(43.48, -70.67) * mm});
            skLineSegment(sketch, "E10338", {"start": v(43.48, -70.67) * mm, "end": v(44.02, -70.9) * mm});
            skLineSegment(sketch, "E10339", {"start": v(44.02, -70.9) * mm, "end": v(44.62, -71.22) * mm});
            skLineSegment(sketch, "E10340", {"start": v(44.62, -71.22) * mm, "end": v(45.29, -71.6) * mm});
            skLineSegment(sketch, "E10341", {"start": v(45.29, -71.6) * mm, "end": v(45.46, -71.71) * mm});
            skLineSegment(sketch, "E10342", {"start": v(45.46, -71.71) * mm, "end": v(45.1, -73.93) * mm});
            skLineSegment(sketch, "E10343", {"start": v(45.1, -73.93) * mm, "end": v(44.9, -73.98) * mm});
            skLineSegment(sketch, "E10344", {"start": v(44.9, -73.98) * mm, "end": v(44.15, -74.14) * mm});
            skLineSegment(sketch, "E10345", {"start": v(44.15, -74.14) * mm, "end": v(43.47, -74.25) * mm});
            skLineSegment(sketch, "E10346", {"start": v(43.47, -74.25) * mm, "end": v(42.89, -74.3) * mm});
            skLineSegment(sketch, "E10347", {"start": v(42.89, -74.3) * mm, "end": v(42.39, -74.34) * mm});
            skLineSegment(sketch, "E10348", {"start": v(42.39, -74.34) * mm, "end": v(41.98, -74.34) * mm});
            skLineSegment(sketch, "E10349", {"start": v(41.98, -74.34) * mm, "end": v(41.66, -74.33) * mm});
            skLineSegment(sketch, "E10350", {"start": v(41.66, -74.33) * mm, "end": v(41.44, -74.3) * mm});
            skLineSegment(sketch, "E10351", {"start": v(41.44, -74.3) * mm, "end": v(41.3, -74.3) * mm});
            skLineSegment(sketch, "E10352", {"start": v(41.3, -74.3) * mm, "end": v(41.26, -74.28) * mm});
            skLineSegment(sketch, "E10353", {"start": v(41.26, -74.28) * mm, "end": v(39.6, -73.92) * mm});
            skLineSegment(sketch, "E10354", {"start": v(39.6, -73.92) * mm, "end": v(38.76, -77) * mm});
            skLineSegment(sketch, "E10355", {"start": v(38.76, -77) * mm, "end": v(40.37, -77.51) * mm});
            skLineSegment(sketch, "E10356", {"start": v(40.37, -77.51) * mm, "end": v(40.42, -77.53) * mm});
            skLineSegment(sketch, "E10357", {"start": v(40.42, -77.53) * mm, "end": v(40.54, -77.58) * mm});
            skLineSegment(sketch, "E10358", {"start": v(40.54, -77.58) * mm, "end": v(40.75, -77.67) * mm});
            skLineSegment(sketch, "E10359", {"start": v(40.75, -77.67) * mm, "end": v(41.03, -77.82) * mm});
            skLineSegment(sketch, "E10360", {"start": v(41.03, -77.82) * mm, "end": v(41.38, -78.02) * mm});
            skLineSegment(sketch, "E10361", {"start": v(41.38, -78.02) * mm, "end": v(41.8, -78.3) * mm});
            skLineSegment(sketch, "E10362", {"start": v(41.8, -78.3) * mm, "end": v(42.27, -78.64) * mm});
            skLineSegment(sketch, "E10363", {"start": v(42.27, -78.64) * mm, "end": v(42.8, -79.06) * mm});
            skLineSegment(sketch, "E10364", {"start": v(42.8, -79.06) * mm, "end": v(43.37, -79.57) * mm});
            skLineSegment(sketch, "E10365", {"start": v(43.37, -79.57) * mm, "end": v(43.52, -79.72) * mm});
            skLineSegment(sketch, "E10366", {"start": v(43.52, -79.72) * mm, "end": v(42.7, -81.82) * mm});
            skLineSegment(sketch, "E10367", {"start": v(42.7, -81.82) * mm, "end": v(42.48, -81.83) * mm});
            skLineSegment(sketch, "E10368", {"start": v(42.48, -81.83) * mm, "end": v(41.71, -81.83) * mm});
            skLineSegment(sketch, "E10369", {"start": v(41.71, -81.83) * mm, "end": v(41.03, -81.8) * mm});
            skLineSegment(sketch, "E10370", {"start": v(41.03, -81.8) * mm, "end": v(40.45, -81.73) * mm});
            skLineSegment(sketch, "E10371", {"start": v(40.45, -81.73) * mm, "end": v(39.95, -81.66) * mm});
            skLineSegment(sketch, "E10372", {"start": v(39.95, -81.66) * mm, "end": v(39.55, -81.58) * mm});
            skLineSegment(sketch, "E10373", {"start": v(39.55, -81.58) * mm, "end": v(39.24, -81.5) * mm});
            skLineSegment(sketch, "E10374", {"start": v(39.24, -81.5) * mm, "end": v(39.03, -81.44) * mm});
            skLineSegment(sketch, "E10375", {"start": v(39.03, -81.44) * mm, "end": v(38.9, -81.4) * mm});
            skLineSegment(sketch, "E10376", {"start": v(38.9, -81.4) * mm, "end": v(38.86, -81.37) * mm});
            skLineSegment(sketch, "E10377", {"start": v(38.86, -81.37) * mm, "end": v(37.31, -80.68) * mm});
            skLineSegment(sketch, "E10378", {"start": v(37.31, -80.68) * mm, "end": v(35.84, -83.52) * mm});
            skLineSegment(sketch, "E10379", {"start": v(35.84, -83.52) * mm, "end": v(37.31, -84.35) * mm});
            skLineSegment(sketch, "E10380", {"start": v(37.31, -84.35) * mm, "end": v(37.35, -84.37) * mm});
            skLineSegment(sketch, "E10381", {"start": v(37.35, -84.37) * mm, "end": v(37.46, -84.45) * mm});
            skLineSegment(sketch, "E10382", {"start": v(37.46, -84.45) * mm, "end": v(37.64, -84.58) * mm});
            skLineSegment(sketch, "E10383", {"start": v(37.64, -84.58) * mm, "end": v(37.89, -84.78) * mm});
            skLineSegment(sketch, "E10384", {"start": v(37.89, -84.78) * mm, "end": v(38.19, -85.06) * mm});
            skLineSegment(sketch, "E10385", {"start": v(38.19, -85.06) * mm, "end": v(38.54, -85.4) * mm});
            skLineSegment(sketch, "E10386", {"start": v(38.54, -85.4) * mm, "end": v(38.93, -85.84) * mm});
            skLineSegment(sketch, "E10387", {"start": v(38.93, -85.84) * mm, "end": v(39.35, -86.37) * mm});
            skLineSegment(sketch, "E10388", {"start": v(39.35, -86.37) * mm, "end": v(39.8, -86.98) * mm});
            skLineSegment(sketch, "E10389", {"start": v(39.8, -86.98) * mm, "end": v(39.92, -87.15) * mm});
            skLineSegment(sketch, "E10390", {"start": v(39.92, -87.15) * mm, "end": v(38.67, -89.04) * mm});
            skLineSegment(sketch, "E10391", {"start": v(38.67, -89.04) * mm, "end": v(38.47, -89) * mm});
            skLineSegment(sketch, "E10392", {"start": v(38.47, -89) * mm, "end": v(37.71, -88.85) * mm});
            skLineSegment(sketch, "E10393", {"start": v(37.71, -88.85) * mm, "end": v(37.05, -88.67) * mm});
            skLineSegment(sketch, "E10394", {"start": v(37.05, -88.67) * mm, "end": v(36.5, -88.5) * mm});
            skLineSegment(sketch, "E10395", {"start": v(36.5, -88.5) * mm, "end": v(36.02, -88.32) * mm});
            skLineSegment(sketch, "E10396", {"start": v(36.02, -88.32) * mm, "end": v(35.65, -88.16) * mm});
            skLineSegment(sketch, "E10397", {"start": v(35.65, -88.16) * mm, "end": v(35.36, -88.02) * mm});
            skLineSegment(sketch, "E10398", {"start": v(35.36, -88.02) * mm, "end": v(35.17, -87.92) * mm});
            skLineSegment(sketch, "E10399", {"start": v(35.17, -87.92) * mm, "end": v(35.05, -87.84) * mm});
            skLineSegment(sketch, "E10400", {"start": v(35.05, -87.84) * mm, "end": v(35.01, -87.82) * mm});
            skLineSegment(sketch, "E10401", {"start": v(35.01, -87.82) * mm, "end": v(33.65, -86.83) * mm});
            skLineSegment(sketch, "E10402", {"start": v(33.65, -86.83) * mm, "end": v(31.6, -89.3) * mm});
            skLineSegment(sketch, "E10403", {"start": v(31.6, -89.3) * mm, "end": v(32.87, -90.41) * mm});
            skLineSegment(sketch, "E10404", {"start": v(32.87, -90.41) * mm, "end": v(32.9, -90.44) * mm});
            skLineSegment(sketch, "E10405", {"start": v(32.9, -90.44) * mm, "end": v(33, -90.54) * mm});
            skLineSegment(sketch, "E10406", {"start": v(33, -90.54) * mm, "end": v(33.15, -90.7) * mm});
            skLineSegment(sketch, "E10407", {"start": v(33.15, -90.7) * mm, "end": v(33.34, -90.96) * mm});
            skLineSegment(sketch, "E10408", {"start": v(33.34, -90.96) * mm, "end": v(33.58, -91.28) * mm});
            skLineSegment(sketch, "E10409", {"start": v(33.58, -91.28) * mm, "end": v(33.85, -91.7) * mm});
            skLineSegment(sketch, "E10410", {"start": v(33.85, -91.7) * mm, "end": v(34.14, -92.2) * mm});
            skLineSegment(sketch, "E10411", {"start": v(34.14, -92.2) * mm, "end": v(34.44, -92.8) * mm});
            skLineSegment(sketch, "E10412", {"start": v(34.44, -92.8) * mm, "end": v(34.76, -93.5) * mm});
            skLineSegment(sketch, "E10413", {"start": v(34.76, -93.5) * mm, "end": v(34.83, -93.69) * mm});
            skLineSegment(sketch, "E10414", {"start": v(34.83, -93.69) * mm, "end": v(33.21, -95.28) * mm});
            skLineSegment(sketch, "E10415", {"start": v(33.21, -95.28) * mm, "end": v(33.02, -95.2) * mm});
            skLineSegment(sketch, "E10416", {"start": v(33.02, -95.2) * mm, "end": v(32.31, -94.9) * mm});
            skLineSegment(sketch, "E10417", {"start": v(32.31, -94.9) * mm, "end": v(31.7, -94.59) * mm});
            skLineSegment(sketch, "E10418", {"start": v(31.7, -94.59) * mm, "end": v(31.2, -94.3) * mm});
            skLineSegment(sketch, "E10419", {"start": v(31.2, -94.3) * mm, "end": v(30.77, -94.04) * mm});
            skLineSegment(sketch, "E10420", {"start": v(30.77, -94.04) * mm, "end": v(30.44, -93.8) * mm});
            skLineSegment(sketch, "E10421", {"start": v(30.44, -93.8) * mm, "end": v(30.2, -93.6) * mm});
            skLineSegment(sketch, "E10422", {"start": v(30.2, -93.6) * mm, "end": v(30.02, -93.46) * mm});
            skLineSegment(sketch, "E10423", {"start": v(30.02, -93.46) * mm, "end": v(29.92, -93.37) * mm});
            skLineSegment(sketch, "E10424", {"start": v(29.92, -93.37) * mm, "end": v(29.9, -93.34) * mm});
            skLineSegment(sketch, "E10425", {"start": v(29.9, -93.34) * mm, "end": v(28.77, -92.08) * mm});
            skLineSegment(sketch, "E10426", {"start": v(28.77, -92.08) * mm, "end": v(26.25, -94.09) * mm});
            skLineSegment(sketch, "E10427", {"start": v(26.25, -94.09) * mm, "end": v(27.25, -95.43) * mm});
            skLineSegment(sketch, "E10428", {"start": v(27.25, -95.43) * mm, "end": v(27.28, -95.47) * mm});
            skLineSegment(sketch, "E10429", {"start": v(27.28, -95.47) * mm, "end": v(27.35, -95.59) * mm});
            skLineSegment(sketch, "E10430", {"start": v(27.35, -95.59) * mm, "end": v(27.46, -95.78) * mm});
            skLineSegment(sketch, "E10431", {"start": v(27.46, -95.78) * mm, "end": v(27.6, -96.06) * mm});
            skLineSegment(sketch, "E10432", {"start": v(27.6, -96.06) * mm, "end": v(27.76, -96.43) * mm});
            skLineSegment(sketch, "E10433", {"start": v(27.76, -96.43) * mm, "end": v(27.93, -96.9) * mm});
            skLineSegment(sketch, "E10434", {"start": v(27.93, -96.9) * mm, "end": v(28.11, -97.45) * mm});
            skLineSegment(sketch, "E10435", {"start": v(28.11, -97.45) * mm, "end": v(28.28, -98.1) * mm});
            skLineSegment(sketch, "E10436", {"start": v(28.28, -98.1) * mm, "end": v(28.44, -98.84) * mm});
            skLineSegment(sketch, "E10437", {"start": v(28.44, -98.84) * mm, "end": v(28.47, -99.04) * mm});
            skLineSegment(sketch, "E10438", {"start": v(28.47, -99.04) * mm, "end": v(26.56, -100.26) * mm});
            skLineSegment(sketch, "E10439", {"start": v(26.56, -100.26) * mm, "end": v(26.38, -100.15) * mm});
            skLineSegment(sketch, "E10440", {"start": v(26.38, -100.15) * mm, "end": v(25.76, -99.7) * mm});
            skLineSegment(sketch, "E10441", {"start": v(25.76, -99.7) * mm, "end": v(25.23, -99.28) * mm});
            skLineSegment(sketch, "E10442", {"start": v(25.23, -99.28) * mm, "end": v(24.79, -98.9) * mm});
            skLineSegment(sketch, "E10443", {"start": v(24.79, -98.9) * mm, "end": v(24.43, -98.55) * mm});
            skLineSegment(sketch, "E10444", {"start": v(24.43, -98.55) * mm, "end": v(24.16, -98.25) * mm});
            skLineSegment(sketch, "E10445", {"start": v(24.16, -98.25) * mm, "end": v(23.96, -98.01) * mm});
            skLineSegment(sketch, "E10446", {"start": v(23.96, -98.01) * mm, "end": v(23.82, -97.83) * mm});
            skLineSegment(sketch, "E10447", {"start": v(23.82, -97.83) * mm, "end": v(23.74, -97.72) * mm});
            skLineSegment(sketch, "E10448", {"start": v(23.74, -97.72) * mm, "end": v(23.72, -97.68) * mm});
            skLineSegment(sketch, "E10449", {"start": v(23.72, -97.68) * mm, "end": v(22.88, -96.23) * mm});
            skLineSegment(sketch, "E10450", {"start": v(22.88, -96.23) * mm, "end": v(20, -97.67) * mm});
            skLineSegment(sketch, "E10451", {"start": v(20, -97.67) * mm, "end": v(20.7, -99.2) * mm});
            skLineSegment(sketch, "E10452", {"start": v(20.7, -99.2) * mm, "end": v(20.7, -99.24) * mm});
            skLineSegment(sketch, "E10453", {"start": v(20.7, -99.24) * mm, "end": v(20.75, -99.36) * mm});
            skLineSegment(sketch, "E10454", {"start": v(20.75, -99.36) * mm, "end": v(20.82, -99.58) * mm});
            skLineSegment(sketch, "E10455", {"start": v(20.82, -99.58) * mm, "end": v(20.9, -99.88) * mm});
            skLineSegment(sketch, "E10456", {"start": v(20.9, -99.88) * mm, "end": v(20.98, -100.27) * mm});
            skLineSegment(sketch, "E10457", {"start": v(20.98, -100.27) * mm, "end": v(21.05, -100.76) * mm});
            skLineSegment(sketch, "E10458", {"start": v(21.05, -100.76) * mm, "end": v(21.1, -101.34) * mm});
            skLineSegment(sketch, "E10459", {"start": v(21.1, -101.34) * mm, "end": v(21.14, -102) * mm});
            skLineSegment(sketch, "E10460", {"start": v(21.14, -102) * mm, "end": v(21.14, -102.77) * mm});
            skLineSegment(sketch, "E10461", {"start": v(21.14, -102.77) * mm, "end": v(21.13, -102.97) * mm});
            skLineSegment(sketch, "E10462", {"start": v(21.13, -102.97) * mm, "end": v(19, -103.78) * mm});
            skLineSegment(sketch, "E10463", {"start": v(19, -103.78) * mm, "end": v(18.85, -103.63) * mm});
            skLineSegment(sketch, "E10464", {"start": v(18.85, -103.63) * mm, "end": v(18.33, -103.06) * mm});
            skLineSegment(sketch, "E10465", {"start": v(18.33, -103.06) * mm, "end": v(17.9, -102.54) * mm});
            skLineSegment(sketch, "E10466", {"start": v(17.9, -102.54) * mm, "end": v(17.55, -102.08) * mm});
            skLineSegment(sketch, "E10467", {"start": v(17.55, -102.08) * mm, "end": v(17.28, -101.67) * mm});
            skLineSegment(sketch, "E10468", {"start": v(17.28, -101.67) * mm, "end": v(17.07, -101.32) * mm});
            skLineSegment(sketch, "E10469", {"start": v(17.07, -101.32) * mm, "end": v(16.92, -101.04) * mm});
            skLineSegment(sketch, "E10470", {"start": v(16.92, -101.04) * mm, "end": v(16.83, -100.84) * mm});
            skLineSegment(sketch, "E10471", {"start": v(16.83, -100.84) * mm, "end": v(16.78, -100.71) * mm});
            skLineSegment(sketch, "E10472", {"start": v(16.78, -100.71) * mm, "end": v(16.76, -100.67) * mm});
            skLineSegment(sketch, "E10473", {"start": v(16.76, -100.67) * mm, "end": v(16.25, -99.08) * mm});
            skLineSegment(sketch, "E10474", {"start": v(16.25, -99.08) * mm, "end": v(13.12, -99.9) * mm});
            skLineSegment(sketch, "E10475", {"start": v(13.12, -99.9) * mm, "end": v(13.48, -101.53) * mm});
            skLineSegment(sketch, "E10476", {"start": v(13.48, -101.53) * mm, "end": v(13.5, -101.58) * mm});
            skLineSegment(sketch, "E10477", {"start": v(13.5, -101.58) * mm, "end": v(13.5, -101.7) * mm});
            skLineSegment(sketch, "E10478", {"start": v(13.5, -101.7) * mm, "end": v(13.53, -101.93) * mm});
            skLineSegment(sketch, "E10479", {"start": v(13.53, -101.93) * mm, "end": v(13.54, -102.24) * mm});
            skLineSegment(sketch, "E10480", {"start": v(13.54, -102.24) * mm, "end": v(13.53, -102.65) * mm});
            skLineSegment(sketch, "E10481", {"start": v(13.53, -102.65) * mm, "end": v(13.5, -103.14) * mm});
            skLineSegment(sketch, "E10482", {"start": v(13.5, -103.14) * mm, "end": v(13.44, -103.71) * mm});
            skLineSegment(sketch, "E10483", {"start": v(13.44, -103.71) * mm, "end": v(13.33, -104.37) * mm});
            skLineSegment(sketch, "E10484", {"start": v(13.33, -104.37) * mm, "end": v(13.16, -105.12) * mm});
            skLineSegment(sketch, "E10485", {"start": v(13.16, -105.12) * mm, "end": v(13.11, -105.32) * mm});
            skLineSegment(sketch, "E10486", {"start": v(13.11, -105.32) * mm, "end": v(10.85, -105.66) * mm});
            skLineSegment(sketch, "E10487", {"start": v(10.85, -105.66) * mm, "end": v(10.74, -105.5) * mm});
            skLineSegment(sketch, "E10488", {"start": v(10.74, -105.5) * mm, "end": v(10.36, -104.83) * mm});
            skLineSegment(sketch, "E10489", {"start": v(10.36, -104.83) * mm, "end": v(10.05, -104.24) * mm});
            skLineSegment(sketch, "E10490", {"start": v(10.05, -104.24) * mm, "end": v(9.8, -103.7) * mm});
            skLineSegment(sketch, "E10491", {"start": v(9.8, -103.7) * mm, "end": v(9.62, -103.25) * mm});
            skLineSegment(sketch, "E10492", {"start": v(9.62, -103.25) * mm, "end": v(9.5, -102.87) * mm});
            skLineSegment(sketch, "E10493", {"start": v(9.5, -102.87) * mm, "end": v(9.4, -102.57) * mm});
            skLineSegment(sketch, "E10494", {"start": v(9.4, -102.57) * mm, "end": v(9.36, -102.35) * mm});
            skLineSegment(sketch, "E10495", {"start": v(9.36, -102.35) * mm, "end": v(9.33, -102.22) * mm});
            skLineSegment(sketch, "E10496", {"start": v(9.33, -102.22) * mm, "end": v(9.33, -102.17) * mm});
            skLineSegment(sketch, "E10497", {"start": v(9.33, -102.17) * mm, "end": v(9.16, -100.5) * mm});
            skLineSegment(sketch, "E10498", {"start": v(9.16, -100.5) * mm, "end": v(5.93, -100.67) * mm});
            skLineSegment(sketch, "E10499", {"start": v(5.93, -100.67) * mm, "end": v(5.94, -102.34) * mm});
            skLineSegment(sketch, "E10500", {"start": v(5.94, -102.34) * mm, "end": v(5.94, -102.38) * mm});
            skLineSegment(sketch, "E10501", {"start": v(5.94, -102.38) * mm, "end": v(5.93, -102.52) * mm});
            skLineSegment(sketch, "E10502", {"start": v(5.93, -102.52) * mm, "end": v(5.9, -102.74) * mm});
            skLineSegment(sketch, "E10503", {"start": v(5.9, -102.74) * mm, "end": v(5.84, -103.05) * mm});
            skLineSegment(sketch, "E10504", {"start": v(5.84, -103.05) * mm, "end": v(5.75, -103.44) * mm});
            skLineSegment(sketch, "E10505", {"start": v(5.75, -103.44) * mm, "end": v(5.62, -103.91) * mm});
            skLineSegment(sketch, "E10506", {"start": v(5.62, -103.91) * mm, "end": v(5.43, -104.47) * mm});
            skLineSegment(sketch, "E10507", {"start": v(5.43, -104.47) * mm, "end": v(5.18, -105.09) * mm});
            skLineSegment(sketch, "E10508", {"start": v(5.18, -105.09) * mm, "end": v(4.87, -105.78) * mm});
            skLineSegment(sketch, "E10509", {"start": v(4.87, -105.78) * mm, "end": v(4.77, -105.97) * mm});
            skLineSegment(sketch, "E10510", {"start": v(4.77, -105.97) * mm, "end": v(2.5, -105.84) * mm});
            skLineSegment(sketch, "E10511", {"start": v(2.5, -105.84) * mm, "end": v(2.42, -105.65) * mm});
            skLineSegment(sketch, "E10512", {"start": v(2.42, -105.65) * mm, "end": v(2.18, -104.93) * mm});
            skLineSegment(sketch, "E10513", {"start": v(2.18, -104.93) * mm, "end": v(2, -104.28) * mm});
            skLineSegment(sketch, "E10514", {"start": v(2, -104.28) * mm, "end": v(1.88, -103.71) * mm});
            skLineSegment(sketch, "E10515", {"start": v(1.88, -103.71) * mm, "end": v(1.8, -103.23) * mm});
            skLineSegment(sketch, "E10516", {"start": v(1.8, -103.23) * mm, "end": v(1.75, -102.83) * mm});
            skLineSegment(sketch, "E10517", {"start": v(1.75, -102.83) * mm, "end": v(1.73, -102.52) * mm});
            skLineSegment(sketch, "E10518", {"start": v(1.73, -102.52) * mm, "end": v(1.73, -102.3) * mm});
            skLineSegment(sketch, "E10519", {"start": v(1.73, -102.3) * mm, "end": v(1.73, -102.16) * mm});
            skLineSegment(sketch, "E10520", {"start": v(1.73, -102.16) * mm, "end": v(1.74, -102.12) * mm});
            skLineSegment(sketch, "E10521", {"start": v(1.74, -102.12) * mm, "end": v(1.93, -100.45) * mm});
            skLineSegment(sketch, "E10522", {"start": v(1.93, -100.45) * mm, "end": v(-1.27, -99.95) * mm});
            skLineSegment(sketch, "E10523", {"start": v(-1.27, -99.95) * mm, "end": v(-1.61, -101.59) * mm});
            skLineSegment(sketch, "E10524", {"start": v(-1.61, -101.59) * mm, "end": v(-1.63, -101.63) * mm});
            skLineSegment(sketch, "E10525", {"start": v(-1.63, -101.63) * mm, "end": v(-1.66, -101.76) * mm});
            skLineSegment(sketch, "E10526", {"start": v(-1.66, -101.76) * mm, "end": v(-1.74, -101.97) * mm});
            skLineSegment(sketch, "E10527", {"start": v(-1.74, -101.97) * mm, "end": v(-1.86, -102.26) * mm});
            skLineSegment(sketch, "E10528", {"start": v(-1.86, -102.26) * mm, "end": v(-2.03, -102.62) * mm});
            skLineSegment(sketch, "E10529", {"start": v(-2.03, -102.62) * mm, "end": v(-2.26, -103.06) * mm});
            skLineSegment(sketch, "E10530", {"start": v(-2.26, -103.06) * mm, "end": v(-2.56, -103.56) * mm});
            skLineSegment(sketch, "E10531", {"start": v(-2.56, -103.56) * mm, "end": v(-2.93, -104.12) * mm});
            skLineSegment(sketch, "E10532", {"start": v(-2.93, -104.12) * mm, "end": v(-3.39, -104.73) * mm});
            skLineSegment(sketch, "E10533", {"start": v(-3.39, -104.73) * mm, "end": v(-3.52, -104.9) * mm});
            skLineSegment(sketch, "E10534", {"start": v(-3.52, -104.9) * mm, "end": v(-5.72, -104.3) * mm});
            skLineSegment(sketch, "E10535", {"start": v(-5.72, -104.3) * mm, "end": v(-5.75, -104.1) * mm});
            skLineSegment(sketch, "E10536", {"start": v(-5.75, -104.1) * mm, "end": v(-5.83, -103.35) * mm});
            skLineSegment(sketch, "E10537", {"start": v(-5.83, -103.35) * mm, "end": v(-5.87, -102.68) * mm});
            skLineSegment(sketch, "E10538", {"start": v(-5.87, -102.68) * mm, "end": v(-5.87, -102.1) * mm});
            skLineSegment(sketch, "E10539", {"start": v(-5.87, -102.1) * mm, "end": v(-5.85, -101.6) * mm});
            skLineSegment(sketch, "E10540", {"start": v(-5.85, -101.6) * mm, "end": v(-5.81, -101.2) * mm});
            skLineSegment(sketch, "E10541", {"start": v(-5.81, -101.2) * mm, "end": v(-5.76, -100.9) * mm});
            skLineSegment(sketch, "E10542", {"start": v(-5.76, -100.9) * mm, "end": v(-5.72, -100.68) * mm});
            skLineSegment(sketch, "E10543", {"start": v(-5.72, -100.68) * mm, "end": v(-5.69, -100.55) * mm});
            skLineSegment(sketch, "E10544", {"start": v(-5.69, -100.55) * mm, "end": v(-5.67, -100.5) * mm});
            skLineSegment(sketch, "E10545", {"start": v(-5.67, -100.5) * mm, "end": v(-5.14, -98.92) * mm});
            skLineSegment(sketch, "E10546", {"start": v(-5.14, -98.92) * mm, "end": v(-8.16, -97.77) * mm});
            skLineSegment(sketch, "E10547", {"start": v(-8.16, -97.77) * mm, "end": v(-8.84, -99.3) * mm});
            skLineSegment(sketch, "E10548", {"start": v(-8.84, -99.3) * mm, "end": v(-8.86, -99.34) * mm});
            skLineSegment(sketch, "E10549", {"start": v(-8.86, -99.34) * mm, "end": v(-8.93, -99.46) * mm});
            skLineSegment(sketch, "E10550", {"start": v(-8.93, -99.46) * mm, "end": v(-9.04, -99.65) * mm});
            skLineSegment(sketch, "E10551", {"start": v(-9.04, -99.65) * mm, "end": v(-9.22, -99.91) * mm});
            skLineSegment(sketch, "E10552", {"start": v(-9.22, -99.91) * mm, "end": v(-9.46, -100.23) * mm});
            skLineSegment(sketch, "E10553", {"start": v(-9.46, -100.23) * mm, "end": v(-9.78, -100.61) * mm});
            skLineSegment(sketch, "E10554", {"start": v(-9.78, -100.61) * mm, "end": v(-10.18, -101.04) * mm});
            skLineSegment(sketch, "E10555", {"start": v(-10.18, -101.04) * mm, "end": v(-10.66, -101.51) * mm});
            skLineSegment(sketch, "E10556", {"start": v(-10.66, -101.51) * mm, "end": v(-11.24, -102.02) * mm});
            skLineSegment(sketch, "E10557", {"start": v(-11.24, -102.02) * mm, "end": v(-11.4, -102.15) * mm});
            skLineSegment(sketch, "E10558", {"start": v(-11.4, -102.15) * mm, "end": v(-13.43, -101.12) * mm});
            skLineSegment(sketch, "E10559", {"start": v(-13.43, -101.12) * mm, "end": v(-13.42, -100.92) * mm});
            skLineSegment(sketch, "E10560", {"start": v(-13.42, -100.92) * mm, "end": v(-13.34, -100.16) * mm});
            skLineSegment(sketch, "E10561", {"start": v(-13.34, -100.16) * mm, "end": v(-13.24, -99.5) * mm});
            skLineSegment(sketch, "E10562", {"start": v(-13.24, -99.5) * mm, "end": v(-13.11, -98.93) * mm});
            skLineSegment(sketch, "E10563", {"start": v(-13.11, -98.93) * mm, "end": v(-12.99, -98.46) * mm});
            skLineSegment(sketch, "E10564", {"start": v(-12.99, -98.46) * mm, "end": v(-12.87, -98.07) * mm});
            skLineSegment(sketch, "E10565", {"start": v(-12.87, -98.07) * mm, "end": v(-12.76, -97.78) * mm});
            skLineSegment(sketch, "E10566", {"start": v(-12.76, -97.78) * mm, "end": v(-12.67, -97.57) * mm});
            skLineSegment(sketch, "E10567", {"start": v(-12.67, -97.57) * mm, "end": v(-12.6, -97.45) * mm});
            skLineSegment(sketch, "E10568", {"start": v(-12.6, -97.45) * mm, "end": v(-12.59, -97.41) * mm});
            skLineSegment(sketch, "E10569", {"start": v(-12.59, -97.41) * mm, "end": v(-11.73, -95.97) * mm});
            skLineSegment(sketch, "E10570", {"start": v(-11.73, -95.97) * mm, "end": v(-14.44, -94.23) * mm});
            skLineSegment(sketch, "E10571", {"start": v(-14.44, -94.23) * mm, "end": v(-15.43, -95.59) * mm});
            skLineSegment(sketch, "E10572", {"start": v(-15.43, -95.59) * mm, "end": v(-15.46, -95.62) * mm});
            skLineSegment(sketch, "E10573", {"start": v(-15.46, -95.62) * mm, "end": v(-15.54, -95.73) * mm});
            skLineSegment(sketch, "E10574", {"start": v(-15.54, -95.73) * mm, "end": v(-15.7, -95.89) * mm});
            skLineSegment(sketch, "E10575", {"start": v(-15.7, -95.89) * mm, "end": v(-15.93, -96.1) * mm});
            skLineSegment(sketch, "E10576", {"start": v(-15.93, -96.1) * mm, "end": v(-16.23, -96.37) * mm});
            skLineSegment(sketch, "E10577", {"start": v(-16.23, -96.37) * mm, "end": v(-16.63, -96.68) * mm});
            skLineSegment(sketch, "E10578", {"start": v(-16.63, -96.68) * mm, "end": v(-17.1, -97.02) * mm});
            skLineSegment(sketch, "E10579", {"start": v(-17.1, -97.02) * mm, "end": v(-17.68, -97.38) * mm});
            skLineSegment(sketch, "E10580", {"start": v(-17.68, -97.38) * mm, "end": v(-18.35, -97.76) * mm});
            skLineSegment(sketch, "E10581", {"start": v(-18.35, -97.76) * mm, "end": v(-18.53, -97.85) * mm});
            skLineSegment(sketch, "E10582", {"start": v(-18.53, -97.85) * mm, "end": v(-20.3, -96.43) * mm});
            skLineSegment(sketch, "E10583", {"start": v(-20.3, -96.43) * mm, "end": v(-20.25, -96.23) * mm});
            skLineSegment(sketch, "E10584", {"start": v(-20.25, -96.23) * mm, "end": v(-20.01, -95.5) * mm});
            skLineSegment(sketch, "E10585", {"start": v(-20.01, -95.5) * mm, "end": v(-19.77, -94.88) * mm});
            skLineSegment(sketch, "E10586", {"start": v(-19.77, -94.88) * mm, "end": v(-19.53, -94.35) * mm});
            skLineSegment(sketch, "E10587", {"start": v(-19.53, -94.35) * mm, "end": v(-19.3, -93.91) * mm});
            skLineSegment(sketch, "E10588", {"start": v(-19.3, -93.91) * mm, "end": v(-19.1, -93.56) * mm});
            skLineSegment(sketch, "E10589", {"start": v(-19.1, -93.56) * mm, "end": v(-18.94, -93.3) * mm});
            skLineSegment(sketch, "E10590", {"start": v(-18.94, -93.3) * mm, "end": v(-18.8, -93.12) * mm});
            skLineSegment(sketch, "E10591", {"start": v(-18.8, -93.12) * mm, "end": v(-18.72, -93) * mm});
            skLineSegment(sketch, "E10592", {"start": v(-18.72, -93) * mm, "end": v(-18.7, -92.98) * mm});
            skLineSegment(sketch, "E10593", {"start": v(-18.7, -92.98) * mm, "end": v(-17.55, -91.74) * mm});
            skLineSegment(sketch, "E10594", {"start": v(-17.55, -91.74) * mm, "end": v(-19.83, -89.48) * mm});
            skLineSegment(sketch, "E10595", {"start": v(-19.83, -89.48) * mm, "end": v(-21.09, -90.6) * mm});
            skLineSegment(sketch, "E10596", {"start": v(-21.09, -90.6) * mm, "end": v(-21.12, -90.64) * mm});
            skLineSegment(sketch, "E10597", {"start": v(-21.12, -90.64) * mm, "end": v(-21.23, -90.72) * mm});
            skLineSegment(sketch, "E10598", {"start": v(-21.23, -90.72) * mm, "end": v(-21.42, -90.85) * mm});
            skLineSegment(sketch, "E10599", {"start": v(-21.42, -90.85) * mm, "end": v(-21.68, -91.01) * mm});
            skLineSegment(sketch, "E10600", {"start": v(-21.68, -91.01) * mm, "end": v(-22.04, -91.2) * mm});
            skLineSegment(sketch, "E10601", {"start": v(-22.04, -91.2) * mm, "end": v(-22.49, -91.43) * mm});
            skLineSegment(sketch, "E10602", {"start": v(-22.49, -91.43) * mm, "end": v(-23.03, -91.66) * mm});
            skLineSegment(sketch, "E10603", {"start": v(-23.03, -91.66) * mm, "end": v(-23.67, -91.9) * mm});
            skLineSegment(sketch, "E10604", {"start": v(-23.67, -91.9) * mm, "end": v(-24.4, -92.13) * mm});
            skLineSegment(sketch, "E10605", {"start": v(-24.4, -92.13) * mm, "end": v(-24.6, -92.18) * mm});
            skLineSegment(sketch, "E10606", {"start": v(-24.6, -92.18) * mm, "end": v(-26.03, -90.43) * mm});
            skLineSegment(sketch, "E10607", {"start": v(-26.03, -90.43) * mm, "end": v(-25.94, -90.25) * mm});
            skLineSegment(sketch, "E10608", {"start": v(-25.94, -90.25) * mm, "end": v(-25.55, -89.6) * mm});
            skLineSegment(sketch, "E10609", {"start": v(-25.55, -89.6) * mm, "end": v(-25.18, -89.03) * mm});
            skLineSegment(sketch, "E10610", {"start": v(-25.18, -89.03) * mm, "end": v(-24.84, -88.56) * mm});
            skLineSegment(sketch, "E10611", {"start": v(-24.84, -88.56) * mm, "end": v(-24.53, -88.17) * mm});
            skLineSegment(sketch, "E10612", {"start": v(-24.53, -88.17) * mm, "end": v(-24.26, -87.87) * mm});
            skLineSegment(sketch, "E10613", {"start": v(-24.26, -87.87) * mm, "end": v(-24.03, -87.65) * mm});
            skLineSegment(sketch, "E10614", {"start": v(-24.03, -87.65) * mm, "end": v(-23.87, -87.5) * mm});
            skLineSegment(sketch, "E10615", {"start": v(-23.87, -87.5) * mm, "end": v(-23.76, -87.41) * mm});
            skLineSegment(sketch, "E10616", {"start": v(-23.76, -87.41) * mm, "end": v(-23.73, -87.38) * mm});
            skLineSegment(sketch, "E10617", {"start": v(-23.73, -87.38) * mm, "end": v(-22.35, -86.41) * mm});
            skLineSegment(sketch, "E10618", {"start": v(-22.35, -86.41) * mm, "end": v(-24.1, -83.73) * mm});
            skLineSegment(sketch, "E10619", {"start": v(-24.1, -83.73) * mm, "end": v(-25.57, -84.58) * mm});
            skLineSegment(sketch, "E10620", {"start": v(-25.57, -84.58) * mm, "end": v(-25.61, -84.6) * mm});
            skLineSegment(sketch, "E10621", {"start": v(-25.61, -84.6) * mm, "end": v(-25.73, -84.66) * mm});
            skLineSegment(sketch, "E10622", {"start": v(-25.73, -84.66) * mm, "end": v(-25.94, -84.74) * mm});
            skLineSegment(sketch, "E10623", {"start": v(-25.94, -84.74) * mm, "end": v(-26.24, -84.85) * mm});
            skLineSegment(sketch, "E10624", {"start": v(-26.24, -84.85) * mm, "end": v(-26.63, -84.97) * mm});
            skLineSegment(sketch, "E10625", {"start": v(-26.63, -84.97) * mm, "end": v(-27.11, -85.1) * mm});
            skLineSegment(sketch, "E10626", {"start": v(-27.11, -85.1) * mm, "end": v(-27.7, -85.2) * mm});
            skLineSegment(sketch, "E10627", {"start": v(-27.7, -85.2) * mm, "end": v(-28.37, -85.3) * mm});
            skLineSegment(sketch, "E10628", {"start": v(-28.37, -85.3) * mm, "end": v(-29.13, -85.39) * mm});
            skLineSegment(sketch, "E10629", {"start": v(-29.13, -85.39) * mm, "end": v(-29.34, -85.4) * mm});
            skLineSegment(sketch, "E10630", {"start": v(-29.34, -85.4) * mm, "end": v(-30.37, -83.4) * mm});
            skLineSegment(sketch, "E10631", {"start": v(-30.37, -83.4) * mm, "end": v(-30.24, -83.23) * mm});
            skLineSegment(sketch, "E10632", {"start": v(-30.24, -83.23) * mm, "end": v(-29.73, -82.67) * mm});
            skLineSegment(sketch, "E10633", {"start": v(-29.73, -82.67) * mm, "end": v(-29.24, -82.2) * mm});
            skLineSegment(sketch, "E10634", {"start": v(-29.24, -82.2) * mm, "end": v(-28.8, -81.8) * mm});
            skLineSegment(sketch, "E10635", {"start": v(-28.8, -81.8) * mm, "end": v(-28.42, -81.5) * mm});
            skLineSegment(sketch, "E10636", {"start": v(-28.42, -81.5) * mm, "end": v(-28.1, -81.25) * mm});
            skLineSegment(sketch, "E10637", {"start": v(-28.1, -81.25) * mm, "end": v(-27.83, -81.08) * mm});
            skLineSegment(sketch, "E10638", {"start": v(-27.83, -81.08) * mm, "end": v(-27.63, -80.96) * mm});
            skLineSegment(sketch, "E10639", {"start": v(-27.63, -80.96) * mm, "end": v(-27.51, -80.9) * mm});
            skLineSegment(sketch, "E10640", {"start": v(-27.51, -80.9) * mm, "end": v(-27.47, -80.88) * mm});
            skLineSegment(sketch, "E10641", {"start": v(-27.47, -80.88) * mm, "end": v(-25.92, -80.21) * mm});
            skLineSegment(sketch, "E10642", {"start": v(-25.92, -80.21) * mm, "end": v(-27.07, -77.24) * mm});
            skLineSegment(sketch, "E10643", {"start": v(-27.07, -77.24) * mm, "end": v(-28.68, -77.76) * mm});
            skLineSegment(sketch, "E10644", {"start": v(-28.68, -77.76) * mm, "end": v(-28.73, -77.77) * mm});
            skLineSegment(sketch, "E10645", {"start": v(-28.73, -77.77) * mm, "end": v(-28.86, -77.8) * mm});
            skLineSegment(sketch, "E10646", {"start": v(-28.86, -77.8) * mm, "end": v(-29.08, -77.85) * mm});
            skLineSegment(sketch, "E10647", {"start": v(-29.08, -77.85) * mm, "end": v(-29.4, -77.9) * mm});
            skLineSegment(sketch, "E10648", {"start": v(-29.4, -77.9) * mm, "end": v(-29.8, -77.93) * mm});
            skLineSegment(sketch, "E10649", {"start": v(-29.8, -77.93) * mm, "end": v(-30.3, -77.95) * mm});
            skLineSegment(sketch, "E10650", {"start": v(-30.3, -77.95) * mm, "end": v(-30.9, -77.94) * mm});
            skLineSegment(sketch, "E10651", {"start": v(-30.9, -77.94) * mm, "end": v(-31.57, -77.9) * mm});
            skLineSegment(sketch, "E10652", {"start": v(-31.57, -77.9) * mm, "end": v(-32.34, -77.82) * mm});
            skLineSegment(sketch, "E10653", {"start": v(-32.34, -77.82) * mm, "end": v(-32.54, -77.8) * mm});
            skLineSegment(sketch, "E10654", {"start": v(-32.54, -77.8) * mm, "end": v(-33.13, -75.62) * mm});
            skLineSegment(sketch, "E10655", {"start": v(-33.13, -75.62) * mm, "end": v(-32.97, -75.49) * mm});
            skLineSegment(sketch, "E10656", {"start": v(-32.97, -75.49) * mm, "end": v(-32.34, -75.04) * mm});
            skLineSegment(sketch, "E10657", {"start": v(-32.34, -75.04) * mm, "end": v(-31.77, -74.68) * mm});
            skLineSegment(sketch, "E10658", {"start": v(-31.77, -74.68) * mm, "end": v(-31.26, -74.38) * mm});
            skLineSegment(sketch, "E10659", {"start": v(-31.26, -74.38) * mm, "end": v(-30.82, -74.16) * mm});
            skLineSegment(sketch, "E10660", {"start": v(-30.82, -74.16) * mm, "end": v(-30.45, -74) * mm});
            skLineSegment(sketch, "E10661", {"start": v(-30.45, -74) * mm, "end": v(-30.15, -73.88) * mm});
            skLineSegment(sketch, "E10662", {"start": v(-30.15, -73.88) * mm, "end": v(-29.94, -73.8) * mm});
            skLineSegment(sketch, "E10663", {"start": v(-29.94, -73.8) * mm, "end": v(-29.8, -73.77) * mm});
            skLineSegment(sketch, "E10664", {"start": v(-29.8, -73.77) * mm, "end": v(-29.76, -73.76) * mm});
            skLineSegment(sketch, "E10665", {"start": v(-29.76, -73.76) * mm, "end": v(-28.1, -73.42) * mm});
            skLineSegment(sketch, "E10666", {"start": v(-28.1, -73.42) * mm, "end": v(-28.6, -70.27) * mm});
            skLineSegment(sketch, "E10667", {"start": v(-28.6, -70.27) * mm, "end": v(-30.29, -70.45) * mm});
            skLineSegment(sketch, "E10668", {"start": v(-30.29, -70.45) * mm, "end": v(-30.33, -70.46) * mm});
            skLineSegment(sketch, "E10669", {"start": v(-30.33, -70.46) * mm, "end": v(-30.47, -70.46) * mm});
            skLineSegment(sketch, "E10670", {"start": v(-30.47, -70.46) * mm, "end": v(-30.7, -70.46) * mm});
            skLineSegment(sketch, "E10671", {"start": v(-30.7, -70.46) * mm, "end": v(-31.01, -70.44) * mm});
            skLineSegment(sketch, "E10672", {"start": v(-31.01, -70.44) * mm, "end": v(-31.42, -70.39) * mm});
            skLineSegment(sketch, "E10673", {"start": v(-31.42, -70.39) * mm, "end": v(-31.91, -70.3) * mm});
            skLineSegment(sketch, "E10674", {"start": v(-31.91, -70.3) * mm, "end": v(-32.49, -70.18) * mm});
            skLineSegment(sketch, "E10675", {"start": v(-32.49, -70.18) * mm, "end": v(-33.14, -70) * mm});
            skLineSegment(sketch, "E10676", {"start": v(-33.14, -70) * mm, "end": v(-33.88, -69.77) * mm});
            skLineSegment(sketch, "E10677", {"start": v(-33.88, -69.77) * mm, "end": v(-34.07, -69.7) * mm});
            skLineSegment(sketch, "E10678", {"start": v(-34.07, -69.7) * mm, "end": v(-34.19, -67.45) * mm});
            skLineSegment(sketch, "E10679", {"start": v(-34.19, -67.45) * mm, "end": v(-34, -67.36) * mm});
            skLineSegment(sketch, "E10680", {"start": v(-34, -67.36) * mm, "end": v(-33.3, -67.05) * mm});
            skLineSegment(sketch, "E10681", {"start": v(-33.3, -67.05) * mm, "end": v(-32.66, -66.8) * mm});
            skLineSegment(sketch, "E10682", {"start": v(-32.66, -66.8) * mm, "end": v(-32.1, -66.62) * mm});
            skLineSegment(sketch, "E10683", {"start": v(-32.1, -66.62) * mm, "end": v(-31.62, -66.5) * mm});
            skLineSegment(sketch, "E10684", {"start": v(-31.62, -66.5) * mm, "end": v(-31.22, -66.4) * mm});
            skLineSegment(sketch, "E10685", {"start": v(-31.22, -66.4) * mm, "end": v(-30.9, -66.35) * mm});
            skLineSegment(sketch, "E10686", {"start": v(-30.9, -66.35) * mm, "end": v(-30.68, -66.33) * mm});
            skLineSegment(sketch, "E10687", {"start": v(-30.68, -66.33) * mm, "end": v(-30.55, -66.32) * mm});
            skLineSegment(sketch, "E10688", {"start": v(-30.55, -66.32) * mm, "end": v(-30.5, -66.32) * mm});
            skLineSegment(sketch, "E10689", {"start": v(-30.5, -66.32) * mm, "end": v(-28.8, -66.33) * mm});
            skLineSegment(sketch, "E10690", {"start": v(-28.8, -66.33) * mm, "end": v(-28.63, -63.15) * mm});
            skLineSegment(sketch, "E10691", {"start": v(-28.63, -63.15) * mm, "end": v(-30.32, -62.98) * mm});
            skLineSegment(sketch, "E10692", {"start": v(-30.32, -62.98) * mm, "end": v(-30.36, -62.97) * mm});
            skLineSegment(sketch, "E10693", {"start": v(-30.36, -62.97) * mm, "end": v(-30.5, -62.95) * mm});
            skLineSegment(sketch, "E10694", {"start": v(-30.5, -62.95) * mm, "end": v(-30.72, -62.9) * mm});
            skLineSegment(sketch, "E10695", {"start": v(-30.72, -62.9) * mm, "end": v(-31.02, -62.81) * mm});
            skLineSegment(sketch, "E10696", {"start": v(-31.02, -62.81) * mm, "end": v(-31.4, -62.68) * mm});
            skLineSegment(sketch, "E10697", {"start": v(-31.4, -62.68) * mm, "end": v(-31.87, -62.5) * mm});
            skLineSegment(sketch, "E10698", {"start": v(-31.87, -62.5) * mm, "end": v(-32.41, -62.26) * mm});
            skLineSegment(sketch, "E10699", {"start": v(-32.41, -62.26) * mm, "end": v(-33.01, -61.96) * mm});
            skLineSegment(sketch, "E10700", {"start": v(-33.01, -61.96) * mm, "end": v(-33.68, -61.57) * mm});
            skLineSegment(sketch, "E10701", {"start": v(-33.68, -61.57) * mm, "end": v(-33.86, -61.46) * mm});
            skLineSegment(sketch, "E10702", {"start": v(-33.86, -61.46) * mm, "end": v(-33.5, -59.24) * mm});
            skLineSegment(sketch, "E10703", {"start": v(-33.5, -59.24) * mm, "end": v(-33.3, -59.19) * mm});
            skLineSegment(sketch, "E10704", {"start": v(-33.3, -59.19) * mm, "end": v(-32.54, -59.03) * mm});
            skLineSegment(sketch, "E10705", {"start": v(-32.54, -59.03) * mm, "end": v(-31.87, -58.93) * mm});
            skLineSegment(sketch, "E10706", {"start": v(-31.87, -58.93) * mm, "end": v(-31.28, -58.86) * mm});
            skLineSegment(sketch, "E10707", {"start": v(-31.28, -58.86) * mm, "end": v(-30.78, -58.83) * mm});
            skLineSegment(sketch, "E10708", {"start": v(-30.78, -58.83) * mm, "end": v(-30.37, -58.83) * mm});
            skLineSegment(sketch, "E10709", {"start": v(-30.37, -58.83) * mm, "end": v(-30.06, -58.84) * mm});
            skLineSegment(sketch, "E10710", {"start": v(-30.06, -58.84) * mm, "end": v(-29.83, -58.86) * mm});
            skLineSegment(sketch, "E10711", {"start": v(-29.83, -58.86) * mm, "end": v(-29.7, -58.88) * mm});
            skLineSegment(sketch, "E10712", {"start": v(-29.7, -58.88) * mm, "end": v(-29.65, -58.89) * mm});
            skLineSegment(sketch, "E10713", {"start": v(-29.65, -58.89) * mm, "end": v(-28, -59.25) * mm});
            skLineSegment(sketch, "E10714", {"start": v(-28, -59.25) * mm, "end": v(-27.15, -56.17) * mm});
            skLineSegment(sketch, "E10715", {"start": v(-27.15, -56.17) * mm, "end": v(-28.77, -55.66) * mm});
            skLineSegment(sketch, "E10716", {"start": v(-28.77, -55.66) * mm, "end": v(-28.8, -55.65) * mm});
            skLineSegment(sketch, "E10717", {"start": v(-28.8, -55.65) * mm, "end": v(-28.93, -55.6) * mm});
            skLineSegment(sketch, "E10718", {"start": v(-28.93, -55.6) * mm, "end": v(-29.14, -55.5) * mm});
            skLineSegment(sketch, "E10719", {"start": v(-29.14, -55.5) * mm, "end": v(-29.42, -55.36) * mm});
            skLineSegment(sketch, "E10720", {"start": v(-29.42, -55.36) * mm, "end": v(-29.77, -55.15) * mm});
            skLineSegment(sketch, "E10721", {"start": v(-29.77, -55.15) * mm, "end": v(-30.19, -54.88) * mm});
            skLineSegment(sketch, "E10722", {"start": v(-30.19, -54.88) * mm, "end": v(-30.66, -54.53) * mm});
            skLineSegment(sketch, "E10723", {"start": v(-30.66, -54.53) * mm, "end": v(-31.19, -54.1) * mm});
            skLineSegment(sketch, "E10724", {"start": v(-31.19, -54.1) * mm, "end": v(-31.76, -53.6) * mm});
            skLineSegment(sketch, "E10725", {"start": v(-31.76, -53.6) * mm, "end": v(-31.9, -53.45) * mm});
            skLineSegment(sketch, "E10726", {"start": v(-31.9, -53.45) * mm, "end": v(-31.09, -51.36) * mm});
            skLineSegment(sketch, "E10727", {"start": v(-31.09, -51.36) * mm, "end": v(-30.88, -51.34) * mm});
            skLineSegment(sketch, "E10728", {"start": v(-30.88, -51.34) * mm, "end": v(-30.1, -51.35) * mm});
            skLineSegment(sketch, "E10729", {"start": v(-30.1, -51.35) * mm, "end": v(-29.43, -51.38) * mm});
            skLineSegment(sketch, "E10730", {"start": v(-29.43, -51.38) * mm, "end": v(-28.84, -51.44) * mm});
            skLineSegment(sketch, "E10731", {"start": v(-28.84, -51.44) * mm, "end": v(-28.35, -51.51) * mm});
            skLineSegment(sketch, "E10732", {"start": v(-28.35, -51.51) * mm, "end": v(-27.95, -51.6) * mm});
            skLineSegment(sketch, "E10733", {"start": v(-27.95, -51.6) * mm, "end": v(-27.64, -51.67) * mm});
            skLineSegment(sketch, "E10734", {"start": v(-27.64, -51.67) * mm, "end": v(-27.42, -51.74) * mm});
            skLineSegment(sketch, "E10735", {"start": v(-27.42, -51.74) * mm, "end": v(-27.3, -51.78) * mm});
            skLineSegment(sketch, "E10736", {"start": v(-27.3, -51.78) * mm, "end": v(-27.25, -51.8) * mm});
            skLineSegment(sketch, "E10737", {"start": v(-27.25, -51.8) * mm, "end": v(-25.7, -52.5) * mm});
            skLineSegment(sketch, "E10738", {"start": v(-25.7, -52.5) * mm, "end": v(-24.23, -49.65) * mm});
            skLineSegment(sketch, "E10739", {"start": v(-24.23, -49.65) * mm, "end": v(-25.7, -48.82) * mm});
            skLineSegment(sketch, "E10740", {"start": v(-25.7, -48.82) * mm, "end": v(-25.74, -48.8) * mm});
            skLineSegment(sketch, "E10741", {"start": v(-25.74, -48.8) * mm, "end": v(-25.86, -48.72) * mm});
            skLineSegment(sketch, "E10742", {"start": v(-25.86, -48.72) * mm, "end": v(-26.04, -48.59) * mm});
            skLineSegment(sketch, "E10743", {"start": v(-26.04, -48.59) * mm, "end": v(-26.28, -48.39) * mm});
            skLineSegment(sketch, "E10744", {"start": v(-26.28, -48.39) * mm, "end": v(-26.58, -48.12) * mm});
            skLineSegment(sketch, "E10745", {"start": v(-26.58, -48.12) * mm, "end": v(-26.93, -47.76) * mm});
            skLineSegment(sketch, "E10746", {"start": v(-26.93, -47.76) * mm, "end": v(-27.32, -47.33) * mm});
            skLineSegment(sketch, "E10747", {"start": v(-27.32, -47.33) * mm, "end": v(-27.75, -46.8) * mm});
            skLineSegment(sketch, "E10748", {"start": v(-27.75, -46.8) * mm, "end": v(-28.2, -46.2) * mm});
            skLineSegment(sketch, "E10749", {"start": v(-28.2, -46.2) * mm, "end": v(-28.31, -46.02) * mm});
            skLineSegment(sketch, "E10750", {"start": v(-28.31, -46.02) * mm, "end": v(-27.06, -44.13) * mm});
            skLineSegment(sketch, "E10751", {"start": v(-27.06, -44.13) * mm, "end": v(-26.86, -44.17) * mm});
            skLineSegment(sketch, "E10752", {"start": v(-26.86, -44.17) * mm, "end": v(-26.1, -44.33) * mm});
            skLineSegment(sketch, "E10753", {"start": v(-26.1, -44.33) * mm, "end": v(-25.45, -44.5) * mm});
            skLineSegment(sketch, "E10754", {"start": v(-25.45, -44.5) * mm, "end": v(-24.88, -44.68) * mm});
            skLineSegment(sketch, "E10755", {"start": v(-24.88, -44.68) * mm, "end": v(-24.42, -44.85) * mm});
            skLineSegment(sketch, "E10756", {"start": v(-24.42, -44.85) * mm, "end": v(-24.04, -45) * mm});
            skLineSegment(sketch, "E10757", {"start": v(-24.04, -45) * mm, "end": v(-23.76, -45.15) * mm});
            skLineSegment(sketch, "E10758", {"start": v(-23.76, -45.15) * mm, "end": v(-23.56, -45.26) * mm});
            skLineSegment(sketch, "E10759", {"start": v(-23.56, -45.26) * mm, "end": v(-23.44, -45.33) * mm});
            skLineSegment(sketch, "E10760", {"start": v(-23.44, -45.33) * mm, "end": v(-23.4, -45.35) * mm});
            skLineSegment(sketch, "E10761", {"start": v(-23.4, -45.35) * mm, "end": v(-22.04, -46.35) * mm});
            skLineSegment(sketch, "E10762", {"start": v(-22.04, -46.35) * mm, "end": v(-20, -43.87) * mm});
            skLineSegment(sketch, "E10763", {"start": v(-20, -43.87) * mm, "end": v(-21.27, -42.76) * mm});
            skLineSegment(sketch, "E10764", {"start": v(-21.27, -42.76) * mm, "end": v(-21.3, -42.73) * mm});
            skLineSegment(sketch, "E10765", {"start": v(-21.3, -42.73) * mm, "end": v(-21.4, -42.63) * mm});
            skLineSegment(sketch, "E10766", {"start": v(-21.4, -42.63) * mm, "end": v(-21.54, -42.46) * mm});
            skLineSegment(sketch, "E10767", {"start": v(-21.54, -42.46) * mm, "end": v(-21.74, -42.22) * mm});
            skLineSegment(sketch, "E10768", {"start": v(-21.74, -42.22) * mm, "end": v(-21.97, -41.89) * mm});
            skLineSegment(sketch, "E10769", {"start": v(-21.97, -41.89) * mm, "end": v(-22.24, -41.47) * mm});
            skLineSegment(sketch, "E10770", {"start": v(-22.24, -41.47) * mm, "end": v(-22.53, -40.97) * mm});
            skLineSegment(sketch, "E10771", {"start": v(-22.53, -40.97) * mm, "end": v(-22.84, -40.37) * mm});
            skLineSegment(sketch, "E10772", {"start": v(-22.84, -40.37) * mm, "end": v(-23.15, -39.67) * mm});
            skLineSegment(sketch, "E10773", {"start": v(-23.15, -39.67) * mm, "end": v(-23.22, -39.48) * mm});
            skLineSegment(sketch, "E10774", {"start": v(-23.22, -39.48) * mm, "end": v(-21.6, -37.9) * mm});
            skLineSegment(sketch, "E10775", {"start": v(-21.6, -37.9) * mm, "end": v(-21.41, -37.97) * mm});
            skLineSegment(sketch, "E10776", {"start": v(-21.41, -37.97) * mm, "end": v(-20.7, -38.28) * mm});
            skLineSegment(sketch, "E10777", {"start": v(-20.7, -38.28) * mm, "end": v(-20.1, -38.58) * mm});
            skLineSegment(sketch, "E10778", {"start": v(-20.1, -38.58) * mm, "end": v(-19.59, -38.87) * mm});
            skLineSegment(sketch, "E10779", {"start": v(-19.59, -38.87) * mm, "end": v(-19.17, -39.14) * mm});
            skLineSegment(sketch, "E10780", {"start": v(-19.17, -39.14) * mm, "end": v(-18.84, -39.37) * mm});
            skLineSegment(sketch, "E10781", {"start": v(-18.84, -39.37) * mm, "end": v(-18.59, -39.56) * mm});
            skLineSegment(sketch, "E10782", {"start": v(-18.59, -39.56) * mm, "end": v(-18.42, -39.71) * mm});
            skLineSegment(sketch, "E10783", {"start": v(-18.42, -39.71) * mm, "end": v(-18.32, -39.8) * mm});
            skLineSegment(sketch, "E10784", {"start": v(-18.32, -39.8) * mm, "end": v(-18.29, -39.84) * mm});
            skLineSegment(sketch, "E10785", {"start": v(-18.29, -39.84) * mm, "end": v(-17.16, -41.09) * mm});
            skLineSegment(sketch, "E10786", {"start": v(-17.16, -41.09) * mm, "end": v(-14.64, -39.09) * mm});
            skLineSegment(sketch, "E10787", {"start": v(-14.64, -39.09) * mm, "end": v(-15.64, -37.74) * mm});
            skLineSegment(sketch, "E10788", {"start": v(-15.64, -37.74) * mm, "end": v(-15.67, -37.7) * mm});
            skLineSegment(sketch, "E10789", {"start": v(-15.67, -37.7) * mm, "end": v(-15.74, -37.59) * mm});
            skLineSegment(sketch, "E10790", {"start": v(-15.74, -37.59) * mm, "end": v(-15.85, -37.4) * mm});
            skLineSegment(sketch, "E10791", {"start": v(-15.85, -37.4) * mm, "end": v(-16, -37.11) * mm});
            skLineSegment(sketch, "E10792", {"start": v(-16, -37.11) * mm, "end": v(-16.15, -36.74) * mm});
            skLineSegment(sketch, "E10793", {"start": v(-16.15, -36.74) * mm, "end": v(-16.33, -36.28) * mm});
            skLineSegment(sketch, "E10794", {"start": v(-16.33, -36.28) * mm, "end": v(-16.5, -35.73) * mm});
            skLineSegment(sketch, "E10795", {"start": v(-16.5, -35.73) * mm, "end": v(-16.68, -35.08) * mm});
            skLineSegment(sketch, "E10796", {"start": v(-16.68, -35.08) * mm, "end": v(-16.83, -34.33) * mm});
            skLineSegment(sketch, "E10797", {"start": v(-16.83, -34.33) * mm, "end": v(-16.87, -34.13) * mm});
            skLineSegment(sketch, "E10798", {"start": v(-16.87, -34.13) * mm, "end": v(-14.95, -32.91) * mm});
            skLineSegment(sketch, "E10799", {"start": v(-14.95, -32.91) * mm, "end": v(-14.78, -33.02) * mm});
            skLineSegment(sketch, "E10800", {"start": v(-14.78, -33.02) * mm, "end": v(-14.15, -33.47) * mm});
            skLineSegment(sketch, "E10801", {"start": v(-14.15, -33.47) * mm, "end": v(-13.62, -33.9) * mm});
            skLineSegment(sketch, "E10802", {"start": v(-13.62, -33.9) * mm, "end": v(-13.18, -34.28) * mm});
            skLineSegment(sketch, "E10803", {"start": v(-13.18, -34.28) * mm, "end": v(-12.83, -34.62) * mm});
            skLineSegment(sketch, "E10804", {"start": v(-12.83, -34.62) * mm, "end": v(-12.55, -34.92) * mm});
            skLineSegment(sketch, "E10805", {"start": v(-12.55, -34.92) * mm, "end": v(-12.35, -35.16) * mm});
            skLineSegment(sketch, "E10806", {"start": v(-12.35, -35.16) * mm, "end": v(-12.21, -35.34) * mm});
            skLineSegment(sketch, "E10807", {"start": v(-12.21, -35.34) * mm, "end": v(-12.14, -35.45) * mm});
            skLineSegment(sketch, "E10808", {"start": v(-12.14, -35.45) * mm, "end": v(-12.11, -35.49) * mm});
            skLineSegment(sketch, "E10809", {"start": v(-12.11, -35.49) * mm, "end": v(-11.27, -36.94) * mm});
            skLineSegment(sketch, "E10810", {"start": v(-11.27, -36.94) * mm, "end": v(-8.39, -35.5) * mm});
            skLineSegment(sketch, "E10811", {"start": v(-8.39, -35.5) * mm, "end": v(-9.08, -33.98) * mm});
            skLineSegment(sketch, "E10812", {"start": v(-9.08, -33.98) * mm, "end": v(-9.1, -33.94) * mm});
            skLineSegment(sketch, "E10813", {"start": v(-9.1, -33.94) * mm, "end": v(-9.15, -33.8) * mm});
            skLineSegment(sketch, "E10814", {"start": v(-9.15, -33.8) * mm, "end": v(-9.21, -33.6) * mm});
            skLineSegment(sketch, "E10815", {"start": v(-9.21, -33.6) * mm, "end": v(-9.3, -33.3) * mm});
            skLineSegment(sketch, "E10816", {"start": v(-9.3, -33.3) * mm, "end": v(-9.37, -32.9) * mm});
            skLineSegment(sketch, "E10817", {"start": v(-9.37, -32.9) * mm, "end": v(-9.44, -32.41) * mm});
            skLineSegment(sketch, "E10818", {"start": v(-9.44, -32.41) * mm, "end": v(-9.5, -31.83) * mm});
            skLineSegment(sketch, "E10819", {"start": v(-9.5, -31.83) * mm, "end": v(-9.53, -31.16) * mm});
            skLineSegment(sketch, "E10820", {"start": v(-9.53, -31.16) * mm, "end": v(-9.53, -30.4) * mm});
            skLineSegment(sketch, "E10821", {"start": v(-9.53, -30.4) * mm, "end": v(-9.52, -30.2) * mm});
            skLineSegment(sketch, "E10822", {"start": v(-9.52, -30.2) * mm, "end": v(-7.39, -29.4) * mm});
            skLineSegment(sketch, "E10823", {"start": v(-7.39, -29.4) * mm, "end": v(-7.24, -29.54) * mm});
            skLineSegment(sketch, "E10824", {"start": v(-7.24, -29.54) * mm, "end": v(-6.72, -30.1) * mm});
            skLineSegment(sketch, "E10825", {"start": v(-6.72, -30.1) * mm, "end": v(-6.3, -30.63) * mm});
            skLineSegment(sketch, "E10826", {"start": v(-6.3, -30.63) * mm, "end": v(-5.95, -31.1) * mm});
            skLineSegment(sketch, "E10827", {"start": v(-5.95, -31.1) * mm, "end": v(-5.67, -31.5) * mm});
            skLineSegment(sketch, "E10828", {"start": v(-5.67, -31.5) * mm, "end": v(-5.46, -31.85) * mm});
            skLineSegment(sketch, "E10829", {"start": v(-5.46, -31.85) * mm, "end": v(-5.32, -32.13) * mm});
            skLineSegment(sketch, "E10830", {"start": v(-5.32, -32.13) * mm, "end": v(-5.22, -32.33) * mm});
            skLineSegment(sketch, "E10831", {"start": v(-5.22, -32.33) * mm, "end": v(-5.17, -32.46) * mm});
            skLineSegment(sketch, "E10832", {"start": v(-5.17, -32.46) * mm, "end": v(-5.16, -32.5) * mm});
            skLineSegment(sketch, "E10833", {"start": v(-5.16, -32.5) * mm, "end": v(-4.64, -34.1) * mm});
            skLineSegment(sketch, "E10834", {"start": v(-4.64, -34.1) * mm, "end": v(-1.52, -33.28) * mm});
            skLineSegment(sketch, "E10835", {"start": v(-1.52, -33.28) * mm, "end": v(-1.87, -31.64) * mm});
            skLineSegment(sketch, "E10836", {"start": v(-1.87, -31.64) * mm, "end": v(-1.88, -31.6) * mm});
            skLineSegment(sketch, "E10837", {"start": v(-1.88, -31.6) * mm, "end": v(-1.9, -31.46) * mm});
            skLineSegment(sketch, "E10838", {"start": v(-1.9, -31.46) * mm, "end": v(-1.92, -31.24) * mm});
            skLineSegment(sketch, "E10839", {"start": v(-1.92, -31.24) * mm, "end": v(-1.93, -30.93) * mm});
            skLineSegment(sketch, "E10840", {"start": v(-1.93, -30.93) * mm, "end": v(-1.93, -30.53) * mm});
            skLineSegment(sketch, "E10841", {"start": v(-1.93, -30.53) * mm, "end": v(-1.9, -30.04) * mm});
            skLineSegment(sketch, "E10842", {"start": v(-1.9, -30.04) * mm, "end": v(-1.83, -29.46) * mm});
            skLineSegment(sketch, "E10843", {"start": v(-1.83, -29.46) * mm, "end": v(-1.72, -28.8) * mm});
            skLineSegment(sketch, "E10844", {"start": v(-1.72, -28.8) * mm, "end": v(-1.56, -28.05) * mm});
            skLineSegment(sketch, "E10845", {"start": v(-1.56, -28.05) * mm, "end": v(-1.5, -27.86) * mm});
            skLineSegment(sketch, "E10846", {"start": v(-1.5, -27.86) * mm, "end": v(0.75, -27.5) * mm});
            skLineSegment(sketch, "E10847", {"start": v(0.75, -27.5) * mm, "end": v(0.87, -27.68) * mm});
            skLineSegment(sketch, "E10848", {"start": v(0.87, -27.68) * mm, "end": v(1.25, -28.34) * mm});
            skLineSegment(sketch, "E10849", {"start": v(1.25, -28.34) * mm, "end": v(1.56, -28.94) * mm});
            skLineSegment(sketch, "E10850", {"start": v(1.56, -28.94) * mm, "end": v(1.8, -29.47) * mm});
            skLineSegment(sketch, "E10851", {"start": v(1.8, -29.47) * mm, "end": v(1.98, -29.92) * mm});
            skLineSegment(sketch, "E10852", {"start": v(1.98, -29.92) * mm, "end": v(2.11, -30.3) * mm});
            skLineSegment(sketch, "E10853", {"start": v(2.11, -30.3) * mm, "end": v(2.2, -30.6) * mm});
            skLineSegment(sketch, "E10854", {"start": v(2.2, -30.6) * mm, "end": v(2.25, -30.82) * mm});
            skLineSegment(sketch, "E10855", {"start": v(2.25, -30.82) * mm, "end": v(2.27, -30.96) * mm});
            skLineSegment(sketch, "E10856", {"start": v(2.27, -30.96) * mm, "end": v(2.28, -31) * mm});
            skLineSegment(sketch, "E10857", {"start": v(2.28, -31) * mm, "end": v(2.45, -32.67) * mm});
            skLineSegment(sketch, "E10858", {"start": v(2.45, -32.67) * mm, "end": v(5.68, -32.5) * mm});
            skLineSegment(sketch, "E10859", {"start": v(5.68, -32.5) * mm, "end": v(5.67, -30.83) * mm});
            skLineSegment(sketch, "E10860", {"start": v(5.67, -30.83) * mm, "end": v(5.67, -30.79) * mm});
            skLineSegment(sketch, "E10861", {"start": v(5.67, -30.79) * mm, "end": v(5.68, -30.65) * mm});
            skLineSegment(sketch, "E10862", {"start": v(5.68, -30.65) * mm, "end": v(5.7, -30.43) * mm});
            skLineSegment(sketch, "E10863", {"start": v(5.7, -30.43) * mm, "end": v(5.76, -30.12) * mm});
            skLineSegment(sketch, "E10864", {"start": v(5.76, -30.12) * mm, "end": v(5.85, -29.73) * mm});
            skLineSegment(sketch, "E10865", {"start": v(5.85, -29.73) * mm, "end": v(5.99, -29.26) * mm});
            skLineSegment(sketch, "E10866", {"start": v(5.99, -29.26) * mm, "end": v(6.18, -28.7) * mm});
            skLineSegment(sketch, "E10867", {"start": v(6.18, -28.7) * mm, "end": v(6.42, -28.08) * mm});
            skLineSegment(sketch, "E10868", {"start": v(6.42, -28.08) * mm, "end": v(6.74, -27.39) * mm});
            skLineSegment(sketch, "E10869", {"start": v(6.74, -27.39) * mm, "end": v(6.83, -27.2) * mm});
            skLineSegment(sketch, "E10870", {"start": v(6.83, -27.2) * mm, "end": v(9.11, -27.33) * mm});
            skLineSegment(sketch, "E10871", {"start": v(9.11, -27.33) * mm, "end": v(9.19, -27.52) * mm});
            skLineSegment(sketch, "E10872", {"start": v(9.19, -27.52) * mm, "end": v(9.43, -28.24) * mm});
            skLineSegment(sketch, "E10873", {"start": v(9.43, -28.24) * mm, "end": v(9.6, -28.9) * mm});
            skLineSegment(sketch, "E10874", {"start": v(9.6, -28.9) * mm, "end": v(9.73, -29.46) * mm});
            skLineSegment(sketch, "E10875", {"start": v(9.73, -29.46) * mm, "end": v(9.8, -29.94) * mm});
            skLineSegment(sketch, "E10876", {"start": v(9.8, -29.94) * mm, "end": v(9.85, -30.34) * mm});
            skLineSegment(sketch, "E10877", {"start": v(9.85, -30.34) * mm, "end": v(9.88, -30.66) * mm});
            skLineSegment(sketch, "E10878", {"start": v(9.88, -30.66) * mm, "end": v(9.88, -30.88) * mm});
            skLineSegment(sketch, "E10879", {"start": v(9.88, -30.88) * mm, "end": v(9.87, -31.01) * mm});
            skLineSegment(sketch, "E10880", {"start": v(9.87, -31.01) * mm, "end": v(9.87, -31.06) * mm});
            skLineSegment(sketch, "E10881", {"start": v(9.87, -31.06) * mm, "end": v(9.68, -32.72) * mm});
            skLineSegment(sketch, "E10882", {"start": v(9.68, -32.72) * mm, "end": v(12.87, -33.22) * mm});
            skLineSegment(sketch, "E10883", {"start": v(12.87, -33.22) * mm, "end": v(13.22, -31.59) * mm});
            skLineSegment(sketch, "E10884", {"start": v(13.22, -31.59) * mm, "end": v(13.23, -31.54) * mm});
            skLineSegment(sketch, "E10885", {"start": v(13.23, -31.54) * mm, "end": v(13.27, -31.41) * mm});
            skLineSegment(sketch, "E10886", {"start": v(13.27, -31.41) * mm, "end": v(13.34, -31.2) * mm});
            skLineSegment(sketch, "E10887", {"start": v(13.34, -31.2) * mm, "end": v(13.46, -30.91) * mm});
            skLineSegment(sketch, "E10888", {"start": v(13.46, -30.91) * mm, "end": v(13.63, -30.55) * mm});
            skLineSegment(sketch, "E10889", {"start": v(13.63, -30.55) * mm, "end": v(13.87, -30.11) * mm});
            skLineSegment(sketch, "E10890", {"start": v(13.87, -30.11) * mm, "end": v(14.16, -29.61) * mm});
            skLineSegment(sketch, "E10891", {"start": v(14.16, -29.61) * mm, "end": v(14.54, -29.05) * mm});
            skLineSegment(sketch, "E10892", {"start": v(14.54, -29.05) * mm, "end": v(15, -28.44) * mm});
            skLineSegment(sketch, "E10893", {"start": v(15, -28.44) * mm, "end": v(15.12, -28.28) * mm});
            skLineSegment(sketch, "E10894", {"start": v(15.12, -28.28) * mm, "end": v(17.33, -28.86) * mm});
            skLineSegment(sketch, "E10895", {"start": v(17.33, -28.86) * mm, "end": v(17.36, -29.07) * mm});
            skLineSegment(sketch, "E10896", {"start": v(17.36, -29.07) * mm, "end": v(17.44, -29.82) * mm});
            skLineSegment(sketch, "E10897", {"start": v(17.44, -29.82) * mm, "end": v(17.48, -30.5) * mm});
            skLineSegment(sketch, "E10898", {"start": v(17.48, -30.5) * mm, "end": v(17.48, -31.07) * mm});
            skLineSegment(sketch, "E10899", {"start": v(17.48, -31.07) * mm, "end": v(17.46, -31.56) * mm});
            skLineSegment(sketch, "E10900", {"start": v(17.46, -31.56) * mm, "end": v(17.42, -31.96) * mm});
            skLineSegment(sketch, "E10901", {"start": v(17.42, -31.96) * mm, "end": v(17.37, -32.27) * mm});
            skLineSegment(sketch, "E10902", {"start": v(17.37, -32.27) * mm, "end": v(17.33, -32.5) * mm});
            skLineSegment(sketch, "E10903", {"start": v(17.33, -32.5) * mm, "end": v(17.3, -32.62) * mm});
            skLineSegment(sketch, "E10904", {"start": v(17.3, -32.62) * mm, "end": v(17.28, -32.67) * mm});
            skLineSegment(sketch, "E10905", {"start": v(17.28, -32.67) * mm, "end": v(16.75, -34.25) * mm});
            skLineSegment(sketch, "E10906", {"start": v(16.75, -34.25) * mm, "end": v(19.76, -35.4) * mm});
            skLineSegment(sketch, "E10907", {"start": v(19.76, -35.4) * mm, "end": v(20.45, -33.87) * mm});
            skLineSegment(sketch, "E10908", {"start": v(20.45, -33.87) * mm, "end": v(20.47, -33.83) * mm});
            skLineSegment(sketch, "E10909", {"start": v(20.47, -33.83) * mm, "end": v(20.53, -33.71) * mm});
            skLineSegment(sketch, "E10910", {"start": v(20.53, -33.71) * mm, "end": v(20.65, -33.52) * mm});
            skLineSegment(sketch, "E10911", {"start": v(20.65, -33.52) * mm, "end": v(20.83, -33.26) * mm});
            skLineSegment(sketch, "E10912", {"start": v(20.83, -33.26) * mm, "end": v(21.07, -32.94) * mm});
            skLineSegment(sketch, "E10913", {"start": v(21.07, -32.94) * mm, "end": v(21.39, -32.56) * mm});
            skLineSegment(sketch, "E10914", {"start": v(21.39, -32.56) * mm, "end": v(21.79, -32.13) * mm});
            skLineSegment(sketch, "E10915", {"start": v(21.79, -32.13) * mm, "end": v(22.27, -31.66) * mm});
            skLineSegment(sketch, "E10916", {"start": v(22.27, -31.66) * mm, "end": v(22.85, -31.15) * mm});
            skLineSegment(sketch, "E10917", {"start": v(22.85, -31.15) * mm, "end": v(23, -31.02) * mm});
            skLineSegment(sketch, "E10918", {"start": v(23, -31.02) * mm, "end": v(25.04, -32.05) * mm});
            skLineSegment(sketch, "E10919", {"start": v(25.04, -32.05) * mm, "end": v(25.03, -32.25) * mm});
            skLineSegment(sketch, "E10920", {"start": v(25.03, -32.25) * mm, "end": v(24.95, -33) * mm});
            skLineSegment(sketch, "E10921", {"start": v(24.95, -33) * mm, "end": v(24.84, -33.67) * mm});
            skLineSegment(sketch, "E10922", {"start": v(24.84, -33.67) * mm, "end": v(24.72, -34.24) * mm});
            skLineSegment(sketch, "E10923", {"start": v(24.72, -34.24) * mm, "end": v(24.6, -34.72) * mm});
            skLineSegment(sketch, "E10924", {"start": v(24.6, -34.72) * mm, "end": v(24.47, -35.1) * mm});
            skLineSegment(sketch, "E10925", {"start": v(24.47, -35.1) * mm, "end": v(24.36, -35.4) * mm});
            skLineSegment(sketch, "E10926", {"start": v(24.36, -35.4) * mm, "end": v(24.27, -35.6) * mm});
            skLineSegment(sketch, "E10927", {"start": v(24.27, -35.6) * mm, "end": v(24.21, -35.72) * mm});
            skLineSegment(sketch, "E10928", {"start": v(24.21, -35.72) * mm, "end": v(24.2, -35.76) * mm});
            skLineSegment(sketch, "E10929", {"start": v(24.2, -35.76) * mm, "end": v(23.33, -37.2) * mm});
            skLineSegment(sketch, "E10930", {"start": v(23.33, -37.2) * mm, "end": v(26.04, -38.94) * mm});
            skLineSegment(sketch, "E10931", {"start": v(26.04, -38.94) * mm, "end": v(27.04, -37.58) * mm});
            skLineSegment(sketch, "E10932", {"start": v(27.04, -37.58) * mm, "end": v(27.06, -37.55) * mm});
            skLineSegment(sketch, "E10933", {"start": v(27.06, -37.55) * mm, "end": v(27.15, -37.45) * mm});
            skLineSegment(sketch, "E10934", {"start": v(27.15, -37.45) * mm, "end": v(27.3, -37.28) * mm});
            skLineSegment(sketch, "E10935", {"start": v(27.3, -37.28) * mm, "end": v(27.53, -37.07) * mm});
            skLineSegment(sketch, "E10936", {"start": v(27.53, -37.07) * mm, "end": v(27.84, -36.8) * mm});
            skLineSegment(sketch, "E10937", {"start": v(27.84, -36.8) * mm, "end": v(28.23, -36.5) * mm});
            skLineSegment(sketch, "E10938", {"start": v(28.23, -36.5) * mm, "end": v(28.71, -36.16) * mm});
            skLineSegment(sketch, "E10939", {"start": v(28.71, -36.16) * mm, "end": v(29.29, -35.8) * mm});
            skLineSegment(sketch, "E10940", {"start": v(29.29, -35.8) * mm, "end": v(29.95, -35.42) * mm});
            skLineSegment(sketch, "E10941", {"start": v(29.95, -35.42) * mm, "end": v(30.14, -35.32) * mm});
            skLineSegment(sketch, "E10942", {"start": v(30.14, -35.32) * mm, "end": v(31.91, -36.74) * mm});
            skLineSegment(sketch, "E10943", {"start": v(31.91, -36.74) * mm, "end": v(31.86, -36.94) * mm});
            skLineSegment(sketch, "E10944", {"start": v(31.86, -36.94) * mm, "end": v(31.62, -37.66) * mm});
            skLineSegment(sketch, "E10945", {"start": v(31.62, -37.66) * mm, "end": v(31.38, -38.29) * mm});
            skLineSegment(sketch, "E10946", {"start": v(31.38, -38.29) * mm, "end": v(31.14, -38.82) * mm});
            skLineSegment(sketch, "E10947", {"start": v(31.14, -38.82) * mm, "end": v(30.91, -39.26) * mm});
            skLineSegment(sketch, "E10948", {"start": v(30.91, -39.26) * mm, "end": v(30.71, -39.6) * mm});
            skLineSegment(sketch, "E10949", {"start": v(30.71, -39.6) * mm, "end": v(30.54, -39.87) * mm});
            skLineSegment(sketch, "E10950", {"start": v(30.54, -39.87) * mm, "end": v(30.41, -40.06) * mm});
            skLineSegment(sketch, "E10951", {"start": v(30.41, -40.06) * mm, "end": v(30.33, -40.16) * mm});
            skLineSegment(sketch, "E10952", {"start": v(30.33, -40.16) * mm, "end": v(30.3, -40.2) * mm});
            skLineSegment(sketch, "E10953", {"start": v(30.3, -40.2) * mm, "end": v(29.15, -41.43) * mm});
            skLineSegment(sketch, "E10954", {"start": v(29.15, -41.43) * mm, "end": v(31.44, -43.69) * mm});
            skCircle(sketch, "E10955", {"center": v(-94.2, 83.41) * mm, "radius": 1.25 * mm});
            skLineSegment(sketch, "E10956", {"start": v(-97.2, 81.35) * mm, "end": v(-91.2, 81.35) * mm});
            skLineSegment(sketch, "E10957", {"start": v(-91.2, 81.35) * mm, "end": v(-91.2, 85.48) * mm});
            skLineSegment(sketch, "E10958", {"start": v(-91.2, 85.48) * mm, "end": v(-97.2, 85.48) * mm});
            skLineSegment(sketch, "E10959", {"start": v(-97.2, 85.48) * mm, "end": v(-97.2, 81.35) * mm});
            skCircle(sketch, "E10960", {"center": v(-94.2, 83.41) * mm, "radius": 3.75 * mm});
            skLineSegment(sketch, "E10961", {"start": v(-70.58, 104.83) * mm, "end": v(-69.27, 106.02) * mm});
            skLineSegment(sketch, "E10962", {"start": v(-69.27, 106.02) * mm, "end": v(-69.24, 106.05) * mm});
            skLineSegment(sketch, "E10963", {"start": v(-69.24, 106.05) * mm, "end": v(-69.14, 106.12) * mm});
            skLineSegment(sketch, "E10964", {"start": v(-69.14, 106.12) * mm, "end": v(-68.96, 106.24) * mm});
            skLineSegment(sketch, "E10965", {"start": v(-68.96, 106.24) * mm, "end": v(-68.71, 106.4) * mm});
            skLineSegment(sketch, "E10966", {"start": v(-68.71, 106.4) * mm, "end": v(-68.38, 106.59) * mm});
            skLineSegment(sketch, "E10967", {"start": v(-68.38, 106.59) * mm, "end": v(-67.97, 106.8) * mm});
            skLineSegment(sketch, "E10968", {"start": v(-67.97, 106.8) * mm, "end": v(-67.46, 107.01) * mm});
            skLineSegment(sketch, "E10969", {"start": v(-67.46, 107.01) * mm, "end": v(-66.87, 107.24) * mm});
            skLineSegment(sketch, "E10970", {"start": v(-66.87, 107.24) * mm, "end": v(-66.19, 107.46) * mm});
            skLineSegment(sketch, "E10971", {"start": v(-66.19, 107.46) * mm, "end": v(-65.82, 107.56) * mm});
            skLineSegment(sketch, "E10972", {"start": v(-65.82, 107.56) * mm, "end": v(-64.4, 105.83) * mm});
            skLineSegment(sketch, "E10973", {"start": v(-64.4, 105.83) * mm, "end": v(-64.57, 105.5) * mm});
            skLineSegment(sketch, "E10974", {"start": v(-64.57, 105.5) * mm, "end": v(-64.93, 104.89) * mm});
            skLineSegment(sketch, "E10975", {"start": v(-64.93, 104.89) * mm, "end": v(-65.28, 104.36) * mm});
            skLineSegment(sketch, "E10976", {"start": v(-65.28, 104.36) * mm, "end": v(-65.6, 103.92) * mm});
            skLineSegment(sketch, "E10977", {"start": v(-65.6, 103.92) * mm, "end": v(-65.89, 103.56) * mm});
            skLineSegment(sketch, "E10978", {"start": v(-65.89, 103.56) * mm, "end": v(-66.14, 103.28) * mm});
            skLineSegment(sketch, "E10979", {"start": v(-66.14, 103.28) * mm, "end": v(-66.35, 103.07) * mm});
            skLineSegment(sketch, "E10980", {"start": v(-66.35, 103.07) * mm, "end": v(-66.5, 102.93) * mm});
            skLineSegment(sketch, "E10981", {"start": v(-66.5, 102.93) * mm, "end": v(-66.6, 102.85) * mm});
            skLineSegment(sketch, "E10982", {"start": v(-66.6, 102.85) * mm, "end": v(-66.63, 102.82) * mm});
            skLineSegment(sketch, "E10983", {"start": v(-66.63, 102.82) * mm, "end": v(-68.08, 101.8) * mm});
            skLineSegment(sketch, "E10984", {"start": v(-68.08, 101.8) * mm, "end": v(-66.33, 99.12) * mm});
            skLineSegment(sketch, "E10985", {"start": v(-66.33, 99.12) * mm, "end": v(-64.79, 99.99) * mm});
            skLineSegment(sketch, "E10986", {"start": v(-64.79, 99.99) * mm, "end": v(-64.75, 100) * mm});
            skLineSegment(sketch, "E10987", {"start": v(-64.75, 100) * mm, "end": v(-64.63, 100.06) * mm});
            skLineSegment(sketch, "E10988", {"start": v(-64.63, 100.06) * mm, "end": v(-64.44, 100.14) * mm});
            skLineSegment(sketch, "E10989", {"start": v(-64.44, 100.14) * mm, "end": v(-64.16, 100.24) * mm});
            skLineSegment(sketch, "E10990", {"start": v(-64.16, 100.24) * mm, "end": v(-63.8, 100.35) * mm});
            skLineSegment(sketch, "E10991", {"start": v(-63.8, 100.35) * mm, "end": v(-63.34, 100.46) * mm});
            skLineSegment(sketch, "E10992", {"start": v(-63.34, 100.46) * mm, "end": v(-62.8, 100.56) * mm});
            skLineSegment(sketch, "E10993", {"start": v(-62.8, 100.56) * mm, "end": v(-62.17, 100.65) * mm});
            skLineSegment(sketch, "E10994", {"start": v(-62.17, 100.65) * mm, "end": v(-61.46, 100.72) * mm});
            skLineSegment(sketch, "E10995", {"start": v(-61.46, 100.72) * mm, "end": v(-61.08, 100.74) * mm});
            skLineSegment(sketch, "E10996", {"start": v(-61.08, 100.74) * mm, "end": v(-60.08, 98.74) * mm});
            skLineSegment(sketch, "E10997", {"start": v(-60.08, 98.74) * mm, "end": v(-60.32, 98.45) * mm});
            skLineSegment(sketch, "E10998", {"start": v(-60.32, 98.45) * mm, "end": v(-60.81, 97.93) * mm});
            skLineSegment(sketch, "E10999", {"start": v(-60.81, 97.93) * mm, "end": v(-61.27, 97.5) * mm});
            skLineSegment(sketch, "E11000", {"start": v(-61.27, 97.5) * mm, "end": v(-61.68, 97.14) * mm});
            skLineSegment(sketch, "E11001", {"start": v(-61.68, 97.14) * mm, "end": v(-62.04, 96.85) * mm});
            skLineSegment(sketch, "E11002", {"start": v(-62.04, 96.85) * mm, "end": v(-62.35, 96.63) * mm});
            skLineSegment(sketch, "E11003", {"start": v(-62.35, 96.63) * mm, "end": v(-62.6, 96.48) * mm});
            skLineSegment(sketch, "E11004", {"start": v(-62.6, 96.48) * mm, "end": v(-62.79, 96.37) * mm});
            skLineSegment(sketch, "E11005", {"start": v(-62.79, 96.37) * mm, "end": v(-62.9, 96.32) * mm});
            skLineSegment(sketch, "E11006", {"start": v(-62.9, 96.32) * mm, "end": v(-62.94, 96.3) * mm});
            skLineSegment(sketch, "E11007", {"start": v(-62.94, 96.3) * mm, "end": v(-64.58, 95.62) * mm});
            skLineSegment(sketch, "E11008", {"start": v(-64.58, 95.62) * mm, "end": v(-63.48, 92.62) * mm});
            skLineSegment(sketch, "E11009", {"start": v(-63.48, 92.62) * mm, "end": v(-61.78, 93.13) * mm});
            skLineSegment(sketch, "E11010", {"start": v(-61.78, 93.13) * mm, "end": v(-61.74, 93.14) * mm});
            skLineSegment(sketch, "E11011", {"start": v(-61.74, 93.14) * mm, "end": v(-61.61, 93.17) * mm});
            skLineSegment(sketch, "E11012", {"start": v(-61.61, 93.17) * mm, "end": v(-61.4, 93.2) * mm});
            skLineSegment(sketch, "E11013", {"start": v(-61.4, 93.2) * mm, "end": v(-61.11, 93.24) * mm});
            skLineSegment(sketch, "E11014", {"start": v(-61.11, 93.24) * mm, "end": v(-60.73, 93.26) * mm});
            skLineSegment(sketch, "E11015", {"start": v(-60.73, 93.26) * mm, "end": v(-60.26, 93.27) * mm});
            skLineSegment(sketch, "E11016", {"start": v(-60.26, 93.27) * mm, "end": v(-59.71, 93.25) * mm});
            skLineSegment(sketch, "E11017", {"start": v(-59.71, 93.25) * mm, "end": v(-59.08, 93.2) * mm});
            skLineSegment(sketch, "E11018", {"start": v(-59.08, 93.2) * mm, "end": v(-58.37, 93.11) * mm});
            skLineSegment(sketch, "E11019", {"start": v(-58.37, 93.11) * mm, "end": v(-58, 93.05) * mm});
            skLineSegment(sketch, "E11020", {"start": v(-58, 93.05) * mm, "end": v(-57.47, 90.88) * mm});
            skLineSegment(sketch, "E11021", {"start": v(-57.47, 90.88) * mm, "end": v(-57.77, 90.65) * mm});
            skLineSegment(sketch, "E11022", {"start": v(-57.77, 90.65) * mm, "end": v(-58.37, 90.25) * mm});
            skLineSegment(sketch, "E11023", {"start": v(-58.37, 90.25) * mm, "end": v(-58.91, 89.93) * mm});
            skLineSegment(sketch, "E11024", {"start": v(-58.91, 89.93) * mm, "end": v(-59.4, 89.67) * mm});
            skLineSegment(sketch, "E11025", {"start": v(-59.4, 89.67) * mm, "end": v(-59.81, 89.47) * mm});
            skLineSegment(sketch, "E11026", {"start": v(-59.81, 89.47) * mm, "end": v(-60.17, 89.33) * mm});
            skLineSegment(sketch, "E11027", {"start": v(-60.17, 89.33) * mm, "end": v(-60.44, 89.23) * mm});
            skLineSegment(sketch, "E11028", {"start": v(-60.44, 89.23) * mm, "end": v(-60.65, 89.16) * mm});
            skLineSegment(sketch, "E11029", {"start": v(-60.65, 89.16) * mm, "end": v(-60.77, 89.13) * mm});
            skLineSegment(sketch, "E11030", {"start": v(-60.77, 89.13) * mm, "end": v(-60.81, 89.13) * mm});
            skLineSegment(sketch, "E11031", {"start": v(-60.81, 89.13) * mm, "end": v(-62.56, 88.83) * mm});
            skLineSegment(sketch, "E11032", {"start": v(-62.56, 88.83) * mm, "end": v(-62.17, 85.66) * mm});
            skLineSegment(sketch, "E11033", {"start": v(-62.17, 85.66) * mm, "end": v(-60.4, 85.78) * mm});
            skLineSegment(sketch, "E11034", {"start": v(-60.4, 85.78) * mm, "end": v(-60.35, 85.78) * mm});
            skLineSegment(sketch, "E11035", {"start": v(-60.35, 85.78) * mm, "end": v(-60.23, 85.78) * mm});
            skLineSegment(sketch, "E11036", {"start": v(-60.23, 85.78) * mm, "end": v(-60.02, 85.77) * mm});
            skLineSegment(sketch, "E11037", {"start": v(-60.02, 85.77) * mm, "end": v(-59.72, 85.74) * mm});
            skLineSegment(sketch, "E11038", {"start": v(-59.72, 85.74) * mm, "end": v(-59.34, 85.68) * mm});
            skLineSegment(sketch, "E11039", {"start": v(-59.34, 85.68) * mm, "end": v(-58.89, 85.59) * mm});
            skLineSegment(sketch, "E11040", {"start": v(-58.89, 85.59) * mm, "end": v(-58.36, 85.45) * mm});
            skLineSegment(sketch, "E11041", {"start": v(-58.36, 85.45) * mm, "end": v(-57.75, 85.26) * mm});
            skLineSegment(sketch, "E11042", {"start": v(-57.75, 85.26) * mm, "end": v(-57.07, 85.02) * mm});
            skLineSegment(sketch, "E11043", {"start": v(-57.07, 85.02) * mm, "end": v(-56.73, 84.87) * mm});
            skLineSegment(sketch, "E11044", {"start": v(-56.73, 84.87) * mm, "end": v(-56.7, 82.64) * mm});
            skLineSegment(sketch, "E11045", {"start": v(-56.7, 82.64) * mm, "end": v(-57.05, 82.49) * mm});
            skLineSegment(sketch, "E11046", {"start": v(-57.05, 82.49) * mm, "end": v(-57.72, 82.23) * mm});
            skLineSegment(sketch, "E11047", {"start": v(-57.72, 82.23) * mm, "end": v(-58.32, 82.03) * mm});
            skLineSegment(sketch, "E11048", {"start": v(-58.32, 82.03) * mm, "end": v(-58.85, 81.89) * mm});
            skLineSegment(sketch, "E11049", {"start": v(-58.85, 81.89) * mm, "end": v(-59.3, 81.78) * mm});
            skLineSegment(sketch, "E11050", {"start": v(-59.3, 81.78) * mm, "end": v(-59.68, 81.72) * mm});
            skLineSegment(sketch, "E11051", {"start": v(-59.68, 81.72) * mm, "end": v(-59.98, 81.68) * mm});
            skLineSegment(sketch, "E11052", {"start": v(-59.98, 81.68) * mm, "end": v(-60.19, 81.67) * mm});
            skLineSegment(sketch, "E11053", {"start": v(-60.19, 81.67) * mm, "end": v(-60.32, 81.67) * mm});
            skLineSegment(sketch, "E11054", {"start": v(-60.32, 81.67) * mm, "end": v(-60.36, 81.67) * mm});
            skLineSegment(sketch, "E11055", {"start": v(-60.36, 81.67) * mm, "end": v(-62.13, 81.76) * mm});
            skLineSegment(sketch, "E11056", {"start": v(-62.13, 81.76) * mm, "end": v(-62.47, 78.58) * mm});
            skLineSegment(sketch, "E11057", {"start": v(-62.47, 78.58) * mm, "end": v(-60.7, 78.31) * mm});
            skLineSegment(sketch, "E11058", {"start": v(-60.7, 78.31) * mm, "end": v(-60.67, 78.3) * mm});
            skLineSegment(sketch, "E11059", {"start": v(-60.67, 78.3) * mm, "end": v(-60.54, 78.28) * mm});
            skLineSegment(sketch, "E11060", {"start": v(-60.54, 78.28) * mm, "end": v(-60.34, 78.22) * mm});
            skLineSegment(sketch, "E11061", {"start": v(-60.34, 78.22) * mm, "end": v(-60.06, 78.13) * mm});
            skLineSegment(sketch, "E11062", {"start": v(-60.06, 78.13) * mm, "end": v(-59.7, 77.99) * mm});
            skLineSegment(sketch, "E11063", {"start": v(-59.7, 77.99) * mm, "end": v(-59.28, 77.8) * mm});
            skLineSegment(sketch, "E11064", {"start": v(-59.28, 77.8) * mm, "end": v(-58.8, 77.55) * mm});
            skLineSegment(sketch, "E11065", {"start": v(-58.8, 77.55) * mm, "end": v(-58.25, 77.23) * mm});
            skLineSegment(sketch, "E11066", {"start": v(-58.25, 77.23) * mm, "end": v(-57.64, 76.84) * mm});
            skLineSegment(sketch, "E11067", {"start": v(-57.64, 76.84) * mm, "end": v(-57.34, 76.62) * mm});
            skLineSegment(sketch, "E11068", {"start": v(-57.34, 76.62) * mm, "end": v(-57.82, 74.45) * mm});
            skLineSegment(sketch, "E11069", {"start": v(-57.82, 74.45) * mm, "end": v(-58.2, 74.37) * mm});
            skLineSegment(sketch, "E11070", {"start": v(-58.2, 74.37) * mm, "end": v(-58.9, 74.27) * mm});
            skLineSegment(sketch, "E11071", {"start": v(-58.9, 74.27) * mm, "end": v(-59.53, 74.2) * mm});
            skLineSegment(sketch, "E11072", {"start": v(-59.53, 74.2) * mm, "end": v(-60.08, 74.18) * mm});
            skLineSegment(sketch, "E11073", {"start": v(-60.08, 74.18) * mm, "end": v(-60.55, 74.18) * mm});
            skLineSegment(sketch, "E11074", {"start": v(-60.55, 74.18) * mm, "end": v(-60.93, 74.2) * mm});
            skLineSegment(sketch, "E11075", {"start": v(-60.93, 74.2) * mm, "end": v(-61.23, 74.23) * mm});
            skLineSegment(sketch, "E11076", {"start": v(-61.23, 74.23) * mm, "end": v(-61.44, 74.26) * mm});
            skLineSegment(sketch, "E11077", {"start": v(-61.44, 74.26) * mm, "end": v(-61.56, 74.28) * mm});
            skLineSegment(sketch, "E11078", {"start": v(-61.56, 74.28) * mm, "end": v(-61.6, 74.3) * mm});
            skLineSegment(sketch, "E11079", {"start": v(-61.6, 74.3) * mm, "end": v(-63.31, 74.77) * mm});
            skLineSegment(sketch, "E11080", {"start": v(-63.31, 74.77) * mm, "end": v(-64.35, 71.75) * mm});
            skLineSegment(sketch, "E11081", {"start": v(-64.35, 71.75) * mm, "end": v(-62.7, 71.1) * mm});
            skLineSegment(sketch, "E11082", {"start": v(-62.7, 71.1) * mm, "end": v(-62.66, 71.09) * mm});
            skLineSegment(sketch, "E11083", {"start": v(-62.66, 71.09) * mm, "end": v(-62.55, 71.03) * mm});
            skLineSegment(sketch, "E11084", {"start": v(-62.55, 71.03) * mm, "end": v(-62.36, 70.93) * mm});
            skLineSegment(sketch, "E11085", {"start": v(-62.36, 70.93) * mm, "end": v(-62.11, 70.78) * mm});
            skLineSegment(sketch, "E11086", {"start": v(-62.11, 70.78) * mm, "end": v(-61.8, 70.56) * mm});
            skLineSegment(sketch, "E11087", {"start": v(-61.8, 70.56) * mm, "end": v(-61.43, 70.29) * mm});
            skLineSegment(sketch, "E11088", {"start": v(-61.43, 70.29) * mm, "end": v(-61, 69.93) * mm});
            skLineSegment(sketch, "E11089", {"start": v(-61, 69.93) * mm, "end": v(-60.54, 69.5) * mm});
            skLineSegment(sketch, "E11090", {"start": v(-60.54, 69.5) * mm, "end": v(-60.04, 69) * mm});
            skLineSegment(sketch, "E11091", {"start": v(-60.04, 69) * mm, "end": v(-59.8, 68.72) * mm});
            skLineSegment(sketch, "E11092", {"start": v(-59.8, 68.72) * mm, "end": v(-60.76, 66.7) * mm});
            skLineSegment(sketch, "E11093", {"start": v(-60.76, 66.7) * mm, "end": v(-61.14, 66.7) * mm});
            skLineSegment(sketch, "E11094", {"start": v(-61.14, 66.7) * mm, "end": v(-61.85, 66.76) * mm});
            skLineSegment(sketch, "E11095", {"start": v(-61.85, 66.76) * mm, "end": v(-62.48, 66.84) * mm});
            skLineSegment(sketch, "E11096", {"start": v(-62.48, 66.84) * mm, "end": v(-63.03, 66.94) * mm});
            skLineSegment(sketch, "E11097", {"start": v(-63.03, 66.94) * mm, "end": v(-63.48, 67.04) * mm});
            skLineSegment(sketch, "E11098", {"start": v(-63.48, 67.04) * mm, "end": v(-63.85, 67.14) * mm});
            skLineSegment(sketch, "E11099", {"start": v(-63.85, 67.14) * mm, "end": v(-64.13, 67.23) * mm});
            skLineSegment(sketch, "E11100", {"start": v(-64.13, 67.23) * mm, "end": v(-64.33, 67.3) * mm});
            skLineSegment(sketch, "E11101", {"start": v(-64.33, 67.3) * mm, "end": v(-64.44, 67.36) * mm});
            skLineSegment(sketch, "E11102", {"start": v(-64.44, 67.36) * mm, "end": v(-64.48, 67.38) * mm});
            skLineSegment(sketch, "E11103", {"start": v(-64.48, 67.38) * mm, "end": v(-66.04, 68.22) * mm});
            skLineSegment(sketch, "E11104", {"start": v(-66.04, 68.22) * mm, "end": v(-67.74, 65.5) * mm});
            skLineSegment(sketch, "E11105", {"start": v(-67.74, 65.5) * mm, "end": v(-66.27, 64.51) * mm});
            skLineSegment(sketch, "E11106", {"start": v(-66.27, 64.51) * mm, "end": v(-66.24, 64.49) * mm});
            skLineSegment(sketch, "E11107", {"start": v(-66.24, 64.49) * mm, "end": v(-66.14, 64.4) * mm});
            skLineSegment(sketch, "E11108", {"start": v(-66.14, 64.4) * mm, "end": v(-65.98, 64.27) * mm});
            skLineSegment(sketch, "E11109", {"start": v(-65.98, 64.27) * mm, "end": v(-65.77, 64.06) * mm});
            skLineSegment(sketch, "E11110", {"start": v(-65.77, 64.06) * mm, "end": v(-65.51, 63.79) * mm});
            skLineSegment(sketch, "E11111", {"start": v(-65.51, 63.79) * mm, "end": v(-65.22, 63.43) * mm});
            skLineSegment(sketch, "E11112", {"start": v(-65.22, 63.43) * mm, "end": v(-64.88, 63) * mm});
            skLineSegment(sketch, "E11113", {"start": v(-64.88, 63) * mm, "end": v(-64.53, 62.48) * mm});
            skLineSegment(sketch, "E11114", {"start": v(-64.53, 62.48) * mm, "end": v(-64.16, 61.87) * mm});
            skLineSegment(sketch, "E11115", {"start": v(-64.16, 61.87) * mm, "end": v(-63.98, 61.55) * mm});
            skLineSegment(sketch, "E11116", {"start": v(-63.98, 61.55) * mm, "end": v(-65.37, 59.8) * mm});
            skLineSegment(sketch, "E11117", {"start": v(-65.37, 59.8) * mm, "end": v(-65.74, 59.88) * mm});
            skLineSegment(sketch, "E11118", {"start": v(-65.74, 59.88) * mm, "end": v(-66.43, 60.1) * mm});
            skLineSegment(sketch, "E11119", {"start": v(-66.43, 60.1) * mm, "end": v(-67.02, 60.3) * mm});
            skLineSegment(sketch, "E11120", {"start": v(-67.02, 60.3) * mm, "end": v(-67.53, 60.52) * mm});
            skLineSegment(sketch, "E11121", {"start": v(-67.53, 60.52) * mm, "end": v(-67.95, 60.72) * mm});
            skLineSegment(sketch, "E11122", {"start": v(-67.95, 60.72) * mm, "end": v(-68.29, 60.9) * mm});
            skLineSegment(sketch, "E11123", {"start": v(-68.29, 60.9) * mm, "end": v(-68.54, 61.05) * mm});
            skLineSegment(sketch, "E11124", {"start": v(-68.54, 61.05) * mm, "end": v(-68.71, 61.17) * mm});
            skLineSegment(sketch, "E11125", {"start": v(-68.71, 61.17) * mm, "end": v(-68.81, 61.24) * mm});
            skLineSegment(sketch, "E11126", {"start": v(-68.81, 61.24) * mm, "end": v(-68.85, 61.27) * mm});
            skLineSegment(sketch, "E11127", {"start": v(-68.85, 61.27) * mm, "end": v(-70.18, 62.43) * mm});
            skLineSegment(sketch, "E11128", {"start": v(-70.18, 62.43) * mm, "end": v(-72.45, 60.15) * mm});
            skLineSegment(sketch, "E11129", {"start": v(-72.45, 60.15) * mm, "end": v(-71.24, 58.87) * mm});
            skLineSegment(sketch, "E11130", {"start": v(-71.24, 58.87) * mm, "end": v(-71.22, 58.83) * mm});
            skLineSegment(sketch, "E11131", {"start": v(-71.22, 58.83) * mm, "end": v(-71.14, 58.74) * mm});
            skLineSegment(sketch, "E11132", {"start": v(-71.14, 58.74) * mm, "end": v(-71.01, 58.57) * mm});
            skLineSegment(sketch, "E11133", {"start": v(-71.01, 58.57) * mm, "end": v(-70.86, 58.32) * mm});
            skLineSegment(sketch, "E11134", {"start": v(-70.86, 58.32) * mm, "end": v(-70.67, 58) * mm});
            skLineSegment(sketch, "E11135", {"start": v(-70.67, 58) * mm, "end": v(-70.46, 57.58) * mm});
            skLineSegment(sketch, "E11136", {"start": v(-70.46, 57.58) * mm, "end": v(-70.23, 57.09) * mm});
            skLineSegment(sketch, "E11137", {"start": v(-70.23, 57.09) * mm, "end": v(-70, 56.5) * mm});
            skLineSegment(sketch, "E11138", {"start": v(-70, 56.5) * mm, "end": v(-69.78, 55.83) * mm});
            skLineSegment(sketch, "E11139", {"start": v(-69.78, 55.83) * mm, "end": v(-69.68, 55.47) * mm});
            skLineSegment(sketch, "E11140", {"start": v(-69.68, 55.47) * mm, "end": v(-71.43, 54.07) * mm});
            skLineSegment(sketch, "E11141", {"start": v(-71.43, 54.07) * mm, "end": v(-71.77, 54.24) * mm});
            skLineSegment(sketch, "E11142", {"start": v(-71.77, 54.24) * mm, "end": v(-72.4, 54.6) * mm});
            skLineSegment(sketch, "E11143", {"start": v(-72.4, 54.6) * mm, "end": v(-72.93, 54.93) * mm});
            skLineSegment(sketch, "E11144", {"start": v(-72.93, 54.93) * mm, "end": v(-73.37, 55.25) * mm});
            skLineSegment(sketch, "E11145", {"start": v(-73.37, 55.25) * mm, "end": v(-73.74, 55.54) * mm});
            skLineSegment(sketch, "E11146", {"start": v(-73.74, 55.54) * mm, "end": v(-74.02, 55.78) * mm});
            skLineSegment(sketch, "E11147", {"start": v(-74.02, 55.78) * mm, "end": v(-74.23, 55.99) * mm});
            skLineSegment(sketch, "E11148", {"start": v(-74.23, 55.99) * mm, "end": v(-74.38, 56.14) * mm});
            skLineSegment(sketch, "E11149", {"start": v(-74.38, 56.14) * mm, "end": v(-74.46, 56.24) * mm});
            skLineSegment(sketch, "E11150", {"start": v(-74.46, 56.24) * mm, "end": v(-74.49, 56.27) * mm});
            skLineSegment(sketch, "E11151", {"start": v(-74.49, 56.27) * mm, "end": v(-75.52, 57.7) * mm});
            skLineSegment(sketch, "E11152", {"start": v(-75.52, 57.7) * mm, "end": v(-78.25, 55.97) * mm});
            skLineSegment(sketch, "E11153", {"start": v(-78.25, 55.97) * mm, "end": v(-77.37, 54.45) * mm});
            skLineSegment(sketch, "E11154", {"start": v(-77.37, 54.45) * mm, "end": v(-77.35, 54.41) * mm});
            skLineSegment(sketch, "E11155", {"start": v(-77.35, 54.41) * mm, "end": v(-77.3, 54.3) * mm});
            skLineSegment(sketch, "E11156", {"start": v(-77.3, 54.3) * mm, "end": v(-77.21, 54.1) * mm});
            skLineSegment(sketch, "E11157", {"start": v(-77.21, 54.1) * mm, "end": v(-77.11, 53.83) * mm});
            skLineSegment(sketch, "E11158", {"start": v(-77.11, 53.83) * mm, "end": v(-77, 53.47) * mm});
            skLineSegment(sketch, "E11159", {"start": v(-77, 53.47) * mm, "end": v(-76.89, 53.03) * mm});
            skLineSegment(sketch, "E11160", {"start": v(-76.89, 53.03) * mm, "end": v(-76.78, 52.5) * mm});
            skLineSegment(sketch, "E11161", {"start": v(-76.78, 52.5) * mm, "end": v(-76.7, 51.88) * mm});
            skLineSegment(sketch, "E11162", {"start": v(-76.7, 51.88) * mm, "end": v(-76.62, 51.17) * mm});
            skLineSegment(sketch, "E11163", {"start": v(-76.62, 51.17) * mm, "end": v(-76.6, 50.8) * mm});
            skLineSegment(sketch, "E11164", {"start": v(-76.6, 50.8) * mm, "end": v(-78.63, 49.81) * mm});
            skLineSegment(sketch, "E11165", {"start": v(-78.63, 49.81) * mm, "end": v(-78.92, 50.05) * mm});
            skLineSegment(sketch, "E11166", {"start": v(-78.92, 50.05) * mm, "end": v(-79.45, 50.54) * mm});
            skLineSegment(sketch, "E11167", {"start": v(-79.45, 50.54) * mm, "end": v(-79.9, 50.98) * mm});
            skLineSegment(sketch, "E11168", {"start": v(-79.9, 50.98) * mm, "end": v(-80.26, 51.4) * mm});
            skLineSegment(sketch, "E11169", {"start": v(-80.26, 51.4) * mm, "end": v(-80.55, 51.75) * mm});
            skLineSegment(sketch, "E11170", {"start": v(-80.55, 51.75) * mm, "end": v(-80.77, 52.06) * mm});
            skLineSegment(sketch, "E11171", {"start": v(-80.77, 52.06) * mm, "end": v(-80.93, 52.3) * mm});
            skLineSegment(sketch, "E11172", {"start": v(-80.93, 52.3) * mm, "end": v(-81.04, 52.48) * mm});
            skLineSegment(sketch, "E11173", {"start": v(-81.04, 52.48) * mm, "end": v(-81.1, 52.6) * mm});
            skLineSegment(sketch, "E11174", {"start": v(-81.1, 52.6) * mm, "end": v(-81.11, 52.63) * mm});
            skLineSegment(sketch, "E11175", {"start": v(-81.11, 52.63) * mm, "end": v(-81.8, 54.25) * mm});
            skLineSegment(sketch, "E11176", {"start": v(-81.8, 54.25) * mm, "end": v(-84.85, 53.16) * mm});
            skLineSegment(sketch, "E11177", {"start": v(-84.85, 53.16) * mm, "end": v(-84.33, 51.49) * mm});
            skLineSegment(sketch, "E11178", {"start": v(-84.33, 51.49) * mm, "end": v(-84.32, 51.45) * mm});
            skLineSegment(sketch, "E11179", {"start": v(-84.32, 51.45) * mm, "end": v(-84.3, 51.33) * mm});
            skLineSegment(sketch, "E11180", {"start": v(-84.3, 51.33) * mm, "end": v(-84.26, 51.12) * mm});
            skLineSegment(sketch, "E11181", {"start": v(-84.26, 51.12) * mm, "end": v(-84.22, 50.83) * mm});
            skLineSegment(sketch, "E11182", {"start": v(-84.22, 50.83) * mm, "end": v(-84.2, 50.46) * mm});
            skLineSegment(sketch, "E11183", {"start": v(-84.2, 50.46) * mm, "end": v(-84.19, 50) * mm});
            skLineSegment(sketch, "E11184", {"start": v(-84.19, 50) * mm, "end": v(-84.2, 49.46) * mm});
            skLineSegment(sketch, "E11185", {"start": v(-84.2, 49.46) * mm, "end": v(-84.26, 48.83) * mm});
            skLineSegment(sketch, "E11186", {"start": v(-84.26, 48.83) * mm, "end": v(-84.35, 48.13) * mm});
            skLineSegment(sketch, "E11187", {"start": v(-84.35, 48.13) * mm, "end": v(-84.42, 47.76) * mm});
            skLineSegment(sketch, "E11188", {"start": v(-84.42, 47.76) * mm, "end": v(-86.62, 47.25) * mm});
            skLineSegment(sketch, "E11189", {"start": v(-86.62, 47.25) * mm, "end": v(-86.85, 47.54) * mm});
            skLineSegment(sketch, "E11190", {"start": v(-86.85, 47.54) * mm, "end": v(-87.25, 48.13) * mm});
            skLineSegment(sketch, "E11191", {"start": v(-87.25, 48.13) * mm, "end": v(-87.58, 48.66) * mm});
            skLineSegment(sketch, "E11192", {"start": v(-87.58, 48.66) * mm, "end": v(-87.84, 49.14) * mm});
            skLineSegment(sketch, "E11193", {"start": v(-87.84, 49.14) * mm, "end": v(-88.05, 49.55) * mm});
            skLineSegment(sketch, "E11194", {"start": v(-88.05, 49.55) * mm, "end": v(-88.2, 49.9) * mm});
            skLineSegment(sketch, "E11195", {"start": v(-88.2, 49.9) * mm, "end": v(-88.3, 50.17) * mm});
            skLineSegment(sketch, "E11196", {"start": v(-88.3, 50.17) * mm, "end": v(-88.36, 50.37) * mm});
            skLineSegment(sketch, "E11197", {"start": v(-88.36, 50.37) * mm, "end": v(-88.39, 50.5) * mm});
            skLineSegment(sketch, "E11198", {"start": v(-88.39, 50.5) * mm, "end": v(-88.4, 50.54) * mm});
            skLineSegment(sketch, "E11199", {"start": v(-88.4, 50.54) * mm, "end": v(-88.7, 52.26) * mm});
            skLineSegment(sketch, "E11200", {"start": v(-88.7, 52.26) * mm, "end": v(-91.92, 51.87) * mm});
            skLineSegment(sketch, "E11201", {"start": v(-91.92, 51.87) * mm, "end": v(-91.8, 50.13) * mm});
            skLineSegment(sketch, "E11202", {"start": v(-91.8, 50.13) * mm, "end": v(-91.8, 50.09) * mm});
            skLineSegment(sketch, "E11203", {"start": v(-91.8, 50.09) * mm, "end": v(-91.8, 49.96) * mm});
            skLineSegment(sketch, "E11204", {"start": v(-91.8, 49.96) * mm, "end": v(-91.8, 49.75) * mm});
            skLineSegment(sketch, "E11205", {"start": v(-91.8, 49.75) * mm, "end": v(-91.84, 49.46) * mm});
            skLineSegment(sketch, "E11206", {"start": v(-91.84, 49.46) * mm, "end": v(-91.9, 49.1) * mm});
            skLineSegment(sketch, "E11207", {"start": v(-91.9, 49.1) * mm, "end": v(-91.99, 48.64) * mm});
            skLineSegment(sketch, "E11208", {"start": v(-91.99, 48.64) * mm, "end": v(-92.13, 48.12) * mm});
            skLineSegment(sketch, "E11209", {"start": v(-92.13, 48.12) * mm, "end": v(-92.32, 47.52) * mm});
            skLineSegment(sketch, "E11210", {"start": v(-92.32, 47.52) * mm, "end": v(-92.57, 46.86) * mm});
            skLineSegment(sketch, "E11211", {"start": v(-92.57, 46.86) * mm, "end": v(-92.72, 46.51) * mm});
            skLineSegment(sketch, "E11212", {"start": v(-92.72, 46.51) * mm, "end": v(-94.98, 46.5) * mm});
            skLineSegment(sketch, "E11213", {"start": v(-94.98, 46.5) * mm, "end": v(-95.13, 46.83) * mm});
            skLineSegment(sketch, "E11214", {"start": v(-95.13, 46.83) * mm, "end": v(-95.4, 47.5) * mm});
            skLineSegment(sketch, "E11215", {"start": v(-95.4, 47.5) * mm, "end": v(-95.6, 48.09) * mm});
            skLineSegment(sketch, "E11216", {"start": v(-95.6, 48.09) * mm, "end": v(-95.75, 48.6) * mm});
            skLineSegment(sketch, "E11217", {"start": v(-95.75, 48.6) * mm, "end": v(-95.85, 49.06) * mm});
            skLineSegment(sketch, "E11218", {"start": v(-95.85, 49.06) * mm, "end": v(-95.92, 49.42) * mm});
            skLineSegment(sketch, "E11219", {"start": v(-95.92, 49.42) * mm, "end": v(-95.95, 49.71) * mm});
            skLineSegment(sketch, "E11220", {"start": v(-95.95, 49.71) * mm, "end": v(-95.97, 49.92) * mm});
            skLineSegment(sketch, "E11221", {"start": v(-95.97, 49.92) * mm, "end": v(-95.97, 50.05) * mm});
            skLineSegment(sketch, "E11222", {"start": v(-95.97, 50.05) * mm, "end": v(-95.97, 50.09) * mm});
            skLineSegment(sketch, "E11223", {"start": v(-95.97, 50.09) * mm, "end": v(-95.88, 51.84) * mm});
            skLineSegment(sketch, "E11224", {"start": v(-95.88, 51.84) * mm, "end": v(-99.1, 52.17) * mm});
            skLineSegment(sketch, "E11225", {"start": v(-99.1, 52.17) * mm, "end": v(-99.37, 50.44) * mm});
            skLineSegment(sketch, "E11226", {"start": v(-99.37, 50.44) * mm, "end": v(-99.38, 50.4) * mm});
            skLineSegment(sketch, "E11227", {"start": v(-99.38, 50.4) * mm, "end": v(-99.41, 50.27) * mm});
            skLineSegment(sketch, "E11228", {"start": v(-99.41, 50.27) * mm, "end": v(-99.47, 50.07) * mm});
            skLineSegment(sketch, "E11229", {"start": v(-99.47, 50.07) * mm, "end": v(-99.57, 49.8) * mm});
            skLineSegment(sketch, "E11230", {"start": v(-99.57, 49.8) * mm, "end": v(-99.7, 49.45) * mm});
            skLineSegment(sketch, "E11231", {"start": v(-99.7, 49.45) * mm, "end": v(-99.9, 49.03) * mm});
            skLineSegment(sketch, "E11232", {"start": v(-99.9, 49.03) * mm, "end": v(-100.15, 48.55) * mm});
            skLineSegment(sketch, "E11233", {"start": v(-100.15, 48.55) * mm, "end": v(-100.48, 48) * mm});
            skLineSegment(sketch, "E11234", {"start": v(-100.48, 48) * mm, "end": v(-100.87, 47.42) * mm});
            skLineSegment(sketch, "E11235", {"start": v(-100.87, 47.42) * mm, "end": v(-101.1, 47.11) * mm});
            skLineSegment(sketch, "E11236", {"start": v(-101.1, 47.11) * mm, "end": v(-103.3, 47.59) * mm});
            skLineSegment(sketch, "E11237", {"start": v(-103.3, 47.59) * mm, "end": v(-103.38, 47.95) * mm});
            skLineSegment(sketch, "E11238", {"start": v(-103.38, 47.95) * mm, "end": v(-103.48, 48.66) * mm});
            skLineSegment(sketch, "E11239", {"start": v(-103.48, 48.66) * mm, "end": v(-103.55, 49.28) * mm});
            skLineSegment(sketch, "E11240", {"start": v(-103.55, 49.28) * mm, "end": v(-103.57, 49.82) * mm});
            skLineSegment(sketch, "E11241", {"start": v(-103.57, 49.82) * mm, "end": v(-103.57, 50.28) * mm});
            skLineSegment(sketch, "E11242", {"start": v(-103.57, 50.28) * mm, "end": v(-103.55, 50.65) * mm});
            skLineSegment(sketch, "E11243", {"start": v(-103.55, 50.65) * mm, "end": v(-103.52, 50.94) * mm});
            skLineSegment(sketch, "E11244", {"start": v(-103.52, 50.94) * mm, "end": v(-103.5, 51.15) * mm});
            skLineSegment(sketch, "E11245", {"start": v(-103.5, 51.15) * mm, "end": v(-103.47, 51.27) * mm});
            skLineSegment(sketch, "E11246", {"start": v(-103.47, 51.27) * mm, "end": v(-103.46, 51.31) * mm});
            skLineSegment(sketch, "E11247", {"start": v(-103.46, 51.31) * mm, "end": v(-102.97, 53) * mm});
            skLineSegment(sketch, "E11248", {"start": v(-102.97, 53) * mm, "end": v(-106.04, 54.02) * mm});
            skLineSegment(sketch, "E11249", {"start": v(-106.04, 54.02) * mm, "end": v(-106.7, 52.4) * mm});
            skLineSegment(sketch, "E11250", {"start": v(-106.7, 52.4) * mm, "end": v(-106.71, 52.36) * mm});
            skLineSegment(sketch, "E11251", {"start": v(-106.71, 52.36) * mm, "end": v(-106.77, 52.25) * mm});
            skLineSegment(sketch, "E11252", {"start": v(-106.77, 52.25) * mm, "end": v(-106.87, 52.06) * mm});
            skLineSegment(sketch, "E11253", {"start": v(-106.87, 52.06) * mm, "end": v(-107.03, 51.82) * mm});
            skLineSegment(sketch, "E11254", {"start": v(-107.03, 51.82) * mm, "end": v(-107.24, 51.5) * mm});
            skLineSegment(sketch, "E11255", {"start": v(-107.24, 51.5) * mm, "end": v(-107.53, 51.14) * mm});
            skLineSegment(sketch, "E11256", {"start": v(-107.53, 51.14) * mm, "end": v(-107.88, 50.73) * mm});
            skLineSegment(sketch, "E11257", {"start": v(-107.88, 50.73) * mm, "end": v(-108.32, 50.27) * mm});
            skLineSegment(sketch, "E11258", {"start": v(-108.32, 50.27) * mm, "end": v(-108.84, 49.78) * mm});
            skLineSegment(sketch, "E11259", {"start": v(-108.84, 49.78) * mm, "end": v(-109.12, 49.53) * mm});
            skLineSegment(sketch, "E11260", {"start": v(-109.12, 49.53) * mm, "end": v(-111.17, 50.48) * mm});
            skLineSegment(sketch, "E11261", {"start": v(-111.17, 50.48) * mm, "end": v(-111.16, 50.86) * mm});
            skLineSegment(sketch, "E11262", {"start": v(-111.16, 50.86) * mm, "end": v(-111.1, 51.56) * mm});
            skLineSegment(sketch, "E11263", {"start": v(-111.1, 51.56) * mm, "end": v(-111.02, 52.18) * mm});
            skLineSegment(sketch, "E11264", {"start": v(-111.02, 52.18) * mm, "end": v(-110.93, 52.72) * mm});
            skLineSegment(sketch, "E11265", {"start": v(-110.93, 52.72) * mm, "end": v(-110.82, 53.16) * mm});
            skLineSegment(sketch, "E11266", {"start": v(-110.82, 53.16) * mm, "end": v(-110.72, 53.53) * mm});
            skLineSegment(sketch, "E11267", {"start": v(-110.72, 53.53) * mm, "end": v(-110.63, 53.8) * mm});
            skLineSegment(sketch, "E11268", {"start": v(-110.63, 53.8) * mm, "end": v(-110.55, 54) * mm});
            skLineSegment(sketch, "E11269", {"start": v(-110.55, 54) * mm, "end": v(-110.5, 54.11) * mm});
            skLineSegment(sketch, "E11270", {"start": v(-110.5, 54.11) * mm, "end": v(-110.48, 54.15) * mm});
            skLineSegment(sketch, "E11271", {"start": v(-110.48, 54.15) * mm, "end": v(-109.62, 55.68) * mm});
            skLineSegment(sketch, "E11272", {"start": v(-109.62, 55.68) * mm, "end": v(-112.38, 57.36) * mm});
            skLineSegment(sketch, "E11273", {"start": v(-112.38, 57.36) * mm, "end": v(-113.4, 55.91) * mm});
            skLineSegment(sketch, "E11274", {"start": v(-113.4, 55.91) * mm, "end": v(-113.42, 55.88) * mm});
            skLineSegment(sketch, "E11275", {"start": v(-113.42, 55.88) * mm, "end": v(-113.5, 55.78) * mm});
            skLineSegment(sketch, "E11276", {"start": v(-113.5, 55.78) * mm, "end": v(-113.64, 55.63) * mm});
            skLineSegment(sketch, "E11277", {"start": v(-113.64, 55.63) * mm, "end": v(-113.85, 55.42) * mm});
            skLineSegment(sketch, "E11278", {"start": v(-113.85, 55.42) * mm, "end": v(-114.13, 55.17) * mm});
            skLineSegment(sketch, "E11279", {"start": v(-114.13, 55.17) * mm, "end": v(-114.48, 54.87) * mm});
            skLineSegment(sketch, "E11280", {"start": v(-114.48, 54.87) * mm, "end": v(-114.93, 54.55) * mm});
            skLineSegment(sketch, "E11281", {"start": v(-114.93, 54.55) * mm, "end": v(-115.45, 54.2) * mm});
            skLineSegment(sketch, "E11282", {"start": v(-115.45, 54.2) * mm, "end": v(-116.07, 53.83) * mm});
            skLineSegment(sketch, "E11283", {"start": v(-116.07, 53.83) * mm, "end": v(-116.4, 53.65) * mm});
            skLineSegment(sketch, "E11284", {"start": v(-116.4, 53.65) * mm, "end": v(-118.18, 55.03) * mm});
            skLineSegment(sketch, "E11285", {"start": v(-118.18, 55.03) * mm, "end": v(-118.1, 55.39) * mm});
            skLineSegment(sketch, "E11286", {"start": v(-118.1, 55.39) * mm, "end": v(-117.88, 56.07) * mm});
            skLineSegment(sketch, "E11287", {"start": v(-117.88, 56.07) * mm, "end": v(-117.66, 56.65) * mm});
            skLineSegment(sketch, "E11288", {"start": v(-117.66, 56.65) * mm, "end": v(-117.45, 57.15) * mm});
            skLineSegment(sketch, "E11289", {"start": v(-117.45, 57.15) * mm, "end": v(-117.24, 57.57) * mm});
            skLineSegment(sketch, "E11290", {"start": v(-117.24, 57.57) * mm, "end": v(-117.06, 57.9) * mm});
            skLineSegment(sketch, "E11291", {"start": v(-117.06, 57.9) * mm, "end": v(-116.9, 58.15) * mm});
            skLineSegment(sketch, "E11292", {"start": v(-116.9, 58.15) * mm, "end": v(-116.79, 58.32) * mm});
            skLineSegment(sketch, "E11293", {"start": v(-116.79, 58.32) * mm, "end": v(-116.7, 58.42) * mm});
            skLineSegment(sketch, "E11294", {"start": v(-116.7, 58.42) * mm, "end": v(-116.68, 58.45) * mm});
            skLineSegment(sketch, "E11295", {"start": v(-116.68, 58.45) * mm, "end": v(-115.5, 59.76) * mm});
            skLineSegment(sketch, "E11296", {"start": v(-115.5, 59.76) * mm, "end": v(-117.82, 62) * mm});
            skLineSegment(sketch, "E11297", {"start": v(-117.82, 62) * mm, "end": v(-119.12, 60.8) * mm});
            skLineSegment(sketch, "E11298", {"start": v(-119.12, 60.8) * mm, "end": v(-119.16, 60.78) * mm});
            skLineSegment(sketch, "E11299", {"start": v(-119.16, 60.78) * mm, "end": v(-119.26, 60.7) * mm});
            skLineSegment(sketch, "E11300", {"start": v(-119.26, 60.7) * mm, "end": v(-119.43, 60.58) * mm});
            skLineSegment(sketch, "E11301", {"start": v(-119.43, 60.58) * mm, "end": v(-119.68, 60.43) * mm});
            skLineSegment(sketch, "E11302", {"start": v(-119.68, 60.43) * mm, "end": v(-120, 60.24) * mm});
            skLineSegment(sketch, "E11303", {"start": v(-120, 60.24) * mm, "end": v(-120.43, 60.03) * mm});
            skLineSegment(sketch, "E11304", {"start": v(-120.43, 60.03) * mm, "end": v(-120.93, 59.81) * mm});
            skLineSegment(sketch, "E11305", {"start": v(-120.93, 59.81) * mm, "end": v(-121.52, 59.59) * mm});
            skLineSegment(sketch, "E11306", {"start": v(-121.52, 59.59) * mm, "end": v(-122.2, 59.37) * mm});
            skLineSegment(sketch, "E11307", {"start": v(-122.2, 59.37) * mm, "end": v(-122.57, 59.27) * mm});
            skLineSegment(sketch, "E11308", {"start": v(-122.57, 59.27) * mm, "end": v(-124, 61) * mm});
            skLineSegment(sketch, "E11309", {"start": v(-124, 61) * mm, "end": v(-123.82, 61.33) * mm});
            skLineSegment(sketch, "E11310", {"start": v(-123.82, 61.33) * mm, "end": v(-123.46, 61.94) * mm});
            skLineSegment(sketch, "E11311", {"start": v(-123.46, 61.94) * mm, "end": v(-123.12, 62.47) * mm});
            skLineSegment(sketch, "E11312", {"start": v(-123.12, 62.47) * mm, "end": v(-122.8, 62.9) * mm});
            skLineSegment(sketch, "E11313", {"start": v(-122.8, 62.9) * mm, "end": v(-122.5, 63.27) * mm});
            skLineSegment(sketch, "E11314", {"start": v(-122.5, 63.27) * mm, "end": v(-122.25, 63.55) * mm});
            skLineSegment(sketch, "E11315", {"start": v(-122.25, 63.55) * mm, "end": v(-122.05, 63.76) * mm});
            skLineSegment(sketch, "E11316", {"start": v(-122.05, 63.76) * mm, "end": v(-121.9, 63.9) * mm});
            skLineSegment(sketch, "E11317", {"start": v(-121.9, 63.9) * mm, "end": v(-121.8, 63.98) * mm});
            skLineSegment(sketch, "E11318", {"start": v(-121.8, 63.98) * mm, "end": v(-121.76, 64) * mm});
            skLineSegment(sketch, "E11319", {"start": v(-121.76, 64) * mm, "end": v(-120.31, 65.02) * mm});
            skLineSegment(sketch, "E11320", {"start": v(-120.31, 65.02) * mm, "end": v(-122.06, 67.7) * mm});
            skLineSegment(sketch, "E11321", {"start": v(-122.06, 67.7) * mm, "end": v(-123.6, 66.84) * mm});
            skLineSegment(sketch, "E11322", {"start": v(-123.6, 66.84) * mm, "end": v(-123.64, 66.82) * mm});
            skLineSegment(sketch, "E11323", {"start": v(-123.64, 66.82) * mm, "end": v(-123.76, 66.77) * mm});
            skLineSegment(sketch, "E11324", {"start": v(-123.76, 66.77) * mm, "end": v(-123.95, 66.69) * mm});
            skLineSegment(sketch, "E11325", {"start": v(-123.95, 66.69) * mm, "end": v(-124.23, 66.59) * mm});
            skLineSegment(sketch, "E11326", {"start": v(-124.23, 66.59) * mm, "end": v(-124.6, 66.48) * mm});
            skLineSegment(sketch, "E11327", {"start": v(-124.6, 66.48) * mm, "end": v(-125.05, 66.37) * mm});
            skLineSegment(sketch, "E11328", {"start": v(-125.05, 66.37) * mm, "end": v(-125.6, 66.26) * mm});
            skLineSegment(sketch, "E11329", {"start": v(-125.6, 66.26) * mm, "end": v(-126.22, 66.17) * mm});
            skLineSegment(sketch, "E11330", {"start": v(-126.22, 66.17) * mm, "end": v(-126.94, 66.1) * mm});
            skLineSegment(sketch, "E11331", {"start": v(-126.94, 66.1) * mm, "end": v(-127.31, 66.1) * mm});
            skLineSegment(sketch, "E11332", {"start": v(-127.31, 66.1) * mm, "end": v(-128.32, 68.09) * mm});
            skLineSegment(sketch, "E11333", {"start": v(-128.32, 68.09) * mm, "end": v(-128.07, 68.37) * mm});
            skLineSegment(sketch, "E11334", {"start": v(-128.07, 68.37) * mm, "end": v(-127.58, 68.9) * mm});
            skLineSegment(sketch, "E11335", {"start": v(-127.58, 68.9) * mm, "end": v(-127.13, 69.33) * mm});
            skLineSegment(sketch, "E11336", {"start": v(-127.13, 69.33) * mm, "end": v(-126.71, 69.69) * mm});
            skLineSegment(sketch, "E11337", {"start": v(-126.71, 69.69) * mm, "end": v(-126.35, 69.97) * mm});
            skLineSegment(sketch, "E11338", {"start": v(-126.35, 69.97) * mm, "end": v(-126.04, 70.2) * mm});
            skLineSegment(sketch, "E11339", {"start": v(-126.04, 70.2) * mm, "end": v(-125.79, 70.35) * mm});
            skLineSegment(sketch, "E11340", {"start": v(-125.79, 70.35) * mm, "end": v(-125.6, 70.46) * mm});
            skLineSegment(sketch, "E11341", {"start": v(-125.6, 70.46) * mm, "end": v(-125.5, 70.51) * mm});
            skLineSegment(sketch, "E11342", {"start": v(-125.5, 70.51) * mm, "end": v(-125.45, 70.53) * mm});
            skLineSegment(sketch, "E11343", {"start": v(-125.45, 70.53) * mm, "end": v(-123.81, 71.2) * mm});
            skLineSegment(sketch, "E11344", {"start": v(-123.81, 71.2) * mm, "end": v(-124.91, 74.2) * mm});
            skLineSegment(sketch, "E11345", {"start": v(-124.91, 74.2) * mm, "end": v(-126.61, 73.7) * mm});
            skLineSegment(sketch, "E11346", {"start": v(-126.61, 73.7) * mm, "end": v(-126.65, 73.69) * mm});
            skLineSegment(sketch, "E11347", {"start": v(-126.65, 73.69) * mm, "end": v(-126.78, 73.66) * mm});
            skLineSegment(sketch, "E11348", {"start": v(-126.78, 73.66) * mm, "end": v(-126.99, 73.63) * mm});
            skLineSegment(sketch, "E11349", {"start": v(-126.99, 73.63) * mm, "end": v(-127.28, 73.6) * mm});
            skLineSegment(sketch, "E11350", {"start": v(-127.28, 73.6) * mm, "end": v(-127.66, 73.57) * mm});
            skLineSegment(sketch, "E11351", {"start": v(-127.66, 73.57) * mm, "end": v(-128.13, 73.56) * mm});
            skLineSegment(sketch, "E11352", {"start": v(-128.13, 73.56) * mm, "end": v(-128.68, 73.57) * mm});
            skLineSegment(sketch, "E11353", {"start": v(-128.68, 73.57) * mm, "end": v(-129.31, 73.62) * mm});
            skLineSegment(sketch, "E11354", {"start": v(-129.31, 73.62) * mm, "end": v(-130.03, 73.72) * mm});
            skLineSegment(sketch, "E11355", {"start": v(-130.03, 73.72) * mm, "end": v(-130.4, 73.78) * mm});
            skLineSegment(sketch, "E11356", {"start": v(-130.4, 73.78) * mm, "end": v(-130.92, 75.95) * mm});
            skLineSegment(sketch, "E11357", {"start": v(-130.92, 75.95) * mm, "end": v(-130.62, 76.17) * mm});
            skLineSegment(sketch, "E11358", {"start": v(-130.62, 76.17) * mm, "end": v(-130.02, 76.57) * mm});
            skLineSegment(sketch, "E11359", {"start": v(-130.02, 76.57) * mm, "end": v(-129.48, 76.9) * mm});
            skLineSegment(sketch, "E11360", {"start": v(-129.48, 76.9) * mm, "end": v(-129, 77.16) * mm});
            skLineSegment(sketch, "E11361", {"start": v(-129, 77.16) * mm, "end": v(-128.58, 77.36) * mm});
            skLineSegment(sketch, "E11362", {"start": v(-128.58, 77.36) * mm, "end": v(-128.23, 77.5) * mm});
            skLineSegment(sketch, "E11363", {"start": v(-128.23, 77.5) * mm, "end": v(-127.95, 77.6) * mm});
            skLineSegment(sketch, "E11364", {"start": v(-127.95, 77.6) * mm, "end": v(-127.75, 77.66) * mm});
            skLineSegment(sketch, "E11365", {"start": v(-127.75, 77.66) * mm, "end": v(-127.62, 77.7) * mm});
            skLineSegment(sketch, "E11366", {"start": v(-127.62, 77.7) * mm, "end": v(-127.58, 77.7) * mm});
            skLineSegment(sketch, "E11367", {"start": v(-127.58, 77.7) * mm, "end": v(-125.83, 78) * mm});
            skLineSegment(sketch, "E11368", {"start": v(-125.83, 78) * mm, "end": v(-126.22, 81.17) * mm});
            skLineSegment(sketch, "E11369", {"start": v(-126.22, 81.17) * mm, "end": v(-128, 81.05) * mm});
            skLineSegment(sketch, "E11370", {"start": v(-128, 81.05) * mm, "end": v(-128.04, 81.05) * mm});
            skLineSegment(sketch, "E11371", {"start": v(-128.04, 81.05) * mm, "end": v(-128.17, 81.05) * mm});
            skLineSegment(sketch, "E11372", {"start": v(-128.17, 81.05) * mm, "end": v(-128.38, 81.06) * mm});
            skLineSegment(sketch, "E11373", {"start": v(-128.38, 81.06) * mm, "end": v(-128.67, 81.09) * mm});
            skLineSegment(sketch, "E11374", {"start": v(-128.67, 81.09) * mm, "end": v(-129.05, 81.15) * mm});
            skLineSegment(sketch, "E11375", {"start": v(-129.05, 81.15) * mm, "end": v(-129.5, 81.24) * mm});
            skLineSegment(sketch, "E11376", {"start": v(-129.5, 81.24) * mm, "end": v(-130.04, 81.38) * mm});
            skLineSegment(sketch, "E11377", {"start": v(-130.04, 81.38) * mm, "end": v(-130.64, 81.56) * mm});
            skLineSegment(sketch, "E11378", {"start": v(-130.64, 81.56) * mm, "end": v(-131.32, 81.81) * mm});
            skLineSegment(sketch, "E11379", {"start": v(-131.32, 81.81) * mm, "end": v(-131.67, 81.96) * mm});
            skLineSegment(sketch, "E11380", {"start": v(-131.67, 81.96) * mm, "end": v(-131.69, 84.18) * mm});
            skLineSegment(sketch, "E11381", {"start": v(-131.69, 84.18) * mm, "end": v(-131.34, 84.34) * mm});
            skLineSegment(sketch, "E11382", {"start": v(-131.34, 84.34) * mm, "end": v(-130.67, 84.6) * mm});
            skLineSegment(sketch, "E11383", {"start": v(-130.67, 84.6) * mm, "end": v(-130.07, 84.8) * mm});
            skLineSegment(sketch, "E11384", {"start": v(-130.07, 84.8) * mm, "end": v(-129.54, 84.94) * mm});
            skLineSegment(sketch, "E11385", {"start": v(-129.54, 84.94) * mm, "end": v(-129.09, 85.04) * mm});
            skLineSegment(sketch, "E11386", {"start": v(-129.09, 85.04) * mm, "end": v(-128.7, 85.1) * mm});
            skLineSegment(sketch, "E11387", {"start": v(-128.7, 85.1) * mm, "end": v(-128.42, 85.14) * mm});
            skLineSegment(sketch, "E11388", {"start": v(-128.42, 85.14) * mm, "end": v(-128.2, 85.16) * mm});
            skLineSegment(sketch, "E11389", {"start": v(-128.2, 85.16) * mm, "end": v(-128.08, 85.16) * mm});
            skLineSegment(sketch, "E11390", {"start": v(-128.08, 85.16) * mm, "end": v(-128.04, 85.16) * mm});
            skLineSegment(sketch, "E11391", {"start": v(-128.04, 85.16) * mm, "end": v(-126.26, 85.07) * mm});
            skLineSegment(sketch, "E11392", {"start": v(-126.26, 85.07) * mm, "end": v(-125.93, 88.25) * mm});
            skLineSegment(sketch, "E11393", {"start": v(-125.93, 88.25) * mm, "end": v(-127.68, 88.51) * mm});
            skLineSegment(sketch, "E11394", {"start": v(-127.68, 88.51) * mm, "end": v(-127.73, 88.52) * mm});
            skLineSegment(sketch, "E11395", {"start": v(-127.73, 88.52) * mm, "end": v(-127.85, 88.55) * mm});
            skLineSegment(sketch, "E11396", {"start": v(-127.85, 88.55) * mm, "end": v(-128.05, 88.6) * mm});
            skLineSegment(sketch, "E11397", {"start": v(-128.05, 88.6) * mm, "end": v(-128.33, 88.7) * mm});
            skLineSegment(sketch, "E11398", {"start": v(-128.33, 88.7) * mm, "end": v(-128.69, 88.84) * mm});
            skLineSegment(sketch, "E11399", {"start": v(-128.69, 88.84) * mm, "end": v(-129.11, 89.03) * mm});
            skLineSegment(sketch, "E11400", {"start": v(-129.11, 89.03) * mm, "end": v(-129.6, 89.28) * mm});
            skLineSegment(sketch, "E11401", {"start": v(-129.6, 89.28) * mm, "end": v(-130.15, 89.6) * mm});
            skLineSegment(sketch, "E11402", {"start": v(-130.15, 89.6) * mm, "end": v(-130.75, 89.99) * mm});
            skLineSegment(sketch, "E11403", {"start": v(-130.75, 89.99) * mm, "end": v(-131.06, 90.2) * mm});
            skLineSegment(sketch, "E11404", {"start": v(-131.06, 90.2) * mm, "end": v(-130.57, 92.38) * mm});
            skLineSegment(sketch, "E11405", {"start": v(-130.57, 92.38) * mm, "end": v(-130.2, 92.46) * mm});
            skLineSegment(sketch, "E11406", {"start": v(-130.2, 92.46) * mm, "end": v(-129.5, 92.56) * mm});
            skLineSegment(sketch, "E11407", {"start": v(-129.5, 92.56) * mm, "end": v(-128.86, 92.62) * mm});
            skLineSegment(sketch, "E11408", {"start": v(-128.86, 92.62) * mm, "end": v(-128.3, 92.65) * mm});
            skLineSegment(sketch, "E11409", {"start": v(-128.3, 92.65) * mm, "end": v(-127.84, 92.65) * mm});
            skLineSegment(sketch, "E11410", {"start": v(-127.84, 92.65) * mm, "end": v(-127.46, 92.63) * mm});
            skLineSegment(sketch, "E11411", {"start": v(-127.46, 92.63) * mm, "end": v(-127.17, 92.6) * mm});
            skLineSegment(sketch, "E11412", {"start": v(-127.17, 92.6) * mm, "end": v(-126.96, 92.57) * mm});
            skLineSegment(sketch, "E11413", {"start": v(-126.96, 92.57) * mm, "end": v(-126.83, 92.54) * mm});
            skLineSegment(sketch, "E11414", {"start": v(-126.83, 92.54) * mm, "end": v(-126.8, 92.53) * mm});
            skLineSegment(sketch, "E11415", {"start": v(-126.8, 92.53) * mm, "end": v(-125.08, 92.05) * mm});
            skLineSegment(sketch, "E11416", {"start": v(-125.08, 92.05) * mm, "end": v(-124.04, 95.08) * mm});
            skLineSegment(sketch, "E11417", {"start": v(-124.04, 95.08) * mm, "end": v(-125.7, 95.72) * mm});
            skLineSegment(sketch, "E11418", {"start": v(-125.7, 95.72) * mm, "end": v(-125.73, 95.74) * mm});
            skLineSegment(sketch, "E11419", {"start": v(-125.73, 95.74) * mm, "end": v(-125.84, 95.8) * mm});
            skLineSegment(sketch, "E11420", {"start": v(-125.84, 95.8) * mm, "end": v(-126.03, 95.9) * mm});
            skLineSegment(sketch, "E11421", {"start": v(-126.03, 95.9) * mm, "end": v(-126.28, 96.05) * mm});
            skLineSegment(sketch, "E11422", {"start": v(-126.28, 96.05) * mm, "end": v(-126.6, 96.26) * mm});
            skLineSegment(sketch, "E11423", {"start": v(-126.6, 96.26) * mm, "end": v(-126.97, 96.54) * mm});
            skLineSegment(sketch, "E11424", {"start": v(-126.97, 96.54) * mm, "end": v(-127.39, 96.9) * mm});
            skLineSegment(sketch, "E11425", {"start": v(-127.39, 96.9) * mm, "end": v(-127.85, 97.32) * mm});
            skLineSegment(sketch, "E11426", {"start": v(-127.85, 97.32) * mm, "end": v(-128.35, 97.83) * mm});
            skLineSegment(sketch, "E11427", {"start": v(-128.35, 97.83) * mm, "end": v(-128.6, 98.11) * mm});
            skLineSegment(sketch, "E11428", {"start": v(-128.6, 98.11) * mm, "end": v(-127.64, 100.13) * mm});
            skLineSegment(sketch, "E11429", {"start": v(-127.64, 100.13) * mm, "end": v(-127.26, 100.12) * mm});
            skLineSegment(sketch, "E11430", {"start": v(-127.26, 100.12) * mm, "end": v(-126.54, 100.07) * mm});
            skLineSegment(sketch, "E11431", {"start": v(-126.54, 100.07) * mm, "end": v(-125.9, 99.99) * mm});
            skLineSegment(sketch, "E11432", {"start": v(-125.9, 99.99) * mm, "end": v(-125.37, 99.9) * mm});
            skLineSegment(sketch, "E11433", {"start": v(-125.37, 99.9) * mm, "end": v(-124.91, 99.79) * mm});
            skLineSegment(sketch, "E11434", {"start": v(-124.91, 99.79) * mm, "end": v(-124.55, 99.69) * mm});
            skLineSegment(sketch, "E11435", {"start": v(-124.55, 99.69) * mm, "end": v(-124.26, 99.6) * mm});
            skLineSegment(sketch, "E11436", {"start": v(-124.26, 99.6) * mm, "end": v(-124.07, 99.52) * mm});
            skLineSegment(sketch, "E11437", {"start": v(-124.07, 99.52) * mm, "end": v(-123.95, 99.47) * mm});
            skLineSegment(sketch, "E11438", {"start": v(-123.95, 99.47) * mm, "end": v(-123.91, 99.45) * mm});
            skLineSegment(sketch, "E11439", {"start": v(-123.91, 99.45) * mm, "end": v(-122.35, 98.6) * mm});
            skLineSegment(sketch, "E11440", {"start": v(-122.35, 98.6) * mm, "end": v(-120.66, 101.33) * mm});
            skLineSegment(sketch, "E11441", {"start": v(-120.66, 101.33) * mm, "end": v(-122.12, 102.32) * mm});
            skLineSegment(sketch, "E11442", {"start": v(-122.12, 102.32) * mm, "end": v(-122.15, 102.34) * mm});
            skLineSegment(sketch, "E11443", {"start": v(-122.15, 102.34) * mm, "end": v(-122.25, 102.42) * mm});
            skLineSegment(sketch, "E11444", {"start": v(-122.25, 102.42) * mm, "end": v(-122.41, 102.56) * mm});
            skLineSegment(sketch, "E11445", {"start": v(-122.41, 102.56) * mm, "end": v(-122.62, 102.76) * mm});
            skLineSegment(sketch, "E11446", {"start": v(-122.62, 102.76) * mm, "end": v(-122.88, 103.04) * mm});
            skLineSegment(sketch, "E11447", {"start": v(-122.88, 103.04) * mm, "end": v(-123.18, 103.4) * mm});
            skLineSegment(sketch, "E11448", {"start": v(-123.18, 103.4) * mm, "end": v(-123.5, 103.83) * mm});
            skLineSegment(sketch, "E11449", {"start": v(-123.5, 103.83) * mm, "end": v(-123.86, 104.35) * mm});
            skLineSegment(sketch, "E11450", {"start": v(-123.86, 104.35) * mm, "end": v(-124.24, 104.95) * mm});
            skLineSegment(sketch, "E11451", {"start": v(-124.24, 104.95) * mm, "end": v(-124.41, 105.28) * mm});
            skLineSegment(sketch, "E11452", {"start": v(-124.41, 105.28) * mm, "end": v(-123.02, 107.04) * mm});
            skLineSegment(sketch, "E11453", {"start": v(-123.02, 107.04) * mm, "end": v(-122.65, 106.94) * mm});
            skLineSegment(sketch, "E11454", {"start": v(-122.65, 106.94) * mm, "end": v(-121.97, 106.74) * mm});
            skLineSegment(sketch, "E11455", {"start": v(-121.97, 106.74) * mm, "end": v(-121.37, 106.52) * mm});
            skLineSegment(sketch, "E11456", {"start": v(-121.37, 106.52) * mm, "end": v(-120.86, 106.3) * mm});
            skLineSegment(sketch, "E11457", {"start": v(-120.86, 106.3) * mm, "end": v(-120.44, 106.1) * mm});
            skLineSegment(sketch, "E11458", {"start": v(-120.44, 106.1) * mm, "end": v(-120.1, 105.93) * mm});
            skLineSegment(sketch, "E11459", {"start": v(-120.1, 105.93) * mm, "end": v(-119.85, 105.78) * mm});
            skLineSegment(sketch, "E11460", {"start": v(-119.85, 105.78) * mm, "end": v(-119.68, 105.66) * mm});
            skLineSegment(sketch, "E11461", {"start": v(-119.68, 105.66) * mm, "end": v(-119.58, 105.58) * mm});
            skLineSegment(sketch, "E11462", {"start": v(-119.58, 105.58) * mm, "end": v(-119.55, 105.56) * mm});
            skLineSegment(sketch, "E11463", {"start": v(-119.55, 105.56) * mm, "end": v(-118.22, 104.4) * mm});
            skLineSegment(sketch, "E11464", {"start": v(-118.22, 104.4) * mm, "end": v(-115.95, 106.67) * mm});
            skLineSegment(sketch, "E11465", {"start": v(-115.95, 106.67) * mm, "end": v(-117.15, 107.96) * mm});
            skLineSegment(sketch, "E11466", {"start": v(-117.15, 107.96) * mm, "end": v(-117.18, 108) * mm});
            skLineSegment(sketch, "E11467", {"start": v(-117.18, 108) * mm, "end": v(-117.26, 108.1) * mm});
            skLineSegment(sketch, "E11468", {"start": v(-117.26, 108.1) * mm, "end": v(-117.38, 108.26) * mm});
            skLineSegment(sketch, "E11469", {"start": v(-117.38, 108.26) * mm, "end": v(-117.54, 108.5) * mm});
            skLineSegment(sketch, "E11470", {"start": v(-117.54, 108.5) * mm, "end": v(-117.73, 108.83) * mm});
            skLineSegment(sketch, "E11471", {"start": v(-117.73, 108.83) * mm, "end": v(-117.94, 109.24) * mm});
            skLineSegment(sketch, "E11472", {"start": v(-117.94, 109.24) * mm, "end": v(-118.16, 109.74) * mm});
            skLineSegment(sketch, "E11473", {"start": v(-118.16, 109.74) * mm, "end": v(-118.39, 110.32) * mm});
            skLineSegment(sketch, "E11474", {"start": v(-118.39, 110.32) * mm, "end": v(-118.61, 111) * mm});
            skLineSegment(sketch, "E11475", {"start": v(-118.61, 111) * mm, "end": v(-118.72, 111.36) * mm});
            skLineSegment(sketch, "E11476", {"start": v(-118.72, 111.36) * mm, "end": v(-116.96, 112.76) * mm});
            skLineSegment(sketch, "E11477", {"start": v(-116.96, 112.76) * mm, "end": v(-116.62, 112.6) * mm});
            skLineSegment(sketch, "E11478", {"start": v(-116.62, 112.6) * mm, "end": v(-116, 112.24) * mm});
            skLineSegment(sketch, "E11479", {"start": v(-116, 112.24) * mm, "end": v(-115.47, 111.9) * mm});
            skLineSegment(sketch, "E11480", {"start": v(-115.47, 111.9) * mm, "end": v(-115.02, 111.58) * mm});
            skLineSegment(sketch, "E11481", {"start": v(-115.02, 111.58) * mm, "end": v(-114.66, 111.3) * mm});
            skLineSegment(sketch, "E11482", {"start": v(-114.66, 111.3) * mm, "end": v(-114.37, 111.04) * mm});
            skLineSegment(sketch, "E11483", {"start": v(-114.37, 111.04) * mm, "end": v(-114.16, 110.84) * mm});
            skLineSegment(sketch, "E11484", {"start": v(-114.16, 110.84) * mm, "end": v(-114.01, 110.69) * mm});
            skLineSegment(sketch, "E11485", {"start": v(-114.01, 110.69) * mm, "end": v(-113.93, 110.6) * mm});
            skLineSegment(sketch, "E11486", {"start": v(-113.93, 110.6) * mm, "end": v(-113.9, 110.56) * mm});
            skLineSegment(sketch, "E11487", {"start": v(-113.9, 110.56) * mm, "end": v(-112.87, 109.13) * mm});
            skLineSegment(sketch, "E11488", {"start": v(-112.87, 109.13) * mm, "end": v(-110.14, 110.86) * mm});
            skLineSegment(sketch, "E11489", {"start": v(-110.14, 110.86) * mm, "end": v(-111.03, 112.38) * mm});
            skLineSegment(sketch, "E11490", {"start": v(-111.03, 112.38) * mm, "end": v(-111.05, 112.41) * mm});
            skLineSegment(sketch, "E11491", {"start": v(-111.05, 112.41) * mm, "end": v(-111.1, 112.53) * mm});
            skLineSegment(sketch, "E11492", {"start": v(-111.1, 112.53) * mm, "end": v(-111.18, 112.72) * mm});
            skLineSegment(sketch, "E11493", {"start": v(-111.18, 112.72) * mm, "end": v(-111.28, 113) * mm});
            skLineSegment(sketch, "E11494", {"start": v(-111.28, 113) * mm, "end": v(-111.4, 113.35) * mm});
            skLineSegment(sketch, "E11495", {"start": v(-111.4, 113.35) * mm, "end": v(-111.5, 113.8) * mm});
            skLineSegment(sketch, "E11496", {"start": v(-111.5, 113.8) * mm, "end": v(-111.61, 114.33) * mm});
            skLineSegment(sketch, "E11497", {"start": v(-111.61, 114.33) * mm, "end": v(-111.7, 114.95) * mm});
            skLineSegment(sketch, "E11498", {"start": v(-111.7, 114.95) * mm, "end": v(-111.77, 115.66) * mm});
            skLineSegment(sketch, "E11499", {"start": v(-111.77, 115.66) * mm, "end": v(-111.79, 116.03) * mm});
            skLineSegment(sketch, "E11500", {"start": v(-111.79, 116.03) * mm, "end": v(-109.76, 117.01) * mm});
            skLineSegment(sketch, "E11501", {"start": v(-109.76, 117.01) * mm, "end": v(-109.47, 116.77) * mm});
            skLineSegment(sketch, "E11502", {"start": v(-109.47, 116.77) * mm, "end": v(-108.94, 116.3) * mm});
            skLineSegment(sketch, "E11503", {"start": v(-108.94, 116.3) * mm, "end": v(-108.5, 115.84) * mm});
            skLineSegment(sketch, "E11504", {"start": v(-108.5, 115.84) * mm, "end": v(-108.13, 115.44) * mm});
            skLineSegment(sketch, "E11505", {"start": v(-108.13, 115.44) * mm, "end": v(-107.84, 115.08) * mm});
            skLineSegment(sketch, "E11506", {"start": v(-107.84, 115.08) * mm, "end": v(-107.62, 114.77) * mm});
            skLineSegment(sketch, "E11507", {"start": v(-107.62, 114.77) * mm, "end": v(-107.46, 114.53) * mm});
            skLineSegment(sketch, "E11508", {"start": v(-107.46, 114.53) * mm, "end": v(-107.36, 114.35) * mm});
            skLineSegment(sketch, "E11509", {"start": v(-107.36, 114.35) * mm, "end": v(-107.3, 114.23) * mm});
            skLineSegment(sketch, "E11510", {"start": v(-107.3, 114.23) * mm, "end": v(-107.28, 114.2) * mm});
            skLineSegment(sketch, "E11511", {"start": v(-107.28, 114.2) * mm, "end": v(-106.6, 112.58) * mm});
            skLineSegment(sketch, "E11512", {"start": v(-106.6, 112.58) * mm, "end": v(-103.54, 113.66) * mm});
            skLineSegment(sketch, "E11513", {"start": v(-103.54, 113.66) * mm, "end": v(-104.06, 115.34) * mm});
            skLineSegment(sketch, "E11514", {"start": v(-104.06, 115.34) * mm, "end": v(-104.07, 115.38) * mm});
            skLineSegment(sketch, "E11515", {"start": v(-104.07, 115.38) * mm, "end": v(-104.1, 115.5) * mm});
            skLineSegment(sketch, "E11516", {"start": v(-104.1, 115.5) * mm, "end": v(-104.13, 115.7) * mm});
            skLineSegment(sketch, "E11517", {"start": v(-104.13, 115.7) * mm, "end": v(-104.17, 116) * mm});
            skLineSegment(sketch, "E11518", {"start": v(-104.17, 116) * mm, "end": v(-104.2, 116.37) * mm});
            skLineSegment(sketch, "E11519", {"start": v(-104.2, 116.37) * mm, "end": v(-104.2, 116.83) * mm});
            skLineSegment(sketch, "E11520", {"start": v(-104.2, 116.83) * mm, "end": v(-104.19, 117.37) * mm});
            skLineSegment(sketch, "E11521", {"start": v(-104.19, 117.37) * mm, "end": v(-104.14, 118) * mm});
            skLineSegment(sketch, "E11522", {"start": v(-104.14, 118) * mm, "end": v(-104.04, 118.7) * mm});
            skLineSegment(sketch, "E11523", {"start": v(-104.04, 118.7) * mm, "end": v(-103.98, 119.07) * mm});
            skLineSegment(sketch, "E11524", {"start": v(-103.98, 119.07) * mm, "end": v(-101.78, 119.58) * mm});
            skLineSegment(sketch, "E11525", {"start": v(-101.78, 119.58) * mm, "end": v(-101.55, 119.28) * mm});
            skLineSegment(sketch, "E11526", {"start": v(-101.55, 119.28) * mm, "end": v(-101.14, 118.7) * mm});
            skLineSegment(sketch, "E11527", {"start": v(-101.14, 118.7) * mm, "end": v(-100.81, 118.16) * mm});
            skLineSegment(sketch, "E11528", {"start": v(-100.81, 118.16) * mm, "end": v(-100.55, 117.69) * mm});
            skLineSegment(sketch, "E11529", {"start": v(-100.55, 117.69) * mm, "end": v(-100.35, 117.27) * mm});
            skLineSegment(sketch, "E11530", {"start": v(-100.35, 117.27) * mm, "end": v(-100.2, 116.93) * mm});
            skLineSegment(sketch, "E11531", {"start": v(-100.2, 116.93) * mm, "end": v(-100.1, 116.65) * mm});
            skLineSegment(sketch, "E11532", {"start": v(-100.1, 116.65) * mm, "end": v(-100.04, 116.45) * mm});
            skLineSegment(sketch, "E11533", {"start": v(-100.04, 116.45) * mm, "end": v(-100, 116.33) * mm});
            skLineSegment(sketch, "E11534", {"start": v(-100, 116.33) * mm, "end": v(-100, 116.3) * mm});
            skLineSegment(sketch, "E11535", {"start": v(-100, 116.3) * mm, "end": v(-99.7, 114.57) * mm});
            skLineSegment(sketch, "E11536", {"start": v(-99.7, 114.57) * mm, "end": v(-96.47, 114.95) * mm});
            skLineSegment(sketch, "E11537", {"start": v(-96.47, 114.95) * mm, "end": v(-96.6, 116.7) * mm});
            skLineSegment(sketch, "E11538", {"start": v(-96.6, 116.7) * mm, "end": v(-96.6, 116.74) * mm});
            skLineSegment(sketch, "E11539", {"start": v(-96.6, 116.74) * mm, "end": v(-96.6, 116.87) * mm});
            skLineSegment(sketch, "E11540", {"start": v(-96.6, 116.87) * mm, "end": v(-96.59, 117.08) * mm});
            skLineSegment(sketch, "E11541", {"start": v(-96.59, 117.08) * mm, "end": v(-96.56, 117.37) * mm});
            skLineSegment(sketch, "E11542", {"start": v(-96.56, 117.37) * mm, "end": v(-96.5, 117.74) * mm});
            skLineSegment(sketch, "E11543", {"start": v(-96.5, 117.74) * mm, "end": v(-96.4, 118.19) * mm});
            skLineSegment(sketch, "E11544", {"start": v(-96.4, 118.19) * mm, "end": v(-96.27, 118.71) * mm});
            skLineSegment(sketch, "E11545", {"start": v(-96.27, 118.71) * mm, "end": v(-96.07, 119.3) * mm});
            skLineSegment(sketch, "E11546", {"start": v(-96.07, 119.3) * mm, "end": v(-95.82, 119.97) * mm});
            skLineSegment(sketch, "E11547", {"start": v(-95.82, 119.97) * mm, "end": v(-95.68, 120.32) * mm});
            skLineSegment(sketch, "E11548", {"start": v(-95.68, 120.32) * mm, "end": v(-93.41, 120.34) * mm});
            skLineSegment(sketch, "E11549", {"start": v(-93.41, 120.34) * mm, "end": v(-93.26, 120) * mm});
            skLineSegment(sketch, "E11550", {"start": v(-93.26, 120) * mm, "end": v(-93, 119.34) * mm});
            skLineSegment(sketch, "E11551", {"start": v(-93, 119.34) * mm, "end": v(-92.8, 118.74) * mm});
            skLineSegment(sketch, "E11552", {"start": v(-92.8, 118.74) * mm, "end": v(-92.65, 118.22) * mm});
            skLineSegment(sketch, "E11553", {"start": v(-92.65, 118.22) * mm, "end": v(-92.54, 117.77) * mm});
            skLineSegment(sketch, "E11554", {"start": v(-92.54, 117.77) * mm, "end": v(-92.48, 117.4) * mm});
            skLineSegment(sketch, "E11555", {"start": v(-92.48, 117.4) * mm, "end": v(-92.44, 117.11) * mm});
            skLineSegment(sketch, "E11556", {"start": v(-92.44, 117.11) * mm, "end": v(-92.42, 116.9) * mm});
            skLineSegment(sketch, "E11557", {"start": v(-92.42, 116.9) * mm, "end": v(-92.42, 116.78) * mm});
            skLineSegment(sketch, "E11558", {"start": v(-92.42, 116.78) * mm, "end": v(-92.42, 116.74) * mm});
            skLineSegment(sketch, "E11559", {"start": v(-92.42, 116.74) * mm, "end": v(-92.51, 115) * mm});
            skLineSegment(sketch, "E11560", {"start": v(-92.51, 115) * mm, "end": v(-89.29, 114.66) * mm});
            skLineSegment(sketch, "E11561", {"start": v(-89.29, 114.66) * mm, "end": v(-89.02, 116.4) * mm});
            skLineSegment(sketch, "E11562", {"start": v(-89.02, 116.4) * mm, "end": v(-89.01, 116.43) * mm});
            skLineSegment(sketch, "E11563", {"start": v(-89.01, 116.43) * mm, "end": v(-88.98, 116.56) * mm});
            skLineSegment(sketch, "E11564", {"start": v(-88.98, 116.56) * mm, "end": v(-88.92, 116.76) * mm});
            skLineSegment(sketch, "E11565", {"start": v(-88.92, 116.76) * mm, "end": v(-88.83, 117.03) * mm});
            skLineSegment(sketch, "E11566", {"start": v(-88.83, 117.03) * mm, "end": v(-88.69, 117.38) * mm});
            skLineSegment(sketch, "E11567", {"start": v(-88.69, 117.38) * mm, "end": v(-88.5, 117.8) * mm});
            skLineSegment(sketch, "E11568", {"start": v(-88.5, 117.8) * mm, "end": v(-88.24, 118.28) * mm});
            skLineSegment(sketch, "E11569", {"start": v(-88.24, 118.28) * mm, "end": v(-87.92, 118.82) * mm});
            skLineSegment(sketch, "E11570", {"start": v(-87.92, 118.82) * mm, "end": v(-87.52, 119.41) * mm});
            skLineSegment(sketch, "E11571", {"start": v(-87.52, 119.41) * mm, "end": v(-87.3, 119.71) * mm});
            skLineSegment(sketch, "E11572", {"start": v(-87.3, 119.71) * mm, "end": v(-85.1, 119.24) * mm});
            skLineSegment(sketch, "E11573", {"start": v(-85.1, 119.24) * mm, "end": v(-85.02, 118.87) * mm});
            skLineSegment(sketch, "E11574", {"start": v(-85.02, 118.87) * mm, "end": v(-84.9, 118.17) * mm});
            skLineSegment(sketch, "E11575", {"start": v(-84.9, 118.17) * mm, "end": v(-84.85, 117.55) * mm});
            skLineSegment(sketch, "E11576", {"start": v(-84.85, 117.55) * mm, "end": v(-84.82, 117) * mm});
            skLineSegment(sketch, "E11577", {"start": v(-84.82, 117) * mm, "end": v(-84.82, 116.55) * mm});
            skLineSegment(sketch, "E11578", {"start": v(-84.82, 116.55) * mm, "end": v(-84.84, 116.17) * mm});
            skLineSegment(sketch, "E11579", {"start": v(-84.84, 116.17) * mm, "end": v(-84.87, 115.88) * mm});
            skLineSegment(sketch, "E11580", {"start": v(-84.87, 115.88) * mm, "end": v(-84.9, 115.68) * mm});
            skLineSegment(sketch, "E11581", {"start": v(-84.9, 115.68) * mm, "end": v(-84.93, 115.55) * mm});
            skLineSegment(sketch, "E11582", {"start": v(-84.93, 115.55) * mm, "end": v(-84.94, 115.51) * mm});
            skLineSegment(sketch, "E11583", {"start": v(-84.94, 115.51) * mm, "end": v(-85.42, 113.83) * mm});
            skLineSegment(sketch, "E11584", {"start": v(-85.42, 113.83) * mm, "end": v(-82.35, 112.8) * mm});
            skLineSegment(sketch, "E11585", {"start": v(-82.35, 112.8) * mm, "end": v(-81.7, 114.43) * mm});
            skLineSegment(sketch, "E11586", {"start": v(-81.7, 114.43) * mm, "end": v(-81.68, 114.47) * mm});
            skLineSegment(sketch, "E11587", {"start": v(-81.68, 114.47) * mm, "end": v(-81.62, 114.58) * mm});
            skLineSegment(sketch, "E11588", {"start": v(-81.62, 114.58) * mm, "end": v(-81.52, 114.76) * mm});
            skLineSegment(sketch, "E11589", {"start": v(-81.52, 114.76) * mm, "end": v(-81.37, 115.01) * mm});
            skLineSegment(sketch, "E11590", {"start": v(-81.37, 115.01) * mm, "end": v(-81.15, 115.32) * mm});
            skLineSegment(sketch, "E11591", {"start": v(-81.15, 115.32) * mm, "end": v(-80.87, 115.69) * mm});
            skLineSegment(sketch, "E11592", {"start": v(-80.87, 115.69) * mm, "end": v(-80.5, 116.1) * mm});
            skLineSegment(sketch, "E11593", {"start": v(-80.5, 116.1) * mm, "end": v(-80.07, 116.56) * mm});
            skLineSegment(sketch, "E11594", {"start": v(-80.07, 116.56) * mm, "end": v(-79.56, 117.05) * mm});
            skLineSegment(sketch, "E11595", {"start": v(-79.56, 117.05) * mm, "end": v(-79.27, 117.3) * mm});
            skLineSegment(sketch, "E11596", {"start": v(-79.27, 117.3) * mm, "end": v(-77.22, 116.35) * mm});
            skLineSegment(sketch, "E11597", {"start": v(-77.22, 116.35) * mm, "end": v(-77.23, 115.97) * mm});
            skLineSegment(sketch, "E11598", {"start": v(-77.23, 115.97) * mm, "end": v(-77.29, 115.26) * mm});
            skLineSegment(sketch, "E11599", {"start": v(-77.29, 115.26) * mm, "end": v(-77.37, 114.64) * mm});
            skLineSegment(sketch, "E11600", {"start": v(-77.37, 114.64) * mm, "end": v(-77.46, 114.11) * mm});
            skLineSegment(sketch, "E11601", {"start": v(-77.46, 114.11) * mm, "end": v(-77.57, 113.66) * mm});
            skLineSegment(sketch, "E11602", {"start": v(-77.57, 113.66) * mm, "end": v(-77.67, 113.3) * mm});
            skLineSegment(sketch, "E11603", {"start": v(-77.67, 113.3) * mm, "end": v(-77.77, 113.03) * mm});
            skLineSegment(sketch, "E11604", {"start": v(-77.77, 113.03) * mm, "end": v(-77.84, 112.83) * mm});
            skLineSegment(sketch, "E11605", {"start": v(-77.84, 112.83) * mm, "end": v(-77.9, 112.72) * mm});
            skLineSegment(sketch, "E11606", {"start": v(-77.9, 112.72) * mm, "end": v(-77.92, 112.68) * mm});
            skLineSegment(sketch, "E11607", {"start": v(-77.92, 112.68) * mm, "end": v(-78.77, 111.14) * mm});
            skLineSegment(sketch, "E11608", {"start": v(-78.77, 111.14) * mm, "end": v(-76, 109.47) * mm});
            skLineSegment(sketch, "E11609", {"start": v(-76, 109.47) * mm, "end": v(-75, 110.91) * mm});
            skLineSegment(sketch, "E11610", {"start": v(-75, 110.91) * mm, "end": v(-74.98, 110.95) * mm});
            skLineSegment(sketch, "E11611", {"start": v(-74.98, 110.95) * mm, "end": v(-74.9, 111.04) * mm});
            skLineSegment(sketch, "E11612", {"start": v(-74.9, 111.04) * mm, "end": v(-74.76, 111.2) * mm});
            skLineSegment(sketch, "E11613", {"start": v(-74.76, 111.2) * mm, "end": v(-74.55, 111.4) * mm});
            skLineSegment(sketch, "E11614", {"start": v(-74.55, 111.4) * mm, "end": v(-74.27, 111.66) * mm});
            skLineSegment(sketch, "E11615", {"start": v(-74.27, 111.66) * mm, "end": v(-73.9, 111.95) * mm});
            skLineSegment(sketch, "E11616", {"start": v(-73.9, 111.95) * mm, "end": v(-73.47, 112.28) * mm});
            skLineSegment(sketch, "E11617", {"start": v(-73.47, 112.28) * mm, "end": v(-72.94, 112.63) * mm});
            skLineSegment(sketch, "E11618", {"start": v(-72.94, 112.63) * mm, "end": v(-72.32, 113) * mm});
            skLineSegment(sketch, "E11619", {"start": v(-72.32, 113) * mm, "end": v(-72, 113.17) * mm});
            skLineSegment(sketch, "E11620", {"start": v(-72, 113.17) * mm, "end": v(-70.2, 111.8) * mm});
            skLineSegment(sketch, "E11621", {"start": v(-70.2, 111.8) * mm, "end": v(-70.3, 111.44) * mm});
            skLineSegment(sketch, "E11622", {"start": v(-70.3, 111.44) * mm, "end": v(-70.52, 110.76) * mm});
            skLineSegment(sketch, "E11623", {"start": v(-70.52, 110.76) * mm, "end": v(-70.73, 110.17) * mm});
            skLineSegment(sketch, "E11624", {"start": v(-70.73, 110.17) * mm, "end": v(-70.95, 109.67) * mm});
            skLineSegment(sketch, "E11625", {"start": v(-70.95, 109.67) * mm, "end": v(-71.15, 109.26) * mm});
            skLineSegment(sketch, "E11626", {"start": v(-71.15, 109.26) * mm, "end": v(-71.33, 108.93) * mm});
            skLineSegment(sketch, "E11627", {"start": v(-71.33, 108.93) * mm, "end": v(-71.49, 108.68) * mm});
            skLineSegment(sketch, "E11628", {"start": v(-71.49, 108.68) * mm, "end": v(-71.6, 108.51) * mm});
            skLineSegment(sketch, "E11629", {"start": v(-71.6, 108.51) * mm, "end": v(-71.68, 108.41) * mm});
            skLineSegment(sketch, "E11630", {"start": v(-71.68, 108.41) * mm, "end": v(-71.71, 108.38) * mm});
            skLineSegment(sketch, "E11631", {"start": v(-71.71, 108.38) * mm, "end": v(-72.9, 107.07) * mm});
            skLineSegment(sketch, "E11632", {"start": v(-72.9, 107.07) * mm, "end": v(-70.58, 104.83) * mm});
            skCircle(sketch, "E11633", {"center": v(95.8, -66.59) * mm, "radius": 1.25 * mm});
            skLineSegment(sketch, "E11634", {"start": v(92.8, -68.69) * mm, "end": v(98.8, -68.69) * mm});
            skLineSegment(sketch, "E11635", {"start": v(98.8, -68.69) * mm, "end": v(98.8, -64.49) * mm});
            skLineSegment(sketch, "E11636", {"start": v(98.8, -64.49) * mm, "end": v(92.8, -64.49) * mm});
            skLineSegment(sketch, "E11637", {"start": v(92.8, -64.49) * mm, "end": v(92.8, -68.69) * mm});
            skCircle(sketch, "E11638", {"center": v(95.8, -66.59) * mm, "radius": 3.75 * mm});
            skLineSegment(sketch, "E11639", {"start": v(117.41, -46.34) * mm, "end": v(118.77, -45.07) * mm});
            skLineSegment(sketch, "E11640", {"start": v(118.77, -45.07) * mm, "end": v(118.8, -45.05) * mm});
            skLineSegment(sketch, "E11641", {"start": v(118.8, -45.05) * mm, "end": v(118.89, -44.97) * mm});
            skLineSegment(sketch, "E11642", {"start": v(118.89, -44.97) * mm, "end": v(119.05, -44.86) * mm});
            skLineSegment(sketch, "E11643", {"start": v(119.05, -44.86) * mm, "end": v(119.28, -44.7) * mm});
            skLineSegment(sketch, "E11644", {"start": v(119.28, -44.7) * mm, "end": v(119.58, -44.53) * mm});
            skLineSegment(sketch, "E11645", {"start": v(119.58, -44.53) * mm, "end": v(119.97, -44.33) * mm});
            skLineSegment(sketch, "E11646", {"start": v(119.97, -44.33) * mm, "end": v(120.43, -44.12) * mm});
            skLineSegment(sketch, "E11647", {"start": v(120.43, -44.12) * mm, "end": v(120.98, -43.9) * mm});
            skLineSegment(sketch, "E11648", {"start": v(120.98, -43.9) * mm, "end": v(121.61, -43.69) * mm});
            skLineSegment(sketch, "E11649", {"start": v(121.61, -43.69) * mm, "end": v(122.14, -43.54) * mm});
            skArc(sketch, "E11650", {"start": v(122.14, -43.54) * mm, "mid": v(122.87, -44.4) * mm, "end": v(123.57, -45.27) * mm});
            skLineSegment(sketch, "E11651", {"start": v(123.57, -45.27) * mm, "end": v(123.31, -45.76) * mm});
            skLineSegment(sketch, "E11652", {"start": v(123.31, -45.76) * mm, "end": v(122.98, -46.34) * mm});
            skLineSegment(sketch, "E11653", {"start": v(122.98, -46.34) * mm, "end": v(122.66, -46.84) * mm});
            skLineSegment(sketch, "E11654", {"start": v(122.66, -46.84) * mm, "end": v(122.36, -47.25) * mm});
            skLineSegment(sketch, "E11655", {"start": v(122.36, -47.25) * mm, "end": v(122.1, -47.59) * mm});
            skLineSegment(sketch, "E11656", {"start": v(122.1, -47.59) * mm, "end": v(121.86, -47.85) * mm});
            skLineSegment(sketch, "E11657", {"start": v(121.86, -47.85) * mm, "end": v(121.66, -48.05) * mm});
            skLineSegment(sketch, "E11658", {"start": v(121.66, -48.05) * mm, "end": v(121.52, -48.18) * mm});
            skLineSegment(sketch, "E11659", {"start": v(121.52, -48.18) * mm, "end": v(121.43, -48.26) * mm});
            skLineSegment(sketch, "E11660", {"start": v(121.43, -48.26) * mm, "end": v(121.4, -48.28) * mm});
            skLineSegment(sketch, "E11661", {"start": v(121.4, -48.28) * mm, "end": v(119.89, -49.36) * mm});
            skArc(sketch, "E11662", {"start": v(119.89, -49.36) * mm, "mid": v(120.8, -50.7) * mm, "end": v(121.63, -52.1) * mm});
            skLineSegment(sketch, "E11663", {"start": v(121.63, -52.1) * mm, "end": v(123.25, -51.2) * mm});
            skLineSegment(sketch, "E11664", {"start": v(123.25, -51.2) * mm, "end": v(123.28, -51.18) * mm});
            skLineSegment(sketch, "E11665", {"start": v(123.28, -51.18) * mm, "end": v(123.39, -51.13) * mm});
            skLineSegment(sketch, "E11666", {"start": v(123.39, -51.13) * mm, "end": v(123.57, -51.05) * mm});
            skLineSegment(sketch, "E11667", {"start": v(123.57, -51.05) * mm, "end": v(123.83, -50.96) * mm});
            skLineSegment(sketch, "E11668", {"start": v(123.83, -50.96) * mm, "end": v(124.17, -50.86) * mm});
            skLineSegment(sketch, "E11669", {"start": v(124.17, -50.86) * mm, "end": v(124.6, -50.76) * mm});
            skLineSegment(sketch, "E11670", {"start": v(124.6, -50.76) * mm, "end": v(125.1, -50.67) * mm});
            skLineSegment(sketch, "E11671", {"start": v(125.1, -50.67) * mm, "end": v(125.68, -50.59) * mm});
            skLineSegment(sketch, "E11672", {"start": v(125.68, -50.59) * mm, "end": v(126.34, -50.53) * mm});
            skLineSegment(sketch, "E11673", {"start": v(126.34, -50.53) * mm, "end": v(126.9, -50.51) * mm});
            skArc(sketch, "E11674", {"start": v(126.9, -50.51) * mm, "mid": v(127.4, -51.52) * mm, "end": v(127.86, -52.54) * mm});
            skLineSegment(sketch, "E11675", {"start": v(127.86, -52.54) * mm, "end": v(127.5, -52.95) * mm});
            skLineSegment(sketch, "E11676", {"start": v(127.5, -52.95) * mm, "end": v(127.04, -53.43) * mm});
            skLineSegment(sketch, "E11677", {"start": v(127.04, -53.43) * mm, "end": v(126.6, -53.84) * mm});
            skLineSegment(sketch, "E11678", {"start": v(126.6, -53.84) * mm, "end": v(126.22, -54.17) * mm});
            skLineSegment(sketch, "E11679", {"start": v(126.22, -54.17) * mm, "end": v(125.87, -54.43) * mm});
            skLineSegment(sketch, "E11680", {"start": v(125.87, -54.43) * mm, "end": v(125.58, -54.63) * mm});
            skLineSegment(sketch, "E11681", {"start": v(125.58, -54.63) * mm, "end": v(125.35, -54.78) * mm});
            skLineSegment(sketch, "E11682", {"start": v(125.35, -54.78) * mm, "end": v(125.18, -54.87) * mm});
            skLineSegment(sketch, "E11683", {"start": v(125.18, -54.87) * mm, "end": v(125.07, -54.92) * mm});
            skLineSegment(sketch, "E11684", {"start": v(125.07, -54.92) * mm, "end": v(125.03, -54.94) * mm});
            skLineSegment(sketch, "E11685", {"start": v(125.03, -54.94) * mm, "end": v(123.3, -55.63) * mm});
            skArc(sketch, "E11686", {"start": v(123.3, -55.63) * mm, "mid": v(123.87, -57.15) * mm, "end": v(124.34, -58.7) * mm});
            skLineSegment(sketch, "E11687", {"start": v(124.34, -58.7) * mm, "end": v(126.13, -58.2) * mm});
            skLineSegment(sketch, "E11688", {"start": v(126.13, -58.2) * mm, "end": v(126.17, -58.2) * mm});
            skLineSegment(sketch, "E11689", {"start": v(126.17, -58.2) * mm, "end": v(126.29, -58.18) * mm});
            skLineSegment(sketch, "E11690", {"start": v(126.29, -58.18) * mm, "end": v(126.48, -58.15) * mm});
            skLineSegment(sketch, "E11691", {"start": v(126.48, -58.15) * mm, "end": v(126.76, -58.12) * mm});
            skLineSegment(sketch, "E11692", {"start": v(126.76, -58.12) * mm, "end": v(127.1, -58.1) * mm});
            skLineSegment(sketch, "E11693", {"start": v(127.1, -58.1) * mm, "end": v(127.54, -58.11) * mm});
            skLineSegment(sketch, "E11694", {"start": v(127.54, -58.11) * mm, "end": v(128.05, -58.14) * mm});
            skLineSegment(sketch, "E11695", {"start": v(128.05, -58.14) * mm, "end": v(128.64, -58.2) * mm});
            skLineSegment(sketch, "E11696", {"start": v(128.64, -58.2) * mm, "end": v(129.3, -58.3) * mm});
            skLineSegment(sketch, "E11697", {"start": v(129.3, -58.3) * mm, "end": v(129.84, -58.42) * mm});
            skArc(sketch, "E11698", {"start": v(129.84, -58.42) * mm, "mid": v(130.08, -59.51) * mm, "end": v(130.3, -60.62) * mm});
            skLineSegment(sketch, "E11699", {"start": v(130.3, -60.62) * mm, "end": v(129.84, -60.93) * mm});
            skLineSegment(sketch, "E11700", {"start": v(129.84, -60.93) * mm, "end": v(129.28, -61.29) * mm});
            skLineSegment(sketch, "E11701", {"start": v(129.28, -61.29) * mm, "end": v(128.76, -61.58) * mm});
            skLineSegment(sketch, "E11702", {"start": v(128.76, -61.58) * mm, "end": v(128.3, -61.8) * mm});
            skLineSegment(sketch, "E11703", {"start": v(128.3, -61.8) * mm, "end": v(127.9, -61.98) * mm});
            skLineSegment(sketch, "E11704", {"start": v(127.9, -61.98) * mm, "end": v(127.58, -62.1) * mm});
            skLineSegment(sketch, "E11705", {"start": v(127.58, -62.1) * mm, "end": v(127.32, -62.2) * mm});
            skLineSegment(sketch, "E11706", {"start": v(127.32, -62.2) * mm, "end": v(127.13, -62.24) * mm});
            skLineSegment(sketch, "E11707", {"start": v(127.13, -62.24) * mm, "end": v(127.01, -62.27) * mm});
            skLineSegment(sketch, "E11708", {"start": v(127.01, -62.27) * mm, "end": v(126.97, -62.27) * mm});
            skLineSegment(sketch, "E11709", {"start": v(126.97, -62.27) * mm, "end": v(125.13, -62.53) * mm});
            skArc(sketch, "E11710", {"start": v(125.13, -62.53) * mm, "mid": v(125.31, -64.14) * mm, "end": v(125.4, -65.76) * mm});
            skLineSegment(sketch, "E11711", {"start": v(125.4, -65.76) * mm, "end": v(127.26, -65.71) * mm});
            skLineSegment(sketch, "E11712", {"start": v(127.26, -65.71) * mm, "end": v(127.3, -65.71) * mm});
            skLineSegment(sketch, "E11713", {"start": v(127.3, -65.71) * mm, "end": v(127.41, -65.72) * mm});
            skLineSegment(sketch, "E11714", {"start": v(127.41, -65.72) * mm, "end": v(127.6, -65.74) * mm});
            skLineSegment(sketch, "E11715", {"start": v(127.6, -65.74) * mm, "end": v(127.88, -65.78) * mm});
            skLineSegment(sketch, "E11716", {"start": v(127.88, -65.78) * mm, "end": v(128.23, -65.85) * mm});
            skLineSegment(sketch, "E11717", {"start": v(128.23, -65.85) * mm, "end": v(128.65, -65.95) * mm});
            skLineSegment(sketch, "E11718", {"start": v(128.65, -65.95) * mm, "end": v(129.14, -66.1) * mm});
            skLineSegment(sketch, "E11719", {"start": v(129.14, -66.1) * mm, "end": v(129.7, -66.3) * mm});
            skLineSegment(sketch, "E11720", {"start": v(129.7, -66.3) * mm, "end": v(130.3, -66.56) * mm});
            skLineSegment(sketch, "E11721", {"start": v(130.3, -66.56) * mm, "end": v(130.8, -66.8) * mm});
            skArc(sketch, "E11722", {"start": v(130.8, -66.8) * mm, "mid": v(130.78, -67.92) * mm, "end": v(130.72, -69.04) * mm});
            skLineSegment(sketch, "E11723", {"start": v(130.72, -69.04) * mm, "end": v(130.2, -69.24) * mm});
            skLineSegment(sketch, "E11724", {"start": v(130.2, -69.24) * mm, "end": v(129.57, -69.45) * mm});
            skLineSegment(sketch, "E11725", {"start": v(129.57, -69.45) * mm, "end": v(129, -69.61) * mm});
            skLineSegment(sketch, "E11726", {"start": v(129, -69.61) * mm, "end": v(128.5, -69.72) * mm});
            skLineSegment(sketch, "E11727", {"start": v(128.5, -69.72) * mm, "end": v(128.08, -69.8) * mm});
            skLineSegment(sketch, "E11728", {"start": v(128.08, -69.8) * mm, "end": v(127.73, -69.84) * mm});
            skLineSegment(sketch, "E11729", {"start": v(127.73, -69.84) * mm, "end": v(127.45, -69.86) * mm});
            skLineSegment(sketch, "E11730", {"start": v(127.45, -69.86) * mm, "end": v(127.25, -69.86) * mm});
            skLineSegment(sketch, "E11731", {"start": v(127.25, -69.86) * mm, "end": v(127.14, -69.86) * mm});
            skLineSegment(sketch, "E11732", {"start": v(127.14, -69.86) * mm, "end": v(127.1, -69.86) * mm});
            skLineSegment(sketch, "E11733", {"start": v(127.1, -69.86) * mm, "end": v(125.25, -69.67) * mm});
            skArc(sketch, "E11734", {"start": v(125.25, -69.67) * mm, "mid": v(125.04, -71.27) * mm, "end": v(124.74, -72.87) * mm});
            skLineSegment(sketch, "E11735", {"start": v(124.74, -72.87) * mm, "end": v(126.55, -73.26) * mm});
            skLineSegment(sketch, "E11736", {"start": v(126.55, -73.26) * mm, "end": v(126.59, -73.27) * mm});
            skLineSegment(sketch, "E11737", {"start": v(126.59, -73.27) * mm, "end": v(126.7, -73.3) * mm});
            skLineSegment(sketch, "E11738", {"start": v(126.7, -73.3) * mm, "end": v(126.89, -73.37) * mm});
            skLineSegment(sketch, "E11739", {"start": v(126.89, -73.37) * mm, "end": v(127.14, -73.48) * mm});
            skLineSegment(sketch, "E11740", {"start": v(127.14, -73.48) * mm, "end": v(127.46, -73.63) * mm});
            skLineSegment(sketch, "E11741", {"start": v(127.46, -73.63) * mm, "end": v(127.84, -73.83) * mm});
            skLineSegment(sketch, "E11742", {"start": v(127.84, -73.83) * mm, "end": v(128.28, -74.1) * mm});
            skLineSegment(sketch, "E11743", {"start": v(128.28, -74.1) * mm, "end": v(128.77, -74.42) * mm});
            skLineSegment(sketch, "E11744", {"start": v(128.77, -74.42) * mm, "end": v(129.31, -74.82) * mm});
            skLineSegment(sketch, "E11745", {"start": v(129.31, -74.82) * mm, "end": v(129.73, -75.17) * mm});
            skArc(sketch, "E11746", {"start": v(129.73, -75.17) * mm, "mid": v(129.44, -76.25) * mm, "end": v(129.11, -77.33) * mm});
            skLineSegment(sketch, "E11747", {"start": v(129.11, -77.33) * mm, "end": v(128.57, -77.4) * mm});
            skLineSegment(sketch, "E11748", {"start": v(128.57, -77.4) * mm, "end": v(127.9, -77.45) * mm});
            skLineSegment(sketch, "E11749", {"start": v(127.9, -77.45) * mm, "end": v(127.31, -77.47) * mm});
            skLineSegment(sketch, "E11750", {"start": v(127.31, -77.47) * mm, "end": v(126.8, -77.46) * mm});
            skLineSegment(sketch, "E11751", {"start": v(126.8, -77.46) * mm, "end": v(126.37, -77.43) * mm});
            skLineSegment(sketch, "E11752", {"start": v(126.37, -77.43) * mm, "end": v(126.02, -77.39) * mm});
            skLineSegment(sketch, "E11753", {"start": v(126.02, -77.39) * mm, "end": v(125.75, -77.34) * mm});
            skLineSegment(sketch, "E11754", {"start": v(125.75, -77.34) * mm, "end": v(125.56, -77.3) * mm});
            skLineSegment(sketch, "E11755", {"start": v(125.56, -77.3) * mm, "end": v(125.44, -77.26) * mm});
            skLineSegment(sketch, "E11756", {"start": v(125.44, -77.26) * mm, "end": v(125.4, -77.25) * mm});
            skLineSegment(sketch, "E11757", {"start": v(125.4, -77.25) * mm, "end": v(123.66, -76.62) * mm});
            skArc(sketch, "E11758", {"start": v(123.66, -76.62) * mm, "mid": v(123.07, -78.13) * mm, "end": v(122.4, -79.61) * mm});
            skLineSegment(sketch, "E11759", {"start": v(122.4, -79.61) * mm, "end": v(124.06, -80.43) * mm});
            skLineSegment(sketch, "E11760", {"start": v(124.06, -80.43) * mm, "end": v(124.1, -80.45) * mm});
            skLineSegment(sketch, "E11761", {"start": v(124.1, -80.45) * mm, "end": v(124.2, -80.5) * mm});
            skLineSegment(sketch, "E11762", {"start": v(124.2, -80.5) * mm, "end": v(124.36, -80.61) * mm});
            skLineSegment(sketch, "E11763", {"start": v(124.36, -80.61) * mm, "end": v(124.58, -80.78) * mm});
            skLineSegment(sketch, "E11764", {"start": v(124.58, -80.78) * mm, "end": v(124.86, -81) * mm});
            skLineSegment(sketch, "E11765", {"start": v(124.86, -81) * mm, "end": v(125.18, -81.29) * mm});
            skLineSegment(sketch, "E11766", {"start": v(125.18, -81.29) * mm, "end": v(125.54, -81.65) * mm});
            skLineSegment(sketch, "E11767", {"start": v(125.54, -81.65) * mm, "end": v(125.94, -82.08) * mm});
            skLineSegment(sketch, "E11768", {"start": v(125.94, -82.08) * mm, "end": v(126.37, -82.6) * mm});
            skLineSegment(sketch, "E11769", {"start": v(126.37, -82.6) * mm, "end": v(126.7, -83.04) * mm});
            skArc(sketch, "E11770", {"start": v(126.7, -83.04) * mm, "mid": v(126.15, -84.02) * mm, "end": v(125.58, -84.99) * mm});
            skLineSegment(sketch, "E11771", {"start": v(125.58, -84.99) * mm, "end": v(125.03, -84.92) * mm});
            skLineSegment(sketch, "E11772", {"start": v(125.03, -84.92) * mm, "end": v(124.37, -84.82) * mm});
            skLineSegment(sketch, "E11773", {"start": v(124.37, -84.82) * mm, "end": v(123.8, -84.7) * mm});
            skLineSegment(sketch, "E11774", {"start": v(123.8, -84.7) * mm, "end": v(123.3, -84.56) * mm});
            skLineSegment(sketch, "E11775", {"start": v(123.3, -84.56) * mm, "end": v(122.89, -84.43) * mm});
            skLineSegment(sketch, "E11776", {"start": v(122.89, -84.43) * mm, "end": v(122.56, -84.3) * mm});
            skLineSegment(sketch, "E11777", {"start": v(122.56, -84.3) * mm, "end": v(122.3, -84.2) * mm});
            skLineSegment(sketch, "E11778", {"start": v(122.3, -84.2) * mm, "end": v(122.13, -84.1) * mm});
            skLineSegment(sketch, "E11779", {"start": v(122.13, -84.1) * mm, "end": v(122.03, -84.05) * mm});
            skLineSegment(sketch, "E11780", {"start": v(122.03, -84.05) * mm, "end": v(122, -84.03) * mm});
            skLineSegment(sketch, "E11781", {"start": v(122, -84.03) * mm, "end": v(120.45, -83) * mm});
            skArc(sketch, "E11782", {"start": v(120.45, -83) * mm, "mid": v(119.51, -84.32) * mm, "end": v(118.5, -85.6) * mm});
            skLineSegment(sketch, "E11783", {"start": v(118.5, -85.6) * mm, "end": v(119.93, -86.79) * mm});
            skLineSegment(sketch, "E11784", {"start": v(119.93, -86.79) * mm, "end": v(119.96, -86.81) * mm});
            skLineSegment(sketch, "E11785", {"start": v(119.96, -86.81) * mm, "end": v(120.04, -86.9) * mm});
            skLineSegment(sketch, "E11786", {"start": v(120.04, -86.9) * mm, "end": v(120.17, -87.04) * mm});
            skLineSegment(sketch, "E11787", {"start": v(120.17, -87.04) * mm, "end": v(120.35, -87.25) * mm});
            skLineSegment(sketch, "E11788", {"start": v(120.35, -87.25) * mm, "end": v(120.56, -87.53) * mm});
            skLineSegment(sketch, "E11789", {"start": v(120.56, -87.53) * mm, "end": v(120.8, -87.9) * mm});
            skLineSegment(sketch, "E11790", {"start": v(120.8, -87.9) * mm, "end": v(121.07, -88.33) * mm});
            skLineSegment(sketch, "E11791", {"start": v(121.07, -88.33) * mm, "end": v(121.36, -88.85) * mm});
            skLineSegment(sketch, "E11792", {"start": v(121.36, -88.85) * mm, "end": v(121.65, -89.45) * mm});
            skLineSegment(sketch, "E11793", {"start": v(121.65, -89.45) * mm, "end": v(121.86, -89.96) * mm});
            skArc(sketch, "E11794", {"start": v(121.86, -89.96) * mm, "mid": v(121.1, -90.78) * mm, "end": v(120.3, -91.58) * mm});
            skLineSegment(sketch, "E11795", {"start": v(120.3, -91.58) * mm, "end": v(119.8, -91.39) * mm});
            skLineSegment(sketch, "E11796", {"start": v(119.8, -91.39) * mm, "end": v(119.18, -91.12) * mm});
            skLineSegment(sketch, "E11797", {"start": v(119.18, -91.12) * mm, "end": v(118.65, -90.87) * mm});
            skLineSegment(sketch, "E11798", {"start": v(118.65, -90.87) * mm, "end": v(118.2, -90.62) * mm});
            skLineSegment(sketch, "E11799", {"start": v(118.2, -90.62) * mm, "end": v(117.83, -90.4) * mm});
            skLineSegment(sketch, "E11800", {"start": v(117.83, -90.4) * mm, "end": v(117.54, -90.2) * mm});
            skLineSegment(sketch, "E11801", {"start": v(117.54, -90.2) * mm, "end": v(117.32, -90.02) * mm});
            skLineSegment(sketch, "E11802", {"start": v(117.32, -90.02) * mm, "end": v(117.17, -89.9) * mm});
            skLineSegment(sketch, "E11803", {"start": v(117.17, -89.9) * mm, "end": v(117.09, -89.82) * mm});
            skLineSegment(sketch, "E11804", {"start": v(117.09, -89.82) * mm, "end": v(117.06, -89.79) * mm});
            skLineSegment(sketch, "E11805", {"start": v(117.06, -89.79) * mm, "end": v(115.8, -88.42) * mm});
            skArc(sketch, "E11806", {"start": v(115.8, -88.42) * mm, "mid": v(114.58, -89.48) * mm, "end": v(113.3, -90.48) * mm});
            skLineSegment(sketch, "E11807", {"start": v(113.3, -90.48) * mm, "end": v(114.4, -91.97) * mm});
            skLineSegment(sketch, "E11808", {"start": v(114.4, -91.97) * mm, "end": v(114.41, -92) * mm});
            skLineSegment(sketch, "E11809", {"start": v(114.41, -92) * mm, "end": v(114.48, -92.1) * mm});
            skLineSegment(sketch, "E11810", {"start": v(114.48, -92.1) * mm, "end": v(114.57, -92.28) * mm});
            skLineSegment(sketch, "E11811", {"start": v(114.57, -92.28) * mm, "end": v(114.7, -92.53) * mm});
            skLineSegment(sketch, "E11812", {"start": v(114.7, -92.53) * mm, "end": v(114.83, -92.85) * mm});
            skLineSegment(sketch, "E11813", {"start": v(114.83, -92.85) * mm, "end": v(114.98, -93.26) * mm});
            skLineSegment(sketch, "E11814", {"start": v(114.98, -93.26) * mm, "end": v(115.14, -93.74) * mm});
            skLineSegment(sketch, "E11815", {"start": v(115.14, -93.74) * mm, "end": v(115.29, -94.31) * mm});
            skLineSegment(sketch, "E11816", {"start": v(115.29, -94.31) * mm, "end": v(115.42, -94.97) * mm});
            skLineSegment(sketch, "E11817", {"start": v(115.42, -94.97) * mm, "end": v(115.5, -95.51) * mm});
            skArc(sketch, "E11818", {"start": v(115.5, -95.51) * mm, "mid": v(114.57, -96.13) * mm, "end": v(113.62, -96.71) * mm});
            skLineSegment(sketch, "E11819", {"start": v(113.62, -96.71) * mm, "end": v(113.16, -96.4) * mm});
            skLineSegment(sketch, "E11820", {"start": v(113.16, -96.4) * mm, "end": v(112.63, -96) * mm});
            skLineSegment(sketch, "E11821", {"start": v(112.63, -96) * mm, "end": v(112.17, -95.63) * mm});
            skLineSegment(sketch, "E11822", {"start": v(112.17, -95.63) * mm, "end": v(111.8, -95.28) * mm});
            skLineSegment(sketch, "E11823", {"start": v(111.8, -95.28) * mm, "end": v(111.5, -94.97) * mm});
            skLineSegment(sketch, "E11824", {"start": v(111.5, -94.97) * mm, "end": v(111.26, -94.7) * mm});
            skLineSegment(sketch, "E11825", {"start": v(111.26, -94.7) * mm, "end": v(111.09, -94.5) * mm});
            skLineSegment(sketch, "E11826", {"start": v(111.09, -94.5) * mm, "end": v(110.97, -94.33) * mm});
            skLineSegment(sketch, "E11827", {"start": v(110.97, -94.33) * mm, "end": v(110.9, -94.23) * mm});
            skLineSegment(sketch, "E11828", {"start": v(110.9, -94.23) * mm, "end": v(110.89, -94.2) * mm});
            skLineSegment(sketch, "E11829", {"start": v(110.89, -94.2) * mm, "end": v(110, -92.57) * mm});
            skArc(sketch, "E11830", {"start": v(110, -92.57) * mm, "mid": v(108.55, -93.3) * mm, "end": v(107.07, -93.97) * mm});
            skLineSegment(sketch, "E11831", {"start": v(107.07, -93.97) * mm, "end": v(107.78, -95.68) * mm});
            skLineSegment(sketch, "E11832", {"start": v(107.78, -95.68) * mm, "end": v(107.79, -95.72) * mm});
            skLineSegment(sketch, "E11833", {"start": v(107.79, -95.72) * mm, "end": v(107.83, -95.83) * mm});
            skLineSegment(sketch, "E11834", {"start": v(107.83, -95.83) * mm, "end": v(107.88, -96.02) * mm});
            skLineSegment(sketch, "E11835", {"start": v(107.88, -96.02) * mm, "end": v(107.94, -96.3) * mm});
            skLineSegment(sketch, "E11836", {"start": v(107.94, -96.3) * mm, "end": v(108, -96.64) * mm});
            skLineSegment(sketch, "E11837", {"start": v(108, -96.64) * mm, "end": v(108.04, -97.07) * mm});
            skLineSegment(sketch, "E11838", {"start": v(108.04, -97.07) * mm, "end": v(108.08, -97.58) * mm});
            skLineSegment(sketch, "E11839", {"start": v(108.08, -97.58) * mm, "end": v(108.08, -98.17) * mm});
            skLineSegment(sketch, "E11840", {"start": v(108.08, -98.17) * mm, "end": v(108.06, -98.84) * mm});
            skLineSegment(sketch, "E11841", {"start": v(108.06, -98.84) * mm, "end": v(108.01, -99.39) * mm});
            skArc(sketch, "E11842", {"start": v(108.01, -99.39) * mm, "mid": v(106.96, -99.76) * mm, "end": v(105.89, -100.1) * mm});
            skLineSegment(sketch, "E11843", {"start": v(105.89, -100.1) * mm, "end": v(105.52, -99.7) * mm});
            skLineSegment(sketch, "E11844", {"start": v(105.52, -99.7) * mm, "end": v(105.1, -99.18) * mm});
            skLineSegment(sketch, "E11845", {"start": v(105.1, -99.18) * mm, "end": v(104.75, -98.7) * mm});
            skLineSegment(sketch, "E11846", {"start": v(104.75, -98.7) * mm, "end": v(104.47, -98.27) * mm});
            skLineSegment(sketch, "E11847", {"start": v(104.47, -98.27) * mm, "end": v(104.25, -97.9) * mm});
            skLineSegment(sketch, "E11848", {"start": v(104.25, -97.9) * mm, "end": v(104.08, -97.59) * mm});
            skLineSegment(sketch, "E11849", {"start": v(104.08, -97.59) * mm, "end": v(103.97, -97.34) * mm});
            skLineSegment(sketch, "E11850", {"start": v(103.97, -97.34) * mm, "end": v(103.9, -97.16) * mm});
            skLineSegment(sketch, "E11851", {"start": v(103.9, -97.16) * mm, "end": v(103.85, -97.04) * mm});
            skLineSegment(sketch, "E11852", {"start": v(103.85, -97.04) * mm, "end": v(103.84, -97) * mm});
            skLineSegment(sketch, "E11853", {"start": v(103.84, -97) * mm, "end": v(103.37, -95.21) * mm});
            skArc(sketch, "E11854", {"start": v(103.37, -95.21) * mm, "mid": v(101.79, -95.58) * mm, "end": v(100.19, -95.87) * mm});
            skLineSegment(sketch, "E11855", {"start": v(100.19, -95.87) * mm, "end": v(100.46, -97.7) * mm});
            skLineSegment(sketch, "E11856", {"start": v(100.46, -97.7) * mm, "end": v(100.47, -97.74) * mm});
            skLineSegment(sketch, "E11857", {"start": v(100.47, -97.74) * mm, "end": v(100.48, -97.86) * mm});
            skLineSegment(sketch, "E11858", {"start": v(100.48, -97.86) * mm, "end": v(100.48, -98.06) * mm});
            skLineSegment(sketch, "E11859", {"start": v(100.48, -98.06) * mm, "end": v(100.47, -98.33) * mm});
            skLineSegment(sketch, "E11860", {"start": v(100.47, -98.33) * mm, "end": v(100.45, -98.69) * mm});
            skLineSegment(sketch, "E11861", {"start": v(100.45, -98.69) * mm, "end": v(100.4, -99.11) * mm});
            skLineSegment(sketch, "E11862", {"start": v(100.4, -99.11) * mm, "end": v(100.3, -99.62) * mm});
            skLineSegment(sketch, "E11863", {"start": v(100.3, -99.62) * mm, "end": v(100.17, -100.2) * mm});
            skLineSegment(sketch, "E11864", {"start": v(100.17, -100.2) * mm, "end": v(99.99, -100.84) * mm});
            skLineSegment(sketch, "E11865", {"start": v(99.99, -100.84) * mm, "end": v(99.8, -101.36) * mm});
            skArc(sketch, "E11866", {"start": v(99.8, -101.36) * mm, "mid": v(98.7, -101.47) * mm, "end": v(97.57, -101.54) * mm});
            skLineSegment(sketch, "E11867", {"start": v(97.57, -101.54) * mm, "end": v(97.31, -101.06) * mm});
            skLineSegment(sketch, "E11868", {"start": v(97.31, -101.06) * mm, "end": v(97.03, -100.45) * mm});
            skLineSegment(sketch, "E11869", {"start": v(97.03, -100.45) * mm, "end": v(96.8, -99.9) * mm});
            skLineSegment(sketch, "E11870", {"start": v(96.8, -99.9) * mm, "end": v(96.63, -99.43) * mm});
            skLineSegment(sketch, "E11871", {"start": v(96.63, -99.43) * mm, "end": v(96.5, -99.01) * mm});
            skLineSegment(sketch, "E11872", {"start": v(96.5, -99.01) * mm, "end": v(96.42, -98.67) * mm});
            skLineSegment(sketch, "E11873", {"start": v(96.42, -98.67) * mm, "end": v(96.37, -98.4) * mm});
            skLineSegment(sketch, "E11874", {"start": v(96.37, -98.4) * mm, "end": v(96.34, -98.2) * mm});
            skLineSegment(sketch, "E11875", {"start": v(96.34, -98.2) * mm, "end": v(96.33, -98.09) * mm});
            skLineSegment(sketch, "E11876", {"start": v(96.33, -98.09) * mm, "end": v(96.33, -98.05) * mm});
            skLineSegment(sketch, "E11877", {"start": v(96.33, -98.05) * mm, "end": v(96.3, -96.19) * mm});
            skArc(sketch, "E11878", {"start": v(96.3, -96.19) * mm, "mid": v(94.67, -96.17) * mm, "end": v(93.05, -96.07) * mm});
            skLineSegment(sketch, "E11879", {"start": v(93.05, -96.07) * mm, "end": v(92.88, -97.91) * mm});
            skLineSegment(sketch, "E11880", {"start": v(92.88, -97.91) * mm, "end": v(92.88, -97.95) * mm});
            skLineSegment(sketch, "E11881", {"start": v(92.88, -97.95) * mm, "end": v(92.86, -98.07) * mm});
            skLineSegment(sketch, "E11882", {"start": v(92.86, -98.07) * mm, "end": v(92.81, -98.26) * mm});
            skLineSegment(sketch, "E11883", {"start": v(92.81, -98.26) * mm, "end": v(92.74, -98.53) * mm});
            skLineSegment(sketch, "E11884", {"start": v(92.74, -98.53) * mm, "end": v(92.63, -98.86) * mm});
            skLineSegment(sketch, "E11885", {"start": v(92.63, -98.86) * mm, "end": v(92.47, -99.27) * mm});
            skLineSegment(sketch, "E11886", {"start": v(92.47, -99.27) * mm, "end": v(92.27, -99.73) * mm});
            skLineSegment(sketch, "E11887", {"start": v(92.27, -99.73) * mm, "end": v(92, -100.26) * mm});
            skLineSegment(sketch, "E11888", {"start": v(92, -100.26) * mm, "end": v(91.67, -100.84) * mm});
            skLineSegment(sketch, "E11889", {"start": v(91.67, -100.84) * mm, "end": v(91.37, -101.3) * mm});
            skArc(sketch, "E11890", {"start": v(91.37, -101.3) * mm, "mid": v(90.26, -101.14) * mm, "end": v(89.16, -100.95) * mm});
            skLineSegment(sketch, "E11891", {"start": v(89.16, -100.95) * mm, "end": v(89.02, -100.42) * mm});
            skLineSegment(sketch, "E11892", {"start": v(89.02, -100.42) * mm, "end": v(88.89, -99.76) * mm});
            skLineSegment(sketch, "E11893", {"start": v(88.89, -99.76) * mm, "end": v(88.8, -99.18) * mm});
            skLineSegment(sketch, "E11894", {"start": v(88.8, -99.18) * mm, "end": v(88.75, -98.67) * mm});
            skLineSegment(sketch, "E11895", {"start": v(88.75, -98.67) * mm, "end": v(88.73, -98.24) * mm});
            skLineSegment(sketch, "E11896", {"start": v(88.73, -98.24) * mm, "end": v(88.73, -97.88) * mm});
            skLineSegment(sketch, "E11897", {"start": v(88.73, -97.88) * mm, "end": v(88.74, -97.6) * mm});
            skLineSegment(sketch, "E11898", {"start": v(88.74, -97.6) * mm, "end": v(88.76, -97.41) * mm});
            skLineSegment(sketch, "E11899", {"start": v(88.76, -97.41) * mm, "end": v(88.78, -97.3) * mm});
            skLineSegment(sketch, "E11900", {"start": v(88.78, -97.3) * mm, "end": v(88.78, -97.26) * mm});
            skLineSegment(sketch, "E11901", {"start": v(88.78, -97.26) * mm, "end": v(89.2, -95.45) * mm});
            skArc(sketch, "E11902", {"start": v(89.2, -95.45) * mm, "mid": v(87.63, -95.04) * mm, "end": v(86.08, -94.55) * mm});
            skLineSegment(sketch, "E11903", {"start": v(86.08, -94.55) * mm, "end": v(85.47, -96.3) * mm});
            skLineSegment(sketch, "E11904", {"start": v(85.47, -96.3) * mm, "end": v(85.45, -96.34) * mm});
            skLineSegment(sketch, "E11905", {"start": v(85.45, -96.34) * mm, "end": v(85.4, -96.45) * mm});
            skLineSegment(sketch, "E11906", {"start": v(85.4, -96.45) * mm, "end": v(85.32, -96.63) * mm});
            skLineSegment(sketch, "E11907", {"start": v(85.32, -96.63) * mm, "end": v(85.19, -96.87) * mm});
            skLineSegment(sketch, "E11908", {"start": v(85.19, -96.87) * mm, "end": v(85, -97.17) * mm});
            skLineSegment(sketch, "E11909", {"start": v(85, -97.17) * mm, "end": v(84.75, -97.52) * mm});
            skLineSegment(sketch, "E11910", {"start": v(84.75, -97.52) * mm, "end": v(84.44, -97.92) * mm});
            skLineSegment(sketch, "E11911", {"start": v(84.44, -97.92) * mm, "end": v(84.05, -98.37) * mm});
            skLineSegment(sketch, "E11912", {"start": v(84.05, -98.37) * mm, "end": v(83.6, -98.86) * mm});
            skLineSegment(sketch, "E11913", {"start": v(83.6, -98.86) * mm, "end": v(83.2, -99.24) * mm});
            skArc(sketch, "E11914", {"start": v(83.2, -99.24) * mm, "mid": v(82.15, -98.81) * mm, "end": v(81.13, -98.36) * mm});
            skLineSegment(sketch, "E11915", {"start": v(81.13, -98.36) * mm, "end": v(81.12, -97.81) * mm});
            skLineSegment(sketch, "E11916", {"start": v(81.12, -97.81) * mm, "end": v(81.15, -97.14) * mm});
            skLineSegment(sketch, "E11917", {"start": v(81.15, -97.14) * mm, "end": v(81.2, -96.55) * mm});
            skLineSegment(sketch, "E11918", {"start": v(81.2, -96.55) * mm, "end": v(81.27, -96.05) * mm});
            skLineSegment(sketch, "E11919", {"start": v(81.27, -96.05) * mm, "end": v(81.36, -95.62) * mm});
            skLineSegment(sketch, "E11920", {"start": v(81.36, -95.62) * mm, "end": v(81.44, -95.28) * mm});
            skLineSegment(sketch, "E11921", {"start": v(81.44, -95.28) * mm, "end": v(81.52, -95.02) * mm});
            skLineSegment(sketch, "E11922", {"start": v(81.52, -95.02) * mm, "end": v(81.59, -94.83) * mm});
            skLineSegment(sketch, "E11923", {"start": v(81.59, -94.83) * mm, "end": v(81.63, -94.72) * mm});
            skLineSegment(sketch, "E11924", {"start": v(81.63, -94.72) * mm, "end": v(81.65, -94.69) * mm});
            skLineSegment(sketch, "E11925", {"start": v(81.65, -94.69) * mm, "end": v(82.48, -93.03) * mm});
            skArc(sketch, "E11926", {"start": v(82.48, -93.03) * mm, "mid": v(81.05, -92.26) * mm, "end": v(79.67, -91.41) * mm});
            skLineSegment(sketch, "E11927", {"start": v(79.67, -91.41) * mm, "end": v(78.66, -92.97) * mm});
            skLineSegment(sketch, "E11928", {"start": v(78.66, -92.97) * mm, "end": v(78.63, -93) * mm});
            skLineSegment(sketch, "E11929", {"start": v(78.63, -93) * mm, "end": v(78.56, -93.1) * mm});
            skLineSegment(sketch, "E11930", {"start": v(78.56, -93.1) * mm, "end": v(78.44, -93.24) * mm});
            skLineSegment(sketch, "E11931", {"start": v(78.44, -93.24) * mm, "end": v(78.25, -93.45) * mm});
            skLineSegment(sketch, "E11932", {"start": v(78.25, -93.45) * mm, "end": v(78, -93.7) * mm});
            skLineSegment(sketch, "E11933", {"start": v(78, -93.7) * mm, "end": v(77.67, -93.98) * mm});
            skLineSegment(sketch, "E11934", {"start": v(77.67, -93.98) * mm, "end": v(77.27, -94.3) * mm});
            skLineSegment(sketch, "E11935", {"start": v(77.27, -94.3) * mm, "end": v(76.79, -94.64) * mm});
            skLineSegment(sketch, "E11936", {"start": v(76.79, -94.64) * mm, "end": v(76.22, -95) * mm});
            skLineSegment(sketch, "E11937", {"start": v(76.22, -95) * mm, "end": v(75.75, -95.27) * mm});
            skArc(sketch, "E11938", {"start": v(75.75, -95.27) * mm, "mid": v(74.84, -94.61) * mm, "end": v(73.95, -93.92) * mm});
            skLineSegment(sketch, "E11939", {"start": v(73.95, -93.92) * mm, "end": v(74.08, -93.39) * mm});
            skLineSegment(sketch, "E11940", {"start": v(74.08, -93.39) * mm, "end": v(74.26, -92.75) * mm});
            skLineSegment(sketch, "E11941", {"start": v(74.26, -92.75) * mm, "end": v(74.46, -92.19) * mm});
            skLineSegment(sketch, "E11942", {"start": v(74.46, -92.19) * mm, "end": v(74.65, -91.72) * mm});
            skLineSegment(sketch, "E11943", {"start": v(74.65, -91.72) * mm, "end": v(74.83, -91.32) * mm});
            skLineSegment(sketch, "E11944", {"start": v(74.83, -91.32) * mm, "end": v(75, -91) * mm});
            skLineSegment(sketch, "E11945", {"start": v(75, -91) * mm, "end": v(75.13, -90.77) * mm});
            skLineSegment(sketch, "E11946", {"start": v(75.13, -90.77) * mm, "end": v(75.24, -90.6) * mm});
            skLineSegment(sketch, "E11947", {"start": v(75.24, -90.6) * mm, "end": v(75.3, -90.51) * mm});
            skLineSegment(sketch, "E11948", {"start": v(75.3, -90.51) * mm, "end": v(75.33, -90.48) * mm});
            skLineSegment(sketch, "E11949", {"start": v(75.33, -90.48) * mm, "end": v(76.54, -89.07) * mm});
            skArc(sketch, "E11950", {"start": v(76.54, -89.07) * mm, "mid": v(75.34, -87.98) * mm, "end": v(74.2, -86.83) * mm});
            skLineSegment(sketch, "E11951", {"start": v(74.2, -86.83) * mm, "end": v(72.84, -88.1) * mm});
            skLineSegment(sketch, "E11952", {"start": v(72.84, -88.1) * mm, "end": v(72.81, -88.12) * mm});
            skLineSegment(sketch, "E11953", {"start": v(72.81, -88.12) * mm, "end": v(72.72, -88.2) * mm});
            skLineSegment(sketch, "E11954", {"start": v(72.72, -88.2) * mm, "end": v(72.56, -88.31) * mm});
            skLineSegment(sketch, "E11955", {"start": v(72.56, -88.31) * mm, "end": v(72.33, -88.46) * mm});
            skLineSegment(sketch, "E11956", {"start": v(72.33, -88.46) * mm, "end": v(72.02, -88.64) * mm});
            skLineSegment(sketch, "E11957", {"start": v(72.02, -88.64) * mm, "end": v(71.64, -88.84) * mm});
            skLineSegment(sketch, "E11958", {"start": v(71.64, -88.84) * mm, "end": v(71.17, -89.05) * mm});
            skLineSegment(sketch, "E11959", {"start": v(71.17, -89.05) * mm, "end": v(70.63, -89.27) * mm});
            skLineSegment(sketch, "E11960", {"start": v(70.63, -89.27) * mm, "end": v(70, -89.48) * mm});
            skLineSegment(sketch, "E11961", {"start": v(70, -89.48) * mm, "end": v(69.46, -89.63) * mm});
            skArc(sketch, "E11962", {"start": v(69.46, -89.63) * mm, "mid": v(68.74, -88.78) * mm, "end": v(68.04, -87.9) * mm});
            skLineSegment(sketch, "E11963", {"start": v(68.04, -87.9) * mm, "end": v(68.3, -87.41) * mm});
            skLineSegment(sketch, "E11964", {"start": v(68.3, -87.41) * mm, "end": v(68.63, -86.83) * mm});
            skLineSegment(sketch, "E11965", {"start": v(68.63, -86.83) * mm, "end": v(68.95, -86.34) * mm});
            skLineSegment(sketch, "E11966", {"start": v(68.95, -86.34) * mm, "end": v(69.25, -85.92) * mm});
            skLineSegment(sketch, "E11967", {"start": v(69.25, -85.92) * mm, "end": v(69.52, -85.58) * mm});
            skLineSegment(sketch, "E11968", {"start": v(69.52, -85.58) * mm, "end": v(69.75, -85.32) * mm});
            skLineSegment(sketch, "E11969", {"start": v(69.75, -85.32) * mm, "end": v(69.94, -85.12) * mm});
            skLineSegment(sketch, "E11970", {"start": v(69.94, -85.12) * mm, "end": v(70.09, -84.99) * mm});
            skLineSegment(sketch, "E11971", {"start": v(70.09, -84.99) * mm, "end": v(70.18, -84.91) * mm});
            skLineSegment(sketch, "E11972", {"start": v(70.18, -84.91) * mm, "end": v(70.2, -84.89) * mm});
            skLineSegment(sketch, "E11973", {"start": v(70.2, -84.89) * mm, "end": v(71.72, -83.8) * mm});
            skArc(sketch, "E11974", {"start": v(71.72, -83.8) * mm, "mid": v(70.81, -82.46) * mm, "end": v(69.98, -81.07) * mm});
            skLineSegment(sketch, "E11975", {"start": v(69.98, -81.07) * mm, "end": v(68.36, -81.98) * mm});
            skLineSegment(sketch, "E11976", {"start": v(68.36, -81.98) * mm, "end": v(68.33, -82) * mm});
            skLineSegment(sketch, "E11977", {"start": v(68.33, -82) * mm, "end": v(68.22, -82.05) * mm});
            skLineSegment(sketch, "E11978", {"start": v(68.22, -82.05) * mm, "end": v(68.04, -82.12) * mm});
            skLineSegment(sketch, "E11979", {"start": v(68.04, -82.12) * mm, "end": v(67.78, -82.2) * mm});
            skLineSegment(sketch, "E11980", {"start": v(67.78, -82.2) * mm, "end": v(67.44, -82.3) * mm});
            skLineSegment(sketch, "E11981", {"start": v(67.44, -82.3) * mm, "end": v(67.02, -82.41) * mm});
            skLineSegment(sketch, "E11982", {"start": v(67.02, -82.41) * mm, "end": v(66.51, -82.5) * mm});
            skLineSegment(sketch, "E11983", {"start": v(66.51, -82.5) * mm, "end": v(65.93, -82.58) * mm});
            skLineSegment(sketch, "E11984", {"start": v(65.93, -82.58) * mm, "end": v(65.26, -82.64) * mm});
            skLineSegment(sketch, "E11985", {"start": v(65.26, -82.64) * mm, "end": v(64.71, -82.66) * mm});
            skArc(sketch, "E11986", {"start": v(64.71, -82.66) * mm, "mid": v(64.21, -81.66) * mm, "end": v(63.75, -80.64) * mm});
            skLineSegment(sketch, "E11987", {"start": v(63.75, -80.64) * mm, "end": v(64.1, -80.22) * mm});
            skLineSegment(sketch, "E11988", {"start": v(64.1, -80.22) * mm, "end": v(64.57, -79.74) * mm});
            skLineSegment(sketch, "E11989", {"start": v(64.57, -79.74) * mm, "end": v(65, -79.34) * mm});
            skLineSegment(sketch, "E11990", {"start": v(65, -79.34) * mm, "end": v(65.4, -79) * mm});
            skLineSegment(sketch, "E11991", {"start": v(65.4, -79) * mm, "end": v(65.73, -78.74) * mm});
            skLineSegment(sketch, "E11992", {"start": v(65.73, -78.74) * mm, "end": v(66.03, -78.54) * mm});
            skLineSegment(sketch, "E11993", {"start": v(66.03, -78.54) * mm, "end": v(66.26, -78.4) * mm});
            skLineSegment(sketch, "E11994", {"start": v(66.26, -78.4) * mm, "end": v(66.43, -78.3) * mm});
            skLineSegment(sketch, "E11995", {"start": v(66.43, -78.3) * mm, "end": v(66.54, -78.25) * mm});
            skLineSegment(sketch, "E11996", {"start": v(66.54, -78.25) * mm, "end": v(66.57, -78.23) * mm});
            skLineSegment(sketch, "E11997", {"start": v(66.57, -78.23) * mm, "end": v(68.3, -77.54) * mm});
            skArc(sketch, "E11998", {"start": v(68.3, -77.54) * mm, "mid": v(67.74, -76.02) * mm, "end": v(67.26, -74.47) * mm});
            skLineSegment(sketch, "E11999", {"start": v(67.26, -74.47) * mm, "end": v(65.47, -74.96) * mm});
            skLineSegment(sketch, "E12000", {"start": v(65.47, -74.96) * mm, "end": v(65.44, -74.97) * mm});
            skLineSegment(sketch, "E12001", {"start": v(65.44, -74.97) * mm, "end": v(65.32, -75) * mm});
            skLineSegment(sketch, "E12002", {"start": v(65.32, -75) * mm, "end": v(65.13, -75.02) * mm});
            skLineSegment(sketch, "E12003", {"start": v(65.13, -75.02) * mm, "end": v(64.85, -75.05) * mm});
            skLineSegment(sketch, "E12004", {"start": v(64.85, -75.05) * mm, "end": v(64.5, -75.06) * mm});
            skLineSegment(sketch, "E12005", {"start": v(64.5, -75.06) * mm, "end": v(64.07, -75.06) * mm});
            skLineSegment(sketch, "E12006", {"start": v(64.07, -75.06) * mm, "end": v(63.56, -75.03) * mm});
            skLineSegment(sketch, "E12007", {"start": v(63.56, -75.03) * mm, "end": v(62.97, -74.97) * mm});
            skLineSegment(sketch, "E12008", {"start": v(62.97, -74.97) * mm, "end": v(62.3, -74.87) * mm});
            skLineSegment(sketch, "E12009", {"start": v(62.3, -74.87) * mm, "end": v(61.77, -74.75) * mm});
            skArc(sketch, "E12010", {"start": v(61.77, -74.75) * mm, "mid": v(61.53, -73.66) * mm, "end": v(61.32, -72.56) * mm});
            skLineSegment(sketch, "E12011", {"start": v(61.32, -72.56) * mm, "end": v(61.77, -72.24) * mm});
            skLineSegment(sketch, "E12012", {"start": v(61.77, -72.24) * mm, "end": v(62.33, -71.88) * mm});
            skLineSegment(sketch, "E12013", {"start": v(62.33, -71.88) * mm, "end": v(62.85, -71.6) * mm});
            skLineSegment(sketch, "E12014", {"start": v(62.85, -71.6) * mm, "end": v(63.3, -71.37) * mm});
            skLineSegment(sketch, "E12015", {"start": v(63.3, -71.37) * mm, "end": v(63.7, -71.2) * mm});
            skLineSegment(sketch, "E12016", {"start": v(63.7, -71.2) * mm, "end": v(64.03, -71.07) * mm});
            skLineSegment(sketch, "E12017", {"start": v(64.03, -71.07) * mm, "end": v(64.3, -70.98) * mm});
            skLineSegment(sketch, "E12018", {"start": v(64.3, -70.98) * mm, "end": v(64.48, -70.93) * mm});
            skLineSegment(sketch, "E12019", {"start": v(64.48, -70.93) * mm, "end": v(64.6, -70.9) * mm});
            skLineSegment(sketch, "E12020", {"start": v(64.6, -70.9) * mm, "end": v(64.64, -70.9) * mm});
            skLineSegment(sketch, "E12021", {"start": v(64.64, -70.9) * mm, "end": v(66.48, -70.64) * mm});
            skArc(sketch, "E12022", {"start": v(66.48, -70.64) * mm, "mid": v(66.3, -69.03) * mm, "end": v(66.2, -67.4) * mm});
            skLineSegment(sketch, "E12023", {"start": v(66.2, -67.4) * mm, "end": v(64.35, -67.46) * mm});
            skLineSegment(sketch, "E12024", {"start": v(64.35, -67.46) * mm, "end": v(64.31, -67.46) * mm});
            skLineSegment(sketch, "E12025", {"start": v(64.31, -67.46) * mm, "end": v(64.2, -67.46) * mm});
            skLineSegment(sketch, "E12026", {"start": v(64.2, -67.46) * mm, "end": v(64, -67.44) * mm});
            skLineSegment(sketch, "E12027", {"start": v(64, -67.44) * mm, "end": v(63.73, -67.4) * mm});
            skLineSegment(sketch, "E12028", {"start": v(63.73, -67.4) * mm, "end": v(63.38, -67.33) * mm});
            skLineSegment(sketch, "E12029", {"start": v(63.38, -67.33) * mm, "end": v(62.96, -67.22) * mm});
            skLineSegment(sketch, "E12030", {"start": v(62.96, -67.22) * mm, "end": v(62.47, -67.07) * mm});
            skLineSegment(sketch, "E12031", {"start": v(62.47, -67.07) * mm, "end": v(61.92, -66.87) * mm});
            skLineSegment(sketch, "E12032", {"start": v(61.92, -66.87) * mm, "end": v(61.3, -66.6) * mm});
            skLineSegment(sketch, "E12033", {"start": v(61.3, -66.6) * mm, "end": v(60.8, -66.37) * mm});
            skArc(sketch, "E12034", {"start": v(60.8, -66.37) * mm, "mid": v(60.83, -65.25) * mm, "end": v(60.89, -64.13) * mm});
            skLineSegment(sketch, "E12035", {"start": v(60.89, -64.13) * mm, "end": v(61.4, -63.93) * mm});
            skLineSegment(sketch, "E12036", {"start": v(61.4, -63.93) * mm, "end": v(62.04, -63.72) * mm});
            skLineSegment(sketch, "E12037", {"start": v(62.04, -63.72) * mm, "end": v(62.6, -63.56) * mm});
            skLineSegment(sketch, "E12038", {"start": v(62.6, -63.56) * mm, "end": v(63.1, -63.45) * mm});
            skLineSegment(sketch, "E12039", {"start": v(63.1, -63.45) * mm, "end": v(63.53, -63.38) * mm});
            skLineSegment(sketch, "E12040", {"start": v(63.53, -63.38) * mm, "end": v(63.88, -63.33) * mm});
            skLineSegment(sketch, "E12041", {"start": v(63.88, -63.33) * mm, "end": v(64.16, -63.31) * mm});
            skLineSegment(sketch, "E12042", {"start": v(64.16, -63.31) * mm, "end": v(64.35, -63.3) * mm});
            skLineSegment(sketch, "E12043", {"start": v(64.35, -63.3) * mm, "end": v(64.47, -63.31) * mm});
            skLineSegment(sketch, "E12044", {"start": v(64.47, -63.31) * mm, "end": v(64.5, -63.31) * mm});
            skLineSegment(sketch, "E12045", {"start": v(64.5, -63.31) * mm, "end": v(66.36, -63.5) * mm});
            skArc(sketch, "E12046", {"start": v(66.36, -63.5) * mm, "mid": v(66.57, -61.9) * mm, "end": v(66.87, -60.3) * mm});
            skLineSegment(sketch, "E12047", {"start": v(66.87, -60.3) * mm, "end": v(65.06, -59.9) * mm});
            skLineSegment(sketch, "E12048", {"start": v(65.06, -59.9) * mm, "end": v(65.02, -59.9) * mm});
            skLineSegment(sketch, "E12049", {"start": v(65.02, -59.9) * mm, "end": v(64.9, -59.87) * mm});
            skLineSegment(sketch, "E12050", {"start": v(64.9, -59.87) * mm, "end": v(64.72, -59.8) * mm});
            skLineSegment(sketch, "E12051", {"start": v(64.72, -59.8) * mm, "end": v(64.46, -59.7) * mm});
            skLineSegment(sketch, "E12052", {"start": v(64.46, -59.7) * mm, "end": v(64.14, -59.54) * mm});
            skLineSegment(sketch, "E12053", {"start": v(64.14, -59.54) * mm, "end": v(63.76, -59.34) * mm});
            skLineSegment(sketch, "E12054", {"start": v(63.76, -59.34) * mm, "end": v(63.32, -59.08) * mm});
            skLineSegment(sketch, "E12055", {"start": v(63.32, -59.08) * mm, "end": v(62.83, -58.75) * mm});
            skLineSegment(sketch, "E12056", {"start": v(62.83, -58.75) * mm, "end": v(62.3, -58.35) * mm});
            skLineSegment(sketch, "E12057", {"start": v(62.3, -58.35) * mm, "end": v(61.87, -58) * mm});
            skArc(sketch, "E12058", {"start": v(61.87, -58) * mm, "mid": v(62.17, -56.92) * mm, "end": v(62.5, -55.85) * mm});
            skLineSegment(sketch, "E12059", {"start": v(62.5, -55.85) * mm, "end": v(63.04, -55.77) * mm});
            skLineSegment(sketch, "E12060", {"start": v(63.04, -55.77) * mm, "end": v(63.7, -55.72) * mm});
            skLineSegment(sketch, "E12061", {"start": v(63.7, -55.72) * mm, "end": v(64.3, -55.7) * mm});
            skLineSegment(sketch, "E12062", {"start": v(64.3, -55.7) * mm, "end": v(64.8, -55.71) * mm});
            skLineSegment(sketch, "E12063", {"start": v(64.8, -55.71) * mm, "end": v(65.24, -55.74) * mm});
            skLineSegment(sketch, "E12064", {"start": v(65.24, -55.74) * mm, "end": v(65.59, -55.79) * mm});
            skLineSegment(sketch, "E12065", {"start": v(65.59, -55.79) * mm, "end": v(65.86, -55.83) * mm});
            skLineSegment(sketch, "E12066", {"start": v(65.86, -55.83) * mm, "end": v(66.05, -55.88) * mm});
            skLineSegment(sketch, "E12067", {"start": v(66.05, -55.88) * mm, "end": v(66.16, -55.9) * mm});
            skLineSegment(sketch, "E12068", {"start": v(66.16, -55.9) * mm, "end": v(66.2, -55.92) * mm});
            skLineSegment(sketch, "E12069", {"start": v(66.2, -55.92) * mm, "end": v(67.95, -56.55) * mm});
            skArc(sketch, "E12070", {"start": v(67.95, -56.55) * mm, "mid": v(68.54, -55.04) * mm, "end": v(69.21, -53.56) * mm});
            skLineSegment(sketch, "E12071", {"start": v(69.21, -53.56) * mm, "end": v(67.55, -52.74) * mm});
            skLineSegment(sketch, "E12072", {"start": v(67.55, -52.74) * mm, "end": v(67.51, -52.73) * mm});
            skLineSegment(sketch, "E12073", {"start": v(67.51, -52.73) * mm, "end": v(67.41, -52.67) * mm});
            skLineSegment(sketch, "E12074", {"start": v(67.41, -52.67) * mm, "end": v(67.25, -52.56) * mm});
            skLineSegment(sketch, "E12075", {"start": v(67.25, -52.56) * mm, "end": v(67.02, -52.4) * mm});
            skLineSegment(sketch, "E12076", {"start": v(67.02, -52.4) * mm, "end": v(66.75, -52.17) * mm});
            skLineSegment(sketch, "E12077", {"start": v(66.75, -52.17) * mm, "end": v(66.43, -51.88) * mm});
            skLineSegment(sketch, "E12078", {"start": v(66.43, -51.88) * mm, "end": v(66.06, -51.52) * mm});
            skLineSegment(sketch, "E12079", {"start": v(66.06, -51.52) * mm, "end": v(65.67, -51.09) * mm});
            skLineSegment(sketch, "E12080", {"start": v(65.67, -51.09) * mm, "end": v(65.24, -50.57) * mm});
            skLineSegment(sketch, "E12081", {"start": v(65.24, -50.57) * mm, "end": v(64.91, -50.13) * mm});
            skArc(sketch, "E12082", {"start": v(64.91, -50.13) * mm, "mid": v(65.46, -49.15) * mm, "end": v(66.03, -48.19) * mm});
            skLineSegment(sketch, "E12083", {"start": v(66.03, -48.19) * mm, "end": v(66.58, -48.25) * mm});
            skLineSegment(sketch, "E12084", {"start": v(66.58, -48.25) * mm, "end": v(67.24, -48.36) * mm});
            skLineSegment(sketch, "E12085", {"start": v(67.24, -48.36) * mm, "end": v(67.81, -48.48) * mm});
            skLineSegment(sketch, "E12086", {"start": v(67.81, -48.48) * mm, "end": v(68.3, -48.61) * mm});
            skLineSegment(sketch, "E12087", {"start": v(68.3, -48.61) * mm, "end": v(68.72, -48.74) * mm});
            skLineSegment(sketch, "E12088", {"start": v(68.72, -48.74) * mm, "end": v(69.05, -48.87) * mm});
            skLineSegment(sketch, "E12089", {"start": v(69.05, -48.87) * mm, "end": v(69.3, -48.98) * mm});
            skLineSegment(sketch, "E12090", {"start": v(69.3, -48.98) * mm, "end": v(69.48, -49.07) * mm});
            skLineSegment(sketch, "E12091", {"start": v(69.48, -49.07) * mm, "end": v(69.58, -49.12) * mm});
            skLineSegment(sketch, "E12092", {"start": v(69.58, -49.12) * mm, "end": v(69.61, -49.15) * mm});
            skLineSegment(sketch, "E12093", {"start": v(69.61, -49.15) * mm, "end": v(71.16, -50.18) * mm});
            skArc(sketch, "E12094", {"start": v(71.16, -50.18) * mm, "mid": v(72.1, -48.85) * mm, "end": v(73.1, -47.58) * mm});
            skLineSegment(sketch, "E12095", {"start": v(73.1, -47.58) * mm, "end": v(71.68, -46.38) * mm});
            skLineSegment(sketch, "E12096", {"start": v(71.68, -46.38) * mm, "end": v(71.65, -46.36) * mm});
            skLineSegment(sketch, "E12097", {"start": v(71.65, -46.36) * mm, "end": v(71.57, -46.28) * mm});
            skLineSegment(sketch, "E12098", {"start": v(71.57, -46.28) * mm, "end": v(71.43, -46.13) * mm});
            skLineSegment(sketch, "E12099", {"start": v(71.43, -46.13) * mm, "end": v(71.26, -45.92) * mm});
            skLineSegment(sketch, "E12100", {"start": v(71.26, -45.92) * mm, "end": v(71.04, -45.64) * mm});
            skLineSegment(sketch, "E12101", {"start": v(71.04, -45.64) * mm, "end": v(70.8, -45.28) * mm});
            skLineSegment(sketch, "E12102", {"start": v(70.8, -45.28) * mm, "end": v(70.53, -44.84) * mm});
            skLineSegment(sketch, "E12103", {"start": v(70.53, -44.84) * mm, "end": v(70.25, -44.33) * mm});
            skLineSegment(sketch, "E12104", {"start": v(70.25, -44.33) * mm, "end": v(69.96, -43.72) * mm});
            skLineSegment(sketch, "E12105", {"start": v(69.96, -43.72) * mm, "end": v(69.75, -43.22) * mm});
            skArc(sketch, "E12106", {"start": v(69.75, -43.22) * mm, "mid": v(70.51, -42.4) * mm, "end": v(71.3, -41.6) * mm});
            skLineSegment(sketch, "E12107", {"start": v(71.3, -41.6) * mm, "end": v(71.81, -41.79) * mm});
            skLineSegment(sketch, "E12108", {"start": v(71.81, -41.79) * mm, "end": v(72.43, -42.05) * mm});
            skLineSegment(sketch, "E12109", {"start": v(72.43, -42.05) * mm, "end": v(72.96, -42.3) * mm});
            skLineSegment(sketch, "E12110", {"start": v(72.96, -42.3) * mm, "end": v(73.4, -42.55) * mm});
            skLineSegment(sketch, "E12111", {"start": v(73.4, -42.55) * mm, "end": v(73.78, -42.78) * mm});
            skLineSegment(sketch, "E12112", {"start": v(73.78, -42.78) * mm, "end": v(74.07, -42.98) * mm});
            skLineSegment(sketch, "E12113", {"start": v(74.07, -42.98) * mm, "end": v(74.29, -43.15) * mm});
            skLineSegment(sketch, "E12114", {"start": v(74.29, -43.15) * mm, "end": v(74.44, -43.28) * mm});
            skLineSegment(sketch, "E12115", {"start": v(74.44, -43.28) * mm, "end": v(74.52, -43.36) * mm});
            skLineSegment(sketch, "E12116", {"start": v(74.52, -43.36) * mm, "end": v(74.55, -43.38) * mm});
            skLineSegment(sketch, "E12117", {"start": v(74.55, -43.38) * mm, "end": v(75.8, -44.75) * mm});
            skArc(sketch, "E12118", {"start": v(75.8, -44.75) * mm, "mid": v(77.03, -43.7) * mm, "end": v(78.31, -42.7) * mm});
            skLineSegment(sketch, "E12119", {"start": v(78.31, -42.7) * mm, "end": v(77.22, -41.2) * mm});
            skLineSegment(sketch, "E12120", {"start": v(77.22, -41.2) * mm, "end": v(77.2, -41.17) * mm});
            skLineSegment(sketch, "E12121", {"start": v(77.2, -41.17) * mm, "end": v(77.13, -41.07) * mm});
            skLineSegment(sketch, "E12122", {"start": v(77.13, -41.07) * mm, "end": v(77.04, -40.9) * mm});
            skLineSegment(sketch, "E12123", {"start": v(77.04, -40.9) * mm, "end": v(76.92, -40.65) * mm});
            skLineSegment(sketch, "E12124", {"start": v(76.92, -40.65) * mm, "end": v(76.78, -40.32) * mm});
            skLineSegment(sketch, "E12125", {"start": v(76.78, -40.32) * mm, "end": v(76.62, -39.92) * mm});
            skLineSegment(sketch, "E12126", {"start": v(76.62, -39.92) * mm, "end": v(76.47, -39.43) * mm});
            skLineSegment(sketch, "E12127", {"start": v(76.47, -39.43) * mm, "end": v(76.32, -38.86) * mm});
            skLineSegment(sketch, "E12128", {"start": v(76.32, -38.86) * mm, "end": v(76.18, -38.2) * mm});
            skLineSegment(sketch, "E12129", {"start": v(76.18, -38.2) * mm, "end": v(76.1, -37.66) * mm});
            skArc(sketch, "E12130", {"start": v(76.1, -37.66) * mm, "mid": v(77.04, -37.04) * mm, "end": v(78, -36.46) * mm});
            skLineSegment(sketch, "E12131", {"start": v(78, -36.46) * mm, "end": v(78.45, -36.77) * mm});
            skLineSegment(sketch, "E12132", {"start": v(78.45, -36.77) * mm, "end": v(78.98, -37.17) * mm});
            skLineSegment(sketch, "E12133", {"start": v(78.98, -37.17) * mm, "end": v(79.43, -37.55) * mm});
            skLineSegment(sketch, "E12134", {"start": v(79.43, -37.55) * mm, "end": v(79.8, -37.9) * mm});
            skLineSegment(sketch, "E12135", {"start": v(79.8, -37.9) * mm, "end": v(80.11, -38.2) * mm});
            skLineSegment(sketch, "E12136", {"start": v(80.11, -38.2) * mm, "end": v(80.35, -38.47) * mm});
            skLineSegment(sketch, "E12137", {"start": v(80.35, -38.47) * mm, "end": v(80.52, -38.68) * mm});
            skLineSegment(sketch, "E12138", {"start": v(80.52, -38.68) * mm, "end": v(80.64, -38.84) * mm});
            skLineSegment(sketch, "E12139", {"start": v(80.64, -38.84) * mm, "end": v(80.7, -38.94) * mm});
            skLineSegment(sketch, "E12140", {"start": v(80.7, -38.94) * mm, "end": v(80.72, -38.97) * mm});
            skLineSegment(sketch, "E12141", {"start": v(80.72, -38.97) * mm, "end": v(81.6, -40.6) * mm});
            skArc(sketch, "E12142", {"start": v(81.6, -40.6) * mm, "mid": v(83.05, -39.86) * mm, "end": v(84.54, -39.2) * mm});
            skLineSegment(sketch, "E12143", {"start": v(84.54, -39.2) * mm, "end": v(83.83, -37.49) * mm});
            skLineSegment(sketch, "E12144", {"start": v(83.83, -37.49) * mm, "end": v(83.82, -37.45) * mm});
            skLineSegment(sketch, "E12145", {"start": v(83.82, -37.45) * mm, "end": v(83.78, -37.34) * mm});
            skLineSegment(sketch, "E12146", {"start": v(83.78, -37.34) * mm, "end": v(83.73, -37.15) * mm});
            skLineSegment(sketch, "E12147", {"start": v(83.73, -37.15) * mm, "end": v(83.67, -36.88) * mm});
            skLineSegment(sketch, "E12148", {"start": v(83.67, -36.88) * mm, "end": v(83.61, -36.53) * mm});
            skLineSegment(sketch, "E12149", {"start": v(83.61, -36.53) * mm, "end": v(83.56, -36.1) * mm});
            skLineSegment(sketch, "E12150", {"start": v(83.56, -36.1) * mm, "end": v(83.53, -35.6) * mm});
            skLineSegment(sketch, "E12151", {"start": v(83.53, -35.6) * mm, "end": v(83.52, -35) * mm});
            skLineSegment(sketch, "E12152", {"start": v(83.52, -35) * mm, "end": v(83.55, -34.33) * mm});
            skLineSegment(sketch, "E12153", {"start": v(83.55, -34.33) * mm, "end": v(83.6, -33.79) * mm});
            skArc(sketch, "E12154", {"start": v(83.6, -33.79) * mm, "mid": v(84.65, -33.41) * mm, "end": v(85.72, -33.07) * mm});
            skLineSegment(sketch, "E12155", {"start": v(85.72, -33.07) * mm, "end": v(86.09, -33.48) * mm});
            skLineSegment(sketch, "E12156", {"start": v(86.09, -33.48) * mm, "end": v(86.5, -34) * mm});
            skLineSegment(sketch, "E12157", {"start": v(86.5, -34) * mm, "end": v(86.86, -34.47) * mm});
            skLineSegment(sketch, "E12158", {"start": v(86.86, -34.47) * mm, "end": v(87.14, -34.9) * mm});
            skLineSegment(sketch, "E12159", {"start": v(87.14, -34.9) * mm, "end": v(87.36, -35.27) * mm});
            skLineSegment(sketch, "E12160", {"start": v(87.36, -35.27) * mm, "end": v(87.53, -35.58) * mm});
            skLineSegment(sketch, "E12161", {"start": v(87.53, -35.58) * mm, "end": v(87.64, -35.83) * mm});
            skLineSegment(sketch, "E12162", {"start": v(87.64, -35.83) * mm, "end": v(87.72, -36.02) * mm});
            skLineSegment(sketch, "E12163", {"start": v(87.72, -36.02) * mm, "end": v(87.75, -36.13) * mm});
            skLineSegment(sketch, "E12164", {"start": v(87.75, -36.13) * mm, "end": v(87.77, -36.17) * mm});
            skLineSegment(sketch, "E12165", {"start": v(87.77, -36.17) * mm, "end": v(88.24, -37.96) * mm});
            skArc(sketch, "E12166", {"start": v(88.24, -37.96) * mm, "mid": v(89.82, -37.59) * mm, "end": v(91.42, -37.3) * mm});
            skLineSegment(sketch, "E12167", {"start": v(91.42, -37.3) * mm, "end": v(91.14, -35.47) * mm});
            skLineSegment(sketch, "E12168", {"start": v(91.14, -35.47) * mm, "end": v(91.14, -35.43) * mm});
            skLineSegment(sketch, "E12169", {"start": v(91.14, -35.43) * mm, "end": v(91.13, -35.31) * mm});
            skLineSegment(sketch, "E12170", {"start": v(91.13, -35.31) * mm, "end": v(91.13, -35.12) * mm});
            skLineSegment(sketch, "E12171", {"start": v(91.13, -35.12) * mm, "end": v(91.13, -34.84) * mm});
            skLineSegment(sketch, "E12172", {"start": v(91.13, -34.84) * mm, "end": v(91.16, -34.49) * mm});
            skLineSegment(sketch, "E12173", {"start": v(91.16, -34.49) * mm, "end": v(91.22, -34.06) * mm});
            skLineSegment(sketch, "E12174", {"start": v(91.22, -34.06) * mm, "end": v(91.3, -33.55) * mm});
            skLineSegment(sketch, "E12175", {"start": v(91.3, -33.55) * mm, "end": v(91.44, -32.98) * mm});
            skLineSegment(sketch, "E12176", {"start": v(91.44, -32.98) * mm, "end": v(91.62, -32.34) * mm});
            skLineSegment(sketch, "E12177", {"start": v(91.62, -32.34) * mm, "end": v(91.8, -31.82) * mm});
            skArc(sketch, "E12178", {"start": v(91.8, -31.82) * mm, "mid": v(92.91, -31.7) * mm, "end": v(94.03, -31.63) * mm});
            skLineSegment(sketch, "E12179", {"start": v(94.03, -31.63) * mm, "end": v(94.3, -32.12) * mm});
            skLineSegment(sketch, "E12180", {"start": v(94.3, -32.12) * mm, "end": v(94.58, -32.72) * mm});
            skLineSegment(sketch, "E12181", {"start": v(94.58, -32.72) * mm, "end": v(94.8, -33.26) * mm});
            skLineSegment(sketch, "E12182", {"start": v(94.8, -33.26) * mm, "end": v(94.98, -33.75) * mm});
            skLineSegment(sketch, "E12183", {"start": v(94.98, -33.75) * mm, "end": v(95.1, -34.16) * mm});
            skLineSegment(sketch, "E12184", {"start": v(95.1, -34.16) * mm, "end": v(95.19, -34.5) * mm});
            skLineSegment(sketch, "E12185", {"start": v(95.19, -34.5) * mm, "end": v(95.24, -34.77) * mm});
            skLineSegment(sketch, "E12186", {"start": v(95.24, -34.77) * mm, "end": v(95.27, -34.97) * mm});
            skLineSegment(sketch, "E12187", {"start": v(95.27, -34.97) * mm, "end": v(95.28, -35.09) * mm});
            skLineSegment(sketch, "E12188", {"start": v(95.28, -35.09) * mm, "end": v(95.28, -35.13) * mm});
            skLineSegment(sketch, "E12189", {"start": v(95.28, -35.13) * mm, "end": v(95.31, -36.98) * mm});
            skArc(sketch, "E12190", {"start": v(95.31, -36.98) * mm, "mid": v(96.93, -37) * mm, "end": v(98.55, -37.1) * mm});
            skLineSegment(sketch, "E12191", {"start": v(98.55, -37.1) * mm, "end": v(98.73, -35.26) * mm});
            skLineSegment(sketch, "E12192", {"start": v(98.73, -35.26) * mm, "end": v(98.73, -35.22) * mm});
            skLineSegment(sketch, "E12193", {"start": v(98.73, -35.22) * mm, "end": v(98.75, -35.1) * mm});
            skLineSegment(sketch, "E12194", {"start": v(98.75, -35.1) * mm, "end": v(98.8, -34.91) * mm});
            skLineSegment(sketch, "E12195", {"start": v(98.8, -34.91) * mm, "end": v(98.87, -34.64) * mm});
            skLineSegment(sketch, "E12196", {"start": v(98.87, -34.64) * mm, "end": v(98.98, -34.3) * mm});
            skLineSegment(sketch, "E12197", {"start": v(98.98, -34.3) * mm, "end": v(99.13, -33.9) * mm});
            skLineSegment(sketch, "E12198", {"start": v(99.13, -33.9) * mm, "end": v(99.34, -33.44) * mm});
            skLineSegment(sketch, "E12199", {"start": v(99.34, -33.44) * mm, "end": v(99.6, -32.91) * mm});
            skLineSegment(sketch, "E12200", {"start": v(99.6, -32.91) * mm, "end": v(99.94, -32.33) * mm});
            skLineSegment(sketch, "E12201", {"start": v(99.94, -32.33) * mm, "end": v(100.24, -31.87) * mm});
            skArc(sketch, "E12202", {"start": v(100.24, -31.87) * mm, "mid": v(101.35, -32.03) * mm, "end": v(102.45, -32.22) * mm});
            skLineSegment(sketch, "E12203", {"start": v(102.45, -32.22) * mm, "end": v(102.59, -32.76) * mm});
            skLineSegment(sketch, "E12204", {"start": v(102.59, -32.76) * mm, "end": v(102.72, -33.41) * mm});
            skLineSegment(sketch, "E12205", {"start": v(102.72, -33.41) * mm, "end": v(102.8, -34) * mm});
            skLineSegment(sketch, "E12206", {"start": v(102.8, -34) * mm, "end": v(102.86, -34.5) * mm});
            skLineSegment(sketch, "E12207", {"start": v(102.86, -34.5) * mm, "end": v(102.88, -34.93) * mm});
            skLineSegment(sketch, "E12208", {"start": v(102.88, -34.93) * mm, "end": v(102.88, -35.29) * mm});
            skLineSegment(sketch, "E12209", {"start": v(102.88, -35.29) * mm, "end": v(102.87, -35.56) * mm});
            skLineSegment(sketch, "E12210", {"start": v(102.87, -35.56) * mm, "end": v(102.85, -35.76) * mm});
            skLineSegment(sketch, "E12211", {"start": v(102.85, -35.76) * mm, "end": v(102.83, -35.88) * mm});
            skLineSegment(sketch, "E12212", {"start": v(102.83, -35.88) * mm, "end": v(102.82, -35.91) * mm});
            skLineSegment(sketch, "E12213", {"start": v(102.82, -35.91) * mm, "end": v(102.4, -37.73) * mm});
            skArc(sketch, "E12214", {"start": v(102.4, -37.73) * mm, "mid": v(103.98, -38.13) * mm, "end": v(105.53, -38.62) * mm});
            skLineSegment(sketch, "E12215", {"start": v(105.53, -38.62) * mm, "end": v(106.14, -36.87) * mm});
            skLineSegment(sketch, "E12216", {"start": v(106.14, -36.87) * mm, "end": v(106.15, -36.83) * mm});
            skLineSegment(sketch, "E12217", {"start": v(106.15, -36.83) * mm, "end": v(106.2, -36.72) * mm});
            skLineSegment(sketch, "E12218", {"start": v(106.2, -36.72) * mm, "end": v(106.29, -36.55) * mm});
            skLineSegment(sketch, "E12219", {"start": v(106.29, -36.55) * mm, "end": v(106.42, -36.3) * mm});
            skLineSegment(sketch, "E12220", {"start": v(106.42, -36.3) * mm, "end": v(106.6, -36) * mm});
            skLineSegment(sketch, "E12221", {"start": v(106.6, -36) * mm, "end": v(106.86, -35.65) * mm});
            skLineSegment(sketch, "E12222", {"start": v(106.86, -35.65) * mm, "end": v(107.17, -35.25) * mm});
            skLineSegment(sketch, "E12223", {"start": v(107.17, -35.25) * mm, "end": v(107.56, -34.8) * mm});
            skLineSegment(sketch, "E12224", {"start": v(107.56, -34.8) * mm, "end": v(108.02, -34.32) * mm});
            skLineSegment(sketch, "E12225", {"start": v(108.02, -34.32) * mm, "end": v(108.41, -33.94) * mm});
            skArc(sketch, "E12226", {"start": v(108.41, -33.94) * mm, "mid": v(109.45, -34.36) * mm, "end": v(110.48, -34.81) * mm});
            skLineSegment(sketch, "E12227", {"start": v(110.48, -34.81) * mm, "end": v(110.49, -35.36) * mm});
            skLineSegment(sketch, "E12228", {"start": v(110.49, -35.36) * mm, "end": v(110.46, -36.03) * mm});
            skLineSegment(sketch, "E12229", {"start": v(110.46, -36.03) * mm, "end": v(110.4, -36.62) * mm});
            skLineSegment(sketch, "E12230", {"start": v(110.4, -36.62) * mm, "end": v(110.33, -37.12) * mm});
            skLineSegment(sketch, "E12231", {"start": v(110.33, -37.12) * mm, "end": v(110.25, -37.55) * mm});
            skLineSegment(sketch, "E12232", {"start": v(110.25, -37.55) * mm, "end": v(110.17, -37.9) * mm});
            skLineSegment(sketch, "E12233", {"start": v(110.17, -37.9) * mm, "end": v(110.09, -38.16) * mm});
            skLineSegment(sketch, "E12234", {"start": v(110.09, -38.16) * mm, "end": v(110.02, -38.34) * mm});
            skLineSegment(sketch, "E12235", {"start": v(110.02, -38.34) * mm, "end": v(109.98, -38.45) * mm});
            skLineSegment(sketch, "E12236", {"start": v(109.98, -38.45) * mm, "end": v(109.96, -38.49) * mm});
            skLineSegment(sketch, "E12237", {"start": v(109.96, -38.49) * mm, "end": v(109.12, -40.14) * mm});
            skArc(sketch, "E12238", {"start": v(109.12, -40.14) * mm, "mid": v(110.55, -40.91) * mm, "end": v(111.94, -41.76) * mm});
            skLineSegment(sketch, "E12239", {"start": v(111.94, -41.76) * mm, "end": v(112.95, -40.2) * mm});
            skLineSegment(sketch, "E12240", {"start": v(112.95, -40.2) * mm, "end": v(112.97, -40.17) * mm});
            skLineSegment(sketch, "E12241", {"start": v(112.97, -40.17) * mm, "end": v(113.04, -40.08) * mm});
            skLineSegment(sketch, "E12242", {"start": v(113.04, -40.08) * mm, "end": v(113.17, -39.93) * mm});
            skLineSegment(sketch, "E12243", {"start": v(113.17, -39.93) * mm, "end": v(113.36, -39.73) * mm});
            skLineSegment(sketch, "E12244", {"start": v(113.36, -39.73) * mm, "end": v(113.61, -39.48) * mm});
            skLineSegment(sketch, "E12245", {"start": v(113.61, -39.48) * mm, "end": v(113.94, -39.2) * mm});
            skLineSegment(sketch, "E12246", {"start": v(113.94, -39.2) * mm, "end": v(114.34, -38.88) * mm});
            skLineSegment(sketch, "E12247", {"start": v(114.34, -38.88) * mm, "end": v(114.82, -38.54) * mm});
            skLineSegment(sketch, "E12248", {"start": v(114.82, -38.54) * mm, "end": v(115.38, -38.18) * mm});
            skLineSegment(sketch, "E12249", {"start": v(115.38, -38.18) * mm, "end": v(115.86, -37.9) * mm});
            skArc(sketch, "E12250", {"start": v(115.86, -37.9) * mm, "mid": v(116.77, -38.56) * mm, "end": v(117.66, -39.25) * mm});
            skLineSegment(sketch, "E12251", {"start": v(117.66, -39.25) * mm, "end": v(117.53, -39.78) * mm});
            skLineSegment(sketch, "E12252", {"start": v(117.53, -39.78) * mm, "end": v(117.34, -40.42) * mm});
            skLineSegment(sketch, "E12253", {"start": v(117.34, -40.42) * mm, "end": v(117.15, -40.98) * mm});
            skLineSegment(sketch, "E12254", {"start": v(117.15, -40.98) * mm, "end": v(116.96, -41.46) * mm});
            skLineSegment(sketch, "E12255", {"start": v(116.96, -41.46) * mm, "end": v(116.78, -41.85) * mm});
            skLineSegment(sketch, "E12256", {"start": v(116.78, -41.85) * mm, "end": v(116.62, -42.16) * mm});
            skLineSegment(sketch, "E12257", {"start": v(116.62, -42.16) * mm, "end": v(116.48, -42.4) * mm});
            skLineSegment(sketch, "E12258", {"start": v(116.48, -42.4) * mm, "end": v(116.37, -42.56) * mm});
            skLineSegment(sketch, "E12259", {"start": v(116.37, -42.56) * mm, "end": v(116.3, -42.66) * mm});
            skLineSegment(sketch, "E12260", {"start": v(116.3, -42.66) * mm, "end": v(116.27, -42.7) * mm});
            skLineSegment(sketch, "E12261", {"start": v(116.27, -42.7) * mm, "end": v(115.07, -44.1) * mm});
            skArc(sketch, "E12262", {"start": v(115.07, -44.1) * mm, "mid": v(116.27, -45.2) * mm, "end": v(117.41, -46.34) * mm});
            skLineSegment(sketch, "E12263", {"start": v(15.4, 102.15) * mm, "end": v(16.8, 103.48) * mm});
            skLineSegment(sketch, "E12264", {"start": v(16.8, 103.48) * mm, "end": v(16.83, 103.5) * mm});
            skLineSegment(sketch, "E12265", {"start": v(16.83, 103.5) * mm, "end": v(16.9, 103.58) * mm});
            skLineSegment(sketch, "E12266", {"start": v(16.9, 103.58) * mm, "end": v(17.06, 103.68) * mm});
            skLineSegment(sketch, "E12267", {"start": v(17.06, 103.68) * mm, "end": v(17.27, 103.83) * mm});
            skLineSegment(sketch, "E12268", {"start": v(17.27, 103.83) * mm, "end": v(17.55, 104) * mm});
            skLineSegment(sketch, "E12269", {"start": v(17.55, 104) * mm, "end": v(17.9, 104.18) * mm});
            skLineSegment(sketch, "E12270", {"start": v(17.9, 104.18) * mm, "end": v(18.33, 104.38) * mm});
            skLineSegment(sketch, "E12271", {"start": v(18.33, 104.38) * mm, "end": v(18.83, 104.58) * mm});
            skLineSegment(sketch, "E12272", {"start": v(18.83, 104.58) * mm, "end": v(19.41, 104.79) * mm});
            skLineSegment(sketch, "E12273", {"start": v(19.41, 104.79) * mm, "end": v(20.08, 104.98) * mm});
            skLineSegment(sketch, "E12274", {"start": v(20.08, 104.98) * mm, "end": v(20.1, 105) * mm});
            skArc(sketch, "E12275", {"start": v(20.1, 105) * mm, "mid": v(20.83, 104.15) * mm, "end": v(21.53, 103.28) * mm});
            skLineSegment(sketch, "E12276", {"start": v(21.53, 103.28) * mm, "end": v(21.51, 103.25) * mm});
            skLineSegment(sketch, "E12277", {"start": v(21.51, 103.25) * mm, "end": v(21.2, 102.64) * mm});
            skLineSegment(sketch, "E12278", {"start": v(21.2, 102.64) * mm, "end": v(20.89, 102.1) * mm});
            skLineSegment(sketch, "E12279", {"start": v(20.89, 102.1) * mm, "end": v(20.6, 101.65) * mm});
            skLineSegment(sketch, "E12280", {"start": v(20.6, 101.65) * mm, "end": v(20.32, 101.26) * mm});
            skLineSegment(sketch, "E12281", {"start": v(20.32, 101.26) * mm, "end": v(20.07, 100.95) * mm});
            skLineSegment(sketch, "E12282", {"start": v(20.07, 100.95) * mm, "end": v(19.85, 100.7) * mm});
            skLineSegment(sketch, "E12283", {"start": v(19.85, 100.7) * mm, "end": v(19.67, 100.52) * mm});
            skLineSegment(sketch, "E12284", {"start": v(19.67, 100.52) * mm, "end": v(19.54, 100.4) * mm});
            skLineSegment(sketch, "E12285", {"start": v(19.54, 100.4) * mm, "end": v(19.46, 100.33) * mm});
            skLineSegment(sketch, "E12286", {"start": v(19.46, 100.33) * mm, "end": v(19.43, 100.3) * mm});
            skLineSegment(sketch, "E12287", {"start": v(19.43, 100.3) * mm, "end": v(17.85, 99.18) * mm});
            skArc(sketch, "E12288", {"start": v(17.85, 99.18) * mm, "mid": v(18.76, 97.83) * mm, "end": v(19.58, 96.44) * mm});
            skLineSegment(sketch, "E12289", {"start": v(19.58, 96.44) * mm, "end": v(21.28, 97.37) * mm});
            skLineSegment(sketch, "E12290", {"start": v(21.28, 97.37) * mm, "end": v(21.3, 97.38) * mm});
            skLineSegment(sketch, "E12291", {"start": v(21.3, 97.38) * mm, "end": v(21.4, 97.43) * mm});
            skLineSegment(sketch, "E12292", {"start": v(21.4, 97.43) * mm, "end": v(21.58, 97.5) * mm});
            skLineSegment(sketch, "E12293", {"start": v(21.58, 97.5) * mm, "end": v(21.82, 97.57) * mm});
            skLineSegment(sketch, "E12294", {"start": v(21.82, 97.57) * mm, "end": v(22.13, 97.66) * mm});
            skLineSegment(sketch, "E12295", {"start": v(22.13, 97.66) * mm, "end": v(22.52, 97.75) * mm});
            skLineSegment(sketch, "E12296", {"start": v(22.52, 97.75) * mm, "end": v(22.99, 97.84) * mm});
            skLineSegment(sketch, "E12297", {"start": v(22.99, 97.84) * mm, "end": v(23.53, 97.9) * mm});
            skLineSegment(sketch, "E12298", {"start": v(23.53, 97.9) * mm, "end": v(24.14, 97.95) * mm});
            skLineSegment(sketch, "E12299", {"start": v(24.14, 97.95) * mm, "end": v(24.83, 97.97) * mm});
            skLineSegment(sketch, "E12300", {"start": v(24.83, 97.97) * mm, "end": v(24.86, 97.97) * mm});
            skArc(sketch, "E12301", {"start": v(24.86, 97.97) * mm, "mid": v(25.34, 96.96) * mm, "end": v(25.8, 95.94) * mm});
            skLineSegment(sketch, "E12302", {"start": v(25.8, 95.94) * mm, "end": v(25.77, 95.92) * mm});
            skLineSegment(sketch, "E12303", {"start": v(25.77, 95.92) * mm, "end": v(25.3, 95.4) * mm});
            skLineSegment(sketch, "E12304", {"start": v(25.3, 95.4) * mm, "end": v(24.87, 94.97) * mm});
            skLineSegment(sketch, "E12305", {"start": v(24.87, 94.97) * mm, "end": v(24.47, 94.6) * mm});
            skLineSegment(sketch, "E12306", {"start": v(24.47, 94.6) * mm, "end": v(24.1, 94.3) * mm});
            skLineSegment(sketch, "E12307", {"start": v(24.1, 94.3) * mm, "end": v(23.78, 94.07) * mm});
            skLineSegment(sketch, "E12308", {"start": v(23.78, 94.07) * mm, "end": v(23.5, 93.9) * mm});
            skLineSegment(sketch, "E12309", {"start": v(23.5, 93.9) * mm, "end": v(23.29, 93.76) * mm});
            skLineSegment(sketch, "E12310", {"start": v(23.29, 93.76) * mm, "end": v(23.13, 93.68) * mm});
            skLineSegment(sketch, "E12311", {"start": v(23.13, 93.68) * mm, "end": v(23.03, 93.63) * mm});
            skLineSegment(sketch, "E12312", {"start": v(23.03, 93.63) * mm, "end": v(23, 93.62) * mm});
            skLineSegment(sketch, "E12313", {"start": v(23, 93.62) * mm, "end": v(21.18, 92.94) * mm});
            skArc(sketch, "E12314", {"start": v(21.18, 92.94) * mm, "mid": v(21.7, 91.4) * mm, "end": v(22.14, 89.84) * mm});
            skLineSegment(sketch, "E12315", {"start": v(22.14, 89.84) * mm, "end": v(24.02, 90.3) * mm});
            skLineSegment(sketch, "E12316", {"start": v(24.02, 90.3) * mm, "end": v(24.06, 90.3) * mm});
            skLineSegment(sketch, "E12317", {"start": v(24.06, 90.3) * mm, "end": v(24.16, 90.32) * mm});
            skLineSegment(sketch, "E12318", {"start": v(24.16, 90.32) * mm, "end": v(24.34, 90.34) * mm});
            skLineSegment(sketch, "E12319", {"start": v(24.34, 90.34) * mm, "end": v(24.6, 90.36) * mm});
            skLineSegment(sketch, "E12320", {"start": v(24.6, 90.36) * mm, "end": v(24.92, 90.36) * mm});
            skLineSegment(sketch, "E12321", {"start": v(24.92, 90.36) * mm, "end": v(25.32, 90.35) * mm});
            skLineSegment(sketch, "E12322", {"start": v(25.32, 90.35) * mm, "end": v(25.8, 90.3) * mm});
            skLineSegment(sketch, "E12323", {"start": v(25.8, 90.3) * mm, "end": v(26.33, 90.23) * mm});
            skLineSegment(sketch, "E12324", {"start": v(26.33, 90.23) * mm, "end": v(26.94, 90.12) * mm});
            skLineSegment(sketch, "E12325", {"start": v(26.94, 90.12) * mm, "end": v(27.6, 89.96) * mm});
            skLineSegment(sketch, "E12326", {"start": v(27.6, 89.96) * mm, "end": v(27.64, 89.95) * mm});
            skArc(sketch, "E12327", {"start": v(27.64, 89.95) * mm, "mid": v(27.84, 88.86) * mm, "end": v(28.01, 87.76) * mm});
            skLineSegment(sketch, "E12328", {"start": v(28.01, 87.76) * mm, "end": v(27.99, 87.74) * mm});
            skLineSegment(sketch, "E12329", {"start": v(27.99, 87.74) * mm, "end": v(27.4, 87.36) * mm});
            skLineSegment(sketch, "E12330", {"start": v(27.4, 87.36) * mm, "end": v(26.87, 87.06) * mm});
            skLineSegment(sketch, "E12331", {"start": v(26.87, 87.06) * mm, "end": v(26.39, 86.8) * mm});
            skLineSegment(sketch, "E12332", {"start": v(26.39, 86.8) * mm, "end": v(25.96, 86.61) * mm});
            skLineSegment(sketch, "E12333", {"start": v(25.96, 86.61) * mm, "end": v(25.59, 86.47) * mm});
            skLineSegment(sketch, "E12334", {"start": v(25.59, 86.47) * mm, "end": v(25.28, 86.37) * mm});
            skLineSegment(sketch, "E12335", {"start": v(25.28, 86.37) * mm, "end": v(25.03, 86.3) * mm});
            skLineSegment(sketch, "E12336", {"start": v(25.03, 86.3) * mm, "end": v(24.85, 86.26) * mm});
            skLineSegment(sketch, "E12337", {"start": v(24.85, 86.26) * mm, "end": v(24.75, 86.24) * mm});
            skLineSegment(sketch, "E12338", {"start": v(24.75, 86.24) * mm, "end": v(24.71, 86.23) * mm});
            skLineSegment(sketch, "E12339", {"start": v(24.71, 86.23) * mm, "end": v(22.78, 86.04) * mm});
            skArc(sketch, "E12340", {"start": v(22.78, 86.04) * mm, "mid": v(22.9, 84.43) * mm, "end": v(22.9, 82.8) * mm});
            skLineSegment(sketch, "E12341", {"start": v(22.9, 82.8) * mm, "end": v(24.84, 82.76) * mm});
            skLineSegment(sketch, "E12342", {"start": v(24.84, 82.76) * mm, "end": v(24.88, 82.76) * mm});
            skLineSegment(sketch, "E12343", {"start": v(24.88, 82.76) * mm, "end": v(24.99, 82.75) * mm});
            skLineSegment(sketch, "E12344", {"start": v(24.99, 82.75) * mm, "end": v(25.16, 82.72) * mm});
            skLineSegment(sketch, "E12345", {"start": v(25.16, 82.72) * mm, "end": v(25.41, 82.67) * mm});
            skLineSegment(sketch, "E12346", {"start": v(25.41, 82.67) * mm, "end": v(25.73, 82.59) * mm});
            skLineSegment(sketch, "E12347", {"start": v(25.73, 82.59) * mm, "end": v(26.11, 82.47) * mm});
            skLineSegment(sketch, "E12348", {"start": v(26.11, 82.47) * mm, "end": v(26.56, 82.31) * mm});
            skLineSegment(sketch, "E12349", {"start": v(26.56, 82.31) * mm, "end": v(27.06, 82.1) * mm});
            skLineSegment(sketch, "E12350", {"start": v(27.06, 82.1) * mm, "end": v(27.61, 81.83) * mm});
            skLineSegment(sketch, "E12351", {"start": v(27.61, 81.83) * mm, "end": v(28.22, 81.5) * mm});
            skLineSegment(sketch, "E12352", {"start": v(28.22, 81.5) * mm, "end": v(28.25, 81.49) * mm});
            skArc(sketch, "E12353", {"start": v(28.25, 81.49) * mm, "mid": v(28.16, 80.38) * mm, "end": v(28.04, 79.27) * mm});
            skLineSegment(sketch, "E12354", {"start": v(28.04, 79.27) * mm, "end": v(28, 79.26) * mm});
            skLineSegment(sketch, "E12355", {"start": v(28, 79.26) * mm, "end": v(27.35, 79.05) * mm});
            skLineSegment(sketch, "E12356", {"start": v(27.35, 79.05) * mm, "end": v(26.76, 78.9) * mm});
            skLineSegment(sketch, "E12357", {"start": v(26.76, 78.9) * mm, "end": v(26.22, 78.78) * mm});
            skLineSegment(sketch, "E12358", {"start": v(26.22, 78.78) * mm, "end": v(25.76, 78.7) * mm});
            skLineSegment(sketch, "E12359", {"start": v(25.76, 78.7) * mm, "end": v(25.36, 78.66) * mm});
            skLineSegment(sketch, "E12360", {"start": v(25.36, 78.66) * mm, "end": v(25.04, 78.64) * mm});
            skLineSegment(sketch, "E12361", {"start": v(25.04, 78.64) * mm, "end": v(24.78, 78.63) * mm});
            skLineSegment(sketch, "E12362", {"start": v(24.78, 78.63) * mm, "end": v(24.6, 78.64) * mm});
            skLineSegment(sketch, "E12363", {"start": v(24.6, 78.64) * mm, "end": v(24.5, 78.65) * mm});
            skLineSegment(sketch, "E12364", {"start": v(24.5, 78.65) * mm, "end": v(24.46, 78.65) * mm});
            skLineSegment(sketch, "E12365", {"start": v(24.46, 78.65) * mm, "end": v(22.54, 78.97) * mm});
            skArc(sketch, "E12366", {"start": v(22.54, 78.97) * mm, "mid": v(22.23, 77.38) * mm, "end": v(21.82, 75.81) * mm});
            skLineSegment(sketch, "E12367", {"start": v(21.82, 75.81) * mm, "end": v(23.68, 75.27) * mm});
            skLineSegment(sketch, "E12368", {"start": v(23.68, 75.27) * mm, "end": v(23.72, 75.26) * mm});
            skLineSegment(sketch, "E12369", {"start": v(23.72, 75.26) * mm, "end": v(23.82, 75.22) * mm});
            skLineSegment(sketch, "E12370", {"start": v(23.82, 75.22) * mm, "end": v(23.98, 75.14) * mm});
            skLineSegment(sketch, "E12371", {"start": v(23.98, 75.14) * mm, "end": v(24.21, 75.03) * mm});
            skLineSegment(sketch, "E12372", {"start": v(24.21, 75.03) * mm, "end": v(24.5, 74.87) * mm});
            skLineSegment(sketch, "E12373", {"start": v(24.5, 74.87) * mm, "end": v(24.84, 74.66) * mm});
            skLineSegment(sketch, "E12374", {"start": v(24.84, 74.66) * mm, "end": v(25.22, 74.39) * mm});
            skLineSegment(sketch, "E12375", {"start": v(25.22, 74.39) * mm, "end": v(25.65, 74.06) * mm});
            skLineSegment(sketch, "E12376", {"start": v(25.65, 74.06) * mm, "end": v(26.12, 73.65) * mm});
            skLineSegment(sketch, "E12377", {"start": v(26.12, 73.65) * mm, "end": v(26.62, 73.18) * mm});
            skLineSegment(sketch, "E12378", {"start": v(26.62, 73.18) * mm, "end": v(26.64, 73.16) * mm});
            skArc(sketch, "E12379", {"start": v(26.64, 73.16) * mm, "mid": v(26.27, 72.1) * mm, "end": v(25.87, 71.07) * mm});
            skLineSegment(sketch, "E12380", {"start": v(25.87, 71.07) * mm, "end": v(25.84, 71.07) * mm});
            skLineSegment(sketch, "E12381", {"start": v(25.84, 71.07) * mm, "end": v(25.15, 71.03) * mm});
            skLineSegment(sketch, "E12382", {"start": v(25.15, 71.03) * mm, "end": v(24.53, 71.03) * mm});
            skLineSegment(sketch, "E12383", {"start": v(24.53, 71.03) * mm, "end": v(23.99, 71.06) * mm});
            skLineSegment(sketch, "E12384", {"start": v(23.99, 71.06) * mm, "end": v(23.52, 71.1) * mm});
            skLineSegment(sketch, "E12385", {"start": v(23.52, 71.1) * mm, "end": v(23.12, 71.17) * mm});
            skLineSegment(sketch, "E12386", {"start": v(23.12, 71.17) * mm, "end": v(22.8, 71.23) * mm});
            skLineSegment(sketch, "E12387", {"start": v(22.8, 71.23) * mm, "end": v(22.56, 71.3) * mm});
            skLineSegment(sketch, "E12388", {"start": v(22.56, 71.3) * mm, "end": v(22.38, 71.35) * mm});
            skLineSegment(sketch, "E12389", {"start": v(22.38, 71.35) * mm, "end": v(22.28, 71.39) * mm});
            skLineSegment(sketch, "E12390", {"start": v(22.28, 71.39) * mm, "end": v(22.25, 71.4) * mm});
            skLineSegment(sketch, "E12391", {"start": v(22.25, 71.4) * mm, "end": v(20.48, 72.2) * mm});
            skArc(sketch, "E12392", {"start": v(20.48, 72.2) * mm, "mid": v(19.77, 70.75) * mm, "end": v(18.97, 69.33) * mm});
            skLineSegment(sketch, "E12393", {"start": v(18.97, 69.33) * mm, "end": v(20.62, 68.33) * mm});
            skLineSegment(sketch, "E12394", {"start": v(20.62, 68.33) * mm, "end": v(20.65, 68.3) * mm});
            skLineSegment(sketch, "E12395", {"start": v(20.65, 68.3) * mm, "end": v(20.74, 68.25) * mm});
            skLineSegment(sketch, "E12396", {"start": v(20.74, 68.25) * mm, "end": v(20.88, 68.13) * mm});
            skLineSegment(sketch, "E12397", {"start": v(20.88, 68.13) * mm, "end": v(21.07, 67.96) * mm});
            skLineSegment(sketch, "E12398", {"start": v(21.07, 67.96) * mm, "end": v(21.3, 67.74) * mm});
            skLineSegment(sketch, "E12399", {"start": v(21.3, 67.74) * mm, "end": v(21.58, 67.44) * mm});
            skLineSegment(sketch, "E12400", {"start": v(21.58, 67.44) * mm, "end": v(21.88, 67.08) * mm});
            skLineSegment(sketch, "E12401", {"start": v(21.88, 67.08) * mm, "end": v(22.21, 66.65) * mm});
            skLineSegment(sketch, "E12402", {"start": v(22.21, 66.65) * mm, "end": v(22.56, 66.14) * mm});
            skLineSegment(sketch, "E12403", {"start": v(22.56, 66.14) * mm, "end": v(22.92, 65.55) * mm});
            skLineSegment(sketch, "E12404", {"start": v(22.92, 65.55) * mm, "end": v(22.94, 65.52) * mm});
            skArc(sketch, "E12405", {"start": v(22.94, 65.52) * mm, "mid": v(22.3, 64.6) * mm, "end": v(21.65, 63.7) * mm});
            skLineSegment(sketch, "E12406", {"start": v(21.65, 63.7) * mm, "end": v(21.62, 63.71) * mm});
            skLineSegment(sketch, "E12407", {"start": v(21.62, 63.71) * mm, "end": v(20.94, 63.86) * mm});
            skLineSegment(sketch, "E12408", {"start": v(20.94, 63.86) * mm, "end": v(20.35, 64.02) * mm});
            skLineSegment(sketch, "E12409", {"start": v(20.35, 64.02) * mm, "end": v(19.83, 64.19) * mm});
            skLineSegment(sketch, "E12410", {"start": v(19.83, 64.19) * mm, "end": v(19.39, 64.35) * mm});
            skLineSegment(sketch, "E12411", {"start": v(19.39, 64.35) * mm, "end": v(19.02, 64.51) * mm});
            skLineSegment(sketch, "E12412", {"start": v(19.02, 64.51) * mm, "end": v(18.73, 64.66) * mm});
            skLineSegment(sketch, "E12413", {"start": v(18.73, 64.66) * mm, "end": v(18.5, 64.79) * mm});
            skLineSegment(sketch, "E12414", {"start": v(18.5, 64.79) * mm, "end": v(18.36, 64.88) * mm});
            skLineSegment(sketch, "E12415", {"start": v(18.36, 64.88) * mm, "end": v(18.27, 64.94) * mm});
            skLineSegment(sketch, "E12416", {"start": v(18.27, 64.94) * mm, "end": v(18.24, 64.97) * mm});
            skLineSegment(sketch, "E12417", {"start": v(18.24, 64.97) * mm, "end": v(16.74, 66.2) * mm});
            skArc(sketch, "E12418", {"start": v(16.74, 66.2) * mm, "mid": v(15.67, 64.97) * mm, "end": v(14.54, 63.82) * mm});
            skLineSegment(sketch, "E12419", {"start": v(14.54, 63.82) * mm, "end": v(15.87, 62.42) * mm});
            skLineSegment(sketch, "E12420", {"start": v(15.87, 62.42) * mm, "end": v(15.9, 62.4) * mm});
            skLineSegment(sketch, "E12421", {"start": v(15.9, 62.4) * mm, "end": v(15.97, 62.3) * mm});
            skLineSegment(sketch, "E12422", {"start": v(15.97, 62.3) * mm, "end": v(16.07, 62.16) * mm});
            skLineSegment(sketch, "E12423", {"start": v(16.07, 62.16) * mm, "end": v(16.22, 61.95) * mm});
            skLineSegment(sketch, "E12424", {"start": v(16.22, 61.95) * mm, "end": v(16.38, 61.67) * mm});
            skLineSegment(sketch, "E12425", {"start": v(16.38, 61.67) * mm, "end": v(16.57, 61.32) * mm});
            skLineSegment(sketch, "E12426", {"start": v(16.57, 61.32) * mm, "end": v(16.77, 60.89) * mm});
            skLineSegment(sketch, "E12427", {"start": v(16.77, 60.89) * mm, "end": v(16.97, 60.38) * mm});
            skLineSegment(sketch, "E12428", {"start": v(16.97, 60.38) * mm, "end": v(17.18, 59.8) * mm});
            skLineSegment(sketch, "E12429", {"start": v(17.18, 59.8) * mm, "end": v(17.37, 59.14) * mm});
            skLineSegment(sketch, "E12430", {"start": v(17.37, 59.14) * mm, "end": v(17.38, 59.11) * mm});
            skArc(sketch, "E12431", {"start": v(17.38, 59.11) * mm, "mid": v(16.54, 58.39) * mm, "end": v(15.67, 57.7) * mm});
            skLineSegment(sketch, "E12432", {"start": v(15.67, 57.7) * mm, "end": v(15.64, 57.7) * mm});
            skLineSegment(sketch, "E12433", {"start": v(15.64, 57.7) * mm, "end": v(15.03, 58.02) * mm});
            skLineSegment(sketch, "E12434", {"start": v(15.03, 58.02) * mm, "end": v(14.5, 58.33) * mm});
            skLineSegment(sketch, "E12435", {"start": v(14.5, 58.33) * mm, "end": v(14.04, 58.62) * mm});
            skLineSegment(sketch, "E12436", {"start": v(14.04, 58.62) * mm, "end": v(13.65, 58.9) * mm});
            skLineSegment(sketch, "E12437", {"start": v(13.65, 58.9) * mm, "end": v(13.34, 59.15) * mm});
            skLineSegment(sketch, "E12438", {"start": v(13.34, 59.15) * mm, "end": v(13.1, 59.37) * mm});
            skLineSegment(sketch, "E12439", {"start": v(13.1, 59.37) * mm, "end": v(12.91, 59.54) * mm});
            skLineSegment(sketch, "E12440", {"start": v(12.91, 59.54) * mm, "end": v(12.8, 59.68) * mm});
            skLineSegment(sketch, "E12441", {"start": v(12.8, 59.68) * mm, "end": v(12.72, 59.76) * mm});
            skLineSegment(sketch, "E12442", {"start": v(12.72, 59.76) * mm, "end": v(12.7, 59.79) * mm});
            skLineSegment(sketch, "E12443", {"start": v(12.7, 59.79) * mm, "end": v(11.57, 61.36) * mm});
            skArc(sketch, "E12444", {"start": v(11.57, 61.36) * mm, "mid": v(10.22, 60.46) * mm, "end": v(8.83, 59.64) * mm});
            skLineSegment(sketch, "E12445", {"start": v(8.83, 59.64) * mm, "end": v(9.76, 57.94) * mm});
            skLineSegment(sketch, "E12446", {"start": v(9.76, 57.94) * mm, "end": v(9.77, 57.9) * mm});
            skLineSegment(sketch, "E12447", {"start": v(9.77, 57.9) * mm, "end": v(9.82, 57.8) * mm});
            skLineSegment(sketch, "E12448", {"start": v(9.82, 57.8) * mm, "end": v(9.88, 57.64) * mm});
            skLineSegment(sketch, "E12449", {"start": v(9.88, 57.64) * mm, "end": v(9.96, 57.4) * mm});
            skLineSegment(sketch, "E12450", {"start": v(9.96, 57.4) * mm, "end": v(10.05, 57.08) * mm});
            skLineSegment(sketch, "E12451", {"start": v(10.05, 57.08) * mm, "end": v(10.14, 56.7) * mm});
            skLineSegment(sketch, "E12452", {"start": v(10.14, 56.7) * mm, "end": v(10.22, 56.23) * mm});
            skLineSegment(sketch, "E12453", {"start": v(10.22, 56.23) * mm, "end": v(10.3, 55.7) * mm});
            skLineSegment(sketch, "E12454", {"start": v(10.3, 55.7) * mm, "end": v(10.34, 55.07) * mm});
            skLineSegment(sketch, "E12455", {"start": v(10.34, 55.07) * mm, "end": v(10.36, 54.39) * mm});
            skLineSegment(sketch, "E12456", {"start": v(10.36, 54.39) * mm, "end": v(10.36, 54.35) * mm});
            skArc(sketch, "E12457", {"start": v(10.36, 54.35) * mm, "mid": v(9.35, 53.87) * mm, "end": v(8.33, 53.43) * mm});
            skLineSegment(sketch, "E12458", {"start": v(8.33, 53.43) * mm, "end": v(8.3, 53.45) * mm});
            skLineSegment(sketch, "E12459", {"start": v(8.3, 53.45) * mm, "end": v(7.8, 53.9) * mm});
            skLineSegment(sketch, "E12460", {"start": v(7.8, 53.9) * mm, "end": v(7.36, 54.35) * mm});
            skLineSegment(sketch, "E12461", {"start": v(7.36, 54.35) * mm, "end": v(7, 54.75) * mm});
            skLineSegment(sketch, "E12462", {"start": v(7, 54.75) * mm, "end": v(6.7, 55.12) * mm});
            skLineSegment(sketch, "E12463", {"start": v(6.7, 55.12) * mm, "end": v(6.46, 55.44) * mm});
            skLineSegment(sketch, "E12464", {"start": v(6.46, 55.44) * mm, "end": v(6.28, 55.7) * mm});
            skLineSegment(sketch, "E12465", {"start": v(6.28, 55.7) * mm, "end": v(6.15, 55.93) * mm});
            skLineSegment(sketch, "E12466", {"start": v(6.15, 55.93) * mm, "end": v(6.07, 56.09) * mm});
            skLineSegment(sketch, "E12467", {"start": v(6.07, 56.09) * mm, "end": v(6.02, 56.19) * mm});
            skLineSegment(sketch, "E12468", {"start": v(6.02, 56.19) * mm, "end": v(6, 56.22) * mm});
            skLineSegment(sketch, "E12469", {"start": v(6, 56.22) * mm, "end": v(5.33, 58.03) * mm});
            skArc(sketch, "E12470", {"start": v(5.33, 58.03) * mm, "mid": v(3.8, 57.51) * mm, "end": v(2.23, 57.08) * mm});
            skLineSegment(sketch, "E12471", {"start": v(2.23, 57.08) * mm, "end": v(2.69, 55.2) * mm});
            skLineSegment(sketch, "E12472", {"start": v(2.69, 55.2) * mm, "end": v(2.7, 55.16) * mm});
            skLineSegment(sketch, "E12473", {"start": v(2.7, 55.16) * mm, "end": v(2.71, 55.05) * mm});
            skLineSegment(sketch, "E12474", {"start": v(2.71, 55.05) * mm, "end": v(2.73, 54.87) * mm});
            skLineSegment(sketch, "E12475", {"start": v(2.73, 54.87) * mm, "end": v(2.75, 54.62) * mm});
            skLineSegment(sketch, "E12476", {"start": v(2.75, 54.62) * mm, "end": v(2.75, 54.3) * mm});
            skLineSegment(sketch, "E12477", {"start": v(2.75, 54.3) * mm, "end": v(2.74, 53.9) * mm});
            skLineSegment(sketch, "E12478", {"start": v(2.74, 53.9) * mm, "end": v(2.7, 53.42) * mm});
            skLineSegment(sketch, "E12479", {"start": v(2.7, 53.42) * mm, "end": v(2.62, 52.88) * mm});
            skLineSegment(sketch, "E12480", {"start": v(2.62, 52.88) * mm, "end": v(2.5, 52.28) * mm});
            skLineSegment(sketch, "E12481", {"start": v(2.5, 52.28) * mm, "end": v(2.35, 51.6) * mm});
            skLineSegment(sketch, "E12482", {"start": v(2.35, 51.6) * mm, "end": v(2.34, 51.58) * mm});
            skArc(sketch, "E12483", {"start": v(2.34, 51.58) * mm, "mid": v(1.25, 51.37) * mm, "end": v(0.15, 51.2) * mm});
            skLineSegment(sketch, "E12484", {"start": v(0.15, 51.2) * mm, "end": v(0.13, 51.23) * mm});
            skLineSegment(sketch, "E12485", {"start": v(0.13, 51.23) * mm, "end": v(-0.25, 51.81) * mm});
            skLineSegment(sketch, "E12486", {"start": v(-0.25, 51.81) * mm, "end": v(-0.55, 52.34) * mm});
            skLineSegment(sketch, "E12487", {"start": v(-0.55, 52.34) * mm, "end": v(-0.8, 52.83) * mm});
            skLineSegment(sketch, "E12488", {"start": v(-0.8, 52.83) * mm, "end": v(-1, 53.26) * mm});
            skLineSegment(sketch, "E12489", {"start": v(-1, 53.26) * mm, "end": v(-1.14, 53.63) * mm});
            skLineSegment(sketch, "E12490", {"start": v(-1.14, 53.63) * mm, "end": v(-1.25, 53.94) * mm});
            skLineSegment(sketch, "E12491", {"start": v(-1.25, 53.94) * mm, "end": v(-1.31, 54.19) * mm});
            skLineSegment(sketch, "E12492", {"start": v(-1.31, 54.19) * mm, "end": v(-1.35, 54.36) * mm});
            skLineSegment(sketch, "E12493", {"start": v(-1.35, 54.36) * mm, "end": v(-1.37, 54.47) * mm});
            skLineSegment(sketch, "E12494", {"start": v(-1.37, 54.47) * mm, "end": v(-1.38, 54.5) * mm});
            skLineSegment(sketch, "E12495", {"start": v(-1.38, 54.5) * mm, "end": v(-1.57, 56.43) * mm});
            skArc(sketch, "E12496", {"start": v(-1.57, 56.43) * mm, "mid": v(-3.18, 56.33) * mm, "end": v(-4.8, 56.31) * mm});
            skLineSegment(sketch, "E12497", {"start": v(-4.8, 56.31) * mm, "end": v(-4.85, 54.38) * mm});
            skLineSegment(sketch, "E12498", {"start": v(-4.85, 54.38) * mm, "end": v(-4.85, 54.34) * mm});
            skLineSegment(sketch, "E12499", {"start": v(-4.85, 54.34) * mm, "end": v(-4.86, 54.23) * mm});
            skLineSegment(sketch, "E12500", {"start": v(-4.86, 54.23) * mm, "end": v(-4.9, 54.05) * mm});
            skLineSegment(sketch, "E12501", {"start": v(-4.9, 54.05) * mm, "end": v(-4.94, 53.8) * mm});
            skLineSegment(sketch, "E12502", {"start": v(-4.94, 53.8) * mm, "end": v(-5.02, 53.49) * mm});
            skLineSegment(sketch, "E12503", {"start": v(-5.02, 53.49) * mm, "end": v(-5.14, 53.1) * mm});
            skLineSegment(sketch, "E12504", {"start": v(-5.14, 53.1) * mm, "end": v(-5.3, 52.66) * mm});
            skLineSegment(sketch, "E12505", {"start": v(-5.3, 52.66) * mm, "end": v(-5.51, 52.16) * mm});
            skLineSegment(sketch, "E12506", {"start": v(-5.51, 52.16) * mm, "end": v(-5.78, 51.6) * mm});
            skLineSegment(sketch, "E12507", {"start": v(-5.78, 51.6) * mm, "end": v(-6.1, 51) * mm});
            skLineSegment(sketch, "E12508", {"start": v(-6.1, 51) * mm, "end": v(-6.12, 50.97) * mm});
            skArc(sketch, "E12509", {"start": v(-6.12, 50.97) * mm, "mid": v(-7.23, 51.06) * mm, "end": v(-8.34, 51.18) * mm});
            skLineSegment(sketch, "E12510", {"start": v(-8.34, 51.18) * mm, "end": v(-8.35, 51.2) * mm});
            skLineSegment(sketch, "E12511", {"start": v(-8.35, 51.2) * mm, "end": v(-8.56, 51.86) * mm});
            skLineSegment(sketch, "E12512", {"start": v(-8.56, 51.86) * mm, "end": v(-8.72, 52.46) * mm});
            skLineSegment(sketch, "E12513", {"start": v(-8.72, 52.46) * mm, "end": v(-8.83, 53) * mm});
            skLineSegment(sketch, "E12514", {"start": v(-8.83, 53) * mm, "end": v(-8.9, 53.46) * mm});
            skLineSegment(sketch, "E12515", {"start": v(-8.9, 53.46) * mm, "end": v(-8.95, 53.86) * mm});
            skLineSegment(sketch, "E12516", {"start": v(-8.95, 53.86) * mm, "end": v(-8.97, 54.18) * mm});
            skLineSegment(sketch, "E12517", {"start": v(-8.97, 54.18) * mm, "end": v(-8.98, 54.44) * mm});
            skLineSegment(sketch, "E12518", {"start": v(-8.98, 54.44) * mm, "end": v(-8.97, 54.62) * mm});
            skLineSegment(sketch, "E12519", {"start": v(-8.97, 54.62) * mm, "end": v(-8.96, 54.73) * mm});
            skLineSegment(sketch, "E12520", {"start": v(-8.96, 54.73) * mm, "end": v(-8.96, 54.76) * mm});
            skLineSegment(sketch, "E12521", {"start": v(-8.96, 54.76) * mm, "end": v(-8.64, 56.67) * mm});
            skArc(sketch, "E12522", {"start": v(-8.64, 56.67) * mm, "mid": v(-10.23, 56.99) * mm, "end": v(-11.8, 57.4) * mm});
            skLineSegment(sketch, "E12523", {"start": v(-11.8, 57.4) * mm, "end": v(-12.34, 55.54) * mm});
            skLineSegment(sketch, "E12524", {"start": v(-12.34, 55.54) * mm, "end": v(-12.35, 55.5) * mm});
            skLineSegment(sketch, "E12525", {"start": v(-12.35, 55.5) * mm, "end": v(-12.4, 55.4) * mm});
            skLineSegment(sketch, "E12526", {"start": v(-12.4, 55.4) * mm, "end": v(-12.47, 55.23) * mm});
            skLineSegment(sketch, "E12527", {"start": v(-12.47, 55.23) * mm, "end": v(-12.58, 55) * mm});
            skLineSegment(sketch, "E12528", {"start": v(-12.58, 55) * mm, "end": v(-12.74, 54.72) * mm});
            skLineSegment(sketch, "E12529", {"start": v(-12.74, 54.72) * mm, "end": v(-12.95, 54.38) * mm});
            skLineSegment(sketch, "E12530", {"start": v(-12.95, 54.38) * mm, "end": v(-13.22, 54) * mm});
            skLineSegment(sketch, "E12531", {"start": v(-13.22, 54) * mm, "end": v(-13.55, 53.56) * mm});
            skLineSegment(sketch, "E12532", {"start": v(-13.55, 53.56) * mm, "end": v(-13.96, 53.1) * mm});
            skLineSegment(sketch, "E12533", {"start": v(-13.96, 53.1) * mm, "end": v(-14.43, 52.6) * mm});
            skLineSegment(sketch, "E12534", {"start": v(-14.43, 52.6) * mm, "end": v(-14.45, 52.58) * mm});
            skArc(sketch, "E12535", {"start": v(-14.45, 52.58) * mm, "mid": v(-15.5, 52.94) * mm, "end": v(-16.54, 53.35) * mm});
            skLineSegment(sketch, "E12536", {"start": v(-16.54, 53.35) * mm, "end": v(-16.54, 53.38) * mm});
            skLineSegment(sketch, "E12537", {"start": v(-16.54, 53.38) * mm, "end": v(-16.58, 54.07) * mm});
            skLineSegment(sketch, "E12538", {"start": v(-16.58, 54.07) * mm, "end": v(-16.58, 54.69) * mm});
            skLineSegment(sketch, "E12539", {"start": v(-16.58, 54.69) * mm, "end": v(-16.55, 55.23) * mm});
            skLineSegment(sketch, "E12540", {"start": v(-16.55, 55.23) * mm, "end": v(-16.5, 55.7) * mm});
            skLineSegment(sketch, "E12541", {"start": v(-16.5, 55.7) * mm, "end": v(-16.44, 56.1) * mm});
            skLineSegment(sketch, "E12542", {"start": v(-16.44, 56.1) * mm, "end": v(-16.38, 56.41) * mm});
            skLineSegment(sketch, "E12543", {"start": v(-16.38, 56.41) * mm, "end": v(-16.31, 56.66) * mm});
            skLineSegment(sketch, "E12544", {"start": v(-16.31, 56.66) * mm, "end": v(-16.26, 56.83) * mm});
            skLineSegment(sketch, "E12545", {"start": v(-16.26, 56.83) * mm, "end": v(-16.22, 56.94) * mm});
            skLineSegment(sketch, "E12546", {"start": v(-16.22, 56.94) * mm, "end": v(-16.2, 56.97) * mm});
            skLineSegment(sketch, "E12547", {"start": v(-16.2, 56.97) * mm, "end": v(-15.4, 58.73) * mm});
            skArc(sketch, "E12548", {"start": v(-15.4, 58.73) * mm, "mid": v(-16.86, 59.45) * mm, "end": v(-18.28, 60.25) * mm});
            skLineSegment(sketch, "E12549", {"start": v(-18.28, 60.25) * mm, "end": v(-19.28, 58.6) * mm});
            skLineSegment(sketch, "E12550", {"start": v(-19.28, 58.6) * mm, "end": v(-19.3, 58.56) * mm});
            skLineSegment(sketch, "E12551", {"start": v(-19.3, 58.56) * mm, "end": v(-19.36, 58.48) * mm});
            skLineSegment(sketch, "E12552", {"start": v(-19.36, 58.48) * mm, "end": v(-19.48, 58.33) * mm});
            skLineSegment(sketch, "E12553", {"start": v(-19.48, 58.33) * mm, "end": v(-19.65, 58.14) * mm});
            skLineSegment(sketch, "E12554", {"start": v(-19.65, 58.14) * mm, "end": v(-19.87, 57.9) * mm});
            skLineSegment(sketch, "E12555", {"start": v(-19.87, 57.9) * mm, "end": v(-20.17, 57.64) * mm});
            skLineSegment(sketch, "E12556", {"start": v(-20.17, 57.64) * mm, "end": v(-20.53, 57.33) * mm});
            skLineSegment(sketch, "E12557", {"start": v(-20.53, 57.33) * mm, "end": v(-20.96, 57) * mm});
            skLineSegment(sketch, "E12558", {"start": v(-20.96, 57) * mm, "end": v(-21.47, 56.66) * mm});
            skLineSegment(sketch, "E12559", {"start": v(-21.47, 56.66) * mm, "end": v(-22.06, 56.3) * mm});
            skLineSegment(sketch, "E12560", {"start": v(-22.06, 56.3) * mm, "end": v(-22.09, 56.28) * mm});
            skArc(sketch, "E12561", {"start": v(-22.09, 56.28) * mm, "mid": v(-23, 56.9) * mm, "end": v(-23.9, 57.57) * mm});
            skLineSegment(sketch, "E12562", {"start": v(-23.9, 57.57) * mm, "end": v(-23.9, 57.6) * mm});
            skLineSegment(sketch, "E12563", {"start": v(-23.9, 57.6) * mm, "end": v(-23.75, 58.27) * mm});
            skLineSegment(sketch, "E12564", {"start": v(-23.75, 58.27) * mm, "end": v(-23.6, 58.87) * mm});
            skLineSegment(sketch, "E12565", {"start": v(-23.6, 58.87) * mm, "end": v(-23.42, 59.39) * mm});
            skLineSegment(sketch, "E12566", {"start": v(-23.42, 59.39) * mm, "end": v(-23.26, 59.83) * mm});
            skLineSegment(sketch, "E12567", {"start": v(-23.26, 59.83) * mm, "end": v(-23.1, 60.2) * mm});
            skLineSegment(sketch, "E12568", {"start": v(-23.1, 60.2) * mm, "end": v(-22.95, 60.49) * mm});
            skLineSegment(sketch, "E12569", {"start": v(-22.95, 60.49) * mm, "end": v(-22.83, 60.7) * mm});
            skLineSegment(sketch, "E12570", {"start": v(-22.83, 60.7) * mm, "end": v(-22.73, 60.86) * mm});
            skLineSegment(sketch, "E12571", {"start": v(-22.73, 60.86) * mm, "end": v(-22.67, 60.95) * mm});
            skLineSegment(sketch, "E12572", {"start": v(-22.67, 60.95) * mm, "end": v(-22.64, 60.98) * mm});
            skLineSegment(sketch, "E12573", {"start": v(-22.64, 60.98) * mm, "end": v(-21.41, 62.48) * mm});
            skArc(sketch, "E12574", {"start": v(-21.41, 62.48) * mm, "mid": v(-22.64, 63.54) * mm, "end": v(-23.8, 64.68) * mm});
            skLineSegment(sketch, "E12575", {"start": v(-23.8, 64.68) * mm, "end": v(-25.2, 63.34) * mm});
            skLineSegment(sketch, "E12576", {"start": v(-25.2, 63.34) * mm, "end": v(-25.22, 63.32) * mm});
            skLineSegment(sketch, "E12577", {"start": v(-25.22, 63.32) * mm, "end": v(-25.3, 63.25) * mm});
            skLineSegment(sketch, "E12578", {"start": v(-25.3, 63.25) * mm, "end": v(-25.45, 63.14) * mm});
            skLineSegment(sketch, "E12579", {"start": v(-25.45, 63.14) * mm, "end": v(-25.66, 63) * mm});
            skLineSegment(sketch, "E12580", {"start": v(-25.66, 63) * mm, "end": v(-25.94, 62.84) * mm});
            skLineSegment(sketch, "E12581", {"start": v(-25.94, 62.84) * mm, "end": v(-26.3, 62.65) * mm});
            skLineSegment(sketch, "E12582", {"start": v(-26.3, 62.65) * mm, "end": v(-26.72, 62.45) * mm});
            skLineSegment(sketch, "E12583", {"start": v(-26.72, 62.45) * mm, "end": v(-27.23, 62.24) * mm});
            skLineSegment(sketch, "E12584", {"start": v(-27.23, 62.24) * mm, "end": v(-27.8, 62.04) * mm});
            skLineSegment(sketch, "E12585", {"start": v(-27.8, 62.04) * mm, "end": v(-28.47, 61.84) * mm});
            skLineSegment(sketch, "E12586", {"start": v(-28.47, 61.84) * mm, "end": v(-28.5, 61.84) * mm});
            skArc(sketch, "E12587", {"start": v(-28.5, 61.84) * mm, "mid": v(-29.22, 62.68) * mm, "end": v(-29.92, 63.55) * mm});
            skLineSegment(sketch, "E12588", {"start": v(-29.92, 63.55) * mm, "end": v(-29.9, 63.58) * mm});
            skLineSegment(sketch, "E12589", {"start": v(-29.9, 63.58) * mm, "end": v(-29.6, 64.2) * mm});
            skLineSegment(sketch, "E12590", {"start": v(-29.6, 64.2) * mm, "end": v(-29.28, 64.73) * mm});
            skLineSegment(sketch, "E12591", {"start": v(-29.28, 64.73) * mm, "end": v(-28.99, 65.18) * mm});
            skLineSegment(sketch, "E12592", {"start": v(-28.99, 65.18) * mm, "end": v(-28.71, 65.57) * mm});
            skLineSegment(sketch, "E12593", {"start": v(-28.71, 65.57) * mm, "end": v(-28.46, 65.88) * mm});
            skLineSegment(sketch, "E12594", {"start": v(-28.46, 65.88) * mm, "end": v(-28.24, 66.12) * mm});
            skLineSegment(sketch, "E12595", {"start": v(-28.24, 66.12) * mm, "end": v(-28.07, 66.3) * mm});
            skLineSegment(sketch, "E12596", {"start": v(-28.07, 66.3) * mm, "end": v(-27.93, 66.43) * mm});
            skLineSegment(sketch, "E12597", {"start": v(-27.93, 66.43) * mm, "end": v(-27.85, 66.5) * mm});
            skLineSegment(sketch, "E12598", {"start": v(-27.85, 66.5) * mm, "end": v(-27.82, 66.52) * mm});
            skLineSegment(sketch, "E12599", {"start": v(-27.82, 66.52) * mm, "end": v(-26.25, 67.65) * mm});
            skArc(sketch, "E12600", {"start": v(-26.25, 67.65) * mm, "mid": v(-27.15, 69) * mm, "end": v(-27.97, 70.4) * mm});
            skLineSegment(sketch, "E12601", {"start": v(-27.97, 70.4) * mm, "end": v(-29.67, 69.46) * mm});
            skLineSegment(sketch, "E12602", {"start": v(-29.67, 69.46) * mm, "end": v(-29.7, 69.45) * mm});
            skLineSegment(sketch, "E12603", {"start": v(-29.7, 69.45) * mm, "end": v(-29.8, 69.4) * mm});
            skLineSegment(sketch, "E12604", {"start": v(-29.8, 69.4) * mm, "end": v(-29.97, 69.33) * mm});
            skLineSegment(sketch, "E12605", {"start": v(-29.97, 69.33) * mm, "end": v(-30.21, 69.25) * mm});
            skLineSegment(sketch, "E12606", {"start": v(-30.21, 69.25) * mm, "end": v(-30.53, 69.16) * mm});
            skLineSegment(sketch, "E12607", {"start": v(-30.53, 69.16) * mm, "end": v(-30.92, 69.08) * mm});
            skLineSegment(sketch, "E12608", {"start": v(-30.92, 69.08) * mm, "end": v(-31.38, 69) * mm});
            skLineSegment(sketch, "E12609", {"start": v(-31.38, 69) * mm, "end": v(-31.92, 68.92) * mm});
            skLineSegment(sketch, "E12610", {"start": v(-31.92, 68.92) * mm, "end": v(-32.54, 68.88) * mm});
            skLineSegment(sketch, "E12611", {"start": v(-32.54, 68.88) * mm, "end": v(-33.23, 68.86) * mm});
            skLineSegment(sketch, "E12612", {"start": v(-33.23, 68.86) * mm, "end": v(-33.26, 68.86) * mm});
            skArc(sketch, "E12613", {"start": v(-33.26, 68.86) * mm, "mid": v(-33.74, 69.86) * mm, "end": v(-34.18, 70.88) * mm});
            skLineSegment(sketch, "E12614", {"start": v(-34.18, 70.88) * mm, "end": v(-34.16, 70.9) * mm});
            skLineSegment(sketch, "E12615", {"start": v(-34.16, 70.9) * mm, "end": v(-33.7, 71.42) * mm});
            skLineSegment(sketch, "E12616", {"start": v(-33.7, 71.42) * mm, "end": v(-33.26, 71.85) * mm});
            skLineSegment(sketch, "E12617", {"start": v(-33.26, 71.85) * mm, "end": v(-32.86, 72.22) * mm});
            skLineSegment(sketch, "E12618", {"start": v(-32.86, 72.22) * mm, "end": v(-32.5, 72.52) * mm});
            skLineSegment(sketch, "E12619", {"start": v(-32.5, 72.52) * mm, "end": v(-32.17, 72.75) * mm});
            skLineSegment(sketch, "E12620", {"start": v(-32.17, 72.75) * mm, "end": v(-31.9, 72.94) * mm});
            skLineSegment(sketch, "E12621", {"start": v(-31.9, 72.94) * mm, "end": v(-31.68, 73.06) * mm});
            skLineSegment(sketch, "E12622", {"start": v(-31.68, 73.06) * mm, "end": v(-31.52, 73.15) * mm});
            skLineSegment(sketch, "E12623", {"start": v(-31.52, 73.15) * mm, "end": v(-31.42, 73.2) * mm});
            skLineSegment(sketch, "E12624", {"start": v(-31.42, 73.2) * mm, "end": v(-31.39, 73.2) * mm});
            skLineSegment(sketch, "E12625", {"start": v(-31.39, 73.2) * mm, "end": v(-29.58, 73.9) * mm});
            skArc(sketch, "E12626", {"start": v(-29.58, 73.9) * mm, "mid": v(-30.1, 75.43) * mm, "end": v(-30.53, 76.99) * mm});
            skLineSegment(sketch, "E12627", {"start": v(-30.53, 76.99) * mm, "end": v(-32.41, 76.53) * mm});
            skLineSegment(sketch, "E12628", {"start": v(-32.41, 76.53) * mm, "end": v(-32.45, 76.52) * mm});
            skLineSegment(sketch, "E12629", {"start": v(-32.45, 76.52) * mm, "end": v(-32.56, 76.5) * mm});
            skLineSegment(sketch, "E12630", {"start": v(-32.56, 76.5) * mm, "end": v(-32.74, 76.48) * mm});
            skLineSegment(sketch, "E12631", {"start": v(-32.74, 76.48) * mm, "end": v(-33, 76.47) * mm});
            skLineSegment(sketch, "E12632", {"start": v(-33, 76.47) * mm, "end": v(-33.32, 76.46) * mm});
            skLineSegment(sketch, "E12633", {"start": v(-33.32, 76.46) * mm, "end": v(-33.72, 76.48) * mm});
            skLineSegment(sketch, "E12634", {"start": v(-33.72, 76.48) * mm, "end": v(-34.19, 76.52) * mm});
            skLineSegment(sketch, "E12635", {"start": v(-34.19, 76.52) * mm, "end": v(-34.73, 76.6) * mm});
            skLineSegment(sketch, "E12636", {"start": v(-34.73, 76.6) * mm, "end": v(-35.33, 76.7) * mm});
            skLineSegment(sketch, "E12637", {"start": v(-35.33, 76.7) * mm, "end": v(-36, 76.87) * mm});
            skLineSegment(sketch, "E12638", {"start": v(-36, 76.87) * mm, "end": v(-36.03, 76.88) * mm});
            skArc(sketch, "E12639", {"start": v(-36.03, 76.88) * mm, "mid": v(-36.24, 77.97) * mm, "end": v(-36.4, 79.07) * mm});
            skLineSegment(sketch, "E12640", {"start": v(-36.4, 79.07) * mm, "end": v(-36.38, 79.1) * mm});
            skLineSegment(sketch, "E12641", {"start": v(-36.38, 79.1) * mm, "end": v(-35.8, 79.46) * mm});
            skLineSegment(sketch, "E12642", {"start": v(-35.8, 79.46) * mm, "end": v(-35.27, 79.77) * mm});
            skLineSegment(sketch, "E12643", {"start": v(-35.27, 79.77) * mm, "end": v(-34.78, 80.02) * mm});
            skLineSegment(sketch, "E12644", {"start": v(-34.78, 80.02) * mm, "end": v(-34.35, 80.21) * mm});
            skLineSegment(sketch, "E12645", {"start": v(-34.35, 80.21) * mm, "end": v(-33.98, 80.36) * mm});
            skLineSegment(sketch, "E12646", {"start": v(-33.98, 80.36) * mm, "end": v(-33.67, 80.46) * mm});
            skLineSegment(sketch, "E12647", {"start": v(-33.67, 80.46) * mm, "end": v(-33.42, 80.53) * mm});
            skLineSegment(sketch, "E12648", {"start": v(-33.42, 80.53) * mm, "end": v(-33.25, 80.57) * mm});
            skLineSegment(sketch, "E12649", {"start": v(-33.25, 80.57) * mm, "end": v(-33.14, 80.6) * mm});
            skLineSegment(sketch, "E12650", {"start": v(-33.14, 80.6) * mm, "end": v(-33.1, 80.6) * mm});
            skLineSegment(sketch, "E12651", {"start": v(-33.1, 80.6) * mm, "end": v(-31.18, 80.78) * mm});
            skArc(sketch, "E12652", {"start": v(-31.18, 80.78) * mm, "mid": v(-31.29, 82.4) * mm, "end": v(-31.3, 84.02) * mm});
            skLineSegment(sketch, "E12653", {"start": v(-31.3, 84.02) * mm, "end": v(-33.23, 84.07) * mm});
            skLineSegment(sketch, "E12654", {"start": v(-33.23, 84.07) * mm, "end": v(-33.27, 84.07) * mm});
            skLineSegment(sketch, "E12655", {"start": v(-33.27, 84.07) * mm, "end": v(-33.38, 84.08) * mm});
            skLineSegment(sketch, "E12656", {"start": v(-33.38, 84.08) * mm, "end": v(-33.56, 84.1) * mm});
            skLineSegment(sketch, "E12657", {"start": v(-33.56, 84.1) * mm, "end": v(-33.8, 84.16) * mm});
            skLineSegment(sketch, "E12658", {"start": v(-33.8, 84.16) * mm, "end": v(-34.12, 84.24) * mm});
            skLineSegment(sketch, "E12659", {"start": v(-34.12, 84.24) * mm, "end": v(-34.5, 84.36) * mm});
            skLineSegment(sketch, "E12660", {"start": v(-34.5, 84.36) * mm, "end": v(-34.95, 84.52) * mm});
            skLineSegment(sketch, "E12661", {"start": v(-34.95, 84.52) * mm, "end": v(-35.45, 84.73) * mm});
            skLineSegment(sketch, "E12662", {"start": v(-35.45, 84.73) * mm, "end": v(-36, 85) * mm});
            skLineSegment(sketch, "E12663", {"start": v(-36, 85) * mm, "end": v(-36.61, 85.32) * mm});
            skLineSegment(sketch, "E12664", {"start": v(-36.61, 85.32) * mm, "end": v(-36.64, 85.34) * mm});
            skArc(sketch, "E12665", {"start": v(-36.64, 85.34) * mm, "mid": v(-36.55, 86.45) * mm, "end": v(-36.43, 87.56) * mm});
            skLineSegment(sketch, "E12666", {"start": v(-36.43, 87.56) * mm, "end": v(-36.4, 87.57) * mm});
            skLineSegment(sketch, "E12667", {"start": v(-36.4, 87.57) * mm, "end": v(-35.75, 87.78) * mm});
            skLineSegment(sketch, "E12668", {"start": v(-35.75, 87.78) * mm, "end": v(-35.15, 87.94) * mm});
            skLineSegment(sketch, "E12669", {"start": v(-35.15, 87.94) * mm, "end": v(-34.62, 88.05) * mm});
            skLineSegment(sketch, "E12670", {"start": v(-34.62, 88.05) * mm, "end": v(-34.15, 88.13) * mm});
            skLineSegment(sketch, "E12671", {"start": v(-34.15, 88.13) * mm, "end": v(-33.75, 88.17) * mm});
            skLineSegment(sketch, "E12672", {"start": v(-33.75, 88.17) * mm, "end": v(-33.43, 88.2) * mm});
            skLineSegment(sketch, "E12673", {"start": v(-33.43, 88.2) * mm, "end": v(-33.17, 88.2) * mm});
            skLineSegment(sketch, "E12674", {"start": v(-33.17, 88.2) * mm, "end": v(-33, 88.19) * mm});
            skLineSegment(sketch, "E12675", {"start": v(-33, 88.19) * mm, "end": v(-32.88, 88.18) * mm});
            skLineSegment(sketch, "E12676", {"start": v(-32.88, 88.18) * mm, "end": v(-32.85, 88.17) * mm});
            skLineSegment(sketch, "E12677", {"start": v(-32.85, 88.17) * mm, "end": v(-30.94, 87.86) * mm});
            skArc(sketch, "E12678", {"start": v(-30.94, 87.86) * mm, "mid": v(-30.62, 89.45) * mm, "end": v(-30.22, 91.02) * mm});
            skLineSegment(sketch, "E12679", {"start": v(-30.22, 91.02) * mm, "end": v(-32.07, 91.56) * mm});
            skLineSegment(sketch, "E12680", {"start": v(-32.07, 91.56) * mm, "end": v(-32.1, 91.57) * mm});
            skLineSegment(sketch, "E12681", {"start": v(-32.1, 91.57) * mm, "end": v(-32.21, 91.61) * mm});
            skLineSegment(sketch, "E12682", {"start": v(-32.21, 91.61) * mm, "end": v(-32.38, 91.68) * mm});
            skLineSegment(sketch, "E12683", {"start": v(-32.38, 91.68) * mm, "end": v(-32.6, 91.8) * mm});
            skLineSegment(sketch, "E12684", {"start": v(-32.6, 91.8) * mm, "end": v(-32.9, 91.96) * mm});
            skLineSegment(sketch, "E12685", {"start": v(-32.9, 91.96) * mm, "end": v(-33.23, 92.17) * mm});
            skLineSegment(sketch, "E12686", {"start": v(-33.23, 92.17) * mm, "end": v(-33.62, 92.44) * mm});
            skLineSegment(sketch, "E12687", {"start": v(-33.62, 92.44) * mm, "end": v(-34.05, 92.77) * mm});
            skLineSegment(sketch, "E12688", {"start": v(-34.05, 92.77) * mm, "end": v(-34.51, 93.17) * mm});
            skLineSegment(sketch, "E12689", {"start": v(-34.51, 93.17) * mm, "end": v(-35.01, 93.65) * mm});
            skLineSegment(sketch, "E12690", {"start": v(-35.01, 93.65) * mm, "end": v(-35.04, 93.67) * mm});
            skArc(sketch, "E12691", {"start": v(-35.04, 93.67) * mm, "mid": v(-34.67, 94.72) * mm, "end": v(-34.26, 95.76) * mm});
            skLineSegment(sketch, "E12692", {"start": v(-34.26, 95.76) * mm, "end": v(-34.23, 95.76) * mm});
            skLineSegment(sketch, "E12693", {"start": v(-34.23, 95.76) * mm, "end": v(-33.54, 95.8) * mm});
            skLineSegment(sketch, "E12694", {"start": v(-33.54, 95.8) * mm, "end": v(-32.92, 95.8) * mm});
            skLineSegment(sketch, "E12695", {"start": v(-32.92, 95.8) * mm, "end": v(-32.38, 95.77) * mm});
            skLineSegment(sketch, "E12696", {"start": v(-32.38, 95.77) * mm, "end": v(-31.91, 95.72) * mm});
            skLineSegment(sketch, "E12697", {"start": v(-31.91, 95.72) * mm, "end": v(-31.52, 95.66) * mm});
            skLineSegment(sketch, "E12698", {"start": v(-31.52, 95.66) * mm, "end": v(-31.2, 95.6) * mm});
            skLineSegment(sketch, "E12699", {"start": v(-31.2, 95.6) * mm, "end": v(-30.95, 95.53) * mm});
            skLineSegment(sketch, "E12700", {"start": v(-30.95, 95.53) * mm, "end": v(-30.78, 95.48) * mm});
            skLineSegment(sketch, "E12701", {"start": v(-30.78, 95.48) * mm, "end": v(-30.67, 95.44) * mm});
            skLineSegment(sketch, "E12702", {"start": v(-30.67, 95.44) * mm, "end": v(-30.64, 95.43) * mm});
            skLineSegment(sketch, "E12703", {"start": v(-30.64, 95.43) * mm, "end": v(-28.88, 94.63) * mm});
            skArc(sketch, "E12704", {"start": v(-28.88, 94.63) * mm, "mid": v(-28.16, 96.08) * mm, "end": v(-27.36, 97.5) * mm});
            skLineSegment(sketch, "E12705", {"start": v(-27.36, 97.5) * mm, "end": v(-29.02, 98.5) * mm});
            skLineSegment(sketch, "E12706", {"start": v(-29.02, 98.5) * mm, "end": v(-29.05, 98.52) * mm});
            skLineSegment(sketch, "E12707", {"start": v(-29.05, 98.52) * mm, "end": v(-29.14, 98.58) * mm});
            skLineSegment(sketch, "E12708", {"start": v(-29.14, 98.58) * mm, "end": v(-29.28, 98.7) * mm});
            skLineSegment(sketch, "E12709", {"start": v(-29.28, 98.7) * mm, "end": v(-29.47, 98.86) * mm});
            skLineSegment(sketch, "E12710", {"start": v(-29.47, 98.86) * mm, "end": v(-29.7, 99.1) * mm});
            skLineSegment(sketch, "E12711", {"start": v(-29.7, 99.1) * mm, "end": v(-29.97, 99.38) * mm});
            skLineSegment(sketch, "E12712", {"start": v(-29.97, 99.38) * mm, "end": v(-30.28, 99.75) * mm});
            skLineSegment(sketch, "E12713", {"start": v(-30.28, 99.75) * mm, "end": v(-30.6, 100.18) * mm});
            skLineSegment(sketch, "E12714", {"start": v(-30.6, 100.18) * mm, "end": v(-30.95, 100.69) * mm});
            skLineSegment(sketch, "E12715", {"start": v(-30.95, 100.69) * mm, "end": v(-31.31, 101.28) * mm});
            skLineSegment(sketch, "E12716", {"start": v(-31.31, 101.28) * mm, "end": v(-31.33, 101.3) * mm});
            skArc(sketch, "E12717", {"start": v(-31.33, 101.3) * mm, "mid": v(-30.7, 102.22) * mm, "end": v(-30.04, 103.12) * mm});
            skLineSegment(sketch, "E12718", {"start": v(-30.04, 103.12) * mm, "end": v(-30.01, 103.11) * mm});
            skLineSegment(sketch, "E12719", {"start": v(-30.01, 103.11) * mm, "end": v(-29.34, 102.97) * mm});
            skLineSegment(sketch, "E12720", {"start": v(-29.34, 102.97) * mm, "end": v(-28.74, 102.8) * mm});
            skLineSegment(sketch, "E12721", {"start": v(-28.74, 102.8) * mm, "end": v(-28.22, 102.64) * mm});
            skLineSegment(sketch, "E12722", {"start": v(-28.22, 102.64) * mm, "end": v(-27.78, 102.47) * mm});
            skLineSegment(sketch, "E12723", {"start": v(-27.78, 102.47) * mm, "end": v(-27.42, 102.31) * mm});
            skLineSegment(sketch, "E12724", {"start": v(-27.42, 102.31) * mm, "end": v(-27.12, 102.17) * mm});
            skLineSegment(sketch, "E12725", {"start": v(-27.12, 102.17) * mm, "end": v(-26.9, 102.04) * mm});
            skLineSegment(sketch, "E12726", {"start": v(-26.9, 102.04) * mm, "end": v(-26.75, 101.95) * mm});
            skLineSegment(sketch, "E12727", {"start": v(-26.75, 101.95) * mm, "end": v(-26.66, 101.88) * mm});
            skLineSegment(sketch, "E12728", {"start": v(-26.66, 101.88) * mm, "end": v(-26.63, 101.86) * mm});
            skLineSegment(sketch, "E12729", {"start": v(-26.63, 101.86) * mm, "end": v(-25.13, 100.63) * mm});
            skArc(sketch, "E12730", {"start": v(-25.13, 100.63) * mm, "mid": v(-24.07, 101.85) * mm, "end": v(-22.93, 103) * mm});
            skLineSegment(sketch, "E12731", {"start": v(-22.93, 103) * mm, "end": v(-24.27, 104.4) * mm});
            skLineSegment(sketch, "E12732", {"start": v(-24.27, 104.4) * mm, "end": v(-24.3, 104.44) * mm});
            skLineSegment(sketch, "E12733", {"start": v(-24.3, 104.44) * mm, "end": v(-24.36, 104.52) * mm});
            skLineSegment(sketch, "E12734", {"start": v(-24.36, 104.52) * mm, "end": v(-24.47, 104.67) * mm});
            skLineSegment(sketch, "E12735", {"start": v(-24.47, 104.67) * mm, "end": v(-24.6, 104.88) * mm});
            skLineSegment(sketch, "E12736", {"start": v(-24.6, 104.88) * mm, "end": v(-24.78, 105.16) * mm});
            skLineSegment(sketch, "E12737", {"start": v(-24.78, 105.16) * mm, "end": v(-24.96, 105.51) * mm});
            skLineSegment(sketch, "E12738", {"start": v(-24.96, 105.51) * mm, "end": v(-25.16, 105.94) * mm});
            skLineSegment(sketch, "E12739", {"start": v(-25.16, 105.94) * mm, "end": v(-25.37, 106.44) * mm});
            skLineSegment(sketch, "E12740", {"start": v(-25.37, 106.44) * mm, "end": v(-25.57, 107.03) * mm});
            skLineSegment(sketch, "E12741", {"start": v(-25.57, 107.03) * mm, "end": v(-25.77, 107.69) * mm});
            skLineSegment(sketch, "E12742", {"start": v(-25.77, 107.69) * mm, "end": v(-25.77, 107.72) * mm});
            skArc(sketch, "E12743", {"start": v(-25.77, 107.72) * mm, "mid": v(-24.93, 108.44) * mm, "end": v(-24.06, 109.14) * mm});
            skLineSegment(sketch, "E12744", {"start": v(-24.06, 109.14) * mm, "end": v(-24.03, 109.12) * mm});
            skLineSegment(sketch, "E12745", {"start": v(-24.03, 109.12) * mm, "end": v(-23.42, 108.8) * mm});
            skLineSegment(sketch, "E12746", {"start": v(-23.42, 108.8) * mm, "end": v(-22.89, 108.5) * mm});
            skLineSegment(sketch, "E12747", {"start": v(-22.89, 108.5) * mm, "end": v(-22.43, 108.2) * mm});
            skLineSegment(sketch, "E12748", {"start": v(-22.43, 108.2) * mm, "end": v(-22.05, 107.93) * mm});
            skLineSegment(sketch, "E12749", {"start": v(-22.05, 107.93) * mm, "end": v(-21.73, 107.68) * mm});
            skLineSegment(sketch, "E12750", {"start": v(-21.73, 107.68) * mm, "end": v(-21.49, 107.46) * mm});
            skLineSegment(sketch, "E12751", {"start": v(-21.49, 107.46) * mm, "end": v(-21.3, 107.28) * mm});
            skLineSegment(sketch, "E12752", {"start": v(-21.3, 107.28) * mm, "end": v(-21.18, 107.15) * mm});
            skLineSegment(sketch, "E12753", {"start": v(-21.18, 107.15) * mm, "end": v(-21.11, 107.07) * mm});
            skLineSegment(sketch, "E12754", {"start": v(-21.11, 107.07) * mm, "end": v(-21.1, 107.04) * mm});
            skLineSegment(sketch, "E12755", {"start": v(-21.1, 107.04) * mm, "end": v(-19.96, 105.46) * mm});
            skArc(sketch, "E12756", {"start": v(-19.96, 105.46) * mm, "mid": v(-18.62, 106.37) * mm, "end": v(-17.22, 107.19) * mm});
            skLineSegment(sketch, "E12757", {"start": v(-17.22, 107.19) * mm, "end": v(-18.15, 108.89) * mm});
            skLineSegment(sketch, "E12758", {"start": v(-18.15, 108.89) * mm, "end": v(-18.16, 108.92) * mm});
            skLineSegment(sketch, "E12759", {"start": v(-18.16, 108.92) * mm, "end": v(-18.2, 109.02) * mm});
            skLineSegment(sketch, "E12760", {"start": v(-18.2, 109.02) * mm, "end": v(-18.28, 109.19) * mm});
            skLineSegment(sketch, "E12761", {"start": v(-18.28, 109.19) * mm, "end": v(-18.36, 109.43) * mm});
            skLineSegment(sketch, "E12762", {"start": v(-18.36, 109.43) * mm, "end": v(-18.45, 109.74) * mm});
            skLineSegment(sketch, "E12763", {"start": v(-18.45, 109.74) * mm, "end": v(-18.54, 110.13) * mm});
            skLineSegment(sketch, "E12764", {"start": v(-18.54, 110.13) * mm, "end": v(-18.62, 110.6) * mm});
            skLineSegment(sketch, "E12765", {"start": v(-18.62, 110.6) * mm, "end": v(-18.69, 111.14) * mm});
            skLineSegment(sketch, "E12766", {"start": v(-18.69, 111.14) * mm, "end": v(-18.73, 111.75) * mm});
            skLineSegment(sketch, "E12767", {"start": v(-18.73, 111.75) * mm, "end": v(-18.75, 112.44) * mm});
            skLineSegment(sketch, "E12768", {"start": v(-18.75, 112.44) * mm, "end": v(-18.75, 112.47) * mm});
            skArc(sketch, "E12769", {"start": v(-18.75, 112.47) * mm, "mid": v(-17.75, 112.95) * mm, "end": v(-16.73, 113.4) * mm});
            skLineSegment(sketch, "E12770", {"start": v(-16.73, 113.4) * mm, "end": v(-16.7, 113.38) * mm});
            skLineSegment(sketch, "E12771", {"start": v(-16.7, 113.38) * mm, "end": v(-16.2, 112.92) * mm});
            skLineSegment(sketch, "E12772", {"start": v(-16.2, 112.92) * mm, "end": v(-15.76, 112.48) * mm});
            skLineSegment(sketch, "E12773", {"start": v(-15.76, 112.48) * mm, "end": v(-15.4, 112.08) * mm});
            skLineSegment(sketch, "E12774", {"start": v(-15.4, 112.08) * mm, "end": v(-15.1, 111.71) * mm});
            skLineSegment(sketch, "E12775", {"start": v(-15.1, 111.71) * mm, "end": v(-14.86, 111.4) * mm});
            skLineSegment(sketch, "E12776", {"start": v(-14.86, 111.4) * mm, "end": v(-14.68, 111.12) * mm});
            skLineSegment(sketch, "E12777", {"start": v(-14.68, 111.12) * mm, "end": v(-14.55, 110.9) * mm});
            skLineSegment(sketch, "E12778", {"start": v(-14.55, 110.9) * mm, "end": v(-14.46, 110.74) * mm});
            skLineSegment(sketch, "E12779", {"start": v(-14.46, 110.74) * mm, "end": v(-14.41, 110.64) * mm});
            skLineSegment(sketch, "E12780", {"start": v(-14.41, 110.64) * mm, "end": v(-14.4, 110.6) * mm});
            skLineSegment(sketch, "E12781", {"start": v(-14.4, 110.6) * mm, "end": v(-13.72, 108.8) * mm});
            skArc(sketch, "E12782", {"start": v(-13.72, 108.8) * mm, "mid": v(-12.18, 109.32) * mm, "end": v(-10.62, 109.75) * mm});
            skLineSegment(sketch, "E12783", {"start": v(-10.62, 109.75) * mm, "end": v(-11.08, 111.63) * mm});
            skLineSegment(sketch, "E12784", {"start": v(-11.08, 111.63) * mm, "end": v(-11.09, 111.67) * mm});
            skLineSegment(sketch, "E12785", {"start": v(-11.09, 111.67) * mm, "end": v(-11.1, 111.77) * mm});
            skLineSegment(sketch, "E12786", {"start": v(-11.1, 111.77) * mm, "end": v(-11.13, 111.95) * mm});
            skLineSegment(sketch, "E12787", {"start": v(-11.13, 111.95) * mm, "end": v(-11.14, 112.2) * mm});
            skLineSegment(sketch, "E12788", {"start": v(-11.14, 112.2) * mm, "end": v(-11.15, 112.53) * mm});
            skLineSegment(sketch, "E12789", {"start": v(-11.15, 112.53) * mm, "end": v(-11.13, 112.93) * mm});
            skLineSegment(sketch, "E12790", {"start": v(-11.13, 112.93) * mm, "end": v(-11.1, 113.4) * mm});
            skLineSegment(sketch, "E12791", {"start": v(-11.1, 113.4) * mm, "end": v(-11.02, 113.94) * mm});
            skLineSegment(sketch, "E12792", {"start": v(-11.02, 113.94) * mm, "end": v(-10.9, 114.55) * mm});
            skLineSegment(sketch, "E12793", {"start": v(-10.9, 114.55) * mm, "end": v(-10.74, 115.22) * mm});
            skLineSegment(sketch, "E12794", {"start": v(-10.74, 115.22) * mm, "end": v(-10.73, 115.25) * mm});
            skArc(sketch, "E12795", {"start": v(-10.73, 115.25) * mm, "mid": v(-9.64, 115.46) * mm, "end": v(-8.54, 115.62) * mm});
            skLineSegment(sketch, "E12796", {"start": v(-8.54, 115.62) * mm, "end": v(-8.52, 115.6) * mm});
            skLineSegment(sketch, "E12797", {"start": v(-8.52, 115.6) * mm, "end": v(-8.15, 115.02) * mm});
            skLineSegment(sketch, "E12798", {"start": v(-8.15, 115.02) * mm, "end": v(-7.84, 114.48) * mm});
            skLineSegment(sketch, "E12799", {"start": v(-7.84, 114.48) * mm, "end": v(-7.6, 114) * mm});
            skLineSegment(sketch, "E12800", {"start": v(-7.6, 114) * mm, "end": v(-7.4, 113.57) * mm});
            skLineSegment(sketch, "E12801", {"start": v(-7.4, 113.57) * mm, "end": v(-7.25, 113.2) * mm});
            skLineSegment(sketch, "E12802", {"start": v(-7.25, 113.2) * mm, "end": v(-7.15, 112.89) * mm});
            skLineSegment(sketch, "E12803", {"start": v(-7.15, 112.89) * mm, "end": v(-7.08, 112.64) * mm});
            skLineSegment(sketch, "E12804", {"start": v(-7.08, 112.64) * mm, "end": v(-7.04, 112.46) * mm});
            skLineSegment(sketch, "E12805", {"start": v(-7.04, 112.46) * mm, "end": v(-7.02, 112.36) * mm});
            skLineSegment(sketch, "E12806", {"start": v(-7.02, 112.36) * mm, "end": v(-7.02, 112.32) * mm});
            skLineSegment(sketch, "E12807", {"start": v(-7.02, 112.32) * mm, "end": v(-6.83, 110.4) * mm});
            skArc(sketch, "E12808", {"start": v(-6.83, 110.4) * mm, "mid": v(-5.2, 110.5) * mm, "end": v(-3.59, 110.51) * mm});
            skLineSegment(sketch, "E12809", {"start": v(-3.59, 110.51) * mm, "end": v(-3.54, 112.45) * mm});
            skLineSegment(sketch, "E12810", {"start": v(-3.54, 112.45) * mm, "end": v(-3.54, 112.49) * mm});
            skLineSegment(sketch, "E12811", {"start": v(-3.54, 112.49) * mm, "end": v(-3.53, 112.6) * mm});
            skLineSegment(sketch, "E12812", {"start": v(-3.53, 112.6) * mm, "end": v(-3.5, 112.78) * mm});
            skLineSegment(sketch, "E12813", {"start": v(-3.5, 112.78) * mm, "end": v(-3.45, 113.02) * mm});
            skLineSegment(sketch, "E12814", {"start": v(-3.45, 113.02) * mm, "end": v(-3.37, 113.34) * mm});
            skLineSegment(sketch, "E12815", {"start": v(-3.37, 113.34) * mm, "end": v(-3.25, 113.72) * mm});
            skLineSegment(sketch, "E12816", {"start": v(-3.25, 113.72) * mm, "end": v(-3.1, 114.17) * mm});
            skLineSegment(sketch, "E12817", {"start": v(-3.1, 114.17) * mm, "end": v(-2.88, 114.67) * mm});
            skLineSegment(sketch, "E12818", {"start": v(-2.88, 114.67) * mm, "end": v(-2.62, 115.22) * mm});
            skLineSegment(sketch, "E12819", {"start": v(-2.62, 115.22) * mm, "end": v(-2.29, 115.83) * mm});
            skLineSegment(sketch, "E12820", {"start": v(-2.29, 115.83) * mm, "end": v(-2.27, 115.86) * mm});
            skArc(sketch, "E12821", {"start": v(-2.27, 115.86) * mm, "mid": v(-1.16, 115.77) * mm, "end": v(-0.05, 115.65) * mm});
            skLineSegment(sketch, "E12822", {"start": v(-0.05, 115.65) * mm, "end": v(-0.04, 115.62) * mm});
            skLineSegment(sketch, "E12823", {"start": v(-0.04, 115.62) * mm, "end": v(0.17, 114.96) * mm});
            skLineSegment(sketch, "E12824", {"start": v(0.17, 114.96) * mm, "end": v(0.33, 114.37) * mm});
            skLineSegment(sketch, "E12825", {"start": v(0.33, 114.37) * mm, "end": v(0.44, 113.83) * mm});
            skLineSegment(sketch, "E12826", {"start": v(0.44, 113.83) * mm, "end": v(0.52, 113.37) * mm});
            skLineSegment(sketch, "E12827", {"start": v(0.52, 113.37) * mm, "end": v(0.56, 112.97) * mm});
            skLineSegment(sketch, "E12828", {"start": v(0.56, 112.97) * mm, "end": v(0.58, 112.65) * mm});
            skLineSegment(sketch, "E12829", {"start": v(0.58, 112.65) * mm, "end": v(0.58, 112.4) * mm});
            skLineSegment(sketch, "E12830", {"start": v(0.58, 112.4) * mm, "end": v(0.58, 112.21) * mm});
            skLineSegment(sketch, "E12831", {"start": v(0.58, 112.21) * mm, "end": v(0.57, 112.1) * mm});
            skLineSegment(sketch, "E12832", {"start": v(0.57, 112.1) * mm, "end": v(0.56, 112.07) * mm});
            skLineSegment(sketch, "E12833", {"start": v(0.56, 112.07) * mm, "end": v(0.25, 110.15) * mm});
            skArc(sketch, "E12834", {"start": v(0.25, 110.15) * mm, "mid": v(1.84, 109.84) * mm, "end": v(3.4, 109.43) * mm});
            skLineSegment(sketch, "E12835", {"start": v(3.4, 109.43) * mm, "end": v(3.95, 111.3) * mm});
            skLineSegment(sketch, "E12836", {"start": v(3.95, 111.3) * mm, "end": v(3.96, 111.33) * mm});
            skLineSegment(sketch, "E12837", {"start": v(3.96, 111.33) * mm, "end": v(4, 111.43) * mm});
            skLineSegment(sketch, "E12838", {"start": v(4, 111.43) * mm, "end": v(4.07, 111.6) * mm});
            skLineSegment(sketch, "E12839", {"start": v(4.07, 111.6) * mm, "end": v(4.19, 111.82) * mm});
            skLineSegment(sketch, "E12840", {"start": v(4.19, 111.82) * mm, "end": v(4.35, 112.1) * mm});
            skLineSegment(sketch, "E12841", {"start": v(4.35, 112.1) * mm, "end": v(4.56, 112.45) * mm});
            skLineSegment(sketch, "E12842", {"start": v(4.56, 112.45) * mm, "end": v(4.83, 112.83) * mm});
            skLineSegment(sketch, "E12843", {"start": v(4.83, 112.83) * mm, "end": v(5.16, 113.26) * mm});
            skLineSegment(sketch, "E12844", {"start": v(5.16, 113.26) * mm, "end": v(5.56, 113.73) * mm});
            skLineSegment(sketch, "E12845", {"start": v(5.56, 113.73) * mm, "end": v(6.04, 114.23) * mm});
            skLineSegment(sketch, "E12846", {"start": v(6.04, 114.23) * mm, "end": v(6.06, 114.25) * mm});
            skArc(sketch, "E12847", {"start": v(6.06, 114.25) * mm, "mid": v(7.11, 113.88) * mm, "end": v(8.15, 113.48) * mm});
            skLineSegment(sketch, "E12848", {"start": v(8.15, 113.48) * mm, "end": v(8.15, 113.45) * mm});
            skLineSegment(sketch, "E12849", {"start": v(8.15, 113.45) * mm, "end": v(8.18, 112.76) * mm});
            skLineSegment(sketch, "E12850", {"start": v(8.18, 112.76) * mm, "end": v(8.18, 112.14) * mm});
            skLineSegment(sketch, "E12851", {"start": v(8.18, 112.14) * mm, "end": v(8.16, 111.6) * mm});
            skLineSegment(sketch, "E12852", {"start": v(8.16, 111.6) * mm, "end": v(8.1, 111.13) * mm});
            skLineSegment(sketch, "E12853", {"start": v(8.1, 111.13) * mm, "end": v(8.05, 110.73) * mm});
            skLineSegment(sketch, "E12854", {"start": v(8.05, 110.73) * mm, "end": v(7.98, 110.41) * mm});
            skLineSegment(sketch, "E12855", {"start": v(7.98, 110.41) * mm, "end": v(7.92, 110.17) * mm});
            skLineSegment(sketch, "E12856", {"start": v(7.92, 110.17) * mm, "end": v(7.87, 110) * mm});
            skLineSegment(sketch, "E12857", {"start": v(7.87, 110) * mm, "end": v(7.83, 109.9) * mm});
            skLineSegment(sketch, "E12858", {"start": v(7.83, 109.9) * mm, "end": v(7.82, 109.86) * mm});
            skLineSegment(sketch, "E12859", {"start": v(7.82, 109.86) * mm, "end": v(7.02, 108.1) * mm});
            skArc(sketch, "E12860", {"start": v(7.02, 108.1) * mm, "mid": v(8.47, 107.38) * mm, "end": v(9.88, 106.58) * mm});
            skLineSegment(sketch, "E12861", {"start": v(9.88, 106.58) * mm, "end": v(10.89, 108.23) * mm});
            skLineSegment(sketch, "E12862", {"start": v(10.89, 108.23) * mm, "end": v(10.9, 108.26) * mm});
            skLineSegment(sketch, "E12863", {"start": v(10.9, 108.26) * mm, "end": v(10.97, 108.35) * mm});
            skLineSegment(sketch, "E12864", {"start": v(10.97, 108.35) * mm, "end": v(11.09, 108.5) * mm});
            skLineSegment(sketch, "E12865", {"start": v(11.09, 108.5) * mm, "end": v(11.25, 108.69) * mm});
            skLineSegment(sketch, "E12866", {"start": v(11.25, 108.69) * mm, "end": v(11.48, 108.92) * mm});
            skLineSegment(sketch, "E12867", {"start": v(11.48, 108.92) * mm, "end": v(11.77, 109.2) * mm});
            skLineSegment(sketch, "E12868", {"start": v(11.77, 109.2) * mm, "end": v(12.13, 109.5) * mm});
            skLineSegment(sketch, "E12869", {"start": v(12.13, 109.5) * mm, "end": v(12.57, 109.82) * mm});
            skLineSegment(sketch, "E12870", {"start": v(12.57, 109.82) * mm, "end": v(13.08, 110.17) * mm});
            skLineSegment(sketch, "E12871", {"start": v(13.08, 110.17) * mm, "end": v(13.67, 110.53) * mm});
            skLineSegment(sketch, "E12872", {"start": v(13.67, 110.53) * mm, "end": v(13.7, 110.55) * mm});
            skArc(sketch, "E12873", {"start": v(13.7, 110.55) * mm, "mid": v(14.61, 109.92) * mm, "end": v(15.5, 109.26) * mm});
            skLineSegment(sketch, "E12874", {"start": v(15.5, 109.26) * mm, "end": v(15.5, 109.23) * mm});
            skLineSegment(sketch, "E12875", {"start": v(15.5, 109.23) * mm, "end": v(15.36, 108.55) * mm});
            skLineSegment(sketch, "E12876", {"start": v(15.36, 108.55) * mm, "end": v(15.2, 107.96) * mm});
            skLineSegment(sketch, "E12877", {"start": v(15.2, 107.96) * mm, "end": v(15.03, 107.44) * mm});
            skLineSegment(sketch, "E12878", {"start": v(15.03, 107.44) * mm, "end": v(14.86, 107) * mm});
            skLineSegment(sketch, "E12879", {"start": v(14.86, 107) * mm, "end": v(14.7, 106.63) * mm});
            skLineSegment(sketch, "E12880", {"start": v(14.7, 106.63) * mm, "end": v(14.56, 106.34) * mm});
            skLineSegment(sketch, "E12881", {"start": v(14.56, 106.34) * mm, "end": v(14.43, 106.12) * mm});
            skLineSegment(sketch, "E12882", {"start": v(14.43, 106.12) * mm, "end": v(14.34, 105.97) * mm});
            skLineSegment(sketch, "E12883", {"start": v(14.34, 105.97) * mm, "end": v(14.27, 105.88) * mm});
            skLineSegment(sketch, "E12884", {"start": v(14.27, 105.88) * mm, "end": v(14.25, 105.85) * mm});
            skLineSegment(sketch, "E12885", {"start": v(14.25, 105.85) * mm, "end": v(13.02, 104.35) * mm});
            skArc(sketch, "E12886", {"start": v(13.02, 104.35) * mm, "mid": v(14.24, 103.28) * mm, "end": v(15.4, 102.15) * mm});
            skCircle(sketch, "E12887", {"center": v(-4.2, 83.41) * mm, "radius": 1.25 * mm});
            skLineSegment(sketch, "E12888", {"start": v(-7.2, 81.31) * mm, "end": v(-1.2, 81.31) * mm});
            skLineSegment(sketch, "E12889", {"start": v(-1.2, 81.31) * mm, "end": v(-1.2, 85.51) * mm});
            skLineSegment(sketch, "E12890", {"start": v(-1.2, 85.51) * mm, "end": v(-7.2, 85.51) * mm});
            skLineSegment(sketch, "E12891", {"start": v(-7.2, 85.51) * mm, "end": v(-7.2, 81.31) * mm});
            skCircle(sketch, "E12892", {"center": v(-4.2, 83.41) * mm, "radius": 3.75 * mm});
            skLineSegment(sketch, "E12893", {"start": v(113.39, 30.37) * mm, "end": v(114.83, 31.76) * mm});
            skLineSegment(sketch, "E12894", {"start": v(114.83, 31.76) * mm, "end": v(114.85, 31.78) * mm});
            skLineSegment(sketch, "E12895", {"start": v(114.85, 31.78) * mm, "end": v(114.93, 31.84) * mm});
            skLineSegment(sketch, "E12896", {"start": v(114.93, 31.84) * mm, "end": v(115.06, 31.94) * mm});
            skLineSegment(sketch, "E12897", {"start": v(115.06, 31.94) * mm, "end": v(115.25, 32.07) * mm});
            skLineSegment(sketch, "E12898", {"start": v(115.25, 32.07) * mm, "end": v(115.51, 32.22) * mm});
            skLineSegment(sketch, "E12899", {"start": v(115.51, 32.22) * mm, "end": v(115.83, 32.4) * mm});
            skLineSegment(sketch, "E12900", {"start": v(115.83, 32.4) * mm, "end": v(116.22, 32.58) * mm});
            skLineSegment(sketch, "E12901", {"start": v(116.22, 32.58) * mm, "end": v(116.68, 32.77) * mm});
            skLineSegment(sketch, "E12902", {"start": v(116.68, 32.77) * mm, "end": v(117.21, 32.96) * mm});
            skLineSegment(sketch, "E12903", {"start": v(117.21, 32.96) * mm, "end": v(117.82, 33.15) * mm});
            skLineSegment(sketch, "E12904", {"start": v(117.82, 33.15) * mm, "end": v(118.07, 33.21) * mm});
            skLineSegment(sketch, "E12905", {"start": v(118.07, 33.21) * mm, "end": v(119.48, 31.56) * mm});
            skLineSegment(sketch, "E12906", {"start": v(119.48, 31.56) * mm, "end": v(119.37, 31.32) * mm});
            skLineSegment(sketch, "E12907", {"start": v(119.37, 31.32) * mm, "end": v(119.08, 30.77) * mm});
            skLineSegment(sketch, "E12908", {"start": v(119.08, 30.77) * mm, "end": v(118.8, 30.28) * mm});
            skLineSegment(sketch, "E12909", {"start": v(118.8, 30.28) * mm, "end": v(118.53, 29.87) * mm});
            skLineSegment(sketch, "E12910", {"start": v(118.53, 29.87) * mm, "end": v(118.27, 29.53) * mm});
            skLineSegment(sketch, "E12911", {"start": v(118.27, 29.53) * mm, "end": v(118.05, 29.24) * mm});
            skLineSegment(sketch, "E12912", {"start": v(118.05, 29.24) * mm, "end": v(117.85, 29.02) * mm});
            skLineSegment(sketch, "E12913", {"start": v(117.85, 29.02) * mm, "end": v(117.68, 28.86) * mm});
            skLineSegment(sketch, "E12914", {"start": v(117.68, 28.86) * mm, "end": v(117.56, 28.75) * mm});
            skLineSegment(sketch, "E12915", {"start": v(117.56, 28.75) * mm, "end": v(117.49, 28.69) * mm});
            skLineSegment(sketch, "E12916", {"start": v(117.49, 28.69) * mm, "end": v(117.46, 28.67) * mm});
            skLineSegment(sketch, "E12917", {"start": v(117.46, 28.67) * mm, "end": v(115.82, 27.51) * mm});
            skLineSegment(sketch, "E12918", {"start": v(115.82, 27.51) * mm, "end": v(117.53, 24.8) * mm});
            skLineSegment(sketch, "E12919", {"start": v(117.53, 24.8) * mm, "end": v(119.3, 25.73) * mm});
            skLineSegment(sketch, "E12920", {"start": v(119.3, 25.73) * mm, "end": v(119.33, 25.75) * mm});
            skLineSegment(sketch, "E12921", {"start": v(119.33, 25.75) * mm, "end": v(119.43, 25.79) * mm});
            skLineSegment(sketch, "E12922", {"start": v(119.43, 25.79) * mm, "end": v(119.58, 25.85) * mm});
            skLineSegment(sketch, "E12923", {"start": v(119.58, 25.85) * mm, "end": v(119.8, 25.92) * mm});
            skLineSegment(sketch, "E12924", {"start": v(119.8, 25.92) * mm, "end": v(120.1, 26) * mm});
            skLineSegment(sketch, "E12925", {"start": v(120.1, 26) * mm, "end": v(120.45, 26.07) * mm});
            skLineSegment(sketch, "E12926", {"start": v(120.45, 26.07) * mm, "end": v(120.88, 26.14) * mm});
            skLineSegment(sketch, "E12927", {"start": v(120.88, 26.14) * mm, "end": v(121.37, 26.2) * mm});
            skLineSegment(sketch, "E12928", {"start": v(121.37, 26.2) * mm, "end": v(121.94, 26.23) * mm});
            skLineSegment(sketch, "E12929", {"start": v(121.94, 26.23) * mm, "end": v(122.57, 26.24) * mm});
            skLineSegment(sketch, "E12930", {"start": v(122.57, 26.24) * mm, "end": v(122.83, 26.23) * mm});
            skLineSegment(sketch, "E12931", {"start": v(122.83, 26.23) * mm, "end": v(123.71, 24.25) * mm});
            skLineSegment(sketch, "E12932", {"start": v(123.71, 24.25) * mm, "end": v(123.54, 24.06) * mm});
            skLineSegment(sketch, "E12933", {"start": v(123.54, 24.06) * mm, "end": v(123.1, 23.6) * mm});
            skLineSegment(sketch, "E12934", {"start": v(123.1, 23.6) * mm, "end": v(122.7, 23.22) * mm});
            skLineSegment(sketch, "E12935", {"start": v(122.7, 23.22) * mm, "end": v(122.32, 22.9) * mm});
            skLineSegment(sketch, "E12936", {"start": v(122.32, 22.9) * mm, "end": v(121.97, 22.64) * mm});
            skLineSegment(sketch, "E12937", {"start": v(121.97, 22.64) * mm, "end": v(121.67, 22.43) * mm});
            skLineSegment(sketch, "E12938", {"start": v(121.67, 22.43) * mm, "end": v(121.42, 22.28) * mm});
            skLineSegment(sketch, "E12939", {"start": v(121.42, 22.28) * mm, "end": v(121.22, 22.16) * mm});
            skLineSegment(sketch, "E12940", {"start": v(121.22, 22.16) * mm, "end": v(121.07, 22.1) * mm});
            skLineSegment(sketch, "E12941", {"start": v(121.07, 22.1) * mm, "end": v(120.98, 22.05) * mm});
            skLineSegment(sketch, "E12942", {"start": v(120.98, 22.05) * mm, "end": v(120.95, 22.04) * mm});
            skLineSegment(sketch, "E12943", {"start": v(120.95, 22.04) * mm, "end": v(119.04, 21.39) * mm});
            skLineSegment(sketch, "E12944", {"start": v(119.04, 21.39) * mm, "end": v(119.9, 18.31) * mm});
            skLineSegment(sketch, "E12945", {"start": v(119.9, 18.31) * mm, "end": v(121.88, 18.71) * mm});
            skLineSegment(sketch, "E12946", {"start": v(121.88, 18.71) * mm, "end": v(121.91, 18.72) * mm});
            skLineSegment(sketch, "E12947", {"start": v(121.91, 18.72) * mm, "end": v(122, 18.73) * mm});
            skLineSegment(sketch, "E12948", {"start": v(122, 18.73) * mm, "end": v(122.18, 18.75) * mm});
            skLineSegment(sketch, "E12949", {"start": v(122.18, 18.75) * mm, "end": v(122.4, 18.75) * mm});
            skLineSegment(sketch, "E12950", {"start": v(122.4, 18.75) * mm, "end": v(122.7, 18.75) * mm});
            skLineSegment(sketch, "E12951", {"start": v(122.7, 18.75) * mm, "end": v(123.07, 18.72) * mm});
            skLineSegment(sketch, "E12952", {"start": v(123.07, 18.72) * mm, "end": v(123.5, 18.67) * mm});
            skLineSegment(sketch, "E12953", {"start": v(123.5, 18.67) * mm, "end": v(124, 18.58) * mm});
            skLineSegment(sketch, "E12954", {"start": v(124, 18.58) * mm, "end": v(124.55, 18.46) * mm});
            skLineSegment(sketch, "E12955", {"start": v(124.55, 18.46) * mm, "end": v(125.15, 18.3) * mm});
            skLineSegment(sketch, "E12956", {"start": v(125.15, 18.3) * mm, "end": v(125.4, 18.21) * mm});
            skLineSegment(sketch, "E12957", {"start": v(125.4, 18.21) * mm, "end": v(125.68, 16.07) * mm});
            skLineSegment(sketch, "E12958", {"start": v(125.68, 16.07) * mm, "end": v(125.46, 15.93) * mm});
            skLineSegment(sketch, "E12959", {"start": v(125.46, 15.93) * mm, "end": v(124.91, 15.62) * mm});
            skLineSegment(sketch, "E12960", {"start": v(124.91, 15.62) * mm, "end": v(124.41, 15.36) * mm});
            skLineSegment(sketch, "E12961", {"start": v(124.41, 15.36) * mm, "end": v(123.96, 15.16) * mm});
            skLineSegment(sketch, "E12962", {"start": v(123.96, 15.16) * mm, "end": v(123.55, 15) * mm});
            skLineSegment(sketch, "E12963", {"start": v(123.55, 15) * mm, "end": v(123.2, 14.89) * mm});
            skLineSegment(sketch, "E12964", {"start": v(123.2, 14.89) * mm, "end": v(122.92, 14.8) * mm});
            skLineSegment(sketch, "E12965", {"start": v(122.92, 14.8) * mm, "end": v(122.7, 14.76) * mm});
            skLineSegment(sketch, "E12966", {"start": v(122.7, 14.76) * mm, "end": v(122.53, 14.73) * mm});
            skLineSegment(sketch, "E12967", {"start": v(122.53, 14.73) * mm, "end": v(122.43, 14.72) * mm});
            skLineSegment(sketch, "E12968", {"start": v(122.43, 14.72) * mm, "end": v(122.4, 14.71) * mm});
            skLineSegment(sketch, "E12969", {"start": v(122.4, 14.71) * mm, "end": v(120.38, 14.62) * mm});
            skLineSegment(sketch, "E12970", {"start": v(120.38, 14.62) * mm, "end": v(120.33, 11.43) * mm});
            skLineSegment(sketch, "E12971", {"start": v(120.33, 11.43) * mm, "end": v(122.34, 11.27) * mm});
            skLineSegment(sketch, "E12972", {"start": v(122.34, 11.27) * mm, "end": v(122.37, 11.26) * mm});
            skLineSegment(sketch, "E12973", {"start": v(122.37, 11.26) * mm, "end": v(122.47, 11.25) * mm});
            skLineSegment(sketch, "E12974", {"start": v(122.47, 11.25) * mm, "end": v(122.63, 11.21) * mm});
            skLineSegment(sketch, "E12975", {"start": v(122.63, 11.21) * mm, "end": v(122.86, 11.15) * mm});
            skLineSegment(sketch, "E12976", {"start": v(122.86, 11.15) * mm, "end": v(123.14, 11.06) * mm});
            skLineSegment(sketch, "E12977", {"start": v(123.14, 11.06) * mm, "end": v(123.49, 10.94) * mm});
            skLineSegment(sketch, "E12978", {"start": v(123.49, 10.94) * mm, "end": v(123.88, 10.77) * mm});
            skLineSegment(sketch, "E12979", {"start": v(123.88, 10.77) * mm, "end": v(124.33, 10.55) * mm});
            skLineSegment(sketch, "E12980", {"start": v(124.33, 10.55) * mm, "end": v(124.83, 10.28) * mm});
            skLineSegment(sketch, "E12981", {"start": v(124.83, 10.28) * mm, "end": v(125.36, 9.95) * mm});
            skLineSegment(sketch, "E12982", {"start": v(125.36, 9.95) * mm, "end": v(125.58, 9.8) * mm});
            skLineSegment(sketch, "E12983", {"start": v(125.58, 9.8) * mm, "end": v(125.23, 7.67) * mm});
            skLineSegment(sketch, "E12984", {"start": v(125.23, 7.67) * mm, "end": v(124.98, 7.6) * mm});
            skLineSegment(sketch, "E12985", {"start": v(124.98, 7.6) * mm, "end": v(124.36, 7.45) * mm});
            skLineSegment(sketch, "E12986", {"start": v(124.36, 7.45) * mm, "end": v(123.8, 7.35) * mm});
            skLineSegment(sketch, "E12987", {"start": v(123.8, 7.35) * mm, "end": v(123.31, 7.28) * mm});
            skLineSegment(sketch, "E12988", {"start": v(123.31, 7.28) * mm, "end": v(122.88, 7.24) * mm});
            skLineSegment(sketch, "E12989", {"start": v(122.88, 7.24) * mm, "end": v(122.52, 7.23) * mm});
            skLineSegment(sketch, "E12990", {"start": v(122.52, 7.23) * mm, "end": v(122.22, 7.23) * mm});
            skLineSegment(sketch, "E12991", {"start": v(122.22, 7.23) * mm, "end": v(121.99, 7.24) * mm});
            skLineSegment(sketch, "E12992", {"start": v(121.99, 7.24) * mm, "end": v(121.82, 7.26) * mm});
            skLineSegment(sketch, "E12993", {"start": v(121.82, 7.26) * mm, "end": v(121.72, 7.28) * mm});
            skLineSegment(sketch, "E12994", {"start": v(121.72, 7.28) * mm, "end": v(121.69, 7.28) * mm});
            skLineSegment(sketch, "E12995", {"start": v(121.69, 7.28) * mm, "end": v(119.73, 7.75) * mm});
            skLineSegment(sketch, "E12996", {"start": v(119.73, 7.75) * mm, "end": v(118.77, 4.7) * mm});
            skLineSegment(sketch, "E12997", {"start": v(118.77, 4.7) * mm, "end": v(120.65, 4) * mm});
            skLineSegment(sketch, "E12998", {"start": v(120.65, 4) * mm, "end": v(120.68, 3.98) * mm});
            skLineSegment(sketch, "E12999", {"start": v(120.68, 3.98) * mm, "end": v(120.77, 3.94) * mm});
            skLineSegment(sketch, "E13000", {"start": v(120.77, 3.94) * mm, "end": v(120.92, 3.86) * mm});
            skLineSegment(sketch, "E13001", {"start": v(120.92, 3.86) * mm, "end": v(121.12, 3.74) * mm});
            skLineSegment(sketch, "E13002", {"start": v(121.12, 3.74) * mm, "end": v(121.36, 3.57) * mm});
            skLineSegment(sketch, "E13003", {"start": v(121.36, 3.57) * mm, "end": v(121.66, 3.36) * mm});
            skLineSegment(sketch, "E13004", {"start": v(121.66, 3.36) * mm, "end": v(121.99, 3.09) * mm});
            skLineSegment(sketch, "E13005", {"start": v(121.99, 3.09) * mm, "end": v(122.36, 2.75) * mm});
            skLineSegment(sketch, "E13006", {"start": v(122.36, 2.75) * mm, "end": v(122.75, 2.36) * mm});
            skLineSegment(sketch, "E13007", {"start": v(122.75, 2.36) * mm, "end": v(123.17, 1.9) * mm});
            skLineSegment(sketch, "E13008", {"start": v(123.17, 1.9) * mm, "end": v(123.34, 1.69) * mm});
            skLineSegment(sketch, "E13009", {"start": v(123.34, 1.69) * mm, "end": v(122.4, -0.26) * mm});
            skLineSegment(sketch, "E13010", {"start": v(122.4, -0.26) * mm, "end": v(122.13, -0.26) * mm});
            skLineSegment(sketch, "E13011", {"start": v(122.13, -0.26) * mm, "end": v(121.5, -0.23) * mm});
            skLineSegment(sketch, "E13012", {"start": v(121.5, -0.23) * mm, "end": v(120.94, -0.18) * mm});
            skLineSegment(sketch, "E13013", {"start": v(120.94, -0.18) * mm, "end": v(120.45, -0.1) * mm});
            skLineSegment(sketch, "E13014", {"start": v(120.45, -0.1) * mm, "end": v(120.02, -0.02) * mm});
            skLineSegment(sketch, "E13015", {"start": v(120.02, -0.02) * mm, "end": v(119.67, 0.07) * mm});
            skLineSegment(sketch, "E13016", {"start": v(119.67, 0.07) * mm, "end": v(119.38, 0.15) * mm});
            skLineSegment(sketch, "E13017", {"start": v(119.38, 0.15) * mm, "end": v(119.16, 0.23) * mm});
            skLineSegment(sketch, "E13018", {"start": v(119.16, 0.23) * mm, "end": v(119, 0.3) * mm});
            skLineSegment(sketch, "E13019", {"start": v(119, 0.3) * mm, "end": v(118.92, 0.33) * mm});
            skLineSegment(sketch, "E13020", {"start": v(118.92, 0.33) * mm, "end": v(118.89, 0.35) * mm});
            skLineSegment(sketch, "E13021", {"start": v(118.89, 0.35) * mm, "end": v(117.14, 1.34) * mm});
            skLineSegment(sketch, "E13022", {"start": v(117.14, 1.34) * mm, "end": v(115.35, -1.31) * mm});
            skLineSegment(sketch, "E13023", {"start": v(115.35, -1.31) * mm, "end": v(116.95, -2.52) * mm});
            skLineSegment(sketch, "E13024", {"start": v(116.95, -2.52) * mm, "end": v(116.97, -2.54) * mm});
            skLineSegment(sketch, "E13025", {"start": v(116.97, -2.54) * mm, "end": v(117.05, -2.6) * mm});
            skLineSegment(sketch, "E13026", {"start": v(117.05, -2.6) * mm, "end": v(117.16, -2.72) * mm});
            skLineSegment(sketch, "E13027", {"start": v(117.16, -2.72) * mm, "end": v(117.32, -2.9) * mm});
            skLineSegment(sketch, "E13028", {"start": v(117.32, -2.9) * mm, "end": v(117.51, -3.12) * mm});
            skLineSegment(sketch, "E13029", {"start": v(117.51, -3.12) * mm, "end": v(117.73, -3.4) * mm});
            skLineSegment(sketch, "E13030", {"start": v(117.73, -3.4) * mm, "end": v(117.97, -3.76) * mm});
            skLineSegment(sketch, "E13031", {"start": v(117.97, -3.76) * mm, "end": v(118.23, -4.18) * mm});
            skLineSegment(sketch, "E13032", {"start": v(118.23, -4.18) * mm, "end": v(118.5, -4.67) * mm});
            skLineSegment(sketch, "E13033", {"start": v(118.5, -4.67) * mm, "end": v(118.77, -5.24) * mm});
            skLineSegment(sketch, "E13034", {"start": v(118.77, -5.24) * mm, "end": v(118.87, -5.48) * mm});
            skLineSegment(sketch, "E13035", {"start": v(118.87, -5.48) * mm, "end": v(117.4, -7.08) * mm});
            skLineSegment(sketch, "E13036", {"start": v(117.4, -7.08) * mm, "end": v(117.16, -7.01) * mm});
            skLineSegment(sketch, "E13037", {"start": v(117.16, -7.01) * mm, "end": v(116.56, -6.8) * mm});
            skLineSegment(sketch, "E13038", {"start": v(116.56, -6.8) * mm, "end": v(116.03, -6.6) * mm});
            skLineSegment(sketch, "E13039", {"start": v(116.03, -6.6) * mm, "end": v(115.58, -6.4) * mm});
            skLineSegment(sketch, "E13040", {"start": v(115.58, -6.4) * mm, "end": v(115.2, -6.2) * mm});
            skLineSegment(sketch, "E13041", {"start": v(115.2, -6.2) * mm, "end": v(114.88, -6.01) * mm});
            skLineSegment(sketch, "E13042", {"start": v(114.88, -6.01) * mm, "end": v(114.63, -5.85) * mm});
            skLineSegment(sketch, "E13043", {"start": v(114.63, -5.85) * mm, "end": v(114.44, -5.72) * mm});
            skLineSegment(sketch, "E13044", {"start": v(114.44, -5.72) * mm, "end": v(114.31, -5.61) * mm});
            skLineSegment(sketch, "E13045", {"start": v(114.31, -5.61) * mm, "end": v(114.24, -5.55) * mm});
            skLineSegment(sketch, "E13046", {"start": v(114.24, -5.55) * mm, "end": v(114.21, -5.53) * mm});
            skLineSegment(sketch, "E13047", {"start": v(114.21, -5.53) * mm, "end": v(112.82, -4.1) * mm});
            skLineSegment(sketch, "E13048", {"start": v(112.82, -4.1) * mm, "end": v(110.34, -6.14) * mm});
            skLineSegment(sketch, "E13049", {"start": v(110.34, -6.14) * mm, "end": v(111.53, -7.74) * mm});
            skLineSegment(sketch, "E13050", {"start": v(111.53, -7.74) * mm, "end": v(111.55, -7.77) * mm});
            skLineSegment(sketch, "E13051", {"start": v(111.55, -7.77) * mm, "end": v(111.6, -7.85) * mm});
            skLineSegment(sketch, "E13052", {"start": v(111.6, -7.85) * mm, "end": v(111.68, -8) * mm});
            skLineSegment(sketch, "E13053", {"start": v(111.68, -8) * mm, "end": v(111.79, -8.2) * mm});
            skLineSegment(sketch, "E13054", {"start": v(111.79, -8.2) * mm, "end": v(111.9, -8.47) * mm});
            skLineSegment(sketch, "E13055", {"start": v(111.9, -8.47) * mm, "end": v(112.03, -8.81) * mm});
            skLineSegment(sketch, "E13056", {"start": v(112.03, -8.81) * mm, "end": v(112.16, -9.22) * mm});
            skLineSegment(sketch, "E13057", {"start": v(112.16, -9.22) * mm, "end": v(112.29, -9.7) * mm});
            skLineSegment(sketch, "E13058", {"start": v(112.29, -9.7) * mm, "end": v(112.4, -10.24) * mm});
            skLineSegment(sketch, "E13059", {"start": v(112.4, -10.24) * mm, "end": v(112.5, -10.85) * mm});
            skLineSegment(sketch, "E13060", {"start": v(112.5, -10.85) * mm, "end": v(112.53, -11.11) * mm});
            skLineSegment(sketch, "E13061", {"start": v(112.53, -11.11) * mm, "end": v(110.67, -12.25) * mm});
            skLineSegment(sketch, "E13062", {"start": v(110.67, -12.25) * mm, "end": v(110.45, -12.1) * mm});
            skLineSegment(sketch, "E13063", {"start": v(110.45, -12.1) * mm, "end": v(109.93, -11.75) * mm});
            skLineSegment(sketch, "E13064", {"start": v(109.93, -11.75) * mm, "end": v(109.49, -11.4) * mm});
            skLineSegment(sketch, "E13065", {"start": v(109.49, -11.4) * mm, "end": v(109.11, -11.08) * mm});
            skLineSegment(sketch, "E13066", {"start": v(109.11, -11.08) * mm, "end": v(108.8, -10.78) * mm});
            skLineSegment(sketch, "E13067", {"start": v(108.8, -10.78) * mm, "end": v(108.55, -10.52) * mm});
            skLineSegment(sketch, "E13068", {"start": v(108.55, -10.52) * mm, "end": v(108.36, -10.3) * mm});
            skLineSegment(sketch, "E13069", {"start": v(108.36, -10.3) * mm, "end": v(108.21, -10.11) * mm});
            skLineSegment(sketch, "E13070", {"start": v(108.21, -10.11) * mm, "end": v(108.12, -9.98) * mm});
            skLineSegment(sketch, "E13071", {"start": v(108.12, -9.98) * mm, "end": v(108.07, -9.9) * mm});
            skLineSegment(sketch, "E13072", {"start": v(108.07, -9.9) * mm, "end": v(108.05, -9.87) * mm});
            skLineSegment(sketch, "E13073", {"start": v(108.05, -9.87) * mm, "end": v(107.12, -8.1) * mm});
            skLineSegment(sketch, "E13074", {"start": v(107.12, -8.1) * mm, "end": v(104.16, -9.38) * mm});
            skLineSegment(sketch, "E13075", {"start": v(104.16, -9.38) * mm, "end": v(104.84, -11.25) * mm});
            skLineSegment(sketch, "E13076", {"start": v(104.84, -11.25) * mm, "end": v(104.85, -11.28) * mm});
            skLineSegment(sketch, "E13077", {"start": v(104.85, -11.28) * mm, "end": v(104.88, -11.37) * mm});
            skLineSegment(sketch, "E13078", {"start": v(104.88, -11.37) * mm, "end": v(104.92, -11.53) * mm});
            skLineSegment(sketch, "E13079", {"start": v(104.92, -11.53) * mm, "end": v(104.95, -11.76) * mm});
            skLineSegment(sketch, "E13080", {"start": v(104.95, -11.76) * mm, "end": v(105, -12.05) * mm});
            skLineSegment(sketch, "E13081", {"start": v(105, -12.05) * mm, "end": v(105.02, -12.41) * mm});
            skLineSegment(sketch, "E13082", {"start": v(105.02, -12.41) * mm, "end": v(105.03, -12.84) * mm});
            skLineSegment(sketch, "E13083", {"start": v(105.03, -12.84) * mm, "end": v(105.01, -13.33) * mm});
            skLineSegment(sketch, "E13084", {"start": v(105.01, -13.33) * mm, "end": v(104.97, -13.89) * mm});
            skLineSegment(sketch, "E13085", {"start": v(104.97, -13.89) * mm, "end": v(104.88, -14.5) * mm});
            skLineSegment(sketch, "E13086", {"start": v(104.88, -14.5) * mm, "end": v(104.84, -14.76) * mm});
            skLineSegment(sketch, "E13087", {"start": v(104.84, -14.76) * mm, "end": v(102.73, -15.33) * mm});
            skLineSegment(sketch, "E13088", {"start": v(102.73, -15.33) * mm, "end": v(102.55, -15.14) * mm});
            skLineSegment(sketch, "E13089", {"start": v(102.55, -15.14) * mm, "end": v(102.16, -14.65) * mm});
            skLineSegment(sketch, "E13090", {"start": v(102.16, -14.65) * mm, "end": v(101.83, -14.2) * mm});
            skLineSegment(sketch, "E13091", {"start": v(101.83, -14.2) * mm, "end": v(101.57, -13.78) * mm});
            skLineSegment(sketch, "E13092", {"start": v(101.57, -13.78) * mm, "end": v(101.35, -13.4) * mm});
            skLineSegment(sketch, "E13093", {"start": v(101.35, -13.4) * mm, "end": v(101.19, -13.09) * mm});
            skLineSegment(sketch, "E13094", {"start": v(101.19, -13.09) * mm, "end": v(101.06, -12.82) * mm});
            skLineSegment(sketch, "E13095", {"start": v(101.06, -12.82) * mm, "end": v(100.98, -12.6) * mm});
            skLineSegment(sketch, "E13096", {"start": v(100.98, -12.6) * mm, "end": v(100.93, -12.45) * mm});
            skLineSegment(sketch, "E13097", {"start": v(100.93, -12.45) * mm, "end": v(100.9, -12.35) * mm});
            skLineSegment(sketch, "E13098", {"start": v(100.9, -12.35) * mm, "end": v(100.9, -12.32) * mm});
            skLineSegment(sketch, "E13099", {"start": v(100.9, -12.32) * mm, "end": v(100.5, -10.37) * mm});
            skLineSegment(sketch, "E13100", {"start": v(100.5, -10.37) * mm, "end": v(97.3, -10.78) * mm});
            skLineSegment(sketch, "E13101", {"start": v(97.3, -10.78) * mm, "end": v(97.42, -12.76) * mm});
            skLineSegment(sketch, "E13102", {"start": v(97.42, -12.76) * mm, "end": v(97.42, -12.8) * mm});
            skLineSegment(sketch, "E13103", {"start": v(97.42, -12.8) * mm, "end": v(97.42, -12.89) * mm});
            skLineSegment(sketch, "E13104", {"start": v(97.42, -12.89) * mm, "end": v(97.4, -13.05) * mm});
            skLineSegment(sketch, "E13105", {"start": v(97.4, -13.05) * mm, "end": v(97.38, -13.28) * mm});
            skLineSegment(sketch, "E13106", {"start": v(97.38, -13.28) * mm, "end": v(97.33, -13.57) * mm});
            skLineSegment(sketch, "E13107", {"start": v(97.33, -13.57) * mm, "end": v(97.25, -13.92) * mm});
            skLineSegment(sketch, "E13108", {"start": v(97.25, -13.92) * mm, "end": v(97.14, -14.33) * mm});
            skLineSegment(sketch, "E13109", {"start": v(97.14, -14.33) * mm, "end": v(96.99, -14.8) * mm});
            skLineSegment(sketch, "E13110", {"start": v(96.99, -14.8) * mm, "end": v(96.79, -15.32) * mm});
            skLineSegment(sketch, "E13111", {"start": v(96.79, -15.32) * mm, "end": v(96.53, -15.9) * mm});
            skLineSegment(sketch, "E13112", {"start": v(96.53, -15.9) * mm, "end": v(96.41, -16.12) * mm});
            skLineSegment(sketch, "E13113", {"start": v(96.41, -16.12) * mm, "end": v(94.22, -16.09) * mm});
            skLineSegment(sketch, "E13114", {"start": v(94.22, -16.09) * mm, "end": v(94.11, -15.85) * mm});
            skLineSegment(sketch, "E13115", {"start": v(94.11, -15.85) * mm, "end": v(93.88, -15.28) * mm});
            skLineSegment(sketch, "E13116", {"start": v(93.88, -15.28) * mm, "end": v(93.7, -14.75) * mm});
            skLineSegment(sketch, "E13117", {"start": v(93.7, -14.75) * mm, "end": v(93.55, -14.28) * mm});
            skLineSegment(sketch, "E13118", {"start": v(93.55, -14.28) * mm, "end": v(93.45, -13.86) * mm});
            skLineSegment(sketch, "E13119", {"start": v(93.45, -13.86) * mm, "end": v(93.39, -13.5) * mm});
            skLineSegment(sketch, "E13120", {"start": v(93.39, -13.5) * mm, "end": v(93.35, -13.22) * mm});
            skLineSegment(sketch, "E13121", {"start": v(93.35, -13.22) * mm, "end": v(93.33, -12.99) * mm});
            skLineSegment(sketch, "E13122", {"start": v(93.33, -12.99) * mm, "end": v(93.32, -12.82) * mm});
            skLineSegment(sketch, "E13123", {"start": v(93.32, -12.82) * mm, "end": v(93.32, -12.72) * mm});
            skLineSegment(sketch, "E13124", {"start": v(93.32, -12.72) * mm, "end": v(93.33, -12.7) * mm});
            skLineSegment(sketch, "E13125", {"start": v(93.33, -12.7) * mm, "end": v(93.51, -10.71) * mm});
            skLineSegment(sketch, "E13126", {"start": v(93.51, -10.71) * mm, "end": v(90.32, -10.2) * mm});
            skLineSegment(sketch, "E13127", {"start": v(90.32, -10.2) * mm, "end": v(89.87, -12.15) * mm});
            skLineSegment(sketch, "E13128", {"start": v(89.87, -12.15) * mm, "end": v(89.86, -12.18) * mm});
            skLineSegment(sketch, "E13129", {"start": v(89.86, -12.18) * mm, "end": v(89.83, -12.27) * mm});
            skLineSegment(sketch, "E13130", {"start": v(89.83, -12.27) * mm, "end": v(89.77, -12.43) * mm});
            skLineSegment(sketch, "E13131", {"start": v(89.77, -12.43) * mm, "end": v(89.68, -12.64) * mm});
            skLineSegment(sketch, "E13132", {"start": v(89.68, -12.64) * mm, "end": v(89.55, -12.9) * mm});
            skLineSegment(sketch, "E13133", {"start": v(89.55, -12.9) * mm, "end": v(89.38, -13.22) * mm});
            skLineSegment(sketch, "E13134", {"start": v(89.38, -13.22) * mm, "end": v(89.15, -13.58) * mm});
            skLineSegment(sketch, "E13135", {"start": v(89.15, -13.58) * mm, "end": v(88.87, -13.99) * mm});
            skLineSegment(sketch, "E13136", {"start": v(88.87, -13.99) * mm, "end": v(88.52, -14.43) * mm});
            skLineSegment(sketch, "E13137", {"start": v(88.52, -14.43) * mm, "end": v(88.12, -14.9) * mm});
            skLineSegment(sketch, "E13138", {"start": v(88.12, -14.9) * mm, "end": v(87.94, -15.1) * mm});
            skLineSegment(sketch, "E13139", {"start": v(87.94, -15.1) * mm, "end": v(85.85, -14.46) * mm});
            skLineSegment(sketch, "E13140", {"start": v(85.85, -14.46) * mm, "end": v(85.8, -14.2) * mm});
            skLineSegment(sketch, "E13141", {"start": v(85.8, -14.2) * mm, "end": v(85.75, -13.58) * mm});
            skLineSegment(sketch, "E13142", {"start": v(85.75, -13.58) * mm, "end": v(85.72, -13.02) * mm});
            skLineSegment(sketch, "E13143", {"start": v(85.72, -13.02) * mm, "end": v(85.72, -12.53) * mm});
            skLineSegment(sketch, "E13144", {"start": v(85.72, -12.53) * mm, "end": v(85.75, -12.1) * mm});
            skLineSegment(sketch, "E13145", {"start": v(85.75, -12.1) * mm, "end": v(85.78, -11.75) * mm});
            skLineSegment(sketch, "E13146", {"start": v(85.78, -11.75) * mm, "end": v(85.83, -11.46) * mm});
            skLineSegment(sketch, "E13147", {"start": v(85.83, -11.46) * mm, "end": v(85.88, -11.23) * mm});
            skLineSegment(sketch, "E13148", {"start": v(85.88, -11.23) * mm, "end": v(85.92, -11.07) * mm});
            skLineSegment(sketch, "E13149", {"start": v(85.92, -11.07) * mm, "end": v(85.95, -10.98) * mm});
            skLineSegment(sketch, "E13150", {"start": v(85.95, -10.98) * mm, "end": v(85.96, -10.95) * mm});
            skLineSegment(sketch, "E13151", {"start": v(85.96, -10.95) * mm, "end": v(86.7, -9.1) * mm});
            skLineSegment(sketch, "E13152", {"start": v(86.7, -9.1) * mm, "end": v(83.78, -7.73) * mm});
            skLineSegment(sketch, "E13153", {"start": v(83.78, -7.73) * mm, "end": v(82.8, -9.46) * mm});
            skLineSegment(sketch, "E13154", {"start": v(82.8, -9.46) * mm, "end": v(82.78, -9.5) * mm});
            skLineSegment(sketch, "E13155", {"start": v(82.78, -9.5) * mm, "end": v(82.72, -9.57) * mm});
            skLineSegment(sketch, "E13156", {"start": v(82.72, -9.57) * mm, "end": v(82.63, -9.7) * mm});
            skLineSegment(sketch, "E13157", {"start": v(82.63, -9.7) * mm, "end": v(82.48, -9.88) * mm});
            skLineSegment(sketch, "E13158", {"start": v(82.48, -9.88) * mm, "end": v(82.28, -10.1) * mm});
            skLineSegment(sketch, "E13159", {"start": v(82.28, -10.1) * mm, "end": v(82.02, -10.36) * mm});
            skLineSegment(sketch, "E13160", {"start": v(82.02, -10.36) * mm, "end": v(81.7, -10.64) * mm});
            skLineSegment(sketch, "E13161", {"start": v(81.7, -10.64) * mm, "end": v(81.3, -10.95) * mm});
            skLineSegment(sketch, "E13162", {"start": v(81.3, -10.95) * mm, "end": v(80.85, -11.28) * mm});
            skLineSegment(sketch, "E13163", {"start": v(80.85, -11.28) * mm, "end": v(80.33, -11.63) * mm});
            skLineSegment(sketch, "E13164", {"start": v(80.33, -11.63) * mm, "end": v(80.1, -11.76) * mm});
            skLineSegment(sketch, "E13165", {"start": v(80.1, -11.76) * mm, "end": v(78.28, -10.56) * mm});
            skLineSegment(sketch, "E13166", {"start": v(78.28, -10.56) * mm, "end": v(78.31, -10.3) * mm});
            skLineSegment(sketch, "E13167", {"start": v(78.31, -10.3) * mm, "end": v(78.43, -9.7) * mm});
            skLineSegment(sketch, "E13168", {"start": v(78.43, -9.7) * mm, "end": v(78.57, -9.15) * mm});
            skLineSegment(sketch, "E13169", {"start": v(78.57, -9.15) * mm, "end": v(78.7, -8.68) * mm});
            skLineSegment(sketch, "E13170", {"start": v(78.7, -8.68) * mm, "end": v(78.85, -8.28) * mm});
            skLineSegment(sketch, "E13171", {"start": v(78.85, -8.28) * mm, "end": v(79, -7.95) * mm});
            skLineSegment(sketch, "E13172", {"start": v(79, -7.95) * mm, "end": v(79.12, -7.68) * mm});
            skLineSegment(sketch, "E13173", {"start": v(79.12, -7.68) * mm, "end": v(79.23, -7.48) * mm});
            skLineSegment(sketch, "E13174", {"start": v(79.23, -7.48) * mm, "end": v(79.31, -7.34) * mm});
            skLineSegment(sketch, "E13175", {"start": v(79.31, -7.34) * mm, "end": v(79.37, -7.25) * mm});
            skLineSegment(sketch, "E13176", {"start": v(79.37, -7.25) * mm, "end": v(79.39, -7.23) * mm});
            skLineSegment(sketch, "E13177", {"start": v(79.39, -7.23) * mm, "end": v(80.63, -5.66) * mm});
            skLineSegment(sketch, "E13178", {"start": v(80.63, -5.66) * mm, "end": v(78.22, -3.54) * mm});
            skLineSegment(sketch, "E13179", {"start": v(78.22, -3.54) * mm, "end": v(76.78, -4.93) * mm});
            skLineSegment(sketch, "E13180", {"start": v(76.78, -4.93) * mm, "end": v(76.75, -4.95) * mm});
            skLineSegment(sketch, "E13181", {"start": v(76.75, -4.95) * mm, "end": v(76.68, -5.01) * mm});
            skLineSegment(sketch, "E13182", {"start": v(76.68, -5.01) * mm, "end": v(76.54, -5.11) * mm});
            skLineSegment(sketch, "E13183", {"start": v(76.54, -5.11) * mm, "end": v(76.35, -5.24) * mm});
            skLineSegment(sketch, "E13184", {"start": v(76.35, -5.24) * mm, "end": v(76.1, -5.4) * mm});
            skLineSegment(sketch, "E13185", {"start": v(76.1, -5.4) * mm, "end": v(75.78, -5.57) * mm});
            skLineSegment(sketch, "E13186", {"start": v(75.78, -5.57) * mm, "end": v(75.39, -5.75) * mm});
            skLineSegment(sketch, "E13187", {"start": v(75.39, -5.75) * mm, "end": v(74.93, -5.94) * mm});
            skLineSegment(sketch, "E13188", {"start": v(74.93, -5.94) * mm, "end": v(74.4, -6.13) * mm});
            skLineSegment(sketch, "E13189", {"start": v(74.4, -6.13) * mm, "end": v(73.8, -6.32) * mm});
            skLineSegment(sketch, "E13190", {"start": v(73.8, -6.32) * mm, "end": v(73.53, -6.38) * mm});
            skLineSegment(sketch, "E13191", {"start": v(73.53, -6.38) * mm, "end": v(72.13, -4.73) * mm});
            skLineSegment(sketch, "E13192", {"start": v(72.13, -4.73) * mm, "end": v(72.24, -4.5) * mm});
            skLineSegment(sketch, "E13193", {"start": v(72.24, -4.5) * mm, "end": v(72.53, -3.94) * mm});
            skLineSegment(sketch, "E13194", {"start": v(72.53, -3.94) * mm, "end": v(72.8, -3.46) * mm});
            skLineSegment(sketch, "E13195", {"start": v(72.8, -3.46) * mm, "end": v(73.08, -3.04) * mm});
            skLineSegment(sketch, "E13196", {"start": v(73.08, -3.04) * mm, "end": v(73.33, -2.7) * mm});
            skLineSegment(sketch, "E13197", {"start": v(73.33, -2.7) * mm, "end": v(73.56, -2.42) * mm});
            skLineSegment(sketch, "E13198", {"start": v(73.56, -2.42) * mm, "end": v(73.76, -2.2) * mm});
            skLineSegment(sketch, "E13199", {"start": v(73.76, -2.2) * mm, "end": v(73.92, -2.03) * mm});
            skLineSegment(sketch, "E13200", {"start": v(73.92, -2.03) * mm, "end": v(74.04, -1.92) * mm});
            skLineSegment(sketch, "E13201", {"start": v(74.04, -1.92) * mm, "end": v(74.12, -1.86) * mm});
            skLineSegment(sketch, "E13202", {"start": v(74.12, -1.86) * mm, "end": v(74.15, -1.84) * mm});
            skLineSegment(sketch, "E13203", {"start": v(74.15, -1.84) * mm, "end": v(75.79, -0.68) * mm});
            skLineSegment(sketch, "E13204", {"start": v(75.79, -0.68) * mm, "end": v(74.08, 2.03) * mm});
            skLineSegment(sketch, "E13205", {"start": v(74.08, 2.03) * mm, "end": v(72.3, 1.1) * mm});
            skLineSegment(sketch, "E13206", {"start": v(72.3, 1.1) * mm, "end": v(72.27, 1.08) * mm});
            skLineSegment(sketch, "E13207", {"start": v(72.27, 1.08) * mm, "end": v(72.18, 1.04) * mm});
            skLineSegment(sketch, "E13208", {"start": v(72.18, 1.04) * mm, "end": v(72.03, 0.98) * mm});
            skLineSegment(sketch, "E13209", {"start": v(72.03, 0.98) * mm, "end": v(71.8, 0.91) * mm});
            skLineSegment(sketch, "E13210", {"start": v(71.8, 0.91) * mm, "end": v(71.51, 0.83) * mm});
            skLineSegment(sketch, "E13211", {"start": v(71.51, 0.83) * mm, "end": v(71.16, 0.76) * mm});
            skLineSegment(sketch, "E13212", {"start": v(71.16, 0.76) * mm, "end": v(70.73, 0.69) * mm});
            skLineSegment(sketch, "E13213", {"start": v(70.73, 0.69) * mm, "end": v(70.23, 0.63) * mm});
            skLineSegment(sketch, "E13214", {"start": v(70.23, 0.63) * mm, "end": v(69.67, 0.6) * mm});
            skLineSegment(sketch, "E13215", {"start": v(69.67, 0.6) * mm, "end": v(69.04, 0.59) * mm});
            skLineSegment(sketch, "E13216", {"start": v(69.04, 0.59) * mm, "end": v(68.77, 0.6) * mm});
            skLineSegment(sketch, "E13217", {"start": v(68.77, 0.6) * mm, "end": v(67.9, 2.57) * mm});
            skLineSegment(sketch, "E13218", {"start": v(67.9, 2.57) * mm, "end": v(68.07, 2.77) * mm});
            skLineSegment(sketch, "E13219", {"start": v(68.07, 2.77) * mm, "end": v(68.5, 3.22) * mm});
            skLineSegment(sketch, "E13220", {"start": v(68.5, 3.22) * mm, "end": v(68.91, 3.6) * mm});
            skLineSegment(sketch, "E13221", {"start": v(68.91, 3.6) * mm, "end": v(69.3, 3.93) * mm});
            skLineSegment(sketch, "E13222", {"start": v(69.3, 3.93) * mm, "end": v(69.63, 4.19) * mm});
            skLineSegment(sketch, "E13223", {"start": v(69.63, 4.19) * mm, "end": v(69.93, 4.4) * mm});
            skLineSegment(sketch, "E13224", {"start": v(69.93, 4.4) * mm, "end": v(70.19, 4.55) * mm});
            skLineSegment(sketch, "E13225", {"start": v(70.19, 4.55) * mm, "end": v(70.39, 4.66) * mm});
            skLineSegment(sketch, "E13226", {"start": v(70.39, 4.66) * mm, "end": v(70.54, 4.74) * mm});
            skLineSegment(sketch, "E13227", {"start": v(70.54, 4.74) * mm, "end": v(70.63, 4.78) * mm});
            skLineSegment(sketch, "E13228", {"start": v(70.63, 4.78) * mm, "end": v(70.66, 4.79) * mm});
            skLineSegment(sketch, "E13229", {"start": v(70.66, 4.79) * mm, "end": v(72.57, 5.44) * mm});
            skLineSegment(sketch, "E13230", {"start": v(72.57, 5.44) * mm, "end": v(71.7, 8.51) * mm});
            skLineSegment(sketch, "E13231", {"start": v(71.7, 8.51) * mm, "end": v(69.73, 8.11) * mm});
            skLineSegment(sketch, "E13232", {"start": v(69.73, 8.11) * mm, "end": v(69.7, 8.1) * mm});
            skLineSegment(sketch, "E13233", {"start": v(69.7, 8.1) * mm, "end": v(69.6, 8.1) * mm});
            skLineSegment(sketch, "E13234", {"start": v(69.6, 8.1) * mm, "end": v(69.43, 8.08) * mm});
            skLineSegment(sketch, "E13235", {"start": v(69.43, 8.08) * mm, "end": v(69.2, 8.08) * mm});
            skLineSegment(sketch, "E13236", {"start": v(69.2, 8.08) * mm, "end": v(68.9, 8.08) * mm});
            skLineSegment(sketch, "E13237", {"start": v(68.9, 8.08) * mm, "end": v(68.53, 8.1) * mm});
            skLineSegment(sketch, "E13238", {"start": v(68.53, 8.1) * mm, "end": v(68.1, 8.16) * mm});
            skLineSegment(sketch, "E13239", {"start": v(68.1, 8.16) * mm, "end": v(67.61, 8.24) * mm});
            skLineSegment(sketch, "E13240", {"start": v(67.61, 8.24) * mm, "end": v(67.06, 8.37) * mm});
            skLineSegment(sketch, "E13241", {"start": v(67.06, 8.37) * mm, "end": v(66.45, 8.53) * mm});
            skLineSegment(sketch, "E13242", {"start": v(66.45, 8.53) * mm, "end": v(66.2, 8.62) * mm});
            skLineSegment(sketch, "E13243", {"start": v(66.2, 8.62) * mm, "end": v(65.93, 10.76) * mm});
            skLineSegment(sketch, "E13244", {"start": v(65.93, 10.76) * mm, "end": v(66.15, 10.9) * mm});
            skLineSegment(sketch, "E13245", {"start": v(66.15, 10.9) * mm, "end": v(66.7, 11.2) * mm});
            skLineSegment(sketch, "E13246", {"start": v(66.7, 11.2) * mm, "end": v(67.2, 11.46) * mm});
            skLineSegment(sketch, "E13247", {"start": v(67.2, 11.46) * mm, "end": v(67.65, 11.67) * mm});
            skLineSegment(sketch, "E13248", {"start": v(67.65, 11.67) * mm, "end": v(68.05, 11.82) * mm});
            skLineSegment(sketch, "E13249", {"start": v(68.05, 11.82) * mm, "end": v(68.4, 11.94) * mm});
            skLineSegment(sketch, "E13250", {"start": v(68.4, 11.94) * mm, "end": v(68.69, 12.02) * mm});
            skLineSegment(sketch, "E13251", {"start": v(68.69, 12.02) * mm, "end": v(68.92, 12.07) * mm});
            skLineSegment(sketch, "E13252", {"start": v(68.92, 12.07) * mm, "end": v(69.08, 12.1) * mm});
            skLineSegment(sketch, "E13253", {"start": v(69.08, 12.1) * mm, "end": v(69.18, 12.11) * mm});
            skLineSegment(sketch, "E13254", {"start": v(69.18, 12.11) * mm, "end": v(69.21, 12.11) * mm});
            skLineSegment(sketch, "E13255", {"start": v(69.21, 12.11) * mm, "end": v(71.23, 12.21) * mm});
            skLineSegment(sketch, "E13256", {"start": v(71.23, 12.21) * mm, "end": v(71.28, 15.4) * mm});
            skLineSegment(sketch, "E13257", {"start": v(71.28, 15.4) * mm, "end": v(69.27, 15.56) * mm});
            skLineSegment(sketch, "E13258", {"start": v(69.27, 15.56) * mm, "end": v(69.24, 15.57) * mm});
            skLineSegment(sketch, "E13259", {"start": v(69.24, 15.57) * mm, "end": v(69.14, 15.58) * mm});
            skLineSegment(sketch, "E13260", {"start": v(69.14, 15.58) * mm, "end": v(68.97, 15.62) * mm});
            skLineSegment(sketch, "E13261", {"start": v(68.97, 15.62) * mm, "end": v(68.75, 15.67) * mm});
            skLineSegment(sketch, "E13262", {"start": v(68.75, 15.67) * mm, "end": v(68.46, 15.76) * mm});
            skLineSegment(sketch, "E13263", {"start": v(68.46, 15.76) * mm, "end": v(68.12, 15.89) * mm});
            skLineSegment(sketch, "E13264", {"start": v(68.12, 15.89) * mm, "end": v(67.72, 16.06) * mm});
            skLineSegment(sketch, "E13265", {"start": v(67.72, 16.06) * mm, "end": v(67.28, 16.28) * mm});
            skLineSegment(sketch, "E13266", {"start": v(67.28, 16.28) * mm, "end": v(66.78, 16.55) * mm});
            skLineSegment(sketch, "E13267", {"start": v(66.78, 16.55) * mm, "end": v(66.25, 16.88) * mm});
            skLineSegment(sketch, "E13268", {"start": v(66.25, 16.88) * mm, "end": v(66.03, 17.02) * mm});
            skLineSegment(sketch, "E13269", {"start": v(66.03, 17.02) * mm, "end": v(66.38, 19.15) * mm});
            skLineSegment(sketch, "E13270", {"start": v(66.38, 19.15) * mm, "end": v(66.63, 19.23) * mm});
            skLineSegment(sketch, "E13271", {"start": v(66.63, 19.23) * mm, "end": v(67.24, 19.38) * mm});
            skLineSegment(sketch, "E13272", {"start": v(67.24, 19.38) * mm, "end": v(67.8, 19.48) * mm});
            skLineSegment(sketch, "E13273", {"start": v(67.8, 19.48) * mm, "end": v(68.3, 19.55) * mm});
            skLineSegment(sketch, "E13274", {"start": v(68.3, 19.55) * mm, "end": v(68.72, 19.59) * mm});
            skLineSegment(sketch, "E13275", {"start": v(68.72, 19.59) * mm, "end": v(69.09, 19.6) * mm});
            skLineSegment(sketch, "E13276", {"start": v(69.09, 19.6) * mm, "end": v(69.39, 19.6) * mm});
            skLineSegment(sketch, "E13277", {"start": v(69.39, 19.6) * mm, "end": v(69.62, 19.58) * mm});
            skLineSegment(sketch, "E13278", {"start": v(69.62, 19.58) * mm, "end": v(69.79, 19.57) * mm});
            skLineSegment(sketch, "E13279", {"start": v(69.79, 19.57) * mm, "end": v(69.88, 19.55) * mm});
            skLineSegment(sketch, "E13280", {"start": v(69.88, 19.55) * mm, "end": v(69.92, 19.54) * mm});
            skLineSegment(sketch, "E13281", {"start": v(69.92, 19.54) * mm, "end": v(71.88, 19.08) * mm});
            skLineSegment(sketch, "E13282", {"start": v(71.88, 19.08) * mm, "end": v(72.84, 22.12) * mm});
            skLineSegment(sketch, "E13283", {"start": v(72.84, 22.12) * mm, "end": v(70.96, 22.84) * mm});
            skLineSegment(sketch, "E13284", {"start": v(70.96, 22.84) * mm, "end": v(70.93, 22.85) * mm});
            skLineSegment(sketch, "E13285", {"start": v(70.93, 22.85) * mm, "end": v(70.84, 22.9) * mm});
            skLineSegment(sketch, "E13286", {"start": v(70.84, 22.9) * mm, "end": v(70.7, 22.97) * mm});
            skLineSegment(sketch, "E13287", {"start": v(70.7, 22.97) * mm, "end": v(70.5, 23.09) * mm});
            skLineSegment(sketch, "E13288", {"start": v(70.5, 23.09) * mm, "end": v(70.24, 23.25) * mm});
            skLineSegment(sketch, "E13289", {"start": v(70.24, 23.25) * mm, "end": v(69.95, 23.47) * mm});
            skLineSegment(sketch, "E13290", {"start": v(69.95, 23.47) * mm, "end": v(69.62, 23.74) * mm});
            skLineSegment(sketch, "E13291", {"start": v(69.62, 23.74) * mm, "end": v(69.25, 24.07) * mm});
            skLineSegment(sketch, "E13292", {"start": v(69.25, 24.07) * mm, "end": v(68.85, 24.47) * mm});
            skLineSegment(sketch, "E13293", {"start": v(68.85, 24.47) * mm, "end": v(68.43, 24.94) * mm});
            skLineSegment(sketch, "E13294", {"start": v(68.43, 24.94) * mm, "end": v(68.27, 25.14) * mm});
            skLineSegment(sketch, "E13295", {"start": v(68.27, 25.14) * mm, "end": v(69.2, 27.09) * mm});
            skLineSegment(sketch, "E13296", {"start": v(69.2, 27.09) * mm, "end": v(69.47, 27.09) * mm});
            skLineSegment(sketch, "E13297", {"start": v(69.47, 27.09) * mm, "end": v(70.1, 27.06) * mm});
            skLineSegment(sketch, "E13298", {"start": v(70.1, 27.06) * mm, "end": v(70.67, 27) * mm});
            skLineSegment(sketch, "E13299", {"start": v(70.67, 27) * mm, "end": v(71.16, 26.93) * mm});
            skLineSegment(sketch, "E13300", {"start": v(71.16, 26.93) * mm, "end": v(71.59, 26.85) * mm});
            skLineSegment(sketch, "E13301", {"start": v(71.59, 26.85) * mm, "end": v(71.94, 26.76) * mm});
            skLineSegment(sketch, "E13302", {"start": v(71.94, 26.76) * mm, "end": v(72.23, 26.68) * mm});
            skLineSegment(sketch, "E13303", {"start": v(72.23, 26.68) * mm, "end": v(72.45, 26.6) * mm});
            skLineSegment(sketch, "E13304", {"start": v(72.45, 26.6) * mm, "end": v(72.6, 26.54) * mm});
            skLineSegment(sketch, "E13305", {"start": v(72.6, 26.54) * mm, "end": v(72.7, 26.5) * mm});
            skLineSegment(sketch, "E13306", {"start": v(72.7, 26.5) * mm, "end": v(72.72, 26.48) * mm});
            skLineSegment(sketch, "E13307", {"start": v(72.72, 26.48) * mm, "end": v(74.47, 25.49) * mm});
            skLineSegment(sketch, "E13308", {"start": v(74.47, 25.49) * mm, "end": v(76.26, 28.14) * mm});
            skLineSegment(sketch, "E13309", {"start": v(76.26, 28.14) * mm, "end": v(74.66, 29.35) * mm});
            skLineSegment(sketch, "E13310", {"start": v(74.66, 29.35) * mm, "end": v(74.63, 29.37) * mm});
            skLineSegment(sketch, "E13311", {"start": v(74.63, 29.37) * mm, "end": v(74.56, 29.44) * mm});
            skLineSegment(sketch, "E13312", {"start": v(74.56, 29.44) * mm, "end": v(74.44, 29.55) * mm});
            skLineSegment(sketch, "E13313", {"start": v(74.44, 29.55) * mm, "end": v(74.28, 29.72) * mm});
            skLineSegment(sketch, "E13314", {"start": v(74.28, 29.72) * mm, "end": v(74.1, 29.95) * mm});
            skLineSegment(sketch, "E13315", {"start": v(74.1, 29.95) * mm, "end": v(73.87, 30.24) * mm});
            skLineSegment(sketch, "E13316", {"start": v(73.87, 30.24) * mm, "end": v(73.63, 30.59) * mm});
            skLineSegment(sketch, "E13317", {"start": v(73.63, 30.59) * mm, "end": v(73.38, 31.01) * mm});
            skLineSegment(sketch, "E13318", {"start": v(73.38, 31.01) * mm, "end": v(73.1, 31.5) * mm});
            skLineSegment(sketch, "E13319", {"start": v(73.1, 31.5) * mm, "end": v(72.84, 32.06) * mm});
            skLineSegment(sketch, "E13320", {"start": v(72.84, 32.06) * mm, "end": v(72.74, 32.3) * mm});
            skLineSegment(sketch, "E13321", {"start": v(72.74, 32.3) * mm, "end": v(74.2, 33.91) * mm});
            skLineSegment(sketch, "E13322", {"start": v(74.2, 33.91) * mm, "end": v(74.45, 33.84) * mm});
            skLineSegment(sketch, "E13323", {"start": v(74.45, 33.84) * mm, "end": v(75.05, 33.64) * mm});
            skLineSegment(sketch, "E13324", {"start": v(75.05, 33.64) * mm, "end": v(75.57, 33.43) * mm});
            skLineSegment(sketch, "E13325", {"start": v(75.57, 33.43) * mm, "end": v(76.03, 33.22) * mm});
            skLineSegment(sketch, "E13326", {"start": v(76.03, 33.22) * mm, "end": v(76.41, 33.03) * mm});
            skLineSegment(sketch, "E13327", {"start": v(76.41, 33.03) * mm, "end": v(76.73, 32.84) * mm});
            skLineSegment(sketch, "E13328", {"start": v(76.73, 32.84) * mm, "end": v(76.98, 32.68) * mm});
            skLineSegment(sketch, "E13329", {"start": v(76.98, 32.68) * mm, "end": v(77.16, 32.55) * mm});
            skLineSegment(sketch, "E13330", {"start": v(77.16, 32.55) * mm, "end": v(77.3, 32.44) * mm});
            skLineSegment(sketch, "E13331", {"start": v(77.3, 32.44) * mm, "end": v(77.37, 32.38) * mm});
            skLineSegment(sketch, "E13332", {"start": v(77.37, 32.38) * mm, "end": v(77.4, 32.35) * mm});
            skLineSegment(sketch, "E13333", {"start": v(77.4, 32.35) * mm, "end": v(78.79, 30.92) * mm});
            skLineSegment(sketch, "E13334", {"start": v(78.79, 30.92) * mm, "end": v(81.27, 32.97) * mm});
            skLineSegment(sketch, "E13335", {"start": v(81.27, 32.97) * mm, "end": v(80.08, 34.57) * mm});
            skLineSegment(sketch, "E13336", {"start": v(80.08, 34.57) * mm, "end": v(80.06, 34.6) * mm});
            skLineSegment(sketch, "E13337", {"start": v(80.06, 34.6) * mm, "end": v(80, 34.68) * mm});
            skLineSegment(sketch, "E13338", {"start": v(80, 34.68) * mm, "end": v(79.92, 34.82) * mm});
            skLineSegment(sketch, "E13339", {"start": v(79.92, 34.82) * mm, "end": v(79.82, 35.03) * mm});
            skLineSegment(sketch, "E13340", {"start": v(79.82, 35.03) * mm, "end": v(79.7, 35.3) * mm});
            skLineSegment(sketch, "E13341", {"start": v(79.7, 35.3) * mm, "end": v(79.58, 35.64) * mm});
            skLineSegment(sketch, "E13342", {"start": v(79.58, 35.64) * mm, "end": v(79.44, 36.04) * mm});
            skLineSegment(sketch, "E13343", {"start": v(79.44, 36.04) * mm, "end": v(79.32, 36.52) * mm});
            skLineSegment(sketch, "E13344", {"start": v(79.32, 36.52) * mm, "end": v(79.2, 37.07) * mm});
            skLineSegment(sketch, "E13345", {"start": v(79.2, 37.07) * mm, "end": v(79.1, 37.68) * mm});
            skLineSegment(sketch, "E13346", {"start": v(79.1, 37.68) * mm, "end": v(79.08, 37.94) * mm});
            skLineSegment(sketch, "E13347", {"start": v(79.08, 37.94) * mm, "end": v(80.94, 39.08) * mm});
            skLineSegment(sketch, "E13348", {"start": v(80.94, 39.08) * mm, "end": v(81.16, 38.94) * mm});
            skLineSegment(sketch, "E13349", {"start": v(81.16, 38.94) * mm, "end": v(81.67, 38.57) * mm});
            skLineSegment(sketch, "E13350", {"start": v(81.67, 38.57) * mm, "end": v(82.12, 38.23) * mm});
            skLineSegment(sketch, "E13351", {"start": v(82.12, 38.23) * mm, "end": v(82.5, 37.9) * mm});
            skLineSegment(sketch, "E13352", {"start": v(82.5, 37.9) * mm, "end": v(82.8, 37.61) * mm});
            skLineSegment(sketch, "E13353", {"start": v(82.8, 37.61) * mm, "end": v(83.06, 37.35) * mm});
            skLineSegment(sketch, "E13354", {"start": v(83.06, 37.35) * mm, "end": v(83.25, 37.12) * mm});
            skLineSegment(sketch, "E13355", {"start": v(83.25, 37.12) * mm, "end": v(83.4, 36.94) * mm});
            skLineSegment(sketch, "E13356", {"start": v(83.4, 36.94) * mm, "end": v(83.49, 36.8) * mm});
            skLineSegment(sketch, "E13357", {"start": v(83.49, 36.8) * mm, "end": v(83.54, 36.72) * mm});
            skLineSegment(sketch, "E13358", {"start": v(83.54, 36.72) * mm, "end": v(83.56, 36.7) * mm});
            skLineSegment(sketch, "E13359", {"start": v(83.56, 36.7) * mm, "end": v(84.48, 34.93) * mm});
            skLineSegment(sketch, "E13360", {"start": v(84.48, 34.93) * mm, "end": v(87.45, 36.2) * mm});
            skLineSegment(sketch, "E13361", {"start": v(87.45, 36.2) * mm, "end": v(86.76, 38.08) * mm});
            skLineSegment(sketch, "E13362", {"start": v(86.76, 38.08) * mm, "end": v(86.75, 38.1) * mm});
            skLineSegment(sketch, "E13363", {"start": v(86.75, 38.1) * mm, "end": v(86.73, 38.2) * mm});
            skLineSegment(sketch, "E13364", {"start": v(86.73, 38.2) * mm, "end": v(86.7, 38.36) * mm});
            skLineSegment(sketch, "E13365", {"start": v(86.7, 38.36) * mm, "end": v(86.65, 38.59) * mm});
            skLineSegment(sketch, "E13366", {"start": v(86.65, 38.59) * mm, "end": v(86.62, 38.88) * mm});
            skLineSegment(sketch, "E13367", {"start": v(86.62, 38.88) * mm, "end": v(86.6, 39.24) * mm});
            skLineSegment(sketch, "E13368", {"start": v(86.6, 39.24) * mm, "end": v(86.58, 39.67) * mm});
            skLineSegment(sketch, "E13369", {"start": v(86.58, 39.67) * mm, "end": v(86.6, 40.16) * mm});
            skLineSegment(sketch, "E13370", {"start": v(86.6, 40.16) * mm, "end": v(86.64, 40.71) * mm});
            skLineSegment(sketch, "E13371", {"start": v(86.64, 40.71) * mm, "end": v(86.72, 41.33) * mm});
            skLineSegment(sketch, "E13372", {"start": v(86.72, 41.33) * mm, "end": v(86.77, 41.59) * mm});
            skLineSegment(sketch, "E13373", {"start": v(86.77, 41.59) * mm, "end": v(88.88, 42.16) * mm});
            skLineSegment(sketch, "E13374", {"start": v(88.88, 42.16) * mm, "end": v(89.05, 41.96) * mm});
            skLineSegment(sketch, "E13375", {"start": v(89.05, 41.96) * mm, "end": v(89.45, 41.48) * mm});
            skLineSegment(sketch, "E13376", {"start": v(89.45, 41.48) * mm, "end": v(89.77, 41.02) * mm});
            skLineSegment(sketch, "E13377", {"start": v(89.77, 41.02) * mm, "end": v(90.04, 40.6) * mm});
            skLineSegment(sketch, "E13378", {"start": v(90.04, 40.6) * mm, "end": v(90.26, 40.24) * mm});
            skLineSegment(sketch, "E13379", {"start": v(90.26, 40.24) * mm, "end": v(90.42, 39.92) * mm});
            skLineSegment(sketch, "E13380", {"start": v(90.42, 39.92) * mm, "end": v(90.54, 39.65) * mm});
            skLineSegment(sketch, "E13381", {"start": v(90.54, 39.65) * mm, "end": v(90.63, 39.43) * mm});
            skLineSegment(sketch, "E13382", {"start": v(90.63, 39.43) * mm, "end": v(90.68, 39.28) * mm});
            skLineSegment(sketch, "E13383", {"start": v(90.68, 39.28) * mm, "end": v(90.7, 39.18) * mm});
            skLineSegment(sketch, "E13384", {"start": v(90.7, 39.18) * mm, "end": v(90.71, 39.15) * mm});
            skLineSegment(sketch, "E13385", {"start": v(90.71, 39.15) * mm, "end": v(91.1, 37.2) * mm});
            skLineSegment(sketch, "E13386", {"start": v(91.1, 37.2) * mm, "end": v(94.3, 37.6) * mm});
            skLineSegment(sketch, "E13387", {"start": v(94.3, 37.6) * mm, "end": v(94.19, 39.59) * mm});
            skLineSegment(sketch, "E13388", {"start": v(94.19, 39.59) * mm, "end": v(94.19, 39.62) * mm});
            skLineSegment(sketch, "E13389", {"start": v(94.19, 39.62) * mm, "end": v(94.19, 39.72) * mm});
            skLineSegment(sketch, "E13390", {"start": v(94.19, 39.72) * mm, "end": v(94.2, 39.88) * mm});
            skLineSegment(sketch, "E13391", {"start": v(94.2, 39.88) * mm, "end": v(94.22, 40.1) * mm});
            skLineSegment(sketch, "E13392", {"start": v(94.22, 40.1) * mm, "end": v(94.27, 40.4) * mm});
            skLineSegment(sketch, "E13393", {"start": v(94.27, 40.4) * mm, "end": v(94.35, 40.75) * mm});
            skLineSegment(sketch, "E13394", {"start": v(94.35, 40.75) * mm, "end": v(94.47, 41.16) * mm});
            skLineSegment(sketch, "E13395", {"start": v(94.47, 41.16) * mm, "end": v(94.62, 41.63) * mm});
            skLineSegment(sketch, "E13396", {"start": v(94.62, 41.63) * mm, "end": v(94.82, 42.15) * mm});
            skLineSegment(sketch, "E13397", {"start": v(94.82, 42.15) * mm, "end": v(95.08, 42.72) * mm});
            skLineSegment(sketch, "E13398", {"start": v(95.08, 42.72) * mm, "end": v(95.2, 42.95) * mm});
            skLineSegment(sketch, "E13399", {"start": v(95.2, 42.95) * mm, "end": v(97.38, 42.92) * mm});
            skLineSegment(sketch, "E13400", {"start": v(97.38, 42.92) * mm, "end": v(97.5, 42.68) * mm});
            skLineSegment(sketch, "E13401", {"start": v(97.5, 42.68) * mm, "end": v(97.73, 42.1) * mm});
            skLineSegment(sketch, "E13402", {"start": v(97.73, 42.1) * mm, "end": v(97.92, 41.58) * mm});
            skLineSegment(sketch, "E13403", {"start": v(97.92, 41.58) * mm, "end": v(98.05, 41.1) * mm});
            skLineSegment(sketch, "E13404", {"start": v(98.05, 41.1) * mm, "end": v(98.15, 40.69) * mm});
            skLineSegment(sketch, "E13405", {"start": v(98.15, 40.69) * mm, "end": v(98.22, 40.34) * mm});
            skLineSegment(sketch, "E13406", {"start": v(98.22, 40.34) * mm, "end": v(98.26, 40.04) * mm});
            skLineSegment(sketch, "E13407", {"start": v(98.26, 40.04) * mm, "end": v(98.28, 39.81) * mm});
            skLineSegment(sketch, "E13408", {"start": v(98.28, 39.81) * mm, "end": v(98.28, 39.65) * mm});
            skLineSegment(sketch, "E13409", {"start": v(98.28, 39.65) * mm, "end": v(98.28, 39.55) * mm});
            skLineSegment(sketch, "E13410", {"start": v(98.28, 39.55) * mm, "end": v(98.28, 39.52) * mm});
            skLineSegment(sketch, "E13411", {"start": v(98.28, 39.52) * mm, "end": v(98.1, 37.54) * mm});
            skLineSegment(sketch, "E13412", {"start": v(98.1, 37.54) * mm, "end": v(101.29, 37.04) * mm});
            skLineSegment(sketch, "E13413", {"start": v(101.29, 37.04) * mm, "end": v(101.74, 38.97) * mm});
            skLineSegment(sketch, "E13414", {"start": v(101.74, 38.97) * mm, "end": v(101.75, 39) * mm});
            skLineSegment(sketch, "E13415", {"start": v(101.75, 39) * mm, "end": v(101.78, 39.1) * mm});
            skLineSegment(sketch, "E13416", {"start": v(101.78, 39.1) * mm, "end": v(101.83, 39.25) * mm});
            skLineSegment(sketch, "E13417", {"start": v(101.83, 39.25) * mm, "end": v(101.93, 39.46) * mm});
            skLineSegment(sketch, "E13418", {"start": v(101.93, 39.46) * mm, "end": v(102.06, 39.73) * mm});
            skLineSegment(sketch, "E13419", {"start": v(102.06, 39.73) * mm, "end": v(102.23, 40.05) * mm});
            skLineSegment(sketch, "E13420", {"start": v(102.23, 40.05) * mm, "end": v(102.46, 40.4) * mm});
            skLineSegment(sketch, "E13421", {"start": v(102.46, 40.4) * mm, "end": v(102.74, 40.81) * mm});
            skLineSegment(sketch, "E13422", {"start": v(102.74, 40.81) * mm, "end": v(103.08, 41.26) * mm});
            skLineSegment(sketch, "E13423", {"start": v(103.08, 41.26) * mm, "end": v(103.49, 41.73) * mm});
            skLineSegment(sketch, "E13424", {"start": v(103.49, 41.73) * mm, "end": v(103.67, 41.92) * mm});
            skLineSegment(sketch, "E13425", {"start": v(103.67, 41.92) * mm, "end": v(105.76, 41.28) * mm});
            skLineSegment(sketch, "E13426", {"start": v(105.76, 41.28) * mm, "end": v(105.8, 41.03) * mm});
            skLineSegment(sketch, "E13427", {"start": v(105.8, 41.03) * mm, "end": v(105.86, 40.4) * mm});
            skLineSegment(sketch, "E13428", {"start": v(105.86, 40.4) * mm, "end": v(105.89, 39.85) * mm});
            skLineSegment(sketch, "E13429", {"start": v(105.89, 39.85) * mm, "end": v(105.88, 39.36) * mm});
            skLineSegment(sketch, "E13430", {"start": v(105.88, 39.36) * mm, "end": v(105.86, 38.93) * mm});
            skLineSegment(sketch, "E13431", {"start": v(105.86, 38.93) * mm, "end": v(105.82, 38.57) * mm});
            skLineSegment(sketch, "E13432", {"start": v(105.82, 38.57) * mm, "end": v(105.78, 38.28) * mm});
            skLineSegment(sketch, "E13433", {"start": v(105.78, 38.28) * mm, "end": v(105.73, 38.06) * mm});
            skLineSegment(sketch, "E13434", {"start": v(105.73, 38.06) * mm, "end": v(105.7, 37.9) * mm});
            skLineSegment(sketch, "E13435", {"start": v(105.7, 37.9) * mm, "end": v(105.66, 37.8) * mm});
            skLineSegment(sketch, "E13436", {"start": v(105.66, 37.8) * mm, "end": v(105.65, 37.77) * mm});
            skLineSegment(sketch, "E13437", {"start": v(105.65, 37.77) * mm, "end": v(104.9, 35.93) * mm});
            skLineSegment(sketch, "E13438", {"start": v(104.9, 35.93) * mm, "end": v(107.83, 34.56) * mm});
            skLineSegment(sketch, "E13439", {"start": v(107.83, 34.56) * mm, "end": v(108.81, 36.3) * mm});
            skLineSegment(sketch, "E13440", {"start": v(108.81, 36.3) * mm, "end": v(108.83, 36.32) * mm});
            skLineSegment(sketch, "E13441", {"start": v(108.83, 36.32) * mm, "end": v(108.88, 36.4) * mm});
            skLineSegment(sketch, "E13442", {"start": v(108.88, 36.4) * mm, "end": v(108.98, 36.53) * mm});
            skLineSegment(sketch, "E13443", {"start": v(108.98, 36.53) * mm, "end": v(109.13, 36.71) * mm});
            skLineSegment(sketch, "E13444", {"start": v(109.13, 36.71) * mm, "end": v(109.33, 36.93) * mm});
            skLineSegment(sketch, "E13445", {"start": v(109.33, 36.93) * mm, "end": v(109.59, 37.18) * mm});
            skLineSegment(sketch, "E13446", {"start": v(109.59, 37.18) * mm, "end": v(109.91, 37.47) * mm});
            skLineSegment(sketch, "E13447", {"start": v(109.91, 37.47) * mm, "end": v(110.3, 37.78) * mm});
            skLineSegment(sketch, "E13448", {"start": v(110.3, 37.78) * mm, "end": v(110.75, 38.11) * mm});
            skLineSegment(sketch, "E13449", {"start": v(110.75, 38.11) * mm, "end": v(111.28, 38.45) * mm});
            skLineSegment(sketch, "E13450", {"start": v(111.28, 38.45) * mm, "end": v(111.5, 38.59) * mm});
            skLineSegment(sketch, "E13451", {"start": v(111.5, 38.59) * mm, "end": v(113.33, 37.4) * mm});
            skLineSegment(sketch, "E13452", {"start": v(113.33, 37.4) * mm, "end": v(113.3, 37.13) * mm});
            skLineSegment(sketch, "E13453", {"start": v(113.3, 37.13) * mm, "end": v(113.17, 36.52) * mm});
            skLineSegment(sketch, "E13454", {"start": v(113.17, 36.52) * mm, "end": v(113.04, 35.98) * mm});
            skLineSegment(sketch, "E13455", {"start": v(113.04, 35.98) * mm, "end": v(112.9, 35.51) * mm});
            skLineSegment(sketch, "E13456", {"start": v(112.9, 35.51) * mm, "end": v(112.75, 35.1) * mm});
            skLineSegment(sketch, "E13457", {"start": v(112.75, 35.1) * mm, "end": v(112.62, 34.77) * mm});
            skLineSegment(sketch, "E13458", {"start": v(112.62, 34.77) * mm, "end": v(112.49, 34.5) * mm});
            skLineSegment(sketch, "E13459", {"start": v(112.49, 34.5) * mm, "end": v(112.38, 34.3) * mm});
            skLineSegment(sketch, "E13460", {"start": v(112.38, 34.3) * mm, "end": v(112.3, 34.16) * mm});
            skLineSegment(sketch, "E13461", {"start": v(112.3, 34.16) * mm, "end": v(112.24, 34.08) * mm});
            skLineSegment(sketch, "E13462", {"start": v(112.24, 34.08) * mm, "end": v(112.22, 34.06) * mm});
            skLineSegment(sketch, "E13463", {"start": v(112.22, 34.06) * mm, "end": v(110.98, 32.5) * mm});
            skLineSegment(sketch, "E13464", {"start": v(110.98, 32.5) * mm, "end": v(113.39, 30.37) * mm});
            skCircle(sketch, "E13465", {"center": v(95.8, 13.41) * mm, "radius": 1.25 * mm});
            skLineSegment(sketch, "E13466", {"start": v(92.8, 11.35) * mm, "end": v(98.8, 11.35) * mm});
            skLineSegment(sketch, "E13467", {"start": v(98.8, 11.35) * mm, "end": v(98.8, 15.48) * mm});
            skLineSegment(sketch, "E13468", {"start": v(98.8, 15.48) * mm, "end": v(92.8, 15.48) * mm});
            skLineSegment(sketch, "E13469", {"start": v(92.8, 15.48) * mm, "end": v(92.8, 11.35) * mm});
            skCircle(sketch, "E13470", {"center": v(95.8, 13.41) * mm, "radius": 3.75 * mm});
            skLineSegment(sketch, "E13471", {"start": v(41.38, 28.87) * mm, "end": v(42.86, 30.33) * mm});
            skLineSegment(sketch, "E13472", {"start": v(42.86, 30.33) * mm, "end": v(42.88, 30.35) * mm});
            skLineSegment(sketch, "E13473", {"start": v(42.88, 30.35) * mm, "end": v(42.95, 30.4) * mm});
            skLineSegment(sketch, "E13474", {"start": v(42.95, 30.4) * mm, "end": v(43.07, 30.5) * mm});
            skLineSegment(sketch, "E13475", {"start": v(43.07, 30.5) * mm, "end": v(43.24, 30.62) * mm});
            skLineSegment(sketch, "E13476", {"start": v(43.24, 30.62) * mm, "end": v(43.47, 30.76) * mm});
            skLineSegment(sketch, "E13477", {"start": v(43.47, 30.76) * mm, "end": v(43.76, 30.92) * mm});
            skLineSegment(sketch, "E13478", {"start": v(43.76, 30.92) * mm, "end": v(44.11, 31.1) * mm});
            skLineSegment(sketch, "E13479", {"start": v(44.11, 31.1) * mm, "end": v(44.53, 31.28) * mm});
            skLineSegment(sketch, "E13480", {"start": v(44.53, 31.28) * mm, "end": v(45, 31.46) * mm});
            skLineSegment(sketch, "E13481", {"start": v(45, 31.46) * mm, "end": v(45.55, 31.63) * mm});
            skLineSegment(sketch, "E13482", {"start": v(45.55, 31.63) * mm, "end": v(46.03, 31.76) * mm});
            skLineSegment(sketch, "E13483", {"start": v(46.03, 31.76) * mm, "end": v(47.43, 30.14) * mm});
            skLineSegment(sketch, "E13484", {"start": v(47.43, 30.14) * mm, "end": v(47.23, 29.7) * mm});
            skLineSegment(sketch, "E13485", {"start": v(47.23, 29.7) * mm, "end": v(46.97, 29.19) * mm});
            skLineSegment(sketch, "E13486", {"start": v(46.97, 29.19) * mm, "end": v(46.7, 28.75) * mm});
            skLineSegment(sketch, "E13487", {"start": v(46.7, 28.75) * mm, "end": v(46.46, 28.38) * mm});
            skLineSegment(sketch, "E13488", {"start": v(46.46, 28.38) * mm, "end": v(46.23, 28.06) * mm});
            skLineSegment(sketch, "E13489", {"start": v(46.23, 28.06) * mm, "end": v(46.02, 27.8) * mm});
            skLineSegment(sketch, "E13490", {"start": v(46.02, 27.8) * mm, "end": v(45.84, 27.6) * mm});
            skLineSegment(sketch, "E13491", {"start": v(45.84, 27.6) * mm, "end": v(45.7, 27.46) * mm});
            skLineSegment(sketch, "E13492", {"start": v(45.7, 27.46) * mm, "end": v(45.58, 27.35) * mm});
            skLineSegment(sketch, "E13493", {"start": v(45.58, 27.35) * mm, "end": v(45.52, 27.3) * mm});
            skLineSegment(sketch, "E13494", {"start": v(45.52, 27.3) * mm, "end": v(45.5, 27.28) * mm});
            skLineSegment(sketch, "E13495", {"start": v(45.5, 27.28) * mm, "end": v(43.79, 26.08) * mm});
            skLineSegment(sketch, "E13496", {"start": v(43.79, 26.08) * mm, "end": v(45.46, 23.37) * mm});
            skLineSegment(sketch, "E13497", {"start": v(45.46, 23.37) * mm, "end": v(47.33, 24.31) * mm});
            skLineSegment(sketch, "E13498", {"start": v(47.33, 24.31) * mm, "end": v(47.36, 24.33) * mm});
            skLineSegment(sketch, "E13499", {"start": v(47.36, 24.33) * mm, "end": v(47.44, 24.36) * mm});
            skLineSegment(sketch, "E13500", {"start": v(47.44, 24.36) * mm, "end": v(47.58, 24.41) * mm});
            skLineSegment(sketch, "E13501", {"start": v(47.58, 24.41) * mm, "end": v(47.78, 24.47) * mm});
            skLineSegment(sketch, "E13502", {"start": v(47.78, 24.47) * mm, "end": v(48.05, 24.54) * mm});
            skLineSegment(sketch, "E13503", {"start": v(48.05, 24.54) * mm, "end": v(48.37, 24.6) * mm});
            skLineSegment(sketch, "E13504", {"start": v(48.37, 24.6) * mm, "end": v(48.76, 24.66) * mm});
            skLineSegment(sketch, "E13505", {"start": v(48.76, 24.66) * mm, "end": v(49.21, 24.7) * mm});
            skLineSegment(sketch, "E13506", {"start": v(49.21, 24.7) * mm, "end": v(49.73, 24.73) * mm});
            skLineSegment(sketch, "E13507", {"start": v(49.73, 24.73) * mm, "end": v(50.3, 24.73) * mm});
            skLineSegment(sketch, "E13508", {"start": v(50.3, 24.73) * mm, "end": v(50.8, 24.7) * mm});
            skLineSegment(sketch, "E13509", {"start": v(50.8, 24.7) * mm, "end": v(51.62, 22.74) * mm});
            skLineSegment(sketch, "E13510", {"start": v(51.62, 22.74) * mm, "end": v(51.29, 22.38) * mm});
            skLineSegment(sketch, "E13511", {"start": v(51.29, 22.38) * mm, "end": v(50.88, 21.98) * mm});
            skLineSegment(sketch, "E13512", {"start": v(50.88, 21.98) * mm, "end": v(50.5, 21.64) * mm});
            skLineSegment(sketch, "E13513", {"start": v(50.5, 21.64) * mm, "end": v(50.15, 21.36) * mm});
            skLineSegment(sketch, "E13514", {"start": v(50.15, 21.36) * mm, "end": v(49.83, 21.13) * mm});
            skLineSegment(sketch, "E13515", {"start": v(49.83, 21.13) * mm, "end": v(49.55, 20.95) * mm});
            skLineSegment(sketch, "E13516", {"start": v(49.55, 20.95) * mm, "end": v(49.32, 20.81) * mm});
            skLineSegment(sketch, "E13517", {"start": v(49.32, 20.81) * mm, "end": v(49.13, 20.71) * mm});
            skLineSegment(sketch, "E13518", {"start": v(49.13, 20.71) * mm, "end": v(49, 20.65) * mm});
            skLineSegment(sketch, "E13519", {"start": v(49, 20.65) * mm, "end": v(48.9, 20.62) * mm});
            skLineSegment(sketch, "E13520", {"start": v(48.9, 20.62) * mm, "end": v(48.88, 20.6) * mm});
            skLineSegment(sketch, "E13521", {"start": v(48.88, 20.6) * mm, "end": v(46.88, 19.99) * mm});
            skLineSegment(sketch, "E13522", {"start": v(46.88, 19.99) * mm, "end": v(47.63, 16.9) * mm});
            skLineSegment(sketch, "E13523", {"start": v(47.63, 16.9) * mm, "end": v(49.7, 17.23) * mm});
            skLineSegment(sketch, "E13524", {"start": v(49.7, 17.23) * mm, "end": v(49.73, 17.23) * mm});
            skLineSegment(sketch, "E13525", {"start": v(49.73, 17.23) * mm, "end": v(49.82, 17.24) * mm});
            skLineSegment(sketch, "E13526", {"start": v(49.82, 17.24) * mm, "end": v(49.97, 17.25) * mm});
            skLineSegment(sketch, "E13527", {"start": v(49.97, 17.25) * mm, "end": v(50.18, 17.24) * mm});
            skLineSegment(sketch, "E13528", {"start": v(50.18, 17.24) * mm, "end": v(50.45, 17.22) * mm});
            skLineSegment(sketch, "E13529", {"start": v(50.45, 17.22) * mm, "end": v(50.78, 17.19) * mm});
            skLineSegment(sketch, "E13530", {"start": v(50.78, 17.19) * mm, "end": v(51.17, 17.12) * mm});
            skLineSegment(sketch, "E13531", {"start": v(51.17, 17.12) * mm, "end": v(51.61, 17.03) * mm});
            skLineSegment(sketch, "E13532", {"start": v(51.61, 17.03) * mm, "end": v(52.1, 16.9) * mm});
            skLineSegment(sketch, "E13533", {"start": v(52.1, 16.9) * mm, "end": v(52.66, 16.72) * mm});
            skLineSegment(sketch, "E13534", {"start": v(52.66, 16.72) * mm, "end": v(53.12, 16.55) * mm});
            skLineSegment(sketch, "E13535", {"start": v(53.12, 16.55) * mm, "end": v(53.28, 14.42) * mm});
            skLineSegment(sketch, "E13536", {"start": v(53.28, 14.42) * mm, "end": v(52.85, 14.18) * mm});
            skLineSegment(sketch, "E13537", {"start": v(52.85, 14.18) * mm, "end": v(52.34, 13.93) * mm});
            skLineSegment(sketch, "E13538", {"start": v(52.34, 13.93) * mm, "end": v(51.87, 13.72) * mm});
            skLineSegment(sketch, "E13539", {"start": v(51.87, 13.72) * mm, "end": v(51.45, 13.56) * mm});
            skLineSegment(sketch, "E13540", {"start": v(51.45, 13.56) * mm, "end": v(51.07, 13.44) * mm});
            skLineSegment(sketch, "E13541", {"start": v(51.07, 13.44) * mm, "end": v(50.75, 13.35) * mm});
            skLineSegment(sketch, "E13542", {"start": v(50.75, 13.35) * mm, "end": v(50.49, 13.3) * mm});
            skLineSegment(sketch, "E13543", {"start": v(50.49, 13.3) * mm, "end": v(50.28, 13.26) * mm});
            skLineSegment(sketch, "E13544", {"start": v(50.28, 13.26) * mm, "end": v(50.13, 13.24) * mm});
            skLineSegment(sketch, "E13545", {"start": v(50.13, 13.24) * mm, "end": v(50.04, 13.24) * mm});
            skLineSegment(sketch, "E13546", {"start": v(50.04, 13.24) * mm, "end": v(50, 13.23) * mm});
            skLineSegment(sketch, "E13547", {"start": v(50, 13.23) * mm, "end": v(47.91, 13.25) * mm});
            skLineSegment(sketch, "E13548", {"start": v(47.91, 13.25) * mm, "end": v(47.65, 10.09) * mm});
            skLineSegment(sketch, "E13549", {"start": v(47.65, 10.09) * mm, "end": v(49.72, 9.77) * mm});
            skLineSegment(sketch, "E13550", {"start": v(49.72, 9.77) * mm, "end": v(49.75, 9.77) * mm});
            skLineSegment(sketch, "E13551", {"start": v(49.75, 9.77) * mm, "end": v(49.84, 9.75) * mm});
            skLineSegment(sketch, "E13552", {"start": v(49.84, 9.75) * mm, "end": v(49.99, 9.7) * mm});
            skLineSegment(sketch, "E13553", {"start": v(49.99, 9.7) * mm, "end": v(50.19, 9.64) * mm});
            skLineSegment(sketch, "E13554", {"start": v(50.19, 9.64) * mm, "end": v(50.44, 9.54) * mm});
            skLineSegment(sketch, "E13555", {"start": v(50.44, 9.54) * mm, "end": v(50.74, 9.4) * mm});
            skLineSegment(sketch, "E13556", {"start": v(50.74, 9.4) * mm, "end": v(51.1, 9.22) * mm});
            skLineSegment(sketch, "E13557", {"start": v(51.1, 9.22) * mm, "end": v(51.48, 9) * mm});
            skLineSegment(sketch, "E13558", {"start": v(51.48, 9) * mm, "end": v(51.91, 8.72) * mm});
            skLineSegment(sketch, "E13559", {"start": v(51.91, 8.72) * mm, "end": v(52.38, 8.39) * mm});
            skLineSegment(sketch, "E13560", {"start": v(52.38, 8.39) * mm, "end": v(52.76, 8.08) * mm});
            skLineSegment(sketch, "E13561", {"start": v(52.76, 8.08) * mm, "end": v(52.26, 6.01) * mm});
            skLineSegment(sketch, "E13562", {"start": v(52.26, 6.01) * mm, "end": v(51.77, 5.91) * mm});
            skLineSegment(sketch, "E13563", {"start": v(51.77, 5.91) * mm, "end": v(51.2, 5.83) * mm});
            skLineSegment(sketch, "E13564", {"start": v(51.2, 5.83) * mm, "end": v(50.7, 5.77) * mm});
            skLineSegment(sketch, "E13565", {"start": v(50.7, 5.77) * mm, "end": v(50.24, 5.75) * mm});
            skLineSegment(sketch, "E13566", {"start": v(50.24, 5.75) * mm, "end": v(49.84, 5.75) * mm});
            skLineSegment(sketch, "E13567", {"start": v(49.84, 5.75) * mm, "end": v(49.51, 5.76) * mm});
            skLineSegment(sketch, "E13568", {"start": v(49.51, 5.76) * mm, "end": v(49.24, 5.79) * mm});
            skLineSegment(sketch, "E13569", {"start": v(49.24, 5.79) * mm, "end": v(49.03, 5.82) * mm});
            skLineSegment(sketch, "E13570", {"start": v(49.03, 5.82) * mm, "end": v(48.88, 5.85) * mm});
            skLineSegment(sketch, "E13571", {"start": v(48.88, 5.85) * mm, "end": v(48.8, 5.87) * mm});
            skLineSegment(sketch, "E13572", {"start": v(48.8, 5.87) * mm, "end": v(48.77, 5.88) * mm});
            skLineSegment(sketch, "E13573", {"start": v(48.77, 5.88) * mm, "end": v(46.78, 6.53) * mm});
            skLineSegment(sketch, "E13574", {"start": v(46.78, 6.53) * mm, "end": v(45.54, 3.6) * mm});
            skLineSegment(sketch, "E13575", {"start": v(45.54, 3.6) * mm, "end": v(47.4, 2.67) * mm});
            skLineSegment(sketch, "E13576", {"start": v(47.4, 2.67) * mm, "end": v(47.44, 2.66) * mm});
            skLineSegment(sketch, "E13577", {"start": v(47.44, 2.66) * mm, "end": v(47.51, 2.6) * mm});
            skLineSegment(sketch, "E13578", {"start": v(47.51, 2.6) * mm, "end": v(47.64, 2.53) * mm});
            skLineSegment(sketch, "E13579", {"start": v(47.64, 2.53) * mm, "end": v(47.8, 2.4) * mm});
            skLineSegment(sketch, "E13580", {"start": v(47.8, 2.4) * mm, "end": v(48.02, 2.23) * mm});
            skLineSegment(sketch, "E13581", {"start": v(48.02, 2.23) * mm, "end": v(48.26, 2) * mm});
            skLineSegment(sketch, "E13582", {"start": v(48.26, 2) * mm, "end": v(48.54, 1.73) * mm});
            skLineSegment(sketch, "E13583", {"start": v(48.54, 1.73) * mm, "end": v(48.84, 1.4) * mm});
            skLineSegment(sketch, "E13584", {"start": v(48.84, 1.4) * mm, "end": v(49.16, 1) * mm});
            skLineSegment(sketch, "E13585", {"start": v(49.16, 1) * mm, "end": v(49.5, 0.55) * mm});
            skLineSegment(sketch, "E13586", {"start": v(49.5, 0.55) * mm, "end": v(49.77, 0.14) * mm});
            skLineSegment(sketch, "E13587", {"start": v(49.77, 0.14) * mm, "end": v(48.64, -1.68) * mm});
            skLineSegment(sketch, "E13588", {"start": v(48.64, -1.68) * mm, "end": v(48.15, -1.62) * mm});
            skLineSegment(sketch, "E13589", {"start": v(48.15, -1.62) * mm, "end": v(47.58, -1.53) * mm});
            skLineSegment(sketch, "E13590", {"start": v(47.58, -1.53) * mm, "end": v(47.08, -1.43) * mm});
            skLineSegment(sketch, "E13591", {"start": v(47.08, -1.43) * mm, "end": v(46.64, -1.31) * mm});
            skLineSegment(sketch, "E13592", {"start": v(46.64, -1.31) * mm, "end": v(46.26, -1.2) * mm});
            skLineSegment(sketch, "E13593", {"start": v(46.26, -1.2) * mm, "end": v(45.95, -1.08) * mm});
            skLineSegment(sketch, "E13594", {"start": v(45.95, -1.08) * mm, "end": v(45.7, -0.97) * mm});
            skLineSegment(sketch, "E13595", {"start": v(45.7, -0.97) * mm, "end": v(45.51, -0.88) * mm});
            skLineSegment(sketch, "E13596", {"start": v(45.51, -0.88) * mm, "end": v(45.38, -0.8) * mm});
            skLineSegment(sketch, "E13597", {"start": v(45.38, -0.8) * mm, "end": v(45.3, -0.76) * mm});
            skLineSegment(sketch, "E13598", {"start": v(45.3, -0.76) * mm, "end": v(45.28, -0.74) * mm});
            skLineSegment(sketch, "E13599", {"start": v(45.28, -0.74) * mm, "end": v(43.6, 0.48) * mm});
            skLineSegment(sketch, "E13600", {"start": v(43.6, 0.48) * mm, "end": v(41.5, -1.92) * mm});
            skLineSegment(sketch, "E13601", {"start": v(41.5, -1.92) * mm, "end": v(42.98, -3.38) * mm});
            skLineSegment(sketch, "E13602", {"start": v(42.98, -3.38) * mm, "end": v(43, -3.4) * mm});
            skLineSegment(sketch, "E13603", {"start": v(43, -3.4) * mm, "end": v(43.06, -3.47) * mm});
            skLineSegment(sketch, "E13604", {"start": v(43.06, -3.47) * mm, "end": v(43.15, -3.59) * mm});
            skLineSegment(sketch, "E13605", {"start": v(43.15, -3.59) * mm, "end": v(43.28, -3.76) * mm});
            skLineSegment(sketch, "E13606", {"start": v(43.28, -3.76) * mm, "end": v(43.42, -3.98) * mm});
            skLineSegment(sketch, "E13607", {"start": v(43.42, -3.98) * mm, "end": v(43.58, -4.27) * mm});
            skLineSegment(sketch, "E13608", {"start": v(43.58, -4.27) * mm, "end": v(43.76, -4.61) * mm});
            skLineSegment(sketch, "E13609", {"start": v(43.76, -4.61) * mm, "end": v(43.94, -5.02) * mm});
            skLineSegment(sketch, "E13610", {"start": v(43.94, -5.02) * mm, "end": v(44.13, -5.5) * mm});
            skLineSegment(sketch, "E13611", {"start": v(44.13, -5.5) * mm, "end": v(44.3, -6.04) * mm});
            skLineSegment(sketch, "E13612", {"start": v(44.3, -6.04) * mm, "end": v(44.43, -6.5) * mm});
            skLineSegment(sketch, "E13613", {"start": v(44.43, -6.5) * mm, "end": v(42.79, -7.89) * mm});
            skLineSegment(sketch, "E13614", {"start": v(42.79, -7.89) * mm, "end": v(42.33, -7.69) * mm});
            skLineSegment(sketch, "E13615", {"start": v(42.33, -7.69) * mm, "end": v(41.82, -7.43) * mm});
            skLineSegment(sketch, "E13616", {"start": v(41.82, -7.43) * mm, "end": v(41.38, -7.17) * mm});
            skLineSegment(sketch, "E13617", {"start": v(41.38, -7.17) * mm, "end": v(41, -6.93) * mm});
            skLineSegment(sketch, "E13618", {"start": v(41, -6.93) * mm, "end": v(40.68, -6.7) * mm});
            skLineSegment(sketch, "E13619", {"start": v(40.68, -6.7) * mm, "end": v(40.42, -6.5) * mm});
            skLineSegment(sketch, "E13620", {"start": v(40.42, -6.5) * mm, "end": v(40.21, -6.32) * mm});
            skLineSegment(sketch, "E13621", {"start": v(40.21, -6.32) * mm, "end": v(40.06, -6.18) * mm});
            skLineSegment(sketch, "E13622", {"start": v(40.06, -6.18) * mm, "end": v(39.96, -6.07) * mm});
            skLineSegment(sketch, "E13623", {"start": v(39.96, -6.07) * mm, "end": v(39.9, -6) * mm});
            skLineSegment(sketch, "E13624", {"start": v(39.9, -6) * mm, "end": v(39.88, -5.97) * mm});
            skLineSegment(sketch, "E13625", {"start": v(39.88, -5.97) * mm, "end": v(38.66, -4.3) * mm});
            skLineSegment(sketch, "E13626", {"start": v(38.66, -4.3) * mm, "end": v(35.91, -5.95) * mm});
            skLineSegment(sketch, "E13627", {"start": v(35.91, -5.95) * mm, "end": v(36.87, -7.78) * mm});
            skLineSegment(sketch, "E13628", {"start": v(36.87, -7.78) * mm, "end": v(36.88, -7.81) * mm});
            skLineSegment(sketch, "E13629", {"start": v(36.88, -7.81) * mm, "end": v(36.92, -7.9) * mm});
            skLineSegment(sketch, "E13630", {"start": v(36.92, -7.9) * mm, "end": v(36.97, -8.03) * mm});
            skLineSegment(sketch, "E13631", {"start": v(36.97, -8.03) * mm, "end": v(37.03, -8.23) * mm});
            skLineSegment(sketch, "E13632", {"start": v(37.03, -8.23) * mm, "end": v(37.1, -8.5) * mm});
            skLineSegment(sketch, "E13633", {"start": v(37.1, -8.5) * mm, "end": v(37.17, -8.81) * mm});
            skLineSegment(sketch, "E13634", {"start": v(37.17, -8.81) * mm, "end": v(37.22, -9.2) * mm});
            skLineSegment(sketch, "E13635", {"start": v(37.22, -9.2) * mm, "end": v(37.27, -9.64) * mm});
            skLineSegment(sketch, "E13636", {"start": v(37.27, -9.64) * mm, "end": v(37.3, -10.15) * mm});
            skLineSegment(sketch, "E13637", {"start": v(37.3, -10.15) * mm, "end": v(37.3, -10.71) * mm});
            skLineSegment(sketch, "E13638", {"start": v(37.3, -10.71) * mm, "end": v(37.27, -11.2) * mm});
            skLineSegment(sketch, "E13639", {"start": v(37.27, -11.2) * mm, "end": v(35.27, -12.01) * mm});
            skLineSegment(sketch, "E13640", {"start": v(35.27, -12.01) * mm, "end": v(34.9, -11.68) * mm});
            skLineSegment(sketch, "E13641", {"start": v(34.9, -11.68) * mm, "end": v(34.5, -11.28) * mm});
            skLineSegment(sketch, "E13642", {"start": v(34.5, -11.28) * mm, "end": v(34.16, -10.9) * mm});
            skLineSegment(sketch, "E13643", {"start": v(34.16, -10.9) * mm, "end": v(33.87, -10.56) * mm});
            skLineSegment(sketch, "E13644", {"start": v(33.87, -10.56) * mm, "end": v(33.64, -10.25) * mm});
            skLineSegment(sketch, "E13645", {"start": v(33.64, -10.25) * mm, "end": v(33.45, -9.97) * mm});
            skLineSegment(sketch, "E13646", {"start": v(33.45, -9.97) * mm, "end": v(33.32, -9.74) * mm});
            skLineSegment(sketch, "E13647", {"start": v(33.32, -9.74) * mm, "end": v(33.22, -9.56) * mm});
            skLineSegment(sketch, "E13648", {"start": v(33.22, -9.56) * mm, "end": v(33.15, -9.42) * mm});
            skLineSegment(sketch, "E13649", {"start": v(33.15, -9.42) * mm, "end": v(33.12, -9.34) * mm});
            skLineSegment(sketch, "E13650", {"start": v(33.12, -9.34) * mm, "end": v(33.1, -9.31) * mm});
            skLineSegment(sketch, "E13651", {"start": v(33.1, -9.31) * mm, "end": v(32.48, -7.34) * mm});
            skLineSegment(sketch, "E13652", {"start": v(32.48, -7.34) * mm, "end": v(29.34, -8.08) * mm});
            skLineSegment(sketch, "E13653", {"start": v(29.34, -8.08) * mm, "end": v(29.68, -10.11) * mm});
            skLineSegment(sketch, "E13654", {"start": v(29.68, -10.11) * mm, "end": v(29.68, -10.14) * mm});
            skLineSegment(sketch, "E13655", {"start": v(29.68, -10.14) * mm, "end": v(29.69, -10.23) * mm});
            skLineSegment(sketch, "E13656", {"start": v(29.69, -10.23) * mm, "end": v(29.7, -10.38) * mm});
            skLineSegment(sketch, "E13657", {"start": v(29.7, -10.38) * mm, "end": v(29.7, -10.6) * mm});
            skLineSegment(sketch, "E13658", {"start": v(29.7, -10.6) * mm, "end": v(29.67, -10.86) * mm});
            skLineSegment(sketch, "E13659", {"start": v(29.67, -10.86) * mm, "end": v(29.63, -11.18) * mm});
            skLineSegment(sketch, "E13660", {"start": v(29.63, -11.18) * mm, "end": v(29.57, -11.57) * mm});
            skLineSegment(sketch, "E13661", {"start": v(29.57, -11.57) * mm, "end": v(29.47, -12) * mm});
            skLineSegment(sketch, "E13662", {"start": v(29.47, -12) * mm, "end": v(29.34, -12.5) * mm});
            skLineSegment(sketch, "E13663", {"start": v(29.34, -12.5) * mm, "end": v(29.16, -13.03) * mm});
            skLineSegment(sketch, "E13664", {"start": v(29.16, -13.03) * mm, "end": v(28.98, -13.49) * mm});
            skLineSegment(sketch, "E13665", {"start": v(28.98, -13.49) * mm, "end": v(26.83, -13.65) * mm});
            skLineSegment(sketch, "E13666", {"start": v(26.83, -13.65) * mm, "end": v(26.58, -13.22) * mm});
            skLineSegment(sketch, "E13667", {"start": v(26.58, -13.22) * mm, "end": v(26.32, -12.72) * mm});
            skLineSegment(sketch, "E13668", {"start": v(26.32, -12.72) * mm, "end": v(26.12, -12.26) * mm});
            skLineSegment(sketch, "E13669", {"start": v(26.12, -12.26) * mm, "end": v(25.95, -11.84) * mm});
            skLineSegment(sketch, "E13670", {"start": v(25.95, -11.84) * mm, "end": v(25.83, -11.47) * mm});
            skLineSegment(sketch, "E13671", {"start": v(25.83, -11.47) * mm, "end": v(25.74, -11.16) * mm});
            skLineSegment(sketch, "E13672", {"start": v(25.74, -11.16) * mm, "end": v(25.68, -10.9) * mm});
            skLineSegment(sketch, "E13673", {"start": v(25.68, -10.9) * mm, "end": v(25.65, -10.69) * mm});
            skLineSegment(sketch, "E13674", {"start": v(25.65, -10.69) * mm, "end": v(25.63, -10.54) * mm});
            skLineSegment(sketch, "E13675", {"start": v(25.63, -10.54) * mm, "end": v(25.62, -10.45) * mm});
            skLineSegment(sketch, "E13676", {"start": v(25.62, -10.45) * mm, "end": v(25.62, -10.42) * mm});
            skLineSegment(sketch, "E13677", {"start": v(25.62, -10.42) * mm, "end": v(25.64, -8.36) * mm});
            skLineSegment(sketch, "E13678", {"start": v(25.64, -8.36) * mm, "end": v(22.43, -8.1) * mm});
            skLineSegment(sketch, "E13679", {"start": v(22.43, -8.1) * mm, "end": v(22.1, -10.14) * mm});
            skLineSegment(sketch, "E13680", {"start": v(22.1, -10.14) * mm, "end": v(22.1, -10.17) * mm});
            skLineSegment(sketch, "E13681", {"start": v(22.1, -10.17) * mm, "end": v(22.08, -10.26) * mm});
            skLineSegment(sketch, "E13682", {"start": v(22.08, -10.26) * mm, "end": v(22.04, -10.4) * mm});
            skLineSegment(sketch, "E13683", {"start": v(22.04, -10.4) * mm, "end": v(21.97, -10.6) * mm});
            skLineSegment(sketch, "E13684", {"start": v(21.97, -10.6) * mm, "end": v(21.87, -10.85) * mm});
            skLineSegment(sketch, "E13685", {"start": v(21.87, -10.85) * mm, "end": v(21.73, -11.15) * mm});
            skLineSegment(sketch, "E13686", {"start": v(21.73, -11.15) * mm, "end": v(21.55, -11.49) * mm});
            skLineSegment(sketch, "E13687", {"start": v(21.55, -11.49) * mm, "end": v(21.32, -11.88) * mm});
            skLineSegment(sketch, "E13688", {"start": v(21.32, -11.88) * mm, "end": v(21.04, -12.3) * mm});
            skLineSegment(sketch, "E13689", {"start": v(21.04, -12.3) * mm, "end": v(20.7, -12.76) * mm});
            skLineSegment(sketch, "E13690", {"start": v(20.7, -12.76) * mm, "end": v(20.39, -13.14) * mm});
            skLineSegment(sketch, "E13691", {"start": v(20.39, -13.14) * mm, "end": v(18.29, -12.64) * mm});
            skLineSegment(sketch, "E13692", {"start": v(18.29, -12.64) * mm, "end": v(18.19, -12.16) * mm});
            skLineSegment(sketch, "E13693", {"start": v(18.19, -12.16) * mm, "end": v(18.1, -11.6) * mm});
            skLineSegment(sketch, "E13694", {"start": v(18.1, -11.6) * mm, "end": v(18.05, -11.1) * mm});
            skLineSegment(sketch, "E13695", {"start": v(18.05, -11.1) * mm, "end": v(18.02, -10.65) * mm});
            skLineSegment(sketch, "E13696", {"start": v(18.02, -10.65) * mm, "end": v(18.02, -10.26) * mm});
            skLineSegment(sketch, "E13697", {"start": v(18.02, -10.26) * mm, "end": v(18.03, -9.93) * mm});
            skLineSegment(sketch, "E13698", {"start": v(18.03, -9.93) * mm, "end": v(18.06, -9.67) * mm});
            skLineSegment(sketch, "E13699", {"start": v(18.06, -9.67) * mm, "end": v(18.1, -9.46) * mm});
            skLineSegment(sketch, "E13700", {"start": v(18.1, -9.46) * mm, "end": v(18.12, -9.31) * mm});
            skLineSegment(sketch, "E13701", {"start": v(18.12, -9.31) * mm, "end": v(18.14, -9.23) * mm});
            skLineSegment(sketch, "E13702", {"start": v(18.14, -9.23) * mm, "end": v(18.15, -9.2) * mm});
            skLineSegment(sketch, "E13703", {"start": v(18.15, -9.2) * mm, "end": v(18.81, -7.24) * mm});
            skLineSegment(sketch, "E13704", {"start": v(18.81, -7.24) * mm, "end": v(15.84, -6.02) * mm});
            skLineSegment(sketch, "E13705", {"start": v(15.84, -6.02) * mm, "end": v(14.9, -7.86) * mm});
            skLineSegment(sketch, "E13706", {"start": v(14.9, -7.86) * mm, "end": v(14.88, -7.89) * mm});
            skLineSegment(sketch, "E13707", {"start": v(14.88, -7.89) * mm, "end": v(14.83, -7.97) * mm});
            skLineSegment(sketch, "E13708", {"start": v(14.83, -7.97) * mm, "end": v(14.75, -8.09) * mm});
            skLineSegment(sketch, "E13709", {"start": v(14.75, -8.09) * mm, "end": v(14.62, -8.26) * mm});
            skLineSegment(sketch, "E13710", {"start": v(14.62, -8.26) * mm, "end": v(14.45, -8.46) * mm});
            skLineSegment(sketch, "E13711", {"start": v(14.45, -8.46) * mm, "end": v(14.22, -8.7) * mm});
            skLineSegment(sketch, "E13712", {"start": v(14.22, -8.7) * mm, "end": v(13.94, -8.98) * mm});
            skLineSegment(sketch, "E13713", {"start": v(13.94, -8.98) * mm, "end": v(13.6, -9.27) * mm});
            skLineSegment(sketch, "E13714", {"start": v(13.6, -9.27) * mm, "end": v(13.2, -9.6) * mm});
            skLineSegment(sketch, "E13715", {"start": v(13.2, -9.6) * mm, "end": v(12.74, -9.92) * mm});
            skLineSegment(sketch, "E13716", {"start": v(12.74, -9.92) * mm, "end": v(12.32, -10.19) * mm});
            skLineSegment(sketch, "E13717", {"start": v(12.32, -10.19) * mm, "end": v(10.48, -9.07) * mm});
            skLineSegment(sketch, "E13718", {"start": v(10.48, -9.07) * mm, "end": v(10.54, -8.59) * mm});
            skLineSegment(sketch, "E13719", {"start": v(10.54, -8.59) * mm, "end": v(10.63, -8.03) * mm});
            skLineSegment(sketch, "E13720", {"start": v(10.63, -8.03) * mm, "end": v(10.73, -7.53) * mm});
            skLineSegment(sketch, "E13721", {"start": v(10.73, -7.53) * mm, "end": v(10.85, -7.1) * mm});
            skLineSegment(sketch, "E13722", {"start": v(10.85, -7.1) * mm, "end": v(10.97, -6.73) * mm});
            skLineSegment(sketch, "E13723", {"start": v(10.97, -6.73) * mm, "end": v(11.09, -6.43) * mm});
            skLineSegment(sketch, "E13724", {"start": v(11.09, -6.43) * mm, "end": v(11.2, -6.18) * mm});
            skLineSegment(sketch, "E13725", {"start": v(11.2, -6.18) * mm, "end": v(11.3, -6) * mm});
            skLineSegment(sketch, "E13726", {"start": v(11.3, -6) * mm, "end": v(11.36, -5.86) * mm});
            skLineSegment(sketch, "E13727", {"start": v(11.36, -5.86) * mm, "end": v(11.41, -5.79) * mm});
            skLineSegment(sketch, "E13728", {"start": v(11.41, -5.79) * mm, "end": v(11.43, -5.76) * mm});
            skLineSegment(sketch, "E13729", {"start": v(11.43, -5.76) * mm, "end": v(12.67, -4.1) * mm});
            skLineSegment(sketch, "E13730", {"start": v(12.67, -4.1) * mm, "end": v(10.23, -2.04) * mm});
            skLineSegment(sketch, "E13731", {"start": v(10.23, -2.04) * mm, "end": v(8.75, -3.5) * mm});
            skLineSegment(sketch, "E13732", {"start": v(8.75, -3.5) * mm, "end": v(8.73, -3.52) * mm});
            skLineSegment(sketch, "E13733", {"start": v(8.73, -3.52) * mm, "end": v(8.66, -3.58) * mm});
            skLineSegment(sketch, "E13734", {"start": v(8.66, -3.58) * mm, "end": v(8.54, -3.67) * mm});
            skLineSegment(sketch, "E13735", {"start": v(8.54, -3.67) * mm, "end": v(8.37, -3.8) * mm});
            skLineSegment(sketch, "E13736", {"start": v(8.37, -3.8) * mm, "end": v(8.14, -3.94) * mm});
            skLineSegment(sketch, "E13737", {"start": v(8.14, -3.94) * mm, "end": v(7.85, -4.1) * mm});
            skLineSegment(sketch, "E13738", {"start": v(7.85, -4.1) * mm, "end": v(7.5, -4.27) * mm});
            skLineSegment(sketch, "E13739", {"start": v(7.5, -4.27) * mm, "end": v(7.08, -4.45) * mm});
            skLineSegment(sketch, "E13740", {"start": v(7.08, -4.45) * mm, "end": v(6.6, -4.63) * mm});
            skLineSegment(sketch, "E13741", {"start": v(6.6, -4.63) * mm, "end": v(6.05, -4.8) * mm});
            skLineSegment(sketch, "E13742", {"start": v(6.05, -4.8) * mm, "end": v(5.57, -4.93) * mm});
            skLineSegment(sketch, "E13743", {"start": v(5.57, -4.93) * mm, "end": v(4.17, -3.31) * mm});
            skLineSegment(sketch, "E13744", {"start": v(4.17, -3.31) * mm, "end": v(4.38, -2.87) * mm});
            skLineSegment(sketch, "E13745", {"start": v(4.38, -2.87) * mm, "end": v(4.64, -2.36) * mm});
            skLineSegment(sketch, "E13746", {"start": v(4.64, -2.36) * mm, "end": v(4.9, -1.92) * mm});
            skLineSegment(sketch, "E13747", {"start": v(4.9, -1.92) * mm, "end": v(5.15, -1.55) * mm});
            skLineSegment(sketch, "E13748", {"start": v(5.15, -1.55) * mm, "end": v(5.38, -1.23) * mm});
            skLineSegment(sketch, "E13749", {"start": v(5.38, -1.23) * mm, "end": v(5.58, -0.98) * mm});
            skLineSegment(sketch, "E13750", {"start": v(5.58, -0.98) * mm, "end": v(5.76, -0.78) * mm});
            skLineSegment(sketch, "E13751", {"start": v(5.76, -0.78) * mm, "end": v(5.91, -0.63) * mm});
            skLineSegment(sketch, "E13752", {"start": v(5.91, -0.63) * mm, "end": v(6.02, -0.53) * mm});
            skLineSegment(sketch, "E13753", {"start": v(6.02, -0.53) * mm, "end": v(6.1, -0.47) * mm});
            skLineSegment(sketch, "E13754", {"start": v(6.1, -0.47) * mm, "end": v(6.12, -0.45) * mm});
            skLineSegment(sketch, "E13755", {"start": v(6.12, -0.45) * mm, "end": v(7.82, 0.75) * mm});
            skLineSegment(sketch, "E13756", {"start": v(7.82, 0.75) * mm, "end": v(6.14, 3.46) * mm});
            skLineSegment(sketch, "E13757", {"start": v(6.14, 3.46) * mm, "end": v(4.28, 2.51) * mm});
            skLineSegment(sketch, "E13758", {"start": v(4.28, 2.51) * mm, "end": v(4.25, 2.5) * mm});
            skLineSegment(sketch, "E13759", {"start": v(4.25, 2.5) * mm, "end": v(4.17, 2.47) * mm});
            skLineSegment(sketch, "E13760", {"start": v(4.17, 2.47) * mm, "end": v(4.03, 2.42) * mm});
            skLineSegment(sketch, "E13761", {"start": v(4.03, 2.42) * mm, "end": v(3.82, 2.36) * mm});
            skLineSegment(sketch, "E13762", {"start": v(3.82, 2.36) * mm, "end": v(3.56, 2.29) * mm});
            skLineSegment(sketch, "E13763", {"start": v(3.56, 2.29) * mm, "end": v(3.23, 2.22) * mm});
            skLineSegment(sketch, "E13764", {"start": v(3.23, 2.22) * mm, "end": v(2.84, 2.17) * mm});
            skLineSegment(sketch, "E13765", {"start": v(2.84, 2.17) * mm, "end": v(2.4, 2.12) * mm});
            skLineSegment(sketch, "E13766", {"start": v(2.4, 2.12) * mm, "end": v(1.88, 2.1) * mm});
            skLineSegment(sketch, "E13767", {"start": v(1.88, 2.1) * mm, "end": v(1.3, 2.1) * mm});
            skLineSegment(sketch, "E13768", {"start": v(1.3, 2.1) * mm, "end": v(0.8, 2.12) * mm});
            skLineSegment(sketch, "E13769", {"start": v(0.8, 2.12) * mm, "end": v(-0.02, 4.09) * mm});
            skLineSegment(sketch, "E13770", {"start": v(-0.02, 4.09) * mm, "end": v(0.32, 4.45) * mm});
            skLineSegment(sketch, "E13771", {"start": v(0.32, 4.45) * mm, "end": v(0.73, 4.85) * mm});
            skLineSegment(sketch, "E13772", {"start": v(0.73, 4.85) * mm, "end": v(1.1, 5.19) * mm});
            skLineSegment(sketch, "E13773", {"start": v(1.1, 5.19) * mm, "end": v(1.46, 5.47) * mm});
            skLineSegment(sketch, "E13774", {"start": v(1.46, 5.47) * mm, "end": v(1.78, 5.7) * mm});
            skLineSegment(sketch, "E13775", {"start": v(1.78, 5.7) * mm, "end": v(2.06, 5.88) * mm});
            skLineSegment(sketch, "E13776", {"start": v(2.06, 5.88) * mm, "end": v(2.3, 6.02) * mm});
            skLineSegment(sketch, "E13777", {"start": v(2.3, 6.02) * mm, "end": v(2.48, 6.11) * mm});
            skLineSegment(sketch, "E13778", {"start": v(2.48, 6.11) * mm, "end": v(2.62, 6.18) * mm});
            skLineSegment(sketch, "E13779", {"start": v(2.62, 6.18) * mm, "end": v(2.7, 6.2) * mm});
            skLineSegment(sketch, "E13780", {"start": v(2.7, 6.2) * mm, "end": v(2.73, 6.22) * mm});
            skLineSegment(sketch, "E13781", {"start": v(2.73, 6.22) * mm, "end": v(4.73, 6.84) * mm});
            skLineSegment(sketch, "E13782", {"start": v(4.73, 6.84) * mm, "end": v(3.98, 9.93) * mm});
            skLineSegment(sketch, "E13783", {"start": v(3.98, 9.93) * mm, "end": v(1.91, 9.6) * mm});
            skLineSegment(sketch, "E13784", {"start": v(1.91, 9.6) * mm, "end": v(1.88, 9.6) * mm});
            skLineSegment(sketch, "E13785", {"start": v(1.88, 9.6) * mm, "end": v(1.8, 9.59) * mm});
            skLineSegment(sketch, "E13786", {"start": v(1.8, 9.59) * mm, "end": v(1.64, 9.58) * mm});
            skLineSegment(sketch, "E13787", {"start": v(1.64, 9.58) * mm, "end": v(1.43, 9.59) * mm});
            skLineSegment(sketch, "E13788", {"start": v(1.43, 9.59) * mm, "end": v(1.16, 9.6) * mm});
            skLineSegment(sketch, "E13789", {"start": v(1.16, 9.6) * mm, "end": v(0.83, 9.64) * mm});
            skLineSegment(sketch, "E13790", {"start": v(0.83, 9.64) * mm, "end": v(0.44, 9.7) * mm});
            skLineSegment(sketch, "E13791", {"start": v(0.44, 9.7) * mm, "end": v(0, 9.8) * mm});
            skLineSegment(sketch, "E13792", {"start": v(0, 9.8) * mm, "end": v(-0.5, 9.93) * mm});
            skLineSegment(sketch, "E13793", {"start": v(-0.5, 9.93) * mm, "end": v(-1.05, 10.1) * mm});
            skLineSegment(sketch, "E13794", {"start": v(-1.05, 10.1) * mm, "end": v(-1.51, 10.28) * mm});
            skLineSegment(sketch, "E13795", {"start": v(-1.51, 10.28) * mm, "end": v(-1.68, 12.4) * mm});
            skLineSegment(sketch, "E13796", {"start": v(-1.68, 12.4) * mm, "end": v(-1.25, 12.65) * mm});
            skLineSegment(sketch, "E13797", {"start": v(-1.25, 12.65) * mm, "end": v(-0.73, 12.9) * mm});
            skLineSegment(sketch, "E13798", {"start": v(-0.73, 12.9) * mm, "end": v(-0.26, 13.1) * mm});
            skLineSegment(sketch, "E13799", {"start": v(-0.26, 13.1) * mm, "end": v(0.16, 13.27) * mm});
            skLineSegment(sketch, "E13800", {"start": v(0.16, 13.27) * mm, "end": v(0.53, 13.39) * mm});
            skLineSegment(sketch, "E13801", {"start": v(0.53, 13.39) * mm, "end": v(0.86, 13.48) * mm});
            skLineSegment(sketch, "E13802", {"start": v(0.86, 13.48) * mm, "end": v(1.12, 13.53) * mm});
            skLineSegment(sketch, "E13803", {"start": v(1.12, 13.53) * mm, "end": v(1.33, 13.57) * mm});
            skLineSegment(sketch, "E13804", {"start": v(1.33, 13.57) * mm, "end": v(1.48, 13.59) * mm});
            skLineSegment(sketch, "E13805", {"start": v(1.48, 13.59) * mm, "end": v(1.57, 13.6) * mm});
            skLineSegment(sketch, "E13806", {"start": v(1.57, 13.6) * mm, "end": v(1.6, 13.6) * mm});
            skLineSegment(sketch, "E13807", {"start": v(1.6, 13.6) * mm, "end": v(3.7, 13.58) * mm});
            skLineSegment(sketch, "E13808", {"start": v(3.7, 13.58) * mm, "end": v(3.96, 16.74) * mm});
            skLineSegment(sketch, "E13809", {"start": v(3.96, 16.74) * mm, "end": v(1.88, 17.06) * mm});
            skLineSegment(sketch, "E13810", {"start": v(1.88, 17.06) * mm, "end": v(1.85, 17.06) * mm});
            skLineSegment(sketch, "E13811", {"start": v(1.85, 17.06) * mm, "end": v(1.77, 17.08) * mm});
            skLineSegment(sketch, "E13812", {"start": v(1.77, 17.08) * mm, "end": v(1.62, 17.12) * mm});
            skLineSegment(sketch, "E13813", {"start": v(1.62, 17.12) * mm, "end": v(1.42, 17.2) * mm});
            skLineSegment(sketch, "E13814", {"start": v(1.42, 17.2) * mm, "end": v(1.17, 17.3) * mm});
            skLineSegment(sketch, "E13815", {"start": v(1.17, 17.3) * mm, "end": v(0.86, 17.43) * mm});
            skLineSegment(sketch, "E13816", {"start": v(0.86, 17.43) * mm, "end": v(0.52, 17.6) * mm});
            skLineSegment(sketch, "E13817", {"start": v(0.52, 17.6) * mm, "end": v(0.12, 17.83) * mm});
            skLineSegment(sketch, "E13818", {"start": v(0.12, 17.83) * mm, "end": v(-0.3, 18.1) * mm});
            skLineSegment(sketch, "E13819", {"start": v(-0.3, 18.1) * mm, "end": v(-0.77, 18.44) * mm});
            skLineSegment(sketch, "E13820", {"start": v(-0.77, 18.44) * mm, "end": v(-1.16, 18.75) * mm});
            skLineSegment(sketch, "E13821", {"start": v(-1.16, 18.75) * mm, "end": v(-0.65, 20.82) * mm});
            skLineSegment(sketch, "E13822", {"start": v(-0.65, 20.82) * mm, "end": v(-0.16, 20.91) * mm});
            skLineSegment(sketch, "E13823", {"start": v(-0.16, 20.91) * mm, "end": v(0.4, 21) * mm});
            skLineSegment(sketch, "E13824", {"start": v(0.4, 21) * mm, "end": v(0.92, 21.05) * mm});
            skLineSegment(sketch, "E13825", {"start": v(0.92, 21.05) * mm, "end": v(1.37, 21.08) * mm});
            skLineSegment(sketch, "E13826", {"start": v(1.37, 21.08) * mm, "end": v(1.76, 21.08) * mm});
            skLineSegment(sketch, "E13827", {"start": v(1.76, 21.08) * mm, "end": v(2.1, 21.06) * mm});
            skLineSegment(sketch, "E13828", {"start": v(2.1, 21.06) * mm, "end": v(2.37, 21.04) * mm});
            skLineSegment(sketch, "E13829", {"start": v(2.37, 21.04) * mm, "end": v(2.58, 21) * mm});
            skLineSegment(sketch, "E13830", {"start": v(2.58, 21) * mm, "end": v(2.72, 20.98) * mm});
            skLineSegment(sketch, "E13831", {"start": v(2.72, 20.98) * mm, "end": v(2.81, 20.96) * mm});
            skLineSegment(sketch, "E13832", {"start": v(2.81, 20.96) * mm, "end": v(2.84, 20.95) * mm});
            skLineSegment(sketch, "E13833", {"start": v(2.84, 20.95) * mm, "end": v(4.83, 20.3) * mm});
            skLineSegment(sketch, "E13834", {"start": v(4.83, 20.3) * mm, "end": v(6.07, 23.23) * mm});
            skLineSegment(sketch, "E13835", {"start": v(6.07, 23.23) * mm, "end": v(4.2, 24.16) * mm});
            skLineSegment(sketch, "E13836", {"start": v(4.2, 24.16) * mm, "end": v(4.17, 24.17) * mm});
            skLineSegment(sketch, "E13837", {"start": v(4.17, 24.17) * mm, "end": v(4.1, 24.22) * mm});
            skLineSegment(sketch, "E13838", {"start": v(4.1, 24.22) * mm, "end": v(3.97, 24.3) * mm});
            skLineSegment(sketch, "E13839", {"start": v(3.97, 24.3) * mm, "end": v(3.8, 24.43) * mm});
            skLineSegment(sketch, "E13840", {"start": v(3.8, 24.43) * mm, "end": v(3.59, 24.6) * mm});
            skLineSegment(sketch, "E13841", {"start": v(3.59, 24.6) * mm, "end": v(3.34, 24.82) * mm});
            skLineSegment(sketch, "E13842", {"start": v(3.34, 24.82) * mm, "end": v(3.07, 25.1) * mm});
            skLineSegment(sketch, "E13843", {"start": v(3.07, 25.1) * mm, "end": v(2.77, 25.43) * mm});
            skLineSegment(sketch, "E13844", {"start": v(2.77, 25.43) * mm, "end": v(2.44, 25.82) * mm});
            skLineSegment(sketch, "E13845", {"start": v(2.44, 25.82) * mm, "end": v(2.1, 26.28) * mm});
            skLineSegment(sketch, "E13846", {"start": v(2.1, 26.28) * mm, "end": v(1.84, 26.7) * mm});
            skLineSegment(sketch, "E13847", {"start": v(1.84, 26.7) * mm, "end": v(2.97, 28.5) * mm});
            skLineSegment(sketch, "E13848", {"start": v(2.97, 28.5) * mm, "end": v(3.46, 28.45) * mm});
            skLineSegment(sketch, "E13849", {"start": v(3.46, 28.45) * mm, "end": v(4.03, 28.36) * mm});
            skLineSegment(sketch, "E13850", {"start": v(4.03, 28.36) * mm, "end": v(4.53, 28.25) * mm});
            skLineSegment(sketch, "E13851", {"start": v(4.53, 28.25) * mm, "end": v(4.97, 28.14) * mm});
            skLineSegment(sketch, "E13852", {"start": v(4.97, 28.14) * mm, "end": v(5.35, 28.02) * mm});
            skLineSegment(sketch, "E13853", {"start": v(5.35, 28.02) * mm, "end": v(5.66, 27.9) * mm});
            skLineSegment(sketch, "E13854", {"start": v(5.66, 27.9) * mm, "end": v(5.9, 27.8) * mm});
            skLineSegment(sketch, "E13855", {"start": v(5.9, 27.8) * mm, "end": v(6.1, 27.7) * mm});
            skLineSegment(sketch, "E13856", {"start": v(6.1, 27.7) * mm, "end": v(6.23, 27.63) * mm});
            skLineSegment(sketch, "E13857", {"start": v(6.23, 27.63) * mm, "end": v(6.3, 27.59) * mm});
            skLineSegment(sketch, "E13858", {"start": v(6.3, 27.59) * mm, "end": v(6.33, 27.57) * mm});
            skLineSegment(sketch, "E13859", {"start": v(6.33, 27.57) * mm, "end": v(8.02, 26.34) * mm});
            skLineSegment(sketch, "E13860", {"start": v(8.02, 26.34) * mm, "end": v(10.11, 28.75) * mm});
            skLineSegment(sketch, "E13861", {"start": v(10.11, 28.75) * mm, "end": v(8.63, 30.2) * mm});
            skLineSegment(sketch, "E13862", {"start": v(8.63, 30.2) * mm, "end": v(8.6, 30.23) * mm});
            skLineSegment(sketch, "E13863", {"start": v(8.6, 30.23) * mm, "end": v(8.55, 30.3) * mm});
            skLineSegment(sketch, "E13864", {"start": v(8.55, 30.3) * mm, "end": v(8.45, 30.41) * mm});
            skLineSegment(sketch, "E13865", {"start": v(8.45, 30.41) * mm, "end": v(8.33, 30.58) * mm});
            skLineSegment(sketch, "E13866", {"start": v(8.33, 30.58) * mm, "end": v(8.19, 30.81) * mm});
            skLineSegment(sketch, "E13867", {"start": v(8.19, 30.81) * mm, "end": v(8.02, 31.1) * mm});
            skLineSegment(sketch, "E13868", {"start": v(8.02, 31.1) * mm, "end": v(7.85, 31.44) * mm});
            skLineSegment(sketch, "E13869", {"start": v(7.85, 31.44) * mm, "end": v(7.66, 31.85) * mm});
            skLineSegment(sketch, "E13870", {"start": v(7.66, 31.85) * mm, "end": v(7.48, 32.33) * mm});
            skLineSegment(sketch, "E13871", {"start": v(7.48, 32.33) * mm, "end": v(7.3, 32.86) * mm});
            skLineSegment(sketch, "E13872", {"start": v(7.3, 32.86) * mm, "end": v(7.18, 33.34) * mm});
            skLineSegment(sketch, "E13873", {"start": v(7.18, 33.34) * mm, "end": v(8.82, 34.71) * mm});
            skLineSegment(sketch, "E13874", {"start": v(8.82, 34.71) * mm, "end": v(9.27, 34.51) * mm});
            skLineSegment(sketch, "E13875", {"start": v(9.27, 34.51) * mm, "end": v(9.78, 34.25) * mm});
            skLineSegment(sketch, "E13876", {"start": v(9.78, 34.25) * mm, "end": v(10.23, 34) * mm});
            skLineSegment(sketch, "E13877", {"start": v(10.23, 34) * mm, "end": v(10.61, 33.76) * mm});
            skLineSegment(sketch, "E13878", {"start": v(10.61, 33.76) * mm, "end": v(10.93, 33.53) * mm});
            skLineSegment(sketch, "E13879", {"start": v(10.93, 33.53) * mm, "end": v(11.19, 33.33) * mm});
            skLineSegment(sketch, "E13880", {"start": v(11.19, 33.33) * mm, "end": v(11.4, 33.15) * mm});
            skLineSegment(sketch, "E13881", {"start": v(11.4, 33.15) * mm, "end": v(11.55, 33) * mm});
            skLineSegment(sketch, "E13882", {"start": v(11.55, 33) * mm, "end": v(11.65, 32.9) * mm});
            skLineSegment(sketch, "E13883", {"start": v(11.65, 32.9) * mm, "end": v(11.7, 32.83) * mm});
            skLineSegment(sketch, "E13884", {"start": v(11.7, 32.83) * mm, "end": v(11.72, 32.8) * mm});
            skLineSegment(sketch, "E13885", {"start": v(11.72, 32.8) * mm, "end": v(12.94, 31.12) * mm});
            skLineSegment(sketch, "E13886", {"start": v(12.94, 31.12) * mm, "end": v(15.7, 32.78) * mm});
            skLineSegment(sketch, "E13887", {"start": v(15.7, 32.78) * mm, "end": v(14.74, 34.61) * mm});
            skLineSegment(sketch, "E13888", {"start": v(14.74, 34.61) * mm, "end": v(14.72, 34.64) * mm});
            skLineSegment(sketch, "E13889", {"start": v(14.72, 34.64) * mm, "end": v(14.69, 34.72) * mm});
            skLineSegment(sketch, "E13890", {"start": v(14.69, 34.72) * mm, "end": v(14.64, 34.86) * mm});
            skLineSegment(sketch, "E13891", {"start": v(14.64, 34.86) * mm, "end": v(14.57, 35.06) * mm});
            skLineSegment(sketch, "E13892", {"start": v(14.57, 35.06) * mm, "end": v(14.5, 35.32) * mm});
            skLineSegment(sketch, "E13893", {"start": v(14.5, 35.32) * mm, "end": v(14.44, 35.64) * mm});
            skLineSegment(sketch, "E13894", {"start": v(14.44, 35.64) * mm, "end": v(14.38, 36.02) * mm});
            skLineSegment(sketch, "E13895", {"start": v(14.38, 36.02) * mm, "end": v(14.34, 36.47) * mm});
            skLineSegment(sketch, "E13896", {"start": v(14.34, 36.47) * mm, "end": v(14.31, 36.98) * mm});
            skLineSegment(sketch, "E13897", {"start": v(14.31, 36.98) * mm, "end": v(14.31, 37.54) * mm});
            skLineSegment(sketch, "E13898", {"start": v(14.31, 37.54) * mm, "end": v(14.34, 38.03) * mm});
            skLineSegment(sketch, "E13899", {"start": v(14.34, 38.03) * mm, "end": v(16.34, 38.84) * mm});
            skLineSegment(sketch, "E13900", {"start": v(16.34, 38.84) * mm, "end": v(16.7, 38.51) * mm});
            skLineSegment(sketch, "E13901", {"start": v(16.7, 38.51) * mm, "end": v(17.1, 38.1) * mm});
            skLineSegment(sketch, "E13902", {"start": v(17.1, 38.1) * mm, "end": v(17.45, 37.73) * mm});
            skLineSegment(sketch, "E13903", {"start": v(17.45, 37.73) * mm, "end": v(17.74, 37.39) * mm});
            skLineSegment(sketch, "E13904", {"start": v(17.74, 37.39) * mm, "end": v(17.97, 37.07) * mm});
            skLineSegment(sketch, "E13905", {"start": v(17.97, 37.07) * mm, "end": v(18.15, 36.8) * mm});
            skLineSegment(sketch, "E13906", {"start": v(18.15, 36.8) * mm, "end": v(18.3, 36.57) * mm});
            skLineSegment(sketch, "E13907", {"start": v(18.3, 36.57) * mm, "end": v(18.39, 36.38) * mm});
            skLineSegment(sketch, "E13908", {"start": v(18.39, 36.38) * mm, "end": v(18.45, 36.25) * mm});
            skLineSegment(sketch, "E13909", {"start": v(18.45, 36.25) * mm, "end": v(18.49, 36.17) * mm});
            skLineSegment(sketch, "E13910", {"start": v(18.49, 36.17) * mm, "end": v(18.5, 36.14) * mm});
            skLineSegment(sketch, "E13911", {"start": v(18.5, 36.14) * mm, "end": v(19.13, 34.17) * mm});
            skLineSegment(sketch, "E13912", {"start": v(19.13, 34.17) * mm, "end": v(22.27, 34.9) * mm});
            skLineSegment(sketch, "E13913", {"start": v(22.27, 34.9) * mm, "end": v(21.93, 36.94) * mm});
            skLineSegment(sketch, "E13914", {"start": v(21.93, 36.94) * mm, "end": v(21.93, 36.97) * mm});
            skLineSegment(sketch, "E13915", {"start": v(21.93, 36.97) * mm, "end": v(21.92, 37.06) * mm});
            skLineSegment(sketch, "E13916", {"start": v(21.92, 37.06) * mm, "end": v(21.91, 37.21) * mm});
            skLineSegment(sketch, "E13917", {"start": v(21.91, 37.21) * mm, "end": v(21.92, 37.42) * mm});
            skLineSegment(sketch, "E13918", {"start": v(21.92, 37.42) * mm, "end": v(21.93, 37.69) * mm});
            skLineSegment(sketch, "E13919", {"start": v(21.93, 37.69) * mm, "end": v(21.97, 38.01) * mm});
            skLineSegment(sketch, "E13920", {"start": v(21.97, 38.01) * mm, "end": v(22.04, 38.4) * mm});
            skLineSegment(sketch, "E13921", {"start": v(22.04, 38.4) * mm, "end": v(22.13, 38.83) * mm});
            skLineSegment(sketch, "E13922", {"start": v(22.13, 38.83) * mm, "end": v(22.27, 39.32) * mm});
            skLineSegment(sketch, "E13923", {"start": v(22.27, 39.32) * mm, "end": v(22.45, 39.86) * mm});
            skLineSegment(sketch, "E13924", {"start": v(22.45, 39.86) * mm, "end": v(22.62, 40.31) * mm});
            skLineSegment(sketch, "E13925", {"start": v(22.62, 40.31) * mm, "end": v(24.78, 40.48) * mm});
            skLineSegment(sketch, "E13926", {"start": v(24.78, 40.48) * mm, "end": v(25.02, 40.05) * mm});
            skLineSegment(sketch, "E13927", {"start": v(25.02, 40.05) * mm, "end": v(25.28, 39.55) * mm});
            skLineSegment(sketch, "E13928", {"start": v(25.28, 39.55) * mm, "end": v(25.5, 39.08) * mm});
            skLineSegment(sketch, "E13929", {"start": v(25.5, 39.08) * mm, "end": v(25.65, 38.67) * mm});
            skLineSegment(sketch, "E13930", {"start": v(25.65, 38.67) * mm, "end": v(25.78, 38.3) * mm});
            skLineSegment(sketch, "E13931", {"start": v(25.78, 38.3) * mm, "end": v(25.87, 37.98) * mm});
            skLineSegment(sketch, "E13932", {"start": v(25.87, 37.98) * mm, "end": v(25.92, 37.72) * mm});
            skLineSegment(sketch, "E13933", {"start": v(25.92, 37.72) * mm, "end": v(25.96, 37.52) * mm});
            skLineSegment(sketch, "E13934", {"start": v(25.96, 37.52) * mm, "end": v(25.98, 37.37) * mm});
            skLineSegment(sketch, "E13935", {"start": v(25.98, 37.37) * mm, "end": v(25.98, 37.28) * mm});
            skLineSegment(sketch, "E13936", {"start": v(25.98, 37.28) * mm, "end": v(25.99, 37.25) * mm});
            skLineSegment(sketch, "E13937", {"start": v(25.99, 37.25) * mm, "end": v(25.97, 35.18) * mm});
            skLineSegment(sketch, "E13938", {"start": v(25.97, 35.18) * mm, "end": v(29.18, 34.93) * mm});
            skLineSegment(sketch, "E13939", {"start": v(29.18, 34.93) * mm, "end": v(29.5, 36.97) * mm});
            skLineSegment(sketch, "E13940", {"start": v(29.5, 36.97) * mm, "end": v(29.5, 37) * mm});
            skLineSegment(sketch, "E13941", {"start": v(29.5, 37) * mm, "end": v(29.53, 37.09) * mm});
            skLineSegment(sketch, "E13942", {"start": v(29.53, 37.09) * mm, "end": v(29.57, 37.23) * mm});
            skLineSegment(sketch, "E13943", {"start": v(29.57, 37.23) * mm, "end": v(29.64, 37.43) * mm});
            skLineSegment(sketch, "E13944", {"start": v(29.64, 37.43) * mm, "end": v(29.74, 37.68) * mm});
            skLineSegment(sketch, "E13945", {"start": v(29.74, 37.68) * mm, "end": v(29.88, 37.97) * mm});
            skLineSegment(sketch, "E13946", {"start": v(29.88, 37.97) * mm, "end": v(30.06, 38.32) * mm});
            skLineSegment(sketch, "E13947", {"start": v(30.06, 38.32) * mm, "end": v(30.29, 38.7) * mm});
            skLineSegment(sketch, "E13948", {"start": v(30.29, 38.7) * mm, "end": v(30.57, 39.13) * mm});
            skLineSegment(sketch, "E13949", {"start": v(30.57, 39.13) * mm, "end": v(30.9, 39.58) * mm});
            skLineSegment(sketch, "E13950", {"start": v(30.9, 39.58) * mm, "end": v(31.22, 39.97) * mm});
            skLineSegment(sketch, "E13951", {"start": v(31.22, 39.97) * mm, "end": v(33.32, 39.46) * mm});
            skLineSegment(sketch, "E13952", {"start": v(33.32, 39.46) * mm, "end": v(33.42, 38.99) * mm});
            skLineSegment(sketch, "E13953", {"start": v(33.42, 38.99) * mm, "end": v(33.5, 38.43) * mm});
            skLineSegment(sketch, "E13954", {"start": v(33.5, 38.43) * mm, "end": v(33.56, 37.92) * mm});
            skLineSegment(sketch, "E13955", {"start": v(33.56, 37.92) * mm, "end": v(33.59, 37.48) * mm});
            skLineSegment(sketch, "E13956", {"start": v(33.59, 37.48) * mm, "end": v(33.59, 37.09) * mm});
            skLineSegment(sketch, "E13957", {"start": v(33.59, 37.09) * mm, "end": v(33.57, 36.76) * mm});
            skLineSegment(sketch, "E13958", {"start": v(33.57, 36.76) * mm, "end": v(33.55, 36.5) * mm});
            skLineSegment(sketch, "E13959", {"start": v(33.55, 36.5) * mm, "end": v(33.52, 36.29) * mm});
            skLineSegment(sketch, "E13960", {"start": v(33.52, 36.29) * mm, "end": v(33.49, 36.14) * mm});
            skLineSegment(sketch, "E13961", {"start": v(33.49, 36.14) * mm, "end": v(33.46, 36.06) * mm});
            skLineSegment(sketch, "E13962", {"start": v(33.46, 36.06) * mm, "end": v(33.46, 36.03) * mm});
            skLineSegment(sketch, "E13963", {"start": v(33.46, 36.03) * mm, "end": v(32.8, 34.07) * mm});
            skLineSegment(sketch, "E13964", {"start": v(32.8, 34.07) * mm, "end": v(35.77, 32.85) * mm});
            skLineSegment(sketch, "E13965", {"start": v(35.77, 32.85) * mm, "end": v(36.71, 34.7) * mm});
            skLineSegment(sketch, "E13966", {"start": v(36.71, 34.7) * mm, "end": v(36.73, 34.72) * mm});
            skLineSegment(sketch, "E13967", {"start": v(36.73, 34.72) * mm, "end": v(36.77, 34.8) * mm});
            skLineSegment(sketch, "E13968", {"start": v(36.77, 34.8) * mm, "end": v(36.86, 34.92) * mm});
            skLineSegment(sketch, "E13969", {"start": v(36.86, 34.92) * mm, "end": v(36.99, 35.08) * mm});
            skLineSegment(sketch, "E13970", {"start": v(36.99, 35.08) * mm, "end": v(37.16, 35.3) * mm});
            skLineSegment(sketch, "E13971", {"start": v(37.16, 35.3) * mm, "end": v(37.39, 35.53) * mm});
            skLineSegment(sketch, "E13972", {"start": v(37.39, 35.53) * mm, "end": v(37.67, 35.8) * mm});
            skLineSegment(sketch, "E13973", {"start": v(37.67, 35.8) * mm, "end": v(38, 36.1) * mm});
            skLineSegment(sketch, "E13974", {"start": v(38, 36.1) * mm, "end": v(38.4, 36.42) * mm});
            skLineSegment(sketch, "E13975", {"start": v(38.4, 36.42) * mm, "end": v(38.87, 36.75) * mm});
            skLineSegment(sketch, "E13976", {"start": v(38.87, 36.75) * mm, "end": v(39.29, 37.02) * mm});
            skLineSegment(sketch, "E13977", {"start": v(39.29, 37.02) * mm, "end": v(41.13, 35.9) * mm});
            skLineSegment(sketch, "E13978", {"start": v(41.13, 35.9) * mm, "end": v(41.07, 35.42) * mm});
            skLineSegment(sketch, "E13979", {"start": v(41.07, 35.42) * mm, "end": v(40.98, 34.86) * mm});
            skLineSegment(sketch, "E13980", {"start": v(40.98, 34.86) * mm, "end": v(40.87, 34.36) * mm});
            skLineSegment(sketch, "E13981", {"start": v(40.87, 34.36) * mm, "end": v(40.76, 33.93) * mm});
            skLineSegment(sketch, "E13982", {"start": v(40.76, 33.93) * mm, "end": v(40.64, 33.56) * mm});
            skLineSegment(sketch, "E13983", {"start": v(40.64, 33.56) * mm, "end": v(40.52, 33.25) * mm});
            skLineSegment(sketch, "E13984", {"start": v(40.52, 33.25) * mm, "end": v(40.4, 33) * mm});
            skLineSegment(sketch, "E13985", {"start": v(40.4, 33) * mm, "end": v(40.32, 32.82) * mm});
            skLineSegment(sketch, "E13986", {"start": v(40.32, 32.82) * mm, "end": v(40.24, 32.7) * mm});
            skLineSegment(sketch, "E13987", {"start": v(40.24, 32.7) * mm, "end": v(40.2, 32.62) * mm});
            skLineSegment(sketch, "E13988", {"start": v(40.2, 32.62) * mm, "end": v(40.18, 32.6) * mm});
            skLineSegment(sketch, "E13989", {"start": v(40.18, 32.6) * mm, "end": v(38.93, 30.93) * mm});
            skLineSegment(sketch, "E13990", {"start": v(38.93, 30.93) * mm, "end": v(41.38, 28.87) * mm});
            skCircle(sketch, "E13991", {"center": v(25.8, 13.41) * mm, "radius": 1.25 * mm});
            skLineSegment(sketch, "E13992", {"start": v(22.8, 11.35) * mm, "end": v(28.8, 11.35) * mm});
            skLineSegment(sketch, "E13993", {"start": v(28.8, 11.35) * mm, "end": v(28.8, 15.48) * mm});
            skLineSegment(sketch, "E13994", {"start": v(28.8, 15.48) * mm, "end": v(22.8, 15.48) * mm});
            skLineSegment(sketch, "E13995", {"start": v(22.8, 15.48) * mm, "end": v(22.8, 11.35) * mm});
            skCircle(sketch, "E13996", {"center": v(25.8, 13.41) * mm, "radius": 3.75 * mm});
            skLineSegment(sketch, "E13997", {"start": v(-20.63, 27.57) * mm, "end": v(-19.12, 29.14) * mm});
            skLineSegment(sketch, "E13998", {"start": v(-19.12, 29.14) * mm, "end": v(-19.1, 29.16) * mm});
            skLineSegment(sketch, "E13999", {"start": v(-19.1, 29.16) * mm, "end": v(-19.04, 29.21) * mm});
            skLineSegment(sketch, "E14000", {"start": v(-19.04, 29.21) * mm, "end": v(-18.94, 29.3) * mm});
            skLineSegment(sketch, "E14001", {"start": v(-18.94, 29.3) * mm, "end": v(-18.78, 29.41) * mm});
            skLineSegment(sketch, "E14002", {"start": v(-18.78, 29.41) * mm, "end": v(-18.58, 29.54) * mm});
            skLineSegment(sketch, "E14003", {"start": v(-18.58, 29.54) * mm, "end": v(-18.32, 29.7) * mm});
            skLineSegment(sketch, "E14004", {"start": v(-18.32, 29.7) * mm, "end": v(-18, 29.86) * mm});
            skLineSegment(sketch, "E14005", {"start": v(-18, 29.86) * mm, "end": v(-17.63, 30.03) * mm});
            skLineSegment(sketch, "E14006", {"start": v(-17.63, 30.03) * mm, "end": v(-17.2, 30.2) * mm});
            skLineSegment(sketch, "E14007", {"start": v(-17.2, 30.2) * mm, "end": v(-16.71, 30.37) * mm});
            skLineSegment(sketch, "E14008", {"start": v(-16.71, 30.37) * mm, "end": v(-16.17, 30.53) * mm});
            skLineSegment(sketch, "E14009", {"start": v(-16.17, 30.53) * mm, "end": v(-16, 30.57) * mm});
            skArc(sketch, "E14010", {"start": v(-16, 30.57) * mm, "mid": v(-15.3, 29.78) * mm, "end": v(-14.62, 28.96) * mm});
            skLineSegment(sketch, "E14011", {"start": v(-14.62, 28.96) * mm, "end": v(-14.68, 28.81) * mm});
            skLineSegment(sketch, "E14012", {"start": v(-14.68, 28.81) * mm, "end": v(-14.91, 28.3) * mm});
            skLineSegment(sketch, "E14013", {"start": v(-14.91, 28.3) * mm, "end": v(-15.15, 27.83) * mm});
            skLineSegment(sketch, "E14014", {"start": v(-15.15, 27.83) * mm, "end": v(-15.38, 27.43) * mm});
            skLineSegment(sketch, "E14015", {"start": v(-15.38, 27.43) * mm, "end": v(-15.6, 27.09) * mm});
            skLineSegment(sketch, "E14016", {"start": v(-15.6, 27.09) * mm, "end": v(-15.81, 26.8) * mm});
            skLineSegment(sketch, "E14017", {"start": v(-15.81, 26.8) * mm, "end": v(-16, 26.57) * mm});
            skLineSegment(sketch, "E14018", {"start": v(-16, 26.57) * mm, "end": v(-16.16, 26.38) * mm});
            skLineSegment(sketch, "E14019", {"start": v(-16.16, 26.38) * mm, "end": v(-16.3, 26.25) * mm});
            skLineSegment(sketch, "E14020", {"start": v(-16.3, 26.25) * mm, "end": v(-16.4, 26.15) * mm});
            skLineSegment(sketch, "E14021", {"start": v(-16.4, 26.15) * mm, "end": v(-16.46, 26.1) * mm});
            skLineSegment(sketch, "E14022", {"start": v(-16.46, 26.1) * mm, "end": v(-16.48, 26.08) * mm});
            skLineSegment(sketch, "E14023", {"start": v(-16.48, 26.08) * mm, "end": v(-18.25, 24.82) * mm});
            skArc(sketch, "E14024", {"start": v(-18.25, 24.82) * mm, "mid": v(-17.37, 23.48) * mm, "end": v(-16.6, 22.07) * mm});
            skLineSegment(sketch, "E14025", {"start": v(-16.6, 22.07) * mm, "end": v(-14.65, 23.03) * mm});
            skLineSegment(sketch, "E14026", {"start": v(-14.65, 23.03) * mm, "end": v(-14.63, 23.05) * mm});
            skLineSegment(sketch, "E14027", {"start": v(-14.63, 23.05) * mm, "end": v(-14.55, 23.08) * mm});
            skLineSegment(sketch, "E14028", {"start": v(-14.55, 23.08) * mm, "end": v(-14.42, 23.12) * mm});
            skLineSegment(sketch, "E14029", {"start": v(-14.42, 23.12) * mm, "end": v(-14.24, 23.17) * mm});
            skLineSegment(sketch, "E14030", {"start": v(-14.24, 23.17) * mm, "end": v(-14, 23.23) * mm});
            skLineSegment(sketch, "E14031", {"start": v(-14, 23.23) * mm, "end": v(-13.7, 23.28) * mm});
            skLineSegment(sketch, "E14032", {"start": v(-13.7, 23.28) * mm, "end": v(-13.36, 23.33) * mm});
            skLineSegment(sketch, "E14033", {"start": v(-13.36, 23.33) * mm, "end": v(-12.95, 23.36) * mm});
            skLineSegment(sketch, "E14034", {"start": v(-12.95, 23.36) * mm, "end": v(-12.49, 23.38) * mm});
            skLineSegment(sketch, "E14035", {"start": v(-12.49, 23.38) * mm, "end": v(-11.97, 23.37) * mm});
            skLineSegment(sketch, "E14036", {"start": v(-11.97, 23.37) * mm, "end": v(-11.4, 23.33) * mm});
            skLineSegment(sketch, "E14037", {"start": v(-11.4, 23.33) * mm, "end": v(-11.24, 23.31) * mm});
            skArc(sketch, "E14038", {"start": v(-11.24, 23.31) * mm, "mid": v(-10.84, 22.33) * mm, "end": v(-10.48, 21.33) * mm});
            skLineSegment(sketch, "E14039", {"start": v(-10.48, 21.33) * mm, "end": v(-10.59, 21.2) * mm});
            skLineSegment(sketch, "E14040", {"start": v(-10.59, 21.2) * mm, "end": v(-10.99, 20.8) * mm});
            skLineSegment(sketch, "E14041", {"start": v(-10.99, 20.8) * mm, "end": v(-11.37, 20.45) * mm});
            skLineSegment(sketch, "E14042", {"start": v(-11.37, 20.45) * mm, "end": v(-11.72, 20.15) * mm});
            skLineSegment(sketch, "E14043", {"start": v(-11.72, 20.15) * mm, "end": v(-12.05, 19.9) * mm});
            skLineSegment(sketch, "E14044", {"start": v(-12.05, 19.9) * mm, "end": v(-12.34, 19.7) * mm});
            skLineSegment(sketch, "E14045", {"start": v(-12.34, 19.7) * mm, "end": v(-12.6, 19.55) * mm});
            skLineSegment(sketch, "E14046", {"start": v(-12.6, 19.55) * mm, "end": v(-12.81, 19.43) * mm});
            skLineSegment(sketch, "E14047", {"start": v(-12.81, 19.43) * mm, "end": v(-12.98, 19.35) * mm});
            skLineSegment(sketch, "E14048", {"start": v(-12.98, 19.35) * mm, "end": v(-13.1, 19.3) * mm});
            skLineSegment(sketch, "E14049", {"start": v(-13.1, 19.3) * mm, "end": v(-13.19, 19.27) * mm});
            skLineSegment(sketch, "E14050", {"start": v(-13.19, 19.27) * mm, "end": v(-13.21, 19.26) * mm});
            skLineSegment(sketch, "E14051", {"start": v(-13.21, 19.26) * mm, "end": v(-15.3, 18.68) * mm});
            skArc(sketch, "E14052", {"start": v(-15.3, 18.68) * mm, "mid": v(-14.94, 17.12) * mm, "end": v(-14.7, 15.53) * mm});
            skLineSegment(sketch, "E14053", {"start": v(-14.7, 15.53) * mm, "end": v(-12.54, 15.77) * mm});
            skLineSegment(sketch, "E14054", {"start": v(-12.54, 15.77) * mm, "end": v(-12.51, 15.77) * mm});
            skLineSegment(sketch, "E14055", {"start": v(-12.51, 15.77) * mm, "end": v(-12.43, 15.77) * mm});
            skLineSegment(sketch, "E14056", {"start": v(-12.43, 15.77) * mm, "end": v(-12.3, 15.77) * mm});
            skLineSegment(sketch, "E14057", {"start": v(-12.3, 15.77) * mm, "end": v(-12.1, 15.76) * mm});
            skLineSegment(sketch, "E14058", {"start": v(-12.1, 15.76) * mm, "end": v(-11.86, 15.73) * mm});
            skLineSegment(sketch, "E14059", {"start": v(-11.86, 15.73) * mm, "end": v(-11.57, 15.68) * mm});
            skLineSegment(sketch, "E14060", {"start": v(-11.57, 15.68) * mm, "end": v(-11.22, 15.6) * mm});
            skLineSegment(sketch, "E14061", {"start": v(-11.22, 15.6) * mm, "end": v(-10.83, 15.5) * mm});
            skLineSegment(sketch, "E14062", {"start": v(-10.83, 15.5) * mm, "end": v(-10.39, 15.35) * mm});
            skLineSegment(sketch, "E14063", {"start": v(-10.39, 15.35) * mm, "end": v(-9.9, 15.17) * mm});
            skLineSegment(sketch, "E14064", {"start": v(-9.9, 15.17) * mm, "end": v(-9.38, 14.94) * mm});
            skLineSegment(sketch, "E14065", {"start": v(-9.38, 14.94) * mm, "end": v(-9.24, 14.86) * mm});
            skArc(sketch, "E14066", {"start": v(-9.24, 14.86) * mm, "mid": v(-9.2, 13.8) * mm, "end": v(-9.2, 12.74) * mm});
            skLineSegment(sketch, "E14067", {"start": v(-9.2, 12.74) * mm, "end": v(-9.35, 12.66) * mm});
            skLineSegment(sketch, "E14068", {"start": v(-9.35, 12.66) * mm, "end": v(-9.86, 12.42) * mm});
            skLineSegment(sketch, "E14069", {"start": v(-9.86, 12.42) * mm, "end": v(-10.34, 12.22) * mm});
            skLineSegment(sketch, "E14070", {"start": v(-10.34, 12.22) * mm, "end": v(-10.77, 12.06) * mm});
            skLineSegment(sketch, "E14071", {"start": v(-10.77, 12.06) * mm, "end": v(-11.16, 11.94) * mm});
            skLineSegment(sketch, "E14072", {"start": v(-11.16, 11.94) * mm, "end": v(-11.5, 11.85) * mm});
            skLineSegment(sketch, "E14073", {"start": v(-11.5, 11.85) * mm, "end": v(-11.8, 11.8) * mm});
            skLineSegment(sketch, "E14074", {"start": v(-11.8, 11.8) * mm, "end": v(-12.04, 11.76) * mm});
            skLineSegment(sketch, "E14075", {"start": v(-12.04, 11.76) * mm, "end": v(-12.23, 11.74) * mm});
            skLineSegment(sketch, "E14076", {"start": v(-12.23, 11.74) * mm, "end": v(-12.37, 11.73) * mm});
            skLineSegment(sketch, "E14077", {"start": v(-12.37, 11.73) * mm, "end": v(-12.45, 11.73) * mm});
            skLineSegment(sketch, "E14078", {"start": v(-12.45, 11.73) * mm, "end": v(-12.48, 11.73) * mm});
            skLineSegment(sketch, "E14079", {"start": v(-12.48, 11.73) * mm, "end": v(-14.65, 11.9) * mm});
            skArc(sketch, "E14080", {"start": v(-14.65, 11.9) * mm, "mid": v(-14.84, 10.3) * mm, "end": v(-15.15, 8.74) * mm});
            skLineSegment(sketch, "E14081", {"start": v(-15.15, 8.74) * mm, "end": v(-13.04, 8.22) * mm});
            skLineSegment(sketch, "E14082", {"start": v(-13.04, 8.22) * mm, "end": v(-13.01, 8.21) * mm});
            skLineSegment(sketch, "E14083", {"start": v(-13.01, 8.21) * mm, "end": v(-12.94, 8.19) * mm});
            skLineSegment(sketch, "E14084", {"start": v(-12.94, 8.19) * mm, "end": v(-12.81, 8.14) * mm});
            skLineSegment(sketch, "E14085", {"start": v(-12.81, 8.14) * mm, "end": v(-12.64, 8.06) * mm});
            skLineSegment(sketch, "E14086", {"start": v(-12.64, 8.06) * mm, "end": v(-12.42, 7.95) * mm});
            skLineSegment(sketch, "E14087", {"start": v(-12.42, 7.95) * mm, "end": v(-12.16, 7.8) * mm});
            skLineSegment(sketch, "E14088", {"start": v(-12.16, 7.8) * mm, "end": v(-11.86, 7.61) * mm});
            skLineSegment(sketch, "E14089", {"start": v(-11.86, 7.61) * mm, "end": v(-11.52, 7.38) * mm});
            skLineSegment(sketch, "E14090", {"start": v(-11.52, 7.38) * mm, "end": v(-11.16, 7.1) * mm});
            skLineSegment(sketch, "E14091", {"start": v(-11.16, 7.1) * mm, "end": v(-10.77, 6.75) * mm});
            skLineSegment(sketch, "E14092", {"start": v(-10.77, 6.75) * mm, "end": v(-10.36, 6.36) * mm});
            skLineSegment(sketch, "E14093", {"start": v(-10.36, 6.36) * mm, "end": v(-10.25, 6.24) * mm});
            skArc(sketch, "E14094", {"start": v(-10.25, 6.24) * mm, "mid": v(-10.57, 5.23) * mm, "end": v(-10.94, 4.23) * mm});
            skLineSegment(sketch, "E14095", {"start": v(-10.94, 4.23) * mm, "end": v(-11.1, 4.2) * mm});
            skLineSegment(sketch, "E14096", {"start": v(-11.1, 4.2) * mm, "end": v(-11.67, 4.15) * mm});
            skLineSegment(sketch, "E14097", {"start": v(-11.67, 4.15) * mm, "end": v(-12.19, 4.13) * mm});
            skLineSegment(sketch, "E14098", {"start": v(-12.19, 4.13) * mm, "end": v(-12.65, 4.13) * mm});
            skLineSegment(sketch, "E14099", {"start": v(-12.65, 4.13) * mm, "end": v(-13.06, 4.15) * mm});
            skLineSegment(sketch, "E14100", {"start": v(-13.06, 4.15) * mm, "end": v(-13.41, 4.18) * mm});
            skLineSegment(sketch, "E14101", {"start": v(-13.41, 4.18) * mm, "end": v(-13.7, 4.23) * mm});
            skLineSegment(sketch, "E14102", {"start": v(-13.7, 4.23) * mm, "end": v(-13.95, 4.28) * mm});
            skLineSegment(sketch, "E14103", {"start": v(-13.95, 4.28) * mm, "end": v(-14.13, 4.33) * mm});
            skLineSegment(sketch, "E14104", {"start": v(-14.13, 4.33) * mm, "end": v(-14.26, 4.37) * mm});
            skLineSegment(sketch, "E14105", {"start": v(-14.26, 4.37) * mm, "end": v(-14.34, 4.4) * mm});
            skLineSegment(sketch, "E14106", {"start": v(-14.34, 4.4) * mm, "end": v(-14.36, 4.4) * mm});
            skLineSegment(sketch, "E14107", {"start": v(-14.36, 4.4) * mm, "end": v(-16.34, 5.3) * mm});
            skArc(sketch, "E14108", {"start": v(-16.34, 5.3) * mm, "mid": v(-17.07, 3.87) * mm, "end": v(-17.9, 2.5) * mm});
            skLineSegment(sketch, "E14109", {"start": v(-17.9, 2.5) * mm, "end": v(-16.1, 1.3) * mm});
            skLineSegment(sketch, "E14110", {"start": v(-16.1, 1.3) * mm, "end": v(-16.07, 1.28) * mm});
            skLineSegment(sketch, "E14111", {"start": v(-16.07, 1.28) * mm, "end": v(-16, 1.23) * mm});
            skLineSegment(sketch, "E14112", {"start": v(-16, 1.23) * mm, "end": v(-15.9, 1.14) * mm});
            skLineSegment(sketch, "E14113", {"start": v(-15.9, 1.14) * mm, "end": v(-15.77, 1.01) * mm});
            skLineSegment(sketch, "E14114", {"start": v(-15.77, 1.01) * mm, "end": v(-15.6, 0.83) * mm});
            skLineSegment(sketch, "E14115", {"start": v(-15.6, 0.83) * mm, "end": v(-15.4, 0.6) * mm});
            skLineSegment(sketch, "E14116", {"start": v(-15.4, 0.6) * mm, "end": v(-15.19, 0.32) * mm});
            skLineSegment(sketch, "E14117", {"start": v(-15.19, 0.32) * mm, "end": v(-14.96, -0.01) * mm});
            skLineSegment(sketch, "E14118", {"start": v(-14.96, -0.01) * mm, "end": v(-14.71, -0.4) * mm});
            skLineSegment(sketch, "E14119", {"start": v(-14.71, -0.4) * mm, "end": v(-14.46, -0.86) * mm});
            skLineSegment(sketch, "E14120", {"start": v(-14.46, -0.86) * mm, "end": v(-14.2, -1.37) * mm});
            skLineSegment(sketch, "E14121", {"start": v(-14.2, -1.37) * mm, "end": v(-14.15, -1.52) * mm});
            skArc(sketch, "E14122", {"start": v(-14.15, -1.52) * mm, "mid": v(-14.8, -2.36) * mm, "end": v(-15.48, -3.17) * mm});
            skLineSegment(sketch, "E14123", {"start": v(-15.48, -3.17) * mm, "end": v(-15.64, -3.13) * mm});
            skLineSegment(sketch, "E14124", {"start": v(-15.64, -3.13) * mm, "end": v(-16.2, -3) * mm});
            skLineSegment(sketch, "E14125", {"start": v(-16.2, -3) * mm, "end": v(-16.7, -2.84) * mm});
            skLineSegment(sketch, "E14126", {"start": v(-16.7, -2.84) * mm, "end": v(-17.13, -2.68) * mm});
            skLineSegment(sketch, "E14127", {"start": v(-17.13, -2.68) * mm, "end": v(-17.5, -2.52) * mm});
            skLineSegment(sketch, "E14128", {"start": v(-17.5, -2.52) * mm, "end": v(-17.82, -2.37) * mm});
            skLineSegment(sketch, "E14129", {"start": v(-17.82, -2.37) * mm, "end": v(-18.08, -2.22) * mm});
            skLineSegment(sketch, "E14130", {"start": v(-18.08, -2.22) * mm, "end": v(-18.3, -2.1) * mm});
            skLineSegment(sketch, "E14131", {"start": v(-18.3, -2.1) * mm, "end": v(-18.45, -1.99) * mm});
            skLineSegment(sketch, "E14132", {"start": v(-18.45, -1.99) * mm, "end": v(-18.56, -1.9) * mm});
            skLineSegment(sketch, "E14133", {"start": v(-18.56, -1.9) * mm, "end": v(-18.62, -1.85) * mm});
            skLineSegment(sketch, "E14134", {"start": v(-18.62, -1.85) * mm, "end": v(-18.64, -1.84) * mm});
            skLineSegment(sketch, "E14135", {"start": v(-18.64, -1.84) * mm, "end": v(-20.2, -0.31) * mm});
            skArc(sketch, "E14136", {"start": v(-20.2, -0.31) * mm, "mid": v(-21.36, -1.4) * mm, "end": v(-22.61, -2.4) * mm});
            skLineSegment(sketch, "E14137", {"start": v(-22.61, -2.4) * mm, "end": v(-21.33, -4.16) * mm});
            skLineSegment(sketch, "E14138", {"start": v(-21.33, -4.16) * mm, "end": v(-21.31, -4.18) * mm});
            skLineSegment(sketch, "E14139", {"start": v(-21.31, -4.18) * mm, "end": v(-21.27, -4.25) * mm});
            skLineSegment(sketch, "E14140", {"start": v(-21.27, -4.25) * mm, "end": v(-21.2, -4.37) * mm});
            skLineSegment(sketch, "E14141", {"start": v(-21.2, -4.37) * mm, "end": v(-21.12, -4.54) * mm});
            skLineSegment(sketch, "E14142", {"start": v(-21.12, -4.54) * mm, "end": v(-21.02, -4.77) * mm});
            skLineSegment(sketch, "E14143", {"start": v(-21.02, -4.77) * mm, "end": v(-20.92, -5.05) * mm});
            skLineSegment(sketch, "E14144", {"start": v(-20.92, -5.05) * mm, "end": v(-20.81, -5.39) * mm});
            skLineSegment(sketch, "E14145", {"start": v(-20.81, -5.39) * mm, "end": v(-20.7, -5.78) * mm});
            skLineSegment(sketch, "E14146", {"start": v(-20.7, -5.78) * mm, "end": v(-20.61, -6.24) * mm});
            skLineSegment(sketch, "E14147", {"start": v(-20.61, -6.24) * mm, "end": v(-20.53, -6.75) * mm});
            skLineSegment(sketch, "E14148", {"start": v(-20.53, -6.75) * mm, "end": v(-20.47, -7.32) * mm});
            skLineSegment(sketch, "E14149", {"start": v(-20.47, -7.32) * mm, "end": v(-20.46, -7.48) * mm});
            skArc(sketch, "E14150", {"start": v(-20.46, -7.48) * mm, "mid": v(-21.36, -8.04) * mm, "end": v(-22.28, -8.57) * mm});
            skLineSegment(sketch, "E14151", {"start": v(-22.28, -8.57) * mm, "end": v(-22.42, -8.48) * mm});
            skLineSegment(sketch, "E14152", {"start": v(-22.42, -8.48) * mm, "end": v(-22.9, -8.16) * mm});
            skLineSegment(sketch, "E14153", {"start": v(-22.9, -8.16) * mm, "end": v(-23.3, -7.85) * mm});
            skLineSegment(sketch, "E14154", {"start": v(-23.3, -7.85) * mm, "end": v(-23.66, -7.55) * mm});
            skLineSegment(sketch, "E14155", {"start": v(-23.66, -7.55) * mm, "end": v(-23.96, -7.27) * mm});
            skLineSegment(sketch, "E14156", {"start": v(-23.96, -7.27) * mm, "end": v(-24.2, -7.02) * mm});
            skLineSegment(sketch, "E14157", {"start": v(-24.2, -7.02) * mm, "end": v(-24.4, -6.8) * mm});
            skLineSegment(sketch, "E14158", {"start": v(-24.4, -6.8) * mm, "end": v(-24.56, -6.6) * mm});
            skLineSegment(sketch, "E14159", {"start": v(-24.56, -6.6) * mm, "end": v(-24.67, -6.45) * mm});
            skLineSegment(sketch, "E14160", {"start": v(-24.67, -6.45) * mm, "end": v(-24.74, -6.33) * mm});
            skLineSegment(sketch, "E14161", {"start": v(-24.74, -6.33) * mm, "end": v(-24.78, -6.26) * mm});
            skLineSegment(sketch, "E14162", {"start": v(-24.78, -6.26) * mm, "end": v(-24.8, -6.24) * mm});
            skLineSegment(sketch, "E14163", {"start": v(-24.8, -6.24) * mm, "end": v(-25.73, -4.27) * mm});
            skArc(sketch, "E14164", {"start": v(-25.73, -4.27) * mm, "mid": v(-27.2, -4.9) * mm, "end": v(-28.72, -5.41) * mm});
            skLineSegment(sketch, "E14165", {"start": v(-28.72, -5.41) * mm, "end": v(-28.12, -7.5) * mm});
            skLineSegment(sketch, "E14166", {"start": v(-28.12, -7.5) * mm, "end": v(-28.1, -7.53) * mm});
            skLineSegment(sketch, "E14167", {"start": v(-28.1, -7.53) * mm, "end": v(-28.1, -7.6) * mm});
            skLineSegment(sketch, "E14168", {"start": v(-28.1, -7.6) * mm, "end": v(-28.07, -7.74) * mm});
            skLineSegment(sketch, "E14169", {"start": v(-28.07, -7.74) * mm, "end": v(-28.05, -7.93) * mm});
            skLineSegment(sketch, "E14170", {"start": v(-28.05, -7.93) * mm, "end": v(-28.04, -8.18) * mm});
            skLineSegment(sketch, "E14171", {"start": v(-28.04, -8.18) * mm, "end": v(-28.03, -8.48) * mm});
            skLineSegment(sketch, "E14172", {"start": v(-28.03, -8.48) * mm, "end": v(-28.05, -8.83) * mm});
            skLineSegment(sketch, "E14173", {"start": v(-28.05, -8.83) * mm, "end": v(-28.09, -9.24) * mm});
            skLineSegment(sketch, "E14174", {"start": v(-28.09, -9.24) * mm, "end": v(-28.15, -9.7) * mm});
            skLineSegment(sketch, "E14175", {"start": v(-28.15, -9.7) * mm, "end": v(-28.25, -10.2) * mm});
            skLineSegment(sketch, "E14176", {"start": v(-28.25, -10.2) * mm, "end": v(-28.39, -10.76) * mm});
            skLineSegment(sketch, "E14177", {"start": v(-28.39, -10.76) * mm, "end": v(-28.44, -10.91) * mm});
            skArc(sketch, "E14178", {"start": v(-28.44, -10.91) * mm, "mid": v(-29.47, -11.14) * mm, "end": v(-30.52, -11.31) * mm});
            skLineSegment(sketch, "E14179", {"start": v(-30.52, -11.31) * mm, "end": v(-30.62, -11.19) * mm});
            skLineSegment(sketch, "E14180", {"start": v(-30.62, -11.19) * mm, "end": v(-30.95, -10.72) * mm});
            skLineSegment(sketch, "E14181", {"start": v(-30.95, -10.72) * mm, "end": v(-31.23, -10.29) * mm});
            skLineSegment(sketch, "E14182", {"start": v(-31.23, -10.29) * mm, "end": v(-31.46, -9.89) * mm});
            skLineSegment(sketch, "E14183", {"start": v(-31.46, -9.89) * mm, "end": v(-31.65, -9.52) * mm});
            skLineSegment(sketch, "E14184", {"start": v(-31.65, -9.52) * mm, "end": v(-31.8, -9.2) * mm});
            skLineSegment(sketch, "E14185", {"start": v(-31.8, -9.2) * mm, "end": v(-31.9, -8.92) * mm});
            skLineSegment(sketch, "E14186", {"start": v(-31.9, -8.92) * mm, "end": v(-31.98, -8.7) * mm});
            skLineSegment(sketch, "E14187", {"start": v(-31.98, -8.7) * mm, "end": v(-32.03, -8.5) * mm});
            skLineSegment(sketch, "E14188", {"start": v(-32.03, -8.5) * mm, "end": v(-32.06, -8.37) * mm});
            skLineSegment(sketch, "E14189", {"start": v(-32.06, -8.37) * mm, "end": v(-32.08, -8.3) * mm});
            skLineSegment(sketch, "E14190", {"start": v(-32.08, -8.3) * mm, "end": v(-32.08, -8.27) * mm});
            skLineSegment(sketch, "E14191", {"start": v(-32.08, -8.27) * mm, "end": v(-32.3, -6.1) * mm});
            skArc(sketch, "E14192", {"start": v(-32.3, -6.1) * mm, "mid": v(-33.9, -6.2) * mm, "end": v(-35.5, -6.15) * mm});
            skLineSegment(sketch, "E14193", {"start": v(-35.5, -6.15) * mm, "end": v(-35.64, -8.32) * mm});
            skLineSegment(sketch, "E14194", {"start": v(-35.64, -8.32) * mm, "end": v(-35.64, -8.35) * mm});
            skLineSegment(sketch, "E14195", {"start": v(-35.64, -8.35) * mm, "end": v(-35.65, -8.43) * mm});
            skLineSegment(sketch, "E14196", {"start": v(-35.65, -8.43) * mm, "end": v(-35.68, -8.56) * mm});
            skLineSegment(sketch, "E14197", {"start": v(-35.68, -8.56) * mm, "end": v(-35.72, -8.75) * mm});
            skLineSegment(sketch, "E14198", {"start": v(-35.72, -8.75) * mm, "end": v(-35.8, -8.98) * mm});
            skLineSegment(sketch, "E14199", {"start": v(-35.8, -8.98) * mm, "end": v(-35.9, -9.27) * mm});
            skLineSegment(sketch, "E14200", {"start": v(-35.9, -9.27) * mm, "end": v(-36.03, -9.6) * mm});
            skLineSegment(sketch, "E14201", {"start": v(-36.03, -9.6) * mm, "end": v(-36.2, -9.96) * mm});
            skLineSegment(sketch, "E14202", {"start": v(-36.2, -9.96) * mm, "end": v(-36.42, -10.37) * mm});
            skLineSegment(sketch, "E14203", {"start": v(-36.42, -10.37) * mm, "end": v(-36.69, -10.81) * mm});
            skLineSegment(sketch, "E14204", {"start": v(-36.69, -10.81) * mm, "end": v(-37, -11.29) * mm});
            skLineSegment(sketch, "E14205", {"start": v(-37, -11.29) * mm, "end": v(-37.1, -11.42) * mm});
            skArc(sketch, "E14206", {"start": v(-37.1, -11.42) * mm, "mid": v(-38.15, -11.27) * mm, "end": v(-39.2, -11.08) * mm});
            skLineSegment(sketch, "E14207", {"start": v(-39.2, -11.08) * mm, "end": v(-39.25, -10.93) * mm});
            skLineSegment(sketch, "E14208", {"start": v(-39.25, -10.93) * mm, "end": v(-39.4, -10.38) * mm});
            skLineSegment(sketch, "E14209", {"start": v(-39.4, -10.38) * mm, "end": v(-39.52, -9.87) * mm});
            skLineSegment(sketch, "E14210", {"start": v(-39.52, -9.87) * mm, "end": v(-39.6, -9.42) * mm});
            skLineSegment(sketch, "E14211", {"start": v(-39.6, -9.42) * mm, "end": v(-39.65, -9.01) * mm});
            skLineSegment(sketch, "E14212", {"start": v(-39.65, -9.01) * mm, "end": v(-39.68, -8.66) * mm});
            skLineSegment(sketch, "E14213", {"start": v(-39.68, -8.66) * mm, "end": v(-39.68, -8.36) * mm});
            skLineSegment(sketch, "E14214", {"start": v(-39.68, -8.36) * mm, "end": v(-39.68, -8.11) * mm});
            skLineSegment(sketch, "E14215", {"start": v(-39.68, -8.11) * mm, "end": v(-39.66, -7.92) * mm});
            skLineSegment(sketch, "E14216", {"start": v(-39.66, -7.92) * mm, "end": v(-39.65, -7.79) * mm});
            skLineSegment(sketch, "E14217", {"start": v(-39.65, -7.79) * mm, "end": v(-39.63, -7.7) * mm});
            skLineSegment(sketch, "E14218", {"start": v(-39.63, -7.7) * mm, "end": v(-39.63, -7.68) * mm});
            skLineSegment(sketch, "E14219", {"start": v(-39.63, -7.68) * mm, "end": v(-39.08, -5.57) * mm});
            skArc(sketch, "E14220", {"start": v(-39.08, -5.57) * mm, "mid": v(-40.62, -5.11) * mm, "end": v(-42.1, -4.53) * mm});
            skLineSegment(sketch, "E14221", {"start": v(-42.1, -4.53) * mm, "end": v(-42.98, -6.52) * mm});
            skLineSegment(sketch, "E14222", {"start": v(-42.98, -6.52) * mm, "end": v(-43, -6.54) * mm});
            skLineSegment(sketch, "E14223", {"start": v(-43, -6.54) * mm, "end": v(-43.03, -6.61) * mm});
            skLineSegment(sketch, "E14224", {"start": v(-43.03, -6.61) * mm, "end": v(-43.1, -6.73) * mm});
            skLineSegment(sketch, "E14225", {"start": v(-43.1, -6.73) * mm, "end": v(-43.21, -6.89) * mm});
            skLineSegment(sketch, "E14226", {"start": v(-43.21, -6.89) * mm, "end": v(-43.36, -7.09) * mm});
            skLineSegment(sketch, "E14227", {"start": v(-43.36, -7.09) * mm, "end": v(-43.55, -7.32) * mm});
            skLineSegment(sketch, "E14228", {"start": v(-43.55, -7.32) * mm, "end": v(-43.79, -7.58) * mm});
            skLineSegment(sketch, "E14229", {"start": v(-43.79, -7.58) * mm, "end": v(-44.08, -7.87) * mm});
            skLineSegment(sketch, "E14230", {"start": v(-44.08, -7.87) * mm, "end": v(-44.42, -8.17) * mm});
            skLineSegment(sketch, "E14231", {"start": v(-44.42, -8.17) * mm, "end": v(-44.82, -8.5) * mm});
            skLineSegment(sketch, "E14232", {"start": v(-44.82, -8.5) * mm, "end": v(-45.29, -8.84) * mm});
            skLineSegment(sketch, "E14233", {"start": v(-45.29, -8.84) * mm, "end": v(-45.42, -8.92) * mm});
            skArc(sketch, "E14234", {"start": v(-45.42, -8.92) * mm, "mid": v(-46.36, -8.43) * mm, "end": v(-47.27, -7.9) * mm});
            skLineSegment(sketch, "E14235", {"start": v(-47.27, -7.9) * mm, "end": v(-47.27, -7.73) * mm});
            skLineSegment(sketch, "E14236", {"start": v(-47.27, -7.73) * mm, "end": v(-47.23, -7.16) * mm});
            skLineSegment(sketch, "E14237", {"start": v(-47.23, -7.16) * mm, "end": v(-47.16, -6.65) * mm});
            skLineSegment(sketch, "E14238", {"start": v(-47.16, -6.65) * mm, "end": v(-47.08, -6.2) * mm});
            skLineSegment(sketch, "E14239", {"start": v(-47.08, -6.2) * mm, "end": v(-47, -5.8) * mm});
            skLineSegment(sketch, "E14240", {"start": v(-47, -5.8) * mm, "end": v(-46.9, -5.45) * mm});
            skLineSegment(sketch, "E14241", {"start": v(-46.9, -5.45) * mm, "end": v(-46.8, -5.17) * mm});
            skLineSegment(sketch, "E14242", {"start": v(-46.8, -5.17) * mm, "end": v(-46.7, -4.94) * mm});
            skLineSegment(sketch, "E14243", {"start": v(-46.7, -4.94) * mm, "end": v(-46.63, -4.77) * mm});
            skLineSegment(sketch, "E14244", {"start": v(-46.63, -4.77) * mm, "end": v(-46.57, -4.65) * mm});
            skLineSegment(sketch, "E14245", {"start": v(-46.57, -4.65) * mm, "end": v(-46.53, -4.58) * mm});
            skLineSegment(sketch, "E14246", {"start": v(-46.53, -4.58) * mm, "end": v(-46.51, -4.55) * mm});
            skLineSegment(sketch, "E14247", {"start": v(-46.51, -4.55) * mm, "end": v(-45.28, -2.76) * mm});
            skArc(sketch, "E14248", {"start": v(-45.28, -2.76) * mm, "mid": v(-46.57, -1.8) * mm, "end": v(-47.77, -0.74) * mm});
            skLineSegment(sketch, "E14249", {"start": v(-47.77, -0.74) * mm, "end": v(-49.27, -2.31) * mm});
            skLineSegment(sketch, "E14250", {"start": v(-49.27, -2.31) * mm, "end": v(-49.3, -2.33) * mm});
            skLineSegment(sketch, "E14251", {"start": v(-49.3, -2.33) * mm, "end": v(-49.35, -2.38) * mm});
            skLineSegment(sketch, "E14252", {"start": v(-49.35, -2.38) * mm, "end": v(-49.46, -2.47) * mm});
            skLineSegment(sketch, "E14253", {"start": v(-49.46, -2.47) * mm, "end": v(-49.61, -2.58) * mm});
            skLineSegment(sketch, "E14254", {"start": v(-49.61, -2.58) * mm, "end": v(-49.82, -2.72) * mm});
            skLineSegment(sketch, "E14255", {"start": v(-49.82, -2.72) * mm, "end": v(-50.07, -2.87) * mm});
            skLineSegment(sketch, "E14256", {"start": v(-50.07, -2.87) * mm, "end": v(-50.39, -3.03) * mm});
            skLineSegment(sketch, "E14257", {"start": v(-50.39, -3.03) * mm, "end": v(-50.76, -3.2) * mm});
            skLineSegment(sketch, "E14258", {"start": v(-50.76, -3.2) * mm, "end": v(-51.19, -3.37) * mm});
            skLineSegment(sketch, "E14259", {"start": v(-51.19, -3.37) * mm, "end": v(-51.68, -3.54) * mm});
            skLineSegment(sketch, "E14260", {"start": v(-51.68, -3.54) * mm, "end": v(-52.23, -3.7) * mm});
            skLineSegment(sketch, "E14261", {"start": v(-52.23, -3.7) * mm, "end": v(-52.38, -3.74) * mm});
            skArc(sketch, "E14262", {"start": v(-52.38, -3.74) * mm, "mid": v(-53.1, -2.95) * mm, "end": v(-53.77, -2.13) * mm});
            skLineSegment(sketch, "E14263", {"start": v(-53.77, -2.13) * mm, "end": v(-53.71, -1.98) * mm});
            skLineSegment(sketch, "E14264", {"start": v(-53.71, -1.98) * mm, "end": v(-53.48, -1.46) * mm});
            skLineSegment(sketch, "E14265", {"start": v(-53.48, -1.46) * mm, "end": v(-53.24, -1) * mm});
            skLineSegment(sketch, "E14266", {"start": v(-53.24, -1) * mm, "end": v(-53.01, -0.6) * mm});
            skLineSegment(sketch, "E14267", {"start": v(-53.01, -0.6) * mm, "end": v(-52.79, -0.26) * mm});
            skLineSegment(sketch, "E14268", {"start": v(-52.79, -0.26) * mm, "end": v(-52.58, 0.03) * mm});
            skLineSegment(sketch, "E14269", {"start": v(-52.58, 0.03) * mm, "end": v(-52.4, 0.26) * mm});
            skLineSegment(sketch, "E14270", {"start": v(-52.4, 0.26) * mm, "end": v(-52.23, 0.44) * mm});
            skLineSegment(sketch, "E14271", {"start": v(-52.23, 0.44) * mm, "end": v(-52.1, 0.58) * mm});
            skLineSegment(sketch, "E14272", {"start": v(-52.1, 0.58) * mm, "end": v(-52, 0.67) * mm});
            skLineSegment(sketch, "E14273", {"start": v(-52, 0.67) * mm, "end": v(-51.94, 0.73) * mm});
            skLineSegment(sketch, "E14274", {"start": v(-51.94, 0.73) * mm, "end": v(-51.92, 0.74) * mm});
            skLineSegment(sketch, "E14275", {"start": v(-51.92, 0.74) * mm, "end": v(-50.15, 2) * mm});
            skArc(sketch, "E14276", {"start": v(-50.15, 2) * mm, "mid": v(-51.02, 3.35) * mm, "end": v(-51.79, 4.75) * mm});
            skLineSegment(sketch, "E14277", {"start": v(-51.79, 4.75) * mm, "end": v(-53.74, 3.8) * mm});
            skLineSegment(sketch, "E14278", {"start": v(-53.74, 3.8) * mm, "end": v(-53.76, 3.78) * mm});
            skLineSegment(sketch, "E14279", {"start": v(-53.76, 3.78) * mm, "end": v(-53.84, 3.75) * mm});
            skLineSegment(sketch, "E14280", {"start": v(-53.84, 3.75) * mm, "end": v(-53.97, 3.7) * mm});
            skLineSegment(sketch, "E14281", {"start": v(-53.97, 3.7) * mm, "end": v(-54.15, 3.65) * mm});
            skLineSegment(sketch, "E14282", {"start": v(-54.15, 3.65) * mm, "end": v(-54.4, 3.6) * mm});
            skLineSegment(sketch, "E14283", {"start": v(-54.4, 3.6) * mm, "end": v(-54.69, 3.54) * mm});
            skLineSegment(sketch, "E14284", {"start": v(-54.69, 3.54) * mm, "end": v(-55.04, 3.5) * mm});
            skLineSegment(sketch, "E14285", {"start": v(-55.04, 3.5) * mm, "end": v(-55.44, 3.46) * mm});
            skLineSegment(sketch, "E14286", {"start": v(-55.44, 3.46) * mm, "end": v(-55.9, 3.45) * mm});
            skLineSegment(sketch, "E14287", {"start": v(-55.9, 3.45) * mm, "end": v(-56.42, 3.46) * mm});
            skLineSegment(sketch, "E14288", {"start": v(-56.42, 3.46) * mm, "end": v(-57, 3.5) * mm});
            skLineSegment(sketch, "E14289", {"start": v(-57, 3.5) * mm, "end": v(-57.15, 3.52) * mm});
            skArc(sketch, "E14290", {"start": v(-57.15, 3.52) * mm, "mid": v(-57.55, 4.5) * mm, "end": v(-57.91, 5.5) * mm});
            skLineSegment(sketch, "E14291", {"start": v(-57.91, 5.5) * mm, "end": v(-57.8, 5.62) * mm});
            skLineSegment(sketch, "E14292", {"start": v(-57.8, 5.62) * mm, "end": v(-57.4, 6.03) * mm});
            skLineSegment(sketch, "E14293", {"start": v(-57.4, 6.03) * mm, "end": v(-57.02, 6.38) * mm});
            skLineSegment(sketch, "E14294", {"start": v(-57.02, 6.38) * mm, "end": v(-56.67, 6.68) * mm});
            skLineSegment(sketch, "E14295", {"start": v(-56.67, 6.68) * mm, "end": v(-56.34, 6.92) * mm});
            skLineSegment(sketch, "E14296", {"start": v(-56.34, 6.92) * mm, "end": v(-56.05, 7.12) * mm});
            skLineSegment(sketch, "E14297", {"start": v(-56.05, 7.12) * mm, "end": v(-55.8, 7.28) * mm});
            skLineSegment(sketch, "E14298", {"start": v(-55.8, 7.28) * mm, "end": v(-55.58, 7.4) * mm});
            skLineSegment(sketch, "E14299", {"start": v(-55.58, 7.4) * mm, "end": v(-55.4, 7.48) * mm});
            skLineSegment(sketch, "E14300", {"start": v(-55.4, 7.48) * mm, "end": v(-55.28, 7.53) * mm});
            skLineSegment(sketch, "E14301", {"start": v(-55.28, 7.53) * mm, "end": v(-55.2, 7.56) * mm});
            skLineSegment(sketch, "E14302", {"start": v(-55.2, 7.56) * mm, "end": v(-55.18, 7.57) * mm});
            skLineSegment(sketch, "E14303", {"start": v(-55.18, 7.57) * mm, "end": v(-53.08, 8.15) * mm});
            skArc(sketch, "E14304", {"start": v(-53.08, 8.15) * mm, "mid": v(-53.45, 9.7) * mm, "end": v(-53.69, 11.3) * mm});
            skLineSegment(sketch, "E14305", {"start": v(-53.69, 11.3) * mm, "end": v(-55.85, 11.06) * mm});
            skLineSegment(sketch, "E14306", {"start": v(-55.85, 11.06) * mm, "end": v(-55.88, 11.06) * mm});
            skLineSegment(sketch, "E14307", {"start": v(-55.88, 11.06) * mm, "end": v(-55.96, 11.05) * mm});
            skLineSegment(sketch, "E14308", {"start": v(-55.96, 11.05) * mm, "end": v(-56.1, 11.06) * mm});
            skLineSegment(sketch, "E14309", {"start": v(-56.1, 11.06) * mm, "end": v(-56.29, 11.07) * mm});
            skLineSegment(sketch, "E14310", {"start": v(-56.29, 11.07) * mm, "end": v(-56.53, 11.1) * mm});
            skLineSegment(sketch, "E14311", {"start": v(-56.53, 11.1) * mm, "end": v(-56.83, 11.15) * mm});
            skLineSegment(sketch, "E14312", {"start": v(-56.83, 11.15) * mm, "end": v(-57.17, 11.22) * mm});
            skLineSegment(sketch, "E14313", {"start": v(-57.17, 11.22) * mm, "end": v(-57.57, 11.33) * mm});
            skLineSegment(sketch, "E14314", {"start": v(-57.57, 11.33) * mm, "end": v(-58, 11.48) * mm});
            skLineSegment(sketch, "E14315", {"start": v(-58, 11.48) * mm, "end": v(-58.49, 11.66) * mm});
            skLineSegment(sketch, "E14316", {"start": v(-58.49, 11.66) * mm, "end": v(-59.01, 11.9) * mm});
            skLineSegment(sketch, "E14317", {"start": v(-59.01, 11.9) * mm, "end": v(-59.15, 11.97) * mm});
            skArc(sketch, "E14318", {"start": v(-59.15, 11.97) * mm, "mid": v(-59.2, 13.03) * mm, "end": v(-59.19, 14.09) * mm});
            skLineSegment(sketch, "E14319", {"start": v(-59.19, 14.09) * mm, "end": v(-59.05, 14.16) * mm});
            skLineSegment(sketch, "E14320", {"start": v(-59.05, 14.16) * mm, "end": v(-58.53, 14.41) * mm});
            skLineSegment(sketch, "E14321", {"start": v(-58.53, 14.41) * mm, "end": v(-58.05, 14.61) * mm});
            skLineSegment(sketch, "E14322", {"start": v(-58.05, 14.61) * mm, "end": v(-57.62, 14.77) * mm});
            skLineSegment(sketch, "E14323", {"start": v(-57.62, 14.77) * mm, "end": v(-57.23, 14.9) * mm});
            skLineSegment(sketch, "E14324", {"start": v(-57.23, 14.9) * mm, "end": v(-56.89, 14.98) * mm});
            skLineSegment(sketch, "E14325", {"start": v(-56.89, 14.98) * mm, "end": v(-56.6, 15.04) * mm});
            skLineSegment(sketch, "E14326", {"start": v(-56.6, 15.04) * mm, "end": v(-56.35, 15.07) * mm});
            skLineSegment(sketch, "E14327", {"start": v(-56.35, 15.07) * mm, "end": v(-56.16, 15.1) * mm});
            skLineSegment(sketch, "E14328", {"start": v(-56.16, 15.1) * mm, "end": v(-56.02, 15.1) * mm});
            skLineSegment(sketch, "E14329", {"start": v(-56.02, 15.1) * mm, "end": v(-55.94, 15.1) * mm});
            skLineSegment(sketch, "E14330", {"start": v(-55.94, 15.1) * mm, "end": v(-55.91, 15.1) * mm});
            skLineSegment(sketch, "E14331", {"start": v(-55.91, 15.1) * mm, "end": v(-53.75, 14.93) * mm});
            skArc(sketch, "E14332", {"start": v(-53.75, 14.93) * mm, "mid": v(-53.56, 16.52) * mm, "end": v(-53.24, 18.09) * mm});
            skLineSegment(sketch, "E14333", {"start": v(-53.24, 18.09) * mm, "end": v(-55.35, 18.6) * mm});
            skLineSegment(sketch, "E14334", {"start": v(-55.35, 18.6) * mm, "end": v(-55.38, 18.61) * mm});
            skLineSegment(sketch, "E14335", {"start": v(-55.38, 18.61) * mm, "end": v(-55.46, 18.64) * mm});
            skLineSegment(sketch, "E14336", {"start": v(-55.46, 18.64) * mm, "end": v(-55.58, 18.69) * mm});
            skLineSegment(sketch, "E14337", {"start": v(-55.58, 18.69) * mm, "end": v(-55.76, 18.77) * mm});
            skLineSegment(sketch, "E14338", {"start": v(-55.76, 18.77) * mm, "end": v(-55.98, 18.88) * mm});
            skLineSegment(sketch, "E14339", {"start": v(-55.98, 18.88) * mm, "end": v(-56.24, 19.02) * mm});
            skLineSegment(sketch, "E14340", {"start": v(-56.24, 19.02) * mm, "end": v(-56.53, 19.21) * mm});
            skLineSegment(sketch, "E14341", {"start": v(-56.53, 19.21) * mm, "end": v(-56.87, 19.45) * mm});
            skLineSegment(sketch, "E14342", {"start": v(-56.87, 19.45) * mm, "end": v(-57.23, 19.74) * mm});
            skLineSegment(sketch, "E14343", {"start": v(-57.23, 19.74) * mm, "end": v(-57.62, 20.07) * mm});
            skLineSegment(sketch, "E14344", {"start": v(-57.62, 20.07) * mm, "end": v(-58.03, 20.47) * mm});
            skLineSegment(sketch, "E14345", {"start": v(-58.03, 20.47) * mm, "end": v(-58.14, 20.59) * mm});
            skArc(sketch, "E14346", {"start": v(-58.14, 20.59) * mm, "mid": v(-57.82, 21.6) * mm, "end": v(-57.45, 22.6) * mm});
            skLineSegment(sketch, "E14347", {"start": v(-57.45, 22.6) * mm, "end": v(-57.3, 22.62) * mm});
            skLineSegment(sketch, "E14348", {"start": v(-57.3, 22.62) * mm, "end": v(-56.72, 22.67) * mm});
            skLineSegment(sketch, "E14349", {"start": v(-56.72, 22.67) * mm, "end": v(-56.2, 22.7) * mm});
            skLineSegment(sketch, "E14350", {"start": v(-56.2, 22.7) * mm, "end": v(-55.74, 22.7) * mm});
            skLineSegment(sketch, "E14351", {"start": v(-55.74, 22.7) * mm, "end": v(-55.33, 22.68) * mm});
            skLineSegment(sketch, "E14352", {"start": v(-55.33, 22.68) * mm, "end": v(-54.98, 22.64) * mm});
            skLineSegment(sketch, "E14353", {"start": v(-54.98, 22.64) * mm, "end": v(-54.69, 22.6) * mm});
            skLineSegment(sketch, "E14354", {"start": v(-54.69, 22.6) * mm, "end": v(-54.45, 22.55) * mm});
            skLineSegment(sketch, "E14355", {"start": v(-54.45, 22.55) * mm, "end": v(-54.26, 22.5) * mm});
            skLineSegment(sketch, "E14356", {"start": v(-54.26, 22.5) * mm, "end": v(-54.13, 22.46) * mm});
            skLineSegment(sketch, "E14357", {"start": v(-54.13, 22.46) * mm, "end": v(-54.05, 22.43) * mm});
            skLineSegment(sketch, "E14358", {"start": v(-54.05, 22.43) * mm, "end": v(-54.03, 22.42) * mm});
            skLineSegment(sketch, "E14359", {"start": v(-54.03, 22.42) * mm, "end": v(-52.05, 21.52) * mm});
            skArc(sketch, "E14360", {"start": v(-52.05, 21.52) * mm, "mid": v(-51.33, 22.95) * mm, "end": v(-50.5, 24.32) * mm});
            skLineSegment(sketch, "E14361", {"start": v(-50.5, 24.32) * mm, "end": v(-52.3, 25.53) * mm});
            skLineSegment(sketch, "E14362", {"start": v(-52.3, 25.53) * mm, "end": v(-52.32, 25.54) * mm});
            skLineSegment(sketch, "E14363", {"start": v(-52.32, 25.54) * mm, "end": v(-52.39, 25.6) * mm});
            skLineSegment(sketch, "E14364", {"start": v(-52.39, 25.6) * mm, "end": v(-52.49, 25.68) * mm});
            skLineSegment(sketch, "E14365", {"start": v(-52.49, 25.68) * mm, "end": v(-52.63, 25.82) * mm});
            skLineSegment(sketch, "E14366", {"start": v(-52.63, 25.82) * mm, "end": v(-52.8, 26) * mm});
            skLineSegment(sketch, "E14367", {"start": v(-52.8, 26) * mm, "end": v(-52.99, 26.22) * mm});
            skLineSegment(sketch, "E14368", {"start": v(-52.99, 26.22) * mm, "end": v(-53.2, 26.5) * mm});
            skLineSegment(sketch, "E14369", {"start": v(-53.2, 26.5) * mm, "end": v(-53.44, 26.84) * mm});
            skLineSegment(sketch, "E14370", {"start": v(-53.44, 26.84) * mm, "end": v(-53.68, 27.23) * mm});
            skLineSegment(sketch, "E14371", {"start": v(-53.68, 27.23) * mm, "end": v(-53.93, 27.69) * mm});
            skLineSegment(sketch, "E14372", {"start": v(-53.93, 27.69) * mm, "end": v(-54.18, 28.2) * mm});
            skLineSegment(sketch, "E14373", {"start": v(-54.18, 28.2) * mm, "end": v(-54.25, 28.35) * mm});
            skArc(sketch, "E14374", {"start": v(-54.25, 28.35) * mm, "mid": v(-53.6, 29.18) * mm, "end": v(-52.9, 30) * mm});
            skLineSegment(sketch, "E14375", {"start": v(-52.9, 30) * mm, "end": v(-52.75, 29.96) * mm});
            skLineSegment(sketch, "E14376", {"start": v(-52.75, 29.96) * mm, "end": v(-52.2, 29.82) * mm});
            skLineSegment(sketch, "E14377", {"start": v(-52.2, 29.82) * mm, "end": v(-51.7, 29.67) * mm});
            skLineSegment(sketch, "E14378", {"start": v(-51.7, 29.67) * mm, "end": v(-51.27, 29.5) * mm});
            skLineSegment(sketch, "E14379", {"start": v(-51.27, 29.5) * mm, "end": v(-50.9, 29.35) * mm});
            skLineSegment(sketch, "E14380", {"start": v(-50.9, 29.35) * mm, "end": v(-50.57, 29.2) * mm});
            skLineSegment(sketch, "E14381", {"start": v(-50.57, 29.2) * mm, "end": v(-50.3, 29.05) * mm});
            skLineSegment(sketch, "E14382", {"start": v(-50.3, 29.05) * mm, "end": v(-50.1, 28.92) * mm});
            skLineSegment(sketch, "E14383", {"start": v(-50.1, 28.92) * mm, "end": v(-49.94, 28.82) * mm});
            skLineSegment(sketch, "E14384", {"start": v(-49.94, 28.82) * mm, "end": v(-49.83, 28.73) * mm});
            skLineSegment(sketch, "E14385", {"start": v(-49.83, 28.73) * mm, "end": v(-49.77, 28.68) * mm});
            skLineSegment(sketch, "E14386", {"start": v(-49.77, 28.68) * mm, "end": v(-49.75, 28.66) * mm});
            skLineSegment(sketch, "E14387", {"start": v(-49.75, 28.66) * mm, "end": v(-48.2, 27.14) * mm});
            skArc(sketch, "E14388", {"start": v(-48.2, 27.14) * mm, "mid": v(-47.03, 28.24) * mm, "end": v(-45.78, 29.23) * mm});
            skLineSegment(sketch, "E14389", {"start": v(-45.78, 29.23) * mm, "end": v(-47.06, 30.99) * mm});
            skLineSegment(sketch, "E14390", {"start": v(-47.06, 30.99) * mm, "end": v(-47.08, 31.01) * mm});
            skLineSegment(sketch, "E14391", {"start": v(-47.08, 31.01) * mm, "end": v(-47.12, 31.08) * mm});
            skLineSegment(sketch, "E14392", {"start": v(-47.12, 31.08) * mm, "end": v(-47.19, 31.2) * mm});
            skLineSegment(sketch, "E14393", {"start": v(-47.19, 31.2) * mm, "end": v(-47.27, 31.37) * mm});
            skLineSegment(sketch, "E14394", {"start": v(-47.27, 31.37) * mm, "end": v(-47.37, 31.6) * mm});
            skLineSegment(sketch, "E14395", {"start": v(-47.37, 31.6) * mm, "end": v(-47.47, 31.88) * mm});
            skLineSegment(sketch, "E14396", {"start": v(-47.47, 31.88) * mm, "end": v(-47.58, 32.22) * mm});
            skLineSegment(sketch, "E14397", {"start": v(-47.58, 32.22) * mm, "end": v(-47.68, 32.61) * mm});
            skLineSegment(sketch, "E14398", {"start": v(-47.68, 32.61) * mm, "end": v(-47.78, 33.06) * mm});
            skLineSegment(sketch, "E14399", {"start": v(-47.78, 33.06) * mm, "end": v(-47.86, 33.57) * mm});
            skLineSegment(sketch, "E14400", {"start": v(-47.86, 33.57) * mm, "end": v(-47.92, 34.14) * mm});
            skLineSegment(sketch, "E14401", {"start": v(-47.92, 34.14) * mm, "end": v(-47.93, 34.3) * mm});
            skArc(sketch, "E14402", {"start": v(-47.93, 34.3) * mm, "mid": v(-47.03, 34.87) * mm, "end": v(-46.1, 35.4) * mm});
            skLineSegment(sketch, "E14403", {"start": v(-46.1, 35.4) * mm, "end": v(-45.97, 35.3) * mm});
            skLineSegment(sketch, "E14404", {"start": v(-45.97, 35.3) * mm, "end": v(-45.5, 34.99) * mm});
            skLineSegment(sketch, "E14405", {"start": v(-45.5, 34.99) * mm, "end": v(-45.09, 34.67) * mm});
            skLineSegment(sketch, "E14406", {"start": v(-45.09, 34.67) * mm, "end": v(-44.73, 34.38) * mm});
            skLineSegment(sketch, "E14407", {"start": v(-44.73, 34.38) * mm, "end": v(-44.43, 34.1) * mm});
            skLineSegment(sketch, "E14408", {"start": v(-44.43, 34.1) * mm, "end": v(-44.19, 33.84) * mm});
            skLineSegment(sketch, "E14409", {"start": v(-44.19, 33.84) * mm, "end": v(-43.99, 33.62) * mm});
            skLineSegment(sketch, "E14410", {"start": v(-43.99, 33.62) * mm, "end": v(-43.84, 33.43) * mm});
            skLineSegment(sketch, "E14411", {"start": v(-43.84, 33.43) * mm, "end": v(-43.73, 33.27) * mm});
            skLineSegment(sketch, "E14412", {"start": v(-43.73, 33.27) * mm, "end": v(-43.65, 33.16) * mm});
            skLineSegment(sketch, "E14413", {"start": v(-43.65, 33.16) * mm, "end": v(-43.61, 33.09) * mm});
            skLineSegment(sketch, "E14414", {"start": v(-43.61, 33.09) * mm, "end": v(-43.6, 33.06) * mm});
            skLineSegment(sketch, "E14415", {"start": v(-43.6, 33.06) * mm, "end": v(-42.66, 31.1) * mm});
            skArc(sketch, "E14416", {"start": v(-42.66, 31.1) * mm, "mid": v(-41.19, 31.73) * mm, "end": v(-39.67, 32.24) * mm});
            skLineSegment(sketch, "E14417", {"start": v(-39.67, 32.24) * mm, "end": v(-40.28, 34.33) * mm});
            skLineSegment(sketch, "E14418", {"start": v(-40.28, 34.33) * mm, "end": v(-40.28, 34.36) * mm});
            skLineSegment(sketch, "E14419", {"start": v(-40.28, 34.36) * mm, "end": v(-40.3, 34.44) * mm});
            skLineSegment(sketch, "E14420", {"start": v(-40.3, 34.44) * mm, "end": v(-40.32, 34.57) * mm});
            skLineSegment(sketch, "E14421", {"start": v(-40.32, 34.57) * mm, "end": v(-40.34, 34.76) * mm});
            skLineSegment(sketch, "E14422", {"start": v(-40.34, 34.76) * mm, "end": v(-40.36, 35) * mm});
            skLineSegment(sketch, "E14423", {"start": v(-40.36, 35) * mm, "end": v(-40.36, 35.3) * mm});
            skLineSegment(sketch, "E14424", {"start": v(-40.36, 35.3) * mm, "end": v(-40.34, 35.66) * mm});
            skLineSegment(sketch, "E14425", {"start": v(-40.34, 35.66) * mm, "end": v(-40.3, 36.07) * mm});
            skLineSegment(sketch, "E14426", {"start": v(-40.3, 36.07) * mm, "end": v(-40.24, 36.52) * mm});
            skLineSegment(sketch, "E14427", {"start": v(-40.24, 36.52) * mm, "end": v(-40.14, 37.03) * mm});
            skLineSegment(sketch, "E14428", {"start": v(-40.14, 37.03) * mm, "end": v(-40, 37.59) * mm});
            skLineSegment(sketch, "E14429", {"start": v(-40, 37.59) * mm, "end": v(-39.96, 37.74) * mm});
            skArc(sketch, "E14430", {"start": v(-39.96, 37.74) * mm, "mid": v(-38.92, 37.96) * mm, "end": v(-37.87, 38.14) * mm});
            skLineSegment(sketch, "E14431", {"start": v(-37.87, 38.14) * mm, "end": v(-37.77, 38.02) * mm});
            skLineSegment(sketch, "E14432", {"start": v(-37.77, 38.02) * mm, "end": v(-37.44, 37.55) * mm});
            skLineSegment(sketch, "E14433", {"start": v(-37.44, 37.55) * mm, "end": v(-37.16, 37.12) * mm});
            skLineSegment(sketch, "E14434", {"start": v(-37.16, 37.12) * mm, "end": v(-36.93, 36.72) * mm});
            skLineSegment(sketch, "E14435", {"start": v(-36.93, 36.72) * mm, "end": v(-36.74, 36.35) * mm});
            skLineSegment(sketch, "E14436", {"start": v(-36.74, 36.35) * mm, "end": v(-36.6, 36.03) * mm});
            skLineSegment(sketch, "E14437", {"start": v(-36.6, 36.03) * mm, "end": v(-36.49, 35.75) * mm});
            skLineSegment(sketch, "E14438", {"start": v(-36.49, 35.75) * mm, "end": v(-36.4, 35.52) * mm});
            skLineSegment(sketch, "E14439", {"start": v(-36.4, 35.52) * mm, "end": v(-36.36, 35.33) * mm});
            skLineSegment(sketch, "E14440", {"start": v(-36.36, 35.33) * mm, "end": v(-36.33, 35.2) * mm});
            skLineSegment(sketch, "E14441", {"start": v(-36.33, 35.2) * mm, "end": v(-36.31, 35.12) * mm});
            skLineSegment(sketch, "E14442", {"start": v(-36.31, 35.12) * mm, "end": v(-36.31, 35.1) * mm});
            skLineSegment(sketch, "E14443", {"start": v(-36.31, 35.1) * mm, "end": v(-36.1, 32.93) * mm});
            skArc(sketch, "E14444", {"start": v(-36.1, 32.93) * mm, "mid": v(-34.5, 33.02) * mm, "end": v(-32.9, 32.98) * mm});
            skLineSegment(sketch, "E14445", {"start": v(-32.9, 32.98) * mm, "end": v(-32.76, 35.15) * mm});
            skLineSegment(sketch, "E14446", {"start": v(-32.76, 35.15) * mm, "end": v(-32.75, 35.18) * mm});
            skLineSegment(sketch, "E14447", {"start": v(-32.75, 35.18) * mm, "end": v(-32.74, 35.26) * mm});
            skLineSegment(sketch, "E14448", {"start": v(-32.74, 35.26) * mm, "end": v(-32.72, 35.4) * mm});
            skLineSegment(sketch, "E14449", {"start": v(-32.72, 35.4) * mm, "end": v(-32.67, 35.58) * mm});
            skLineSegment(sketch, "E14450", {"start": v(-32.67, 35.58) * mm, "end": v(-32.6, 35.81) * mm});
            skLineSegment(sketch, "E14451", {"start": v(-32.6, 35.81) * mm, "end": v(-32.5, 36.1) * mm});
            skLineSegment(sketch, "E14452", {"start": v(-32.5, 36.1) * mm, "end": v(-32.36, 36.42) * mm});
            skLineSegment(sketch, "E14453", {"start": v(-32.36, 36.42) * mm, "end": v(-32.19, 36.79) * mm});
            skLineSegment(sketch, "E14454", {"start": v(-32.19, 36.79) * mm, "end": v(-31.97, 37.2) * mm});
            skLineSegment(sketch, "E14455", {"start": v(-31.97, 37.2) * mm, "end": v(-31.7, 37.64) * mm});
            skLineSegment(sketch, "E14456", {"start": v(-31.7, 37.64) * mm, "end": v(-31.39, 38.12) * mm});
            skLineSegment(sketch, "E14457", {"start": v(-31.39, 38.12) * mm, "end": v(-31.29, 38.24) * mm});
            skArc(sketch, "E14458", {"start": v(-31.29, 38.24) * mm, "mid": v(-30.24, 38.1) * mm, "end": v(-29.2, 37.9) * mm});
            skLineSegment(sketch, "E14459", {"start": v(-29.2, 37.9) * mm, "end": v(-29.14, 37.76) * mm});
            skLineSegment(sketch, "E14460", {"start": v(-29.14, 37.76) * mm, "end": v(-28.99, 37.2) * mm});
            skLineSegment(sketch, "E14461", {"start": v(-28.99, 37.2) * mm, "end": v(-28.87, 36.7) * mm});
            skLineSegment(sketch, "E14462", {"start": v(-28.87, 36.7) * mm, "end": v(-28.8, 36.24) * mm});
            skLineSegment(sketch, "E14463", {"start": v(-28.8, 36.24) * mm, "end": v(-28.74, 35.84) * mm});
            skLineSegment(sketch, "E14464", {"start": v(-28.74, 35.84) * mm, "end": v(-28.72, 35.49) * mm});
            skLineSegment(sketch, "E14465", {"start": v(-28.72, 35.49) * mm, "end": v(-28.7, 35.19) * mm});
            skLineSegment(sketch, "E14466", {"start": v(-28.7, 35.19) * mm, "end": v(-28.72, 34.94) * mm});
            skLineSegment(sketch, "E14467", {"start": v(-28.72, 34.94) * mm, "end": v(-28.73, 34.75) * mm});
            skLineSegment(sketch, "E14468", {"start": v(-28.73, 34.75) * mm, "end": v(-28.75, 34.62) * mm});
            skLineSegment(sketch, "E14469", {"start": v(-28.75, 34.62) * mm, "end": v(-28.76, 34.54) * mm});
            skLineSegment(sketch, "E14470", {"start": v(-28.76, 34.54) * mm, "end": v(-28.77, 34.5) * mm});
            skLineSegment(sketch, "E14471", {"start": v(-28.77, 34.5) * mm, "end": v(-29.3, 32.4) * mm});
            skArc(sketch, "E14472", {"start": v(-29.3, 32.4) * mm, "mid": v(-27.78, 31.94) * mm, "end": v(-26.29, 31.36) * mm});
            skLineSegment(sketch, "E14473", {"start": v(-26.29, 31.36) * mm, "end": v(-25.4, 33.35) * mm});
            skLineSegment(sketch, "E14474", {"start": v(-25.4, 33.35) * mm, "end": v(-25.4, 33.37) * mm});
            skLineSegment(sketch, "E14475", {"start": v(-25.4, 33.37) * mm, "end": v(-25.36, 33.44) * mm});
            skLineSegment(sketch, "E14476", {"start": v(-25.36, 33.44) * mm, "end": v(-25.29, 33.56) * mm});
            skLineSegment(sketch, "E14477", {"start": v(-25.29, 33.56) * mm, "end": v(-25.18, 33.72) * mm});
            skLineSegment(sketch, "E14478", {"start": v(-25.18, 33.72) * mm, "end": v(-25.04, 33.91) * mm});
            skLineSegment(sketch, "E14479", {"start": v(-25.04, 33.91) * mm, "end": v(-24.84, 34.14) * mm});
            skLineSegment(sketch, "E14480", {"start": v(-24.84, 34.14) * mm, "end": v(-24.6, 34.4) * mm});
            skLineSegment(sketch, "E14481", {"start": v(-24.6, 34.4) * mm, "end": v(-24.32, 34.7) * mm});
            skLineSegment(sketch, "E14482", {"start": v(-24.32, 34.7) * mm, "end": v(-23.97, 35) * mm});
            skLineSegment(sketch, "E14483", {"start": v(-23.97, 35) * mm, "end": v(-23.57, 35.33) * mm});
            skLineSegment(sketch, "E14484", {"start": v(-23.57, 35.33) * mm, "end": v(-23.1, 35.66) * mm});
            skLineSegment(sketch, "E14485", {"start": v(-23.1, 35.66) * mm, "end": v(-22.97, 35.75) * mm});
            skArc(sketch, "E14486", {"start": v(-22.97, 35.75) * mm, "mid": v(-22.03, 35.26) * mm, "end": v(-21.12, 34.72) * mm});
            skLineSegment(sketch, "E14487", {"start": v(-21.12, 34.72) * mm, "end": v(-21.12, 34.56) * mm});
            skLineSegment(sketch, "E14488", {"start": v(-21.12, 34.56) * mm, "end": v(-21.17, 33.99) * mm});
            skLineSegment(sketch, "E14489", {"start": v(-21.17, 33.99) * mm, "end": v(-21.23, 33.48) * mm});
            skLineSegment(sketch, "E14490", {"start": v(-21.23, 33.48) * mm, "end": v(-21.31, 33.02) * mm});
            skLineSegment(sketch, "E14491", {"start": v(-21.31, 33.02) * mm, "end": v(-21.4, 32.62) * mm});
            skLineSegment(sketch, "E14492", {"start": v(-21.4, 32.62) * mm, "end": v(-21.5, 32.28) * mm});
            skLineSegment(sketch, "E14493", {"start": v(-21.5, 32.28) * mm, "end": v(-21.6, 32) * mm});
            skLineSegment(sketch, "E14494", {"start": v(-21.6, 32) * mm, "end": v(-21.68, 31.77) * mm});
            skLineSegment(sketch, "E14495", {"start": v(-21.68, 31.77) * mm, "end": v(-21.76, 31.6) * mm});
            skLineSegment(sketch, "E14496", {"start": v(-21.76, 31.6) * mm, "end": v(-21.82, 31.47) * mm});
            skLineSegment(sketch, "E14497", {"start": v(-21.82, 31.47) * mm, "end": v(-21.87, 31.4) * mm});
            skLineSegment(sketch, "E14498", {"start": v(-21.87, 31.4) * mm, "end": v(-21.88, 31.38) * mm});
            skLineSegment(sketch, "E14499", {"start": v(-21.88, 31.38) * mm, "end": v(-23.11, 29.59) * mm});
            skArc(sketch, "E14500", {"start": v(-23.11, 29.59) * mm, "mid": v(-21.83, 28.63) * mm, "end": v(-20.63, 27.57) * mm});
            skCircle(sketch, "E14501", {"center": v(-34.2, 13.41) * mm, "radius": 1.25 * mm});
            skLineSegment(sketch, "E14502", {"start": v(-37.2, 11.31) * mm, "end": v(-31.2, 11.31) * mm});
            skLineSegment(sketch, "E14503", {"start": v(-31.2, 11.31) * mm, "end": v(-31.2, 15.51) * mm});
            skLineSegment(sketch, "E14504", {"start": v(-31.2, 15.51) * mm, "end": v(-37.2, 15.51) * mm});
            skLineSegment(sketch, "E14505", {"start": v(-37.2, 15.51) * mm, "end": v(-37.2, 11.31) * mm});
            skCircle(sketch, "E14506", {"center": v(-34.2, 13.41) * mm, "radius": 3.75 * mm});
            skLineSegment(sketch, "E14507", {"start": v(-82.63, 26.02) * mm, "end": v(-81.1, 27.68) * mm});
            skLineSegment(sketch, "E14508", {"start": v(-81.1, 27.68) * mm, "end": v(-81.09, 27.7) * mm});
            skLineSegment(sketch, "E14509", {"start": v(-81.09, 27.7) * mm, "end": v(-81.03, 27.75) * mm});
            skLineSegment(sketch, "E14510", {"start": v(-81.03, 27.75) * mm, "end": v(-80.94, 27.83) * mm});
            skLineSegment(sketch, "E14511", {"start": v(-80.94, 27.83) * mm, "end": v(-80.8, 27.93) * mm});
            skLineSegment(sketch, "E14512", {"start": v(-80.8, 27.93) * mm, "end": v(-80.63, 28.05) * mm});
            skLineSegment(sketch, "E14513", {"start": v(-80.63, 28.05) * mm, "end": v(-80.4, 28.2) * mm});
            skLineSegment(sketch, "E14514", {"start": v(-80.4, 28.2) * mm, "end": v(-80.13, 28.34) * mm});
            skLineSegment(sketch, "E14515", {"start": v(-80.13, 28.34) * mm, "end": v(-79.8, 28.5) * mm});
            skLineSegment(sketch, "E14516", {"start": v(-79.8, 28.5) * mm, "end": v(-79.42, 28.66) * mm});
            skLineSegment(sketch, "E14517", {"start": v(-79.42, 28.66) * mm, "end": v(-78.99, 28.82) * mm});
            skLineSegment(sketch, "E14518", {"start": v(-78.99, 28.82) * mm, "end": v(-78.5, 28.97) * mm});
            skLineSegment(sketch, "E14519", {"start": v(-78.5, 28.97) * mm, "end": v(-78.06, 29.09) * mm});
            skArc(sketch, "E14520", {"start": v(-78.06, 29.09) * mm, "mid": v(-77.35, 28.33) * mm, "end": v(-76.68, 27.53) * mm});
            skLineSegment(sketch, "E14521", {"start": v(-76.68, 27.53) * mm, "end": v(-76.85, 27.1) * mm});
            skLineSegment(sketch, "E14522", {"start": v(-76.85, 27.1) * mm, "end": v(-77.06, 26.64) * mm});
            skLineSegment(sketch, "E14523", {"start": v(-77.06, 26.64) * mm, "end": v(-77.27, 26.23) * mm});
            skLineSegment(sketch, "E14524", {"start": v(-77.27, 26.23) * mm, "end": v(-77.47, 25.87) * mm});
            skLineSegment(sketch, "E14525", {"start": v(-77.47, 25.87) * mm, "end": v(-77.67, 25.57) * mm});
            skLineSegment(sketch, "E14526", {"start": v(-77.67, 25.57) * mm, "end": v(-77.85, 25.31) * mm});
            skLineSegment(sketch, "E14527", {"start": v(-77.85, 25.31) * mm, "end": v(-78.02, 25.1) * mm});
            skLineSegment(sketch, "E14528", {"start": v(-78.02, 25.1) * mm, "end": v(-78.16, 24.94) * mm});
            skLineSegment(sketch, "E14529", {"start": v(-78.16, 24.94) * mm, "end": v(-78.28, 24.82) * mm});
            skLineSegment(sketch, "E14530", {"start": v(-78.28, 24.82) * mm, "end": v(-78.37, 24.74) * mm});
            skLineSegment(sketch, "E14531", {"start": v(-78.37, 24.74) * mm, "end": v(-78.43, 24.7) * mm});
            skLineSegment(sketch, "E14532", {"start": v(-78.43, 24.7) * mm, "end": v(-78.45, 24.68) * mm});
            skLineSegment(sketch, "E14533", {"start": v(-78.45, 24.68) * mm, "end": v(-80.28, 23.37) * mm});
            skArc(sketch, "E14534", {"start": v(-80.28, 23.37) * mm, "mid": v(-79.42, 22.04) * mm, "end": v(-78.69, 20.63) * mm});
            skLineSegment(sketch, "E14535", {"start": v(-78.69, 20.63) * mm, "end": v(-76.64, 21.58) * mm});
            skLineSegment(sketch, "E14536", {"start": v(-76.64, 21.58) * mm, "end": v(-76.62, 21.6) * mm});
            skLineSegment(sketch, "E14537", {"start": v(-76.62, 21.6) * mm, "end": v(-76.55, 21.62) * mm});
            skLineSegment(sketch, "E14538", {"start": v(-76.55, 21.62) * mm, "end": v(-76.44, 21.66) * mm});
            skLineSegment(sketch, "E14539", {"start": v(-76.44, 21.66) * mm, "end": v(-76.27, 21.7) * mm});
            skLineSegment(sketch, "E14540", {"start": v(-76.27, 21.7) * mm, "end": v(-76.06, 21.75) * mm});
            skLineSegment(sketch, "E14541", {"start": v(-76.06, 21.75) * mm, "end": v(-75.8, 21.79) * mm});
            skLineSegment(sketch, "E14542", {"start": v(-75.8, 21.79) * mm, "end": v(-75.48, 21.82) * mm});
            skLineSegment(sketch, "E14543", {"start": v(-75.48, 21.82) * mm, "end": v(-75.12, 21.84) * mm});
            skLineSegment(sketch, "E14544", {"start": v(-75.12, 21.84) * mm, "end": v(-74.71, 21.85) * mm});
            skLineSegment(sketch, "E14545", {"start": v(-74.71, 21.85) * mm, "end": v(-74.25, 21.83) * mm});
            skLineSegment(sketch, "E14546", {"start": v(-74.25, 21.83) * mm, "end": v(-73.74, 21.78) * mm});
            skLineSegment(sketch, "E14547", {"start": v(-73.74, 21.78) * mm, "end": v(-73.29, 21.72) * mm});
            skArc(sketch, "E14548", {"start": v(-73.29, 21.72) * mm, "mid": v(-72.92, 20.74) * mm, "end": v(-72.6, 19.75) * mm});
            skLineSegment(sketch, "E14549", {"start": v(-72.6, 19.75) * mm, "end": v(-72.93, 19.42) * mm});
            skLineSegment(sketch, "E14550", {"start": v(-72.93, 19.42) * mm, "end": v(-73.3, 19.07) * mm});
            skLineSegment(sketch, "E14551", {"start": v(-73.3, 19.07) * mm, "end": v(-73.65, 18.77) * mm});
            skLineSegment(sketch, "E14552", {"start": v(-73.65, 18.77) * mm, "end": v(-73.98, 18.52) * mm});
            skLineSegment(sketch, "E14553", {"start": v(-73.98, 18.52) * mm, "end": v(-74.28, 18.32) * mm});
            skLineSegment(sketch, "E14554", {"start": v(-74.28, 18.32) * mm, "end": v(-74.54, 18.15) * mm});
            skLineSegment(sketch, "E14555", {"start": v(-74.54, 18.15) * mm, "end": v(-74.78, 18.02) * mm});
            skLineSegment(sketch, "E14556", {"start": v(-74.78, 18.02) * mm, "end": v(-74.97, 17.93) * mm});
            skLineSegment(sketch, "E14557", {"start": v(-74.97, 17.93) * mm, "end": v(-75.13, 17.86) * mm});
            skLineSegment(sketch, "E14558", {"start": v(-75.13, 17.86) * mm, "end": v(-75.24, 17.82) * mm});
            skLineSegment(sketch, "E14559", {"start": v(-75.24, 17.82) * mm, "end": v(-75.31, 17.8) * mm});
            skLineSegment(sketch, "E14560", {"start": v(-75.31, 17.8) * mm, "end": v(-75.34, 17.8) * mm});
            skLineSegment(sketch, "E14561", {"start": v(-75.34, 17.8) * mm, "end": v(-77.53, 17.28) * mm});
            skArc(sketch, "E14562", {"start": v(-77.53, 17.28) * mm, "mid": v(-77.25, 15.73) * mm, "end": v(-77.1, 14.15) * mm});
            skLineSegment(sketch, "E14563", {"start": v(-77.1, 14.15) * mm, "end": v(-74.85, 14.24) * mm});
            skLineSegment(sketch, "E14564", {"start": v(-74.85, 14.24) * mm, "end": v(-74.83, 14.25) * mm});
            skLineSegment(sketch, "E14565", {"start": v(-74.83, 14.25) * mm, "end": v(-74.75, 14.24) * mm});
            skLineSegment(sketch, "E14566", {"start": v(-74.75, 14.24) * mm, "end": v(-74.63, 14.23) * mm});
            skLineSegment(sketch, "E14567", {"start": v(-74.63, 14.23) * mm, "end": v(-74.47, 14.2) * mm});
            skLineSegment(sketch, "E14568", {"start": v(-74.47, 14.2) * mm, "end": v(-74.25, 14.17) * mm});
            skLineSegment(sketch, "E14569", {"start": v(-74.25, 14.17) * mm, "end": v(-74, 14.1) * mm});
            skLineSegment(sketch, "E14570", {"start": v(-74, 14.1) * mm, "end": v(-73.7, 14.02) * mm});
            skLineSegment(sketch, "E14571", {"start": v(-73.7, 14.02) * mm, "end": v(-73.35, 13.9) * mm});
            skLineSegment(sketch, "E14572", {"start": v(-73.35, 13.9) * mm, "end": v(-72.97, 13.75) * mm});
            skLineSegment(sketch, "E14573", {"start": v(-72.97, 13.75) * mm, "end": v(-72.55, 13.56) * mm});
            skLineSegment(sketch, "E14574", {"start": v(-72.55, 13.56) * mm, "end": v(-72.1, 13.32) * mm});
            skLineSegment(sketch, "E14575", {"start": v(-72.1, 13.32) * mm, "end": v(-71.7, 13.09) * mm});
            skArc(sketch, "E14576", {"start": v(-71.7, 13.09) * mm, "mid": v(-71.74, 12.05) * mm, "end": v(-71.83, 11) * mm});
            skLineSegment(sketch, "E14577", {"start": v(-71.83, 11) * mm, "end": v(-72.25, 10.82) * mm});
            skLineSegment(sketch, "E14578", {"start": v(-72.25, 10.82) * mm, "end": v(-72.73, 10.65) * mm});
            skLineSegment(sketch, "E14579", {"start": v(-72.73, 10.65) * mm, "end": v(-73.16, 10.5) * mm});
            skLineSegment(sketch, "E14580", {"start": v(-73.16, 10.5) * mm, "end": v(-73.56, 10.4) * mm});
            skLineSegment(sketch, "E14581", {"start": v(-73.56, 10.4) * mm, "end": v(-73.92, 10.32) * mm});
            skLineSegment(sketch, "E14582", {"start": v(-73.92, 10.32) * mm, "end": v(-74.23, 10.27) * mm});
            skLineSegment(sketch, "E14583", {"start": v(-74.23, 10.27) * mm, "end": v(-74.5, 10.24) * mm});
            skLineSegment(sketch, "E14584", {"start": v(-74.5, 10.24) * mm, "end": v(-74.7, 10.23) * mm});
            skLineSegment(sketch, "E14585", {"start": v(-74.7, 10.23) * mm, "end": v(-74.88, 10.23) * mm});
            skLineSegment(sketch, "E14586", {"start": v(-74.88, 10.23) * mm, "end": v(-75, 10.23) * mm});
            skLineSegment(sketch, "E14587", {"start": v(-75, 10.23) * mm, "end": v(-75.07, 10.24) * mm});
            skLineSegment(sketch, "E14588", {"start": v(-75.07, 10.24) * mm, "end": v(-75.1, 10.24) * mm});
            skLineSegment(sketch, "E14589", {"start": v(-75.1, 10.24) * mm, "end": v(-77.32, 10.61) * mm});
            skArc(sketch, "E14590", {"start": v(-77.32, 10.61) * mm, "mid": v(-77.65, 9.06) * mm, "end": v(-78.12, 7.55) * mm});
            skLineSegment(sketch, "E14591", {"start": v(-78.12, 7.55) * mm, "end": v(-76, 6.78) * mm});
            skLineSegment(sketch, "E14592", {"start": v(-76, 6.78) * mm, "end": v(-75.98, 6.77) * mm});
            skLineSegment(sketch, "E14593", {"start": v(-75.98, 6.77) * mm, "end": v(-75.92, 6.74) * mm});
            skLineSegment(sketch, "E14594", {"start": v(-75.92, 6.74) * mm, "end": v(-75.8, 6.68) * mm});
            skLineSegment(sketch, "E14595", {"start": v(-75.8, 6.68) * mm, "end": v(-75.66, 6.6) * mm});
            skLineSegment(sketch, "E14596", {"start": v(-75.66, 6.6) * mm, "end": v(-75.48, 6.48) * mm});
            skLineSegment(sketch, "E14597", {"start": v(-75.48, 6.48) * mm, "end": v(-75.26, 6.32) * mm});
            skLineSegment(sketch, "E14598", {"start": v(-75.26, 6.32) * mm, "end": v(-75.02, 6.13) * mm});
            skLineSegment(sketch, "E14599", {"start": v(-75.02, 6.13) * mm, "end": v(-74.75, 5.89) * mm});
            skLineSegment(sketch, "E14600", {"start": v(-74.75, 5.89) * mm, "end": v(-74.45, 5.6) * mm});
            skLineSegment(sketch, "E14601", {"start": v(-74.45, 5.6) * mm, "end": v(-74.14, 5.26) * mm});
            skLineSegment(sketch, "E14602", {"start": v(-74.14, 5.26) * mm, "end": v(-73.82, 4.87) * mm});
            skLineSegment(sketch, "E14603", {"start": v(-73.82, 4.87) * mm, "end": v(-73.54, 4.5) * mm});
            skArc(sketch, "E14604", {"start": v(-73.54, 4.5) * mm, "mid": v(-73.97, 3.56) * mm, "end": v(-74.45, 2.63) * mm});
            skLineSegment(sketch, "E14605", {"start": v(-74.45, 2.63) * mm, "end": v(-74.91, 2.62) * mm});
            skLineSegment(sketch, "E14606", {"start": v(-74.91, 2.62) * mm, "end": v(-75.42, 2.64) * mm});
            skLineSegment(sketch, "E14607", {"start": v(-75.42, 2.64) * mm, "end": v(-75.88, 2.68) * mm});
            skLineSegment(sketch, "E14608", {"start": v(-75.88, 2.68) * mm, "end": v(-76.29, 2.73) * mm});
            skLineSegment(sketch, "E14609", {"start": v(-76.29, 2.73) * mm, "end": v(-76.64, 2.8) * mm});
            skLineSegment(sketch, "E14610", {"start": v(-76.64, 2.8) * mm, "end": v(-76.95, 2.87) * mm});
            skLineSegment(sketch, "E14611", {"start": v(-76.95, 2.87) * mm, "end": v(-77.2, 2.94) * mm});
            skLineSegment(sketch, "E14612", {"start": v(-77.2, 2.94) * mm, "end": v(-77.41, 3.01) * mm});
            skLineSegment(sketch, "E14613", {"start": v(-77.41, 3.01) * mm, "end": v(-77.57, 3.08) * mm});
            skLineSegment(sketch, "E14614", {"start": v(-77.57, 3.08) * mm, "end": v(-77.68, 3.13) * mm});
            skLineSegment(sketch, "E14615", {"start": v(-77.68, 3.13) * mm, "end": v(-77.74, 3.16) * mm});
            skLineSegment(sketch, "E14616", {"start": v(-77.74, 3.16) * mm, "end": v(-77.76, 3.17) * mm});
            skLineSegment(sketch, "E14617", {"start": v(-77.76, 3.17) * mm, "end": v(-79.68, 4.37) * mm});
            skArc(sketch, "E14618", {"start": v(-79.68, 4.37) * mm, "mid": v(-80.58, 3.06) * mm, "end": v(-81.6, 1.85) * mm});
            skLineSegment(sketch, "E14619", {"start": v(-81.6, 1.85) * mm, "end": v(-79.93, 0.32) * mm});
            skLineSegment(sketch, "E14620", {"start": v(-79.93, 0.32) * mm, "end": v(-79.91, 0.3) * mm});
            skLineSegment(sketch, "E14621", {"start": v(-79.91, 0.3) * mm, "end": v(-79.86, 0.25) * mm});
            skLineSegment(sketch, "E14622", {"start": v(-79.86, 0.25) * mm, "end": v(-79.78, 0.16) * mm});
            skLineSegment(sketch, "E14623", {"start": v(-79.78, 0.16) * mm, "end": v(-79.68, 0.03) * mm});
            skLineSegment(sketch, "E14624", {"start": v(-79.68, 0.03) * mm, "end": v(-79.56, -0.15) * mm});
            skLineSegment(sketch, "E14625", {"start": v(-79.56, -0.15) * mm, "end": v(-79.42, -0.38) * mm});
            skLineSegment(sketch, "E14626", {"start": v(-79.42, -0.38) * mm, "end": v(-79.27, -0.66) * mm});
            skLineSegment(sketch, "E14627", {"start": v(-79.27, -0.66) * mm, "end": v(-79.1, -0.98) * mm});
            skLineSegment(sketch, "E14628", {"start": v(-79.1, -0.98) * mm, "end": v(-78.95, -1.36) * mm});
            skLineSegment(sketch, "E14629", {"start": v(-78.95, -1.36) * mm, "end": v(-78.79, -1.8) * mm});
            skLineSegment(sketch, "E14630", {"start": v(-78.79, -1.8) * mm, "end": v(-78.64, -2.28) * mm});
            skLineSegment(sketch, "E14631", {"start": v(-78.64, -2.28) * mm, "end": v(-78.52, -2.73) * mm});
            skArc(sketch, "E14632", {"start": v(-78.52, -2.73) * mm, "mid": v(-79.28, -3.43) * mm, "end": v(-80.08, -4.1) * mm});
            skLineSegment(sketch, "E14633", {"start": v(-80.08, -4.1) * mm, "end": v(-80.5, -3.94) * mm});
            skLineSegment(sketch, "E14634", {"start": v(-80.5, -3.94) * mm, "end": v(-80.97, -3.73) * mm});
            skLineSegment(sketch, "E14635", {"start": v(-80.97, -3.73) * mm, "end": v(-81.38, -3.52) * mm});
            skLineSegment(sketch, "E14636", {"start": v(-81.38, -3.52) * mm, "end": v(-81.74, -3.3) * mm});
            skLineSegment(sketch, "E14637", {"start": v(-81.74, -3.3) * mm, "end": v(-82.04, -3.11) * mm});
            skLineSegment(sketch, "E14638", {"start": v(-82.04, -3.11) * mm, "end": v(-82.3, -2.93) * mm});
            skLineSegment(sketch, "E14639", {"start": v(-82.3, -2.93) * mm, "end": v(-82.5, -2.76) * mm});
            skLineSegment(sketch, "E14640", {"start": v(-82.5, -2.76) * mm, "end": v(-82.67, -2.62) * mm});
            skLineSegment(sketch, "E14641", {"start": v(-82.67, -2.62) * mm, "end": v(-82.79, -2.5) * mm});
            skLineSegment(sketch, "E14642", {"start": v(-82.79, -2.5) * mm, "end": v(-82.87, -2.41) * mm});
            skLineSegment(sketch, "E14643", {"start": v(-82.87, -2.41) * mm, "end": v(-82.92, -2.36) * mm});
            skLineSegment(sketch, "E14644", {"start": v(-82.92, -2.36) * mm, "end": v(-82.93, -2.34) * mm});
            skLineSegment(sketch, "E14645", {"start": v(-82.93, -2.34) * mm, "end": v(-84.25, -0.5) * mm});
            skArc(sketch, "E14646", {"start": v(-84.25, -0.5) * mm, "mid": v(-85.57, -1.36) * mm, "end": v(-86.98, -2.1) * mm});
            skLineSegment(sketch, "E14647", {"start": v(-86.98, -2.1) * mm, "end": v(-86.03, -4.14) * mm});
            skLineSegment(sketch, "E14648", {"start": v(-86.03, -4.14) * mm, "end": v(-86.02, -4.16) * mm});
            skLineSegment(sketch, "E14649", {"start": v(-86.02, -4.16) * mm, "end": v(-86, -4.23) * mm});
            skLineSegment(sketch, "E14650", {"start": v(-86, -4.23) * mm, "end": v(-85.95, -4.35) * mm});
            skLineSegment(sketch, "E14651", {"start": v(-85.95, -4.35) * mm, "end": v(-85.91, -4.5) * mm});
            skLineSegment(sketch, "E14652", {"start": v(-85.91, -4.5) * mm, "end": v(-85.87, -4.72) * mm});
            skLineSegment(sketch, "E14653", {"start": v(-85.87, -4.72) * mm, "end": v(-85.82, -4.99) * mm});
            skLineSegment(sketch, "E14654", {"start": v(-85.82, -4.99) * mm, "end": v(-85.79, -5.3) * mm});
            skLineSegment(sketch, "E14655", {"start": v(-85.79, -5.3) * mm, "end": v(-85.77, -5.66) * mm});
            skLineSegment(sketch, "E14656", {"start": v(-85.77, -5.66) * mm, "end": v(-85.76, -6.07) * mm});
            skLineSegment(sketch, "E14657", {"start": v(-85.76, -6.07) * mm, "end": v(-85.78, -6.53) * mm});
            skLineSegment(sketch, "E14658", {"start": v(-85.78, -6.53) * mm, "end": v(-85.83, -7.04) * mm});
            skLineSegment(sketch, "E14659", {"start": v(-85.83, -7.04) * mm, "end": v(-85.9, -7.5) * mm});
            skArc(sketch, "E14660", {"start": v(-85.9, -7.5) * mm, "mid": v(-86.87, -7.86) * mm, "end": v(-87.86, -8.17) * mm});
            skLineSegment(sketch, "E14661", {"start": v(-87.86, -8.17) * mm, "end": v(-88.2, -7.85) * mm});
            skLineSegment(sketch, "E14662", {"start": v(-88.2, -7.85) * mm, "end": v(-88.54, -7.48) * mm});
            skLineSegment(sketch, "E14663", {"start": v(-88.54, -7.48) * mm, "end": v(-88.84, -7.13) * mm});
            skLineSegment(sketch, "E14664", {"start": v(-88.84, -7.13) * mm, "end": v(-89.09, -6.8) * mm});
            skLineSegment(sketch, "E14665", {"start": v(-89.09, -6.8) * mm, "end": v(-89.3, -6.5) * mm});
            skLineSegment(sketch, "E14666", {"start": v(-89.3, -6.5) * mm, "end": v(-89.46, -6.24) * mm});
            skLineSegment(sketch, "E14667", {"start": v(-89.46, -6.24) * mm, "end": v(-89.59, -6) * mm});
            skLineSegment(sketch, "E14668", {"start": v(-89.59, -6) * mm, "end": v(-89.68, -5.8) * mm});
            skLineSegment(sketch, "E14669", {"start": v(-89.68, -5.8) * mm, "end": v(-89.75, -5.65) * mm});
            skLineSegment(sketch, "E14670", {"start": v(-89.75, -5.65) * mm, "end": v(-89.79, -5.54) * mm});
            skLineSegment(sketch, "E14671", {"start": v(-89.79, -5.54) * mm, "end": v(-89.81, -5.47) * mm});
            skLineSegment(sketch, "E14672", {"start": v(-89.81, -5.47) * mm, "end": v(-89.82, -5.45) * mm});
            skLineSegment(sketch, "E14673", {"start": v(-89.82, -5.45) * mm, "end": v(-90.33, -3.25) * mm});
            skArc(sketch, "E14674", {"start": v(-90.33, -3.25) * mm, "mid": v(-91.89, -3.54) * mm, "end": v(-93.46, -3.68) * mm});
            skLineSegment(sketch, "E14675", {"start": v(-93.46, -3.68) * mm, "end": v(-93.37, -5.93) * mm});
            skLineSegment(sketch, "E14676", {"start": v(-93.37, -5.93) * mm, "end": v(-93.37, -5.96) * mm});
            skLineSegment(sketch, "E14677", {"start": v(-93.37, -5.96) * mm, "end": v(-93.37, -6.03) * mm});
            skLineSegment(sketch, "E14678", {"start": v(-93.37, -6.03) * mm, "end": v(-93.38, -6.15) * mm});
            skLineSegment(sketch, "E14679", {"start": v(-93.38, -6.15) * mm, "end": v(-93.4, -6.32) * mm});
            skLineSegment(sketch, "E14680", {"start": v(-93.4, -6.32) * mm, "end": v(-93.44, -6.53) * mm});
            skLineSegment(sketch, "E14681", {"start": v(-93.44, -6.53) * mm, "end": v(-93.5, -6.79) * mm});
            skLineSegment(sketch, "E14682", {"start": v(-93.5, -6.79) * mm, "end": v(-93.59, -7.1) * mm});
            skLineSegment(sketch, "E14683", {"start": v(-93.59, -7.1) * mm, "end": v(-93.7, -7.43) * mm});
            skLineSegment(sketch, "E14684", {"start": v(-93.7, -7.43) * mm, "end": v(-93.86, -7.82) * mm});
            skLineSegment(sketch, "E14685", {"start": v(-93.86, -7.82) * mm, "end": v(-94.05, -8.23) * mm});
            skLineSegment(sketch, "E14686", {"start": v(-94.05, -8.23) * mm, "end": v(-94.29, -8.68) * mm});
            skLineSegment(sketch, "E14687", {"start": v(-94.29, -8.68) * mm, "end": v(-94.53, -9.08) * mm});
            skArc(sketch, "E14688", {"start": v(-94.53, -9.08) * mm, "mid": v(-95.56, -9.04) * mm, "end": v(-96.6, -8.96) * mm});
            skLineSegment(sketch, "E14689", {"start": v(-96.6, -8.96) * mm, "end": v(-96.79, -8.53) * mm});
            skLineSegment(sketch, "E14690", {"start": v(-96.79, -8.53) * mm, "end": v(-96.97, -8.06) * mm});
            skLineSegment(sketch, "E14691", {"start": v(-96.97, -8.06) * mm, "end": v(-97.1, -7.62) * mm});
            skLineSegment(sketch, "E14692", {"start": v(-97.1, -7.62) * mm, "end": v(-97.21, -7.22) * mm});
            skLineSegment(sketch, "E14693", {"start": v(-97.21, -7.22) * mm, "end": v(-97.29, -6.87) * mm});
            skLineSegment(sketch, "E14694", {"start": v(-97.29, -6.87) * mm, "end": v(-97.34, -6.56) * mm});
            skLineSegment(sketch, "E14695", {"start": v(-97.34, -6.56) * mm, "end": v(-97.37, -6.3) * mm});
            skLineSegment(sketch, "E14696", {"start": v(-97.37, -6.3) * mm, "end": v(-97.38, -6.07) * mm});
            skLineSegment(sketch, "E14697", {"start": v(-97.38, -6.07) * mm, "end": v(-97.38, -5.9) * mm});
            skLineSegment(sketch, "E14698", {"start": v(-97.38, -5.9) * mm, "end": v(-97.38, -5.78) * mm});
            skLineSegment(sketch, "E14699", {"start": v(-97.38, -5.78) * mm, "end": v(-97.37, -5.71) * mm});
            skLineSegment(sketch, "E14700", {"start": v(-97.37, -5.71) * mm, "end": v(-97.37, -5.69) * mm});
            skLineSegment(sketch, "E14701", {"start": v(-97.37, -5.69) * mm, "end": v(-97, -3.46) * mm});
            skArc(sketch, "E14702", {"start": v(-97, -3.46) * mm, "mid": v(-98.55, -3.13) * mm, "end": v(-100.06, -2.66) * mm});
            skLineSegment(sketch, "E14703", {"start": v(-100.06, -2.66) * mm, "end": v(-100.83, -4.78) * mm});
            skLineSegment(sketch, "E14704", {"start": v(-100.83, -4.78) * mm, "end": v(-100.84, -4.8) * mm});
            skLineSegment(sketch, "E14705", {"start": v(-100.84, -4.8) * mm, "end": v(-100.87, -4.87) * mm});
            skLineSegment(sketch, "E14706", {"start": v(-100.87, -4.87) * mm, "end": v(-100.93, -4.97) * mm});
            skLineSegment(sketch, "E14707", {"start": v(-100.93, -4.97) * mm, "end": v(-101.01, -5.12) * mm});
            skLineSegment(sketch, "E14708", {"start": v(-101.01, -5.12) * mm, "end": v(-101.13, -5.3) * mm});
            skLineSegment(sketch, "E14709", {"start": v(-101.13, -5.3) * mm, "end": v(-101.29, -5.52) * mm});
            skLineSegment(sketch, "E14710", {"start": v(-101.29, -5.52) * mm, "end": v(-101.48, -5.76) * mm});
            skLineSegment(sketch, "E14711", {"start": v(-101.48, -5.76) * mm, "end": v(-101.72, -6.03) * mm});
            skLineSegment(sketch, "E14712", {"start": v(-101.72, -6.03) * mm, "end": v(-102.01, -6.33) * mm});
            skLineSegment(sketch, "E14713", {"start": v(-102.01, -6.33) * mm, "end": v(-102.35, -6.64) * mm});
            skLineSegment(sketch, "E14714", {"start": v(-102.35, -6.64) * mm, "end": v(-102.74, -6.97) * mm});
            skLineSegment(sketch, "E14715", {"start": v(-102.74, -6.97) * mm, "end": v(-103.1, -7.25) * mm});
            skArc(sketch, "E14716", {"start": v(-103.1, -7.25) * mm, "mid": v(-104.05, -6.81) * mm, "end": v(-104.98, -6.33) * mm});
            skLineSegment(sketch, "E14717", {"start": v(-104.98, -6.33) * mm, "end": v(-104.99, -5.87) * mm});
            skLineSegment(sketch, "E14718", {"start": v(-104.99, -5.87) * mm, "end": v(-104.97, -5.36) * mm});
            skLineSegment(sketch, "E14719", {"start": v(-104.97, -5.36) * mm, "end": v(-104.93, -4.9) * mm});
            skLineSegment(sketch, "E14720", {"start": v(-104.93, -4.9) * mm, "end": v(-104.88, -4.5) * mm});
            skLineSegment(sketch, "E14721", {"start": v(-104.88, -4.5) * mm, "end": v(-104.81, -4.14) * mm});
            skLineSegment(sketch, "E14722", {"start": v(-104.81, -4.14) * mm, "end": v(-104.74, -3.83) * mm});
            skLineSegment(sketch, "E14723", {"start": v(-104.74, -3.83) * mm, "end": v(-104.67, -3.58) * mm});
            skLineSegment(sketch, "E14724", {"start": v(-104.67, -3.58) * mm, "end": v(-104.6, -3.37) * mm});
            skLineSegment(sketch, "E14725", {"start": v(-104.6, -3.37) * mm, "end": v(-104.53, -3.21) * mm});
            skLineSegment(sketch, "E14726", {"start": v(-104.53, -3.21) * mm, "end": v(-104.48, -3.1) * mm});
            skLineSegment(sketch, "E14727", {"start": v(-104.48, -3.1) * mm, "end": v(-104.45, -3.04) * mm});
            skLineSegment(sketch, "E14728", {"start": v(-104.45, -3.04) * mm, "end": v(-104.44, -3.02) * mm});
            skLineSegment(sketch, "E14729", {"start": v(-104.44, -3.02) * mm, "end": v(-103.24, -1.1) * mm});
            skArc(sketch, "E14730", {"start": v(-103.24, -1.1) * mm, "mid": v(-104.55, -0.2) * mm, "end": v(-105.76, 0.8) * mm});
            skLineSegment(sketch, "E14731", {"start": v(-105.76, 0.8) * mm, "end": v(-107.29, -0.85) * mm});
            skLineSegment(sketch, "E14732", {"start": v(-107.29, -0.85) * mm, "end": v(-107.3, -0.87) * mm});
            skLineSegment(sketch, "E14733", {"start": v(-107.3, -0.87) * mm, "end": v(-107.36, -0.92) * mm});
            skLineSegment(sketch, "E14734", {"start": v(-107.36, -0.92) * mm, "end": v(-107.45, -1) * mm});
            skLineSegment(sketch, "E14735", {"start": v(-107.45, -1) * mm, "end": v(-107.58, -1.1) * mm});
            skLineSegment(sketch, "E14736", {"start": v(-107.58, -1.1) * mm, "end": v(-107.76, -1.22) * mm});
            skLineSegment(sketch, "E14737", {"start": v(-107.76, -1.22) * mm, "end": v(-108, -1.36) * mm});
            skLineSegment(sketch, "E14738", {"start": v(-108, -1.36) * mm, "end": v(-108.27, -1.52) * mm});
            skLineSegment(sketch, "E14739", {"start": v(-108.27, -1.52) * mm, "end": v(-108.6, -1.67) * mm});
            skLineSegment(sketch, "E14740", {"start": v(-108.6, -1.67) * mm, "end": v(-108.97, -1.84) * mm});
            skLineSegment(sketch, "E14741", {"start": v(-108.97, -1.84) * mm, "end": v(-109.4, -2) * mm});
            skLineSegment(sketch, "E14742", {"start": v(-109.4, -2) * mm, "end": v(-109.89, -2.15) * mm});
            skLineSegment(sketch, "E14743", {"start": v(-109.89, -2.15) * mm, "end": v(-110.34, -2.26) * mm});
            skArc(sketch, "E14744", {"start": v(-110.34, -2.26) * mm, "mid": v(-111.04, -1.5) * mm, "end": v(-111.72, -0.7) * mm});
            skLineSegment(sketch, "E14745", {"start": v(-111.72, -0.7) * mm, "end": v(-111.55, -0.27) * mm});
            skLineSegment(sketch, "E14746", {"start": v(-111.55, -0.27) * mm, "end": v(-111.34, 0.19) * mm});
            skLineSegment(sketch, "E14747", {"start": v(-111.34, 0.19) * mm, "end": v(-111.13, 0.6) * mm});
            skLineSegment(sketch, "E14748", {"start": v(-111.13, 0.6) * mm, "end": v(-110.92, 0.95) * mm});
            skLineSegment(sketch, "E14749", {"start": v(-110.92, 0.95) * mm, "end": v(-110.72, 1.26) * mm});
            skLineSegment(sketch, "E14750", {"start": v(-110.72, 1.26) * mm, "end": v(-110.54, 1.51) * mm});
            skLineSegment(sketch, "E14751", {"start": v(-110.54, 1.51) * mm, "end": v(-110.37, 1.72) * mm});
            skLineSegment(sketch, "E14752", {"start": v(-110.37, 1.72) * mm, "end": v(-110.23, 1.89) * mm});
            skLineSegment(sketch, "E14753", {"start": v(-110.23, 1.89) * mm, "end": v(-110.11, 2) * mm});
            skLineSegment(sketch, "E14754", {"start": v(-110.11, 2) * mm, "end": v(-110.02, 2.09) * mm});
            skLineSegment(sketch, "E14755", {"start": v(-110.02, 2.09) * mm, "end": v(-109.97, 2.14) * mm});
            skLineSegment(sketch, "E14756", {"start": v(-109.97, 2.14) * mm, "end": v(-109.95, 2.15) * mm});
            skLineSegment(sketch, "E14757", {"start": v(-109.95, 2.15) * mm, "end": v(-108.11, 3.46) * mm});
            skArc(sketch, "E14758", {"start": v(-108.11, 3.46) * mm, "mid": v(-108.97, 4.8) * mm, "end": v(-109.7, 6.2) * mm});
            skLineSegment(sketch, "E14759", {"start": v(-109.7, 6.2) * mm, "end": v(-111.75, 5.24) * mm});
            skLineSegment(sketch, "E14760", {"start": v(-111.75, 5.24) * mm, "end": v(-111.77, 5.23) * mm});
            skLineSegment(sketch, "E14761", {"start": v(-111.77, 5.23) * mm, "end": v(-111.84, 5.2) * mm});
            skLineSegment(sketch, "E14762", {"start": v(-111.84, 5.2) * mm, "end": v(-111.96, 5.17) * mm});
            skLineSegment(sketch, "E14763", {"start": v(-111.96, 5.17) * mm, "end": v(-112.12, 5.13) * mm});
            skLineSegment(sketch, "E14764", {"start": v(-112.12, 5.13) * mm, "end": v(-112.33, 5.08) * mm});
            skLineSegment(sketch, "E14765", {"start": v(-112.33, 5.08) * mm, "end": v(-112.6, 5.04) * mm});
            skLineSegment(sketch, "E14766", {"start": v(-112.6, 5.04) * mm, "end": v(-112.9, 5) * mm});
            skLineSegment(sketch, "E14767", {"start": v(-112.9, 5) * mm, "end": v(-113.27, 4.98) * mm});
            skLineSegment(sketch, "E14768", {"start": v(-113.27, 4.98) * mm, "end": v(-113.68, 4.98) * mm});
            skLineSegment(sketch, "E14769", {"start": v(-113.68, 4.98) * mm, "end": v(-114.14, 5) * mm});
            skLineSegment(sketch, "E14770", {"start": v(-114.14, 5) * mm, "end": v(-114.65, 5.04) * mm});
            skLineSegment(sketch, "E14771", {"start": v(-114.65, 5.04) * mm, "end": v(-115.1, 5.1) * mm});
            skArc(sketch, "E14772", {"start": v(-115.1, 5.1) * mm, "mid": v(-115.47, 6.08) * mm, "end": v(-115.78, 7.07) * mm});
            skLineSegment(sketch, "E14773", {"start": v(-115.78, 7.07) * mm, "end": v(-115.46, 7.4) * mm});
            skLineSegment(sketch, "E14774", {"start": v(-115.46, 7.4) * mm, "end": v(-115.1, 7.76) * mm});
            skLineSegment(sketch, "E14775", {"start": v(-115.1, 7.76) * mm, "end": v(-114.74, 8.05) * mm});
            skLineSegment(sketch, "E14776", {"start": v(-114.74, 8.05) * mm, "end": v(-114.42, 8.3) * mm});
            skLineSegment(sketch, "E14777", {"start": v(-114.42, 8.3) * mm, "end": v(-114.12, 8.5) * mm});
            skLineSegment(sketch, "E14778", {"start": v(-114.12, 8.5) * mm, "end": v(-113.85, 8.67) * mm});
            skLineSegment(sketch, "E14779", {"start": v(-113.85, 8.67) * mm, "end": v(-113.62, 8.8) * mm});
            skLineSegment(sketch, "E14780", {"start": v(-113.62, 8.8) * mm, "end": v(-113.42, 8.9) * mm});
            skLineSegment(sketch, "E14781", {"start": v(-113.42, 8.9) * mm, "end": v(-113.26, 8.97) * mm});
            skLineSegment(sketch, "E14782", {"start": v(-113.26, 8.97) * mm, "end": v(-113.15, 9) * mm});
            skLineSegment(sketch, "E14783", {"start": v(-113.15, 9) * mm, "end": v(-113.08, 9.03) * mm});
            skLineSegment(sketch, "E14784", {"start": v(-113.08, 9.03) * mm, "end": v(-113.06, 9.04) * mm});
            skLineSegment(sketch, "E14785", {"start": v(-113.06, 9.04) * mm, "end": v(-110.86, 9.55) * mm});
            skArc(sketch, "E14786", {"start": v(-110.86, 9.55) * mm, "mid": v(-111.15, 11.1) * mm, "end": v(-111.29, 12.68) * mm});
            skLineSegment(sketch, "E14787", {"start": v(-111.29, 12.68) * mm, "end": v(-113.54, 12.58) * mm});
            skLineSegment(sketch, "E14788", {"start": v(-113.54, 12.58) * mm, "end": v(-113.57, 12.58) * mm});
            skLineSegment(sketch, "E14789", {"start": v(-113.57, 12.58) * mm, "end": v(-113.64, 12.59) * mm});
            skLineSegment(sketch, "E14790", {"start": v(-113.64, 12.59) * mm, "end": v(-113.76, 12.6) * mm});
            skLineSegment(sketch, "E14791", {"start": v(-113.76, 12.6) * mm, "end": v(-113.93, 12.62) * mm});
            skLineSegment(sketch, "E14792", {"start": v(-113.93, 12.62) * mm, "end": v(-114.14, 12.66) * mm});
            skLineSegment(sketch, "E14793", {"start": v(-114.14, 12.66) * mm, "end": v(-114.4, 12.72) * mm});
            skLineSegment(sketch, "E14794", {"start": v(-114.4, 12.72) * mm, "end": v(-114.7, 12.8) * mm});
            skLineSegment(sketch, "E14795", {"start": v(-114.7, 12.8) * mm, "end": v(-115.05, 12.93) * mm});
            skLineSegment(sketch, "E14796", {"start": v(-115.05, 12.93) * mm, "end": v(-115.43, 13.08) * mm});
            skLineSegment(sketch, "E14797", {"start": v(-115.43, 13.08) * mm, "end": v(-115.84, 13.27) * mm});
            skLineSegment(sketch, "E14798", {"start": v(-115.84, 13.27) * mm, "end": v(-116.3, 13.5) * mm});
            skLineSegment(sketch, "E14799", {"start": v(-116.3, 13.5) * mm, "end": v(-116.7, 13.74) * mm});
            skArc(sketch, "E14800", {"start": v(-116.7, 13.74) * mm, "mid": v(-116.65, 14.78) * mm, "end": v(-116.57, 15.82) * mm});
            skLineSegment(sketch, "E14801", {"start": v(-116.57, 15.82) * mm, "end": v(-116.14, 16) * mm});
            skLineSegment(sketch, "E14802", {"start": v(-116.14, 16) * mm, "end": v(-115.67, 16.18) * mm});
            skLineSegment(sketch, "E14803", {"start": v(-115.67, 16.18) * mm, "end": v(-115.23, 16.32) * mm});
            skLineSegment(sketch, "E14804", {"start": v(-115.23, 16.32) * mm, "end": v(-114.83, 16.43) * mm});
            skLineSegment(sketch, "E14805", {"start": v(-114.83, 16.43) * mm, "end": v(-114.48, 16.5) * mm});
            skLineSegment(sketch, "E14806", {"start": v(-114.48, 16.5) * mm, "end": v(-114.17, 16.56) * mm});
            skLineSegment(sketch, "E14807", {"start": v(-114.17, 16.56) * mm, "end": v(-113.9, 16.59) * mm});
            skLineSegment(sketch, "E14808", {"start": v(-113.9, 16.59) * mm, "end": v(-113.68, 16.6) * mm});
            skLineSegment(sketch, "E14809", {"start": v(-113.68, 16.6) * mm, "end": v(-113.51, 16.6) * mm});
            skLineSegment(sketch, "E14810", {"start": v(-113.51, 16.6) * mm, "end": v(-113.4, 16.6) * mm});
            skLineSegment(sketch, "E14811", {"start": v(-113.4, 16.6) * mm, "end": v(-113.32, 16.59) * mm});
            skLineSegment(sketch, "E14812", {"start": v(-113.32, 16.59) * mm, "end": v(-113.3, 16.59) * mm});
            skLineSegment(sketch, "E14813", {"start": v(-113.3, 16.59) * mm, "end": v(-111.07, 16.22) * mm});
            skArc(sketch, "E14814", {"start": v(-111.07, 16.22) * mm, "mid": v(-110.74, 17.77) * mm, "end": v(-110.27, 19.28) * mm});
            skLineSegment(sketch, "E14815", {"start": v(-110.27, 19.28) * mm, "end": v(-112.39, 20.05) * mm});
            skLineSegment(sketch, "E14816", {"start": v(-112.39, 20.05) * mm, "end": v(-112.4, 20.06) * mm});
            skLineSegment(sketch, "E14817", {"start": v(-112.4, 20.06) * mm, "end": v(-112.48, 20.09) * mm});
            skLineSegment(sketch, "E14818", {"start": v(-112.48, 20.09) * mm, "end": v(-112.58, 20.14) * mm});
            skLineSegment(sketch, "E14819", {"start": v(-112.58, 20.14) * mm, "end": v(-112.73, 20.23) * mm});
            skLineSegment(sketch, "E14820", {"start": v(-112.73, 20.23) * mm, "end": v(-112.91, 20.35) * mm});
            skLineSegment(sketch, "E14821", {"start": v(-112.91, 20.35) * mm, "end": v(-113.13, 20.5) * mm});
            skLineSegment(sketch, "E14822", {"start": v(-113.13, 20.5) * mm, "end": v(-113.37, 20.7) * mm});
            skLineSegment(sketch, "E14823", {"start": v(-113.37, 20.7) * mm, "end": v(-113.65, 20.94) * mm});
            skLineSegment(sketch, "E14824", {"start": v(-113.65, 20.94) * mm, "end": v(-113.94, 21.23) * mm});
            skLineSegment(sketch, "E14825", {"start": v(-113.94, 21.23) * mm, "end": v(-114.25, 21.57) * mm});
            skLineSegment(sketch, "E14826", {"start": v(-114.25, 21.57) * mm, "end": v(-114.58, 21.96) * mm});
            skLineSegment(sketch, "E14827", {"start": v(-114.58, 21.96) * mm, "end": v(-114.86, 22.33) * mm});
            skArc(sketch, "E14828", {"start": v(-114.86, 22.33) * mm, "mid": v(-114.42, 23.27) * mm, "end": v(-113.94, 24.2) * mm});
            skLineSegment(sketch, "E14829", {"start": v(-113.94, 24.2) * mm, "end": v(-113.48, 24.2) * mm});
            skLineSegment(sketch, "E14830", {"start": v(-113.48, 24.2) * mm, "end": v(-112.97, 24.19) * mm});
            skLineSegment(sketch, "E14831", {"start": v(-112.97, 24.19) * mm, "end": v(-112.51, 24.15) * mm});
            skLineSegment(sketch, "E14832", {"start": v(-112.51, 24.15) * mm, "end": v(-112.1, 24.1) * mm});
            skLineSegment(sketch, "E14833", {"start": v(-112.1, 24.1) * mm, "end": v(-111.75, 24.03) * mm});
            skLineSegment(sketch, "E14834", {"start": v(-111.75, 24.03) * mm, "end": v(-111.44, 23.96) * mm});
            skLineSegment(sketch, "E14835", {"start": v(-111.44, 23.96) * mm, "end": v(-111.19, 23.88) * mm});
            skLineSegment(sketch, "E14836", {"start": v(-111.19, 23.88) * mm, "end": v(-110.98, 23.81) * mm});
            skLineSegment(sketch, "E14837", {"start": v(-110.98, 23.81) * mm, "end": v(-110.82, 23.75) * mm});
            skLineSegment(sketch, "E14838", {"start": v(-110.82, 23.75) * mm, "end": v(-110.71, 23.7) * mm});
            skLineSegment(sketch, "E14839", {"start": v(-110.71, 23.7) * mm, "end": v(-110.65, 23.67) * mm});
            skLineSegment(sketch, "E14840", {"start": v(-110.65, 23.67) * mm, "end": v(-110.63, 23.65) * mm});
            skLineSegment(sketch, "E14841", {"start": v(-110.63, 23.65) * mm, "end": v(-108.72, 22.46) * mm});
            skArc(sketch, "E14842", {"start": v(-108.72, 22.46) * mm, "mid": v(-107.82, 23.77) * mm, "end": v(-106.8, 24.98) * mm});
            skLineSegment(sketch, "E14843", {"start": v(-106.8, 24.98) * mm, "end": v(-108.46, 26.5) * mm});
            skLineSegment(sketch, "E14844", {"start": v(-108.46, 26.5) * mm, "end": v(-108.48, 26.52) * mm});
            skLineSegment(sketch, "E14845", {"start": v(-108.48, 26.52) * mm, "end": v(-108.53, 26.58) * mm});
            skLineSegment(sketch, "E14846", {"start": v(-108.53, 26.58) * mm, "end": v(-108.6, 26.67) * mm});
            skLineSegment(sketch, "E14847", {"start": v(-108.6, 26.67) * mm, "end": v(-108.71, 26.8) * mm});
            skLineSegment(sketch, "E14848", {"start": v(-108.71, 26.8) * mm, "end": v(-108.83, 26.98) * mm});
            skLineSegment(sketch, "E14849", {"start": v(-108.83, 26.98) * mm, "end": v(-108.97, 27.2) * mm});
            skLineSegment(sketch, "E14850", {"start": v(-108.97, 27.2) * mm, "end": v(-109.13, 27.48) * mm});
            skLineSegment(sketch, "E14851", {"start": v(-109.13, 27.48) * mm, "end": v(-109.28, 27.81) * mm});
            skLineSegment(sketch, "E14852", {"start": v(-109.28, 27.81) * mm, "end": v(-109.45, 28.19) * mm});
            skLineSegment(sketch, "E14853", {"start": v(-109.45, 28.19) * mm, "end": v(-109.6, 28.62) * mm});
            skLineSegment(sketch, "E14854", {"start": v(-109.6, 28.62) * mm, "end": v(-109.76, 29.1) * mm});
            skLineSegment(sketch, "E14855", {"start": v(-109.76, 29.1) * mm, "end": v(-109.87, 29.55) * mm});
            skArc(sketch, "E14856", {"start": v(-109.87, 29.55) * mm, "mid": v(-109.1, 30.26) * mm, "end": v(-108.32, 30.93) * mm});
            skLineSegment(sketch, "E14857", {"start": v(-108.32, 30.93) * mm, "end": v(-107.88, 30.76) * mm});
            skLineSegment(sketch, "E14858", {"start": v(-107.88, 30.76) * mm, "end": v(-107.42, 30.55) * mm});
            skLineSegment(sketch, "E14859", {"start": v(-107.42, 30.55) * mm, "end": v(-107.01, 30.34) * mm});
            skLineSegment(sketch, "E14860", {"start": v(-107.01, 30.34) * mm, "end": v(-106.66, 30.14) * mm});
            skLineSegment(sketch, "E14861", {"start": v(-106.66, 30.14) * mm, "end": v(-106.35, 29.94) * mm});
            skLineSegment(sketch, "E14862", {"start": v(-106.35, 29.94) * mm, "end": v(-106.1, 29.76) * mm});
            skLineSegment(sketch, "E14863", {"start": v(-106.1, 29.76) * mm, "end": v(-105.89, 29.6) * mm});
            skLineSegment(sketch, "E14864", {"start": v(-105.89, 29.6) * mm, "end": v(-105.72, 29.45) * mm});
            skLineSegment(sketch, "E14865", {"start": v(-105.72, 29.45) * mm, "end": v(-105.6, 29.33) * mm});
            skLineSegment(sketch, "E14866", {"start": v(-105.6, 29.33) * mm, "end": v(-105.52, 29.24) * mm});
            skLineSegment(sketch, "E14867", {"start": v(-105.52, 29.24) * mm, "end": v(-105.47, 29.18) * mm});
            skLineSegment(sketch, "E14868", {"start": v(-105.47, 29.18) * mm, "end": v(-105.46, 29.16) * mm});
            skLineSegment(sketch, "E14869", {"start": v(-105.46, 29.16) * mm, "end": v(-104.15, 27.33) * mm});
            skArc(sketch, "E14870", {"start": v(-104.15, 27.33) * mm, "mid": v(-102.82, 28.19) * mm, "end": v(-101.42, 28.92) * mm});
            skLineSegment(sketch, "E14871", {"start": v(-101.42, 28.92) * mm, "end": v(-102.37, 30.97) * mm});
            skLineSegment(sketch, "E14872", {"start": v(-102.37, 30.97) * mm, "end": v(-102.38, 31) * mm});
            skLineSegment(sketch, "E14873", {"start": v(-102.38, 31) * mm, "end": v(-102.4, 31.06) * mm});
            skLineSegment(sketch, "E14874", {"start": v(-102.4, 31.06) * mm, "end": v(-102.44, 31.17) * mm});
            skLineSegment(sketch, "E14875", {"start": v(-102.44, 31.17) * mm, "end": v(-102.48, 31.34) * mm});
            skLineSegment(sketch, "E14876", {"start": v(-102.48, 31.34) * mm, "end": v(-102.53, 31.55) * mm});
            skLineSegment(sketch, "E14877", {"start": v(-102.53, 31.55) * mm, "end": v(-102.57, 31.81) * mm});
            skLineSegment(sketch, "E14878", {"start": v(-102.57, 31.81) * mm, "end": v(-102.6, 32.13) * mm});
            skLineSegment(sketch, "E14879", {"start": v(-102.6, 32.13) * mm, "end": v(-102.63, 32.49) * mm});
            skLineSegment(sketch, "E14880", {"start": v(-102.63, 32.49) * mm, "end": v(-102.63, 32.9) * mm});
            skLineSegment(sketch, "E14881", {"start": v(-102.63, 32.9) * mm, "end": v(-102.61, 33.36) * mm});
            skLineSegment(sketch, "E14882", {"start": v(-102.61, 33.36) * mm, "end": v(-102.57, 33.87) * mm});
            skLineSegment(sketch, "E14883", {"start": v(-102.57, 33.87) * mm, "end": v(-102.5, 34.32) * mm});
            skArc(sketch, "E14884", {"start": v(-102.5, 34.32) * mm, "mid": v(-101.53, 34.69) * mm, "end": v(-100.54, 35) * mm});
            skLineSegment(sketch, "E14885", {"start": v(-100.54, 35) * mm, "end": v(-100.2, 34.68) * mm});
            skLineSegment(sketch, "E14886", {"start": v(-100.2, 34.68) * mm, "end": v(-99.85, 34.3) * mm});
            skLineSegment(sketch, "E14887", {"start": v(-99.85, 34.3) * mm, "end": v(-99.56, 33.96) * mm});
            skLineSegment(sketch, "E14888", {"start": v(-99.56, 33.96) * mm, "end": v(-99.3, 33.63) * mm});
            skLineSegment(sketch, "E14889", {"start": v(-99.3, 33.63) * mm, "end": v(-99.1, 33.33) * mm});
            skLineSegment(sketch, "E14890", {"start": v(-99.1, 33.33) * mm, "end": v(-98.94, 33.07) * mm});
            skLineSegment(sketch, "E14891", {"start": v(-98.94, 33.07) * mm, "end": v(-98.8, 32.83) * mm});
            skLineSegment(sketch, "E14892", {"start": v(-98.8, 32.83) * mm, "end": v(-98.71, 32.64) * mm});
            skLineSegment(sketch, "E14893", {"start": v(-98.71, 32.64) * mm, "end": v(-98.65, 32.48) * mm});
            skLineSegment(sketch, "E14894", {"start": v(-98.65, 32.48) * mm, "end": v(-98.6, 32.37) * mm});
            skLineSegment(sketch, "E14895", {"start": v(-98.6, 32.37) * mm, "end": v(-98.58, 32.3) * mm});
            skLineSegment(sketch, "E14896", {"start": v(-98.58, 32.3) * mm, "end": v(-98.57, 32.28) * mm});
            skLineSegment(sketch, "E14897", {"start": v(-98.57, 32.28) * mm, "end": v(-98.06, 30.08) * mm});
            skArc(sketch, "E14898", {"start": v(-98.06, 30.08) * mm, "mid": v(-96.5, 30.36) * mm, "end": v(-94.93, 30.5) * mm});
            skLineSegment(sketch, "E14899", {"start": v(-94.93, 30.5) * mm, "end": v(-95.03, 32.76) * mm});
            skLineSegment(sketch, "E14900", {"start": v(-95.03, 32.76) * mm, "end": v(-95.03, 32.78) * mm});
            skLineSegment(sketch, "E14901", {"start": v(-95.03, 32.78) * mm, "end": v(-95.03, 32.86) * mm});
            skLineSegment(sketch, "E14902", {"start": v(-95.03, 32.86) * mm, "end": v(-95.02, 32.98) * mm});
            skLineSegment(sketch, "E14903", {"start": v(-95.02, 32.98) * mm, "end": v(-95, 33.14) * mm});
            skLineSegment(sketch, "E14904", {"start": v(-95, 33.14) * mm, "end": v(-94.95, 33.36) * mm});
            skLineSegment(sketch, "E14905", {"start": v(-94.95, 33.36) * mm, "end": v(-94.9, 33.62) * mm});
            skLineSegment(sketch, "E14906", {"start": v(-94.9, 33.62) * mm, "end": v(-94.8, 33.92) * mm});
            skLineSegment(sketch, "E14907", {"start": v(-94.8, 33.92) * mm, "end": v(-94.69, 34.26) * mm});
            skLineSegment(sketch, "E14908", {"start": v(-94.69, 34.26) * mm, "end": v(-94.53, 34.64) * mm});
            skLineSegment(sketch, "E14909", {"start": v(-94.53, 34.64) * mm, "end": v(-94.34, 35.06) * mm});
            skLineSegment(sketch, "E14910", {"start": v(-94.34, 35.06) * mm, "end": v(-94.1, 35.51) * mm});
            skLineSegment(sketch, "E14911", {"start": v(-94.1, 35.51) * mm, "end": v(-93.87, 35.91) * mm});
            skArc(sketch, "E14912", {"start": v(-93.87, 35.91) * mm, "mid": v(-92.83, 35.87) * mm, "end": v(-91.8, 35.79) * mm});
            skLineSegment(sketch, "E14913", {"start": v(-91.8, 35.79) * mm, "end": v(-91.6, 35.36) * mm});
            skLineSegment(sketch, "E14914", {"start": v(-91.6, 35.36) * mm, "end": v(-91.43, 34.88) * mm});
            skLineSegment(sketch, "E14915", {"start": v(-91.43, 34.88) * mm, "end": v(-91.29, 34.45) * mm});
            skLineSegment(sketch, "E14916", {"start": v(-91.29, 34.45) * mm, "end": v(-91.18, 34.05) * mm});
            skLineSegment(sketch, "E14917", {"start": v(-91.18, 34.05) * mm, "end": v(-91.1, 33.7) * mm});
            skLineSegment(sketch, "E14918", {"start": v(-91.1, 33.7) * mm, "end": v(-91.05, 33.38) * mm});
            skLineSegment(sketch, "E14919", {"start": v(-91.05, 33.38) * mm, "end": v(-91.02, 33.12) * mm});
            skLineSegment(sketch, "E14920", {"start": v(-91.02, 33.12) * mm, "end": v(-91.01, 32.9) * mm});
            skLineSegment(sketch, "E14921", {"start": v(-91.01, 32.9) * mm, "end": v(-91, 32.73) * mm});
            skLineSegment(sketch, "E14922", {"start": v(-91, 32.73) * mm, "end": v(-91.01, 32.61) * mm});
            skLineSegment(sketch, "E14923", {"start": v(-91.01, 32.61) * mm, "end": v(-91.02, 32.54) * mm});
            skLineSegment(sketch, "E14924", {"start": v(-91.02, 32.54) * mm, "end": v(-91.02, 32.52) * mm});
            skLineSegment(sketch, "E14925", {"start": v(-91.02, 32.52) * mm, "end": v(-91.4, 30.3) * mm});
            skArc(sketch, "E14926", {"start": v(-91.4, 30.3) * mm, "mid": v(-89.84, 29.96) * mm, "end": v(-88.33, 29.49) * mm});
            skLineSegment(sketch, "E14927", {"start": v(-88.33, 29.49) * mm, "end": v(-87.56, 31.6) * mm});
            skLineSegment(sketch, "E14928", {"start": v(-87.56, 31.6) * mm, "end": v(-87.55, 31.63) * mm});
            skLineSegment(sketch, "E14929", {"start": v(-87.55, 31.63) * mm, "end": v(-87.52, 31.7) * mm});
            skLineSegment(sketch, "E14930", {"start": v(-87.52, 31.7) * mm, "end": v(-87.47, 31.8) * mm});
            skLineSegment(sketch, "E14931", {"start": v(-87.47, 31.8) * mm, "end": v(-87.38, 31.95) * mm});
            skLineSegment(sketch, "E14932", {"start": v(-87.38, 31.95) * mm, "end": v(-87.26, 32.13) * mm});
            skLineSegment(sketch, "E14933", {"start": v(-87.26, 32.13) * mm, "end": v(-87.1, 32.35) * mm});
            skLineSegment(sketch, "E14934", {"start": v(-87.1, 32.35) * mm, "end": v(-86.91, 32.6) * mm});
            skLineSegment(sketch, "E14935", {"start": v(-86.91, 32.6) * mm, "end": v(-86.67, 32.86) * mm});
            skLineSegment(sketch, "E14936", {"start": v(-86.67, 32.86) * mm, "end": v(-86.38, 33.16) * mm});
            skLineSegment(sketch, "E14937", {"start": v(-86.38, 33.16) * mm, "end": v(-86.04, 33.47) * mm});
            skLineSegment(sketch, "E14938", {"start": v(-86.04, 33.47) * mm, "end": v(-85.65, 33.8) * mm});
            skLineSegment(sketch, "E14939", {"start": v(-85.65, 33.8) * mm, "end": v(-85.28, 34.07) * mm});
            skArc(sketch, "E14940", {"start": v(-85.28, 34.07) * mm, "mid": v(-84.34, 33.64) * mm, "end": v(-83.41, 33.16) * mm});
            skLineSegment(sketch, "E14941", {"start": v(-83.41, 33.16) * mm, "end": v(-83.4, 32.7) * mm});
            skLineSegment(sketch, "E14942", {"start": v(-83.4, 32.7) * mm, "end": v(-83.42, 32.2) * mm});
            skLineSegment(sketch, "E14943", {"start": v(-83.42, 32.2) * mm, "end": v(-83.46, 31.73) * mm});
            skLineSegment(sketch, "E14944", {"start": v(-83.46, 31.73) * mm, "end": v(-83.51, 31.32) * mm});
            skLineSegment(sketch, "E14945", {"start": v(-83.51, 31.32) * mm, "end": v(-83.58, 30.97) * mm});
            skLineSegment(sketch, "E14946", {"start": v(-83.58, 30.97) * mm, "end": v(-83.65, 30.66) * mm});
            skLineSegment(sketch, "E14947", {"start": v(-83.65, 30.66) * mm, "end": v(-83.73, 30.4) * mm});
            skLineSegment(sketch, "E14948", {"start": v(-83.73, 30.4) * mm, "end": v(-83.8, 30.2) * mm});
            skLineSegment(sketch, "E14949", {"start": v(-83.8, 30.2) * mm, "end": v(-83.86, 30.04) * mm});
            skLineSegment(sketch, "E14950", {"start": v(-83.86, 30.04) * mm, "end": v(-83.9, 29.93) * mm});
            skLineSegment(sketch, "E14951", {"start": v(-83.9, 29.93) * mm, "end": v(-83.94, 29.87) * mm});
            skLineSegment(sketch, "E14952", {"start": v(-83.94, 29.87) * mm, "end": v(-83.96, 29.85) * mm});
            skLineSegment(sketch, "E14953", {"start": v(-83.96, 29.85) * mm, "end": v(-85.15, 27.93) * mm});
            skArc(sketch, "E14954", {"start": v(-85.15, 27.93) * mm, "mid": v(-83.84, 27.03) * mm, "end": v(-82.63, 26.02) * mm});
            skCircle(sketch, "E14955", {"center": v(-94.2, 13.41) * mm, "radius": 1.25 * mm});
            skLineSegment(sketch, "E14956", {"start": v(-97.2, 11.31) * mm, "end": v(-91.2, 11.31) * mm});
            skLineSegment(sketch, "E14957", {"start": v(-91.2, 11.31) * mm, "end": v(-91.2, 15.51) * mm});
            skLineSegment(sketch, "E14958", {"start": v(-91.2, 15.51) * mm, "end": v(-97.2, 15.51) * mm});
            skLineSegment(sketch, "E14959", {"start": v(-97.2, 15.51) * mm, "end": v(-97.2, 11.31) * mm});
            skCircle(sketch, "E14960", {"center": v(-94.2, 13.41) * mm, "radius": 3.75 * mm});
            skSolve(sketch);
        }
        {
            var Q0;
            Q0 = qSketchRegion(id + "F9", true);
            extrude(context, id + "F10", {"entities" : qUnion([Q0]), "depth" : 4 * mm});
        }
    });
